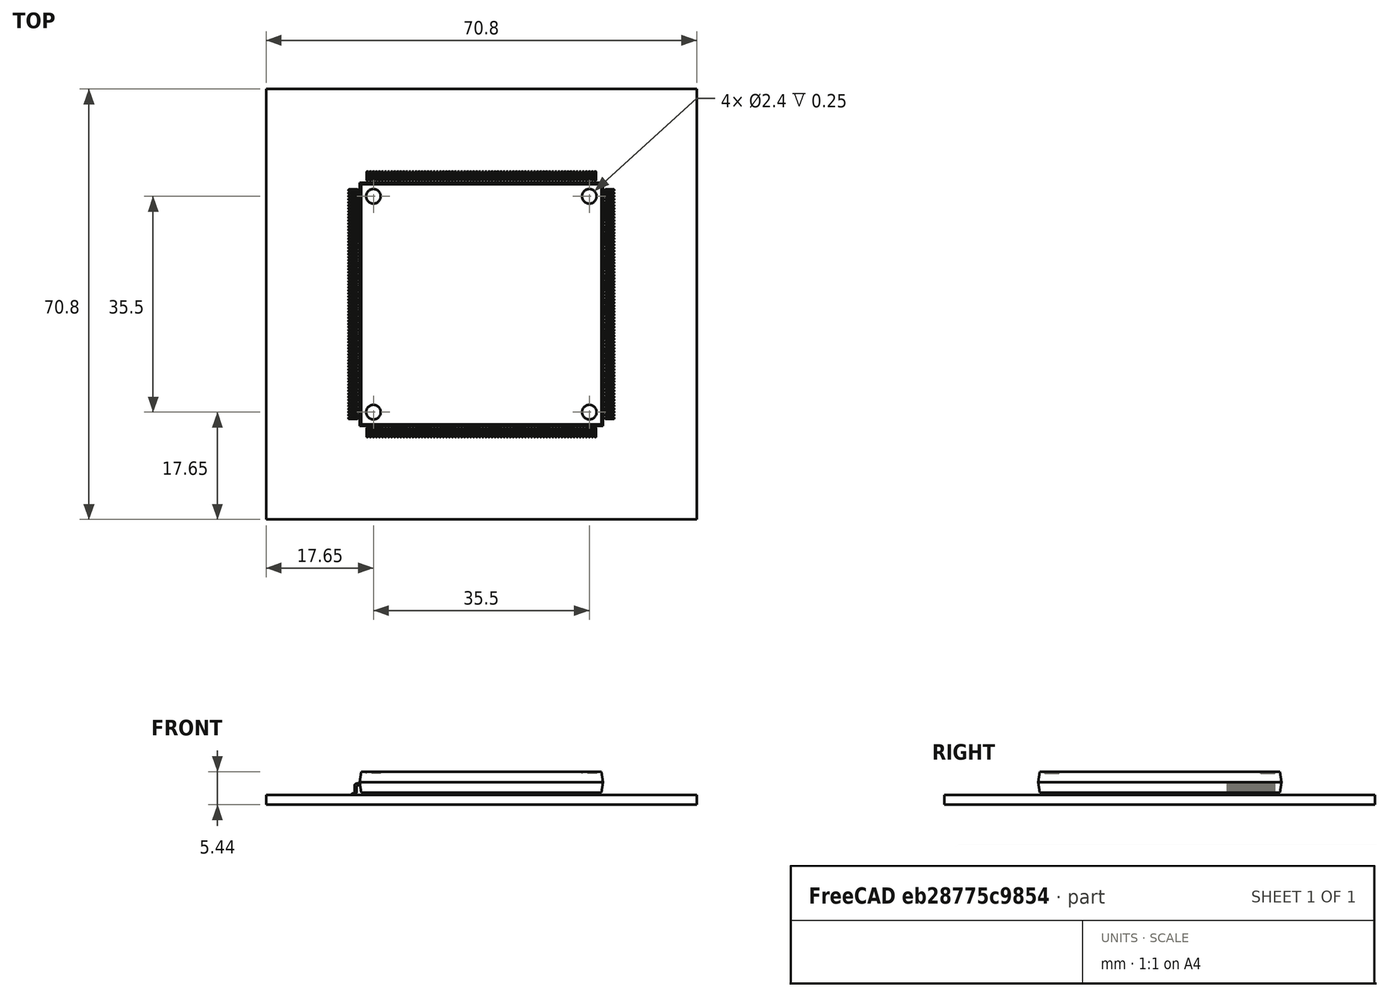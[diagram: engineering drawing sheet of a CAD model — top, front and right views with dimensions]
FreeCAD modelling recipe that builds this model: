
FCSTD DOCUMENT  (FreeCAD 0.19R24291 (Git))
Label: AT40K40
License: All rights reserved
LicenseURL: http://en.wikipedia.org/wiki/All_rights_reserved
objects: PartDesign::SubtractiveBox×1824, PartDesign::AdditiveBox×1217, PartDesign::Fillet×912, PartDesign::SubtractiveCylinder×612, PartDesign::Body×305, App::Part×28, PartDesign::Chamfer×8, Part::FeaturePython×5, Sketcher::SketchObject×1, App::DocumentObjectGroup×1
note: 9457 computed .brp shape members not serialized (recipe doc carries the construction recipe); baked Part::Feature solids carry a one-line shape summary decoded from their .brp

FEATURE [Sketcher::SketchObject] Sketch001  label="body-sketch"
  FullyConstrained = false
  MapMode = 5
  Support = -> [XY_Plane]
  sketch-geometry (20):
    g0: LineSegment StartX=20.05 StartY=20 StartZ=0 EndX=20.05 EndY=-20 EndZ=0
    g1: ArcOfCircle CenterX=20 CenterY=-20 CenterZ=0 NormalX=0 NormalY=0 NormalZ=1 AngleXU=-3.14159 Radius=0.05 StartAngle=0 EndAngle=3.14159
    g2: LineSegment StartX=19.95 StartY=-20 StartZ=0 EndX=19.95 EndY=20 EndZ=0
    g3: ArcOfCircle CenterX=20 CenterY=20 CenterZ=0 NormalX=0 NormalY=0 NormalZ=1 AngleXU=-3.14159 Radius=0.05 StartAngle=3.14159 EndAngle=6.28319
    g4: LineSegment StartX=-20.0354 StartY=19.0354 StartZ=0 EndX=-19.0354 EndY=20.0354 EndZ=0
    g5: ArcOfCircle CenterX=-19 CenterY=20 CenterZ=0 NormalX=0 NormalY=0 NormalZ=1 AngleXU=-0.785398 Radius=0.05 StartAngle=0 EndAngle=3.14159
    g6: LineSegment StartX=-18.9646 StartY=19.9646 StartZ=0 EndX=-19.9646 EndY=18.9646 EndZ=0
    g7: ArcOfCircle CenterX=-20 CenterY=19 CenterZ=0 NormalX=0 NormalY=0 NormalZ=1 AngleXU=-0.785398 Radius=0.05 StartAngle=3.14159 EndAngle=6.28319
    g8: LineSegment StartX=20 StartY=-20.05 StartZ=0 EndX=-20 EndY=-20.05 EndZ=0
    g9: ArcOfCircle CenterX=-20 CenterY=-20 CenterZ=0 NormalX=0 NormalY=0 NormalZ=1 AngleXU=1.5708 Radius=0.05 StartAngle=0 EndAngle=3.14159
    g10: LineSegment StartX=-20 StartY=-19.95 StartZ=0 EndX=20 EndY=-19.95 EndZ=0
    g11: ArcOfCircle CenterX=20 CenterY=-20 CenterZ=0 NormalX=0 NormalY=0 NormalZ=1 AngleXU=1.5708 Radius=0.05 StartAngle=3.14159 EndAngle=6.28319
    g12: LineSegment StartX=-19 StartY=20.05 StartZ=0 EndX=20 EndY=20.05 EndZ=0
    g13: ArcOfCircle CenterX=20 CenterY=20 CenterZ=0 NormalX=0 NormalY=0 NormalZ=1 AngleXU=-1.5708 Radius=0.05 StartAngle=0 EndAngle=3.14159
    g14: LineSegment StartX=20 StartY=19.95 StartZ=0 EndX=-19 EndY=19.95 EndZ=0
    g15: ArcOfCircle CenterX=-19 CenterY=20 CenterZ=0 NormalX=0 NormalY=0 NormalZ=1 AngleXU=-1.5708 Radius=0.05 StartAngle=3.14159 EndAngle=6.28319
    g16: LineSegment StartX=-20.05 StartY=-20 StartZ=0 EndX=-20.05 EndY=19 EndZ=0
    g17: ArcOfCircle CenterX=-20 CenterY=19 CenterZ=0 NormalX=0 NormalY=0 NormalZ=1 AngleXU=1e-16 Radius=0.05 StartAngle=0 EndAngle=3.14159
    g18: LineSegment StartX=-19.95 StartY=19 StartZ=0 EndX=-19.95 EndY=-20 EndZ=0
    g19: ArcOfCircle CenterX=-20 CenterY=-20 CenterZ=0 NormalX=0 NormalY=0 NormalZ=1 AngleXU=0 Radius=0.05 StartAngle=3.14159 EndAngle=6.28319
FEATURE [PartDesign::AdditiveBox] Box
  AttacherType = Attacher::AttachEngine3D
  AttachmentOffset = pos=(-20,-20,0.375) rot=(0,0,1;0rad)
  Height = 3.475
  Length = 40
  MapMode = 5
  Placement = pos=(-20,-20,0.375) rot=(0,0,1;0rad)
  Support = -> [XY_Plane]
  Width = 40
FEATURE [PartDesign::SubtractiveCylinder] Cylinder
  Angle = 360
  AttacherType = Attacher::AttachEngine3D
  AttachmentOffset = pos=(17.75,-17.75,3.6) rot=(0,0,1;0rad)
  BaseFeature = -> Box
  Height = 0.25
  MapMode = 5
  Placement = pos=(17.75,-17.75,3.6) rot=(0,0,1;0rad)
  Radius = 1.2
  Support = -> [XY_Plane]
FEATURE [PartDesign::SubtractiveCylinder] Cylinder001
  Angle = 360
  AttacherType = Attacher::AttachEngine3D
  AttachmentOffset = pos=(-17.75,17.75,3.6) rot=(0,0,1;0rad)
  BaseFeature = -> Cylinder
  Height = 0.25
  MapMode = 5
  Placement = pos=(-17.75,17.75,3.6) rot=(0,0,1;0rad)
  Radius = 1.2
  Support = -> [XY_Plane]
FEATURE [PartDesign::SubtractiveCylinder] Cylinder002
  Angle = 360
  AttacherType = Attacher::AttachEngine3D
  AttachmentOffset = pos=(-17.75,-17.75,3.6) rot=(0,0,1;0rad)
  BaseFeature = -> Cylinder001
  Height = 0.25
  MapMode = 5
  Placement = pos=(-17.75,-17.75,3.6) rot=(0,0,1;0rad)
  Radius = 1.2
  Support = -> [XY_Plane]
FEATURE [PartDesign::SubtractiveCylinder] Cylinder003
  Angle = 360
  AttacherType = Attacher::AttachEngine3D
  AttachmentOffset = pos=(17.75,17.75,3.6) rot=(0,0,1;0rad)
  BaseFeature = -> Cylinder002
  Height = 0.25
  MapMode = 5
  Placement = pos=(17.75,17.75,3.6) rot=(0,0,1;0rad)
  Radius = 1.2
  Support = -> [XY_Plane]
FEATURE [PartDesign::AdditiveBox] Box001
  AttacherType = Attacher::AttachEngine3D
  AttachmentOffset = pos=(-21.3,18.635,0) rot=(0,0,1;0rad)
  Height = 1.9
  Length = 1.3
  MapMode = 5
  Placement = pos=(-21.3,18.635,0) rot=(0,0,1;0rad)
  Support = -> [XY_Plane001]
  Width = 0.23
FEATURE [PartDesign::SubtractiveBox] Box002
  AttacherType = Attacher::AttachEngine3D
  AttachmentOffset = pos=(-21.35,18.635,0.35) rot=(0,0,1;0rad)
  BaseFeature = -> Box001
  Height = 1.55
  Length = 0.5
  MapMode = 5
  Placement = pos=(-21.35,18.635,0.35) rot=(0,0,1;0rad)
  Support = -> [XY_Plane001]
  Width = 0.23
FEATURE [PartDesign::SubtractiveBox] Box003
  AttacherType = Attacher::AttachEngine3D
  AttachmentOffset = pos=(-20.5,18.63,0) rot=(0,0,1;0rad)
  BaseFeature = -> Box002
  Height = 1.635
  Length = 0.5
  MapMode = 5
  Placement = pos=(-20.5,18.63,0) rot=(0,0,1;0rad)
  Support = -> [XY_Plane001]
  Width = 0.25
FEATURE [PartDesign::SubtractiveBox] Box004
  AttacherType = Attacher::AttachEngine3D
  AttachmentOffset = pos=(-21.19,18.635,-0.12) rot=(0,-1,0;0.15708rad)
  BaseFeature = -> Box003
  Height = 0.12
  Length = 0.725
  MapMode = 5
  Placement = pos=(-21.19,18.635,-0.12) rot=(0,-1,0;0.15708rad)
  Support = -> [XY_Plane001]
  Width = 0.25
FEATURE [PartDesign::SubtractiveBox] Box005
  AttacherType = Attacher::AttachEngine3D
  AttachmentOffset = pos=(-21.5005,18.625,0.235) rot=(0,-1,0;0.174533rad)
  BaseFeature = -> Box004
  Height = 0.3
  Length = 0.6605
  MapMode = 5
  Placement = pos=(-21.5005,18.625,0.235) rot=(0,-1,0;0.174533rad)
  Support = -> [XY_Plane001]
  Width = 0.25
FEATURE [PartDesign::Fillet] Fillet
  Base = -> Box005 [Edge2]
  BaseFeature = -> Box005
  Placement = pos=(-21.5005,18.625,0.235) rot=(0,-1,0;0.174533rad)
  Radius = 0.05
  SupportTransform = false
FEATURE [PartDesign::Fillet] Fillet001
  Base = -> Fillet [Edge33]
  BaseFeature = -> Fillet
  Placement = pos=(-21.5005,18.625,0.235) rot=(0,-1,0;0.174533rad)
  Radius = 0.5
  SupportTransform = false
FEATURE [PartDesign::AdditiveBox] Box006
  AttacherType = Attacher::AttachEngine3D
  AttachmentOffset = pos=(-21.1,18.635,0.305) rot=(0,1,0;0.785398rad)
  BaseFeature = -> Fillet001
  Height = 0.375
  Length = 0.2
  MapMode = 5
  Placement = pos=(-21.1,18.635,0.305) rot=(0,1,0;0.785398rad)
  Support = -> [XY_Plane001]
  Width = 0.23
FEATURE [PartDesign::SubtractiveCylinder] Cylinder004
  Angle = 360
  AttacherType = Attacher::AttachEngine3D
  AttachmentOffset = pos=(-21.055,18.935,0.52) rot=(1,0,0;1.5708rad)
  BaseFeature = -> Box006
  Height = 0.375
  MapMode = 5
  Placement = pos=(-21.055,18.935,0.52) rot=(1,0,0;1.5708rad)
  Radius = 0.205
  Support = -> [XY_Plane001]
FEATURE [PartDesign::SubtractiveBox] Box007
  AttacherType = Attacher::AttachEngine3D
  AttachmentOffset = pos=(-20.95,18.635,0.53) rot=(0,0,1;0rad)
  BaseFeature = -> Cylinder004
  Height = 0.5
  Length = 0.1
  MapMode = 5
  Placement = pos=(-20.95,18.635,0.53) rot=(0,0,1;0rad)
  Support = -> [XY_Plane001]
  Width = 0.23
FEATURE [PartDesign::SubtractiveBox] Box008
  AttacherType = Attacher::AttachEngine3D
  AttachmentOffset = pos=(-21.15,18.635,0.297) rot=(0,-1,0;0.174533rad)
  BaseFeature = -> Box007
  Height = 0.115
  Length = 0.115
  MapMode = 5
  Placement = pos=(-21.15,18.635,0.297) rot=(0,-1,0;0.174533rad)
  Support = -> [XY_Plane001]
  Width = 0.23
FEATURE [PartDesign::Fillet] Fillet002
  Base = -> Box008 [Edge28]
  BaseFeature = -> Box008
  Placement = pos=(-21.15,18.635,0.297) rot=(0,-1,0;0.174533rad)
  Radius = 0.375
  SupportTransform = false
FEATURE [PartDesign::AdditiveBox] Box009
  AttacherType = Attacher::AttachEngine3D
  AttachmentOffset = pos=(-20.7,18.635,1.55) rot=(0,1,0;0.785398rad)
  BaseFeature = -> Fillet002
  Height = 0.375
  Length = 0.23
  MapMode = 5
  Placement = pos=(-20.7,18.635,1.55) rot=(0,1,0;0.785398rad)
  Support = -> [XY_Plane001]
  Width = 0.23
FEATURE [PartDesign::SubtractiveCylinder] Cylinder005
  Angle = 360
  AttacherType = Attacher::AttachEngine3D
  AttachmentOffset = pos=(-20.271,18.635,1.4056) rot=(-1,0,0;1.5708rad)
  BaseFeature = -> Box009
  Height = 0.23
  MapMode = 5
  Placement = pos=(-20.271,18.635,1.4056) rot=(-1,0,0;1.5708rad)
  Radius = 0.23
  Support = -> [XY_Plane001]
FEATURE [PartDesign::Chamfer] Chamfer
  Angle = 45
  Base = -> Cylinder003 [Edge2]
  BaseFeature = -> Cylinder003
  ChamferType = 1
  FlipDirection = false
  Placement = pos=(17.75,17.75,3.6) rot=(0,0,1;0rad)
  Size = 1.7125
  Size2 = 0.25
  SupportTransform = false
FEATURE [PartDesign::Chamfer] Chamfer001
  Angle = 45
  Base = -> Chamfer [Edge3]
  BaseFeature = -> Chamfer
  ChamferType = 1
  FlipDirection = false
  Placement = pos=(17.75,17.75,3.6) rot=(0,0,1;0rad)
  Size = 1.7125
  Size2 = 0.25
  SupportTransform = false
FEATURE [PartDesign::Chamfer] Chamfer002
  Angle = 45
  Base = -> Chamfer001 [Edge15]
  BaseFeature = -> Chamfer001
  ChamferType = 1
  FlipDirection = false
  Placement = pos=(17.75,17.75,3.6) rot=(0,0,1;0rad)
  Size = 1.7125
  Size2 = 0.25
  SupportTransform = false
FEATURE [PartDesign::Chamfer] Chamfer003
  Angle = 45
  Base = -> Chamfer002 [Edge30]
  BaseFeature = -> Chamfer002
  ChamferType = 1
  FlipDirection = false
  Placement = pos=(17.75,17.75,3.6) rot=(0,0,1;0rad)
  Size = 1.7125
  Size2 = 0.25
  SupportTransform = false
FEATURE [PartDesign::Chamfer] Chamfer004
  Angle = 45
  Base = -> Chamfer003 [Edge5]
  BaseFeature = -> Chamfer003
  ChamferType = 1
  FlipDirection = false
  Placement = pos=(17.75,17.75,3.6) rot=(0,0,1;0rad)
  Size = 1.7125
  Size2 = 0.25
  SupportTransform = false
FEATURE [PartDesign::Chamfer] Chamfer005
  Angle = 45
  Base = -> Chamfer004 [Edge3]
  BaseFeature = -> Chamfer004
  ChamferType = 1
  FlipDirection = false
  Placement = pos=(17.75,17.75,3.6) rot=(0,0,1;0rad)
  Size = 1.7125
  Size2 = 0.25
  SupportTransform = false
FEATURE [PartDesign::Chamfer] Chamfer006
  Angle = 45
  Base = -> Chamfer005 [Edge8]
  BaseFeature = -> Chamfer005
  ChamferType = 1
  FlipDirection = false
  Placement = pos=(17.75,17.75,3.6) rot=(0,0,1;0rad)
  Size = 1.7125
  Size2 = 0.25
  SupportTransform = false
FEATURE [PartDesign::Chamfer] Chamfer007
  Angle = 45
  Base = -> Chamfer006 [Edge6]
  BaseFeature = -> Chamfer006
  ChamferType = 1
  FlipDirection = false
  Placement = pos=(17.75,17.75,3.6) rot=(0,0,1;0rad)
  Size = 1.7125
  Size2 = 0.25
  SupportTransform = false
FEATURE [PartDesign::Body] Body
  Group = -> [Sketch001,Box,Cylinder,Cylinder001,Cylinder002,Cylinder003,Chamfer,Chamfer001,Chamfer002,Chamfer003,Chamfer004,Chamfer005,Chamfer006,Chamfer007]
  Origin = -> Origin
  Tip = -> Chamfer007
FEATURE [PartDesign::AdditiveBox] Box010
  AttacherType = Attacher::AttachEngine3D
  AttachmentOffset = pos=(-20.1,18.635,1.635) rot=(0,0,1;0rad)
  BaseFeature = -> Cylinder005
  Height = 0.265
  Length = 0.23
  MapMode = 5
  Placement = pos=(-20.1,18.635,1.635) rot=(0,0,1;0rad)
  Support = -> [XY_Plane001]
  Width = 0.23
FEATURE [PartDesign::Body] Body001  label="pin1"
  Group = -> [Box001,Box002,Box003,Box004,Box005,Fillet,Fillet001,Box006,Cylinder004,Box007,Box008,Fillet002,Box009,Cylinder005,Box010]
  Origin = -> Origin001
  Tip = -> Box010
FEATURE [PartDesign::AdditiveBox] Box019
  AttacherType = Attacher::AttachEngine3D
  AttachmentOffset = pos=(-21.3,18.635,0) rot=(0,0,1;0rad)
  Height = 1.9
  Length = 1.3
  MapMode = 5
  Placement = pos=(-21.3,18.635,0) rot=(0,0,1;0rad)
  Support = -> [XY_Plane002]
  Width = 0.23
FEATURE [PartDesign::SubtractiveBox] Box020
  AttacherType = Attacher::AttachEngine3D
  AttachmentOffset = pos=(-21.35,18.635,0.35) rot=(0,0,1;0rad)
  BaseFeature = -> Box019
  Height = 1.55
  Length = 0.5
  MapMode = 5
  Placement = pos=(-21.35,18.635,0.35) rot=(0,0,1;0rad)
  Support = -> [XY_Plane002]
  Width = 0.23
FEATURE [PartDesign::SubtractiveBox] Box014
  AttacherType = Attacher::AttachEngine3D
  AttachmentOffset = pos=(-20.5,18.63,0) rot=(0,0,1;0rad)
  BaseFeature = -> Box020
  Height = 1.635
  Length = 0.5
  MapMode = 5
  Placement = pos=(-20.5,18.63,0) rot=(0,0,1;0rad)
  Support = -> [XY_Plane002]
  Width = 0.25
FEATURE [PartDesign::SubtractiveBox] Box015
  AttacherType = Attacher::AttachEngine3D
  AttachmentOffset = pos=(-21.19,18.635,-0.12) rot=(0,-1,0;0.15708rad)
  BaseFeature = -> Box014
  Height = 0.12
  Length = 0.725
  MapMode = 5
  Placement = pos=(-21.19,18.635,-0.12) rot=(0,-1,0;0.15708rad)
  Support = -> [XY_Plane002]
  Width = 0.25
FEATURE [PartDesign::SubtractiveBox] Box018
  AttacherType = Attacher::AttachEngine3D
  AttachmentOffset = pos=(-21.5005,18.625,0.235) rot=(0,-1,0;0.174533rad)
  BaseFeature = -> Box015
  Height = 0.3
  Length = 0.6605
  MapMode = 5
  Placement = pos=(-21.5005,18.625,0.235) rot=(0,-1,0;0.174533rad)
  Support = -> [XY_Plane002]
  Width = 0.25
FEATURE [PartDesign::Fillet] Fillet004
  Base = -> Box018 [Edge2]
  BaseFeature = -> Box018
  Placement = pos=(-21.5005,18.625,0.235) rot=(0,-1,0;0.174533rad)
  Radius = 0.05
  SupportTransform = false
FEATURE [PartDesign::Fillet] Fillet003
  Base = -> Fillet004 [Edge33]
  BaseFeature = -> Fillet004
  Placement = pos=(-21.5005,18.625,0.235) rot=(0,-1,0;0.174533rad)
  Radius = 0.5
  SupportTransform = false
FEATURE [PartDesign::AdditiveBox] Box011
  AttacherType = Attacher::AttachEngine3D
  AttachmentOffset = pos=(-21.1,18.635,0.305) rot=(0,1,0;0.785398rad)
  BaseFeature = -> Fillet003
  Height = 0.375
  Length = 0.2
  MapMode = 5
  Placement = pos=(-21.1,18.635,0.305) rot=(0,1,0;0.785398rad)
  Support = -> [XY_Plane002]
  Width = 0.23
FEATURE [PartDesign::SubtractiveCylinder] Cylinder006
  Angle = 360
  AttacherType = Attacher::AttachEngine3D
  AttachmentOffset = pos=(-21.055,18.935,0.52) rot=(1,0,0;1.5708rad)
  BaseFeature = -> Box011
  Height = 0.375
  MapMode = 5
  Placement = pos=(-21.055,18.935,0.52) rot=(1,0,0;1.5708rad)
  Radius = 0.205
  Support = -> [XY_Plane002]
FEATURE [PartDesign::SubtractiveBox] Box013
  AttacherType = Attacher::AttachEngine3D
  AttachmentOffset = pos=(-20.95,18.635,0.53) rot=(0,0,1;0rad)
  BaseFeature = -> Cylinder006
  Height = 0.5
  Length = 0.1
  MapMode = 5
  Placement = pos=(-20.95,18.635,0.53) rot=(0,0,1;0rad)
  Support = -> [XY_Plane002]
  Width = 0.23
FEATURE [PartDesign::SubtractiveBox] Box012
  AttacherType = Attacher::AttachEngine3D
  AttachmentOffset = pos=(-21.15,18.635,0.297) rot=(0,-1,0;0.174533rad)
  BaseFeature = -> Box013
  Height = 0.115
  Length = 0.115
  MapMode = 5
  Placement = pos=(-21.15,18.635,0.297) rot=(0,-1,0;0.174533rad)
  Support = -> [XY_Plane002]
  Width = 0.23
FEATURE [PartDesign::Fillet] Fillet005
  Base = -> Box012 [Edge28]
  BaseFeature = -> Box012
  Placement = pos=(-21.15,18.635,0.297) rot=(0,-1,0;0.174533rad)
  Radius = 0.375
  SupportTransform = false
FEATURE [PartDesign::AdditiveBox] Box016
  AttacherType = Attacher::AttachEngine3D
  AttachmentOffset = pos=(-20.7,18.635,1.55) rot=(0,1,0;0.785398rad)
  BaseFeature = -> Fillet005
  Height = 0.375
  Length = 0.23
  MapMode = 5
  Placement = pos=(-20.7,18.635,1.55) rot=(0,1,0;0.785398rad)
  Support = -> [XY_Plane002]
  Width = 0.23
FEATURE [PartDesign::SubtractiveCylinder] Cylinder007
  Angle = 360
  AttacherType = Attacher::AttachEngine3D
  AttachmentOffset = pos=(-20.271,18.635,1.4056) rot=(-1,0,0;1.5708rad)
  BaseFeature = -> Box016
  Height = 0.23
  MapMode = 5
  Placement = pos=(-20.271,18.635,1.4056) rot=(-1,0,0;1.5708rad)
  Radius = 0.23
  Support = -> [XY_Plane002]
FEATURE [PartDesign::AdditiveBox] Box017
  AttacherType = Attacher::AttachEngine3D
  AttachmentOffset = pos=(-20.1,18.635,1.635) rot=(0,0,1;0rad)
  BaseFeature = -> Cylinder007
  Height = 0.265
  Length = 0.23
  MapMode = 5
  Placement = pos=(-20.1,18.635,1.635) rot=(0,0,1;0rad)
  Support = -> [XY_Plane002]
  Width = 0.23
FEATURE [PartDesign::Body] Body002  label="pin002"
  Group = -> [Box019,Box020,Box014,Box015,Box018,Fillet004,Fillet003,Box011,Cylinder006,Box013,Box012,Fillet005,Box016,Cylinder007,Box017]
  Origin = -> Origin002
  Placement = pos=(0,-0.5,0) rot=(0,0,1;0rad)
  Tip = -> Box017
FEATURE [PartDesign::AdditiveBox] Box029
  AttacherType = Attacher::AttachEngine3D
  AttachmentOffset = pos=(-21.3,18.635,0) rot=(0,0,1;0rad)
  Height = 1.9
  Length = 1.3
  MapMode = 5
  Placement = pos=(-21.3,18.635,0) rot=(0,0,1;0rad)
  Support = -> [XY_Plane003]
  Width = 0.23
FEATURE [PartDesign::SubtractiveBox] Box030
  AttacherType = Attacher::AttachEngine3D
  AttachmentOffset = pos=(-21.35,18.635,0.35) rot=(0,0,1;0rad)
  BaseFeature = -> Box029
  Height = 1.55
  Length = 0.5
  MapMode = 5
  Placement = pos=(-21.35,18.635,0.35) rot=(0,0,1;0rad)
  Support = -> [XY_Plane003]
  Width = 0.23
FEATURE [PartDesign::SubtractiveBox] Box021
  AttacherType = Attacher::AttachEngine3D
  AttachmentOffset = pos=(-20.5,18.63,0) rot=(0,0,1;0rad)
  BaseFeature = -> Box030
  Height = 1.635
  Length = 0.5
  MapMode = 5
  Placement = pos=(-20.5,18.63,0) rot=(0,0,1;0rad)
  Support = -> [XY_Plane003]
  Width = 0.25
FEATURE [PartDesign::SubtractiveBox] Box026
  AttacherType = Attacher::AttachEngine3D
  AttachmentOffset = pos=(-21.19,18.635,-0.12) rot=(0,-1,0;0.15708rad)
  BaseFeature = -> Box021
  Height = 0.12
  Length = 0.725
  MapMode = 5
  Placement = pos=(-21.19,18.635,-0.12) rot=(0,-1,0;0.15708rad)
  Support = -> [XY_Plane003]
  Width = 0.25
FEATURE [PartDesign::SubtractiveBox] Box027
  AttacherType = Attacher::AttachEngine3D
  AttachmentOffset = pos=(-21.5005,18.625,0.235) rot=(0,-1,0;0.174533rad)
  BaseFeature = -> Box026
  Height = 0.3
  Length = 0.6605
  MapMode = 5
  Placement = pos=(-21.5005,18.625,0.235) rot=(0,-1,0;0.174533rad)
  Support = -> [XY_Plane003]
  Width = 0.25
FEATURE [PartDesign::Fillet] Fillet006
  Base = -> Box027 [Edge2]
  BaseFeature = -> Box027
  Placement = pos=(-21.5005,18.625,0.235) rot=(0,-1,0;0.174533rad)
  Radius = 0.05
  SupportTransform = false
FEATURE [PartDesign::Fillet] Fillet007
  Base = -> Fillet006 [Edge33]
  BaseFeature = -> Fillet006
  Placement = pos=(-21.5005,18.625,0.235) rot=(0,-1,0;0.174533rad)
  Radius = 0.5
  SupportTransform = false
FEATURE [PartDesign::AdditiveBox] Box023
  AttacherType = Attacher::AttachEngine3D
  AttachmentOffset = pos=(-21.1,18.635,0.305) rot=(0,1,0;0.785398rad)
  BaseFeature = -> Fillet007
  Height = 0.375
  Length = 0.2
  MapMode = 5
  Placement = pos=(-21.1,18.635,0.305) rot=(0,1,0;0.785398rad)
  Support = -> [XY_Plane003]
  Width = 0.23
FEATURE [PartDesign::SubtractiveCylinder] Cylinder008
  Angle = 360
  AttacherType = Attacher::AttachEngine3D
  AttachmentOffset = pos=(-21.055,18.935,0.52) rot=(1,0,0;1.5708rad)
  BaseFeature = -> Box023
  Height = 0.375
  MapMode = 5
  Placement = pos=(-21.055,18.935,0.52) rot=(1,0,0;1.5708rad)
  Radius = 0.205
  Support = -> [XY_Plane003]
FEATURE [PartDesign::SubtractiveBox] Box025
  AttacherType = Attacher::AttachEngine3D
  AttachmentOffset = pos=(-20.95,18.635,0.53) rot=(0,0,1;0rad)
  BaseFeature = -> Cylinder008
  Height = 0.5
  Length = 0.1
  MapMode = 5
  Placement = pos=(-20.95,18.635,0.53) rot=(0,0,1;0rad)
  Support = -> [XY_Plane003]
  Width = 0.23
FEATURE [PartDesign::SubtractiveBox] Box024
  AttacherType = Attacher::AttachEngine3D
  AttachmentOffset = pos=(-21.15,18.635,0.297) rot=(0,-1,0;0.174533rad)
  BaseFeature = -> Box025
  Height = 0.115
  Length = 0.115
  MapMode = 5
  Placement = pos=(-21.15,18.635,0.297) rot=(0,-1,0;0.174533rad)
  Support = -> [XY_Plane003]
  Width = 0.23
FEATURE [PartDesign::Fillet] Fillet008
  Base = -> Box024 [Edge28]
  BaseFeature = -> Box024
  Placement = pos=(-21.15,18.635,0.297) rot=(0,-1,0;0.174533rad)
  Radius = 0.375
  SupportTransform = false
FEATURE [PartDesign::AdditiveBox] Box022
  AttacherType = Attacher::AttachEngine3D
  AttachmentOffset = pos=(-20.7,18.635,1.55) rot=(0,1,0;0.785398rad)
  BaseFeature = -> Fillet008
  Height = 0.375
  Length = 0.23
  MapMode = 5
  Placement = pos=(-20.7,18.635,1.55) rot=(0,1,0;0.785398rad)
  Support = -> [XY_Plane003]
  Width = 0.23
FEATURE [PartDesign::SubtractiveCylinder] Cylinder009
  Angle = 360
  AttacherType = Attacher::AttachEngine3D
  AttachmentOffset = pos=(-20.271,18.635,1.4056) rot=(-1,0,0;1.5708rad)
  BaseFeature = -> Box022
  Height = 0.23
  MapMode = 5
  Placement = pos=(-20.271,18.635,1.4056) rot=(-1,0,0;1.5708rad)
  Radius = 0.23
  Support = -> [XY_Plane003]
FEATURE [PartDesign::AdditiveBox] Box028
  AttacherType = Attacher::AttachEngine3D
  AttachmentOffset = pos=(-20.1,18.635,1.635) rot=(0,0,1;0rad)
  BaseFeature = -> Cylinder009
  Height = 0.265
  Length = 0.23
  MapMode = 5
  Placement = pos=(-20.1,18.635,1.635) rot=(0,0,1;0rad)
  Support = -> [XY_Plane003]
  Width = 0.23
FEATURE [PartDesign::Body] Body003  label="pin003"
  Group = -> [Box029,Box030,Box021,Box026,Box027,Fillet006,Fillet007,Box023,Cylinder008,Box025,Box024,Fillet008,Box022,Cylinder009,Box028]
  Origin = -> Origin003
  Placement = pos=(0,-1,0) rot=(0,0,1;0rad)
  Tip = -> Box028
FEATURE [PartDesign::AdditiveBox] Box048
  AttacherType = Attacher::AttachEngine3D
  AttachmentOffset = pos=(-21.3,18.635,0) rot=(0,0,1;0rad)
  Height = 1.9
  Length = 1.3
  MapMode = 5
  Placement = pos=(-21.3,18.635,0) rot=(0,0,1;0rad)
  Support = -> [XY_Plane006]
  Width = 0.23
FEATURE [PartDesign::SubtractiveBox] Box049
  AttacherType = Attacher::AttachEngine3D
  AttachmentOffset = pos=(-21.35,18.635,0.35) rot=(0,0,1;0rad)
  BaseFeature = -> Box048
  Height = 1.55
  Length = 0.5
  MapMode = 5
  Placement = pos=(-21.35,18.635,0.35) rot=(0,0,1;0rad)
  Support = -> [XY_Plane006]
  Width = 0.23
FEATURE [PartDesign::SubtractiveBox] Box038
  AttacherType = Attacher::AttachEngine3D
  AttachmentOffset = pos=(-20.5,18.63,0) rot=(0,0,1;0rad)
  BaseFeature = -> Box049
  Height = 1.635
  Length = 0.5
  MapMode = 5
  Placement = pos=(-20.5,18.63,0) rot=(0,0,1;0rad)
  Support = -> [XY_Plane006]
  Width = 0.25
FEATURE [PartDesign::SubtractiveBox] Box045
  AttacherType = Attacher::AttachEngine3D
  AttachmentOffset = pos=(-21.19,18.635,-0.12) rot=(0,-1,0;0.15708rad)
  BaseFeature = -> Box038
  Height = 0.12
  Length = 0.725
  MapMode = 5
  Placement = pos=(-21.19,18.635,-0.12) rot=(0,-1,0;0.15708rad)
  Support = -> [XY_Plane006]
  Width = 0.25
FEATURE [PartDesign::SubtractiveBox] Box046
  AttacherType = Attacher::AttachEngine3D
  AttachmentOffset = pos=(-21.5005,18.625,0.235) rot=(0,-1,0;0.174533rad)
  BaseFeature = -> Box045
  Height = 0.3
  Length = 0.6605
  MapMode = 5
  Placement = pos=(-21.5005,18.625,0.235) rot=(0,-1,0;0.174533rad)
  Support = -> [XY_Plane006]
  Width = 0.25
FEATURE [PartDesign::Fillet] Fillet010
  Base = -> Box046 [Edge2]
  BaseFeature = -> Box046
  Placement = pos=(-21.5005,18.625,0.235) rot=(0,-1,0;0.174533rad)
  Radius = 0.05
  SupportTransform = false
FEATURE [PartDesign::Fillet] Fillet011
  Base = -> Fillet010 [Edge33]
  BaseFeature = -> Fillet010
  Placement = pos=(-21.5005,18.625,0.235) rot=(0,-1,0;0.174533rad)
  Radius = 0.5
  SupportTransform = false
FEATURE [PartDesign::AdditiveBox] Box040
  AttacherType = Attacher::AttachEngine3D
  AttachmentOffset = pos=(-21.1,18.635,0.305) rot=(0,1,0;0.785398rad)
  BaseFeature = -> Fillet011
  Height = 0.375
  Length = 0.2
  MapMode = 5
  Placement = pos=(-21.1,18.635,0.305) rot=(0,1,0;0.785398rad)
  Support = -> [XY_Plane006]
  Width = 0.23
FEATURE [PartDesign::SubtractiveCylinder] Cylinder012
  Angle = 360
  AttacherType = Attacher::AttachEngine3D
  AttachmentOffset = pos=(-21.055,18.935,0.52) rot=(1,0,0;1.5708rad)
  BaseFeature = -> Box040
  Height = 0.375
  MapMode = 5
  Placement = pos=(-21.055,18.935,0.52) rot=(1,0,0;1.5708rad)
  Radius = 0.205
  Support = -> [XY_Plane006]
FEATURE [PartDesign::SubtractiveBox] Box044
  AttacherType = Attacher::AttachEngine3D
  AttachmentOffset = pos=(-20.95,18.635,0.53) rot=(0,0,1;0rad)
  BaseFeature = -> Cylinder012
  Height = 0.5
  Length = 0.1
  MapMode = 5
  Placement = pos=(-20.95,18.635,0.53) rot=(0,0,1;0rad)
  Support = -> [XY_Plane006]
  Width = 0.23
FEATURE [PartDesign::SubtractiveBox] Box041
  AttacherType = Attacher::AttachEngine3D
  AttachmentOffset = pos=(-21.15,18.635,0.297) rot=(0,-1,0;0.174533rad)
  BaseFeature = -> Box044
  Height = 0.115
  Length = 0.115
  MapMode = 5
  Placement = pos=(-21.15,18.635,0.297) rot=(0,-1,0;0.174533rad)
  Support = -> [XY_Plane006]
  Width = 0.23
FEATURE [PartDesign::Fillet] Fillet012
  Base = -> Box041 [Edge28]
  BaseFeature = -> Box041
  Placement = pos=(-21.15,18.635,0.297) rot=(0,-1,0;0.174533rad)
  Radius = 0.375
  SupportTransform = false
FEATURE [PartDesign::AdditiveBox] Box039
  AttacherType = Attacher::AttachEngine3D
  AttachmentOffset = pos=(-20.7,18.635,1.55) rot=(0,1,0;0.785398rad)
  BaseFeature = -> Fillet012
  Height = 0.375
  Length = 0.23
  MapMode = 5
  Placement = pos=(-20.7,18.635,1.55) rot=(0,1,0;0.785398rad)
  Support = -> [XY_Plane006]
  Width = 0.23
FEATURE [PartDesign::SubtractiveCylinder] Cylinder013
  Angle = 360
  AttacherType = Attacher::AttachEngine3D
  AttachmentOffset = pos=(-20.271,18.635,1.4056) rot=(-1,0,0;1.5708rad)
  BaseFeature = -> Box039
  Height = 0.23
  MapMode = 5
  Placement = pos=(-20.271,18.635,1.4056) rot=(-1,0,0;1.5708rad)
  Radius = 0.23
  Support = -> [XY_Plane006]
FEATURE [PartDesign::AdditiveBox] Box047
  AttacherType = Attacher::AttachEngine3D
  AttachmentOffset = pos=(-20.1,18.635,1.635) rot=(0,0,1;0rad)
  BaseFeature = -> Cylinder013
  Height = 0.265
  Length = 0.23
  MapMode = 5
  Placement = pos=(-20.1,18.635,1.635) rot=(0,0,1;0rad)
  Support = -> [XY_Plane006]
  Width = 0.23
FEATURE [PartDesign::Body] Body005  label="pin005"
  Group = -> [Box048,Box049,Box038,Box045,Box046,Fillet010,Fillet011,Box040,Cylinder012,Box044,Box041,Fillet012,Box039,Cylinder013,Box047]
  Origin = -> Origin005
  Placement = pos=(0,-2,0) rot=(0,0,1;0rad)
  Tip = -> Box047
FEATURE [PartDesign::AdditiveBox] Box055
  AttacherType = Attacher::AttachEngine3D
  AttachmentOffset = pos=(-21.3,18.635,0) rot=(0,0,1;0rad)
  Height = 1.9
  Length = 1.3
  MapMode = 5
  Placement = pos=(-21.3,18.635,0) rot=(0,0,1;0rad)
  Support = -> [XY_Plane004]
  Width = 0.23
FEATURE [PartDesign::SubtractiveBox] Box058
  AttacherType = Attacher::AttachEngine3D
  AttachmentOffset = pos=(-21.35,18.635,0.35) rot=(0,0,1;0rad)
  BaseFeature = -> Box055
  Height = 1.55
  Length = 0.5
  MapMode = 5
  Placement = pos=(-21.35,18.635,0.35) rot=(0,0,1;0rad)
  Support = -> [XY_Plane004]
  Width = 0.23
FEATURE [PartDesign::SubtractiveBox] Box035
  AttacherType = Attacher::AttachEngine3D
  AttachmentOffset = pos=(-20.5,18.63,0) rot=(0,0,1;0rad)
  BaseFeature = -> Box058
  Height = 1.635
  Length = 0.5
  MapMode = 5
  Placement = pos=(-20.5,18.63,0) rot=(0,0,1;0rad)
  Support = -> [XY_Plane004]
  Width = 0.25
FEATURE [PartDesign::SubtractiveBox] Box054
  AttacherType = Attacher::AttachEngine3D
  AttachmentOffset = pos=(-21.19,18.635,-0.12) rot=(0,-1,0;0.15708rad)
  BaseFeature = -> Box035
  Height = 0.12
  Length = 0.725
  MapMode = 5
  Placement = pos=(-21.19,18.635,-0.12) rot=(0,-1,0;0.15708rad)
  Support = -> [XY_Plane004]
  Width = 0.25
FEATURE [PartDesign::SubtractiveBox] Box052
  AttacherType = Attacher::AttachEngine3D
  AttachmentOffset = pos=(-21.5005,18.625,0.235) rot=(0,-1,0;0.174533rad)
  BaseFeature = -> Box054
  Height = 0.3
  Length = 0.6605
  MapMode = 5
  Placement = pos=(-21.5005,18.625,0.235) rot=(0,-1,0;0.174533rad)
  Support = -> [XY_Plane004]
  Width = 0.25
FEATURE [PartDesign::Fillet] Fillet013
  Base = -> Box052 [Edge2]
  BaseFeature = -> Box052
  Placement = pos=(-21.5005,18.625,0.235) rot=(0,-1,0;0.174533rad)
  Radius = 0.05
  SupportTransform = false
FEATURE [PartDesign::Fillet] Fillet014
  Base = -> Fillet013 [Edge33]
  BaseFeature = -> Fillet013
  Placement = pos=(-21.5005,18.625,0.235) rot=(0,-1,0;0.174533rad)
  Radius = 0.5
  SupportTransform = false
FEATURE [PartDesign::AdditiveBox] Box042
  AttacherType = Attacher::AttachEngine3D
  AttachmentOffset = pos=(-21.1,18.635,0.305) rot=(0,1,0;0.785398rad)
  BaseFeature = -> Fillet014
  Height = 0.375
  Length = 0.2
  MapMode = 5
  Placement = pos=(-21.1,18.635,0.305) rot=(0,1,0;0.785398rad)
  Support = -> [XY_Plane004]
  Width = 0.23
FEATURE [PartDesign::SubtractiveCylinder] Cylinder014
  Angle = 360
  AttacherType = Attacher::AttachEngine3D
  AttachmentOffset = pos=(-21.055,18.935,0.52) rot=(1,0,0;1.5708rad)
  BaseFeature = -> Box042
  Height = 0.375
  MapMode = 5
  Placement = pos=(-21.055,18.935,0.52) rot=(1,0,0;1.5708rad)
  Radius = 0.205
  Support = -> [XY_Plane004]
FEATURE [PartDesign::SubtractiveBox] Box057
  AttacherType = Attacher::AttachEngine3D
  AttachmentOffset = pos=(-20.95,18.635,0.53) rot=(0,0,1;0rad)
  BaseFeature = -> Cylinder014
  Height = 0.5
  Length = 0.1
  MapMode = 5
  Placement = pos=(-20.95,18.635,0.53) rot=(0,0,1;0rad)
  Support = -> [XY_Plane004]
  Width = 0.23
FEATURE [PartDesign::SubtractiveBox] Box051
  AttacherType = Attacher::AttachEngine3D
  AttachmentOffset = pos=(-21.15,18.635,0.297) rot=(0,-1,0;0.174533rad)
  BaseFeature = -> Box057
  Height = 0.115
  Length = 0.115
  MapMode = 5
  Placement = pos=(-21.15,18.635,0.297) rot=(0,-1,0;0.174533rad)
  Support = -> [XY_Plane004]
  Width = 0.23
FEATURE [PartDesign::Fillet] Fillet015
  Base = -> Box051 [Edge28]
  BaseFeature = -> Box051
  Placement = pos=(-21.15,18.635,0.297) rot=(0,-1,0;0.174533rad)
  Radius = 0.375
  SupportTransform = false
FEATURE [PartDesign::AdditiveBox] Box050
  AttacherType = Attacher::AttachEngine3D
  AttachmentOffset = pos=(-20.7,18.635,1.55) rot=(0,1,0;0.785398rad)
  BaseFeature = -> Fillet015
  Height = 0.375
  Length = 0.23
  MapMode = 5
  Placement = pos=(-20.7,18.635,1.55) rot=(0,1,0;0.785398rad)
  Support = -> [XY_Plane004]
  Width = 0.23
FEATURE [PartDesign::SubtractiveCylinder] Cylinder015
  Angle = 360
  AttacherType = Attacher::AttachEngine3D
  AttachmentOffset = pos=(-20.271,18.635,1.4056) rot=(-1,0,0;1.5708rad)
  BaseFeature = -> Box050
  Height = 0.23
  MapMode = 5
  Placement = pos=(-20.271,18.635,1.4056) rot=(-1,0,0;1.5708rad)
  Radius = 0.23
  Support = -> [XY_Plane004]
FEATURE [PartDesign::AdditiveBox] Box053
  AttacherType = Attacher::AttachEngine3D
  AttachmentOffset = pos=(-20.1,18.635,1.635) rot=(0,0,1;0rad)
  BaseFeature = -> Cylinder015
  Height = 0.265
  Length = 0.23
  MapMode = 5
  Placement = pos=(-20.1,18.635,1.635) rot=(0,0,1;0rad)
  Support = -> [XY_Plane004]
  Width = 0.23
FEATURE [PartDesign::Body] Body006  label="pin006"
  Group = -> [Box055,Box058,Box035,Box054,Box052,Fillet013,Fillet014,Box042,Cylinder014,Box057,Box051,Fillet015,Box050,Cylinder015,Box053]
  Origin = -> Origin006
  Placement = pos=(0,-2.5,0) rot=(0,0,1;0rad)
  Tip = -> Box053
FEATURE [PartDesign::AdditiveBox] Box059
  AttacherType = Attacher::AttachEngine3D
  AttachmentOffset = pos=(-21.3,18.635,0) rot=(0,0,1;0rad)
  Height = 1.9
  Length = 1.3
  MapMode = 5
  Placement = pos=(-21.3,18.635,0) rot=(0,0,1;0rad)
  Support = -> [XY_Plane005]
  Width = 0.23
FEATURE [PartDesign::SubtractiveBox] Box060
  AttacherType = Attacher::AttachEngine3D
  AttachmentOffset = pos=(-21.35,18.635,0.35) rot=(0,0,1;0rad)
  BaseFeature = -> Box059
  Height = 1.55
  Length = 0.5
  MapMode = 5
  Placement = pos=(-21.35,18.635,0.35) rot=(0,0,1;0rad)
  Support = -> [XY_Plane005]
  Width = 0.23
FEATURE [PartDesign::SubtractiveBox] Box034
  AttacherType = Attacher::AttachEngine3D
  AttachmentOffset = pos=(-20.5,18.63,0) rot=(0,0,1;0rad)
  BaseFeature = -> Box060
  Height = 1.635
  Length = 0.5
  MapMode = 5
  Placement = pos=(-20.5,18.63,0) rot=(0,0,1;0rad)
  Support = -> [XY_Plane005]
  Width = 0.25
FEATURE [PartDesign::SubtractiveBox] Box036
  AttacherType = Attacher::AttachEngine3D
  AttachmentOffset = pos=(-21.19,18.635,-0.12) rot=(0,-1,0;0.15708rad)
  BaseFeature = -> Box034
  Height = 0.12
  Length = 0.725
  MapMode = 5
  Placement = pos=(-21.19,18.635,-0.12) rot=(0,-1,0;0.15708rad)
  Support = -> [XY_Plane005]
  Width = 0.25
FEATURE [PartDesign::SubtractiveBox] Box056
  AttacherType = Attacher::AttachEngine3D
  AttachmentOffset = pos=(-21.5005,18.625,0.235) rot=(0,-1,0;0.174533rad)
  BaseFeature = -> Box036
  Height = 0.3
  Length = 0.6605
  MapMode = 5
  Placement = pos=(-21.5005,18.625,0.235) rot=(0,-1,0;0.174533rad)
  Support = -> [XY_Plane005]
  Width = 0.25
FEATURE [PartDesign::Fillet] Fillet016
  Base = -> Box056 [Edge2]
  BaseFeature = -> Box056
  Placement = pos=(-21.5005,18.625,0.235) rot=(0,-1,0;0.174533rad)
  Radius = 0.05
  SupportTransform = false
FEATURE [PartDesign::Fillet] Fillet009
  Base = -> Fillet016 [Edge33]
  BaseFeature = -> Fillet016
  Placement = pos=(-21.5005,18.625,0.235) rot=(0,-1,0;0.174533rad)
  Radius = 0.5
  SupportTransform = false
FEATURE [PartDesign::AdditiveBox] Box031
  AttacherType = Attacher::AttachEngine3D
  AttachmentOffset = pos=(-21.1,18.635,0.305) rot=(0,1,0;0.785398rad)
  BaseFeature = -> Fillet009
  Height = 0.375
  Length = 0.2
  MapMode = 5
  Placement = pos=(-21.1,18.635,0.305) rot=(0,1,0;0.785398rad)
  Support = -> [XY_Plane005]
  Width = 0.23
FEATURE [PartDesign::SubtractiveCylinder] Cylinder010
  Angle = 360
  AttacherType = Attacher::AttachEngine3D
  AttachmentOffset = pos=(-21.055,18.935,0.52) rot=(1,0,0;1.5708rad)
  BaseFeature = -> Box031
  Height = 0.375
  MapMode = 5
  Placement = pos=(-21.055,18.935,0.52) rot=(1,0,0;1.5708rad)
  Radius = 0.205
  Support = -> [XY_Plane005]
FEATURE [PartDesign::SubtractiveBox] Box033
  AttacherType = Attacher::AttachEngine3D
  AttachmentOffset = pos=(-20.95,18.635,0.53) rot=(0,0,1;0rad)
  BaseFeature = -> Cylinder010
  Height = 0.5
  Length = 0.1
  MapMode = 5
  Placement = pos=(-20.95,18.635,0.53) rot=(0,0,1;0rad)
  Support = -> [XY_Plane005]
  Width = 0.23
FEATURE [PartDesign::SubtractiveBox] Box032
  AttacherType = Attacher::AttachEngine3D
  AttachmentOffset = pos=(-21.15,18.635,0.297) rot=(0,-1,0;0.174533rad)
  BaseFeature = -> Box033
  Height = 0.115
  Length = 0.115
  MapMode = 5
  Placement = pos=(-21.15,18.635,0.297) rot=(0,-1,0;0.174533rad)
  Support = -> [XY_Plane005]
  Width = 0.23
FEATURE [PartDesign::Fillet] Fillet017
  Base = -> Box032 [Edge28]
  BaseFeature = -> Box032
  Placement = pos=(-21.15,18.635,0.297) rot=(0,-1,0;0.174533rad)
  Radius = 0.375
  SupportTransform = false
FEATURE [PartDesign::AdditiveBox] Box037
  AttacherType = Attacher::AttachEngine3D
  AttachmentOffset = pos=(-20.7,18.635,1.55) rot=(0,1,0;0.785398rad)
  BaseFeature = -> Fillet017
  Height = 0.375
  Length = 0.23
  MapMode = 5
  Placement = pos=(-20.7,18.635,1.55) rot=(0,1,0;0.785398rad)
  Support = -> [XY_Plane005]
  Width = 0.23
FEATURE [PartDesign::SubtractiveCylinder] Cylinder011
  Angle = 360
  AttacherType = Attacher::AttachEngine3D
  AttachmentOffset = pos=(-20.271,18.635,1.4056) rot=(-1,0,0;1.5708rad)
  BaseFeature = -> Box037
  Height = 0.23
  MapMode = 5
  Placement = pos=(-20.271,18.635,1.4056) rot=(-1,0,0;1.5708rad)
  Radius = 0.23
  Support = -> [XY_Plane005]
FEATURE [PartDesign::AdditiveBox] Box043
  AttacherType = Attacher::AttachEngine3D
  AttachmentOffset = pos=(-20.1,18.635,1.635) rot=(0,0,1;0rad)
  BaseFeature = -> Cylinder011
  Height = 0.265
  Length = 0.23
  MapMode = 5
  Placement = pos=(-20.1,18.635,1.635) rot=(0,0,1;0rad)
  Support = -> [XY_Plane005]
  Width = 0.23
FEATURE [PartDesign::Body] Body004  label="pin004"
  Group = -> [Box059,Box060,Box034,Box036,Box056,Fillet016,Fillet009,Box031,Cylinder010,Box033,Box032,Fillet017,Box037,Cylinder011,Box043]
  Origin = -> Origin004
  Placement = pos=(0,-1.5,0) rot=(0,0,1;0rad)
  Tip = -> Box043
FEATURE [PartDesign::AdditiveBox] Box075
  AttacherType = Attacher::AttachEngine3D
  AttachmentOffset = pos=(-21.3,18.635,0) rot=(0,0,1;0rad)
  Height = 1.9
  Length = 1.3
  MapMode = 5
  Placement = pos=(-21.3,18.635,0) rot=(0,0,1;0rad)
  Support = -> [XY_Plane010]
  Width = 0.23
FEATURE [PartDesign::SubtractiveBox] Box078
  AttacherType = Attacher::AttachEngine3D
  AttachmentOffset = pos=(-21.35,18.635,0.35) rot=(0,0,1;0rad)
  BaseFeature = -> Box075
  Height = 1.55
  Length = 0.5
  MapMode = 5
  Placement = pos=(-21.35,18.635,0.35) rot=(0,0,1;0rad)
  Support = -> [XY_Plane010]
  Width = 0.23
FEATURE [PartDesign::SubtractiveBox] Box071
  AttacherType = Attacher::AttachEngine3D
  AttachmentOffset = pos=(-20.5,18.63,0) rot=(0,0,1;0rad)
  BaseFeature = -> Box078
  Height = 1.635
  Length = 0.5
  MapMode = 5
  Placement = pos=(-20.5,18.63,0) rot=(0,0,1;0rad)
  Support = -> [XY_Plane010]
  Width = 0.25
FEATURE [PartDesign::SubtractiveBox] Box080
  AttacherType = Attacher::AttachEngine3D
  AttachmentOffset = pos=(-21.19,18.635,-0.12) rot=(0,-1,0;0.15708rad)
  BaseFeature = -> Box071
  Height = 0.12
  Length = 0.725
  MapMode = 5
  Placement = pos=(-21.19,18.635,-0.12) rot=(0,-1,0;0.15708rad)
  Support = -> [XY_Plane010]
  Width = 0.25
FEATURE [PartDesign::SubtractiveBox] Box081
  AttacherType = Attacher::AttachEngine3D
  AttachmentOffset = pos=(-21.5005,18.625,0.235) rot=(0,-1,0;0.174533rad)
  BaseFeature = -> Box080
  Height = 0.3
  Length = 0.6605
  MapMode = 5
  Placement = pos=(-21.5005,18.625,0.235) rot=(0,-1,0;0.174533rad)
  Support = -> [XY_Plane010]
  Width = 0.25
FEATURE [PartDesign::AdditiveBox] Box087
  AttacherType = Attacher::AttachEngine3D
  AttachmentOffset = pos=(-21.3,18.635,0) rot=(0,0,1;0rad)
  Height = 1.9
  Length = 1.3
  MapMode = 5
  Placement = pos=(-21.3,18.635,0) rot=(0,0,1;0rad)
  Support = -> [XY_Plane007]
  Width = 0.23
FEATURE [PartDesign::SubtractiveBox] Box090
  AttacherType = Attacher::AttachEngine3D
  AttachmentOffset = pos=(-21.35,18.635,0.35) rot=(0,0,1;0rad)
  BaseFeature = -> Box087
  Height = 1.55
  Length = 0.5
  MapMode = 5
  Placement = pos=(-21.35,18.635,0.35) rot=(0,0,1;0rad)
  Support = -> [XY_Plane007]
  Width = 0.23
FEATURE [PartDesign::SubtractiveBox] Box069
  AttacherType = Attacher::AttachEngine3D
  AttachmentOffset = pos=(-20.5,18.63,0) rot=(0,0,1;0rad)
  BaseFeature = -> Box090
  Height = 1.635
  Length = 0.5
  MapMode = 5
  Placement = pos=(-20.5,18.63,0) rot=(0,0,1;0rad)
  Support = -> [XY_Plane007]
  Width = 0.25
FEATURE [PartDesign::SubtractiveBox] Box077
  AttacherType = Attacher::AttachEngine3D
  AttachmentOffset = pos=(-21.19,18.635,-0.12) rot=(0,-1,0;0.15708rad)
  BaseFeature = -> Box069
  Height = 0.12
  Length = 0.725
  MapMode = 5
  Placement = pos=(-21.19,18.635,-0.12) rot=(0,-1,0;0.15708rad)
  Support = -> [XY_Plane007]
  Width = 0.25
FEATURE [PartDesign::SubtractiveBox] Box086
  AttacherType = Attacher::AttachEngine3D
  AttachmentOffset = pos=(-21.5005,18.625,0.235) rot=(0,-1,0;0.174533rad)
  BaseFeature = -> Box077
  Height = 0.3
  Length = 0.6605
  MapMode = 5
  Placement = pos=(-21.5005,18.625,0.235) rot=(0,-1,0;0.174533rad)
  Support = -> [XY_Plane007]
  Width = 0.25
FEATURE [PartDesign::AdditiveBox] Box091
  AttacherType = Attacher::AttachEngine3D
  AttachmentOffset = pos=(-21.3,18.635,0) rot=(0,0,1;0rad)
  Height = 1.9
  Length = 1.3
  MapMode = 5
  Placement = pos=(-21.3,18.635,0) rot=(0,0,1;0rad)
  Support = -> [XY_Plane011]
  Width = 0.23
FEATURE [PartDesign::SubtractiveBox] Box089
  AttacherType = Attacher::AttachEngine3D
  AttachmentOffset = pos=(-21.35,18.635,0.35) rot=(0,0,1;0rad)
  BaseFeature = -> Box091
  Height = 1.55
  Length = 0.5
  MapMode = 5
  Placement = pos=(-21.35,18.635,0.35) rot=(0,0,1;0rad)
  Support = -> [XY_Plane011]
  Width = 0.23
FEATURE [PartDesign::SubtractiveBox] Box068
  AttacherType = Attacher::AttachEngine3D
  AttachmentOffset = pos=(-20.5,18.63,0) rot=(0,0,1;0rad)
  BaseFeature = -> Box089
  Height = 1.635
  Length = 0.5
  MapMode = 5
  Placement = pos=(-20.5,18.63,0) rot=(0,0,1;0rad)
  Support = -> [XY_Plane011]
  Width = 0.25
FEATURE [PartDesign::SubtractiveBox] Box070
  AttacherType = Attacher::AttachEngine3D
  AttachmentOffset = pos=(-21.19,18.635,-0.12) rot=(0,-1,0;0.15708rad)
  BaseFeature = -> Box068
  Height = 0.12
  Length = 0.725
  MapMode = 5
  Placement = pos=(-21.19,18.635,-0.12) rot=(0,-1,0;0.15708rad)
  Support = -> [XY_Plane011]
  Width = 0.25
FEATURE [PartDesign::SubtractiveBox] Box088
  AttacherType = Attacher::AttachEngine3D
  AttachmentOffset = pos=(-21.5005,18.625,0.235) rot=(0,-1,0;0.174533rad)
  BaseFeature = -> Box070
  Height = 0.3
  Length = 0.6605
  MapMode = 5
  Placement = pos=(-21.5005,18.625,0.235) rot=(0,-1,0;0.174533rad)
  Support = -> [XY_Plane011]
  Width = 0.25
FEATURE [PartDesign::Fillet] Fillet025
  Base = -> Box081 [Edge2]
  BaseFeature = -> Box081
  Placement = pos=(-21.5005,18.625,0.235) rot=(0,-1,0;0.174533rad)
  Radius = 0.05
  SupportTransform = false
FEATURE [PartDesign::Fillet] Fillet027
  Base = -> Fillet025 [Edge33]
  BaseFeature = -> Fillet025
  Placement = pos=(-21.5005,18.625,0.235) rot=(0,-1,0;0.174533rad)
  Radius = 0.5
  SupportTransform = false
FEATURE [PartDesign::AdditiveBox] Box062
  AttacherType = Attacher::AttachEngine3D
  AttachmentOffset = pos=(-21.1,18.635,0.305) rot=(0,1,0;0.785398rad)
  BaseFeature = -> Fillet027
  Height = 0.375
  Length = 0.2
  MapMode = 5
  Placement = pos=(-21.1,18.635,0.305) rot=(0,1,0;0.785398rad)
  Support = -> [XY_Plane010]
  Width = 0.23
FEATURE [PartDesign::SubtractiveCylinder] Cylinder018
  Angle = 360
  AttacherType = Attacher::AttachEngine3D
  AttachmentOffset = pos=(-21.055,18.935,0.52) rot=(1,0,0;1.5708rad)
  BaseFeature = -> Box062
  Height = 0.375
  MapMode = 5
  Placement = pos=(-21.055,18.935,0.52) rot=(1,0,0;1.5708rad)
  Radius = 0.205
  Support = -> [XY_Plane010]
FEATURE [PartDesign::SubtractiveBox] Box083
  AttacherType = Attacher::AttachEngine3D
  AttachmentOffset = pos=(-20.95,18.635,0.53) rot=(0,0,1;0rad)
  BaseFeature = -> Cylinder018
  Height = 0.5
  Length = 0.1
  MapMode = 5
  Placement = pos=(-20.95,18.635,0.53) rot=(0,0,1;0rad)
  Support = -> [XY_Plane010]
  Width = 0.23
FEATURE [PartDesign::SubtractiveBox] Box073
  AttacherType = Attacher::AttachEngine3D
  AttachmentOffset = pos=(-21.15,18.635,0.297) rot=(0,-1,0;0.174533rad)
  BaseFeature = -> Box083
  Height = 0.115
  Length = 0.115
  MapMode = 5
  Placement = pos=(-21.15,18.635,0.297) rot=(0,-1,0;0.174533rad)
  Support = -> [XY_Plane010]
  Width = 0.23
FEATURE [PartDesign::Fillet] Fillet026
  Base = -> Box073 [Edge28]
  BaseFeature = -> Box073
  Placement = pos=(-21.15,18.635,0.297) rot=(0,-1,0;0.174533rad)
  Radius = 0.375
  SupportTransform = false
FEATURE [PartDesign::AdditiveBox] Box072
  AttacherType = Attacher::AttachEngine3D
  AttachmentOffset = pos=(-20.7,18.635,1.55) rot=(0,1,0;0.785398rad)
  BaseFeature = -> Fillet026
  Height = 0.375
  Length = 0.23
  MapMode = 5
  Placement = pos=(-20.7,18.635,1.55) rot=(0,1,0;0.785398rad)
  Support = -> [XY_Plane010]
  Width = 0.23
FEATURE [PartDesign::SubtractiveCylinder] Cylinder020
  Angle = 360
  AttacherType = Attacher::AttachEngine3D
  AttachmentOffset = pos=(-20.271,18.635,1.4056) rot=(-1,0,0;1.5708rad)
  BaseFeature = -> Box072
  Height = 0.23
  MapMode = 5
  Placement = pos=(-20.271,18.635,1.4056) rot=(-1,0,0;1.5708rad)
  Radius = 0.23
  Support = -> [XY_Plane010]
FEATURE [PartDesign::AdditiveBox] Box082
  AttacherType = Attacher::AttachEngine3D
  AttachmentOffset = pos=(-20.1,18.635,1.635) rot=(0,0,1;0rad)
  BaseFeature = -> Cylinder020
  Height = 0.265
  Length = 0.23
  MapMode = 5
  Placement = pos=(-20.1,18.635,1.635) rot=(0,0,1;0rad)
  Support = -> [XY_Plane010]
  Width = 0.23
FEATURE [PartDesign::Body] Body011  label="pin011"
  Group = -> [Box075,Box078,Box071,Box080,Box081,Fillet025,Fillet027,Box062,Cylinder018,Box083,Box073,Fillet026,Box072,Cylinder020,Box082]
  Origin = -> Origin011
  Placement = pos=(0,-5,0) rot=(0,0,1;0rad)
  Tip = -> Box082
FEATURE [PartDesign::Fillet] Fillet028
  Base = -> Box086 [Edge2]
  BaseFeature = -> Box086
  Placement = pos=(-21.5005,18.625,0.235) rot=(0,-1,0;0.174533rad)
  Radius = 0.05
  SupportTransform = false
FEATURE [PartDesign::Fillet] Fillet029
  Base = -> Fillet028 [Edge33]
  BaseFeature = -> Fillet028
  Placement = pos=(-21.5005,18.625,0.235) rot=(0,-1,0;0.174533rad)
  Radius = 0.5
  SupportTransform = false
FEATURE [PartDesign::AdditiveBox] Box074
  AttacherType = Attacher::AttachEngine3D
  AttachmentOffset = pos=(-21.1,18.635,0.305) rot=(0,1,0;0.785398rad)
  BaseFeature = -> Fillet029
  Height = 0.375
  Length = 0.2
  MapMode = 5
  Placement = pos=(-21.1,18.635,0.305) rot=(0,1,0;0.785398rad)
  Support = -> [XY_Plane007]
  Width = 0.23
FEATURE [PartDesign::SubtractiveCylinder] Cylinder019
  Angle = 360
  AttacherType = Attacher::AttachEngine3D
  AttachmentOffset = pos=(-21.055,18.935,0.52) rot=(1,0,0;1.5708rad)
  BaseFeature = -> Box074
  Height = 0.375
  MapMode = 5
  Placement = pos=(-21.055,18.935,0.52) rot=(1,0,0;1.5708rad)
  Radius = 0.205
  Support = -> [XY_Plane007]
FEATURE [PartDesign::SubtractiveBox] Box079
  AttacherType = Attacher::AttachEngine3D
  AttachmentOffset = pos=(-20.95,18.635,0.53) rot=(0,0,1;0rad)
  BaseFeature = -> Cylinder019
  Height = 0.5
  Length = 0.1
  MapMode = 5
  Placement = pos=(-20.95,18.635,0.53) rot=(0,0,1;0rad)
  Support = -> [XY_Plane007]
  Width = 0.23
FEATURE [PartDesign::SubtractiveBox] Box085
  AttacherType = Attacher::AttachEngine3D
  AttachmentOffset = pos=(-21.15,18.635,0.297) rot=(0,-1,0;0.174533rad)
  BaseFeature = -> Box079
  Height = 0.115
  Length = 0.115
  MapMode = 5
  Placement = pos=(-21.15,18.635,0.297) rot=(0,-1,0;0.174533rad)
  Support = -> [XY_Plane007]
  Width = 0.23
FEATURE [PartDesign::Fillet] Fillet019
  Base = -> Box085 [Edge28]
  BaseFeature = -> Box085
  Placement = pos=(-21.15,18.635,0.297) rot=(0,-1,0;0.174533rad)
  Radius = 0.375
  SupportTransform = false
FEATURE [PartDesign::AdditiveBox] Box084
  AttacherType = Attacher::AttachEngine3D
  AttachmentOffset = pos=(-20.7,18.635,1.55) rot=(0,1,0;0.785398rad)
  BaseFeature = -> Fillet019
  Height = 0.375
  Length = 0.23
  MapMode = 5
  Placement = pos=(-20.7,18.635,1.55) rot=(0,1,0;0.785398rad)
  Support = -> [XY_Plane007]
  Width = 0.23
FEATURE [PartDesign::SubtractiveCylinder] Cylinder021
  Angle = 360
  AttacherType = Attacher::AttachEngine3D
  AttachmentOffset = pos=(-20.271,18.635,1.4056) rot=(-1,0,0;1.5708rad)
  BaseFeature = -> Box084
  Height = 0.23
  MapMode = 5
  Placement = pos=(-20.271,18.635,1.4056) rot=(-1,0,0;1.5708rad)
  Radius = 0.23
  Support = -> [XY_Plane007]
FEATURE [PartDesign::AdditiveBox] Box076
  AttacherType = Attacher::AttachEngine3D
  AttachmentOffset = pos=(-20.1,18.635,1.635) rot=(0,0,1;0rad)
  BaseFeature = -> Cylinder021
  Height = 0.265
  Length = 0.23
  MapMode = 5
  Placement = pos=(-20.1,18.635,1.635) rot=(0,0,1;0rad)
  Support = -> [XY_Plane007]
  Width = 0.23
FEATURE [PartDesign::Body] Body012  label="pin012"
  Group = -> [Box087,Box090,Box069,Box077,Box086,Fillet028,Fillet029,Box074,Cylinder019,Box079,Box085,Fillet019,Box084,Cylinder021,Box076]
  Origin = -> Origin012
  Placement = pos=(0,-5.5,0) rot=(0,0,1;0rad)
  Tip = -> Box076
FEATURE [PartDesign::AdditiveBox] Box108
  AttacherType = Attacher::AttachEngine3D
  AttachmentOffset = pos=(-21.3,18.635,0) rot=(0,0,1;0rad)
  Height = 1.9
  Length = 1.3
  MapMode = 5
  Placement = pos=(-21.3,18.635,0) rot=(0,0,1;0rad)
  Support = -> [XY_Plane012]
  Width = 0.23
FEATURE [PartDesign::SubtractiveBox] Box109
  AttacherType = Attacher::AttachEngine3D
  AttachmentOffset = pos=(-21.35,18.635,0.35) rot=(0,0,1;0rad)
  BaseFeature = -> Box108
  Height = 1.55
  Length = 0.5
  MapMode = 5
  Placement = pos=(-21.35,18.635,0.35) rot=(0,0,1;0rad)
  Support = -> [XY_Plane012]
  Width = 0.23
FEATURE [PartDesign::SubtractiveBox] Box098
  AttacherType = Attacher::AttachEngine3D
  AttachmentOffset = pos=(-20.5,18.63,0) rot=(0,0,1;0rad)
  BaseFeature = -> Box109
  Height = 1.635
  Length = 0.5
  MapMode = 5
  Placement = pos=(-20.5,18.63,0) rot=(0,0,1;0rad)
  Support = -> [XY_Plane012]
  Width = 0.25
FEATURE [PartDesign::SubtractiveBox] Box105
  AttacherType = Attacher::AttachEngine3D
  AttachmentOffset = pos=(-21.19,18.635,-0.12) rot=(0,-1,0;0.15708rad)
  BaseFeature = -> Box098
  Height = 0.12
  Length = 0.725
  MapMode = 5
  Placement = pos=(-21.19,18.635,-0.12) rot=(0,-1,0;0.15708rad)
  Support = -> [XY_Plane012]
  Width = 0.25
FEATURE [PartDesign::SubtractiveBox] Box106
  AttacherType = Attacher::AttachEngine3D
  AttachmentOffset = pos=(-21.5005,18.625,0.235) rot=(0,-1,0;0.174533rad)
  BaseFeature = -> Box105
  Height = 0.3
  Length = 0.6605
  MapMode = 5
  Placement = pos=(-21.5005,18.625,0.235) rot=(0,-1,0;0.174533rad)
  Support = -> [XY_Plane012]
  Width = 0.25
FEATURE [PartDesign::Fillet] Fillet020
  Base = -> Box106 [Edge2]
  BaseFeature = -> Box106
  Placement = pos=(-21.5005,18.625,0.235) rot=(0,-1,0;0.174533rad)
  Radius = 0.05
  SupportTransform = false
FEATURE [PartDesign::Fillet] Fillet021
  Base = -> Fillet020 [Edge33]
  BaseFeature = -> Fillet020
  Placement = pos=(-21.5005,18.625,0.235) rot=(0,-1,0;0.174533rad)
  Radius = 0.5
  SupportTransform = false
FEATURE [PartDesign::AdditiveBox] Box100
  AttacherType = Attacher::AttachEngine3D
  AttachmentOffset = pos=(-21.1,18.635,0.305) rot=(0,1,0;0.785398rad)
  BaseFeature = -> Fillet021
  Height = 0.375
  Length = 0.2
  MapMode = 5
  Placement = pos=(-21.1,18.635,0.305) rot=(0,1,0;0.785398rad)
  Support = -> [XY_Plane012]
  Width = 0.23
FEATURE [PartDesign::SubtractiveCylinder] Cylinder024
  Angle = 360
  AttacherType = Attacher::AttachEngine3D
  AttachmentOffset = pos=(-21.055,18.935,0.52) rot=(1,0,0;1.5708rad)
  BaseFeature = -> Box100
  Height = 0.375
  MapMode = 5
  Placement = pos=(-21.055,18.935,0.52) rot=(1,0,0;1.5708rad)
  Radius = 0.205
  Support = -> [XY_Plane012]
FEATURE [PartDesign::SubtractiveBox] Box104
  AttacherType = Attacher::AttachEngine3D
  AttachmentOffset = pos=(-20.95,18.635,0.53) rot=(0,0,1;0rad)
  BaseFeature = -> Cylinder024
  Height = 0.5
  Length = 0.1
  MapMode = 5
  Placement = pos=(-20.95,18.635,0.53) rot=(0,0,1;0rad)
  Support = -> [XY_Plane012]
  Width = 0.23
FEATURE [PartDesign::SubtractiveBox] Box101
  AttacherType = Attacher::AttachEngine3D
  AttachmentOffset = pos=(-21.15,18.635,0.297) rot=(0,-1,0;0.174533rad)
  BaseFeature = -> Box104
  Height = 0.115
  Length = 0.115
  MapMode = 5
  Placement = pos=(-21.15,18.635,0.297) rot=(0,-1,0;0.174533rad)
  Support = -> [XY_Plane012]
  Width = 0.23
FEATURE [PartDesign::Fillet] Fillet022
  Base = -> Box101 [Edge28]
  BaseFeature = -> Box101
  Placement = pos=(-21.15,18.635,0.297) rot=(0,-1,0;0.174533rad)
  Radius = 0.375
  SupportTransform = false
FEATURE [PartDesign::AdditiveBox] Box099
  AttacherType = Attacher::AttachEngine3D
  AttachmentOffset = pos=(-20.7,18.635,1.55) rot=(0,1,0;0.785398rad)
  BaseFeature = -> Fillet022
  Height = 0.375
  Length = 0.23
  MapMode = 5
  Placement = pos=(-20.7,18.635,1.55) rot=(0,1,0;0.785398rad)
  Support = -> [XY_Plane012]
  Width = 0.23
FEATURE [PartDesign::SubtractiveCylinder] Cylinder025
  Angle = 360
  AttacherType = Attacher::AttachEngine3D
  AttachmentOffset = pos=(-20.271,18.635,1.4056) rot=(-1,0,0;1.5708rad)
  BaseFeature = -> Box099
  Height = 0.23
  MapMode = 5
  Placement = pos=(-20.271,18.635,1.4056) rot=(-1,0,0;1.5708rad)
  Radius = 0.23
  Support = -> [XY_Plane012]
FEATURE [PartDesign::AdditiveBox] Box107
  AttacherType = Attacher::AttachEngine3D
  AttachmentOffset = pos=(-20.1,18.635,1.635) rot=(0,0,1;0rad)
  BaseFeature = -> Cylinder025
  Height = 0.265
  Length = 0.23
  MapMode = 5
  Placement = pos=(-20.1,18.635,1.635) rot=(0,0,1;0rad)
  Support = -> [XY_Plane012]
  Width = 0.23
FEATURE [PartDesign::Body] Body008  label="pin008"
  Group = -> [Box108,Box109,Box098,Box105,Box106,Fillet020,Fillet021,Box100,Cylinder024,Box104,Box101,Fillet022,Box099,Cylinder025,Box107]
  Origin = -> Origin008
  Placement = pos=(0,-3.5,0) rot=(0,0,1;0rad)
  Tip = -> Box107
FEATURE [PartDesign::AdditiveBox] Box115
  AttacherType = Attacher::AttachEngine3D
  AttachmentOffset = pos=(-21.3,18.635,0) rot=(0,0,1;0rad)
  Height = 1.9
  Length = 1.3
  MapMode = 5
  Placement = pos=(-21.3,18.635,0) rot=(0,0,1;0rad)
  Support = -> [XY_Plane008]
  Width = 0.23
FEATURE [PartDesign::SubtractiveBox] Box118
  AttacherType = Attacher::AttachEngine3D
  AttachmentOffset = pos=(-21.35,18.635,0.35) rot=(0,0,1;0rad)
  BaseFeature = -> Box115
  Height = 1.55
  Length = 0.5
  MapMode = 5
  Placement = pos=(-21.35,18.635,0.35) rot=(0,0,1;0rad)
  Support = -> [XY_Plane008]
  Width = 0.23
FEATURE [PartDesign::SubtractiveBox] Box095
  AttacherType = Attacher::AttachEngine3D
  AttachmentOffset = pos=(-20.5,18.63,0) rot=(0,0,1;0rad)
  BaseFeature = -> Box118
  Height = 1.635
  Length = 0.5
  MapMode = 5
  Placement = pos=(-20.5,18.63,0) rot=(0,0,1;0rad)
  Support = -> [XY_Plane008]
  Width = 0.25
FEATURE [PartDesign::SubtractiveBox] Box114
  AttacherType = Attacher::AttachEngine3D
  AttachmentOffset = pos=(-21.19,18.635,-0.12) rot=(0,-1,0;0.15708rad)
  BaseFeature = -> Box095
  Height = 0.12
  Length = 0.725
  MapMode = 5
  Placement = pos=(-21.19,18.635,-0.12) rot=(0,-1,0;0.15708rad)
  Support = -> [XY_Plane008]
  Width = 0.25
FEATURE [PartDesign::SubtractiveBox] Box112
  AttacherType = Attacher::AttachEngine3D
  AttachmentOffset = pos=(-21.5005,18.625,0.235) rot=(0,-1,0;0.174533rad)
  BaseFeature = -> Box114
  Height = 0.3
  Length = 0.6605
  MapMode = 5
  Placement = pos=(-21.5005,18.625,0.235) rot=(0,-1,0;0.174533rad)
  Support = -> [XY_Plane008]
  Width = 0.25
FEATURE [PartDesign::Fillet] Fillet023
  Base = -> Box112 [Edge2]
  BaseFeature = -> Box112
  Placement = pos=(-21.5005,18.625,0.235) rot=(0,-1,0;0.174533rad)
  Radius = 0.05
  SupportTransform = false
FEATURE [PartDesign::Fillet] Fillet030
  Base = -> Fillet023 [Edge33]
  BaseFeature = -> Fillet023
  Placement = pos=(-21.5005,18.625,0.235) rot=(0,-1,0;0.174533rad)
  Radius = 0.5
  SupportTransform = false
FEATURE [PartDesign::AdditiveBox] Box102
  AttacherType = Attacher::AttachEngine3D
  AttachmentOffset = pos=(-21.1,18.635,0.305) rot=(0,1,0;0.785398rad)
  BaseFeature = -> Fillet030
  Height = 0.375
  Length = 0.2
  MapMode = 5
  Placement = pos=(-21.1,18.635,0.305) rot=(0,1,0;0.785398rad)
  Support = -> [XY_Plane008]
  Width = 0.23
FEATURE [PartDesign::SubtractiveCylinder] Cylinder026
  Angle = 360
  AttacherType = Attacher::AttachEngine3D
  AttachmentOffset = pos=(-21.055,18.935,0.52) rot=(1,0,0;1.5708rad)
  BaseFeature = -> Box102
  Height = 0.375
  MapMode = 5
  Placement = pos=(-21.055,18.935,0.52) rot=(1,0,0;1.5708rad)
  Radius = 0.205
  Support = -> [XY_Plane008]
FEATURE [PartDesign::SubtractiveBox] Box117
  AttacherType = Attacher::AttachEngine3D
  AttachmentOffset = pos=(-20.95,18.635,0.53) rot=(0,0,1;0rad)
  BaseFeature = -> Cylinder026
  Height = 0.5
  Length = 0.1
  MapMode = 5
  Placement = pos=(-20.95,18.635,0.53) rot=(0,0,1;0rad)
  Support = -> [XY_Plane008]
  Width = 0.23
FEATURE [PartDesign::SubtractiveBox] Box111
  AttacherType = Attacher::AttachEngine3D
  AttachmentOffset = pos=(-21.15,18.635,0.297) rot=(0,-1,0;0.174533rad)
  BaseFeature = -> Box117
  Height = 0.115
  Length = 0.115
  MapMode = 5
  Placement = pos=(-21.15,18.635,0.297) rot=(0,-1,0;0.174533rad)
  Support = -> [XY_Plane008]
  Width = 0.23
FEATURE [PartDesign::Fillet] Fillet031
  Base = -> Box111 [Edge28]
  BaseFeature = -> Box111
  Placement = pos=(-21.15,18.635,0.297) rot=(0,-1,0;0.174533rad)
  Radius = 0.375
  SupportTransform = false
FEATURE [PartDesign::AdditiveBox] Box110
  AttacherType = Attacher::AttachEngine3D
  AttachmentOffset = pos=(-20.7,18.635,1.55) rot=(0,1,0;0.785398rad)
  BaseFeature = -> Fillet031
  Height = 0.375
  Length = 0.23
  MapMode = 5
  Placement = pos=(-20.7,18.635,1.55) rot=(0,1,0;0.785398rad)
  Support = -> [XY_Plane008]
  Width = 0.23
FEATURE [PartDesign::SubtractiveCylinder] Cylinder027
  Angle = 360
  AttacherType = Attacher::AttachEngine3D
  AttachmentOffset = pos=(-20.271,18.635,1.4056) rot=(-1,0,0;1.5708rad)
  BaseFeature = -> Box110
  Height = 0.23
  MapMode = 5
  Placement = pos=(-20.271,18.635,1.4056) rot=(-1,0,0;1.5708rad)
  Radius = 0.23
  Support = -> [XY_Plane008]
FEATURE [PartDesign::AdditiveBox] Box113
  AttacherType = Attacher::AttachEngine3D
  AttachmentOffset = pos=(-20.1,18.635,1.635) rot=(0,0,1;0rad)
  BaseFeature = -> Cylinder027
  Height = 0.265
  Length = 0.23
  MapMode = 5
  Placement = pos=(-20.1,18.635,1.635) rot=(0,0,1;0rad)
  Support = -> [XY_Plane008]
  Width = 0.23
FEATURE [PartDesign::Body] Body009  label="pin009"
  Group = -> [Box115,Box118,Box095,Box114,Box112,Fillet023,Fillet030,Box102,Cylinder026,Box117,Box111,Fillet031,Box110,Cylinder027,Box113]
  Origin = -> Origin009
  Placement = pos=(0,-4,0) rot=(0,0,1;0rad)
  Tip = -> Box113
FEATURE [PartDesign::AdditiveBox] Box119
  AttacherType = Attacher::AttachEngine3D
  AttachmentOffset = pos=(-21.3,18.635,0) rot=(0,0,1;0rad)
  Height = 1.9
  Length = 1.3
  MapMode = 5
  Placement = pos=(-21.3,18.635,0) rot=(0,0,1;0rad)
  Support = -> [XY_Plane009]
  Width = 0.23
FEATURE [PartDesign::Fillet] Fillet034
  Base = -> Box088 [Edge2]
  BaseFeature = -> Box088
  Placement = pos=(-21.5005,18.625,0.235) rot=(0,-1,0;0.174533rad)
  Radius = 0.05
  SupportTransform = false
FEATURE [PartDesign::Fillet] Fillet024
  Base = -> Fillet034 [Edge33]
  BaseFeature = -> Fillet034
  Placement = pos=(-21.5005,18.625,0.235) rot=(0,-1,0;0.174533rad)
  Radius = 0.5
  SupportTransform = false
FEATURE [PartDesign::AdditiveBox] Box065
  AttacherType = Attacher::AttachEngine3D
  AttachmentOffset = pos=(-21.1,18.635,0.305) rot=(0,1,0;0.785398rad)
  BaseFeature = -> Fillet024
  Height = 0.375
  Length = 0.2
  MapMode = 5
  Placement = pos=(-21.1,18.635,0.305) rot=(0,1,0;0.785398rad)
  Support = -> [XY_Plane011]
  Width = 0.23
FEATURE [PartDesign::SubtractiveCylinder] Cylinder017
  Angle = 360
  AttacherType = Attacher::AttachEngine3D
  AttachmentOffset = pos=(-21.055,18.935,0.52) rot=(1,0,0;1.5708rad)
  BaseFeature = -> Box065
  Height = 0.375
  MapMode = 5
  Placement = pos=(-21.055,18.935,0.52) rot=(1,0,0;1.5708rad)
  Radius = 0.205
  Support = -> [XY_Plane011]
FEATURE [PartDesign::SubtractiveBox] Box067
  AttacherType = Attacher::AttachEngine3D
  AttachmentOffset = pos=(-20.95,18.635,0.53) rot=(0,0,1;0rad)
  BaseFeature = -> Cylinder017
  Height = 0.5
  Length = 0.1
  MapMode = 5
  Placement = pos=(-20.95,18.635,0.53) rot=(0,0,1;0rad)
  Support = -> [XY_Plane011]
  Width = 0.23
FEATURE [PartDesign::SubtractiveBox] Box066
  AttacherType = Attacher::AttachEngine3D
  AttachmentOffset = pos=(-21.15,18.635,0.297) rot=(0,-1,0;0.174533rad)
  BaseFeature = -> Box067
  Height = 0.115
  Length = 0.115
  MapMode = 5
  Placement = pos=(-21.15,18.635,0.297) rot=(0,-1,0;0.174533rad)
  Support = -> [XY_Plane011]
  Width = 0.23
FEATURE [PartDesign::Fillet] Fillet033
  Base = -> Box066 [Edge28]
  BaseFeature = -> Box066
  Placement = pos=(-21.15,18.635,0.297) rot=(0,-1,0;0.174533rad)
  Radius = 0.375
  SupportTransform = false
FEATURE [PartDesign::AdditiveBox] Box064
  AttacherType = Attacher::AttachEngine3D
  AttachmentOffset = pos=(-20.7,18.635,1.55) rot=(0,1,0;0.785398rad)
  BaseFeature = -> Fillet033
  Height = 0.375
  Length = 0.23
  MapMode = 5
  Placement = pos=(-20.7,18.635,1.55) rot=(0,1,0;0.785398rad)
  Support = -> [XY_Plane011]
  Width = 0.23
FEATURE [PartDesign::SubtractiveCylinder] Cylinder016
  Angle = 360
  AttacherType = Attacher::AttachEngine3D
  AttachmentOffset = pos=(-20.271,18.635,1.4056) rot=(-1,0,0;1.5708rad)
  BaseFeature = -> Box064
  Height = 0.23
  MapMode = 5
  Placement = pos=(-20.271,18.635,1.4056) rot=(-1,0,0;1.5708rad)
  Radius = 0.23
  Support = -> [XY_Plane011]
FEATURE [PartDesign::AdditiveBox] Box063
  AttacherType = Attacher::AttachEngine3D
  AttachmentOffset = pos=(-20.1,18.635,1.635) rot=(0,0,1;0rad)
  BaseFeature = -> Cylinder016
  Height = 0.265
  Length = 0.23
  MapMode = 5
  Placement = pos=(-20.1,18.635,1.635) rot=(0,0,1;0rad)
  Support = -> [XY_Plane011]
  Width = 0.23
FEATURE [PartDesign::Body] Body010  label="pin010"
  Group = -> [Box091,Box089,Box068,Box070,Box088,Fillet034,Fillet024,Box065,Cylinder017,Box067,Box066,Fillet033,Box064,Cylinder016,Box063]
  Origin = -> Origin010
  Placement = pos=(0,-4.5,0) rot=(0,0,1;0rad)
  Tip = -> Box063
FEATURE [PartDesign::SubtractiveBox] Box120
  AttacherType = Attacher::AttachEngine3D
  AttachmentOffset = pos=(-21.35,18.635,0.35) rot=(0,0,1;0rad)
  BaseFeature = -> Box119
  Height = 1.55
  Length = 0.5
  MapMode = 5
  Placement = pos=(-21.35,18.635,0.35) rot=(0,0,1;0rad)
  Support = -> [XY_Plane009]
  Width = 0.23
FEATURE [PartDesign::SubtractiveBox] Box094
  AttacherType = Attacher::AttachEngine3D
  AttachmentOffset = pos=(-20.5,18.63,0) rot=(0,0,1;0rad)
  BaseFeature = -> Box120
  Height = 1.635
  Length = 0.5
  MapMode = 5
  Placement = pos=(-20.5,18.63,0) rot=(0,0,1;0rad)
  Support = -> [XY_Plane009]
  Width = 0.25
FEATURE [PartDesign::SubtractiveBox] Box096
  AttacherType = Attacher::AttachEngine3D
  AttachmentOffset = pos=(-21.19,18.635,-0.12) rot=(0,-1,0;0.15708rad)
  BaseFeature = -> Box094
  Height = 0.12
  Length = 0.725
  MapMode = 5
  Placement = pos=(-21.19,18.635,-0.12) rot=(0,-1,0;0.15708rad)
  Support = -> [XY_Plane009]
  Width = 0.25
FEATURE [PartDesign::SubtractiveBox] Box116
  AttacherType = Attacher::AttachEngine3D
  AttachmentOffset = pos=(-21.5005,18.625,0.235) rot=(0,-1,0;0.174533rad)
  BaseFeature = -> Box096
  Height = 0.3
  Length = 0.6605
  MapMode = 5
  Placement = pos=(-21.5005,18.625,0.235) rot=(0,-1,0;0.174533rad)
  Support = -> [XY_Plane009]
  Width = 0.25
FEATURE [PartDesign::Fillet] Fillet032
  Base = -> Box116 [Edge2]
  BaseFeature = -> Box116
  Placement = pos=(-21.5005,18.625,0.235) rot=(0,-1,0;0.174533rad)
  Radius = 0.05
  SupportTransform = false
FEATURE [PartDesign::Fillet] Fillet018
  Base = -> Fillet032 [Edge33]
  BaseFeature = -> Fillet032
  Placement = pos=(-21.5005,18.625,0.235) rot=(0,-1,0;0.174533rad)
  Radius = 0.5
  SupportTransform = false
FEATURE [PartDesign::AdditiveBox] Box061
  AttacherType = Attacher::AttachEngine3D
  AttachmentOffset = pos=(-21.1,18.635,0.305) rot=(0,1,0;0.785398rad)
  BaseFeature = -> Fillet018
  Height = 0.375
  Length = 0.2
  MapMode = 5
  Placement = pos=(-21.1,18.635,0.305) rot=(0,1,0;0.785398rad)
  Support = -> [XY_Plane009]
  Width = 0.23
FEATURE [PartDesign::SubtractiveCylinder] Cylinder022
  Angle = 360
  AttacherType = Attacher::AttachEngine3D
  AttachmentOffset = pos=(-21.055,18.935,0.52) rot=(1,0,0;1.5708rad)
  BaseFeature = -> Box061
  Height = 0.375
  MapMode = 5
  Placement = pos=(-21.055,18.935,0.52) rot=(1,0,0;1.5708rad)
  Radius = 0.205
  Support = -> [XY_Plane009]
FEATURE [PartDesign::SubtractiveBox] Box093
  AttacherType = Attacher::AttachEngine3D
  AttachmentOffset = pos=(-20.95,18.635,0.53) rot=(0,0,1;0rad)
  BaseFeature = -> Cylinder022
  Height = 0.5
  Length = 0.1
  MapMode = 5
  Placement = pos=(-20.95,18.635,0.53) rot=(0,0,1;0rad)
  Support = -> [XY_Plane009]
  Width = 0.23
FEATURE [PartDesign::SubtractiveBox] Box092
  AttacherType = Attacher::AttachEngine3D
  AttachmentOffset = pos=(-21.15,18.635,0.297) rot=(0,-1,0;0.174533rad)
  BaseFeature = -> Box093
  Height = 0.115
  Length = 0.115
  MapMode = 5
  Placement = pos=(-21.15,18.635,0.297) rot=(0,-1,0;0.174533rad)
  Support = -> [XY_Plane009]
  Width = 0.23
FEATURE [PartDesign::Fillet] Fillet035
  Base = -> Box092 [Edge28]
  BaseFeature = -> Box092
  Placement = pos=(-21.15,18.635,0.297) rot=(0,-1,0;0.174533rad)
  Radius = 0.375
  SupportTransform = false
FEATURE [PartDesign::AdditiveBox] Box097
  AttacherType = Attacher::AttachEngine3D
  AttachmentOffset = pos=(-20.7,18.635,1.55) rot=(0,1,0;0.785398rad)
  BaseFeature = -> Fillet035
  Height = 0.375
  Length = 0.23
  MapMode = 5
  Placement = pos=(-20.7,18.635,1.55) rot=(0,1,0;0.785398rad)
  Support = -> [XY_Plane009]
  Width = 0.23
FEATURE [PartDesign::SubtractiveCylinder] Cylinder023
  Angle = 360
  AttacherType = Attacher::AttachEngine3D
  AttachmentOffset = pos=(-20.271,18.635,1.4056) rot=(-1,0,0;1.5708rad)
  BaseFeature = -> Box097
  Height = 0.23
  MapMode = 5
  Placement = pos=(-20.271,18.635,1.4056) rot=(-1,0,0;1.5708rad)
  Radius = 0.23
  Support = -> [XY_Plane009]
FEATURE [PartDesign::AdditiveBox] Box103
  AttacherType = Attacher::AttachEngine3D
  AttachmentOffset = pos=(-20.1,18.635,1.635) rot=(0,0,1;0rad)
  BaseFeature = -> Cylinder023
  Height = 0.265
  Length = 0.23
  MapMode = 5
  Placement = pos=(-20.1,18.635,1.635) rot=(0,0,1;0rad)
  Support = -> [XY_Plane009]
  Width = 0.23
FEATURE [PartDesign::Body] Body007  label="pin007"
  Group = -> [Box119,Box120,Box094,Box096,Box116,Fillet032,Fillet018,Box061,Cylinder022,Box093,Box092,Fillet035,Box097,Cylinder023,Box103]
  Origin = -> Origin007
  Placement = pos=(0,-3,0) rot=(0,0,1;0rad)
  Tip = -> Box103
FEATURE [App::Part] Part  label="Pin-set1"
  Group = -> [Body001,Body002,Body003,Body004,Body005,Body006,Body007,Body008,Body009,Body010,Body011,Body012]
  Origin = -> Origin013
FEATURE [PartDesign::AdditiveBox] Box129
  AttacherType = Attacher::AttachEngine3D
  AttachmentOffset = pos=(-21.3,18.635,0) rot=(0,0,1;0rad)
  Height = 1.9
  Length = 1.3
  MapMode = 5
  Placement = pos=(-21.3,18.635,0) rot=(0,0,1;0rad)
  Support = -> [XY_Plane025]
  Width = 0.23
FEATURE [PartDesign::SubtractiveBox] Box122
  AttacherType = Attacher::AttachEngine3D
  AttachmentOffset = pos=(-21.35,18.635,0.35) rot=(0,0,1;0rad)
  BaseFeature = -> Box129
  Height = 1.55
  Length = 0.5
  MapMode = 5
  Placement = pos=(-21.35,18.635,0.35) rot=(0,0,1;0rad)
  Support = -> [XY_Plane025]
  Width = 0.23
FEATURE [PartDesign::AdditiveBox] Box132
  AttacherType = Attacher::AttachEngine3D
  AttachmentOffset = pos=(-21.3,18.635,0) rot=(0,0,1;0rad)
  Height = 1.9
  Length = 1.3
  MapMode = 5
  Placement = pos=(-21.3,18.635,0) rot=(0,0,1;0rad)
  Support = -> [XY_Plane021]
  Width = 0.23
FEATURE [PartDesign::SubtractiveBox] Box127
  AttacherType = Attacher::AttachEngine3D
  AttachmentOffset = pos=(-21.35,18.635,0.35) rot=(0,0,1;0rad)
  BaseFeature = -> Box132
  Height = 1.55
  Length = 0.5
  MapMode = 5
  Placement = pos=(-21.35,18.635,0.35) rot=(0,0,1;0rad)
  Support = -> [XY_Plane021]
  Width = 0.23
FEATURE [PartDesign::AdditiveBox] Box135
  AttacherType = Attacher::AttachEngine3D
  AttachmentOffset = pos=(-21.3,18.635,0) rot=(0,0,1;0rad)
  Height = 1.9
  Length = 1.3
  MapMode = 5
  Placement = pos=(-21.3,18.635,0) rot=(0,0,1;0rad)
  Support = -> [XY_Plane020]
  Width = 0.23
FEATURE [PartDesign::SubtractiveBox] Box136
  AttacherType = Attacher::AttachEngine3D
  AttachmentOffset = pos=(-21.35,18.635,0.35) rot=(0,0,1;0rad)
  BaseFeature = -> Box135
  Height = 1.55
  Length = 0.5
  MapMode = 5
  Placement = pos=(-21.35,18.635,0.35) rot=(0,0,1;0rad)
  Support = -> [XY_Plane020]
  Width = 0.23
FEATURE [PartDesign::AdditiveBox] Box151
  AttacherType = Attacher::AttachEngine3D
  AttachmentOffset = pos=(-21.3,18.635,0) rot=(0,0,1;0rad)
  Height = 1.9
  Length = 1.3
  MapMode = 5
  Placement = pos=(-21.3,18.635,0) rot=(0,0,1;0rad)
  Support = -> [XY_Plane017]
  Width = 0.23
FEATURE [PartDesign::SubtractiveBox] Box154
  AttacherType = Attacher::AttachEngine3D
  AttachmentOffset = pos=(-21.35,18.635,0.35) rot=(0,0,1;0rad)
  BaseFeature = -> Box151
  Height = 1.55
  Length = 0.5
  MapMode = 5
  Placement = pos=(-21.35,18.635,0.35) rot=(0,0,1;0rad)
  Support = -> [XY_Plane017]
  Width = 0.23
FEATURE [PartDesign::SubtractiveBox] Box147
  AttacherType = Attacher::AttachEngine3D
  AttachmentOffset = pos=(-20.5,18.63,0) rot=(0,0,1;0rad)
  BaseFeature = -> Box154
  Height = 1.635
  Length = 0.5
  MapMode = 5
  Placement = pos=(-20.5,18.63,0) rot=(0,0,1;0rad)
  Support = -> [XY_Plane017]
  Width = 0.25
FEATURE [PartDesign::SubtractiveBox] Box156
  AttacherType = Attacher::AttachEngine3D
  AttachmentOffset = pos=(-21.19,18.635,-0.12) rot=(0,-1,0;0.15708rad)
  BaseFeature = -> Box147
  Height = 0.12
  Length = 0.725
  MapMode = 5
  Placement = pos=(-21.19,18.635,-0.12) rot=(0,-1,0;0.15708rad)
  Support = -> [XY_Plane017]
  Width = 0.25
FEATURE [PartDesign::SubtractiveBox] Box157
  AttacherType = Attacher::AttachEngine3D
  AttachmentOffset = pos=(-21.5005,18.625,0.235) rot=(0,-1,0;0.174533rad)
  BaseFeature = -> Box156
  Height = 0.3
  Length = 0.6605
  MapMode = 5
  Placement = pos=(-21.5005,18.625,0.235) rot=(0,-1,0;0.174533rad)
  Support = -> [XY_Plane017]
  Width = 0.25
FEATURE [PartDesign::AdditiveBox] Box163
  AttacherType = Attacher::AttachEngine3D
  AttachmentOffset = pos=(-21.3,18.635,0) rot=(0,0,1;0rad)
  Height = 1.9
  Length = 1.3
  MapMode = 5
  Placement = pos=(-21.3,18.635,0) rot=(0,0,1;0rad)
  Support = -> [XY_Plane014]
  Width = 0.23
FEATURE [PartDesign::SubtractiveBox] Box169
  AttacherType = Attacher::AttachEngine3D
  AttachmentOffset = pos=(-21.35,18.635,0.35) rot=(0,0,1;0rad)
  BaseFeature = -> Box163
  Height = 1.55
  Length = 0.5
  MapMode = 5
  Placement = pos=(-21.35,18.635,0.35) rot=(0,0,1;0rad)
  Support = -> [XY_Plane014]
  Width = 0.23
FEATURE [PartDesign::SubtractiveBox] Box145
  AttacherType = Attacher::AttachEngine3D
  AttachmentOffset = pos=(-20.5,18.63,0) rot=(0,0,1;0rad)
  BaseFeature = -> Box169
  Height = 1.635
  Length = 0.5
  MapMode = 5
  Placement = pos=(-20.5,18.63,0) rot=(0,0,1;0rad)
  Support = -> [XY_Plane014]
  Width = 0.25
FEATURE [PartDesign::SubtractiveBox] Box153
  AttacherType = Attacher::AttachEngine3D
  AttachmentOffset = pos=(-21.19,18.635,-0.12) rot=(0,-1,0;0.15708rad)
  BaseFeature = -> Box145
  Height = 0.12
  Length = 0.725
  MapMode = 5
  Placement = pos=(-21.19,18.635,-0.12) rot=(0,-1,0;0.15708rad)
  Support = -> [XY_Plane014]
  Width = 0.25
FEATURE [PartDesign::SubtractiveBox] Box162
  AttacherType = Attacher::AttachEngine3D
  AttachmentOffset = pos=(-21.5005,18.625,0.235) rot=(0,-1,0;0.174533rad)
  BaseFeature = -> Box153
  Height = 0.3
  Length = 0.6605
  MapMode = 5
  Placement = pos=(-21.5005,18.625,0.235) rot=(0,-1,0;0.174533rad)
  Support = -> [XY_Plane014]
  Width = 0.25
FEATURE [PartDesign::AdditiveBox] Box174
  AttacherType = Attacher::AttachEngine3D
  AttachmentOffset = pos=(-21.3,18.635,0) rot=(0,0,1;0rad)
  Height = 1.9
  Length = 1.3
  MapMode = 5
  Placement = pos=(-21.3,18.635,0) rot=(0,0,1;0rad)
  Support = -> [XY_Plane018]
  Width = 0.23
FEATURE [PartDesign::SubtractiveBox] Box165
  AttacherType = Attacher::AttachEngine3D
  AttachmentOffset = pos=(-21.35,18.635,0.35) rot=(0,0,1;0rad)
  BaseFeature = -> Box174
  Height = 1.55
  Length = 0.5
  MapMode = 5
  Placement = pos=(-21.35,18.635,0.35) rot=(0,0,1;0rad)
  Support = -> [XY_Plane018]
  Width = 0.23
FEATURE [PartDesign::SubtractiveBox] Box144
  AttacherType = Attacher::AttachEngine3D
  AttachmentOffset = pos=(-20.5,18.63,0) rot=(0,0,1;0rad)
  BaseFeature = -> Box165
  Height = 1.635
  Length = 0.5
  MapMode = 5
  Placement = pos=(-20.5,18.63,0) rot=(0,0,1;0rad)
  Support = -> [XY_Plane018]
  Width = 0.25
FEATURE [PartDesign::SubtractiveBox] Box146
  AttacherType = Attacher::AttachEngine3D
  AttachmentOffset = pos=(-21.19,18.635,-0.12) rot=(0,-1,0;0.15708rad)
  BaseFeature = -> Box144
  Height = 0.12
  Length = 0.725
  MapMode = 5
  Placement = pos=(-21.19,18.635,-0.12) rot=(0,-1,0;0.15708rad)
  Support = -> [XY_Plane018]
  Width = 0.25
FEATURE [PartDesign::SubtractiveBox] Box164
  AttacherType = Attacher::AttachEngine3D
  AttachmentOffset = pos=(-21.5005,18.625,0.235) rot=(0,-1,0;0.174533rad)
  BaseFeature = -> Box146
  Height = 0.3
  Length = 0.6605
  MapMode = 5
  Placement = pos=(-21.5005,18.625,0.235) rot=(0,-1,0;0.174533rad)
  Support = -> [XY_Plane018]
  Width = 0.25
FEATURE [PartDesign::AdditiveBox] Box180
  AttacherType = Attacher::AttachEngine3D
  AttachmentOffset = pos=(-21.3,18.635,0) rot=(0,0,1;0rad)
  Height = 1.9
  Length = 1.3
  MapMode = 5
  Placement = pos=(-21.3,18.635,0) rot=(0,0,1;0rad)
  Support = -> [XY_Plane022]
  Width = 0.23
FEATURE [PartDesign::SubtractiveBox] Box183
  AttacherType = Attacher::AttachEngine3D
  AttachmentOffset = pos=(-21.35,18.635,0.35) rot=(0,0,1;0rad)
  BaseFeature = -> Box180
  Height = 1.55
  Length = 0.5
  MapMode = 5
  Placement = pos=(-21.35,18.635,0.35) rot=(0,0,1;0rad)
  Support = -> [XY_Plane022]
  Width = 0.23
FEATURE [PartDesign::SubtractiveBox] Box168
  AttacherType = Attacher::AttachEngine3D
  AttachmentOffset = pos=(-20.5,18.63,0) rot=(0,0,1;0rad)
  BaseFeature = -> Box183
  Height = 1.635
  Length = 0.5
  MapMode = 5
  Placement = pos=(-20.5,18.63,0) rot=(0,0,1;0rad)
  Support = -> [XY_Plane022]
  Width = 0.25
FEATURE [PartDesign::SubtractiveBox] Box193
  AttacherType = Attacher::AttachEngine3D
  AttachmentOffset = pos=(-21.19,18.635,-0.12) rot=(0,-1,0;0.15708rad)
  BaseFeature = -> Box168
  Height = 0.12
  Length = 0.725
  MapMode = 5
  Placement = pos=(-21.19,18.635,-0.12) rot=(0,-1,0;0.15708rad)
  Support = -> [XY_Plane022]
  Width = 0.25
FEATURE [PartDesign::SubtractiveBox] Box188
  AttacherType = Attacher::AttachEngine3D
  AttachmentOffset = pos=(-21.5005,18.625,0.235) rot=(0,-1,0;0.174533rad)
  BaseFeature = -> Box193
  Height = 0.3
  Length = 0.6605
  MapMode = 5
  Placement = pos=(-21.5005,18.625,0.235) rot=(0,-1,0;0.174533rad)
  Support = -> [XY_Plane022]
  Width = 0.25
FEATURE [PartDesign::SubtractiveBox] Box196
  AttacherType = Attacher::AttachEngine3D
  AttachmentOffset = pos=(-20.5,18.63,0) rot=(0,0,1;0rad)
  BaseFeature = -> Box127
  Height = 1.635
  Length = 0.5
  MapMode = 5
  Placement = pos=(-20.5,18.63,0) rot=(0,0,1;0rad)
  Support = -> [XY_Plane021]
  Width = 0.25
FEATURE [PartDesign::SubtractiveBox] Box124
  AttacherType = Attacher::AttachEngine3D
  AttachmentOffset = pos=(-21.19,18.635,-0.12) rot=(0,-1,0;0.15708rad)
  BaseFeature = -> Box196
  Height = 0.12
  Length = 0.725
  MapMode = 5
  Placement = pos=(-21.19,18.635,-0.12) rot=(0,-1,0;0.15708rad)
  Support = -> [XY_Plane021]
  Width = 0.25
FEATURE [PartDesign::SubtractiveBox] Box123
  AttacherType = Attacher::AttachEngine3D
  AttachmentOffset = pos=(-21.5005,18.625,0.235) rot=(0,-1,0;0.174533rad)
  BaseFeature = -> Box124
  Height = 0.3
  Length = 0.6605
  MapMode = 5
  Placement = pos=(-21.5005,18.625,0.235) rot=(0,-1,0;0.174533rad)
  Support = -> [XY_Plane021]
  Width = 0.25
FEATURE [PartDesign::AdditiveBox] Box199
  AttacherType = Attacher::AttachEngine3D
  AttachmentOffset = pos=(-21.3,18.635,0) rot=(0,0,1;0rad)
  Height = 1.9
  Length = 1.3
  MapMode = 5
  Placement = pos=(-21.3,18.635,0) rot=(0,0,1;0rad)
  Support = -> [XY_Plane023]
  Width = 0.23
FEATURE [PartDesign::SubtractiveBox] Box197
  AttacherType = Attacher::AttachEngine3D
  AttachmentOffset = pos=(-21.35,18.635,0.35) rot=(0,0,1;0rad)
  BaseFeature = -> Box199
  Height = 1.55
  Length = 0.5
  MapMode = 5
  Placement = pos=(-21.35,18.635,0.35) rot=(0,0,1;0rad)
  Support = -> [XY_Plane023]
  Width = 0.23
FEATURE [PartDesign::SubtractiveBox] Box175
  AttacherType = Attacher::AttachEngine3D
  AttachmentOffset = pos=(-20.5,18.63,0) rot=(0,0,1;0rad)
  BaseFeature = -> Box197
  Height = 1.635
  Length = 0.5
  MapMode = 5
  Placement = pos=(-20.5,18.63,0) rot=(0,0,1;0rad)
  Support = -> [XY_Plane023]
  Width = 0.25
FEATURE [PartDesign::SubtractiveBox] Box178
  AttacherType = Attacher::AttachEngine3D
  AttachmentOffset = pos=(-21.19,18.635,-0.12) rot=(0,-1,0;0.15708rad)
  BaseFeature = -> Box175
  Height = 0.12
  Length = 0.725
  MapMode = 5
  Placement = pos=(-21.19,18.635,-0.12) rot=(0,-1,0;0.15708rad)
  Support = -> [XY_Plane023]
  Width = 0.25
FEATURE [PartDesign::SubtractiveBox] Box202
  AttacherType = Attacher::AttachEngine3D
  AttachmentOffset = pos=(-20.5,18.63,0) rot=(0,0,1;0rad)
  BaseFeature = -> Box136
  Height = 1.635
  Length = 0.5
  MapMode = 5
  Placement = pos=(-20.5,18.63,0) rot=(0,0,1;0rad)
  Support = -> [XY_Plane020]
  Width = 0.25
FEATURE [PartDesign::AdditiveBox] Box203
  AttacherType = Attacher::AttachEngine3D
  AttachmentOffset = pos=(-21.3,18.635,0) rot=(0,0,1;0rad)
  Height = 1.9
  Length = 1.3
  MapMode = 5
  Placement = pos=(-21.3,18.635,0) rot=(0,0,1;0rad)
  Support = -> [XY_Plane019]
  Width = 0.23
FEATURE [PartDesign::SubtractiveBox] Box198
  AttacherType = Attacher::AttachEngine3D
  AttachmentOffset = pos=(-21.35,18.635,0.35) rot=(0,0,1;0rad)
  BaseFeature = -> Box203
  Height = 1.55
  Length = 0.5
  MapMode = 5
  Placement = pos=(-21.35,18.635,0.35) rot=(0,0,1;0rad)
  Support = -> [XY_Plane019]
  Width = 0.23
FEATURE [PartDesign::SubtractiveBox] Box167
  AttacherType = Attacher::AttachEngine3D
  AttachmentOffset = pos=(-20.5,18.63,0) rot=(0,0,1;0rad)
  BaseFeature = -> Box198
  Height = 1.635
  Length = 0.5
  MapMode = 5
  Placement = pos=(-20.5,18.63,0) rot=(0,0,1;0rad)
  Support = -> [XY_Plane019]
  Width = 0.25
FEATURE [PartDesign::SubtractiveBox] Box182
  AttacherType = Attacher::AttachEngine3D
  AttachmentOffset = pos=(-21.19,18.635,-0.12) rot=(0,-1,0;0.15708rad)
  BaseFeature = -> Box167
  Height = 0.12
  Length = 0.725
  MapMode = 5
  Placement = pos=(-21.19,18.635,-0.12) rot=(0,-1,0;0.15708rad)
  Support = -> [XY_Plane019]
  Width = 0.25
FEATURE [PartDesign::SubtractiveBox] Box186
  AttacherType = Attacher::AttachEngine3D
  AttachmentOffset = pos=(-21.5005,18.625,0.235) rot=(0,-1,0;0.174533rad)
  BaseFeature = -> Box182
  Height = 0.3
  Length = 0.6605
  MapMode = 5
  Placement = pos=(-21.5005,18.625,0.235) rot=(0,-1,0;0.174533rad)
  Support = -> [XY_Plane019]
  Width = 0.25
FEATURE [PartDesign::SubtractiveBox] Box204
  AttacherType = Attacher::AttachEngine3D
  AttachmentOffset = pos=(-21.5005,18.625,0.235) rot=(0,-1,0;0.174533rad)
  BaseFeature = -> Box178
  Height = 0.3
  Length = 0.6605
  MapMode = 5
  Placement = pos=(-21.5005,18.625,0.235) rot=(0,-1,0;0.174533rad)
  Support = -> [XY_Plane023]
  Width = 0.25
FEATURE [PartDesign::SubtractiveBox] Box209
  AttacherType = Attacher::AttachEngine3D
  AttachmentOffset = pos=(-20.5,18.63,0) rot=(0,0,1;0rad)
  BaseFeature = -> Box122
  Height = 1.635
  Length = 0.5
  MapMode = 5
  Placement = pos=(-20.5,18.63,0) rot=(0,0,1;0rad)
  Support = -> [XY_Plane025]
  Width = 0.25
FEATURE [PartDesign::SubtractiveBox] Box125
  AttacherType = Attacher::AttachEngine3D
  AttachmentOffset = pos=(-21.19,18.635,-0.12) rot=(0,-1,0;0.15708rad)
  BaseFeature = -> Box209
  Height = 0.12
  Length = 0.725
  MapMode = 5
  Placement = pos=(-21.19,18.635,-0.12) rot=(0,-1,0;0.15708rad)
  Support = -> [XY_Plane025]
  Width = 0.25
FEATURE [PartDesign::SubtractiveBox] Box128
  AttacherType = Attacher::AttachEngine3D
  AttachmentOffset = pos=(-21.5005,18.625,0.235) rot=(0,-1,0;0.174533rad)
  BaseFeature = -> Box125
  Height = 0.3
  Length = 0.6605
  MapMode = 5
  Placement = pos=(-21.5005,18.625,0.235) rot=(0,-1,0;0.174533rad)
  Support = -> [XY_Plane025]
  Width = 0.25
FEATURE [PartDesign::SubtractiveBox] Box210
  AttacherType = Attacher::AttachEngine3D
  AttachmentOffset = pos=(-21.19,18.635,-0.12) rot=(0,-1,0;0.15708rad)
  BaseFeature = -> Box202
  Height = 0.12
  Length = 0.725
  MapMode = 5
  Placement = pos=(-21.19,18.635,-0.12) rot=(0,-1,0;0.15708rad)
  Support = -> [XY_Plane020]
  Width = 0.25
FEATURE [PartDesign::SubtractiveBox] Box133
  AttacherType = Attacher::AttachEngine3D
  AttachmentOffset = pos=(-21.5005,18.625,0.235) rot=(0,-1,0;0.174533rad)
  BaseFeature = -> Box210
  Height = 0.3
  Length = 0.6605
  MapMode = 5
  Placement = pos=(-21.5005,18.625,0.235) rot=(0,-1,0;0.174533rad)
  Support = -> [XY_Plane020]
  Width = 0.25
FEATURE [PartDesign::Fillet] Fillet043
  Base = -> Box157 [Edge2]
  BaseFeature = -> Box157
  Placement = pos=(-21.5005,18.625,0.235) rot=(0,-1,0;0.174533rad)
  Radius = 0.05
  SupportTransform = false
FEATURE [PartDesign::Fillet] Fillet045
  Base = -> Fillet043 [Edge33]
  BaseFeature = -> Fillet043
  Placement = pos=(-21.5005,18.625,0.235) rot=(0,-1,0;0.174533rad)
  Radius = 0.5
  SupportTransform = false
FEATURE [PartDesign::AdditiveBox] Box138
  AttacherType = Attacher::AttachEngine3D
  AttachmentOffset = pos=(-21.1,18.635,0.305) rot=(0,1,0;0.785398rad)
  BaseFeature = -> Fillet045
  Height = 0.375
  Length = 0.2
  MapMode = 5
  Placement = pos=(-21.1,18.635,0.305) rot=(0,1,0;0.785398rad)
  Support = -> [XY_Plane017]
  Width = 0.23
FEATURE [PartDesign::SubtractiveCylinder] Cylinder032
  Angle = 360
  AttacherType = Attacher::AttachEngine3D
  AttachmentOffset = pos=(-21.055,18.935,0.52) rot=(1,0,0;1.5708rad)
  BaseFeature = -> Box138
  Height = 0.375
  MapMode = 5
  Placement = pos=(-21.055,18.935,0.52) rot=(1,0,0;1.5708rad)
  Radius = 0.205
  Support = -> [XY_Plane017]
FEATURE [PartDesign::SubtractiveBox] Box159
  AttacherType = Attacher::AttachEngine3D
  AttachmentOffset = pos=(-20.95,18.635,0.53) rot=(0,0,1;0rad)
  BaseFeature = -> Cylinder032
  Height = 0.5
  Length = 0.1
  MapMode = 5
  Placement = pos=(-20.95,18.635,0.53) rot=(0,0,1;0rad)
  Support = -> [XY_Plane017]
  Width = 0.23
FEATURE [PartDesign::SubtractiveBox] Box149
  AttacherType = Attacher::AttachEngine3D
  AttachmentOffset = pos=(-21.15,18.635,0.297) rot=(0,-1,0;0.174533rad)
  BaseFeature = -> Box159
  Height = 0.115
  Length = 0.115
  MapMode = 5
  Placement = pos=(-21.15,18.635,0.297) rot=(0,-1,0;0.174533rad)
  Support = -> [XY_Plane017]
  Width = 0.23
FEATURE [PartDesign::Fillet] Fillet044
  Base = -> Box149 [Edge28]
  BaseFeature = -> Box149
  Placement = pos=(-21.15,18.635,0.297) rot=(0,-1,0;0.174533rad)
  Radius = 0.375
  SupportTransform = false
FEATURE [PartDesign::AdditiveBox] Box148
  AttacherType = Attacher::AttachEngine3D
  AttachmentOffset = pos=(-20.7,18.635,1.55) rot=(0,1,0;0.785398rad)
  BaseFeature = -> Fillet044
  Height = 0.375
  Length = 0.23
  MapMode = 5
  Placement = pos=(-20.7,18.635,1.55) rot=(0,1,0;0.785398rad)
  Support = -> [XY_Plane017]
  Width = 0.23
FEATURE [PartDesign::SubtractiveCylinder] Cylinder034
  Angle = 360
  AttacherType = Attacher::AttachEngine3D
  AttachmentOffset = pos=(-20.271,18.635,1.4056) rot=(-1,0,0;1.5708rad)
  BaseFeature = -> Box148
  Height = 0.23
  MapMode = 5
  Placement = pos=(-20.271,18.635,1.4056) rot=(-1,0,0;1.5708rad)
  Radius = 0.23
  Support = -> [XY_Plane017]
FEATURE [PartDesign::AdditiveBox] Box158
  AttacherType = Attacher::AttachEngine3D
  AttachmentOffset = pos=(-20.1,18.635,1.635) rot=(0,0,1;0rad)
  BaseFeature = -> Cylinder034
  Height = 0.265
  Length = 0.23
  MapMode = 5
  Placement = pos=(-20.1,18.635,1.635) rot=(0,0,1;0rad)
  Support = -> [XY_Plane017]
  Width = 0.23
FEATURE [PartDesign::Body] Body017  label="pin017"
  Group = -> [Box151,Box154,Box147,Box156,Box157,Fillet043,Fillet045,Box138,Cylinder032,Box159,Box149,Fillet044,Box148,Cylinder034,Box158]
  Origin = -> Origin021
  Placement = pos=(0,-2,0) rot=(0,0,1;0rad)
  Tip = -> Box158
FEATURE [PartDesign::Fillet] Fillet046
  Base = -> Box162 [Edge2]
  BaseFeature = -> Box162
  Placement = pos=(-21.5005,18.625,0.235) rot=(0,-1,0;0.174533rad)
  Radius = 0.05
  SupportTransform = false
FEATURE [PartDesign::Fillet] Fillet047
  Base = -> Fillet046 [Edge33]
  BaseFeature = -> Fillet046
  Placement = pos=(-21.5005,18.625,0.235) rot=(0,-1,0;0.174533rad)
  Radius = 0.5
  SupportTransform = false
FEATURE [PartDesign::AdditiveBox] Box150
  AttacherType = Attacher::AttachEngine3D
  AttachmentOffset = pos=(-21.1,18.635,0.305) rot=(0,1,0;0.785398rad)
  BaseFeature = -> Fillet047
  Height = 0.375
  Length = 0.2
  MapMode = 5
  Placement = pos=(-21.1,18.635,0.305) rot=(0,1,0;0.785398rad)
  Support = -> [XY_Plane014]
  Width = 0.23
FEATURE [PartDesign::SubtractiveCylinder] Cylinder033
  Angle = 360
  AttacherType = Attacher::AttachEngine3D
  AttachmentOffset = pos=(-21.055,18.935,0.52) rot=(1,0,0;1.5708rad)
  BaseFeature = -> Box150
  Height = 0.375
  MapMode = 5
  Placement = pos=(-21.055,18.935,0.52) rot=(1,0,0;1.5708rad)
  Radius = 0.205
  Support = -> [XY_Plane014]
FEATURE [PartDesign::SubtractiveBox] Box155
  AttacherType = Attacher::AttachEngine3D
  AttachmentOffset = pos=(-20.95,18.635,0.53) rot=(0,0,1;0rad)
  BaseFeature = -> Cylinder033
  Height = 0.5
  Length = 0.1
  MapMode = 5
  Placement = pos=(-20.95,18.635,0.53) rot=(0,0,1;0rad)
  Support = -> [XY_Plane014]
  Width = 0.23
FEATURE [PartDesign::SubtractiveBox] Box161
  AttacherType = Attacher::AttachEngine3D
  AttachmentOffset = pos=(-21.15,18.635,0.297) rot=(0,-1,0;0.174533rad)
  BaseFeature = -> Box155
  Height = 0.115
  Length = 0.115
  MapMode = 5
  Placement = pos=(-21.15,18.635,0.297) rot=(0,-1,0;0.174533rad)
  Support = -> [XY_Plane014]
  Width = 0.23
FEATURE [PartDesign::Fillet] Fillet037
  Base = -> Box161 [Edge28]
  BaseFeature = -> Box161
  Placement = pos=(-21.15,18.635,0.297) rot=(0,-1,0;0.174533rad)
  Radius = 0.375
  SupportTransform = false
FEATURE [PartDesign::AdditiveBox] Box160
  AttacherType = Attacher::AttachEngine3D
  AttachmentOffset = pos=(-20.7,18.635,1.55) rot=(0,1,0;0.785398rad)
  BaseFeature = -> Fillet037
  Height = 0.375
  Length = 0.23
  MapMode = 5
  Placement = pos=(-20.7,18.635,1.55) rot=(0,1,0;0.785398rad)
  Support = -> [XY_Plane014]
  Width = 0.23
FEATURE [PartDesign::SubtractiveCylinder] Cylinder035
  Angle = 360
  AttacherType = Attacher::AttachEngine3D
  AttachmentOffset = pos=(-20.271,18.635,1.4056) rot=(-1,0,0;1.5708rad)
  BaseFeature = -> Box160
  Height = 0.23
  MapMode = 5
  Placement = pos=(-20.271,18.635,1.4056) rot=(-1,0,0;1.5708rad)
  Radius = 0.23
  Support = -> [XY_Plane014]
FEATURE [PartDesign::AdditiveBox] Box152
  AttacherType = Attacher::AttachEngine3D
  AttachmentOffset = pos=(-20.1,18.635,1.635) rot=(0,0,1;0rad)
  BaseFeature = -> Cylinder035
  Height = 0.265
  Length = 0.23
  MapMode = 5
  Placement = pos=(-20.1,18.635,1.635) rot=(0,0,1;0rad)
  Support = -> [XY_Plane014]
  Width = 0.23
FEATURE [PartDesign::Body] Body018  label="pin018"
  Group = -> [Box163,Box169,Box145,Box153,Box162,Fillet046,Fillet047,Box150,Cylinder033,Box155,Box161,Fillet037,Box160,Cylinder035,Box152]
  Origin = -> Origin023
  Placement = pos=(0,-2.5,0) rot=(0,0,1;0rad)
  Tip = -> Box152
FEATURE [PartDesign::AdditiveBox] Box228
  AttacherType = Attacher::AttachEngine3D
  AttachmentOffset = pos=(-21.3,18.635,0) rot=(0,0,1;0rad)
  Height = 1.9
  Length = 1.3
  MapMode = 5
  Placement = pos=(-21.3,18.635,0) rot=(0,0,1;0rad)
  Support = -> [XY_Plane024]
  Width = 0.23
FEATURE [PartDesign::SubtractiveBox] Box229
  AttacherType = Attacher::AttachEngine3D
  AttachmentOffset = pos=(-21.35,18.635,0.35) rot=(0,0,1;0rad)
  BaseFeature = -> Box228
  Height = 1.55
  Length = 0.5
  MapMode = 5
  Placement = pos=(-21.35,18.635,0.35) rot=(0,0,1;0rad)
  Support = -> [XY_Plane024]
  Width = 0.23
FEATURE [PartDesign::SubtractiveBox] Box218
  AttacherType = Attacher::AttachEngine3D
  AttachmentOffset = pos=(-20.5,18.63,0) rot=(0,0,1;0rad)
  BaseFeature = -> Box229
  Height = 1.635
  Length = 0.5
  MapMode = 5
  Placement = pos=(-20.5,18.63,0) rot=(0,0,1;0rad)
  Support = -> [XY_Plane024]
  Width = 0.25
FEATURE [PartDesign::SubtractiveBox] Box225
  AttacherType = Attacher::AttachEngine3D
  AttachmentOffset = pos=(-21.19,18.635,-0.12) rot=(0,-1,0;0.15708rad)
  BaseFeature = -> Box218
  Height = 0.12
  Length = 0.725
  MapMode = 5
  Placement = pos=(-21.19,18.635,-0.12) rot=(0,-1,0;0.15708rad)
  Support = -> [XY_Plane024]
  Width = 0.25
FEATURE [PartDesign::SubtractiveBox] Box226
  AttacherType = Attacher::AttachEngine3D
  AttachmentOffset = pos=(-21.5005,18.625,0.235) rot=(0,-1,0;0.174533rad)
  BaseFeature = -> Box225
  Height = 0.3
  Length = 0.6605
  MapMode = 5
  Placement = pos=(-21.5005,18.625,0.235) rot=(0,-1,0;0.174533rad)
  Support = -> [XY_Plane024]
  Width = 0.25
FEATURE [PartDesign::Fillet] Fillet038
  Base = -> Box226 [Edge2]
  BaseFeature = -> Box226
  Placement = pos=(-21.5005,18.625,0.235) rot=(0,-1,0;0.174533rad)
  Radius = 0.05
  SupportTransform = false
FEATURE [PartDesign::Fillet] Fillet039
  Base = -> Fillet038 [Edge33]
  BaseFeature = -> Fillet038
  Placement = pos=(-21.5005,18.625,0.235) rot=(0,-1,0;0.174533rad)
  Radius = 0.5
  SupportTransform = false
FEATURE [PartDesign::AdditiveBox] Box220
  AttacherType = Attacher::AttachEngine3D
  AttachmentOffset = pos=(-21.1,18.635,0.305) rot=(0,1,0;0.785398rad)
  BaseFeature = -> Fillet039
  Height = 0.375
  Length = 0.2
  MapMode = 5
  Placement = pos=(-21.1,18.635,0.305) rot=(0,1,0;0.785398rad)
  Support = -> [XY_Plane024]
  Width = 0.23
FEATURE [PartDesign::SubtractiveCylinder] Cylinder048
  Angle = 360
  AttacherType = Attacher::AttachEngine3D
  AttachmentOffset = pos=(-21.055,18.935,0.52) rot=(1,0,0;1.5708rad)
  BaseFeature = -> Box220
  Height = 0.375
  MapMode = 5
  Placement = pos=(-21.055,18.935,0.52) rot=(1,0,0;1.5708rad)
  Radius = 0.205
  Support = -> [XY_Plane024]
FEATURE [PartDesign::SubtractiveBox] Box224
  AttacherType = Attacher::AttachEngine3D
  AttachmentOffset = pos=(-20.95,18.635,0.53) rot=(0,0,1;0rad)
  BaseFeature = -> Cylinder048
  Height = 0.5
  Length = 0.1
  MapMode = 5
  Placement = pos=(-20.95,18.635,0.53) rot=(0,0,1;0rad)
  Support = -> [XY_Plane024]
  Width = 0.23
FEATURE [PartDesign::SubtractiveBox] Box221
  AttacherType = Attacher::AttachEngine3D
  AttachmentOffset = pos=(-21.15,18.635,0.297) rot=(0,-1,0;0.174533rad)
  BaseFeature = -> Box224
  Height = 0.115
  Length = 0.115
  MapMode = 5
  Placement = pos=(-21.15,18.635,0.297) rot=(0,-1,0;0.174533rad)
  Support = -> [XY_Plane024]
  Width = 0.23
FEATURE [PartDesign::Fillet] Fillet040
  Base = -> Box221 [Edge28]
  BaseFeature = -> Box221
  Placement = pos=(-21.15,18.635,0.297) rot=(0,-1,0;0.174533rad)
  Radius = 0.375
  SupportTransform = false
FEATURE [PartDesign::AdditiveBox] Box219
  AttacherType = Attacher::AttachEngine3D
  AttachmentOffset = pos=(-20.7,18.635,1.55) rot=(0,1,0;0.785398rad)
  BaseFeature = -> Fillet040
  Height = 0.375
  Length = 0.23
  MapMode = 5
  Placement = pos=(-20.7,18.635,1.55) rot=(0,1,0;0.785398rad)
  Support = -> [XY_Plane024]
  Width = 0.23
FEATURE [PartDesign::SubtractiveCylinder] Cylinder049
  Angle = 360
  AttacherType = Attacher::AttachEngine3D
  AttachmentOffset = pos=(-20.271,18.635,1.4056) rot=(-1,0,0;1.5708rad)
  BaseFeature = -> Box219
  Height = 0.23
  MapMode = 5
  Placement = pos=(-20.271,18.635,1.4056) rot=(-1,0,0;1.5708rad)
  Radius = 0.23
  Support = -> [XY_Plane024]
FEATURE [PartDesign::AdditiveBox] Box227
  AttacherType = Attacher::AttachEngine3D
  AttachmentOffset = pos=(-20.1,18.635,1.635) rot=(0,0,1;0rad)
  BaseFeature = -> Cylinder049
  Height = 0.265
  Length = 0.23
  MapMode = 5
  Placement = pos=(-20.1,18.635,1.635) rot=(0,0,1;0rad)
  Support = -> [XY_Plane024]
  Width = 0.23
FEATURE [PartDesign::Body] Body014  label="pin014"
  Group = -> [Box228,Box229,Box218,Box225,Box226,Fillet038,Fillet039,Box220,Cylinder048,Box224,Box221,Fillet040,Box219,Cylinder049,Box227]
  Origin = -> Origin016
  Placement = pos=(0,-0.5,0) rot=(0,0,1;0rad)
  Tip = -> Box227
FEATURE [PartDesign::AdditiveBox] Box235
  AttacherType = Attacher::AttachEngine3D
  AttachmentOffset = pos=(-21.3,18.635,0) rot=(0,0,1;0rad)
  Height = 1.9
  Length = 1.3
  MapMode = 5
  Placement = pos=(-21.3,18.635,0) rot=(0,0,1;0rad)
  Support = -> [XY_Plane015]
  Width = 0.23
FEATURE [PartDesign::SubtractiveBox] Box238
  AttacherType = Attacher::AttachEngine3D
  AttachmentOffset = pos=(-21.35,18.635,0.35) rot=(0,0,1;0rad)
  BaseFeature = -> Box235
  Height = 1.55
  Length = 0.5
  MapMode = 5
  Placement = pos=(-21.35,18.635,0.35) rot=(0,0,1;0rad)
  Support = -> [XY_Plane015]
  Width = 0.23
FEATURE [PartDesign::SubtractiveBox] Box215
  AttacherType = Attacher::AttachEngine3D
  AttachmentOffset = pos=(-20.5,18.63,0) rot=(0,0,1;0rad)
  BaseFeature = -> Box238
  Height = 1.635
  Length = 0.5
  MapMode = 5
  Placement = pos=(-20.5,18.63,0) rot=(0,0,1;0rad)
  Support = -> [XY_Plane015]
  Width = 0.25
FEATURE [PartDesign::SubtractiveBox] Box234
  AttacherType = Attacher::AttachEngine3D
  AttachmentOffset = pos=(-21.19,18.635,-0.12) rot=(0,-1,0;0.15708rad)
  BaseFeature = -> Box215
  Height = 0.12
  Length = 0.725
  MapMode = 5
  Placement = pos=(-21.19,18.635,-0.12) rot=(0,-1,0;0.15708rad)
  Support = -> [XY_Plane015]
  Width = 0.25
FEATURE [PartDesign::SubtractiveBox] Box232
  AttacherType = Attacher::AttachEngine3D
  AttachmentOffset = pos=(-21.5005,18.625,0.235) rot=(0,-1,0;0.174533rad)
  BaseFeature = -> Box234
  Height = 0.3
  Length = 0.6605
  MapMode = 5
  Placement = pos=(-21.5005,18.625,0.235) rot=(0,-1,0;0.174533rad)
  Support = -> [XY_Plane015]
  Width = 0.25
FEATURE [PartDesign::Fillet] Fillet041
  Base = -> Box232 [Edge2]
  BaseFeature = -> Box232
  Placement = pos=(-21.5005,18.625,0.235) rot=(0,-1,0;0.174533rad)
  Radius = 0.05
  SupportTransform = false
FEATURE [PartDesign::Fillet] Fillet048
  Base = -> Fillet041 [Edge33]
  BaseFeature = -> Fillet041
  Placement = pos=(-21.5005,18.625,0.235) rot=(0,-1,0;0.174533rad)
  Radius = 0.5
  SupportTransform = false
FEATURE [PartDesign::AdditiveBox] Box222
  AttacherType = Attacher::AttachEngine3D
  AttachmentOffset = pos=(-21.1,18.635,0.305) rot=(0,1,0;0.785398rad)
  BaseFeature = -> Fillet048
  Height = 0.375
  Length = 0.2
  MapMode = 5
  Placement = pos=(-21.1,18.635,0.305) rot=(0,1,0;0.785398rad)
  Support = -> [XY_Plane015]
  Width = 0.23
FEATURE [PartDesign::SubtractiveCylinder] Cylinder050
  Angle = 360
  AttacherType = Attacher::AttachEngine3D
  AttachmentOffset = pos=(-21.055,18.935,0.52) rot=(1,0,0;1.5708rad)
  BaseFeature = -> Box222
  Height = 0.375
  MapMode = 5
  Placement = pos=(-21.055,18.935,0.52) rot=(1,0,0;1.5708rad)
  Radius = 0.205
  Support = -> [XY_Plane015]
FEATURE [PartDesign::SubtractiveBox] Box237
  AttacherType = Attacher::AttachEngine3D
  AttachmentOffset = pos=(-20.95,18.635,0.53) rot=(0,0,1;0rad)
  BaseFeature = -> Cylinder050
  Height = 0.5
  Length = 0.1
  MapMode = 5
  Placement = pos=(-20.95,18.635,0.53) rot=(0,0,1;0rad)
  Support = -> [XY_Plane015]
  Width = 0.23
FEATURE [PartDesign::SubtractiveBox] Box231
  AttacherType = Attacher::AttachEngine3D
  AttachmentOffset = pos=(-21.15,18.635,0.297) rot=(0,-1,0;0.174533rad)
  BaseFeature = -> Box237
  Height = 0.115
  Length = 0.115
  MapMode = 5
  Placement = pos=(-21.15,18.635,0.297) rot=(0,-1,0;0.174533rad)
  Support = -> [XY_Plane015]
  Width = 0.23
FEATURE [PartDesign::Fillet] Fillet049
  Base = -> Box231 [Edge28]
  BaseFeature = -> Box231
  Placement = pos=(-21.15,18.635,0.297) rot=(0,-1,0;0.174533rad)
  Radius = 0.375
  SupportTransform = false
FEATURE [PartDesign::AdditiveBox] Box230
  AttacherType = Attacher::AttachEngine3D
  AttachmentOffset = pos=(-20.7,18.635,1.55) rot=(0,1,0;0.785398rad)
  BaseFeature = -> Fillet049
  Height = 0.375
  Length = 0.23
  MapMode = 5
  Placement = pos=(-20.7,18.635,1.55) rot=(0,1,0;0.785398rad)
  Support = -> [XY_Plane015]
  Width = 0.23
FEATURE [PartDesign::SubtractiveCylinder] Cylinder051
  Angle = 360
  AttacherType = Attacher::AttachEngine3D
  AttachmentOffset = pos=(-20.271,18.635,1.4056) rot=(-1,0,0;1.5708rad)
  BaseFeature = -> Box230
  Height = 0.23
  MapMode = 5
  Placement = pos=(-20.271,18.635,1.4056) rot=(-1,0,0;1.5708rad)
  Radius = 0.23
  Support = -> [XY_Plane015]
FEATURE [PartDesign::AdditiveBox] Box233
  AttacherType = Attacher::AttachEngine3D
  AttachmentOffset = pos=(-20.1,18.635,1.635) rot=(0,0,1;0rad)
  BaseFeature = -> Cylinder051
  Height = 0.265
  Length = 0.23
  MapMode = 5
  Placement = pos=(-20.1,18.635,1.635) rot=(0,0,1;0rad)
  Support = -> [XY_Plane015]
  Width = 0.23
FEATURE [PartDesign::Body] Body015  label="pin015"
  Group = -> [Box235,Box238,Box215,Box234,Box232,Fillet041,Fillet048,Box222,Cylinder050,Box237,Box231,Fillet049,Box230,Cylinder051,Box233]
  Origin = -> Origin017
  Placement = pos=(0,-1,0) rot=(0,0,1;0rad)
  Tip = -> Box233
FEATURE [PartDesign::AdditiveBox] Box239
  AttacherType = Attacher::AttachEngine3D
  AttachmentOffset = pos=(-21.3,18.635,0) rot=(0,0,1;0rad)
  Height = 1.9
  Length = 1.3
  MapMode = 5
  Placement = pos=(-21.3,18.635,0) rot=(0,0,1;0rad)
  Support = -> [XY_Plane016]
  Width = 0.23
FEATURE [PartDesign::Fillet] Fillet052
  Base = -> Box123 [Edge2]
  BaseFeature = -> Box123
  Placement = pos=(-21.5005,18.625,0.235) rot=(0,-1,0;0.174533rad)
  Radius = 0.05
  SupportTransform = false
FEATURE [PartDesign::Fillet] Fillet055
  Base = -> Box186 [Edge2]
  BaseFeature = -> Box186
  Placement = pos=(-21.5005,18.625,0.235) rot=(0,-1,0;0.174533rad)
  Radius = 0.05
  SupportTransform = false
FEATURE [PartDesign::Fillet] Fillet057
  Base = -> Box164 [Edge2]
  BaseFeature = -> Box164
  Placement = pos=(-21.5005,18.625,0.235) rot=(0,-1,0;0.174533rad)
  Radius = 0.05
  SupportTransform = false
FEATURE [PartDesign::Fillet] Fillet042
  Base = -> Fillet057 [Edge33]
  BaseFeature = -> Fillet057
  Placement = pos=(-21.5005,18.625,0.235) rot=(0,-1,0;0.174533rad)
  Radius = 0.5
  SupportTransform = false
FEATURE [PartDesign::AdditiveBox] Box141
  AttacherType = Attacher::AttachEngine3D
  AttachmentOffset = pos=(-21.1,18.635,0.305) rot=(0,1,0;0.785398rad)
  BaseFeature = -> Fillet042
  Height = 0.375
  Length = 0.2
  MapMode = 5
  Placement = pos=(-21.1,18.635,0.305) rot=(0,1,0;0.785398rad)
  Support = -> [XY_Plane018]
  Width = 0.23
FEATURE [PartDesign::SubtractiveCylinder] Cylinder031
  Angle = 360
  AttacherType = Attacher::AttachEngine3D
  AttachmentOffset = pos=(-21.055,18.935,0.52) rot=(1,0,0;1.5708rad)
  BaseFeature = -> Box141
  Height = 0.375
  MapMode = 5
  Placement = pos=(-21.055,18.935,0.52) rot=(1,0,0;1.5708rad)
  Radius = 0.205
  Support = -> [XY_Plane018]
FEATURE [PartDesign::SubtractiveBox] Box143
  AttacherType = Attacher::AttachEngine3D
  AttachmentOffset = pos=(-20.95,18.635,0.53) rot=(0,0,1;0rad)
  BaseFeature = -> Cylinder031
  Height = 0.5
  Length = 0.1
  MapMode = 5
  Placement = pos=(-20.95,18.635,0.53) rot=(0,0,1;0rad)
  Support = -> [XY_Plane018]
  Width = 0.23
FEATURE [PartDesign::SubtractiveBox] Box142
  AttacherType = Attacher::AttachEngine3D
  AttachmentOffset = pos=(-21.15,18.635,0.297) rot=(0,-1,0;0.174533rad)
  BaseFeature = -> Box143
  Height = 0.115
  Length = 0.115
  MapMode = 5
  Placement = pos=(-21.15,18.635,0.297) rot=(0,-1,0;0.174533rad)
  Support = -> [XY_Plane018]
  Width = 0.23
FEATURE [PartDesign::Fillet] Fillet056
  Base = -> Box142 [Edge28]
  BaseFeature = -> Box142
  Placement = pos=(-21.15,18.635,0.297) rot=(0,-1,0;0.174533rad)
  Radius = 0.375
  SupportTransform = false
FEATURE [PartDesign::AdditiveBox] Box140
  AttacherType = Attacher::AttachEngine3D
  AttachmentOffset = pos=(-20.7,18.635,1.55) rot=(0,1,0;0.785398rad)
  BaseFeature = -> Fillet056
  Height = 0.375
  Length = 0.23
  MapMode = 5
  Placement = pos=(-20.7,18.635,1.55) rot=(0,1,0;0.785398rad)
  Support = -> [XY_Plane018]
  Width = 0.23
FEATURE [PartDesign::SubtractiveCylinder] Cylinder030
  Angle = 360
  AttacherType = Attacher::AttachEngine3D
  AttachmentOffset = pos=(-20.271,18.635,1.4056) rot=(-1,0,0;1.5708rad)
  BaseFeature = -> Box140
  Height = 0.23
  MapMode = 5
  Placement = pos=(-20.271,18.635,1.4056) rot=(-1,0,0;1.5708rad)
  Radius = 0.23
  Support = -> [XY_Plane018]
FEATURE [PartDesign::AdditiveBox] Box139
  AttacherType = Attacher::AttachEngine3D
  AttachmentOffset = pos=(-20.1,18.635,1.635) rot=(0,0,1;0rad)
  BaseFeature = -> Cylinder030
  Height = 0.265
  Length = 0.23
  MapMode = 5
  Placement = pos=(-20.1,18.635,1.635) rot=(0,0,1;0rad)
  Support = -> [XY_Plane018]
  Width = 0.23
FEATURE [PartDesign::Body] Body016  label="pin016"
  Group = -> [Box174,Box165,Box144,Box146,Box164,Fillet057,Fillet042,Box141,Cylinder031,Box143,Box142,Fillet056,Box140,Cylinder030,Box139]
  Origin = -> Origin020
  Placement = pos=(0,-1.5,0) rot=(0,0,1;0rad)
  Tip = -> Box139
FEATURE [PartDesign::Fillet] Fillet058
  Base = -> Box128 [Edge2]
  BaseFeature = -> Box128
  Placement = pos=(-21.5005,18.625,0.235) rot=(0,-1,0;0.174533rad)
  Radius = 0.05
  SupportTransform = false
FEATURE [PartDesign::Fillet] Fillet059
  Base = -> Fillet058 [Edge33]
  BaseFeature = -> Fillet058
  Placement = pos=(-21.5005,18.625,0.235) rot=(0,-1,0;0.174533rad)
  Radius = 0.5
  SupportTransform = false
FEATURE [PartDesign::AdditiveBox] Box206
  AttacherType = Attacher::AttachEngine3D
  AttachmentOffset = pos=(-21.1,18.635,0.305) rot=(0,1,0;0.785398rad)
  BaseFeature = -> Fillet059
  Height = 0.375
  Length = 0.2
  MapMode = 5
  Placement = pos=(-21.1,18.635,0.305) rot=(0,1,0;0.785398rad)
  Support = -> [XY_Plane025]
  Width = 0.23
FEATURE [PartDesign::SubtractiveCylinder] Cylinder046
  Angle = 360
  AttacherType = Attacher::AttachEngine3D
  AttachmentOffset = pos=(-21.055,18.935,0.52) rot=(1,0,0;1.5708rad)
  BaseFeature = -> Box206
  Height = 0.375
  MapMode = 5
  Placement = pos=(-21.055,18.935,0.52) rot=(1,0,0;1.5708rad)
  Radius = 0.205
  Support = -> [XY_Plane025]
FEATURE [PartDesign::SubtractiveBox] Box213
  AttacherType = Attacher::AttachEngine3D
  AttachmentOffset = pos=(-20.95,18.635,0.53) rot=(0,0,1;0rad)
  BaseFeature = -> Cylinder046
  Height = 0.5
  Length = 0.1
  MapMode = 5
  Placement = pos=(-20.95,18.635,0.53) rot=(0,0,1;0rad)
  Support = -> [XY_Plane025]
  Width = 0.23
FEATURE [PartDesign::SubtractiveBox] Box211
  AttacherType = Attacher::AttachEngine3D
  AttachmentOffset = pos=(-21.15,18.635,0.297) rot=(0,-1,0;0.174533rad)
  BaseFeature = -> Box213
  Height = 0.115
  Length = 0.115
  MapMode = 5
  Placement = pos=(-21.15,18.635,0.297) rot=(0,-1,0;0.174533rad)
  Support = -> [XY_Plane025]
  Width = 0.23
FEATURE [PartDesign::Fillet] Fillet060
  Base = -> Box211 [Edge28]
  BaseFeature = -> Box211
  Placement = pos=(-21.15,18.635,0.297) rot=(0,-1,0;0.174533rad)
  Radius = 0.375
  SupportTransform = false
FEATURE [PartDesign::AdditiveBox] Box207
  AttacherType = Attacher::AttachEngine3D
  AttachmentOffset = pos=(-20.7,18.635,1.55) rot=(0,1,0;0.785398rad)
  BaseFeature = -> Fillet060
  Height = 0.375
  Length = 0.23
  MapMode = 5
  Placement = pos=(-20.7,18.635,1.55) rot=(0,1,0;0.785398rad)
  Support = -> [XY_Plane025]
  Width = 0.23
FEATURE [PartDesign::SubtractiveCylinder] Cylinder047
  Angle = 360
  AttacherType = Attacher::AttachEngine3D
  AttachmentOffset = pos=(-20.271,18.635,1.4056) rot=(-1,0,0;1.5708rad)
  BaseFeature = -> Box207
  Height = 0.23
  MapMode = 5
  Placement = pos=(-20.271,18.635,1.4056) rot=(-1,0,0;1.5708rad)
  Radius = 0.23
  Support = -> [XY_Plane025]
FEATURE [PartDesign::AdditiveBox] Box126
  AttacherType = Attacher::AttachEngine3D
  AttachmentOffset = pos=(-20.1,18.635,1.635) rot=(0,0,1;0rad)
  BaseFeature = -> Cylinder047
  Height = 0.265
  Length = 0.23
  MapMode = 5
  Placement = pos=(-20.1,18.635,1.635) rot=(0,0,1;0rad)
  Support = -> [XY_Plane025]
  Width = 0.23
FEATURE [PartDesign::Body] Body020  label="pin020"
  Group = -> [Box129,Box122,Box209,Box125,Box128,Fillet058,Fillet059,Box206,Cylinder046,Box213,Box211,Fillet060,Box207,Cylinder047,Box126]
  Origin = -> Origin024
  Placement = pos=(0,-3.5,0) rot=(0,0,1;0rad)
  Tip = -> Box126
FEATURE [PartDesign::Fillet] Fillet061
  Base = -> Box188 [Edge2]
  BaseFeature = -> Box188
  Placement = pos=(-21.5005,18.625,0.235) rot=(0,-1,0;0.174533rad)
  Radius = 0.05
  SupportTransform = false
FEATURE [PartDesign::Fillet] Fillet063
  Base = -> Fillet061 [Edge33]
  BaseFeature = -> Fillet061
  Placement = pos=(-21.5005,18.625,0.235) rot=(0,-1,0;0.174533rad)
  Radius = 0.5
  SupportTransform = false
FEATURE [PartDesign::AdditiveBox] Box172
  AttacherType = Attacher::AttachEngine3D
  AttachmentOffset = pos=(-21.1,18.635,0.305) rot=(0,1,0;0.785398rad)
  BaseFeature = -> Fillet063
  Height = 0.375
  Length = 0.2
  MapMode = 5
  Placement = pos=(-21.1,18.635,0.305) rot=(0,1,0;0.785398rad)
  Support = -> [XY_Plane022]
  Width = 0.23
FEATURE [PartDesign::SubtractiveCylinder] Cylinder038
  Angle = 360
  AttacherType = Attacher::AttachEngine3D
  AttachmentOffset = pos=(-21.055,18.935,0.52) rot=(1,0,0;1.5708rad)
  BaseFeature = -> Box172
  Height = 0.375
  MapMode = 5
  Placement = pos=(-21.055,18.935,0.52) rot=(1,0,0;1.5708rad)
  Radius = 0.205
  Support = -> [XY_Plane022]
FEATURE [PartDesign::SubtractiveBox] Box189
  AttacherType = Attacher::AttachEngine3D
  AttachmentOffset = pos=(-20.95,18.635,0.53) rot=(0,0,1;0rad)
  BaseFeature = -> Cylinder038
  Height = 0.5
  Length = 0.1
  MapMode = 5
  Placement = pos=(-20.95,18.635,0.53) rot=(0,0,1;0rad)
  Support = -> [XY_Plane022]
  Width = 0.23
FEATURE [PartDesign::SubtractiveBox] Box184
  AttacherType = Attacher::AttachEngine3D
  AttachmentOffset = pos=(-21.15,18.635,0.297) rot=(0,-1,0;0.174533rad)
  BaseFeature = -> Box189
  Height = 0.115
  Length = 0.115
  MapMode = 5
  Placement = pos=(-21.15,18.635,0.297) rot=(0,-1,0;0.174533rad)
  Support = -> [XY_Plane022]
  Width = 0.23
FEATURE [PartDesign::Fillet] Fillet062
  Base = -> Box184 [Edge28]
  BaseFeature = -> Box184
  Placement = pos=(-21.15,18.635,0.297) rot=(0,-1,0;0.174533rad)
  Radius = 0.375
  SupportTransform = false
FEATURE [PartDesign::AdditiveBox] Box179
  AttacherType = Attacher::AttachEngine3D
  AttachmentOffset = pos=(-20.7,18.635,1.55) rot=(0,1,0;0.785398rad)
  BaseFeature = -> Fillet062
  Height = 0.375
  Length = 0.23
  MapMode = 5
  Placement = pos=(-20.7,18.635,1.55) rot=(0,1,0;0.785398rad)
  Support = -> [XY_Plane022]
  Width = 0.23
FEATURE [PartDesign::SubtractiveCylinder] Cylinder039
  Angle = 360
  AttacherType = Attacher::AttachEngine3D
  AttachmentOffset = pos=(-20.271,18.635,1.4056) rot=(-1,0,0;1.5708rad)
  BaseFeature = -> Box179
  Height = 0.23
  MapMode = 5
  Placement = pos=(-20.271,18.635,1.4056) rot=(-1,0,0;1.5708rad)
  Radius = 0.23
  Support = -> [XY_Plane022]
FEATURE [PartDesign::AdditiveBox] Box187
  AttacherType = Attacher::AttachEngine3D
  AttachmentOffset = pos=(-20.1,18.635,1.635) rot=(0,0,1;0rad)
  BaseFeature = -> Cylinder039
  Height = 0.265
  Length = 0.23
  MapMode = 5
  Placement = pos=(-20.1,18.635,1.635) rot=(0,0,1;0rad)
  Support = -> [XY_Plane022]
  Width = 0.23
FEATURE [PartDesign::Body] Body023  label="pin023"
  Group = -> [Box180,Box183,Box168,Box193,Box188,Fillet061,Fillet063,Box172,Cylinder038,Box189,Box184,Fillet062,Box179,Cylinder039,Box187]
  Origin = -> Origin022
  Placement = pos=(0,-5,0) rot=(0,0,1;0rad)
  Tip = -> Box187
FEATURE [PartDesign::Fillet] Fillet064
  Base = -> Fillet052 [Edge33]
  BaseFeature = -> Fillet052
  Placement = pos=(-21.5005,18.625,0.235) rot=(0,-1,0;0.174533rad)
  Radius = 0.5
  SupportTransform = false
FEATURE [PartDesign::AdditiveBox] Box205
  AttacherType = Attacher::AttachEngine3D
  AttachmentOffset = pos=(-21.1,18.635,0.305) rot=(0,1,0;0.785398rad)
  BaseFeature = -> Fillet064
  Height = 0.375
  Length = 0.2
  MapMode = 5
  Placement = pos=(-21.1,18.635,0.305) rot=(0,1,0;0.785398rad)
  Support = -> [XY_Plane021]
  Width = 0.23
FEATURE [PartDesign::SubtractiveCylinder] Cylinder028
  Angle = 360
  AttacherType = Attacher::AttachEngine3D
  AttachmentOffset = pos=(-21.055,18.935,0.52) rot=(1,0,0;1.5708rad)
  BaseFeature = -> Box205
  Height = 0.375
  MapMode = 5
  Placement = pos=(-21.055,18.935,0.52) rot=(1,0,0;1.5708rad)
  Radius = 0.205
  Support = -> [XY_Plane021]
FEATURE [PartDesign::SubtractiveBox] Box134
  AttacherType = Attacher::AttachEngine3D
  AttachmentOffset = pos=(-20.95,18.635,0.53) rot=(0,0,1;0rad)
  BaseFeature = -> Cylinder028
  Height = 0.5
  Length = 0.1
  MapMode = 5
  Placement = pos=(-20.95,18.635,0.53) rot=(0,0,1;0rad)
  Support = -> [XY_Plane021]
  Width = 0.23
FEATURE [PartDesign::SubtractiveBox] Box131
  AttacherType = Attacher::AttachEngine3D
  AttachmentOffset = pos=(-21.15,18.635,0.297) rot=(0,-1,0;0.174533rad)
  BaseFeature = -> Box134
  Height = 0.115
  Length = 0.115
  MapMode = 5
  Placement = pos=(-21.15,18.635,0.297) rot=(0,-1,0;0.174533rad)
  Support = -> [XY_Plane021]
  Width = 0.23
FEATURE [PartDesign::Fillet] Fillet065
  Base = -> Box131 [Edge28]
  BaseFeature = -> Box131
  Placement = pos=(-21.15,18.635,0.297) rot=(0,-1,0;0.174533rad)
  Radius = 0.375
  SupportTransform = false
FEATURE [PartDesign::AdditiveBox] Box130
  AttacherType = Attacher::AttachEngine3D
  AttachmentOffset = pos=(-20.7,18.635,1.55) rot=(0,1,0;0.785398rad)
  BaseFeature = -> Fillet065
  Height = 0.375
  Length = 0.23
  MapMode = 5
  Placement = pos=(-20.7,18.635,1.55) rot=(0,1,0;0.785398rad)
  Support = -> [XY_Plane021]
  Width = 0.23
FEATURE [PartDesign::SubtractiveCylinder] Cylinder029
  Angle = 360
  AttacherType = Attacher::AttachEngine3D
  AttachmentOffset = pos=(-20.271,18.635,1.4056) rot=(-1,0,0;1.5708rad)
  BaseFeature = -> Box130
  Height = 0.23
  MapMode = 5
  Placement = pos=(-20.271,18.635,1.4056) rot=(-1,0,0;1.5708rad)
  Radius = 0.23
  Support = -> [XY_Plane021]
FEATURE [PartDesign::AdditiveBox] Box121
  AttacherType = Attacher::AttachEngine3D
  AttachmentOffset = pos=(-20.1,18.635,1.635) rot=(0,0,1;0rad)
  BaseFeature = -> Cylinder029
  Height = 0.265
  Length = 0.23
  MapMode = 5
  Placement = pos=(-20.1,18.635,1.635) rot=(0,0,1;0rad)
  Support = -> [XY_Plane021]
  Width = 0.23
FEATURE [PartDesign::Body] Body021  label="pin021"
  Group = -> [Box132,Box127,Box196,Box124,Box123,Fillet052,Fillet064,Box205,Cylinder028,Box134,Box131,Fillet065,Box130,Cylinder029,Box121]
  Origin = -> Origin018
  Placement = pos=(0,-4,0) rot=(0,0,1;0rad)
  Tip = -> Box121
FEATURE [PartDesign::Fillet] Fillet066
  Base = -> Box133 [Edge2]
  BaseFeature = -> Box133
  Placement = pos=(-21.5005,18.625,0.235) rot=(0,-1,0;0.174533rad)
  Radius = 0.05
  SupportTransform = false
FEATURE [PartDesign::Fillet] Fillet054
  Base = -> Fillet066 [Edge33]
  BaseFeature = -> Fillet066
  Placement = pos=(-21.5005,18.625,0.235) rot=(0,-1,0;0.174533rad)
  Radius = 0.5
  SupportTransform = false
FEATURE [PartDesign::AdditiveBox] Box177
  AttacherType = Attacher::AttachEngine3D
  AttachmentOffset = pos=(-21.1,18.635,0.305) rot=(0,1,0;0.785398rad)
  BaseFeature = -> Fillet054
  Height = 0.375
  Length = 0.2
  MapMode = 5
  Placement = pos=(-21.1,18.635,0.305) rot=(0,1,0;0.785398rad)
  Support = -> [XY_Plane020]
  Width = 0.23
FEATURE [PartDesign::SubtractiveCylinder] Cylinder043
  Angle = 360
  AttacherType = Attacher::AttachEngine3D
  AttachmentOffset = pos=(-21.055,18.935,0.52) rot=(1,0,0;1.5708rad)
  BaseFeature = -> Box177
  Height = 0.375
  MapMode = 5
  Placement = pos=(-21.055,18.935,0.52) rot=(1,0,0;1.5708rad)
  Radius = 0.205
  Support = -> [XY_Plane020]
FEATURE [PartDesign::SubtractiveBox] Box200
  AttacherType = Attacher::AttachEngine3D
  AttachmentOffset = pos=(-20.95,18.635,0.53) rot=(0,0,1;0rad)
  BaseFeature = -> Cylinder043
  Height = 0.5
  Length = 0.1
  MapMode = 5
  Placement = pos=(-20.95,18.635,0.53) rot=(0,0,1;0rad)
  Support = -> [XY_Plane020]
  Width = 0.23
FEATURE [PartDesign::SubtractiveBox] Box201
  AttacherType = Attacher::AttachEngine3D
  AttachmentOffset = pos=(-21.15,18.635,0.297) rot=(0,-1,0;0.174533rad)
  BaseFeature = -> Box200
  Height = 0.115
  Length = 0.115
  MapMode = 5
  Placement = pos=(-21.15,18.635,0.297) rot=(0,-1,0;0.174533rad)
  Support = -> [XY_Plane020]
  Width = 0.23
FEATURE [PartDesign::Fillet] Fillet068
  Base = -> Box201 [Edge28]
  BaseFeature = -> Box201
  Placement = pos=(-21.15,18.635,0.297) rot=(0,-1,0;0.174533rad)
  Radius = 0.375
  SupportTransform = false
FEATURE [PartDesign::AdditiveBox] Box208
  AttacherType = Attacher::AttachEngine3D
  AttachmentOffset = pos=(-20.7,18.635,1.55) rot=(0,1,0;0.785398rad)
  BaseFeature = -> Fillet068
  Height = 0.375
  Length = 0.23
  MapMode = 5
  Placement = pos=(-20.7,18.635,1.55) rot=(0,1,0;0.785398rad)
  Support = -> [XY_Plane020]
  Width = 0.23
FEATURE [PartDesign::SubtractiveCylinder] Cylinder044
  Angle = 360
  AttacherType = Attacher::AttachEngine3D
  AttachmentOffset = pos=(-20.271,18.635,1.4056) rot=(-1,0,0;1.5708rad)
  BaseFeature = -> Box208
  Height = 0.23
  MapMode = 5
  Placement = pos=(-20.271,18.635,1.4056) rot=(-1,0,0;1.5708rad)
  Radius = 0.23
  Support = -> [XY_Plane020]
FEATURE [PartDesign::AdditiveBox] Box212
  AttacherType = Attacher::AttachEngine3D
  AttachmentOffset = pos=(-20.1,18.635,1.635) rot=(0,0,1;0rad)
  BaseFeature = -> Cylinder044
  Height = 0.265
  Length = 0.23
  MapMode = 5
  Placement = pos=(-20.1,18.635,1.635) rot=(0,0,1;0rad)
  Support = -> [XY_Plane020]
  Width = 0.23
FEATURE [PartDesign::Body] Body019  label="pin019"
  Group = -> [Box135,Box136,Box202,Box210,Box133,Fillet066,Fillet054,Box177,Cylinder043,Box200,Box201,Fillet068,Box208,Cylinder044,Box212]
  Origin = -> Origin019
  Placement = pos=(0,-3,0) rot=(0,0,1;0rad)
  Tip = -> Box212
FEATURE [PartDesign::Fillet] Fillet069
  Base = -> Fillet055 [Edge33]
  BaseFeature = -> Fillet055
  Placement = pos=(-21.5005,18.625,0.235) rot=(0,-1,0;0.174533rad)
  Radius = 0.5
  SupportTransform = false
FEATURE [PartDesign::AdditiveBox] Box185
  AttacherType = Attacher::AttachEngine3D
  AttachmentOffset = pos=(-21.1,18.635,0.305) rot=(0,1,0;0.785398rad)
  BaseFeature = -> Fillet069
  Height = 0.375
  Length = 0.2
  MapMode = 5
  Placement = pos=(-21.1,18.635,0.305) rot=(0,1,0;0.785398rad)
  Support = -> [XY_Plane019]
  Width = 0.23
FEATURE [PartDesign::SubtractiveCylinder] Cylinder042
  Angle = 360
  AttacherType = Attacher::AttachEngine3D
  AttachmentOffset = pos=(-21.055,18.935,0.52) rot=(1,0,0;1.5708rad)
  BaseFeature = -> Box185
  Height = 0.375
  MapMode = 5
  Placement = pos=(-21.055,18.935,0.52) rot=(1,0,0;1.5708rad)
  Radius = 0.205
  Support = -> [XY_Plane019]
FEATURE [PartDesign::SubtractiveBox] Box192
  AttacherType = Attacher::AttachEngine3D
  AttachmentOffset = pos=(-20.95,18.635,0.53) rot=(0,0,1;0rad)
  BaseFeature = -> Cylinder042
  Height = 0.5
  Length = 0.1
  MapMode = 5
  Placement = pos=(-20.95,18.635,0.53) rot=(0,0,1;0rad)
  Support = -> [XY_Plane019]
  Width = 0.23
FEATURE [PartDesign::SubtractiveBox] Box195
  AttacherType = Attacher::AttachEngine3D
  AttachmentOffset = pos=(-21.15,18.635,0.297) rot=(0,-1,0;0.174533rad)
  BaseFeature = -> Box192
  Height = 0.115
  Length = 0.115
  MapMode = 5
  Placement = pos=(-21.15,18.635,0.297) rot=(0,-1,0;0.174533rad)
  Support = -> [XY_Plane019]
  Width = 0.23
FEATURE [PartDesign::Fillet] Fillet051
  Base = -> Box195 [Edge28]
  BaseFeature = -> Box195
  Placement = pos=(-21.15,18.635,0.297) rot=(0,-1,0;0.174533rad)
  Radius = 0.375
  SupportTransform = false
FEATURE [PartDesign::AdditiveBox] Box194
  AttacherType = Attacher::AttachEngine3D
  AttachmentOffset = pos=(-20.7,18.635,1.55) rot=(0,1,0;0.785398rad)
  BaseFeature = -> Fillet051
  Height = 0.375
  Length = 0.23
  MapMode = 5
  Placement = pos=(-20.7,18.635,1.55) rot=(0,1,0;0.785398rad)
  Support = -> [XY_Plane019]
  Width = 0.23
FEATURE [PartDesign::SubtractiveCylinder] Cylinder041
  Angle = 360
  AttacherType = Attacher::AttachEngine3D
  AttachmentOffset = pos=(-20.271,18.635,1.4056) rot=(-1,0,0;1.5708rad)
  BaseFeature = -> Box194
  Height = 0.23
  MapMode = 5
  Placement = pos=(-20.271,18.635,1.4056) rot=(-1,0,0;1.5708rad)
  Radius = 0.23
  Support = -> [XY_Plane019]
FEATURE [PartDesign::AdditiveBox] Box181
  AttacherType = Attacher::AttachEngine3D
  AttachmentOffset = pos=(-20.1,18.635,1.635) rot=(0,0,1;0rad)
  BaseFeature = -> Cylinder041
  Height = 0.265
  Length = 0.23
  MapMode = 5
  Placement = pos=(-20.1,18.635,1.635) rot=(0,0,1;0rad)
  Support = -> [XY_Plane019]
  Width = 0.23
FEATURE [PartDesign::Body] Body024  label="pin024"
  Group = -> [Box203,Box198,Box167,Box182,Box186,Fillet055,Fillet069,Box185,Cylinder042,Box192,Box195,Fillet051,Box194,Cylinder041,Box181]
  Origin = -> Origin025
  Placement = pos=(0,-5.5,0) rot=(0,0,1;0rad)
  Tip = -> Box181
FEATURE [PartDesign::Fillet] Fillet070
  Base = -> Box204 [Edge2]
  BaseFeature = -> Box204
  Placement = pos=(-21.5005,18.625,0.235) rot=(0,-1,0;0.174533rad)
  Radius = 0.05
  SupportTransform = false
FEATURE [PartDesign::Fillet] Fillet053
  Base = -> Fillet070 [Edge33]
  BaseFeature = -> Fillet070
  Placement = pos=(-21.5005,18.625,0.235) rot=(0,-1,0;0.174533rad)
  Radius = 0.5
  SupportTransform = false
FEATURE [PartDesign::AdditiveBox] Box171
  AttacherType = Attacher::AttachEngine3D
  AttachmentOffset = pos=(-21.1,18.635,0.305) rot=(0,1,0;0.785398rad)
  BaseFeature = -> Fillet053
  Height = 0.375
  Length = 0.2
  MapMode = 5
  Placement = pos=(-21.1,18.635,0.305) rot=(0,1,0;0.785398rad)
  Support = -> [XY_Plane023]
  Width = 0.23
FEATURE [PartDesign::SubtractiveCylinder] Cylinder036
  Angle = 360
  AttacherType = Attacher::AttachEngine3D
  AttachmentOffset = pos=(-21.055,18.935,0.52) rot=(1,0,0;1.5708rad)
  BaseFeature = -> Box171
  Height = 0.375
  MapMode = 5
  Placement = pos=(-21.055,18.935,0.52) rot=(1,0,0;1.5708rad)
  Radius = 0.205
  Support = -> [XY_Plane023]
FEATURE [PartDesign::SubtractiveBox] Box173
  AttacherType = Attacher::AttachEngine3D
  AttachmentOffset = pos=(-20.95,18.635,0.53) rot=(0,0,1;0rad)
  BaseFeature = -> Cylinder036
  Height = 0.5
  Length = 0.1
  MapMode = 5
  Placement = pos=(-20.95,18.635,0.53) rot=(0,0,1;0rad)
  Support = -> [XY_Plane023]
  Width = 0.23
FEATURE [PartDesign::SubtractiveBox] Box170
  AttacherType = Attacher::AttachEngine3D
  AttachmentOffset = pos=(-21.15,18.635,0.297) rot=(0,-1,0;0.174533rad)
  BaseFeature = -> Box173
  Height = 0.115
  Length = 0.115
  MapMode = 5
  Placement = pos=(-21.15,18.635,0.297) rot=(0,-1,0;0.174533rad)
  Support = -> [XY_Plane023]
  Width = 0.23
FEATURE [PartDesign::Fillet] Fillet067
  Base = -> Box170 [Edge28]
  BaseFeature = -> Box170
  Placement = pos=(-21.15,18.635,0.297) rot=(0,-1,0;0.174533rad)
  Radius = 0.375
  SupportTransform = false
FEATURE [PartDesign::AdditiveBox] Box176
  AttacherType = Attacher::AttachEngine3D
  AttachmentOffset = pos=(-20.7,18.635,1.55) rot=(0,1,0;0.785398rad)
  BaseFeature = -> Fillet067
  Height = 0.375
  Length = 0.23
  MapMode = 5
  Placement = pos=(-20.7,18.635,1.55) rot=(0,1,0;0.785398rad)
  Support = -> [XY_Plane023]
  Width = 0.23
FEATURE [PartDesign::SubtractiveCylinder] Cylinder037
  Angle = 360
  AttacherType = Attacher::AttachEngine3D
  AttachmentOffset = pos=(-20.271,18.635,1.4056) rot=(-1,0,0;1.5708rad)
  BaseFeature = -> Box176
  Height = 0.23
  MapMode = 5
  Placement = pos=(-20.271,18.635,1.4056) rot=(-1,0,0;1.5708rad)
  Radius = 0.23
  Support = -> [XY_Plane023]
FEATURE [PartDesign::AdditiveBox] Box166
  AttacherType = Attacher::AttachEngine3D
  AttachmentOffset = pos=(-20.1,18.635,1.635) rot=(0,0,1;0rad)
  BaseFeature = -> Cylinder037
  Height = 0.265
  Length = 0.23
  MapMode = 5
  Placement = pos=(-20.1,18.635,1.635) rot=(0,0,1;0rad)
  Support = -> [XY_Plane023]
  Width = 0.23
FEATURE [PartDesign::Body] Body022  label="pin022"
  Group = -> [Box199,Box197,Box175,Box178,Box204,Fillet070,Fillet053,Box171,Cylinder036,Box173,Box170,Fillet067,Box176,Cylinder037,Box166]
  Origin = -> Origin014
  Placement = pos=(0,-4.5,0) rot=(0,0,1;0rad)
  Tip = -> Box166
FEATURE [PartDesign::SubtractiveBox] Box240
  AttacherType = Attacher::AttachEngine3D
  AttachmentOffset = pos=(-21.35,18.635,0.35) rot=(0,0,1;0rad)
  BaseFeature = -> Box239
  Height = 1.55
  Length = 0.5
  MapMode = 5
  Placement = pos=(-21.35,18.635,0.35) rot=(0,0,1;0rad)
  Support = -> [XY_Plane016]
  Width = 0.23
FEATURE [PartDesign::SubtractiveBox] Box214
  AttacherType = Attacher::AttachEngine3D
  AttachmentOffset = pos=(-20.5,18.63,0) rot=(0,0,1;0rad)
  BaseFeature = -> Box240
  Height = 1.635
  Length = 0.5
  MapMode = 5
  Placement = pos=(-20.5,18.63,0) rot=(0,0,1;0rad)
  Support = -> [XY_Plane016]
  Width = 0.25
FEATURE [PartDesign::SubtractiveBox] Box216
  AttacherType = Attacher::AttachEngine3D
  AttachmentOffset = pos=(-21.19,18.635,-0.12) rot=(0,-1,0;0.15708rad)
  BaseFeature = -> Box214
  Height = 0.12
  Length = 0.725
  MapMode = 5
  Placement = pos=(-21.19,18.635,-0.12) rot=(0,-1,0;0.15708rad)
  Support = -> [XY_Plane016]
  Width = 0.25
FEATURE [PartDesign::SubtractiveBox] Box236
  AttacherType = Attacher::AttachEngine3D
  AttachmentOffset = pos=(-21.5005,18.625,0.235) rot=(0,-1,0;0.174533rad)
  BaseFeature = -> Box216
  Height = 0.3
  Length = 0.6605
  MapMode = 5
  Placement = pos=(-21.5005,18.625,0.235) rot=(0,-1,0;0.174533rad)
  Support = -> [XY_Plane016]
  Width = 0.25
FEATURE [PartDesign::Fillet] Fillet050
  Base = -> Box236 [Edge2]
  BaseFeature = -> Box236
  Placement = pos=(-21.5005,18.625,0.235) rot=(0,-1,0;0.174533rad)
  Radius = 0.05
  SupportTransform = false
FEATURE [PartDesign::Fillet] Fillet036
  Base = -> Fillet050 [Edge33]
  BaseFeature = -> Fillet050
  Placement = pos=(-21.5005,18.625,0.235) rot=(0,-1,0;0.174533rad)
  Radius = 0.5
  SupportTransform = false
FEATURE [PartDesign::AdditiveBox] Box137
  AttacherType = Attacher::AttachEngine3D
  AttachmentOffset = pos=(-21.1,18.635,0.305) rot=(0,1,0;0.785398rad)
  BaseFeature = -> Fillet036
  Height = 0.375
  Length = 0.2
  MapMode = 5
  Placement = pos=(-21.1,18.635,0.305) rot=(0,1,0;0.785398rad)
  Support = -> [XY_Plane016]
  Width = 0.23
FEATURE [PartDesign::SubtractiveCylinder] Cylinder040
  Angle = 360
  AttacherType = Attacher::AttachEngine3D
  AttachmentOffset = pos=(-21.055,18.935,0.52) rot=(1,0,0;1.5708rad)
  BaseFeature = -> Box137
  Height = 0.375
  MapMode = 5
  Placement = pos=(-21.055,18.935,0.52) rot=(1,0,0;1.5708rad)
  Radius = 0.205
  Support = -> [XY_Plane016]
FEATURE [PartDesign::SubtractiveBox] Box191
  AttacherType = Attacher::AttachEngine3D
  AttachmentOffset = pos=(-20.95,18.635,0.53) rot=(0,0,1;0rad)
  BaseFeature = -> Cylinder040
  Height = 0.5
  Length = 0.1
  MapMode = 5
  Placement = pos=(-20.95,18.635,0.53) rot=(0,0,1;0rad)
  Support = -> [XY_Plane016]
  Width = 0.23
FEATURE [PartDesign::SubtractiveBox] Box190
  AttacherType = Attacher::AttachEngine3D
  AttachmentOffset = pos=(-21.15,18.635,0.297) rot=(0,-1,0;0.174533rad)
  BaseFeature = -> Box191
  Height = 0.115
  Length = 0.115
  MapMode = 5
  Placement = pos=(-21.15,18.635,0.297) rot=(0,-1,0;0.174533rad)
  Support = -> [XY_Plane016]
  Width = 0.23
FEATURE [PartDesign::Fillet] Fillet071
  Base = -> Box190 [Edge28]
  BaseFeature = -> Box190
  Placement = pos=(-21.15,18.635,0.297) rot=(0,-1,0;0.174533rad)
  Radius = 0.375
  SupportTransform = false
FEATURE [PartDesign::AdditiveBox] Box217
  AttacherType = Attacher::AttachEngine3D
  AttachmentOffset = pos=(-20.7,18.635,1.55) rot=(0,1,0;0.785398rad)
  BaseFeature = -> Fillet071
  Height = 0.375
  Length = 0.23
  MapMode = 5
  Placement = pos=(-20.7,18.635,1.55) rot=(0,1,0;0.785398rad)
  Support = -> [XY_Plane016]
  Width = 0.23
FEATURE [PartDesign::SubtractiveCylinder] Cylinder045
  Angle = 360
  AttacherType = Attacher::AttachEngine3D
  AttachmentOffset = pos=(-20.271,18.635,1.4056) rot=(-1,0,0;1.5708rad)
  BaseFeature = -> Box217
  Height = 0.23
  MapMode = 5
  Placement = pos=(-20.271,18.635,1.4056) rot=(-1,0,0;1.5708rad)
  Radius = 0.23
  Support = -> [XY_Plane016]
FEATURE [PartDesign::AdditiveBox] Box223
  AttacherType = Attacher::AttachEngine3D
  AttachmentOffset = pos=(-20.1,18.635,1.635) rot=(0,0,1;0rad)
  BaseFeature = -> Cylinder045
  Height = 0.265
  Length = 0.23
  MapMode = 5
  Placement = pos=(-20.1,18.635,1.635) rot=(0,0,1;0rad)
  Support = -> [XY_Plane016]
  Width = 0.23
FEATURE [PartDesign::Body] Body013  label="pin013"
  Group = -> [Box239,Box240,Box214,Box216,Box236,Fillet050,Fillet036,Box137,Cylinder040,Box191,Box190,Fillet071,Box217,Cylinder045,Box223]
  Origin = -> Origin015
  Tip = -> Box223
FEATURE [App::Part] Part001  label="Pin-set002"
  Group = -> [Body013,Body014,Body015,Body016,Body017,Body018,Body019,Body020,Body021,Body022,Body023,Body024]
  Origin = -> Origin026
  Placement = pos=(0,-6,0) rot=(0,0,1;0rad)
FEATURE [PartDesign::AdditiveBox] Box243
  AttacherType = Attacher::AttachEngine3D
  AttachmentOffset = pos=(-21.3,18.635,0) rot=(0,0,1;0rad)
  Height = 1.9
  Length = 1.3
  MapMode = 5
  Placement = pos=(-21.3,18.635,0) rot=(0,0,1;0rad)
  Support = -> [XY_Plane033]
  Width = 0.23
FEATURE [PartDesign::AdditiveBox] Box244
  AttacherType = Attacher::AttachEngine3D
  AttachmentOffset = pos=(-21.3,18.635,0) rot=(0,0,1;0rad)
  Height = 1.9
  Length = 1.3
  MapMode = 5
  Placement = pos=(-21.3,18.635,0) rot=(0,0,1;0rad)
  Support = -> [XY_Plane036]
  Width = 0.23
FEATURE [PartDesign::SubtractiveBox] Box248
  AttacherType = Attacher::AttachEngine3D
  AttachmentOffset = pos=(-21.35,18.635,0.35) rot=(0,0,1;0rad)
  BaseFeature = -> Box243
  Height = 1.55
  Length = 0.5
  MapMode = 5
  Placement = pos=(-21.35,18.635,0.35) rot=(0,0,1;0rad)
  Support = -> [XY_Plane033]
  Width = 0.23
FEATURE [PartDesign::AdditiveBox] Box249
  AttacherType = Attacher::AttachEngine3D
  AttachmentOffset = pos=(-21.3,18.635,0) rot=(0,0,1;0rad)
  Height = 1.9
  Length = 1.3
  MapMode = 5
  Placement = pos=(-21.3,18.635,0) rot=(0,0,1;0rad)
  Support = -> [XY_Plane038]
  Width = 0.23
FEATURE [PartDesign::SubtractiveBox] Box252
  AttacherType = Attacher::AttachEngine3D
  AttachmentOffset = pos=(-21.35,18.635,0.35) rot=(0,0,1;0rad)
  BaseFeature = -> Box249
  Height = 1.55
  Length = 0.5
  MapMode = 5
  Placement = pos=(-21.35,18.635,0.35) rot=(0,0,1;0rad)
  Support = -> [XY_Plane038]
  Width = 0.23
FEATURE [PartDesign::SubtractiveBox] Box256
  AttacherType = Attacher::AttachEngine3D
  AttachmentOffset = pos=(-21.35,18.635,0.35) rot=(0,0,1;0rad)
  BaseFeature = -> Box244
  Height = 1.55
  Length = 0.5
  MapMode = 5
  Placement = pos=(-21.35,18.635,0.35) rot=(0,0,1;0rad)
  Support = -> [XY_Plane036]
  Width = 0.23
FEATURE [PartDesign::AdditiveBox] Box265
  AttacherType = Attacher::AttachEngine3D
  AttachmentOffset = pos=(-21.3,18.635,0) rot=(0,0,1;0rad)
  Height = 1.9
  Length = 1.3
  MapMode = 5
  Placement = pos=(-21.3,18.635,0) rot=(0,0,1;0rad)
  Support = -> [XY_Plane031]
  Width = 0.23
FEATURE [PartDesign::SubtractiveBox] Box261
  AttacherType = Attacher::AttachEngine3D
  AttachmentOffset = pos=(-21.35,18.635,0.35) rot=(0,0,1;0rad)
  BaseFeature = -> Box265
  Height = 1.55
  Length = 0.5
  MapMode = 5
  Placement = pos=(-21.35,18.635,0.35) rot=(0,0,1;0rad)
  Support = -> [XY_Plane031]
  Width = 0.23
FEATURE [PartDesign::AdditiveBox] Box279
  AttacherType = Attacher::AttachEngine3D
  AttachmentOffset = pos=(-21.3,18.635,0) rot=(0,0,1;0rad)
  Height = 1.9
  Length = 1.3
  MapMode = 5
  Placement = pos=(-21.3,18.635,0) rot=(0,0,1;0rad)
  Support = -> [XY_Plane029]
  Width = 0.23
FEATURE [PartDesign::SubtractiveBox] Box270
  AttacherType = Attacher::AttachEngine3D
  AttachmentOffset = pos=(-21.35,18.635,0.35) rot=(0,0,1;0rad)
  BaseFeature = -> Box279
  Height = 1.55
  Length = 0.5
  MapMode = 5
  Placement = pos=(-21.35,18.635,0.35) rot=(0,0,1;0rad)
  Support = -> [XY_Plane029]
  Width = 0.23
FEATURE [PartDesign::AdditiveBox] Box285
  AttacherType = Attacher::AttachEngine3D
  AttachmentOffset = pos=(-21.3,18.635,0) rot=(0,0,1;0rad)
  Height = 1.9
  Length = 1.3
  MapMode = 5
  Placement = pos=(-21.3,18.635,0) rot=(0,0,1;0rad)
  Support = -> [XY_Plane028]
  Width = 0.23
FEATURE [PartDesign::SubtractiveBox] Box276
  AttacherType = Attacher::AttachEngine3D
  AttachmentOffset = pos=(-21.35,18.635,0.35) rot=(0,0,1;0rad)
  BaseFeature = -> Box285
  Height = 1.55
  Length = 0.5
  MapMode = 5
  Placement = pos=(-21.35,18.635,0.35) rot=(0,0,1;0rad)
  Support = -> [XY_Plane028]
  Width = 0.23
FEATURE [PartDesign::AdditiveBox] Box293
  AttacherType = Attacher::AttachEngine3D
  AttachmentOffset = pos=(-21.3,18.635,0) rot=(0,0,1;0rad)
  Height = 1.9
  Length = 1.3
  MapMode = 5
  Placement = pos=(-21.3,18.635,0) rot=(0,0,1;0rad)
  Support = -> [XY_Plane035]
  Width = 0.23
FEATURE [PartDesign::SubtractiveBox] Box290
  AttacherType = Attacher::AttachEngine3D
  AttachmentOffset = pos=(-21.35,18.635,0.35) rot=(0,0,1;0rad)
  BaseFeature = -> Box293
  Height = 1.55
  Length = 0.5
  MapMode = 5
  Placement = pos=(-21.35,18.635,0.35) rot=(0,0,1;0rad)
  Support = -> [XY_Plane035]
  Width = 0.23
FEATURE [PartDesign::SubtractiveBox] Box280
  AttacherType = Attacher::AttachEngine3D
  AttachmentOffset = pos=(-20.5,18.63,0) rot=(0,0,1;0rad)
  BaseFeature = -> Box290
  Height = 1.635
  Length = 0.5
  MapMode = 5
  Placement = pos=(-20.5,18.63,0) rot=(0,0,1;0rad)
  Support = -> [XY_Plane035]
  Width = 0.25
FEATURE [PartDesign::SubtractiveBox] Box294
  AttacherType = Attacher::AttachEngine3D
  AttachmentOffset = pos=(-21.19,18.635,-0.12) rot=(0,-1,0;0.15708rad)
  BaseFeature = -> Box280
  Height = 0.12
  Length = 0.725
  MapMode = 5
  Placement = pos=(-21.19,18.635,-0.12) rot=(0,-1,0;0.15708rad)
  Support = -> [XY_Plane035]
  Width = 0.25
FEATURE [PartDesign::SubtractiveBox] Box298
  AttacherType = Attacher::AttachEngine3D
  AttachmentOffset = pos=(-20.5,18.63,0) rot=(0,0,1;0rad)
  BaseFeature = -> Box248
  Height = 1.635
  Length = 0.5
  MapMode = 5
  Placement = pos=(-20.5,18.63,0) rot=(0,0,1;0rad)
  Support = -> [XY_Plane033]
  Width = 0.25
FEATURE [PartDesign::SubtractiveBox] Box246
  AttacherType = Attacher::AttachEngine3D
  AttachmentOffset = pos=(-21.19,18.635,-0.12) rot=(0,-1,0;0.15708rad)
  BaseFeature = -> Box298
  Height = 0.12
  Length = 0.725
  MapMode = 5
  Placement = pos=(-21.19,18.635,-0.12) rot=(0,-1,0;0.15708rad)
  Support = -> [XY_Plane033]
  Width = 0.25
FEATURE [PartDesign::SubtractiveBox] Box245
  AttacherType = Attacher::AttachEngine3D
  AttachmentOffset = pos=(-21.5005,18.625,0.235) rot=(0,-1,0;0.174533rad)
  BaseFeature = -> Box246
  Height = 0.3
  Length = 0.6605
  MapMode = 5
  Placement = pos=(-21.5005,18.625,0.235) rot=(0,-1,0;0.174533rad)
  Support = -> [XY_Plane033]
  Width = 0.25
FEATURE [PartDesign::SubtractiveBox] Box301
  AttacherType = Attacher::AttachEngine3D
  AttachmentOffset = pos=(-21.5005,18.625,0.235) rot=(0,-1,0;0.174533rad)
  BaseFeature = -> Box294
  Height = 0.3
  Length = 0.6605
  MapMode = 5
  Placement = pos=(-21.5005,18.625,0.235) rot=(0,-1,0;0.174533rad)
  Support = -> [XY_Plane035]
  Width = 0.25
FEATURE [PartDesign::AdditiveBox] Box308
  AttacherType = Attacher::AttachEngine3D
  AttachmentOffset = pos=(-21.3,18.635,0) rot=(0,0,1;0rad)
  Height = 1.9
  Length = 1.3
  MapMode = 5
  Placement = pos=(-21.3,18.635,0) rot=(0,0,1;0rad)
  Support = -> [XY_Plane037]
  Width = 0.23
FEATURE [PartDesign::SubtractiveBox] Box296
  AttacherType = Attacher::AttachEngine3D
  AttachmentOffset = pos=(-21.35,18.635,0.35) rot=(0,0,1;0rad)
  BaseFeature = -> Box308
  Height = 1.55
  Length = 0.5
  MapMode = 5
  Placement = pos=(-21.35,18.635,0.35) rot=(0,0,1;0rad)
  Support = -> [XY_Plane037]
  Width = 0.23
FEATURE [PartDesign::SubtractiveBox] Box284
  AttacherType = Attacher::AttachEngine3D
  AttachmentOffset = pos=(-20.5,18.63,0) rot=(0,0,1;0rad)
  BaseFeature = -> Box296
  Height = 1.635
  Length = 0.5
  MapMode = 5
  Placement = pos=(-20.5,18.63,0) rot=(0,0,1;0rad)
  Support = -> [XY_Plane037]
  Width = 0.25
FEATURE [PartDesign::SubtractiveBox] Box275
  AttacherType = Attacher::AttachEngine3D
  AttachmentOffset = pos=(-21.19,18.635,-0.12) rot=(0,-1,0;0.15708rad)
  BaseFeature = -> Box284
  Height = 0.12
  Length = 0.725
  MapMode = 5
  Placement = pos=(-21.19,18.635,-0.12) rot=(0,-1,0;0.15708rad)
  Support = -> [XY_Plane037]
  Width = 0.25
FEATURE [PartDesign::SubtractiveBox] Box310
  AttacherType = Attacher::AttachEngine3D
  AttachmentOffset = pos=(-20.5,18.63,0) rot=(0,0,1;0rad)
  BaseFeature = -> Box256
  Height = 1.635
  Length = 0.5
  MapMode = 5
  Placement = pos=(-20.5,18.63,0) rot=(0,0,1;0rad)
  Support = -> [XY_Plane036]
  Width = 0.25
FEATURE [PartDesign::AdditiveBox] Box312
  AttacherType = Attacher::AttachEngine3D
  AttachmentOffset = pos=(-21.3,18.635,0) rot=(0,0,1;0rad)
  Height = 1.9
  Length = 1.3
  MapMode = 5
  Placement = pos=(-21.3,18.635,0) rot=(0,0,1;0rad)
  Support = -> [XY_Plane027]
  Width = 0.23
FEATURE [PartDesign::SubtractiveBox] Box307
  AttacherType = Attacher::AttachEngine3D
  AttachmentOffset = pos=(-21.35,18.635,0.35) rot=(0,0,1;0rad)
  BaseFeature = -> Box312
  Height = 1.55
  Length = 0.5
  MapMode = 5
  Placement = pos=(-21.35,18.635,0.35) rot=(0,0,1;0rad)
  Support = -> [XY_Plane027]
  Width = 0.23
FEATURE [PartDesign::SubtractiveBox] Box278
  AttacherType = Attacher::AttachEngine3D
  AttachmentOffset = pos=(-20.5,18.63,0) rot=(0,0,1;0rad)
  BaseFeature = -> Box307
  Height = 1.635
  Length = 0.5
  MapMode = 5
  Placement = pos=(-20.5,18.63,0) rot=(0,0,1;0rad)
  Support = -> [XY_Plane027]
  Width = 0.25
FEATURE [PartDesign::SubtractiveBox] Box288
  AttacherType = Attacher::AttachEngine3D
  AttachmentOffset = pos=(-21.19,18.635,-0.12) rot=(0,-1,0;0.15708rad)
  BaseFeature = -> Box278
  Height = 0.12
  Length = 0.725
  MapMode = 5
  Placement = pos=(-21.19,18.635,-0.12) rot=(0,-1,0;0.15708rad)
  Support = -> [XY_Plane027]
  Width = 0.25
FEATURE [PartDesign::SubtractiveBox] Box289
  AttacherType = Attacher::AttachEngine3D
  AttachmentOffset = pos=(-21.5005,18.625,0.235) rot=(0,-1,0;0.174533rad)
  BaseFeature = -> Box288
  Height = 0.3
  Length = 0.6605
  MapMode = 5
  Placement = pos=(-21.5005,18.625,0.235) rot=(0,-1,0;0.174533rad)
  Support = -> [XY_Plane027]
  Width = 0.25
FEATURE [PartDesign::SubtractiveBox] Box315
  AttacherType = Attacher::AttachEngine3D
  AttachmentOffset = pos=(-20.5,18.63,0) rot=(0,0,1;0rad)
  BaseFeature = -> Box252
  Height = 1.635
  Length = 0.5
  MapMode = 5
  Placement = pos=(-20.5,18.63,0) rot=(0,0,1;0rad)
  Support = -> [XY_Plane038]
  Width = 0.25
FEATURE [PartDesign::SubtractiveBox] Box253
  AttacherType = Attacher::AttachEngine3D
  AttachmentOffset = pos=(-21.19,18.635,-0.12) rot=(0,-1,0;0.15708rad)
  BaseFeature = -> Box315
  Height = 0.12
  Length = 0.725
  MapMode = 5
  Placement = pos=(-21.19,18.635,-0.12) rot=(0,-1,0;0.15708rad)
  Support = -> [XY_Plane038]
  Width = 0.25
FEATURE [PartDesign::SubtractiveBox] Box242
  AttacherType = Attacher::AttachEngine3D
  AttachmentOffset = pos=(-21.5005,18.625,0.235) rot=(0,-1,0;0.174533rad)
  BaseFeature = -> Box253
  Height = 0.3
  Length = 0.6605
  MapMode = 5
  Placement = pos=(-21.5005,18.625,0.235) rot=(0,-1,0;0.174533rad)
  Support = -> [XY_Plane038]
  Width = 0.25
FEATURE [PartDesign::SubtractiveBox] Box316
  AttacherType = Attacher::AttachEngine3D
  AttachmentOffset = pos=(-21.19,18.635,-0.12) rot=(0,-1,0;0.15708rad)
  BaseFeature = -> Box310
  Height = 0.12
  Length = 0.725
  MapMode = 5
  Placement = pos=(-21.19,18.635,-0.12) rot=(0,-1,0;0.15708rad)
  Support = -> [XY_Plane036]
  Width = 0.25
FEATURE [PartDesign::SubtractiveBox] Box254
  AttacherType = Attacher::AttachEngine3D
  AttachmentOffset = pos=(-21.5005,18.625,0.235) rot=(0,-1,0;0.174533rad)
  BaseFeature = -> Box316
  Height = 0.3
  Length = 0.6605
  MapMode = 5
  Placement = pos=(-21.5005,18.625,0.235) rot=(0,-1,0;0.174533rad)
  Support = -> [XY_Plane036]
  Width = 0.25
FEATURE [PartDesign::SubtractiveBox] Box317
  AttacherType = Attacher::AttachEngine3D
  AttachmentOffset = pos=(-21.5005,18.625,0.235) rot=(0,-1,0;0.174533rad)
  BaseFeature = -> Box275
  Height = 0.3
  Length = 0.6605
  MapMode = 5
  Placement = pos=(-21.5005,18.625,0.235) rot=(0,-1,0;0.174533rad)
  Support = -> [XY_Plane037]
  Width = 0.25
FEATURE [PartDesign::AdditiveBox] Box337
  AttacherType = Attacher::AttachEngine3D
  AttachmentOffset = pos=(-21.3,18.635,0) rot=(0,0,1;0rad)
  Height = 1.9
  Length = 1.3
  MapMode = 5
  Placement = pos=(-21.3,18.635,0) rot=(0,0,1;0rad)
  Support = -> [XY_Plane034]
  Width = 0.23
FEATURE [PartDesign::SubtractiveBox] Box327
  AttacherType = Attacher::AttachEngine3D
  AttachmentOffset = pos=(-21.35,18.635,0.35) rot=(0,0,1;0rad)
  BaseFeature = -> Box337
  Height = 1.55
  Length = 0.5
  MapMode = 5
  Placement = pos=(-21.35,18.635,0.35) rot=(0,0,1;0rad)
  Support = -> [XY_Plane034]
  Width = 0.23
FEATURE [PartDesign::SubtractiveBox] Box329
  AttacherType = Attacher::AttachEngine3D
  AttachmentOffset = pos=(-20.5,18.63,0) rot=(0,0,1;0rad)
  BaseFeature = -> Box327
  Height = 1.635
  Length = 0.5
  MapMode = 5
  Placement = pos=(-20.5,18.63,0) rot=(0,0,1;0rad)
  Support = -> [XY_Plane034]
  Width = 0.25
FEATURE [PartDesign::SubtractiveBox] Box333
  AttacherType = Attacher::AttachEngine3D
  AttachmentOffset = pos=(-21.19,18.635,-0.12) rot=(0,-1,0;0.15708rad)
  BaseFeature = -> Box329
  Height = 0.12
  Length = 0.725
  MapMode = 5
  Placement = pos=(-21.19,18.635,-0.12) rot=(0,-1,0;0.15708rad)
  Support = -> [XY_Plane034]
  Width = 0.25
FEATURE [PartDesign::SubtractiveBox] Box334
  AttacherType = Attacher::AttachEngine3D
  AttachmentOffset = pos=(-21.5005,18.625,0.235) rot=(0,-1,0;0.174533rad)
  BaseFeature = -> Box333
  Height = 0.3
  Length = 0.6605
  MapMode = 5
  Placement = pos=(-21.5005,18.625,0.235) rot=(0,-1,0;0.174533rad)
  Support = -> [XY_Plane034]
  Width = 0.25
FEATURE [PartDesign::AdditiveBox] Box343
  AttacherType = Attacher::AttachEngine3D
  AttachmentOffset = pos=(-21.3,18.635,0) rot=(0,0,1;0rad)
  Height = 1.9
  Length = 1.3
  MapMode = 5
  Placement = pos=(-21.3,18.635,0) rot=(0,0,1;0rad)
  Support = -> [XY_Plane030]
  Width = 0.23
FEATURE [PartDesign::SubtractiveBox] Box341
  AttacherType = Attacher::AttachEngine3D
  AttachmentOffset = pos=(-21.35,18.635,0.35) rot=(0,0,1;0rad)
  BaseFeature = -> Box343
  Height = 1.55
  Length = 0.5
  MapMode = 5
  Placement = pos=(-21.35,18.635,0.35) rot=(0,0,1;0rad)
  Support = -> [XY_Plane030]
  Width = 0.23
FEATURE [PartDesign::SubtractiveBox] Box326
  AttacherType = Attacher::AttachEngine3D
  AttachmentOffset = pos=(-20.5,18.63,0) rot=(0,0,1;0rad)
  BaseFeature = -> Box341
  Height = 1.635
  Length = 0.5
  MapMode = 5
  Placement = pos=(-20.5,18.63,0) rot=(0,0,1;0rad)
  Support = -> [XY_Plane030]
  Width = 0.25
FEATURE [PartDesign::AdditiveBox] Box345
  AttacherType = Attacher::AttachEngine3D
  AttachmentOffset = pos=(-21.3,18.635,0) rot=(0,0,1;0rad)
  Height = 1.9
  Length = 1.3
  MapMode = 5
  Placement = pos=(-21.3,18.635,0) rot=(0,0,1;0rad)
  Support = -> [XY_Plane032]
  Width = 0.23
FEATURE [PartDesign::SubtractiveBox] Box347
  AttacherType = Attacher::AttachEngine3D
  AttachmentOffset = pos=(-21.19,18.635,-0.12) rot=(0,-1,0;0.15708rad)
  BaseFeature = -> Box326
  Height = 0.12
  Length = 0.725
  MapMode = 5
  Placement = pos=(-21.19,18.635,-0.12) rot=(0,-1,0;0.15708rad)
  Support = -> [XY_Plane030]
  Width = 0.25
FEATURE [PartDesign::SubtractiveBox] Box346
  AttacherType = Attacher::AttachEngine3D
  AttachmentOffset = pos=(-21.5005,18.625,0.235) rot=(0,-1,0;0.174533rad)
  BaseFeature = -> Box347
  Height = 0.3
  Length = 0.6605
  MapMode = 5
  Placement = pos=(-21.5005,18.625,0.235) rot=(0,-1,0;0.174533rad)
  Support = -> [XY_Plane030]
  Width = 0.25
FEATURE [PartDesign::SubtractiveBox] Box348
  AttacherType = Attacher::AttachEngine3D
  AttachmentOffset = pos=(-21.35,18.635,0.35) rot=(0,0,1;0rad)
  BaseFeature = -> Box345
  Height = 1.55
  Length = 0.5
  MapMode = 5
  Placement = pos=(-21.35,18.635,0.35) rot=(0,0,1;0rad)
  Support = -> [XY_Plane032]
  Width = 0.23
FEATURE [PartDesign::SubtractiveBox] Box328
  AttacherType = Attacher::AttachEngine3D
  AttachmentOffset = pos=(-20.5,18.63,0) rot=(0,0,1;0rad)
  BaseFeature = -> Box348
  Height = 1.635
  Length = 0.5
  MapMode = 5
  Placement = pos=(-20.5,18.63,0) rot=(0,0,1;0rad)
  Support = -> [XY_Plane032]
  Width = 0.25
FEATURE [PartDesign::SubtractiveBox] Box323
  AttacherType = Attacher::AttachEngine3D
  AttachmentOffset = pos=(-21.19,18.635,-0.12) rot=(0,-1,0;0.15708rad)
  BaseFeature = -> Box328
  Height = 0.12
  Length = 0.725
  MapMode = 5
  Placement = pos=(-21.19,18.635,-0.12) rot=(0,-1,0;0.15708rad)
  Support = -> [XY_Plane032]
  Width = 0.25
FEATURE [PartDesign::SubtractiveBox] Box344
  AttacherType = Attacher::AttachEngine3D
  AttachmentOffset = pos=(-21.5005,18.625,0.235) rot=(0,-1,0;0.174533rad)
  BaseFeature = -> Box323
  Height = 0.3
  Length = 0.6605
  MapMode = 5
  Placement = pos=(-21.5005,18.625,0.235) rot=(0,-1,0;0.174533rad)
  Support = -> [XY_Plane032]
  Width = 0.25
FEATURE [PartDesign::Fillet] Fillet077
  Base = -> Box334 [Edge2]
  BaseFeature = -> Box334
  Placement = pos=(-21.5005,18.625,0.235) rot=(0,-1,0;0.174533rad)
  Radius = 0.05
  SupportTransform = false
FEATURE [PartDesign::Fillet] Fillet078
  Base = -> Fillet077 [Edge33]
  BaseFeature = -> Fillet077
  Placement = pos=(-21.5005,18.625,0.235) rot=(0,-1,0;0.174533rad)
  Radius = 0.5
  SupportTransform = false
FEATURE [PartDesign::AdditiveBox] Box320
  AttacherType = Attacher::AttachEngine3D
  AttachmentOffset = pos=(-21.1,18.635,0.305) rot=(0,1,0;0.785398rad)
  BaseFeature = -> Fillet078
  Height = 0.375
  Length = 0.2
  MapMode = 5
  Placement = pos=(-21.1,18.635,0.305) rot=(0,1,0;0.785398rad)
  Support = -> [XY_Plane034]
  Width = 0.23
FEATURE [PartDesign::SubtractiveCylinder] Cylinder068
  Angle = 360
  AttacherType = Attacher::AttachEngine3D
  AttachmentOffset = pos=(-21.055,18.935,0.52) rot=(1,0,0;1.5708rad)
  BaseFeature = -> Box320
  Height = 0.375
  MapMode = 5
  Placement = pos=(-21.055,18.935,0.52) rot=(1,0,0;1.5708rad)
  Radius = 0.205
  Support = -> [XY_Plane034]
FEATURE [PartDesign::SubtractiveBox] Box335
  AttacherType = Attacher::AttachEngine3D
  AttachmentOffset = pos=(-20.95,18.635,0.53) rot=(0,0,1;0rad)
  BaseFeature = -> Cylinder068
  Height = 0.5
  Length = 0.1
  MapMode = 5
  Placement = pos=(-20.95,18.635,0.53) rot=(0,0,1;0rad)
  Support = -> [XY_Plane034]
  Width = 0.23
FEATURE [PartDesign::SubtractiveBox] Box331
  AttacherType = Attacher::AttachEngine3D
  AttachmentOffset = pos=(-21.15,18.635,0.297) rot=(0,-1,0;0.174533rad)
  BaseFeature = -> Box335
  Height = 0.115
  Length = 0.115
  MapMode = 5
  Placement = pos=(-21.15,18.635,0.297) rot=(0,-1,0;0.174533rad)
  Support = -> [XY_Plane034]
  Width = 0.23
FEATURE [PartDesign::Fillet] Fillet079
  Base = -> Box346 [Edge2]
  BaseFeature = -> Box346
  Placement = pos=(-21.5005,18.625,0.235) rot=(0,-1,0;0.174533rad)
  Radius = 0.05
  SupportTransform = false
FEATURE [PartDesign::Fillet] Fillet085
  Base = -> Box331 [Edge28]
  BaseFeature = -> Box331
  Placement = pos=(-21.15,18.635,0.297) rot=(0,-1,0;0.174533rad)
  Radius = 0.375
  SupportTransform = false
FEATURE [PartDesign::AdditiveBox] Box330
  AttacherType = Attacher::AttachEngine3D
  AttachmentOffset = pos=(-20.7,18.635,1.55) rot=(0,1,0;0.785398rad)
  BaseFeature = -> Fillet085
  Height = 0.375
  Length = 0.23
  MapMode = 5
  Placement = pos=(-20.7,18.635,1.55) rot=(0,1,0;0.785398rad)
  Support = -> [XY_Plane034]
  Width = 0.23
FEATURE [PartDesign::SubtractiveCylinder] Cylinder071
  Angle = 360
  AttacherType = Attacher::AttachEngine3D
  AttachmentOffset = pos=(-20.271,18.635,1.4056) rot=(-1,0,0;1.5708rad)
  BaseFeature = -> Box330
  Height = 0.23
  MapMode = 5
  Placement = pos=(-20.271,18.635,1.4056) rot=(-1,0,0;1.5708rad)
  Radius = 0.23
  Support = -> [XY_Plane034]
FEATURE [PartDesign::AdditiveBox] Box336
  AttacherType = Attacher::AttachEngine3D
  AttachmentOffset = pos=(-20.1,18.635,1.635) rot=(0,0,1;0rad)
  BaseFeature = -> Cylinder071
  Height = 0.265
  Length = 0.23
  MapMode = 5
  Placement = pos=(-20.1,18.635,1.635) rot=(0,0,1;0rad)
  Support = -> [XY_Plane034]
  Width = 0.23
FEATURE [PartDesign::Body] Body026  label="pin026"
  Group = -> [Box337,Box327,Box329,Box333,Box334,Fillet077,Fillet078,Box320,Cylinder068,Box335,Box331,Fillet085,Box330,Cylinder071,Box336]
  Origin = -> Origin029
  Placement = pos=(0,-0.5,0) rot=(0,0,1;0rad)
  Tip = -> Box336
FEATURE [PartDesign::Fillet] Fillet086
  Base = -> Fillet079 [Edge33]
  BaseFeature = -> Fillet079
  Placement = pos=(-21.5005,18.625,0.235) rot=(0,-1,0;0.174533rad)
  Radius = 0.5
  SupportTransform = false
FEATURE [PartDesign::AdditiveBox] Box325
  AttacherType = Attacher::AttachEngine3D
  AttachmentOffset = pos=(-21.1,18.635,0.305) rot=(0,1,0;0.785398rad)
  BaseFeature = -> Fillet086
  Height = 0.375
  Length = 0.2
  MapMode = 5
  Placement = pos=(-21.1,18.635,0.305) rot=(0,1,0;0.785398rad)
  Support = -> [XY_Plane030]
  Width = 0.23
FEATURE [PartDesign::SubtractiveCylinder] Cylinder072
  Angle = 360
  AttacherType = Attacher::AttachEngine3D
  AttachmentOffset = pos=(-21.055,18.935,0.52) rot=(1,0,0;1.5708rad)
  BaseFeature = -> Box325
  Height = 0.375
  MapMode = 5
  Placement = pos=(-21.055,18.935,0.52) rot=(1,0,0;1.5708rad)
  Radius = 0.205
  Support = -> [XY_Plane030]
FEATURE [PartDesign::SubtractiveBox] Box340
  AttacherType = Attacher::AttachEngine3D
  AttachmentOffset = pos=(-20.95,18.635,0.53) rot=(0,0,1;0rad)
  BaseFeature = -> Cylinder072
  Height = 0.5
  Length = 0.1
  MapMode = 5
  Placement = pos=(-20.95,18.635,0.53) rot=(0,0,1;0rad)
  Support = -> [XY_Plane030]
  Width = 0.23
FEATURE [PartDesign::SubtractiveBox] Box338
  AttacherType = Attacher::AttachEngine3D
  AttachmentOffset = pos=(-21.15,18.635,0.297) rot=(0,-1,0;0.174533rad)
  BaseFeature = -> Box340
  Height = 0.115
  Length = 0.115
  MapMode = 5
  Placement = pos=(-21.15,18.635,0.297) rot=(0,-1,0;0.174533rad)
  Support = -> [XY_Plane030]
  Width = 0.23
FEATURE [PartDesign::Fillet] Fillet074
  Base = -> Box338 [Edge28]
  BaseFeature = -> Box338
  Placement = pos=(-21.15,18.635,0.297) rot=(0,-1,0;0.174533rad)
  Radius = 0.375
  SupportTransform = false
FEATURE [PartDesign::AdditiveBox] Box339
  AttacherType = Attacher::AttachEngine3D
  AttachmentOffset = pos=(-20.7,18.635,1.55) rot=(0,1,0;0.785398rad)
  BaseFeature = -> Fillet074
  Height = 0.375
  Length = 0.23
  MapMode = 5
  Placement = pos=(-20.7,18.635,1.55) rot=(0,1,0;0.785398rad)
  Support = -> [XY_Plane030]
  Width = 0.23
FEATURE [PartDesign::SubtractiveCylinder] Cylinder073
  Angle = 360
  AttacherType = Attacher::AttachEngine3D
  AttachmentOffset = pos=(-20.271,18.635,1.4056) rot=(-1,0,0;1.5708rad)
  BaseFeature = -> Box339
  Height = 0.23
  MapMode = 5
  Placement = pos=(-20.271,18.635,1.4056) rot=(-1,0,0;1.5708rad)
  Radius = 0.23
  Support = -> [XY_Plane030]
FEATURE [PartDesign::AdditiveBox] Box342
  AttacherType = Attacher::AttachEngine3D
  AttachmentOffset = pos=(-20.1,18.635,1.635) rot=(0,0,1;0rad)
  BaseFeature = -> Cylinder073
  Height = 0.265
  Length = 0.23
  MapMode = 5
  Placement = pos=(-20.1,18.635,1.635) rot=(0,0,1;0rad)
  Support = -> [XY_Plane030]
  Width = 0.23
FEATURE [PartDesign::Body] Body030  label="pin030"
  Group = -> [Box343,Box341,Box326,Box347,Box346,Fillet079,Fillet086,Box325,Cylinder072,Box340,Box338,Fillet074,Box339,Cylinder073,Box342]
  Origin = -> Origin032
  Placement = pos=(0,-1,0) rot=(0,0,1;0rad)
  Tip = -> Box342
FEATURE [PartDesign::Fillet] Fillet087
  Base = -> Box344 [Edge2]
  BaseFeature = -> Box344
  Placement = pos=(-21.5005,18.625,0.235) rot=(0,-1,0;0.174533rad)
  Radius = 0.05
  SupportTransform = false
FEATURE [PartDesign::Fillet] Fillet072
  Base = -> Fillet087 [Edge33]
  BaseFeature = -> Fillet087
  Placement = pos=(-21.5005,18.625,0.235) rot=(0,-1,0;0.174533rad)
  Radius = 0.5
  SupportTransform = false
FEATURE [PartDesign::AdditiveBox] Box257
  AttacherType = Attacher::AttachEngine3D
  AttachmentOffset = pos=(-21.1,18.635,0.305) rot=(0,1,0;0.785398rad)
  BaseFeature = -> Fillet072
  Height = 0.375
  Length = 0.2
  MapMode = 5
  Placement = pos=(-21.1,18.635,0.305) rot=(0,1,0;0.785398rad)
  Support = -> [XY_Plane032]
  Width = 0.23
FEATURE [PartDesign::SubtractiveCylinder] Cylinder063
  Angle = 360
  AttacherType = Attacher::AttachEngine3D
  AttachmentOffset = pos=(-21.055,18.935,0.52) rot=(1,0,0;1.5708rad)
  BaseFeature = -> Box257
  Height = 0.375
  MapMode = 5
  Placement = pos=(-21.055,18.935,0.52) rot=(1,0,0;1.5708rad)
  Radius = 0.205
  Support = -> [XY_Plane032]
FEATURE [PartDesign::SubtractiveBox] Box303
  AttacherType = Attacher::AttachEngine3D
  AttachmentOffset = pos=(-20.95,18.635,0.53) rot=(0,0,1;0rad)
  BaseFeature = -> Cylinder063
  Height = 0.5
  Length = 0.1
  MapMode = 5
  Placement = pos=(-20.95,18.635,0.53) rot=(0,0,1;0rad)
  Support = -> [XY_Plane032]
  Width = 0.23
FEATURE [PartDesign::SubtractiveBox] Box291
  AttacherType = Attacher::AttachEngine3D
  AttachmentOffset = pos=(-21.15,18.635,0.297) rot=(0,-1,0;0.174533rad)
  BaseFeature = -> Box303
  Height = 0.115
  Length = 0.115
  MapMode = 5
  Placement = pos=(-21.15,18.635,0.297) rot=(0,-1,0;0.174533rad)
  Support = -> [XY_Plane032]
  Width = 0.23
FEATURE [PartDesign::Fillet] Fillet091
  Base = -> Box301 [Edge2]
  BaseFeature = -> Box301
  Placement = pos=(-21.5005,18.625,0.235) rot=(0,-1,0;0.174533rad)
  Radius = 0.05
  SupportTransform = false
FEATURE [PartDesign::Fillet] Fillet093
  Base = -> Fillet091 [Edge33]
  BaseFeature = -> Fillet091
  Placement = pos=(-21.5005,18.625,0.235) rot=(0,-1,0;0.174533rad)
  Radius = 0.5
  SupportTransform = false
FEATURE [PartDesign::AdditiveBox] Box283
  AttacherType = Attacher::AttachEngine3D
  AttachmentOffset = pos=(-21.1,18.635,0.305) rot=(0,1,0;0.785398rad)
  BaseFeature = -> Fillet093
  Height = 0.375
  Length = 0.2
  MapMode = 5
  Placement = pos=(-21.1,18.635,0.305) rot=(0,1,0;0.785398rad)
  Support = -> [XY_Plane035]
  Width = 0.23
FEATURE [PartDesign::SubtractiveCylinder] Cylinder060
  Angle = 360
  AttacherType = Attacher::AttachEngine3D
  AttachmentOffset = pos=(-21.055,18.935,0.52) rot=(1,0,0;1.5708rad)
  BaseFeature = -> Box283
  Height = 0.375
  MapMode = 5
  Placement = pos=(-21.055,18.935,0.52) rot=(1,0,0;1.5708rad)
  Radius = 0.205
  Support = -> [XY_Plane035]
FEATURE [PartDesign::SubtractiveBox] Box302
  AttacherType = Attacher::AttachEngine3D
  AttachmentOffset = pos=(-20.95,18.635,0.53) rot=(0,0,1;0rad)
  BaseFeature = -> Cylinder060
  Height = 0.5
  Length = 0.1
  MapMode = 5
  Placement = pos=(-20.95,18.635,0.53) rot=(0,0,1;0rad)
  Support = -> [XY_Plane035]
  Width = 0.23
FEATURE [PartDesign::SubtractiveBox] Box287
  AttacherType = Attacher::AttachEngine3D
  AttachmentOffset = pos=(-21.15,18.635,0.297) rot=(0,-1,0;0.174533rad)
  BaseFeature = -> Box302
  Height = 0.115
  Length = 0.115
  MapMode = 5
  Placement = pos=(-21.15,18.635,0.297) rot=(0,-1,0;0.174533rad)
  Support = -> [XY_Plane035]
  Width = 0.23
FEATURE [PartDesign::Fillet] Fillet092
  Base = -> Box287 [Edge28]
  BaseFeature = -> Box287
  Placement = pos=(-21.15,18.635,0.297) rot=(0,-1,0;0.174533rad)
  Radius = 0.375
  SupportTransform = false
FEATURE [PartDesign::AdditiveBox] Box292
  AttacherType = Attacher::AttachEngine3D
  AttachmentOffset = pos=(-20.7,18.635,1.55) rot=(0,1,0;0.785398rad)
  BaseFeature = -> Fillet092
  Height = 0.375
  Length = 0.23
  MapMode = 5
  Placement = pos=(-20.7,18.635,1.55) rot=(0,1,0;0.785398rad)
  Support = -> [XY_Plane035]
  Width = 0.23
FEATURE [PartDesign::SubtractiveCylinder] Cylinder062
  Angle = 360
  AttacherType = Attacher::AttachEngine3D
  AttachmentOffset = pos=(-20.271,18.635,1.4056) rot=(-1,0,0;1.5708rad)
  BaseFeature = -> Box292
  Height = 0.23
  MapMode = 5
  Placement = pos=(-20.271,18.635,1.4056) rot=(-1,0,0;1.5708rad)
  Radius = 0.23
  Support = -> [XY_Plane035]
FEATURE [PartDesign::AdditiveBox] Box300
  AttacherType = Attacher::AttachEngine3D
  AttachmentOffset = pos=(-20.1,18.635,1.635) rot=(0,0,1;0rad)
  BaseFeature = -> Cylinder062
  Height = 0.265
  Length = 0.23
  MapMode = 5
  Placement = pos=(-20.1,18.635,1.635) rot=(0,0,1;0rad)
  Support = -> [XY_Plane035]
  Width = 0.23
FEATURE [PartDesign::Body] Body033  label="pin033"
  Group = -> [Box293,Box290,Box280,Box294,Box301,Fillet091,Fillet093,Box283,Cylinder060,Box302,Box287,Fillet092,Box292,Cylinder062,Box300]
  Origin = -> Origin031
  Placement = pos=(0,-5,0) rot=(0,0,1;0rad)
  Tip = -> Box300
FEATURE [PartDesign::Fillet] Fillet094
  Base = -> Box242 [Edge2]
  BaseFeature = -> Box242
  Placement = pos=(-21.5005,18.625,0.235) rot=(0,-1,0;0.174533rad)
  Radius = 0.05
  SupportTransform = false
FEATURE [PartDesign::Fillet] Fillet097
  Base = -> Box245 [Edge2]
  BaseFeature = -> Box245
  Placement = pos=(-21.5005,18.625,0.235) rot=(0,-1,0;0.174533rad)
  Radius = 0.05
  SupportTransform = false
FEATURE [PartDesign::Fillet] Fillet098
  Base = -> Box289 [Edge2]
  BaseFeature = -> Box289
  Placement = pos=(-21.5005,18.625,0.235) rot=(0,-1,0;0.174533rad)
  Radius = 0.05
  SupportTransform = false
FEATURE [PartDesign::Fillet] Fillet099
  Base = -> Fillet094 [Edge33]
  BaseFeature = -> Fillet094
  Placement = pos=(-21.5005,18.625,0.235) rot=(0,-1,0;0.174533rad)
  Radius = 0.5
  SupportTransform = false
FEATURE [PartDesign::AdditiveBox] Box322
  AttacherType = Attacher::AttachEngine3D
  AttachmentOffset = pos=(-21.1,18.635,0.305) rot=(0,1,0;0.785398rad)
  BaseFeature = -> Fillet099
  Height = 0.375
  Length = 0.2
  MapMode = 5
  Placement = pos=(-21.1,18.635,0.305) rot=(0,1,0;0.785398rad)
  Support = -> [XY_Plane038]
  Width = 0.23
FEATURE [PartDesign::SubtractiveCylinder] Cylinder070
  Angle = 360
  AttacherType = Attacher::AttachEngine3D
  AttachmentOffset = pos=(-21.055,18.935,0.52) rot=(1,0,0;1.5708rad)
  BaseFeature = -> Box322
  Height = 0.375
  MapMode = 5
  Placement = pos=(-21.055,18.935,0.52) rot=(1,0,0;1.5708rad)
  Radius = 0.205
  Support = -> [XY_Plane038]
FEATURE [PartDesign::SubtractiveBox] Box319
  AttacherType = Attacher::AttachEngine3D
  AttachmentOffset = pos=(-20.95,18.635,0.53) rot=(0,0,1;0rad)
  BaseFeature = -> Cylinder070
  Height = 0.5
  Length = 0.1
  MapMode = 5
  Placement = pos=(-20.95,18.635,0.53) rot=(0,0,1;0rad)
  Support = -> [XY_Plane038]
  Width = 0.23
FEATURE [PartDesign::SubtractiveBox] Box311
  AttacherType = Attacher::AttachEngine3D
  AttachmentOffset = pos=(-21.15,18.635,0.297) rot=(0,-1,0;0.174533rad)
  BaseFeature = -> Box319
  Height = 0.115
  Length = 0.115
  MapMode = 5
  Placement = pos=(-21.15,18.635,0.297) rot=(0,-1,0;0.174533rad)
  Support = -> [XY_Plane038]
  Width = 0.23
FEATURE [PartDesign::Fillet] Fillet089
  Base = -> Box311 [Edge28]
  BaseFeature = -> Box311
  Placement = pos=(-21.15,18.635,0.297) rot=(0,-1,0;0.174533rad)
  Radius = 0.375
  SupportTransform = false
FEATURE [PartDesign::AdditiveBox] Box314
  AttacherType = Attacher::AttachEngine3D
  AttachmentOffset = pos=(-20.7,18.635,1.55) rot=(0,1,0;0.785398rad)
  BaseFeature = -> Fillet089
  Height = 0.375
  Length = 0.23
  MapMode = 5
  Placement = pos=(-20.7,18.635,1.55) rot=(0,1,0;0.785398rad)
  Support = -> [XY_Plane038]
  Width = 0.23
FEATURE [PartDesign::SubtractiveCylinder] Cylinder069
  Angle = 360
  AttacherType = Attacher::AttachEngine3D
  AttachmentOffset = pos=(-20.271,18.635,1.4056) rot=(-1,0,0;1.5708rad)
  BaseFeature = -> Box314
  Height = 0.23
  MapMode = 5
  Placement = pos=(-20.271,18.635,1.4056) rot=(-1,0,0;1.5708rad)
  Radius = 0.23
  Support = -> [XY_Plane038]
FEATURE [PartDesign::AdditiveBox] Box247
  AttacherType = Attacher::AttachEngine3D
  AttachmentOffset = pos=(-20.1,18.635,1.635) rot=(0,0,1;0rad)
  BaseFeature = -> Cylinder069
  Height = 0.265
  Length = 0.23
  MapMode = 5
  Placement = pos=(-20.1,18.635,1.635) rot=(0,0,1;0rad)
  Support = -> [XY_Plane038]
  Width = 0.23
FEATURE [PartDesign::Body] Body035  label="pin035"
  Group = -> [Box249,Box252,Box315,Box253,Box242,Fillet094,Fillet099,Box322,Cylinder070,Box319,Box311,Fillet089,Box314,Cylinder069,Box247]
  Origin = -> Origin038
  Placement = pos=(0,-3.5,0) rot=(0,0,1;0rad)
  Tip = -> Box247
FEATURE [PartDesign::Fillet] Fillet101
  Base = -> Fillet097 [Edge33]
  BaseFeature = -> Fillet097
  Placement = pos=(-21.5005,18.625,0.235) rot=(0,-1,0;0.174533rad)
  Radius = 0.5
  SupportTransform = false
FEATURE [PartDesign::AdditiveBox] Box321
  AttacherType = Attacher::AttachEngine3D
  AttachmentOffset = pos=(-21.1,18.635,0.305) rot=(0,1,0;0.785398rad)
  BaseFeature = -> Fillet101
  Height = 0.375
  Length = 0.2
  MapMode = 5
  Placement = pos=(-21.1,18.635,0.305) rot=(0,1,0;0.785398rad)
  Support = -> [XY_Plane033]
  Width = 0.23
FEATURE [PartDesign::SubtractiveCylinder] Cylinder052
  Angle = 360
  AttacherType = Attacher::AttachEngine3D
  AttachmentOffset = pos=(-21.055,18.935,0.52) rot=(1,0,0;1.5708rad)
  BaseFeature = -> Box321
  Height = 0.375
  MapMode = 5
  Placement = pos=(-21.055,18.935,0.52) rot=(1,0,0;1.5708rad)
  Radius = 0.205
  Support = -> [XY_Plane033]
FEATURE [PartDesign::SubtractiveBox] Box255
  AttacherType = Attacher::AttachEngine3D
  AttachmentOffset = pos=(-20.95,18.635,0.53) rot=(0,0,1;0rad)
  BaseFeature = -> Cylinder052
  Height = 0.5
  Length = 0.1
  MapMode = 5
  Placement = pos=(-20.95,18.635,0.53) rot=(0,0,1;0rad)
  Support = -> [XY_Plane033]
  Width = 0.23
FEATURE [PartDesign::SubtractiveBox] Box251
  AttacherType = Attacher::AttachEngine3D
  AttachmentOffset = pos=(-21.15,18.635,0.297) rot=(0,-1,0;0.174533rad)
  BaseFeature = -> Box255
  Height = 0.115
  Length = 0.115
  MapMode = 5
  Placement = pos=(-21.15,18.635,0.297) rot=(0,-1,0;0.174533rad)
  Support = -> [XY_Plane033]
  Width = 0.23
FEATURE [PartDesign::Fillet] Fillet102
  Base = -> Box317 [Edge2]
  BaseFeature = -> Box317
  Placement = pos=(-21.5005,18.625,0.235) rot=(0,-1,0;0.174533rad)
  Radius = 0.05
  SupportTransform = false
FEATURE [PartDesign::Fillet] Fillet095
  Base = -> Fillet102 [Edge33]
  BaseFeature = -> Fillet102
  Placement = pos=(-21.5005,18.625,0.235) rot=(0,-1,0;0.174533rad)
  Radius = 0.5
  SupportTransform = false
FEATURE [PartDesign::AdditiveBox] Box274
  AttacherType = Attacher::AttachEngine3D
  AttachmentOffset = pos=(-21.1,18.635,0.305) rot=(0,1,0;0.785398rad)
  BaseFeature = -> Fillet095
  Height = 0.375
  Length = 0.2
  MapMode = 5
  Placement = pos=(-21.1,18.635,0.305) rot=(0,1,0;0.785398rad)
  Support = -> [XY_Plane037]
  Width = 0.23
FEATURE [PartDesign::SubtractiveCylinder] Cylinder058
  Angle = 360
  AttacherType = Attacher::AttachEngine3D
  AttachmentOffset = pos=(-21.055,18.935,0.52) rot=(1,0,0;1.5708rad)
  BaseFeature = -> Box274
  Height = 0.375
  MapMode = 5
  Placement = pos=(-21.055,18.935,0.52) rot=(1,0,0;1.5708rad)
  Radius = 0.205
  Support = -> [XY_Plane037]
FEATURE [PartDesign::SubtractiveBox] Box271
  AttacherType = Attacher::AttachEngine3D
  AttachmentOffset = pos=(-20.95,18.635,0.53) rot=(0,0,1;0rad)
  BaseFeature = -> Cylinder058
  Height = 0.5
  Length = 0.1
  MapMode = 5
  Placement = pos=(-20.95,18.635,0.53) rot=(0,0,1;0rad)
  Support = -> [XY_Plane037]
  Width = 0.23
FEATURE [PartDesign::SubtractiveBox] Box282
  AttacherType = Attacher::AttachEngine3D
  AttachmentOffset = pos=(-21.15,18.635,0.297) rot=(0,-1,0;0.174533rad)
  BaseFeature = -> Box271
  Height = 0.115
  Length = 0.115
  MapMode = 5
  Placement = pos=(-21.15,18.635,0.297) rot=(0,-1,0;0.174533rad)
  Support = -> [XY_Plane037]
  Width = 0.23
FEATURE [PartDesign::Fillet] Fillet103
  Base = -> Box254 [Edge2]
  BaseFeature = -> Box254
  Placement = pos=(-21.5005,18.625,0.235) rot=(0,-1,0;0.174533rad)
  Radius = 0.05
  SupportTransform = false
FEATURE [PartDesign::Fillet] Fillet096
  Base = -> Fillet103 [Edge33]
  BaseFeature = -> Fillet103
  Placement = pos=(-21.5005,18.625,0.235) rot=(0,-1,0;0.174533rad)
  Radius = 0.5
  SupportTransform = false
FEATURE [PartDesign::AdditiveBox] Box286
  AttacherType = Attacher::AttachEngine3D
  AttachmentOffset = pos=(-21.1,18.635,0.305) rot=(0,1,0;0.785398rad)
  BaseFeature = -> Fillet096
  Height = 0.375
  Length = 0.2
  MapMode = 5
  Placement = pos=(-21.1,18.635,0.305) rot=(0,1,0;0.785398rad)
  Support = -> [XY_Plane036]
  Width = 0.23
FEATURE [PartDesign::SubtractiveCylinder] Cylinder065
  Angle = 360
  AttacherType = Attacher::AttachEngine3D
  AttachmentOffset = pos=(-21.055,18.935,0.52) rot=(1,0,0;1.5708rad)
  BaseFeature = -> Box286
  Height = 0.375
  MapMode = 5
  Placement = pos=(-21.055,18.935,0.52) rot=(1,0,0;1.5708rad)
  Radius = 0.205
  Support = -> [XY_Plane036]
FEATURE [PartDesign::SubtractiveBox] Box297
  AttacherType = Attacher::AttachEngine3D
  AttachmentOffset = pos=(-20.95,18.635,0.53) rot=(0,0,1;0rad)
  BaseFeature = -> Cylinder065
  Height = 0.5
  Length = 0.1
  MapMode = 5
  Placement = pos=(-20.95,18.635,0.53) rot=(0,0,1;0rad)
  Support = -> [XY_Plane036]
  Width = 0.23
FEATURE [PartDesign::SubtractiveBox] Box309
  AttacherType = Attacher::AttachEngine3D
  AttachmentOffset = pos=(-21.15,18.635,0.297) rot=(0,-1,0;0.174533rad)
  BaseFeature = -> Box297
  Height = 0.115
  Length = 0.115
  MapMode = 5
  Placement = pos=(-21.15,18.635,0.297) rot=(0,-1,0;0.174533rad)
  Support = -> [XY_Plane036]
  Width = 0.23
FEATURE [PartDesign::Fillet] Fillet100
  Base = -> Box309 [Edge28]
  BaseFeature = -> Box309
  Placement = pos=(-21.15,18.635,0.297) rot=(0,-1,0;0.174533rad)
  Radius = 0.375
  SupportTransform = false
FEATURE [PartDesign::AdditiveBox] Box313
  AttacherType = Attacher::AttachEngine3D
  AttachmentOffset = pos=(-20.7,18.635,1.55) rot=(0,1,0;0.785398rad)
  BaseFeature = -> Fillet100
  Height = 0.375
  Length = 0.23
  MapMode = 5
  Placement = pos=(-20.7,18.635,1.55) rot=(0,1,0;0.785398rad)
  Support = -> [XY_Plane036]
  Width = 0.23
FEATURE [PartDesign::SubtractiveCylinder] Cylinder066
  Angle = 360
  AttacherType = Attacher::AttachEngine3D
  AttachmentOffset = pos=(-20.271,18.635,1.4056) rot=(-1,0,0;1.5708rad)
  BaseFeature = -> Box313
  Height = 0.23
  MapMode = 5
  Placement = pos=(-20.271,18.635,1.4056) rot=(-1,0,0;1.5708rad)
  Radius = 0.23
  Support = -> [XY_Plane036]
FEATURE [PartDesign::AdditiveBox] Box324
  AttacherType = Attacher::AttachEngine3D
  AttachmentOffset = pos=(-20.1,18.635,1.635) rot=(0,0,1;0rad)
  BaseFeature = -> Cylinder066
  Height = 0.265
  Length = 0.23
  MapMode = 5
  Placement = pos=(-20.1,18.635,1.635) rot=(0,0,1;0rad)
  Support = -> [XY_Plane036]
  Width = 0.23
FEATURE [PartDesign::Body] Body034  label="pin034"
  Group = -> [Box244,Box256,Box310,Box316,Box254,Fillet103,Fillet096,Box286,Cylinder065,Box297,Box309,Fillet100,Box313,Cylinder066,Box324]
  Origin = -> Origin039
  Placement = pos=(0,-3,0) rot=(0,0,1;0rad)
  Tip = -> Box324
FEATURE [PartDesign::Fillet] Fillet104
  Base = -> Fillet098 [Edge33]
  BaseFeature = -> Fillet098
  Placement = pos=(-21.5005,18.625,0.235) rot=(0,-1,0;0.174533rad)
  Radius = 0.5
  SupportTransform = false
FEATURE [PartDesign::AdditiveBox] Box299
  AttacherType = Attacher::AttachEngine3D
  AttachmentOffset = pos=(-21.1,18.635,0.305) rot=(0,1,0;0.785398rad)
  BaseFeature = -> Fillet104
  Height = 0.375
  Length = 0.2
  MapMode = 5
  Placement = pos=(-21.1,18.635,0.305) rot=(0,1,0;0.785398rad)
  Support = -> [XY_Plane027]
  Width = 0.23
FEATURE [PartDesign::SubtractiveCylinder] Cylinder064
  Angle = 360
  AttacherType = Attacher::AttachEngine3D
  AttachmentOffset = pos=(-21.055,18.935,0.52) rot=(1,0,0;1.5708rad)
  BaseFeature = -> Box299
  Height = 0.375
  MapMode = 5
  Placement = pos=(-21.055,18.935,0.52) rot=(1,0,0;1.5708rad)
  Radius = 0.205
  Support = -> [XY_Plane027]
FEATURE [PartDesign::SubtractiveBox] Box304
  AttacherType = Attacher::AttachEngine3D
  AttachmentOffset = pos=(-20.95,18.635,0.53) rot=(0,0,1;0rad)
  BaseFeature = -> Cylinder064
  Height = 0.5
  Length = 0.1
  MapMode = 5
  Placement = pos=(-20.95,18.635,0.53) rot=(0,0,1;0rad)
  Support = -> [XY_Plane027]
  Width = 0.23
FEATURE [PartDesign::SubtractiveBox] Box306
  AttacherType = Attacher::AttachEngine3D
  AttachmentOffset = pos=(-21.15,18.635,0.297) rot=(0,-1,0;0.174533rad)
  BaseFeature = -> Box304
  Height = 0.115
  Length = 0.115
  MapMode = 5
  Placement = pos=(-21.15,18.635,0.297) rot=(0,-1,0;0.174533rad)
  Support = -> [XY_Plane027]
  Width = 0.23
FEATURE [PartDesign::Fillet] Fillet075
  Base = -> Box306 [Edge28]
  BaseFeature = -> Box306
  Placement = pos=(-21.15,18.635,0.297) rot=(0,-1,0;0.174533rad)
  Radius = 0.375
  SupportTransform = false
FEATURE [PartDesign::AdditiveBox] Box305
  AttacherType = Attacher::AttachEngine3D
  AttachmentOffset = pos=(-20.7,18.635,1.55) rot=(0,1,0;0.785398rad)
  BaseFeature = -> Fillet075
  Height = 0.375
  Length = 0.23
  MapMode = 5
  Placement = pos=(-20.7,18.635,1.55) rot=(0,1,0;0.785398rad)
  Support = -> [XY_Plane027]
  Width = 0.23
FEATURE [PartDesign::SubtractiveCylinder] Cylinder061
  Angle = 360
  AttacherType = Attacher::AttachEngine3D
  AttachmentOffset = pos=(-20.271,18.635,1.4056) rot=(-1,0,0;1.5708rad)
  BaseFeature = -> Box305
  Height = 0.23
  MapMode = 5
  Placement = pos=(-20.271,18.635,1.4056) rot=(-1,0,0;1.5708rad)
  Radius = 0.23
  Support = -> [XY_Plane027]
FEATURE [PartDesign::AdditiveBox] Box295
  AttacherType = Attacher::AttachEngine3D
  AttachmentOffset = pos=(-20.1,18.635,1.635) rot=(0,0,1;0rad)
  BaseFeature = -> Cylinder061
  Height = 0.265
  Length = 0.23
  MapMode = 5
  Placement = pos=(-20.1,18.635,1.635) rot=(0,0,1;0rad)
  Support = -> [XY_Plane027]
  Width = 0.23
FEATURE [PartDesign::Body] Body036  label="pin036"
  Group = -> [Box312,Box307,Box278,Box288,Box289,Fillet098,Fillet104,Box299,Cylinder064,Box304,Box306,Fillet075,Box305,Cylinder061,Box295]
  Origin = -> Origin035
  Placement = pos=(0,-5.5,0) rot=(0,0,1;0rad)
  Tip = -> Box295
FEATURE [PartDesign::Fillet] Fillet105
  Base = -> Box251 [Edge28]
  BaseFeature = -> Box251
  Placement = pos=(-21.15,18.635,0.297) rot=(0,-1,0;0.174533rad)
  Radius = 0.375
  SupportTransform = false
FEATURE [PartDesign::AdditiveBox] Box250
  AttacherType = Attacher::AttachEngine3D
  AttachmentOffset = pos=(-20.7,18.635,1.55) rot=(0,1,0;0.785398rad)
  BaseFeature = -> Fillet105
  Height = 0.375
  Length = 0.23
  MapMode = 5
  Placement = pos=(-20.7,18.635,1.55) rot=(0,1,0;0.785398rad)
  Support = -> [XY_Plane033]
  Width = 0.23
FEATURE [PartDesign::SubtractiveCylinder] Cylinder053
  Angle = 360
  AttacherType = Attacher::AttachEngine3D
  AttachmentOffset = pos=(-20.271,18.635,1.4056) rot=(-1,0,0;1.5708rad)
  BaseFeature = -> Box250
  Height = 0.23
  MapMode = 5
  Placement = pos=(-20.271,18.635,1.4056) rot=(-1,0,0;1.5708rad)
  Radius = 0.23
  Support = -> [XY_Plane033]
FEATURE [PartDesign::AdditiveBox] Box241
  AttacherType = Attacher::AttachEngine3D
  AttachmentOffset = pos=(-20.1,18.635,1.635) rot=(0,0,1;0rad)
  BaseFeature = -> Cylinder053
  Height = 0.265
  Length = 0.23
  MapMode = 5
  Placement = pos=(-20.1,18.635,1.635) rot=(0,0,1;0rad)
  Support = -> [XY_Plane033]
  Width = 0.23
FEATURE [PartDesign::Body] Body031  label="pin031"
  Group = -> [Box243,Box248,Box298,Box246,Box245,Fillet097,Fillet101,Box321,Cylinder052,Box255,Box251,Fillet105,Box250,Cylinder053,Box241]
  Origin = -> Origin034
  Placement = pos=(0,-4,0) rot=(0,0,1;0rad)
  Tip = -> Box241
FEATURE [PartDesign::Fillet] Fillet106
  Base = -> Box282 [Edge28]
  BaseFeature = -> Box282
  Placement = pos=(-21.15,18.635,0.297) rot=(0,-1,0;0.174533rad)
  Radius = 0.375
  SupportTransform = false
FEATURE [PartDesign::AdditiveBox] Box277
  AttacherType = Attacher::AttachEngine3D
  AttachmentOffset = pos=(-20.7,18.635,1.55) rot=(0,1,0;0.785398rad)
  BaseFeature = -> Fillet106
  Height = 0.375
  Length = 0.23
  MapMode = 5
  Placement = pos=(-20.7,18.635,1.55) rot=(0,1,0;0.785398rad)
  Support = -> [XY_Plane037]
  Width = 0.23
FEATURE [PartDesign::SubtractiveCylinder] Cylinder059
  Angle = 360
  AttacherType = Attacher::AttachEngine3D
  AttachmentOffset = pos=(-20.271,18.635,1.4056) rot=(-1,0,0;1.5708rad)
  BaseFeature = -> Box277
  Height = 0.23
  MapMode = 5
  Placement = pos=(-20.271,18.635,1.4056) rot=(-1,0,0;1.5708rad)
  Radius = 0.23
  Support = -> [XY_Plane037]
FEATURE [PartDesign::AdditiveBox] Box281
  AttacherType = Attacher::AttachEngine3D
  AttachmentOffset = pos=(-20.1,18.635,1.635) rot=(0,0,1;0rad)
  BaseFeature = -> Cylinder059
  Height = 0.265
  Length = 0.23
  MapMode = 5
  Placement = pos=(-20.1,18.635,1.635) rot=(0,0,1;0rad)
  Support = -> [XY_Plane037]
  Width = 0.23
FEATURE [PartDesign::Body] Body032  label="pin032"
  Group = -> [Box308,Box296,Box284,Box275,Box317,Fillet102,Fillet095,Box274,Cylinder058,Box271,Box282,Fillet106,Box277,Cylinder059,Box281]
  Origin = -> Origin028
  Placement = pos=(0,-4.5,0) rot=(0,0,1;0rad)
  Tip = -> Box281
FEATURE [PartDesign::Fillet] Fillet107
  Base = -> Box291 [Edge28]
  BaseFeature = -> Box291
  Placement = pos=(-21.15,18.635,0.297) rot=(0,-1,0;0.174533rad)
  Radius = 0.375
  SupportTransform = false
FEATURE [PartDesign::AdditiveBox] Box318
  AttacherType = Attacher::AttachEngine3D
  AttachmentOffset = pos=(-20.7,18.635,1.55) rot=(0,1,0;0.785398rad)
  BaseFeature = -> Fillet107
  Height = 0.375
  Length = 0.23
  MapMode = 5
  Placement = pos=(-20.7,18.635,1.55) rot=(0,1,0;0.785398rad)
  Support = -> [XY_Plane032]
  Width = 0.23
FEATURE [PartDesign::SubtractiveCylinder] Cylinder067
  Angle = 360
  AttacherType = Attacher::AttachEngine3D
  AttachmentOffset = pos=(-20.271,18.635,1.4056) rot=(-1,0,0;1.5708rad)
  BaseFeature = -> Box318
  Height = 0.23
  MapMode = 5
  Placement = pos=(-20.271,18.635,1.4056) rot=(-1,0,0;1.5708rad)
  Radius = 0.23
  Support = -> [XY_Plane032]
FEATURE [PartDesign::AdditiveBox] Box332
  AttacherType = Attacher::AttachEngine3D
  AttachmentOffset = pos=(-20.1,18.635,1.635) rot=(0,0,1;0rad)
  BaseFeature = -> Cylinder067
  Height = 0.265
  Length = 0.23
  MapMode = 5
  Placement = pos=(-20.1,18.635,1.635) rot=(0,0,1;0rad)
  Support = -> [XY_Plane032]
  Width = 0.23
FEATURE [PartDesign::Body] Body028  label="pin028"
  Group = -> [Box345,Box348,Box328,Box323,Box344,Fillet087,Fillet072,Box257,Cylinder063,Box303,Box291,Fillet107,Box318,Cylinder067,Box332]
  Origin = -> Origin027
  Tip = -> Box332
FEATURE [PartDesign::SubtractiveBox] Box351
  AttacherType = Attacher::AttachEngine3D
  AttachmentOffset = pos=(-20.5,18.63,0) rot=(0,0,1;0rad)
  BaseFeature = -> Box261
  Height = 1.635
  Length = 0.5
  MapMode = 5
  Placement = pos=(-20.5,18.63,0) rot=(0,0,1;0rad)
  Support = -> [XY_Plane031]
  Width = 0.25
FEATURE [PartDesign::SubtractiveBox] Box263
  AttacherType = Attacher::AttachEngine3D
  AttachmentOffset = pos=(-21.19,18.635,-0.12) rot=(0,-1,0;0.15708rad)
  BaseFeature = -> Box351
  Height = 0.12
  Length = 0.725
  MapMode = 5
  Placement = pos=(-21.19,18.635,-0.12) rot=(0,-1,0;0.15708rad)
  Support = -> [XY_Plane031]
  Width = 0.25
FEATURE [PartDesign::SubtractiveBox] Box264
  AttacherType = Attacher::AttachEngine3D
  AttachmentOffset = pos=(-21.5005,18.625,0.235) rot=(0,-1,0;0.174533rad)
  BaseFeature = -> Box263
  Height = 0.3
  Length = 0.6605
  MapMode = 5
  Placement = pos=(-21.5005,18.625,0.235) rot=(0,-1,0;0.174533rad)
  Support = -> [XY_Plane031]
  Width = 0.25
FEATURE [PartDesign::Fillet] Fillet081
  Base = -> Box264 [Edge2]
  BaseFeature = -> Box264
  Placement = pos=(-21.5005,18.625,0.235) rot=(0,-1,0;0.174533rad)
  Radius = 0.05
  SupportTransform = false
FEATURE [PartDesign::Fillet] Fillet082
  Base = -> Fillet081 [Edge33]
  BaseFeature = -> Fillet081
  Placement = pos=(-21.5005,18.625,0.235) rot=(0,-1,0;0.174533rad)
  Radius = 0.5
  SupportTransform = false
FEATURE [PartDesign::SubtractiveBox] Box354
  AttacherType = Attacher::AttachEngine3D
  AttachmentOffset = pos=(-20.5,18.63,0) rot=(0,0,1;0rad)
  BaseFeature = -> Box270
  Height = 1.635
  Length = 0.5
  MapMode = 5
  Placement = pos=(-20.5,18.63,0) rot=(0,0,1;0rad)
  Support = -> [XY_Plane029]
  Width = 0.25
FEATURE [PartDesign::SubtractiveBox] Box259
  AttacherType = Attacher::AttachEngine3D
  AttachmentOffset = pos=(-21.19,18.635,-0.12) rot=(0,-1,0;0.15708rad)
  BaseFeature = -> Box354
  Height = 0.12
  Length = 0.725
  MapMode = 5
  Placement = pos=(-21.19,18.635,-0.12) rot=(0,-1,0;0.15708rad)
  Support = -> [XY_Plane029]
  Width = 0.25
FEATURE [PartDesign::SubtractiveBox] Box272
  AttacherType = Attacher::AttachEngine3D
  AttachmentOffset = pos=(-21.5005,18.625,0.235) rot=(0,-1,0;0.174533rad)
  BaseFeature = -> Box259
  Height = 0.3
  Length = 0.6605
  MapMode = 5
  Placement = pos=(-21.5005,18.625,0.235) rot=(0,-1,0;0.174533rad)
  Support = -> [XY_Plane029]
  Width = 0.25
FEATURE [PartDesign::Fillet] Fillet083
  Base = -> Box272 [Edge2]
  BaseFeature = -> Box272
  Placement = pos=(-21.5005,18.625,0.235) rot=(0,-1,0;0.174533rad)
  Radius = 0.05
  SupportTransform = false
FEATURE [PartDesign::Fillet] Fillet084
  Base = -> Fillet083 [Edge33]
  BaseFeature = -> Fillet083
  Placement = pos=(-21.5005,18.625,0.235) rot=(0,-1,0;0.174533rad)
  Radius = 0.5
  SupportTransform = false
FEATURE [PartDesign::AdditiveBox] Box349
  AttacherType = Attacher::AttachEngine3D
  AttachmentOffset = pos=(-21.1,18.635,0.305) rot=(0,1,0;0.785398rad)
  BaseFeature = -> Fillet084
  Height = 0.375
  Length = 0.2
  MapMode = 5
  Placement = pos=(-21.1,18.635,0.305) rot=(0,1,0;0.785398rad)
  Support = -> [XY_Plane029]
  Width = 0.23
FEATURE [PartDesign::SubtractiveCylinder] Cylinder056
  Angle = 360
  AttacherType = Attacher::AttachEngine3D
  AttachmentOffset = pos=(-21.055,18.935,0.52) rot=(1,0,0;1.5708rad)
  BaseFeature = -> Box349
  Height = 0.375
  MapMode = 5
  Placement = pos=(-21.055,18.935,0.52) rot=(1,0,0;1.5708rad)
  Radius = 0.205
  Support = -> [XY_Plane029]
FEATURE [PartDesign::SubtractiveBox] Box262
  AttacherType = Attacher::AttachEngine3D
  AttachmentOffset = pos=(-20.95,18.635,0.53) rot=(0,0,1;0rad)
  BaseFeature = -> Cylinder056
  Height = 0.5
  Length = 0.1
  MapMode = 5
  Placement = pos=(-20.95,18.635,0.53) rot=(0,0,1;0rad)
  Support = -> [XY_Plane029]
  Width = 0.23
FEATURE [PartDesign::SubtractiveBox] Box269
  AttacherType = Attacher::AttachEngine3D
  AttachmentOffset = pos=(-21.15,18.635,0.297) rot=(0,-1,0;0.174533rad)
  BaseFeature = -> Box262
  Height = 0.115
  Length = 0.115
  MapMode = 5
  Placement = pos=(-21.15,18.635,0.297) rot=(0,-1,0;0.174533rad)
  Support = -> [XY_Plane029]
  Width = 0.23
FEATURE [PartDesign::Fillet] Fillet073
  Base = -> Box269 [Edge28]
  BaseFeature = -> Box269
  Placement = pos=(-21.15,18.635,0.297) rot=(0,-1,0;0.174533rad)
  Radius = 0.375
  SupportTransform = false
FEATURE [PartDesign::AdditiveBox] Box268
  AttacherType = Attacher::AttachEngine3D
  AttachmentOffset = pos=(-20.7,18.635,1.55) rot=(0,1,0;0.785398rad)
  BaseFeature = -> Fillet073
  Height = 0.375
  Length = 0.23
  MapMode = 5
  Placement = pos=(-20.7,18.635,1.55) rot=(0,1,0;0.785398rad)
  Support = -> [XY_Plane029]
  Width = 0.23
FEATURE [PartDesign::SubtractiveCylinder] Cylinder055
  Angle = 360
  AttacherType = Attacher::AttachEngine3D
  AttachmentOffset = pos=(-20.271,18.635,1.4056) rot=(-1,0,0;1.5708rad)
  BaseFeature = -> Box268
  Height = 0.23
  MapMode = 5
  Placement = pos=(-20.271,18.635,1.4056) rot=(-1,0,0;1.5708rad)
  Radius = 0.23
  Support = -> [XY_Plane029]
FEATURE [PartDesign::AdditiveBox] Box260
  AttacherType = Attacher::AttachEngine3D
  AttachmentOffset = pos=(-20.1,18.635,1.635) rot=(0,0,1;0rad)
  BaseFeature = -> Cylinder055
  Height = 0.265
  Length = 0.23
  MapMode = 5
  Placement = pos=(-20.1,18.635,1.635) rot=(0,0,1;0rad)
  Support = -> [XY_Plane029]
  Width = 0.23
FEATURE [PartDesign::Body] Body029  label="pin029"
  Group = -> [Box279,Box270,Box354,Box259,Box272,Fillet083,Fillet084,Box349,Cylinder056,Box262,Box269,Fillet073,Box268,Cylinder055,Box260]
  Origin = -> Origin036
  Placement = pos=(0,-2.5,0) rot=(0,0,1;0rad)
  Tip = -> Box260
FEATURE [PartDesign::AdditiveBox] Box356
  AttacherType = Attacher::AttachEngine3D
  AttachmentOffset = pos=(-21.1,18.635,0.305) rot=(0,1,0;0.785398rad)
  BaseFeature = -> Fillet082
  Height = 0.375
  Length = 0.2
  MapMode = 5
  Placement = pos=(-21.1,18.635,0.305) rot=(0,1,0;0.785398rad)
  Support = -> [XY_Plane031]
  Width = 0.23
FEATURE [PartDesign::SubtractiveCylinder] Cylinder075
  Angle = 360
  AttacherType = Attacher::AttachEngine3D
  AttachmentOffset = pos=(-21.055,18.935,0.52) rot=(1,0,0;1.5708rad)
  BaseFeature = -> Box356
  Height = 0.375
  MapMode = 5
  Placement = pos=(-21.055,18.935,0.52) rot=(1,0,0;1.5708rad)
  Radius = 0.205
  Support = -> [XY_Plane031]
FEATURE [PartDesign::SubtractiveBox] Box267
  AttacherType = Attacher::AttachEngine3D
  AttachmentOffset = pos=(-20.95,18.635,0.53) rot=(0,0,1;0rad)
  BaseFeature = -> Cylinder075
  Height = 0.5
  Length = 0.1
  MapMode = 5
  Placement = pos=(-20.95,18.635,0.53) rot=(0,0,1;0rad)
  Support = -> [XY_Plane031]
  Width = 0.23
FEATURE [PartDesign::SubtractiveBox] Box258
  AttacherType = Attacher::AttachEngine3D
  AttachmentOffset = pos=(-21.15,18.635,0.297) rot=(0,-1,0;0.174533rad)
  BaseFeature = -> Box267
  Height = 0.115
  Length = 0.115
  MapMode = 5
  Placement = pos=(-21.15,18.635,0.297) rot=(0,-1,0;0.174533rad)
  Support = -> [XY_Plane031]
  Width = 0.23
FEATURE [PartDesign::Fillet] Fillet076
  Base = -> Box258 [Edge28]
  BaseFeature = -> Box258
  Placement = pos=(-21.15,18.635,0.297) rot=(0,-1,0;0.174533rad)
  Radius = 0.375
  SupportTransform = false
FEATURE [PartDesign::AdditiveBox] Box350
  AttacherType = Attacher::AttachEngine3D
  AttachmentOffset = pos=(-20.7,18.635,1.55) rot=(0,1,0;0.785398rad)
  BaseFeature = -> Fillet076
  Height = 0.375
  Length = 0.23
  MapMode = 5
  Placement = pos=(-20.7,18.635,1.55) rot=(0,1,0;0.785398rad)
  Support = -> [XY_Plane031]
  Width = 0.23
FEATURE [PartDesign::SubtractiveCylinder] Cylinder057
  Angle = 360
  AttacherType = Attacher::AttachEngine3D
  AttachmentOffset = pos=(-20.271,18.635,1.4056) rot=(-1,0,0;1.5708rad)
  BaseFeature = -> Box350
  Height = 0.23
  MapMode = 5
  Placement = pos=(-20.271,18.635,1.4056) rot=(-1,0,0;1.5708rad)
  Radius = 0.23
  Support = -> [XY_Plane031]
FEATURE [PartDesign::AdditiveBox] Box266
  AttacherType = Attacher::AttachEngine3D
  AttachmentOffset = pos=(-20.1,18.635,1.635) rot=(0,0,1;0rad)
  BaseFeature = -> Cylinder057
  Height = 0.265
  Length = 0.23
  MapMode = 5
  Placement = pos=(-20.1,18.635,1.635) rot=(0,0,1;0rad)
  Support = -> [XY_Plane031]
  Width = 0.23
FEATURE [PartDesign::Body] Body025  label="pin025"
  Group = -> [Box265,Box261,Box351,Box263,Box264,Fillet081,Fillet082,Box356,Cylinder075,Box267,Box258,Fillet076,Box350,Cylinder057,Box266]
  Origin = -> Origin030
  Placement = pos=(0,-2,0) rot=(0,0,1;0rad)
  Tip = -> Box266
FEATURE [PartDesign::SubtractiveBox] Box360
  AttacherType = Attacher::AttachEngine3D
  AttachmentOffset = pos=(-20.5,18.63,0) rot=(0,0,1;0rad)
  BaseFeature = -> Box276
  Height = 1.635
  Length = 0.5
  MapMode = 5
  Placement = pos=(-20.5,18.63,0) rot=(0,0,1;0rad)
  Support = -> [XY_Plane028]
  Width = 0.25
FEATURE [PartDesign::SubtractiveBox] Box355
  AttacherType = Attacher::AttachEngine3D
  AttachmentOffset = pos=(-21.19,18.635,-0.12) rot=(0,-1,0;0.15708rad)
  BaseFeature = -> Box360
  Height = 0.12
  Length = 0.725
  MapMode = 5
  Placement = pos=(-21.19,18.635,-0.12) rot=(0,-1,0;0.15708rad)
  Support = -> [XY_Plane028]
  Width = 0.25
FEATURE [PartDesign::SubtractiveBox] Box273
  AttacherType = Attacher::AttachEngine3D
  AttachmentOffset = pos=(-21.5005,18.625,0.235) rot=(0,-1,0;0.174533rad)
  BaseFeature = -> Box355
  Height = 0.3
  Length = 0.6605
  MapMode = 5
  Placement = pos=(-21.5005,18.625,0.235) rot=(0,-1,0;0.174533rad)
  Support = -> [XY_Plane028]
  Width = 0.25
FEATURE [PartDesign::Fillet] Fillet090
  Base = -> Box273 [Edge2]
  BaseFeature = -> Box273
  Placement = pos=(-21.5005,18.625,0.235) rot=(0,-1,0;0.174533rad)
  Radius = 0.05
  SupportTransform = false
FEATURE [PartDesign::Fillet] Fillet080
  Base = -> Fillet090 [Edge33]
  BaseFeature = -> Fillet090
  Placement = pos=(-21.5005,18.625,0.235) rot=(0,-1,0;0.174533rad)
  Radius = 0.5
  SupportTransform = false
FEATURE [PartDesign::AdditiveBox] Box358
  AttacherType = Attacher::AttachEngine3D
  AttachmentOffset = pos=(-21.1,18.635,0.305) rot=(0,1,0;0.785398rad)
  BaseFeature = -> Fillet080
  Height = 0.375
  Length = 0.2
  MapMode = 5
  Placement = pos=(-21.1,18.635,0.305) rot=(0,1,0;0.785398rad)
  Support = -> [XY_Plane028]
  Width = 0.23
FEATURE [PartDesign::SubtractiveCylinder] Cylinder074
  Angle = 360
  AttacherType = Attacher::AttachEngine3D
  AttachmentOffset = pos=(-21.055,18.935,0.52) rot=(1,0,0;1.5708rad)
  BaseFeature = -> Box358
  Height = 0.375
  MapMode = 5
  Placement = pos=(-21.055,18.935,0.52) rot=(1,0,0;1.5708rad)
  Radius = 0.205
  Support = -> [XY_Plane028]
FEATURE [PartDesign::SubtractiveBox] Box353
  AttacherType = Attacher::AttachEngine3D
  AttachmentOffset = pos=(-20.95,18.635,0.53) rot=(0,0,1;0rad)
  BaseFeature = -> Cylinder074
  Height = 0.5
  Length = 0.1
  MapMode = 5
  Placement = pos=(-20.95,18.635,0.53) rot=(0,0,1;0rad)
  Support = -> [XY_Plane028]
  Width = 0.23
FEATURE [PartDesign::SubtractiveBox] Box352
  AttacherType = Attacher::AttachEngine3D
  AttachmentOffset = pos=(-21.15,18.635,0.297) rot=(0,-1,0;0.174533rad)
  BaseFeature = -> Box353
  Height = 0.115
  Length = 0.115
  MapMode = 5
  Placement = pos=(-21.15,18.635,0.297) rot=(0,-1,0;0.174533rad)
  Support = -> [XY_Plane028]
  Width = 0.23
FEATURE [PartDesign::Fillet] Fillet088
  Base = -> Box352 [Edge28]
  BaseFeature = -> Box352
  Placement = pos=(-21.15,18.635,0.297) rot=(0,-1,0;0.174533rad)
  Radius = 0.375
  SupportTransform = false
FEATURE [PartDesign::AdditiveBox] Box357
  AttacherType = Attacher::AttachEngine3D
  AttachmentOffset = pos=(-20.7,18.635,1.55) rot=(0,1,0;0.785398rad)
  BaseFeature = -> Fillet088
  Height = 0.375
  Length = 0.23
  MapMode = 5
  Placement = pos=(-20.7,18.635,1.55) rot=(0,1,0;0.785398rad)
  Support = -> [XY_Plane028]
  Width = 0.23
FEATURE [PartDesign::SubtractiveCylinder] Cylinder054
  Angle = 360
  AttacherType = Attacher::AttachEngine3D
  AttachmentOffset = pos=(-20.271,18.635,1.4056) rot=(-1,0,0;1.5708rad)
  BaseFeature = -> Box357
  Height = 0.23
  MapMode = 5
  Placement = pos=(-20.271,18.635,1.4056) rot=(-1,0,0;1.5708rad)
  Radius = 0.23
  Support = -> [XY_Plane028]
FEATURE [PartDesign::AdditiveBox] Box359
  AttacherType = Attacher::AttachEngine3D
  AttachmentOffset = pos=(-20.1,18.635,1.635) rot=(0,0,1;0rad)
  BaseFeature = -> Cylinder054
  Height = 0.265
  Length = 0.23
  MapMode = 5
  Placement = pos=(-20.1,18.635,1.635) rot=(0,0,1;0rad)
  Support = -> [XY_Plane028]
  Width = 0.23
FEATURE [PartDesign::Body] Body027  label="pin027"
  Group = -> [Box285,Box276,Box360,Box355,Box273,Fillet090,Fillet080,Box358,Cylinder074,Box353,Box352,Fillet088,Box357,Cylinder054,Box359]
  Origin = -> Origin033
  Placement = pos=(0,-1.5,0) rot=(0,0,1;0rad)
  Tip = -> Box359
FEATURE [App::Part] Part002  label="Pin-set003"
  Group = -> [Body028,Body026,Body030,Body027,Body025,Body029,Body034,Body035,Body031,Body032,Body033,Body036]
  Origin = -> Origin037
  Placement = pos=(0,-12,0) rot=(0,0,1;0rad)
FEATURE [PartDesign::AdditiveBox] Box362
  AttacherType = Attacher::AttachEngine3D
  AttachmentOffset = pos=(-21.3,18.635,0) rot=(0,0,1;0rad)
  Height = 1.9
  Length = 1.3
  MapMode = 5
  Placement = pos=(-21.3,18.635,0) rot=(0,0,1;0rad)
  Support = -> [XY_Plane049]
  Width = 0.23
FEATURE [PartDesign::AdditiveBox] Box364
  AttacherType = Attacher::AttachEngine3D
  AttachmentOffset = pos=(-21.3,18.635,0) rot=(0,0,1;0rad)
  Height = 1.9
  Length = 1.3
  MapMode = 5
  Placement = pos=(-21.3,18.635,0) rot=(0,0,1;0rad)
  Support = -> [XY_Plane047]
  Width = 0.23
FEATURE [PartDesign::SubtractiveBox] Box366
  AttacherType = Attacher::AttachEngine3D
  AttachmentOffset = pos=(-21.35,18.635,0.35) rot=(0,0,1;0rad)
  BaseFeature = -> Box364
  Height = 1.55
  Length = 0.5
  MapMode = 5
  Placement = pos=(-21.35,18.635,0.35) rot=(0,0,1;0rad)
  Support = -> [XY_Plane047]
  Width = 0.23
FEATURE [PartDesign::AdditiveBox] Box369
  AttacherType = Attacher::AttachEngine3D
  AttachmentOffset = pos=(-21.3,18.635,0) rot=(0,0,1;0rad)
  Height = 1.9
  Length = 1.3
  MapMode = 5
  Placement = pos=(-21.3,18.635,0) rot=(0,0,1;0rad)
  Support = -> [XY_Plane052]
  Width = 0.23
FEATURE [PartDesign::SubtractiveBox] Box372
  AttacherType = Attacher::AttachEngine3D
  AttachmentOffset = pos=(-21.35,18.635,0.35) rot=(0,0,1;0rad)
  BaseFeature = -> Box362
  Height = 1.55
  Length = 0.5
  MapMode = 5
  Placement = pos=(-21.35,18.635,0.35) rot=(0,0,1;0rad)
  Support = -> [XY_Plane049]
  Width = 0.23
FEATURE [PartDesign::SubtractiveBox] Box377
  AttacherType = Attacher::AttachEngine3D
  AttachmentOffset = pos=(-21.35,18.635,0.35) rot=(0,0,1;0rad)
  BaseFeature = -> Box369
  Height = 1.55
  Length = 0.5
  MapMode = 5
  Placement = pos=(-21.35,18.635,0.35) rot=(0,0,1;0rad)
  Support = -> [XY_Plane052]
  Width = 0.23
FEATURE [PartDesign::AdditiveBox] Box380
  AttacherType = Attacher::AttachEngine3D
  AttachmentOffset = pos=(-21.3,18.635,0) rot=(0,0,1;0rad)
  Height = 1.9
  Length = 1.3
  MapMode = 5
  Placement = pos=(-21.3,18.635,0) rot=(0,0,1;0rad)
  Support = -> [XY_Plane045]
  Width = 0.23
FEATURE [PartDesign::SubtractiveBox] Box391
  AttacherType = Attacher::AttachEngine3D
  AttachmentOffset = pos=(-21.35,18.635,0.35) rot=(0,0,1;0rad)
  BaseFeature = -> Box380
  Height = 1.55
  Length = 0.5
  MapMode = 5
  Placement = pos=(-21.35,18.635,0.35) rot=(0,0,1;0rad)
  Support = -> [XY_Plane045]
  Width = 0.23
FEATURE [PartDesign::AdditiveBox] Box402
  AttacherType = Attacher::AttachEngine3D
  AttachmentOffset = pos=(-21.3,18.635,0) rot=(0,0,1;0rad)
  Height = 1.9
  Length = 1.3
  MapMode = 5
  Placement = pos=(-21.3,18.635,0) rot=(0,0,1;0rad)
  Support = -> [XY_Plane042]
  Width = 0.23
FEATURE [PartDesign::SubtractiveBox] Box396
  AttacherType = Attacher::AttachEngine3D
  AttachmentOffset = pos=(-21.35,18.635,0.35) rot=(0,0,1;0rad)
  BaseFeature = -> Box402
  Height = 1.55
  Length = 0.5
  MapMode = 5
  Placement = pos=(-21.35,18.635,0.35) rot=(0,0,1;0rad)
  Support = -> [XY_Plane042]
  Width = 0.23
FEATURE [PartDesign::AdditiveBox] Box404
  AttacherType = Attacher::AttachEngine3D
  AttachmentOffset = pos=(-21.3,18.635,0) rot=(0,0,1;0rad)
  Height = 1.9
  Length = 1.3
  MapMode = 5
  Placement = pos=(-21.3,18.635,0) rot=(0,0,1;0rad)
  Support = -> [XY_Plane041]
  Width = 0.23
FEATURE [PartDesign::SubtractiveBox] Box382
  AttacherType = Attacher::AttachEngine3D
  AttachmentOffset = pos=(-21.35,18.635,0.35) rot=(0,0,1;0rad)
  BaseFeature = -> Box404
  Height = 1.55
  Length = 0.5
  MapMode = 5
  Placement = pos=(-21.35,18.635,0.35) rot=(0,0,1;0rad)
  Support = -> [XY_Plane041]
  Width = 0.23
FEATURE [PartDesign::AdditiveBox] Box410
  AttacherType = Attacher::AttachEngine3D
  AttachmentOffset = pos=(-21.3,18.635,0) rot=(0,0,1;0rad)
  Height = 1.9
  Length = 1.3
  MapMode = 5
  Placement = pos=(-21.3,18.635,0) rot=(0,0,1;0rad)
  Support = -> [XY_Plane048]
  Width = 0.23
FEATURE [PartDesign::SubtractiveBox] Box415
  AttacherType = Attacher::AttachEngine3D
  AttachmentOffset = pos=(-20.5,18.63,0) rot=(0,0,1;0rad)
  BaseFeature = -> Box366
  Height = 1.635
  Length = 0.5
  MapMode = 5
  Placement = pos=(-20.5,18.63,0) rot=(0,0,1;0rad)
  Support = -> [XY_Plane047]
  Width = 0.25
FEATURE [PartDesign::SubtractiveBox] Box375
  AttacherType = Attacher::AttachEngine3D
  AttachmentOffset = pos=(-21.19,18.635,-0.12) rot=(0,-1,0;0.15708rad)
  BaseFeature = -> Box415
  Height = 0.12
  Length = 0.725
  MapMode = 5
  Placement = pos=(-21.19,18.635,-0.12) rot=(0,-1,0;0.15708rad)
  Support = -> [XY_Plane047]
  Width = 0.25
FEATURE [PartDesign::SubtractiveBox] Box376
  AttacherType = Attacher::AttachEngine3D
  AttachmentOffset = pos=(-21.5005,18.625,0.235) rot=(0,-1,0;0.174533rad)
  BaseFeature = -> Box375
  Height = 0.3
  Length = 0.6605
  MapMode = 5
  Placement = pos=(-21.5005,18.625,0.235) rot=(0,-1,0;0.174533rad)
  Support = -> [XY_Plane047]
  Width = 0.25
FEATURE [PartDesign::Fillet] Fillet135
  Base = -> Box376 [Edge2]
  BaseFeature = -> Box376
  Placement = pos=(-21.5005,18.625,0.235) rot=(0,-1,0;0.174533rad)
  Radius = 0.05
  SupportTransform = false
FEATURE [PartDesign::Fillet] Fillet140
  Base = -> Fillet135 [Edge33]
  BaseFeature = -> Fillet135
  Placement = pos=(-21.5005,18.625,0.235) rot=(0,-1,0;0.174533rad)
  Radius = 0.5
  SupportTransform = false
FEATURE [PartDesign::SubtractiveBox] Box416
  AttacherType = Attacher::AttachEngine3D
  AttachmentOffset = pos=(-21.35,18.635,0.35) rot=(0,0,1;0rad)
  BaseFeature = -> Box410
  Height = 1.55
  Length = 0.5
  MapMode = 5
  Placement = pos=(-21.35,18.635,0.35) rot=(0,0,1;0rad)
  Support = -> [XY_Plane048]
  Width = 0.23
FEATURE [PartDesign::SubtractiveBox] Box405
  AttacherType = Attacher::AttachEngine3D
  AttachmentOffset = pos=(-20.5,18.63,0) rot=(0,0,1;0rad)
  BaseFeature = -> Box416
  Height = 1.635
  Length = 0.5
  MapMode = 5
  Placement = pos=(-20.5,18.63,0) rot=(0,0,1;0rad)
  Support = -> [XY_Plane048]
  Width = 0.25
FEATURE [PartDesign::SubtractiveBox] Box413
  AttacherType = Attacher::AttachEngine3D
  AttachmentOffset = pos=(-21.19,18.635,-0.12) rot=(0,-1,0;0.15708rad)
  BaseFeature = -> Box405
  Height = 0.12
  Length = 0.725
  MapMode = 5
  Placement = pos=(-21.19,18.635,-0.12) rot=(0,-1,0;0.15708rad)
  Support = -> [XY_Plane048]
  Width = 0.25
FEATURE [PartDesign::AdditiveBox] Box423
  AttacherType = Attacher::AttachEngine3D
  AttachmentOffset = pos=(-21.3,18.635,0) rot=(0,0,1;0rad)
  Height = 1.9
  Length = 1.3
  MapMode = 5
  Placement = pos=(-21.3,18.635,0) rot=(0,0,1;0rad)
  Support = -> [XY_Plane050]
  Width = 0.23
FEATURE [PartDesign::SubtractiveBox] Box418
  AttacherType = Attacher::AttachEngine3D
  AttachmentOffset = pos=(-21.35,18.635,0.35) rot=(0,0,1;0rad)
  BaseFeature = -> Box423
  Height = 1.55
  Length = 0.5
  MapMode = 5
  Placement = pos=(-21.35,18.635,0.35) rot=(0,0,1;0rad)
  Support = -> [XY_Plane050]
  Width = 0.23
FEATURE [PartDesign::SubtractiveBox] Box403
  AttacherType = Attacher::AttachEngine3D
  AttachmentOffset = pos=(-20.5,18.63,0) rot=(0,0,1;0rad)
  BaseFeature = -> Box418
  Height = 1.635
  Length = 0.5
  MapMode = 5
  Placement = pos=(-20.5,18.63,0) rot=(0,0,1;0rad)
  Support = -> [XY_Plane050]
  Width = 0.25
FEATURE [PartDesign::SubtractiveBox] Box397
  AttacherType = Attacher::AttachEngine3D
  AttachmentOffset = pos=(-21.19,18.635,-0.12) rot=(0,-1,0;0.15708rad)
  BaseFeature = -> Box403
  Height = 0.12
  Length = 0.725
  MapMode = 5
  Placement = pos=(-21.19,18.635,-0.12) rot=(0,-1,0;0.15708rad)
  Support = -> [XY_Plane050]
  Width = 0.25
FEATURE [PartDesign::SubtractiveBox] Box427
  AttacherType = Attacher::AttachEngine3D
  AttachmentOffset = pos=(-20.5,18.63,0) rot=(0,0,1;0rad)
  BaseFeature = -> Box372
  Height = 1.635
  Length = 0.5
  MapMode = 5
  Placement = pos=(-20.5,18.63,0) rot=(0,0,1;0rad)
  Support = -> [XY_Plane049]
  Width = 0.25
FEATURE [PartDesign::SubtractiveBox] Box428
  AttacherType = Attacher::AttachEngine3D
  AttachmentOffset = pos=(-21.5005,18.625,0.235) rot=(0,-1,0;0.174533rad)
  BaseFeature = -> Box413
  Height = 0.3
  Length = 0.6605
  MapMode = 5
  Placement = pos=(-21.5005,18.625,0.235) rot=(0,-1,0;0.174533rad)
  Support = -> [XY_Plane048]
  Width = 0.25
FEATURE [PartDesign::Fillet] Fillet129
  Base = -> Box428 [Edge2]
  BaseFeature = -> Box428
  Placement = pos=(-21.5005,18.625,0.235) rot=(0,-1,0;0.174533rad)
  Radius = 0.05
  SupportTransform = false
FEATURE [PartDesign::Fillet] Fillet121
  Base = -> Fillet129 [Edge33]
  BaseFeature = -> Fillet129
  Placement = pos=(-21.5005,18.625,0.235) rot=(0,-1,0;0.174533rad)
  Radius = 0.5
  SupportTransform = false
FEATURE [PartDesign::AdditiveBox] Box399
  AttacherType = Attacher::AttachEngine3D
  AttachmentOffset = pos=(-21.1,18.635,0.305) rot=(0,1,0;0.785398rad)
  BaseFeature = -> Fillet121
  Height = 0.375
  Length = 0.2
  MapMode = 5
  Placement = pos=(-21.1,18.635,0.305) rot=(0,1,0;0.785398rad)
  Support = -> [XY_Plane048]
  Width = 0.23
FEATURE [PartDesign::SubtractiveCylinder] Cylinder084
  Angle = 360
  AttacherType = Attacher::AttachEngine3D
  AttachmentOffset = pos=(-21.055,18.935,0.52) rot=(1,0,0;1.5708rad)
  BaseFeature = -> Box399
  Height = 0.375
  MapMode = 5
  Placement = pos=(-21.055,18.935,0.52) rot=(1,0,0;1.5708rad)
  Radius = 0.205
  Support = -> [XY_Plane048]
FEATURE [PartDesign::SubtractiveBox] Box426
  AttacherType = Attacher::AttachEngine3D
  AttachmentOffset = pos=(-20.95,18.635,0.53) rot=(0,0,1;0rad)
  BaseFeature = -> Cylinder084
  Height = 0.5
  Length = 0.1
  MapMode = 5
  Placement = pos=(-20.95,18.635,0.53) rot=(0,0,1;0rad)
  Support = -> [XY_Plane048]
  Width = 0.23
FEATURE [PartDesign::SubtractiveBox] Box406
  AttacherType = Attacher::AttachEngine3D
  AttachmentOffset = pos=(-21.15,18.635,0.297) rot=(0,-1,0;0.174533rad)
  BaseFeature = -> Box426
  Height = 0.115
  Length = 0.115
  MapMode = 5
  Placement = pos=(-21.15,18.635,0.297) rot=(0,-1,0;0.174533rad)
  Support = -> [XY_Plane048]
  Width = 0.23
FEATURE [PartDesign::Fillet] Fillet127
  Base = -> Box406 [Edge28]
  BaseFeature = -> Box406
  Placement = pos=(-21.15,18.635,0.297) rot=(0,-1,0;0.174533rad)
  Radius = 0.375
  SupportTransform = false
FEATURE [PartDesign::AdditiveBox] Box412
  AttacherType = Attacher::AttachEngine3D
  AttachmentOffset = pos=(-20.7,18.635,1.55) rot=(0,1,0;0.785398rad)
  BaseFeature = -> Fillet127
  Height = 0.375
  Length = 0.23
  MapMode = 5
  Placement = pos=(-20.7,18.635,1.55) rot=(0,1,0;0.785398rad)
  Support = -> [XY_Plane048]
  Width = 0.23
FEATURE [PartDesign::SubtractiveCylinder] Cylinder085
  Angle = 360
  AttacherType = Attacher::AttachEngine3D
  AttachmentOffset = pos=(-20.271,18.635,1.4056) rot=(-1,0,0;1.5708rad)
  BaseFeature = -> Box412
  Height = 0.23
  MapMode = 5
  Placement = pos=(-20.271,18.635,1.4056) rot=(-1,0,0;1.5708rad)
  Radius = 0.23
  Support = -> [XY_Plane048]
FEATURE [PartDesign::AdditiveBox] Box421
  AttacherType = Attacher::AttachEngine3D
  AttachmentOffset = pos=(-20.1,18.635,1.635) rot=(0,0,1;0rad)
  BaseFeature = -> Cylinder085
  Height = 0.265
  Length = 0.23
  MapMode = 5
  Placement = pos=(-20.1,18.635,1.635) rot=(0,0,1;0rad)
  Support = -> [XY_Plane048]
  Width = 0.23
FEATURE [PartDesign::Body] Body046  label="pin046"
  Group = -> [Box410,Box416,Box405,Box413,Box428,Fillet129,Fillet121,Box399,Cylinder084,Box426,Box406,Fillet127,Box412,Cylinder085,Box421]
  Origin = -> Origin046
  Placement = pos=(0,-5,0) rot=(0,0,1;0rad)
  Tip = -> Box421
FEATURE [PartDesign::AdditiveBox] Box431
  AttacherType = Attacher::AttachEngine3D
  AttachmentOffset = pos=(-21.3,18.635,0) rot=(0,0,1;0rad)
  Height = 1.9
  Length = 1.3
  MapMode = 5
  Placement = pos=(-21.3,18.635,0) rot=(0,0,1;0rad)
  Support = -> [XY_Plane040]
  Width = 0.23
FEATURE [PartDesign::SubtractiveBox] Box429
  AttacherType = Attacher::AttachEngine3D
  AttachmentOffset = pos=(-21.35,18.635,0.35) rot=(0,0,1;0rad)
  BaseFeature = -> Box431
  Height = 1.55
  Length = 0.5
  MapMode = 5
  Placement = pos=(-21.35,18.635,0.35) rot=(0,0,1;0rad)
  Support = -> [XY_Plane040]
  Width = 0.23
FEATURE [PartDesign::SubtractiveBox] Box387
  AttacherType = Attacher::AttachEngine3D
  AttachmentOffset = pos=(-20.5,18.63,0) rot=(0,0,1;0rad)
  BaseFeature = -> Box429
  Height = 1.635
  Length = 0.5
  MapMode = 5
  Placement = pos=(-20.5,18.63,0) rot=(0,0,1;0rad)
  Support = -> [XY_Plane040]
  Width = 0.25
FEATURE [PartDesign::SubtractiveBox] Box408
  AttacherType = Attacher::AttachEngine3D
  AttachmentOffset = pos=(-21.19,18.635,-0.12) rot=(0,-1,0;0.15708rad)
  BaseFeature = -> Box387
  Height = 0.12
  Length = 0.725
  MapMode = 5
  Placement = pos=(-21.19,18.635,-0.12) rot=(0,-1,0;0.15708rad)
  Support = -> [XY_Plane040]
  Width = 0.25
FEATURE [PartDesign::SubtractiveBox] Box400
  AttacherType = Attacher::AttachEngine3D
  AttachmentOffset = pos=(-21.5005,18.625,0.235) rot=(0,-1,0;0.174533rad)
  BaseFeature = -> Box408
  Height = 0.3
  Length = 0.6605
  MapMode = 5
  Placement = pos=(-21.5005,18.625,0.235) rot=(0,-1,0;0.174533rad)
  Support = -> [XY_Plane040]
  Width = 0.25
FEATURE [PartDesign::Fillet] Fillet123
  Base = -> Box400 [Edge2]
  BaseFeature = -> Box400
  Placement = pos=(-21.5005,18.625,0.235) rot=(0,-1,0;0.174533rad)
  Radius = 0.05
  SupportTransform = false
FEATURE [PartDesign::Fillet] Fillet141
  Base = -> Fillet123 [Edge33]
  BaseFeature = -> Fillet123
  Placement = pos=(-21.5005,18.625,0.235) rot=(0,-1,0;0.174533rad)
  Radius = 0.5
  SupportTransform = false
FEATURE [PartDesign::AdditiveBox] Box422
  AttacherType = Attacher::AttachEngine3D
  AttachmentOffset = pos=(-21.1,18.635,0.305) rot=(0,1,0;0.785398rad)
  BaseFeature = -> Fillet141
  Height = 0.375
  Length = 0.2
  MapMode = 5
  Placement = pos=(-21.1,18.635,0.305) rot=(0,1,0;0.785398rad)
  Support = -> [XY_Plane040]
  Width = 0.23
FEATURE [PartDesign::SubtractiveCylinder] Cylinder091
  Angle = 360
  AttacherType = Attacher::AttachEngine3D
  AttachmentOffset = pos=(-21.055,18.935,0.52) rot=(1,0,0;1.5708rad)
  BaseFeature = -> Box422
  Height = 0.375
  MapMode = 5
  Placement = pos=(-21.055,18.935,0.52) rot=(1,0,0;1.5708rad)
  Radius = 0.205
  Support = -> [XY_Plane040]
FEATURE [PartDesign::SubtractiveBox] Box419
  AttacherType = Attacher::AttachEngine3D
  AttachmentOffset = pos=(-20.95,18.635,0.53) rot=(0,0,1;0rad)
  BaseFeature = -> Cylinder091
  Height = 0.5
  Length = 0.1
  MapMode = 5
  Placement = pos=(-20.95,18.635,0.53) rot=(0,0,1;0rad)
  Support = -> [XY_Plane040]
  Width = 0.23
FEATURE [PartDesign::SubtractiveBox] Box420
  AttacherType = Attacher::AttachEngine3D
  AttachmentOffset = pos=(-21.15,18.635,0.297) rot=(0,-1,0;0.174533rad)
  BaseFeature = -> Box419
  Height = 0.115
  Length = 0.115
  MapMode = 5
  Placement = pos=(-21.15,18.635,0.297) rot=(0,-1,0;0.174533rad)
  Support = -> [XY_Plane040]
  Width = 0.23
FEATURE [PartDesign::Fillet] Fillet112
  Base = -> Box420 [Edge28]
  BaseFeature = -> Box420
  Placement = pos=(-21.15,18.635,0.297) rot=(0,-1,0;0.174533rad)
  Radius = 0.375
  SupportTransform = false
FEATURE [PartDesign::AdditiveBox] Box425
  AttacherType = Attacher::AttachEngine3D
  AttachmentOffset = pos=(-20.7,18.635,1.55) rot=(0,1,0;0.785398rad)
  BaseFeature = -> Fillet112
  Height = 0.375
  Length = 0.23
  MapMode = 5
  Placement = pos=(-20.7,18.635,1.55) rot=(0,1,0;0.785398rad)
  Support = -> [XY_Plane040]
  Width = 0.23
FEATURE [PartDesign::SubtractiveCylinder] Cylinder086
  Angle = 360
  AttacherType = Attacher::AttachEngine3D
  AttachmentOffset = pos=(-20.271,18.635,1.4056) rot=(-1,0,0;1.5708rad)
  BaseFeature = -> Box425
  Height = 0.23
  MapMode = 5
  Placement = pos=(-20.271,18.635,1.4056) rot=(-1,0,0;1.5708rad)
  Radius = 0.23
  Support = -> [XY_Plane040]
FEATURE [PartDesign::AdditiveBox] Box417
  AttacherType = Attacher::AttachEngine3D
  AttachmentOffset = pos=(-20.1,18.635,1.635) rot=(0,0,1;0rad)
  BaseFeature = -> Cylinder086
  Height = 0.265
  Length = 0.23
  MapMode = 5
  Placement = pos=(-20.1,18.635,1.635) rot=(0,0,1;0rad)
  Support = -> [XY_Plane040]
  Width = 0.23
FEATURE [PartDesign::Body] Body048  label="pin048"
  Group = -> [Box431,Box429,Box387,Box408,Box400,Fillet123,Fillet141,Box422,Cylinder091,Box419,Box420,Fillet112,Box425,Cylinder086,Box417]
  Origin = -> Origin050
  Placement = pos=(0,-5.5,0) rot=(0,0,1;0rad)
  Tip = -> Box417
FEATURE [PartDesign::SubtractiveBox] Box434
  AttacherType = Attacher::AttachEngine3D
  AttachmentOffset = pos=(-21.19,18.635,-0.12) rot=(0,-1,0;0.15708rad)
  BaseFeature = -> Box427
  Height = 0.12
  Length = 0.725
  MapMode = 5
  Placement = pos=(-21.19,18.635,-0.12) rot=(0,-1,0;0.15708rad)
  Support = -> [XY_Plane049]
  Width = 0.25
FEATURE [PartDesign::SubtractiveBox] Box371
  AttacherType = Attacher::AttachEngine3D
  AttachmentOffset = pos=(-21.5005,18.625,0.235) rot=(0,-1,0;0.174533rad)
  BaseFeature = -> Box434
  Height = 0.3
  Length = 0.6605
  MapMode = 5
  Placement = pos=(-21.5005,18.625,0.235) rot=(0,-1,0;0.174533rad)
  Support = -> [XY_Plane049]
  Width = 0.25
FEATURE [PartDesign::Fillet] Fillet142
  Base = -> Box371 [Edge2]
  BaseFeature = -> Box371
  Placement = pos=(-21.5005,18.625,0.235) rot=(0,-1,0;0.174533rad)
  Radius = 0.05
  SupportTransform = false
FEATURE [PartDesign::Fillet] Fillet134
  Base = -> Fillet142 [Edge33]
  BaseFeature = -> Fillet142
  Placement = pos=(-21.5005,18.625,0.235) rot=(0,-1,0;0.174533rad)
  Radius = 0.5
  SupportTransform = false
FEATURE [PartDesign::AdditiveBox] Box407
  AttacherType = Attacher::AttachEngine3D
  AttachmentOffset = pos=(-21.1,18.635,0.305) rot=(0,1,0;0.785398rad)
  BaseFeature = -> Fillet134
  Height = 0.375
  Length = 0.2
  MapMode = 5
  Placement = pos=(-21.1,18.635,0.305) rot=(0,1,0;0.785398rad)
  Support = -> [XY_Plane049]
  Width = 0.23
FEATURE [PartDesign::SubtractiveCylinder] Cylinder089
  Angle = 360
  AttacherType = Attacher::AttachEngine3D
  AttachmentOffset = pos=(-21.055,18.935,0.52) rot=(1,0,0;1.5708rad)
  BaseFeature = -> Box407
  Height = 0.375
  MapMode = 5
  Placement = pos=(-21.055,18.935,0.52) rot=(1,0,0;1.5708rad)
  Radius = 0.205
  Support = -> [XY_Plane049]
FEATURE [PartDesign::SubtractiveBox] Box414
  AttacherType = Attacher::AttachEngine3D
  AttachmentOffset = pos=(-20.95,18.635,0.53) rot=(0,0,1;0rad)
  BaseFeature = -> Cylinder089
  Height = 0.5
  Length = 0.1
  MapMode = 5
  Placement = pos=(-20.95,18.635,0.53) rot=(0,0,1;0rad)
  Support = -> [XY_Plane049]
  Width = 0.23
FEATURE [PartDesign::SubtractiveBox] Box432
  AttacherType = Attacher::AttachEngine3D
  AttachmentOffset = pos=(-21.15,18.635,0.297) rot=(0,-1,0;0.174533rad)
  BaseFeature = -> Box414
  Height = 0.115
  Length = 0.115
  MapMode = 5
  Placement = pos=(-21.15,18.635,0.297) rot=(0,-1,0;0.174533rad)
  Support = -> [XY_Plane049]
  Width = 0.23
FEATURE [PartDesign::Fillet] Fillet136
  Base = -> Box432 [Edge28]
  BaseFeature = -> Box432
  Placement = pos=(-21.15,18.635,0.297) rot=(0,-1,0;0.174533rad)
  Radius = 0.375
  SupportTransform = false
FEATURE [PartDesign::AdditiveBox] Box433
  AttacherType = Attacher::AttachEngine3D
  AttachmentOffset = pos=(-20.7,18.635,1.55) rot=(0,1,0;0.785398rad)
  BaseFeature = -> Fillet136
  Height = 0.375
  Length = 0.23
  MapMode = 5
  Placement = pos=(-20.7,18.635,1.55) rot=(0,1,0;0.785398rad)
  Support = -> [XY_Plane049]
  Width = 0.23
FEATURE [PartDesign::SubtractiveCylinder] Cylinder090
  Angle = 360
  AttacherType = Attacher::AttachEngine3D
  AttachmentOffset = pos=(-20.271,18.635,1.4056) rot=(-1,0,0;1.5708rad)
  BaseFeature = -> Box433
  Height = 0.23
  MapMode = 5
  Placement = pos=(-20.271,18.635,1.4056) rot=(-1,0,0;1.5708rad)
  Radius = 0.23
  Support = -> [XY_Plane049]
FEATURE [PartDesign::AdditiveBox] Box435
  AttacherType = Attacher::AttachEngine3D
  AttachmentOffset = pos=(-20.1,18.635,1.635) rot=(0,0,1;0rad)
  BaseFeature = -> Cylinder090
  Height = 0.265
  Length = 0.23
  MapMode = 5
  Placement = pos=(-20.1,18.635,1.635) rot=(0,0,1;0rad)
  Support = -> [XY_Plane049]
  Width = 0.23
FEATURE [PartDesign::Body] Body047  label="pin047"
  Group = -> [Box362,Box372,Box427,Box434,Box371,Fillet142,Fillet134,Box407,Cylinder089,Box414,Box432,Fillet136,Box433,Cylinder090,Box435]
  Origin = -> Origin041
  Placement = pos=(0,-3,0) rot=(0,0,1;0rad)
  Tip = -> Box435
FEATURE [PartDesign::SubtractiveBox] Box439
  AttacherType = Attacher::AttachEngine3D
  AttachmentOffset = pos=(-21.5005,18.625,0.235) rot=(0,-1,0;0.174533rad)
  BaseFeature = -> Box397
  Height = 0.3
  Length = 0.6605
  MapMode = 5
  Placement = pos=(-21.5005,18.625,0.235) rot=(0,-1,0;0.174533rad)
  Support = -> [XY_Plane050]
  Width = 0.25
FEATURE [PartDesign::Fillet] Fillet143
  Base = -> Box439 [Edge2]
  BaseFeature = -> Box439
  Placement = pos=(-21.5005,18.625,0.235) rot=(0,-1,0;0.174533rad)
  Radius = 0.05
  SupportTransform = false
FEATURE [PartDesign::Fillet] Fillet122
  Base = -> Fillet143 [Edge33]
  BaseFeature = -> Fillet143
  Placement = pos=(-21.5005,18.625,0.235) rot=(0,-1,0;0.174533rad)
  Radius = 0.5
  SupportTransform = false
FEATURE [PartDesign::AdditiveBox] Box384
  AttacherType = Attacher::AttachEngine3D
  AttachmentOffset = pos=(-21.1,18.635,0.305) rot=(0,1,0;0.785398rad)
  BaseFeature = -> Fillet122
  Height = 0.375
  Length = 0.2
  MapMode = 5
  Placement = pos=(-21.1,18.635,0.305) rot=(0,1,0;0.785398rad)
  Support = -> [XY_Plane050]
  Width = 0.23
FEATURE [PartDesign::SubtractiveCylinder] Cylinder082
  Angle = 360
  AttacherType = Attacher::AttachEngine3D
  AttachmentOffset = pos=(-21.055,18.935,0.52) rot=(1,0,0;1.5708rad)
  BaseFeature = -> Box384
  Height = 0.375
  MapMode = 5
  Placement = pos=(-21.055,18.935,0.52) rot=(1,0,0;1.5708rad)
  Radius = 0.205
  Support = -> [XY_Plane050]
FEATURE [PartDesign::SubtractiveBox] Box383
  AttacherType = Attacher::AttachEngine3D
  AttachmentOffset = pos=(-20.95,18.635,0.53) rot=(0,0,1;0rad)
  BaseFeature = -> Cylinder082
  Height = 0.5
  Length = 0.1
  MapMode = 5
  Placement = pos=(-20.95,18.635,0.53) rot=(0,0,1;0rad)
  Support = -> [XY_Plane050]
  Width = 0.23
FEATURE [PartDesign::SubtractiveBox] Box411
  AttacherType = Attacher::AttachEngine3D
  AttachmentOffset = pos=(-21.15,18.635,0.297) rot=(0,-1,0;0.174533rad)
  BaseFeature = -> Box383
  Height = 0.115
  Length = 0.115
  MapMode = 5
  Placement = pos=(-21.15,18.635,0.297) rot=(0,-1,0;0.174533rad)
  Support = -> [XY_Plane050]
  Width = 0.23
FEATURE [PartDesign::Fillet] Fillet139
  Base = -> Box411 [Edge28]
  BaseFeature = -> Box411
  Placement = pos=(-21.15,18.635,0.297) rot=(0,-1,0;0.174533rad)
  Radius = 0.375
  SupportTransform = false
FEATURE [PartDesign::AdditiveBox] Box398
  AttacherType = Attacher::AttachEngine3D
  AttachmentOffset = pos=(-20.7,18.635,1.55) rot=(0,1,0;0.785398rad)
  BaseFeature = -> Fillet139
  Height = 0.375
  Length = 0.23
  MapMode = 5
  Placement = pos=(-20.7,18.635,1.55) rot=(0,1,0;0.785398rad)
  Support = -> [XY_Plane050]
  Width = 0.23
FEATURE [PartDesign::SubtractiveCylinder] Cylinder083
  Angle = 360
  AttacherType = Attacher::AttachEngine3D
  AttachmentOffset = pos=(-20.271,18.635,1.4056) rot=(-1,0,0;1.5708rad)
  BaseFeature = -> Box398
  Height = 0.23
  MapMode = 5
  Placement = pos=(-20.271,18.635,1.4056) rot=(-1,0,0;1.5708rad)
  Radius = 0.23
  Support = -> [XY_Plane050]
FEATURE [PartDesign::AdditiveBox] Box401
  AttacherType = Attacher::AttachEngine3D
  AttachmentOffset = pos=(-20.1,18.635,1.635) rot=(0,0,1;0rad)
  BaseFeature = -> Cylinder083
  Height = 0.265
  Length = 0.23
  MapMode = 5
  Placement = pos=(-20.1,18.635,1.635) rot=(0,0,1;0rad)
  Support = -> [XY_Plane050]
  Width = 0.23
FEATURE [PartDesign::Body] Body043  label="pin043"
  Group = -> [Box423,Box418,Box403,Box397,Box439,Fillet143,Fillet122,Box384,Cylinder082,Box383,Box411,Fillet139,Box398,Cylinder083,Box401]
  Origin = -> Origin042
  Placement = pos=(0,-4.5,0) rot=(0,0,1;0rad)
  Tip = -> Box401
FEATURE [PartDesign::SubtractiveBox] Box442
  AttacherType = Attacher::AttachEngine3D
  AttachmentOffset = pos=(-20.5,18.63,0) rot=(0,0,1;0rad)
  BaseFeature = -> Box377
  Height = 1.635
  Length = 0.5
  MapMode = 5
  Placement = pos=(-20.5,18.63,0) rot=(0,0,1;0rad)
  Support = -> [XY_Plane052]
  Width = 0.25
FEATURE [PartDesign::SubtractiveBox] Box378
  AttacherType = Attacher::AttachEngine3D
  AttachmentOffset = pos=(-21.19,18.635,-0.12) rot=(0,-1,0;0.15708rad)
  BaseFeature = -> Box442
  Height = 0.12
  Length = 0.725
  MapMode = 5
  Placement = pos=(-21.19,18.635,-0.12) rot=(0,-1,0;0.15708rad)
  Support = -> [XY_Plane052]
  Width = 0.25
FEATURE [PartDesign::SubtractiveBox] Box363
  AttacherType = Attacher::AttachEngine3D
  AttachmentOffset = pos=(-21.5005,18.625,0.235) rot=(0,-1,0;0.174533rad)
  BaseFeature = -> Box378
  Height = 0.3
  Length = 0.6605
  MapMode = 5
  Placement = pos=(-21.5005,18.625,0.235) rot=(0,-1,0;0.174533rad)
  Support = -> [XY_Plane052]
  Width = 0.25
FEATURE [PartDesign::Fillet] Fillet132
  Base = -> Box363 [Edge2]
  BaseFeature = -> Box363
  Placement = pos=(-21.5005,18.625,0.235) rot=(0,-1,0;0.174533rad)
  Radius = 0.05
  SupportTransform = false
FEATURE [PartDesign::Fillet] Fillet124
  Base = -> Fillet132 [Edge33]
  BaseFeature = -> Fillet132
  Placement = pos=(-21.5005,18.625,0.235) rot=(0,-1,0;0.174533rad)
  Radius = 0.5
  SupportTransform = false
FEATURE [PartDesign::AdditiveBox] Box443
  AttacherType = Attacher::AttachEngine3D
  AttachmentOffset = pos=(-21.1,18.635,0.305) rot=(0,1,0;0.785398rad)
  BaseFeature = -> Fillet140
  Height = 0.375
  Length = 0.2
  MapMode = 5
  Placement = pos=(-21.1,18.635,0.305) rot=(0,1,0;0.785398rad)
  Support = -> [XY_Plane047]
  Width = 0.23
FEATURE [PartDesign::SubtractiveCylinder] Cylinder076
  Angle = 360
  AttacherType = Attacher::AttachEngine3D
  AttachmentOffset = pos=(-21.055,18.935,0.52) rot=(1,0,0;1.5708rad)
  BaseFeature = -> Box443
  Height = 0.375
  MapMode = 5
  Placement = pos=(-21.055,18.935,0.52) rot=(1,0,0;1.5708rad)
  Radius = 0.205
  Support = -> [XY_Plane047]
FEATURE [PartDesign::SubtractiveBox] Box374
  AttacherType = Attacher::AttachEngine3D
  AttachmentOffset = pos=(-20.95,18.635,0.53) rot=(0,0,1;0rad)
  BaseFeature = -> Cylinder076
  Height = 0.5
  Length = 0.1
  MapMode = 5
  Placement = pos=(-20.95,18.635,0.53) rot=(0,0,1;0rad)
  Support = -> [XY_Plane047]
  Width = 0.23
FEATURE [PartDesign::SubtractiveBox] Box367
  AttacherType = Attacher::AttachEngine3D
  AttachmentOffset = pos=(-21.15,18.635,0.297) rot=(0,-1,0;0.174533rad)
  BaseFeature = -> Box374
  Height = 0.115
  Length = 0.115
  MapMode = 5
  Placement = pos=(-21.15,18.635,0.297) rot=(0,-1,0;0.174533rad)
  Support = -> [XY_Plane047]
  Width = 0.23
FEATURE [PartDesign::Fillet] Fillet138
  Base = -> Box367 [Edge28]
  BaseFeature = -> Box367
  Placement = pos=(-21.15,18.635,0.297) rot=(0,-1,0;0.174533rad)
  Radius = 0.375
  SupportTransform = false
FEATURE [PartDesign::AdditiveBox] Box370
  AttacherType = Attacher::AttachEngine3D
  AttachmentOffset = pos=(-20.7,18.635,1.55) rot=(0,1,0;0.785398rad)
  BaseFeature = -> Fillet138
  Height = 0.375
  Length = 0.23
  MapMode = 5
  Placement = pos=(-20.7,18.635,1.55) rot=(0,1,0;0.785398rad)
  Support = -> [XY_Plane047]
  Width = 0.23
FEATURE [PartDesign::SubtractiveCylinder] Cylinder077
  Angle = 360
  AttacherType = Attacher::AttachEngine3D
  AttachmentOffset = pos=(-20.271,18.635,1.4056) rot=(-1,0,0;1.5708rad)
  BaseFeature = -> Box370
  Height = 0.23
  MapMode = 5
  Placement = pos=(-20.271,18.635,1.4056) rot=(-1,0,0;1.5708rad)
  Radius = 0.23
  Support = -> [XY_Plane047]
FEATURE [PartDesign::AdditiveBox] Box361
  AttacherType = Attacher::AttachEngine3D
  AttachmentOffset = pos=(-20.1,18.635,1.635) rot=(0,0,1;0rad)
  BaseFeature = -> Cylinder077
  Height = 0.265
  Length = 0.23
  MapMode = 5
  Placement = pos=(-20.1,18.635,1.635) rot=(0,0,1;0rad)
  Support = -> [XY_Plane047]
  Width = 0.23
FEATURE [PartDesign::Body] Body044  label="pin044"
  Group = -> [Box364,Box366,Box415,Box375,Box376,Fillet135,Fillet140,Box443,Cylinder076,Box374,Box367,Fillet138,Box370,Cylinder077,Box361]
  Origin = -> Origin048
  Placement = pos=(0,-4,0) rot=(0,0,1;0rad)
  Tip = -> Box361
FEATURE [PartDesign::AdditiveBox] Box446
  AttacherType = Attacher::AttachEngine3D
  AttachmentOffset = pos=(-21.1,18.635,0.305) rot=(0,1,0;0.785398rad)
  BaseFeature = -> Fillet124
  Height = 0.375
  Length = 0.2
  MapMode = 5
  Placement = pos=(-21.1,18.635,0.305) rot=(0,1,0;0.785398rad)
  Support = -> [XY_Plane052]
  Width = 0.23
FEATURE [PartDesign::SubtractiveCylinder] Cylinder092
  Angle = 360
  AttacherType = Attacher::AttachEngine3D
  AttachmentOffset = pos=(-21.055,18.935,0.52) rot=(1,0,0;1.5708rad)
  BaseFeature = -> Box446
  Height = 0.375
  MapMode = 5
  Placement = pos=(-21.055,18.935,0.52) rot=(1,0,0;1.5708rad)
  Radius = 0.205
  Support = -> [XY_Plane052]
FEATURE [PartDesign::SubtractiveBox] Box445
  AttacherType = Attacher::AttachEngine3D
  AttachmentOffset = pos=(-20.95,18.635,0.53) rot=(0,0,1;0rad)
  BaseFeature = -> Cylinder092
  Height = 0.5
  Length = 0.1
  MapMode = 5
  Placement = pos=(-20.95,18.635,0.53) rot=(0,0,1;0rad)
  Support = -> [XY_Plane052]
  Width = 0.23
FEATURE [PartDesign::SubtractiveBox] Box430
  AttacherType = Attacher::AttachEngine3D
  AttachmentOffset = pos=(-21.15,18.635,0.297) rot=(0,-1,0;0.174533rad)
  BaseFeature = -> Box445
  Height = 0.115
  Length = 0.115
  MapMode = 5
  Placement = pos=(-21.15,18.635,0.297) rot=(0,-1,0;0.174533rad)
  Support = -> [XY_Plane052]
  Width = 0.23
FEATURE [PartDesign::Fillet] Fillet128
  Base = -> Box430 [Edge28]
  BaseFeature = -> Box430
  Placement = pos=(-21.15,18.635,0.297) rot=(0,-1,0;0.174533rad)
  Radius = 0.375
  SupportTransform = false
FEATURE [PartDesign::AdditiveBox] Box440
  AttacherType = Attacher::AttachEngine3D
  AttachmentOffset = pos=(-20.7,18.635,1.55) rot=(0,1,0;0.785398rad)
  BaseFeature = -> Fillet128
  Height = 0.375
  Length = 0.23
  MapMode = 5
  Placement = pos=(-20.7,18.635,1.55) rot=(0,1,0;0.785398rad)
  Support = -> [XY_Plane052]
  Width = 0.23
FEATURE [PartDesign::SubtractiveCylinder] Cylinder093
  Angle = 360
  AttacherType = Attacher::AttachEngine3D
  AttachmentOffset = pos=(-20.271,18.635,1.4056) rot=(-1,0,0;1.5708rad)
  BaseFeature = -> Box440
  Height = 0.23
  MapMode = 5
  Placement = pos=(-20.271,18.635,1.4056) rot=(-1,0,0;1.5708rad)
  Radius = 0.23
  Support = -> [XY_Plane052]
FEATURE [PartDesign::AdditiveBox] Box365
  AttacherType = Attacher::AttachEngine3D
  AttachmentOffset = pos=(-20.1,18.635,1.635) rot=(0,0,1;0rad)
  BaseFeature = -> Cylinder093
  Height = 0.265
  Length = 0.23
  MapMode = 5
  Placement = pos=(-20.1,18.635,1.635) rot=(0,0,1;0rad)
  Support = -> [XY_Plane052]
  Width = 0.23
FEATURE [PartDesign::Body] Body042  label="pin042"
  Group = -> [Box369,Box377,Box442,Box378,Box363,Fillet132,Fillet124,Box446,Cylinder092,Box445,Box430,Fillet128,Box440,Cylinder093,Box365]
  Origin = -> Origin052
  Placement = pos=(0,-3.5,0) rot=(0,0,1;0rad)
  Tip = -> Box365
FEATURE [PartDesign::AdditiveBox] Box455
  AttacherType = Attacher::AttachEngine3D
  AttachmentOffset = pos=(-21.3,18.635,0) rot=(0,0,1;0rad)
  Height = 1.9
  Length = 1.3
  MapMode = 5
  Placement = pos=(-21.3,18.635,0) rot=(0,0,1;0rad)
  Support = -> [XY_Plane046]
  Width = 0.23
FEATURE [PartDesign::SubtractiveBox] Box448
  AttacherType = Attacher::AttachEngine3D
  AttachmentOffset = pos=(-21.35,18.635,0.35) rot=(0,0,1;0rad)
  BaseFeature = -> Box455
  Height = 1.55
  Length = 0.5
  MapMode = 5
  Placement = pos=(-21.35,18.635,0.35) rot=(0,0,1;0rad)
  Support = -> [XY_Plane046]
  Width = 0.23
FEATURE [PartDesign::SubtractiveBox] Box438
  AttacherType = Attacher::AttachEngine3D
  AttachmentOffset = pos=(-20.5,18.63,0) rot=(0,0,1;0rad)
  BaseFeature = -> Box448
  Height = 1.635
  Length = 0.5
  MapMode = 5
  Placement = pos=(-20.5,18.63,0) rot=(0,0,1;0rad)
  Support = -> [XY_Plane046]
  Width = 0.25
FEATURE [PartDesign::SubtractiveBox] Box452
  AttacherType = Attacher::AttachEngine3D
  AttachmentOffset = pos=(-21.19,18.635,-0.12) rot=(0,-1,0;0.15708rad)
  BaseFeature = -> Box438
  Height = 0.12
  Length = 0.725
  MapMode = 5
  Placement = pos=(-21.19,18.635,-0.12) rot=(0,-1,0;0.15708rad)
  Support = -> [XY_Plane046]
  Width = 0.25
FEATURE [PartDesign::SubtractiveBox] Box453
  AttacherType = Attacher::AttachEngine3D
  AttachmentOffset = pos=(-21.5005,18.625,0.235) rot=(0,-1,0;0.174533rad)
  BaseFeature = -> Box452
  Height = 0.3
  Length = 0.6605
  MapMode = 5
  Placement = pos=(-21.5005,18.625,0.235) rot=(0,-1,0;0.174533rad)
  Support = -> [XY_Plane046]
  Width = 0.25
FEATURE [PartDesign::Fillet] Fillet114
  Base = -> Box453 [Edge2]
  BaseFeature = -> Box453
  Placement = pos=(-21.5005,18.625,0.235) rot=(0,-1,0;0.174533rad)
  Radius = 0.05
  SupportTransform = false
FEATURE [PartDesign::Fillet] Fillet115
  Base = -> Fillet114 [Edge33]
  BaseFeature = -> Fillet114
  Placement = pos=(-21.5005,18.625,0.235) rot=(0,-1,0;0.174533rad)
  Radius = 0.5
  SupportTransform = false
FEATURE [PartDesign::AdditiveBox] Box437
  AttacherType = Attacher::AttachEngine3D
  AttachmentOffset = pos=(-21.1,18.635,0.305) rot=(0,1,0;0.785398rad)
  BaseFeature = -> Fillet115
  Height = 0.375
  Length = 0.2
  MapMode = 5
  Placement = pos=(-21.1,18.635,0.305) rot=(0,1,0;0.785398rad)
  Support = -> [XY_Plane046]
  Width = 0.23
FEATURE [PartDesign::SubtractiveCylinder] Cylinder094
  Angle = 360
  AttacherType = Attacher::AttachEngine3D
  AttachmentOffset = pos=(-21.055,18.935,0.52) rot=(1,0,0;1.5708rad)
  BaseFeature = -> Box437
  Height = 0.375
  MapMode = 5
  Placement = pos=(-21.055,18.935,0.52) rot=(1,0,0;1.5708rad)
  Radius = 0.205
  Support = -> [XY_Plane046]
FEATURE [PartDesign::SubtractiveBox] Box459
  AttacherType = Attacher::AttachEngine3D
  AttachmentOffset = pos=(-20.95,18.635,0.53) rot=(0,0,1;0rad)
  BaseFeature = -> Cylinder094
  Height = 0.5
  Length = 0.1
  MapMode = 5
  Placement = pos=(-20.95,18.635,0.53) rot=(0,0,1;0rad)
  Support = -> [XY_Plane046]
  Width = 0.23
FEATURE [PartDesign::SubtractiveBox] Box451
  AttacherType = Attacher::AttachEngine3D
  AttachmentOffset = pos=(-21.15,18.635,0.297) rot=(0,-1,0;0.174533rad)
  BaseFeature = -> Box459
  Height = 0.115
  Length = 0.115
  MapMode = 5
  Placement = pos=(-21.15,18.635,0.297) rot=(0,-1,0;0.174533rad)
  Support = -> [XY_Plane046]
  Width = 0.23
FEATURE [PartDesign::Fillet] Fillet130
  Base = -> Box451 [Edge28]
  BaseFeature = -> Box451
  Placement = pos=(-21.15,18.635,0.297) rot=(0,-1,0;0.174533rad)
  Radius = 0.375
  SupportTransform = false
FEATURE [PartDesign::AdditiveBox] Box450
  AttacherType = Attacher::AttachEngine3D
  AttachmentOffset = pos=(-20.7,18.635,1.55) rot=(0,1,0;0.785398rad)
  BaseFeature = -> Fillet130
  Height = 0.375
  Length = 0.23
  MapMode = 5
  Placement = pos=(-20.7,18.635,1.55) rot=(0,1,0;0.785398rad)
  Support = -> [XY_Plane046]
  Width = 0.23
FEATURE [PartDesign::SubtractiveCylinder] Cylinder095
  Angle = 360
  AttacherType = Attacher::AttachEngine3D
  AttachmentOffset = pos=(-20.271,18.635,1.4056) rot=(-1,0,0;1.5708rad)
  BaseFeature = -> Box450
  Height = 0.23
  MapMode = 5
  Placement = pos=(-20.271,18.635,1.4056) rot=(-1,0,0;1.5708rad)
  Radius = 0.23
  Support = -> [XY_Plane046]
FEATURE [PartDesign::AdditiveBox] Box456
  AttacherType = Attacher::AttachEngine3D
  AttachmentOffset = pos=(-20.1,18.635,1.635) rot=(0,0,1;0rad)
  BaseFeature = -> Cylinder095
  Height = 0.265
  Length = 0.23
  MapMode = 5
  Placement = pos=(-20.1,18.635,1.635) rot=(0,0,1;0rad)
  Support = -> [XY_Plane046]
  Width = 0.23
FEATURE [PartDesign::Body] Body037  label="pin037"
  Group = -> [Box455,Box448,Box438,Box452,Box453,Fillet114,Fillet115,Box437,Cylinder094,Box459,Box451,Fillet130,Box450,Cylinder095,Box456]
  Origin = -> Origin044
  Placement = pos=(0,-0.5,0) rot=(0,0,1;0rad)
  Tip = -> Box456
FEATURE [PartDesign::SubtractiveBox] Box468
  AttacherType = Attacher::AttachEngine3D
  AttachmentOffset = pos=(-20.5,18.63,0) rot=(0,0,1;0rad)
  BaseFeature = -> Box391
  Height = 1.635
  Length = 0.5
  MapMode = 5
  Placement = pos=(-20.5,18.63,0) rot=(0,0,1;0rad)
  Support = -> [XY_Plane045]
  Width = 0.25
FEATURE [PartDesign::SubtractiveBox] Box389
  AttacherType = Attacher::AttachEngine3D
  AttachmentOffset = pos=(-21.19,18.635,-0.12) rot=(0,-1,0;0.15708rad)
  BaseFeature = -> Box468
  Height = 0.12
  Length = 0.725
  MapMode = 5
  Placement = pos=(-21.19,18.635,-0.12) rot=(0,-1,0;0.15708rad)
  Support = -> [XY_Plane045]
  Width = 0.25
FEATURE [PartDesign::SubtractiveBox] Box386
  AttacherType = Attacher::AttachEngine3D
  AttachmentOffset = pos=(-21.5005,18.625,0.235) rot=(0,-1,0;0.174533rad)
  BaseFeature = -> Box389
  Height = 0.3
  Length = 0.6605
  MapMode = 5
  Placement = pos=(-21.5005,18.625,0.235) rot=(0,-1,0;0.174533rad)
  Support = -> [XY_Plane045]
  Width = 0.25
FEATURE [PartDesign::Fillet] Fillet116
  Base = -> Box386 [Edge2]
  BaseFeature = -> Box386
  Placement = pos=(-21.5005,18.625,0.235) rot=(0,-1,0;0.174533rad)
  Radius = 0.05
  SupportTransform = false
FEATURE [PartDesign::Fillet] Fillet119
  Base = -> Fillet116 [Edge33]
  BaseFeature = -> Fillet116
  Placement = pos=(-21.5005,18.625,0.235) rot=(0,-1,0;0.174533rad)
  Radius = 0.5
  SupportTransform = false
FEATURE [PartDesign::SubtractiveBox] Box470
  AttacherType = Attacher::AttachEngine3D
  AttachmentOffset = pos=(-20.5,18.63,0) rot=(0,0,1;0rad)
  BaseFeature = -> Box382
  Height = 1.635
  Length = 0.5
  MapMode = 5
  Placement = pos=(-20.5,18.63,0) rot=(0,0,1;0rad)
  Support = -> [XY_Plane041]
  Width = 0.25
FEATURE [PartDesign::SubtractiveBox] Box368
  AttacherType = Attacher::AttachEngine3D
  AttachmentOffset = pos=(-21.19,18.635,-0.12) rot=(0,-1,0;0.15708rad)
  BaseFeature = -> Box470
  Height = 0.12
  Length = 0.725
  MapMode = 5
  Placement = pos=(-21.19,18.635,-0.12) rot=(0,-1,0;0.15708rad)
  Support = -> [XY_Plane041]
  Width = 0.25
FEATURE [PartDesign::SubtractiveBox] Box388
  AttacherType = Attacher::AttachEngine3D
  AttachmentOffset = pos=(-21.5005,18.625,0.235) rot=(0,-1,0;0.174533rad)
  BaseFeature = -> Box368
  Height = 0.3
  Length = 0.6605
  MapMode = 5
  Placement = pos=(-21.5005,18.625,0.235) rot=(0,-1,0;0.174533rad)
  Support = -> [XY_Plane041]
  Width = 0.25
FEATURE [PartDesign::Fillet] Fillet120
  Base = -> Box388 [Edge2]
  BaseFeature = -> Box388
  Placement = pos=(-21.5005,18.625,0.235) rot=(0,-1,0;0.174533rad)
  Radius = 0.05
  SupportTransform = false
FEATURE [PartDesign::Fillet] Fillet110
  Base = -> Fillet120 [Edge33]
  BaseFeature = -> Fillet120
  Placement = pos=(-21.5005,18.625,0.235) rot=(0,-1,0;0.174533rad)
  Radius = 0.5
  SupportTransform = false
FEATURE [PartDesign::AdditiveBox] Box471
  AttacherType = Attacher::AttachEngine3D
  AttachmentOffset = pos=(-21.3,18.635,0) rot=(0,0,1;0rad)
  Height = 1.9
  Length = 1.3
  MapMode = 5
  Placement = pos=(-21.3,18.635,0) rot=(0,0,1;0rad)
  Support = -> [XY_Plane043]
  Width = 0.23
FEATURE [PartDesign::SubtractiveBox] Box466
  AttacherType = Attacher::AttachEngine3D
  AttachmentOffset = pos=(-21.35,18.635,0.35) rot=(0,0,1;0rad)
  BaseFeature = -> Box471
  Height = 1.55
  Length = 0.5
  MapMode = 5
  Placement = pos=(-21.35,18.635,0.35) rot=(0,0,1;0rad)
  Support = -> [XY_Plane043]
  Width = 0.23
FEATURE [PartDesign::SubtractiveBox] Box447
  AttacherType = Attacher::AttachEngine3D
  AttachmentOffset = pos=(-20.5,18.63,0) rot=(0,0,1;0rad)
  BaseFeature = -> Box466
  Height = 1.635
  Length = 0.5
  MapMode = 5
  Placement = pos=(-20.5,18.63,0) rot=(0,0,1;0rad)
  Support = -> [XY_Plane043]
  Width = 0.25
FEATURE [PartDesign::SubtractiveBox] Box463
  AttacherType = Attacher::AttachEngine3D
  AttachmentOffset = pos=(-21.19,18.635,-0.12) rot=(0,-1,0;0.15708rad)
  BaseFeature = -> Box447
  Height = 0.12
  Length = 0.725
  MapMode = 5
  Placement = pos=(-21.19,18.635,-0.12) rot=(0,-1,0;0.15708rad)
  Support = -> [XY_Plane043]
  Width = 0.25
FEATURE [PartDesign::SubtractiveBox] Box462
  AttacherType = Attacher::AttachEngine3D
  AttachmentOffset = pos=(-21.5005,18.625,0.235) rot=(0,-1,0;0.174533rad)
  BaseFeature = -> Box463
  Height = 0.3
  Length = 0.6605
  MapMode = 5
  Placement = pos=(-21.5005,18.625,0.235) rot=(0,-1,0;0.174533rad)
  Support = -> [XY_Plane043]
  Width = 0.25
FEATURE [PartDesign::Fillet] Fillet117
  Base = -> Box462 [Edge2]
  BaseFeature = -> Box462
  Placement = pos=(-21.5005,18.625,0.235) rot=(0,-1,0;0.174533rad)
  Radius = 0.05
  SupportTransform = false
FEATURE [PartDesign::Fillet] Fillet131
  Base = -> Fillet117 [Edge33]
  BaseFeature = -> Fillet117
  Placement = pos=(-21.5005,18.625,0.235) rot=(0,-1,0;0.174533rad)
  Radius = 0.5
  SupportTransform = false
FEATURE [PartDesign::AdditiveBox] Box436
  AttacherType = Attacher::AttachEngine3D
  AttachmentOffset = pos=(-21.1,18.635,0.305) rot=(0,1,0;0.785398rad)
  BaseFeature = -> Fillet131
  Height = 0.375
  Length = 0.2
  MapMode = 5
  Placement = pos=(-21.1,18.635,0.305) rot=(0,1,0;0.785398rad)
  Support = -> [XY_Plane043]
  Width = 0.23
FEATURE [PartDesign::SubtractiveCylinder] Cylinder098
  Angle = 360
  AttacherType = Attacher::AttachEngine3D
  AttachmentOffset = pos=(-21.055,18.935,0.52) rot=(1,0,0;1.5708rad)
  BaseFeature = -> Box436
  Height = 0.375
  MapMode = 5
  Placement = pos=(-21.055,18.935,0.52) rot=(1,0,0;1.5708rad)
  Radius = 0.205
  Support = -> [XY_Plane043]
FEATURE [PartDesign::SubtractiveBox] Box460
  AttacherType = Attacher::AttachEngine3D
  AttachmentOffset = pos=(-20.95,18.635,0.53) rot=(0,0,1;0rad)
  BaseFeature = -> Cylinder098
  Height = 0.5
  Length = 0.1
  MapMode = 5
  Placement = pos=(-20.95,18.635,0.53) rot=(0,0,1;0rad)
  Support = -> [XY_Plane043]
  Width = 0.23
FEATURE [PartDesign::SubtractiveBox] Box458
  AttacherType = Attacher::AttachEngine3D
  AttachmentOffset = pos=(-21.15,18.635,0.297) rot=(0,-1,0;0.174533rad)
  BaseFeature = -> Box460
  Height = 0.115
  Length = 0.115
  MapMode = 5
  Placement = pos=(-21.15,18.635,0.297) rot=(0,-1,0;0.174533rad)
  Support = -> [XY_Plane043]
  Width = 0.23
FEATURE [PartDesign::Fillet] Fillet111
  Base = -> Box458 [Edge28]
  BaseFeature = -> Box458
  Placement = pos=(-21.15,18.635,0.297) rot=(0,-1,0;0.174533rad)
  Radius = 0.375
  SupportTransform = false
FEATURE [PartDesign::AdditiveBox] Box457
  AttacherType = Attacher::AttachEngine3D
  AttachmentOffset = pos=(-20.7,18.635,1.55) rot=(0,1,0;0.785398rad)
  BaseFeature = -> Fillet111
  Height = 0.375
  Length = 0.23
  MapMode = 5
  Placement = pos=(-20.7,18.635,1.55) rot=(0,1,0;0.785398rad)
  Support = -> [XY_Plane043]
  Width = 0.23
FEATURE [PartDesign::SubtractiveCylinder] Cylinder097
  Angle = 360
  AttacherType = Attacher::AttachEngine3D
  AttachmentOffset = pos=(-20.271,18.635,1.4056) rot=(-1,0,0;1.5708rad)
  BaseFeature = -> Box457
  Height = 0.23
  MapMode = 5
  Placement = pos=(-20.271,18.635,1.4056) rot=(-1,0,0;1.5708rad)
  Radius = 0.23
  Support = -> [XY_Plane043]
FEATURE [PartDesign::AdditiveBox] Box465
  AttacherType = Attacher::AttachEngine3D
  AttachmentOffset = pos=(-20.1,18.635,1.635) rot=(0,0,1;0rad)
  BaseFeature = -> Cylinder097
  Height = 0.265
  Length = 0.23
  MapMode = 5
  Placement = pos=(-20.1,18.635,1.635) rot=(0,0,1;0rad)
  Support = -> [XY_Plane043]
  Width = 0.23
FEATURE [PartDesign::Body] Body045  label="pin045"
  Group = -> [Box471,Box466,Box447,Box463,Box462,Fillet117,Fillet131,Box436,Cylinder098,Box460,Box458,Fillet111,Box457,Cylinder097,Box465]
  Origin = -> Origin049
  Placement = pos=(0,-1,0) rot=(0,0,1;0rad)
  Tip = -> Box465
FEATURE [PartDesign::AdditiveBox] Box472
  AttacherType = Attacher::AttachEngine3D
  AttachmentOffset = pos=(-21.3,18.635,0) rot=(0,0,1;0rad)
  Height = 1.9
  Length = 1.3
  MapMode = 5
  Placement = pos=(-21.3,18.635,0) rot=(0,0,1;0rad)
  Support = -> [XY_Plane044]
  Width = 0.23
FEATURE [PartDesign::SubtractiveBox] Box473
  AttacherType = Attacher::AttachEngine3D
  AttachmentOffset = pos=(-21.35,18.635,0.35) rot=(0,0,1;0rad)
  BaseFeature = -> Box472
  Height = 1.55
  Length = 0.5
  MapMode = 5
  Placement = pos=(-21.35,18.635,0.35) rot=(0,0,1;0rad)
  Support = -> [XY_Plane044]
  Width = 0.23
FEATURE [PartDesign::SubtractiveBox] Box449
  AttacherType = Attacher::AttachEngine3D
  AttachmentOffset = pos=(-20.5,18.63,0) rot=(0,0,1;0rad)
  BaseFeature = -> Box473
  Height = 1.635
  Length = 0.5
  MapMode = 5
  Placement = pos=(-20.5,18.63,0) rot=(0,0,1;0rad)
  Support = -> [XY_Plane044]
  Width = 0.25
FEATURE [PartDesign::SubtractiveBox] Box441
  AttacherType = Attacher::AttachEngine3D
  AttachmentOffset = pos=(-21.19,18.635,-0.12) rot=(0,-1,0;0.15708rad)
  BaseFeature = -> Box449
  Height = 0.12
  Length = 0.725
  MapMode = 5
  Placement = pos=(-21.19,18.635,-0.12) rot=(0,-1,0;0.15708rad)
  Support = -> [XY_Plane044]
  Width = 0.25
FEATURE [PartDesign::SubtractiveBox] Box461
  AttacherType = Attacher::AttachEngine3D
  AttachmentOffset = pos=(-21.5005,18.625,0.235) rot=(0,-1,0;0.174533rad)
  BaseFeature = -> Box441
  Height = 0.3
  Length = 0.6605
  MapMode = 5
  Placement = pos=(-21.5005,18.625,0.235) rot=(0,-1,0;0.174533rad)
  Support = -> [XY_Plane044]
  Width = 0.25
FEATURE [PartDesign::Fillet] Fillet133
  Base = -> Box461 [Edge2]
  BaseFeature = -> Box461
  Placement = pos=(-21.5005,18.625,0.235) rot=(0,-1,0;0.174533rad)
  Radius = 0.05
  SupportTransform = false
FEATURE [PartDesign::Fillet] Fillet108
  Base = -> Fillet133 [Edge33]
  BaseFeature = -> Fillet133
  Placement = pos=(-21.5005,18.625,0.235) rot=(0,-1,0;0.174533rad)
  Radius = 0.5
  SupportTransform = false
FEATURE [PartDesign::AdditiveBox] Box373
  AttacherType = Attacher::AttachEngine3D
  AttachmentOffset = pos=(-21.1,18.635,0.305) rot=(0,1,0;0.785398rad)
  BaseFeature = -> Fillet108
  Height = 0.375
  Length = 0.2
  MapMode = 5
  Placement = pos=(-21.1,18.635,0.305) rot=(0,1,0;0.785398rad)
  Support = -> [XY_Plane044]
  Width = 0.23
FEATURE [PartDesign::SubtractiveCylinder] Cylinder088
  Angle = 360
  AttacherType = Attacher::AttachEngine3D
  AttachmentOffset = pos=(-21.055,18.935,0.52) rot=(1,0,0;1.5708rad)
  BaseFeature = -> Box373
  Height = 0.375
  MapMode = 5
  Placement = pos=(-21.055,18.935,0.52) rot=(1,0,0;1.5708rad)
  Radius = 0.205
  Support = -> [XY_Plane044]
FEATURE [PartDesign::SubtractiveBox] Box424
  AttacherType = Attacher::AttachEngine3D
  AttachmentOffset = pos=(-20.95,18.635,0.53) rot=(0,0,1;0rad)
  BaseFeature = -> Cylinder088
  Height = 0.5
  Length = 0.1
  MapMode = 5
  Placement = pos=(-20.95,18.635,0.53) rot=(0,0,1;0rad)
  Support = -> [XY_Plane044]
  Width = 0.23
FEATURE [PartDesign::SubtractiveBox] Box409
  AttacherType = Attacher::AttachEngine3D
  AttachmentOffset = pos=(-21.15,18.635,0.297) rot=(0,-1,0;0.174533rad)
  BaseFeature = -> Box424
  Height = 0.115
  Length = 0.115
  MapMode = 5
  Placement = pos=(-21.15,18.635,0.297) rot=(0,-1,0;0.174533rad)
  Support = -> [XY_Plane044]
  Width = 0.23
FEATURE [PartDesign::Fillet] Fillet137
  Base = -> Box409 [Edge28]
  BaseFeature = -> Box409
  Placement = pos=(-21.15,18.635,0.297) rot=(0,-1,0;0.174533rad)
  Radius = 0.375
  SupportTransform = false
FEATURE [PartDesign::AdditiveBox] Box444
  AttacherType = Attacher::AttachEngine3D
  AttachmentOffset = pos=(-20.7,18.635,1.55) rot=(0,1,0;0.785398rad)
  BaseFeature = -> Fillet137
  Height = 0.375
  Length = 0.23
  MapMode = 5
  Placement = pos=(-20.7,18.635,1.55) rot=(0,1,0;0.785398rad)
  Support = -> [XY_Plane044]
  Width = 0.23
FEATURE [PartDesign::SubtractiveCylinder] Cylinder087
  Angle = 360
  AttacherType = Attacher::AttachEngine3D
  AttachmentOffset = pos=(-20.271,18.635,1.4056) rot=(-1,0,0;1.5708rad)
  BaseFeature = -> Box444
  Height = 0.23
  MapMode = 5
  Placement = pos=(-20.271,18.635,1.4056) rot=(-1,0,0;1.5708rad)
  Radius = 0.23
  Support = -> [XY_Plane044]
FEATURE [PartDesign::AdditiveBox] Box454
  AttacherType = Attacher::AttachEngine3D
  AttachmentOffset = pos=(-20.1,18.635,1.635) rot=(0,0,1;0rad)
  BaseFeature = -> Cylinder087
  Height = 0.265
  Length = 0.23
  MapMode = 5
  Placement = pos=(-20.1,18.635,1.635) rot=(0,0,1;0rad)
  Support = -> [XY_Plane044]
  Width = 0.23
FEATURE [PartDesign::Body] Body039  label="pin039"
  Group = -> [Box472,Box473,Box449,Box441,Box461,Fillet133,Fillet108,Box373,Cylinder088,Box424,Box409,Fillet137,Box444,Cylinder087,Box454]
  Origin = -> Origin043
  Tip = -> Box454
FEATURE [PartDesign::AdditiveBox] Box474
  AttacherType = Attacher::AttachEngine3D
  AttachmentOffset = pos=(-21.1,18.635,0.305) rot=(0,1,0;0.785398rad)
  BaseFeature = -> Fillet110
  Height = 0.375
  Length = 0.2
  MapMode = 5
  Placement = pos=(-21.1,18.635,0.305) rot=(0,1,0;0.785398rad)
  Support = -> [XY_Plane041]
  Width = 0.23
FEATURE [PartDesign::SubtractiveCylinder] Cylinder080
  Angle = 360
  AttacherType = Attacher::AttachEngine3D
  AttachmentOffset = pos=(-21.055,18.935,0.52) rot=(1,0,0;1.5708rad)
  BaseFeature = -> Box474
  Height = 0.375
  MapMode = 5
  Placement = pos=(-21.055,18.935,0.52) rot=(1,0,0;1.5708rad)
  Radius = 0.205
  Support = -> [XY_Plane041]
FEATURE [PartDesign::SubtractiveBox] Box390
  AttacherType = Attacher::AttachEngine3D
  AttachmentOffset = pos=(-20.95,18.635,0.53) rot=(0,0,1;0rad)
  BaseFeature = -> Cylinder080
  Height = 0.5
  Length = 0.1
  MapMode = 5
  Placement = pos=(-20.95,18.635,0.53) rot=(0,0,1;0rad)
  Support = -> [XY_Plane041]
  Width = 0.23
FEATURE [PartDesign::SubtractiveBox] Box394
  AttacherType = Attacher::AttachEngine3D
  AttachmentOffset = pos=(-21.15,18.635,0.297) rot=(0,-1,0;0.174533rad)
  BaseFeature = -> Box390
  Height = 0.115
  Length = 0.115
  MapMode = 5
  Placement = pos=(-21.15,18.635,0.297) rot=(0,-1,0;0.174533rad)
  Support = -> [XY_Plane041]
  Width = 0.23
FEATURE [PartDesign::Fillet] Fillet109
  Base = -> Box394 [Edge28]
  BaseFeature = -> Box394
  Placement = pos=(-21.15,18.635,0.297) rot=(0,-1,0;0.174533rad)
  Radius = 0.375
  SupportTransform = false
FEATURE [PartDesign::AdditiveBox] Box381
  AttacherType = Attacher::AttachEngine3D
  AttachmentOffset = pos=(-20.7,18.635,1.55) rot=(0,1,0;0.785398rad)
  BaseFeature = -> Fillet109
  Height = 0.375
  Length = 0.23
  MapMode = 5
  Placement = pos=(-20.7,18.635,1.55) rot=(0,1,0;0.785398rad)
  Support = -> [XY_Plane041]
  Width = 0.23
FEATURE [PartDesign::SubtractiveCylinder] Cylinder079
  Angle = 360
  AttacherType = Attacher::AttachEngine3D
  AttachmentOffset = pos=(-20.271,18.635,1.4056) rot=(-1,0,0;1.5708rad)
  BaseFeature = -> Box381
  Height = 0.23
  MapMode = 5
  Placement = pos=(-20.271,18.635,1.4056) rot=(-1,0,0;1.5708rad)
  Radius = 0.23
  Support = -> [XY_Plane041]
FEATURE [PartDesign::AdditiveBox] Box385
  AttacherType = Attacher::AttachEngine3D
  AttachmentOffset = pos=(-20.1,18.635,1.635) rot=(0,0,1;0rad)
  BaseFeature = -> Cylinder079
  Height = 0.265
  Length = 0.23
  MapMode = 5
  Placement = pos=(-20.1,18.635,1.635) rot=(0,0,1;0rad)
  Support = -> [XY_Plane041]
  Width = 0.23
FEATURE [PartDesign::Body] Body040  label="pin040"
  Group = -> [Box404,Box382,Box470,Box368,Box388,Fillet120,Fillet110,Box474,Cylinder080,Box390,Box394,Fillet109,Box381,Cylinder079,Box385]
  Origin = -> Origin051
  Placement = pos=(0,-2.5,0) rot=(0,0,1;0rad)
  Tip = -> Box385
FEATURE [PartDesign::SubtractiveBox] Box476
  AttacherType = Attacher::AttachEngine3D
  AttachmentOffset = pos=(-20.5,18.63,0) rot=(0,0,1;0rad)
  BaseFeature = -> Box396
  Height = 1.635
  Length = 0.5
  MapMode = 5
  Placement = pos=(-20.5,18.63,0) rot=(0,0,1;0rad)
  Support = -> [XY_Plane042]
  Width = 0.25
FEATURE [PartDesign::SubtractiveBox] Box464
  AttacherType = Attacher::AttachEngine3D
  AttachmentOffset = pos=(-21.19,18.635,-0.12) rot=(0,-1,0;0.15708rad)
  BaseFeature = -> Box476
  Height = 0.12
  Length = 0.725
  MapMode = 5
  Placement = pos=(-21.19,18.635,-0.12) rot=(0,-1,0;0.15708rad)
  Support = -> [XY_Plane042]
  Width = 0.25
FEATURE [PartDesign::SubtractiveBox] Box395
  AttacherType = Attacher::AttachEngine3D
  AttachmentOffset = pos=(-21.5005,18.625,0.235) rot=(0,-1,0;0.174533rad)
  BaseFeature = -> Box464
  Height = 0.3
  Length = 0.6605
  MapMode = 5
  Placement = pos=(-21.5005,18.625,0.235) rot=(0,-1,0;0.174533rad)
  Support = -> [XY_Plane042]
  Width = 0.25
FEATURE [PartDesign::Fillet] Fillet125
  Base = -> Box395 [Edge2]
  BaseFeature = -> Box395
  Placement = pos=(-21.5005,18.625,0.235) rot=(0,-1,0;0.174533rad)
  Radius = 0.05
  SupportTransform = false
FEATURE [PartDesign::Fillet] Fillet118
  Base = -> Fillet125 [Edge33]
  BaseFeature = -> Fillet125
  Placement = pos=(-21.5005,18.625,0.235) rot=(0,-1,0;0.174533rad)
  Radius = 0.5
  SupportTransform = false
FEATURE [PartDesign::AdditiveBox] Box477
  AttacherType = Attacher::AttachEngine3D
  AttachmentOffset = pos=(-21.1,18.635,0.305) rot=(0,1,0;0.785398rad)
  BaseFeature = -> Fillet119
  Height = 0.375
  Length = 0.2
  MapMode = 5
  Placement = pos=(-21.1,18.635,0.305) rot=(0,1,0;0.785398rad)
  Support = -> [XY_Plane045]
  Width = 0.23
FEATURE [PartDesign::SubtractiveCylinder] Cylinder099
  Angle = 360
  AttacherType = Attacher::AttachEngine3D
  AttachmentOffset = pos=(-21.055,18.935,0.52) rot=(1,0,0;1.5708rad)
  BaseFeature = -> Box477
  Height = 0.375
  MapMode = 5
  Placement = pos=(-21.055,18.935,0.52) rot=(1,0,0;1.5708rad)
  Radius = 0.205
  Support = -> [XY_Plane045]
FEATURE [PartDesign::SubtractiveBox] Box393
  AttacherType = Attacher::AttachEngine3D
  AttachmentOffset = pos=(-20.95,18.635,0.53) rot=(0,0,1;0rad)
  BaseFeature = -> Cylinder099
  Height = 0.5
  Length = 0.1
  MapMode = 5
  Placement = pos=(-20.95,18.635,0.53) rot=(0,0,1;0rad)
  Support = -> [XY_Plane045]
  Width = 0.23
FEATURE [PartDesign::SubtractiveBox] Box379
  AttacherType = Attacher::AttachEngine3D
  AttachmentOffset = pos=(-21.15,18.635,0.297) rot=(0,-1,0;0.174533rad)
  BaseFeature = -> Box393
  Height = 0.115
  Length = 0.115
  MapMode = 5
  Placement = pos=(-21.15,18.635,0.297) rot=(0,-1,0;0.174533rad)
  Support = -> [XY_Plane045]
  Width = 0.23
FEATURE [PartDesign::Fillet] Fillet113
  Base = -> Box379 [Edge28]
  BaseFeature = -> Box379
  Placement = pos=(-21.15,18.635,0.297) rot=(0,-1,0;0.174533rad)
  Radius = 0.375
  SupportTransform = false
FEATURE [PartDesign::AdditiveBox] Box467
  AttacherType = Attacher::AttachEngine3D
  AttachmentOffset = pos=(-20.7,18.635,1.55) rot=(0,1,0;0.785398rad)
  BaseFeature = -> Fillet113
  Height = 0.375
  Length = 0.23
  MapMode = 5
  Placement = pos=(-20.7,18.635,1.55) rot=(0,1,0;0.785398rad)
  Support = -> [XY_Plane045]
  Width = 0.23
FEATURE [PartDesign::SubtractiveCylinder] Cylinder081
  Angle = 360
  AttacherType = Attacher::AttachEngine3D
  AttachmentOffset = pos=(-20.271,18.635,1.4056) rot=(-1,0,0;1.5708rad)
  BaseFeature = -> Box467
  Height = 0.23
  MapMode = 5
  Placement = pos=(-20.271,18.635,1.4056) rot=(-1,0,0;1.5708rad)
  Radius = 0.23
  Support = -> [XY_Plane045]
FEATURE [PartDesign::AdditiveBox] Box392
  AttacherType = Attacher::AttachEngine3D
  AttachmentOffset = pos=(-20.1,18.635,1.635) rot=(0,0,1;0rad)
  BaseFeature = -> Cylinder081
  Height = 0.265
  Length = 0.23
  MapMode = 5
  Placement = pos=(-20.1,18.635,1.635) rot=(0,0,1;0rad)
  Support = -> [XY_Plane045]
  Width = 0.23
FEATURE [PartDesign::Body] Body038  label="pin038"
  Group = -> [Box380,Box391,Box468,Box389,Box386,Fillet116,Fillet119,Box477,Cylinder099,Box393,Box379,Fillet113,Box467,Cylinder081,Box392]
  Origin = -> Origin045
  Placement = pos=(0,-2,0) rot=(0,0,1;0rad)
  Tip = -> Box392
FEATURE [PartDesign::AdditiveBox] Box479
  AttacherType = Attacher::AttachEngine3D
  AttachmentOffset = pos=(-21.1,18.635,0.305) rot=(0,1,0;0.785398rad)
  BaseFeature = -> Fillet118
  Height = 0.375
  Length = 0.2
  MapMode = 5
  Placement = pos=(-21.1,18.635,0.305) rot=(0,1,0;0.785398rad)
  Support = -> [XY_Plane042]
  Width = 0.23
FEATURE [PartDesign::SubtractiveCylinder] Cylinder096
  Angle = 360
  AttacherType = Attacher::AttachEngine3D
  AttachmentOffset = pos=(-21.055,18.935,0.52) rot=(1,0,0;1.5708rad)
  BaseFeature = -> Box479
  Height = 0.375
  MapMode = 5
  Placement = pos=(-21.055,18.935,0.52) rot=(1,0,0;1.5708rad)
  Radius = 0.205
  Support = -> [XY_Plane042]
FEATURE [PartDesign::SubtractiveBox] Box469
  AttacherType = Attacher::AttachEngine3D
  AttachmentOffset = pos=(-20.95,18.635,0.53) rot=(0,0,1;0rad)
  BaseFeature = -> Cylinder096
  Height = 0.5
  Length = 0.1
  MapMode = 5
  Placement = pos=(-20.95,18.635,0.53) rot=(0,0,1;0rad)
  Support = -> [XY_Plane042]
  Width = 0.23
FEATURE [PartDesign::SubtractiveBox] Box475
  AttacherType = Attacher::AttachEngine3D
  AttachmentOffset = pos=(-21.15,18.635,0.297) rot=(0,-1,0;0.174533rad)
  BaseFeature = -> Box469
  Height = 0.115
  Length = 0.115
  MapMode = 5
  Placement = pos=(-21.15,18.635,0.297) rot=(0,-1,0;0.174533rad)
  Support = -> [XY_Plane042]
  Width = 0.23
FEATURE [PartDesign::Fillet] Fillet126
  Base = -> Box475 [Edge28]
  BaseFeature = -> Box475
  Placement = pos=(-21.15,18.635,0.297) rot=(0,-1,0;0.174533rad)
  Radius = 0.375
  SupportTransform = false
FEATURE [PartDesign::AdditiveBox] Box478
  AttacherType = Attacher::AttachEngine3D
  AttachmentOffset = pos=(-20.7,18.635,1.55) rot=(0,1,0;0.785398rad)
  BaseFeature = -> Fillet126
  Height = 0.375
  Length = 0.23
  MapMode = 5
  Placement = pos=(-20.7,18.635,1.55) rot=(0,1,0;0.785398rad)
  Support = -> [XY_Plane042]
  Width = 0.23
FEATURE [PartDesign::SubtractiveCylinder] Cylinder078
  Angle = 360
  AttacherType = Attacher::AttachEngine3D
  AttachmentOffset = pos=(-20.271,18.635,1.4056) rot=(-1,0,0;1.5708rad)
  BaseFeature = -> Box478
  Height = 0.23
  MapMode = 5
  Placement = pos=(-20.271,18.635,1.4056) rot=(-1,0,0;1.5708rad)
  Radius = 0.23
  Support = -> [XY_Plane042]
FEATURE [PartDesign::AdditiveBox] Box480
  AttacherType = Attacher::AttachEngine3D
  AttachmentOffset = pos=(-20.1,18.635,1.635) rot=(0,0,1;0rad)
  BaseFeature = -> Cylinder078
  Height = 0.265
  Length = 0.23
  MapMode = 5
  Placement = pos=(-20.1,18.635,1.635) rot=(0,0,1;0rad)
  Support = -> [XY_Plane042]
  Width = 0.23
FEATURE [PartDesign::Body] Body041  label="pin041"
  Group = -> [Box402,Box396,Box476,Box464,Box395,Fillet125,Fillet118,Box479,Cylinder096,Box469,Box475,Fillet126,Box478,Cylinder078,Box480]
  Origin = -> Origin047
  Placement = pos=(0,-1.5,0) rot=(0,0,1;0rad)
  Tip = -> Box480
FEATURE [App::Part] Part003  label="Pin-set004"
  Group = -> [Body039,Body037,Body045,Body041,Body038,Body040,Body047,Body042,Body044,Body043,Body046,Body048]
  Origin = -> Origin040
  Placement = pos=(0,-18,0) rot=(0,0,1;0rad)
FEATURE [PartDesign::AdditiveBox] Box500
  AttacherType = Attacher::AttachEngine3D
  AttachmentOffset = pos=(-21.3,18.635,0) rot=(0,0,1;0rad)
  Height = 1.9
  Length = 1.3
  MapMode = 5
  Placement = pos=(-21.3,18.635,0) rot=(0,0,1;0rad)
  Support = -> [XY_Plane053]
  Width = 0.23
FEATURE [PartDesign::SubtractiveBox] Box485
  AttacherType = Attacher::AttachEngine3D
  AttachmentOffset = pos=(-21.35,18.635,0.35) rot=(0,0,1;0rad)
  BaseFeature = -> Box500
  Height = 1.55
  Length = 0.5
  MapMode = 5
  Placement = pos=(-21.35,18.635,0.35) rot=(0,0,1;0rad)
  Support = -> [XY_Plane053]
  Width = 0.23
FEATURE [PartDesign::AdditiveBox] Box504
  AttacherType = Attacher::AttachEngine3D
  AttachmentOffset = pos=(-21.3,18.635,0) rot=(0,0,1;0rad)
  Height = 1.9
  Length = 1.3
  MapMode = 5
  Placement = pos=(-21.3,18.635,0) rot=(0,0,1;0rad)
  Support = -> [XY_Plane055]
  Width = 0.23
FEATURE [PartDesign::SubtractiveBox] Box487
  AttacherType = Attacher::AttachEngine3D
  AttachmentOffset = pos=(-21.35,18.635,0.35) rot=(0,0,1;0rad)
  BaseFeature = -> Box504
  Height = 1.55
  Length = 0.5
  MapMode = 5
  Placement = pos=(-21.35,18.635,0.35) rot=(0,0,1;0rad)
  Support = -> [XY_Plane055]
  Width = 0.23
FEATURE [PartDesign::AdditiveBox] Box511
  AttacherType = Attacher::AttachEngine3D
  AttachmentOffset = pos=(-21.3,18.635,0) rot=(0,0,1;0rad)
  Height = 1.9
  Length = 1.3
  MapMode = 5
  Placement = pos=(-21.3,18.635,0) rot=(0,0,1;0rad)
  Support = -> [XY_Plane062]
  Width = 0.23
FEATURE [PartDesign::SubtractiveBox] Box519
  AttacherType = Attacher::AttachEngine3D
  AttachmentOffset = pos=(-21.35,18.635,0.35) rot=(0,0,1;0rad)
  BaseFeature = -> Box511
  Height = 1.55
  Length = 0.5
  MapMode = 5
  Placement = pos=(-21.35,18.635,0.35) rot=(0,0,1;0rad)
  Support = -> [XY_Plane062]
  Width = 0.23
FEATURE [PartDesign::SubtractiveBox] Box509
  AttacherType = Attacher::AttachEngine3D
  AttachmentOffset = pos=(-20.5,18.63,0) rot=(0,0,1;0rad)
  BaseFeature = -> Box519
  Height = 1.635
  Length = 0.5
  MapMode = 5
  Placement = pos=(-20.5,18.63,0) rot=(0,0,1;0rad)
  Support = -> [XY_Plane062]
  Width = 0.25
FEATURE [PartDesign::SubtractiveBox] Box513
  AttacherType = Attacher::AttachEngine3D
  AttachmentOffset = pos=(-21.19,18.635,-0.12) rot=(0,-1,0;0.15708rad)
  BaseFeature = -> Box509
  Height = 0.12
  Length = 0.725
  MapMode = 5
  Placement = pos=(-21.19,18.635,-0.12) rot=(0,-1,0;0.15708rad)
  Support = -> [XY_Plane062]
  Width = 0.25
FEATURE [PartDesign::SubtractiveBox] Box518
  AttacherType = Attacher::AttachEngine3D
  AttachmentOffset = pos=(-21.5005,18.625,0.235) rot=(0,-1,0;0.174533rad)
  BaseFeature = -> Box513
  Height = 0.3
  Length = 0.6605
  MapMode = 5
  Placement = pos=(-21.5005,18.625,0.235) rot=(0,-1,0;0.174533rad)
  Support = -> [XY_Plane062]
  Width = 0.25
FEATURE [PartDesign::AdditiveBox] Box525
  AttacherType = Attacher::AttachEngine3D
  AttachmentOffset = pos=(-21.3,18.635,0) rot=(0,0,1;0rad)
  Height = 1.9
  Length = 1.3
  MapMode = 5
  Placement = pos=(-21.3,18.635,0) rot=(0,0,1;0rad)
  Support = -> [XY_Plane059]
  Width = 0.23
FEATURE [PartDesign::SubtractiveBox] Box517
  AttacherType = Attacher::AttachEngine3D
  AttachmentOffset = pos=(-21.35,18.635,0.35) rot=(0,0,1;0rad)
  BaseFeature = -> Box525
  Height = 1.55
  Length = 0.5
  MapMode = 5
  Placement = pos=(-21.35,18.635,0.35) rot=(0,0,1;0rad)
  Support = -> [XY_Plane059]
  Width = 0.23
FEATURE [PartDesign::SubtractiveBox] Box505
  AttacherType = Attacher::AttachEngine3D
  AttachmentOffset = pos=(-20.5,18.63,0) rot=(0,0,1;0rad)
  BaseFeature = -> Box517
  Height = 1.635
  Length = 0.5
  MapMode = 5
  Placement = pos=(-20.5,18.63,0) rot=(0,0,1;0rad)
  Support = -> [XY_Plane059]
  Width = 0.25
FEATURE [PartDesign::SubtractiveBox] Box507
  AttacherType = Attacher::AttachEngine3D
  AttachmentOffset = pos=(-21.19,18.635,-0.12) rot=(0,-1,0;0.15708rad)
  BaseFeature = -> Box505
  Height = 0.12
  Length = 0.725
  MapMode = 5
  Placement = pos=(-21.19,18.635,-0.12) rot=(0,-1,0;0.15708rad)
  Support = -> [XY_Plane059]
  Width = 0.25
FEATURE [PartDesign::AdditiveBox] Box529
  AttacherType = Attacher::AttachEngine3D
  AttachmentOffset = pos=(-21.3,18.635,0) rot=(0,0,1;0rad)
  Height = 1.9
  Length = 1.3
  MapMode = 5
  Placement = pos=(-21.3,18.635,0) rot=(0,0,1;0rad)
  Support = -> [XY_Plane054]
  Width = 0.23
FEATURE [PartDesign::SubtractiveBox] Box530
  AttacherType = Attacher::AttachEngine3D
  AttachmentOffset = pos=(-21.35,18.635,0.35) rot=(0,0,1;0rad)
  BaseFeature = -> Box529
  Height = 1.55
  Length = 0.5
  MapMode = 5
  Placement = pos=(-21.35,18.635,0.35) rot=(0,0,1;0rad)
  Support = -> [XY_Plane054]
  Width = 0.23
FEATURE [PartDesign::SubtractiveBox] Box488
  AttacherType = Attacher::AttachEngine3D
  AttachmentOffset = pos=(-20.5,18.63,0) rot=(0,0,1;0rad)
  BaseFeature = -> Box530
  Height = 1.635
  Length = 0.5
  MapMode = 5
  Placement = pos=(-20.5,18.63,0) rot=(0,0,1;0rad)
  Support = -> [XY_Plane054]
  Width = 0.25
FEATURE [PartDesign::SubtractiveBox] Box499
  AttacherType = Attacher::AttachEngine3D
  AttachmentOffset = pos=(-21.19,18.635,-0.12) rot=(0,-1,0;0.15708rad)
  BaseFeature = -> Box488
  Height = 0.12
  Length = 0.725
  MapMode = 5
  Placement = pos=(-21.19,18.635,-0.12) rot=(0,-1,0;0.15708rad)
  Support = -> [XY_Plane054]
  Width = 0.25
FEATURE [PartDesign::SubtractiveBox] Box498
  AttacherType = Attacher::AttachEngine3D
  AttachmentOffset = pos=(-21.5005,18.625,0.235) rot=(0,-1,0;0.174533rad)
  BaseFeature = -> Box499
  Height = 0.3
  Length = 0.6605
  MapMode = 5
  Placement = pos=(-21.5005,18.625,0.235) rot=(0,-1,0;0.174533rad)
  Support = -> [XY_Plane054]
  Width = 0.25
FEATURE [PartDesign::AdditiveBox] Box535
  AttacherType = Attacher::AttachEngine3D
  AttachmentOffset = pos=(-21.3,18.635,0) rot=(0,0,1;0rad)
  Height = 1.9
  Length = 1.3
  MapMode = 5
  Placement = pos=(-21.3,18.635,0) rot=(0,0,1;0rad)
  Support = -> [XY_Plane061]
  Width = 0.23
FEATURE [PartDesign::SubtractiveBox] Box536
  AttacherType = Attacher::AttachEngine3D
  AttachmentOffset = pos=(-21.35,18.635,0.35) rot=(0,0,1;0rad)
  BaseFeature = -> Box535
  Height = 1.55
  Length = 0.5
  MapMode = 5
  Placement = pos=(-21.35,18.635,0.35) rot=(0,0,1;0rad)
  Support = -> [XY_Plane061]
  Width = 0.23
FEATURE [PartDesign::SubtractiveBox] Box521
  AttacherType = Attacher::AttachEngine3D
  AttachmentOffset = pos=(-20.5,18.63,0) rot=(0,0,1;0rad)
  BaseFeature = -> Box536
  Height = 1.635
  Length = 0.5
  MapMode = 5
  Placement = pos=(-20.5,18.63,0) rot=(0,0,1;0rad)
  Support = -> [XY_Plane061]
  Width = 0.25
FEATURE [PartDesign::AdditiveBox] Box537
  AttacherType = Attacher::AttachEngine3D
  AttachmentOffset = pos=(-21.3,18.635,0) rot=(0,0,1;0rad)
  Height = 1.9
  Length = 1.3
  MapMode = 5
  Placement = pos=(-21.3,18.635,0) rot=(0,0,1;0rad)
  Support = -> [XY_Plane064]
  Width = 0.23
FEATURE [PartDesign::AdditiveBox] Box541
  AttacherType = Attacher::AttachEngine3D
  AttachmentOffset = pos=(-21.3,18.635,0) rot=(0,0,1;0rad)
  Height = 1.9
  Length = 1.3
  MapMode = 5
  Placement = pos=(-21.3,18.635,0) rot=(0,0,1;0rad)
  Support = -> [XY_Plane063]
  Width = 0.23
FEATURE [PartDesign::SubtractiveBox] Box545
  AttacherType = Attacher::AttachEngine3D
  AttachmentOffset = pos=(-21.19,18.635,-0.12) rot=(0,-1,0;0.15708rad)
  BaseFeature = -> Box521
  Height = 0.12
  Length = 0.725
  MapMode = 5
  Placement = pos=(-21.19,18.635,-0.12) rot=(0,-1,0;0.15708rad)
  Support = -> [XY_Plane061]
  Width = 0.25
FEATURE [PartDesign::SubtractiveBox] Box547
  AttacherType = Attacher::AttachEngine3D
  AttachmentOffset = pos=(-21.5005,18.625,0.235) rot=(0,-1,0;0.174533rad)
  BaseFeature = -> Box545
  Height = 0.3
  Length = 0.6605
  MapMode = 5
  Placement = pos=(-21.5005,18.625,0.235) rot=(0,-1,0;0.174533rad)
  Support = -> [XY_Plane061]
  Width = 0.25
FEATURE [PartDesign::SubtractiveBox] Box550
  AttacherType = Attacher::AttachEngine3D
  AttachmentOffset = pos=(-21.35,18.635,0.35) rot=(0,0,1;0rad)
  BaseFeature = -> Box537
  Height = 1.55
  Length = 0.5
  MapMode = 5
  Placement = pos=(-21.35,18.635,0.35) rot=(0,0,1;0rad)
  Support = -> [XY_Plane064]
  Width = 0.23
FEATURE [PartDesign::AdditiveBox] Box551
  AttacherType = Attacher::AttachEngine3D
  AttachmentOffset = pos=(-21.3,18.635,0) rot=(0,0,1;0rad)
  Height = 1.9
  Length = 1.3
  MapMode = 5
  Placement = pos=(-21.3,18.635,0) rot=(0,0,1;0rad)
  Support = -> [XY_Plane056]
  Width = 0.23
FEATURE [PartDesign::SubtractiveBox] Box496
  AttacherType = Attacher::AttachEngine3D
  AttachmentOffset = pos=(-21.35,18.635,0.35) rot=(0,0,1;0rad)
  BaseFeature = -> Box551
  Height = 1.55
  Length = 0.5
  MapMode = 5
  Placement = pos=(-21.35,18.635,0.35) rot=(0,0,1;0rad)
  Support = -> [XY_Plane056]
  Width = 0.23
FEATURE [PartDesign::SubtractiveBox] Box553
  AttacherType = Attacher::AttachEngine3D
  AttachmentOffset = pos=(-21.35,18.635,0.35) rot=(0,0,1;0rad)
  BaseFeature = -> Box541
  Height = 1.55
  Length = 0.5
  MapMode = 5
  Placement = pos=(-21.35,18.635,0.35) rot=(0,0,1;0rad)
  Support = -> [XY_Plane063]
  Width = 0.23
FEATURE [PartDesign::SubtractiveBox] Box527
  AttacherType = Attacher::AttachEngine3D
  AttachmentOffset = pos=(-20.5,18.63,0) rot=(0,0,1;0rad)
  BaseFeature = -> Box553
  Height = 1.635
  Length = 0.5
  MapMode = 5
  Placement = pos=(-20.5,18.63,0) rot=(0,0,1;0rad)
  Support = -> [XY_Plane063]
  Width = 0.25
FEATURE [PartDesign::Fillet] Fillet157
  Base = -> Box498 [Edge2]
  BaseFeature = -> Box498
  Placement = pos=(-21.5005,18.625,0.235) rot=(0,-1,0;0.174533rad)
  Radius = 0.05
  SupportTransform = false
FEATURE [PartDesign::Fillet] Fillet165
  Base = -> Box518 [Edge2]
  BaseFeature = -> Box518
  Placement = pos=(-21.5005,18.625,0.235) rot=(0,-1,0;0.174533rad)
  Radius = 0.05
  SupportTransform = false
FEATURE [PartDesign::Fillet] Fillet147
  Base = -> Fillet165 [Edge33]
  BaseFeature = -> Fillet165
  Placement = pos=(-21.5005,18.625,0.235) rot=(0,-1,0;0.174533rad)
  Radius = 0.5
  SupportTransform = false
FEATURE [PartDesign::AdditiveBox] Box497
  AttacherType = Attacher::AttachEngine3D
  AttachmentOffset = pos=(-21.1,18.635,0.305) rot=(0,1,0;0.785398rad)
  BaseFeature = -> Fillet147
  Height = 0.375
  Length = 0.2
  MapMode = 5
  Placement = pos=(-21.1,18.635,0.305) rot=(0,1,0;0.785398rad)
  Support = -> [XY_Plane062]
  Width = 0.23
FEATURE [PartDesign::SubtractiveCylinder] Cylinder104
  Angle = 360
  AttacherType = Attacher::AttachEngine3D
  AttachmentOffset = pos=(-21.055,18.935,0.52) rot=(1,0,0;1.5708rad)
  BaseFeature = -> Box497
  Height = 0.375
  MapMode = 5
  Placement = pos=(-21.055,18.935,0.52) rot=(1,0,0;1.5708rad)
  Radius = 0.205
  Support = -> [XY_Plane062]
FEATURE [PartDesign::SubtractiveBox] Box528
  AttacherType = Attacher::AttachEngine3D
  AttachmentOffset = pos=(-20.95,18.635,0.53) rot=(0,0,1;0rad)
  BaseFeature = -> Cylinder104
  Height = 0.5
  Length = 0.1
  MapMode = 5
  Placement = pos=(-20.95,18.635,0.53) rot=(0,0,1;0rad)
  Support = -> [XY_Plane062]
  Width = 0.23
FEATURE [PartDesign::SubtractiveBox] Box503
  AttacherType = Attacher::AttachEngine3D
  AttachmentOffset = pos=(-21.15,18.635,0.297) rot=(0,-1,0;0.174533rad)
  BaseFeature = -> Box528
  Height = 0.115
  Length = 0.115
  MapMode = 5
  Placement = pos=(-21.15,18.635,0.297) rot=(0,-1,0;0.174533rad)
  Support = -> [XY_Plane062]
  Width = 0.23
FEATURE [PartDesign::Fillet] Fillet153
  Base = -> Box503 [Edge28]
  BaseFeature = -> Box503
  Placement = pos=(-21.15,18.635,0.297) rot=(0,-1,0;0.174533rad)
  Radius = 0.375
  SupportTransform = false
FEATURE [PartDesign::AdditiveBox] Box512
  AttacherType = Attacher::AttachEngine3D
  AttachmentOffset = pos=(-20.7,18.635,1.55) rot=(0,1,0;0.785398rad)
  BaseFeature = -> Fillet153
  Height = 0.375
  Length = 0.23
  MapMode = 5
  Placement = pos=(-20.7,18.635,1.55) rot=(0,1,0;0.785398rad)
  Support = -> [XY_Plane062]
  Width = 0.23
FEATURE [PartDesign::SubtractiveCylinder] Cylinder102
  Angle = 360
  AttacherType = Attacher::AttachEngine3D
  AttachmentOffset = pos=(-20.271,18.635,1.4056) rot=(-1,0,0;1.5708rad)
  BaseFeature = -> Box512
  Height = 0.23
  MapMode = 5
  Placement = pos=(-20.271,18.635,1.4056) rot=(-1,0,0;1.5708rad)
  Radius = 0.23
  Support = -> [XY_Plane062]
FEATURE [PartDesign::AdditiveBox] Box522
  AttacherType = Attacher::AttachEngine3D
  AttachmentOffset = pos=(-20.1,18.635,1.635) rot=(0,0,1;0rad)
  BaseFeature = -> Cylinder102
  Height = 0.265
  Length = 0.23
  MapMode = 5
  Placement = pos=(-20.1,18.635,1.635) rot=(0,0,1;0rad)
  Support = -> [XY_Plane062]
  Width = 0.23
FEATURE [PartDesign::Fillet] Fillet167
  Base = -> Box547 [Edge2]
  BaseFeature = -> Box547
  Placement = pos=(-21.5005,18.625,0.235) rot=(0,-1,0;0.174533rad)
  Radius = 0.05
  SupportTransform = false
FEATURE [PartDesign::Fillet] Fillet170
  Base = -> Fillet167 [Edge33]
  BaseFeature = -> Fillet167
  Placement = pos=(-21.5005,18.625,0.235) rot=(0,-1,0;0.174533rad)
  Radius = 0.5
  SupportTransform = false
FEATURE [PartDesign::Body] Body060  label="pin060"
  Group = -> [Box511,Box519,Box509,Box513,Box518,Fillet165,Fillet147,Box497,Cylinder104,Box528,Box503,Fillet153,Box512,Cylinder102,Box522]
  Origin = -> Origin054
  Placement = pos=(0,-5,0) rot=(0,0,1;0rad)
  Tip = -> Box522
FEATURE [PartDesign::Fillet] Fillet176
  Base = -> Fillet157 [Edge33]
  BaseFeature = -> Fillet157
  Placement = pos=(-21.5005,18.625,0.235) rot=(0,-1,0;0.174533rad)
  Radius = 0.5
  SupportTransform = false
FEATURE [PartDesign::AdditiveBox] Box524
  AttacherType = Attacher::AttachEngine3D
  AttachmentOffset = pos=(-21.1,18.635,0.305) rot=(0,1,0;0.785398rad)
  BaseFeature = -> Fillet176
  Height = 0.375
  Length = 0.2
  MapMode = 5
  Placement = pos=(-21.1,18.635,0.305) rot=(0,1,0;0.785398rad)
  Support = -> [XY_Plane054]
  Width = 0.23
FEATURE [PartDesign::SubtractiveCylinder] Cylinder110
  Angle = 360
  AttacherType = Attacher::AttachEngine3D
  AttachmentOffset = pos=(-21.055,18.935,0.52) rot=(1,0,0;1.5708rad)
  BaseFeature = -> Box524
  Height = 0.375
  MapMode = 5
  Placement = pos=(-21.055,18.935,0.52) rot=(1,0,0;1.5708rad)
  Radius = 0.205
  Support = -> [XY_Plane054]
FEATURE [PartDesign::SubtractiveBox] Box520
  AttacherType = Attacher::AttachEngine3D
  AttachmentOffset = pos=(-20.95,18.635,0.53) rot=(0,0,1;0rad)
  BaseFeature = -> Cylinder110
  Height = 0.5
  Length = 0.1
  MapMode = 5
  Placement = pos=(-20.95,18.635,0.53) rot=(0,0,1;0rad)
  Support = -> [XY_Plane054]
  Width = 0.23
FEATURE [PartDesign::SubtractiveBox] Box516
  AttacherType = Attacher::AttachEngine3D
  AttachmentOffset = pos=(-21.15,18.635,0.297) rot=(0,-1,0;0.174533rad)
  BaseFeature = -> Box520
  Height = 0.115
  Length = 0.115
  MapMode = 5
  Placement = pos=(-21.15,18.635,0.297) rot=(0,-1,0;0.174533rad)
  Support = -> [XY_Plane054]
  Width = 0.23
FEATURE [PartDesign::Fillet] Fillet158
  Base = -> Box516 [Edge28]
  BaseFeature = -> Box516
  Placement = pos=(-21.15,18.635,0.297) rot=(0,-1,0;0.174533rad)
  Radius = 0.375
  SupportTransform = false
FEATURE [PartDesign::AdditiveBox] Box526
  AttacherType = Attacher::AttachEngine3D
  AttachmentOffset = pos=(-20.7,18.635,1.55) rot=(0,1,0;0.785398rad)
  BaseFeature = -> Fillet158
  Height = 0.375
  Length = 0.23
  MapMode = 5
  Placement = pos=(-20.7,18.635,1.55) rot=(0,1,0;0.785398rad)
  Support = -> [XY_Plane054]
  Width = 0.23
FEATURE [PartDesign::SubtractiveCylinder] Cylinder107
  Angle = 360
  AttacherType = Attacher::AttachEngine3D
  AttachmentOffset = pos=(-20.271,18.635,1.4056) rot=(-1,0,0;1.5708rad)
  BaseFeature = -> Box526
  Height = 0.23
  MapMode = 5
  Placement = pos=(-20.271,18.635,1.4056) rot=(-1,0,0;1.5708rad)
  Radius = 0.23
  Support = -> [XY_Plane054]
FEATURE [PartDesign::AdditiveBox] Box523
  AttacherType = Attacher::AttachEngine3D
  AttachmentOffset = pos=(-20.1,18.635,1.635) rot=(0,0,1;0rad)
  BaseFeature = -> Cylinder107
  Height = 0.265
  Length = 0.23
  MapMode = 5
  Placement = pos=(-20.1,18.635,1.635) rot=(0,0,1;0rad)
  Support = -> [XY_Plane054]
  Width = 0.23
FEATURE [PartDesign::Body] Body059  label="pin059"
  Group = -> [Box529,Box530,Box488,Box499,Box498,Fillet157,Fillet176,Box524,Cylinder110,Box520,Box516,Fillet158,Box526,Cylinder107,Box523]
  Origin = -> Origin057
  Placement = pos=(0,-5.5,0) rot=(0,0,1;0rad)
  Tip = -> Box523
FEATURE [PartDesign::AdditiveBox] Box557
  AttacherType = Attacher::AttachEngine3D
  AttachmentOffset = pos=(-21.1,18.635,0.305) rot=(0,1,0;0.785398rad)
  BaseFeature = -> Fillet170
  Height = 0.375
  Length = 0.2
  MapMode = 5
  Placement = pos=(-21.1,18.635,0.305) rot=(0,1,0;0.785398rad)
  Support = -> [XY_Plane061]
  Width = 0.23
FEATURE [PartDesign::SubtractiveCylinder] Cylinder112
  Angle = 360
  AttacherType = Attacher::AttachEngine3D
  AttachmentOffset = pos=(-21.055,18.935,0.52) rot=(1,0,0;1.5708rad)
  BaseFeature = -> Box557
  Height = 0.375
  MapMode = 5
  Placement = pos=(-21.055,18.935,0.52) rot=(1,0,0;1.5708rad)
  Radius = 0.205
  Support = -> [XY_Plane061]
FEATURE [PartDesign::SubtractiveBox] Box546
  AttacherType = Attacher::AttachEngine3D
  AttachmentOffset = pos=(-20.95,18.635,0.53) rot=(0,0,1;0rad)
  BaseFeature = -> Cylinder112
  Height = 0.5
  Length = 0.1
  MapMode = 5
  Placement = pos=(-20.95,18.635,0.53) rot=(0,0,1;0rad)
  Support = -> [XY_Plane061]
  Width = 0.23
FEATURE [PartDesign::SubtractiveBox] Box539
  AttacherType = Attacher::AttachEngine3D
  AttachmentOffset = pos=(-21.15,18.635,0.297) rot=(0,-1,0;0.174533rad)
  BaseFeature = -> Box546
  Height = 0.115
  Length = 0.115
  MapMode = 5
  Placement = pos=(-21.15,18.635,0.297) rot=(0,-1,0;0.174533rad)
  Support = -> [XY_Plane061]
  Width = 0.23
FEATURE [PartDesign::Fillet] Fillet172
  Base = -> Box539 [Edge28]
  BaseFeature = -> Box539
  Placement = pos=(-21.15,18.635,0.297) rot=(0,-1,0;0.174533rad)
  Radius = 0.375
  SupportTransform = false
FEATURE [PartDesign::AdditiveBox] Box544
  AttacherType = Attacher::AttachEngine3D
  AttachmentOffset = pos=(-20.7,18.635,1.55) rot=(0,1,0;0.785398rad)
  BaseFeature = -> Fillet172
  Height = 0.375
  Length = 0.23
  MapMode = 5
  Placement = pos=(-20.7,18.635,1.55) rot=(0,1,0;0.785398rad)
  Support = -> [XY_Plane061]
  Width = 0.23
FEATURE [PartDesign::SubtractiveCylinder] Cylinder111
  Angle = 360
  AttacherType = Attacher::AttachEngine3D
  AttachmentOffset = pos=(-20.271,18.635,1.4056) rot=(-1,0,0;1.5708rad)
  BaseFeature = -> Box544
  Height = 0.23
  MapMode = 5
  Placement = pos=(-20.271,18.635,1.4056) rot=(-1,0,0;1.5708rad)
  Radius = 0.23
  Support = -> [XY_Plane061]
FEATURE [PartDesign::AdditiveBox] Box534
  AttacherType = Attacher::AttachEngine3D
  AttachmentOffset = pos=(-20.1,18.635,1.635) rot=(0,0,1;0rad)
  BaseFeature = -> Cylinder111
  Height = 0.265
  Length = 0.23
  MapMode = 5
  Placement = pos=(-20.1,18.635,1.635) rot=(0,0,1;0rad)
  Support = -> [XY_Plane061]
  Width = 0.23
FEATURE [PartDesign::Body] Body056  label="pin056"
  Group = -> [Box535,Box536,Box521,Box545,Box547,Fillet167,Fillet170,Box557,Cylinder112,Box546,Box539,Fillet172,Box544,Cylinder111,Box534]
  Origin = -> Origin065
  Placement = pos=(0,-4,0) rot=(0,0,1;0rad)
  Tip = -> Box534
FEATURE [PartDesign::SubtractiveBox] Box560
  AttacherType = Attacher::AttachEngine3D
  AttachmentOffset = pos=(-21.5005,18.625,0.235) rot=(0,-1,0;0.174533rad)
  BaseFeature = -> Box507
  Height = 0.3
  Length = 0.6605
  MapMode = 5
  Placement = pos=(-21.5005,18.625,0.235) rot=(0,-1,0;0.174533rad)
  Support = -> [XY_Plane059]
  Width = 0.25
FEATURE [PartDesign::Fillet] Fillet179
  Base = -> Box560 [Edge2]
  BaseFeature = -> Box560
  Placement = pos=(-21.5005,18.625,0.235) rot=(0,-1,0;0.174533rad)
  Radius = 0.05
  SupportTransform = false
FEATURE [PartDesign::Fillet] Fillet161
  Base = -> Fillet179 [Edge33]
  BaseFeature = -> Fillet179
  Placement = pos=(-21.5005,18.625,0.235) rot=(0,-1,0;0.174533rad)
  Radius = 0.5
  SupportTransform = false
FEATURE [PartDesign::AdditiveBox] Box484
  AttacherType = Attacher::AttachEngine3D
  AttachmentOffset = pos=(-21.1,18.635,0.305) rot=(0,1,0;0.785398rad)
  BaseFeature = -> Fillet161
  Height = 0.375
  Length = 0.2
  MapMode = 5
  Placement = pos=(-21.1,18.635,0.305) rot=(0,1,0;0.785398rad)
  Support = -> [XY_Plane059]
  Width = 0.23
FEATURE [PartDesign::SubtractiveCylinder] Cylinder101
  Angle = 360
  AttacherType = Attacher::AttachEngine3D
  AttachmentOffset = pos=(-21.055,18.935,0.52) rot=(1,0,0;1.5708rad)
  BaseFeature = -> Box484
  Height = 0.375
  MapMode = 5
  Placement = pos=(-21.055,18.935,0.52) rot=(1,0,0;1.5708rad)
  Radius = 0.205
  Support = -> [XY_Plane059]
FEATURE [PartDesign::SubtractiveBox] Box483
  AttacherType = Attacher::AttachEngine3D
  AttachmentOffset = pos=(-20.95,18.635,0.53) rot=(0,0,1;0rad)
  BaseFeature = -> Cylinder101
  Height = 0.5
  Length = 0.1
  MapMode = 5
  Placement = pos=(-20.95,18.635,0.53) rot=(0,0,1;0rad)
  Support = -> [XY_Plane059]
  Width = 0.23
FEATURE [PartDesign::SubtractiveBox] Box501
  AttacherType = Attacher::AttachEngine3D
  AttachmentOffset = pos=(-21.15,18.635,0.297) rot=(0,-1,0;0.174533rad)
  BaseFeature = -> Box483
  Height = 0.115
  Length = 0.115
  MapMode = 5
  Placement = pos=(-21.15,18.635,0.297) rot=(0,-1,0;0.174533rad)
  Support = -> [XY_Plane059]
  Width = 0.23
FEATURE [PartDesign::Fillet] Fillet174
  Base = -> Box501 [Edge28]
  BaseFeature = -> Box501
  Placement = pos=(-21.15,18.635,0.297) rot=(0,-1,0;0.174533rad)
  Radius = 0.375
  SupportTransform = false
FEATURE [PartDesign::AdditiveBox] Box508
  AttacherType = Attacher::AttachEngine3D
  AttachmentOffset = pos=(-20.7,18.635,1.55) rot=(0,1,0;0.785398rad)
  BaseFeature = -> Fillet174
  Height = 0.375
  Length = 0.23
  MapMode = 5
  Placement = pos=(-20.7,18.635,1.55) rot=(0,1,0;0.785398rad)
  Support = -> [XY_Plane059]
  Width = 0.23
FEATURE [PartDesign::SubtractiveCylinder] Cylinder103
  Angle = 360
  AttacherType = Attacher::AttachEngine3D
  AttachmentOffset = pos=(-20.271,18.635,1.4056) rot=(-1,0,0;1.5708rad)
  BaseFeature = -> Box508
  Height = 0.23
  MapMode = 5
  Placement = pos=(-20.271,18.635,1.4056) rot=(-1,0,0;1.5708rad)
  Radius = 0.23
  Support = -> [XY_Plane059]
FEATURE [PartDesign::AdditiveBox] Box502
  AttacherType = Attacher::AttachEngine3D
  AttachmentOffset = pos=(-20.1,18.635,1.635) rot=(0,0,1;0rad)
  BaseFeature = -> Cylinder103
  Height = 0.265
  Length = 0.23
  MapMode = 5
  Placement = pos=(-20.1,18.635,1.635) rot=(0,0,1;0rad)
  Support = -> [XY_Plane059]
  Width = 0.23
FEATURE [PartDesign::Body] Body055  label="pin055"
  Group = -> [Box525,Box517,Box505,Box507,Box560,Fillet179,Fillet161,Box484,Cylinder101,Box483,Box501,Fillet174,Box508,Cylinder103,Box502]
  Origin = -> Origin056
  Placement = pos=(0,-4.5,0) rot=(0,0,1;0rad)
  Tip = -> Box502
FEATURE [PartDesign::SubtractiveBox] Box565
  AttacherType = Attacher::AttachEngine3D
  AttachmentOffset = pos=(-21.19,18.635,-0.12) rot=(0,-1,0;0.15708rad)
  BaseFeature = -> Box527
  Height = 0.12
  Length = 0.725
  MapMode = 5
  Placement = pos=(-21.19,18.635,-0.12) rot=(0,-1,0;0.15708rad)
  Support = -> [XY_Plane063]
  Width = 0.25
FEATURE [PartDesign::SubtractiveBox] Box538
  AttacherType = Attacher::AttachEngine3D
  AttachmentOffset = pos=(-21.5005,18.625,0.235) rot=(0,-1,0;0.174533rad)
  BaseFeature = -> Box565
  Height = 0.3
  Length = 0.6605
  MapMode = 5
  Placement = pos=(-21.5005,18.625,0.235) rot=(0,-1,0;0.174533rad)
  Support = -> [XY_Plane063]
  Width = 0.25
FEATURE [PartDesign::Fillet] Fillet178
  Base = -> Box538 [Edge2]
  BaseFeature = -> Box538
  Placement = pos=(-21.5005,18.625,0.235) rot=(0,-1,0;0.174533rad)
  Radius = 0.05
  SupportTransform = false
FEATURE [PartDesign::Fillet] Fillet177
  Base = -> Fillet178 [Edge33]
  BaseFeature = -> Fillet178
  Placement = pos=(-21.5005,18.625,0.235) rot=(0,-1,0;0.174533rad)
  Radius = 0.5
  SupportTransform = false
FEATURE [PartDesign::AdditiveBox] Box506
  AttacherType = Attacher::AttachEngine3D
  AttachmentOffset = pos=(-21.1,18.635,0.305) rot=(0,1,0;0.785398rad)
  BaseFeature = -> Fillet177
  Height = 0.375
  Length = 0.2
  MapMode = 5
  Placement = pos=(-21.1,18.635,0.305) rot=(0,1,0;0.785398rad)
  Support = -> [XY_Plane063]
  Width = 0.23
FEATURE [PartDesign::SubtractiveCylinder] Cylinder106
  Angle = 360
  AttacherType = Attacher::AttachEngine3D
  AttachmentOffset = pos=(-21.055,18.935,0.52) rot=(1,0,0;1.5708rad)
  BaseFeature = -> Box506
  Height = 0.375
  MapMode = 5
  Placement = pos=(-21.055,18.935,0.52) rot=(1,0,0;1.5708rad)
  Radius = 0.205
  Support = -> [XY_Plane063]
FEATURE [PartDesign::SubtractiveBox] Box514
  AttacherType = Attacher::AttachEngine3D
  AttachmentOffset = pos=(-20.95,18.635,0.53) rot=(0,0,1;0rad)
  BaseFeature = -> Cylinder106
  Height = 0.5
  Length = 0.1
  MapMode = 5
  Placement = pos=(-20.95,18.635,0.53) rot=(0,0,1;0rad)
  Support = -> [XY_Plane063]
  Width = 0.23
FEATURE [PartDesign::SubtractiveBox] Box531
  AttacherType = Attacher::AttachEngine3D
  AttachmentOffset = pos=(-21.15,18.635,0.297) rot=(0,-1,0;0.174533rad)
  BaseFeature = -> Box514
  Height = 0.115
  Length = 0.115
  MapMode = 5
  Placement = pos=(-21.15,18.635,0.297) rot=(0,-1,0;0.174533rad)
  Support = -> [XY_Plane063]
  Width = 0.23
FEATURE [PartDesign::Fillet] Fillet169
  Base = -> Box531 [Edge28]
  BaseFeature = -> Box531
  Placement = pos=(-21.15,18.635,0.297) rot=(0,-1,0;0.174533rad)
  Radius = 0.375
  SupportTransform = false
FEATURE [PartDesign::AdditiveBox] Box533
  AttacherType = Attacher::AttachEngine3D
  AttachmentOffset = pos=(-20.7,18.635,1.55) rot=(0,1,0;0.785398rad)
  BaseFeature = -> Fillet169
  Height = 0.375
  Length = 0.23
  MapMode = 5
  Placement = pos=(-20.7,18.635,1.55) rot=(0,1,0;0.785398rad)
  Support = -> [XY_Plane063]
  Width = 0.23
FEATURE [PartDesign::SubtractiveCylinder] Cylinder109
  Angle = 360
  AttacherType = Attacher::AttachEngine3D
  AttachmentOffset = pos=(-20.271,18.635,1.4056) rot=(-1,0,0;1.5708rad)
  BaseFeature = -> Box533
  Height = 0.23
  MapMode = 5
  Placement = pos=(-20.271,18.635,1.4056) rot=(-1,0,0;1.5708rad)
  Radius = 0.23
  Support = -> [XY_Plane063]
FEATURE [PartDesign::AdditiveBox] Box556
  AttacherType = Attacher::AttachEngine3D
  AttachmentOffset = pos=(-20.1,18.635,1.635) rot=(0,0,1;0rad)
  BaseFeature = -> Cylinder109
  Height = 0.265
  Length = 0.23
  MapMode = 5
  Placement = pos=(-20.1,18.635,1.635) rot=(0,0,1;0rad)
  Support = -> [XY_Plane063]
  Width = 0.23
FEATURE [PartDesign::Body] Body057  label="pin057"
  Group = -> [Box541,Box553,Box527,Box565,Box538,Fillet178,Fillet177,Box506,Cylinder106,Box514,Box531,Fillet169,Box533,Cylinder109,Box556]
  Origin = -> Origin060
  Placement = pos=(0,-3,0) rot=(0,0,1;0rad)
  Tip = -> Box556
FEATURE [PartDesign::SubtractiveBox] Box566
  AttacherType = Attacher::AttachEngine3D
  AttachmentOffset = pos=(-20.5,18.63,0) rot=(0,0,1;0rad)
  BaseFeature = -> Box550
  Height = 1.635
  Length = 0.5
  MapMode = 5
  Placement = pos=(-20.5,18.63,0) rot=(0,0,1;0rad)
  Support = -> [XY_Plane064]
  Width = 0.25
FEATURE [PartDesign::SubtractiveBox] Box548
  AttacherType = Attacher::AttachEngine3D
  AttachmentOffset = pos=(-21.19,18.635,-0.12) rot=(0,-1,0;0.15708rad)
  BaseFeature = -> Box566
  Height = 0.12
  Length = 0.725
  MapMode = 5
  Placement = pos=(-21.19,18.635,-0.12) rot=(0,-1,0;0.15708rad)
  Support = -> [XY_Plane064]
  Width = 0.25
FEATURE [PartDesign::SubtractiveBox] Box540
  AttacherType = Attacher::AttachEngine3D
  AttachmentOffset = pos=(-21.5005,18.625,0.235) rot=(0,-1,0;0.174533rad)
  BaseFeature = -> Box548
  Height = 0.3
  Length = 0.6605
  MapMode = 5
  Placement = pos=(-21.5005,18.625,0.235) rot=(0,-1,0;0.174533rad)
  Support = -> [XY_Plane064]
  Width = 0.25
FEATURE [PartDesign::Fillet] Fillet175
  Base = -> Box540 [Edge2]
  BaseFeature = -> Box540
  Placement = pos=(-21.5005,18.625,0.235) rot=(0,-1,0;0.174533rad)
  Radius = 0.05
  SupportTransform = false
FEATURE [PartDesign::Fillet] Fillet162
  Base = -> Fillet175 [Edge33]
  BaseFeature = -> Fillet175
  Placement = pos=(-21.5005,18.625,0.235) rot=(0,-1,0;0.174533rad)
  Radius = 0.5
  SupportTransform = false
FEATURE [PartDesign::AdditiveBox] Box564
  AttacherType = Attacher::AttachEngine3D
  AttachmentOffset = pos=(-21.1,18.635,0.305) rot=(0,1,0;0.785398rad)
  BaseFeature = -> Fillet162
  Height = 0.375
  Length = 0.2
  MapMode = 5
  Placement = pos=(-21.1,18.635,0.305) rot=(0,1,0;0.785398rad)
  Support = -> [XY_Plane064]
  Width = 0.23
FEATURE [PartDesign::SubtractiveCylinder] Cylinder117
  Angle = 360
  AttacherType = Attacher::AttachEngine3D
  AttachmentOffset = pos=(-21.055,18.935,0.52) rot=(1,0,0;1.5708rad)
  BaseFeature = -> Box564
  Height = 0.375
  MapMode = 5
  Placement = pos=(-21.055,18.935,0.52) rot=(1,0,0;1.5708rad)
  Radius = 0.205
  Support = -> [XY_Plane064]
FEATURE [PartDesign::SubtractiveBox] Box555
  AttacherType = Attacher::AttachEngine3D
  AttachmentOffset = pos=(-20.95,18.635,0.53) rot=(0,0,1;0rad)
  BaseFeature = -> Cylinder117
  Height = 0.5
  Length = 0.1
  MapMode = 5
  Placement = pos=(-20.95,18.635,0.53) rot=(0,0,1;0rad)
  Support = -> [XY_Plane064]
  Width = 0.23
FEATURE [PartDesign::SubtractiveBox] Box532
  AttacherType = Attacher::AttachEngine3D
  AttachmentOffset = pos=(-21.15,18.635,0.297) rot=(0,-1,0;0.174533rad)
  BaseFeature = -> Box555
  Height = 0.115
  Length = 0.115
  MapMode = 5
  Placement = pos=(-21.15,18.635,0.297) rot=(0,-1,0;0.174533rad)
  Support = -> [XY_Plane064]
  Width = 0.23
FEATURE [PartDesign::Fillet] Fillet164
  Base = -> Box532 [Edge28]
  BaseFeature = -> Box532
  Placement = pos=(-21.15,18.635,0.297) rot=(0,-1,0;0.174533rad)
  Radius = 0.375
  SupportTransform = false
FEATURE [PartDesign::AdditiveBox] Box563
  AttacherType = Attacher::AttachEngine3D
  AttachmentOffset = pos=(-20.7,18.635,1.55) rot=(0,1,0;0.785398rad)
  BaseFeature = -> Fillet164
  Height = 0.375
  Length = 0.23
  MapMode = 5
  Placement = pos=(-20.7,18.635,1.55) rot=(0,1,0;0.785398rad)
  Support = -> [XY_Plane064]
  Width = 0.23
FEATURE [PartDesign::SubtractiveCylinder] Cylinder116
  Angle = 360
  AttacherType = Attacher::AttachEngine3D
  AttachmentOffset = pos=(-20.271,18.635,1.4056) rot=(-1,0,0;1.5708rad)
  BaseFeature = -> Box563
  Height = 0.23
  MapMode = 5
  Placement = pos=(-20.271,18.635,1.4056) rot=(-1,0,0;1.5708rad)
  Radius = 0.23
  Support = -> [XY_Plane064]
FEATURE [PartDesign::AdditiveBox] Box542
  AttacherType = Attacher::AttachEngine3D
  AttachmentOffset = pos=(-20.1,18.635,1.635) rot=(0,0,1;0rad)
  BaseFeature = -> Cylinder116
  Height = 0.265
  Length = 0.23
  MapMode = 5
  Placement = pos=(-20.1,18.635,1.635) rot=(0,0,1;0rad)
  Support = -> [XY_Plane064]
  Width = 0.23
FEATURE [PartDesign::Body] Body054  label="pin054"
  Group = -> [Box537,Box550,Box566,Box548,Box540,Fillet175,Fillet162,Box564,Cylinder117,Box555,Box532,Fillet164,Box563,Cylinder116,Box542]
  Origin = -> Origin064
  Placement = pos=(0,-3.5,0) rot=(0,0,1;0rad)
  Tip = -> Box542
FEATURE [PartDesign::AdditiveBox] Box583
  AttacherType = Attacher::AttachEngine3D
  AttachmentOffset = pos=(-21.3,18.635,0) rot=(0,0,1;0rad)
  Height = 1.9
  Length = 1.3
  MapMode = 5
  Placement = pos=(-21.3,18.635,0) rot=(0,0,1;0rad)
  Support = -> [XY_Plane060]
  Width = 0.23
FEATURE [PartDesign::SubtractiveBox] Box571
  AttacherType = Attacher::AttachEngine3D
  AttachmentOffset = pos=(-21.35,18.635,0.35) rot=(0,0,1;0rad)
  BaseFeature = -> Box583
  Height = 1.55
  Length = 0.5
  MapMode = 5
  Placement = pos=(-21.35,18.635,0.35) rot=(0,0,1;0rad)
  Support = -> [XY_Plane060]
  Width = 0.23
FEATURE [PartDesign::SubtractiveBox] Box554
  AttacherType = Attacher::AttachEngine3D
  AttachmentOffset = pos=(-20.5,18.63,0) rot=(0,0,1;0rad)
  BaseFeature = -> Box571
  Height = 1.635
  Length = 0.5
  MapMode = 5
  Placement = pos=(-20.5,18.63,0) rot=(0,0,1;0rad)
  Support = -> [XY_Plane060]
  Width = 0.25
FEATURE [PartDesign::SubtractiveBox] Box576
  AttacherType = Attacher::AttachEngine3D
  AttachmentOffset = pos=(-21.19,18.635,-0.12) rot=(0,-1,0;0.15708rad)
  BaseFeature = -> Box554
  Height = 0.12
  Length = 0.725
  MapMode = 5
  Placement = pos=(-21.19,18.635,-0.12) rot=(0,-1,0;0.15708rad)
  Support = -> [XY_Plane060]
  Width = 0.25
FEATURE [PartDesign::SubtractiveBox] Box569
  AttacherType = Attacher::AttachEngine3D
  AttachmentOffset = pos=(-21.5005,18.625,0.235) rot=(0,-1,0;0.174533rad)
  BaseFeature = -> Box576
  Height = 0.3
  Length = 0.6605
  MapMode = 5
  Placement = pos=(-21.5005,18.625,0.235) rot=(0,-1,0;0.174533rad)
  Support = -> [XY_Plane060]
  Width = 0.25
FEATURE [PartDesign::Fillet] Fillet152
  Base = -> Box569 [Edge2]
  BaseFeature = -> Box569
  Placement = pos=(-21.5005,18.625,0.235) rot=(0,-1,0;0.174533rad)
  Radius = 0.05
  SupportTransform = false
FEATURE [PartDesign::Fillet] Fillet154
  Base = -> Fillet152 [Edge33]
  BaseFeature = -> Fillet152
  Placement = pos=(-21.5005,18.625,0.235) rot=(0,-1,0;0.174533rad)
  Radius = 0.5
  SupportTransform = false
FEATURE [PartDesign::AdditiveBox] Box561
  AttacherType = Attacher::AttachEngine3D
  AttachmentOffset = pos=(-21.1,18.635,0.305) rot=(0,1,0;0.785398rad)
  BaseFeature = -> Fillet154
  Height = 0.375
  Length = 0.2
  MapMode = 5
  Placement = pos=(-21.1,18.635,0.305) rot=(0,1,0;0.785398rad)
  Support = -> [XY_Plane060]
  Width = 0.23
FEATURE [PartDesign::SubtractiveCylinder] Cylinder118
  Angle = 360
  AttacherType = Attacher::AttachEngine3D
  AttachmentOffset = pos=(-21.055,18.935,0.52) rot=(1,0,0;1.5708rad)
  BaseFeature = -> Box561
  Height = 0.375
  MapMode = 5
  Placement = pos=(-21.055,18.935,0.52) rot=(1,0,0;1.5708rad)
  Radius = 0.205
  Support = -> [XY_Plane060]
FEATURE [PartDesign::SubtractiveBox] Box575
  AttacherType = Attacher::AttachEngine3D
  AttachmentOffset = pos=(-20.95,18.635,0.53) rot=(0,0,1;0rad)
  BaseFeature = -> Cylinder118
  Height = 0.5
  Length = 0.1
  MapMode = 5
  Placement = pos=(-20.95,18.635,0.53) rot=(0,0,1;0rad)
  Support = -> [XY_Plane060]
  Width = 0.23
FEATURE [PartDesign::SubtractiveBox] Box562
  AttacherType = Attacher::AttachEngine3D
  AttachmentOffset = pos=(-21.15,18.635,0.297) rot=(0,-1,0;0.174533rad)
  BaseFeature = -> Box575
  Height = 0.115
  Length = 0.115
  MapMode = 5
  Placement = pos=(-21.15,18.635,0.297) rot=(0,-1,0;0.174533rad)
  Support = -> [XY_Plane060]
  Width = 0.23
FEATURE [PartDesign::Fillet] Fillet168
  Base = -> Box562 [Edge28]
  BaseFeature = -> Box562
  Placement = pos=(-21.15,18.635,0.297) rot=(0,-1,0;0.174533rad)
  Radius = 0.375
  SupportTransform = false
FEATURE [PartDesign::AdditiveBox] Box570
  AttacherType = Attacher::AttachEngine3D
  AttachmentOffset = pos=(-20.7,18.635,1.55) rot=(0,1,0;0.785398rad)
  BaseFeature = -> Fillet168
  Height = 0.375
  Length = 0.23
  MapMode = 5
  Placement = pos=(-20.7,18.635,1.55) rot=(0,1,0;0.785398rad)
  Support = -> [XY_Plane060]
  Width = 0.23
FEATURE [PartDesign::SubtractiveCylinder] Cylinder120
  Angle = 360
  AttacherType = Attacher::AttachEngine3D
  AttachmentOffset = pos=(-20.271,18.635,1.4056) rot=(-1,0,0;1.5708rad)
  BaseFeature = -> Box570
  Height = 0.23
  MapMode = 5
  Placement = pos=(-20.271,18.635,1.4056) rot=(-1,0,0;1.5708rad)
  Radius = 0.23
  Support = -> [XY_Plane060]
FEATURE [PartDesign::AdditiveBox] Box579
  AttacherType = Attacher::AttachEngine3D
  AttachmentOffset = pos=(-20.1,18.635,1.635) rot=(0,0,1;0rad)
  BaseFeature = -> Cylinder120
  Height = 0.265
  Length = 0.23
  MapMode = 5
  Placement = pos=(-20.1,18.635,1.635) rot=(0,0,1;0rad)
  Support = -> [XY_Plane060]
  Width = 0.23
FEATURE [PartDesign::Body] Body049  label="pin049"
  Group = -> [Box583,Box571,Box554,Box576,Box569,Fillet152,Fillet154,Box561,Cylinder118,Box575,Box562,Fillet168,Box570,Cylinder120,Box579]
  Origin = -> Origin053
  Placement = pos=(0,-0.5,0) rot=(0,0,1;0rad)
  Tip = -> Box579
FEATURE [PartDesign::SubtractiveBox] Box587
  AttacherType = Attacher::AttachEngine3D
  AttachmentOffset = pos=(-20.5,18.63,0) rot=(0,0,1;0rad)
  BaseFeature = -> Box485
  Height = 1.635
  Length = 0.5
  MapMode = 5
  Placement = pos=(-20.5,18.63,0) rot=(0,0,1;0rad)
  Support = -> [XY_Plane053]
  Width = 0.25
FEATURE [PartDesign::SubtractiveBox] Box574
  AttacherType = Attacher::AttachEngine3D
  AttachmentOffset = pos=(-21.19,18.635,-0.12) rot=(0,-1,0;0.15708rad)
  BaseFeature = -> Box587
  Height = 0.12
  Length = 0.725
  MapMode = 5
  Placement = pos=(-21.19,18.635,-0.12) rot=(0,-1,0;0.15708rad)
  Support = -> [XY_Plane053]
  Width = 0.25
FEATURE [PartDesign::SubtractiveBox] Box490
  AttacherType = Attacher::AttachEngine3D
  AttachmentOffset = pos=(-21.5005,18.625,0.235) rot=(0,-1,0;0.174533rad)
  BaseFeature = -> Box574
  Height = 0.3
  Length = 0.6605
  MapMode = 5
  Placement = pos=(-21.5005,18.625,0.235) rot=(0,-1,0;0.174533rad)
  Support = -> [XY_Plane053]
  Width = 0.25
FEATURE [PartDesign::Fillet] Fillet151
  Base = -> Box490 [Edge2]
  BaseFeature = -> Box490
  Placement = pos=(-21.5005,18.625,0.235) rot=(0,-1,0;0.174533rad)
  Radius = 0.05
  SupportTransform = false
FEATURE [PartDesign::Fillet] Fillet160
  Base = -> Fillet151 [Edge33]
  BaseFeature = -> Fillet151
  Placement = pos=(-21.5005,18.625,0.235) rot=(0,-1,0;0.174533rad)
  Radius = 0.5
  SupportTransform = false
FEATURE [PartDesign::AdditiveBox] Box592
  AttacherType = Attacher::AttachEngine3D
  AttachmentOffset = pos=(-21.3,18.635,0) rot=(0,0,1;0rad)
  Height = 1.9
  Length = 1.3
  MapMode = 5
  Placement = pos=(-21.3,18.635,0) rot=(0,0,1;0rad)
  Support = -> [XY_Plane058]
  Width = 0.23
FEATURE [PartDesign::SubtractiveBox] Box593
  AttacherType = Attacher::AttachEngine3D
  AttachmentOffset = pos=(-20.5,18.63,0) rot=(0,0,1;0rad)
  BaseFeature = -> Box496
  Height = 1.635
  Length = 0.5
  MapMode = 5
  Placement = pos=(-20.5,18.63,0) rot=(0,0,1;0rad)
  Support = -> [XY_Plane056]
  Width = 0.25
FEATURE [PartDesign::SubtractiveBox] Box481
  AttacherType = Attacher::AttachEngine3D
  AttachmentOffset = pos=(-21.19,18.635,-0.12) rot=(0,-1,0;0.15708rad)
  BaseFeature = -> Box593
  Height = 0.12
  Length = 0.725
  MapMode = 5
  Placement = pos=(-21.19,18.635,-0.12) rot=(0,-1,0;0.15708rad)
  Support = -> [XY_Plane056]
  Width = 0.25
FEATURE [PartDesign::SubtractiveBox] Box491
  AttacherType = Attacher::AttachEngine3D
  AttachmentOffset = pos=(-21.5005,18.625,0.235) rot=(0,-1,0;0.174533rad)
  BaseFeature = -> Box481
  Height = 0.3
  Length = 0.6605
  MapMode = 5
  Placement = pos=(-21.5005,18.625,0.235) rot=(0,-1,0;0.174533rad)
  Support = -> [XY_Plane056]
  Width = 0.25
FEATURE [PartDesign::Fillet] Fillet156
  Base = -> Box491 [Edge2]
  BaseFeature = -> Box491
  Placement = pos=(-21.5005,18.625,0.235) rot=(0,-1,0;0.174533rad)
  Radius = 0.05
  SupportTransform = false
FEATURE [PartDesign::Fillet] Fillet150
  Base = -> Fillet156 [Edge33]
  BaseFeature = -> Fillet156
  Placement = pos=(-21.5005,18.625,0.235) rot=(0,-1,0;0.174533rad)
  Radius = 0.5
  SupportTransform = false
FEATURE [PartDesign::AdditiveBox] Box594
  AttacherType = Attacher::AttachEngine3D
  AttachmentOffset = pos=(-21.3,18.635,0) rot=(0,0,1;0rad)
  Height = 1.9
  Length = 1.3
  MapMode = 5
  Placement = pos=(-21.3,18.635,0) rot=(0,0,1;0rad)
  Support = -> [XY_Plane057]
  Width = 0.23
FEATURE [PartDesign::SubtractiveBox] Box588
  AttacherType = Attacher::AttachEngine3D
  AttachmentOffset = pos=(-21.35,18.635,0.35) rot=(0,0,1;0rad)
  BaseFeature = -> Box594
  Height = 1.55
  Length = 0.5
  MapMode = 5
  Placement = pos=(-21.35,18.635,0.35) rot=(0,0,1;0rad)
  Support = -> [XY_Plane057]
  Width = 0.23
FEATURE [PartDesign::SubtractiveBox] Box568
  AttacherType = Attacher::AttachEngine3D
  AttachmentOffset = pos=(-20.5,18.63,0) rot=(0,0,1;0rad)
  BaseFeature = -> Box588
  Height = 1.635
  Length = 0.5
  MapMode = 5
  Placement = pos=(-20.5,18.63,0) rot=(0,0,1;0rad)
  Support = -> [XY_Plane057]
  Width = 0.25
FEATURE [PartDesign::SubtractiveBox] Box567
  AttacherType = Attacher::AttachEngine3D
  AttachmentOffset = pos=(-21.19,18.635,-0.12) rot=(0,-1,0;0.15708rad)
  BaseFeature = -> Box568
  Height = 0.12
  Length = 0.725
  MapMode = 5
  Placement = pos=(-21.19,18.635,-0.12) rot=(0,-1,0;0.15708rad)
  Support = -> [XY_Plane057]
  Width = 0.25
FEATURE [PartDesign::SubtractiveBox] Box582
  AttacherType = Attacher::AttachEngine3D
  AttachmentOffset = pos=(-21.5005,18.625,0.235) rot=(0,-1,0;0.174533rad)
  BaseFeature = -> Box567
  Height = 0.3
  Length = 0.6605
  MapMode = 5
  Placement = pos=(-21.5005,18.625,0.235) rot=(0,-1,0;0.174533rad)
  Support = -> [XY_Plane057]
  Width = 0.25
FEATURE [PartDesign::Fillet] Fillet166
  Base = -> Box582 [Edge2]
  BaseFeature = -> Box582
  Placement = pos=(-21.5005,18.625,0.235) rot=(0,-1,0;0.174533rad)
  Radius = 0.05
  SupportTransform = false
FEATURE [PartDesign::Fillet] Fillet145
  Base = -> Fillet166 [Edge33]
  BaseFeature = -> Fillet166
  Placement = pos=(-21.5005,18.625,0.235) rot=(0,-1,0;0.174533rad)
  Radius = 0.5
  SupportTransform = false
FEATURE [PartDesign::AdditiveBox] Box552
  AttacherType = Attacher::AttachEngine3D
  AttachmentOffset = pos=(-21.1,18.635,0.305) rot=(0,1,0;0.785398rad)
  BaseFeature = -> Fillet145
  Height = 0.375
  Length = 0.2
  MapMode = 5
  Placement = pos=(-21.1,18.635,0.305) rot=(0,1,0;0.785398rad)
  Support = -> [XY_Plane057]
  Width = 0.23
FEATURE [PartDesign::SubtractiveCylinder] Cylinder108
  Angle = 360
  AttacherType = Attacher::AttachEngine3D
  AttachmentOffset = pos=(-21.055,18.935,0.52) rot=(1,0,0;1.5708rad)
  BaseFeature = -> Box552
  Height = 0.375
  MapMode = 5
  Placement = pos=(-21.055,18.935,0.52) rot=(1,0,0;1.5708rad)
  Radius = 0.205
  Support = -> [XY_Plane057]
FEATURE [PartDesign::SubtractiveBox] Box515
  AttacherType = Attacher::AttachEngine3D
  AttachmentOffset = pos=(-20.95,18.635,0.53) rot=(0,0,1;0rad)
  BaseFeature = -> Cylinder108
  Height = 0.5
  Length = 0.1
  MapMode = 5
  Placement = pos=(-20.95,18.635,0.53) rot=(0,0,1;0rad)
  Support = -> [XY_Plane057]
  Width = 0.23
FEATURE [PartDesign::SubtractiveBox] Box510
  AttacherType = Attacher::AttachEngine3D
  AttachmentOffset = pos=(-21.15,18.635,0.297) rot=(0,-1,0;0.174533rad)
  BaseFeature = -> Box515
  Height = 0.115
  Length = 0.115
  MapMode = 5
  Placement = pos=(-21.15,18.635,0.297) rot=(0,-1,0;0.174533rad)
  Support = -> [XY_Plane057]
  Width = 0.23
FEATURE [PartDesign::Fillet] Fillet171
  Base = -> Box510 [Edge28]
  BaseFeature = -> Box510
  Placement = pos=(-21.15,18.635,0.297) rot=(0,-1,0;0.174533rad)
  Radius = 0.375
  SupportTransform = false
FEATURE [PartDesign::AdditiveBox] Box558
  AttacherType = Attacher::AttachEngine3D
  AttachmentOffset = pos=(-20.7,18.635,1.55) rot=(0,1,0;0.785398rad)
  BaseFeature = -> Fillet171
  Height = 0.375
  Length = 0.23
  MapMode = 5
  Placement = pos=(-20.7,18.635,1.55) rot=(0,1,0;0.785398rad)
  Support = -> [XY_Plane057]
  Width = 0.23
FEATURE [PartDesign::SubtractiveCylinder] Cylinder105
  Angle = 360
  AttacherType = Attacher::AttachEngine3D
  AttachmentOffset = pos=(-20.271,18.635,1.4056) rot=(-1,0,0;1.5708rad)
  BaseFeature = -> Box558
  Height = 0.23
  MapMode = 5
  Placement = pos=(-20.271,18.635,1.4056) rot=(-1,0,0;1.5708rad)
  Radius = 0.23
  Support = -> [XY_Plane057]
FEATURE [PartDesign::AdditiveBox] Box577
  AttacherType = Attacher::AttachEngine3D
  AttachmentOffset = pos=(-20.1,18.635,1.635) rot=(0,0,1;0rad)
  BaseFeature = -> Cylinder105
  Height = 0.265
  Length = 0.23
  MapMode = 5
  Placement = pos=(-20.1,18.635,1.635) rot=(0,0,1;0rad)
  Support = -> [XY_Plane057]
  Width = 0.23
FEATURE [PartDesign::Body] Body051  label="pin051"
  Group = -> [Box594,Box588,Box568,Box567,Box582,Fillet166,Fillet145,Box552,Cylinder108,Box515,Box510,Fillet171,Box558,Cylinder105,Box577]
  Origin = -> Origin059
  Tip = -> Box577
FEATURE [PartDesign::SubtractiveBox] Box597
  AttacherType = Attacher::AttachEngine3D
  AttachmentOffset = pos=(-21.35,18.635,0.35) rot=(0,0,1;0rad)
  BaseFeature = -> Box592
  Height = 1.55
  Length = 0.5
  MapMode = 5
  Placement = pos=(-21.35,18.635,0.35) rot=(0,0,1;0rad)
  Support = -> [XY_Plane058]
  Width = 0.23
FEATURE [PartDesign::SubtractiveBox] Box572
  AttacherType = Attacher::AttachEngine3D
  AttachmentOffset = pos=(-20.5,18.63,0) rot=(0,0,1;0rad)
  BaseFeature = -> Box597
  Height = 1.635
  Length = 0.5
  MapMode = 5
  Placement = pos=(-20.5,18.63,0) rot=(0,0,1;0rad)
  Support = -> [XY_Plane058]
  Width = 0.25
FEATURE [PartDesign::SubtractiveBox] Box584
  AttacherType = Attacher::AttachEngine3D
  AttachmentOffset = pos=(-21.19,18.635,-0.12) rot=(0,-1,0;0.15708rad)
  BaseFeature = -> Box572
  Height = 0.12
  Length = 0.725
  MapMode = 5
  Placement = pos=(-21.19,18.635,-0.12) rot=(0,-1,0;0.15708rad)
  Support = -> [XY_Plane058]
  Width = 0.25
FEATURE [PartDesign::SubtractiveBox] Box581
  AttacherType = Attacher::AttachEngine3D
  AttachmentOffset = pos=(-21.5005,18.625,0.235) rot=(0,-1,0;0.174533rad)
  BaseFeature = -> Box584
  Height = 0.3
  Length = 0.6605
  MapMode = 5
  Placement = pos=(-21.5005,18.625,0.235) rot=(0,-1,0;0.174533rad)
  Support = -> [XY_Plane058]
  Width = 0.25
FEATURE [PartDesign::Fillet] Fillet159
  Base = -> Box581 [Edge2]
  BaseFeature = -> Box581
  Placement = pos=(-21.5005,18.625,0.235) rot=(0,-1,0;0.174533rad)
  Radius = 0.05
  SupportTransform = false
FEATURE [PartDesign::Fillet] Fillet173
  Base = -> Fillet159 [Edge33]
  BaseFeature = -> Fillet159
  Placement = pos=(-21.5005,18.625,0.235) rot=(0,-1,0;0.174533rad)
  Radius = 0.5
  SupportTransform = false
FEATURE [PartDesign::AdditiveBox] Box559
  AttacherType = Attacher::AttachEngine3D
  AttachmentOffset = pos=(-21.1,18.635,0.305) rot=(0,1,0;0.785398rad)
  BaseFeature = -> Fillet173
  Height = 0.375
  Length = 0.2
  MapMode = 5
  Placement = pos=(-21.1,18.635,0.305) rot=(0,1,0;0.785398rad)
  Support = -> [XY_Plane058]
  Width = 0.23
FEATURE [PartDesign::SubtractiveCylinder] Cylinder122
  Angle = 360
  AttacherType = Attacher::AttachEngine3D
  AttachmentOffset = pos=(-21.055,18.935,0.52) rot=(1,0,0;1.5708rad)
  BaseFeature = -> Box559
  Height = 0.375
  MapMode = 5
  Placement = pos=(-21.055,18.935,0.52) rot=(1,0,0;1.5708rad)
  Radius = 0.205
  Support = -> [XY_Plane058]
FEATURE [PartDesign::SubtractiveBox] Box573
  AttacherType = Attacher::AttachEngine3D
  AttachmentOffset = pos=(-20.95,18.635,0.53) rot=(0,0,1;0rad)
  BaseFeature = -> Cylinder122
  Height = 0.5
  Length = 0.1
  MapMode = 5
  Placement = pos=(-20.95,18.635,0.53) rot=(0,0,1;0rad)
  Support = -> [XY_Plane058]
  Width = 0.23
FEATURE [PartDesign::SubtractiveBox] Box580
  AttacherType = Attacher::AttachEngine3D
  AttachmentOffset = pos=(-21.15,18.635,0.297) rot=(0,-1,0;0.174533rad)
  BaseFeature = -> Box573
  Height = 0.115
  Length = 0.115
  MapMode = 5
  Placement = pos=(-21.15,18.635,0.297) rot=(0,-1,0;0.174533rad)
  Support = -> [XY_Plane058]
  Width = 0.23
FEATURE [PartDesign::Fillet] Fillet148
  Base = -> Box580 [Edge28]
  BaseFeature = -> Box580
  Placement = pos=(-21.15,18.635,0.297) rot=(0,-1,0;0.174533rad)
  Radius = 0.375
  SupportTransform = false
FEATURE [PartDesign::AdditiveBox] Box578
  AttacherType = Attacher::AttachEngine3D
  AttachmentOffset = pos=(-20.7,18.635,1.55) rot=(0,1,0;0.785398rad)
  BaseFeature = -> Fillet148
  Height = 0.375
  Length = 0.23
  MapMode = 5
  Placement = pos=(-20.7,18.635,1.55) rot=(0,1,0;0.785398rad)
  Support = -> [XY_Plane058]
  Width = 0.23
FEATURE [PartDesign::SubtractiveCylinder] Cylinder119
  Angle = 360
  AttacherType = Attacher::AttachEngine3D
  AttachmentOffset = pos=(-20.271,18.635,1.4056) rot=(-1,0,0;1.5708rad)
  BaseFeature = -> Box578
  Height = 0.23
  MapMode = 5
  Placement = pos=(-20.271,18.635,1.4056) rot=(-1,0,0;1.5708rad)
  Radius = 0.23
  Support = -> [XY_Plane058]
FEATURE [PartDesign::AdditiveBox] Box585
  AttacherType = Attacher::AttachEngine3D
  AttachmentOffset = pos=(-20.1,18.635,1.635) rot=(0,0,1;0rad)
  BaseFeature = -> Cylinder119
  Height = 0.265
  Length = 0.23
  MapMode = 5
  Placement = pos=(-20.1,18.635,1.635) rot=(0,0,1;0rad)
  Support = -> [XY_Plane058]
  Width = 0.23
FEATURE [PartDesign::Body] Body058  label="pin058"
  Group = -> [Box592,Box597,Box572,Box584,Box581,Fillet159,Fillet173,Box559,Cylinder122,Box573,Box580,Fillet148,Box578,Cylinder119,Box585]
  Origin = -> Origin055
  Placement = pos=(0,-1,0) rot=(0,0,1;0rad)
  Tip = -> Box585
FEATURE [PartDesign::SubtractiveBox] Box598
  AttacherType = Attacher::AttachEngine3D
  AttachmentOffset = pos=(-20.5,18.63,0) rot=(0,0,1;0rad)
  BaseFeature = -> Box487
  Height = 1.635
  Length = 0.5
  MapMode = 5
  Placement = pos=(-20.5,18.63,0) rot=(0,0,1;0rad)
  Support = -> [XY_Plane055]
  Width = 0.25
FEATURE [PartDesign::SubtractiveBox] Box543
  AttacherType = Attacher::AttachEngine3D
  AttachmentOffset = pos=(-21.19,18.635,-0.12) rot=(0,-1,0;0.15708rad)
  BaseFeature = -> Box598
  Height = 0.12
  Length = 0.725
  MapMode = 5
  Placement = pos=(-21.19,18.635,-0.12) rot=(0,-1,0;0.15708rad)
  Support = -> [XY_Plane055]
  Width = 0.25
FEATURE [PartDesign::SubtractiveBox] Box493
  AttacherType = Attacher::AttachEngine3D
  AttachmentOffset = pos=(-21.5005,18.625,0.235) rot=(0,-1,0;0.174533rad)
  BaseFeature = -> Box543
  Height = 0.3
  Length = 0.6605
  MapMode = 5
  Placement = pos=(-21.5005,18.625,0.235) rot=(0,-1,0;0.174533rad)
  Support = -> [XY_Plane055]
  Width = 0.25
FEATURE [PartDesign::Fillet] Fillet155
  Base = -> Box493 [Edge2]
  BaseFeature = -> Box493
  Placement = pos=(-21.5005,18.625,0.235) rot=(0,-1,0;0.174533rad)
  Radius = 0.05
  SupportTransform = false
FEATURE [PartDesign::Fillet] Fillet146
  Base = -> Fillet155 [Edge33]
  BaseFeature = -> Fillet155
  Placement = pos=(-21.5005,18.625,0.235) rot=(0,-1,0;0.174533rad)
  Radius = 0.5
  SupportTransform = false
FEATURE [PartDesign::AdditiveBox] Box591
  AttacherType = Attacher::AttachEngine3D
  AttachmentOffset = pos=(-21.1,18.635,0.305) rot=(0,1,0;0.785398rad)
  BaseFeature = -> Fillet146
  Height = 0.375
  Length = 0.2
  MapMode = 5
  Placement = pos=(-21.1,18.635,0.305) rot=(0,1,0;0.785398rad)
  Support = -> [XY_Plane055]
  Width = 0.23
FEATURE [PartDesign::SubtractiveCylinder] Cylinder114
  Angle = 360
  AttacherType = Attacher::AttachEngine3D
  AttachmentOffset = pos=(-21.055,18.935,0.52) rot=(1,0,0;1.5708rad)
  BaseFeature = -> Box591
  Height = 0.375
  MapMode = 5
  Placement = pos=(-21.055,18.935,0.52) rot=(1,0,0;1.5708rad)
  Radius = 0.205
  Support = -> [XY_Plane055]
FEATURE [PartDesign::SubtractiveBox] Box482
  AttacherType = Attacher::AttachEngine3D
  AttachmentOffset = pos=(-20.95,18.635,0.53) rot=(0,0,1;0rad)
  BaseFeature = -> Cylinder114
  Height = 0.5
  Length = 0.1
  MapMode = 5
  Placement = pos=(-20.95,18.635,0.53) rot=(0,0,1;0rad)
  Support = -> [XY_Plane055]
  Width = 0.23
FEATURE [PartDesign::SubtractiveBox] Box489
  AttacherType = Attacher::AttachEngine3D
  AttachmentOffset = pos=(-21.15,18.635,0.297) rot=(0,-1,0;0.174533rad)
  BaseFeature = -> Box482
  Height = 0.115
  Length = 0.115
  MapMode = 5
  Placement = pos=(-21.15,18.635,0.297) rot=(0,-1,0;0.174533rad)
  Support = -> [XY_Plane055]
  Width = 0.23
FEATURE [PartDesign::Fillet] Fillet144
  Base = -> Box489 [Edge28]
  BaseFeature = -> Box489
  Placement = pos=(-21.15,18.635,0.297) rot=(0,-1,0;0.174533rad)
  Radius = 0.375
  SupportTransform = false
FEATURE [PartDesign::AdditiveBox] Box492
  AttacherType = Attacher::AttachEngine3D
  AttachmentOffset = pos=(-20.7,18.635,1.55) rot=(0,1,0;0.785398rad)
  BaseFeature = -> Fillet144
  Height = 0.375
  Length = 0.23
  MapMode = 5
  Placement = pos=(-20.7,18.635,1.55) rot=(0,1,0;0.785398rad)
  Support = -> [XY_Plane055]
  Width = 0.23
FEATURE [PartDesign::SubtractiveCylinder] Cylinder113
  Angle = 360
  AttacherType = Attacher::AttachEngine3D
  AttachmentOffset = pos=(-20.271,18.635,1.4056) rot=(-1,0,0;1.5708rad)
  BaseFeature = -> Box492
  Height = 0.23
  MapMode = 5
  Placement = pos=(-20.271,18.635,1.4056) rot=(-1,0,0;1.5708rad)
  Radius = 0.23
  Support = -> [XY_Plane055]
FEATURE [PartDesign::AdditiveBox] Box486
  AttacherType = Attacher::AttachEngine3D
  AttachmentOffset = pos=(-20.1,18.635,1.635) rot=(0,0,1;0rad)
  BaseFeature = -> Cylinder113
  Height = 0.265
  Length = 0.23
  MapMode = 5
  Placement = pos=(-20.1,18.635,1.635) rot=(0,0,1;0rad)
  Support = -> [XY_Plane055]
  Width = 0.23
FEATURE [PartDesign::Body] Body052  label="pin052"
  Group = -> [Box504,Box487,Box598,Box543,Box493,Fillet155,Fillet146,Box591,Cylinder114,Box482,Box489,Fillet144,Box492,Cylinder113,Box486]
  Origin = -> Origin058
  Placement = pos=(0,-2.5,0) rot=(0,0,1;0rad)
  Tip = -> Box486
FEATURE [PartDesign::AdditiveBox] Box599
  AttacherType = Attacher::AttachEngine3D
  AttachmentOffset = pos=(-21.1,18.635,0.305) rot=(0,1,0;0.785398rad)
  BaseFeature = -> Fillet150
  Height = 0.375
  Length = 0.2
  MapMode = 5
  Placement = pos=(-21.1,18.635,0.305) rot=(0,1,0;0.785398rad)
  Support = -> [XY_Plane056]
  Width = 0.23
FEATURE [PartDesign::SubtractiveCylinder] Cylinder123
  Angle = 360
  AttacherType = Attacher::AttachEngine3D
  AttachmentOffset = pos=(-21.055,18.935,0.52) rot=(1,0,0;1.5708rad)
  BaseFeature = -> Box599
  Height = 0.375
  MapMode = 5
  Placement = pos=(-21.055,18.935,0.52) rot=(1,0,0;1.5708rad)
  Radius = 0.205
  Support = -> [XY_Plane056]
FEATURE [PartDesign::SubtractiveBox] Box495
  AttacherType = Attacher::AttachEngine3D
  AttachmentOffset = pos=(-20.95,18.635,0.53) rot=(0,0,1;0rad)
  BaseFeature = -> Cylinder123
  Height = 0.5
  Length = 0.1
  MapMode = 5
  Placement = pos=(-20.95,18.635,0.53) rot=(0,0,1;0rad)
  Support = -> [XY_Plane056]
  Width = 0.23
FEATURE [PartDesign::SubtractiveBox] Box549
  AttacherType = Attacher::AttachEngine3D
  AttachmentOffset = pos=(-21.15,18.635,0.297) rot=(0,-1,0;0.174533rad)
  BaseFeature = -> Box495
  Height = 0.115
  Length = 0.115
  MapMode = 5
  Placement = pos=(-21.15,18.635,0.297) rot=(0,-1,0;0.174533rad)
  Support = -> [XY_Plane056]
  Width = 0.23
FEATURE [PartDesign::Fillet] Fillet149
  Base = -> Box549 [Edge28]
  BaseFeature = -> Box549
  Placement = pos=(-21.15,18.635,0.297) rot=(0,-1,0;0.174533rad)
  Radius = 0.375
  SupportTransform = false
FEATURE [PartDesign::AdditiveBox] Box586
  AttacherType = Attacher::AttachEngine3D
  AttachmentOffset = pos=(-20.7,18.635,1.55) rot=(0,1,0;0.785398rad)
  BaseFeature = -> Fillet149
  Height = 0.375
  Length = 0.23
  MapMode = 5
  Placement = pos=(-20.7,18.635,1.55) rot=(0,1,0;0.785398rad)
  Support = -> [XY_Plane056]
  Width = 0.23
FEATURE [PartDesign::SubtractiveCylinder] Cylinder100
  Angle = 360
  AttacherType = Attacher::AttachEngine3D
  AttachmentOffset = pos=(-20.271,18.635,1.4056) rot=(-1,0,0;1.5708rad)
  BaseFeature = -> Box586
  Height = 0.23
  MapMode = 5
  Placement = pos=(-20.271,18.635,1.4056) rot=(-1,0,0;1.5708rad)
  Radius = 0.23
  Support = -> [XY_Plane056]
FEATURE [PartDesign::AdditiveBox] Box494
  AttacherType = Attacher::AttachEngine3D
  AttachmentOffset = pos=(-20.1,18.635,1.635) rot=(0,0,1;0rad)
  BaseFeature = -> Cylinder100
  Height = 0.265
  Length = 0.23
  MapMode = 5
  Placement = pos=(-20.1,18.635,1.635) rot=(0,0,1;0rad)
  Support = -> [XY_Plane056]
  Width = 0.23
FEATURE [PartDesign::Body] Body050  label="pin050"
  Group = -> [Box551,Box496,Box593,Box481,Box491,Fillet156,Fillet150,Box599,Cylinder123,Box495,Box549,Fillet149,Box586,Cylinder100,Box494]
  Origin = -> Origin061
  Placement = pos=(0,-2,0) rot=(0,0,1;0rad)
  Tip = -> Box494
FEATURE [PartDesign::AdditiveBox] Box600
  AttacherType = Attacher::AttachEngine3D
  AttachmentOffset = pos=(-21.1,18.635,0.305) rot=(0,1,0;0.785398rad)
  BaseFeature = -> Fillet160
  Height = 0.375
  Length = 0.2
  MapMode = 5
  Placement = pos=(-21.1,18.635,0.305) rot=(0,1,0;0.785398rad)
  Support = -> [XY_Plane053]
  Width = 0.23
FEATURE [PartDesign::SubtractiveCylinder] Cylinder121
  Angle = 360
  AttacherType = Attacher::AttachEngine3D
  AttachmentOffset = pos=(-21.055,18.935,0.52) rot=(1,0,0;1.5708rad)
  BaseFeature = -> Box600
  Height = 0.375
  MapMode = 5
  Placement = pos=(-21.055,18.935,0.52) rot=(1,0,0;1.5708rad)
  Radius = 0.205
  Support = -> [XY_Plane053]
FEATURE [PartDesign::SubtractiveBox] Box595
  AttacherType = Attacher::AttachEngine3D
  AttachmentOffset = pos=(-20.95,18.635,0.53) rot=(0,0,1;0rad)
  BaseFeature = -> Cylinder121
  Height = 0.5
  Length = 0.1
  MapMode = 5
  Placement = pos=(-20.95,18.635,0.53) rot=(0,0,1;0rad)
  Support = -> [XY_Plane053]
  Width = 0.23
FEATURE [PartDesign::SubtractiveBox] Box596
  AttacherType = Attacher::AttachEngine3D
  AttachmentOffset = pos=(-21.15,18.635,0.297) rot=(0,-1,0;0.174533rad)
  BaseFeature = -> Box595
  Height = 0.115
  Length = 0.115
  MapMode = 5
  Placement = pos=(-21.15,18.635,0.297) rot=(0,-1,0;0.174533rad)
  Support = -> [XY_Plane053]
  Width = 0.23
FEATURE [PartDesign::Fillet] Fillet163
  Base = -> Box596 [Edge28]
  BaseFeature = -> Box596
  Placement = pos=(-21.15,18.635,0.297) rot=(0,-1,0;0.174533rad)
  Radius = 0.375
  SupportTransform = false
FEATURE [PartDesign::AdditiveBox] Box589
  AttacherType = Attacher::AttachEngine3D
  AttachmentOffset = pos=(-20.7,18.635,1.55) rot=(0,1,0;0.785398rad)
  BaseFeature = -> Fillet163
  Height = 0.375
  Length = 0.23
  MapMode = 5
  Placement = pos=(-20.7,18.635,1.55) rot=(0,1,0;0.785398rad)
  Support = -> [XY_Plane053]
  Width = 0.23
FEATURE [PartDesign::SubtractiveCylinder] Cylinder115
  Angle = 360
  AttacherType = Attacher::AttachEngine3D
  AttachmentOffset = pos=(-20.271,18.635,1.4056) rot=(-1,0,0;1.5708rad)
  BaseFeature = -> Box589
  Height = 0.23
  MapMode = 5
  Placement = pos=(-20.271,18.635,1.4056) rot=(-1,0,0;1.5708rad)
  Radius = 0.23
  Support = -> [XY_Plane053]
FEATURE [PartDesign::AdditiveBox] Box590
  AttacherType = Attacher::AttachEngine3D
  AttachmentOffset = pos=(-20.1,18.635,1.635) rot=(0,0,1;0rad)
  BaseFeature = -> Cylinder115
  Height = 0.265
  Length = 0.23
  MapMode = 5
  Placement = pos=(-20.1,18.635,1.635) rot=(0,0,1;0rad)
  Support = -> [XY_Plane053]
  Width = 0.23
FEATURE [PartDesign::Body] Body053  label="pin053"
  Group = -> [Box500,Box485,Box587,Box574,Box490,Fillet151,Fillet160,Box600,Cylinder121,Box595,Box596,Fillet163,Box589,Cylinder115,Box590]
  Origin = -> Origin062
  Placement = pos=(0,-1.5,0) rot=(0,0,1;0rad)
  Tip = -> Box590
FEATURE [App::Part] Part004  label="Pin-set005"
  Group = -> [Body051,Body049,Body058,Body053,Body050,Body052,Body057,Body054,Body056,Body055,Body060,Body059]
  Origin = -> Origin063
  Placement = pos=(0,-24,0) rot=(0,0,1;0rad)
FEATURE [PartDesign::AdditiveBox] Box622
  AttacherType = Attacher::AttachEngine3D
  AttachmentOffset = pos=(-21.3,18.635,0) rot=(0,0,1;0rad)
  Height = 1.9
  Length = 1.3
  MapMode = 5
  Placement = pos=(-21.3,18.635,0) rot=(0,0,1;0rad)
  Support = -> [XY_Plane066]
  Width = 0.23
FEATURE [PartDesign::SubtractiveBox] Box607
  AttacherType = Attacher::AttachEngine3D
  AttachmentOffset = pos=(-21.35,18.635,0.35) rot=(0,0,1;0rad)
  BaseFeature = -> Box622
  Height = 1.55
  Length = 0.5
  MapMode = 5
  Placement = pos=(-21.35,18.635,0.35) rot=(0,0,1;0rad)
  Support = -> [XY_Plane066]
  Width = 0.23
FEATURE [PartDesign::AdditiveBox] Box624
  AttacherType = Attacher::AttachEngine3D
  AttachmentOffset = pos=(-21.3,18.635,0) rot=(0,0,1;0rad)
  Height = 1.9
  Length = 1.3
  MapMode = 5
  Placement = pos=(-21.3,18.635,0) rot=(0,0,1;0rad)
  Support = -> [XY_Plane069]
  Width = 0.23
FEATURE [PartDesign::SubtractiveBox] Box606
  AttacherType = Attacher::AttachEngine3D
  AttachmentOffset = pos=(-21.35,18.635,0.35) rot=(0,0,1;0rad)
  BaseFeature = -> Box624
  Height = 1.55
  Length = 0.5
  MapMode = 5
  Placement = pos=(-21.35,18.635,0.35) rot=(0,0,1;0rad)
  Support = -> [XY_Plane069]
  Width = 0.23
FEATURE [PartDesign::AdditiveBox] Box635
  AttacherType = Attacher::AttachEngine3D
  AttachmentOffset = pos=(-21.3,18.635,0) rot=(0,0,1;0rad)
  Height = 1.9
  Length = 1.3
  MapMode = 5
  Placement = pos=(-21.3,18.635,0) rot=(0,0,1;0rad)
  Support = -> [XY_Plane073]
  Width = 0.23
FEATURE [PartDesign::AdditiveBox] Box637
  AttacherType = Attacher::AttachEngine3D
  AttachmentOffset = pos=(-21.3,18.635,0) rot=(0,0,1;0rad)
  Height = 1.9
  Length = 1.3
  MapMode = 5
  Placement = pos=(-21.3,18.635,0) rot=(0,0,1;0rad)
  Support = -> [XY_Plane074]
  Width = 0.23
FEATURE [PartDesign::SubtractiveBox] Box643
  AttacherType = Attacher::AttachEngine3D
  AttachmentOffset = pos=(-21.35,18.635,0.35) rot=(0,0,1;0rad)
  BaseFeature = -> Box635
  Height = 1.55
  Length = 0.5
  MapMode = 5
  Placement = pos=(-21.35,18.635,0.35) rot=(0,0,1;0rad)
  Support = -> [XY_Plane073]
  Width = 0.23
FEATURE [PartDesign::SubtractiveBox] Box627
  AttacherType = Attacher::AttachEngine3D
  AttachmentOffset = pos=(-20.5,18.63,0) rot=(0,0,1;0rad)
  BaseFeature = -> Box643
  Height = 1.635
  Length = 0.5
  MapMode = 5
  Placement = pos=(-20.5,18.63,0) rot=(0,0,1;0rad)
  Support = -> [XY_Plane073]
  Width = 0.25
FEATURE [PartDesign::SubtractiveBox] Box632
  AttacherType = Attacher::AttachEngine3D
  AttachmentOffset = pos=(-21.19,18.635,-0.12) rot=(0,-1,0;0.15708rad)
  BaseFeature = -> Box627
  Height = 0.12
  Length = 0.725
  MapMode = 5
  Placement = pos=(-21.19,18.635,-0.12) rot=(0,-1,0;0.15708rad)
  Support = -> [XY_Plane073]
  Width = 0.25
FEATURE [PartDesign::SubtractiveBox] Box638
  AttacherType = Attacher::AttachEngine3D
  AttachmentOffset = pos=(-21.5005,18.625,0.235) rot=(0,-1,0;0.174533rad)
  BaseFeature = -> Box632
  Height = 0.3
  Length = 0.6605
  MapMode = 5
  Placement = pos=(-21.5005,18.625,0.235) rot=(0,-1,0;0.174533rad)
  Support = -> [XY_Plane073]
  Width = 0.25
FEATURE [PartDesign::SubtractiveBox] Box645
  AttacherType = Attacher::AttachEngine3D
  AttachmentOffset = pos=(-21.35,18.635,0.35) rot=(0,0,1;0rad)
  BaseFeature = -> Box637
  Height = 1.55
  Length = 0.5
  MapMode = 5
  Placement = pos=(-21.35,18.635,0.35) rot=(0,0,1;0rad)
  Support = -> [XY_Plane074]
  Width = 0.23
FEATURE [PartDesign::SubtractiveBox] Box629
  AttacherType = Attacher::AttachEngine3D
  AttachmentOffset = pos=(-20.5,18.63,0) rot=(0,0,1;0rad)
  BaseFeature = -> Box645
  Height = 1.635
  Length = 0.5
  MapMode = 5
  Placement = pos=(-20.5,18.63,0) rot=(0,0,1;0rad)
  Support = -> [XY_Plane074]
  Width = 0.25
FEATURE [PartDesign::SubtractiveBox] Box634
  AttacherType = Attacher::AttachEngine3D
  AttachmentOffset = pos=(-21.19,18.635,-0.12) rot=(0,-1,0;0.15708rad)
  BaseFeature = -> Box629
  Height = 0.12
  Length = 0.725
  MapMode = 5
  Placement = pos=(-21.19,18.635,-0.12) rot=(0,-1,0;0.15708rad)
  Support = -> [XY_Plane074]
  Width = 0.25
FEATURE [PartDesign::AdditiveBox] Box649
  AttacherType = Attacher::AttachEngine3D
  AttachmentOffset = pos=(-21.3,18.635,0) rot=(0,0,1;0rad)
  Height = 1.9
  Length = 1.3
  MapMode = 5
  Placement = pos=(-21.3,18.635,0) rot=(0,0,1;0rad)
  Support = -> [XY_Plane072]
  Width = 0.23
FEATURE [PartDesign::AdditiveBox] Box652
  AttacherType = Attacher::AttachEngine3D
  AttachmentOffset = pos=(-21.3,18.635,0) rot=(0,0,1;0rad)
  Height = 1.9
  Length = 1.3
  MapMode = 5
  Placement = pos=(-21.3,18.635,0) rot=(0,0,1;0rad)
  Support = -> [XY_Plane076]
  Width = 0.23
FEATURE [PartDesign::AdditiveBox] Box654
  AttacherType = Attacher::AttachEngine3D
  AttachmentOffset = pos=(-21.3,18.635,0) rot=(0,0,1;0rad)
  Height = 1.9
  Length = 1.3
  MapMode = 5
  Placement = pos=(-21.3,18.635,0) rot=(0,0,1;0rad)
  Support = -> [XY_Plane068]
  Width = 0.23
FEATURE [PartDesign::SubtractiveBox] Box660
  AttacherType = Attacher::AttachEngine3D
  AttachmentOffset = pos=(-21.35,18.635,0.35) rot=(0,0,1;0rad)
  BaseFeature = -> Box654
  Height = 1.55
  Length = 0.5
  MapMode = 5
  Placement = pos=(-21.35,18.635,0.35) rot=(0,0,1;0rad)
  Support = -> [XY_Plane068]
  Width = 0.23
FEATURE [PartDesign::SubtractiveBox] Box608
  AttacherType = Attacher::AttachEngine3D
  AttachmentOffset = pos=(-20.5,18.63,0) rot=(0,0,1;0rad)
  BaseFeature = -> Box660
  Height = 1.635
  Length = 0.5
  MapMode = 5
  Placement = pos=(-20.5,18.63,0) rot=(0,0,1;0rad)
  Support = -> [XY_Plane068]
  Width = 0.25
FEATURE [PartDesign::SubtractiveBox] Box620
  AttacherType = Attacher::AttachEngine3D
  AttachmentOffset = pos=(-21.19,18.635,-0.12) rot=(0,-1,0;0.15708rad)
  BaseFeature = -> Box608
  Height = 0.12
  Length = 0.725
  MapMode = 5
  Placement = pos=(-21.19,18.635,-0.12) rot=(0,-1,0;0.15708rad)
  Support = -> [XY_Plane068]
  Width = 0.25
FEATURE [PartDesign::SubtractiveBox] Box616
  AttacherType = Attacher::AttachEngine3D
  AttachmentOffset = pos=(-21.5005,18.625,0.235) rot=(0,-1,0;0.174533rad)
  BaseFeature = -> Box620
  Height = 0.3
  Length = 0.6605
  MapMode = 5
  Placement = pos=(-21.5005,18.625,0.235) rot=(0,-1,0;0.174533rad)
  Support = -> [XY_Plane068]
  Width = 0.25
FEATURE [PartDesign::SubtractiveBox] Box663
  AttacherType = Attacher::AttachEngine3D
  AttachmentOffset = pos=(-21.35,18.635,0.35) rot=(0,0,1;0rad)
  BaseFeature = -> Box649
  Height = 1.55
  Length = 0.5
  MapMode = 5
  Placement = pos=(-21.35,18.635,0.35) rot=(0,0,1;0rad)
  Support = -> [XY_Plane072]
  Width = 0.23
FEATURE [PartDesign::SubtractiveBox] Box646
  AttacherType = Attacher::AttachEngine3D
  AttachmentOffset = pos=(-20.5,18.63,0) rot=(0,0,1;0rad)
  BaseFeature = -> Box663
  Height = 1.635
  Length = 0.5
  MapMode = 5
  Placement = pos=(-20.5,18.63,0) rot=(0,0,1;0rad)
  Support = -> [XY_Plane072]
  Width = 0.25
FEATURE [PartDesign::AdditiveBox] Box664
  AttacherType = Attacher::AttachEngine3D
  AttachmentOffset = pos=(-21.3,18.635,0) rot=(0,0,1;0rad)
  Height = 1.9
  Length = 1.3
  MapMode = 5
  Placement = pos=(-21.3,18.635,0) rot=(0,0,1;0rad)
  Support = -> [XY_Plane077]
  Width = 0.23
FEATURE [PartDesign::SubtractiveBox] Box668
  AttacherType = Attacher::AttachEngine3D
  AttachmentOffset = pos=(-21.19,18.635,-0.12) rot=(0,-1,0;0.15708rad)
  BaseFeature = -> Box646
  Height = 0.12
  Length = 0.725
  MapMode = 5
  Placement = pos=(-21.19,18.635,-0.12) rot=(0,-1,0;0.15708rad)
  Support = -> [XY_Plane072]
  Width = 0.25
FEATURE [PartDesign::SubtractiveBox] Box658
  AttacherType = Attacher::AttachEngine3D
  AttachmentOffset = pos=(-21.5005,18.625,0.235) rot=(0,-1,0;0.174533rad)
  BaseFeature = -> Box668
  Height = 0.3
  Length = 0.6605
  MapMode = 5
  Placement = pos=(-21.5005,18.625,0.235) rot=(0,-1,0;0.174533rad)
  Support = -> [XY_Plane072]
  Width = 0.25
FEATURE [PartDesign::AdditiveBox] Box670
  AttacherType = Attacher::AttachEngine3D
  AttachmentOffset = pos=(-21.3,18.635,0) rot=(0,0,1;0rad)
  Height = 1.9
  Length = 1.3
  MapMode = 5
  Placement = pos=(-21.3,18.635,0) rot=(0,0,1;0rad)
  Support = -> [XY_Plane070]
  Width = 0.23
FEATURE [PartDesign::SubtractiveBox] Box618
  AttacherType = Attacher::AttachEngine3D
  AttachmentOffset = pos=(-21.35,18.635,0.35) rot=(0,0,1;0rad)
  BaseFeature = -> Box670
  Height = 1.55
  Length = 0.5
  MapMode = 5
  Placement = pos=(-21.35,18.635,0.35) rot=(0,0,1;0rad)
  Support = -> [XY_Plane070]
  Width = 0.23
FEATURE [PartDesign::SubtractiveBox] Box673
  AttacherType = Attacher::AttachEngine3D
  AttachmentOffset = pos=(-21.35,18.635,0.35) rot=(0,0,1;0rad)
  BaseFeature = -> Box664
  Height = 1.55
  Length = 0.5
  MapMode = 5
  Placement = pos=(-21.35,18.635,0.35) rot=(0,0,1;0rad)
  Support = -> [XY_Plane077]
  Width = 0.23
FEATURE [PartDesign::SubtractiveBox] Box675
  AttacherType = Attacher::AttachEngine3D
  AttachmentOffset = pos=(-21.35,18.635,0.35) rot=(0,0,1;0rad)
  BaseFeature = -> Box652
  Height = 1.55
  Length = 0.5
  MapMode = 5
  Placement = pos=(-21.35,18.635,0.35) rot=(0,0,1;0rad)
  Support = -> [XY_Plane076]
  Width = 0.23
FEATURE [PartDesign::SubtractiveBox] Box639
  AttacherType = Attacher::AttachEngine3D
  AttachmentOffset = pos=(-20.5,18.63,0) rot=(0,0,1;0rad)
  BaseFeature = -> Box675
  Height = 1.635
  Length = 0.5
  MapMode = 5
  Placement = pos=(-20.5,18.63,0) rot=(0,0,1;0rad)
  Support = -> [XY_Plane076]
  Width = 0.25
FEATURE [PartDesign::SubtractiveBox] Box683
  AttacherType = Attacher::AttachEngine3D
  AttachmentOffset = pos=(-21.5005,18.625,0.235) rot=(0,-1,0;0.174533rad)
  BaseFeature = -> Box634
  Height = 0.3
  Length = 0.6605
  MapMode = 5
  Placement = pos=(-21.5005,18.625,0.235) rot=(0,-1,0;0.174533rad)
  Support = -> [XY_Plane074]
  Width = 0.25
FEATURE [PartDesign::SubtractiveBox] Box686
  AttacherType = Attacher::AttachEngine3D
  AttachmentOffset = pos=(-20.5,18.63,0) rot=(0,0,1;0rad)
  BaseFeature = -> Box673
  Height = 1.635
  Length = 0.5
  MapMode = 5
  Placement = pos=(-20.5,18.63,0) rot=(0,0,1;0rad)
  Support = -> [XY_Plane077]
  Width = 0.25
FEATURE [PartDesign::SubtractiveBox] Box657
  AttacherType = Attacher::AttachEngine3D
  AttachmentOffset = pos=(-21.19,18.635,-0.12) rot=(0,-1,0;0.15708rad)
  BaseFeature = -> Box686
  Height = 0.12
  Length = 0.725
  MapMode = 5
  Placement = pos=(-21.19,18.635,-0.12) rot=(0,-1,0;0.15708rad)
  Support = -> [XY_Plane077]
  Width = 0.25
FEATURE [PartDesign::SubtractiveBox] Box656
  AttacherType = Attacher::AttachEngine3D
  AttachmentOffset = pos=(-21.5005,18.625,0.235) rot=(0,-1,0;0.174533rad)
  BaseFeature = -> Box657
  Height = 0.3
  Length = 0.6605
  MapMode = 5
  Placement = pos=(-21.5005,18.625,0.235) rot=(0,-1,0;0.174533rad)
  Support = -> [XY_Plane077]
  Width = 0.25
FEATURE [PartDesign::SubtractiveBox] Box691
  AttacherType = Attacher::AttachEngine3D
  AttachmentOffset = pos=(-21.19,18.635,-0.12) rot=(0,-1,0;0.15708rad)
  BaseFeature = -> Box639
  Height = 0.12
  Length = 0.725
  MapMode = 5
  Placement = pos=(-21.19,18.635,-0.12) rot=(0,-1,0;0.15708rad)
  Support = -> [XY_Plane076]
  Width = 0.25
FEATURE [PartDesign::SubtractiveBox] Box651
  AttacherType = Attacher::AttachEngine3D
  AttachmentOffset = pos=(-21.5005,18.625,0.235) rot=(0,-1,0;0.174533rad)
  BaseFeature = -> Box691
  Height = 0.3
  Length = 0.6605
  MapMode = 5
  Placement = pos=(-21.5005,18.625,0.235) rot=(0,-1,0;0.174533rad)
  Support = -> [XY_Plane076]
  Width = 0.25
FEATURE [PartDesign::AdditiveBox] Box703
  AttacherType = Attacher::AttachEngine3D
  AttachmentOffset = pos=(-21.3,18.635,0) rot=(0,0,1;0rad)
  Height = 1.9
  Length = 1.3
  MapMode = 5
  Placement = pos=(-21.3,18.635,0) rot=(0,0,1;0rad)
  Support = -> [XY_Plane067]
  Width = 0.23
FEATURE [PartDesign::SubtractiveBox] Box705
  AttacherType = Attacher::AttachEngine3D
  AttachmentOffset = pos=(-20.5,18.63,0) rot=(0,0,1;0rad)
  BaseFeature = -> Box607
  Height = 1.635
  Length = 0.5
  MapMode = 5
  Placement = pos=(-20.5,18.63,0) rot=(0,0,1;0rad)
  Support = -> [XY_Plane066]
  Width = 0.25
FEATURE [PartDesign::SubtractiveBox] Box701
  AttacherType = Attacher::AttachEngine3D
  AttachmentOffset = pos=(-21.19,18.635,-0.12) rot=(0,-1,0;0.15708rad)
  BaseFeature = -> Box705
  Height = 0.12
  Length = 0.725
  MapMode = 5
  Placement = pos=(-21.19,18.635,-0.12) rot=(0,-1,0;0.15708rad)
  Support = -> [XY_Plane066]
  Width = 0.25
FEATURE [PartDesign::SubtractiveBox] Box617
  AttacherType = Attacher::AttachEngine3D
  AttachmentOffset = pos=(-21.5005,18.625,0.235) rot=(0,-1,0;0.174533rad)
  BaseFeature = -> Box701
  Height = 0.3
  Length = 0.6605
  MapMode = 5
  Placement = pos=(-21.5005,18.625,0.235) rot=(0,-1,0;0.174533rad)
  Support = -> [XY_Plane066]
  Width = 0.25
FEATURE [PartDesign::Fillet] Fillet187
  Base = -> Box617 [Edge2]
  BaseFeature = -> Box617
  Placement = pos=(-21.5005,18.625,0.235) rot=(0,-1,0;0.174533rad)
  Radius = 0.05
  SupportTransform = false
FEATURE [PartDesign::SubtractiveBox] Box710
  AttacherType = Attacher::AttachEngine3D
  AttachmentOffset = pos=(-21.35,18.635,0.35) rot=(0,0,1;0rad)
  BaseFeature = -> Box703
  Height = 1.55
  Length = 0.5
  MapMode = 5
  Placement = pos=(-21.35,18.635,0.35) rot=(0,0,1;0rad)
  Support = -> [XY_Plane067]
  Width = 0.23
FEATURE [PartDesign::SubtractiveBox] Box688
  AttacherType = Attacher::AttachEngine3D
  AttachmentOffset = pos=(-20.5,18.63,0) rot=(0,0,1;0rad)
  BaseFeature = -> Box710
  Height = 1.635
  Length = 0.5
  MapMode = 5
  Placement = pos=(-20.5,18.63,0) rot=(0,0,1;0rad)
  Support = -> [XY_Plane067]
  Width = 0.25
FEATURE [PartDesign::SubtractiveBox] Box687
  AttacherType = Attacher::AttachEngine3D
  AttachmentOffset = pos=(-21.19,18.635,-0.12) rot=(0,-1,0;0.15708rad)
  BaseFeature = -> Box688
  Height = 0.12
  Length = 0.725
  MapMode = 5
  Placement = pos=(-21.19,18.635,-0.12) rot=(0,-1,0;0.15708rad)
  Support = -> [XY_Plane067]
  Width = 0.25
FEATURE [PartDesign::SubtractiveBox] Box706
  AttacherType = Attacher::AttachEngine3D
  AttachmentOffset = pos=(-21.5005,18.625,0.235) rot=(0,-1,0;0.174533rad)
  BaseFeature = -> Box687
  Height = 0.3
  Length = 0.6605
  MapMode = 5
  Placement = pos=(-21.5005,18.625,0.235) rot=(0,-1,0;0.174533rad)
  Support = -> [XY_Plane067]
  Width = 0.25
FEATURE [PartDesign::AdditiveBox] Box712
  AttacherType = Attacher::AttachEngine3D
  AttachmentOffset = pos=(-21.3,18.635,0) rot=(0,0,1;0rad)
  Height = 1.9
  Length = 1.3
  MapMode = 5
  Placement = pos=(-21.3,18.635,0) rot=(0,0,1;0rad)
  Support = -> [XY_Plane075]
  Width = 0.23
FEATURE [PartDesign::SubtractiveBox] Box680
  AttacherType = Attacher::AttachEngine3D
  AttachmentOffset = pos=(-21.35,18.635,0.35) rot=(0,0,1;0rad)
  BaseFeature = -> Box712
  Height = 1.55
  Length = 0.5
  MapMode = 5
  Placement = pos=(-21.35,18.635,0.35) rot=(0,0,1;0rad)
  Support = -> [XY_Plane075]
  Width = 0.23
FEATURE [PartDesign::SubtractiveBox] Box676
  AttacherType = Attacher::AttachEngine3D
  AttachmentOffset = pos=(-20.5,18.63,0) rot=(0,0,1;0rad)
  BaseFeature = -> Box680
  Height = 1.635
  Length = 0.5
  MapMode = 5
  Placement = pos=(-20.5,18.63,0) rot=(0,0,1;0rad)
  Support = -> [XY_Plane075]
  Width = 0.25
FEATURE [PartDesign::SubtractiveBox] Box699
  AttacherType = Attacher::AttachEngine3D
  AttachmentOffset = pos=(-21.19,18.635,-0.12) rot=(0,-1,0;0.15708rad)
  BaseFeature = -> Box676
  Height = 0.12
  Length = 0.725
  MapMode = 5
  Placement = pos=(-21.19,18.635,-0.12) rot=(0,-1,0;0.15708rad)
  Support = -> [XY_Plane075]
  Width = 0.25
FEATURE [PartDesign::SubtractiveBox] Box689
  AttacherType = Attacher::AttachEngine3D
  AttachmentOffset = pos=(-21.5005,18.625,0.235) rot=(0,-1,0;0.174533rad)
  BaseFeature = -> Box699
  Height = 0.3
  Length = 0.6605
  MapMode = 5
  Placement = pos=(-21.5005,18.625,0.235) rot=(0,-1,0;0.174533rad)
  Support = -> [XY_Plane075]
  Width = 0.25
FEATURE [PartDesign::Fillet] Fillet188
  Base = -> Box689 [Edge2]
  BaseFeature = -> Box689
  Placement = pos=(-21.5005,18.625,0.235) rot=(0,-1,0;0.174533rad)
  Radius = 0.05
  SupportTransform = false
FEATURE [PartDesign::AdditiveBox] Box713
  AttacherType = Attacher::AttachEngine3D
  AttachmentOffset = pos=(-21.3,18.635,0) rot=(0,0,1;0rad)
  Height = 1.9
  Length = 1.3
  MapMode = 5
  Placement = pos=(-21.3,18.635,0) rot=(0,0,1;0rad)
  Support = -> [XY_Plane071]
  Width = 0.23
FEATURE [PartDesign::SubtractiveBox] Box714
  AttacherType = Attacher::AttachEngine3D
  AttachmentOffset = pos=(-20.5,18.63,0) rot=(0,0,1;0rad)
  BaseFeature = -> Box618
  Height = 1.635
  Length = 0.5
  MapMode = 5
  Placement = pos=(-20.5,18.63,0) rot=(0,0,1;0rad)
  Support = -> [XY_Plane070]
  Width = 0.25
FEATURE [PartDesign::SubtractiveBox] Box602
  AttacherType = Attacher::AttachEngine3D
  AttachmentOffset = pos=(-21.19,18.635,-0.12) rot=(0,-1,0;0.15708rad)
  BaseFeature = -> Box714
  Height = 0.12
  Length = 0.725
  MapMode = 5
  Placement = pos=(-21.19,18.635,-0.12) rot=(0,-1,0;0.15708rad)
  Support = -> [XY_Plane070]
  Width = 0.25
FEATURE [PartDesign::SubtractiveBox] Box611
  AttacherType = Attacher::AttachEngine3D
  AttachmentOffset = pos=(-21.5005,18.625,0.235) rot=(0,-1,0;0.174533rad)
  BaseFeature = -> Box602
  Height = 0.3
  Length = 0.6605
  MapMode = 5
  Placement = pos=(-21.5005,18.625,0.235) rot=(0,-1,0;0.174533rad)
  Support = -> [XY_Plane070]
  Width = 0.25
FEATURE [PartDesign::SubtractiveBox] Box718
  AttacherType = Attacher::AttachEngine3D
  AttachmentOffset = pos=(-21.35,18.635,0.35) rot=(0,0,1;0rad)
  BaseFeature = -> Box713
  Height = 1.55
  Length = 0.5
  MapMode = 5
  Placement = pos=(-21.35,18.635,0.35) rot=(0,0,1;0rad)
  Support = -> [XY_Plane071]
  Width = 0.23
FEATURE [PartDesign::SubtractiveBox] Box700
  AttacherType = Attacher::AttachEngine3D
  AttachmentOffset = pos=(-20.5,18.63,0) rot=(0,0,1;0rad)
  BaseFeature = -> Box718
  Height = 1.635
  Length = 0.5
  MapMode = 5
  Placement = pos=(-20.5,18.63,0) rot=(0,0,1;0rad)
  Support = -> [XY_Plane071]
  Width = 0.25
FEATURE [PartDesign::SubtractiveBox] Box702
  AttacherType = Attacher::AttachEngine3D
  AttachmentOffset = pos=(-21.19,18.635,-0.12) rot=(0,-1,0;0.15708rad)
  BaseFeature = -> Box700
  Height = 0.12
  Length = 0.725
  MapMode = 5
  Placement = pos=(-21.19,18.635,-0.12) rot=(0,-1,0;0.15708rad)
  Support = -> [XY_Plane071]
  Width = 0.25
FEATURE [PartDesign::SubtractiveBox] Box698
  AttacherType = Attacher::AttachEngine3D
  AttachmentOffset = pos=(-21.5005,18.625,0.235) rot=(0,-1,0;0.174533rad)
  BaseFeature = -> Box702
  Height = 0.3
  Length = 0.6605
  MapMode = 5
  Placement = pos=(-21.5005,18.625,0.235) rot=(0,-1,0;0.174533rad)
  Support = -> [XY_Plane071]
  Width = 0.25
FEATURE [PartDesign::SubtractiveBox] Box719
  AttacherType = Attacher::AttachEngine3D
  AttachmentOffset = pos=(-20.5,18.63,0) rot=(0,0,1;0rad)
  BaseFeature = -> Box606
  Height = 1.635
  Length = 0.5
  MapMode = 5
  Placement = pos=(-20.5,18.63,0) rot=(0,0,1;0rad)
  Support = -> [XY_Plane069]
  Width = 0.25
FEATURE [PartDesign::SubtractiveBox] Box666
  AttacherType = Attacher::AttachEngine3D
  AttachmentOffset = pos=(-21.19,18.635,-0.12) rot=(0,-1,0;0.15708rad)
  BaseFeature = -> Box719
  Height = 0.12
  Length = 0.725
  MapMode = 5
  Placement = pos=(-21.19,18.635,-0.12) rot=(0,-1,0;0.15708rad)
  Support = -> [XY_Plane069]
  Width = 0.25
FEATURE [PartDesign::SubtractiveBox] Box619
  AttacherType = Attacher::AttachEngine3D
  AttachmentOffset = pos=(-21.5005,18.625,0.235) rot=(0,-1,0;0.174533rad)
  BaseFeature = -> Box666
  Height = 0.3
  Length = 0.6605
  MapMode = 5
  Placement = pos=(-21.5005,18.625,0.235) rot=(0,-1,0;0.174533rad)
  Support = -> [XY_Plane069]
  Width = 0.25
FEATURE [PartDesign::Fillet] Fillet190
  Base = -> Box619 [Edge2]
  BaseFeature = -> Box619
  Placement = pos=(-21.5005,18.625,0.235) rot=(0,-1,0;0.174533rad)
  Radius = 0.05
  SupportTransform = false
FEATURE [PartDesign::Fillet] Fillet181
  Base = -> Fillet190 [Edge33]
  BaseFeature = -> Fillet190
  Placement = pos=(-21.5005,18.625,0.235) rot=(0,-1,0;0.174533rad)
  Radius = 0.5
  SupportTransform = false
FEATURE [PartDesign::AdditiveBox] Box708
  AttacherType = Attacher::AttachEngine3D
  AttachmentOffset = pos=(-21.1,18.635,0.305) rot=(0,1,0;0.785398rad)
  BaseFeature = -> Fillet181
  Height = 0.375
  Length = 0.2
  MapMode = 5
  Placement = pos=(-21.1,18.635,0.305) rot=(0,1,0;0.785398rad)
  Support = -> [XY_Plane069]
  Width = 0.23
FEATURE [PartDesign::SubtractiveCylinder] Cylinder138
  Angle = 360
  AttacherType = Attacher::AttachEngine3D
  AttachmentOffset = pos=(-21.055,18.935,0.52) rot=(1,0,0;1.5708rad)
  BaseFeature = -> Box708
  Height = 0.375
  MapMode = 5
  Placement = pos=(-21.055,18.935,0.52) rot=(1,0,0;1.5708rad)
  Radius = 0.205
  Support = -> [XY_Plane069]
FEATURE [PartDesign::SubtractiveBox] Box601
  AttacherType = Attacher::AttachEngine3D
  AttachmentOffset = pos=(-20.95,18.635,0.53) rot=(0,0,1;0rad)
  BaseFeature = -> Cylinder138
  Height = 0.5
  Length = 0.1
  MapMode = 5
  Placement = pos=(-20.95,18.635,0.53) rot=(0,0,1;0rad)
  Support = -> [XY_Plane069]
  Width = 0.23
FEATURE [PartDesign::SubtractiveBox] Box609
  AttacherType = Attacher::AttachEngine3D
  AttachmentOffset = pos=(-21.15,18.635,0.297) rot=(0,-1,0;0.174533rad)
  BaseFeature = -> Box601
  Height = 0.115
  Length = 0.115
  MapMode = 5
  Placement = pos=(-21.15,18.635,0.297) rot=(0,-1,0;0.174533rad)
  Support = -> [XY_Plane069]
  Width = 0.23
FEATURE [PartDesign::Fillet] Fillet184
  Base = -> Box609 [Edge28]
  BaseFeature = -> Box609
  Placement = pos=(-21.15,18.635,0.297) rot=(0,-1,0;0.174533rad)
  Radius = 0.375
  SupportTransform = false
FEATURE [PartDesign::AdditiveBox] Box614
  AttacherType = Attacher::AttachEngine3D
  AttachmentOffset = pos=(-20.7,18.635,1.55) rot=(0,1,0;0.785398rad)
  BaseFeature = -> Fillet184
  Height = 0.375
  Length = 0.23
  MapMode = 5
  Placement = pos=(-20.7,18.635,1.55) rot=(0,1,0;0.785398rad)
  Support = -> [XY_Plane069]
  Width = 0.23
FEATURE [PartDesign::SubtractiveCylinder] Cylinder140
  Angle = 360
  AttacherType = Attacher::AttachEngine3D
  AttachmentOffset = pos=(-20.271,18.635,1.4056) rot=(-1,0,0;1.5708rad)
  BaseFeature = -> Box614
  Height = 0.23
  MapMode = 5
  Placement = pos=(-20.271,18.635,1.4056) rot=(-1,0,0;1.5708rad)
  Radius = 0.23
  Support = -> [XY_Plane069]
FEATURE [PartDesign::AdditiveBox] Box605
  AttacherType = Attacher::AttachEngine3D
  AttachmentOffset = pos=(-20.1,18.635,1.635) rot=(0,0,1;0rad)
  BaseFeature = -> Cylinder140
  Height = 0.265
  Length = 0.23
  MapMode = 5
  Placement = pos=(-20.1,18.635,1.635) rot=(0,0,1;0rad)
  Support = -> [XY_Plane069]
  Width = 0.23
FEATURE [PartDesign::Fillet] Fillet191
  Base = -> Fillet188 [Edge33]
  BaseFeature = -> Fillet188
  Placement = pos=(-21.5005,18.625,0.235) rot=(0,-1,0;0.174533rad)
  Radius = 0.5
  SupportTransform = false
FEATURE [PartDesign::AdditiveBox] Box684
  AttacherType = Attacher::AttachEngine3D
  AttachmentOffset = pos=(-21.1,18.635,0.305) rot=(0,1,0;0.785398rad)
  BaseFeature = -> Fillet191
  Height = 0.375
  Length = 0.2
  MapMode = 5
  Placement = pos=(-21.1,18.635,0.305) rot=(0,1,0;0.785398rad)
  Support = -> [XY_Plane075]
  Width = 0.23
FEATURE [PartDesign::SubtractiveCylinder] Cylinder142
  Angle = 360
  AttacherType = Attacher::AttachEngine3D
  AttachmentOffset = pos=(-21.055,18.935,0.52) rot=(1,0,0;1.5708rad)
  BaseFeature = -> Box684
  Height = 0.375
  MapMode = 5
  Placement = pos=(-21.055,18.935,0.52) rot=(1,0,0;1.5708rad)
  Radius = 0.205
  Support = -> [XY_Plane075]
FEATURE [PartDesign::SubtractiveBox] Box692
  AttacherType = Attacher::AttachEngine3D
  AttachmentOffset = pos=(-20.95,18.635,0.53) rot=(0,0,1;0rad)
  BaseFeature = -> Cylinder142
  Height = 0.5
  Length = 0.1
  MapMode = 5
  Placement = pos=(-20.95,18.635,0.53) rot=(0,0,1;0rad)
  Support = -> [XY_Plane075]
  Width = 0.23
FEATURE [PartDesign::SubtractiveBox] Box685
  AttacherType = Attacher::AttachEngine3D
  AttachmentOffset = pos=(-21.15,18.635,0.297) rot=(0,-1,0;0.174533rad)
  BaseFeature = -> Box692
  Height = 0.115
  Length = 0.115
  MapMode = 5
  Placement = pos=(-21.15,18.635,0.297) rot=(0,-1,0;0.174533rad)
  Support = -> [XY_Plane075]
  Width = 0.23
FEATURE [PartDesign::Fillet] Fillet192
  Base = -> Box611 [Edge2]
  BaseFeature = -> Box611
  Placement = pos=(-21.5005,18.625,0.235) rot=(0,-1,0;0.174533rad)
  Radius = 0.05
  SupportTransform = false
FEATURE [PartDesign::Fillet] Fillet186
  Base = -> Fillet192 [Edge33]
  BaseFeature = -> Fillet192
  Placement = pos=(-21.5005,18.625,0.235) rot=(0,-1,0;0.174533rad)
  Radius = 0.5
  SupportTransform = false
FEATURE [PartDesign::AdditiveBox] Box717
  AttacherType = Attacher::AttachEngine3D
  AttachmentOffset = pos=(-21.1,18.635,0.305) rot=(0,1,0;0.785398rad)
  BaseFeature = -> Fillet186
  Height = 0.375
  Length = 0.2
  MapMode = 5
  Placement = pos=(-21.1,18.635,0.305) rot=(0,1,0;0.785398rad)
  Support = -> [XY_Plane070]
  Width = 0.23
FEATURE [PartDesign::SubtractiveCylinder] Cylinder147
  Angle = 360
  AttacherType = Attacher::AttachEngine3D
  AttachmentOffset = pos=(-21.055,18.935,0.52) rot=(1,0,0;1.5708rad)
  BaseFeature = -> Box717
  Height = 0.375
  MapMode = 5
  Placement = pos=(-21.055,18.935,0.52) rot=(1,0,0;1.5708rad)
  Radius = 0.205
  Support = -> [XY_Plane070]
FEATURE [PartDesign::SubtractiveBox] Box621
  AttacherType = Attacher::AttachEngine3D
  AttachmentOffset = pos=(-20.95,18.635,0.53) rot=(0,0,1;0rad)
  BaseFeature = -> Cylinder147
  Height = 0.5
  Length = 0.1
  MapMode = 5
  Placement = pos=(-20.95,18.635,0.53) rot=(0,0,1;0rad)
  Support = -> [XY_Plane070]
  Width = 0.23
FEATURE [PartDesign::SubtractiveBox] Box669
  AttacherType = Attacher::AttachEngine3D
  AttachmentOffset = pos=(-21.15,18.635,0.297) rot=(0,-1,0;0.174533rad)
  BaseFeature = -> Box621
  Height = 0.115
  Length = 0.115
  MapMode = 5
  Placement = pos=(-21.15,18.635,0.297) rot=(0,-1,0;0.174533rad)
  Support = -> [XY_Plane070]
  Width = 0.23
FEATURE [PartDesign::Fillet] Fillet185
  Base = -> Box669 [Edge28]
  BaseFeature = -> Box669
  Placement = pos=(-21.15,18.635,0.297) rot=(0,-1,0;0.174533rad)
  Radius = 0.375
  SupportTransform = false
FEATURE [PartDesign::AdditiveBox] Box707
  AttacherType = Attacher::AttachEngine3D
  AttachmentOffset = pos=(-20.7,18.635,1.55) rot=(0,1,0;0.785398rad)
  BaseFeature = -> Fillet185
  Height = 0.375
  Length = 0.23
  MapMode = 5
  Placement = pos=(-20.7,18.635,1.55) rot=(0,1,0;0.785398rad)
  Support = -> [XY_Plane070]
  Width = 0.23
FEATURE [PartDesign::SubtractiveCylinder] Cylinder125
  Angle = 360
  AttacherType = Attacher::AttachEngine3D
  AttachmentOffset = pos=(-20.271,18.635,1.4056) rot=(-1,0,0;1.5708rad)
  BaseFeature = -> Box707
  Height = 0.23
  MapMode = 5
  Placement = pos=(-20.271,18.635,1.4056) rot=(-1,0,0;1.5708rad)
  Radius = 0.23
  Support = -> [XY_Plane070]
FEATURE [PartDesign::AdditiveBox] Box615
  AttacherType = Attacher::AttachEngine3D
  AttachmentOffset = pos=(-20.1,18.635,1.635) rot=(0,0,1;0rad)
  BaseFeature = -> Cylinder125
  Height = 0.265
  Length = 0.23
  MapMode = 5
  Placement = pos=(-20.1,18.635,1.635) rot=(0,0,1;0rad)
  Support = -> [XY_Plane070]
  Width = 0.23
FEATURE [PartDesign::Body] Body062  label="pin062"
  Group = -> [Box670,Box618,Box714,Box602,Box611,Fillet192,Fillet186,Box717,Cylinder147,Box621,Box669,Fillet185,Box707,Cylinder125,Box615]
  Origin = -> Origin072
  Placement = pos=(0,-2,0) rot=(0,0,1;0rad)
  Tip = -> Box615
FEATURE [PartDesign::Fillet] Fillet194
  Base = -> Box706 [Edge2]
  BaseFeature = -> Box706
  Placement = pos=(-21.5005,18.625,0.235) rot=(0,-1,0;0.174533rad)
  Radius = 0.05
  SupportTransform = false
FEATURE [PartDesign::Fillet] Fillet180
  Base = -> Fillet194 [Edge33]
  BaseFeature = -> Fillet194
  Placement = pos=(-21.5005,18.625,0.235) rot=(0,-1,0;0.174533rad)
  Radius = 0.5
  SupportTransform = false
FEATURE [PartDesign::AdditiveBox] Box672
  AttacherType = Attacher::AttachEngine3D
  AttachmentOffset = pos=(-21.1,18.635,0.305) rot=(0,1,0;0.785398rad)
  BaseFeature = -> Fillet180
  Height = 0.375
  Length = 0.2
  MapMode = 5
  Placement = pos=(-21.1,18.635,0.305) rot=(0,1,0;0.785398rad)
  Support = -> [XY_Plane067]
  Width = 0.23
FEATURE [PartDesign::SubtractiveCylinder] Cylinder134
  Angle = 360
  AttacherType = Attacher::AttachEngine3D
  AttachmentOffset = pos=(-21.055,18.935,0.52) rot=(1,0,0;1.5708rad)
  BaseFeature = -> Box672
  Height = 0.375
  MapMode = 5
  Placement = pos=(-21.055,18.935,0.52) rot=(1,0,0;1.5708rad)
  Radius = 0.205
  Support = -> [XY_Plane067]
FEATURE [PartDesign::SubtractiveBox] Box633
  AttacherType = Attacher::AttachEngine3D
  AttachmentOffset = pos=(-20.95,18.635,0.53) rot=(0,0,1;0rad)
  BaseFeature = -> Cylinder134
  Height = 0.5
  Length = 0.1
  MapMode = 5
  Placement = pos=(-20.95,18.635,0.53) rot=(0,0,1;0rad)
  Support = -> [XY_Plane067]
  Width = 0.23
FEATURE [PartDesign::SubtractiveBox] Box625
  AttacherType = Attacher::AttachEngine3D
  AttachmentOffset = pos=(-21.15,18.635,0.297) rot=(0,-1,0;0.174533rad)
  BaseFeature = -> Box633
  Height = 0.115
  Length = 0.115
  MapMode = 5
  Placement = pos=(-21.15,18.635,0.297) rot=(0,-1,0;0.174533rad)
  Support = -> [XY_Plane067]
  Width = 0.23
FEATURE [PartDesign::Fillet] Fillet195
  Base = -> Box638 [Edge2]
  BaseFeature = -> Box638
  Placement = pos=(-21.5005,18.625,0.235) rot=(0,-1,0;0.174533rad)
  Radius = 0.05
  SupportTransform = false
FEATURE [PartDesign::Fillet] Fillet182
  Base = -> Fillet195 [Edge33]
  BaseFeature = -> Fillet195
  Placement = pos=(-21.5005,18.625,0.235) rot=(0,-1,0;0.174533rad)
  Radius = 0.5
  SupportTransform = false
FEATURE [PartDesign::AdditiveBox] Box612
  AttacherType = Attacher::AttachEngine3D
  AttachmentOffset = pos=(-21.1,18.635,0.305) rot=(0,1,0;0.785398rad)
  BaseFeature = -> Fillet182
  Height = 0.375
  Length = 0.2
  MapMode = 5
  Placement = pos=(-21.1,18.635,0.305) rot=(0,1,0;0.785398rad)
  Support = -> [XY_Plane073]
  Width = 0.23
FEATURE [PartDesign::SubtractiveCylinder] Cylinder130
  Angle = 360
  AttacherType = Attacher::AttachEngine3D
  AttachmentOffset = pos=(-21.055,18.935,0.52) rot=(1,0,0;1.5708rad)
  BaseFeature = -> Box612
  Height = 0.375
  MapMode = 5
  Placement = pos=(-21.055,18.935,0.52) rot=(1,0,0;1.5708rad)
  Radius = 0.205
  Support = -> [XY_Plane073]
FEATURE [PartDesign::SubtractiveBox] Box640
  AttacherType = Attacher::AttachEngine3D
  AttachmentOffset = pos=(-20.95,18.635,0.53) rot=(0,0,1;0rad)
  BaseFeature = -> Cylinder130
  Height = 0.5
  Length = 0.1
  MapMode = 5
  Placement = pos=(-20.95,18.635,0.53) rot=(0,0,1;0rad)
  Support = -> [XY_Plane073]
  Width = 0.23
FEATURE [PartDesign::SubtractiveBox] Box613
  AttacherType = Attacher::AttachEngine3D
  AttachmentOffset = pos=(-21.15,18.635,0.297) rot=(0,-1,0;0.174533rad)
  BaseFeature = -> Box640
  Height = 0.115
  Length = 0.115
  MapMode = 5
  Placement = pos=(-21.15,18.635,0.297) rot=(0,-1,0;0.174533rad)
  Support = -> [XY_Plane073]
  Width = 0.23
FEATURE [PartDesign::Fillet] Fillet189
  Base = -> Box613 [Edge28]
  BaseFeature = -> Box613
  Placement = pos=(-21.15,18.635,0.297) rot=(0,-1,0;0.174533rad)
  Radius = 0.375
  SupportTransform = false
FEATURE [PartDesign::AdditiveBox] Box631
  AttacherType = Attacher::AttachEngine3D
  AttachmentOffset = pos=(-20.7,18.635,1.55) rot=(0,1,0;0.785398rad)
  BaseFeature = -> Fillet189
  Height = 0.375
  Length = 0.23
  MapMode = 5
  Placement = pos=(-20.7,18.635,1.55) rot=(0,1,0;0.785398rad)
  Support = -> [XY_Plane073]
  Width = 0.23
FEATURE [PartDesign::SubtractiveCylinder] Cylinder126
  Angle = 360
  AttacherType = Attacher::AttachEngine3D
  AttachmentOffset = pos=(-20.271,18.635,1.4056) rot=(-1,0,0;1.5708rad)
  BaseFeature = -> Box631
  Height = 0.23
  MapMode = 5
  Placement = pos=(-20.271,18.635,1.4056) rot=(-1,0,0;1.5708rad)
  Radius = 0.23
  Support = -> [XY_Plane073]
FEATURE [PartDesign::AdditiveBox] Box647
  AttacherType = Attacher::AttachEngine3D
  AttachmentOffset = pos=(-20.1,18.635,1.635) rot=(0,0,1;0rad)
  BaseFeature = -> Cylinder126
  Height = 0.265
  Length = 0.23
  MapMode = 5
  Placement = pos=(-20.1,18.635,1.635) rot=(0,0,1;0rad)
  Support = -> [XY_Plane073]
  Width = 0.23
FEATURE [PartDesign::Fillet] Fillet197
  Base = -> Box698 [Edge2]
  BaseFeature = -> Box698
  Placement = pos=(-21.5005,18.625,0.235) rot=(0,-1,0;0.174533rad)
  Radius = 0.05
  SupportTransform = false
FEATURE [PartDesign::Body] Body065  label="pin065"
  Group = -> [Box624,Box606,Box719,Box666,Box619,Fillet190,Fillet181,Box708,Cylinder138,Box601,Box609,Fillet184,Box614,Cylinder140,Box605]
  Origin = -> Origin070
  Placement = pos=(0,-2.5,0) rot=(0,0,1;0rad)
  Tip = -> Box605
FEATURE [PartDesign::Fillet] Fillet199
  Base = -> Fillet187 [Edge33]
  BaseFeature = -> Fillet187
  Placement = pos=(-21.5005,18.625,0.235) rot=(0,-1,0;0.174533rad)
  Radius = 0.5
  SupportTransform = false
FEATURE [PartDesign::AdditiveBox] Box720
  AttacherType = Attacher::AttachEngine3D
  AttachmentOffset = pos=(-21.1,18.635,0.305) rot=(0,1,0;0.785398rad)
  BaseFeature = -> Fillet199
  Height = 0.375
  Length = 0.2
  MapMode = 5
  Placement = pos=(-21.1,18.635,0.305) rot=(0,1,0;0.785398rad)
  Support = -> [XY_Plane066]
  Width = 0.23
FEATURE [PartDesign::SubtractiveCylinder] Cylinder145
  Angle = 360
  AttacherType = Attacher::AttachEngine3D
  AttachmentOffset = pos=(-21.055,18.935,0.52) rot=(1,0,0;1.5708rad)
  BaseFeature = -> Box720
  Height = 0.375
  MapMode = 5
  Placement = pos=(-21.055,18.935,0.52) rot=(1,0,0;1.5708rad)
  Radius = 0.205
  Support = -> [XY_Plane066]
FEATURE [PartDesign::SubtractiveBox] Box716
  AttacherType = Attacher::AttachEngine3D
  AttachmentOffset = pos=(-20.95,18.635,0.53) rot=(0,0,1;0rad)
  BaseFeature = -> Cylinder145
  Height = 0.5
  Length = 0.1
  MapMode = 5
  Placement = pos=(-20.95,18.635,0.53) rot=(0,0,1;0rad)
  Support = -> [XY_Plane066]
  Width = 0.23
FEATURE [PartDesign::SubtractiveBox] Box704
  AttacherType = Attacher::AttachEngine3D
  AttachmentOffset = pos=(-21.15,18.635,0.297) rot=(0,-1,0;0.174533rad)
  BaseFeature = -> Box716
  Height = 0.115
  Length = 0.115
  MapMode = 5
  Placement = pos=(-21.15,18.635,0.297) rot=(0,-1,0;0.174533rad)
  Support = -> [XY_Plane066]
  Width = 0.23
FEATURE [PartDesign::Fillet] Fillet200
  Base = -> Box616 [Edge2]
  BaseFeature = -> Box616
  Placement = pos=(-21.5005,18.625,0.235) rot=(0,-1,0;0.174533rad)
  Radius = 0.05
  SupportTransform = false
FEATURE [PartDesign::Fillet] Fillet202
  Base = -> Box704 [Edge28]
  BaseFeature = -> Box704
  Placement = pos=(-21.15,18.635,0.297) rot=(0,-1,0;0.174533rad)
  Radius = 0.375
  SupportTransform = false
FEATURE [PartDesign::AdditiveBox] Box715
  AttacherType = Attacher::AttachEngine3D
  AttachmentOffset = pos=(-20.7,18.635,1.55) rot=(0,1,0;0.785398rad)
  BaseFeature = -> Fillet202
  Height = 0.375
  Length = 0.23
  MapMode = 5
  Placement = pos=(-20.7,18.635,1.55) rot=(0,1,0;0.785398rad)
  Support = -> [XY_Plane066]
  Width = 0.23
FEATURE [PartDesign::SubtractiveCylinder] Cylinder137
  Angle = 360
  AttacherType = Attacher::AttachEngine3D
  AttachmentOffset = pos=(-20.271,18.635,1.4056) rot=(-1,0,0;1.5708rad)
  BaseFeature = -> Box715
  Height = 0.23
  MapMode = 5
  Placement = pos=(-20.271,18.635,1.4056) rot=(-1,0,0;1.5708rad)
  Radius = 0.23
  Support = -> [XY_Plane066]
FEATURE [PartDesign::AdditiveBox] Box711
  AttacherType = Attacher::AttachEngine3D
  AttachmentOffset = pos=(-20.1,18.635,1.635) rot=(0,0,1;0rad)
  BaseFeature = -> Cylinder137
  Height = 0.265
  Length = 0.23
  MapMode = 5
  Placement = pos=(-20.1,18.635,1.635) rot=(0,0,1;0rad)
  Support = -> [XY_Plane066]
  Width = 0.23
FEATURE [PartDesign::Body] Body066  label="pin066"
  Group = -> [Box622,Box607,Box705,Box701,Box617,Fillet187,Fillet199,Box720,Cylinder145,Box716,Box704,Fillet202,Box715,Cylinder137,Box711]
  Origin = -> Origin076
  Placement = pos=(0,-1.5,0) rot=(0,0,1;0rad)
  Tip = -> Box711
FEATURE [PartDesign::Fillet] Fillet203
  Base = -> Box651 [Edge2]
  BaseFeature = -> Box651
  Placement = pos=(-21.5005,18.625,0.235) rot=(0,-1,0;0.174533rad)
  Radius = 0.05
  SupportTransform = false
FEATURE [PartDesign::Fillet] Fillet204
  Base = -> Box685 [Edge28]
  BaseFeature = -> Box685
  Placement = pos=(-21.15,18.635,0.297) rot=(0,-1,0;0.174533rad)
  Radius = 0.375
  SupportTransform = false
FEATURE [PartDesign::AdditiveBox] Box690
  AttacherType = Attacher::AttachEngine3D
  AttachmentOffset = pos=(-20.7,18.635,1.55) rot=(0,1,0;0.785398rad)
  BaseFeature = -> Fillet204
  Height = 0.375
  Length = 0.23
  MapMode = 5
  Placement = pos=(-20.7,18.635,1.55) rot=(0,1,0;0.785398rad)
  Support = -> [XY_Plane075]
  Width = 0.23
FEATURE [PartDesign::SubtractiveCylinder] Cylinder143
  Angle = 360
  AttacherType = Attacher::AttachEngine3D
  AttachmentOffset = pos=(-20.271,18.635,1.4056) rot=(-1,0,0;1.5708rad)
  BaseFeature = -> Box690
  Height = 0.23
  MapMode = 5
  Placement = pos=(-20.271,18.635,1.4056) rot=(-1,0,0;1.5708rad)
  Radius = 0.23
  Support = -> [XY_Plane075]
FEATURE [PartDesign::AdditiveBox] Box695
  AttacherType = Attacher::AttachEngine3D
  AttachmentOffset = pos=(-20.1,18.635,1.635) rot=(0,0,1;0rad)
  BaseFeature = -> Cylinder143
  Height = 0.265
  Length = 0.23
  MapMode = 5
  Placement = pos=(-20.1,18.635,1.635) rot=(0,0,1;0rad)
  Support = -> [XY_Plane075]
  Width = 0.23
FEATURE [PartDesign::Body] Body061  label="pin061"
  Group = -> [Box712,Box680,Box676,Box699,Box689,Fillet188,Fillet191,Box684,Cylinder142,Box692,Box685,Fillet204,Box690,Cylinder143,Box695]
  Origin = -> Origin066
  Placement = pos=(0,-0.5,0) rot=(0,0,1;0rad)
  Tip = -> Box695
FEATURE [PartDesign::Body] Body071  label="pin071"
  Group = -> [Box635,Box643,Box627,Box632,Box638,Fillet195,Fillet182,Box612,Cylinder130,Box640,Box613,Fillet189,Box631,Cylinder126,Box647]
  Origin = -> Origin067
  Placement = pos=(0,-5,0) rot=(0,0,1;0rad)
  Tip = -> Box647
FEATURE [PartDesign::Fillet] Fillet209
  Base = -> Box658 [Edge2]
  BaseFeature = -> Box658
  Placement = pos=(-21.5005,18.625,0.235) rot=(0,-1,0;0.174533rad)
  Radius = 0.05
  SupportTransform = false
FEATURE [PartDesign::Fillet] Fillet207
  Base = -> Fillet209 [Edge33]
  BaseFeature = -> Fillet209
  Placement = pos=(-21.5005,18.625,0.235) rot=(0,-1,0;0.174533rad)
  Radius = 0.5
  SupportTransform = false
FEATURE [PartDesign::AdditiveBox] Box677
  AttacherType = Attacher::AttachEngine3D
  AttachmentOffset = pos=(-21.1,18.635,0.305) rot=(0,1,0;0.785398rad)
  BaseFeature = -> Fillet207
  Height = 0.375
  Length = 0.2
  MapMode = 5
  Placement = pos=(-21.1,18.635,0.305) rot=(0,1,0;0.785398rad)
  Support = -> [XY_Plane072]
  Width = 0.23
FEATURE [PartDesign::SubtractiveCylinder] Cylinder136
  Angle = 360
  AttacherType = Attacher::AttachEngine3D
  AttachmentOffset = pos=(-21.055,18.935,0.52) rot=(1,0,0;1.5708rad)
  BaseFeature = -> Box677
  Height = 0.375
  MapMode = 5
  Placement = pos=(-21.055,18.935,0.52) rot=(1,0,0;1.5708rad)
  Radius = 0.205
  Support = -> [XY_Plane072]
FEATURE [PartDesign::SubtractiveBox] Box667
  AttacherType = Attacher::AttachEngine3D
  AttachmentOffset = pos=(-20.95,18.635,0.53) rot=(0,0,1;0rad)
  BaseFeature = -> Cylinder136
  Height = 0.5
  Length = 0.1
  MapMode = 5
  Placement = pos=(-20.95,18.635,0.53) rot=(0,0,1;0rad)
  Support = -> [XY_Plane072]
  Width = 0.23
FEATURE [PartDesign::SubtractiveBox] Box659
  AttacherType = Attacher::AttachEngine3D
  AttachmentOffset = pos=(-21.15,18.635,0.297) rot=(0,-1,0;0.174533rad)
  BaseFeature = -> Box667
  Height = 0.115
  Length = 0.115
  MapMode = 5
  Placement = pos=(-21.15,18.635,0.297) rot=(0,-1,0;0.174533rad)
  Support = -> [XY_Plane072]
  Width = 0.23
FEATURE [PartDesign::Fillet] Fillet205
  Base = -> Box659 [Edge28]
  BaseFeature = -> Box659
  Placement = pos=(-21.15,18.635,0.297) rot=(0,-1,0;0.174533rad)
  Radius = 0.375
  SupportTransform = false
FEATURE [PartDesign::AdditiveBox] Box665
  AttacherType = Attacher::AttachEngine3D
  AttachmentOffset = pos=(-20.7,18.635,1.55) rot=(0,1,0;0.785398rad)
  BaseFeature = -> Fillet205
  Height = 0.375
  Length = 0.23
  MapMode = 5
  Placement = pos=(-20.7,18.635,1.55) rot=(0,1,0;0.785398rad)
  Support = -> [XY_Plane072]
  Width = 0.23
FEATURE [PartDesign::SubtractiveCylinder] Cylinder135
  Angle = 360
  AttacherType = Attacher::AttachEngine3D
  AttachmentOffset = pos=(-20.271,18.635,1.4056) rot=(-1,0,0;1.5708rad)
  BaseFeature = -> Box665
  Height = 0.23
  MapMode = 5
  Placement = pos=(-20.271,18.635,1.4056) rot=(-1,0,0;1.5708rad)
  Radius = 0.23
  Support = -> [XY_Plane072]
FEATURE [PartDesign::AdditiveBox] Box650
  AttacherType = Attacher::AttachEngine3D
  AttachmentOffset = pos=(-20.1,18.635,1.635) rot=(0,0,1;0rad)
  BaseFeature = -> Cylinder135
  Height = 0.265
  Length = 0.23
  MapMode = 5
  Placement = pos=(-20.1,18.635,1.635) rot=(0,0,1;0rad)
  Support = -> [XY_Plane072]
  Width = 0.23
FEATURE [PartDesign::Body] Body069  label="pin069"
  Group = -> [Box649,Box663,Box646,Box668,Box658,Fillet209,Fillet207,Box677,Cylinder136,Box667,Box659,Fillet205,Box665,Cylinder135,Box650]
  Origin = -> Origin078
  Placement = pos=(0,-4,0) rot=(0,0,1;0rad)
  Tip = -> Box650
FEATURE [PartDesign::Fillet] Fillet210
  Base = -> Fillet200 [Edge33]
  BaseFeature = -> Fillet200
  Placement = pos=(-21.5005,18.625,0.235) rot=(0,-1,0;0.174533rad)
  Radius = 0.5
  SupportTransform = false
FEATURE [PartDesign::AdditiveBox] Box644
  AttacherType = Attacher::AttachEngine3D
  AttachmentOffset = pos=(-21.1,18.635,0.305) rot=(0,1,0;0.785398rad)
  BaseFeature = -> Fillet210
  Height = 0.375
  Length = 0.2
  MapMode = 5
  Placement = pos=(-21.1,18.635,0.305) rot=(0,1,0;0.785398rad)
  Support = -> [XY_Plane068]
  Width = 0.23
FEATURE [PartDesign::SubtractiveCylinder] Cylinder132
  Angle = 360
  AttacherType = Attacher::AttachEngine3D
  AttachmentOffset = pos=(-21.055,18.935,0.52) rot=(1,0,0;1.5708rad)
  BaseFeature = -> Box644
  Height = 0.375
  MapMode = 5
  Placement = pos=(-21.055,18.935,0.52) rot=(1,0,0;1.5708rad)
  Radius = 0.205
  Support = -> [XY_Plane068]
FEATURE [PartDesign::SubtractiveBox] Box641
  AttacherType = Attacher::AttachEngine3D
  AttachmentOffset = pos=(-20.95,18.635,0.53) rot=(0,0,1;0rad)
  BaseFeature = -> Cylinder132
  Height = 0.5
  Length = 0.1
  MapMode = 5
  Placement = pos=(-20.95,18.635,0.53) rot=(0,0,1;0rad)
  Support = -> [XY_Plane068]
  Width = 0.23
FEATURE [PartDesign::SubtractiveBox] Box636
  AttacherType = Attacher::AttachEngine3D
  AttachmentOffset = pos=(-21.15,18.635,0.297) rot=(0,-1,0;0.174533rad)
  BaseFeature = -> Box641
  Height = 0.115
  Length = 0.115
  MapMode = 5
  Placement = pos=(-21.15,18.635,0.297) rot=(0,-1,0;0.174533rad)
  Support = -> [XY_Plane068]
  Width = 0.23
FEATURE [PartDesign::Fillet] Fillet198
  Base = -> Box636 [Edge28]
  BaseFeature = -> Box636
  Placement = pos=(-21.15,18.635,0.297) rot=(0,-1,0;0.174533rad)
  Radius = 0.375
  SupportTransform = false
FEATURE [PartDesign::AdditiveBox] Box648
  AttacherType = Attacher::AttachEngine3D
  AttachmentOffset = pos=(-20.7,18.635,1.55) rot=(0,1,0;0.785398rad)
  BaseFeature = -> Fillet198
  Height = 0.375
  Length = 0.23
  MapMode = 5
  Placement = pos=(-20.7,18.635,1.55) rot=(0,1,0;0.785398rad)
  Support = -> [XY_Plane068]
  Width = 0.23
FEATURE [PartDesign::SubtractiveCylinder] Cylinder133
  Angle = 360
  AttacherType = Attacher::AttachEngine3D
  AttachmentOffset = pos=(-20.271,18.635,1.4056) rot=(-1,0,0;1.5708rad)
  BaseFeature = -> Box648
  Height = 0.23
  MapMode = 5
  Placement = pos=(-20.271,18.635,1.4056) rot=(-1,0,0;1.5708rad)
  Radius = 0.23
  Support = -> [XY_Plane068]
FEATURE [PartDesign::AdditiveBox] Box642
  AttacherType = Attacher::AttachEngine3D
  AttachmentOffset = pos=(-20.1,18.635,1.635) rot=(0,0,1;0rad)
  BaseFeature = -> Cylinder133
  Height = 0.265
  Length = 0.23
  MapMode = 5
  Placement = pos=(-20.1,18.635,1.635) rot=(0,0,1;0rad)
  Support = -> [XY_Plane068]
  Width = 0.23
FEATURE [PartDesign::Body] Body072  label="pin072"
  Group = -> [Box654,Box660,Box608,Box620,Box616,Fillet200,Fillet210,Box644,Cylinder132,Box641,Box636,Fillet198,Box648,Cylinder133,Box642]
  Origin = -> Origin069
  Placement = pos=(0,-5.5,0) rot=(0,0,1;0rad)
  Tip = -> Box642
FEATURE [PartDesign::Fillet] Fillet211
  Base = -> Box625 [Edge28]
  BaseFeature = -> Box625
  Placement = pos=(-21.15,18.635,0.297) rot=(0,-1,0;0.174533rad)
  Radius = 0.375
  SupportTransform = false
FEATURE [PartDesign::AdditiveBox] Box682
  AttacherType = Attacher::AttachEngine3D
  AttachmentOffset = pos=(-20.7,18.635,1.55) rot=(0,1,0;0.785398rad)
  BaseFeature = -> Fillet211
  Height = 0.375
  Length = 0.23
  MapMode = 5
  Placement = pos=(-20.7,18.635,1.55) rot=(0,1,0;0.785398rad)
  Support = -> [XY_Plane067]
  Width = 0.23
FEATURE [PartDesign::SubtractiveCylinder] Cylinder128
  Angle = 360
  AttacherType = Attacher::AttachEngine3D
  AttachmentOffset = pos=(-20.271,18.635,1.4056) rot=(-1,0,0;1.5708rad)
  BaseFeature = -> Box682
  Height = 0.23
  MapMode = 5
  Placement = pos=(-20.271,18.635,1.4056) rot=(-1,0,0;1.5708rad)
  Radius = 0.23
  Support = -> [XY_Plane067]
FEATURE [PartDesign::AdditiveBox] Box694
  AttacherType = Attacher::AttachEngine3D
  AttachmentOffset = pos=(-20.1,18.635,1.635) rot=(0,0,1;0rad)
  BaseFeature = -> Cylinder128
  Height = 0.265
  Length = 0.23
  MapMode = 5
  Placement = pos=(-20.1,18.635,1.635) rot=(0,0,1;0rad)
  Support = -> [XY_Plane067]
  Width = 0.23
FEATURE [PartDesign::Body] Body064  label="pin064"
  Group = -> [Box703,Box710,Box688,Box687,Box706,Fillet194,Fillet180,Box672,Cylinder134,Box633,Box625,Fillet211,Box682,Cylinder128,Box694]
  Origin = -> Origin073
  Tip = -> Box694
FEATURE [PartDesign::Fillet] Fillet212
  Base = -> Fillet203 [Edge33]
  BaseFeature = -> Fillet203
  Placement = pos=(-21.5005,18.625,0.235) rot=(0,-1,0;0.174533rad)
  Radius = 0.5
  SupportTransform = false
FEATURE [PartDesign::AdditiveBox] Box628
  AttacherType = Attacher::AttachEngine3D
  AttachmentOffset = pos=(-21.1,18.635,0.305) rot=(0,1,0;0.785398rad)
  BaseFeature = -> Fillet212
  Height = 0.375
  Length = 0.2
  MapMode = 5
  Placement = pos=(-21.1,18.635,0.305) rot=(0,1,0;0.785398rad)
  Support = -> [XY_Plane076]
  Width = 0.23
FEATURE [PartDesign::SubtractiveCylinder] Cylinder127
  Angle = 360
  AttacherType = Attacher::AttachEngine3D
  AttachmentOffset = pos=(-21.055,18.935,0.52) rot=(1,0,0;1.5708rad)
  BaseFeature = -> Box628
  Height = 0.375
  MapMode = 5
  Placement = pos=(-21.055,18.935,0.52) rot=(1,0,0;1.5708rad)
  Radius = 0.205
  Support = -> [XY_Plane076]
FEATURE [PartDesign::SubtractiveBox] Box626
  AttacherType = Attacher::AttachEngine3D
  AttachmentOffset = pos=(-20.95,18.635,0.53) rot=(0,0,1;0rad)
  BaseFeature = -> Cylinder127
  Height = 0.5
  Length = 0.1
  MapMode = 5
  Placement = pos=(-20.95,18.635,0.53) rot=(0,0,1;0rad)
  Support = -> [XY_Plane076]
  Width = 0.23
FEATURE [PartDesign::SubtractiveBox] Box662
  AttacherType = Attacher::AttachEngine3D
  AttachmentOffset = pos=(-21.15,18.635,0.297) rot=(0,-1,0;0.174533rad)
  BaseFeature = -> Box626
  Height = 0.115
  Length = 0.115
  MapMode = 5
  Placement = pos=(-21.15,18.635,0.297) rot=(0,-1,0;0.174533rad)
  Support = -> [XY_Plane076]
  Width = 0.23
FEATURE [PartDesign::Fillet] Fillet208
  Base = -> Box662 [Edge28]
  BaseFeature = -> Box662
  Placement = pos=(-21.15,18.635,0.297) rot=(0,-1,0;0.174533rad)
  Radius = 0.375
  SupportTransform = false
FEATURE [PartDesign::AdditiveBox] Box655
  AttacherType = Attacher::AttachEngine3D
  AttachmentOffset = pos=(-20.7,18.635,1.55) rot=(0,1,0;0.785398rad)
  BaseFeature = -> Fillet208
  Height = 0.375
  Length = 0.23
  MapMode = 5
  Placement = pos=(-20.7,18.635,1.55) rot=(0,1,0;0.785398rad)
  Support = -> [XY_Plane076]
  Width = 0.23
FEATURE [PartDesign::SubtractiveCylinder] Cylinder131
  Angle = 360
  AttacherType = Attacher::AttachEngine3D
  AttachmentOffset = pos=(-20.271,18.635,1.4056) rot=(-1,0,0;1.5708rad)
  BaseFeature = -> Box655
  Height = 0.23
  MapMode = 5
  Placement = pos=(-20.271,18.635,1.4056) rot=(-1,0,0;1.5708rad)
  Radius = 0.23
  Support = -> [XY_Plane076]
FEATURE [PartDesign::AdditiveBox] Box681
  AttacherType = Attacher::AttachEngine3D
  AttachmentOffset = pos=(-20.1,18.635,1.635) rot=(0,0,1;0rad)
  BaseFeature = -> Cylinder131
  Height = 0.265
  Length = 0.23
  MapMode = 5
  Placement = pos=(-20.1,18.635,1.635) rot=(0,0,1;0rad)
  Support = -> [XY_Plane076]
  Width = 0.23
FEATURE [PartDesign::Body] Body063  label="pin063"
  Group = -> [Box652,Box675,Box639,Box691,Box651,Fillet203,Fillet212,Box628,Cylinder127,Box626,Box662,Fillet208,Box655,Cylinder131,Box681]
  Origin = -> Origin071
  Placement = pos=(0,-3,0) rot=(0,0,1;0rad)
  Tip = -> Box681
FEATURE [PartDesign::Fillet] Fillet213
  Base = -> Fillet197 [Edge33]
  BaseFeature = -> Fillet197
  Placement = pos=(-21.5005,18.625,0.235) rot=(0,-1,0;0.174533rad)
  Radius = 0.5
  SupportTransform = false
FEATURE [PartDesign::AdditiveBox] Box671
  AttacherType = Attacher::AttachEngine3D
  AttachmentOffset = pos=(-21.1,18.635,0.305) rot=(0,1,0;0.785398rad)
  BaseFeature = -> Fillet213
  Height = 0.375
  Length = 0.2
  MapMode = 5
  Placement = pos=(-21.1,18.635,0.305) rot=(0,1,0;0.785398rad)
  Support = -> [XY_Plane071]
  Width = 0.23
FEATURE [PartDesign::SubtractiveCylinder] Cylinder146
  Angle = 360
  AttacherType = Attacher::AttachEngine3D
  AttachmentOffset = pos=(-21.055,18.935,0.52) rot=(1,0,0;1.5708rad)
  BaseFeature = -> Box671
  Height = 0.375
  MapMode = 5
  Placement = pos=(-21.055,18.935,0.52) rot=(1,0,0;1.5708rad)
  Radius = 0.205
  Support = -> [XY_Plane071]
FEATURE [PartDesign::SubtractiveBox] Box696
  AttacherType = Attacher::AttachEngine3D
  AttachmentOffset = pos=(-20.95,18.635,0.53) rot=(0,0,1;0rad)
  BaseFeature = -> Cylinder146
  Height = 0.5
  Length = 0.1
  MapMode = 5
  Placement = pos=(-20.95,18.635,0.53) rot=(0,0,1;0rad)
  Support = -> [XY_Plane071]
  Width = 0.23
FEATURE [PartDesign::SubtractiveBox] Box697
  AttacherType = Attacher::AttachEngine3D
  AttachmentOffset = pos=(-21.15,18.635,0.297) rot=(0,-1,0;0.174533rad)
  BaseFeature = -> Box696
  Height = 0.115
  Length = 0.115
  MapMode = 5
  Placement = pos=(-21.15,18.635,0.297) rot=(0,-1,0;0.174533rad)
  Support = -> [XY_Plane071]
  Width = 0.23
FEATURE [PartDesign::Fillet] Fillet183
  Base = -> Box697 [Edge28]
  BaseFeature = -> Box697
  Placement = pos=(-21.15,18.635,0.297) rot=(0,-1,0;0.174533rad)
  Radius = 0.375
  SupportTransform = false
FEATURE [PartDesign::AdditiveBox] Box693
  AttacherType = Attacher::AttachEngine3D
  AttachmentOffset = pos=(-20.7,18.635,1.55) rot=(0,1,0;0.785398rad)
  BaseFeature = -> Fillet183
  Height = 0.375
  Length = 0.23
  MapMode = 5
  Placement = pos=(-20.7,18.635,1.55) rot=(0,1,0;0.785398rad)
  Support = -> [XY_Plane071]
  Width = 0.23
FEATURE [PartDesign::SubtractiveCylinder] Cylinder144
  Angle = 360
  AttacherType = Attacher::AttachEngine3D
  AttachmentOffset = pos=(-20.271,18.635,1.4056) rot=(-1,0,0;1.5708rad)
  BaseFeature = -> Box693
  Height = 0.23
  MapMode = 5
  Placement = pos=(-20.271,18.635,1.4056) rot=(-1,0,0;1.5708rad)
  Radius = 0.23
  Support = -> [XY_Plane071]
FEATURE [PartDesign::AdditiveBox] Box709
  AttacherType = Attacher::AttachEngine3D
  AttachmentOffset = pos=(-20.1,18.635,1.635) rot=(0,0,1;0rad)
  BaseFeature = -> Cylinder144
  Height = 0.265
  Length = 0.23
  MapMode = 5
  Placement = pos=(-20.1,18.635,1.635) rot=(0,0,1;0rad)
  Support = -> [XY_Plane071]
  Width = 0.23
FEATURE [PartDesign::Body] Body070  label="pin070"
  Group = -> [Box713,Box718,Box700,Box702,Box698,Fillet197,Fillet213,Box671,Cylinder146,Box696,Box697,Fillet183,Box693,Cylinder144,Box709]
  Origin = -> Origin068
  Placement = pos=(0,-1,0) rot=(0,0,1;0rad)
  Tip = -> Box709
FEATURE [PartDesign::Fillet] Fillet214
  Base = -> Box656 [Edge2]
  BaseFeature = -> Box656
  Placement = pos=(-21.5005,18.625,0.235) rot=(0,-1,0;0.174533rad)
  Radius = 0.05
  SupportTransform = false
FEATURE [PartDesign::Fillet] Fillet201
  Base = -> Fillet214 [Edge33]
  BaseFeature = -> Fillet214
  Placement = pos=(-21.5005,18.625,0.235) rot=(0,-1,0;0.174533rad)
  Radius = 0.5
  SupportTransform = false
FEATURE [PartDesign::AdditiveBox] Box674
  AttacherType = Attacher::AttachEngine3D
  AttachmentOffset = pos=(-21.1,18.635,0.305) rot=(0,1,0;0.785398rad)
  BaseFeature = -> Fillet201
  Height = 0.375
  Length = 0.2
  MapMode = 5
  Placement = pos=(-21.1,18.635,0.305) rot=(0,1,0;0.785398rad)
  Support = -> [XY_Plane077]
  Width = 0.23
FEATURE [PartDesign::SubtractiveCylinder] Cylinder141
  Angle = 360
  AttacherType = Attacher::AttachEngine3D
  AttachmentOffset = pos=(-21.055,18.935,0.52) rot=(1,0,0;1.5708rad)
  BaseFeature = -> Box674
  Height = 0.375
  MapMode = 5
  Placement = pos=(-21.055,18.935,0.52) rot=(1,0,0;1.5708rad)
  Radius = 0.205
  Support = -> [XY_Plane077]
FEATURE [PartDesign::SubtractiveBox] Box678
  AttacherType = Attacher::AttachEngine3D
  AttachmentOffset = pos=(-20.95,18.635,0.53) rot=(0,0,1;0rad)
  BaseFeature = -> Cylinder141
  Height = 0.5
  Length = 0.1
  MapMode = 5
  Placement = pos=(-20.95,18.635,0.53) rot=(0,0,1;0rad)
  Support = -> [XY_Plane077]
  Width = 0.23
FEATURE [PartDesign::SubtractiveBox] Box661
  AttacherType = Attacher::AttachEngine3D
  AttachmentOffset = pos=(-21.15,18.635,0.297) rot=(0,-1,0;0.174533rad)
  BaseFeature = -> Box678
  Height = 0.115
  Length = 0.115
  MapMode = 5
  Placement = pos=(-21.15,18.635,0.297) rot=(0,-1,0;0.174533rad)
  Support = -> [XY_Plane077]
  Width = 0.23
FEATURE [PartDesign::Fillet] Fillet193
  Base = -> Box661 [Edge28]
  BaseFeature = -> Box661
  Placement = pos=(-21.15,18.635,0.297) rot=(0,-1,0;0.174533rad)
  Radius = 0.375
  SupportTransform = false
FEATURE [PartDesign::AdditiveBox] Box679
  AttacherType = Attacher::AttachEngine3D
  AttachmentOffset = pos=(-20.7,18.635,1.55) rot=(0,1,0;0.785398rad)
  BaseFeature = -> Fillet193
  Height = 0.375
  Length = 0.23
  MapMode = 5
  Placement = pos=(-20.7,18.635,1.55) rot=(0,1,0;0.785398rad)
  Support = -> [XY_Plane077]
  Width = 0.23
FEATURE [PartDesign::SubtractiveCylinder] Cylinder139
  Angle = 360
  AttacherType = Attacher::AttachEngine3D
  AttachmentOffset = pos=(-20.271,18.635,1.4056) rot=(-1,0,0;1.5708rad)
  BaseFeature = -> Box679
  Height = 0.23
  MapMode = 5
  Placement = pos=(-20.271,18.635,1.4056) rot=(-1,0,0;1.5708rad)
  Radius = 0.23
  Support = -> [XY_Plane077]
FEATURE [PartDesign::AdditiveBox] Box653
  AttacherType = Attacher::AttachEngine3D
  AttachmentOffset = pos=(-20.1,18.635,1.635) rot=(0,0,1;0rad)
  BaseFeature = -> Cylinder139
  Height = 0.265
  Length = 0.23
  MapMode = 5
  Placement = pos=(-20.1,18.635,1.635) rot=(0,0,1;0rad)
  Support = -> [XY_Plane077]
  Width = 0.23
FEATURE [PartDesign::Body] Body068  label="pin068"
  Group = -> [Box664,Box673,Box686,Box657,Box656,Fillet214,Fillet201,Box674,Cylinder141,Box678,Box661,Fillet193,Box679,Cylinder139,Box653]
  Origin = -> Origin077
  Placement = pos=(0,-3.5,0) rot=(0,0,1;0rad)
  Tip = -> Box653
FEATURE [PartDesign::Fillet] Fillet215
  Base = -> Box683 [Edge2]
  BaseFeature = -> Box683
  Placement = pos=(-21.5005,18.625,0.235) rot=(0,-1,0;0.174533rad)
  Radius = 0.05
  SupportTransform = false
FEATURE [PartDesign::Fillet] Fillet196
  Base = -> Fillet215 [Edge33]
  BaseFeature = -> Fillet215
  Placement = pos=(-21.5005,18.625,0.235) rot=(0,-1,0;0.174533rad)
  Radius = 0.5
  SupportTransform = false
FEATURE [PartDesign::AdditiveBox] Box604
  AttacherType = Attacher::AttachEngine3D
  AttachmentOffset = pos=(-21.1,18.635,0.305) rot=(0,1,0;0.785398rad)
  BaseFeature = -> Fillet196
  Height = 0.375
  Length = 0.2
  MapMode = 5
  Placement = pos=(-21.1,18.635,0.305) rot=(0,1,0;0.785398rad)
  Support = -> [XY_Plane074]
  Width = 0.23
FEATURE [PartDesign::SubtractiveCylinder] Cylinder124
  Angle = 360
  AttacherType = Attacher::AttachEngine3D
  AttachmentOffset = pos=(-21.055,18.935,0.52) rot=(1,0,0;1.5708rad)
  BaseFeature = -> Box604
  Height = 0.375
  MapMode = 5
  Placement = pos=(-21.055,18.935,0.52) rot=(1,0,0;1.5708rad)
  Radius = 0.205
  Support = -> [XY_Plane074]
FEATURE [PartDesign::SubtractiveBox] Box603
  AttacherType = Attacher::AttachEngine3D
  AttachmentOffset = pos=(-20.95,18.635,0.53) rot=(0,0,1;0rad)
  BaseFeature = -> Cylinder124
  Height = 0.5
  Length = 0.1
  MapMode = 5
  Placement = pos=(-20.95,18.635,0.53) rot=(0,0,1;0rad)
  Support = -> [XY_Plane074]
  Width = 0.23
FEATURE [PartDesign::SubtractiveBox] Box610
  AttacherType = Attacher::AttachEngine3D
  AttachmentOffset = pos=(-21.15,18.635,0.297) rot=(0,-1,0;0.174533rad)
  BaseFeature = -> Box603
  Height = 0.115
  Length = 0.115
  MapMode = 5
  Placement = pos=(-21.15,18.635,0.297) rot=(0,-1,0;0.174533rad)
  Support = -> [XY_Plane074]
  Width = 0.23
FEATURE [PartDesign::Fillet] Fillet206
  Base = -> Box610 [Edge28]
  BaseFeature = -> Box610
  Placement = pos=(-21.15,18.635,0.297) rot=(0,-1,0;0.174533rad)
  Radius = 0.375
  SupportTransform = false
FEATURE [PartDesign::AdditiveBox] Box630
  AttacherType = Attacher::AttachEngine3D
  AttachmentOffset = pos=(-20.7,18.635,1.55) rot=(0,1,0;0.785398rad)
  BaseFeature = -> Fillet206
  Height = 0.375
  Length = 0.23
  MapMode = 5
  Placement = pos=(-20.7,18.635,1.55) rot=(0,1,0;0.785398rad)
  Support = -> [XY_Plane074]
  Width = 0.23
FEATURE [PartDesign::SubtractiveCylinder] Cylinder129
  Angle = 360
  AttacherType = Attacher::AttachEngine3D
  AttachmentOffset = pos=(-20.271,18.635,1.4056) rot=(-1,0,0;1.5708rad)
  BaseFeature = -> Box630
  Height = 0.23
  MapMode = 5
  Placement = pos=(-20.271,18.635,1.4056) rot=(-1,0,0;1.5708rad)
  Radius = 0.23
  Support = -> [XY_Plane074]
FEATURE [PartDesign::AdditiveBox] Box623
  AttacherType = Attacher::AttachEngine3D
  AttachmentOffset = pos=(-20.1,18.635,1.635) rot=(0,0,1;0rad)
  BaseFeature = -> Cylinder129
  Height = 0.265
  Length = 0.23
  MapMode = 5
  Placement = pos=(-20.1,18.635,1.635) rot=(0,0,1;0rad)
  Support = -> [XY_Plane074]
  Width = 0.23
FEATURE [PartDesign::Body] Body067  label="pin067"
  Group = -> [Box637,Box645,Box629,Box634,Box683,Fillet215,Fillet196,Box604,Cylinder124,Box603,Box610,Fillet206,Box630,Cylinder129,Box623]
  Origin = -> Origin074
  Placement = pos=(0,-4.5,0) rot=(0,0,1;0rad)
  Tip = -> Box623
FEATURE [PartDesign::AdditiveBox] Box738
  AttacherType = Attacher::AttachEngine3D
  AttachmentOffset = pos=(-21.3,18.635,0) rot=(0,0,1;0rad)
  Height = 1.9
  Length = 1.3
  MapMode = 5
  Placement = pos=(-21.3,18.635,0) rot=(0,0,1;0rad)
  Support = -> [XY_Plane080]
  Width = 0.23
FEATURE [PartDesign::AdditiveBox] Box740
  AttacherType = Attacher::AttachEngine3D
  AttachmentOffset = pos=(-21.3,18.635,0) rot=(0,0,1;0rad)
  Height = 1.9
  Length = 1.3
  MapMode = 5
  Placement = pos=(-21.3,18.635,0) rot=(0,0,1;0rad)
  Support = -> [XY_Plane081]
  Width = 0.23
FEATURE [PartDesign::AdditiveBox] Box743
  AttacherType = Attacher::AttachEngine3D
  AttachmentOffset = pos=(-21.3,18.635,0) rot=(0,0,1;0rad)
  Height = 1.9
  Length = 1.3
  MapMode = 5
  Placement = pos=(-21.3,18.635,0) rot=(0,0,1;0rad)
  Support = -> [XY_Plane079]
  Width = 0.23
FEATURE [PartDesign::SubtractiveBox] Box744
  AttacherType = Attacher::AttachEngine3D
  AttachmentOffset = pos=(-21.35,18.635,0.35) rot=(0,0,1;0rad)
  BaseFeature = -> Box740
  Height = 1.55
  Length = 0.5
  MapMode = 5
  Placement = pos=(-21.35,18.635,0.35) rot=(0,0,1;0rad)
  Support = -> [XY_Plane081]
  Width = 0.23
FEATURE [PartDesign::SubtractiveBox] Box734
  AttacherType = Attacher::AttachEngine3D
  AttachmentOffset = pos=(-20.5,18.63,0) rot=(0,0,1;0rad)
  BaseFeature = -> Box744
  Height = 1.635
  Length = 0.5
  MapMode = 5
  Placement = pos=(-20.5,18.63,0) rot=(0,0,1;0rad)
  Support = -> [XY_Plane081]
  Width = 0.25
FEATURE [PartDesign::SubtractiveBox] Box735
  AttacherType = Attacher::AttachEngine3D
  AttachmentOffset = pos=(-21.19,18.635,-0.12) rot=(0,-1,0;0.15708rad)
  BaseFeature = -> Box734
  Height = 0.12
  Length = 0.725
  MapMode = 5
  Placement = pos=(-21.19,18.635,-0.12) rot=(0,-1,0;0.15708rad)
  Support = -> [XY_Plane081]
  Width = 0.25
FEATURE [PartDesign::SubtractiveBox] Box747
  AttacherType = Attacher::AttachEngine3D
  AttachmentOffset = pos=(-21.35,18.635,0.35) rot=(0,0,1;0rad)
  BaseFeature = -> Box738
  Height = 1.55
  Length = 0.5
  MapMode = 5
  Placement = pos=(-21.35,18.635,0.35) rot=(0,0,1;0rad)
  Support = -> [XY_Plane080]
  Width = 0.23
FEATURE [PartDesign::SubtractiveBox] Box737
  AttacherType = Attacher::AttachEngine3D
  AttachmentOffset = pos=(-20.5,18.63,0) rot=(0,0,1;0rad)
  BaseFeature = -> Box747
  Height = 1.635
  Length = 0.5
  MapMode = 5
  Placement = pos=(-20.5,18.63,0) rot=(0,0,1;0rad)
  Support = -> [XY_Plane080]
  Width = 0.25
FEATURE [PartDesign::SubtractiveBox] Box733
  AttacherType = Attacher::AttachEngine3D
  AttachmentOffset = pos=(-21.19,18.635,-0.12) rot=(0,-1,0;0.15708rad)
  BaseFeature = -> Box737
  Height = 0.12
  Length = 0.725
  MapMode = 5
  Placement = pos=(-21.19,18.635,-0.12) rot=(0,-1,0;0.15708rad)
  Support = -> [XY_Plane080]
  Width = 0.25
FEATURE [PartDesign::SubtractiveBox] Box731
  AttacherType = Attacher::AttachEngine3D
  AttachmentOffset = pos=(-21.5005,18.625,0.235) rot=(0,-1,0;0.174533rad)
  BaseFeature = -> Box733
  Height = 0.3
  Length = 0.6605
  MapMode = 5
  Placement = pos=(-21.5005,18.625,0.235) rot=(0,-1,0;0.174533rad)
  Support = -> [XY_Plane080]
  Width = 0.25
FEATURE [PartDesign::AdditiveBox] Box751
  AttacherType = Attacher::AttachEngine3D
  AttachmentOffset = pos=(-21.3,18.635,0) rot=(0,0,1;0rad)
  Height = 1.9
  Length = 1.3
  MapMode = 5
  Placement = pos=(-21.3,18.635,0) rot=(0,0,1;0rad)
  Support = -> [XY_Plane082]
  Width = 0.23
FEATURE [PartDesign::SubtractiveBox] Box752
  AttacherType = Attacher::AttachEngine3D
  AttachmentOffset = pos=(-21.35,18.635,0.35) rot=(0,0,1;0rad)
  BaseFeature = -> Box743
  Height = 1.55
  Length = 0.5
  MapMode = 5
  Placement = pos=(-21.35,18.635,0.35) rot=(0,0,1;0rad)
  Support = -> [XY_Plane079]
  Width = 0.23
FEATURE [PartDesign::SubtractiveBox] Box721
  AttacherType = Attacher::AttachEngine3D
  AttachmentOffset = pos=(-20.5,18.63,0) rot=(0,0,1;0rad)
  BaseFeature = -> Box752
  Height = 1.635
  Length = 0.5
  MapMode = 5
  Placement = pos=(-20.5,18.63,0) rot=(0,0,1;0rad)
  Support = -> [XY_Plane079]
  Width = 0.25
FEATURE [PartDesign::SubtractiveBox] Box727
  AttacherType = Attacher::AttachEngine3D
  AttachmentOffset = pos=(-21.19,18.635,-0.12) rot=(0,-1,0;0.15708rad)
  BaseFeature = -> Box721
  Height = 0.12
  Length = 0.725
  MapMode = 5
  Placement = pos=(-21.19,18.635,-0.12) rot=(0,-1,0;0.15708rad)
  Support = -> [XY_Plane079]
  Width = 0.25
FEATURE [PartDesign::SubtractiveBox] Box725
  AttacherType = Attacher::AttachEngine3D
  AttachmentOffset = pos=(-21.5005,18.625,0.235) rot=(0,-1,0;0.174533rad)
  BaseFeature = -> Box727
  Height = 0.3
  Length = 0.6605
  MapMode = 5
  Placement = pos=(-21.5005,18.625,0.235) rot=(0,-1,0;0.174533rad)
  Support = -> [XY_Plane079]
  Width = 0.25
FEATURE [PartDesign::SubtractiveBox] Box756
  AttacherType = Attacher::AttachEngine3D
  AttachmentOffset = pos=(-21.35,18.635,0.35) rot=(0,0,1;0rad)
  BaseFeature = -> Box751
  Height = 1.55
  Length = 0.5
  MapMode = 5
  Placement = pos=(-21.35,18.635,0.35) rot=(0,0,1;0rad)
  Support = -> [XY_Plane082]
  Width = 0.23
FEATURE [PartDesign::SubtractiveBox] Box745
  AttacherType = Attacher::AttachEngine3D
  AttachmentOffset = pos=(-20.5,18.63,0) rot=(0,0,1;0rad)
  BaseFeature = -> Box756
  Height = 1.635
  Length = 0.5
  MapMode = 5
  Placement = pos=(-20.5,18.63,0) rot=(0,0,1;0rad)
  Support = -> [XY_Plane082]
  Width = 0.25
FEATURE [PartDesign::SubtractiveBox] Box757
  AttacherType = Attacher::AttachEngine3D
  AttachmentOffset = pos=(-21.19,18.635,-0.12) rot=(0,-1,0;0.15708rad)
  BaseFeature = -> Box745
  Height = 0.12
  Length = 0.725
  MapMode = 5
  Placement = pos=(-21.19,18.635,-0.12) rot=(0,-1,0;0.15708rad)
  Support = -> [XY_Plane082]
  Width = 0.25
FEATURE [PartDesign::SubtractiveBox] Box754
  AttacherType = Attacher::AttachEngine3D
  AttachmentOffset = pos=(-21.5005,18.625,0.235) rot=(0,-1,0;0.174533rad)
  BaseFeature = -> Box757
  Height = 0.3
  Length = 0.6605
  MapMode = 5
  Placement = pos=(-21.5005,18.625,0.235) rot=(0,-1,0;0.174533rad)
  Support = -> [XY_Plane082]
  Width = 0.25
FEATURE [PartDesign::SubtractiveBox] Box760
  AttacherType = Attacher::AttachEngine3D
  AttachmentOffset = pos=(-21.5005,18.625,0.235) rot=(0,-1,0;0.174533rad)
  BaseFeature = -> Box735
  Height = 0.3
  Length = 0.6605
  MapMode = 5
  Placement = pos=(-21.5005,18.625,0.235) rot=(0,-1,0;0.174533rad)
  Support = -> [XY_Plane081]
  Width = 0.25
FEATURE [PartDesign::Fillet] Fillet217
  Base = -> Box731 [Edge2]
  BaseFeature = -> Box731
  Placement = pos=(-21.5005,18.625,0.235) rot=(0,-1,0;0.174533rad)
  Radius = 0.05
  SupportTransform = false
FEATURE [PartDesign::Fillet] Fillet219
  Base = -> Fillet217 [Edge33]
  BaseFeature = -> Fillet217
  Placement = pos=(-21.5005,18.625,0.235) rot=(0,-1,0;0.174533rad)
  Radius = 0.5
  SupportTransform = false
FEATURE [PartDesign::AdditiveBox] Box728
  AttacherType = Attacher::AttachEngine3D
  AttachmentOffset = pos=(-21.1,18.635,0.305) rot=(0,1,0;0.785398rad)
  BaseFeature = -> Fillet219
  Height = 0.375
  Length = 0.2
  MapMode = 5
  Placement = pos=(-21.1,18.635,0.305) rot=(0,1,0;0.785398rad)
  Support = -> [XY_Plane080]
  Width = 0.23
FEATURE [PartDesign::SubtractiveCylinder] Cylinder152
  Angle = 360
  AttacherType = Attacher::AttachEngine3D
  AttachmentOffset = pos=(-21.055,18.935,0.52) rot=(1,0,0;1.5708rad)
  BaseFeature = -> Box728
  Height = 0.375
  MapMode = 5
  Placement = pos=(-21.055,18.935,0.52) rot=(1,0,0;1.5708rad)
  Radius = 0.205
  Support = -> [XY_Plane080]
FEATURE [PartDesign::SubtractiveBox] Box732
  AttacherType = Attacher::AttachEngine3D
  AttachmentOffset = pos=(-20.95,18.635,0.53) rot=(0,0,1;0rad)
  BaseFeature = -> Cylinder152
  Height = 0.5
  Length = 0.1
  MapMode = 5
  Placement = pos=(-20.95,18.635,0.53) rot=(0,0,1;0rad)
  Support = -> [XY_Plane080]
  Width = 0.23
FEATURE [PartDesign::SubtractiveBox] Box726
  AttacherType = Attacher::AttachEngine3D
  AttachmentOffset = pos=(-21.15,18.635,0.297) rot=(0,-1,0;0.174533rad)
  BaseFeature = -> Box732
  Height = 0.115
  Length = 0.115
  MapMode = 5
  Placement = pos=(-21.15,18.635,0.297) rot=(0,-1,0;0.174533rad)
  Support = -> [XY_Plane080]
  Width = 0.23
FEATURE [PartDesign::Fillet] Fillet218
  Base = -> Box726 [Edge28]
  BaseFeature = -> Box726
  Placement = pos=(-21.15,18.635,0.297) rot=(0,-1,0;0.174533rad)
  Radius = 0.375
  SupportTransform = false
FEATURE [PartDesign::AdditiveBox] Box736
  AttacherType = Attacher::AttachEngine3D
  AttachmentOffset = pos=(-20.7,18.635,1.55) rot=(0,1,0;0.785398rad)
  BaseFeature = -> Fillet218
  Height = 0.375
  Length = 0.23
  MapMode = 5
  Placement = pos=(-20.7,18.635,1.55) rot=(0,1,0;0.785398rad)
  Support = -> [XY_Plane080]
  Width = 0.23
FEATURE [PartDesign::SubtractiveCylinder] Cylinder149
  Angle = 360
  AttacherType = Attacher::AttachEngine3D
  AttachmentOffset = pos=(-20.271,18.635,1.4056) rot=(-1,0,0;1.5708rad)
  BaseFeature = -> Box736
  Height = 0.23
  MapMode = 5
  Placement = pos=(-20.271,18.635,1.4056) rot=(-1,0,0;1.5708rad)
  Radius = 0.23
  Support = -> [XY_Plane080]
FEATURE [PartDesign::AdditiveBox] Box748
  AttacherType = Attacher::AttachEngine3D
  AttachmentOffset = pos=(-20.1,18.635,1.635) rot=(0,0,1;0rad)
  BaseFeature = -> Cylinder149
  Height = 0.265
  Length = 0.23
  MapMode = 5
  Placement = pos=(-20.1,18.635,1.635) rot=(0,0,1;0rad)
  Support = -> [XY_Plane080]
  Width = 0.23
FEATURE [PartDesign::Fillet] Fillet220
  Base = -> Box725 [Edge2]
  BaseFeature = -> Box725
  Placement = pos=(-21.5005,18.625,0.235) rot=(0,-1,0;0.174533rad)
  Radius = 0.05
  SupportTransform = false
FEATURE [PartDesign::Body] Body073  label="pin073"
  Group = -> [Box738,Box747,Box737,Box733,Box731,Fillet217,Fillet219,Box728,Cylinder152,Box732,Box726,Fillet218,Box736,Cylinder149,Box748]
  Origin = -> Origin079
  Placement = pos=(0,-6,0) rot=(0,0,1;0rad)
  Tip = -> Box748
FEATURE [PartDesign::Fillet] Fillet225
  Base = -> Box754 [Edge2]
  BaseFeature = -> Box754
  Placement = pos=(-21.5005,18.625,0.235) rot=(0,-1,0;0.174533rad)
  Radius = 0.05
  SupportTransform = false
FEATURE [PartDesign::Fillet] Fillet224
  Base = -> Fillet225 [Edge33]
  BaseFeature = -> Fillet225
  Placement = pos=(-21.5005,18.625,0.235) rot=(0,-1,0;0.174533rad)
  Radius = 0.5
  SupportTransform = false
FEATURE [PartDesign::AdditiveBox] Box759
  AttacherType = Attacher::AttachEngine3D
  AttachmentOffset = pos=(-21.1,18.635,0.305) rot=(0,1,0;0.785398rad)
  BaseFeature = -> Fillet224
  Height = 0.375
  Length = 0.2
  MapMode = 5
  Placement = pos=(-21.1,18.635,0.305) rot=(0,1,0;0.785398rad)
  Support = -> [XY_Plane082]
  Width = 0.23
FEATURE [PartDesign::SubtractiveCylinder] Cylinder155
  Angle = 360
  AttacherType = Attacher::AttachEngine3D
  AttachmentOffset = pos=(-21.055,18.935,0.52) rot=(1,0,0;1.5708rad)
  BaseFeature = -> Box759
  Height = 0.375
  MapMode = 5
  Placement = pos=(-21.055,18.935,0.52) rot=(1,0,0;1.5708rad)
  Radius = 0.205
  Support = -> [XY_Plane082]
FEATURE [PartDesign::SubtractiveBox] Box758
  AttacherType = Attacher::AttachEngine3D
  AttachmentOffset = pos=(-20.95,18.635,0.53) rot=(0,0,1;0rad)
  BaseFeature = -> Cylinder155
  Height = 0.5
  Length = 0.1
  MapMode = 5
  Placement = pos=(-20.95,18.635,0.53) rot=(0,0,1;0rad)
  Support = -> [XY_Plane082]
  Width = 0.23
FEATURE [PartDesign::SubtractiveBox] Box753
  AttacherType = Attacher::AttachEngine3D
  AttachmentOffset = pos=(-21.15,18.635,0.297) rot=(0,-1,0;0.174533rad)
  BaseFeature = -> Box758
  Height = 0.115
  Length = 0.115
  MapMode = 5
  Placement = pos=(-21.15,18.635,0.297) rot=(0,-1,0;0.174533rad)
  Support = -> [XY_Plane082]
  Width = 0.23
FEATURE [PartDesign::Fillet] Fillet221
  Base = -> Box753 [Edge28]
  BaseFeature = -> Box753
  Placement = pos=(-21.15,18.635,0.297) rot=(0,-1,0;0.174533rad)
  Radius = 0.375
  SupportTransform = false
FEATURE [PartDesign::AdditiveBox] Box755
  AttacherType = Attacher::AttachEngine3D
  AttachmentOffset = pos=(-20.7,18.635,1.55) rot=(0,1,0;0.785398rad)
  BaseFeature = -> Fillet221
  Height = 0.375
  Length = 0.23
  MapMode = 5
  Placement = pos=(-20.7,18.635,1.55) rot=(0,1,0;0.785398rad)
  Support = -> [XY_Plane082]
  Width = 0.23
FEATURE [PartDesign::SubtractiveCylinder] Cylinder154
  Angle = 360
  AttacherType = Attacher::AttachEngine3D
  AttachmentOffset = pos=(-20.271,18.635,1.4056) rot=(-1,0,0;1.5708rad)
  BaseFeature = -> Box755
  Height = 0.23
  MapMode = 5
  Placement = pos=(-20.271,18.635,1.4056) rot=(-1,0,0;1.5708rad)
  Radius = 0.23
  Support = -> [XY_Plane082]
FEATURE [PartDesign::AdditiveBox] Box742
  AttacherType = Attacher::AttachEngine3D
  AttachmentOffset = pos=(-20.1,18.635,1.635) rot=(0,0,1;0rad)
  BaseFeature = -> Cylinder154
  Height = 0.265
  Length = 0.23
  MapMode = 5
  Placement = pos=(-20.1,18.635,1.635) rot=(0,0,1;0rad)
  Support = -> [XY_Plane082]
  Width = 0.23
FEATURE [PartDesign::Body] Body075  label="pin075"
  Group = -> [Box751,Box756,Box745,Box757,Box754,Fillet225,Fillet224,Box759,Cylinder155,Box758,Box753,Fillet221,Box755,Cylinder154,Box742]
  Origin = -> Origin082
  Placement = pos=(0,-7,0) rot=(0,0,1;0rad)
  Tip = -> Box742
FEATURE [PartDesign::Fillet] Fillet226
  Base = -> Fillet220 [Edge33]
  BaseFeature = -> Fillet220
  Placement = pos=(-21.5005,18.625,0.235) rot=(0,-1,0;0.174533rad)
  Radius = 0.5
  SupportTransform = false
FEATURE [PartDesign::AdditiveBox] Box746
  AttacherType = Attacher::AttachEngine3D
  AttachmentOffset = pos=(-21.1,18.635,0.305) rot=(0,1,0;0.785398rad)
  BaseFeature = -> Fillet226
  Height = 0.375
  Length = 0.2
  MapMode = 5
  Placement = pos=(-21.1,18.635,0.305) rot=(0,1,0;0.785398rad)
  Support = -> [XY_Plane079]
  Width = 0.23
FEATURE [PartDesign::SubtractiveCylinder] Cylinder151
  Angle = 360
  AttacherType = Attacher::AttachEngine3D
  AttachmentOffset = pos=(-21.055,18.935,0.52) rot=(1,0,0;1.5708rad)
  BaseFeature = -> Box746
  Height = 0.375
  MapMode = 5
  Placement = pos=(-21.055,18.935,0.52) rot=(1,0,0;1.5708rad)
  Radius = 0.205
  Support = -> [XY_Plane079]
FEATURE [PartDesign::SubtractiveBox] Box741
  AttacherType = Attacher::AttachEngine3D
  AttachmentOffset = pos=(-20.95,18.635,0.53) rot=(0,0,1;0rad)
  BaseFeature = -> Cylinder151
  Height = 0.5
  Length = 0.1
  MapMode = 5
  Placement = pos=(-20.95,18.635,0.53) rot=(0,0,1;0rad)
  Support = -> [XY_Plane079]
  Width = 0.23
FEATURE [PartDesign::SubtractiveBox] Box739
  AttacherType = Attacher::AttachEngine3D
  AttachmentOffset = pos=(-21.15,18.635,0.297) rot=(0,-1,0;0.174533rad)
  BaseFeature = -> Box741
  Height = 0.115
  Length = 0.115
  MapMode = 5
  Placement = pos=(-21.15,18.635,0.297) rot=(0,-1,0;0.174533rad)
  Support = -> [XY_Plane079]
  Width = 0.23
FEATURE [PartDesign::Fillet] Fillet223
  Base = -> Box739 [Edge28]
  BaseFeature = -> Box739
  Placement = pos=(-21.15,18.635,0.297) rot=(0,-1,0;0.174533rad)
  Radius = 0.375
  SupportTransform = false
FEATURE [PartDesign::AdditiveBox] Box749
  AttacherType = Attacher::AttachEngine3D
  AttachmentOffset = pos=(-20.7,18.635,1.55) rot=(0,1,0;0.785398rad)
  BaseFeature = -> Fillet223
  Height = 0.375
  Length = 0.23
  MapMode = 5
  Placement = pos=(-20.7,18.635,1.55) rot=(0,1,0;0.785398rad)
  Support = -> [XY_Plane079]
  Width = 0.23
FEATURE [PartDesign::SubtractiveCylinder] Cylinder153
  Angle = 360
  AttacherType = Attacher::AttachEngine3D
  AttachmentOffset = pos=(-20.271,18.635,1.4056) rot=(-1,0,0;1.5708rad)
  BaseFeature = -> Box749
  Height = 0.23
  MapMode = 5
  Placement = pos=(-20.271,18.635,1.4056) rot=(-1,0,0;1.5708rad)
  Radius = 0.23
  Support = -> [XY_Plane079]
FEATURE [PartDesign::AdditiveBox] Box750
  AttacherType = Attacher::AttachEngine3D
  AttachmentOffset = pos=(-20.1,18.635,1.635) rot=(0,0,1;0rad)
  BaseFeature = -> Cylinder153
  Height = 0.265
  Length = 0.23
  MapMode = 5
  Placement = pos=(-20.1,18.635,1.635) rot=(0,0,1;0rad)
  Support = -> [XY_Plane079]
  Width = 0.23
FEATURE [PartDesign::Body] Body076  label="pin076"
  Group = -> [Box743,Box752,Box721,Box727,Box725,Fillet220,Fillet226,Box746,Cylinder151,Box741,Box739,Fillet223,Box749,Cylinder153,Box750]
  Origin = -> Origin080
  Placement = pos=(0,-7.5,0) rot=(0,0,1;0rad)
  Tip = -> Box750
FEATURE [PartDesign::Fillet] Fillet227
  Base = -> Box760 [Edge2]
  BaseFeature = -> Box760
  Placement = pos=(-21.5005,18.625,0.235) rot=(0,-1,0;0.174533rad)
  Radius = 0.05
  SupportTransform = false
FEATURE [PartDesign::Fillet] Fillet216
  Base = -> Fillet227 [Edge33]
  BaseFeature = -> Fillet227
  Placement = pos=(-21.5005,18.625,0.235) rot=(0,-1,0;0.174533rad)
  Radius = 0.5
  SupportTransform = false
FEATURE [PartDesign::AdditiveBox] Box723
  AttacherType = Attacher::AttachEngine3D
  AttachmentOffset = pos=(-21.1,18.635,0.305) rot=(0,1,0;0.785398rad)
  BaseFeature = -> Fillet216
  Height = 0.375
  Length = 0.2
  MapMode = 5
  Placement = pos=(-21.1,18.635,0.305) rot=(0,1,0;0.785398rad)
  Support = -> [XY_Plane081]
  Width = 0.23
FEATURE [PartDesign::SubtractiveCylinder] Cylinder148
  Angle = 360
  AttacherType = Attacher::AttachEngine3D
  AttachmentOffset = pos=(-21.055,18.935,0.52) rot=(1,0,0;1.5708rad)
  BaseFeature = -> Box723
  Height = 0.375
  MapMode = 5
  Placement = pos=(-21.055,18.935,0.52) rot=(1,0,0;1.5708rad)
  Radius = 0.205
  Support = -> [XY_Plane081]
FEATURE [PartDesign::SubtractiveBox] Box724
  AttacherType = Attacher::AttachEngine3D
  AttachmentOffset = pos=(-20.95,18.635,0.53) rot=(0,0,1;0rad)
  BaseFeature = -> Cylinder148
  Height = 0.5
  Length = 0.1
  MapMode = 5
  Placement = pos=(-20.95,18.635,0.53) rot=(0,0,1;0rad)
  Support = -> [XY_Plane081]
  Width = 0.23
FEATURE [PartDesign::SubtractiveBox] Box722
  AttacherType = Attacher::AttachEngine3D
  AttachmentOffset = pos=(-21.15,18.635,0.297) rot=(0,-1,0;0.174533rad)
  BaseFeature = -> Box724
  Height = 0.115
  Length = 0.115
  MapMode = 5
  Placement = pos=(-21.15,18.635,0.297) rot=(0,-1,0;0.174533rad)
  Support = -> [XY_Plane081]
  Width = 0.23
FEATURE [PartDesign::Fillet] Fillet222
  Base = -> Box722 [Edge28]
  BaseFeature = -> Box722
  Placement = pos=(-21.15,18.635,0.297) rot=(0,-1,0;0.174533rad)
  Radius = 0.375
  SupportTransform = false
FEATURE [PartDesign::AdditiveBox] Box730
  AttacherType = Attacher::AttachEngine3D
  AttachmentOffset = pos=(-20.7,18.635,1.55) rot=(0,1,0;0.785398rad)
  BaseFeature = -> Fillet222
  Height = 0.375
  Length = 0.23
  MapMode = 5
  Placement = pos=(-20.7,18.635,1.55) rot=(0,1,0;0.785398rad)
  Support = -> [XY_Plane081]
  Width = 0.23
FEATURE [PartDesign::SubtractiveCylinder] Cylinder150
  Angle = 360
  AttacherType = Attacher::AttachEngine3D
  AttachmentOffset = pos=(-20.271,18.635,1.4056) rot=(-1,0,0;1.5708rad)
  BaseFeature = -> Box730
  Height = 0.23
  MapMode = 5
  Placement = pos=(-20.271,18.635,1.4056) rot=(-1,0,0;1.5708rad)
  Radius = 0.23
  Support = -> [XY_Plane081]
FEATURE [PartDesign::AdditiveBox] Box729
  AttacherType = Attacher::AttachEngine3D
  AttachmentOffset = pos=(-20.1,18.635,1.635) rot=(0,0,1;0rad)
  BaseFeature = -> Cylinder150
  Height = 0.265
  Length = 0.23
  MapMode = 5
  Placement = pos=(-20.1,18.635,1.635) rot=(0,0,1;0rad)
  Support = -> [XY_Plane081]
  Width = 0.23
FEATURE [PartDesign::Body] Body074  label="pin074"
  Group = -> [Box740,Box744,Box734,Box735,Box760,Fillet227,Fillet216,Box723,Cylinder148,Box724,Box722,Fillet222,Box730,Cylinder150,Box729]
  Origin = -> Origin081
  Placement = pos=(0,-6.5,0) rot=(0,0,1;0rad)
  Tip = -> Box729
FEATURE [App::Part] Part005  label="Pin-set006"
  Group = -> [Body064,Body061,Body070,Body066,Body062,Body065,Body063,Body068,Body069,Body067,Body071,Body072,Body073,Body074,Body075,Body076]
  Origin = -> Origin075
  Placement = pos=(0,-30,0) rot=(0,0,1;0rad)
FEATURE [App::Part] Part006  label="Pin-collection1"
  Group = -> [Part,Part001,Part002,Part003,Part004,Part005]
  Origin = -> Origin083
FEATURE [PartDesign::AdditiveBox] Box769
  AttacherType = Attacher::AttachEngine3D
  AttachmentOffset = pos=(-21.3,18.635,0) rot=(0,0,1;0rad)
  Height = 1.9
  Length = 1.3
  MapMode = 5
  Placement = pos=(-21.3,18.635,0) rot=(0,0,1;0rad)
  Support = -> [XY_Plane096]
  Width = 0.23
FEATURE [PartDesign::SubtractiveBox] Box762
  AttacherType = Attacher::AttachEngine3D
  AttachmentOffset = pos=(-21.35,18.635,0.35) rot=(0,0,1;0rad)
  BaseFeature = -> Box769
  Height = 1.55
  Length = 0.5
  MapMode = 5
  Placement = pos=(-21.35,18.635,0.35) rot=(0,0,1;0rad)
  Support = -> [XY_Plane096]
  Width = 0.23
FEATURE [PartDesign::AdditiveBox] Box772
  AttacherType = Attacher::AttachEngine3D
  AttachmentOffset = pos=(-21.3,18.635,0) rot=(0,0,1;0rad)
  Height = 1.9
  Length = 1.3
  MapMode = 5
  Placement = pos=(-21.3,18.635,0) rot=(0,0,1;0rad)
  Support = -> [XY_Plane092]
  Width = 0.23
FEATURE [PartDesign::SubtractiveBox] Box767
  AttacherType = Attacher::AttachEngine3D
  AttachmentOffset = pos=(-21.35,18.635,0.35) rot=(0,0,1;0rad)
  BaseFeature = -> Box772
  Height = 1.55
  Length = 0.5
  MapMode = 5
  Placement = pos=(-21.35,18.635,0.35) rot=(0,0,1;0rad)
  Support = -> [XY_Plane092]
  Width = 0.23
FEATURE [PartDesign::AdditiveBox] Box776
  AttacherType = Attacher::AttachEngine3D
  AttachmentOffset = pos=(-21.3,18.635,0) rot=(0,0,1;0rad)
  Height = 1.9
  Length = 1.3
  MapMode = 5
  Placement = pos=(-21.3,18.635,0) rot=(0,0,1;0rad)
  Support = -> [XY_Plane091]
  Width = 0.23
FEATURE [PartDesign::SubtractiveBox] Box777
  AttacherType = Attacher::AttachEngine3D
  AttachmentOffset = pos=(-21.35,18.635,0.35) rot=(0,0,1;0rad)
  BaseFeature = -> Box776
  Height = 1.55
  Length = 0.5
  MapMode = 5
  Placement = pos=(-21.35,18.635,0.35) rot=(0,0,1;0rad)
  Support = -> [XY_Plane091]
  Width = 0.23
FEATURE [PartDesign::AdditiveBox] Box779
  AttacherType = Attacher::AttachEngine3D
  AttachmentOffset = pos=(-21.3,18.635,0) rot=(0,0,1;0rad)
  Height = 1.9
  Length = 1.3
  MapMode = 5
  Placement = pos=(-21.3,18.635,0) rot=(0,0,1;0rad)
  Support = -> [XY_Plane104]
  Width = 0.23
FEATURE [PartDesign::AdditiveBox] Box780
  AttacherType = Attacher::AttachEngine3D
  AttachmentOffset = pos=(-21.3,18.635,0) rot=(0,0,1;0rad)
  Height = 1.9
  Length = 1.3
  MapMode = 5
  Placement = pos=(-21.3,18.635,0) rot=(0,0,1;0rad)
  Support = -> [XY_Plane107]
  Width = 0.23
FEATURE [PartDesign::SubtractiveBox] Box784
  AttacherType = Attacher::AttachEngine3D
  AttachmentOffset = pos=(-21.35,18.635,0.35) rot=(0,0,1;0rad)
  BaseFeature = -> Box779
  Height = 1.55
  Length = 0.5
  MapMode = 5
  Placement = pos=(-21.35,18.635,0.35) rot=(0,0,1;0rad)
  Support = -> [XY_Plane104]
  Width = 0.23
FEATURE [PartDesign::AdditiveBox] Box785
  AttacherType = Attacher::AttachEngine3D
  AttachmentOffset = pos=(-21.3,18.635,0) rot=(0,0,1;0rad)
  Height = 1.9
  Length = 1.3
  MapMode = 5
  Placement = pos=(-21.3,18.635,0) rot=(0,0,1;0rad)
  Support = -> [XY_Plane109]
  Width = 0.23
FEATURE [PartDesign::SubtractiveBox] Box788
  AttacherType = Attacher::AttachEngine3D
  AttachmentOffset = pos=(-21.35,18.635,0.35) rot=(0,0,1;0rad)
  BaseFeature = -> Box785
  Height = 1.55
  Length = 0.5
  MapMode = 5
  Placement = pos=(-21.35,18.635,0.35) rot=(0,0,1;0rad)
  Support = -> [XY_Plane109]
  Width = 0.23
FEATURE [PartDesign::SubtractiveBox] Box792
  AttacherType = Attacher::AttachEngine3D
  AttachmentOffset = pos=(-21.35,18.635,0.35) rot=(0,0,1;0rad)
  BaseFeature = -> Box780
  Height = 1.55
  Length = 0.5
  MapMode = 5
  Placement = pos=(-21.35,18.635,0.35) rot=(0,0,1;0rad)
  Support = -> [XY_Plane107]
  Width = 0.23
FEATURE [PartDesign::AdditiveBox] Box808
  AttacherType = Attacher::AttachEngine3D
  AttachmentOffset = pos=(-21.3,18.635,0) rot=(0,0,1;0rad)
  Height = 1.9
  Length = 1.3
  MapMode = 5
  Placement = pos=(-21.3,18.635,0) rot=(0,0,1;0rad)
  Support = -> [XY_Plane087]
  Width = 0.23
FEATURE [PartDesign::SubtractiveBox] Box811
  AttacherType = Attacher::AttachEngine3D
  AttachmentOffset = pos=(-21.35,18.635,0.35) rot=(0,0,1;0rad)
  BaseFeature = -> Box808
  Height = 1.55
  Length = 0.5
  MapMode = 5
  Placement = pos=(-21.35,18.635,0.35) rot=(0,0,1;0rad)
  Support = -> [XY_Plane087]
  Width = 0.23
FEATURE [PartDesign::SubtractiveBox] Box804
  AttacherType = Attacher::AttachEngine3D
  AttachmentOffset = pos=(-20.5,18.63,0) rot=(0,0,1;0rad)
  BaseFeature = -> Box811
  Height = 1.635
  Length = 0.5
  MapMode = 5
  Placement = pos=(-20.5,18.63,0) rot=(0,0,1;0rad)
  Support = -> [XY_Plane087]
  Width = 0.25
FEATURE [PartDesign::SubtractiveBox] Box813
  AttacherType = Attacher::AttachEngine3D
  AttachmentOffset = pos=(-21.19,18.635,-0.12) rot=(0,-1,0;0.15708rad)
  BaseFeature = -> Box804
  Height = 0.12
  Length = 0.725
  MapMode = 5
  Placement = pos=(-21.19,18.635,-0.12) rot=(0,-1,0;0.15708rad)
  Support = -> [XY_Plane087]
  Width = 0.25
FEATURE [PartDesign::SubtractiveBox] Box814
  AttacherType = Attacher::AttachEngine3D
  AttachmentOffset = pos=(-21.5005,18.625,0.235) rot=(0,-1,0;0.174533rad)
  BaseFeature = -> Box813
  Height = 0.3
  Length = 0.6605
  MapMode = 5
  Placement = pos=(-21.5005,18.625,0.235) rot=(0,-1,0;0.174533rad)
  Support = -> [XY_Plane087]
  Width = 0.25
FEATURE [PartDesign::AdditiveBox] Box820
  AttacherType = Attacher::AttachEngine3D
  AttachmentOffset = pos=(-21.3,18.635,0) rot=(0,0,1;0rad)
  Height = 1.9
  Length = 1.3
  MapMode = 5
  Placement = pos=(-21.3,18.635,0) rot=(0,0,1;0rad)
  Support = -> [XY_Plane084]
  Width = 0.23
FEATURE [PartDesign::SubtractiveBox] Box826
  AttacherType = Attacher::AttachEngine3D
  AttachmentOffset = pos=(-21.35,18.635,0.35) rot=(0,0,1;0rad)
  BaseFeature = -> Box820
  Height = 1.55
  Length = 0.5
  MapMode = 5
  Placement = pos=(-21.35,18.635,0.35) rot=(0,0,1;0rad)
  Support = -> [XY_Plane084]
  Width = 0.23
FEATURE [PartDesign::SubtractiveBox] Box802
  AttacherType = Attacher::AttachEngine3D
  AttachmentOffset = pos=(-20.5,18.63,0) rot=(0,0,1;0rad)
  BaseFeature = -> Box826
  Height = 1.635
  Length = 0.5
  MapMode = 5
  Placement = pos=(-20.5,18.63,0) rot=(0,0,1;0rad)
  Support = -> [XY_Plane084]
  Width = 0.25
FEATURE [PartDesign::SubtractiveBox] Box810
  AttacherType = Attacher::AttachEngine3D
  AttachmentOffset = pos=(-21.19,18.635,-0.12) rot=(0,-1,0;0.15708rad)
  BaseFeature = -> Box802
  Height = 0.12
  Length = 0.725
  MapMode = 5
  Placement = pos=(-21.19,18.635,-0.12) rot=(0,-1,0;0.15708rad)
  Support = -> [XY_Plane084]
  Width = 0.25
FEATURE [PartDesign::SubtractiveBox] Box819
  AttacherType = Attacher::AttachEngine3D
  AttachmentOffset = pos=(-21.5005,18.625,0.235) rot=(0,-1,0;0.174533rad)
  BaseFeature = -> Box810
  Height = 0.3
  Length = 0.6605
  MapMode = 5
  Placement = pos=(-21.5005,18.625,0.235) rot=(0,-1,0;0.174533rad)
  Support = -> [XY_Plane084]
  Width = 0.25
FEATURE [PartDesign::AdditiveBox] Box831
  AttacherType = Attacher::AttachEngine3D
  AttachmentOffset = pos=(-21.3,18.635,0) rot=(0,0,1;0rad)
  Height = 1.9
  Length = 1.3
  MapMode = 5
  Placement = pos=(-21.3,18.635,0) rot=(0,0,1;0rad)
  Support = -> [XY_Plane088]
  Width = 0.23
FEATURE [PartDesign::SubtractiveBox] Box822
  AttacherType = Attacher::AttachEngine3D
  AttachmentOffset = pos=(-21.35,18.635,0.35) rot=(0,0,1;0rad)
  BaseFeature = -> Box831
  Height = 1.55
  Length = 0.5
  MapMode = 5
  Placement = pos=(-21.35,18.635,0.35) rot=(0,0,1;0rad)
  Support = -> [XY_Plane088]
  Width = 0.23
FEATURE [PartDesign::SubtractiveBox] Box801
  AttacherType = Attacher::AttachEngine3D
  AttachmentOffset = pos=(-20.5,18.63,0) rot=(0,0,1;0rad)
  BaseFeature = -> Box822
  Height = 1.635
  Length = 0.5
  MapMode = 5
  Placement = pos=(-20.5,18.63,0) rot=(0,0,1;0rad)
  Support = -> [XY_Plane088]
  Width = 0.25
FEATURE [PartDesign::SubtractiveBox] Box803
  AttacherType = Attacher::AttachEngine3D
  AttachmentOffset = pos=(-21.19,18.635,-0.12) rot=(0,-1,0;0.15708rad)
  BaseFeature = -> Box801
  Height = 0.12
  Length = 0.725
  MapMode = 5
  Placement = pos=(-21.19,18.635,-0.12) rot=(0,-1,0;0.15708rad)
  Support = -> [XY_Plane088]
  Width = 0.25
FEATURE [PartDesign::SubtractiveBox] Box821
  AttacherType = Attacher::AttachEngine3D
  AttachmentOffset = pos=(-21.5005,18.625,0.235) rot=(0,-1,0;0.174533rad)
  BaseFeature = -> Box803
  Height = 0.3
  Length = 0.6605
  MapMode = 5
  Placement = pos=(-21.5005,18.625,0.235) rot=(0,-1,0;0.174533rad)
  Support = -> [XY_Plane088]
  Width = 0.25
FEATURE [PartDesign::AdditiveBox] Box837
  AttacherType = Attacher::AttachEngine3D
  AttachmentOffset = pos=(-21.3,18.635,0) rot=(0,0,1;0rad)
  Height = 1.9
  Length = 1.3
  MapMode = 5
  Placement = pos=(-21.3,18.635,0) rot=(0,0,1;0rad)
  Support = -> [XY_Plane093]
  Width = 0.23
FEATURE [PartDesign::SubtractiveBox] Box840
  AttacherType = Attacher::AttachEngine3D
  AttachmentOffset = pos=(-21.35,18.635,0.35) rot=(0,0,1;0rad)
  BaseFeature = -> Box837
  Height = 1.55
  Length = 0.5
  MapMode = 5
  Placement = pos=(-21.35,18.635,0.35) rot=(0,0,1;0rad)
  Support = -> [XY_Plane093]
  Width = 0.23
FEATURE [PartDesign::SubtractiveBox] Box825
  AttacherType = Attacher::AttachEngine3D
  AttachmentOffset = pos=(-20.5,18.63,0) rot=(0,0,1;0rad)
  BaseFeature = -> Box840
  Height = 1.635
  Length = 0.5
  MapMode = 5
  Placement = pos=(-20.5,18.63,0) rot=(0,0,1;0rad)
  Support = -> [XY_Plane093]
  Width = 0.25
FEATURE [PartDesign::SubtractiveBox] Box850
  AttacherType = Attacher::AttachEngine3D
  AttachmentOffset = pos=(-21.19,18.635,-0.12) rot=(0,-1,0;0.15708rad)
  BaseFeature = -> Box825
  Height = 0.12
  Length = 0.725
  MapMode = 5
  Placement = pos=(-21.19,18.635,-0.12) rot=(0,-1,0;0.15708rad)
  Support = -> [XY_Plane093]
  Width = 0.25
FEATURE [PartDesign::SubtractiveBox] Box845
  AttacherType = Attacher::AttachEngine3D
  AttachmentOffset = pos=(-21.5005,18.625,0.235) rot=(0,-1,0;0.174533rad)
  BaseFeature = -> Box850
  Height = 0.3
  Length = 0.6605
  MapMode = 5
  Placement = pos=(-21.5005,18.625,0.235) rot=(0,-1,0;0.174533rad)
  Support = -> [XY_Plane093]
  Width = 0.25
FEATURE [PartDesign::SubtractiveBox] Box853
  AttacherType = Attacher::AttachEngine3D
  AttachmentOffset = pos=(-20.5,18.63,0) rot=(0,0,1;0rad)
  BaseFeature = -> Box767
  Height = 1.635
  Length = 0.5
  MapMode = 5
  Placement = pos=(-20.5,18.63,0) rot=(0,0,1;0rad)
  Support = -> [XY_Plane092]
  Width = 0.25
FEATURE [PartDesign::SubtractiveBox] Box764
  AttacherType = Attacher::AttachEngine3D
  AttachmentOffset = pos=(-21.19,18.635,-0.12) rot=(0,-1,0;0.15708rad)
  BaseFeature = -> Box853
  Height = 0.12
  Length = 0.725
  MapMode = 5
  Placement = pos=(-21.19,18.635,-0.12) rot=(0,-1,0;0.15708rad)
  Support = -> [XY_Plane092]
  Width = 0.25
FEATURE [PartDesign::SubtractiveBox] Box763
  AttacherType = Attacher::AttachEngine3D
  AttachmentOffset = pos=(-21.5005,18.625,0.235) rot=(0,-1,0;0.174533rad)
  BaseFeature = -> Box764
  Height = 0.3
  Length = 0.6605
  MapMode = 5
  Placement = pos=(-21.5005,18.625,0.235) rot=(0,-1,0;0.174533rad)
  Support = -> [XY_Plane092]
  Width = 0.25
FEATURE [PartDesign::AdditiveBox] Box856
  AttacherType = Attacher::AttachEngine3D
  AttachmentOffset = pos=(-21.3,18.635,0) rot=(0,0,1;0rad)
  Height = 1.9
  Length = 1.3
  MapMode = 5
  Placement = pos=(-21.3,18.635,0) rot=(0,0,1;0rad)
  Support = -> [XY_Plane094]
  Width = 0.23
FEATURE [PartDesign::SubtractiveBox] Box854
  AttacherType = Attacher::AttachEngine3D
  AttachmentOffset = pos=(-21.35,18.635,0.35) rot=(0,0,1;0rad)
  BaseFeature = -> Box856
  Height = 1.55
  Length = 0.5
  MapMode = 5
  Placement = pos=(-21.35,18.635,0.35) rot=(0,0,1;0rad)
  Support = -> [XY_Plane094]
  Width = 0.23
FEATURE [PartDesign::SubtractiveBox] Box832
  AttacherType = Attacher::AttachEngine3D
  AttachmentOffset = pos=(-20.5,18.63,0) rot=(0,0,1;0rad)
  BaseFeature = -> Box854
  Height = 1.635
  Length = 0.5
  MapMode = 5
  Placement = pos=(-20.5,18.63,0) rot=(0,0,1;0rad)
  Support = -> [XY_Plane094]
  Width = 0.25
FEATURE [PartDesign::SubtractiveBox] Box835
  AttacherType = Attacher::AttachEngine3D
  AttachmentOffset = pos=(-21.19,18.635,-0.12) rot=(0,-1,0;0.15708rad)
  BaseFeature = -> Box832
  Height = 0.12
  Length = 0.725
  MapMode = 5
  Placement = pos=(-21.19,18.635,-0.12) rot=(0,-1,0;0.15708rad)
  Support = -> [XY_Plane094]
  Width = 0.25
FEATURE [PartDesign::SubtractiveBox] Box859
  AttacherType = Attacher::AttachEngine3D
  AttachmentOffset = pos=(-20.5,18.63,0) rot=(0,0,1;0rad)
  BaseFeature = -> Box777
  Height = 1.635
  Length = 0.5
  MapMode = 5
  Placement = pos=(-20.5,18.63,0) rot=(0,0,1;0rad)
  Support = -> [XY_Plane091]
  Width = 0.25
FEATURE [PartDesign::AdditiveBox] Box860
  AttacherType = Attacher::AttachEngine3D
  AttachmentOffset = pos=(-21.3,18.635,0) rot=(0,0,1;0rad)
  Height = 1.9
  Length = 1.3
  MapMode = 5
  Placement = pos=(-21.3,18.635,0) rot=(0,0,1;0rad)
  Support = -> [XY_Plane089]
  Width = 0.23
FEATURE [PartDesign::SubtractiveBox] Box855
  AttacherType = Attacher::AttachEngine3D
  AttachmentOffset = pos=(-21.35,18.635,0.35) rot=(0,0,1;0rad)
  BaseFeature = -> Box860
  Height = 1.55
  Length = 0.5
  MapMode = 5
  Placement = pos=(-21.35,18.635,0.35) rot=(0,0,1;0rad)
  Support = -> [XY_Plane089]
  Width = 0.23
FEATURE [PartDesign::SubtractiveBox] Box824
  AttacherType = Attacher::AttachEngine3D
  AttachmentOffset = pos=(-20.5,18.63,0) rot=(0,0,1;0rad)
  BaseFeature = -> Box855
  Height = 1.635
  Length = 0.5
  MapMode = 5
  Placement = pos=(-20.5,18.63,0) rot=(0,0,1;0rad)
  Support = -> [XY_Plane089]
  Width = 0.25
FEATURE [PartDesign::SubtractiveBox] Box839
  AttacherType = Attacher::AttachEngine3D
  AttachmentOffset = pos=(-21.19,18.635,-0.12) rot=(0,-1,0;0.15708rad)
  BaseFeature = -> Box824
  Height = 0.12
  Length = 0.725
  MapMode = 5
  Placement = pos=(-21.19,18.635,-0.12) rot=(0,-1,0;0.15708rad)
  Support = -> [XY_Plane089]
  Width = 0.25
FEATURE [PartDesign::SubtractiveBox] Box843
  AttacherType = Attacher::AttachEngine3D
  AttachmentOffset = pos=(-21.5005,18.625,0.235) rot=(0,-1,0;0.174533rad)
  BaseFeature = -> Box839
  Height = 0.3
  Length = 0.6605
  MapMode = 5
  Placement = pos=(-21.5005,18.625,0.235) rot=(0,-1,0;0.174533rad)
  Support = -> [XY_Plane089]
  Width = 0.25
FEATURE [PartDesign::SubtractiveBox] Box861
  AttacherType = Attacher::AttachEngine3D
  AttachmentOffset = pos=(-21.5005,18.625,0.235) rot=(0,-1,0;0.174533rad)
  BaseFeature = -> Box835
  Height = 0.3
  Length = 0.6605
  MapMode = 5
  Placement = pos=(-21.5005,18.625,0.235) rot=(0,-1,0;0.174533rad)
  Support = -> [XY_Plane094]
  Width = 0.25
FEATURE [PartDesign::SubtractiveBox] Box866
  AttacherType = Attacher::AttachEngine3D
  AttachmentOffset = pos=(-20.5,18.63,0) rot=(0,0,1;0rad)
  BaseFeature = -> Box762
  Height = 1.635
  Length = 0.5
  MapMode = 5
  Placement = pos=(-20.5,18.63,0) rot=(0,0,1;0rad)
  Support = -> [XY_Plane096]
  Width = 0.25
FEATURE [PartDesign::SubtractiveBox] Box765
  AttacherType = Attacher::AttachEngine3D
  AttachmentOffset = pos=(-21.19,18.635,-0.12) rot=(0,-1,0;0.15708rad)
  BaseFeature = -> Box866
  Height = 0.12
  Length = 0.725
  MapMode = 5
  Placement = pos=(-21.19,18.635,-0.12) rot=(0,-1,0;0.15708rad)
  Support = -> [XY_Plane096]
  Width = 0.25
FEATURE [PartDesign::SubtractiveBox] Box768
  AttacherType = Attacher::AttachEngine3D
  AttachmentOffset = pos=(-21.5005,18.625,0.235) rot=(0,-1,0;0.174533rad)
  BaseFeature = -> Box765
  Height = 0.3
  Length = 0.6605
  MapMode = 5
  Placement = pos=(-21.5005,18.625,0.235) rot=(0,-1,0;0.174533rad)
  Support = -> [XY_Plane096]
  Width = 0.25
FEATURE [PartDesign::SubtractiveBox] Box867
  AttacherType = Attacher::AttachEngine3D
  AttachmentOffset = pos=(-21.19,18.635,-0.12) rot=(0,-1,0;0.15708rad)
  BaseFeature = -> Box859
  Height = 0.12
  Length = 0.725
  MapMode = 5
  Placement = pos=(-21.19,18.635,-0.12) rot=(0,-1,0;0.15708rad)
  Support = -> [XY_Plane091]
  Width = 0.25
FEATURE [PartDesign::SubtractiveBox] Box773
  AttacherType = Attacher::AttachEngine3D
  AttachmentOffset = pos=(-21.5005,18.625,0.235) rot=(0,-1,0;0.174533rad)
  BaseFeature = -> Box867
  Height = 0.3
  Length = 0.6605
  MapMode = 5
  Placement = pos=(-21.5005,18.625,0.235) rot=(0,-1,0;0.174533rad)
  Support = -> [XY_Plane091]
  Width = 0.25
FEATURE [PartDesign::Fillet] Fillet237
  Base = -> Box814 [Edge2]
  BaseFeature = -> Box814
  Placement = pos=(-21.5005,18.625,0.235) rot=(0,-1,0;0.174533rad)
  Radius = 0.05
  SupportTransform = false
FEATURE [PartDesign::Fillet] Fillet239
  Base = -> Fillet237 [Edge33]
  BaseFeature = -> Fillet237
  Placement = pos=(-21.5005,18.625,0.235) rot=(0,-1,0;0.174533rad)
  Radius = 0.5
  SupportTransform = false
FEATURE [PartDesign::AdditiveBox] Box795
  AttacherType = Attacher::AttachEngine3D
  AttachmentOffset = pos=(-21.1,18.635,0.305) rot=(0,1,0;0.785398rad)
  BaseFeature = -> Fillet239
  Height = 0.375
  Length = 0.2
  MapMode = 5
  Placement = pos=(-21.1,18.635,0.305) rot=(0,1,0;0.785398rad)
  Support = -> [XY_Plane087]
  Width = 0.23
FEATURE [PartDesign::SubtractiveCylinder] Cylinder163
  Angle = 360
  AttacherType = Attacher::AttachEngine3D
  AttachmentOffset = pos=(-21.055,18.935,0.52) rot=(1,0,0;1.5708rad)
  BaseFeature = -> Box795
  Height = 0.375
  MapMode = 5
  Placement = pos=(-21.055,18.935,0.52) rot=(1,0,0;1.5708rad)
  Radius = 0.205
  Support = -> [XY_Plane087]
FEATURE [PartDesign::SubtractiveBox] Box816
  AttacherType = Attacher::AttachEngine3D
  AttachmentOffset = pos=(-20.95,18.635,0.53) rot=(0,0,1;0rad)
  BaseFeature = -> Cylinder163
  Height = 0.5
  Length = 0.1
  MapMode = 5
  Placement = pos=(-20.95,18.635,0.53) rot=(0,0,1;0rad)
  Support = -> [XY_Plane087]
  Width = 0.23
FEATURE [PartDesign::SubtractiveBox] Box806
  AttacherType = Attacher::AttachEngine3D
  AttachmentOffset = pos=(-21.15,18.635,0.297) rot=(0,-1,0;0.174533rad)
  BaseFeature = -> Box816
  Height = 0.115
  Length = 0.115
  MapMode = 5
  Placement = pos=(-21.15,18.635,0.297) rot=(0,-1,0;0.174533rad)
  Support = -> [XY_Plane087]
  Width = 0.23
FEATURE [PartDesign::Fillet] Fillet238
  Base = -> Box806 [Edge28]
  BaseFeature = -> Box806
  Placement = pos=(-21.15,18.635,0.297) rot=(0,-1,0;0.174533rad)
  Radius = 0.375
  SupportTransform = false
FEATURE [PartDesign::AdditiveBox] Box805
  AttacherType = Attacher::AttachEngine3D
  AttachmentOffset = pos=(-20.7,18.635,1.55) rot=(0,1,0;0.785398rad)
  BaseFeature = -> Fillet238
  Height = 0.375
  Length = 0.23
  MapMode = 5
  Placement = pos=(-20.7,18.635,1.55) rot=(0,1,0;0.785398rad)
  Support = -> [XY_Plane087]
  Width = 0.23
FEATURE [PartDesign::SubtractiveCylinder] Cylinder165
  Angle = 360
  AttacherType = Attacher::AttachEngine3D
  AttachmentOffset = pos=(-20.271,18.635,1.4056) rot=(-1,0,0;1.5708rad)
  BaseFeature = -> Box805
  Height = 0.23
  MapMode = 5
  Placement = pos=(-20.271,18.635,1.4056) rot=(-1,0,0;1.5708rad)
  Radius = 0.23
  Support = -> [XY_Plane087]
FEATURE [PartDesign::AdditiveBox] Box815
  AttacherType = Attacher::AttachEngine3D
  AttachmentOffset = pos=(-20.1,18.635,1.635) rot=(0,0,1;0rad)
  BaseFeature = -> Cylinder165
  Height = 0.265
  Length = 0.23
  MapMode = 5
  Placement = pos=(-20.1,18.635,1.635) rot=(0,0,1;0rad)
  Support = -> [XY_Plane087]
  Width = 0.23
FEATURE [PartDesign::Body] Body081  label="pin081"
  Group = -> [Box808,Box811,Box804,Box813,Box814,Fillet237,Fillet239,Box795,Cylinder163,Box816,Box806,Fillet238,Box805,Cylinder165,Box815]
  Origin = -> Origin091
  Placement = pos=(0,-2,0) rot=(0,0,1;0rad)
  Tip = -> Box815
FEATURE [PartDesign::Fillet] Fillet240
  Base = -> Box819 [Edge2]
  BaseFeature = -> Box819
  Placement = pos=(-21.5005,18.625,0.235) rot=(0,-1,0;0.174533rad)
  Radius = 0.05
  SupportTransform = false
FEATURE [PartDesign::Fillet] Fillet241
  Base = -> Fillet240 [Edge33]
  BaseFeature = -> Fillet240
  Placement = pos=(-21.5005,18.625,0.235) rot=(0,-1,0;0.174533rad)
  Radius = 0.5
  SupportTransform = false
FEATURE [PartDesign::AdditiveBox] Box807
  AttacherType = Attacher::AttachEngine3D
  AttachmentOffset = pos=(-21.1,18.635,0.305) rot=(0,1,0;0.785398rad)
  BaseFeature = -> Fillet241
  Height = 0.375
  Length = 0.2
  MapMode = 5
  Placement = pos=(-21.1,18.635,0.305) rot=(0,1,0;0.785398rad)
  Support = -> [XY_Plane084]
  Width = 0.23
FEATURE [PartDesign::SubtractiveCylinder] Cylinder164
  Angle = 360
  AttacherType = Attacher::AttachEngine3D
  AttachmentOffset = pos=(-21.055,18.935,0.52) rot=(1,0,0;1.5708rad)
  BaseFeature = -> Box807
  Height = 0.375
  MapMode = 5
  Placement = pos=(-21.055,18.935,0.52) rot=(1,0,0;1.5708rad)
  Radius = 0.205
  Support = -> [XY_Plane084]
FEATURE [PartDesign::SubtractiveBox] Box812
  AttacherType = Attacher::AttachEngine3D
  AttachmentOffset = pos=(-20.95,18.635,0.53) rot=(0,0,1;0rad)
  BaseFeature = -> Cylinder164
  Height = 0.5
  Length = 0.1
  MapMode = 5
  Placement = pos=(-20.95,18.635,0.53) rot=(0,0,1;0rad)
  Support = -> [XY_Plane084]
  Width = 0.23
FEATURE [PartDesign::SubtractiveBox] Box818
  AttacherType = Attacher::AttachEngine3D
  AttachmentOffset = pos=(-21.15,18.635,0.297) rot=(0,-1,0;0.174533rad)
  BaseFeature = -> Box812
  Height = 0.115
  Length = 0.115
  MapMode = 5
  Placement = pos=(-21.15,18.635,0.297) rot=(0,-1,0;0.174533rad)
  Support = -> [XY_Plane084]
  Width = 0.23
FEATURE [PartDesign::Fillet] Fillet229
  Base = -> Box818 [Edge28]
  BaseFeature = -> Box818
  Placement = pos=(-21.15,18.635,0.297) rot=(0,-1,0;0.174533rad)
  Radius = 0.375
  SupportTransform = false
FEATURE [PartDesign::AdditiveBox] Box817
  AttacherType = Attacher::AttachEngine3D
  AttachmentOffset = pos=(-20.7,18.635,1.55) rot=(0,1,0;0.785398rad)
  BaseFeature = -> Fillet229
  Height = 0.375
  Length = 0.23
  MapMode = 5
  Placement = pos=(-20.7,18.635,1.55) rot=(0,1,0;0.785398rad)
  Support = -> [XY_Plane084]
  Width = 0.23
FEATURE [PartDesign::SubtractiveCylinder] Cylinder166
  Angle = 360
  AttacherType = Attacher::AttachEngine3D
  AttachmentOffset = pos=(-20.271,18.635,1.4056) rot=(-1,0,0;1.5708rad)
  BaseFeature = -> Box817
  Height = 0.23
  MapMode = 5
  Placement = pos=(-20.271,18.635,1.4056) rot=(-1,0,0;1.5708rad)
  Radius = 0.23
  Support = -> [XY_Plane084]
FEATURE [PartDesign::AdditiveBox] Box809
  AttacherType = Attacher::AttachEngine3D
  AttachmentOffset = pos=(-20.1,18.635,1.635) rot=(0,0,1;0rad)
  BaseFeature = -> Cylinder166
  Height = 0.265
  Length = 0.23
  MapMode = 5
  Placement = pos=(-20.1,18.635,1.635) rot=(0,0,1;0rad)
  Support = -> [XY_Plane084]
  Width = 0.23
FEATURE [PartDesign::Body] Body082  label="pin082"
  Group = -> [Box820,Box826,Box802,Box810,Box819,Fillet240,Fillet241,Box807,Cylinder164,Box812,Box818,Fillet229,Box817,Cylinder166,Box809]
  Origin = -> Origin096
  Placement = pos=(0,-2.5,0) rot=(0,0,1;0rad)
  Tip = -> Box809
FEATURE [PartDesign::AdditiveBox] Box886
  AttacherType = Attacher::AttachEngine3D
  AttachmentOffset = pos=(-21.3,18.635,0) rot=(0,0,1;0rad)
  Height = 1.9
  Length = 1.3
  MapMode = 5
  Placement = pos=(-21.3,18.635,0) rot=(0,0,1;0rad)
  Support = -> [XY_Plane095]
  Width = 0.23
FEATURE [PartDesign::SubtractiveBox] Box887
  AttacherType = Attacher::AttachEngine3D
  AttachmentOffset = pos=(-21.35,18.635,0.35) rot=(0,0,1;0rad)
  BaseFeature = -> Box886
  Height = 1.55
  Length = 0.5
  MapMode = 5
  Placement = pos=(-21.35,18.635,0.35) rot=(0,0,1;0rad)
  Support = -> [XY_Plane095]
  Width = 0.23
FEATURE [PartDesign::SubtractiveBox] Box876
  AttacherType = Attacher::AttachEngine3D
  AttachmentOffset = pos=(-20.5,18.63,0) rot=(0,0,1;0rad)
  BaseFeature = -> Box887
  Height = 1.635
  Length = 0.5
  MapMode = 5
  Placement = pos=(-20.5,18.63,0) rot=(0,0,1;0rad)
  Support = -> [XY_Plane095]
  Width = 0.25
FEATURE [PartDesign::SubtractiveBox] Box883
  AttacherType = Attacher::AttachEngine3D
  AttachmentOffset = pos=(-21.19,18.635,-0.12) rot=(0,-1,0;0.15708rad)
  BaseFeature = -> Box876
  Height = 0.12
  Length = 0.725
  MapMode = 5
  Placement = pos=(-21.19,18.635,-0.12) rot=(0,-1,0;0.15708rad)
  Support = -> [XY_Plane095]
  Width = 0.25
FEATURE [PartDesign::SubtractiveBox] Box884
  AttacherType = Attacher::AttachEngine3D
  AttachmentOffset = pos=(-21.5005,18.625,0.235) rot=(0,-1,0;0.174533rad)
  BaseFeature = -> Box883
  Height = 0.3
  Length = 0.6605
  MapMode = 5
  Placement = pos=(-21.5005,18.625,0.235) rot=(0,-1,0;0.174533rad)
  Support = -> [XY_Plane095]
  Width = 0.25
FEATURE [PartDesign::Fillet] Fillet232
  Base = -> Box884 [Edge2]
  BaseFeature = -> Box884
  Placement = pos=(-21.5005,18.625,0.235) rot=(0,-1,0;0.174533rad)
  Radius = 0.05
  SupportTransform = false
FEATURE [PartDesign::Fillet] Fillet233
  Base = -> Fillet232 [Edge33]
  BaseFeature = -> Fillet232
  Placement = pos=(-21.5005,18.625,0.235) rot=(0,-1,0;0.174533rad)
  Radius = 0.5
  SupportTransform = false
FEATURE [PartDesign::AdditiveBox] Box878
  AttacherType = Attacher::AttachEngine3D
  AttachmentOffset = pos=(-21.1,18.635,0.305) rot=(0,1,0;0.785398rad)
  BaseFeature = -> Fillet233
  Height = 0.375
  Length = 0.2
  MapMode = 5
  Placement = pos=(-21.1,18.635,0.305) rot=(0,1,0;0.785398rad)
  Support = -> [XY_Plane095]
  Width = 0.23
FEATURE [PartDesign::SubtractiveCylinder] Cylinder179
  Angle = 360
  AttacherType = Attacher::AttachEngine3D
  AttachmentOffset = pos=(-21.055,18.935,0.52) rot=(1,0,0;1.5708rad)
  BaseFeature = -> Box878
  Height = 0.375
  MapMode = 5
  Placement = pos=(-21.055,18.935,0.52) rot=(1,0,0;1.5708rad)
  Radius = 0.205
  Support = -> [XY_Plane095]
FEATURE [PartDesign::SubtractiveBox] Box882
  AttacherType = Attacher::AttachEngine3D
  AttachmentOffset = pos=(-20.95,18.635,0.53) rot=(0,0,1;0rad)
  BaseFeature = -> Cylinder179
  Height = 0.5
  Length = 0.1
  MapMode = 5
  Placement = pos=(-20.95,18.635,0.53) rot=(0,0,1;0rad)
  Support = -> [XY_Plane095]
  Width = 0.23
FEATURE [PartDesign::SubtractiveBox] Box879
  AttacherType = Attacher::AttachEngine3D
  AttachmentOffset = pos=(-21.15,18.635,0.297) rot=(0,-1,0;0.174533rad)
  BaseFeature = -> Box882
  Height = 0.115
  Length = 0.115
  MapMode = 5
  Placement = pos=(-21.15,18.635,0.297) rot=(0,-1,0;0.174533rad)
  Support = -> [XY_Plane095]
  Width = 0.23
FEATURE [PartDesign::Fillet] Fillet234
  Base = -> Box879 [Edge28]
  BaseFeature = -> Box879
  Placement = pos=(-21.15,18.635,0.297) rot=(0,-1,0;0.174533rad)
  Radius = 0.375
  SupportTransform = false
FEATURE [PartDesign::AdditiveBox] Box877
  AttacherType = Attacher::AttachEngine3D
  AttachmentOffset = pos=(-20.7,18.635,1.55) rot=(0,1,0;0.785398rad)
  BaseFeature = -> Fillet234
  Height = 0.375
  Length = 0.23
  MapMode = 5
  Placement = pos=(-20.7,18.635,1.55) rot=(0,1,0;0.785398rad)
  Support = -> [XY_Plane095]
  Width = 0.23
FEATURE [PartDesign::SubtractiveCylinder] Cylinder180
  Angle = 360
  AttacherType = Attacher::AttachEngine3D
  AttachmentOffset = pos=(-20.271,18.635,1.4056) rot=(-1,0,0;1.5708rad)
  BaseFeature = -> Box877
  Height = 0.23
  MapMode = 5
  Placement = pos=(-20.271,18.635,1.4056) rot=(-1,0,0;1.5708rad)
  Radius = 0.23
  Support = -> [XY_Plane095]
FEATURE [PartDesign::AdditiveBox] Box885
  AttacherType = Attacher::AttachEngine3D
  AttachmentOffset = pos=(-20.1,18.635,1.635) rot=(0,0,1;0rad)
  BaseFeature = -> Cylinder180
  Height = 0.265
  Length = 0.23
  MapMode = 5
  Placement = pos=(-20.1,18.635,1.635) rot=(0,0,1;0rad)
  Support = -> [XY_Plane095]
  Width = 0.23
FEATURE [PartDesign::Body] Body078  label="pin078"
  Group = -> [Box886,Box887,Box876,Box883,Box884,Fillet232,Fillet233,Box878,Cylinder179,Box882,Box879,Fillet234,Box877,Cylinder180,Box885]
  Origin = -> Origin086
  Placement = pos=(0,-0.5,0) rot=(0,0,1;0rad)
  Tip = -> Box885
FEATURE [PartDesign::AdditiveBox] Box893
  AttacherType = Attacher::AttachEngine3D
  AttachmentOffset = pos=(-21.3,18.635,0) rot=(0,0,1;0rad)
  Height = 1.9
  Length = 1.3
  MapMode = 5
  Placement = pos=(-21.3,18.635,0) rot=(0,0,1;0rad)
  Support = -> [XY_Plane085]
  Width = 0.23
FEATURE [PartDesign::SubtractiveBox] Box896
  AttacherType = Attacher::AttachEngine3D
  AttachmentOffset = pos=(-21.35,18.635,0.35) rot=(0,0,1;0rad)
  BaseFeature = -> Box893
  Height = 1.55
  Length = 0.5
  MapMode = 5
  Placement = pos=(-21.35,18.635,0.35) rot=(0,0,1;0rad)
  Support = -> [XY_Plane085]
  Width = 0.23
FEATURE [PartDesign::SubtractiveBox] Box872
  AttacherType = Attacher::AttachEngine3D
  AttachmentOffset = pos=(-20.5,18.63,0) rot=(0,0,1;0rad)
  BaseFeature = -> Box896
  Height = 1.635
  Length = 0.5
  MapMode = 5
  Placement = pos=(-20.5,18.63,0) rot=(0,0,1;0rad)
  Support = -> [XY_Plane085]
  Width = 0.25
FEATURE [PartDesign::SubtractiveBox] Box892
  AttacherType = Attacher::AttachEngine3D
  AttachmentOffset = pos=(-21.19,18.635,-0.12) rot=(0,-1,0;0.15708rad)
  BaseFeature = -> Box872
  Height = 0.12
  Length = 0.725
  MapMode = 5
  Placement = pos=(-21.19,18.635,-0.12) rot=(0,-1,0;0.15708rad)
  Support = -> [XY_Plane085]
  Width = 0.25
FEATURE [PartDesign::SubtractiveBox] Box890
  AttacherType = Attacher::AttachEngine3D
  AttachmentOffset = pos=(-21.5005,18.625,0.235) rot=(0,-1,0;0.174533rad)
  BaseFeature = -> Box892
  Height = 0.3
  Length = 0.6605
  MapMode = 5
  Placement = pos=(-21.5005,18.625,0.235) rot=(0,-1,0;0.174533rad)
  Support = -> [XY_Plane085]
  Width = 0.25
FEATURE [PartDesign::Fillet] Fillet235
  Base = -> Box890 [Edge2]
  BaseFeature = -> Box890
  Placement = pos=(-21.5005,18.625,0.235) rot=(0,-1,0;0.174533rad)
  Radius = 0.05
  SupportTransform = false
FEATURE [PartDesign::Fillet] Fillet242
  Base = -> Fillet235 [Edge33]
  BaseFeature = -> Fillet235
  Placement = pos=(-21.5005,18.625,0.235) rot=(0,-1,0;0.174533rad)
  Radius = 0.5
  SupportTransform = false
FEATURE [PartDesign::AdditiveBox] Box880
  AttacherType = Attacher::AttachEngine3D
  AttachmentOffset = pos=(-21.1,18.635,0.305) rot=(0,1,0;0.785398rad)
  BaseFeature = -> Fillet242
  Height = 0.375
  Length = 0.2
  MapMode = 5
  Placement = pos=(-21.1,18.635,0.305) rot=(0,1,0;0.785398rad)
  Support = -> [XY_Plane085]
  Width = 0.23
FEATURE [PartDesign::SubtractiveCylinder] Cylinder181
  Angle = 360
  AttacherType = Attacher::AttachEngine3D
  AttachmentOffset = pos=(-21.055,18.935,0.52) rot=(1,0,0;1.5708rad)
  BaseFeature = -> Box880
  Height = 0.375
  MapMode = 5
  Placement = pos=(-21.055,18.935,0.52) rot=(1,0,0;1.5708rad)
  Radius = 0.205
  Support = -> [XY_Plane085]
FEATURE [PartDesign::SubtractiveBox] Box895
  AttacherType = Attacher::AttachEngine3D
  AttachmentOffset = pos=(-20.95,18.635,0.53) rot=(0,0,1;0rad)
  BaseFeature = -> Cylinder181
  Height = 0.5
  Length = 0.1
  MapMode = 5
  Placement = pos=(-20.95,18.635,0.53) rot=(0,0,1;0rad)
  Support = -> [XY_Plane085]
  Width = 0.23
FEATURE [PartDesign::SubtractiveBox] Box889
  AttacherType = Attacher::AttachEngine3D
  AttachmentOffset = pos=(-21.15,18.635,0.297) rot=(0,-1,0;0.174533rad)
  BaseFeature = -> Box895
  Height = 0.115
  Length = 0.115
  MapMode = 5
  Placement = pos=(-21.15,18.635,0.297) rot=(0,-1,0;0.174533rad)
  Support = -> [XY_Plane085]
  Width = 0.23
FEATURE [PartDesign::Fillet] Fillet243
  Base = -> Box889 [Edge28]
  BaseFeature = -> Box889
  Placement = pos=(-21.15,18.635,0.297) rot=(0,-1,0;0.174533rad)
  Radius = 0.375
  SupportTransform = false
FEATURE [PartDesign::AdditiveBox] Box888
  AttacherType = Attacher::AttachEngine3D
  AttachmentOffset = pos=(-20.7,18.635,1.55) rot=(0,1,0;0.785398rad)
  BaseFeature = -> Fillet243
  Height = 0.375
  Length = 0.23
  MapMode = 5
  Placement = pos=(-20.7,18.635,1.55) rot=(0,1,0;0.785398rad)
  Support = -> [XY_Plane085]
  Width = 0.23
FEATURE [PartDesign::SubtractiveCylinder] Cylinder182
  Angle = 360
  AttacherType = Attacher::AttachEngine3D
  AttachmentOffset = pos=(-20.271,18.635,1.4056) rot=(-1,0,0;1.5708rad)
  BaseFeature = -> Box888
  Height = 0.23
  MapMode = 5
  Placement = pos=(-20.271,18.635,1.4056) rot=(-1,0,0;1.5708rad)
  Radius = 0.23
  Support = -> [XY_Plane085]
FEATURE [PartDesign::AdditiveBox] Box891
  AttacherType = Attacher::AttachEngine3D
  AttachmentOffset = pos=(-20.1,18.635,1.635) rot=(0,0,1;0rad)
  BaseFeature = -> Cylinder182
  Height = 0.265
  Length = 0.23
  MapMode = 5
  Placement = pos=(-20.1,18.635,1.635) rot=(0,0,1;0rad)
  Support = -> [XY_Plane085]
  Width = 0.23
FEATURE [PartDesign::Body] Body079  label="pin079"
  Group = -> [Box893,Box896,Box872,Box892,Box890,Fillet235,Fillet242,Box880,Cylinder181,Box895,Box889,Fillet243,Box888,Cylinder182,Box891]
  Origin = -> Origin087
  Placement = pos=(0,-1,0) rot=(0,0,1;0rad)
  Tip = -> Box891
FEATURE [PartDesign::AdditiveBox] Box897
  AttacherType = Attacher::AttachEngine3D
  AttachmentOffset = pos=(-21.3,18.635,0) rot=(0,0,1;0rad)
  Height = 1.9
  Length = 1.3
  MapMode = 5
  Placement = pos=(-21.3,18.635,0) rot=(0,0,1;0rad)
  Support = -> [XY_Plane086]
  Width = 0.23
FEATURE [PartDesign::Fillet] Fillet246
  Base = -> Box763 [Edge2]
  BaseFeature = -> Box763
  Placement = pos=(-21.5005,18.625,0.235) rot=(0,-1,0;0.174533rad)
  Radius = 0.05
  SupportTransform = false
FEATURE [PartDesign::Fillet] Fillet249
  Base = -> Box843 [Edge2]
  BaseFeature = -> Box843
  Placement = pos=(-21.5005,18.625,0.235) rot=(0,-1,0;0.174533rad)
  Radius = 0.05
  SupportTransform = false
FEATURE [PartDesign::Fillet] Fillet251
  Base = -> Box821 [Edge2]
  BaseFeature = -> Box821
  Placement = pos=(-21.5005,18.625,0.235) rot=(0,-1,0;0.174533rad)
  Radius = 0.05
  SupportTransform = false
FEATURE [PartDesign::Fillet] Fillet236
  Base = -> Fillet251 [Edge33]
  BaseFeature = -> Fillet251
  Placement = pos=(-21.5005,18.625,0.235) rot=(0,-1,0;0.174533rad)
  Radius = 0.5
  SupportTransform = false
FEATURE [PartDesign::AdditiveBox] Box798
  AttacherType = Attacher::AttachEngine3D
  AttachmentOffset = pos=(-21.1,18.635,0.305) rot=(0,1,0;0.785398rad)
  BaseFeature = -> Fillet236
  Height = 0.375
  Length = 0.2
  MapMode = 5
  Placement = pos=(-21.1,18.635,0.305) rot=(0,1,0;0.785398rad)
  Support = -> [XY_Plane088]
  Width = 0.23
FEATURE [PartDesign::SubtractiveCylinder] Cylinder162
  Angle = 360
  AttacherType = Attacher::AttachEngine3D
  AttachmentOffset = pos=(-21.055,18.935,0.52) rot=(1,0,0;1.5708rad)
  BaseFeature = -> Box798
  Height = 0.375
  MapMode = 5
  Placement = pos=(-21.055,18.935,0.52) rot=(1,0,0;1.5708rad)
  Radius = 0.205
  Support = -> [XY_Plane088]
FEATURE [PartDesign::SubtractiveBox] Box800
  AttacherType = Attacher::AttachEngine3D
  AttachmentOffset = pos=(-20.95,18.635,0.53) rot=(0,0,1;0rad)
  BaseFeature = -> Cylinder162
  Height = 0.5
  Length = 0.1
  MapMode = 5
  Placement = pos=(-20.95,18.635,0.53) rot=(0,0,1;0rad)
  Support = -> [XY_Plane088]
  Width = 0.23
FEATURE [PartDesign::SubtractiveBox] Box799
  AttacherType = Attacher::AttachEngine3D
  AttachmentOffset = pos=(-21.15,18.635,0.297) rot=(0,-1,0;0.174533rad)
  BaseFeature = -> Box800
  Height = 0.115
  Length = 0.115
  MapMode = 5
  Placement = pos=(-21.15,18.635,0.297) rot=(0,-1,0;0.174533rad)
  Support = -> [XY_Plane088]
  Width = 0.23
FEATURE [PartDesign::Fillet] Fillet250
  Base = -> Box799 [Edge28]
  BaseFeature = -> Box799
  Placement = pos=(-21.15,18.635,0.297) rot=(0,-1,0;0.174533rad)
  Radius = 0.375
  SupportTransform = false
FEATURE [PartDesign::AdditiveBox] Box797
  AttacherType = Attacher::AttachEngine3D
  AttachmentOffset = pos=(-20.7,18.635,1.55) rot=(0,1,0;0.785398rad)
  BaseFeature = -> Fillet250
  Height = 0.375
  Length = 0.23
  MapMode = 5
  Placement = pos=(-20.7,18.635,1.55) rot=(0,1,0;0.785398rad)
  Support = -> [XY_Plane088]
  Width = 0.23
FEATURE [PartDesign::SubtractiveCylinder] Cylinder161
  Angle = 360
  AttacherType = Attacher::AttachEngine3D
  AttachmentOffset = pos=(-20.271,18.635,1.4056) rot=(-1,0,0;1.5708rad)
  BaseFeature = -> Box797
  Height = 0.23
  MapMode = 5
  Placement = pos=(-20.271,18.635,1.4056) rot=(-1,0,0;1.5708rad)
  Radius = 0.23
  Support = -> [XY_Plane088]
FEATURE [PartDesign::AdditiveBox] Box796
  AttacherType = Attacher::AttachEngine3D
  AttachmentOffset = pos=(-20.1,18.635,1.635) rot=(0,0,1;0rad)
  BaseFeature = -> Cylinder161
  Height = 0.265
  Length = 0.23
  MapMode = 5
  Placement = pos=(-20.1,18.635,1.635) rot=(0,0,1;0rad)
  Support = -> [XY_Plane088]
  Width = 0.23
FEATURE [PartDesign::Body] Body080  label="pin080"
  Group = -> [Box831,Box822,Box801,Box803,Box821,Fillet251,Fillet236,Box798,Cylinder162,Box800,Box799,Fillet250,Box797,Cylinder161,Box796]
  Origin = -> Origin090
  Placement = pos=(0,-1.5,0) rot=(0,0,1;0rad)
  Tip = -> Box796
FEATURE [PartDesign::Fillet] Fillet252
  Base = -> Box768 [Edge2]
  BaseFeature = -> Box768
  Placement = pos=(-21.5005,18.625,0.235) rot=(0,-1,0;0.174533rad)
  Radius = 0.05
  SupportTransform = false
FEATURE [PartDesign::Fillet] Fillet253
  Base = -> Fillet252 [Edge33]
  BaseFeature = -> Fillet252
  Placement = pos=(-21.5005,18.625,0.235) rot=(0,-1,0;0.174533rad)
  Radius = 0.5
  SupportTransform = false
FEATURE [PartDesign::AdditiveBox] Box863
  AttacherType = Attacher::AttachEngine3D
  AttachmentOffset = pos=(-21.1,18.635,0.305) rot=(0,1,0;0.785398rad)
  BaseFeature = -> Fillet253
  Height = 0.375
  Length = 0.2
  MapMode = 5
  Placement = pos=(-21.1,18.635,0.305) rot=(0,1,0;0.785398rad)
  Support = -> [XY_Plane096]
  Width = 0.23
FEATURE [PartDesign::SubtractiveCylinder] Cylinder177
  Angle = 360
  AttacherType = Attacher::AttachEngine3D
  AttachmentOffset = pos=(-21.055,18.935,0.52) rot=(1,0,0;1.5708rad)
  BaseFeature = -> Box863
  Height = 0.375
  MapMode = 5
  Placement = pos=(-21.055,18.935,0.52) rot=(1,0,0;1.5708rad)
  Radius = 0.205
  Support = -> [XY_Plane096]
FEATURE [PartDesign::SubtractiveBox] Box870
  AttacherType = Attacher::AttachEngine3D
  AttachmentOffset = pos=(-20.95,18.635,0.53) rot=(0,0,1;0rad)
  BaseFeature = -> Cylinder177
  Height = 0.5
  Length = 0.1
  MapMode = 5
  Placement = pos=(-20.95,18.635,0.53) rot=(0,0,1;0rad)
  Support = -> [XY_Plane096]
  Width = 0.23
FEATURE [PartDesign::SubtractiveBox] Box868
  AttacherType = Attacher::AttachEngine3D
  AttachmentOffset = pos=(-21.15,18.635,0.297) rot=(0,-1,0;0.174533rad)
  BaseFeature = -> Box870
  Height = 0.115
  Length = 0.115
  MapMode = 5
  Placement = pos=(-21.15,18.635,0.297) rot=(0,-1,0;0.174533rad)
  Support = -> [XY_Plane096]
  Width = 0.23
FEATURE [PartDesign::Fillet] Fillet254
  Base = -> Box868 [Edge28]
  BaseFeature = -> Box868
  Placement = pos=(-21.15,18.635,0.297) rot=(0,-1,0;0.174533rad)
  Radius = 0.375
  SupportTransform = false
FEATURE [PartDesign::AdditiveBox] Box864
  AttacherType = Attacher::AttachEngine3D
  AttachmentOffset = pos=(-20.7,18.635,1.55) rot=(0,1,0;0.785398rad)
  BaseFeature = -> Fillet254
  Height = 0.375
  Length = 0.23
  MapMode = 5
  Placement = pos=(-20.7,18.635,1.55) rot=(0,1,0;0.785398rad)
  Support = -> [XY_Plane096]
  Width = 0.23
FEATURE [PartDesign::SubtractiveCylinder] Cylinder178
  Angle = 360
  AttacherType = Attacher::AttachEngine3D
  AttachmentOffset = pos=(-20.271,18.635,1.4056) rot=(-1,0,0;1.5708rad)
  BaseFeature = -> Box864
  Height = 0.23
  MapMode = 5
  Placement = pos=(-20.271,18.635,1.4056) rot=(-1,0,0;1.5708rad)
  Radius = 0.23
  Support = -> [XY_Plane096]
FEATURE [PartDesign::AdditiveBox] Box766
  AttacherType = Attacher::AttachEngine3D
  AttachmentOffset = pos=(-20.1,18.635,1.635) rot=(0,0,1;0rad)
  BaseFeature = -> Cylinder178
  Height = 0.265
  Length = 0.23
  MapMode = 5
  Placement = pos=(-20.1,18.635,1.635) rot=(0,0,1;0rad)
  Support = -> [XY_Plane096]
  Width = 0.23
FEATURE [PartDesign::Body] Body084  label="pin084"
  Group = -> [Box769,Box762,Box866,Box765,Box768,Fillet252,Fillet253,Box863,Cylinder177,Box870,Box868,Fillet254,Box864,Cylinder178,Box766]
  Origin = -> Origin097
  Placement = pos=(0,-3.5,0) rot=(0,0,1;0rad)
  Tip = -> Box766
FEATURE [PartDesign::Fillet] Fillet255
  Base = -> Box845 [Edge2]
  BaseFeature = -> Box845
  Placement = pos=(-21.5005,18.625,0.235) rot=(0,-1,0;0.174533rad)
  Radius = 0.05
  SupportTransform = false
FEATURE [PartDesign::Fillet] Fillet257
  Base = -> Fillet255 [Edge33]
  BaseFeature = -> Fillet255
  Placement = pos=(-21.5005,18.625,0.235) rot=(0,-1,0;0.174533rad)
  Radius = 0.5
  SupportTransform = false
FEATURE [PartDesign::AdditiveBox] Box829
  AttacherType = Attacher::AttachEngine3D
  AttachmentOffset = pos=(-21.1,18.635,0.305) rot=(0,1,0;0.785398rad)
  BaseFeature = -> Fillet257
  Height = 0.375
  Length = 0.2
  MapMode = 5
  Placement = pos=(-21.1,18.635,0.305) rot=(0,1,0;0.785398rad)
  Support = -> [XY_Plane093]
  Width = 0.23
FEATURE [PartDesign::SubtractiveCylinder] Cylinder169
  Angle = 360
  AttacherType = Attacher::AttachEngine3D
  AttachmentOffset = pos=(-21.055,18.935,0.52) rot=(1,0,0;1.5708rad)
  BaseFeature = -> Box829
  Height = 0.375
  MapMode = 5
  Placement = pos=(-21.055,18.935,0.52) rot=(1,0,0;1.5708rad)
  Radius = 0.205
  Support = -> [XY_Plane093]
FEATURE [PartDesign::SubtractiveBox] Box846
  AttacherType = Attacher::AttachEngine3D
  AttachmentOffset = pos=(-20.95,18.635,0.53) rot=(0,0,1;0rad)
  BaseFeature = -> Cylinder169
  Height = 0.5
  Length = 0.1
  MapMode = 5
  Placement = pos=(-20.95,18.635,0.53) rot=(0,0,1;0rad)
  Support = -> [XY_Plane093]
  Width = 0.23
FEATURE [PartDesign::SubtractiveBox] Box841
  AttacherType = Attacher::AttachEngine3D
  AttachmentOffset = pos=(-21.15,18.635,0.297) rot=(0,-1,0;0.174533rad)
  BaseFeature = -> Box846
  Height = 0.115
  Length = 0.115
  MapMode = 5
  Placement = pos=(-21.15,18.635,0.297) rot=(0,-1,0;0.174533rad)
  Support = -> [XY_Plane093]
  Width = 0.23
FEATURE [PartDesign::Fillet] Fillet256
  Base = -> Box841 [Edge28]
  BaseFeature = -> Box841
  Placement = pos=(-21.15,18.635,0.297) rot=(0,-1,0;0.174533rad)
  Radius = 0.375
  SupportTransform = false
FEATURE [PartDesign::AdditiveBox] Box836
  AttacherType = Attacher::AttachEngine3D
  AttachmentOffset = pos=(-20.7,18.635,1.55) rot=(0,1,0;0.785398rad)
  BaseFeature = -> Fillet256
  Height = 0.375
  Length = 0.23
  MapMode = 5
  Placement = pos=(-20.7,18.635,1.55) rot=(0,1,0;0.785398rad)
  Support = -> [XY_Plane093]
  Width = 0.23
FEATURE [PartDesign::SubtractiveCylinder] Cylinder170
  Angle = 360
  AttacherType = Attacher::AttachEngine3D
  AttachmentOffset = pos=(-20.271,18.635,1.4056) rot=(-1,0,0;1.5708rad)
  BaseFeature = -> Box836
  Height = 0.23
  MapMode = 5
  Placement = pos=(-20.271,18.635,1.4056) rot=(-1,0,0;1.5708rad)
  Radius = 0.23
  Support = -> [XY_Plane093]
FEATURE [PartDesign::AdditiveBox] Box844
  AttacherType = Attacher::AttachEngine3D
  AttachmentOffset = pos=(-20.1,18.635,1.635) rot=(0,0,1;0rad)
  BaseFeature = -> Cylinder170
  Height = 0.265
  Length = 0.23
  MapMode = 5
  Placement = pos=(-20.1,18.635,1.635) rot=(0,0,1;0rad)
  Support = -> [XY_Plane093]
  Width = 0.23
FEATURE [PartDesign::Body] Body087  label="pin087"
  Group = -> [Box837,Box840,Box825,Box850,Box845,Fillet255,Fillet257,Box829,Cylinder169,Box846,Box841,Fillet256,Box836,Cylinder170,Box844]
  Origin = -> Origin092
  Placement = pos=(0,-5,0) rot=(0,0,1;0rad)
  Tip = -> Box844
FEATURE [PartDesign::Fillet] Fillet258
  Base = -> Fillet246 [Edge33]
  BaseFeature = -> Fillet246
  Placement = pos=(-21.5005,18.625,0.235) rot=(0,-1,0;0.174533rad)
  Radius = 0.5
  SupportTransform = false
FEATURE [PartDesign::AdditiveBox] Box862
  AttacherType = Attacher::AttachEngine3D
  AttachmentOffset = pos=(-21.1,18.635,0.305) rot=(0,1,0;0.785398rad)
  BaseFeature = -> Fillet258
  Height = 0.375
  Length = 0.2
  MapMode = 5
  Placement = pos=(-21.1,18.635,0.305) rot=(0,1,0;0.785398rad)
  Support = -> [XY_Plane092]
  Width = 0.23
FEATURE [PartDesign::SubtractiveCylinder] Cylinder156
  Angle = 360
  AttacherType = Attacher::AttachEngine3D
  AttachmentOffset = pos=(-21.055,18.935,0.52) rot=(1,0,0;1.5708rad)
  BaseFeature = -> Box862
  Height = 0.375
  MapMode = 5
  Placement = pos=(-21.055,18.935,0.52) rot=(1,0,0;1.5708rad)
  Radius = 0.205
  Support = -> [XY_Plane092]
FEATURE [PartDesign::SubtractiveBox] Box774
  AttacherType = Attacher::AttachEngine3D
  AttachmentOffset = pos=(-20.95,18.635,0.53) rot=(0,0,1;0rad)
  BaseFeature = -> Cylinder156
  Height = 0.5
  Length = 0.1
  MapMode = 5
  Placement = pos=(-20.95,18.635,0.53) rot=(0,0,1;0rad)
  Support = -> [XY_Plane092]
  Width = 0.23
FEATURE [PartDesign::SubtractiveBox] Box771
  AttacherType = Attacher::AttachEngine3D
  AttachmentOffset = pos=(-21.15,18.635,0.297) rot=(0,-1,0;0.174533rad)
  BaseFeature = -> Box774
  Height = 0.115
  Length = 0.115
  MapMode = 5
  Placement = pos=(-21.15,18.635,0.297) rot=(0,-1,0;0.174533rad)
  Support = -> [XY_Plane092]
  Width = 0.23
FEATURE [PartDesign::Fillet] Fillet259
  Base = -> Box771 [Edge28]
  BaseFeature = -> Box771
  Placement = pos=(-21.15,18.635,0.297) rot=(0,-1,0;0.174533rad)
  Radius = 0.375
  SupportTransform = false
FEATURE [PartDesign::AdditiveBox] Box770
  AttacherType = Attacher::AttachEngine3D
  AttachmentOffset = pos=(-20.7,18.635,1.55) rot=(0,1,0;0.785398rad)
  BaseFeature = -> Fillet259
  Height = 0.375
  Length = 0.23
  MapMode = 5
  Placement = pos=(-20.7,18.635,1.55) rot=(0,1,0;0.785398rad)
  Support = -> [XY_Plane092]
  Width = 0.23
FEATURE [PartDesign::SubtractiveCylinder] Cylinder157
  Angle = 360
  AttacherType = Attacher::AttachEngine3D
  AttachmentOffset = pos=(-20.271,18.635,1.4056) rot=(-1,0,0;1.5708rad)
  BaseFeature = -> Box770
  Height = 0.23
  MapMode = 5
  Placement = pos=(-20.271,18.635,1.4056) rot=(-1,0,0;1.5708rad)
  Radius = 0.23
  Support = -> [XY_Plane092]
FEATURE [PartDesign::AdditiveBox] Box761
  AttacherType = Attacher::AttachEngine3D
  AttachmentOffset = pos=(-20.1,18.635,1.635) rot=(0,0,1;0rad)
  BaseFeature = -> Cylinder157
  Height = 0.265
  Length = 0.23
  MapMode = 5
  Placement = pos=(-20.1,18.635,1.635) rot=(0,0,1;0rad)
  Support = -> [XY_Plane092]
  Width = 0.23
FEATURE [PartDesign::Body] Body085  label="pin085"
  Group = -> [Box772,Box767,Box853,Box764,Box763,Fillet246,Fillet258,Box862,Cylinder156,Box774,Box771,Fillet259,Box770,Cylinder157,Box761]
  Origin = -> Origin088
  Placement = pos=(0,-4,0) rot=(0,0,1;0rad)
  Tip = -> Box761
FEATURE [PartDesign::Fillet] Fillet260
  Base = -> Box773 [Edge2]
  BaseFeature = -> Box773
  Placement = pos=(-21.5005,18.625,0.235) rot=(0,-1,0;0.174533rad)
  Radius = 0.05
  SupportTransform = false
FEATURE [PartDesign::Fillet] Fillet248
  Base = -> Fillet260 [Edge33]
  BaseFeature = -> Fillet260
  Placement = pos=(-21.5005,18.625,0.235) rot=(0,-1,0;0.174533rad)
  Radius = 0.5
  SupportTransform = false
FEATURE [PartDesign::AdditiveBox] Box834
  AttacherType = Attacher::AttachEngine3D
  AttachmentOffset = pos=(-21.1,18.635,0.305) rot=(0,1,0;0.785398rad)
  BaseFeature = -> Fillet248
  Height = 0.375
  Length = 0.2
  MapMode = 5
  Placement = pos=(-21.1,18.635,0.305) rot=(0,1,0;0.785398rad)
  Support = -> [XY_Plane091]
  Width = 0.23
FEATURE [PartDesign::SubtractiveCylinder] Cylinder174
  Angle = 360
  AttacherType = Attacher::AttachEngine3D
  AttachmentOffset = pos=(-21.055,18.935,0.52) rot=(1,0,0;1.5708rad)
  BaseFeature = -> Box834
  Height = 0.375
  MapMode = 5
  Placement = pos=(-21.055,18.935,0.52) rot=(1,0,0;1.5708rad)
  Radius = 0.205
  Support = -> [XY_Plane091]
FEATURE [PartDesign::SubtractiveBox] Box857
  AttacherType = Attacher::AttachEngine3D
  AttachmentOffset = pos=(-20.95,18.635,0.53) rot=(0,0,1;0rad)
  BaseFeature = -> Cylinder174
  Height = 0.5
  Length = 0.1
  MapMode = 5
  Placement = pos=(-20.95,18.635,0.53) rot=(0,0,1;0rad)
  Support = -> [XY_Plane091]
  Width = 0.23
FEATURE [PartDesign::SubtractiveBox] Box858
  AttacherType = Attacher::AttachEngine3D
  AttachmentOffset = pos=(-21.15,18.635,0.297) rot=(0,-1,0;0.174533rad)
  BaseFeature = -> Box857
  Height = 0.115
  Length = 0.115
  MapMode = 5
  Placement = pos=(-21.15,18.635,0.297) rot=(0,-1,0;0.174533rad)
  Support = -> [XY_Plane091]
  Width = 0.23
FEATURE [PartDesign::Fillet] Fillet262
  Base = -> Box858 [Edge28]
  BaseFeature = -> Box858
  Placement = pos=(-21.15,18.635,0.297) rot=(0,-1,0;0.174533rad)
  Radius = 0.375
  SupportTransform = false
FEATURE [PartDesign::AdditiveBox] Box865
  AttacherType = Attacher::AttachEngine3D
  AttachmentOffset = pos=(-20.7,18.635,1.55) rot=(0,1,0;0.785398rad)
  BaseFeature = -> Fillet262
  Height = 0.375
  Length = 0.23
  MapMode = 5
  Placement = pos=(-20.7,18.635,1.55) rot=(0,1,0;0.785398rad)
  Support = -> [XY_Plane091]
  Width = 0.23
FEATURE [PartDesign::SubtractiveCylinder] Cylinder175
  Angle = 360
  AttacherType = Attacher::AttachEngine3D
  AttachmentOffset = pos=(-20.271,18.635,1.4056) rot=(-1,0,0;1.5708rad)
  BaseFeature = -> Box865
  Height = 0.23
  MapMode = 5
  Placement = pos=(-20.271,18.635,1.4056) rot=(-1,0,0;1.5708rad)
  Radius = 0.23
  Support = -> [XY_Plane091]
FEATURE [PartDesign::AdditiveBox] Box869
  AttacherType = Attacher::AttachEngine3D
  AttachmentOffset = pos=(-20.1,18.635,1.635) rot=(0,0,1;0rad)
  BaseFeature = -> Cylinder175
  Height = 0.265
  Length = 0.23
  MapMode = 5
  Placement = pos=(-20.1,18.635,1.635) rot=(0,0,1;0rad)
  Support = -> [XY_Plane091]
  Width = 0.23
FEATURE [PartDesign::Body] Body083  label="pin083"
  Group = -> [Box776,Box777,Box859,Box867,Box773,Fillet260,Fillet248,Box834,Cylinder174,Box857,Box858,Fillet262,Box865,Cylinder175,Box869]
  Origin = -> Origin089
  Placement = pos=(0,-3,0) rot=(0,0,1;0rad)
  Tip = -> Box869
FEATURE [PartDesign::Fillet] Fillet263
  Base = -> Fillet249 [Edge33]
  BaseFeature = -> Fillet249
  Placement = pos=(-21.5005,18.625,0.235) rot=(0,-1,0;0.174533rad)
  Radius = 0.5
  SupportTransform = false
FEATURE [PartDesign::AdditiveBox] Box842
  AttacherType = Attacher::AttachEngine3D
  AttachmentOffset = pos=(-21.1,18.635,0.305) rot=(0,1,0;0.785398rad)
  BaseFeature = -> Fillet263
  Height = 0.375
  Length = 0.2
  MapMode = 5
  Placement = pos=(-21.1,18.635,0.305) rot=(0,1,0;0.785398rad)
  Support = -> [XY_Plane089]
  Width = 0.23
FEATURE [PartDesign::SubtractiveCylinder] Cylinder173
  Angle = 360
  AttacherType = Attacher::AttachEngine3D
  AttachmentOffset = pos=(-21.055,18.935,0.52) rot=(1,0,0;1.5708rad)
  BaseFeature = -> Box842
  Height = 0.375
  MapMode = 5
  Placement = pos=(-21.055,18.935,0.52) rot=(1,0,0;1.5708rad)
  Radius = 0.205
  Support = -> [XY_Plane089]
FEATURE [PartDesign::SubtractiveBox] Box849
  AttacherType = Attacher::AttachEngine3D
  AttachmentOffset = pos=(-20.95,18.635,0.53) rot=(0,0,1;0rad)
  BaseFeature = -> Cylinder173
  Height = 0.5
  Length = 0.1
  MapMode = 5
  Placement = pos=(-20.95,18.635,0.53) rot=(0,0,1;0rad)
  Support = -> [XY_Plane089]
  Width = 0.23
FEATURE [PartDesign::SubtractiveBox] Box852
  AttacherType = Attacher::AttachEngine3D
  AttachmentOffset = pos=(-21.15,18.635,0.297) rot=(0,-1,0;0.174533rad)
  BaseFeature = -> Box849
  Height = 0.115
  Length = 0.115
  MapMode = 5
  Placement = pos=(-21.15,18.635,0.297) rot=(0,-1,0;0.174533rad)
  Support = -> [XY_Plane089]
  Width = 0.23
FEATURE [PartDesign::Fillet] Fillet245
  Base = -> Box852 [Edge28]
  BaseFeature = -> Box852
  Placement = pos=(-21.15,18.635,0.297) rot=(0,-1,0;0.174533rad)
  Radius = 0.375
  SupportTransform = false
FEATURE [PartDesign::AdditiveBox] Box851
  AttacherType = Attacher::AttachEngine3D
  AttachmentOffset = pos=(-20.7,18.635,1.55) rot=(0,1,0;0.785398rad)
  BaseFeature = -> Fillet245
  Height = 0.375
  Length = 0.23
  MapMode = 5
  Placement = pos=(-20.7,18.635,1.55) rot=(0,1,0;0.785398rad)
  Support = -> [XY_Plane089]
  Width = 0.23
FEATURE [PartDesign::SubtractiveCylinder] Cylinder172
  Angle = 360
  AttacherType = Attacher::AttachEngine3D
  AttachmentOffset = pos=(-20.271,18.635,1.4056) rot=(-1,0,0;1.5708rad)
  BaseFeature = -> Box851
  Height = 0.23
  MapMode = 5
  Placement = pos=(-20.271,18.635,1.4056) rot=(-1,0,0;1.5708rad)
  Radius = 0.23
  Support = -> [XY_Plane089]
FEATURE [PartDesign::AdditiveBox] Box838
  AttacherType = Attacher::AttachEngine3D
  AttachmentOffset = pos=(-20.1,18.635,1.635) rot=(0,0,1;0rad)
  BaseFeature = -> Cylinder172
  Height = 0.265
  Length = 0.23
  MapMode = 5
  Placement = pos=(-20.1,18.635,1.635) rot=(0,0,1;0rad)
  Support = -> [XY_Plane089]
  Width = 0.23
FEATURE [PartDesign::Body] Body088  label="pin088"
  Group = -> [Box860,Box855,Box824,Box839,Box843,Fillet249,Fillet263,Box842,Cylinder173,Box849,Box852,Fillet245,Box851,Cylinder172,Box838]
  Origin = -> Origin098
  Placement = pos=(0,-5.5,0) rot=(0,0,1;0rad)
  Tip = -> Box838
FEATURE [PartDesign::Fillet] Fillet264
  Base = -> Box861 [Edge2]
  BaseFeature = -> Box861
  Placement = pos=(-21.5005,18.625,0.235) rot=(0,-1,0;0.174533rad)
  Radius = 0.05
  SupportTransform = false
FEATURE [PartDesign::Fillet] Fillet247
  Base = -> Fillet264 [Edge33]
  BaseFeature = -> Fillet264
  Placement = pos=(-21.5005,18.625,0.235) rot=(0,-1,0;0.174533rad)
  Radius = 0.5
  SupportTransform = false
FEATURE [PartDesign::AdditiveBox] Box828
  AttacherType = Attacher::AttachEngine3D
  AttachmentOffset = pos=(-21.1,18.635,0.305) rot=(0,1,0;0.785398rad)
  BaseFeature = -> Fillet247
  Height = 0.375
  Length = 0.2
  MapMode = 5
  Placement = pos=(-21.1,18.635,0.305) rot=(0,1,0;0.785398rad)
  Support = -> [XY_Plane094]
  Width = 0.23
FEATURE [PartDesign::SubtractiveCylinder] Cylinder167
  Angle = 360
  AttacherType = Attacher::AttachEngine3D
  AttachmentOffset = pos=(-21.055,18.935,0.52) rot=(1,0,0;1.5708rad)
  BaseFeature = -> Box828
  Height = 0.375
  MapMode = 5
  Placement = pos=(-21.055,18.935,0.52) rot=(1,0,0;1.5708rad)
  Radius = 0.205
  Support = -> [XY_Plane094]
FEATURE [PartDesign::SubtractiveBox] Box830
  AttacherType = Attacher::AttachEngine3D
  AttachmentOffset = pos=(-20.95,18.635,0.53) rot=(0,0,1;0rad)
  BaseFeature = -> Cylinder167
  Height = 0.5
  Length = 0.1
  MapMode = 5
  Placement = pos=(-20.95,18.635,0.53) rot=(0,0,1;0rad)
  Support = -> [XY_Plane094]
  Width = 0.23
FEATURE [PartDesign::SubtractiveBox] Box827
  AttacherType = Attacher::AttachEngine3D
  AttachmentOffset = pos=(-21.15,18.635,0.297) rot=(0,-1,0;0.174533rad)
  BaseFeature = -> Box830
  Height = 0.115
  Length = 0.115
  MapMode = 5
  Placement = pos=(-21.15,18.635,0.297) rot=(0,-1,0;0.174533rad)
  Support = -> [XY_Plane094]
  Width = 0.23
FEATURE [PartDesign::Fillet] Fillet261
  Base = -> Box827 [Edge28]
  BaseFeature = -> Box827
  Placement = pos=(-21.15,18.635,0.297) rot=(0,-1,0;0.174533rad)
  Radius = 0.375
  SupportTransform = false
FEATURE [PartDesign::AdditiveBox] Box833
  AttacherType = Attacher::AttachEngine3D
  AttachmentOffset = pos=(-20.7,18.635,1.55) rot=(0,1,0;0.785398rad)
  BaseFeature = -> Fillet261
  Height = 0.375
  Length = 0.23
  MapMode = 5
  Placement = pos=(-20.7,18.635,1.55) rot=(0,1,0;0.785398rad)
  Support = -> [XY_Plane094]
  Width = 0.23
FEATURE [PartDesign::SubtractiveCylinder] Cylinder168
  Angle = 360
  AttacherType = Attacher::AttachEngine3D
  AttachmentOffset = pos=(-20.271,18.635,1.4056) rot=(-1,0,0;1.5708rad)
  BaseFeature = -> Box833
  Height = 0.23
  MapMode = 5
  Placement = pos=(-20.271,18.635,1.4056) rot=(-1,0,0;1.5708rad)
  Radius = 0.23
  Support = -> [XY_Plane094]
FEATURE [PartDesign::AdditiveBox] Box823
  AttacherType = Attacher::AttachEngine3D
  AttachmentOffset = pos=(-20.1,18.635,1.635) rot=(0,0,1;0rad)
  BaseFeature = -> Cylinder168
  Height = 0.265
  Length = 0.23
  MapMode = 5
  Placement = pos=(-20.1,18.635,1.635) rot=(0,0,1;0rad)
  Support = -> [XY_Plane094]
  Width = 0.23
FEATURE [PartDesign::Body] Body086  label="pin086"
  Group = -> [Box856,Box854,Box832,Box835,Box861,Fillet264,Fillet247,Box828,Cylinder167,Box830,Box827,Fillet261,Box833,Cylinder168,Box823]
  Origin = -> Origin084
  Placement = pos=(0,-4.5,0) rot=(0,0,1;0rad)
  Tip = -> Box823
FEATURE [PartDesign::AdditiveBox] Box904
  AttacherType = Attacher::AttachEngine3D
  AttachmentOffset = pos=(-21.3,18.635,0) rot=(0,0,1;0rad)
  Height = 1.9
  Length = 1.3
  MapMode = 5
  Placement = pos=(-21.3,18.635,0) rot=(0,0,1;0rad)
  Support = -> [XY_Plane102]
  Width = 0.23
FEATURE [PartDesign::SubtractiveBox] Box900
  AttacherType = Attacher::AttachEngine3D
  AttachmentOffset = pos=(-21.35,18.635,0.35) rot=(0,0,1;0rad)
  BaseFeature = -> Box904
  Height = 1.55
  Length = 0.5
  MapMode = 5
  Placement = pos=(-21.35,18.635,0.35) rot=(0,0,1;0rad)
  Support = -> [XY_Plane102]
  Width = 0.23
FEATURE [PartDesign::AdditiveBox] Box918
  AttacherType = Attacher::AttachEngine3D
  AttachmentOffset = pos=(-21.3,18.635,0) rot=(0,0,1;0rad)
  Height = 1.9
  Length = 1.3
  MapMode = 5
  Placement = pos=(-21.3,18.635,0) rot=(0,0,1;0rad)
  Support = -> [XY_Plane100]
  Width = 0.23
FEATURE [PartDesign::SubtractiveBox] Box909
  AttacherType = Attacher::AttachEngine3D
  AttachmentOffset = pos=(-21.35,18.635,0.35) rot=(0,0,1;0rad)
  BaseFeature = -> Box918
  Height = 1.55
  Length = 0.5
  MapMode = 5
  Placement = pos=(-21.35,18.635,0.35) rot=(0,0,1;0rad)
  Support = -> [XY_Plane100]
  Width = 0.23
FEATURE [PartDesign::AdditiveBox] Box924
  AttacherType = Attacher::AttachEngine3D
  AttachmentOffset = pos=(-21.3,18.635,0) rot=(0,0,1;0rad)
  Height = 1.9
  Length = 1.3
  MapMode = 5
  Placement = pos=(-21.3,18.635,0) rot=(0,0,1;0rad)
  Support = -> [XY_Plane097]
  Width = 0.23
FEATURE [PartDesign::SubtractiveBox] Box915
  AttacherType = Attacher::AttachEngine3D
  AttachmentOffset = pos=(-21.35,18.635,0.35) rot=(0,0,1;0rad)
  BaseFeature = -> Box924
  Height = 1.55
  Length = 0.5
  MapMode = 5
  Placement = pos=(-21.35,18.635,0.35) rot=(0,0,1;0rad)
  Support = -> [XY_Plane097]
  Width = 0.23
FEATURE [PartDesign::AdditiveBox] Box932
  AttacherType = Attacher::AttachEngine3D
  AttachmentOffset = pos=(-21.3,18.635,0) rot=(0,0,1;0rad)
  Height = 1.9
  Length = 1.3
  MapMode = 5
  Placement = pos=(-21.3,18.635,0) rot=(0,0,1;0rad)
  Support = -> [XY_Plane106]
  Width = 0.23
FEATURE [PartDesign::SubtractiveBox] Box929
  AttacherType = Attacher::AttachEngine3D
  AttachmentOffset = pos=(-21.35,18.635,0.35) rot=(0,0,1;0rad)
  BaseFeature = -> Box932
  Height = 1.55
  Length = 0.5
  MapMode = 5
  Placement = pos=(-21.35,18.635,0.35) rot=(0,0,1;0rad)
  Support = -> [XY_Plane106]
  Width = 0.23
FEATURE [PartDesign::SubtractiveBox] Box919
  AttacherType = Attacher::AttachEngine3D
  AttachmentOffset = pos=(-20.5,18.63,0) rot=(0,0,1;0rad)
  BaseFeature = -> Box929
  Height = 1.635
  Length = 0.5
  MapMode = 5
  Placement = pos=(-20.5,18.63,0) rot=(0,0,1;0rad)
  Support = -> [XY_Plane106]
  Width = 0.25
FEATURE [PartDesign::SubtractiveBox] Box933
  AttacherType = Attacher::AttachEngine3D
  AttachmentOffset = pos=(-21.19,18.635,-0.12) rot=(0,-1,0;0.15708rad)
  BaseFeature = -> Box919
  Height = 0.12
  Length = 0.725
  MapMode = 5
  Placement = pos=(-21.19,18.635,-0.12) rot=(0,-1,0;0.15708rad)
  Support = -> [XY_Plane106]
  Width = 0.25
FEATURE [PartDesign::SubtractiveBox] Box937
  AttacherType = Attacher::AttachEngine3D
  AttachmentOffset = pos=(-20.5,18.63,0) rot=(0,0,1;0rad)
  BaseFeature = -> Box784
  Height = 1.635
  Length = 0.5
  MapMode = 5
  Placement = pos=(-20.5,18.63,0) rot=(0,0,1;0rad)
  Support = -> [XY_Plane104]
  Width = 0.25
FEATURE [PartDesign::SubtractiveBox] Box782
  AttacherType = Attacher::AttachEngine3D
  AttachmentOffset = pos=(-21.19,18.635,-0.12) rot=(0,-1,0;0.15708rad)
  BaseFeature = -> Box937
  Height = 0.12
  Length = 0.725
  MapMode = 5
  Placement = pos=(-21.19,18.635,-0.12) rot=(0,-1,0;0.15708rad)
  Support = -> [XY_Plane104]
  Width = 0.25
FEATURE [PartDesign::SubtractiveBox] Box781
  AttacherType = Attacher::AttachEngine3D
  AttachmentOffset = pos=(-21.5005,18.625,0.235) rot=(0,-1,0;0.174533rad)
  BaseFeature = -> Box782
  Height = 0.3
  Length = 0.6605
  MapMode = 5
  Placement = pos=(-21.5005,18.625,0.235) rot=(0,-1,0;0.174533rad)
  Support = -> [XY_Plane104]
  Width = 0.25
FEATURE [PartDesign::SubtractiveBox] Box940
  AttacherType = Attacher::AttachEngine3D
  AttachmentOffset = pos=(-21.5005,18.625,0.235) rot=(0,-1,0;0.174533rad)
  BaseFeature = -> Box933
  Height = 0.3
  Length = 0.6605
  MapMode = 5
  Placement = pos=(-21.5005,18.625,0.235) rot=(0,-1,0;0.174533rad)
  Support = -> [XY_Plane106]
  Width = 0.25
FEATURE [PartDesign::AdditiveBox] Box947
  AttacherType = Attacher::AttachEngine3D
  AttachmentOffset = pos=(-21.3,18.635,0) rot=(0,0,1;0rad)
  Height = 1.9
  Length = 1.3
  MapMode = 5
  Placement = pos=(-21.3,18.635,0) rot=(0,0,1;0rad)
  Support = -> [XY_Plane108]
  Width = 0.23
FEATURE [PartDesign::SubtractiveBox] Box935
  AttacherType = Attacher::AttachEngine3D
  AttachmentOffset = pos=(-21.35,18.635,0.35) rot=(0,0,1;0rad)
  BaseFeature = -> Box947
  Height = 1.55
  Length = 0.5
  MapMode = 5
  Placement = pos=(-21.35,18.635,0.35) rot=(0,0,1;0rad)
  Support = -> [XY_Plane108]
  Width = 0.23
FEATURE [PartDesign::SubtractiveBox] Box923
  AttacherType = Attacher::AttachEngine3D
  AttachmentOffset = pos=(-20.5,18.63,0) rot=(0,0,1;0rad)
  BaseFeature = -> Box935
  Height = 1.635
  Length = 0.5
  MapMode = 5
  Placement = pos=(-20.5,18.63,0) rot=(0,0,1;0rad)
  Support = -> [XY_Plane108]
  Width = 0.25
FEATURE [PartDesign::SubtractiveBox] Box914
  AttacherType = Attacher::AttachEngine3D
  AttachmentOffset = pos=(-21.19,18.635,-0.12) rot=(0,-1,0;0.15708rad)
  BaseFeature = -> Box923
  Height = 0.12
  Length = 0.725
  MapMode = 5
  Placement = pos=(-21.19,18.635,-0.12) rot=(0,-1,0;0.15708rad)
  Support = -> [XY_Plane108]
  Width = 0.25
FEATURE [PartDesign::SubtractiveBox] Box949
  AttacherType = Attacher::AttachEngine3D
  AttachmentOffset = pos=(-20.5,18.63,0) rot=(0,0,1;0rad)
  BaseFeature = -> Box792
  Height = 1.635
  Length = 0.5
  MapMode = 5
  Placement = pos=(-20.5,18.63,0) rot=(0,0,1;0rad)
  Support = -> [XY_Plane107]
  Width = 0.25
FEATURE [PartDesign::AdditiveBox] Box951
  AttacherType = Attacher::AttachEngine3D
  AttachmentOffset = pos=(-21.3,18.635,0) rot=(0,0,1;0rad)
  Height = 1.9
  Length = 1.3
  MapMode = 5
  Placement = pos=(-21.3,18.635,0) rot=(0,0,1;0rad)
  Support = -> [XY_Plane090]
  Width = 0.23
FEATURE [PartDesign::SubtractiveBox] Box946
  AttacherType = Attacher::AttachEngine3D
  AttachmentOffset = pos=(-21.35,18.635,0.35) rot=(0,0,1;0rad)
  BaseFeature = -> Box951
  Height = 1.55
  Length = 0.5
  MapMode = 5
  Placement = pos=(-21.35,18.635,0.35) rot=(0,0,1;0rad)
  Support = -> [XY_Plane090]
  Width = 0.23
FEATURE [PartDesign::SubtractiveBox] Box917
  AttacherType = Attacher::AttachEngine3D
  AttachmentOffset = pos=(-20.5,18.63,0) rot=(0,0,1;0rad)
  BaseFeature = -> Box946
  Height = 1.635
  Length = 0.5
  MapMode = 5
  Placement = pos=(-20.5,18.63,0) rot=(0,0,1;0rad)
  Support = -> [XY_Plane090]
  Width = 0.25
FEATURE [PartDesign::SubtractiveBox] Box927
  AttacherType = Attacher::AttachEngine3D
  AttachmentOffset = pos=(-21.19,18.635,-0.12) rot=(0,-1,0;0.15708rad)
  BaseFeature = -> Box917
  Height = 0.12
  Length = 0.725
  MapMode = 5
  Placement = pos=(-21.19,18.635,-0.12) rot=(0,-1,0;0.15708rad)
  Support = -> [XY_Plane090]
  Width = 0.25
FEATURE [PartDesign::SubtractiveBox] Box928
  AttacherType = Attacher::AttachEngine3D
  AttachmentOffset = pos=(-21.5005,18.625,0.235) rot=(0,-1,0;0.174533rad)
  BaseFeature = -> Box927
  Height = 0.3
  Length = 0.6605
  MapMode = 5
  Placement = pos=(-21.5005,18.625,0.235) rot=(0,-1,0;0.174533rad)
  Support = -> [XY_Plane090]
  Width = 0.25
FEATURE [PartDesign::SubtractiveBox] Box954
  AttacherType = Attacher::AttachEngine3D
  AttachmentOffset = pos=(-20.5,18.63,0) rot=(0,0,1;0rad)
  BaseFeature = -> Box788
  Height = 1.635
  Length = 0.5
  MapMode = 5
  Placement = pos=(-20.5,18.63,0) rot=(0,0,1;0rad)
  Support = -> [XY_Plane109]
  Width = 0.25
FEATURE [PartDesign::SubtractiveBox] Box789
  AttacherType = Attacher::AttachEngine3D
  AttachmentOffset = pos=(-21.19,18.635,-0.12) rot=(0,-1,0;0.15708rad)
  BaseFeature = -> Box954
  Height = 0.12
  Length = 0.725
  MapMode = 5
  Placement = pos=(-21.19,18.635,-0.12) rot=(0,-1,0;0.15708rad)
  Support = -> [XY_Plane109]
  Width = 0.25
FEATURE [PartDesign::SubtractiveBox] Box778
  AttacherType = Attacher::AttachEngine3D
  AttachmentOffset = pos=(-21.5005,18.625,0.235) rot=(0,-1,0;0.174533rad)
  BaseFeature = -> Box789
  Height = 0.3
  Length = 0.6605
  MapMode = 5
  Placement = pos=(-21.5005,18.625,0.235) rot=(0,-1,0;0.174533rad)
  Support = -> [XY_Plane109]
  Width = 0.25
FEATURE [PartDesign::SubtractiveBox] Box955
  AttacherType = Attacher::AttachEngine3D
  AttachmentOffset = pos=(-21.19,18.635,-0.12) rot=(0,-1,0;0.15708rad)
  BaseFeature = -> Box949
  Height = 0.12
  Length = 0.725
  MapMode = 5
  Placement = pos=(-21.19,18.635,-0.12) rot=(0,-1,0;0.15708rad)
  Support = -> [XY_Plane107]
  Width = 0.25
FEATURE [PartDesign::SubtractiveBox] Box790
  AttacherType = Attacher::AttachEngine3D
  AttachmentOffset = pos=(-21.5005,18.625,0.235) rot=(0,-1,0;0.174533rad)
  BaseFeature = -> Box955
  Height = 0.3
  Length = 0.6605
  MapMode = 5
  Placement = pos=(-21.5005,18.625,0.235) rot=(0,-1,0;0.174533rad)
  Support = -> [XY_Plane107]
  Width = 0.25
FEATURE [PartDesign::SubtractiveBox] Box956
  AttacherType = Attacher::AttachEngine3D
  AttachmentOffset = pos=(-21.5005,18.625,0.235) rot=(0,-1,0;0.174533rad)
  BaseFeature = -> Box914
  Height = 0.3
  Length = 0.6605
  MapMode = 5
  Placement = pos=(-21.5005,18.625,0.235) rot=(0,-1,0;0.174533rad)
  Support = -> [XY_Plane108]
  Width = 0.25
FEATURE [PartDesign::AdditiveBox] Box976
  AttacherType = Attacher::AttachEngine3D
  AttachmentOffset = pos=(-21.3,18.635,0) rot=(0,0,1;0rad)
  Height = 1.9
  Length = 1.3
  MapMode = 5
  Placement = pos=(-21.3,18.635,0) rot=(0,0,1;0rad)
  Support = -> [XY_Plane105]
  Width = 0.23
FEATURE [PartDesign::SubtractiveBox] Box966
  AttacherType = Attacher::AttachEngine3D
  AttachmentOffset = pos=(-21.35,18.635,0.35) rot=(0,0,1;0rad)
  BaseFeature = -> Box976
  Height = 1.55
  Length = 0.5
  MapMode = 5
  Placement = pos=(-21.35,18.635,0.35) rot=(0,0,1;0rad)
  Support = -> [XY_Plane105]
  Width = 0.23
FEATURE [PartDesign::SubtractiveBox] Box968
  AttacherType = Attacher::AttachEngine3D
  AttachmentOffset = pos=(-20.5,18.63,0) rot=(0,0,1;0rad)
  BaseFeature = -> Box966
  Height = 1.635
  Length = 0.5
  MapMode = 5
  Placement = pos=(-20.5,18.63,0) rot=(0,0,1;0rad)
  Support = -> [XY_Plane105]
  Width = 0.25
FEATURE [PartDesign::SubtractiveBox] Box972
  AttacherType = Attacher::AttachEngine3D
  AttachmentOffset = pos=(-21.19,18.635,-0.12) rot=(0,-1,0;0.15708rad)
  BaseFeature = -> Box968
  Height = 0.12
  Length = 0.725
  MapMode = 5
  Placement = pos=(-21.19,18.635,-0.12) rot=(0,-1,0;0.15708rad)
  Support = -> [XY_Plane105]
  Width = 0.25
FEATURE [PartDesign::SubtractiveBox] Box973
  AttacherType = Attacher::AttachEngine3D
  AttachmentOffset = pos=(-21.5005,18.625,0.235) rot=(0,-1,0;0.174533rad)
  BaseFeature = -> Box972
  Height = 0.3
  Length = 0.6605
  MapMode = 5
  Placement = pos=(-21.5005,18.625,0.235) rot=(0,-1,0;0.174533rad)
  Support = -> [XY_Plane105]
  Width = 0.25
FEATURE [PartDesign::AdditiveBox] Box982
  AttacherType = Attacher::AttachEngine3D
  AttachmentOffset = pos=(-21.3,18.635,0) rot=(0,0,1;0rad)
  Height = 1.9
  Length = 1.3
  MapMode = 5
  Placement = pos=(-21.3,18.635,0) rot=(0,0,1;0rad)
  Support = -> [XY_Plane122]
  Width = 0.23
FEATURE [PartDesign::AdditiveBox] Box984
  AttacherType = Attacher::AttachEngine3D
  AttachmentOffset = pos=(-21.3,18.635,0) rot=(0,0,1;0rad)
  Height = 1.9
  Length = 1.3
  MapMode = 5
  Placement = pos=(-21.3,18.635,0) rot=(0,0,1;0rad)
  Support = -> [XY_Plane101]
  Width = 0.23
FEATURE [PartDesign::SubtractiveBox] Box981
  AttacherType = Attacher::AttachEngine3D
  AttachmentOffset = pos=(-21.35,18.635,0.35) rot=(0,0,1;0rad)
  BaseFeature = -> Box984
  Height = 1.55
  Length = 0.5
  MapMode = 5
  Placement = pos=(-21.35,18.635,0.35) rot=(0,0,1;0rad)
  Support = -> [XY_Plane101]
  Width = 0.23
FEATURE [PartDesign::SubtractiveBox] Box965
  AttacherType = Attacher::AttachEngine3D
  AttachmentOffset = pos=(-20.5,18.63,0) rot=(0,0,1;0rad)
  BaseFeature = -> Box981
  Height = 1.635
  Length = 0.5
  MapMode = 5
  Placement = pos=(-20.5,18.63,0) rot=(0,0,1;0rad)
  Support = -> [XY_Plane101]
  Width = 0.25
FEATURE [PartDesign::AdditiveBox] Box986
  AttacherType = Attacher::AttachEngine3D
  AttachmentOffset = pos=(-21.3,18.635,0) rot=(0,0,1;0rad)
  Height = 1.9
  Length = 1.3
  MapMode = 5
  Placement = pos=(-21.3,18.635,0) rot=(0,0,1;0rad)
  Support = -> [XY_Plane103]
  Width = 0.23
FEATURE [PartDesign::SubtractiveBox] Box988
  AttacherType = Attacher::AttachEngine3D
  AttachmentOffset = pos=(-21.19,18.635,-0.12) rot=(0,-1,0;0.15708rad)
  BaseFeature = -> Box965
  Height = 0.12
  Length = 0.725
  MapMode = 5
  Placement = pos=(-21.19,18.635,-0.12) rot=(0,-1,0;0.15708rad)
  Support = -> [XY_Plane101]
  Width = 0.25
FEATURE [PartDesign::SubtractiveBox] Box987
  AttacherType = Attacher::AttachEngine3D
  AttachmentOffset = pos=(-21.5005,18.625,0.235) rot=(0,-1,0;0.174533rad)
  BaseFeature = -> Box988
  Height = 0.3
  Length = 0.6605
  MapMode = 5
  Placement = pos=(-21.5005,18.625,0.235) rot=(0,-1,0;0.174533rad)
  Support = -> [XY_Plane101]
  Width = 0.25
FEATURE [PartDesign::SubtractiveBox] Box989
  AttacherType = Attacher::AttachEngine3D
  AttachmentOffset = pos=(-21.35,18.635,0.35) rot=(0,0,1;0rad)
  BaseFeature = -> Box986
  Height = 1.55
  Length = 0.5
  MapMode = 5
  Placement = pos=(-21.35,18.635,0.35) rot=(0,0,1;0rad)
  Support = -> [XY_Plane103]
  Width = 0.23
FEATURE [PartDesign::SubtractiveBox] Box967
  AttacherType = Attacher::AttachEngine3D
  AttachmentOffset = pos=(-20.5,18.63,0) rot=(0,0,1;0rad)
  BaseFeature = -> Box989
  Height = 1.635
  Length = 0.5
  MapMode = 5
  Placement = pos=(-20.5,18.63,0) rot=(0,0,1;0rad)
  Support = -> [XY_Plane103]
  Width = 0.25
FEATURE [PartDesign::SubtractiveBox] Box962
  AttacherType = Attacher::AttachEngine3D
  AttachmentOffset = pos=(-21.19,18.635,-0.12) rot=(0,-1,0;0.15708rad)
  BaseFeature = -> Box967
  Height = 0.12
  Length = 0.725
  MapMode = 5
  Placement = pos=(-21.19,18.635,-0.12) rot=(0,-1,0;0.15708rad)
  Support = -> [XY_Plane103]
  Width = 0.25
FEATURE [PartDesign::SubtractiveBox] Box985
  AttacherType = Attacher::AttachEngine3D
  AttachmentOffset = pos=(-21.5005,18.625,0.235) rot=(0,-1,0;0.174533rad)
  BaseFeature = -> Box962
  Height = 0.3
  Length = 0.6605
  MapMode = 5
  Placement = pos=(-21.5005,18.625,0.235) rot=(0,-1,0;0.174533rad)
  Support = -> [XY_Plane103]
  Width = 0.25
FEATURE [PartDesign::AdditiveBox] Box991
  AttacherType = Attacher::AttachEngine3D
  AttachmentOffset = pos=(-21.3,18.635,0) rot=(0,0,1;0rad)
  Height = 1.9
  Length = 1.3
  MapMode = 5
  Placement = pos=(-21.3,18.635,0) rot=(0,0,1;0rad)
  Support = -> [XY_Plane120]
  Width = 0.23
FEATURE [PartDesign::Fillet] Fillet268
  Base = -> Box973 [Edge2]
  BaseFeature = -> Box973
  Placement = pos=(-21.5005,18.625,0.235) rot=(0,-1,0;0.174533rad)
  Radius = 0.05
  SupportTransform = false
FEATURE [PartDesign::Fillet] Fillet269
  Base = -> Fillet268 [Edge33]
  BaseFeature = -> Fillet268
  Placement = pos=(-21.5005,18.625,0.235) rot=(0,-1,0;0.174533rad)
  Radius = 0.5
  SupportTransform = false
FEATURE [PartDesign::AdditiveBox] Box959
  AttacherType = Attacher::AttachEngine3D
  AttachmentOffset = pos=(-21.1,18.635,0.305) rot=(0,1,0;0.785398rad)
  BaseFeature = -> Fillet269
  Height = 0.375
  Length = 0.2
  MapMode = 5
  Placement = pos=(-21.1,18.635,0.305) rot=(0,1,0;0.785398rad)
  Support = -> [XY_Plane105]
  Width = 0.23
FEATURE [PartDesign::SubtractiveCylinder] Cylinder196
  Angle = 360
  AttacherType = Attacher::AttachEngine3D
  AttachmentOffset = pos=(-21.055,18.935,0.52) rot=(1,0,0;1.5708rad)
  BaseFeature = -> Box959
  Height = 0.375
  MapMode = 5
  Placement = pos=(-21.055,18.935,0.52) rot=(1,0,0;1.5708rad)
  Radius = 0.205
  Support = -> [XY_Plane105]
FEATURE [PartDesign::SubtractiveBox] Box974
  AttacherType = Attacher::AttachEngine3D
  AttachmentOffset = pos=(-20.95,18.635,0.53) rot=(0,0,1;0rad)
  BaseFeature = -> Cylinder196
  Height = 0.5
  Length = 0.1
  MapMode = 5
  Placement = pos=(-20.95,18.635,0.53) rot=(0,0,1;0rad)
  Support = -> [XY_Plane105]
  Width = 0.23
FEATURE [PartDesign::SubtractiveBox] Box970
  AttacherType = Attacher::AttachEngine3D
  AttachmentOffset = pos=(-21.15,18.635,0.297) rot=(0,-1,0;0.174533rad)
  BaseFeature = -> Box974
  Height = 0.115
  Length = 0.115
  MapMode = 5
  Placement = pos=(-21.15,18.635,0.297) rot=(0,-1,0;0.174533rad)
  Support = -> [XY_Plane105]
  Width = 0.23
FEATURE [PartDesign::Fillet] Fillet270
  Base = -> Box987 [Edge2]
  BaseFeature = -> Box987
  Placement = pos=(-21.5005,18.625,0.235) rot=(0,-1,0;0.174533rad)
  Radius = 0.05
  SupportTransform = false
FEATURE [PartDesign::Fillet] Fillet276
  Base = -> Box970 [Edge28]
  BaseFeature = -> Box970
  Placement = pos=(-21.15,18.635,0.297) rot=(0,-1,0;0.174533rad)
  Radius = 0.375
  SupportTransform = false
FEATURE [PartDesign::AdditiveBox] Box969
  AttacherType = Attacher::AttachEngine3D
  AttachmentOffset = pos=(-20.7,18.635,1.55) rot=(0,1,0;0.785398rad)
  BaseFeature = -> Fillet276
  Height = 0.375
  Length = 0.23
  MapMode = 5
  Placement = pos=(-20.7,18.635,1.55) rot=(0,1,0;0.785398rad)
  Support = -> [XY_Plane105]
  Width = 0.23
FEATURE [PartDesign::SubtractiveCylinder] Cylinder199
  Angle = 360
  AttacherType = Attacher::AttachEngine3D
  AttachmentOffset = pos=(-20.271,18.635,1.4056) rot=(-1,0,0;1.5708rad)
  BaseFeature = -> Box969
  Height = 0.23
  MapMode = 5
  Placement = pos=(-20.271,18.635,1.4056) rot=(-1,0,0;1.5708rad)
  Radius = 0.23
  Support = -> [XY_Plane105]
FEATURE [PartDesign::AdditiveBox] Box975
  AttacherType = Attacher::AttachEngine3D
  AttachmentOffset = pos=(-20.1,18.635,1.635) rot=(0,0,1;0rad)
  BaseFeature = -> Cylinder199
  Height = 0.265
  Length = 0.23
  MapMode = 5
  Placement = pos=(-20.1,18.635,1.635) rot=(0,0,1;0rad)
  Support = -> [XY_Plane105]
  Width = 0.23
FEATURE [PartDesign::Body] Body090  label="pin090"
  Group = -> [Box976,Box966,Box968,Box972,Box973,Fillet268,Fillet269,Box959,Cylinder196,Box974,Box970,Fillet276,Box969,Cylinder199,Box975]
  Origin = -> Origin095
  Placement = pos=(0,-0.5,0) rot=(0,0,1;0rad)
  Tip = -> Box975
FEATURE [PartDesign::Fillet] Fillet277
  Base = -> Fillet270 [Edge33]
  BaseFeature = -> Fillet270
  Placement = pos=(-21.5005,18.625,0.235) rot=(0,-1,0;0.174533rad)
  Radius = 0.5
  SupportTransform = false
FEATURE [PartDesign::AdditiveBox] Box964
  AttacherType = Attacher::AttachEngine3D
  AttachmentOffset = pos=(-21.1,18.635,0.305) rot=(0,1,0;0.785398rad)
  BaseFeature = -> Fillet277
  Height = 0.375
  Length = 0.2
  MapMode = 5
  Placement = pos=(-21.1,18.635,0.305) rot=(0,1,0;0.785398rad)
  Support = -> [XY_Plane101]
  Width = 0.23
FEATURE [PartDesign::SubtractiveCylinder] Cylinder200
  Angle = 360
  AttacherType = Attacher::AttachEngine3D
  AttachmentOffset = pos=(-21.055,18.935,0.52) rot=(1,0,0;1.5708rad)
  BaseFeature = -> Box964
  Height = 0.375
  MapMode = 5
  Placement = pos=(-21.055,18.935,0.52) rot=(1,0,0;1.5708rad)
  Radius = 0.205
  Support = -> [XY_Plane101]
FEATURE [PartDesign::SubtractiveBox] Box980
  AttacherType = Attacher::AttachEngine3D
  AttachmentOffset = pos=(-20.95,18.635,0.53) rot=(0,0,1;0rad)
  BaseFeature = -> Cylinder200
  Height = 0.5
  Length = 0.1
  MapMode = 5
  Placement = pos=(-20.95,18.635,0.53) rot=(0,0,1;0rad)
  Support = -> [XY_Plane101]
  Width = 0.23
FEATURE [PartDesign::SubtractiveBox] Box977
  AttacherType = Attacher::AttachEngine3D
  AttachmentOffset = pos=(-21.15,18.635,0.297) rot=(0,-1,0;0.174533rad)
  BaseFeature = -> Box980
  Height = 0.115
  Length = 0.115
  MapMode = 5
  Placement = pos=(-21.15,18.635,0.297) rot=(0,-1,0;0.174533rad)
  Support = -> [XY_Plane101]
  Width = 0.23
FEATURE [PartDesign::Fillet] Fillet265
  Base = -> Box977 [Edge28]
  BaseFeature = -> Box977
  Placement = pos=(-21.15,18.635,0.297) rot=(0,-1,0;0.174533rad)
  Radius = 0.375
  SupportTransform = false
FEATURE [PartDesign::AdditiveBox] Box979
  AttacherType = Attacher::AttachEngine3D
  AttachmentOffset = pos=(-20.7,18.635,1.55) rot=(0,1,0;0.785398rad)
  BaseFeature = -> Fillet265
  Height = 0.375
  Length = 0.23
  MapMode = 5
  Placement = pos=(-20.7,18.635,1.55) rot=(0,1,0;0.785398rad)
  Support = -> [XY_Plane101]
  Width = 0.23
FEATURE [PartDesign::SubtractiveCylinder] Cylinder201
  Angle = 360
  AttacherType = Attacher::AttachEngine3D
  AttachmentOffset = pos=(-20.271,18.635,1.4056) rot=(-1,0,0;1.5708rad)
  BaseFeature = -> Box979
  Height = 0.23
  MapMode = 5
  Placement = pos=(-20.271,18.635,1.4056) rot=(-1,0,0;1.5708rad)
  Radius = 0.23
  Support = -> [XY_Plane101]
FEATURE [PartDesign::AdditiveBox] Box983
  AttacherType = Attacher::AttachEngine3D
  AttachmentOffset = pos=(-20.1,18.635,1.635) rot=(0,0,1;0rad)
  BaseFeature = -> Cylinder201
  Height = 0.265
  Length = 0.23
  MapMode = 5
  Placement = pos=(-20.1,18.635,1.635) rot=(0,0,1;0rad)
  Support = -> [XY_Plane101]
  Width = 0.23
FEATURE [PartDesign::Body] Body094  label="pin094"
  Group = -> [Box984,Box981,Box965,Box988,Box987,Fillet270,Fillet277,Box964,Cylinder200,Box980,Box977,Fillet265,Box979,Cylinder201,Box983]
  Origin = -> Origin104
  Placement = pos=(0,-1,0) rot=(0,0,1;0rad)
  Tip = -> Box983
FEATURE [PartDesign::Fillet] Fillet278
  Base = -> Box985 [Edge2]
  BaseFeature = -> Box985
  Placement = pos=(-21.5005,18.625,0.235) rot=(0,-1,0;0.174533rad)
  Radius = 0.05
  SupportTransform = false
FEATURE [PartDesign::Fillet] Fillet230
  Base = -> Fillet278 [Edge33]
  BaseFeature = -> Fillet278
  Placement = pos=(-21.5005,18.625,0.235) rot=(0,-1,0;0.174533rad)
  Radius = 0.5
  SupportTransform = false
FEATURE [PartDesign::AdditiveBox] Box793
  AttacherType = Attacher::AttachEngine3D
  AttachmentOffset = pos=(-21.1,18.635,0.305) rot=(0,1,0;0.785398rad)
  BaseFeature = -> Fillet230
  Height = 0.375
  Length = 0.2
  MapMode = 5
  Placement = pos=(-21.1,18.635,0.305) rot=(0,1,0;0.785398rad)
  Support = -> [XY_Plane103]
  Width = 0.23
FEATURE [PartDesign::SubtractiveCylinder] Cylinder191
  Angle = 360
  AttacherType = Attacher::AttachEngine3D
  AttachmentOffset = pos=(-21.055,18.935,0.52) rot=(1,0,0;1.5708rad)
  BaseFeature = -> Box793
  Height = 0.375
  MapMode = 5
  Placement = pos=(-21.055,18.935,0.52) rot=(1,0,0;1.5708rad)
  Radius = 0.205
  Support = -> [XY_Plane103]
FEATURE [PartDesign::SubtractiveBox] Box942
  AttacherType = Attacher::AttachEngine3D
  AttachmentOffset = pos=(-20.95,18.635,0.53) rot=(0,0,1;0rad)
  BaseFeature = -> Cylinder191
  Height = 0.5
  Length = 0.1
  MapMode = 5
  Placement = pos=(-20.95,18.635,0.53) rot=(0,0,1;0rad)
  Support = -> [XY_Plane103]
  Width = 0.23
FEATURE [PartDesign::SubtractiveBox] Box930
  AttacherType = Attacher::AttachEngine3D
  AttachmentOffset = pos=(-21.15,18.635,0.297) rot=(0,-1,0;0.174533rad)
  BaseFeature = -> Box942
  Height = 0.115
  Length = 0.115
  MapMode = 5
  Placement = pos=(-21.15,18.635,0.297) rot=(0,-1,0;0.174533rad)
  Support = -> [XY_Plane103]
  Width = 0.23
FEATURE [PartDesign::Fillet] Fillet282
  Base = -> Box940 [Edge2]
  BaseFeature = -> Box940
  Placement = pos=(-21.5005,18.625,0.235) rot=(0,-1,0;0.174533rad)
  Radius = 0.05
  SupportTransform = false
FEATURE [PartDesign::Fillet] Fillet284
  Base = -> Fillet282 [Edge33]
  BaseFeature = -> Fillet282
  Placement = pos=(-21.5005,18.625,0.235) rot=(0,-1,0;0.174533rad)
  Radius = 0.5
  SupportTransform = false
FEATURE [PartDesign::AdditiveBox] Box922
  AttacherType = Attacher::AttachEngine3D
  AttachmentOffset = pos=(-21.1,18.635,0.305) rot=(0,1,0;0.785398rad)
  BaseFeature = -> Fillet284
  Height = 0.375
  Length = 0.2
  MapMode = 5
  Placement = pos=(-21.1,18.635,0.305) rot=(0,1,0;0.785398rad)
  Support = -> [XY_Plane106]
  Width = 0.23
FEATURE [PartDesign::SubtractiveCylinder] Cylinder188
  Angle = 360
  AttacherType = Attacher::AttachEngine3D
  AttachmentOffset = pos=(-21.055,18.935,0.52) rot=(1,0,0;1.5708rad)
  BaseFeature = -> Box922
  Height = 0.375
  MapMode = 5
  Placement = pos=(-21.055,18.935,0.52) rot=(1,0,0;1.5708rad)
  Radius = 0.205
  Support = -> [XY_Plane106]
FEATURE [PartDesign::SubtractiveBox] Box941
  AttacherType = Attacher::AttachEngine3D
  AttachmentOffset = pos=(-20.95,18.635,0.53) rot=(0,0,1;0rad)
  BaseFeature = -> Cylinder188
  Height = 0.5
  Length = 0.1
  MapMode = 5
  Placement = pos=(-20.95,18.635,0.53) rot=(0,0,1;0rad)
  Support = -> [XY_Plane106]
  Width = 0.23
FEATURE [PartDesign::SubtractiveBox] Box926
  AttacherType = Attacher::AttachEngine3D
  AttachmentOffset = pos=(-21.15,18.635,0.297) rot=(0,-1,0;0.174533rad)
  BaseFeature = -> Box941
  Height = 0.115
  Length = 0.115
  MapMode = 5
  Placement = pos=(-21.15,18.635,0.297) rot=(0,-1,0;0.174533rad)
  Support = -> [XY_Plane106]
  Width = 0.23
FEATURE [PartDesign::Fillet] Fillet283
  Base = -> Box926 [Edge28]
  BaseFeature = -> Box926
  Placement = pos=(-21.15,18.635,0.297) rot=(0,-1,0;0.174533rad)
  Radius = 0.375
  SupportTransform = false
FEATURE [PartDesign::AdditiveBox] Box931
  AttacherType = Attacher::AttachEngine3D
  AttachmentOffset = pos=(-20.7,18.635,1.55) rot=(0,1,0;0.785398rad)
  BaseFeature = -> Fillet283
  Height = 0.375
  Length = 0.23
  MapMode = 5
  Placement = pos=(-20.7,18.635,1.55) rot=(0,1,0;0.785398rad)
  Support = -> [XY_Plane106]
  Width = 0.23
FEATURE [PartDesign::SubtractiveCylinder] Cylinder190
  Angle = 360
  AttacherType = Attacher::AttachEngine3D
  AttachmentOffset = pos=(-20.271,18.635,1.4056) rot=(-1,0,0;1.5708rad)
  BaseFeature = -> Box931
  Height = 0.23
  MapMode = 5
  Placement = pos=(-20.271,18.635,1.4056) rot=(-1,0,0;1.5708rad)
  Radius = 0.23
  Support = -> [XY_Plane106]
FEATURE [PartDesign::AdditiveBox] Box939
  AttacherType = Attacher::AttachEngine3D
  AttachmentOffset = pos=(-20.1,18.635,1.635) rot=(0,0,1;0rad)
  BaseFeature = -> Cylinder190
  Height = 0.265
  Length = 0.23
  MapMode = 5
  Placement = pos=(-20.1,18.635,1.635) rot=(0,0,1;0rad)
  Support = -> [XY_Plane106]
  Width = 0.23
FEATURE [PartDesign::Body] Body097  label="pin097"
  Group = -> [Box932,Box929,Box919,Box933,Box940,Fillet282,Fillet284,Box922,Cylinder188,Box941,Box926,Fillet283,Box931,Cylinder190,Box939]
  Origin = -> Origin103
  Placement = pos=(0,-5,0) rot=(0,0,1;0rad)
  Tip = -> Box939
FEATURE [PartDesign::Fillet] Fillet285
  Base = -> Box778 [Edge2]
  BaseFeature = -> Box778
  Placement = pos=(-21.5005,18.625,0.235) rot=(0,-1,0;0.174533rad)
  Radius = 0.05
  SupportTransform = false
FEATURE [PartDesign::Fillet] Fillet288
  Base = -> Box781 [Edge2]
  BaseFeature = -> Box781
  Placement = pos=(-21.5005,18.625,0.235) rot=(0,-1,0;0.174533rad)
  Radius = 0.05
  SupportTransform = false
FEATURE [PartDesign::Fillet] Fillet289
  Base = -> Box928 [Edge2]
  BaseFeature = -> Box928
  Placement = pos=(-21.5005,18.625,0.235) rot=(0,-1,0;0.174533rad)
  Radius = 0.05
  SupportTransform = false
FEATURE [PartDesign::Fillet] Fillet290
  Base = -> Fillet285 [Edge33]
  BaseFeature = -> Fillet285
  Placement = pos=(-21.5005,18.625,0.235) rot=(0,-1,0;0.174533rad)
  Radius = 0.5
  SupportTransform = false
FEATURE [PartDesign::AdditiveBox] Box961
  AttacherType = Attacher::AttachEngine3D
  AttachmentOffset = pos=(-21.1,18.635,0.305) rot=(0,1,0;0.785398rad)
  BaseFeature = -> Fillet290
  Height = 0.375
  Length = 0.2
  MapMode = 5
  Placement = pos=(-21.1,18.635,0.305) rot=(0,1,0;0.785398rad)
  Support = -> [XY_Plane109]
  Width = 0.23
FEATURE [PartDesign::SubtractiveCylinder] Cylinder198
  Angle = 360
  AttacherType = Attacher::AttachEngine3D
  AttachmentOffset = pos=(-21.055,18.935,0.52) rot=(1,0,0;1.5708rad)
  BaseFeature = -> Box961
  Height = 0.375
  MapMode = 5
  Placement = pos=(-21.055,18.935,0.52) rot=(1,0,0;1.5708rad)
  Radius = 0.205
  Support = -> [XY_Plane109]
FEATURE [PartDesign::SubtractiveBox] Box958
  AttacherType = Attacher::AttachEngine3D
  AttachmentOffset = pos=(-20.95,18.635,0.53) rot=(0,0,1;0rad)
  BaseFeature = -> Cylinder198
  Height = 0.5
  Length = 0.1
  MapMode = 5
  Placement = pos=(-20.95,18.635,0.53) rot=(0,0,1;0rad)
  Support = -> [XY_Plane109]
  Width = 0.23
FEATURE [PartDesign::SubtractiveBox] Box950
  AttacherType = Attacher::AttachEngine3D
  AttachmentOffset = pos=(-21.15,18.635,0.297) rot=(0,-1,0;0.174533rad)
  BaseFeature = -> Box958
  Height = 0.115
  Length = 0.115
  MapMode = 5
  Placement = pos=(-21.15,18.635,0.297) rot=(0,-1,0;0.174533rad)
  Support = -> [XY_Plane109]
  Width = 0.23
FEATURE [PartDesign::Fillet] Fillet280
  Base = -> Box950 [Edge28]
  BaseFeature = -> Box950
  Placement = pos=(-21.15,18.635,0.297) rot=(0,-1,0;0.174533rad)
  Radius = 0.375
  SupportTransform = false
FEATURE [PartDesign::AdditiveBox] Box953
  AttacherType = Attacher::AttachEngine3D
  AttachmentOffset = pos=(-20.7,18.635,1.55) rot=(0,1,0;0.785398rad)
  BaseFeature = -> Fillet280
  Height = 0.375
  Length = 0.23
  MapMode = 5
  Placement = pos=(-20.7,18.635,1.55) rot=(0,1,0;0.785398rad)
  Support = -> [XY_Plane109]
  Width = 0.23
FEATURE [PartDesign::SubtractiveCylinder] Cylinder197
  Angle = 360
  AttacherType = Attacher::AttachEngine3D
  AttachmentOffset = pos=(-20.271,18.635,1.4056) rot=(-1,0,0;1.5708rad)
  BaseFeature = -> Box953
  Height = 0.23
  MapMode = 5
  Placement = pos=(-20.271,18.635,1.4056) rot=(-1,0,0;1.5708rad)
  Radius = 0.23
  Support = -> [XY_Plane109]
FEATURE [PartDesign::AdditiveBox] Box783
  AttacherType = Attacher::AttachEngine3D
  AttachmentOffset = pos=(-20.1,18.635,1.635) rot=(0,0,1;0rad)
  BaseFeature = -> Cylinder197
  Height = 0.265
  Length = 0.23
  MapMode = 5
  Placement = pos=(-20.1,18.635,1.635) rot=(0,0,1;0rad)
  Support = -> [XY_Plane109]
  Width = 0.23
FEATURE [PartDesign::Body] Body099  label="pin099"
  Group = -> [Box785,Box788,Box954,Box789,Box778,Fillet285,Fillet290,Box961,Cylinder198,Box958,Box950,Fillet280,Box953,Cylinder197,Box783]
  Origin = -> Origin119
  Placement = pos=(0,-3.5,0) rot=(0,0,1;0rad)
  Tip = -> Box783
FEATURE [PartDesign::Fillet] Fillet292
  Base = -> Fillet288 [Edge33]
  BaseFeature = -> Fillet288
  Placement = pos=(-21.5005,18.625,0.235) rot=(0,-1,0;0.174533rad)
  Radius = 0.5
  SupportTransform = false
FEATURE [PartDesign::AdditiveBox] Box960
  AttacherType = Attacher::AttachEngine3D
  AttachmentOffset = pos=(-21.1,18.635,0.305) rot=(0,1,0;0.785398rad)
  BaseFeature = -> Fillet292
  Height = 0.375
  Length = 0.2
  MapMode = 5
  Placement = pos=(-21.1,18.635,0.305) rot=(0,1,0;0.785398rad)
  Support = -> [XY_Plane104]
  Width = 0.23
FEATURE [PartDesign::SubtractiveCylinder] Cylinder158
  Angle = 360
  AttacherType = Attacher::AttachEngine3D
  AttachmentOffset = pos=(-21.055,18.935,0.52) rot=(1,0,0;1.5708rad)
  BaseFeature = -> Box960
  Height = 0.375
  MapMode = 5
  Placement = pos=(-21.055,18.935,0.52) rot=(1,0,0;1.5708rad)
  Radius = 0.205
  Support = -> [XY_Plane104]
FEATURE [PartDesign::SubtractiveBox] Box791
  AttacherType = Attacher::AttachEngine3D
  AttachmentOffset = pos=(-20.95,18.635,0.53) rot=(0,0,1;0rad)
  BaseFeature = -> Cylinder158
  Height = 0.5
  Length = 0.1
  MapMode = 5
  Placement = pos=(-20.95,18.635,0.53) rot=(0,0,1;0rad)
  Support = -> [XY_Plane104]
  Width = 0.23
FEATURE [PartDesign::SubtractiveBox] Box787
  AttacherType = Attacher::AttachEngine3D
  AttachmentOffset = pos=(-21.15,18.635,0.297) rot=(0,-1,0;0.174533rad)
  BaseFeature = -> Box791
  Height = 0.115
  Length = 0.115
  MapMode = 5
  Placement = pos=(-21.15,18.635,0.297) rot=(0,-1,0;0.174533rad)
  Support = -> [XY_Plane104]
  Width = 0.23
FEATURE [PartDesign::Fillet] Fillet293
  Base = -> Box956 [Edge2]
  BaseFeature = -> Box956
  Placement = pos=(-21.5005,18.625,0.235) rot=(0,-1,0;0.174533rad)
  Radius = 0.05
  SupportTransform = false
FEATURE [PartDesign::Fillet] Fillet286
  Base = -> Fillet293 [Edge33]
  BaseFeature = -> Fillet293
  Placement = pos=(-21.5005,18.625,0.235) rot=(0,-1,0;0.174533rad)
  Radius = 0.5
  SupportTransform = false
FEATURE [PartDesign::AdditiveBox] Box913
  AttacherType = Attacher::AttachEngine3D
  AttachmentOffset = pos=(-21.1,18.635,0.305) rot=(0,1,0;0.785398rad)
  BaseFeature = -> Fillet286
  Height = 0.375
  Length = 0.2
  MapMode = 5
  Placement = pos=(-21.1,18.635,0.305) rot=(0,1,0;0.785398rad)
  Support = -> [XY_Plane108]
  Width = 0.23
FEATURE [PartDesign::SubtractiveCylinder] Cylinder186
  Angle = 360
  AttacherType = Attacher::AttachEngine3D
  AttachmentOffset = pos=(-21.055,18.935,0.52) rot=(1,0,0;1.5708rad)
  BaseFeature = -> Box913
  Height = 0.375
  MapMode = 5
  Placement = pos=(-21.055,18.935,0.52) rot=(1,0,0;1.5708rad)
  Radius = 0.205
  Support = -> [XY_Plane108]
FEATURE [PartDesign::SubtractiveBox] Box910
  AttacherType = Attacher::AttachEngine3D
  AttachmentOffset = pos=(-20.95,18.635,0.53) rot=(0,0,1;0rad)
  BaseFeature = -> Cylinder186
  Height = 0.5
  Length = 0.1
  MapMode = 5
  Placement = pos=(-20.95,18.635,0.53) rot=(0,0,1;0rad)
  Support = -> [XY_Plane108]
  Width = 0.23
FEATURE [PartDesign::SubtractiveBox] Box921
  AttacherType = Attacher::AttachEngine3D
  AttachmentOffset = pos=(-21.15,18.635,0.297) rot=(0,-1,0;0.174533rad)
  BaseFeature = -> Box910
  Height = 0.115
  Length = 0.115
  MapMode = 5
  Placement = pos=(-21.15,18.635,0.297) rot=(0,-1,0;0.174533rad)
  Support = -> [XY_Plane108]
  Width = 0.23
FEATURE [PartDesign::Fillet] Fillet294
  Base = -> Box790 [Edge2]
  BaseFeature = -> Box790
  Placement = pos=(-21.5005,18.625,0.235) rot=(0,-1,0;0.174533rad)
  Radius = 0.05
  SupportTransform = false
FEATURE [PartDesign::Fillet] Fillet287
  Base = -> Fillet294 [Edge33]
  BaseFeature = -> Fillet294
  Placement = pos=(-21.5005,18.625,0.235) rot=(0,-1,0;0.174533rad)
  Radius = 0.5
  SupportTransform = false
FEATURE [PartDesign::AdditiveBox] Box925
  AttacherType = Attacher::AttachEngine3D
  AttachmentOffset = pos=(-21.1,18.635,0.305) rot=(0,1,0;0.785398rad)
  BaseFeature = -> Fillet287
  Height = 0.375
  Length = 0.2
  MapMode = 5
  Placement = pos=(-21.1,18.635,0.305) rot=(0,1,0;0.785398rad)
  Support = -> [XY_Plane107]
  Width = 0.23
FEATURE [PartDesign::SubtractiveCylinder] Cylinder193
  Angle = 360
  AttacherType = Attacher::AttachEngine3D
  AttachmentOffset = pos=(-21.055,18.935,0.52) rot=(1,0,0;1.5708rad)
  BaseFeature = -> Box925
  Height = 0.375
  MapMode = 5
  Placement = pos=(-21.055,18.935,0.52) rot=(1,0,0;1.5708rad)
  Radius = 0.205
  Support = -> [XY_Plane107]
FEATURE [PartDesign::SubtractiveBox] Box936
  AttacherType = Attacher::AttachEngine3D
  AttachmentOffset = pos=(-20.95,18.635,0.53) rot=(0,0,1;0rad)
  BaseFeature = -> Cylinder193
  Height = 0.5
  Length = 0.1
  MapMode = 5
  Placement = pos=(-20.95,18.635,0.53) rot=(0,0,1;0rad)
  Support = -> [XY_Plane107]
  Width = 0.23
FEATURE [PartDesign::SubtractiveBox] Box948
  AttacherType = Attacher::AttachEngine3D
  AttachmentOffset = pos=(-21.15,18.635,0.297) rot=(0,-1,0;0.174533rad)
  BaseFeature = -> Box936
  Height = 0.115
  Length = 0.115
  MapMode = 5
  Placement = pos=(-21.15,18.635,0.297) rot=(0,-1,0;0.174533rad)
  Support = -> [XY_Plane107]
  Width = 0.23
FEATURE [PartDesign::Fillet] Fillet291
  Base = -> Box948 [Edge28]
  BaseFeature = -> Box948
  Placement = pos=(-21.15,18.635,0.297) rot=(0,-1,0;0.174533rad)
  Radius = 0.375
  SupportTransform = false
FEATURE [PartDesign::AdditiveBox] Box952
  AttacherType = Attacher::AttachEngine3D
  AttachmentOffset = pos=(-20.7,18.635,1.55) rot=(0,1,0;0.785398rad)
  BaseFeature = -> Fillet291
  Height = 0.375
  Length = 0.23
  MapMode = 5
  Placement = pos=(-20.7,18.635,1.55) rot=(0,1,0;0.785398rad)
  Support = -> [XY_Plane107]
  Width = 0.23
FEATURE [PartDesign::SubtractiveCylinder] Cylinder194
  Angle = 360
  AttacherType = Attacher::AttachEngine3D
  AttachmentOffset = pos=(-20.271,18.635,1.4056) rot=(-1,0,0;1.5708rad)
  BaseFeature = -> Box952
  Height = 0.23
  MapMode = 5
  Placement = pos=(-20.271,18.635,1.4056) rot=(-1,0,0;1.5708rad)
  Radius = 0.23
  Support = -> [XY_Plane107]
FEATURE [PartDesign::AdditiveBox] Box963
  AttacherType = Attacher::AttachEngine3D
  AttachmentOffset = pos=(-20.1,18.635,1.635) rot=(0,0,1;0rad)
  BaseFeature = -> Cylinder194
  Height = 0.265
  Length = 0.23
  MapMode = 5
  Placement = pos=(-20.1,18.635,1.635) rot=(0,0,1;0rad)
  Support = -> [XY_Plane107]
  Width = 0.23
FEATURE [PartDesign::Body] Body098  label="pin098"
  Group = -> [Box780,Box792,Box949,Box955,Box790,Fillet294,Fillet287,Box925,Cylinder193,Box936,Box948,Fillet291,Box952,Cylinder194,Box963]
  Origin = -> Origin121
  Placement = pos=(0,-3,0) rot=(0,0,1;0rad)
  Tip = -> Box963
FEATURE [PartDesign::Fillet] Fillet295
  Base = -> Fillet289 [Edge33]
  BaseFeature = -> Fillet289
  Placement = pos=(-21.5005,18.625,0.235) rot=(0,-1,0;0.174533rad)
  Radius = 0.5
  SupportTransform = false
FEATURE [PartDesign::AdditiveBox] Box938
  AttacherType = Attacher::AttachEngine3D
  AttachmentOffset = pos=(-21.1,18.635,0.305) rot=(0,1,0;0.785398rad)
  BaseFeature = -> Fillet295
  Height = 0.375
  Length = 0.2
  MapMode = 5
  Placement = pos=(-21.1,18.635,0.305) rot=(0,1,0;0.785398rad)
  Support = -> [XY_Plane090]
  Width = 0.23
FEATURE [PartDesign::SubtractiveCylinder] Cylinder192
  Angle = 360
  AttacherType = Attacher::AttachEngine3D
  AttachmentOffset = pos=(-21.055,18.935,0.52) rot=(1,0,0;1.5708rad)
  BaseFeature = -> Box938
  Height = 0.375
  MapMode = 5
  Placement = pos=(-21.055,18.935,0.52) rot=(1,0,0;1.5708rad)
  Radius = 0.205
  Support = -> [XY_Plane090]
FEATURE [PartDesign::SubtractiveBox] Box943
  AttacherType = Attacher::AttachEngine3D
  AttachmentOffset = pos=(-20.95,18.635,0.53) rot=(0,0,1;0rad)
  BaseFeature = -> Cylinder192
  Height = 0.5
  Length = 0.1
  MapMode = 5
  Placement = pos=(-20.95,18.635,0.53) rot=(0,0,1;0rad)
  Support = -> [XY_Plane090]
  Width = 0.23
FEATURE [PartDesign::SubtractiveBox] Box945
  AttacherType = Attacher::AttachEngine3D
  AttachmentOffset = pos=(-21.15,18.635,0.297) rot=(0,-1,0;0.174533rad)
  BaseFeature = -> Box943
  Height = 0.115
  Length = 0.115
  MapMode = 5
  Placement = pos=(-21.15,18.635,0.297) rot=(0,-1,0;0.174533rad)
  Support = -> [XY_Plane090]
  Width = 0.23
FEATURE [PartDesign::Fillet] Fillet266
  Base = -> Box945 [Edge28]
  BaseFeature = -> Box945
  Placement = pos=(-21.15,18.635,0.297) rot=(0,-1,0;0.174533rad)
  Radius = 0.375
  SupportTransform = false
FEATURE [PartDesign::AdditiveBox] Box944
  AttacherType = Attacher::AttachEngine3D
  AttachmentOffset = pos=(-20.7,18.635,1.55) rot=(0,1,0;0.785398rad)
  BaseFeature = -> Fillet266
  Height = 0.375
  Length = 0.23
  MapMode = 5
  Placement = pos=(-20.7,18.635,1.55) rot=(0,1,0;0.785398rad)
  Support = -> [XY_Plane090]
  Width = 0.23
FEATURE [PartDesign::SubtractiveCylinder] Cylinder189
  Angle = 360
  AttacherType = Attacher::AttachEngine3D
  AttachmentOffset = pos=(-20.271,18.635,1.4056) rot=(-1,0,0;1.5708rad)
  BaseFeature = -> Box944
  Height = 0.23
  MapMode = 5
  Placement = pos=(-20.271,18.635,1.4056) rot=(-1,0,0;1.5708rad)
  Radius = 0.23
  Support = -> [XY_Plane090]
FEATURE [PartDesign::AdditiveBox] Box934
  AttacherType = Attacher::AttachEngine3D
  AttachmentOffset = pos=(-20.1,18.635,1.635) rot=(0,0,1;0rad)
  BaseFeature = -> Cylinder189
  Height = 0.265
  Length = 0.23
  MapMode = 5
  Placement = pos=(-20.1,18.635,1.635) rot=(0,0,1;0rad)
  Support = -> [XY_Plane090]
  Width = 0.23
FEATURE [PartDesign::Body] Body100  label="pin100"
  Group = -> [Box951,Box946,Box917,Box927,Box928,Fillet289,Fillet295,Box938,Cylinder192,Box943,Box945,Fillet266,Box944,Cylinder189,Box934]
  Origin = -> Origin107
  Placement = pos=(0,-5.5,0) rot=(0,0,1;0rad)
  Tip = -> Box934
FEATURE [PartDesign::Fillet] Fillet296
  Base = -> Box787 [Edge28]
  BaseFeature = -> Box787
  Placement = pos=(-21.15,18.635,0.297) rot=(0,-1,0;0.174533rad)
  Radius = 0.375
  SupportTransform = false
FEATURE [PartDesign::AdditiveBox] Box786
  AttacherType = Attacher::AttachEngine3D
  AttachmentOffset = pos=(-20.7,18.635,1.55) rot=(0,1,0;0.785398rad)
  BaseFeature = -> Fillet296
  Height = 0.375
  Length = 0.23
  MapMode = 5
  Placement = pos=(-20.7,18.635,1.55) rot=(0,1,0;0.785398rad)
  Support = -> [XY_Plane104]
  Width = 0.23
FEATURE [PartDesign::SubtractiveCylinder] Cylinder159
  Angle = 360
  AttacherType = Attacher::AttachEngine3D
  AttachmentOffset = pos=(-20.271,18.635,1.4056) rot=(-1,0,0;1.5708rad)
  BaseFeature = -> Box786
  Height = 0.23
  MapMode = 5
  Placement = pos=(-20.271,18.635,1.4056) rot=(-1,0,0;1.5708rad)
  Radius = 0.23
  Support = -> [XY_Plane104]
FEATURE [PartDesign::AdditiveBox] Box775
  AttacherType = Attacher::AttachEngine3D
  AttachmentOffset = pos=(-20.1,18.635,1.635) rot=(0,0,1;0rad)
  BaseFeature = -> Cylinder159
  Height = 0.265
  Length = 0.23
  MapMode = 5
  Placement = pos=(-20.1,18.635,1.635) rot=(0,0,1;0rad)
  Support = -> [XY_Plane104]
  Width = 0.23
FEATURE [PartDesign::Body] Body095  label="pin095"
  Group = -> [Box779,Box784,Box937,Box782,Box781,Fillet288,Fillet292,Box960,Cylinder158,Box791,Box787,Fillet296,Box786,Cylinder159,Box775]
  Origin = -> Origin106
  Placement = pos=(0,-4,0) rot=(0,0,1;0rad)
  Tip = -> Box775
FEATURE [PartDesign::Fillet] Fillet297
  Base = -> Box921 [Edge28]
  BaseFeature = -> Box921
  Placement = pos=(-21.15,18.635,0.297) rot=(0,-1,0;0.174533rad)
  Radius = 0.375
  SupportTransform = false
FEATURE [PartDesign::AdditiveBox] Box916
  AttacherType = Attacher::AttachEngine3D
  AttachmentOffset = pos=(-20.7,18.635,1.55) rot=(0,1,0;0.785398rad)
  BaseFeature = -> Fillet297
  Height = 0.375
  Length = 0.23
  MapMode = 5
  Placement = pos=(-20.7,18.635,1.55) rot=(0,1,0;0.785398rad)
  Support = -> [XY_Plane108]
  Width = 0.23
FEATURE [PartDesign::SubtractiveCylinder] Cylinder187
  Angle = 360
  AttacherType = Attacher::AttachEngine3D
  AttachmentOffset = pos=(-20.271,18.635,1.4056) rot=(-1,0,0;1.5708rad)
  BaseFeature = -> Box916
  Height = 0.23
  MapMode = 5
  Placement = pos=(-20.271,18.635,1.4056) rot=(-1,0,0;1.5708rad)
  Radius = 0.23
  Support = -> [XY_Plane108]
FEATURE [PartDesign::AdditiveBox] Box920
  AttacherType = Attacher::AttachEngine3D
  AttachmentOffset = pos=(-20.1,18.635,1.635) rot=(0,0,1;0rad)
  BaseFeature = -> Cylinder187
  Height = 0.265
  Length = 0.23
  MapMode = 5
  Placement = pos=(-20.1,18.635,1.635) rot=(0,0,1;0rad)
  Support = -> [XY_Plane108]
  Width = 0.23
FEATURE [PartDesign::Body] Body096  label="pin096"
  Group = -> [Box947,Box935,Box923,Box914,Box956,Fillet293,Fillet286,Box913,Cylinder186,Box910,Box921,Fillet297,Box916,Cylinder187,Box920]
  Origin = -> Origin094
  Placement = pos=(0,-4.5,0) rot=(0,0,1;0rad)
  Tip = -> Box920
FEATURE [PartDesign::Fillet] Fillet298
  Base = -> Box930 [Edge28]
  BaseFeature = -> Box930
  Placement = pos=(-21.15,18.635,0.297) rot=(0,-1,0;0.174533rad)
  Radius = 0.375
  SupportTransform = false
FEATURE [PartDesign::AdditiveBox] Box957
  AttacherType = Attacher::AttachEngine3D
  AttachmentOffset = pos=(-20.7,18.635,1.55) rot=(0,1,0;0.785398rad)
  BaseFeature = -> Fillet298
  Height = 0.375
  Length = 0.23
  MapMode = 5
  Placement = pos=(-20.7,18.635,1.55) rot=(0,1,0;0.785398rad)
  Support = -> [XY_Plane103]
  Width = 0.23
FEATURE [PartDesign::SubtractiveCylinder] Cylinder195
  Angle = 360
  AttacherType = Attacher::AttachEngine3D
  AttachmentOffset = pos=(-20.271,18.635,1.4056) rot=(-1,0,0;1.5708rad)
  BaseFeature = -> Box957
  Height = 0.23
  MapMode = 5
  Placement = pos=(-20.271,18.635,1.4056) rot=(-1,0,0;1.5708rad)
  Radius = 0.23
  Support = -> [XY_Plane103]
FEATURE [PartDesign::AdditiveBox] Box971
  AttacherType = Attacher::AttachEngine3D
  AttachmentOffset = pos=(-20.1,18.635,1.635) rot=(0,0,1;0rad)
  BaseFeature = -> Cylinder195
  Height = 0.265
  Length = 0.23
  MapMode = 5
  Placement = pos=(-20.1,18.635,1.635) rot=(0,0,1;0rad)
  Support = -> [XY_Plane103]
  Width = 0.23
FEATURE [PartDesign::Body] Body092  label="pin092"
  Group = -> [Box986,Box989,Box967,Box962,Box985,Fillet278,Fillet230,Box793,Cylinder191,Box942,Box930,Fillet298,Box957,Cylinder195,Box971]
  Origin = -> Origin093
  Tip = -> Box971
FEATURE [PartDesign::SubtractiveBox] Box993
  AttacherType = Attacher::AttachEngine3D
  AttachmentOffset = pos=(-21.35,18.635,0.35) rot=(0,0,1;0rad)
  BaseFeature = -> Box991
  Height = 1.55
  Length = 0.5
  MapMode = 5
  Placement = pos=(-21.35,18.635,0.35) rot=(0,0,1;0rad)
  Support = -> [XY_Plane120]
  Width = 0.23
FEATURE [PartDesign::AdditiveBox] Box996
  AttacherType = Attacher::AttachEngine3D
  AttachmentOffset = pos=(-21.3,18.635,0) rot=(0,0,1;0rad)
  Height = 1.9
  Length = 1.3
  MapMode = 5
  Placement = pos=(-21.3,18.635,0) rot=(0,0,1;0rad)
  Support = -> [XY_Plane125]
  Width = 0.23
FEATURE [PartDesign::SubtractiveBox] Box999
  AttacherType = Attacher::AttachEngine3D
  AttachmentOffset = pos=(-21.35,18.635,0.35) rot=(0,0,1;0rad)
  BaseFeature = -> Box982
  Height = 1.55
  Length = 0.5
  MapMode = 5
  Placement = pos=(-21.35,18.635,0.35) rot=(0,0,1;0rad)
  Support = -> [XY_Plane122]
  Width = 0.23
FEATURE [PartDesign::SubtractiveBox] Box1004
  AttacherType = Attacher::AttachEngine3D
  AttachmentOffset = pos=(-21.35,18.635,0.35) rot=(0,0,1;0rad)
  BaseFeature = -> Box996
  Height = 1.55
  Length = 0.5
  MapMode = 5
  Placement = pos=(-21.35,18.635,0.35) rot=(0,0,1;0rad)
  Support = -> [XY_Plane125]
  Width = 0.23
FEATURE [PartDesign::AdditiveBox] Box1007
  AttacherType = Attacher::AttachEngine3D
  AttachmentOffset = pos=(-21.3,18.635,0) rot=(0,0,1;0rad)
  Height = 1.9
  Length = 1.3
  MapMode = 5
  Placement = pos=(-21.3,18.635,0) rot=(0,0,1;0rad)
  Support = -> [XY_Plane118]
  Width = 0.23
FEATURE [PartDesign::SubtractiveBox] Box1018
  AttacherType = Attacher::AttachEngine3D
  AttachmentOffset = pos=(-21.35,18.635,0.35) rot=(0,0,1;0rad)
  BaseFeature = -> Box1007
  Height = 1.55
  Length = 0.5
  MapMode = 5
  Placement = pos=(-21.35,18.635,0.35) rot=(0,0,1;0rad)
  Support = -> [XY_Plane118]
  Width = 0.23
FEATURE [PartDesign::AdditiveBox] Box1029
  AttacherType = Attacher::AttachEngine3D
  AttachmentOffset = pos=(-21.3,18.635,0) rot=(0,0,1;0rad)
  Height = 1.9
  Length = 1.3
  MapMode = 5
  Placement = pos=(-21.3,18.635,0) rot=(0,0,1;0rad)
  Support = -> [XY_Plane115]
  Width = 0.23
FEATURE [PartDesign::SubtractiveBox] Box1023
  AttacherType = Attacher::AttachEngine3D
  AttachmentOffset = pos=(-21.35,18.635,0.35) rot=(0,0,1;0rad)
  BaseFeature = -> Box1029
  Height = 1.55
  Length = 0.5
  MapMode = 5
  Placement = pos=(-21.35,18.635,0.35) rot=(0,0,1;0rad)
  Support = -> [XY_Plane115]
  Width = 0.23
FEATURE [PartDesign::AdditiveBox] Box1031
  AttacherType = Attacher::AttachEngine3D
  AttachmentOffset = pos=(-21.3,18.635,0) rot=(0,0,1;0rad)
  Height = 1.9
  Length = 1.3
  MapMode = 5
  Placement = pos=(-21.3,18.635,0) rot=(0,0,1;0rad)
  Support = -> [XY_Plane114]
  Width = 0.23
FEATURE [PartDesign::SubtractiveBox] Box1009
  AttacherType = Attacher::AttachEngine3D
  AttachmentOffset = pos=(-21.35,18.635,0.35) rot=(0,0,1;0rad)
  BaseFeature = -> Box1031
  Height = 1.55
  Length = 0.5
  MapMode = 5
  Placement = pos=(-21.35,18.635,0.35) rot=(0,0,1;0rad)
  Support = -> [XY_Plane114]
  Width = 0.23
FEATURE [PartDesign::AdditiveBox] Box1037
  AttacherType = Attacher::AttachEngine3D
  AttachmentOffset = pos=(-21.3,18.635,0) rot=(0,0,1;0rad)
  Height = 1.9
  Length = 1.3
  MapMode = 5
  Placement = pos=(-21.3,18.635,0) rot=(0,0,1;0rad)
  Support = -> [XY_Plane121]
  Width = 0.23
FEATURE [PartDesign::SubtractiveBox] Box1042
  AttacherType = Attacher::AttachEngine3D
  AttachmentOffset = pos=(-20.5,18.63,0) rot=(0,0,1;0rad)
  BaseFeature = -> Box993
  Height = 1.635
  Length = 0.5
  MapMode = 5
  Placement = pos=(-20.5,18.63,0) rot=(0,0,1;0rad)
  Support = -> [XY_Plane120]
  Width = 0.25
FEATURE [PartDesign::SubtractiveBox] Box1002
  AttacherType = Attacher::AttachEngine3D
  AttachmentOffset = pos=(-21.19,18.635,-0.12) rot=(0,-1,0;0.15708rad)
  BaseFeature = -> Box1042
  Height = 0.12
  Length = 0.725
  MapMode = 5
  Placement = pos=(-21.19,18.635,-0.12) rot=(0,-1,0;0.15708rad)
  Support = -> [XY_Plane120]
  Width = 0.25
FEATURE [PartDesign::SubtractiveBox] Box1003
  AttacherType = Attacher::AttachEngine3D
  AttachmentOffset = pos=(-21.5005,18.625,0.235) rot=(0,-1,0;0.174533rad)
  BaseFeature = -> Box1002
  Height = 0.3
  Length = 0.6605
  MapMode = 5
  Placement = pos=(-21.5005,18.625,0.235) rot=(0,-1,0;0.174533rad)
  Support = -> [XY_Plane120]
  Width = 0.25
FEATURE [PartDesign::Fillet] Fillet326
  Base = -> Box1003 [Edge2]
  BaseFeature = -> Box1003
  Placement = pos=(-21.5005,18.625,0.235) rot=(0,-1,0;0.174533rad)
  Radius = 0.05
  SupportTransform = false
FEATURE [PartDesign::Fillet] Fillet331
  Base = -> Fillet326 [Edge33]
  BaseFeature = -> Fillet326
  Placement = pos=(-21.5005,18.625,0.235) rot=(0,-1,0;0.174533rad)
  Radius = 0.5
  SupportTransform = false
FEATURE [PartDesign::SubtractiveBox] Box1043
  AttacherType = Attacher::AttachEngine3D
  AttachmentOffset = pos=(-21.35,18.635,0.35) rot=(0,0,1;0rad)
  BaseFeature = -> Box1037
  Height = 1.55
  Length = 0.5
  MapMode = 5
  Placement = pos=(-21.35,18.635,0.35) rot=(0,0,1;0rad)
  Support = -> [XY_Plane121]
  Width = 0.23
FEATURE [PartDesign::SubtractiveBox] Box1032
  AttacherType = Attacher::AttachEngine3D
  AttachmentOffset = pos=(-20.5,18.63,0) rot=(0,0,1;0rad)
  BaseFeature = -> Box1043
  Height = 1.635
  Length = 0.5
  MapMode = 5
  Placement = pos=(-20.5,18.63,0) rot=(0,0,1;0rad)
  Support = -> [XY_Plane121]
  Width = 0.25
FEATURE [PartDesign::SubtractiveBox] Box1040
  AttacherType = Attacher::AttachEngine3D
  AttachmentOffset = pos=(-21.19,18.635,-0.12) rot=(0,-1,0;0.15708rad)
  BaseFeature = -> Box1032
  Height = 0.12
  Length = 0.725
  MapMode = 5
  Placement = pos=(-21.19,18.635,-0.12) rot=(0,-1,0;0.15708rad)
  Support = -> [XY_Plane121]
  Width = 0.25
FEATURE [PartDesign::AdditiveBox] Box1050
  AttacherType = Attacher::AttachEngine3D
  AttachmentOffset = pos=(-21.3,18.635,0) rot=(0,0,1;0rad)
  Height = 1.9
  Length = 1.3
  MapMode = 5
  Placement = pos=(-21.3,18.635,0) rot=(0,0,1;0rad)
  Support = -> [XY_Plane123]
  Width = 0.23
FEATURE [PartDesign::SubtractiveBox] Box1045
  AttacherType = Attacher::AttachEngine3D
  AttachmentOffset = pos=(-21.35,18.635,0.35) rot=(0,0,1;0rad)
  BaseFeature = -> Box1050
  Height = 1.55
  Length = 0.5
  MapMode = 5
  Placement = pos=(-21.35,18.635,0.35) rot=(0,0,1;0rad)
  Support = -> [XY_Plane123]
  Width = 0.23
FEATURE [PartDesign::SubtractiveBox] Box1030
  AttacherType = Attacher::AttachEngine3D
  AttachmentOffset = pos=(-20.5,18.63,0) rot=(0,0,1;0rad)
  BaseFeature = -> Box1045
  Height = 1.635
  Length = 0.5
  MapMode = 5
  Placement = pos=(-20.5,18.63,0) rot=(0,0,1;0rad)
  Support = -> [XY_Plane123]
  Width = 0.25
FEATURE [PartDesign::SubtractiveBox] Box1024
  AttacherType = Attacher::AttachEngine3D
  AttachmentOffset = pos=(-21.19,18.635,-0.12) rot=(0,-1,0;0.15708rad)
  BaseFeature = -> Box1030
  Height = 0.12
  Length = 0.725
  MapMode = 5
  Placement = pos=(-21.19,18.635,-0.12) rot=(0,-1,0;0.15708rad)
  Support = -> [XY_Plane123]
  Width = 0.25
FEATURE [PartDesign::SubtractiveBox] Box1054
  AttacherType = Attacher::AttachEngine3D
  AttachmentOffset = pos=(-20.5,18.63,0) rot=(0,0,1;0rad)
  BaseFeature = -> Box999
  Height = 1.635
  Length = 0.5
  MapMode = 5
  Placement = pos=(-20.5,18.63,0) rot=(0,0,1;0rad)
  Support = -> [XY_Plane122]
  Width = 0.25
FEATURE [PartDesign::SubtractiveBox] Box1055
  AttacherType = Attacher::AttachEngine3D
  AttachmentOffset = pos=(-21.5005,18.625,0.235) rot=(0,-1,0;0.174533rad)
  BaseFeature = -> Box1040
  Height = 0.3
  Length = 0.6605
  MapMode = 5
  Placement = pos=(-21.5005,18.625,0.235) rot=(0,-1,0;0.174533rad)
  Support = -> [XY_Plane121]
  Width = 0.25
FEATURE [PartDesign::Fillet] Fillet320
  Base = -> Box1055 [Edge2]
  BaseFeature = -> Box1055
  Placement = pos=(-21.5005,18.625,0.235) rot=(0,-1,0;0.174533rad)
  Radius = 0.05
  SupportTransform = false
FEATURE [PartDesign::Fillet] Fillet312
  Base = -> Fillet320 [Edge33]
  BaseFeature = -> Fillet320
  Placement = pos=(-21.5005,18.625,0.235) rot=(0,-1,0;0.174533rad)
  Radius = 0.5
  SupportTransform = false
FEATURE [PartDesign::AdditiveBox] Box1026
  AttacherType = Attacher::AttachEngine3D
  AttachmentOffset = pos=(-21.1,18.635,0.305) rot=(0,1,0;0.785398rad)
  BaseFeature = -> Fillet312
  Height = 0.375
  Length = 0.2
  MapMode = 5
  Placement = pos=(-21.1,18.635,0.305) rot=(0,1,0;0.785398rad)
  Support = -> [XY_Plane121]
  Width = 0.23
FEATURE [PartDesign::SubtractiveCylinder] Cylinder210
  Angle = 360
  AttacherType = Attacher::AttachEngine3D
  AttachmentOffset = pos=(-21.055,18.935,0.52) rot=(1,0,0;1.5708rad)
  BaseFeature = -> Box1026
  Height = 0.375
  MapMode = 5
  Placement = pos=(-21.055,18.935,0.52) rot=(1,0,0;1.5708rad)
  Radius = 0.205
  Support = -> [XY_Plane121]
FEATURE [PartDesign::SubtractiveBox] Box1053
  AttacherType = Attacher::AttachEngine3D
  AttachmentOffset = pos=(-20.95,18.635,0.53) rot=(0,0,1;0rad)
  BaseFeature = -> Cylinder210
  Height = 0.5
  Length = 0.1
  MapMode = 5
  Placement = pos=(-20.95,18.635,0.53) rot=(0,0,1;0rad)
  Support = -> [XY_Plane121]
  Width = 0.23
FEATURE [PartDesign::SubtractiveBox] Box1033
  AttacherType = Attacher::AttachEngine3D
  AttachmentOffset = pos=(-21.15,18.635,0.297) rot=(0,-1,0;0.174533rad)
  BaseFeature = -> Box1053
  Height = 0.115
  Length = 0.115
  MapMode = 5
  Placement = pos=(-21.15,18.635,0.297) rot=(0,-1,0;0.174533rad)
  Support = -> [XY_Plane121]
  Width = 0.23
FEATURE [PartDesign::Fillet] Fillet318
  Base = -> Box1033 [Edge28]
  BaseFeature = -> Box1033
  Placement = pos=(-21.15,18.635,0.297) rot=(0,-1,0;0.174533rad)
  Radius = 0.375
  SupportTransform = false
FEATURE [PartDesign::AdditiveBox] Box1039
  AttacherType = Attacher::AttachEngine3D
  AttachmentOffset = pos=(-20.7,18.635,1.55) rot=(0,1,0;0.785398rad)
  BaseFeature = -> Fillet318
  Height = 0.375
  Length = 0.23
  MapMode = 5
  Placement = pos=(-20.7,18.635,1.55) rot=(0,1,0;0.785398rad)
  Support = -> [XY_Plane121]
  Width = 0.23
FEATURE [PartDesign::SubtractiveCylinder] Cylinder211
  Angle = 360
  AttacherType = Attacher::AttachEngine3D
  AttachmentOffset = pos=(-20.271,18.635,1.4056) rot=(-1,0,0;1.5708rad)
  BaseFeature = -> Box1039
  Height = 0.23
  MapMode = 5
  Placement = pos=(-20.271,18.635,1.4056) rot=(-1,0,0;1.5708rad)
  Radius = 0.23
  Support = -> [XY_Plane121]
FEATURE [PartDesign::AdditiveBox] Box1048
  AttacherType = Attacher::AttachEngine3D
  AttachmentOffset = pos=(-20.1,18.635,1.635) rot=(0,0,1;0rad)
  BaseFeature = -> Cylinder211
  Height = 0.265
  Length = 0.23
  MapMode = 5
  Placement = pos=(-20.1,18.635,1.635) rot=(0,0,1;0rad)
  Support = -> [XY_Plane121]
  Width = 0.23
FEATURE [PartDesign::Body] Body110  label="pin110"
  Group = -> [Box1037,Box1043,Box1032,Box1040,Box1055,Fillet320,Fillet312,Box1026,Cylinder210,Box1053,Box1033,Fillet318,Box1039,Cylinder211,Box1048]
  Origin = -> Origin114
  Placement = pos=(0,-5,0) rot=(0,0,1;0rad)
  Tip = -> Box1048
FEATURE [PartDesign::AdditiveBox] Box1058
  AttacherType = Attacher::AttachEngine3D
  AttachmentOffset = pos=(-21.3,18.635,0) rot=(0,0,1;0rad)
  Height = 1.9
  Length = 1.3
  MapMode = 5
  Placement = pos=(-21.3,18.635,0) rot=(0,0,1;0rad)
  Support = -> [XY_Plane113]
  Width = 0.23
FEATURE [PartDesign::SubtractiveBox] Box1056
  AttacherType = Attacher::AttachEngine3D
  AttachmentOffset = pos=(-21.35,18.635,0.35) rot=(0,0,1;0rad)
  BaseFeature = -> Box1058
  Height = 1.55
  Length = 0.5
  MapMode = 5
  Placement = pos=(-21.35,18.635,0.35) rot=(0,0,1;0rad)
  Support = -> [XY_Plane113]
  Width = 0.23
FEATURE [PartDesign::SubtractiveBox] Box1014
  AttacherType = Attacher::AttachEngine3D
  AttachmentOffset = pos=(-20.5,18.63,0) rot=(0,0,1;0rad)
  BaseFeature = -> Box1056
  Height = 1.635
  Length = 0.5
  MapMode = 5
  Placement = pos=(-20.5,18.63,0) rot=(0,0,1;0rad)
  Support = -> [XY_Plane113]
  Width = 0.25
FEATURE [PartDesign::SubtractiveBox] Box1035
  AttacherType = Attacher::AttachEngine3D
  AttachmentOffset = pos=(-21.19,18.635,-0.12) rot=(0,-1,0;0.15708rad)
  BaseFeature = -> Box1014
  Height = 0.12
  Length = 0.725
  MapMode = 5
  Placement = pos=(-21.19,18.635,-0.12) rot=(0,-1,0;0.15708rad)
  Support = -> [XY_Plane113]
  Width = 0.25
FEATURE [PartDesign::SubtractiveBox] Box1027
  AttacherType = Attacher::AttachEngine3D
  AttachmentOffset = pos=(-21.5005,18.625,0.235) rot=(0,-1,0;0.174533rad)
  BaseFeature = -> Box1035
  Height = 0.3
  Length = 0.6605
  MapMode = 5
  Placement = pos=(-21.5005,18.625,0.235) rot=(0,-1,0;0.174533rad)
  Support = -> [XY_Plane113]
  Width = 0.25
FEATURE [PartDesign::Fillet] Fillet314
  Base = -> Box1027 [Edge2]
  BaseFeature = -> Box1027
  Placement = pos=(-21.5005,18.625,0.235) rot=(0,-1,0;0.174533rad)
  Radius = 0.05
  SupportTransform = false
FEATURE [PartDesign::Fillet] Fillet332
  Base = -> Fillet314 [Edge33]
  BaseFeature = -> Fillet314
  Placement = pos=(-21.5005,18.625,0.235) rot=(0,-1,0;0.174533rad)
  Radius = 0.5
  SupportTransform = false
FEATURE [PartDesign::AdditiveBox] Box1049
  AttacherType = Attacher::AttachEngine3D
  AttachmentOffset = pos=(-21.1,18.635,0.305) rot=(0,1,0;0.785398rad)
  BaseFeature = -> Fillet332
  Height = 0.375
  Length = 0.2
  MapMode = 5
  Placement = pos=(-21.1,18.635,0.305) rot=(0,1,0;0.785398rad)
  Support = -> [XY_Plane113]
  Width = 0.23
FEATURE [PartDesign::SubtractiveCylinder] Cylinder217
  Angle = 360
  AttacherType = Attacher::AttachEngine3D
  AttachmentOffset = pos=(-21.055,18.935,0.52) rot=(1,0,0;1.5708rad)
  BaseFeature = -> Box1049
  Height = 0.375
  MapMode = 5
  Placement = pos=(-21.055,18.935,0.52) rot=(1,0,0;1.5708rad)
  Radius = 0.205
  Support = -> [XY_Plane113]
FEATURE [PartDesign::SubtractiveBox] Box1046
  AttacherType = Attacher::AttachEngine3D
  AttachmentOffset = pos=(-20.95,18.635,0.53) rot=(0,0,1;0rad)
  BaseFeature = -> Cylinder217
  Height = 0.5
  Length = 0.1
  MapMode = 5
  Placement = pos=(-20.95,18.635,0.53) rot=(0,0,1;0rad)
  Support = -> [XY_Plane113]
  Width = 0.23
FEATURE [PartDesign::SubtractiveBox] Box1047
  AttacherType = Attacher::AttachEngine3D
  AttachmentOffset = pos=(-21.15,18.635,0.297) rot=(0,-1,0;0.174533rad)
  BaseFeature = -> Box1046
  Height = 0.115
  Length = 0.115
  MapMode = 5
  Placement = pos=(-21.15,18.635,0.297) rot=(0,-1,0;0.174533rad)
  Support = -> [XY_Plane113]
  Width = 0.23
FEATURE [PartDesign::Fillet] Fillet303
  Base = -> Box1047 [Edge28]
  BaseFeature = -> Box1047
  Placement = pos=(-21.15,18.635,0.297) rot=(0,-1,0;0.174533rad)
  Radius = 0.375
  SupportTransform = false
FEATURE [PartDesign::AdditiveBox] Box1052
  AttacherType = Attacher::AttachEngine3D
  AttachmentOffset = pos=(-20.7,18.635,1.55) rot=(0,1,0;0.785398rad)
  BaseFeature = -> Fillet303
  Height = 0.375
  Length = 0.23
  MapMode = 5
  Placement = pos=(-20.7,18.635,1.55) rot=(0,1,0;0.785398rad)
  Support = -> [XY_Plane113]
  Width = 0.23
FEATURE [PartDesign::SubtractiveCylinder] Cylinder212
  Angle = 360
  AttacherType = Attacher::AttachEngine3D
  AttachmentOffset = pos=(-20.271,18.635,1.4056) rot=(-1,0,0;1.5708rad)
  BaseFeature = -> Box1052
  Height = 0.23
  MapMode = 5
  Placement = pos=(-20.271,18.635,1.4056) rot=(-1,0,0;1.5708rad)
  Radius = 0.23
  Support = -> [XY_Plane113]
FEATURE [PartDesign::AdditiveBox] Box1044
  AttacherType = Attacher::AttachEngine3D
  AttachmentOffset = pos=(-20.1,18.635,1.635) rot=(0,0,1;0rad)
  BaseFeature = -> Cylinder212
  Height = 0.265
  Length = 0.23
  MapMode = 5
  Placement = pos=(-20.1,18.635,1.635) rot=(0,0,1;0rad)
  Support = -> [XY_Plane113]
  Width = 0.23
FEATURE [PartDesign::Body] Body112  label="pin112"
  Group = -> [Box1058,Box1056,Box1014,Box1035,Box1027,Fillet314,Fillet332,Box1049,Cylinder217,Box1046,Box1047,Fillet303,Box1052,Cylinder212,Box1044]
  Origin = -> Origin118
  Placement = pos=(0,-5.5,0) rot=(0,0,1;0rad)
  Tip = -> Box1044
FEATURE [PartDesign::SubtractiveBox] Box1061
  AttacherType = Attacher::AttachEngine3D
  AttachmentOffset = pos=(-21.19,18.635,-0.12) rot=(0,-1,0;0.15708rad)
  BaseFeature = -> Box1054
  Height = 0.12
  Length = 0.725
  MapMode = 5
  Placement = pos=(-21.19,18.635,-0.12) rot=(0,-1,0;0.15708rad)
  Support = -> [XY_Plane122]
  Width = 0.25
FEATURE [PartDesign::SubtractiveBox] Box998
  AttacherType = Attacher::AttachEngine3D
  AttachmentOffset = pos=(-21.5005,18.625,0.235) rot=(0,-1,0;0.174533rad)
  BaseFeature = -> Box1061
  Height = 0.3
  Length = 0.6605
  MapMode = 5
  Placement = pos=(-21.5005,18.625,0.235) rot=(0,-1,0;0.174533rad)
  Support = -> [XY_Plane122]
  Width = 0.25
FEATURE [PartDesign::Fillet] Fillet333
  Base = -> Box998 [Edge2]
  BaseFeature = -> Box998
  Placement = pos=(-21.5005,18.625,0.235) rot=(0,-1,0;0.174533rad)
  Radius = 0.05
  SupportTransform = false
FEATURE [PartDesign::Fillet] Fillet325
  Base = -> Fillet333 [Edge33]
  BaseFeature = -> Fillet333
  Placement = pos=(-21.5005,18.625,0.235) rot=(0,-1,0;0.174533rad)
  Radius = 0.5
  SupportTransform = false
FEATURE [PartDesign::AdditiveBox] Box1034
  AttacherType = Attacher::AttachEngine3D
  AttachmentOffset = pos=(-21.1,18.635,0.305) rot=(0,1,0;0.785398rad)
  BaseFeature = -> Fillet325
  Height = 0.375
  Length = 0.2
  MapMode = 5
  Placement = pos=(-21.1,18.635,0.305) rot=(0,1,0;0.785398rad)
  Support = -> [XY_Plane122]
  Width = 0.23
FEATURE [PartDesign::SubtractiveCylinder] Cylinder215
  Angle = 360
  AttacherType = Attacher::AttachEngine3D
  AttachmentOffset = pos=(-21.055,18.935,0.52) rot=(1,0,0;1.5708rad)
  BaseFeature = -> Box1034
  Height = 0.375
  MapMode = 5
  Placement = pos=(-21.055,18.935,0.52) rot=(1,0,0;1.5708rad)
  Radius = 0.205
  Support = -> [XY_Plane122]
FEATURE [PartDesign::SubtractiveBox] Box1041
  AttacherType = Attacher::AttachEngine3D
  AttachmentOffset = pos=(-20.95,18.635,0.53) rot=(0,0,1;0rad)
  BaseFeature = -> Cylinder215
  Height = 0.5
  Length = 0.1
  MapMode = 5
  Placement = pos=(-20.95,18.635,0.53) rot=(0,0,1;0rad)
  Support = -> [XY_Plane122]
  Width = 0.23
FEATURE [PartDesign::SubtractiveBox] Box1059
  AttacherType = Attacher::AttachEngine3D
  AttachmentOffset = pos=(-21.15,18.635,0.297) rot=(0,-1,0;0.174533rad)
  BaseFeature = -> Box1041
  Height = 0.115
  Length = 0.115
  MapMode = 5
  Placement = pos=(-21.15,18.635,0.297) rot=(0,-1,0;0.174533rad)
  Support = -> [XY_Plane122]
  Width = 0.23
FEATURE [PartDesign::Fillet] Fillet327
  Base = -> Box1059 [Edge28]
  BaseFeature = -> Box1059
  Placement = pos=(-21.15,18.635,0.297) rot=(0,-1,0;0.174533rad)
  Radius = 0.375
  SupportTransform = false
FEATURE [PartDesign::AdditiveBox] Box1060
  AttacherType = Attacher::AttachEngine3D
  AttachmentOffset = pos=(-20.7,18.635,1.55) rot=(0,1,0;0.785398rad)
  BaseFeature = -> Fillet327
  Height = 0.375
  Length = 0.23
  MapMode = 5
  Placement = pos=(-20.7,18.635,1.55) rot=(0,1,0;0.785398rad)
  Support = -> [XY_Plane122]
  Width = 0.23
FEATURE [PartDesign::SubtractiveCylinder] Cylinder216
  Angle = 360
  AttacherType = Attacher::AttachEngine3D
  AttachmentOffset = pos=(-20.271,18.635,1.4056) rot=(-1,0,0;1.5708rad)
  BaseFeature = -> Box1060
  Height = 0.23
  MapMode = 5
  Placement = pos=(-20.271,18.635,1.4056) rot=(-1,0,0;1.5708rad)
  Radius = 0.23
  Support = -> [XY_Plane122]
FEATURE [PartDesign::AdditiveBox] Box1062
  AttacherType = Attacher::AttachEngine3D
  AttachmentOffset = pos=(-20.1,18.635,1.635) rot=(0,0,1;0rad)
  BaseFeature = -> Cylinder216
  Height = 0.265
  Length = 0.23
  MapMode = 5
  Placement = pos=(-20.1,18.635,1.635) rot=(0,0,1;0rad)
  Support = -> [XY_Plane122]
  Width = 0.23
FEATURE [PartDesign::Body] Body111  label="pin111"
  Group = -> [Box982,Box999,Box1054,Box1061,Box998,Fillet333,Fillet325,Box1034,Cylinder215,Box1041,Box1059,Fillet327,Box1060,Cylinder216,Box1062]
  Origin = -> Origin101
  Placement = pos=(0,-3,0) rot=(0,0,1;0rad)
  Tip = -> Box1062
FEATURE [PartDesign::SubtractiveBox] Box1066
  AttacherType = Attacher::AttachEngine3D
  AttachmentOffset = pos=(-21.5005,18.625,0.235) rot=(0,-1,0;0.174533rad)
  BaseFeature = -> Box1024
  Height = 0.3
  Length = 0.6605
  MapMode = 5
  Placement = pos=(-21.5005,18.625,0.235) rot=(0,-1,0;0.174533rad)
  Support = -> [XY_Plane123]
  Width = 0.25
FEATURE [PartDesign::Fillet] Fillet334
  Base = -> Box1066 [Edge2]
  BaseFeature = -> Box1066
  Placement = pos=(-21.5005,18.625,0.235) rot=(0,-1,0;0.174533rad)
  Radius = 0.05
  SupportTransform = false
FEATURE [PartDesign::Fillet] Fillet313
  Base = -> Fillet334 [Edge33]
  BaseFeature = -> Fillet334
  Placement = pos=(-21.5005,18.625,0.235) rot=(0,-1,0;0.174533rad)
  Radius = 0.5
  SupportTransform = false
FEATURE [PartDesign::AdditiveBox] Box1011
  AttacherType = Attacher::AttachEngine3D
  AttachmentOffset = pos=(-21.1,18.635,0.305) rot=(0,1,0;0.785398rad)
  BaseFeature = -> Fillet313
  Height = 0.375
  Length = 0.2
  MapMode = 5
  Placement = pos=(-21.1,18.635,0.305) rot=(0,1,0;0.785398rad)
  Support = -> [XY_Plane123]
  Width = 0.23
FEATURE [PartDesign::SubtractiveCylinder] Cylinder208
  Angle = 360
  AttacherType = Attacher::AttachEngine3D
  AttachmentOffset = pos=(-21.055,18.935,0.52) rot=(1,0,0;1.5708rad)
  BaseFeature = -> Box1011
  Height = 0.375
  MapMode = 5
  Placement = pos=(-21.055,18.935,0.52) rot=(1,0,0;1.5708rad)
  Radius = 0.205
  Support = -> [XY_Plane123]
FEATURE [PartDesign::SubtractiveBox] Box1010
  AttacherType = Attacher::AttachEngine3D
  AttachmentOffset = pos=(-20.95,18.635,0.53) rot=(0,0,1;0rad)
  BaseFeature = -> Cylinder208
  Height = 0.5
  Length = 0.1
  MapMode = 5
  Placement = pos=(-20.95,18.635,0.53) rot=(0,0,1;0rad)
  Support = -> [XY_Plane123]
  Width = 0.23
FEATURE [PartDesign::SubtractiveBox] Box1038
  AttacherType = Attacher::AttachEngine3D
  AttachmentOffset = pos=(-21.15,18.635,0.297) rot=(0,-1,0;0.174533rad)
  BaseFeature = -> Box1010
  Height = 0.115
  Length = 0.115
  MapMode = 5
  Placement = pos=(-21.15,18.635,0.297) rot=(0,-1,0;0.174533rad)
  Support = -> [XY_Plane123]
  Width = 0.23
FEATURE [PartDesign::Fillet] Fillet330
  Base = -> Box1038 [Edge28]
  BaseFeature = -> Box1038
  Placement = pos=(-21.15,18.635,0.297) rot=(0,-1,0;0.174533rad)
  Radius = 0.375
  SupportTransform = false
FEATURE [PartDesign::AdditiveBox] Box1025
  AttacherType = Attacher::AttachEngine3D
  AttachmentOffset = pos=(-20.7,18.635,1.55) rot=(0,1,0;0.785398rad)
  BaseFeature = -> Fillet330
  Height = 0.375
  Length = 0.23
  MapMode = 5
  Placement = pos=(-20.7,18.635,1.55) rot=(0,1,0;0.785398rad)
  Support = -> [XY_Plane123]
  Width = 0.23
FEATURE [PartDesign::SubtractiveCylinder] Cylinder209
  Angle = 360
  AttacherType = Attacher::AttachEngine3D
  AttachmentOffset = pos=(-20.271,18.635,1.4056) rot=(-1,0,0;1.5708rad)
  BaseFeature = -> Box1025
  Height = 0.23
  MapMode = 5
  Placement = pos=(-20.271,18.635,1.4056) rot=(-1,0,0;1.5708rad)
  Radius = 0.23
  Support = -> [XY_Plane123]
FEATURE [PartDesign::AdditiveBox] Box1028
  AttacherType = Attacher::AttachEngine3D
  AttachmentOffset = pos=(-20.1,18.635,1.635) rot=(0,0,1;0rad)
  BaseFeature = -> Cylinder209
  Height = 0.265
  Length = 0.23
  MapMode = 5
  Placement = pos=(-20.1,18.635,1.635) rot=(0,0,1;0rad)
  Support = -> [XY_Plane123]
  Width = 0.23
FEATURE [PartDesign::Body] Body107  label="pin107"
  Group = -> [Box1050,Box1045,Box1030,Box1024,Box1066,Fillet334,Fillet313,Box1011,Cylinder208,Box1010,Box1038,Fillet330,Box1025,Cylinder209,Box1028]
  Origin = -> Origin108
  Placement = pos=(0,-4.5,0) rot=(0,0,1;0rad)
  Tip = -> Box1028
FEATURE [PartDesign::SubtractiveBox] Box1069
  AttacherType = Attacher::AttachEngine3D
  AttachmentOffset = pos=(-20.5,18.63,0) rot=(0,0,1;0rad)
  BaseFeature = -> Box1004
  Height = 1.635
  Length = 0.5
  MapMode = 5
  Placement = pos=(-20.5,18.63,0) rot=(0,0,1;0rad)
  Support = -> [XY_Plane125]
  Width = 0.25
FEATURE [PartDesign::SubtractiveBox] Box1005
  AttacherType = Attacher::AttachEngine3D
  AttachmentOffset = pos=(-21.19,18.635,-0.12) rot=(0,-1,0;0.15708rad)
  BaseFeature = -> Box1069
  Height = 0.12
  Length = 0.725
  MapMode = 5
  Placement = pos=(-21.19,18.635,-0.12) rot=(0,-1,0;0.15708rad)
  Support = -> [XY_Plane125]
  Width = 0.25
FEATURE [PartDesign::SubtractiveBox] Box990
  AttacherType = Attacher::AttachEngine3D
  AttachmentOffset = pos=(-21.5005,18.625,0.235) rot=(0,-1,0;0.174533rad)
  BaseFeature = -> Box1005
  Height = 0.3
  Length = 0.6605
  MapMode = 5
  Placement = pos=(-21.5005,18.625,0.235) rot=(0,-1,0;0.174533rad)
  Support = -> [XY_Plane125]
  Width = 0.25
FEATURE [PartDesign::Fillet] Fillet323
  Base = -> Box990 [Edge2]
  BaseFeature = -> Box990
  Placement = pos=(-21.5005,18.625,0.235) rot=(0,-1,0;0.174533rad)
  Radius = 0.05
  SupportTransform = false
FEATURE [PartDesign::Fillet] Fillet315
  Base = -> Fillet323 [Edge33]
  BaseFeature = -> Fillet323
  Placement = pos=(-21.5005,18.625,0.235) rot=(0,-1,0;0.174533rad)
  Radius = 0.5
  SupportTransform = false
FEATURE [PartDesign::AdditiveBox] Box1070
  AttacherType = Attacher::AttachEngine3D
  AttachmentOffset = pos=(-21.1,18.635,0.305) rot=(0,1,0;0.785398rad)
  BaseFeature = -> Fillet331
  Height = 0.375
  Length = 0.2
  MapMode = 5
  Placement = pos=(-21.1,18.635,0.305) rot=(0,1,0;0.785398rad)
  Support = -> [XY_Plane120]
  Width = 0.23
FEATURE [PartDesign::SubtractiveCylinder] Cylinder202
  Angle = 360
  AttacherType = Attacher::AttachEngine3D
  AttachmentOffset = pos=(-21.055,18.935,0.52) rot=(1,0,0;1.5708rad)
  BaseFeature = -> Box1070
  Height = 0.375
  MapMode = 5
  Placement = pos=(-21.055,18.935,0.52) rot=(1,0,0;1.5708rad)
  Radius = 0.205
  Support = -> [XY_Plane120]
FEATURE [PartDesign::SubtractiveBox] Box1001
  AttacherType = Attacher::AttachEngine3D
  AttachmentOffset = pos=(-20.95,18.635,0.53) rot=(0,0,1;0rad)
  BaseFeature = -> Cylinder202
  Height = 0.5
  Length = 0.1
  MapMode = 5
  Placement = pos=(-20.95,18.635,0.53) rot=(0,0,1;0rad)
  Support = -> [XY_Plane120]
  Width = 0.23
FEATURE [PartDesign::SubtractiveBox] Box994
  AttacherType = Attacher::AttachEngine3D
  AttachmentOffset = pos=(-21.15,18.635,0.297) rot=(0,-1,0;0.174533rad)
  BaseFeature = -> Box1001
  Height = 0.115
  Length = 0.115
  MapMode = 5
  Placement = pos=(-21.15,18.635,0.297) rot=(0,-1,0;0.174533rad)
  Support = -> [XY_Plane120]
  Width = 0.23
FEATURE [PartDesign::Fillet] Fillet329
  Base = -> Box994 [Edge28]
  BaseFeature = -> Box994
  Placement = pos=(-21.15,18.635,0.297) rot=(0,-1,0;0.174533rad)
  Radius = 0.375
  SupportTransform = false
FEATURE [PartDesign::AdditiveBox] Box997
  AttacherType = Attacher::AttachEngine3D
  AttachmentOffset = pos=(-20.7,18.635,1.55) rot=(0,1,0;0.785398rad)
  BaseFeature = -> Fillet329
  Height = 0.375
  Length = 0.23
  MapMode = 5
  Placement = pos=(-20.7,18.635,1.55) rot=(0,1,0;0.785398rad)
  Support = -> [XY_Plane120]
  Width = 0.23
FEATURE [PartDesign::SubtractiveCylinder] Cylinder203
  Angle = 360
  AttacherType = Attacher::AttachEngine3D
  AttachmentOffset = pos=(-20.271,18.635,1.4056) rot=(-1,0,0;1.5708rad)
  BaseFeature = -> Box997
  Height = 0.23
  MapMode = 5
  Placement = pos=(-20.271,18.635,1.4056) rot=(-1,0,0;1.5708rad)
  Radius = 0.23
  Support = -> [XY_Plane120]
FEATURE [PartDesign::AdditiveBox] Box978
  AttacherType = Attacher::AttachEngine3D
  AttachmentOffset = pos=(-20.1,18.635,1.635) rot=(0,0,1;0rad)
  BaseFeature = -> Cylinder203
  Height = 0.265
  Length = 0.23
  MapMode = 5
  Placement = pos=(-20.1,18.635,1.635) rot=(0,0,1;0rad)
  Support = -> [XY_Plane120]
  Width = 0.23
FEATURE [PartDesign::Body] Body108  label="pin108"
  Group = -> [Box991,Box993,Box1042,Box1002,Box1003,Fillet326,Fillet331,Box1070,Cylinder202,Box1001,Box994,Fillet329,Box997,Cylinder203,Box978]
  Origin = -> Origin116
  Placement = pos=(0,-4,0) rot=(0,0,1;0rad)
  Tip = -> Box978
FEATURE [PartDesign::AdditiveBox] Box1073
  AttacherType = Attacher::AttachEngine3D
  AttachmentOffset = pos=(-21.1,18.635,0.305) rot=(0,1,0;0.785398rad)
  BaseFeature = -> Fillet315
  Height = 0.375
  Length = 0.2
  MapMode = 5
  Placement = pos=(-21.1,18.635,0.305) rot=(0,1,0;0.785398rad)
  Support = -> [XY_Plane125]
  Width = 0.23
FEATURE [PartDesign::SubtractiveCylinder] Cylinder218
  Angle = 360
  AttacherType = Attacher::AttachEngine3D
  AttachmentOffset = pos=(-21.055,18.935,0.52) rot=(1,0,0;1.5708rad)
  BaseFeature = -> Box1073
  Height = 0.375
  MapMode = 5
  Placement = pos=(-21.055,18.935,0.52) rot=(1,0,0;1.5708rad)
  Radius = 0.205
  Support = -> [XY_Plane125]
FEATURE [PartDesign::SubtractiveBox] Box1072
  AttacherType = Attacher::AttachEngine3D
  AttachmentOffset = pos=(-20.95,18.635,0.53) rot=(0,0,1;0rad)
  BaseFeature = -> Cylinder218
  Height = 0.5
  Length = 0.1
  MapMode = 5
  Placement = pos=(-20.95,18.635,0.53) rot=(0,0,1;0rad)
  Support = -> [XY_Plane125]
  Width = 0.23
FEATURE [PartDesign::SubtractiveBox] Box1057
  AttacherType = Attacher::AttachEngine3D
  AttachmentOffset = pos=(-21.15,18.635,0.297) rot=(0,-1,0;0.174533rad)
  BaseFeature = -> Box1072
  Height = 0.115
  Length = 0.115
  MapMode = 5
  Placement = pos=(-21.15,18.635,0.297) rot=(0,-1,0;0.174533rad)
  Support = -> [XY_Plane125]
  Width = 0.23
FEATURE [PartDesign::Fillet] Fillet319
  Base = -> Box1057 [Edge28]
  BaseFeature = -> Box1057
  Placement = pos=(-21.15,18.635,0.297) rot=(0,-1,0;0.174533rad)
  Radius = 0.375
  SupportTransform = false
FEATURE [PartDesign::AdditiveBox] Box1067
  AttacherType = Attacher::AttachEngine3D
  AttachmentOffset = pos=(-20.7,18.635,1.55) rot=(0,1,0;0.785398rad)
  BaseFeature = -> Fillet319
  Height = 0.375
  Length = 0.23
  MapMode = 5
  Placement = pos=(-20.7,18.635,1.55) rot=(0,1,0;0.785398rad)
  Support = -> [XY_Plane125]
  Width = 0.23
FEATURE [PartDesign::SubtractiveCylinder] Cylinder219
  Angle = 360
  AttacherType = Attacher::AttachEngine3D
  AttachmentOffset = pos=(-20.271,18.635,1.4056) rot=(-1,0,0;1.5708rad)
  BaseFeature = -> Box1067
  Height = 0.23
  MapMode = 5
  Placement = pos=(-20.271,18.635,1.4056) rot=(-1,0,0;1.5708rad)
  Radius = 0.23
  Support = -> [XY_Plane125]
FEATURE [PartDesign::AdditiveBox] Box992
  AttacherType = Attacher::AttachEngine3D
  AttachmentOffset = pos=(-20.1,18.635,1.635) rot=(0,0,1;0rad)
  BaseFeature = -> Cylinder219
  Height = 0.265
  Length = 0.23
  MapMode = 5
  Placement = pos=(-20.1,18.635,1.635) rot=(0,0,1;0rad)
  Support = -> [XY_Plane125]
  Width = 0.23
FEATURE [PartDesign::Body] Body106  label="pin106"
  Group = -> [Box996,Box1004,Box1069,Box1005,Box990,Fillet323,Fillet315,Box1073,Cylinder218,Box1072,Box1057,Fillet319,Box1067,Cylinder219,Box992]
  Origin = -> Origin122
  Placement = pos=(0,-3.5,0) rot=(0,0,1;0rad)
  Tip = -> Box992
FEATURE [PartDesign::AdditiveBox] Box1082
  AttacherType = Attacher::AttachEngine3D
  AttachmentOffset = pos=(-21.3,18.635,0) rot=(0,0,1;0rad)
  Height = 1.9
  Length = 1.3
  MapMode = 5
  Placement = pos=(-21.3,18.635,0) rot=(0,0,1;0rad)
  Support = -> [XY_Plane119]
  Width = 0.23
FEATURE [PartDesign::SubtractiveBox] Box1075
  AttacherType = Attacher::AttachEngine3D
  AttachmentOffset = pos=(-21.35,18.635,0.35) rot=(0,0,1;0rad)
  BaseFeature = -> Box1082
  Height = 1.55
  Length = 0.5
  MapMode = 5
  Placement = pos=(-21.35,18.635,0.35) rot=(0,0,1;0rad)
  Support = -> [XY_Plane119]
  Width = 0.23
FEATURE [PartDesign::SubtractiveBox] Box1065
  AttacherType = Attacher::AttachEngine3D
  AttachmentOffset = pos=(-20.5,18.63,0) rot=(0,0,1;0rad)
  BaseFeature = -> Box1075
  Height = 1.635
  Length = 0.5
  MapMode = 5
  Placement = pos=(-20.5,18.63,0) rot=(0,0,1;0rad)
  Support = -> [XY_Plane119]
  Width = 0.25
FEATURE [PartDesign::SubtractiveBox] Box1079
  AttacherType = Attacher::AttachEngine3D
  AttachmentOffset = pos=(-21.19,18.635,-0.12) rot=(0,-1,0;0.15708rad)
  BaseFeature = -> Box1065
  Height = 0.12
  Length = 0.725
  MapMode = 5
  Placement = pos=(-21.19,18.635,-0.12) rot=(0,-1,0;0.15708rad)
  Support = -> [XY_Plane119]
  Width = 0.25
FEATURE [PartDesign::SubtractiveBox] Box1080
  AttacherType = Attacher::AttachEngine3D
  AttachmentOffset = pos=(-21.5005,18.625,0.235) rot=(0,-1,0;0.174533rad)
  BaseFeature = -> Box1079
  Height = 0.3
  Length = 0.6605
  MapMode = 5
  Placement = pos=(-21.5005,18.625,0.235) rot=(0,-1,0;0.174533rad)
  Support = -> [XY_Plane119]
  Width = 0.25
FEATURE [PartDesign::Fillet] Fillet305
  Base = -> Box1080 [Edge2]
  BaseFeature = -> Box1080
  Placement = pos=(-21.5005,18.625,0.235) rot=(0,-1,0;0.174533rad)
  Radius = 0.05
  SupportTransform = false
FEATURE [PartDesign::Fillet] Fillet306
  Base = -> Fillet305 [Edge33]
  BaseFeature = -> Fillet305
  Placement = pos=(-21.5005,18.625,0.235) rot=(0,-1,0;0.174533rad)
  Radius = 0.5
  SupportTransform = false
FEATURE [PartDesign::AdditiveBox] Box1064
  AttacherType = Attacher::AttachEngine3D
  AttachmentOffset = pos=(-21.1,18.635,0.305) rot=(0,1,0;0.785398rad)
  BaseFeature = -> Fillet306
  Height = 0.375
  Length = 0.2
  MapMode = 5
  Placement = pos=(-21.1,18.635,0.305) rot=(0,1,0;0.785398rad)
  Support = -> [XY_Plane119]
  Width = 0.23
FEATURE [PartDesign::SubtractiveCylinder] Cylinder220
  Angle = 360
  AttacherType = Attacher::AttachEngine3D
  AttachmentOffset = pos=(-21.055,18.935,0.52) rot=(1,0,0;1.5708rad)
  BaseFeature = -> Box1064
  Height = 0.375
  MapMode = 5
  Placement = pos=(-21.055,18.935,0.52) rot=(1,0,0;1.5708rad)
  Radius = 0.205
  Support = -> [XY_Plane119]
FEATURE [PartDesign::SubtractiveBox] Box1086
  AttacherType = Attacher::AttachEngine3D
  AttachmentOffset = pos=(-20.95,18.635,0.53) rot=(0,0,1;0rad)
  BaseFeature = -> Cylinder220
  Height = 0.5
  Length = 0.1
  MapMode = 5
  Placement = pos=(-20.95,18.635,0.53) rot=(0,0,1;0rad)
  Support = -> [XY_Plane119]
  Width = 0.23
FEATURE [PartDesign::SubtractiveBox] Box1078
  AttacherType = Attacher::AttachEngine3D
  AttachmentOffset = pos=(-21.15,18.635,0.297) rot=(0,-1,0;0.174533rad)
  BaseFeature = -> Box1086
  Height = 0.115
  Length = 0.115
  MapMode = 5
  Placement = pos=(-21.15,18.635,0.297) rot=(0,-1,0;0.174533rad)
  Support = -> [XY_Plane119]
  Width = 0.23
FEATURE [PartDesign::Fillet] Fillet321
  Base = -> Box1078 [Edge28]
  BaseFeature = -> Box1078
  Placement = pos=(-21.15,18.635,0.297) rot=(0,-1,0;0.174533rad)
  Radius = 0.375
  SupportTransform = false
FEATURE [PartDesign::AdditiveBox] Box1077
  AttacherType = Attacher::AttachEngine3D
  AttachmentOffset = pos=(-20.7,18.635,1.55) rot=(0,1,0;0.785398rad)
  BaseFeature = -> Fillet321
  Height = 0.375
  Length = 0.23
  MapMode = 5
  Placement = pos=(-20.7,18.635,1.55) rot=(0,1,0;0.785398rad)
  Support = -> [XY_Plane119]
  Width = 0.23
FEATURE [PartDesign::SubtractiveCylinder] Cylinder221
  Angle = 360
  AttacherType = Attacher::AttachEngine3D
  AttachmentOffset = pos=(-20.271,18.635,1.4056) rot=(-1,0,0;1.5708rad)
  BaseFeature = -> Box1077
  Height = 0.23
  MapMode = 5
  Placement = pos=(-20.271,18.635,1.4056) rot=(-1,0,0;1.5708rad)
  Radius = 0.23
  Support = -> [XY_Plane119]
FEATURE [PartDesign::AdditiveBox] Box1083
  AttacherType = Attacher::AttachEngine3D
  AttachmentOffset = pos=(-20.1,18.635,1.635) rot=(0,0,1;0rad)
  BaseFeature = -> Cylinder221
  Height = 0.265
  Length = 0.23
  MapMode = 5
  Placement = pos=(-20.1,18.635,1.635) rot=(0,0,1;0rad)
  Support = -> [XY_Plane119]
  Width = 0.23
FEATURE [PartDesign::Body] Body101  label="pin101"
  Group = -> [Box1082,Box1075,Box1065,Box1079,Box1080,Fillet305,Fillet306,Box1064,Cylinder220,Box1086,Box1078,Fillet321,Box1077,Cylinder221,Box1083]
  Origin = -> Origin111
  Placement = pos=(0,-0.5,0) rot=(0,0,1;0rad)
  Tip = -> Box1083
FEATURE [PartDesign::AdditiveBox] Box1106
  AttacherType = Attacher::AttachEngine3D
  AttachmentOffset = pos=(-21.3,18.635,0) rot=(0,0,1;0rad)
  Height = 1.9
  Length = 1.3
  MapMode = 5
  Placement = pos=(-21.3,18.635,0) rot=(0,0,1;0rad)
  Support = -> [XY_Plane098]
  Width = 0.23
FEATURE [PartDesign::SubtractiveBox] Box1091
  AttacherType = Attacher::AttachEngine3D
  AttachmentOffset = pos=(-21.35,18.635,0.35) rot=(0,0,1;0rad)
  BaseFeature = -> Box1106
  Height = 1.55
  Length = 0.5
  MapMode = 5
  Placement = pos=(-21.35,18.635,0.35) rot=(0,0,1;0rad)
  Support = -> [XY_Plane098]
  Width = 0.23
FEATURE [PartDesign::AdditiveBox] Box1110
  AttacherType = Attacher::AttachEngine3D
  AttachmentOffset = pos=(-21.3,18.635,0) rot=(0,0,1;0rad)
  Height = 1.9
  Length = 1.3
  MapMode = 5
  Placement = pos=(-21.3,18.635,0) rot=(0,0,1;0rad)
  Support = -> [XY_Plane112]
  Width = 0.23
FEATURE [PartDesign::SubtractiveBox] Box1093
  AttacherType = Attacher::AttachEngine3D
  AttachmentOffset = pos=(-21.35,18.635,0.35) rot=(0,0,1;0rad)
  BaseFeature = -> Box1110
  Height = 1.55
  Length = 0.5
  MapMode = 5
  Placement = pos=(-21.35,18.635,0.35) rot=(0,0,1;0rad)
  Support = -> [XY_Plane112]
  Width = 0.23
FEATURE [PartDesign::AdditiveBox] Box1117
  AttacherType = Attacher::AttachEngine3D
  AttachmentOffset = pos=(-21.3,18.635,0) rot=(0,0,1;0rad)
  Height = 1.9
  Length = 1.3
  MapMode = 5
  Placement = pos=(-21.3,18.635,0) rot=(0,0,1;0rad)
  Support = -> [XY_Plane133]
  Width = 0.23
FEATURE [PartDesign::SubtractiveBox] Box1125
  AttacherType = Attacher::AttachEngine3D
  AttachmentOffset = pos=(-21.35,18.635,0.35) rot=(0,0,1;0rad)
  BaseFeature = -> Box1117
  Height = 1.55
  Length = 0.5
  MapMode = 5
  Placement = pos=(-21.35,18.635,0.35) rot=(0,0,1;0rad)
  Support = -> [XY_Plane133]
  Width = 0.23
FEATURE [PartDesign::SubtractiveBox] Box1115
  AttacherType = Attacher::AttachEngine3D
  AttachmentOffset = pos=(-20.5,18.63,0) rot=(0,0,1;0rad)
  BaseFeature = -> Box1125
  Height = 1.635
  Length = 0.5
  MapMode = 5
  Placement = pos=(-20.5,18.63,0) rot=(0,0,1;0rad)
  Support = -> [XY_Plane133]
  Width = 0.25
FEATURE [PartDesign::SubtractiveBox] Box1119
  AttacherType = Attacher::AttachEngine3D
  AttachmentOffset = pos=(-21.19,18.635,-0.12) rot=(0,-1,0;0.15708rad)
  BaseFeature = -> Box1115
  Height = 0.12
  Length = 0.725
  MapMode = 5
  Placement = pos=(-21.19,18.635,-0.12) rot=(0,-1,0;0.15708rad)
  Support = -> [XY_Plane133]
  Width = 0.25
FEATURE [PartDesign::SubtractiveBox] Box1124
  AttacherType = Attacher::AttachEngine3D
  AttachmentOffset = pos=(-21.5005,18.625,0.235) rot=(0,-1,0;0.174533rad)
  BaseFeature = -> Box1119
  Height = 0.3
  Length = 0.6605
  MapMode = 5
  Placement = pos=(-21.5005,18.625,0.235) rot=(0,-1,0;0.174533rad)
  Support = -> [XY_Plane133]
  Width = 0.25
FEATURE [PartDesign::AdditiveBox] Box1131
  AttacherType = Attacher::AttachEngine3D
  AttachmentOffset = pos=(-21.3,18.635,0) rot=(0,0,1;0rad)
  Height = 1.9
  Length = 1.3
  MapMode = 5
  Placement = pos=(-21.3,18.635,0) rot=(0,0,1;0rad)
  Support = -> [XY_Plane130]
  Width = 0.23
FEATURE [PartDesign::SubtractiveBox] Box1123
  AttacherType = Attacher::AttachEngine3D
  AttachmentOffset = pos=(-21.35,18.635,0.35) rot=(0,0,1;0rad)
  BaseFeature = -> Box1131
  Height = 1.55
  Length = 0.5
  MapMode = 5
  Placement = pos=(-21.35,18.635,0.35) rot=(0,0,1;0rad)
  Support = -> [XY_Plane130]
  Width = 0.23
FEATURE [PartDesign::SubtractiveBox] Box1111
  AttacherType = Attacher::AttachEngine3D
  AttachmentOffset = pos=(-20.5,18.63,0) rot=(0,0,1;0rad)
  BaseFeature = -> Box1123
  Height = 1.635
  Length = 0.5
  MapMode = 5
  Placement = pos=(-20.5,18.63,0) rot=(0,0,1;0rad)
  Support = -> [XY_Plane130]
  Width = 0.25
FEATURE [PartDesign::SubtractiveBox] Box1113
  AttacherType = Attacher::AttachEngine3D
  AttachmentOffset = pos=(-21.19,18.635,-0.12) rot=(0,-1,0;0.15708rad)
  BaseFeature = -> Box1111
  Height = 0.12
  Length = 0.725
  MapMode = 5
  Placement = pos=(-21.19,18.635,-0.12) rot=(0,-1,0;0.15708rad)
  Support = -> [XY_Plane130]
  Width = 0.25
FEATURE [PartDesign::AdditiveBox] Box1135
  AttacherType = Attacher::AttachEngine3D
  AttachmentOffset = pos=(-21.3,18.635,0) rot=(0,0,1;0rad)
  Height = 1.9
  Length = 1.3
  MapMode = 5
  Placement = pos=(-21.3,18.635,0) rot=(0,0,1;0rad)
  Support = -> [XY_Plane111]
  Width = 0.23
FEATURE [PartDesign::SubtractiveBox] Box1136
  AttacherType = Attacher::AttachEngine3D
  AttachmentOffset = pos=(-21.35,18.635,0.35) rot=(0,0,1;0rad)
  BaseFeature = -> Box1135
  Height = 1.55
  Length = 0.5
  MapMode = 5
  Placement = pos=(-21.35,18.635,0.35) rot=(0,0,1;0rad)
  Support = -> [XY_Plane111]
  Width = 0.23
FEATURE [PartDesign::SubtractiveBox] Box1094
  AttacherType = Attacher::AttachEngine3D
  AttachmentOffset = pos=(-20.5,18.63,0) rot=(0,0,1;0rad)
  BaseFeature = -> Box1136
  Height = 1.635
  Length = 0.5
  MapMode = 5
  Placement = pos=(-20.5,18.63,0) rot=(0,0,1;0rad)
  Support = -> [XY_Plane111]
  Width = 0.25
FEATURE [PartDesign::SubtractiveBox] Box1105
  AttacherType = Attacher::AttachEngine3D
  AttachmentOffset = pos=(-21.19,18.635,-0.12) rot=(0,-1,0;0.15708rad)
  BaseFeature = -> Box1094
  Height = 0.12
  Length = 0.725
  MapMode = 5
  Placement = pos=(-21.19,18.635,-0.12) rot=(0,-1,0;0.15708rad)
  Support = -> [XY_Plane111]
  Width = 0.25
FEATURE [PartDesign::SubtractiveBox] Box1104
  AttacherType = Attacher::AttachEngine3D
  AttachmentOffset = pos=(-21.5005,18.625,0.235) rot=(0,-1,0;0.174533rad)
  BaseFeature = -> Box1105
  Height = 0.3
  Length = 0.6605
  MapMode = 5
  Placement = pos=(-21.5005,18.625,0.235) rot=(0,-1,0;0.174533rad)
  Support = -> [XY_Plane111]
  Width = 0.25
FEATURE [PartDesign::SubtractiveBox] Box1148
  AttacherType = Attacher::AttachEngine3D
  AttachmentOffset = pos=(-20.5,18.63,0) rot=(0,0,1;0rad)
  BaseFeature = -> Box1018
  Height = 1.635
  Length = 0.5
  MapMode = 5
  Placement = pos=(-20.5,18.63,0) rot=(0,0,1;0rad)
  Support = -> [XY_Plane118]
  Width = 0.25
FEATURE [PartDesign::SubtractiveBox] Box1016
  AttacherType = Attacher::AttachEngine3D
  AttachmentOffset = pos=(-21.19,18.635,-0.12) rot=(0,-1,0;0.15708rad)
  BaseFeature = -> Box1148
  Height = 0.12
  Length = 0.725
  MapMode = 5
  Placement = pos=(-21.19,18.635,-0.12) rot=(0,-1,0;0.15708rad)
  Support = -> [XY_Plane118]
  Width = 0.25
FEATURE [PartDesign::SubtractiveBox] Box1013
  AttacherType = Attacher::AttachEngine3D
  AttachmentOffset = pos=(-21.5005,18.625,0.235) rot=(0,-1,0;0.174533rad)
  BaseFeature = -> Box1016
  Height = 0.3
  Length = 0.6605
  MapMode = 5
  Placement = pos=(-21.5005,18.625,0.235) rot=(0,-1,0;0.174533rad)
  Support = -> [XY_Plane118]
  Width = 0.25
FEATURE [PartDesign::Fillet] Fillet307
  Base = -> Box1013 [Edge2]
  BaseFeature = -> Box1013
  Placement = pos=(-21.5005,18.625,0.235) rot=(0,-1,0;0.174533rad)
  Radius = 0.05
  SupportTransform = false
FEATURE [PartDesign::Fillet] Fillet310
  Base = -> Fillet307 [Edge33]
  BaseFeature = -> Fillet307
  Placement = pos=(-21.5005,18.625,0.235) rot=(0,-1,0;0.174533rad)
  Radius = 0.5
  SupportTransform = false
FEATURE [PartDesign::SubtractiveBox] Box1150
  AttacherType = Attacher::AttachEngine3D
  AttachmentOffset = pos=(-20.5,18.63,0) rot=(0,0,1;0rad)
  BaseFeature = -> Box1009
  Height = 1.635
  Length = 0.5
  MapMode = 5
  Placement = pos=(-20.5,18.63,0) rot=(0,0,1;0rad)
  Support = -> [XY_Plane114]
  Width = 0.25
FEATURE [PartDesign::SubtractiveBox] Box995
  AttacherType = Attacher::AttachEngine3D
  AttachmentOffset = pos=(-21.19,18.635,-0.12) rot=(0,-1,0;0.15708rad)
  BaseFeature = -> Box1150
  Height = 0.12
  Length = 0.725
  MapMode = 5
  Placement = pos=(-21.19,18.635,-0.12) rot=(0,-1,0;0.15708rad)
  Support = -> [XY_Plane114]
  Width = 0.25
FEATURE [PartDesign::SubtractiveBox] Box1015
  AttacherType = Attacher::AttachEngine3D
  AttachmentOffset = pos=(-21.5005,18.625,0.235) rot=(0,-1,0;0.174533rad)
  BaseFeature = -> Box995
  Height = 0.3
  Length = 0.6605
  MapMode = 5
  Placement = pos=(-21.5005,18.625,0.235) rot=(0,-1,0;0.174533rad)
  Support = -> [XY_Plane114]
  Width = 0.25
FEATURE [PartDesign::Fillet] Fillet311
  Base = -> Box1015 [Edge2]
  BaseFeature = -> Box1015
  Placement = pos=(-21.5005,18.625,0.235) rot=(0,-1,0;0.174533rad)
  Radius = 0.05
  SupportTransform = false
FEATURE [PartDesign::Fillet] Fillet301
  Base = -> Fillet311 [Edge33]
  BaseFeature = -> Fillet311
  Placement = pos=(-21.5005,18.625,0.235) rot=(0,-1,0;0.174533rad)
  Radius = 0.5
  SupportTransform = false
FEATURE [PartDesign::AdditiveBox] Box1151
  AttacherType = Attacher::AttachEngine3D
  AttachmentOffset = pos=(-21.3,18.635,0) rot=(0,0,1;0rad)
  Height = 1.9
  Length = 1.3
  MapMode = 5
  Placement = pos=(-21.3,18.635,0) rot=(0,0,1;0rad)
  Support = -> [XY_Plane116]
  Width = 0.23
FEATURE [PartDesign::SubtractiveBox] Box1146
  AttacherType = Attacher::AttachEngine3D
  AttachmentOffset = pos=(-21.35,18.635,0.35) rot=(0,0,1;0rad)
  BaseFeature = -> Box1151
  Height = 1.55
  Length = 0.5
  MapMode = 5
  Placement = pos=(-21.35,18.635,0.35) rot=(0,0,1;0rad)
  Support = -> [XY_Plane116]
  Width = 0.23
FEATURE [PartDesign::SubtractiveBox] Box1074
  AttacherType = Attacher::AttachEngine3D
  AttachmentOffset = pos=(-20.5,18.63,0) rot=(0,0,1;0rad)
  BaseFeature = -> Box1146
  Height = 1.635
  Length = 0.5
  MapMode = 5
  Placement = pos=(-20.5,18.63,0) rot=(0,0,1;0rad)
  Support = -> [XY_Plane116]
  Width = 0.25
FEATURE [PartDesign::SubtractiveBox] Box1143
  AttacherType = Attacher::AttachEngine3D
  AttachmentOffset = pos=(-21.19,18.635,-0.12) rot=(0,-1,0;0.15708rad)
  BaseFeature = -> Box1074
  Height = 0.12
  Length = 0.725
  MapMode = 5
  Placement = pos=(-21.19,18.635,-0.12) rot=(0,-1,0;0.15708rad)
  Support = -> [XY_Plane116]
  Width = 0.25
FEATURE [PartDesign::SubtractiveBox] Box1142
  AttacherType = Attacher::AttachEngine3D
  AttachmentOffset = pos=(-21.5005,18.625,0.235) rot=(0,-1,0;0.174533rad)
  BaseFeature = -> Box1143
  Height = 0.3
  Length = 0.6605
  MapMode = 5
  Placement = pos=(-21.5005,18.625,0.235) rot=(0,-1,0;0.174533rad)
  Support = -> [XY_Plane116]
  Width = 0.25
FEATURE [PartDesign::Fillet] Fillet308
  Base = -> Box1142 [Edge2]
  BaseFeature = -> Box1142
  Placement = pos=(-21.5005,18.625,0.235) rot=(0,-1,0;0.174533rad)
  Radius = 0.05
  SupportTransform = false
FEATURE [PartDesign::Fillet] Fillet322
  Base = -> Fillet308 [Edge33]
  BaseFeature = -> Fillet308
  Placement = pos=(-21.5005,18.625,0.235) rot=(0,-1,0;0.174533rad)
  Radius = 0.5
  SupportTransform = false
FEATURE [PartDesign::AdditiveBox] Box1063
  AttacherType = Attacher::AttachEngine3D
  AttachmentOffset = pos=(-21.1,18.635,0.305) rot=(0,1,0;0.785398rad)
  BaseFeature = -> Fillet322
  Height = 0.375
  Length = 0.2
  MapMode = 5
  Placement = pos=(-21.1,18.635,0.305) rot=(0,1,0;0.785398rad)
  Support = -> [XY_Plane116]
  Width = 0.23
FEATURE [PartDesign::SubtractiveCylinder] Cylinder235
  Angle = 360
  AttacherType = Attacher::AttachEngine3D
  AttachmentOffset = pos=(-21.055,18.935,0.52) rot=(1,0,0;1.5708rad)
  BaseFeature = -> Box1063
  Height = 0.375
  MapMode = 5
  Placement = pos=(-21.055,18.935,0.52) rot=(1,0,0;1.5708rad)
  Radius = 0.205
  Support = -> [XY_Plane116]
FEATURE [PartDesign::SubtractiveBox] Box1140
  AttacherType = Attacher::AttachEngine3D
  AttachmentOffset = pos=(-20.95,18.635,0.53) rot=(0,0,1;0rad)
  BaseFeature = -> Cylinder235
  Height = 0.5
  Length = 0.1
  MapMode = 5
  Placement = pos=(-20.95,18.635,0.53) rot=(0,0,1;0rad)
  Support = -> [XY_Plane116]
  Width = 0.23
FEATURE [PartDesign::SubtractiveBox] Box1085
  AttacherType = Attacher::AttachEngine3D
  AttachmentOffset = pos=(-21.15,18.635,0.297) rot=(0,-1,0;0.174533rad)
  BaseFeature = -> Box1140
  Height = 0.115
  Length = 0.115
  MapMode = 5
  Placement = pos=(-21.15,18.635,0.297) rot=(0,-1,0;0.174533rad)
  Support = -> [XY_Plane116]
  Width = 0.23
FEATURE [PartDesign::Fillet] Fillet302
  Base = -> Box1085 [Edge28]
  BaseFeature = -> Box1085
  Placement = pos=(-21.15,18.635,0.297) rot=(0,-1,0;0.174533rad)
  Radius = 0.375
  SupportTransform = false
FEATURE [PartDesign::AdditiveBox] Box1084
  AttacherType = Attacher::AttachEngine3D
  AttachmentOffset = pos=(-20.7,18.635,1.55) rot=(0,1,0;0.785398rad)
  BaseFeature = -> Fillet302
  Height = 0.375
  Length = 0.23
  MapMode = 5
  Placement = pos=(-20.7,18.635,1.55) rot=(0,1,0;0.785398rad)
  Support = -> [XY_Plane116]
  Width = 0.23
FEATURE [PartDesign::SubtractiveCylinder] Cylinder234
  Angle = 360
  AttacherType = Attacher::AttachEngine3D
  AttachmentOffset = pos=(-20.271,18.635,1.4056) rot=(-1,0,0;1.5708rad)
  BaseFeature = -> Box1084
  Height = 0.23
  MapMode = 5
  Placement = pos=(-20.271,18.635,1.4056) rot=(-1,0,0;1.5708rad)
  Radius = 0.23
  Support = -> [XY_Plane116]
FEATURE [PartDesign::AdditiveBox] Box1145
  AttacherType = Attacher::AttachEngine3D
  AttachmentOffset = pos=(-20.1,18.635,1.635) rot=(0,0,1;0rad)
  BaseFeature = -> Cylinder234
  Height = 0.265
  Length = 0.23
  MapMode = 5
  Placement = pos=(-20.1,18.635,1.635) rot=(0,0,1;0rad)
  Support = -> [XY_Plane116]
  Width = 0.23
FEATURE [PartDesign::Body] Body109  label="pin109"
  Group = -> [Box1151,Box1146,Box1074,Box1143,Box1142,Fillet308,Fillet322,Box1063,Cylinder235,Box1140,Box1085,Fillet302,Box1084,Cylinder234,Box1145]
  Origin = -> Origin117
  Placement = pos=(0,-1,0) rot=(0,0,1;0rad)
  Tip = -> Box1145
FEATURE [PartDesign::AdditiveBox] Box1152
  AttacherType = Attacher::AttachEngine3D
  AttachmentOffset = pos=(-21.3,18.635,0) rot=(0,0,1;0rad)
  Height = 1.9
  Length = 1.3
  MapMode = 5
  Placement = pos=(-21.3,18.635,0) rot=(0,0,1;0rad)
  Support = -> [XY_Plane117]
  Width = 0.23
FEATURE [PartDesign::SubtractiveBox] Box1153
  AttacherType = Attacher::AttachEngine3D
  AttachmentOffset = pos=(-21.35,18.635,0.35) rot=(0,0,1;0rad)
  BaseFeature = -> Box1152
  Height = 1.55
  Length = 0.5
  MapMode = 5
  Placement = pos=(-21.35,18.635,0.35) rot=(0,0,1;0rad)
  Support = -> [XY_Plane117]
  Width = 0.23
FEATURE [PartDesign::SubtractiveBox] Box1076
  AttacherType = Attacher::AttachEngine3D
  AttachmentOffset = pos=(-20.5,18.63,0) rot=(0,0,1;0rad)
  BaseFeature = -> Box1153
  Height = 1.635
  Length = 0.5
  MapMode = 5
  Placement = pos=(-20.5,18.63,0) rot=(0,0,1;0rad)
  Support = -> [XY_Plane117]
  Width = 0.25
FEATURE [PartDesign::SubtractiveBox] Box1068
  AttacherType = Attacher::AttachEngine3D
  AttachmentOffset = pos=(-21.19,18.635,-0.12) rot=(0,-1,0;0.15708rad)
  BaseFeature = -> Box1076
  Height = 0.12
  Length = 0.725
  MapMode = 5
  Placement = pos=(-21.19,18.635,-0.12) rot=(0,-1,0;0.15708rad)
  Support = -> [XY_Plane117]
  Width = 0.25
FEATURE [PartDesign::SubtractiveBox] Box1141
  AttacherType = Attacher::AttachEngine3D
  AttachmentOffset = pos=(-21.5005,18.625,0.235) rot=(0,-1,0;0.174533rad)
  BaseFeature = -> Box1068
  Height = 0.3
  Length = 0.6605
  MapMode = 5
  Placement = pos=(-21.5005,18.625,0.235) rot=(0,-1,0;0.174533rad)
  Support = -> [XY_Plane117]
  Width = 0.25
FEATURE [PartDesign::Fillet] Fillet324
  Base = -> Box1141 [Edge2]
  BaseFeature = -> Box1141
  Placement = pos=(-21.5005,18.625,0.235) rot=(0,-1,0;0.174533rad)
  Radius = 0.05
  SupportTransform = false
FEATURE [PartDesign::Fillet] Fillet299
  Base = -> Fillet324 [Edge33]
  BaseFeature = -> Fillet324
  Placement = pos=(-21.5005,18.625,0.235) rot=(0,-1,0;0.174533rad)
  Radius = 0.5
  SupportTransform = false
FEATURE [PartDesign::AdditiveBox] Box1000
  AttacherType = Attacher::AttachEngine3D
  AttachmentOffset = pos=(-21.1,18.635,0.305) rot=(0,1,0;0.785398rad)
  BaseFeature = -> Fillet299
  Height = 0.375
  Length = 0.2
  MapMode = 5
  Placement = pos=(-21.1,18.635,0.305) rot=(0,1,0;0.785398rad)
  Support = -> [XY_Plane117]
  Width = 0.23
FEATURE [PartDesign::SubtractiveCylinder] Cylinder214
  Angle = 360
  AttacherType = Attacher::AttachEngine3D
  AttachmentOffset = pos=(-21.055,18.935,0.52) rot=(1,0,0;1.5708rad)
  BaseFeature = -> Box1000
  Height = 0.375
  MapMode = 5
  Placement = pos=(-21.055,18.935,0.52) rot=(1,0,0;1.5708rad)
  Radius = 0.205
  Support = -> [XY_Plane117]
FEATURE [PartDesign::SubtractiveBox] Box1051
  AttacherType = Attacher::AttachEngine3D
  AttachmentOffset = pos=(-20.95,18.635,0.53) rot=(0,0,1;0rad)
  BaseFeature = -> Cylinder214
  Height = 0.5
  Length = 0.1
  MapMode = 5
  Placement = pos=(-20.95,18.635,0.53) rot=(0,0,1;0rad)
  Support = -> [XY_Plane117]
  Width = 0.23
FEATURE [PartDesign::SubtractiveBox] Box1036
  AttacherType = Attacher::AttachEngine3D
  AttachmentOffset = pos=(-21.15,18.635,0.297) rot=(0,-1,0;0.174533rad)
  BaseFeature = -> Box1051
  Height = 0.115
  Length = 0.115
  MapMode = 5
  Placement = pos=(-21.15,18.635,0.297) rot=(0,-1,0;0.174533rad)
  Support = -> [XY_Plane117]
  Width = 0.23
FEATURE [PartDesign::Fillet] Fillet328
  Base = -> Box1036 [Edge28]
  BaseFeature = -> Box1036
  Placement = pos=(-21.15,18.635,0.297) rot=(0,-1,0;0.174533rad)
  Radius = 0.375
  SupportTransform = false
FEATURE [PartDesign::AdditiveBox] Box1071
  AttacherType = Attacher::AttachEngine3D
  AttachmentOffset = pos=(-20.7,18.635,1.55) rot=(0,1,0;0.785398rad)
  BaseFeature = -> Fillet328
  Height = 0.375
  Length = 0.23
  MapMode = 5
  Placement = pos=(-20.7,18.635,1.55) rot=(0,1,0;0.785398rad)
  Support = -> [XY_Plane117]
  Width = 0.23
FEATURE [PartDesign::SubtractiveCylinder] Cylinder213
  Angle = 360
  AttacherType = Attacher::AttachEngine3D
  AttachmentOffset = pos=(-20.271,18.635,1.4056) rot=(-1,0,0;1.5708rad)
  BaseFeature = -> Box1071
  Height = 0.23
  MapMode = 5
  Placement = pos=(-20.271,18.635,1.4056) rot=(-1,0,0;1.5708rad)
  Radius = 0.23
  Support = -> [XY_Plane117]
FEATURE [PartDesign::AdditiveBox] Box1081
  AttacherType = Attacher::AttachEngine3D
  AttachmentOffset = pos=(-20.1,18.635,1.635) rot=(0,0,1;0rad)
  BaseFeature = -> Cylinder213
  Height = 0.265
  Length = 0.23
  MapMode = 5
  Placement = pos=(-20.1,18.635,1.635) rot=(0,0,1;0rad)
  Support = -> [XY_Plane117]
  Width = 0.23
FEATURE [PartDesign::Body] Body103  label="pin103"
  Group = -> [Box1152,Box1153,Box1076,Box1068,Box1141,Fillet324,Fillet299,Box1000,Cylinder214,Box1051,Box1036,Fillet328,Box1071,Cylinder213,Box1081]
  Origin = -> Origin110
  Tip = -> Box1081
FEATURE [PartDesign::AdditiveBox] Box1154
  AttacherType = Attacher::AttachEngine3D
  AttachmentOffset = pos=(-21.1,18.635,0.305) rot=(0,1,0;0.785398rad)
  BaseFeature = -> Fillet301
  Height = 0.375
  Length = 0.2
  MapMode = 5
  Placement = pos=(-21.1,18.635,0.305) rot=(0,1,0;0.785398rad)
  Support = -> [XY_Plane114]
  Width = 0.23
FEATURE [PartDesign::SubtractiveCylinder] Cylinder206
  Angle = 360
  AttacherType = Attacher::AttachEngine3D
  AttachmentOffset = pos=(-21.055,18.935,0.52) rot=(1,0,0;1.5708rad)
  BaseFeature = -> Box1154
  Height = 0.375
  MapMode = 5
  Placement = pos=(-21.055,18.935,0.52) rot=(1,0,0;1.5708rad)
  Radius = 0.205
  Support = -> [XY_Plane114]
FEATURE [PartDesign::SubtractiveBox] Box1017
  AttacherType = Attacher::AttachEngine3D
  AttachmentOffset = pos=(-20.95,18.635,0.53) rot=(0,0,1;0rad)
  BaseFeature = -> Cylinder206
  Height = 0.5
  Length = 0.1
  MapMode = 5
  Placement = pos=(-20.95,18.635,0.53) rot=(0,0,1;0rad)
  Support = -> [XY_Plane114]
  Width = 0.23
FEATURE [PartDesign::SubtractiveBox] Box1021
  AttacherType = Attacher::AttachEngine3D
  AttachmentOffset = pos=(-21.15,18.635,0.297) rot=(0,-1,0;0.174533rad)
  BaseFeature = -> Box1017
  Height = 0.115
  Length = 0.115
  MapMode = 5
  Placement = pos=(-21.15,18.635,0.297) rot=(0,-1,0;0.174533rad)
  Support = -> [XY_Plane114]
  Width = 0.23
FEATURE [PartDesign::Fillet] Fillet300
  Base = -> Box1021 [Edge28]
  BaseFeature = -> Box1021
  Placement = pos=(-21.15,18.635,0.297) rot=(0,-1,0;0.174533rad)
  Radius = 0.375
  SupportTransform = false
FEATURE [PartDesign::AdditiveBox] Box1008
  AttacherType = Attacher::AttachEngine3D
  AttachmentOffset = pos=(-20.7,18.635,1.55) rot=(0,1,0;0.785398rad)
  BaseFeature = -> Fillet300
  Height = 0.375
  Length = 0.23
  MapMode = 5
  Placement = pos=(-20.7,18.635,1.55) rot=(0,1,0;0.785398rad)
  Support = -> [XY_Plane114]
  Width = 0.23
FEATURE [PartDesign::SubtractiveCylinder] Cylinder205
  Angle = 360
  AttacherType = Attacher::AttachEngine3D
  AttachmentOffset = pos=(-20.271,18.635,1.4056) rot=(-1,0,0;1.5708rad)
  BaseFeature = -> Box1008
  Height = 0.23
  MapMode = 5
  Placement = pos=(-20.271,18.635,1.4056) rot=(-1,0,0;1.5708rad)
  Radius = 0.23
  Support = -> [XY_Plane114]
FEATURE [PartDesign::AdditiveBox] Box1012
  AttacherType = Attacher::AttachEngine3D
  AttachmentOffset = pos=(-20.1,18.635,1.635) rot=(0,0,1;0rad)
  BaseFeature = -> Cylinder205
  Height = 0.265
  Length = 0.23
  MapMode = 5
  Placement = pos=(-20.1,18.635,1.635) rot=(0,0,1;0rad)
  Support = -> [XY_Plane114]
  Width = 0.23
FEATURE [PartDesign::Body] Body104  label="pin104"
  Group = -> [Box1031,Box1009,Box1150,Box995,Box1015,Fillet311,Fillet301,Box1154,Cylinder206,Box1017,Box1021,Fillet300,Box1008,Cylinder205,Box1012]
  Origin = -> Origin120
  Placement = pos=(0,-2.5,0) rot=(0,0,1;0rad)
  Tip = -> Box1012
FEATURE [PartDesign::AdditiveBox] Box1157
  AttacherType = Attacher::AttachEngine3D
  AttachmentOffset = pos=(-21.3,18.635,0) rot=(0,0,1;0rad)
  Height = 1.9
  Length = 1.3
  MapMode = 5
  Placement = pos=(-21.3,18.635,0) rot=(0,0,1;0rad)
  Support = -> [XY_Plane132]
  Width = 0.23
FEATURE [PartDesign::SubtractiveBox] Box1158
  AttacherType = Attacher::AttachEngine3D
  AttachmentOffset = pos=(-20.5,18.63,0) rot=(0,0,1;0rad)
  BaseFeature = -> Box1023
  Height = 1.635
  Length = 0.5
  MapMode = 5
  Placement = pos=(-20.5,18.63,0) rot=(0,0,1;0rad)
  Support = -> [XY_Plane115]
  Width = 0.25
FEATURE [PartDesign::SubtractiveBox] Box1144
  AttacherType = Attacher::AttachEngine3D
  AttachmentOffset = pos=(-21.19,18.635,-0.12) rot=(0,-1,0;0.15708rad)
  BaseFeature = -> Box1158
  Height = 0.12
  Length = 0.725
  MapMode = 5
  Placement = pos=(-21.19,18.635,-0.12) rot=(0,-1,0;0.15708rad)
  Support = -> [XY_Plane115]
  Width = 0.25
FEATURE [PartDesign::SubtractiveBox] Box1022
  AttacherType = Attacher::AttachEngine3D
  AttachmentOffset = pos=(-21.5005,18.625,0.235) rot=(0,-1,0;0.174533rad)
  BaseFeature = -> Box1144
  Height = 0.3
  Length = 0.6605
  MapMode = 5
  Placement = pos=(-21.5005,18.625,0.235) rot=(0,-1,0;0.174533rad)
  Support = -> [XY_Plane115]
  Width = 0.25
FEATURE [PartDesign::Fillet] Fillet316
  Base = -> Box1022 [Edge2]
  BaseFeature = -> Box1022
  Placement = pos=(-21.5005,18.625,0.235) rot=(0,-1,0;0.174533rad)
  Radius = 0.05
  SupportTransform = false
FEATURE [PartDesign::Fillet] Fillet309
  Base = -> Fillet316 [Edge33]
  BaseFeature = -> Fillet316
  Placement = pos=(-21.5005,18.625,0.235) rot=(0,-1,0;0.174533rad)
  Radius = 0.5
  SupportTransform = false
FEATURE [PartDesign::SubtractiveBox] Box1159
  AttacherType = Attacher::AttachEngine3D
  AttachmentOffset = pos=(-21.35,18.635,0.35) rot=(0,0,1;0rad)
  BaseFeature = -> Box1157
  Height = 1.55
  Length = 0.5
  MapMode = 5
  Placement = pos=(-21.35,18.635,0.35) rot=(0,0,1;0rad)
  Support = -> [XY_Plane132]
  Width = 0.23
FEATURE [PartDesign::SubtractiveBox] Box1127
  AttacherType = Attacher::AttachEngine3D
  AttachmentOffset = pos=(-20.5,18.63,0) rot=(0,0,1;0rad)
  BaseFeature = -> Box1159
  Height = 1.635
  Length = 0.5
  MapMode = 5
  Placement = pos=(-20.5,18.63,0) rot=(0,0,1;0rad)
  Support = -> [XY_Plane132]
  Width = 0.25
FEATURE [PartDesign::AdditiveBox] Box1160
  AttacherType = Attacher::AttachEngine3D
  AttachmentOffset = pos=(-21.3,18.635,0) rot=(0,0,1;0rad)
  Height = 1.9
  Length = 1.3
  MapMode = 5
  Placement = pos=(-21.3,18.635,0) rot=(0,0,1;0rad)
  Support = -> [XY_Plane135]
  Width = 0.23
FEATURE [PartDesign::AdditiveBox] Box1163
  AttacherType = Attacher::AttachEngine3D
  AttachmentOffset = pos=(-21.1,18.635,0.305) rot=(0,1,0;0.785398rad)
  BaseFeature = -> Fillet310
  Height = 0.375
  Length = 0.2
  MapMode = 5
  Placement = pos=(-21.1,18.635,0.305) rot=(0,1,0;0.785398rad)
  Support = -> [XY_Plane118]
  Width = 0.23
FEATURE [PartDesign::SubtractiveCylinder] Cylinder236
  Angle = 360
  AttacherType = Attacher::AttachEngine3D
  AttachmentOffset = pos=(-21.055,18.935,0.52) rot=(1,0,0;1.5708rad)
  BaseFeature = -> Box1163
  Height = 0.375
  MapMode = 5
  Placement = pos=(-21.055,18.935,0.52) rot=(1,0,0;1.5708rad)
  Radius = 0.205
  Support = -> [XY_Plane118]
FEATURE [PartDesign::SubtractiveBox] Box1020
  AttacherType = Attacher::AttachEngine3D
  AttachmentOffset = pos=(-20.95,18.635,0.53) rot=(0,0,1;0rad)
  BaseFeature = -> Cylinder236
  Height = 0.5
  Length = 0.1
  MapMode = 5
  Placement = pos=(-20.95,18.635,0.53) rot=(0,0,1;0rad)
  Support = -> [XY_Plane118]
  Width = 0.23
FEATURE [PartDesign::SubtractiveBox] Box1006
  AttacherType = Attacher::AttachEngine3D
  AttachmentOffset = pos=(-21.15,18.635,0.297) rot=(0,-1,0;0.174533rad)
  BaseFeature = -> Box1020
  Height = 0.115
  Length = 0.115
  MapMode = 5
  Placement = pos=(-21.15,18.635,0.297) rot=(0,-1,0;0.174533rad)
  Support = -> [XY_Plane118]
  Width = 0.23
FEATURE [PartDesign::Fillet] Fillet304
  Base = -> Box1006 [Edge28]
  BaseFeature = -> Box1006
  Placement = pos=(-21.15,18.635,0.297) rot=(0,-1,0;0.174533rad)
  Radius = 0.375
  SupportTransform = false
FEATURE [PartDesign::AdditiveBox] Box1147
  AttacherType = Attacher::AttachEngine3D
  AttachmentOffset = pos=(-20.7,18.635,1.55) rot=(0,1,0;0.785398rad)
  BaseFeature = -> Fillet304
  Height = 0.375
  Length = 0.23
  MapMode = 5
  Placement = pos=(-20.7,18.635,1.55) rot=(0,1,0;0.785398rad)
  Support = -> [XY_Plane118]
  Width = 0.23
FEATURE [PartDesign::SubtractiveCylinder] Cylinder207
  Angle = 360
  AttacherType = Attacher::AttachEngine3D
  AttachmentOffset = pos=(-20.271,18.635,1.4056) rot=(-1,0,0;1.5708rad)
  BaseFeature = -> Box1147
  Height = 0.23
  MapMode = 5
  Placement = pos=(-20.271,18.635,1.4056) rot=(-1,0,0;1.5708rad)
  Radius = 0.23
  Support = -> [XY_Plane118]
FEATURE [PartDesign::AdditiveBox] Box1019
  AttacherType = Attacher::AttachEngine3D
  AttachmentOffset = pos=(-20.1,18.635,1.635) rot=(0,0,1;0rad)
  BaseFeature = -> Cylinder207
  Height = 0.265
  Length = 0.23
  MapMode = 5
  Placement = pos=(-20.1,18.635,1.635) rot=(0,0,1;0rad)
  Support = -> [XY_Plane118]
  Width = 0.23
FEATURE [PartDesign::Body] Body102  label="pin102"
  Group = -> [Box1007,Box1018,Box1148,Box1016,Box1013,Fillet307,Fillet310,Box1163,Cylinder236,Box1020,Box1006,Fillet304,Box1147,Cylinder207,Box1019]
  Origin = -> Origin112
  Placement = pos=(0,-2,0) rot=(0,0,1;0rad)
  Tip = -> Box1019
FEATURE [PartDesign::AdditiveBox] Box1165
  AttacherType = Attacher::AttachEngine3D
  AttachmentOffset = pos=(-21.1,18.635,0.305) rot=(0,1,0;0.785398rad)
  BaseFeature = -> Fillet309
  Height = 0.375
  Length = 0.2
  MapMode = 5
  Placement = pos=(-21.1,18.635,0.305) rot=(0,1,0;0.785398rad)
  Support = -> [XY_Plane115]
  Width = 0.23
FEATURE [PartDesign::SubtractiveCylinder] Cylinder233
  Angle = 360
  AttacherType = Attacher::AttachEngine3D
  AttachmentOffset = pos=(-21.055,18.935,0.52) rot=(1,0,0;1.5708rad)
  BaseFeature = -> Box1165
  Height = 0.375
  MapMode = 5
  Placement = pos=(-21.055,18.935,0.52) rot=(1,0,0;1.5708rad)
  Radius = 0.205
  Support = -> [XY_Plane115]
FEATURE [PartDesign::SubtractiveBox] Box1149
  AttacherType = Attacher::AttachEngine3D
  AttachmentOffset = pos=(-20.95,18.635,0.53) rot=(0,0,1;0rad)
  BaseFeature = -> Cylinder233
  Height = 0.5
  Length = 0.1
  MapMode = 5
  Placement = pos=(-20.95,18.635,0.53) rot=(0,0,1;0rad)
  Support = -> [XY_Plane115]
  Width = 0.23
FEATURE [PartDesign::SubtractiveBox] Box1155
  AttacherType = Attacher::AttachEngine3D
  AttachmentOffset = pos=(-21.15,18.635,0.297) rot=(0,-1,0;0.174533rad)
  BaseFeature = -> Box1149
  Height = 0.115
  Length = 0.115
  MapMode = 5
  Placement = pos=(-21.15,18.635,0.297) rot=(0,-1,0;0.174533rad)
  Support = -> [XY_Plane115]
  Width = 0.23
FEATURE [PartDesign::Fillet] Fillet317
  Base = -> Box1155 [Edge28]
  BaseFeature = -> Box1155
  Placement = pos=(-21.15,18.635,0.297) rot=(0,-1,0;0.174533rad)
  Radius = 0.375
  SupportTransform = false
FEATURE [PartDesign::AdditiveBox] Box1164
  AttacherType = Attacher::AttachEngine3D
  AttachmentOffset = pos=(-20.7,18.635,1.55) rot=(0,1,0;0.785398rad)
  BaseFeature = -> Fillet317
  Height = 0.375
  Length = 0.23
  MapMode = 5
  Placement = pos=(-20.7,18.635,1.55) rot=(0,1,0;0.785398rad)
  Support = -> [XY_Plane115]
  Width = 0.23
FEATURE [PartDesign::SubtractiveCylinder] Cylinder204
  Angle = 360
  AttacherType = Attacher::AttachEngine3D
  AttachmentOffset = pos=(-20.271,18.635,1.4056) rot=(-1,0,0;1.5708rad)
  BaseFeature = -> Box1164
  Height = 0.23
  MapMode = 5
  Placement = pos=(-20.271,18.635,1.4056) rot=(-1,0,0;1.5708rad)
  Radius = 0.23
  Support = -> [XY_Plane115]
FEATURE [PartDesign::AdditiveBox] Box1167
  AttacherType = Attacher::AttachEngine3D
  AttachmentOffset = pos=(-20.1,18.635,1.635) rot=(0,0,1;0rad)
  BaseFeature = -> Cylinder204
  Height = 0.265
  Length = 0.23
  MapMode = 5
  Placement = pos=(-20.1,18.635,1.635) rot=(0,0,1;0rad)
  Support = -> [XY_Plane115]
  Width = 0.23
FEATURE [PartDesign::Body] Body105  label="pin105"
  Group = -> [Box1029,Box1023,Box1158,Box1144,Box1022,Fillet316,Fillet309,Box1165,Cylinder233,Box1149,Box1155,Fillet317,Box1164,Cylinder204,Box1167]
  Origin = -> Origin115
  Placement = pos=(0,-1.5,0) rot=(0,0,1;0rad)
  Tip = -> Box1167
FEATURE [App::Part] Part007  label="Pin-set007"
  Group = -> [Body103,Body101,Body109,Body105,Body102,Body104,Body111,Body106,Body108,Body107,Body110,Body112]
  Origin = -> Origin100
  Placement = pos=(0,-12,0) rot=(0,0,1;0rad)
FEATURE [PartDesign::AdditiveBox] Box1168
  AttacherType = Attacher::AttachEngine3D
  AttachmentOffset = pos=(-21.3,18.635,0) rot=(0,0,1;0rad)
  Height = 1.9
  Length = 1.3
  MapMode = 5
  Placement = pos=(-21.3,18.635,0) rot=(0,0,1;0rad)
  Support = -> [XY_Plane134]
  Width = 0.23
FEATURE [PartDesign::SubtractiveBox] Box1172
  AttacherType = Attacher::AttachEngine3D
  AttachmentOffset = pos=(-21.19,18.635,-0.12) rot=(0,-1,0;0.15708rad)
  BaseFeature = -> Box1127
  Height = 0.12
  Length = 0.725
  MapMode = 5
  Placement = pos=(-21.19,18.635,-0.12) rot=(0,-1,0;0.15708rad)
  Support = -> [XY_Plane132]
  Width = 0.25
FEATURE [PartDesign::SubtractiveBox] Box1174
  AttacherType = Attacher::AttachEngine3D
  AttachmentOffset = pos=(-21.5005,18.625,0.235) rot=(0,-1,0;0.174533rad)
  BaseFeature = -> Box1172
  Height = 0.3
  Length = 0.6605
  MapMode = 5
  Placement = pos=(-21.5005,18.625,0.235) rot=(0,-1,0;0.174533rad)
  Support = -> [XY_Plane132]
  Width = 0.25
FEATURE [PartDesign::SubtractiveBox] Box1177
  AttacherType = Attacher::AttachEngine3D
  AttachmentOffset = pos=(-21.35,18.635,0.35) rot=(0,0,1;0rad)
  BaseFeature = -> Box1160
  Height = 1.55
  Length = 0.5
  MapMode = 5
  Placement = pos=(-21.35,18.635,0.35) rot=(0,0,1;0rad)
  Support = -> [XY_Plane135]
  Width = 0.23
FEATURE [PartDesign::AdditiveBox] Box1178
  AttacherType = Attacher::AttachEngine3D
  AttachmentOffset = pos=(-21.3,18.635,0) rot=(0,0,1;0rad)
  Height = 1.9
  Length = 1.3
  MapMode = 5
  Placement = pos=(-21.3,18.635,0) rot=(0,0,1;0rad)
  Support = -> [XY_Plane127]
  Width = 0.23
FEATURE [PartDesign::SubtractiveBox] Box1102
  AttacherType = Attacher::AttachEngine3D
  AttachmentOffset = pos=(-21.35,18.635,0.35) rot=(0,0,1;0rad)
  BaseFeature = -> Box1178
  Height = 1.55
  Length = 0.5
  MapMode = 5
  Placement = pos=(-21.35,18.635,0.35) rot=(0,0,1;0rad)
  Support = -> [XY_Plane127]
  Width = 0.23
FEATURE [PartDesign::SubtractiveBox] Box1180
  AttacherType = Attacher::AttachEngine3D
  AttachmentOffset = pos=(-21.35,18.635,0.35) rot=(0,0,1;0rad)
  BaseFeature = -> Box1168
  Height = 1.55
  Length = 0.5
  MapMode = 5
  Placement = pos=(-21.35,18.635,0.35) rot=(0,0,1;0rad)
  Support = -> [XY_Plane134]
  Width = 0.23
FEATURE [PartDesign::SubtractiveBox] Box1133
  AttacherType = Attacher::AttachEngine3D
  AttachmentOffset = pos=(-20.5,18.63,0) rot=(0,0,1;0rad)
  BaseFeature = -> Box1180
  Height = 1.635
  Length = 0.5
  MapMode = 5
  Placement = pos=(-20.5,18.63,0) rot=(0,0,1;0rad)
  Support = -> [XY_Plane134]
  Width = 0.25
FEATURE [PartDesign::Fillet] Fillet348
  Base = -> Box1104 [Edge2]
  BaseFeature = -> Box1104
  Placement = pos=(-21.5005,18.625,0.235) rot=(0,-1,0;0.174533rad)
  Radius = 0.05
  SupportTransform = false
FEATURE [PartDesign::Fillet] Fillet356
  Base = -> Box1124 [Edge2]
  BaseFeature = -> Box1124
  Placement = pos=(-21.5005,18.625,0.235) rot=(0,-1,0;0.174533rad)
  Radius = 0.05
  SupportTransform = false
FEATURE [PartDesign::Fillet] Fillet338
  Base = -> Fillet356 [Edge33]
  BaseFeature = -> Fillet356
  Placement = pos=(-21.5005,18.625,0.235) rot=(0,-1,0;0.174533rad)
  Radius = 0.5
  SupportTransform = false
FEATURE [PartDesign::AdditiveBox] Box1103
  AttacherType = Attacher::AttachEngine3D
  AttachmentOffset = pos=(-21.1,18.635,0.305) rot=(0,1,0;0.785398rad)
  BaseFeature = -> Fillet338
  Height = 0.375
  Length = 0.2
  MapMode = 5
  Placement = pos=(-21.1,18.635,0.305) rot=(0,1,0;0.785398rad)
  Support = -> [XY_Plane133]
  Width = 0.23
FEATURE [PartDesign::SubtractiveCylinder] Cylinder226
  Angle = 360
  AttacherType = Attacher::AttachEngine3D
  AttachmentOffset = pos=(-21.055,18.935,0.52) rot=(1,0,0;1.5708rad)
  BaseFeature = -> Box1103
  Height = 0.375
  MapMode = 5
  Placement = pos=(-21.055,18.935,0.52) rot=(1,0,0;1.5708rad)
  Radius = 0.205
  Support = -> [XY_Plane133]
FEATURE [PartDesign::SubtractiveBox] Box1134
  AttacherType = Attacher::AttachEngine3D
  AttachmentOffset = pos=(-20.95,18.635,0.53) rot=(0,0,1;0rad)
  BaseFeature = -> Cylinder226
  Height = 0.5
  Length = 0.1
  MapMode = 5
  Placement = pos=(-20.95,18.635,0.53) rot=(0,0,1;0rad)
  Support = -> [XY_Plane133]
  Width = 0.23
FEATURE [PartDesign::SubtractiveBox] Box1109
  AttacherType = Attacher::AttachEngine3D
  AttachmentOffset = pos=(-21.15,18.635,0.297) rot=(0,-1,0;0.174533rad)
  BaseFeature = -> Box1134
  Height = 0.115
  Length = 0.115
  MapMode = 5
  Placement = pos=(-21.15,18.635,0.297) rot=(0,-1,0;0.174533rad)
  Support = -> [XY_Plane133]
  Width = 0.23
FEATURE [PartDesign::Fillet] Fillet344
  Base = -> Box1109 [Edge28]
  BaseFeature = -> Box1109
  Placement = pos=(-21.15,18.635,0.297) rot=(0,-1,0;0.174533rad)
  Radius = 0.375
  SupportTransform = false
FEATURE [PartDesign::AdditiveBox] Box1118
  AttacherType = Attacher::AttachEngine3D
  AttachmentOffset = pos=(-20.7,18.635,1.55) rot=(0,1,0;0.785398rad)
  BaseFeature = -> Fillet344
  Height = 0.375
  Length = 0.23
  MapMode = 5
  Placement = pos=(-20.7,18.635,1.55) rot=(0,1,0;0.785398rad)
  Support = -> [XY_Plane133]
  Width = 0.23
FEATURE [PartDesign::SubtractiveCylinder] Cylinder224
  Angle = 360
  AttacherType = Attacher::AttachEngine3D
  AttachmentOffset = pos=(-20.271,18.635,1.4056) rot=(-1,0,0;1.5708rad)
  BaseFeature = -> Box1118
  Height = 0.23
  MapMode = 5
  Placement = pos=(-20.271,18.635,1.4056) rot=(-1,0,0;1.5708rad)
  Radius = 0.23
  Support = -> [XY_Plane133]
FEATURE [PartDesign::AdditiveBox] Box1128
  AttacherType = Attacher::AttachEngine3D
  AttachmentOffset = pos=(-20.1,18.635,1.635) rot=(0,0,1;0rad)
  BaseFeature = -> Cylinder224
  Height = 0.265
  Length = 0.23
  MapMode = 5
  Placement = pos=(-20.1,18.635,1.635) rot=(0,0,1;0rad)
  Support = -> [XY_Plane133]
  Width = 0.23
FEATURE [PartDesign::Fillet] Fillet358
  Base = -> Box1174 [Edge2]
  BaseFeature = -> Box1174
  Placement = pos=(-21.5005,18.625,0.235) rot=(0,-1,0;0.174533rad)
  Radius = 0.05
  SupportTransform = false
FEATURE [PartDesign::Fillet] Fillet361
  Base = -> Fillet358 [Edge33]
  BaseFeature = -> Fillet358
  Placement = pos=(-21.5005,18.625,0.235) rot=(0,-1,0;0.174533rad)
  Radius = 0.5
  SupportTransform = false
FEATURE [PartDesign::Body] Body124  label="pin124"
  Group = -> [Box1117,Box1125,Box1115,Box1119,Box1124,Fillet356,Fillet338,Box1103,Cylinder226,Box1134,Box1109,Fillet344,Box1118,Cylinder224,Box1128]
  Origin = -> Origin124
  Placement = pos=(0,-5,0) rot=(0,0,1;0rad)
  Tip = -> Box1128
FEATURE [PartDesign::Fillet] Fillet367
  Base = -> Fillet348 [Edge33]
  BaseFeature = -> Fillet348
  Placement = pos=(-21.5005,18.625,0.235) rot=(0,-1,0;0.174533rad)
  Radius = 0.5
  SupportTransform = false
FEATURE [PartDesign::AdditiveBox] Box1130
  AttacherType = Attacher::AttachEngine3D
  AttachmentOffset = pos=(-21.1,18.635,0.305) rot=(0,1,0;0.785398rad)
  BaseFeature = -> Fillet367
  Height = 0.375
  Length = 0.2
  MapMode = 5
  Placement = pos=(-21.1,18.635,0.305) rot=(0,1,0;0.785398rad)
  Support = -> [XY_Plane111]
  Width = 0.23
FEATURE [PartDesign::SubtractiveCylinder] Cylinder232
  Angle = 360
  AttacherType = Attacher::AttachEngine3D
  AttachmentOffset = pos=(-21.055,18.935,0.52) rot=(1,0,0;1.5708rad)
  BaseFeature = -> Box1130
  Height = 0.375
  MapMode = 5
  Placement = pos=(-21.055,18.935,0.52) rot=(1,0,0;1.5708rad)
  Radius = 0.205
  Support = -> [XY_Plane111]
FEATURE [PartDesign::SubtractiveBox] Box1126
  AttacherType = Attacher::AttachEngine3D
  AttachmentOffset = pos=(-20.95,18.635,0.53) rot=(0,0,1;0rad)
  BaseFeature = -> Cylinder232
  Height = 0.5
  Length = 0.1
  MapMode = 5
  Placement = pos=(-20.95,18.635,0.53) rot=(0,0,1;0rad)
  Support = -> [XY_Plane111]
  Width = 0.23
FEATURE [PartDesign::SubtractiveBox] Box1122
  AttacherType = Attacher::AttachEngine3D
  AttachmentOffset = pos=(-21.15,18.635,0.297) rot=(0,-1,0;0.174533rad)
  BaseFeature = -> Box1126
  Height = 0.115
  Length = 0.115
  MapMode = 5
  Placement = pos=(-21.15,18.635,0.297) rot=(0,-1,0;0.174533rad)
  Support = -> [XY_Plane111]
  Width = 0.23
FEATURE [PartDesign::Fillet] Fillet349
  Base = -> Box1122 [Edge28]
  BaseFeature = -> Box1122
  Placement = pos=(-21.15,18.635,0.297) rot=(0,-1,0;0.174533rad)
  Radius = 0.375
  SupportTransform = false
FEATURE [PartDesign::AdditiveBox] Box1132
  AttacherType = Attacher::AttachEngine3D
  AttachmentOffset = pos=(-20.7,18.635,1.55) rot=(0,1,0;0.785398rad)
  BaseFeature = -> Fillet349
  Height = 0.375
  Length = 0.23
  MapMode = 5
  Placement = pos=(-20.7,18.635,1.55) rot=(0,1,0;0.785398rad)
  Support = -> [XY_Plane111]
  Width = 0.23
FEATURE [PartDesign::SubtractiveCylinder] Cylinder229
  Angle = 360
  AttacherType = Attacher::AttachEngine3D
  AttachmentOffset = pos=(-20.271,18.635,1.4056) rot=(-1,0,0;1.5708rad)
  BaseFeature = -> Box1132
  Height = 0.23
  MapMode = 5
  Placement = pos=(-20.271,18.635,1.4056) rot=(-1,0,0;1.5708rad)
  Radius = 0.23
  Support = -> [XY_Plane111]
FEATURE [PartDesign::AdditiveBox] Box1129
  AttacherType = Attacher::AttachEngine3D
  AttachmentOffset = pos=(-20.1,18.635,1.635) rot=(0,0,1;0rad)
  BaseFeature = -> Cylinder229
  Height = 0.265
  Length = 0.23
  MapMode = 5
  Placement = pos=(-20.1,18.635,1.635) rot=(0,0,1;0rad)
  Support = -> [XY_Plane111]
  Width = 0.23
FEATURE [PartDesign::Body] Body123  label="pin123"
  Group = -> [Box1135,Box1136,Box1094,Box1105,Box1104,Fillet348,Fillet367,Box1130,Cylinder232,Box1126,Box1122,Fillet349,Box1132,Cylinder229,Box1129]
  Origin = -> Origin128
  Placement = pos=(0,-5.5,0) rot=(0,0,1;0rad)
  Tip = -> Box1129
FEATURE [PartDesign::SubtractiveBox] Box1183
  AttacherType = Attacher::AttachEngine3D
  AttachmentOffset = pos=(-20.5,18.63,0) rot=(0,0,1;0rad)
  BaseFeature = -> Box900
  Height = 1.635
  Length = 0.5
  MapMode = 5
  Placement = pos=(-20.5,18.63,0) rot=(0,0,1;0rad)
  Support = -> [XY_Plane102]
  Width = 0.25
FEATURE [PartDesign::SubtractiveBox] Box902
  AttacherType = Attacher::AttachEngine3D
  AttachmentOffset = pos=(-21.19,18.635,-0.12) rot=(0,-1,0;0.15708rad)
  BaseFeature = -> Box1183
  Height = 0.12
  Length = 0.725
  MapMode = 5
  Placement = pos=(-21.19,18.635,-0.12) rot=(0,-1,0;0.15708rad)
  Support = -> [XY_Plane102]
  Width = 0.25
FEATURE [PartDesign::SubtractiveBox] Box903
  AttacherType = Attacher::AttachEngine3D
  AttachmentOffset = pos=(-21.5005,18.625,0.235) rot=(0,-1,0;0.174533rad)
  BaseFeature = -> Box902
  Height = 0.3
  Length = 0.6605
  MapMode = 5
  Placement = pos=(-21.5005,18.625,0.235) rot=(0,-1,0;0.174533rad)
  Support = -> [XY_Plane102]
  Width = 0.25
FEATURE [PartDesign::Fillet] Fillet272
  Base = -> Box903 [Edge2]
  BaseFeature = -> Box903
  Placement = pos=(-21.5005,18.625,0.235) rot=(0,-1,0;0.174533rad)
  Radius = 0.05
  SupportTransform = false
FEATURE [PartDesign::Fillet] Fillet273
  Base = -> Fillet272 [Edge33]
  BaseFeature = -> Fillet272
  Placement = pos=(-21.5005,18.625,0.235) rot=(0,-1,0;0.174533rad)
  Radius = 0.5
  SupportTransform = false
FEATURE [PartDesign::SubtractiveBox] Box1186
  AttacherType = Attacher::AttachEngine3D
  AttachmentOffset = pos=(-20.5,18.63,0) rot=(0,0,1;0rad)
  BaseFeature = -> Box909
  Height = 1.635
  Length = 0.5
  MapMode = 5
  Placement = pos=(-20.5,18.63,0) rot=(0,0,1;0rad)
  Support = -> [XY_Plane100]
  Width = 0.25
FEATURE [PartDesign::SubtractiveBox] Box898
  AttacherType = Attacher::AttachEngine3D
  AttachmentOffset = pos=(-21.19,18.635,-0.12) rot=(0,-1,0;0.15708rad)
  BaseFeature = -> Box1186
  Height = 0.12
  Length = 0.725
  MapMode = 5
  Placement = pos=(-21.19,18.635,-0.12) rot=(0,-1,0;0.15708rad)
  Support = -> [XY_Plane100]
  Width = 0.25
FEATURE [PartDesign::SubtractiveBox] Box911
  AttacherType = Attacher::AttachEngine3D
  AttachmentOffset = pos=(-21.5005,18.625,0.235) rot=(0,-1,0;0.174533rad)
  BaseFeature = -> Box898
  Height = 0.3
  Length = 0.6605
  MapMode = 5
  Placement = pos=(-21.5005,18.625,0.235) rot=(0,-1,0;0.174533rad)
  Support = -> [XY_Plane100]
  Width = 0.25
FEATURE [PartDesign::Fillet] Fillet274
  Base = -> Box911 [Edge2]
  BaseFeature = -> Box911
  Placement = pos=(-21.5005,18.625,0.235) rot=(0,-1,0;0.174533rad)
  Radius = 0.05
  SupportTransform = false
FEATURE [PartDesign::Fillet] Fillet275
  Base = -> Fillet274 [Edge33]
  BaseFeature = -> Fillet274
  Placement = pos=(-21.5005,18.625,0.235) rot=(0,-1,0;0.174533rad)
  Radius = 0.5
  SupportTransform = false
FEATURE [PartDesign::AdditiveBox] Box1181
  AttacherType = Attacher::AttachEngine3D
  AttachmentOffset = pos=(-21.1,18.635,0.305) rot=(0,1,0;0.785398rad)
  BaseFeature = -> Fillet275
  Height = 0.375
  Length = 0.2
  MapMode = 5
  Placement = pos=(-21.1,18.635,0.305) rot=(0,1,0;0.785398rad)
  Support = -> [XY_Plane100]
  Width = 0.23
FEATURE [PartDesign::SubtractiveCylinder] Cylinder184
  Angle = 360
  AttacherType = Attacher::AttachEngine3D
  AttachmentOffset = pos=(-21.055,18.935,0.52) rot=(1,0,0;1.5708rad)
  BaseFeature = -> Box1181
  Height = 0.375
  MapMode = 5
  Placement = pos=(-21.055,18.935,0.52) rot=(1,0,0;1.5708rad)
  Radius = 0.205
  Support = -> [XY_Plane100]
FEATURE [PartDesign::SubtractiveBox] Box901
  AttacherType = Attacher::AttachEngine3D
  AttachmentOffset = pos=(-20.95,18.635,0.53) rot=(0,0,1;0rad)
  BaseFeature = -> Cylinder184
  Height = 0.5
  Length = 0.1
  MapMode = 5
  Placement = pos=(-20.95,18.635,0.53) rot=(0,0,1;0rad)
  Support = -> [XY_Plane100]
  Width = 0.23
FEATURE [PartDesign::SubtractiveBox] Box908
  AttacherType = Attacher::AttachEngine3D
  AttachmentOffset = pos=(-21.15,18.635,0.297) rot=(0,-1,0;0.174533rad)
  BaseFeature = -> Box901
  Height = 0.115
  Length = 0.115
  MapMode = 5
  Placement = pos=(-21.15,18.635,0.297) rot=(0,-1,0;0.174533rad)
  Support = -> [XY_Plane100]
  Width = 0.23
FEATURE [PartDesign::Fillet] Fillet231
  Base = -> Box908 [Edge28]
  BaseFeature = -> Box908
  Placement = pos=(-21.15,18.635,0.297) rot=(0,-1,0;0.174533rad)
  Radius = 0.375
  SupportTransform = false
FEATURE [PartDesign::AdditiveBox] Box907
  AttacherType = Attacher::AttachEngine3D
  AttachmentOffset = pos=(-20.7,18.635,1.55) rot=(0,1,0;0.785398rad)
  BaseFeature = -> Fillet231
  Height = 0.375
  Length = 0.23
  MapMode = 5
  Placement = pos=(-20.7,18.635,1.55) rot=(0,1,0;0.785398rad)
  Support = -> [XY_Plane100]
  Width = 0.23
FEATURE [PartDesign::SubtractiveCylinder] Cylinder183
  Angle = 360
  AttacherType = Attacher::AttachEngine3D
  AttachmentOffset = pos=(-20.271,18.635,1.4056) rot=(-1,0,0;1.5708rad)
  BaseFeature = -> Box907
  Height = 0.23
  MapMode = 5
  Placement = pos=(-20.271,18.635,1.4056) rot=(-1,0,0;1.5708rad)
  Radius = 0.23
  Support = -> [XY_Plane100]
FEATURE [PartDesign::AdditiveBox] Box899
  AttacherType = Attacher::AttachEngine3D
  AttachmentOffset = pos=(-20.1,18.635,1.635) rot=(0,0,1;0rad)
  BaseFeature = -> Cylinder183
  Height = 0.265
  Length = 0.23
  MapMode = 5
  Placement = pos=(-20.1,18.635,1.635) rot=(0,0,1;0rad)
  Support = -> [XY_Plane100]
  Width = 0.23
FEATURE [PartDesign::Body] Body093  label="pin093"
  Group = -> [Box918,Box909,Box1186,Box898,Box911,Fillet274,Fillet275,Box1181,Cylinder184,Box901,Box908,Fillet231,Box907,Cylinder183,Box899]
  Origin = -> Origin109
  Placement = pos=(0,-2.5,0) rot=(0,0,1;0rad)
  Tip = -> Box899
FEATURE [PartDesign::AdditiveBox] Box1188
  AttacherType = Attacher::AttachEngine3D
  AttachmentOffset = pos=(-21.1,18.635,0.305) rot=(0,1,0;0.785398rad)
  BaseFeature = -> Fillet273
  Height = 0.375
  Length = 0.2
  MapMode = 5
  Placement = pos=(-21.1,18.635,0.305) rot=(0,1,0;0.785398rad)
  Support = -> [XY_Plane102]
  Width = 0.23
FEATURE [PartDesign::SubtractiveCylinder] Cylinder243
  Angle = 360
  AttacherType = Attacher::AttachEngine3D
  AttachmentOffset = pos=(-21.055,18.935,0.52) rot=(1,0,0;1.5708rad)
  BaseFeature = -> Box1188
  Height = 0.375
  MapMode = 5
  Placement = pos=(-21.055,18.935,0.52) rot=(1,0,0;1.5708rad)
  Radius = 0.205
  Support = -> [XY_Plane102]
FEATURE [PartDesign::SubtractiveBox] Box906
  AttacherType = Attacher::AttachEngine3D
  AttachmentOffset = pos=(-20.95,18.635,0.53) rot=(0,0,1;0rad)
  BaseFeature = -> Cylinder243
  Height = 0.5
  Length = 0.1
  MapMode = 5
  Placement = pos=(-20.95,18.635,0.53) rot=(0,0,1;0rad)
  Support = -> [XY_Plane102]
  Width = 0.23
FEATURE [PartDesign::SubtractiveBox] Box874
  AttacherType = Attacher::AttachEngine3D
  AttachmentOffset = pos=(-21.15,18.635,0.297) rot=(0,-1,0;0.174533rad)
  BaseFeature = -> Box906
  Height = 0.115
  Length = 0.115
  MapMode = 5
  Placement = pos=(-21.15,18.635,0.297) rot=(0,-1,0;0.174533rad)
  Support = -> [XY_Plane102]
  Width = 0.23
FEATURE [PartDesign::Fillet] Fillet267
  Base = -> Box874 [Edge28]
  BaseFeature = -> Box874
  Placement = pos=(-21.15,18.635,0.297) rot=(0,-1,0;0.174533rad)
  Radius = 0.375
  SupportTransform = false
FEATURE [PartDesign::AdditiveBox] Box1182
  AttacherType = Attacher::AttachEngine3D
  AttachmentOffset = pos=(-20.7,18.635,1.55) rot=(0,1,0;0.785398rad)
  BaseFeature = -> Fillet267
  Height = 0.375
  Length = 0.23
  MapMode = 5
  Placement = pos=(-20.7,18.635,1.55) rot=(0,1,0;0.785398rad)
  Support = -> [XY_Plane102]
  Width = 0.23
FEATURE [PartDesign::SubtractiveCylinder] Cylinder185
  Angle = 360
  AttacherType = Attacher::AttachEngine3D
  AttachmentOffset = pos=(-20.271,18.635,1.4056) rot=(-1,0,0;1.5708rad)
  BaseFeature = -> Box1182
  Height = 0.23
  MapMode = 5
  Placement = pos=(-20.271,18.635,1.4056) rot=(-1,0,0;1.5708rad)
  Radius = 0.23
  Support = -> [XY_Plane102]
FEATURE [PartDesign::AdditiveBox] Box905
  AttacherType = Attacher::AttachEngine3D
  AttachmentOffset = pos=(-20.1,18.635,1.635) rot=(0,0,1;0rad)
  BaseFeature = -> Cylinder185
  Height = 0.265
  Length = 0.23
  MapMode = 5
  Placement = pos=(-20.1,18.635,1.635) rot=(0,0,1;0rad)
  Support = -> [XY_Plane102]
  Width = 0.23
FEATURE [PartDesign::Body] Body089  label="pin089"
  Group = -> [Box904,Box900,Box1183,Box902,Box903,Fillet272,Fillet273,Box1188,Cylinder243,Box906,Box874,Fillet267,Box1182,Cylinder185,Box905]
  Origin = -> Origin102
  Placement = pos=(0,-2,0) rot=(0,0,1;0rad)
  Tip = -> Box905
FEATURE [PartDesign::SubtractiveBox] Box1192
  AttacherType = Attacher::AttachEngine3D
  AttachmentOffset = pos=(-20.5,18.63,0) rot=(0,0,1;0rad)
  BaseFeature = -> Box915
  Height = 1.635
  Length = 0.5
  MapMode = 5
  Placement = pos=(-20.5,18.63,0) rot=(0,0,1;0rad)
  Support = -> [XY_Plane097]
  Width = 0.25
FEATURE [PartDesign::SubtractiveBox] Box1187
  AttacherType = Attacher::AttachEngine3D
  AttachmentOffset = pos=(-21.19,18.635,-0.12) rot=(0,-1,0;0.15708rad)
  BaseFeature = -> Box1192
  Height = 0.12
  Length = 0.725
  MapMode = 5
  Placement = pos=(-21.19,18.635,-0.12) rot=(0,-1,0;0.15708rad)
  Support = -> [XY_Plane097]
  Width = 0.25
FEATURE [PartDesign::SubtractiveBox] Box912
  AttacherType = Attacher::AttachEngine3D
  AttachmentOffset = pos=(-21.5005,18.625,0.235) rot=(0,-1,0;0.174533rad)
  BaseFeature = -> Box1187
  Height = 0.3
  Length = 0.6605
  MapMode = 5
  Placement = pos=(-21.5005,18.625,0.235) rot=(0,-1,0;0.174533rad)
  Support = -> [XY_Plane097]
  Width = 0.25
FEATURE [PartDesign::Fillet] Fillet281
  Base = -> Box912 [Edge2]
  BaseFeature = -> Box912
  Placement = pos=(-21.5005,18.625,0.235) rot=(0,-1,0;0.174533rad)
  Radius = 0.05
  SupportTransform = false
FEATURE [PartDesign::Fillet] Fillet271
  Base = -> Fillet281 [Edge33]
  BaseFeature = -> Fillet281
  Placement = pos=(-21.5005,18.625,0.235) rot=(0,-1,0;0.174533rad)
  Radius = 0.5
  SupportTransform = false
FEATURE [PartDesign::AdditiveBox] Box1190
  AttacherType = Attacher::AttachEngine3D
  AttachmentOffset = pos=(-21.1,18.635,0.305) rot=(0,1,0;0.785398rad)
  BaseFeature = -> Fillet271
  Height = 0.375
  Length = 0.2
  MapMode = 5
  Placement = pos=(-21.1,18.635,0.305) rot=(0,1,0;0.785398rad)
  Support = -> [XY_Plane097]
  Width = 0.23
FEATURE [PartDesign::SubtractiveCylinder] Cylinder242
  Angle = 360
  AttacherType = Attacher::AttachEngine3D
  AttachmentOffset = pos=(-21.055,18.935,0.52) rot=(1,0,0;1.5708rad)
  BaseFeature = -> Box1190
  Height = 0.375
  MapMode = 5
  Placement = pos=(-21.055,18.935,0.52) rot=(1,0,0;1.5708rad)
  Radius = 0.205
  Support = -> [XY_Plane097]
FEATURE [PartDesign::SubtractiveBox] Box1185
  AttacherType = Attacher::AttachEngine3D
  AttachmentOffset = pos=(-20.95,18.635,0.53) rot=(0,0,1;0rad)
  BaseFeature = -> Cylinder242
  Height = 0.5
  Length = 0.1
  MapMode = 5
  Placement = pos=(-20.95,18.635,0.53) rot=(0,0,1;0rad)
  Support = -> [XY_Plane097]
  Width = 0.23
FEATURE [PartDesign::SubtractiveBox] Box1184
  AttacherType = Attacher::AttachEngine3D
  AttachmentOffset = pos=(-21.15,18.635,0.297) rot=(0,-1,0;0.174533rad)
  BaseFeature = -> Box1185
  Height = 0.115
  Length = 0.115
  MapMode = 5
  Placement = pos=(-21.15,18.635,0.297) rot=(0,-1,0;0.174533rad)
  Support = -> [XY_Plane097]
  Width = 0.23
FEATURE [PartDesign::Fillet] Fillet279
  Base = -> Box1184 [Edge28]
  BaseFeature = -> Box1184
  Placement = pos=(-21.15,18.635,0.297) rot=(0,-1,0;0.174533rad)
  Radius = 0.375
  SupportTransform = false
FEATURE [PartDesign::AdditiveBox] Box1189
  AttacherType = Attacher::AttachEngine3D
  AttachmentOffset = pos=(-20.7,18.635,1.55) rot=(0,1,0;0.785398rad)
  BaseFeature = -> Fillet279
  Height = 0.375
  Length = 0.23
  MapMode = 5
  Placement = pos=(-20.7,18.635,1.55) rot=(0,1,0;0.785398rad)
  Support = -> [XY_Plane097]
  Width = 0.23
FEATURE [PartDesign::SubtractiveCylinder] Cylinder160
  Angle = 360
  AttacherType = Attacher::AttachEngine3D
  AttachmentOffset = pos=(-20.271,18.635,1.4056) rot=(-1,0,0;1.5708rad)
  BaseFeature = -> Box1189
  Height = 0.23
  MapMode = 5
  Placement = pos=(-20.271,18.635,1.4056) rot=(-1,0,0;1.5708rad)
  Radius = 0.23
  Support = -> [XY_Plane097]
FEATURE [PartDesign::AdditiveBox] Box1191
  AttacherType = Attacher::AttachEngine3D
  AttachmentOffset = pos=(-20.1,18.635,1.635) rot=(0,0,1;0rad)
  BaseFeature = -> Cylinder160
  Height = 0.265
  Length = 0.23
  MapMode = 5
  Placement = pos=(-20.1,18.635,1.635) rot=(0,0,1;0rad)
  Support = -> [XY_Plane097]
  Width = 0.23
FEATURE [PartDesign::Body] Body091  label="pin091"
  Group = -> [Box924,Box915,Box1192,Box1187,Box912,Fillet281,Fillet271,Box1190,Cylinder242,Box1185,Box1184,Fillet279,Box1189,Cylinder160,Box1191]
  Origin = -> Origin105
  Placement = pos=(0,-1.5,0) rot=(0,0,1;0rad)
  Tip = -> Box1191
FEATURE [App::Part] Part008  label="Pin-set008"
  Group = -> [Body092,Body090,Body094,Body091,Body089,Body093,Body098,Body099,Body095,Body096,Body097,Body100]
  Origin = -> Origin113
  Placement = pos=(0,-6,0) rot=(0,0,1;0rad)
FEATURE [PartDesign::SubtractiveBox] Box1193
  AttacherType = Attacher::AttachEngine3D
  AttachmentOffset = pos=(-21.35,18.635,0.35) rot=(0,0,1;0rad)
  BaseFeature = -> Box897
  Height = 1.55
  Length = 0.5
  MapMode = 5
  Placement = pos=(-21.35,18.635,0.35) rot=(0,0,1;0rad)
  Support = -> [XY_Plane086]
  Width = 0.23
FEATURE [PartDesign::SubtractiveBox] Box871
  AttacherType = Attacher::AttachEngine3D
  AttachmentOffset = pos=(-20.5,18.63,0) rot=(0,0,1;0rad)
  BaseFeature = -> Box1193
  Height = 1.635
  Length = 0.5
  MapMode = 5
  Placement = pos=(-20.5,18.63,0) rot=(0,0,1;0rad)
  Support = -> [XY_Plane086]
  Width = 0.25
FEATURE [PartDesign::SubtractiveBox] Box873
  AttacherType = Attacher::AttachEngine3D
  AttachmentOffset = pos=(-21.19,18.635,-0.12) rot=(0,-1,0;0.15708rad)
  BaseFeature = -> Box871
  Height = 0.12
  Length = 0.725
  MapMode = 5
  Placement = pos=(-21.19,18.635,-0.12) rot=(0,-1,0;0.15708rad)
  Support = -> [XY_Plane086]
  Width = 0.25
FEATURE [PartDesign::SubtractiveBox] Box894
  AttacherType = Attacher::AttachEngine3D
  AttachmentOffset = pos=(-21.5005,18.625,0.235) rot=(0,-1,0;0.174533rad)
  BaseFeature = -> Box873
  Height = 0.3
  Length = 0.6605
  MapMode = 5
  Placement = pos=(-21.5005,18.625,0.235) rot=(0,-1,0;0.174533rad)
  Support = -> [XY_Plane086]
  Width = 0.25
FEATURE [PartDesign::Fillet] Fillet244
  Base = -> Box894 [Edge2]
  BaseFeature = -> Box894
  Placement = pos=(-21.5005,18.625,0.235) rot=(0,-1,0;0.174533rad)
  Radius = 0.05
  SupportTransform = false
FEATURE [PartDesign::Fillet] Fillet228
  Base = -> Fillet244 [Edge33]
  BaseFeature = -> Fillet244
  Placement = pos=(-21.5005,18.625,0.235) rot=(0,-1,0;0.174533rad)
  Radius = 0.5
  SupportTransform = false
FEATURE [PartDesign::AdditiveBox] Box794
  AttacherType = Attacher::AttachEngine3D
  AttachmentOffset = pos=(-21.1,18.635,0.305) rot=(0,1,0;0.785398rad)
  BaseFeature = -> Fillet228
  Height = 0.375
  Length = 0.2
  MapMode = 5
  Placement = pos=(-21.1,18.635,0.305) rot=(0,1,0;0.785398rad)
  Support = -> [XY_Plane086]
  Width = 0.23
FEATURE [PartDesign::SubtractiveCylinder] Cylinder171
  Angle = 360
  AttacherType = Attacher::AttachEngine3D
  AttachmentOffset = pos=(-21.055,18.935,0.52) rot=(1,0,0;1.5708rad)
  BaseFeature = -> Box794
  Height = 0.375
  MapMode = 5
  Placement = pos=(-21.055,18.935,0.52) rot=(1,0,0;1.5708rad)
  Radius = 0.205
  Support = -> [XY_Plane086]
FEATURE [PartDesign::SubtractiveBox] Box848
  AttacherType = Attacher::AttachEngine3D
  AttachmentOffset = pos=(-20.95,18.635,0.53) rot=(0,0,1;0rad)
  BaseFeature = -> Cylinder171
  Height = 0.5
  Length = 0.1
  MapMode = 5
  Placement = pos=(-20.95,18.635,0.53) rot=(0,0,1;0rad)
  Support = -> [XY_Plane086]
  Width = 0.23
FEATURE [PartDesign::SubtractiveBox] Box847
  AttacherType = Attacher::AttachEngine3D
  AttachmentOffset = pos=(-21.15,18.635,0.297) rot=(0,-1,0;0.174533rad)
  BaseFeature = -> Box848
  Height = 0.115
  Length = 0.115
  MapMode = 5
  Placement = pos=(-21.15,18.635,0.297) rot=(0,-1,0;0.174533rad)
  Support = -> [XY_Plane086]
  Width = 0.23
FEATURE [PartDesign::Fillet] Fillet371
  Base = -> Box847 [Edge28]
  BaseFeature = -> Box847
  Placement = pos=(-21.15,18.635,0.297) rot=(0,-1,0;0.174533rad)
  Radius = 0.375
  SupportTransform = false
FEATURE [PartDesign::AdditiveBox] Box875
  AttacherType = Attacher::AttachEngine3D
  AttachmentOffset = pos=(-20.7,18.635,1.55) rot=(0,1,0;0.785398rad)
  BaseFeature = -> Fillet371
  Height = 0.375
  Length = 0.23
  MapMode = 5
  Placement = pos=(-20.7,18.635,1.55) rot=(0,1,0;0.785398rad)
  Support = -> [XY_Plane086]
  Width = 0.23
FEATURE [PartDesign::SubtractiveCylinder] Cylinder176
  Angle = 360
  AttacherType = Attacher::AttachEngine3D
  AttachmentOffset = pos=(-20.271,18.635,1.4056) rot=(-1,0,0;1.5708rad)
  BaseFeature = -> Box875
  Height = 0.23
  MapMode = 5
  Placement = pos=(-20.271,18.635,1.4056) rot=(-1,0,0;1.5708rad)
  Radius = 0.23
  Support = -> [XY_Plane086]
FEATURE [PartDesign::AdditiveBox] Box881
  AttacherType = Attacher::AttachEngine3D
  AttachmentOffset = pos=(-20.1,18.635,1.635) rot=(0,0,1;0rad)
  BaseFeature = -> Cylinder176
  Height = 0.265
  Length = 0.23
  MapMode = 5
  Placement = pos=(-20.1,18.635,1.635) rot=(0,0,1;0rad)
  Support = -> [XY_Plane086]
  Width = 0.23
FEATURE [PartDesign::Body] Body077  label="pin077"
  Group = -> [Box897,Box1193,Box871,Box873,Box894,Fillet244,Fillet228,Box794,Cylinder171,Box848,Box847,Fillet371,Box875,Cylinder176,Box881]
  Origin = -> Origin085
  Tip = -> Box881
FEATURE [App::Part] Part010  label="Pin-set009"
  Group = -> [Body077,Body078,Body079,Body080,Body081,Body082,Body083,Body084,Body085,Body086,Body087,Body088]
  Origin = -> Origin099
FEATURE [PartDesign::AdditiveBox] Box1197
  AttacherType = Attacher::AttachEngine3D
  AttachmentOffset = pos=(-21.1,18.635,0.305) rot=(0,1,0;0.785398rad)
  BaseFeature = -> Fillet361
  Height = 0.375
  Length = 0.2
  MapMode = 5
  Placement = pos=(-21.1,18.635,0.305) rot=(0,1,0;0.785398rad)
  Support = -> [XY_Plane132]
  Width = 0.23
FEATURE [PartDesign::SubtractiveCylinder] Cylinder238
  Angle = 360
  AttacherType = Attacher::AttachEngine3D
  AttachmentOffset = pos=(-21.055,18.935,0.52) rot=(1,0,0;1.5708rad)
  BaseFeature = -> Box1197
  Height = 0.375
  MapMode = 5
  Placement = pos=(-21.055,18.935,0.52) rot=(1,0,0;1.5708rad)
  Radius = 0.205
  Support = -> [XY_Plane132]
FEATURE [PartDesign::SubtractiveBox] Box1173
  AttacherType = Attacher::AttachEngine3D
  AttachmentOffset = pos=(-20.95,18.635,0.53) rot=(0,0,1;0rad)
  BaseFeature = -> Cylinder238
  Height = 0.5
  Length = 0.1
  MapMode = 5
  Placement = pos=(-20.95,18.635,0.53) rot=(0,0,1;0rad)
  Support = -> [XY_Plane132]
  Width = 0.23
FEATURE [PartDesign::SubtractiveBox] Box1162
  AttacherType = Attacher::AttachEngine3D
  AttachmentOffset = pos=(-21.15,18.635,0.297) rot=(0,-1,0;0.174533rad)
  BaseFeature = -> Box1173
  Height = 0.115
  Length = 0.115
  MapMode = 5
  Placement = pos=(-21.15,18.635,0.297) rot=(0,-1,0;0.174533rad)
  Support = -> [XY_Plane132]
  Width = 0.23
FEATURE [PartDesign::Fillet] Fillet363
  Base = -> Box1162 [Edge28]
  BaseFeature = -> Box1162
  Placement = pos=(-21.15,18.635,0.297) rot=(0,-1,0;0.174533rad)
  Radius = 0.375
  SupportTransform = false
FEATURE [PartDesign::AdditiveBox] Box1171
  AttacherType = Attacher::AttachEngine3D
  AttachmentOffset = pos=(-20.7,18.635,1.55) rot=(0,1,0;0.785398rad)
  BaseFeature = -> Fillet363
  Height = 0.375
  Length = 0.23
  MapMode = 5
  Placement = pos=(-20.7,18.635,1.55) rot=(0,1,0;0.785398rad)
  Support = -> [XY_Plane132]
  Width = 0.23
FEATURE [PartDesign::SubtractiveCylinder] Cylinder237
  Angle = 360
  AttacherType = Attacher::AttachEngine3D
  AttachmentOffset = pos=(-20.271,18.635,1.4056) rot=(-1,0,0;1.5708rad)
  BaseFeature = -> Box1171
  Height = 0.23
  MapMode = 5
  Placement = pos=(-20.271,18.635,1.4056) rot=(-1,0,0;1.5708rad)
  Radius = 0.23
  Support = -> [XY_Plane132]
FEATURE [PartDesign::AdditiveBox] Box1156
  AttacherType = Attacher::AttachEngine3D
  AttachmentOffset = pos=(-20.1,18.635,1.635) rot=(0,0,1;0rad)
  BaseFeature = -> Cylinder237
  Height = 0.265
  Length = 0.23
  MapMode = 5
  Placement = pos=(-20.1,18.635,1.635) rot=(0,0,1;0rad)
  Support = -> [XY_Plane132]
  Width = 0.23
FEATURE [PartDesign::Body] Body120  label="pin120"
  Group = -> [Box1157,Box1159,Box1127,Box1172,Box1174,Fillet358,Fillet361,Box1197,Cylinder238,Box1173,Box1162,Fillet363,Box1171,Cylinder237,Box1156]
  Origin = -> Origin144
  Placement = pos=(0,-4,0) rot=(0,0,1;0rad)
  Tip = -> Box1156
FEATURE [PartDesign::SubtractiveBox] Box1200
  AttacherType = Attacher::AttachEngine3D
  AttachmentOffset = pos=(-21.5005,18.625,0.235) rot=(0,-1,0;0.174533rad)
  BaseFeature = -> Box1113
  Height = 0.3
  Length = 0.6605
  MapMode = 5
  Placement = pos=(-21.5005,18.625,0.235) rot=(0,-1,0;0.174533rad)
  Support = -> [XY_Plane130]
  Width = 0.25
FEATURE [PartDesign::Fillet] Fillet370
  Base = -> Box1200 [Edge2]
  BaseFeature = -> Box1200
  Placement = pos=(-21.5005,18.625,0.235) rot=(0,-1,0;0.174533rad)
  Radius = 0.05
  SupportTransform = false
FEATURE [PartDesign::Fillet] Fillet352
  Base = -> Fillet370 [Edge33]
  BaseFeature = -> Fillet370
  Placement = pos=(-21.5005,18.625,0.235) rot=(0,-1,0;0.174533rad)
  Radius = 0.5
  SupportTransform = false
FEATURE [PartDesign::AdditiveBox] Box1090
  AttacherType = Attacher::AttachEngine3D
  AttachmentOffset = pos=(-21.1,18.635,0.305) rot=(0,1,0;0.785398rad)
  BaseFeature = -> Fillet352
  Height = 0.375
  Length = 0.2
  MapMode = 5
  Placement = pos=(-21.1,18.635,0.305) rot=(0,1,0;0.785398rad)
  Support = -> [XY_Plane130]
  Width = 0.23
FEATURE [PartDesign::SubtractiveCylinder] Cylinder223
  Angle = 360
  AttacherType = Attacher::AttachEngine3D
  AttachmentOffset = pos=(-21.055,18.935,0.52) rot=(1,0,0;1.5708rad)
  BaseFeature = -> Box1090
  Height = 0.375
  MapMode = 5
  Placement = pos=(-21.055,18.935,0.52) rot=(1,0,0;1.5708rad)
  Radius = 0.205
  Support = -> [XY_Plane130]
FEATURE [PartDesign::SubtractiveBox] Box1089
  AttacherType = Attacher::AttachEngine3D
  AttachmentOffset = pos=(-20.95,18.635,0.53) rot=(0,0,1;0rad)
  BaseFeature = -> Cylinder223
  Height = 0.5
  Length = 0.1
  MapMode = 5
  Placement = pos=(-20.95,18.635,0.53) rot=(0,0,1;0rad)
  Support = -> [XY_Plane130]
  Width = 0.23
FEATURE [PartDesign::SubtractiveBox] Box1107
  AttacherType = Attacher::AttachEngine3D
  AttachmentOffset = pos=(-21.15,18.635,0.297) rot=(0,-1,0;0.174533rad)
  BaseFeature = -> Box1089
  Height = 0.115
  Length = 0.115
  MapMode = 5
  Placement = pos=(-21.15,18.635,0.297) rot=(0,-1,0;0.174533rad)
  Support = -> [XY_Plane130]
  Width = 0.23
FEATURE [PartDesign::Fillet] Fillet365
  Base = -> Box1107 [Edge28]
  BaseFeature = -> Box1107
  Placement = pos=(-21.15,18.635,0.297) rot=(0,-1,0;0.174533rad)
  Radius = 0.375
  SupportTransform = false
FEATURE [PartDesign::AdditiveBox] Box1114
  AttacherType = Attacher::AttachEngine3D
  AttachmentOffset = pos=(-20.7,18.635,1.55) rot=(0,1,0;0.785398rad)
  BaseFeature = -> Fillet365
  Height = 0.375
  Length = 0.23
  MapMode = 5
  Placement = pos=(-20.7,18.635,1.55) rot=(0,1,0;0.785398rad)
  Support = -> [XY_Plane130]
  Width = 0.23
FEATURE [PartDesign::SubtractiveCylinder] Cylinder225
  Angle = 360
  AttacherType = Attacher::AttachEngine3D
  AttachmentOffset = pos=(-20.271,18.635,1.4056) rot=(-1,0,0;1.5708rad)
  BaseFeature = -> Box1114
  Height = 0.23
  MapMode = 5
  Placement = pos=(-20.271,18.635,1.4056) rot=(-1,0,0;1.5708rad)
  Radius = 0.23
  Support = -> [XY_Plane130]
FEATURE [PartDesign::AdditiveBox] Box1108
  AttacherType = Attacher::AttachEngine3D
  AttachmentOffset = pos=(-20.1,18.635,1.635) rot=(0,0,1;0rad)
  BaseFeature = -> Cylinder225
  Height = 0.265
  Length = 0.23
  MapMode = 5
  Placement = pos=(-20.1,18.635,1.635) rot=(0,0,1;0rad)
  Support = -> [XY_Plane130]
  Width = 0.23
FEATURE [PartDesign::Body] Body119  label="pin119"
  Group = -> [Box1131,Box1123,Box1111,Box1113,Box1200,Fillet370,Fillet352,Box1090,Cylinder223,Box1089,Box1107,Fillet365,Box1114,Cylinder225,Box1108]
  Origin = -> Origin127
  Placement = pos=(0,-4.5,0) rot=(0,0,1;0rad)
  Tip = -> Box1108
FEATURE [PartDesign::SubtractiveBox] Box1205
  AttacherType = Attacher::AttachEngine3D
  AttachmentOffset = pos=(-21.19,18.635,-0.12) rot=(0,-1,0;0.15708rad)
  BaseFeature = -> Box1133
  Height = 0.12
  Length = 0.725
  MapMode = 5
  Placement = pos=(-21.19,18.635,-0.12) rot=(0,-1,0;0.15708rad)
  Support = -> [XY_Plane134]
  Width = 0.25
FEATURE [PartDesign::SubtractiveBox] Box1161
  AttacherType = Attacher::AttachEngine3D
  AttachmentOffset = pos=(-21.5005,18.625,0.235) rot=(0,-1,0;0.174533rad)
  BaseFeature = -> Box1205
  Height = 0.3
  Length = 0.6605
  MapMode = 5
  Placement = pos=(-21.5005,18.625,0.235) rot=(0,-1,0;0.174533rad)
  Support = -> [XY_Plane134]
  Width = 0.25
FEATURE [PartDesign::Fillet] Fillet369
  Base = -> Box1161 [Edge2]
  BaseFeature = -> Box1161
  Placement = pos=(-21.5005,18.625,0.235) rot=(0,-1,0;0.174533rad)
  Radius = 0.05
  SupportTransform = false
FEATURE [PartDesign::Fillet] Fillet368
  Base = -> Fillet369 [Edge33]
  BaseFeature = -> Fillet369
  Placement = pos=(-21.5005,18.625,0.235) rot=(0,-1,0;0.174533rad)
  Radius = 0.5
  SupportTransform = false
FEATURE [PartDesign::AdditiveBox] Box1112
  AttacherType = Attacher::AttachEngine3D
  AttachmentOffset = pos=(-21.1,18.635,0.305) rot=(0,1,0;0.785398rad)
  BaseFeature = -> Fillet368
  Height = 0.375
  Length = 0.2
  MapMode = 5
  Placement = pos=(-21.1,18.635,0.305) rot=(0,1,0;0.785398rad)
  Support = -> [XY_Plane134]
  Width = 0.23
FEATURE [PartDesign::SubtractiveCylinder] Cylinder228
  Angle = 360
  AttacherType = Attacher::AttachEngine3D
  AttachmentOffset = pos=(-21.055,18.935,0.52) rot=(1,0,0;1.5708rad)
  BaseFeature = -> Box1112
  Height = 0.375
  MapMode = 5
  Placement = pos=(-21.055,18.935,0.52) rot=(1,0,0;1.5708rad)
  Radius = 0.205
  Support = -> [XY_Plane134]
FEATURE [PartDesign::SubtractiveBox] Box1120
  AttacherType = Attacher::AttachEngine3D
  AttachmentOffset = pos=(-20.95,18.635,0.53) rot=(0,0,1;0rad)
  BaseFeature = -> Cylinder228
  Height = 0.5
  Length = 0.1
  MapMode = 5
  Placement = pos=(-20.95,18.635,0.53) rot=(0,0,1;0rad)
  Support = -> [XY_Plane134]
  Width = 0.23
FEATURE [PartDesign::SubtractiveBox] Box1137
  AttacherType = Attacher::AttachEngine3D
  AttachmentOffset = pos=(-21.15,18.635,0.297) rot=(0,-1,0;0.174533rad)
  BaseFeature = -> Box1120
  Height = 0.115
  Length = 0.115
  MapMode = 5
  Placement = pos=(-21.15,18.635,0.297) rot=(0,-1,0;0.174533rad)
  Support = -> [XY_Plane134]
  Width = 0.23
FEATURE [PartDesign::Fillet] Fillet360
  Base = -> Box1137 [Edge28]
  BaseFeature = -> Box1137
  Placement = pos=(-21.15,18.635,0.297) rot=(0,-1,0;0.174533rad)
  Radius = 0.375
  SupportTransform = false
FEATURE [PartDesign::AdditiveBox] Box1139
  AttacherType = Attacher::AttachEngine3D
  AttachmentOffset = pos=(-20.7,18.635,1.55) rot=(0,1,0;0.785398rad)
  BaseFeature = -> Fillet360
  Height = 0.375
  Length = 0.23
  MapMode = 5
  Placement = pos=(-20.7,18.635,1.55) rot=(0,1,0;0.785398rad)
  Support = -> [XY_Plane134]
  Width = 0.23
FEATURE [PartDesign::SubtractiveCylinder] Cylinder231
  Angle = 360
  AttacherType = Attacher::AttachEngine3D
  AttachmentOffset = pos=(-20.271,18.635,1.4056) rot=(-1,0,0;1.5708rad)
  BaseFeature = -> Box1139
  Height = 0.23
  MapMode = 5
  Placement = pos=(-20.271,18.635,1.4056) rot=(-1,0,0;1.5708rad)
  Radius = 0.23
  Support = -> [XY_Plane134]
FEATURE [PartDesign::AdditiveBox] Box1196
  AttacherType = Attacher::AttachEngine3D
  AttachmentOffset = pos=(-20.1,18.635,1.635) rot=(0,0,1;0rad)
  BaseFeature = -> Cylinder231
  Height = 0.265
  Length = 0.23
  MapMode = 5
  Placement = pos=(-20.1,18.635,1.635) rot=(0,0,1;0rad)
  Support = -> [XY_Plane134]
  Width = 0.23
FEATURE [PartDesign::Body] Body121  label="pin121"
  Group = -> [Box1168,Box1180,Box1133,Box1205,Box1161,Fillet369,Fillet368,Box1112,Cylinder228,Box1120,Box1137,Fillet360,Box1139,Cylinder231,Box1196]
  Origin = -> Origin138
  Placement = pos=(0,-3,0) rot=(0,0,1;0rad)
  Tip = -> Box1196
FEATURE [PartDesign::SubtractiveBox] Box1206
  AttacherType = Attacher::AttachEngine3D
  AttachmentOffset = pos=(-20.5,18.63,0) rot=(0,0,1;0rad)
  BaseFeature = -> Box1177
  Height = 1.635
  Length = 0.5
  MapMode = 5
  Placement = pos=(-20.5,18.63,0) rot=(0,0,1;0rad)
  Support = -> [XY_Plane135]
  Width = 0.25
FEATURE [PartDesign::SubtractiveBox] Box1175
  AttacherType = Attacher::AttachEngine3D
  AttachmentOffset = pos=(-21.19,18.635,-0.12) rot=(0,-1,0;0.15708rad)
  BaseFeature = -> Box1206
  Height = 0.12
  Length = 0.725
  MapMode = 5
  Placement = pos=(-21.19,18.635,-0.12) rot=(0,-1,0;0.15708rad)
  Support = -> [XY_Plane135]
  Width = 0.25
FEATURE [PartDesign::SubtractiveBox] Box1166
  AttacherType = Attacher::AttachEngine3D
  AttachmentOffset = pos=(-21.5005,18.625,0.235) rot=(0,-1,0;0.174533rad)
  BaseFeature = -> Box1175
  Height = 0.3
  Length = 0.6605
  MapMode = 5
  Placement = pos=(-21.5005,18.625,0.235) rot=(0,-1,0;0.174533rad)
  Support = -> [XY_Plane135]
  Width = 0.25
FEATURE [PartDesign::Fillet] Fillet366
  Base = -> Box1166 [Edge2]
  BaseFeature = -> Box1166
  Placement = pos=(-21.5005,18.625,0.235) rot=(0,-1,0;0.174533rad)
  Radius = 0.05
  SupportTransform = false
FEATURE [PartDesign::Fillet] Fillet353
  Base = -> Fillet366 [Edge33]
  BaseFeature = -> Fillet366
  Placement = pos=(-21.5005,18.625,0.235) rot=(0,-1,0;0.174533rad)
  Radius = 0.5
  SupportTransform = false
FEATURE [PartDesign::AdditiveBox] Box1204
  AttacherType = Attacher::AttachEngine3D
  AttachmentOffset = pos=(-21.1,18.635,0.305) rot=(0,1,0;0.785398rad)
  BaseFeature = -> Fillet353
  Height = 0.375
  Length = 0.2
  MapMode = 5
  Placement = pos=(-21.1,18.635,0.305) rot=(0,1,0;0.785398rad)
  Support = -> [XY_Plane135]
  Width = 0.23
FEATURE [PartDesign::SubtractiveCylinder] Cylinder245
  Angle = 360
  AttacherType = Attacher::AttachEngine3D
  AttachmentOffset = pos=(-21.055,18.935,0.52) rot=(1,0,0;1.5708rad)
  BaseFeature = -> Box1204
  Height = 0.375
  MapMode = 5
  Placement = pos=(-21.055,18.935,0.52) rot=(1,0,0;1.5708rad)
  Radius = 0.205
  Support = -> [XY_Plane135]
FEATURE [PartDesign::SubtractiveBox] Box1195
  AttacherType = Attacher::AttachEngine3D
  AttachmentOffset = pos=(-20.95,18.635,0.53) rot=(0,0,1;0rad)
  BaseFeature = -> Cylinder245
  Height = 0.5
  Length = 0.1
  MapMode = 5
  Placement = pos=(-20.95,18.635,0.53) rot=(0,0,1;0rad)
  Support = -> [XY_Plane135]
  Width = 0.23
FEATURE [PartDesign::SubtractiveBox] Box1138
  AttacherType = Attacher::AttachEngine3D
  AttachmentOffset = pos=(-21.15,18.635,0.297) rot=(0,-1,0;0.174533rad)
  BaseFeature = -> Box1195
  Height = 0.115
  Length = 0.115
  MapMode = 5
  Placement = pos=(-21.15,18.635,0.297) rot=(0,-1,0;0.174533rad)
  Support = -> [XY_Plane135]
  Width = 0.23
FEATURE [PartDesign::Fillet] Fillet355
  Base = -> Box1138 [Edge28]
  BaseFeature = -> Box1138
  Placement = pos=(-21.15,18.635,0.297) rot=(0,-1,0;0.174533rad)
  Radius = 0.375
  SupportTransform = false
FEATURE [PartDesign::AdditiveBox] Box1203
  AttacherType = Attacher::AttachEngine3D
  AttachmentOffset = pos=(-20.7,18.635,1.55) rot=(0,1,0;0.785398rad)
  BaseFeature = -> Fillet355
  Height = 0.375
  Length = 0.23
  MapMode = 5
  Placement = pos=(-20.7,18.635,1.55) rot=(0,1,0;0.785398rad)
  Support = -> [XY_Plane135]
  Width = 0.23
FEATURE [PartDesign::SubtractiveCylinder] Cylinder244
  Angle = 360
  AttacherType = Attacher::AttachEngine3D
  AttachmentOffset = pos=(-20.271,18.635,1.4056) rot=(-1,0,0;1.5708rad)
  BaseFeature = -> Box1203
  Height = 0.23
  MapMode = 5
  Placement = pos=(-20.271,18.635,1.4056) rot=(-1,0,0;1.5708rad)
  Radius = 0.23
  Support = -> [XY_Plane135]
FEATURE [PartDesign::AdditiveBox] Box1169
  AttacherType = Attacher::AttachEngine3D
  AttachmentOffset = pos=(-20.1,18.635,1.635) rot=(0,0,1;0rad)
  BaseFeature = -> Cylinder244
  Height = 0.265
  Length = 0.23
  MapMode = 5
  Placement = pos=(-20.1,18.635,1.635) rot=(0,0,1;0rad)
  Support = -> [XY_Plane135]
  Width = 0.23
FEATURE [PartDesign::Body] Body118  label="pin118"
  Group = -> [Box1160,Box1177,Box1206,Box1175,Box1166,Fillet366,Fillet353,Box1204,Cylinder245,Box1195,Box1138,Fillet355,Box1203,Cylinder244,Box1169]
  Origin = -> Origin143
  Placement = pos=(0,-3.5,0) rot=(0,0,1;0rad)
  Tip = -> Box1169
FEATURE [PartDesign::AdditiveBox] Box1223
  AttacherType = Attacher::AttachEngine3D
  AttachmentOffset = pos=(-21.3,18.635,0) rot=(0,0,1;0rad)
  Height = 1.9
  Length = 1.3
  MapMode = 5
  Placement = pos=(-21.3,18.635,0) rot=(0,0,1;0rad)
  Support = -> [XY_Plane131]
  Width = 0.23
FEATURE [PartDesign::SubtractiveBox] Box1211
  AttacherType = Attacher::AttachEngine3D
  AttachmentOffset = pos=(-21.35,18.635,0.35) rot=(0,0,1;0rad)
  BaseFeature = -> Box1223
  Height = 1.55
  Length = 0.5
  MapMode = 5
  Placement = pos=(-21.35,18.635,0.35) rot=(0,0,1;0rad)
  Support = -> [XY_Plane131]
  Width = 0.23
FEATURE [PartDesign::SubtractiveBox] Box1194
  AttacherType = Attacher::AttachEngine3D
  AttachmentOffset = pos=(-20.5,18.63,0) rot=(0,0,1;0rad)
  BaseFeature = -> Box1211
  Height = 1.635
  Length = 0.5
  MapMode = 5
  Placement = pos=(-20.5,18.63,0) rot=(0,0,1;0rad)
  Support = -> [XY_Plane131]
  Width = 0.25
FEATURE [PartDesign::SubtractiveBox] Box1216
  AttacherType = Attacher::AttachEngine3D
  AttachmentOffset = pos=(-21.19,18.635,-0.12) rot=(0,-1,0;0.15708rad)
  BaseFeature = -> Box1194
  Height = 0.12
  Length = 0.725
  MapMode = 5
  Placement = pos=(-21.19,18.635,-0.12) rot=(0,-1,0;0.15708rad)
  Support = -> [XY_Plane131]
  Width = 0.25
FEATURE [PartDesign::SubtractiveBox] Box1209
  AttacherType = Attacher::AttachEngine3D
  AttachmentOffset = pos=(-21.5005,18.625,0.235) rot=(0,-1,0;0.174533rad)
  BaseFeature = -> Box1216
  Height = 0.3
  Length = 0.6605
  MapMode = 5
  Placement = pos=(-21.5005,18.625,0.235) rot=(0,-1,0;0.174533rad)
  Support = -> [XY_Plane131]
  Width = 0.25
FEATURE [PartDesign::Fillet] Fillet343
  Base = -> Box1209 [Edge2]
  BaseFeature = -> Box1209
  Placement = pos=(-21.5005,18.625,0.235) rot=(0,-1,0;0.174533rad)
  Radius = 0.05
  SupportTransform = false
FEATURE [PartDesign::Fillet] Fillet345
  Base = -> Fillet343 [Edge33]
  BaseFeature = -> Fillet343
  Placement = pos=(-21.5005,18.625,0.235) rot=(0,-1,0;0.174533rad)
  Radius = 0.5
  SupportTransform = false
FEATURE [PartDesign::AdditiveBox] Box1201
  AttacherType = Attacher::AttachEngine3D
  AttachmentOffset = pos=(-21.1,18.635,0.305) rot=(0,1,0;0.785398rad)
  BaseFeature = -> Fillet345
  Height = 0.375
  Length = 0.2
  MapMode = 5
  Placement = pos=(-21.1,18.635,0.305) rot=(0,1,0;0.785398rad)
  Support = -> [XY_Plane131]
  Width = 0.23
FEATURE [PartDesign::SubtractiveCylinder] Cylinder246
  Angle = 360
  AttacherType = Attacher::AttachEngine3D
  AttachmentOffset = pos=(-21.055,18.935,0.52) rot=(1,0,0;1.5708rad)
  BaseFeature = -> Box1201
  Height = 0.375
  MapMode = 5
  Placement = pos=(-21.055,18.935,0.52) rot=(1,0,0;1.5708rad)
  Radius = 0.205
  Support = -> [XY_Plane131]
FEATURE [PartDesign::SubtractiveBox] Box1215
  AttacherType = Attacher::AttachEngine3D
  AttachmentOffset = pos=(-20.95,18.635,0.53) rot=(0,0,1;0rad)
  BaseFeature = -> Cylinder246
  Height = 0.5
  Length = 0.1
  MapMode = 5
  Placement = pos=(-20.95,18.635,0.53) rot=(0,0,1;0rad)
  Support = -> [XY_Plane131]
  Width = 0.23
FEATURE [PartDesign::SubtractiveBox] Box1202
  AttacherType = Attacher::AttachEngine3D
  AttachmentOffset = pos=(-21.15,18.635,0.297) rot=(0,-1,0;0.174533rad)
  BaseFeature = -> Box1215
  Height = 0.115
  Length = 0.115
  MapMode = 5
  Placement = pos=(-21.15,18.635,0.297) rot=(0,-1,0;0.174533rad)
  Support = -> [XY_Plane131]
  Width = 0.23
FEATURE [PartDesign::Fillet] Fillet359
  Base = -> Box1202 [Edge28]
  BaseFeature = -> Box1202
  Placement = pos=(-21.15,18.635,0.297) rot=(0,-1,0;0.174533rad)
  Radius = 0.375
  SupportTransform = false
FEATURE [PartDesign::AdditiveBox] Box1210
  AttacherType = Attacher::AttachEngine3D
  AttachmentOffset = pos=(-20.7,18.635,1.55) rot=(0,1,0;0.785398rad)
  BaseFeature = -> Fillet359
  Height = 0.375
  Length = 0.23
  MapMode = 5
  Placement = pos=(-20.7,18.635,1.55) rot=(0,1,0;0.785398rad)
  Support = -> [XY_Plane131]
  Width = 0.23
FEATURE [PartDesign::SubtractiveCylinder] Cylinder248
  Angle = 360
  AttacherType = Attacher::AttachEngine3D
  AttachmentOffset = pos=(-20.271,18.635,1.4056) rot=(-1,0,0;1.5708rad)
  BaseFeature = -> Box1210
  Height = 0.23
  MapMode = 5
  Placement = pos=(-20.271,18.635,1.4056) rot=(-1,0,0;1.5708rad)
  Radius = 0.23
  Support = -> [XY_Plane131]
FEATURE [PartDesign::AdditiveBox] Box1219
  AttacherType = Attacher::AttachEngine3D
  AttachmentOffset = pos=(-20.1,18.635,1.635) rot=(0,0,1;0rad)
  BaseFeature = -> Cylinder248
  Height = 0.265
  Length = 0.23
  MapMode = 5
  Placement = pos=(-20.1,18.635,1.635) rot=(0,0,1;0rad)
  Support = -> [XY_Plane131]
  Width = 0.23
FEATURE [PartDesign::Body] Body113  label="pin113"
  Group = -> [Box1223,Box1211,Box1194,Box1216,Box1209,Fillet343,Fillet345,Box1201,Cylinder246,Box1215,Box1202,Fillet359,Box1210,Cylinder248,Box1219]
  Origin = -> Origin123
  Placement = pos=(0,-0.5,0) rot=(0,0,1;0rad)
  Tip = -> Box1219
FEATURE [PartDesign::SubtractiveBox] Box1227
  AttacherType = Attacher::AttachEngine3D
  AttachmentOffset = pos=(-20.5,18.63,0) rot=(0,0,1;0rad)
  BaseFeature = -> Box1091
  Height = 1.635
  Length = 0.5
  MapMode = 5
  Placement = pos=(-20.5,18.63,0) rot=(0,0,1;0rad)
  Support = -> [XY_Plane098]
  Width = 0.25
FEATURE [PartDesign::SubtractiveBox] Box1214
  AttacherType = Attacher::AttachEngine3D
  AttachmentOffset = pos=(-21.19,18.635,-0.12) rot=(0,-1,0;0.15708rad)
  BaseFeature = -> Box1227
  Height = 0.12
  Length = 0.725
  MapMode = 5
  Placement = pos=(-21.19,18.635,-0.12) rot=(0,-1,0;0.15708rad)
  Support = -> [XY_Plane098]
  Width = 0.25
FEATURE [PartDesign::SubtractiveBox] Box1096
  AttacherType = Attacher::AttachEngine3D
  AttachmentOffset = pos=(-21.5005,18.625,0.235) rot=(0,-1,0;0.174533rad)
  BaseFeature = -> Box1214
  Height = 0.3
  Length = 0.6605
  MapMode = 5
  Placement = pos=(-21.5005,18.625,0.235) rot=(0,-1,0;0.174533rad)
  Support = -> [XY_Plane098]
  Width = 0.25
FEATURE [PartDesign::Fillet] Fillet342
  Base = -> Box1096 [Edge2]
  BaseFeature = -> Box1096
  Placement = pos=(-21.5005,18.625,0.235) rot=(0,-1,0;0.174533rad)
  Radius = 0.05
  SupportTransform = false
FEATURE [PartDesign::Fillet] Fillet351
  Base = -> Fillet342 [Edge33]
  BaseFeature = -> Fillet342
  Placement = pos=(-21.5005,18.625,0.235) rot=(0,-1,0;0.174533rad)
  Radius = 0.5
  SupportTransform = false
FEATURE [PartDesign::AdditiveBox] Box1233
  AttacherType = Attacher::AttachEngine3D
  AttachmentOffset = pos=(-21.3,18.635,0) rot=(0,0,1;0rad)
  Height = 1.9
  Length = 1.3
  MapMode = 5
  Placement = pos=(-21.3,18.635,0) rot=(0,0,1;0rad)
  Support = -> [XY_Plane129]
  Width = 0.23
FEATURE [PartDesign::SubtractiveBox] Box1234
  AttacherType = Attacher::AttachEngine3D
  AttachmentOffset = pos=(-20.5,18.63,0) rot=(0,0,1;0rad)
  BaseFeature = -> Box1102
  Height = 1.635
  Length = 0.5
  MapMode = 5
  Placement = pos=(-20.5,18.63,0) rot=(0,0,1;0rad)
  Support = -> [XY_Plane127]
  Width = 0.25
FEATURE [PartDesign::SubtractiveBox] Box1087
  AttacherType = Attacher::AttachEngine3D
  AttachmentOffset = pos=(-21.19,18.635,-0.12) rot=(0,-1,0;0.15708rad)
  BaseFeature = -> Box1234
  Height = 0.12
  Length = 0.725
  MapMode = 5
  Placement = pos=(-21.19,18.635,-0.12) rot=(0,-1,0;0.15708rad)
  Support = -> [XY_Plane127]
  Width = 0.25
FEATURE [PartDesign::SubtractiveBox] Box1097
  AttacherType = Attacher::AttachEngine3D
  AttachmentOffset = pos=(-21.5005,18.625,0.235) rot=(0,-1,0;0.174533rad)
  BaseFeature = -> Box1087
  Height = 0.3
  Length = 0.6605
  MapMode = 5
  Placement = pos=(-21.5005,18.625,0.235) rot=(0,-1,0;0.174533rad)
  Support = -> [XY_Plane127]
  Width = 0.25
FEATURE [PartDesign::Fillet] Fillet347
  Base = -> Box1097 [Edge2]
  BaseFeature = -> Box1097
  Placement = pos=(-21.5005,18.625,0.235) rot=(0,-1,0;0.174533rad)
  Radius = 0.05
  SupportTransform = false
FEATURE [PartDesign::Fillet] Fillet341
  Base = -> Fillet347 [Edge33]
  BaseFeature = -> Fillet347
  Placement = pos=(-21.5005,18.625,0.235) rot=(0,-1,0;0.174533rad)
  Radius = 0.5
  SupportTransform = false
FEATURE [PartDesign::AdditiveBox] Box1235
  AttacherType = Attacher::AttachEngine3D
  AttachmentOffset = pos=(-21.3,18.635,0) rot=(0,0,1;0rad)
  Height = 1.9
  Length = 1.3
  MapMode = 5
  Placement = pos=(-21.3,18.635,0) rot=(0,0,1;0rad)
  Support = -> [XY_Plane128]
  Width = 0.23
FEATURE [PartDesign::SubtractiveBox] Box1228
  AttacherType = Attacher::AttachEngine3D
  AttachmentOffset = pos=(-21.35,18.635,0.35) rot=(0,0,1;0rad)
  BaseFeature = -> Box1235
  Height = 1.55
  Length = 0.5
  MapMode = 5
  Placement = pos=(-21.35,18.635,0.35) rot=(0,0,1;0rad)
  Support = -> [XY_Plane128]
  Width = 0.23
FEATURE [PartDesign::SubtractiveBox] Box1208
  AttacherType = Attacher::AttachEngine3D
  AttachmentOffset = pos=(-20.5,18.63,0) rot=(0,0,1;0rad)
  BaseFeature = -> Box1228
  Height = 1.635
  Length = 0.5
  MapMode = 5
  Placement = pos=(-20.5,18.63,0) rot=(0,0,1;0rad)
  Support = -> [XY_Plane128]
  Width = 0.25
FEATURE [PartDesign::SubtractiveBox] Box1207
  AttacherType = Attacher::AttachEngine3D
  AttachmentOffset = pos=(-21.19,18.635,-0.12) rot=(0,-1,0;0.15708rad)
  BaseFeature = -> Box1208
  Height = 0.12
  Length = 0.725
  MapMode = 5
  Placement = pos=(-21.19,18.635,-0.12) rot=(0,-1,0;0.15708rad)
  Support = -> [XY_Plane128]
  Width = 0.25
FEATURE [PartDesign::SubtractiveBox] Box1222
  AttacherType = Attacher::AttachEngine3D
  AttachmentOffset = pos=(-21.5005,18.625,0.235) rot=(0,-1,0;0.174533rad)
  BaseFeature = -> Box1207
  Height = 0.3
  Length = 0.6605
  MapMode = 5
  Placement = pos=(-21.5005,18.625,0.235) rot=(0,-1,0;0.174533rad)
  Support = -> [XY_Plane128]
  Width = 0.25
FEATURE [PartDesign::Fillet] Fillet357
  Base = -> Box1222 [Edge2]
  BaseFeature = -> Box1222
  Placement = pos=(-21.5005,18.625,0.235) rot=(0,-1,0;0.174533rad)
  Radius = 0.05
  SupportTransform = false
FEATURE [PartDesign::Fillet] Fillet336
  Base = -> Fillet357 [Edge33]
  BaseFeature = -> Fillet357
  Placement = pos=(-21.5005,18.625,0.235) rot=(0,-1,0;0.174533rad)
  Radius = 0.5
  SupportTransform = false
FEATURE [PartDesign::AdditiveBox] Box1179
  AttacherType = Attacher::AttachEngine3D
  AttachmentOffset = pos=(-21.1,18.635,0.305) rot=(0,1,0;0.785398rad)
  BaseFeature = -> Fillet336
  Height = 0.375
  Length = 0.2
  MapMode = 5
  Placement = pos=(-21.1,18.635,0.305) rot=(0,1,0;0.785398rad)
  Support = -> [XY_Plane128]
  Width = 0.23
FEATURE [PartDesign::SubtractiveCylinder] Cylinder230
  Angle = 360
  AttacherType = Attacher::AttachEngine3D
  AttachmentOffset = pos=(-21.055,18.935,0.52) rot=(1,0,0;1.5708rad)
  BaseFeature = -> Box1179
  Height = 0.375
  MapMode = 5
  Placement = pos=(-21.055,18.935,0.52) rot=(1,0,0;1.5708rad)
  Radius = 0.205
  Support = -> [XY_Plane128]
FEATURE [PartDesign::SubtractiveBox] Box1121
  AttacherType = Attacher::AttachEngine3D
  AttachmentOffset = pos=(-20.95,18.635,0.53) rot=(0,0,1;0rad)
  BaseFeature = -> Cylinder230
  Height = 0.5
  Length = 0.1
  MapMode = 5
  Placement = pos=(-20.95,18.635,0.53) rot=(0,0,1;0rad)
  Support = -> [XY_Plane128]
  Width = 0.23
FEATURE [PartDesign::SubtractiveBox] Box1116
  AttacherType = Attacher::AttachEngine3D
  AttachmentOffset = pos=(-21.15,18.635,0.297) rot=(0,-1,0;0.174533rad)
  BaseFeature = -> Box1121
  Height = 0.115
  Length = 0.115
  MapMode = 5
  Placement = pos=(-21.15,18.635,0.297) rot=(0,-1,0;0.174533rad)
  Support = -> [XY_Plane128]
  Width = 0.23
FEATURE [PartDesign::Fillet] Fillet362
  Base = -> Box1116 [Edge28]
  BaseFeature = -> Box1116
  Placement = pos=(-21.15,18.635,0.297) rot=(0,-1,0;0.174533rad)
  Radius = 0.375
  SupportTransform = false
FEATURE [PartDesign::AdditiveBox] Box1198
  AttacherType = Attacher::AttachEngine3D
  AttachmentOffset = pos=(-20.7,18.635,1.55) rot=(0,1,0;0.785398rad)
  BaseFeature = -> Fillet362
  Height = 0.375
  Length = 0.23
  MapMode = 5
  Placement = pos=(-20.7,18.635,1.55) rot=(0,1,0;0.785398rad)
  Support = -> [XY_Plane128]
  Width = 0.23
FEATURE [PartDesign::SubtractiveCylinder] Cylinder227
  Angle = 360
  AttacherType = Attacher::AttachEngine3D
  AttachmentOffset = pos=(-20.271,18.635,1.4056) rot=(-1,0,0;1.5708rad)
  BaseFeature = -> Box1198
  Height = 0.23
  MapMode = 5
  Placement = pos=(-20.271,18.635,1.4056) rot=(-1,0,0;1.5708rad)
  Radius = 0.23
  Support = -> [XY_Plane128]
FEATURE [PartDesign::AdditiveBox] Box1217
  AttacherType = Attacher::AttachEngine3D
  AttachmentOffset = pos=(-20.1,18.635,1.635) rot=(0,0,1;0rad)
  BaseFeature = -> Cylinder227
  Height = 0.265
  Length = 0.23
  MapMode = 5
  Placement = pos=(-20.1,18.635,1.635) rot=(0,0,1;0rad)
  Support = -> [XY_Plane128]
  Width = 0.23
FEATURE [PartDesign::Body] Body115  label="pin115"
  Group = -> [Box1235,Box1228,Box1208,Box1207,Box1222,Fillet357,Fillet336,Box1179,Cylinder230,Box1121,Box1116,Fillet362,Box1198,Cylinder227,Box1217]
  Origin = -> Origin131
  Tip = -> Box1217
FEATURE [PartDesign::SubtractiveBox] Box1238
  AttacherType = Attacher::AttachEngine3D
  AttachmentOffset = pos=(-21.35,18.635,0.35) rot=(0,0,1;0rad)
  BaseFeature = -> Box1233
  Height = 1.55
  Length = 0.5
  MapMode = 5
  Placement = pos=(-21.35,18.635,0.35) rot=(0,0,1;0rad)
  Support = -> [XY_Plane129]
  Width = 0.23
FEATURE [PartDesign::SubtractiveBox] Box1212
  AttacherType = Attacher::AttachEngine3D
  AttachmentOffset = pos=(-20.5,18.63,0) rot=(0,0,1;0rad)
  BaseFeature = -> Box1238
  Height = 1.635
  Length = 0.5
  MapMode = 5
  Placement = pos=(-20.5,18.63,0) rot=(0,0,1;0rad)
  Support = -> [XY_Plane129]
  Width = 0.25
FEATURE [PartDesign::SubtractiveBox] Box1224
  AttacherType = Attacher::AttachEngine3D
  AttachmentOffset = pos=(-21.19,18.635,-0.12) rot=(0,-1,0;0.15708rad)
  BaseFeature = -> Box1212
  Height = 0.12
  Length = 0.725
  MapMode = 5
  Placement = pos=(-21.19,18.635,-0.12) rot=(0,-1,0;0.15708rad)
  Support = -> [XY_Plane129]
  Width = 0.25
FEATURE [PartDesign::SubtractiveBox] Box1221
  AttacherType = Attacher::AttachEngine3D
  AttachmentOffset = pos=(-21.5005,18.625,0.235) rot=(0,-1,0;0.174533rad)
  BaseFeature = -> Box1224
  Height = 0.3
  Length = 0.6605
  MapMode = 5
  Placement = pos=(-21.5005,18.625,0.235) rot=(0,-1,0;0.174533rad)
  Support = -> [XY_Plane129]
  Width = 0.25
FEATURE [PartDesign::Fillet] Fillet350
  Base = -> Box1221 [Edge2]
  BaseFeature = -> Box1221
  Placement = pos=(-21.5005,18.625,0.235) rot=(0,-1,0;0.174533rad)
  Radius = 0.05
  SupportTransform = false
FEATURE [PartDesign::Fillet] Fillet364
  Base = -> Fillet350 [Edge33]
  BaseFeature = -> Fillet350
  Placement = pos=(-21.5005,18.625,0.235) rot=(0,-1,0;0.174533rad)
  Radius = 0.5
  SupportTransform = false
FEATURE [PartDesign::AdditiveBox] Box1199
  AttacherType = Attacher::AttachEngine3D
  AttachmentOffset = pos=(-21.1,18.635,0.305) rot=(0,1,0;0.785398rad)
  BaseFeature = -> Fillet364
  Height = 0.375
  Length = 0.2
  MapMode = 5
  Placement = pos=(-21.1,18.635,0.305) rot=(0,1,0;0.785398rad)
  Support = -> [XY_Plane129]
  Width = 0.23
FEATURE [PartDesign::SubtractiveCylinder] Cylinder250
  Angle = 360
  AttacherType = Attacher::AttachEngine3D
  AttachmentOffset = pos=(-21.055,18.935,0.52) rot=(1,0,0;1.5708rad)
  BaseFeature = -> Box1199
  Height = 0.375
  MapMode = 5
  Placement = pos=(-21.055,18.935,0.52) rot=(1,0,0;1.5708rad)
  Radius = 0.205
  Support = -> [XY_Plane129]
FEATURE [PartDesign::SubtractiveBox] Box1213
  AttacherType = Attacher::AttachEngine3D
  AttachmentOffset = pos=(-20.95,18.635,0.53) rot=(0,0,1;0rad)
  BaseFeature = -> Cylinder250
  Height = 0.5
  Length = 0.1
  MapMode = 5
  Placement = pos=(-20.95,18.635,0.53) rot=(0,0,1;0rad)
  Support = -> [XY_Plane129]
  Width = 0.23
FEATURE [PartDesign::SubtractiveBox] Box1220
  AttacherType = Attacher::AttachEngine3D
  AttachmentOffset = pos=(-21.15,18.635,0.297) rot=(0,-1,0;0.174533rad)
  BaseFeature = -> Box1213
  Height = 0.115
  Length = 0.115
  MapMode = 5
  Placement = pos=(-21.15,18.635,0.297) rot=(0,-1,0;0.174533rad)
  Support = -> [XY_Plane129]
  Width = 0.23
FEATURE [PartDesign::Fillet] Fillet339
  Base = -> Box1220 [Edge28]
  BaseFeature = -> Box1220
  Placement = pos=(-21.15,18.635,0.297) rot=(0,-1,0;0.174533rad)
  Radius = 0.375
  SupportTransform = false
FEATURE [PartDesign::AdditiveBox] Box1218
  AttacherType = Attacher::AttachEngine3D
  AttachmentOffset = pos=(-20.7,18.635,1.55) rot=(0,1,0;0.785398rad)
  BaseFeature = -> Fillet339
  Height = 0.375
  Length = 0.23
  MapMode = 5
  Placement = pos=(-20.7,18.635,1.55) rot=(0,1,0;0.785398rad)
  Support = -> [XY_Plane129]
  Width = 0.23
FEATURE [PartDesign::SubtractiveCylinder] Cylinder247
  Angle = 360
  AttacherType = Attacher::AttachEngine3D
  AttachmentOffset = pos=(-20.271,18.635,1.4056) rot=(-1,0,0;1.5708rad)
  BaseFeature = -> Box1218
  Height = 0.23
  MapMode = 5
  Placement = pos=(-20.271,18.635,1.4056) rot=(-1,0,0;1.5708rad)
  Radius = 0.23
  Support = -> [XY_Plane129]
FEATURE [PartDesign::AdditiveBox] Box1225
  AttacherType = Attacher::AttachEngine3D
  AttachmentOffset = pos=(-20.1,18.635,1.635) rot=(0,0,1;0rad)
  BaseFeature = -> Cylinder247
  Height = 0.265
  Length = 0.23
  MapMode = 5
  Placement = pos=(-20.1,18.635,1.635) rot=(0,0,1;0rad)
  Support = -> [XY_Plane129]
  Width = 0.23
FEATURE [PartDesign::Body] Body122  label="pin122"
  Group = -> [Box1233,Box1238,Box1212,Box1224,Box1221,Fillet350,Fillet364,Box1199,Cylinder250,Box1213,Box1220,Fillet339,Box1218,Cylinder247,Box1225]
  Origin = -> Origin126
  Placement = pos=(0,-1,0) rot=(0,0,1;0rad)
  Tip = -> Box1225
FEATURE [PartDesign::SubtractiveBox] Box1239
  AttacherType = Attacher::AttachEngine3D
  AttachmentOffset = pos=(-20.5,18.63,0) rot=(0,0,1;0rad)
  BaseFeature = -> Box1093
  Height = 1.635
  Length = 0.5
  MapMode = 5
  Placement = pos=(-20.5,18.63,0) rot=(0,0,1;0rad)
  Support = -> [XY_Plane112]
  Width = 0.25
FEATURE [PartDesign::SubtractiveBox] Box1170
  AttacherType = Attacher::AttachEngine3D
  AttachmentOffset = pos=(-21.19,18.635,-0.12) rot=(0,-1,0;0.15708rad)
  BaseFeature = -> Box1239
  Height = 0.12
  Length = 0.725
  MapMode = 5
  Placement = pos=(-21.19,18.635,-0.12) rot=(0,-1,0;0.15708rad)
  Support = -> [XY_Plane112]
  Width = 0.25
FEATURE [PartDesign::SubtractiveBox] Box1099
  AttacherType = Attacher::AttachEngine3D
  AttachmentOffset = pos=(-21.5005,18.625,0.235) rot=(0,-1,0;0.174533rad)
  BaseFeature = -> Box1170
  Height = 0.3
  Length = 0.6605
  MapMode = 5
  Placement = pos=(-21.5005,18.625,0.235) rot=(0,-1,0;0.174533rad)
  Support = -> [XY_Plane112]
  Width = 0.25
FEATURE [PartDesign::Fillet] Fillet346
  Base = -> Box1099 [Edge2]
  BaseFeature = -> Box1099
  Placement = pos=(-21.5005,18.625,0.235) rot=(0,-1,0;0.174533rad)
  Radius = 0.05
  SupportTransform = false
FEATURE [PartDesign::Fillet] Fillet337
  Base = -> Fillet346 [Edge33]
  BaseFeature = -> Fillet346
  Placement = pos=(-21.5005,18.625,0.235) rot=(0,-1,0;0.174533rad)
  Radius = 0.5
  SupportTransform = false
FEATURE [PartDesign::AdditiveBox] Box1232
  AttacherType = Attacher::AttachEngine3D
  AttachmentOffset = pos=(-21.1,18.635,0.305) rot=(0,1,0;0.785398rad)
  BaseFeature = -> Fillet337
  Height = 0.375
  Length = 0.2
  MapMode = 5
  Placement = pos=(-21.1,18.635,0.305) rot=(0,1,0;0.785398rad)
  Support = -> [XY_Plane112]
  Width = 0.23
FEATURE [PartDesign::SubtractiveCylinder] Cylinder240
  Angle = 360
  AttacherType = Attacher::AttachEngine3D
  AttachmentOffset = pos=(-21.055,18.935,0.52) rot=(1,0,0;1.5708rad)
  BaseFeature = -> Box1232
  Height = 0.375
  MapMode = 5
  Placement = pos=(-21.055,18.935,0.52) rot=(1,0,0;1.5708rad)
  Radius = 0.205
  Support = -> [XY_Plane112]
FEATURE [PartDesign::SubtractiveBox] Box1088
  AttacherType = Attacher::AttachEngine3D
  AttachmentOffset = pos=(-20.95,18.635,0.53) rot=(0,0,1;0rad)
  BaseFeature = -> Cylinder240
  Height = 0.5
  Length = 0.1
  MapMode = 5
  Placement = pos=(-20.95,18.635,0.53) rot=(0,0,1;0rad)
  Support = -> [XY_Plane112]
  Width = 0.23
FEATURE [PartDesign::SubtractiveBox] Box1095
  AttacherType = Attacher::AttachEngine3D
  AttachmentOffset = pos=(-21.15,18.635,0.297) rot=(0,-1,0;0.174533rad)
  BaseFeature = -> Box1088
  Height = 0.115
  Length = 0.115
  MapMode = 5
  Placement = pos=(-21.15,18.635,0.297) rot=(0,-1,0;0.174533rad)
  Support = -> [XY_Plane112]
  Width = 0.23
FEATURE [PartDesign::Fillet] Fillet335
  Base = -> Box1095 [Edge28]
  BaseFeature = -> Box1095
  Placement = pos=(-21.15,18.635,0.297) rot=(0,-1,0;0.174533rad)
  Radius = 0.375
  SupportTransform = false
FEATURE [PartDesign::AdditiveBox] Box1098
  AttacherType = Attacher::AttachEngine3D
  AttachmentOffset = pos=(-20.7,18.635,1.55) rot=(0,1,0;0.785398rad)
  BaseFeature = -> Fillet335
  Height = 0.375
  Length = 0.23
  MapMode = 5
  Placement = pos=(-20.7,18.635,1.55) rot=(0,1,0;0.785398rad)
  Support = -> [XY_Plane112]
  Width = 0.23
FEATURE [PartDesign::SubtractiveCylinder] Cylinder239
  Angle = 360
  AttacherType = Attacher::AttachEngine3D
  AttachmentOffset = pos=(-20.271,18.635,1.4056) rot=(-1,0,0;1.5708rad)
  BaseFeature = -> Box1098
  Height = 0.23
  MapMode = 5
  Placement = pos=(-20.271,18.635,1.4056) rot=(-1,0,0;1.5708rad)
  Radius = 0.23
  Support = -> [XY_Plane112]
FEATURE [PartDesign::AdditiveBox] Box1092
  AttacherType = Attacher::AttachEngine3D
  AttachmentOffset = pos=(-20.1,18.635,1.635) rot=(0,0,1;0rad)
  BaseFeature = -> Cylinder239
  Height = 0.265
  Length = 0.23
  MapMode = 5
  Placement = pos=(-20.1,18.635,1.635) rot=(0,0,1;0rad)
  Support = -> [XY_Plane112]
  Width = 0.23
FEATURE [PartDesign::Body] Body116  label="pin116"
  Group = -> [Box1110,Box1093,Box1239,Box1170,Box1099,Fillet346,Fillet337,Box1232,Cylinder240,Box1088,Box1095,Fillet335,Box1098,Cylinder239,Box1092]
  Origin = -> Origin130
  Placement = pos=(0,-2.5,0) rot=(0,0,1;0rad)
  Tip = -> Box1092
FEATURE [PartDesign::AdditiveBox] Box1240
  AttacherType = Attacher::AttachEngine3D
  AttachmentOffset = pos=(-21.1,18.635,0.305) rot=(0,1,0;0.785398rad)
  BaseFeature = -> Fillet341
  Height = 0.375
  Length = 0.2
  MapMode = 5
  Placement = pos=(-21.1,18.635,0.305) rot=(0,1,0;0.785398rad)
  Support = -> [XY_Plane127]
  Width = 0.23
FEATURE [PartDesign::SubtractiveCylinder] Cylinder251
  Angle = 360
  AttacherType = Attacher::AttachEngine3D
  AttachmentOffset = pos=(-21.055,18.935,0.52) rot=(1,0,0;1.5708rad)
  BaseFeature = -> Box1240
  Height = 0.375
  MapMode = 5
  Placement = pos=(-21.055,18.935,0.52) rot=(1,0,0;1.5708rad)
  Radius = 0.205
  Support = -> [XY_Plane127]
FEATURE [PartDesign::SubtractiveBox] Box1101
  AttacherType = Attacher::AttachEngine3D
  AttachmentOffset = pos=(-20.95,18.635,0.53) rot=(0,0,1;0rad)
  BaseFeature = -> Cylinder251
  Height = 0.5
  Length = 0.1
  MapMode = 5
  Placement = pos=(-20.95,18.635,0.53) rot=(0,0,1;0rad)
  Support = -> [XY_Plane127]
  Width = 0.23
FEATURE [PartDesign::SubtractiveBox] Box1176
  AttacherType = Attacher::AttachEngine3D
  AttachmentOffset = pos=(-21.15,18.635,0.297) rot=(0,-1,0;0.174533rad)
  BaseFeature = -> Box1101
  Height = 0.115
  Length = 0.115
  MapMode = 5
  Placement = pos=(-21.15,18.635,0.297) rot=(0,-1,0;0.174533rad)
  Support = -> [XY_Plane127]
  Width = 0.23
FEATURE [PartDesign::Fillet] Fillet340
  Base = -> Box1176 [Edge28]
  BaseFeature = -> Box1176
  Placement = pos=(-21.15,18.635,0.297) rot=(0,-1,0;0.174533rad)
  Radius = 0.375
  SupportTransform = false
FEATURE [PartDesign::AdditiveBox] Box1226
  AttacherType = Attacher::AttachEngine3D
  AttachmentOffset = pos=(-20.7,18.635,1.55) rot=(0,1,0;0.785398rad)
  BaseFeature = -> Fillet340
  Height = 0.375
  Length = 0.23
  MapMode = 5
  Placement = pos=(-20.7,18.635,1.55) rot=(0,1,0;0.785398rad)
  Support = -> [XY_Plane127]
  Width = 0.23
FEATURE [PartDesign::SubtractiveCylinder] Cylinder222
  Angle = 360
  AttacherType = Attacher::AttachEngine3D
  AttachmentOffset = pos=(-20.271,18.635,1.4056) rot=(-1,0,0;1.5708rad)
  BaseFeature = -> Box1226
  Height = 0.23
  MapMode = 5
  Placement = pos=(-20.271,18.635,1.4056) rot=(-1,0,0;1.5708rad)
  Radius = 0.23
  Support = -> [XY_Plane127]
FEATURE [PartDesign::AdditiveBox] Box1100
  AttacherType = Attacher::AttachEngine3D
  AttachmentOffset = pos=(-20.1,18.635,1.635) rot=(0,0,1;0rad)
  BaseFeature = -> Cylinder222
  Height = 0.265
  Length = 0.23
  MapMode = 5
  Placement = pos=(-20.1,18.635,1.635) rot=(0,0,1;0rad)
  Support = -> [XY_Plane127]
  Width = 0.23
FEATURE [PartDesign::Body] Body114  label="pin114"
  Group = -> [Box1178,Box1102,Box1234,Box1087,Box1097,Fillet347,Fillet341,Box1240,Cylinder251,Box1101,Box1176,Fillet340,Box1226,Cylinder222,Box1100]
  Origin = -> Origin139
  Placement = pos=(0,-2,0) rot=(0,0,1;0rad)
  Tip = -> Box1100
FEATURE [PartDesign::AdditiveBox] Box1241
  AttacherType = Attacher::AttachEngine3D
  AttachmentOffset = pos=(-21.1,18.635,0.305) rot=(0,1,0;0.785398rad)
  BaseFeature = -> Fillet351
  Height = 0.375
  Length = 0.2
  MapMode = 5
  Placement = pos=(-21.1,18.635,0.305) rot=(0,1,0;0.785398rad)
  Support = -> [XY_Plane098]
  Width = 0.23
FEATURE [PartDesign::SubtractiveCylinder] Cylinder249
  Angle = 360
  AttacherType = Attacher::AttachEngine3D
  AttachmentOffset = pos=(-21.055,18.935,0.52) rot=(1,0,0;1.5708rad)
  BaseFeature = -> Box1241
  Height = 0.375
  MapMode = 5
  Placement = pos=(-21.055,18.935,0.52) rot=(1,0,0;1.5708rad)
  Radius = 0.205
  Support = -> [XY_Plane098]
FEATURE [PartDesign::SubtractiveBox] Box1236
  AttacherType = Attacher::AttachEngine3D
  AttachmentOffset = pos=(-20.95,18.635,0.53) rot=(0,0,1;0rad)
  BaseFeature = -> Cylinder249
  Height = 0.5
  Length = 0.1
  MapMode = 5
  Placement = pos=(-20.95,18.635,0.53) rot=(0,0,1;0rad)
  Support = -> [XY_Plane098]
  Width = 0.23
FEATURE [PartDesign::SubtractiveBox] Box1237
  AttacherType = Attacher::AttachEngine3D
  AttachmentOffset = pos=(-21.15,18.635,0.297) rot=(0,-1,0;0.174533rad)
  BaseFeature = -> Box1236
  Height = 0.115
  Length = 0.115
  MapMode = 5
  Placement = pos=(-21.15,18.635,0.297) rot=(0,-1,0;0.174533rad)
  Support = -> [XY_Plane098]
  Width = 0.23
FEATURE [PartDesign::Fillet] Fillet354
  Base = -> Box1237 [Edge28]
  BaseFeature = -> Box1237
  Placement = pos=(-21.15,18.635,0.297) rot=(0,-1,0;0.174533rad)
  Radius = 0.375
  SupportTransform = false
FEATURE [PartDesign::AdditiveBox] Box1229
  AttacherType = Attacher::AttachEngine3D
  AttachmentOffset = pos=(-20.7,18.635,1.55) rot=(0,1,0;0.785398rad)
  BaseFeature = -> Fillet354
  Height = 0.375
  Length = 0.23
  MapMode = 5
  Placement = pos=(-20.7,18.635,1.55) rot=(0,1,0;0.785398rad)
  Support = -> [XY_Plane098]
  Width = 0.23
FEATURE [PartDesign::SubtractiveCylinder] Cylinder241
  Angle = 360
  AttacherType = Attacher::AttachEngine3D
  AttachmentOffset = pos=(-20.271,18.635,1.4056) rot=(-1,0,0;1.5708rad)
  BaseFeature = -> Box1229
  Height = 0.23
  MapMode = 5
  Placement = pos=(-20.271,18.635,1.4056) rot=(-1,0,0;1.5708rad)
  Radius = 0.23
  Support = -> [XY_Plane098]
FEATURE [PartDesign::AdditiveBox] Box1230
  AttacherType = Attacher::AttachEngine3D
  AttachmentOffset = pos=(-20.1,18.635,1.635) rot=(0,0,1;0rad)
  BaseFeature = -> Cylinder241
  Height = 0.265
  Length = 0.23
  MapMode = 5
  Placement = pos=(-20.1,18.635,1.635) rot=(0,0,1;0rad)
  Support = -> [XY_Plane098]
  Width = 0.23
FEATURE [PartDesign::Body] Body117  label="pin117"
  Group = -> [Box1106,Box1091,Box1227,Box1214,Box1096,Fillet342,Fillet351,Box1241,Cylinder249,Box1236,Box1237,Fillet354,Box1229,Cylinder241,Box1230]
  Origin = -> Origin141
  Placement = pos=(0,-1.5,0) rot=(0,0,1;0rad)
  Tip = -> Box1230
FEATURE [App::Part] Part013  label="Pin-set012"
  Group = -> [Body115,Body113,Body122,Body117,Body114,Body116,Body121,Body118,Body120,Body119,Body124,Body123]
  Origin = -> Origin142
  Placement = pos=(0,-18,0) rot=(0,0,1;0rad)
FEATURE [PartDesign::AdditiveBox] Box1262
  AttacherType = Attacher::AttachEngine3D
  AttachmentOffset = pos=(-21.3,18.635,0) rot=(0,0,1;0rad)
  Height = 1.9
  Length = 1.3
  MapMode = 5
  Placement = pos=(-21.3,18.635,0) rot=(0,0,1;0rad)
  Support = -> [XY_Plane136]
  Width = 0.23
FEATURE [PartDesign::SubtractiveBox] Box1247
  AttacherType = Attacher::AttachEngine3D
  AttachmentOffset = pos=(-21.35,18.635,0.35) rot=(0,0,1;0rad)
  BaseFeature = -> Box1262
  Height = 1.55
  Length = 0.5
  MapMode = 5
  Placement = pos=(-21.35,18.635,0.35) rot=(0,0,1;0rad)
  Support = -> [XY_Plane136]
  Width = 0.23
FEATURE [PartDesign::AdditiveBox] Box1264
  AttacherType = Attacher::AttachEngine3D
  AttachmentOffset = pos=(-21.3,18.635,0) rot=(0,0,1;0rad)
  Height = 1.9
  Length = 1.3
  MapMode = 5
  Placement = pos=(-21.3,18.635,0) rot=(0,0,1;0rad)
  Support = -> [XY_Plane140]
  Width = 0.23
FEATURE [PartDesign::SubtractiveBox] Box1246
  AttacherType = Attacher::AttachEngine3D
  AttachmentOffset = pos=(-21.35,18.635,0.35) rot=(0,0,1;0rad)
  BaseFeature = -> Box1264
  Height = 1.55
  Length = 0.5
  MapMode = 5
  Placement = pos=(-21.35,18.635,0.35) rot=(0,0,1;0rad)
  Support = -> [XY_Plane140]
  Width = 0.23
FEATURE [PartDesign::AdditiveBox] Box1275
  AttacherType = Attacher::AttachEngine3D
  AttachmentOffset = pos=(-21.3,18.635,0) rot=(0,0,1;0rad)
  Height = 1.9
  Length = 1.3
  MapMode = 5
  Placement = pos=(-21.3,18.635,0) rot=(0,0,1;0rad)
  Support = -> [XY_Plane144]
  Width = 0.23
FEATURE [PartDesign::AdditiveBox] Box1277
  AttacherType = Attacher::AttachEngine3D
  AttachmentOffset = pos=(-21.3,18.635,0) rot=(0,0,1;0rad)
  Height = 1.9
  Length = 1.3
  MapMode = 5
  Placement = pos=(-21.3,18.635,0) rot=(0,0,1;0rad)
  Support = -> [XY_Plane145]
  Width = 0.23
FEATURE [PartDesign::SubtractiveBox] Box1283
  AttacherType = Attacher::AttachEngine3D
  AttachmentOffset = pos=(-21.35,18.635,0.35) rot=(0,0,1;0rad)
  BaseFeature = -> Box1275
  Height = 1.55
  Length = 0.5
  MapMode = 5
  Placement = pos=(-21.35,18.635,0.35) rot=(0,0,1;0rad)
  Support = -> [XY_Plane144]
  Width = 0.23
FEATURE [PartDesign::SubtractiveBox] Box1267
  AttacherType = Attacher::AttachEngine3D
  AttachmentOffset = pos=(-20.5,18.63,0) rot=(0,0,1;0rad)
  BaseFeature = -> Box1283
  Height = 1.635
  Length = 0.5
  MapMode = 5
  Placement = pos=(-20.5,18.63,0) rot=(0,0,1;0rad)
  Support = -> [XY_Plane144]
  Width = 0.25
FEATURE [PartDesign::SubtractiveBox] Box1272
  AttacherType = Attacher::AttachEngine3D
  AttachmentOffset = pos=(-21.19,18.635,-0.12) rot=(0,-1,0;0.15708rad)
  BaseFeature = -> Box1267
  Height = 0.12
  Length = 0.725
  MapMode = 5
  Placement = pos=(-21.19,18.635,-0.12) rot=(0,-1,0;0.15708rad)
  Support = -> [XY_Plane144]
  Width = 0.25
FEATURE [PartDesign::SubtractiveBox] Box1278
  AttacherType = Attacher::AttachEngine3D
  AttachmentOffset = pos=(-21.5005,18.625,0.235) rot=(0,-1,0;0.174533rad)
  BaseFeature = -> Box1272
  Height = 0.3
  Length = 0.6605
  MapMode = 5
  Placement = pos=(-21.5005,18.625,0.235) rot=(0,-1,0;0.174533rad)
  Support = -> [XY_Plane144]
  Width = 0.25
FEATURE [PartDesign::SubtractiveBox] Box1285
  AttacherType = Attacher::AttachEngine3D
  AttachmentOffset = pos=(-21.35,18.635,0.35) rot=(0,0,1;0rad)
  BaseFeature = -> Box1277
  Height = 1.55
  Length = 0.5
  MapMode = 5
  Placement = pos=(-21.35,18.635,0.35) rot=(0,0,1;0rad)
  Support = -> [XY_Plane145]
  Width = 0.23
FEATURE [PartDesign::SubtractiveBox] Box1269
  AttacherType = Attacher::AttachEngine3D
  AttachmentOffset = pos=(-20.5,18.63,0) rot=(0,0,1;0rad)
  BaseFeature = -> Box1285
  Height = 1.635
  Length = 0.5
  MapMode = 5
  Placement = pos=(-20.5,18.63,0) rot=(0,0,1;0rad)
  Support = -> [XY_Plane145]
  Width = 0.25
FEATURE [PartDesign::SubtractiveBox] Box1274
  AttacherType = Attacher::AttachEngine3D
  AttachmentOffset = pos=(-21.19,18.635,-0.12) rot=(0,-1,0;0.15708rad)
  BaseFeature = -> Box1269
  Height = 0.12
  Length = 0.725
  MapMode = 5
  Placement = pos=(-21.19,18.635,-0.12) rot=(0,-1,0;0.15708rad)
  Support = -> [XY_Plane145]
  Width = 0.25
FEATURE [PartDesign::AdditiveBox] Box1289
  AttacherType = Attacher::AttachEngine3D
  AttachmentOffset = pos=(-21.3,18.635,0) rot=(0,0,1;0rad)
  Height = 1.9
  Length = 1.3
  MapMode = 5
  Placement = pos=(-21.3,18.635,0) rot=(0,0,1;0rad)
  Support = -> [XY_Plane143]
  Width = 0.23
FEATURE [PartDesign::AdditiveBox] Box1292
  AttacherType = Attacher::AttachEngine3D
  AttachmentOffset = pos=(-21.3,18.635,0) rot=(0,0,1;0rad)
  Height = 1.9
  Length = 1.3
  MapMode = 5
  Placement = pos=(-21.3,18.635,0) rot=(0,0,1;0rad)
  Support = -> [XY_Plane147]
  Width = 0.23
FEATURE [PartDesign::AdditiveBox] Box1294
  AttacherType = Attacher::AttachEngine3D
  AttachmentOffset = pos=(-21.3,18.635,0) rot=(0,0,1;0rad)
  Height = 1.9
  Length = 1.3
  MapMode = 5
  Placement = pos=(-21.3,18.635,0) rot=(0,0,1;0rad)
  Support = -> [XY_Plane139]
  Width = 0.23
FEATURE [PartDesign::SubtractiveBox] Box1300
  AttacherType = Attacher::AttachEngine3D
  AttachmentOffset = pos=(-21.35,18.635,0.35) rot=(0,0,1;0rad)
  BaseFeature = -> Box1294
  Height = 1.55
  Length = 0.5
  MapMode = 5
  Placement = pos=(-21.35,18.635,0.35) rot=(0,0,1;0rad)
  Support = -> [XY_Plane139]
  Width = 0.23
FEATURE [PartDesign::SubtractiveBox] Box1248
  AttacherType = Attacher::AttachEngine3D
  AttachmentOffset = pos=(-20.5,18.63,0) rot=(0,0,1;0rad)
  BaseFeature = -> Box1300
  Height = 1.635
  Length = 0.5
  MapMode = 5
  Placement = pos=(-20.5,18.63,0) rot=(0,0,1;0rad)
  Support = -> [XY_Plane139]
  Width = 0.25
FEATURE [PartDesign::SubtractiveBox] Box1260
  AttacherType = Attacher::AttachEngine3D
  AttachmentOffset = pos=(-21.19,18.635,-0.12) rot=(0,-1,0;0.15708rad)
  BaseFeature = -> Box1248
  Height = 0.12
  Length = 0.725
  MapMode = 5
  Placement = pos=(-21.19,18.635,-0.12) rot=(0,-1,0;0.15708rad)
  Support = -> [XY_Plane139]
  Width = 0.25
FEATURE [PartDesign::SubtractiveBox] Box1256
  AttacherType = Attacher::AttachEngine3D
  AttachmentOffset = pos=(-21.5005,18.625,0.235) rot=(0,-1,0;0.174533rad)
  BaseFeature = -> Box1260
  Height = 0.3
  Length = 0.6605
  MapMode = 5
  Placement = pos=(-21.5005,18.625,0.235) rot=(0,-1,0;0.174533rad)
  Support = -> [XY_Plane139]
  Width = 0.25
FEATURE [PartDesign::SubtractiveBox] Box1303
  AttacherType = Attacher::AttachEngine3D
  AttachmentOffset = pos=(-21.35,18.635,0.35) rot=(0,0,1;0rad)
  BaseFeature = -> Box1289
  Height = 1.55
  Length = 0.5
  MapMode = 5
  Placement = pos=(-21.35,18.635,0.35) rot=(0,0,1;0rad)
  Support = -> [XY_Plane143]
  Width = 0.23
FEATURE [PartDesign::SubtractiveBox] Box1286
  AttacherType = Attacher::AttachEngine3D
  AttachmentOffset = pos=(-20.5,18.63,0) rot=(0,0,1;0rad)
  BaseFeature = -> Box1303
  Height = 1.635
  Length = 0.5
  MapMode = 5
  Placement = pos=(-20.5,18.63,0) rot=(0,0,1;0rad)
  Support = -> [XY_Plane143]
  Width = 0.25
FEATURE [PartDesign::AdditiveBox] Box1304
  AttacherType = Attacher::AttachEngine3D
  AttachmentOffset = pos=(-21.3,18.635,0) rot=(0,0,1;0rad)
  Height = 1.9
  Length = 1.3
  MapMode = 5
  Placement = pos=(-21.3,18.635,0) rot=(0,0,1;0rad)
  Support = -> [XY_Plane148]
  Width = 0.23
FEATURE [PartDesign::SubtractiveBox] Box1308
  AttacherType = Attacher::AttachEngine3D
  AttachmentOffset = pos=(-21.19,18.635,-0.12) rot=(0,-1,0;0.15708rad)
  BaseFeature = -> Box1286
  Height = 0.12
  Length = 0.725
  MapMode = 5
  Placement = pos=(-21.19,18.635,-0.12) rot=(0,-1,0;0.15708rad)
  Support = -> [XY_Plane143]
  Width = 0.25
FEATURE [PartDesign::SubtractiveBox] Box1298
  AttacherType = Attacher::AttachEngine3D
  AttachmentOffset = pos=(-21.5005,18.625,0.235) rot=(0,-1,0;0.174533rad)
  BaseFeature = -> Box1308
  Height = 0.3
  Length = 0.6605
  MapMode = 5
  Placement = pos=(-21.5005,18.625,0.235) rot=(0,-1,0;0.174533rad)
  Support = -> [XY_Plane143]
  Width = 0.25
FEATURE [PartDesign::AdditiveBox] Box1310
  AttacherType = Attacher::AttachEngine3D
  AttachmentOffset = pos=(-21.3,18.635,0) rot=(0,0,1;0rad)
  Height = 1.9
  Length = 1.3
  MapMode = 5
  Placement = pos=(-21.3,18.635,0) rot=(0,0,1;0rad)
  Support = -> [XY_Plane141]
  Width = 0.23
FEATURE [PartDesign::SubtractiveBox] Box1258
  AttacherType = Attacher::AttachEngine3D
  AttachmentOffset = pos=(-21.35,18.635,0.35) rot=(0,0,1;0rad)
  BaseFeature = -> Box1310
  Height = 1.55
  Length = 0.5
  MapMode = 5
  Placement = pos=(-21.35,18.635,0.35) rot=(0,0,1;0rad)
  Support = -> [XY_Plane141]
  Width = 0.23
FEATURE [PartDesign::SubtractiveBox] Box1313
  AttacherType = Attacher::AttachEngine3D
  AttachmentOffset = pos=(-21.35,18.635,0.35) rot=(0,0,1;0rad)
  BaseFeature = -> Box1304
  Height = 1.55
  Length = 0.5
  MapMode = 5
  Placement = pos=(-21.35,18.635,0.35) rot=(0,0,1;0rad)
  Support = -> [XY_Plane148]
  Width = 0.23
FEATURE [PartDesign::SubtractiveBox] Box1315
  AttacherType = Attacher::AttachEngine3D
  AttachmentOffset = pos=(-21.35,18.635,0.35) rot=(0,0,1;0rad)
  BaseFeature = -> Box1292
  Height = 1.55
  Length = 0.5
  MapMode = 5
  Placement = pos=(-21.35,18.635,0.35) rot=(0,0,1;0rad)
  Support = -> [XY_Plane147]
  Width = 0.23
FEATURE [PartDesign::SubtractiveBox] Box1279
  AttacherType = Attacher::AttachEngine3D
  AttachmentOffset = pos=(-20.5,18.63,0) rot=(0,0,1;0rad)
  BaseFeature = -> Box1315
  Height = 1.635
  Length = 0.5
  MapMode = 5
  Placement = pos=(-20.5,18.63,0) rot=(0,0,1;0rad)
  Support = -> [XY_Plane147]
  Width = 0.25
FEATURE [PartDesign::SubtractiveBox] Box1323
  AttacherType = Attacher::AttachEngine3D
  AttachmentOffset = pos=(-21.5005,18.625,0.235) rot=(0,-1,0;0.174533rad)
  BaseFeature = -> Box1274
  Height = 0.3
  Length = 0.6605
  MapMode = 5
  Placement = pos=(-21.5005,18.625,0.235) rot=(0,-1,0;0.174533rad)
  Support = -> [XY_Plane145]
  Width = 0.25
FEATURE [PartDesign::SubtractiveBox] Box1326
  AttacherType = Attacher::AttachEngine3D
  AttachmentOffset = pos=(-20.5,18.63,0) rot=(0,0,1;0rad)
  BaseFeature = -> Box1313
  Height = 1.635
  Length = 0.5
  MapMode = 5
  Placement = pos=(-20.5,18.63,0) rot=(0,0,1;0rad)
  Support = -> [XY_Plane148]
  Width = 0.25
FEATURE [PartDesign::SubtractiveBox] Box1297
  AttacherType = Attacher::AttachEngine3D
  AttachmentOffset = pos=(-21.19,18.635,-0.12) rot=(0,-1,0;0.15708rad)
  BaseFeature = -> Box1326
  Height = 0.12
  Length = 0.725
  MapMode = 5
  Placement = pos=(-21.19,18.635,-0.12) rot=(0,-1,0;0.15708rad)
  Support = -> [XY_Plane148]
  Width = 0.25
FEATURE [PartDesign::SubtractiveBox] Box1296
  AttacherType = Attacher::AttachEngine3D
  AttachmentOffset = pos=(-21.5005,18.625,0.235) rot=(0,-1,0;0.174533rad)
  BaseFeature = -> Box1297
  Height = 0.3
  Length = 0.6605
  MapMode = 5
  Placement = pos=(-21.5005,18.625,0.235) rot=(0,-1,0;0.174533rad)
  Support = -> [XY_Plane148]
  Width = 0.25
FEATURE [PartDesign::SubtractiveBox] Box1331
  AttacherType = Attacher::AttachEngine3D
  AttachmentOffset = pos=(-21.19,18.635,-0.12) rot=(0,-1,0;0.15708rad)
  BaseFeature = -> Box1279
  Height = 0.12
  Length = 0.725
  MapMode = 5
  Placement = pos=(-21.19,18.635,-0.12) rot=(0,-1,0;0.15708rad)
  Support = -> [XY_Plane147]
  Width = 0.25
FEATURE [PartDesign::SubtractiveBox] Box1291
  AttacherType = Attacher::AttachEngine3D
  AttachmentOffset = pos=(-21.5005,18.625,0.235) rot=(0,-1,0;0.174533rad)
  BaseFeature = -> Box1331
  Height = 0.3
  Length = 0.6605
  MapMode = 5
  Placement = pos=(-21.5005,18.625,0.235) rot=(0,-1,0;0.174533rad)
  Support = -> [XY_Plane147]
  Width = 0.25
FEATURE [PartDesign::AdditiveBox] Box1343
  AttacherType = Attacher::AttachEngine3D
  AttachmentOffset = pos=(-21.3,18.635,0) rot=(0,0,1;0rad)
  Height = 1.9
  Length = 1.3
  MapMode = 5
  Placement = pos=(-21.3,18.635,0) rot=(0,0,1;0rad)
  Support = -> [XY_Plane137]
  Width = 0.23
FEATURE [PartDesign::SubtractiveBox] Box1345
  AttacherType = Attacher::AttachEngine3D
  AttachmentOffset = pos=(-20.5,18.63,0) rot=(0,0,1;0rad)
  BaseFeature = -> Box1247
  Height = 1.635
  Length = 0.5
  MapMode = 5
  Placement = pos=(-20.5,18.63,0) rot=(0,0,1;0rad)
  Support = -> [XY_Plane136]
  Width = 0.25
FEATURE [PartDesign::SubtractiveBox] Box1341
  AttacherType = Attacher::AttachEngine3D
  AttachmentOffset = pos=(-21.19,18.635,-0.12) rot=(0,-1,0;0.15708rad)
  BaseFeature = -> Box1345
  Height = 0.12
  Length = 0.725
  MapMode = 5
  Placement = pos=(-21.19,18.635,-0.12) rot=(0,-1,0;0.15708rad)
  Support = -> [XY_Plane136]
  Width = 0.25
FEATURE [PartDesign::SubtractiveBox] Box1257
  AttacherType = Attacher::AttachEngine3D
  AttachmentOffset = pos=(-21.5005,18.625,0.235) rot=(0,-1,0;0.174533rad)
  BaseFeature = -> Box1341
  Height = 0.3
  Length = 0.6605
  MapMode = 5
  Placement = pos=(-21.5005,18.625,0.235) rot=(0,-1,0;0.174533rad)
  Support = -> [XY_Plane136]
  Width = 0.25
FEATURE [PartDesign::Fillet] Fillet379
  Base = -> Box1257 [Edge2]
  BaseFeature = -> Box1257
  Placement = pos=(-21.5005,18.625,0.235) rot=(0,-1,0;0.174533rad)
  Radius = 0.05
  SupportTransform = false
FEATURE [PartDesign::SubtractiveBox] Box1350
  AttacherType = Attacher::AttachEngine3D
  AttachmentOffset = pos=(-21.35,18.635,0.35) rot=(0,0,1;0rad)
  BaseFeature = -> Box1343
  Height = 1.55
  Length = 0.5
  MapMode = 5
  Placement = pos=(-21.35,18.635,0.35) rot=(0,0,1;0rad)
  Support = -> [XY_Plane137]
  Width = 0.23
FEATURE [PartDesign::SubtractiveBox] Box1328
  AttacherType = Attacher::AttachEngine3D
  AttachmentOffset = pos=(-20.5,18.63,0) rot=(0,0,1;0rad)
  BaseFeature = -> Box1350
  Height = 1.635
  Length = 0.5
  MapMode = 5
  Placement = pos=(-20.5,18.63,0) rot=(0,0,1;0rad)
  Support = -> [XY_Plane137]
  Width = 0.25
FEATURE [PartDesign::SubtractiveBox] Box1327
  AttacherType = Attacher::AttachEngine3D
  AttachmentOffset = pos=(-21.19,18.635,-0.12) rot=(0,-1,0;0.15708rad)
  BaseFeature = -> Box1328
  Height = 0.12
  Length = 0.725
  MapMode = 5
  Placement = pos=(-21.19,18.635,-0.12) rot=(0,-1,0;0.15708rad)
  Support = -> [XY_Plane137]
  Width = 0.25
FEATURE [PartDesign::SubtractiveBox] Box1346
  AttacherType = Attacher::AttachEngine3D
  AttachmentOffset = pos=(-21.5005,18.625,0.235) rot=(0,-1,0;0.174533rad)
  BaseFeature = -> Box1327
  Height = 0.3
  Length = 0.6605
  MapMode = 5
  Placement = pos=(-21.5005,18.625,0.235) rot=(0,-1,0;0.174533rad)
  Support = -> [XY_Plane137]
  Width = 0.25
FEATURE [PartDesign::AdditiveBox] Box1352
  AttacherType = Attacher::AttachEngine3D
  AttachmentOffset = pos=(-21.3,18.635,0) rot=(0,0,1;0rad)
  Height = 1.9
  Length = 1.3
  MapMode = 5
  Placement = pos=(-21.3,18.635,0) rot=(0,0,1;0rad)
  Support = -> [XY_Plane146]
  Width = 0.23
FEATURE [PartDesign::SubtractiveBox] Box1320
  AttacherType = Attacher::AttachEngine3D
  AttachmentOffset = pos=(-21.35,18.635,0.35) rot=(0,0,1;0rad)
  BaseFeature = -> Box1352
  Height = 1.55
  Length = 0.5
  MapMode = 5
  Placement = pos=(-21.35,18.635,0.35) rot=(0,0,1;0rad)
  Support = -> [XY_Plane146]
  Width = 0.23
FEATURE [PartDesign::SubtractiveBox] Box1316
  AttacherType = Attacher::AttachEngine3D
  AttachmentOffset = pos=(-20.5,18.63,0) rot=(0,0,1;0rad)
  BaseFeature = -> Box1320
  Height = 1.635
  Length = 0.5
  MapMode = 5
  Placement = pos=(-20.5,18.63,0) rot=(0,0,1;0rad)
  Support = -> [XY_Plane146]
  Width = 0.25
FEATURE [PartDesign::SubtractiveBox] Box1339
  AttacherType = Attacher::AttachEngine3D
  AttachmentOffset = pos=(-21.19,18.635,-0.12) rot=(0,-1,0;0.15708rad)
  BaseFeature = -> Box1316
  Height = 0.12
  Length = 0.725
  MapMode = 5
  Placement = pos=(-21.19,18.635,-0.12) rot=(0,-1,0;0.15708rad)
  Support = -> [XY_Plane146]
  Width = 0.25
FEATURE [PartDesign::SubtractiveBox] Box1329
  AttacherType = Attacher::AttachEngine3D
  AttachmentOffset = pos=(-21.5005,18.625,0.235) rot=(0,-1,0;0.174533rad)
  BaseFeature = -> Box1339
  Height = 0.3
  Length = 0.6605
  MapMode = 5
  Placement = pos=(-21.5005,18.625,0.235) rot=(0,-1,0;0.174533rad)
  Support = -> [XY_Plane146]
  Width = 0.25
FEATURE [PartDesign::Fillet] Fillet380
  Base = -> Box1329 [Edge2]
  BaseFeature = -> Box1329
  Placement = pos=(-21.5005,18.625,0.235) rot=(0,-1,0;0.174533rad)
  Radius = 0.05
  SupportTransform = false
FEATURE [PartDesign::AdditiveBox] Box1353
  AttacherType = Attacher::AttachEngine3D
  AttachmentOffset = pos=(-21.3,18.635,0) rot=(0,0,1;0rad)
  Height = 1.9
  Length = 1.3
  MapMode = 5
  Placement = pos=(-21.3,18.635,0) rot=(0,0,1;0rad)
  Support = -> [XY_Plane142]
  Width = 0.23
FEATURE [PartDesign::SubtractiveBox] Box1354
  AttacherType = Attacher::AttachEngine3D
  AttachmentOffset = pos=(-20.5,18.63,0) rot=(0,0,1;0rad)
  BaseFeature = -> Box1258
  Height = 1.635
  Length = 0.5
  MapMode = 5
  Placement = pos=(-20.5,18.63,0) rot=(0,0,1;0rad)
  Support = -> [XY_Plane141]
  Width = 0.25
FEATURE [PartDesign::SubtractiveBox] Box1242
  AttacherType = Attacher::AttachEngine3D
  AttachmentOffset = pos=(-21.19,18.635,-0.12) rot=(0,-1,0;0.15708rad)
  BaseFeature = -> Box1354
  Height = 0.12
  Length = 0.725
  MapMode = 5
  Placement = pos=(-21.19,18.635,-0.12) rot=(0,-1,0;0.15708rad)
  Support = -> [XY_Plane141]
  Width = 0.25
FEATURE [PartDesign::SubtractiveBox] Box1251
  AttacherType = Attacher::AttachEngine3D
  AttachmentOffset = pos=(-21.5005,18.625,0.235) rot=(0,-1,0;0.174533rad)
  BaseFeature = -> Box1242
  Height = 0.3
  Length = 0.6605
  MapMode = 5
  Placement = pos=(-21.5005,18.625,0.235) rot=(0,-1,0;0.174533rad)
  Support = -> [XY_Plane141]
  Width = 0.25
FEATURE [PartDesign::SubtractiveBox] Box1360
  AttacherType = Attacher::AttachEngine3D
  AttachmentOffset = pos=(-21.35,18.635,0.35) rot=(0,0,1;0rad)
  BaseFeature = -> Box1353
  Height = 1.55
  Length = 0.5
  MapMode = 5
  Placement = pos=(-21.35,18.635,0.35) rot=(0,0,1;0rad)
  Support = -> [XY_Plane142]
  Width = 0.23
FEATURE [PartDesign::SubtractiveBox] Box1340
  AttacherType = Attacher::AttachEngine3D
  AttachmentOffset = pos=(-20.5,18.63,0) rot=(0,0,1;0rad)
  BaseFeature = -> Box1360
  Height = 1.635
  Length = 0.5
  MapMode = 5
  Placement = pos=(-20.5,18.63,0) rot=(0,0,1;0rad)
  Support = -> [XY_Plane142]
  Width = 0.25
FEATURE [PartDesign::SubtractiveBox] Box1342
  AttacherType = Attacher::AttachEngine3D
  AttachmentOffset = pos=(-21.19,18.635,-0.12) rot=(0,-1,0;0.15708rad)
  BaseFeature = -> Box1340
  Height = 0.12
  Length = 0.725
  MapMode = 5
  Placement = pos=(-21.19,18.635,-0.12) rot=(0,-1,0;0.15708rad)
  Support = -> [XY_Plane142]
  Width = 0.25
FEATURE [PartDesign::SubtractiveBox] Box1338
  AttacherType = Attacher::AttachEngine3D
  AttachmentOffset = pos=(-21.5005,18.625,0.235) rot=(0,-1,0;0.174533rad)
  BaseFeature = -> Box1342
  Height = 0.3
  Length = 0.6605
  MapMode = 5
  Placement = pos=(-21.5005,18.625,0.235) rot=(0,-1,0;0.174533rad)
  Support = -> [XY_Plane142]
  Width = 0.25
FEATURE [PartDesign::SubtractiveBox] Box1361
  AttacherType = Attacher::AttachEngine3D
  AttachmentOffset = pos=(-20.5,18.63,0) rot=(0,0,1;0rad)
  BaseFeature = -> Box1246
  Height = 1.635
  Length = 0.5
  MapMode = 5
  Placement = pos=(-20.5,18.63,0) rot=(0,0,1;0rad)
  Support = -> [XY_Plane140]
  Width = 0.25
FEATURE [PartDesign::SubtractiveBox] Box1306
  AttacherType = Attacher::AttachEngine3D
  AttachmentOffset = pos=(-21.19,18.635,-0.12) rot=(0,-1,0;0.15708rad)
  BaseFeature = -> Box1361
  Height = 0.12
  Length = 0.725
  MapMode = 5
  Placement = pos=(-21.19,18.635,-0.12) rot=(0,-1,0;0.15708rad)
  Support = -> [XY_Plane140]
  Width = 0.25
FEATURE [PartDesign::SubtractiveBox] Box1259
  AttacherType = Attacher::AttachEngine3D
  AttachmentOffset = pos=(-21.5005,18.625,0.235) rot=(0,-1,0;0.174533rad)
  BaseFeature = -> Box1306
  Height = 0.3
  Length = 0.6605
  MapMode = 5
  Placement = pos=(-21.5005,18.625,0.235) rot=(0,-1,0;0.174533rad)
  Support = -> [XY_Plane140]
  Width = 0.25
FEATURE [PartDesign::AdditiveBox] Box1381
  AttacherType = Attacher::AttachEngine3D
  AttachmentOffset = pos=(-21.3,18.635,0) rot=(0,0,1;0rad)
  Height = 1.9
  Length = 1.3
  MapMode = 5
  Placement = pos=(-21.3,18.635,0) rot=(0,0,1;0rad)
  Support = -> [XY_Plane150]
  Width = 0.23
FEATURE [PartDesign::SubtractiveBox] Box1365
  AttacherType = Attacher::AttachEngine3D
  AttachmentOffset = pos=(-21.35,18.635,0.35) rot=(0,0,1;0rad)
  BaseFeature = -> Box1381
  Height = 1.55
  Length = 0.5
  MapMode = 5
  Placement = pos=(-21.35,18.635,0.35) rot=(0,0,1;0rad)
  Support = -> [XY_Plane150]
  Width = 0.23
FEATURE [PartDesign::AdditiveBox] Box1384
  AttacherType = Attacher::AttachEngine3D
  AttachmentOffset = pos=(-21.3,18.635,0) rot=(0,0,1;0rad)
  Height = 1.9
  Length = 1.3
  MapMode = 5
  Placement = pos=(-21.3,18.635,0) rot=(0,0,1;0rad)
  Support = -> [XY_Plane151]
  Width = 0.23
FEATURE [PartDesign::SubtractiveBox] Box1364
  AttacherType = Attacher::AttachEngine3D
  AttachmentOffset = pos=(-21.35,18.635,0.35) rot=(0,0,1;0rad)
  BaseFeature = -> Box1384
  Height = 1.55
  Length = 0.5
  MapMode = 5
  Placement = pos=(-21.35,18.635,0.35) rot=(0,0,1;0rad)
  Support = -> [XY_Plane151]
  Width = 0.23
FEATURE [PartDesign::Fillet] Fillet382
  Base = -> Box1259 [Edge2]
  BaseFeature = -> Box1259
  Placement = pos=(-21.5005,18.625,0.235) rot=(0,-1,0;0.174533rad)
  Radius = 0.05
  SupportTransform = false
FEATURE [PartDesign::Fillet] Fillet373
  Base = -> Fillet382 [Edge33]
  BaseFeature = -> Fillet382
  Placement = pos=(-21.5005,18.625,0.235) rot=(0,-1,0;0.174533rad)
  Radius = 0.5
  SupportTransform = false
FEATURE [PartDesign::AdditiveBox] Box1348
  AttacherType = Attacher::AttachEngine3D
  AttachmentOffset = pos=(-21.1,18.635,0.305) rot=(0,1,0;0.785398rad)
  BaseFeature = -> Fillet373
  Height = 0.375
  Length = 0.2
  MapMode = 5
  Placement = pos=(-21.1,18.635,0.305) rot=(0,1,0;0.785398rad)
  Support = -> [XY_Plane140]
  Width = 0.23
FEATURE [PartDesign::SubtractiveCylinder] Cylinder266
  Angle = 360
  AttacherType = Attacher::AttachEngine3D
  AttachmentOffset = pos=(-21.055,18.935,0.52) rot=(1,0,0;1.5708rad)
  BaseFeature = -> Box1348
  Height = 0.375
  MapMode = 5
  Placement = pos=(-21.055,18.935,0.52) rot=(1,0,0;1.5708rad)
  Radius = 0.205
  Support = -> [XY_Plane140]
FEATURE [PartDesign::SubtractiveBox] Box1231
  AttacherType = Attacher::AttachEngine3D
  AttachmentOffset = pos=(-20.95,18.635,0.53) rot=(0,0,1;0rad)
  BaseFeature = -> Cylinder266
  Height = 0.5
  Length = 0.1
  MapMode = 5
  Placement = pos=(-20.95,18.635,0.53) rot=(0,0,1;0rad)
  Support = -> [XY_Plane140]
  Width = 0.23
FEATURE [PartDesign::SubtractiveBox] Box1249
  AttacherType = Attacher::AttachEngine3D
  AttachmentOffset = pos=(-21.15,18.635,0.297) rot=(0,-1,0;0.174533rad)
  BaseFeature = -> Box1231
  Height = 0.115
  Length = 0.115
  MapMode = 5
  Placement = pos=(-21.15,18.635,0.297) rot=(0,-1,0;0.174533rad)
  Support = -> [XY_Plane140]
  Width = 0.23
FEATURE [PartDesign::Fillet] Fillet376
  Base = -> Box1249 [Edge28]
  BaseFeature = -> Box1249
  Placement = pos=(-21.15,18.635,0.297) rot=(0,-1,0;0.174533rad)
  Radius = 0.375
  SupportTransform = false
FEATURE [PartDesign::AdditiveBox] Box1254
  AttacherType = Attacher::AttachEngine3D
  AttachmentOffset = pos=(-20.7,18.635,1.55) rot=(0,1,0;0.785398rad)
  BaseFeature = -> Fillet376
  Height = 0.375
  Length = 0.23
  MapMode = 5
  Placement = pos=(-20.7,18.635,1.55) rot=(0,1,0;0.785398rad)
  Support = -> [XY_Plane140]
  Width = 0.23
FEATURE [PartDesign::SubtractiveCylinder] Cylinder268
  Angle = 360
  AttacherType = Attacher::AttachEngine3D
  AttachmentOffset = pos=(-20.271,18.635,1.4056) rot=(-1,0,0;1.5708rad)
  BaseFeature = -> Box1254
  Height = 0.23
  MapMode = 5
  Placement = pos=(-20.271,18.635,1.4056) rot=(-1,0,0;1.5708rad)
  Radius = 0.23
  Support = -> [XY_Plane140]
FEATURE [PartDesign::AdditiveBox] Box1245
  AttacherType = Attacher::AttachEngine3D
  AttachmentOffset = pos=(-20.1,18.635,1.635) rot=(0,0,1;0rad)
  BaseFeature = -> Cylinder268
  Height = 0.265
  Length = 0.23
  MapMode = 5
  Placement = pos=(-20.1,18.635,1.635) rot=(0,0,1;0rad)
  Support = -> [XY_Plane140]
  Width = 0.23
FEATURE [PartDesign::Fillet] Fillet383
  Base = -> Fillet380 [Edge33]
  BaseFeature = -> Fillet380
  Placement = pos=(-21.5005,18.625,0.235) rot=(0,-1,0;0.174533rad)
  Radius = 0.5
  SupportTransform = false
FEATURE [PartDesign::AdditiveBox] Box1324
  AttacherType = Attacher::AttachEngine3D
  AttachmentOffset = pos=(-21.1,18.635,0.305) rot=(0,1,0;0.785398rad)
  BaseFeature = -> Fillet383
  Height = 0.375
  Length = 0.2
  MapMode = 5
  Placement = pos=(-21.1,18.635,0.305) rot=(0,1,0;0.785398rad)
  Support = -> [XY_Plane146]
  Width = 0.23
FEATURE [PartDesign::SubtractiveCylinder] Cylinder270
  Angle = 360
  AttacherType = Attacher::AttachEngine3D
  AttachmentOffset = pos=(-21.055,18.935,0.52) rot=(1,0,0;1.5708rad)
  BaseFeature = -> Box1324
  Height = 0.375
  MapMode = 5
  Placement = pos=(-21.055,18.935,0.52) rot=(1,0,0;1.5708rad)
  Radius = 0.205
  Support = -> [XY_Plane146]
FEATURE [PartDesign::SubtractiveBox] Box1332
  AttacherType = Attacher::AttachEngine3D
  AttachmentOffset = pos=(-20.95,18.635,0.53) rot=(0,0,1;0rad)
  BaseFeature = -> Cylinder270
  Height = 0.5
  Length = 0.1
  MapMode = 5
  Placement = pos=(-20.95,18.635,0.53) rot=(0,0,1;0rad)
  Support = -> [XY_Plane146]
  Width = 0.23
FEATURE [PartDesign::SubtractiveBox] Box1325
  AttacherType = Attacher::AttachEngine3D
  AttachmentOffset = pos=(-21.15,18.635,0.297) rot=(0,-1,0;0.174533rad)
  BaseFeature = -> Box1332
  Height = 0.115
  Length = 0.115
  MapMode = 5
  Placement = pos=(-21.15,18.635,0.297) rot=(0,-1,0;0.174533rad)
  Support = -> [XY_Plane146]
  Width = 0.23
FEATURE [PartDesign::Fillet] Fillet384
  Base = -> Box1251 [Edge2]
  BaseFeature = -> Box1251
  Placement = pos=(-21.5005,18.625,0.235) rot=(0,-1,0;0.174533rad)
  Radius = 0.05
  SupportTransform = false
FEATURE [PartDesign::Fillet] Fillet378
  Base = -> Fillet384 [Edge33]
  BaseFeature = -> Fillet384
  Placement = pos=(-21.5005,18.625,0.235) rot=(0,-1,0;0.174533rad)
  Radius = 0.5
  SupportTransform = false
FEATURE [PartDesign::AdditiveBox] Box1357
  AttacherType = Attacher::AttachEngine3D
  AttachmentOffset = pos=(-21.1,18.635,0.305) rot=(0,1,0;0.785398rad)
  BaseFeature = -> Fillet378
  Height = 0.375
  Length = 0.2
  MapMode = 5
  Placement = pos=(-21.1,18.635,0.305) rot=(0,1,0;0.785398rad)
  Support = -> [XY_Plane141]
  Width = 0.23
FEATURE [PartDesign::SubtractiveCylinder] Cylinder275
  Angle = 360
  AttacherType = Attacher::AttachEngine3D
  AttachmentOffset = pos=(-21.055,18.935,0.52) rot=(1,0,0;1.5708rad)
  BaseFeature = -> Box1357
  Height = 0.375
  MapMode = 5
  Placement = pos=(-21.055,18.935,0.52) rot=(1,0,0;1.5708rad)
  Radius = 0.205
  Support = -> [XY_Plane141]
FEATURE [PartDesign::SubtractiveBox] Box1261
  AttacherType = Attacher::AttachEngine3D
  AttachmentOffset = pos=(-20.95,18.635,0.53) rot=(0,0,1;0rad)
  BaseFeature = -> Cylinder275
  Height = 0.5
  Length = 0.1
  MapMode = 5
  Placement = pos=(-20.95,18.635,0.53) rot=(0,0,1;0rad)
  Support = -> [XY_Plane141]
  Width = 0.23
FEATURE [PartDesign::SubtractiveBox] Box1309
  AttacherType = Attacher::AttachEngine3D
  AttachmentOffset = pos=(-21.15,18.635,0.297) rot=(0,-1,0;0.174533rad)
  BaseFeature = -> Box1261
  Height = 0.115
  Length = 0.115
  MapMode = 5
  Placement = pos=(-21.15,18.635,0.297) rot=(0,-1,0;0.174533rad)
  Support = -> [XY_Plane141]
  Width = 0.23
FEATURE [PartDesign::Fillet] Fillet377
  Base = -> Box1309 [Edge28]
  BaseFeature = -> Box1309
  Placement = pos=(-21.15,18.635,0.297) rot=(0,-1,0;0.174533rad)
  Radius = 0.375
  SupportTransform = false
FEATURE [PartDesign::AdditiveBox] Box1347
  AttacherType = Attacher::AttachEngine3D
  AttachmentOffset = pos=(-20.7,18.635,1.55) rot=(0,1,0;0.785398rad)
  BaseFeature = -> Fillet377
  Height = 0.375
  Length = 0.23
  MapMode = 5
  Placement = pos=(-20.7,18.635,1.55) rot=(0,1,0;0.785398rad)
  Support = -> [XY_Plane141]
  Width = 0.23
FEATURE [PartDesign::SubtractiveCylinder] Cylinder253
  Angle = 360
  AttacherType = Attacher::AttachEngine3D
  AttachmentOffset = pos=(-20.271,18.635,1.4056) rot=(-1,0,0;1.5708rad)
  BaseFeature = -> Box1347
  Height = 0.23
  MapMode = 5
  Placement = pos=(-20.271,18.635,1.4056) rot=(-1,0,0;1.5708rad)
  Radius = 0.23
  Support = -> [XY_Plane141]
FEATURE [PartDesign::AdditiveBox] Box1255
  AttacherType = Attacher::AttachEngine3D
  AttachmentOffset = pos=(-20.1,18.635,1.635) rot=(0,0,1;0rad)
  BaseFeature = -> Cylinder253
  Height = 0.265
  Length = 0.23
  MapMode = 5
  Placement = pos=(-20.1,18.635,1.635) rot=(0,0,1;0rad)
  Support = -> [XY_Plane141]
  Width = 0.23
FEATURE [PartDesign::Body] Body126  label="pin126"
  Group = -> [Box1310,Box1258,Box1354,Box1242,Box1251,Fillet384,Fillet378,Box1357,Cylinder275,Box1261,Box1309,Fillet377,Box1347,Cylinder253,Box1255]
  Origin = -> Origin136
  Placement = pos=(0,-2,0) rot=(0,0,1;0rad)
  Tip = -> Box1255
FEATURE [PartDesign::Fillet] Fillet386
  Base = -> Box1346 [Edge2]
  BaseFeature = -> Box1346
  Placement = pos=(-21.5005,18.625,0.235) rot=(0,-1,0;0.174533rad)
  Radius = 0.05
  SupportTransform = false
FEATURE [PartDesign::Fillet] Fillet372
  Base = -> Fillet386 [Edge33]
  BaseFeature = -> Fillet386
  Placement = pos=(-21.5005,18.625,0.235) rot=(0,-1,0;0.174533rad)
  Radius = 0.5
  SupportTransform = false
FEATURE [PartDesign::AdditiveBox] Box1312
  AttacherType = Attacher::AttachEngine3D
  AttachmentOffset = pos=(-21.1,18.635,0.305) rot=(0,1,0;0.785398rad)
  BaseFeature = -> Fillet372
  Height = 0.375
  Length = 0.2
  MapMode = 5
  Placement = pos=(-21.1,18.635,0.305) rot=(0,1,0;0.785398rad)
  Support = -> [XY_Plane137]
  Width = 0.23
FEATURE [PartDesign::SubtractiveCylinder] Cylinder262
  Angle = 360
  AttacherType = Attacher::AttachEngine3D
  AttachmentOffset = pos=(-21.055,18.935,0.52) rot=(1,0,0;1.5708rad)
  BaseFeature = -> Box1312
  Height = 0.375
  MapMode = 5
  Placement = pos=(-21.055,18.935,0.52) rot=(1,0,0;1.5708rad)
  Radius = 0.205
  Support = -> [XY_Plane137]
FEATURE [PartDesign::SubtractiveBox] Box1273
  AttacherType = Attacher::AttachEngine3D
  AttachmentOffset = pos=(-20.95,18.635,0.53) rot=(0,0,1;0rad)
  BaseFeature = -> Cylinder262
  Height = 0.5
  Length = 0.1
  MapMode = 5
  Placement = pos=(-20.95,18.635,0.53) rot=(0,0,1;0rad)
  Support = -> [XY_Plane137]
  Width = 0.23
FEATURE [PartDesign::SubtractiveBox] Box1265
  AttacherType = Attacher::AttachEngine3D
  AttachmentOffset = pos=(-21.15,18.635,0.297) rot=(0,-1,0;0.174533rad)
  BaseFeature = -> Box1273
  Height = 0.115
  Length = 0.115
  MapMode = 5
  Placement = pos=(-21.15,18.635,0.297) rot=(0,-1,0;0.174533rad)
  Support = -> [XY_Plane137]
  Width = 0.23
FEATURE [PartDesign::Fillet] Fillet387
  Base = -> Box1278 [Edge2]
  BaseFeature = -> Box1278
  Placement = pos=(-21.5005,18.625,0.235) rot=(0,-1,0;0.174533rad)
  Radius = 0.05
  SupportTransform = false
FEATURE [PartDesign::Fillet] Fillet374
  Base = -> Fillet387 [Edge33]
  BaseFeature = -> Fillet387
  Placement = pos=(-21.5005,18.625,0.235) rot=(0,-1,0;0.174533rad)
  Radius = 0.5
  SupportTransform = false
FEATURE [PartDesign::AdditiveBox] Box1252
  AttacherType = Attacher::AttachEngine3D
  AttachmentOffset = pos=(-21.1,18.635,0.305) rot=(0,1,0;0.785398rad)
  BaseFeature = -> Fillet374
  Height = 0.375
  Length = 0.2
  MapMode = 5
  Placement = pos=(-21.1,18.635,0.305) rot=(0,1,0;0.785398rad)
  Support = -> [XY_Plane144]
  Width = 0.23
FEATURE [PartDesign::SubtractiveCylinder] Cylinder258
  Angle = 360
  AttacherType = Attacher::AttachEngine3D
  AttachmentOffset = pos=(-21.055,18.935,0.52) rot=(1,0,0;1.5708rad)
  BaseFeature = -> Box1252
  Height = 0.375
  MapMode = 5
  Placement = pos=(-21.055,18.935,0.52) rot=(1,0,0;1.5708rad)
  Radius = 0.205
  Support = -> [XY_Plane144]
FEATURE [PartDesign::SubtractiveBox] Box1280
  AttacherType = Attacher::AttachEngine3D
  AttachmentOffset = pos=(-20.95,18.635,0.53) rot=(0,0,1;0rad)
  BaseFeature = -> Cylinder258
  Height = 0.5
  Length = 0.1
  MapMode = 5
  Placement = pos=(-20.95,18.635,0.53) rot=(0,0,1;0rad)
  Support = -> [XY_Plane144]
  Width = 0.23
FEATURE [PartDesign::SubtractiveBox] Box1253
  AttacherType = Attacher::AttachEngine3D
  AttachmentOffset = pos=(-21.15,18.635,0.297) rot=(0,-1,0;0.174533rad)
  BaseFeature = -> Box1280
  Height = 0.115
  Length = 0.115
  MapMode = 5
  Placement = pos=(-21.15,18.635,0.297) rot=(0,-1,0;0.174533rad)
  Support = -> [XY_Plane144]
  Width = 0.23
FEATURE [PartDesign::Fillet] Fillet381
  Base = -> Box1253 [Edge28]
  BaseFeature = -> Box1253
  Placement = pos=(-21.15,18.635,0.297) rot=(0,-1,0;0.174533rad)
  Radius = 0.375
  SupportTransform = false
FEATURE [PartDesign::AdditiveBox] Box1271
  AttacherType = Attacher::AttachEngine3D
  AttachmentOffset = pos=(-20.7,18.635,1.55) rot=(0,1,0;0.785398rad)
  BaseFeature = -> Fillet381
  Height = 0.375
  Length = 0.23
  MapMode = 5
  Placement = pos=(-20.7,18.635,1.55) rot=(0,1,0;0.785398rad)
  Support = -> [XY_Plane144]
  Width = 0.23
FEATURE [PartDesign::SubtractiveCylinder] Cylinder254
  Angle = 360
  AttacherType = Attacher::AttachEngine3D
  AttachmentOffset = pos=(-20.271,18.635,1.4056) rot=(-1,0,0;1.5708rad)
  BaseFeature = -> Box1271
  Height = 0.23
  MapMode = 5
  Placement = pos=(-20.271,18.635,1.4056) rot=(-1,0,0;1.5708rad)
  Radius = 0.23
  Support = -> [XY_Plane144]
FEATURE [PartDesign::AdditiveBox] Box1287
  AttacherType = Attacher::AttachEngine3D
  AttachmentOffset = pos=(-20.1,18.635,1.635) rot=(0,0,1;0rad)
  BaseFeature = -> Cylinder254
  Height = 0.265
  Length = 0.23
  MapMode = 5
  Placement = pos=(-20.1,18.635,1.635) rot=(0,0,1;0rad)
  Support = -> [XY_Plane144]
  Width = 0.23
FEATURE [PartDesign::Fillet] Fillet389
  Base = -> Box1338 [Edge2]
  BaseFeature = -> Box1338
  Placement = pos=(-21.5005,18.625,0.235) rot=(0,-1,0;0.174533rad)
  Radius = 0.05
  SupportTransform = false
FEATURE [PartDesign::Body] Body129  label="pin129"
  Group = -> [Box1264,Box1246,Box1361,Box1306,Box1259,Fillet382,Fillet373,Box1348,Cylinder266,Box1231,Box1249,Fillet376,Box1254,Cylinder268,Box1245]
  Origin = -> Origin134
  Placement = pos=(0,-2.5,0) rot=(0,0,1;0rad)
  Tip = -> Box1245
FEATURE [PartDesign::Fillet] Fillet391
  Base = -> Fillet379 [Edge33]
  BaseFeature = -> Fillet379
  Placement = pos=(-21.5005,18.625,0.235) rot=(0,-1,0;0.174533rad)
  Radius = 0.5
  SupportTransform = false
FEATURE [PartDesign::AdditiveBox] Box1362
  AttacherType = Attacher::AttachEngine3D
  AttachmentOffset = pos=(-21.1,18.635,0.305) rot=(0,1,0;0.785398rad)
  BaseFeature = -> Fillet391
  Height = 0.375
  Length = 0.2
  MapMode = 5
  Placement = pos=(-21.1,18.635,0.305) rot=(0,1,0;0.785398rad)
  Support = -> [XY_Plane136]
  Width = 0.23
FEATURE [PartDesign::SubtractiveCylinder] Cylinder273
  Angle = 360
  AttacherType = Attacher::AttachEngine3D
  AttachmentOffset = pos=(-21.055,18.935,0.52) rot=(1,0,0;1.5708rad)
  BaseFeature = -> Box1362
  Height = 0.375
  MapMode = 5
  Placement = pos=(-21.055,18.935,0.52) rot=(1,0,0;1.5708rad)
  Radius = 0.205
  Support = -> [XY_Plane136]
FEATURE [PartDesign::SubtractiveBox] Box1356
  AttacherType = Attacher::AttachEngine3D
  AttachmentOffset = pos=(-20.95,18.635,0.53) rot=(0,0,1;0rad)
  BaseFeature = -> Cylinder273
  Height = 0.5
  Length = 0.1
  MapMode = 5
  Placement = pos=(-20.95,18.635,0.53) rot=(0,0,1;0rad)
  Support = -> [XY_Plane136]
  Width = 0.23
FEATURE [PartDesign::SubtractiveBox] Box1344
  AttacherType = Attacher::AttachEngine3D
  AttachmentOffset = pos=(-21.15,18.635,0.297) rot=(0,-1,0;0.174533rad)
  BaseFeature = -> Box1356
  Height = 0.115
  Length = 0.115
  MapMode = 5
  Placement = pos=(-21.15,18.635,0.297) rot=(0,-1,0;0.174533rad)
  Support = -> [XY_Plane136]
  Width = 0.23
FEATURE [PartDesign::Fillet] Fillet392
  Base = -> Box1256 [Edge2]
  BaseFeature = -> Box1256
  Placement = pos=(-21.5005,18.625,0.235) rot=(0,-1,0;0.174533rad)
  Radius = 0.05
  SupportTransform = false
FEATURE [PartDesign::Fillet] Fillet394
  Base = -> Box1344 [Edge28]
  BaseFeature = -> Box1344
  Placement = pos=(-21.15,18.635,0.297) rot=(0,-1,0;0.174533rad)
  Radius = 0.375
  SupportTransform = false
FEATURE [PartDesign::AdditiveBox] Box1355
  AttacherType = Attacher::AttachEngine3D
  AttachmentOffset = pos=(-20.7,18.635,1.55) rot=(0,1,0;0.785398rad)
  BaseFeature = -> Fillet394
  Height = 0.375
  Length = 0.23
  MapMode = 5
  Placement = pos=(-20.7,18.635,1.55) rot=(0,1,0;0.785398rad)
  Support = -> [XY_Plane136]
  Width = 0.23
FEATURE [PartDesign::SubtractiveCylinder] Cylinder265
  Angle = 360
  AttacherType = Attacher::AttachEngine3D
  AttachmentOffset = pos=(-20.271,18.635,1.4056) rot=(-1,0,0;1.5708rad)
  BaseFeature = -> Box1355
  Height = 0.23
  MapMode = 5
  Placement = pos=(-20.271,18.635,1.4056) rot=(-1,0,0;1.5708rad)
  Radius = 0.23
  Support = -> [XY_Plane136]
FEATURE [PartDesign::AdditiveBox] Box1351
  AttacherType = Attacher::AttachEngine3D
  AttachmentOffset = pos=(-20.1,18.635,1.635) rot=(0,0,1;0rad)
  BaseFeature = -> Cylinder265
  Height = 0.265
  Length = 0.23
  MapMode = 5
  Placement = pos=(-20.1,18.635,1.635) rot=(0,0,1;0rad)
  Support = -> [XY_Plane136]
  Width = 0.23
FEATURE [PartDesign::Body] Body130  label="pin130"
  Group = -> [Box1262,Box1247,Box1345,Box1341,Box1257,Fillet379,Fillet391,Box1362,Cylinder273,Box1356,Box1344,Fillet394,Box1355,Cylinder265,Box1351]
  Origin = -> Origin151
  Placement = pos=(0,-1.5,0) rot=(0,0,1;0rad)
  Tip = -> Box1351
FEATURE [PartDesign::Fillet] Fillet395
  Base = -> Box1291 [Edge2]
  BaseFeature = -> Box1291
  Placement = pos=(-21.5005,18.625,0.235) rot=(0,-1,0;0.174533rad)
  Radius = 0.05
  SupportTransform = false
FEATURE [PartDesign::Fillet] Fillet396
  Base = -> Box1325 [Edge28]
  BaseFeature = -> Box1325
  Placement = pos=(-21.15,18.635,0.297) rot=(0,-1,0;0.174533rad)
  Radius = 0.375
  SupportTransform = false
FEATURE [PartDesign::AdditiveBox] Box1330
  AttacherType = Attacher::AttachEngine3D
  AttachmentOffset = pos=(-20.7,18.635,1.55) rot=(0,1,0;0.785398rad)
  BaseFeature = -> Fillet396
  Height = 0.375
  Length = 0.23
  MapMode = 5
  Placement = pos=(-20.7,18.635,1.55) rot=(0,1,0;0.785398rad)
  Support = -> [XY_Plane146]
  Width = 0.23
FEATURE [PartDesign::SubtractiveCylinder] Cylinder271
  Angle = 360
  AttacherType = Attacher::AttachEngine3D
  AttachmentOffset = pos=(-20.271,18.635,1.4056) rot=(-1,0,0;1.5708rad)
  BaseFeature = -> Box1330
  Height = 0.23
  MapMode = 5
  Placement = pos=(-20.271,18.635,1.4056) rot=(-1,0,0;1.5708rad)
  Radius = 0.23
  Support = -> [XY_Plane146]
FEATURE [PartDesign::AdditiveBox] Box1335
  AttacherType = Attacher::AttachEngine3D
  AttachmentOffset = pos=(-20.1,18.635,1.635) rot=(0,0,1;0rad)
  BaseFeature = -> Cylinder271
  Height = 0.265
  Length = 0.23
  MapMode = 5
  Placement = pos=(-20.1,18.635,1.635) rot=(0,0,1;0rad)
  Support = -> [XY_Plane146]
  Width = 0.23
FEATURE [PartDesign::Body] Body125  label="pin125"
  Group = -> [Box1352,Box1320,Box1316,Box1339,Box1329,Fillet380,Fillet383,Box1324,Cylinder270,Box1332,Box1325,Fillet396,Box1330,Cylinder271,Box1335]
  Origin = -> Origin125
  Placement = pos=(0,-0.5,0) rot=(0,0,1;0rad)
  Tip = -> Box1335
FEATURE [PartDesign::Body] Body135  label="pin135"
  Group = -> [Box1275,Box1283,Box1267,Box1272,Box1278,Fillet387,Fillet374,Box1252,Cylinder258,Box1280,Box1253,Fillet381,Box1271,Cylinder254,Box1287]
  Origin = -> Origin129
  Placement = pos=(0,-5,0) rot=(0,0,1;0rad)
  Tip = -> Box1287
FEATURE [PartDesign::Fillet] Fillet401
  Base = -> Box1298 [Edge2]
  BaseFeature = -> Box1298
  Placement = pos=(-21.5005,18.625,0.235) rot=(0,-1,0;0.174533rad)
  Radius = 0.05
  SupportTransform = false
FEATURE [PartDesign::Fillet] Fillet399
  Base = -> Fillet401 [Edge33]
  BaseFeature = -> Fillet401
  Placement = pos=(-21.5005,18.625,0.235) rot=(0,-1,0;0.174533rad)
  Radius = 0.5
  SupportTransform = false
FEATURE [PartDesign::AdditiveBox] Box1317
  AttacherType = Attacher::AttachEngine3D
  AttachmentOffset = pos=(-21.1,18.635,0.305) rot=(0,1,0;0.785398rad)
  BaseFeature = -> Fillet399
  Height = 0.375
  Length = 0.2
  MapMode = 5
  Placement = pos=(-21.1,18.635,0.305) rot=(0,1,0;0.785398rad)
  Support = -> [XY_Plane143]
  Width = 0.23
FEATURE [PartDesign::SubtractiveCylinder] Cylinder264
  Angle = 360
  AttacherType = Attacher::AttachEngine3D
  AttachmentOffset = pos=(-21.055,18.935,0.52) rot=(1,0,0;1.5708rad)
  BaseFeature = -> Box1317
  Height = 0.375
  MapMode = 5
  Placement = pos=(-21.055,18.935,0.52) rot=(1,0,0;1.5708rad)
  Radius = 0.205
  Support = -> [XY_Plane143]
FEATURE [PartDesign::SubtractiveBox] Box1307
  AttacherType = Attacher::AttachEngine3D
  AttachmentOffset = pos=(-20.95,18.635,0.53) rot=(0,0,1;0rad)
  BaseFeature = -> Cylinder264
  Height = 0.5
  Length = 0.1
  MapMode = 5
  Placement = pos=(-20.95,18.635,0.53) rot=(0,0,1;0rad)
  Support = -> [XY_Plane143]
  Width = 0.23
FEATURE [PartDesign::SubtractiveBox] Box1299
  AttacherType = Attacher::AttachEngine3D
  AttachmentOffset = pos=(-21.15,18.635,0.297) rot=(0,-1,0;0.174533rad)
  BaseFeature = -> Box1307
  Height = 0.115
  Length = 0.115
  MapMode = 5
  Placement = pos=(-21.15,18.635,0.297) rot=(0,-1,0;0.174533rad)
  Support = -> [XY_Plane143]
  Width = 0.23
FEATURE [PartDesign::Fillet] Fillet397
  Base = -> Box1299 [Edge28]
  BaseFeature = -> Box1299
  Placement = pos=(-21.15,18.635,0.297) rot=(0,-1,0;0.174533rad)
  Radius = 0.375
  SupportTransform = false
FEATURE [PartDesign::AdditiveBox] Box1305
  AttacherType = Attacher::AttachEngine3D
  AttachmentOffset = pos=(-20.7,18.635,1.55) rot=(0,1,0;0.785398rad)
  BaseFeature = -> Fillet397
  Height = 0.375
  Length = 0.23
  MapMode = 5
  Placement = pos=(-20.7,18.635,1.55) rot=(0,1,0;0.785398rad)
  Support = -> [XY_Plane143]
  Width = 0.23
FEATURE [PartDesign::SubtractiveCylinder] Cylinder263
  Angle = 360
  AttacherType = Attacher::AttachEngine3D
  AttachmentOffset = pos=(-20.271,18.635,1.4056) rot=(-1,0,0;1.5708rad)
  BaseFeature = -> Box1305
  Height = 0.23
  MapMode = 5
  Placement = pos=(-20.271,18.635,1.4056) rot=(-1,0,0;1.5708rad)
  Radius = 0.23
  Support = -> [XY_Plane143]
FEATURE [PartDesign::AdditiveBox] Box1290
  AttacherType = Attacher::AttachEngine3D
  AttachmentOffset = pos=(-20.1,18.635,1.635) rot=(0,0,1;0rad)
  BaseFeature = -> Cylinder263
  Height = 0.265
  Length = 0.23
  MapMode = 5
  Placement = pos=(-20.1,18.635,1.635) rot=(0,0,1;0rad)
  Support = -> [XY_Plane143]
  Width = 0.23
FEATURE [PartDesign::Body] Body133  label="pin133"
  Group = -> [Box1289,Box1303,Box1286,Box1308,Box1298,Fillet401,Fillet399,Box1317,Cylinder264,Box1307,Box1299,Fillet397,Box1305,Cylinder263,Box1290]
  Origin = -> Origin163
  Placement = pos=(0,-4,0) rot=(0,0,1;0rad)
  Tip = -> Box1290
FEATURE [PartDesign::Fillet] Fillet402
  Base = -> Fillet392 [Edge33]
  BaseFeature = -> Fillet392
  Placement = pos=(-21.5005,18.625,0.235) rot=(0,-1,0;0.174533rad)
  Radius = 0.5
  SupportTransform = false
FEATURE [PartDesign::AdditiveBox] Box1284
  AttacherType = Attacher::AttachEngine3D
  AttachmentOffset = pos=(-21.1,18.635,0.305) rot=(0,1,0;0.785398rad)
  BaseFeature = -> Fillet402
  Height = 0.375
  Length = 0.2
  MapMode = 5
  Placement = pos=(-21.1,18.635,0.305) rot=(0,1,0;0.785398rad)
  Support = -> [XY_Plane139]
  Width = 0.23
FEATURE [PartDesign::SubtractiveCylinder] Cylinder260
  Angle = 360
  AttacherType = Attacher::AttachEngine3D
  AttachmentOffset = pos=(-21.055,18.935,0.52) rot=(1,0,0;1.5708rad)
  BaseFeature = -> Box1284
  Height = 0.375
  MapMode = 5
  Placement = pos=(-21.055,18.935,0.52) rot=(1,0,0;1.5708rad)
  Radius = 0.205
  Support = -> [XY_Plane139]
FEATURE [PartDesign::SubtractiveBox] Box1281
  AttacherType = Attacher::AttachEngine3D
  AttachmentOffset = pos=(-20.95,18.635,0.53) rot=(0,0,1;0rad)
  BaseFeature = -> Cylinder260
  Height = 0.5
  Length = 0.1
  MapMode = 5
  Placement = pos=(-20.95,18.635,0.53) rot=(0,0,1;0rad)
  Support = -> [XY_Plane139]
  Width = 0.23
FEATURE [PartDesign::SubtractiveBox] Box1276
  AttacherType = Attacher::AttachEngine3D
  AttachmentOffset = pos=(-21.15,18.635,0.297) rot=(0,-1,0;0.174533rad)
  BaseFeature = -> Box1281
  Height = 0.115
  Length = 0.115
  MapMode = 5
  Placement = pos=(-21.15,18.635,0.297) rot=(0,-1,0;0.174533rad)
  Support = -> [XY_Plane139]
  Width = 0.23
FEATURE [PartDesign::Fillet] Fillet390
  Base = -> Box1276 [Edge28]
  BaseFeature = -> Box1276
  Placement = pos=(-21.15,18.635,0.297) rot=(0,-1,0;0.174533rad)
  Radius = 0.375
  SupportTransform = false
FEATURE [PartDesign::AdditiveBox] Box1288
  AttacherType = Attacher::AttachEngine3D
  AttachmentOffset = pos=(-20.7,18.635,1.55) rot=(0,1,0;0.785398rad)
  BaseFeature = -> Fillet390
  Height = 0.375
  Length = 0.23
  MapMode = 5
  Placement = pos=(-20.7,18.635,1.55) rot=(0,1,0;0.785398rad)
  Support = -> [XY_Plane139]
  Width = 0.23
FEATURE [PartDesign::SubtractiveCylinder] Cylinder261
  Angle = 360
  AttacherType = Attacher::AttachEngine3D
  AttachmentOffset = pos=(-20.271,18.635,1.4056) rot=(-1,0,0;1.5708rad)
  BaseFeature = -> Box1288
  Height = 0.23
  MapMode = 5
  Placement = pos=(-20.271,18.635,1.4056) rot=(-1,0,0;1.5708rad)
  Radius = 0.23
  Support = -> [XY_Plane139]
FEATURE [PartDesign::AdditiveBox] Box1282
  AttacherType = Attacher::AttachEngine3D
  AttachmentOffset = pos=(-20.1,18.635,1.635) rot=(0,0,1;0rad)
  BaseFeature = -> Cylinder261
  Height = 0.265
  Length = 0.23
  MapMode = 5
  Placement = pos=(-20.1,18.635,1.635) rot=(0,0,1;0rad)
  Support = -> [XY_Plane139]
  Width = 0.23
FEATURE [PartDesign::Body] Body136  label="pin136"
  Group = -> [Box1294,Box1300,Box1248,Box1260,Box1256,Fillet392,Fillet402,Box1284,Cylinder260,Box1281,Box1276,Fillet390,Box1288,Cylinder261,Box1282]
  Origin = -> Origin133
  Placement = pos=(0,-5.5,0) rot=(0,0,1;0rad)
  Tip = -> Box1282
FEATURE [PartDesign::Fillet] Fillet403
  Base = -> Box1265 [Edge28]
  BaseFeature = -> Box1265
  Placement = pos=(-21.15,18.635,0.297) rot=(0,-1,0;0.174533rad)
  Radius = 0.375
  SupportTransform = false
FEATURE [PartDesign::AdditiveBox] Box1322
  AttacherType = Attacher::AttachEngine3D
  AttachmentOffset = pos=(-20.7,18.635,1.55) rot=(0,1,0;0.785398rad)
  BaseFeature = -> Fillet403
  Height = 0.375
  Length = 0.23
  MapMode = 5
  Placement = pos=(-20.7,18.635,1.55) rot=(0,1,0;0.785398rad)
  Support = -> [XY_Plane137]
  Width = 0.23
FEATURE [PartDesign::SubtractiveCylinder] Cylinder256
  Angle = 360
  AttacherType = Attacher::AttachEngine3D
  AttachmentOffset = pos=(-20.271,18.635,1.4056) rot=(-1,0,0;1.5708rad)
  BaseFeature = -> Box1322
  Height = 0.23
  MapMode = 5
  Placement = pos=(-20.271,18.635,1.4056) rot=(-1,0,0;1.5708rad)
  Radius = 0.23
  Support = -> [XY_Plane137]
FEATURE [PartDesign::AdditiveBox] Box1334
  AttacherType = Attacher::AttachEngine3D
  AttachmentOffset = pos=(-20.1,18.635,1.635) rot=(0,0,1;0rad)
  BaseFeature = -> Cylinder256
  Height = 0.265
  Length = 0.23
  MapMode = 5
  Placement = pos=(-20.1,18.635,1.635) rot=(0,0,1;0rad)
  Support = -> [XY_Plane137]
  Width = 0.23
FEATURE [PartDesign::Body] Body128  label="pin128"
  Group = -> [Box1343,Box1350,Box1328,Box1327,Box1346,Fillet386,Fillet372,Box1312,Cylinder262,Box1273,Box1265,Fillet403,Box1322,Cylinder256,Box1334]
  Origin = -> Origin137
  Tip = -> Box1334
FEATURE [PartDesign::Fillet] Fillet404
  Base = -> Fillet395 [Edge33]
  BaseFeature = -> Fillet395
  Placement = pos=(-21.5005,18.625,0.235) rot=(0,-1,0;0.174533rad)
  Radius = 0.5
  SupportTransform = false
FEATURE [PartDesign::AdditiveBox] Box1268
  AttacherType = Attacher::AttachEngine3D
  AttachmentOffset = pos=(-21.1,18.635,0.305) rot=(0,1,0;0.785398rad)
  BaseFeature = -> Fillet404
  Height = 0.375
  Length = 0.2
  MapMode = 5
  Placement = pos=(-21.1,18.635,0.305) rot=(0,1,0;0.785398rad)
  Support = -> [XY_Plane147]
  Width = 0.23
FEATURE [PartDesign::SubtractiveCylinder] Cylinder255
  Angle = 360
  AttacherType = Attacher::AttachEngine3D
  AttachmentOffset = pos=(-21.055,18.935,0.52) rot=(1,0,0;1.5708rad)
  BaseFeature = -> Box1268
  Height = 0.375
  MapMode = 5
  Placement = pos=(-21.055,18.935,0.52) rot=(1,0,0;1.5708rad)
  Radius = 0.205
  Support = -> [XY_Plane147]
FEATURE [PartDesign::SubtractiveBox] Box1266
  AttacherType = Attacher::AttachEngine3D
  AttachmentOffset = pos=(-20.95,18.635,0.53) rot=(0,0,1;0rad)
  BaseFeature = -> Cylinder255
  Height = 0.5
  Length = 0.1
  MapMode = 5
  Placement = pos=(-20.95,18.635,0.53) rot=(0,0,1;0rad)
  Support = -> [XY_Plane147]
  Width = 0.23
FEATURE [PartDesign::SubtractiveBox] Box1302
  AttacherType = Attacher::AttachEngine3D
  AttachmentOffset = pos=(-21.15,18.635,0.297) rot=(0,-1,0;0.174533rad)
  BaseFeature = -> Box1266
  Height = 0.115
  Length = 0.115
  MapMode = 5
  Placement = pos=(-21.15,18.635,0.297) rot=(0,-1,0;0.174533rad)
  Support = -> [XY_Plane147]
  Width = 0.23
FEATURE [PartDesign::Fillet] Fillet400
  Base = -> Box1302 [Edge28]
  BaseFeature = -> Box1302
  Placement = pos=(-21.15,18.635,0.297) rot=(0,-1,0;0.174533rad)
  Radius = 0.375
  SupportTransform = false
FEATURE [PartDesign::AdditiveBox] Box1295
  AttacherType = Attacher::AttachEngine3D
  AttachmentOffset = pos=(-20.7,18.635,1.55) rot=(0,1,0;0.785398rad)
  BaseFeature = -> Fillet400
  Height = 0.375
  Length = 0.23
  MapMode = 5
  Placement = pos=(-20.7,18.635,1.55) rot=(0,1,0;0.785398rad)
  Support = -> [XY_Plane147]
  Width = 0.23
FEATURE [PartDesign::SubtractiveCylinder] Cylinder259
  Angle = 360
  AttacherType = Attacher::AttachEngine3D
  AttachmentOffset = pos=(-20.271,18.635,1.4056) rot=(-1,0,0;1.5708rad)
  BaseFeature = -> Box1295
  Height = 0.23
  MapMode = 5
  Placement = pos=(-20.271,18.635,1.4056) rot=(-1,0,0;1.5708rad)
  Radius = 0.23
  Support = -> [XY_Plane147]
FEATURE [PartDesign::AdditiveBox] Box1321
  AttacherType = Attacher::AttachEngine3D
  AttachmentOffset = pos=(-20.1,18.635,1.635) rot=(0,0,1;0rad)
  BaseFeature = -> Cylinder259
  Height = 0.265
  Length = 0.23
  MapMode = 5
  Placement = pos=(-20.1,18.635,1.635) rot=(0,0,1;0rad)
  Support = -> [XY_Plane147]
  Width = 0.23
FEATURE [PartDesign::Body] Body127  label="pin127"
  Group = -> [Box1292,Box1315,Box1279,Box1331,Box1291,Fillet395,Fillet404,Box1268,Cylinder255,Box1266,Box1302,Fillet400,Box1295,Cylinder259,Box1321]
  Origin = -> Origin135
  Placement = pos=(0,-3,0) rot=(0,0,1;0rad)
  Tip = -> Box1321
FEATURE [PartDesign::Fillet] Fillet405
  Base = -> Fillet389 [Edge33]
  BaseFeature = -> Fillet389
  Placement = pos=(-21.5005,18.625,0.235) rot=(0,-1,0;0.174533rad)
  Radius = 0.5
  SupportTransform = false
FEATURE [PartDesign::AdditiveBox] Box1311
  AttacherType = Attacher::AttachEngine3D
  AttachmentOffset = pos=(-21.1,18.635,0.305) rot=(0,1,0;0.785398rad)
  BaseFeature = -> Fillet405
  Height = 0.375
  Length = 0.2
  MapMode = 5
  Placement = pos=(-21.1,18.635,0.305) rot=(0,1,0;0.785398rad)
  Support = -> [XY_Plane142]
  Width = 0.23
FEATURE [PartDesign::SubtractiveCylinder] Cylinder274
  Angle = 360
  AttacherType = Attacher::AttachEngine3D
  AttachmentOffset = pos=(-21.055,18.935,0.52) rot=(1,0,0;1.5708rad)
  BaseFeature = -> Box1311
  Height = 0.375
  MapMode = 5
  Placement = pos=(-21.055,18.935,0.52) rot=(1,0,0;1.5708rad)
  Radius = 0.205
  Support = -> [XY_Plane142]
FEATURE [PartDesign::SubtractiveBox] Box1336
  AttacherType = Attacher::AttachEngine3D
  AttachmentOffset = pos=(-20.95,18.635,0.53) rot=(0,0,1;0rad)
  BaseFeature = -> Cylinder274
  Height = 0.5
  Length = 0.1
  MapMode = 5
  Placement = pos=(-20.95,18.635,0.53) rot=(0,0,1;0rad)
  Support = -> [XY_Plane142]
  Width = 0.23
FEATURE [PartDesign::SubtractiveBox] Box1337
  AttacherType = Attacher::AttachEngine3D
  AttachmentOffset = pos=(-21.15,18.635,0.297) rot=(0,-1,0;0.174533rad)
  BaseFeature = -> Box1336
  Height = 0.115
  Length = 0.115
  MapMode = 5
  Placement = pos=(-21.15,18.635,0.297) rot=(0,-1,0;0.174533rad)
  Support = -> [XY_Plane142]
  Width = 0.23
FEATURE [PartDesign::Fillet] Fillet375
  Base = -> Box1337 [Edge28]
  BaseFeature = -> Box1337
  Placement = pos=(-21.15,18.635,0.297) rot=(0,-1,0;0.174533rad)
  Radius = 0.375
  SupportTransform = false
FEATURE [PartDesign::AdditiveBox] Box1333
  AttacherType = Attacher::AttachEngine3D
  AttachmentOffset = pos=(-20.7,18.635,1.55) rot=(0,1,0;0.785398rad)
  BaseFeature = -> Fillet375
  Height = 0.375
  Length = 0.23
  MapMode = 5
  Placement = pos=(-20.7,18.635,1.55) rot=(0,1,0;0.785398rad)
  Support = -> [XY_Plane142]
  Width = 0.23
FEATURE [PartDesign::SubtractiveCylinder] Cylinder272
  Angle = 360
  AttacherType = Attacher::AttachEngine3D
  AttachmentOffset = pos=(-20.271,18.635,1.4056) rot=(-1,0,0;1.5708rad)
  BaseFeature = -> Box1333
  Height = 0.23
  MapMode = 5
  Placement = pos=(-20.271,18.635,1.4056) rot=(-1,0,0;1.5708rad)
  Radius = 0.23
  Support = -> [XY_Plane142]
FEATURE [PartDesign::AdditiveBox] Box1349
  AttacherType = Attacher::AttachEngine3D
  AttachmentOffset = pos=(-20.1,18.635,1.635) rot=(0,0,1;0rad)
  BaseFeature = -> Cylinder272
  Height = 0.265
  Length = 0.23
  MapMode = 5
  Placement = pos=(-20.1,18.635,1.635) rot=(0,0,1;0rad)
  Support = -> [XY_Plane142]
  Width = 0.23
FEATURE [PartDesign::Body] Body134  label="pin134"
  Group = -> [Box1353,Box1360,Box1340,Box1342,Box1338,Fillet389,Fillet405,Box1311,Cylinder274,Box1336,Box1337,Fillet375,Box1333,Cylinder272,Box1349]
  Origin = -> Origin132
  Placement = pos=(0,-1,0) rot=(0,0,1;0rad)
  Tip = -> Box1349
FEATURE [PartDesign::Fillet] Fillet406
  Base = -> Box1296 [Edge2]
  BaseFeature = -> Box1296
  Placement = pos=(-21.5005,18.625,0.235) rot=(0,-1,0;0.174533rad)
  Radius = 0.05
  SupportTransform = false
FEATURE [PartDesign::Fillet] Fillet393
  Base = -> Fillet406 [Edge33]
  BaseFeature = -> Fillet406
  Placement = pos=(-21.5005,18.625,0.235) rot=(0,-1,0;0.174533rad)
  Radius = 0.5
  SupportTransform = false
FEATURE [PartDesign::AdditiveBox] Box1314
  AttacherType = Attacher::AttachEngine3D
  AttachmentOffset = pos=(-21.1,18.635,0.305) rot=(0,1,0;0.785398rad)
  BaseFeature = -> Fillet393
  Height = 0.375
  Length = 0.2
  MapMode = 5
  Placement = pos=(-21.1,18.635,0.305) rot=(0,1,0;0.785398rad)
  Support = -> [XY_Plane148]
  Width = 0.23
FEATURE [PartDesign::SubtractiveCylinder] Cylinder269
  Angle = 360
  AttacherType = Attacher::AttachEngine3D
  AttachmentOffset = pos=(-21.055,18.935,0.52) rot=(1,0,0;1.5708rad)
  BaseFeature = -> Box1314
  Height = 0.375
  MapMode = 5
  Placement = pos=(-21.055,18.935,0.52) rot=(1,0,0;1.5708rad)
  Radius = 0.205
  Support = -> [XY_Plane148]
FEATURE [PartDesign::SubtractiveBox] Box1318
  AttacherType = Attacher::AttachEngine3D
  AttachmentOffset = pos=(-20.95,18.635,0.53) rot=(0,0,1;0rad)
  BaseFeature = -> Cylinder269
  Height = 0.5
  Length = 0.1
  MapMode = 5
  Placement = pos=(-20.95,18.635,0.53) rot=(0,0,1;0rad)
  Support = -> [XY_Plane148]
  Width = 0.23
FEATURE [PartDesign::SubtractiveBox] Box1301
  AttacherType = Attacher::AttachEngine3D
  AttachmentOffset = pos=(-21.15,18.635,0.297) rot=(0,-1,0;0.174533rad)
  BaseFeature = -> Box1318
  Height = 0.115
  Length = 0.115
  MapMode = 5
  Placement = pos=(-21.15,18.635,0.297) rot=(0,-1,0;0.174533rad)
  Support = -> [XY_Plane148]
  Width = 0.23
FEATURE [PartDesign::Fillet] Fillet385
  Base = -> Box1301 [Edge28]
  BaseFeature = -> Box1301
  Placement = pos=(-21.15,18.635,0.297) rot=(0,-1,0;0.174533rad)
  Radius = 0.375
  SupportTransform = false
FEATURE [PartDesign::AdditiveBox] Box1319
  AttacherType = Attacher::AttachEngine3D
  AttachmentOffset = pos=(-20.7,18.635,1.55) rot=(0,1,0;0.785398rad)
  BaseFeature = -> Fillet385
  Height = 0.375
  Length = 0.23
  MapMode = 5
  Placement = pos=(-20.7,18.635,1.55) rot=(0,1,0;0.785398rad)
  Support = -> [XY_Plane148]
  Width = 0.23
FEATURE [PartDesign::SubtractiveCylinder] Cylinder267
  Angle = 360
  AttacherType = Attacher::AttachEngine3D
  AttachmentOffset = pos=(-20.271,18.635,1.4056) rot=(-1,0,0;1.5708rad)
  BaseFeature = -> Box1319
  Height = 0.23
  MapMode = 5
  Placement = pos=(-20.271,18.635,1.4056) rot=(-1,0,0;1.5708rad)
  Radius = 0.23
  Support = -> [XY_Plane148]
FEATURE [PartDesign::AdditiveBox] Box1293
  AttacherType = Attacher::AttachEngine3D
  AttachmentOffset = pos=(-20.1,18.635,1.635) rot=(0,0,1;0rad)
  BaseFeature = -> Cylinder267
  Height = 0.265
  Length = 0.23
  MapMode = 5
  Placement = pos=(-20.1,18.635,1.635) rot=(0,0,1;0rad)
  Support = -> [XY_Plane148]
  Width = 0.23
FEATURE [PartDesign::Body] Body132  label="pin132"
  Group = -> [Box1304,Box1313,Box1326,Box1297,Box1296,Fillet406,Fillet393,Box1314,Cylinder269,Box1318,Box1301,Fillet385,Box1319,Cylinder267,Box1293]
  Origin = -> Origin152
  Placement = pos=(0,-3.5,0) rot=(0,0,1;0rad)
  Tip = -> Box1293
FEATURE [PartDesign::Fillet] Fillet407
  Base = -> Box1323 [Edge2]
  BaseFeature = -> Box1323
  Placement = pos=(-21.5005,18.625,0.235) rot=(0,-1,0;0.174533rad)
  Radius = 0.05
  SupportTransform = false
FEATURE [PartDesign::Fillet] Fillet388
  Base = -> Fillet407 [Edge33]
  BaseFeature = -> Fillet407
  Placement = pos=(-21.5005,18.625,0.235) rot=(0,-1,0;0.174533rad)
  Radius = 0.5
  SupportTransform = false
FEATURE [PartDesign::AdditiveBox] Box1244
  AttacherType = Attacher::AttachEngine3D
  AttachmentOffset = pos=(-21.1,18.635,0.305) rot=(0,1,0;0.785398rad)
  BaseFeature = -> Fillet388
  Height = 0.375
  Length = 0.2
  MapMode = 5
  Placement = pos=(-21.1,18.635,0.305) rot=(0,1,0;0.785398rad)
  Support = -> [XY_Plane145]
  Width = 0.23
FEATURE [PartDesign::SubtractiveCylinder] Cylinder252
  Angle = 360
  AttacherType = Attacher::AttachEngine3D
  AttachmentOffset = pos=(-21.055,18.935,0.52) rot=(1,0,0;1.5708rad)
  BaseFeature = -> Box1244
  Height = 0.375
  MapMode = 5
  Placement = pos=(-21.055,18.935,0.52) rot=(1,0,0;1.5708rad)
  Radius = 0.205
  Support = -> [XY_Plane145]
FEATURE [PartDesign::SubtractiveBox] Box1243
  AttacherType = Attacher::AttachEngine3D
  AttachmentOffset = pos=(-20.95,18.635,0.53) rot=(0,0,1;0rad)
  BaseFeature = -> Cylinder252
  Height = 0.5
  Length = 0.1
  MapMode = 5
  Placement = pos=(-20.95,18.635,0.53) rot=(0,0,1;0rad)
  Support = -> [XY_Plane145]
  Width = 0.23
FEATURE [PartDesign::SubtractiveBox] Box1250
  AttacherType = Attacher::AttachEngine3D
  AttachmentOffset = pos=(-21.15,18.635,0.297) rot=(0,-1,0;0.174533rad)
  BaseFeature = -> Box1243
  Height = 0.115
  Length = 0.115
  MapMode = 5
  Placement = pos=(-21.15,18.635,0.297) rot=(0,-1,0;0.174533rad)
  Support = -> [XY_Plane145]
  Width = 0.23
FEATURE [PartDesign::Fillet] Fillet398
  Base = -> Box1250 [Edge28]
  BaseFeature = -> Box1250
  Placement = pos=(-21.15,18.635,0.297) rot=(0,-1,0;0.174533rad)
  Radius = 0.375
  SupportTransform = false
FEATURE [PartDesign::AdditiveBox] Box1270
  AttacherType = Attacher::AttachEngine3D
  AttachmentOffset = pos=(-20.7,18.635,1.55) rot=(0,1,0;0.785398rad)
  BaseFeature = -> Fillet398
  Height = 0.375
  Length = 0.23
  MapMode = 5
  Placement = pos=(-20.7,18.635,1.55) rot=(0,1,0;0.785398rad)
  Support = -> [XY_Plane145]
  Width = 0.23
FEATURE [PartDesign::SubtractiveCylinder] Cylinder257
  Angle = 360
  AttacherType = Attacher::AttachEngine3D
  AttachmentOffset = pos=(-20.271,18.635,1.4056) rot=(-1,0,0;1.5708rad)
  BaseFeature = -> Box1270
  Height = 0.23
  MapMode = 5
  Placement = pos=(-20.271,18.635,1.4056) rot=(-1,0,0;1.5708rad)
  Radius = 0.23
  Support = -> [XY_Plane145]
FEATURE [PartDesign::AdditiveBox] Box1263
  AttacherType = Attacher::AttachEngine3D
  AttachmentOffset = pos=(-20.1,18.635,1.635) rot=(0,0,1;0rad)
  BaseFeature = -> Cylinder257
  Height = 0.265
  Length = 0.23
  MapMode = 5
  Placement = pos=(-20.1,18.635,1.635) rot=(0,0,1;0rad)
  Support = -> [XY_Plane145]
  Width = 0.23
FEATURE [PartDesign::Body] Body131  label="pin131"
  Group = -> [Box1277,Box1285,Box1269,Box1274,Box1323,Fillet407,Fillet388,Box1244,Cylinder252,Box1243,Box1250,Fillet398,Box1270,Cylinder257,Box1263]
  Origin = -> Origin140
  Placement = pos=(0,-4.5,0) rot=(0,0,1;0rad)
  Tip = -> Box1263
FEATURE [App::Part] Part011  label="Pin-set010"
  Group = -> [Body128,Body125,Body134,Body130,Body126,Body129,Body127,Body132,Body133,Body131,Body135,Body136]
  Origin = -> Origin145
  Placement = pos=(0,-24,0) rot=(0,0,1;0rad)
FEATURE [PartDesign::AdditiveBox] Box1397
  AttacherType = Attacher::AttachEngine3D
  AttachmentOffset = pos=(-21.3,18.635,0) rot=(0,0,1;0rad)
  Height = 1.9
  Length = 1.3
  MapMode = 5
  Placement = pos=(-21.3,18.635,0) rot=(0,0,1;0rad)
  Support = -> [XY_Plane157]
  Width = 0.23
FEATURE [PartDesign::AdditiveBox] Box1399
  AttacherType = Attacher::AttachEngine3D
  AttachmentOffset = pos=(-21.3,18.635,0) rot=(0,0,1;0rad)
  Height = 1.9
  Length = 1.3
  MapMode = 5
  Placement = pos=(-21.3,18.635,0) rot=(0,0,1;0rad)
  Support = -> [XY_Plane158]
  Width = 0.23
FEATURE [PartDesign::AdditiveBox] Box1404
  AttacherType = Attacher::AttachEngine3D
  AttachmentOffset = pos=(-21.3,18.635,0) rot=(0,0,1;0rad)
  Height = 1.9
  Length = 1.3
  MapMode = 5
  Placement = pos=(-21.3,18.635,0) rot=(0,0,1;0rad)
  Support = -> [XY_Plane153]
  Width = 0.23
FEATURE [PartDesign::SubtractiveBox] Box1406
  AttacherType = Attacher::AttachEngine3D
  AttachmentOffset = pos=(-21.35,18.635,0.35) rot=(0,0,1;0rad)
  BaseFeature = -> Box1399
  Height = 1.55
  Length = 0.5
  MapMode = 5
  Placement = pos=(-21.35,18.635,0.35) rot=(0,0,1;0rad)
  Support = -> [XY_Plane158]
  Width = 0.23
FEATURE [PartDesign::SubtractiveBox] Box1393
  AttacherType = Attacher::AttachEngine3D
  AttachmentOffset = pos=(-20.5,18.63,0) rot=(0,0,1;0rad)
  BaseFeature = -> Box1406
  Height = 1.635
  Length = 0.5
  MapMode = 5
  Placement = pos=(-20.5,18.63,0) rot=(0,0,1;0rad)
  Support = -> [XY_Plane158]
  Width = 0.25
FEATURE [PartDesign::SubtractiveBox] Box1394
  AttacherType = Attacher::AttachEngine3D
  AttachmentOffset = pos=(-21.19,18.635,-0.12) rot=(0,-1,0;0.15708rad)
  BaseFeature = -> Box1393
  Height = 0.12
  Length = 0.725
  MapMode = 5
  Placement = pos=(-21.19,18.635,-0.12) rot=(0,-1,0;0.15708rad)
  Support = -> [XY_Plane158]
  Width = 0.25
FEATURE [PartDesign::SubtractiveBox] Box1409
  AttacherType = Attacher::AttachEngine3D
  AttachmentOffset = pos=(-21.35,18.635,0.35) rot=(0,0,1;0rad)
  BaseFeature = -> Box1397
  Height = 1.55
  Length = 0.5
  MapMode = 5
  Placement = pos=(-21.35,18.635,0.35) rot=(0,0,1;0rad)
  Support = -> [XY_Plane157]
  Width = 0.23
FEATURE [PartDesign::SubtractiveBox] Box1396
  AttacherType = Attacher::AttachEngine3D
  AttachmentOffset = pos=(-20.5,18.63,0) rot=(0,0,1;0rad)
  BaseFeature = -> Box1409
  Height = 1.635
  Length = 0.5
  MapMode = 5
  Placement = pos=(-20.5,18.63,0) rot=(0,0,1;0rad)
  Support = -> [XY_Plane157]
  Width = 0.25
FEATURE [PartDesign::SubtractiveBox] Box1391
  AttacherType = Attacher::AttachEngine3D
  AttachmentOffset = pos=(-21.19,18.635,-0.12) rot=(0,-1,0;0.15708rad)
  BaseFeature = -> Box1396
  Height = 0.12
  Length = 0.725
  MapMode = 5
  Placement = pos=(-21.19,18.635,-0.12) rot=(0,-1,0;0.15708rad)
  Support = -> [XY_Plane157]
  Width = 0.25
FEATURE [PartDesign::SubtractiveBox] Box1389
  AttacherType = Attacher::AttachEngine3D
  AttachmentOffset = pos=(-21.5005,18.625,0.235) rot=(0,-1,0;0.174533rad)
  BaseFeature = -> Box1391
  Height = 0.3
  Length = 0.6605
  MapMode = 5
  Placement = pos=(-21.5005,18.625,0.235) rot=(0,-1,0;0.174533rad)
  Support = -> [XY_Plane157]
  Width = 0.25
FEATURE [PartDesign::AdditiveBox] Box1413
  AttacherType = Attacher::AttachEngine3D
  AttachmentOffset = pos=(-21.3,18.635,0) rot=(0,0,1;0rad)
  Height = 1.9
  Length = 1.3
  MapMode = 5
  Placement = pos=(-21.3,18.635,0) rot=(0,0,1;0rad)
  Support = -> [XY_Plane159]
  Width = 0.23
FEATURE [PartDesign::AdditiveBox] Box1414
  AttacherType = Attacher::AttachEngine3D
  AttachmentOffset = pos=(-21.3,18.635,0) rot=(0,0,1;0rad)
  Height = 1.9
  Length = 1.3
  MapMode = 5
  Placement = pos=(-21.3,18.635,0) rot=(0,0,1;0rad)
  Support = -> [XY_Plane160]
  Width = 0.23
FEATURE [PartDesign::AdditiveBox] Box1417
  AttacherType = Attacher::AttachEngine3D
  AttachmentOffset = pos=(-21.3,18.635,0) rot=(0,0,1;0rad)
  Height = 1.9
  Length = 1.3
  MapMode = 5
  Placement = pos=(-21.3,18.635,0) rot=(0,0,1;0rad)
  Support = -> [XY_Plane162]
  Width = 0.23
FEATURE [PartDesign::SubtractiveBox] Box1418
  AttacherType = Attacher::AttachEngine3D
  AttachmentOffset = pos=(-21.35,18.635,0.35) rot=(0,0,1;0rad)
  BaseFeature = -> Box1404
  Height = 1.55
  Length = 0.5
  MapMode = 5
  Placement = pos=(-21.35,18.635,0.35) rot=(0,0,1;0rad)
  Support = -> [XY_Plane153]
  Width = 0.23
FEATURE [PartDesign::SubtractiveBox] Box1358
  AttacherType = Attacher::AttachEngine3D
  AttachmentOffset = pos=(-20.5,18.63,0) rot=(0,0,1;0rad)
  BaseFeature = -> Box1418
  Height = 1.635
  Length = 0.5
  MapMode = 5
  Placement = pos=(-20.5,18.63,0) rot=(0,0,1;0rad)
  Support = -> [XY_Plane153]
  Width = 0.25
FEATURE [PartDesign::SubtractiveBox] Box1377
  AttacherType = Attacher::AttachEngine3D
  AttachmentOffset = pos=(-21.19,18.635,-0.12) rot=(0,-1,0;0.15708rad)
  BaseFeature = -> Box1358
  Height = 0.12
  Length = 0.725
  MapMode = 5
  Placement = pos=(-21.19,18.635,-0.12) rot=(0,-1,0;0.15708rad)
  Support = -> [XY_Plane153]
  Width = 0.25
FEATURE [PartDesign::SubtractiveBox] Box1373
  AttacherType = Attacher::AttachEngine3D
  AttachmentOffset = pos=(-21.5005,18.625,0.235) rot=(0,-1,0;0.174533rad)
  BaseFeature = -> Box1377
  Height = 0.3
  Length = 0.6605
  MapMode = 5
  Placement = pos=(-21.5005,18.625,0.235) rot=(0,-1,0;0.174533rad)
  Support = -> [XY_Plane153]
  Width = 0.25
FEATURE [PartDesign::AdditiveBox] Box1420
  AttacherType = Attacher::AttachEngine3D
  AttachmentOffset = pos=(-21.3,18.635,0) rot=(0,0,1;0rad)
  Height = 1.9
  Length = 1.3
  MapMode = 5
  Placement = pos=(-21.3,18.635,0) rot=(0,0,1;0rad)
  Support = -> [XY_Plane154]
  Width = 0.23
FEATURE [PartDesign::SubtractiveBox] Box1372
  AttacherType = Attacher::AttachEngine3D
  AttachmentOffset = pos=(-21.35,18.635,0.35) rot=(0,0,1;0rad)
  BaseFeature = -> Box1420
  Height = 1.55
  Length = 0.5
  MapMode = 5
  Placement = pos=(-21.35,18.635,0.35) rot=(0,0,1;0rad)
  Support = -> [XY_Plane154]
  Width = 0.23
FEATURE [PartDesign::SubtractiveBox] Box1427
  AttacherType = Attacher::AttachEngine3D
  AttachmentOffset = pos=(-21.35,18.635,0.35) rot=(0,0,1;0rad)
  BaseFeature = -> Box1413
  Height = 1.55
  Length = 0.5
  MapMode = 5
  Placement = pos=(-21.35,18.635,0.35) rot=(0,0,1;0rad)
  Support = -> [XY_Plane159]
  Width = 0.23
FEATURE [PartDesign::SubtractiveBox] Box1407
  AttacherType = Attacher::AttachEngine3D
  AttachmentOffset = pos=(-20.5,18.63,0) rot=(0,0,1;0rad)
  BaseFeature = -> Box1427
  Height = 1.635
  Length = 0.5
  MapMode = 5
  Placement = pos=(-20.5,18.63,0) rot=(0,0,1;0rad)
  Support = -> [XY_Plane159]
  Width = 0.25
FEATURE [PartDesign::SubtractiveBox] Box1428
  AttacherType = Attacher::AttachEngine3D
  AttachmentOffset = pos=(-21.19,18.635,-0.12) rot=(0,-1,0;0.15708rad)
  BaseFeature = -> Box1407
  Height = 0.12
  Length = 0.725
  MapMode = 5
  Placement = pos=(-21.19,18.635,-0.12) rot=(0,-1,0;0.15708rad)
  Support = -> [XY_Plane159]
  Width = 0.25
FEATURE [PartDesign::SubtractiveBox] Box1422
  AttacherType = Attacher::AttachEngine3D
  AttachmentOffset = pos=(-21.5005,18.625,0.235) rot=(0,-1,0;0.174533rad)
  BaseFeature = -> Box1428
  Height = 0.3
  Length = 0.6605
  MapMode = 5
  Placement = pos=(-21.5005,18.625,0.235) rot=(0,-1,0;0.174533rad)
  Support = -> [XY_Plane159]
  Width = 0.25
FEATURE [PartDesign::SubtractiveBox] Box1434
  AttacherType = Attacher::AttachEngine3D
  AttachmentOffset = pos=(-21.35,18.635,0.35) rot=(0,0,1;0rad)
  BaseFeature = -> Box1414
  Height = 1.55
  Length = 0.5
  MapMode = 5
  Placement = pos=(-21.35,18.635,0.35) rot=(0,0,1;0rad)
  Support = -> [XY_Plane160]
  Width = 0.23
FEATURE [PartDesign::SubtractiveBox] Box1400
  AttacherType = Attacher::AttachEngine3D
  AttachmentOffset = pos=(-20.5,18.63,0) rot=(0,0,1;0rad)
  BaseFeature = -> Box1434
  Height = 1.635
  Length = 0.5
  MapMode = 5
  Placement = pos=(-20.5,18.63,0) rot=(0,0,1;0rad)
  Support = -> [XY_Plane160]
  Width = 0.25
FEATURE [PartDesign::SubtractiveBox] Box1436
  AttacherType = Attacher::AttachEngine3D
  AttachmentOffset = pos=(-21.35,18.635,0.35) rot=(0,0,1;0rad)
  BaseFeature = -> Box1417
  Height = 1.55
  Length = 0.5
  MapMode = 5
  Placement = pos=(-21.35,18.635,0.35) rot=(0,0,1;0rad)
  Support = -> [XY_Plane162]
  Width = 0.23
FEATURE [PartDesign::SubtractiveBox] Box1442
  AttacherType = Attacher::AttachEngine3D
  AttachmentOffset = pos=(-21.5005,18.625,0.235) rot=(0,-1,0;0.174533rad)
  BaseFeature = -> Box1394
  Height = 0.3
  Length = 0.6605
  MapMode = 5
  Placement = pos=(-21.5005,18.625,0.235) rot=(0,-1,0;0.174533rad)
  Support = -> [XY_Plane158]
  Width = 0.25
FEATURE [PartDesign::SubtractiveBox] Box1448
  AttacherType = Attacher::AttachEngine3D
  AttachmentOffset = pos=(-20.5,18.63,0) rot=(0,0,1;0rad)
  BaseFeature = -> Box1436
  Height = 1.635
  Length = 0.5
  MapMode = 5
  Placement = pos=(-20.5,18.63,0) rot=(0,0,1;0rad)
  Support = -> [XY_Plane162]
  Width = 0.25
FEATURE [PartDesign::SubtractiveBox] Box1421
  AttacherType = Attacher::AttachEngine3D
  AttachmentOffset = pos=(-21.19,18.635,-0.12) rot=(0,-1,0;0.15708rad)
  BaseFeature = -> Box1448
  Height = 0.12
  Length = 0.725
  MapMode = 5
  Placement = pos=(-21.19,18.635,-0.12) rot=(0,-1,0;0.15708rad)
  Support = -> [XY_Plane162]
  Width = 0.25
FEATURE [PartDesign::SubtractiveBox] Box1405
  AttacherType = Attacher::AttachEngine3D
  AttachmentOffset = pos=(-21.5005,18.625,0.235) rot=(0,-1,0;0.174533rad)
  BaseFeature = -> Box1421
  Height = 0.3
  Length = 0.6605
  MapMode = 5
  Placement = pos=(-21.5005,18.625,0.235) rot=(0,-1,0;0.174533rad)
  Support = -> [XY_Plane162]
  Width = 0.25
FEATURE [PartDesign::AdditiveBox] Box1453
  AttacherType = Attacher::AttachEngine3D
  AttachmentOffset = pos=(-21.3,18.635,0) rot=(0,0,1;0rad)
  Height = 1.9
  Length = 1.3
  MapMode = 5
  Placement = pos=(-21.3,18.635,0) rot=(0,0,1;0rad)
  Support = -> [XY_Plane155]
  Width = 0.23
FEATURE [PartDesign::SubtractiveBox] Box1460
  AttacherType = Attacher::AttachEngine3D
  AttachmentOffset = pos=(-21.19,18.635,-0.12) rot=(0,-1,0;0.15708rad)
  BaseFeature = -> Box1400
  Height = 0.12
  Length = 0.725
  MapMode = 5
  Placement = pos=(-21.19,18.635,-0.12) rot=(0,-1,0;0.15708rad)
  Support = -> [XY_Plane160]
  Width = 0.25
FEATURE [PartDesign::SubtractiveBox] Box1402
  AttacherType = Attacher::AttachEngine3D
  AttachmentOffset = pos=(-21.5005,18.625,0.235) rot=(0,-1,0;0.174533rad)
  BaseFeature = -> Box1460
  Height = 0.3
  Length = 0.6605
  MapMode = 5
  Placement = pos=(-21.5005,18.625,0.235) rot=(0,-1,0;0.174533rad)
  Support = -> [XY_Plane160]
  Width = 0.25
FEATURE [PartDesign::SubtractiveBox] Box1469
  AttacherType = Attacher::AttachEngine3D
  AttachmentOffset = pos=(-20.5,18.63,0) rot=(0,0,1;0rad)
  BaseFeature = -> Box1364
  Height = 1.635
  Length = 0.5
  MapMode = 5
  Placement = pos=(-20.5,18.63,0) rot=(0,0,1;0rad)
  Support = -> [XY_Plane151]
  Width = 0.25
FEATURE [PartDesign::SubtractiveBox] Box1425
  AttacherType = Attacher::AttachEngine3D
  AttachmentOffset = pos=(-21.19,18.635,-0.12) rot=(0,-1,0;0.15708rad)
  BaseFeature = -> Box1469
  Height = 0.12
  Length = 0.725
  MapMode = 5
  Placement = pos=(-21.19,18.635,-0.12) rot=(0,-1,0;0.15708rad)
  Support = -> [XY_Plane151]
  Width = 0.25
FEATURE [PartDesign::SubtractiveBox] Box1379
  AttacherType = Attacher::AttachEngine3D
  AttachmentOffset = pos=(-21.5005,18.625,0.235) rot=(0,-1,0;0.174533rad)
  BaseFeature = -> Box1425
  Height = 0.3
  Length = 0.6605
  MapMode = 5
  Placement = pos=(-21.5005,18.625,0.235) rot=(0,-1,0;0.174533rad)
  Support = -> [XY_Plane151]
  Width = 0.25
FEATURE [PartDesign::SubtractiveBox] Box1471
  AttacherType = Attacher::AttachEngine3D
  AttachmentOffset = pos=(-21.35,18.635,0.35) rot=(0,0,1;0rad)
  BaseFeature = -> Box1453
  Height = 1.55
  Length = 0.5
  MapMode = 5
  Placement = pos=(-21.35,18.635,0.35) rot=(0,0,1;0rad)
  Support = -> [XY_Plane155]
  Width = 0.23
FEATURE [PartDesign::SubtractiveBox] Box1439
  AttacherType = Attacher::AttachEngine3D
  AttachmentOffset = pos=(-20.5,18.63,0) rot=(0,0,1;0rad)
  BaseFeature = -> Box1471
  Height = 1.635
  Length = 0.5
  MapMode = 5
  Placement = pos=(-20.5,18.63,0) rot=(0,0,1;0rad)
  Support = -> [XY_Plane155]
  Width = 0.25
FEATURE [PartDesign::SubtractiveBox] Box1449
  AttacherType = Attacher::AttachEngine3D
  AttachmentOffset = pos=(-21.19,18.635,-0.12) rot=(0,-1,0;0.15708rad)
  BaseFeature = -> Box1439
  Height = 0.12
  Length = 0.725
  MapMode = 5
  Placement = pos=(-21.19,18.635,-0.12) rot=(0,-1,0;0.15708rad)
  Support = -> [XY_Plane155]
  Width = 0.25
FEATURE [PartDesign::SubtractiveBox] Box1464
  AttacherType = Attacher::AttachEngine3D
  AttachmentOffset = pos=(-21.5005,18.625,0.235) rot=(0,-1,0;0.174533rad)
  BaseFeature = -> Box1449
  Height = 0.3
  Length = 0.6605
  MapMode = 5
  Placement = pos=(-21.5005,18.625,0.235) rot=(0,-1,0;0.174533rad)
  Support = -> [XY_Plane155]
  Width = 0.25
FEATURE [PartDesign::AdditiveBox] Box1472
  AttacherType = Attacher::AttachEngine3D
  AttachmentOffset = pos=(-21.3,18.635,0) rot=(0,0,1;0rad)
  Height = 1.9
  Length = 1.3
  MapMode = 5
  Placement = pos=(-21.3,18.635,0) rot=(0,0,1;0rad)
  Support = -> [XY_Plane156]
  Width = 0.23
FEATURE [PartDesign::SubtractiveBox] Box1446
  AttacherType = Attacher::AttachEngine3D
  AttachmentOffset = pos=(-21.35,18.635,0.35) rot=(0,0,1;0rad)
  BaseFeature = -> Box1472
  Height = 1.55
  Length = 0.5
  MapMode = 5
  Placement = pos=(-21.35,18.635,0.35) rot=(0,0,1;0rad)
  Support = -> [XY_Plane156]
  Width = 0.23
FEATURE [PartDesign::SubtractiveBox] Box1435
  AttacherType = Attacher::AttachEngine3D
  AttachmentOffset = pos=(-20.5,18.63,0) rot=(0,0,1;0rad)
  BaseFeature = -> Box1446
  Height = 1.635
  Length = 0.5
  MapMode = 5
  Placement = pos=(-20.5,18.63,0) rot=(0,0,1;0rad)
  Support = -> [XY_Plane156]
  Width = 0.25
FEATURE [PartDesign::SubtractiveBox] Box1462
  AttacherType = Attacher::AttachEngine3D
  AttachmentOffset = pos=(-21.19,18.635,-0.12) rot=(0,-1,0;0.15708rad)
  BaseFeature = -> Box1435
  Height = 0.12
  Length = 0.725
  MapMode = 5
  Placement = pos=(-21.19,18.635,-0.12) rot=(0,-1,0;0.15708rad)
  Support = -> [XY_Plane156]
  Width = 0.25
FEATURE [PartDesign::SubtractiveBox] Box1450
  AttacherType = Attacher::AttachEngine3D
  AttachmentOffset = pos=(-21.5005,18.625,0.235) rot=(0,-1,0;0.174533rad)
  BaseFeature = -> Box1462
  Height = 0.3
  Length = 0.6605
  MapMode = 5
  Placement = pos=(-21.5005,18.625,0.235) rot=(0,-1,0;0.174533rad)
  Support = -> [XY_Plane156]
  Width = 0.25
FEATURE [PartDesign::SubtractiveBox] Box1473
  AttacherType = Attacher::AttachEngine3D
  AttachmentOffset = pos=(-20.5,18.63,0) rot=(0,0,1;0rad)
  BaseFeature = -> Box1365
  Height = 1.635
  Length = 0.5
  MapMode = 5
  Placement = pos=(-20.5,18.63,0) rot=(0,0,1;0rad)
  Support = -> [XY_Plane150]
  Width = 0.25
FEATURE [PartDesign::SubtractiveBox] Box1452
  AttacherType = Attacher::AttachEngine3D
  AttachmentOffset = pos=(-21.19,18.635,-0.12) rot=(0,-1,0;0.15708rad)
  BaseFeature = -> Box1473
  Height = 0.12
  Length = 0.725
  MapMode = 5
  Placement = pos=(-21.19,18.635,-0.12) rot=(0,-1,0;0.15708rad)
  Support = -> [XY_Plane150]
  Width = 0.25
FEATURE [PartDesign::SubtractiveBox] Box1376
  AttacherType = Attacher::AttachEngine3D
  AttachmentOffset = pos=(-21.5005,18.625,0.235) rot=(0,-1,0;0.174533rad)
  BaseFeature = -> Box1452
  Height = 0.3
  Length = 0.6605
  MapMode = 5
  Placement = pos=(-21.5005,18.625,0.235) rot=(0,-1,0;0.174533rad)
  Support = -> [XY_Plane150]
  Width = 0.25
FEATURE [PartDesign::AdditiveBox] Box1474
  AttacherType = Attacher::AttachEngine3D
  AttachmentOffset = pos=(-21.3,18.635,0) rot=(0,0,1;0rad)
  Height = 1.9
  Length = 1.3
  MapMode = 5
  Placement = pos=(-21.3,18.635,0) rot=(0,0,1;0rad)
  Support = -> [XY_Plane152]
  Width = 0.23
FEATURE [PartDesign::SubtractiveBox] Box1468
  AttacherType = Attacher::AttachEngine3D
  AttachmentOffset = pos=(-21.35,18.635,0.35) rot=(0,0,1;0rad)
  BaseFeature = -> Box1474
  Height = 1.55
  Length = 0.5
  MapMode = 5
  Placement = pos=(-21.35,18.635,0.35) rot=(0,0,1;0rad)
  Support = -> [XY_Plane152]
  Width = 0.23
FEATURE [PartDesign::SubtractiveBox] Box1458
  AttacherType = Attacher::AttachEngine3D
  AttachmentOffset = pos=(-20.5,18.63,0) rot=(0,0,1;0rad)
  BaseFeature = -> Box1468
  Height = 1.635
  Length = 0.5
  MapMode = 5
  Placement = pos=(-20.5,18.63,0) rot=(0,0,1;0rad)
  Support = -> [XY_Plane152]
  Width = 0.25
FEATURE [PartDesign::SubtractiveBox] Box1463
  AttacherType = Attacher::AttachEngine3D
  AttachmentOffset = pos=(-21.19,18.635,-0.12) rot=(0,-1,0;0.15708rad)
  BaseFeature = -> Box1458
  Height = 0.12
  Length = 0.725
  MapMode = 5
  Placement = pos=(-21.19,18.635,-0.12) rot=(0,-1,0;0.15708rad)
  Support = -> [XY_Plane152]
  Width = 0.25
FEATURE [PartDesign::SubtractiveBox] Box1459
  AttacherType = Attacher::AttachEngine3D
  AttachmentOffset = pos=(-21.5005,18.625,0.235) rot=(0,-1,0;0.174533rad)
  BaseFeature = -> Box1463
  Height = 0.3
  Length = 0.6605
  MapMode = 5
  Placement = pos=(-21.5005,18.625,0.235) rot=(0,-1,0;0.174533rad)
  Support = -> [XY_Plane152]
  Width = 0.25
FEATURE [PartDesign::SubtractiveBox] Box1475
  AttacherType = Attacher::AttachEngine3D
  AttachmentOffset = pos=(-20.5,18.63,0) rot=(0,0,1;0rad)
  BaseFeature = -> Box1372
  Height = 1.635
  Length = 0.5
  MapMode = 5
  Placement = pos=(-20.5,18.63,0) rot=(0,0,1;0rad)
  Support = -> [XY_Plane154]
  Width = 0.25
FEATURE [PartDesign::SubtractiveBox] Box1370
  AttacherType = Attacher::AttachEngine3D
  AttachmentOffset = pos=(-21.19,18.635,-0.12) rot=(0,-1,0;0.15708rad)
  BaseFeature = -> Box1475
  Height = 0.12
  Length = 0.725
  MapMode = 5
  Placement = pos=(-21.19,18.635,-0.12) rot=(0,-1,0;0.15708rad)
  Support = -> [XY_Plane154]
  Width = 0.25
FEATURE [PartDesign::SubtractiveBox] Box1371
  AttacherType = Attacher::AttachEngine3D
  AttachmentOffset = pos=(-21.5005,18.625,0.235) rot=(0,-1,0;0.174533rad)
  BaseFeature = -> Box1370
  Height = 0.3
  Length = 0.6605
  MapMode = 5
  Placement = pos=(-21.5005,18.625,0.235) rot=(0,-1,0;0.174533rad)
  Support = -> [XY_Plane154]
  Width = 0.25
FEATURE [PartDesign::Fillet] Fillet409
  Base = -> Box1464 [Edge2]
  BaseFeature = -> Box1464
  Placement = pos=(-21.5005,18.625,0.235) rot=(0,-1,0;0.174533rad)
  Radius = 0.05
  SupportTransform = false
FEATURE [PartDesign::Fillet] Fillet408
  Base = -> Fillet409 [Edge33]
  BaseFeature = -> Fillet409
  Placement = pos=(-21.5005,18.625,0.235) rot=(0,-1,0;0.174533rad)
  Radius = 0.5
  SupportTransform = false
FEATURE [PartDesign::AdditiveBox] Box1431
  AttacherType = Attacher::AttachEngine3D
  AttachmentOffset = pos=(-21.1,18.635,0.305) rot=(0,1,0;0.785398rad)
  BaseFeature = -> Fillet408
  Height = 0.375
  Length = 0.2
  MapMode = 5
  Placement = pos=(-21.1,18.635,0.305) rot=(0,1,0;0.785398rad)
  Support = -> [XY_Plane155]
  Width = 0.23
FEATURE [PartDesign::SubtractiveCylinder] Cylinder285
  Angle = 360
  AttacherType = Attacher::AttachEngine3D
  AttachmentOffset = pos=(-21.055,18.935,0.52) rot=(1,0,0;1.5708rad)
  BaseFeature = -> Box1431
  Height = 0.375
  MapMode = 5
  Placement = pos=(-21.055,18.935,0.52) rot=(1,0,0;1.5708rad)
  Radius = 0.205
  Support = -> [XY_Plane155]
FEATURE [PartDesign::SubtractiveBox] Box1388
  AttacherType = Attacher::AttachEngine3D
  AttachmentOffset = pos=(-20.95,18.635,0.53) rot=(0,0,1;0rad)
  BaseFeature = -> Cylinder285
  Height = 0.5
  Length = 0.1
  MapMode = 5
  Placement = pos=(-20.95,18.635,0.53) rot=(0,0,1;0rad)
  Support = -> [XY_Plane155]
  Width = 0.23
FEATURE [PartDesign::SubtractiveBox] Box1385
  AttacherType = Attacher::AttachEngine3D
  AttachmentOffset = pos=(-21.15,18.635,0.297) rot=(0,-1,0;0.174533rad)
  BaseFeature = -> Box1388
  Height = 0.115
  Length = 0.115
  MapMode = 5
  Placement = pos=(-21.15,18.635,0.297) rot=(0,-1,0;0.174533rad)
  Support = -> [XY_Plane155]
  Width = 0.23
FEATURE [PartDesign::Fillet] Fillet413
  Base = -> Box1389 [Edge2]
  BaseFeature = -> Box1389
  Placement = pos=(-21.5005,18.625,0.235) rot=(0,-1,0;0.174533rad)
  Radius = 0.05
  SupportTransform = false
FEATURE [PartDesign::Fillet] Fillet416
  Base = -> Fillet413 [Edge33]
  BaseFeature = -> Fillet413
  Placement = pos=(-21.5005,18.625,0.235) rot=(0,-1,0;0.174533rad)
  Radius = 0.5
  SupportTransform = false
FEATURE [PartDesign::AdditiveBox] Box1380
  AttacherType = Attacher::AttachEngine3D
  AttachmentOffset = pos=(-21.1,18.635,0.305) rot=(0,1,0;0.785398rad)
  BaseFeature = -> Fillet416
  Height = 0.375
  Length = 0.2
  MapMode = 5
  Placement = pos=(-21.1,18.635,0.305) rot=(0,1,0;0.785398rad)
  Support = -> [XY_Plane157]
  Width = 0.23
FEATURE [PartDesign::SubtractiveCylinder] Cylinder283
  Angle = 360
  AttacherType = Attacher::AttachEngine3D
  AttachmentOffset = pos=(-21.055,18.935,0.52) rot=(1,0,0;1.5708rad)
  BaseFeature = -> Box1380
  Height = 0.375
  MapMode = 5
  Placement = pos=(-21.055,18.935,0.52) rot=(1,0,0;1.5708rad)
  Radius = 0.205
  Support = -> [XY_Plane157]
FEATURE [PartDesign::SubtractiveBox] Box1390
  AttacherType = Attacher::AttachEngine3D
  AttachmentOffset = pos=(-20.95,18.635,0.53) rot=(0,0,1;0rad)
  BaseFeature = -> Cylinder283
  Height = 0.5
  Length = 0.1
  MapMode = 5
  Placement = pos=(-20.95,18.635,0.53) rot=(0,0,1;0rad)
  Support = -> [XY_Plane157]
  Width = 0.23
FEATURE [PartDesign::SubtractiveBox] Box1375
  AttacherType = Attacher::AttachEngine3D
  AttachmentOffset = pos=(-21.15,18.635,0.297) rot=(0,-1,0;0.174533rad)
  BaseFeature = -> Box1390
  Height = 0.115
  Length = 0.115
  MapMode = 5
  Placement = pos=(-21.15,18.635,0.297) rot=(0,-1,0;0.174533rad)
  Support = -> [XY_Plane157]
  Width = 0.23
FEATURE [PartDesign::Fillet] Fillet415
  Base = -> Box1375 [Edge28]
  BaseFeature = -> Box1375
  Placement = pos=(-21.15,18.635,0.297) rot=(0,-1,0;0.174533rad)
  Radius = 0.375
  SupportTransform = false
FEATURE [PartDesign::AdditiveBox] Box1395
  AttacherType = Attacher::AttachEngine3D
  AttachmentOffset = pos=(-20.7,18.635,1.55) rot=(0,1,0;0.785398rad)
  BaseFeature = -> Fillet415
  Height = 0.375
  Length = 0.23
  MapMode = 5
  Placement = pos=(-20.7,18.635,1.55) rot=(0,1,0;0.785398rad)
  Support = -> [XY_Plane157]
  Width = 0.23
FEATURE [PartDesign::SubtractiveCylinder] Cylinder277
  Angle = 360
  AttacherType = Attacher::AttachEngine3D
  AttachmentOffset = pos=(-20.271,18.635,1.4056) rot=(-1,0,0;1.5708rad)
  BaseFeature = -> Box1395
  Height = 0.23
  MapMode = 5
  Placement = pos=(-20.271,18.635,1.4056) rot=(-1,0,0;1.5708rad)
  Radius = 0.23
  Support = -> [XY_Plane157]
FEATURE [PartDesign::AdditiveBox] Box1410
  AttacherType = Attacher::AttachEngine3D
  AttachmentOffset = pos=(-20.1,18.635,1.635) rot=(0,0,1;0rad)
  BaseFeature = -> Cylinder277
  Height = 0.265
  Length = 0.23
  MapMode = 5
  Placement = pos=(-20.1,18.635,1.635) rot=(0,0,1;0rad)
  Support = -> [XY_Plane157]
  Width = 0.23
FEATURE [PartDesign::Fillet] Fillet419
  Base = -> Box1450 [Edge2]
  BaseFeature = -> Box1450
  Placement = pos=(-21.5005,18.625,0.235) rot=(0,-1,0;0.174533rad)
  Radius = 0.05
  SupportTransform = false
FEATURE [PartDesign::Fillet] Fillet410
  Base = -> Fillet419 [Edge33]
  BaseFeature = -> Fillet419
  Placement = pos=(-21.5005,18.625,0.235) rot=(0,-1,0;0.174533rad)
  Radius = 0.5
  SupportTransform = false
FEATURE [PartDesign::AdditiveBox] Box1438
  AttacherType = Attacher::AttachEngine3D
  AttachmentOffset = pos=(-21.1,18.635,0.305) rot=(0,1,0;0.785398rad)
  BaseFeature = -> Fillet410
  Height = 0.375
  Length = 0.2
  MapMode = 5
  Placement = pos=(-21.1,18.635,0.305) rot=(0,1,0;0.785398rad)
  Support = -> [XY_Plane156]
  Width = 0.23
FEATURE [PartDesign::SubtractiveCylinder] Cylinder294
  Angle = 360
  AttacherType = Attacher::AttachEngine3D
  AttachmentOffset = pos=(-21.055,18.935,0.52) rot=(1,0,0;1.5708rad)
  BaseFeature = -> Box1438
  Height = 0.375
  MapMode = 5
  Placement = pos=(-21.055,18.935,0.52) rot=(1,0,0;1.5708rad)
  Radius = 0.205
  Support = -> [XY_Plane156]
FEATURE [PartDesign::SubtractiveBox] Box1455
  AttacherType = Attacher::AttachEngine3D
  AttachmentOffset = pos=(-20.95,18.635,0.53) rot=(0,0,1;0rad)
  BaseFeature = -> Cylinder294
  Height = 0.5
  Length = 0.1
  MapMode = 5
  Placement = pos=(-20.95,18.635,0.53) rot=(0,0,1;0rad)
  Support = -> [XY_Plane156]
  Width = 0.23
FEATURE [PartDesign::SubtractiveBox] Box1443
  AttacherType = Attacher::AttachEngine3D
  AttachmentOffset = pos=(-21.15,18.635,0.297) rot=(0,-1,0;0.174533rad)
  BaseFeature = -> Box1455
  Height = 0.115
  Length = 0.115
  MapMode = 5
  Placement = pos=(-21.15,18.635,0.297) rot=(0,-1,0;0.174533rad)
  Support = -> [XY_Plane156]
  Width = 0.23
FEATURE [PartDesign::Fillet] Fillet421
  Base = -> Box1376 [Edge2]
  BaseFeature = -> Box1376
  Placement = pos=(-21.5005,18.625,0.235) rot=(0,-1,0;0.174533rad)
  Radius = 0.05
  SupportTransform = false
FEATURE [PartDesign::Fillet] Fillet422
  Base = -> Box1373 [Edge2]
  BaseFeature = -> Box1373
  Placement = pos=(-21.5005,18.625,0.235) rot=(0,-1,0;0.174533rad)
  Radius = 0.05
  SupportTransform = false
FEATURE [PartDesign::Fillet] Fillet423
  Base = -> Box1379 [Edge2]
  BaseFeature = -> Box1379
  Placement = pos=(-21.5005,18.625,0.235) rot=(0,-1,0;0.174533rad)
  Radius = 0.05
  SupportTransform = false
FEATURE [PartDesign::Fillet] Fillet412
  Base = -> Fillet423 [Edge33]
  BaseFeature = -> Fillet423
  Placement = pos=(-21.5005,18.625,0.235) rot=(0,-1,0;0.174533rad)
  Radius = 0.5
  SupportTransform = false
FEATURE [PartDesign::AdditiveBox] Box1477
  AttacherType = Attacher::AttachEngine3D
  AttachmentOffset = pos=(-21.1,18.635,0.305) rot=(0,1,0;0.785398rad)
  BaseFeature = -> Fillet412
  Height = 0.375
  Length = 0.2
  MapMode = 5
  Placement = pos=(-21.1,18.635,0.305) rot=(0,1,0;0.785398rad)
  Support = -> [XY_Plane151]
  Width = 0.23
FEATURE [PartDesign::SubtractiveCylinder] Cylinder290
  Angle = 360
  AttacherType = Attacher::AttachEngine3D
  AttachmentOffset = pos=(-21.055,18.935,0.52) rot=(1,0,0;1.5708rad)
  BaseFeature = -> Box1477
  Height = 0.375
  MapMode = 5
  Placement = pos=(-21.055,18.935,0.52) rot=(1,0,0;1.5708rad)
  Radius = 0.205
  Support = -> [XY_Plane151]
FEATURE [PartDesign::SubtractiveBox] Box1367
  AttacherType = Attacher::AttachEngine3D
  AttachmentOffset = pos=(-20.95,18.635,0.53) rot=(0,0,1;0rad)
  BaseFeature = -> Cylinder290
  Height = 0.5
  Length = 0.1
  MapMode = 5
  Placement = pos=(-20.95,18.635,0.53) rot=(0,0,1;0rad)
  Support = -> [XY_Plane151]
  Width = 0.23
FEATURE [PartDesign::SubtractiveBox] Box1369
  AttacherType = Attacher::AttachEngine3D
  AttachmentOffset = pos=(-21.15,18.635,0.297) rot=(0,-1,0;0.174533rad)
  BaseFeature = -> Box1367
  Height = 0.115
  Length = 0.115
  MapMode = 5
  Placement = pos=(-21.15,18.635,0.297) rot=(0,-1,0;0.174533rad)
  Support = -> [XY_Plane151]
  Width = 0.23
FEATURE [PartDesign::Fillet] Fillet420
  Base = -> Box1369 [Edge28]
  BaseFeature = -> Box1369
  Placement = pos=(-21.15,18.635,0.297) rot=(0,-1,0;0.174533rad)
  Radius = 0.375
  SupportTransform = false
FEATURE [PartDesign::AdditiveBox] Box1374
  AttacherType = Attacher::AttachEngine3D
  AttachmentOffset = pos=(-20.7,18.635,1.55) rot=(0,1,0;0.785398rad)
  BaseFeature = -> Fillet420
  Height = 0.375
  Length = 0.23
  MapMode = 5
  Placement = pos=(-20.7,18.635,1.55) rot=(0,1,0;0.785398rad)
  Support = -> [XY_Plane151]
  Width = 0.23
FEATURE [PartDesign::SubtractiveCylinder] Cylinder293
  Angle = 360
  AttacherType = Attacher::AttachEngine3D
  AttachmentOffset = pos=(-20.271,18.635,1.4056) rot=(-1,0,0;1.5708rad)
  BaseFeature = -> Box1374
  Height = 0.23
  MapMode = 5
  Placement = pos=(-20.271,18.635,1.4056) rot=(-1,0,0;1.5708rad)
  Radius = 0.23
  Support = -> [XY_Plane151]
FEATURE [PartDesign::AdditiveBox] Box1366
  AttacherType = Attacher::AttachEngine3D
  AttachmentOffset = pos=(-20.1,18.635,1.635) rot=(0,0,1;0rad)
  BaseFeature = -> Cylinder293
  Height = 0.265
  Length = 0.23
  MapMode = 5
  Placement = pos=(-20.1,18.635,1.635) rot=(0,0,1;0rad)
  Support = -> [XY_Plane151]
  Width = 0.23
FEATURE [PartDesign::Fillet] Fillet424
  Base = -> Box1371 [Edge2]
  BaseFeature = -> Box1371
  Placement = pos=(-21.5005,18.625,0.235) rot=(0,-1,0;0.174533rad)
  Radius = 0.05
  SupportTransform = false
FEATURE [PartDesign::Fillet] Fillet417
  Base = -> Fillet424 [Edge33]
  BaseFeature = -> Fillet424
  Placement = pos=(-21.5005,18.625,0.235) rot=(0,-1,0;0.174533rad)
  Radius = 0.5
  SupportTransform = false
FEATURE [PartDesign::AdditiveBox] Box1480
  AttacherType = Attacher::AttachEngine3D
  AttachmentOffset = pos=(-21.1,18.635,0.305) rot=(0,1,0;0.785398rad)
  BaseFeature = -> Fillet417
  Height = 0.375
  Length = 0.2
  MapMode = 5
  Placement = pos=(-21.1,18.635,0.305) rot=(0,1,0;0.785398rad)
  Support = -> [XY_Plane154]
  Width = 0.23
FEATURE [PartDesign::Fillet] Fillet427
  Base = -> Box1402 [Edge2]
  BaseFeature = -> Box1402
  Placement = pos=(-21.5005,18.625,0.235) rot=(0,-1,0;0.174533rad)
  Radius = 0.05
  SupportTransform = false
FEATURE [PartDesign::Body] Body142  label="pin142"
  Group = -> [Box1397,Box1409,Box1396,Box1391,Box1389,Fillet413,Fillet416,Box1380,Cylinder283,Box1390,Box1375,Fillet415,Box1395,Cylinder277,Box1410]
  Origin = -> Origin146
  Placement = pos=(0,-5,0) rot=(0,0,1;0rad)
  Tip = -> Box1410
FEATURE [PartDesign::Fillet] Fillet430
  Base = -> Box1385 [Edge28]
  BaseFeature = -> Box1385
  Placement = pos=(-21.15,18.635,0.297) rot=(0,-1,0;0.174533rad)
  Radius = 0.375
  SupportTransform = false
FEATURE [PartDesign::AdditiveBox] Box1441
  AttacherType = Attacher::AttachEngine3D
  AttachmentOffset = pos=(-20.7,18.635,1.55) rot=(0,1,0;0.785398rad)
  BaseFeature = -> Fillet430
  Height = 0.375
  Length = 0.23
  MapMode = 5
  Placement = pos=(-20.7,18.635,1.55) rot=(0,1,0;0.785398rad)
  Support = -> [XY_Plane155]
  Width = 0.23
FEATURE [PartDesign::SubtractiveCylinder] Cylinder279
  Angle = 360
  AttacherType = Attacher::AttachEngine3D
  AttachmentOffset = pos=(-20.271,18.635,1.4056) rot=(-1,0,0;1.5708rad)
  BaseFeature = -> Box1441
  Height = 0.23
  MapMode = 5
  Placement = pos=(-20.271,18.635,1.4056) rot=(-1,0,0;1.5708rad)
  Radius = 0.23
  Support = -> [XY_Plane155]
FEATURE [PartDesign::AdditiveBox] Box1457
  AttacherType = Attacher::AttachEngine3D
  AttachmentOffset = pos=(-20.1,18.635,1.635) rot=(0,0,1;0rad)
  BaseFeature = -> Cylinder279
  Height = 0.265
  Length = 0.23
  MapMode = 5
  Placement = pos=(-20.1,18.635,1.635) rot=(0,0,1;0rad)
  Support = -> [XY_Plane155]
  Width = 0.23
FEATURE [PartDesign::Body] Body140  label="pin140"
  Group = -> [Box1453,Box1471,Box1439,Box1449,Box1464,Fillet409,Fillet408,Box1431,Cylinder285,Box1388,Box1385,Fillet430,Box1441,Cylinder279,Box1457]
  Origin = -> Origin165
  Tip = -> Box1457
FEATURE [PartDesign::Fillet] Fillet433
  Base = -> Box1443 [Edge28]
  BaseFeature = -> Box1443
  Placement = pos=(-21.15,18.635,0.297) rot=(0,-1,0;0.174533rad)
  Radius = 0.375
  SupportTransform = false
FEATURE [PartDesign::AdditiveBox] Box1440
  AttacherType = Attacher::AttachEngine3D
  AttachmentOffset = pos=(-20.7,18.635,1.55) rot=(0,1,0;0.785398rad)
  BaseFeature = -> Fillet433
  Height = 0.375
  Length = 0.23
  MapMode = 5
  Placement = pos=(-20.7,18.635,1.55) rot=(0,1,0;0.785398rad)
  Support = -> [XY_Plane156]
  Width = 0.23
FEATURE [PartDesign::SubtractiveCylinder] Cylinder295
  Angle = 360
  AttacherType = Attacher::AttachEngine3D
  AttachmentOffset = pos=(-20.271,18.635,1.4056) rot=(-1,0,0;1.5708rad)
  BaseFeature = -> Box1440
  Height = 0.23
  MapMode = 5
  Placement = pos=(-20.271,18.635,1.4056) rot=(-1,0,0;1.5708rad)
  Radius = 0.23
  Support = -> [XY_Plane156]
FEATURE [PartDesign::AdditiveBox] Box1456
  AttacherType = Attacher::AttachEngine3D
  AttachmentOffset = pos=(-20.1,18.635,1.635) rot=(0,0,1;0rad)
  BaseFeature = -> Cylinder295
  Height = 0.265
  Length = 0.23
  MapMode = 5
  Placement = pos=(-20.1,18.635,1.635) rot=(0,0,1;0rad)
  Support = -> [XY_Plane156]
  Width = 0.23
FEATURE [PartDesign::Body] Body137  label="pin137"
  Group = -> [Box1472,Box1446,Box1435,Box1462,Box1450,Fillet419,Fillet410,Box1438,Cylinder294,Box1455,Box1443,Fillet433,Box1440,Cylinder295,Box1456]
  Origin = -> Origin153
  Placement = pos=(0,-0.5,0) rot=(0,0,1;0rad)
  Tip = -> Box1456
FEATURE [PartDesign::Fillet] Fillet434
  Base = -> Fillet421 [Edge33]
  BaseFeature = -> Fillet421
  Placement = pos=(-21.5005,18.625,0.235) rot=(0,-1,0;0.174533rad)
  Radius = 0.5
  SupportTransform = false
FEATURE [PartDesign::AdditiveBox] Box1470
  AttacherType = Attacher::AttachEngine3D
  AttachmentOffset = pos=(-21.1,18.635,0.305) rot=(0,1,0;0.785398rad)
  BaseFeature = -> Fillet434
  Height = 0.375
  Length = 0.2
  MapMode = 5
  Placement = pos=(-21.1,18.635,0.305) rot=(0,1,0;0.785398rad)
  Support = -> [XY_Plane150]
  Width = 0.23
FEATURE [PartDesign::SubtractiveCylinder] Cylinder296
  Angle = 360
  AttacherType = Attacher::AttachEngine3D
  AttachmentOffset = pos=(-21.055,18.935,0.52) rot=(1,0,0;1.5708rad)
  BaseFeature = -> Box1470
  Height = 0.375
  MapMode = 5
  Placement = pos=(-21.055,18.935,0.52) rot=(1,0,0;1.5708rad)
  Radius = 0.205
  Support = -> [XY_Plane150]
FEATURE [PartDesign::SubtractiveBox] Box1467
  AttacherType = Attacher::AttachEngine3D
  AttachmentOffset = pos=(-20.95,18.635,0.53) rot=(0,0,1;0rad)
  BaseFeature = -> Cylinder296
  Height = 0.5
  Length = 0.1
  MapMode = 5
  Placement = pos=(-20.95,18.635,0.53) rot=(0,0,1;0rad)
  Support = -> [XY_Plane150]
  Width = 0.23
FEATURE [PartDesign::SubtractiveBox] Box1466
  AttacherType = Attacher::AttachEngine3D
  AttachmentOffset = pos=(-21.15,18.635,0.297) rot=(0,-1,0;0.174533rad)
  BaseFeature = -> Box1467
  Height = 0.115
  Length = 0.115
  MapMode = 5
  Placement = pos=(-21.15,18.635,0.297) rot=(0,-1,0;0.174533rad)
  Support = -> [XY_Plane150]
  Width = 0.23
FEATURE [PartDesign::Fillet] Fillet426
  Base = -> Box1466 [Edge28]
  BaseFeature = -> Box1466
  Placement = pos=(-21.15,18.635,0.297) rot=(0,-1,0;0.174533rad)
  Radius = 0.375
  SupportTransform = false
FEATURE [PartDesign::AdditiveBox] Box1476
  AttacherType = Attacher::AttachEngine3D
  AttachmentOffset = pos=(-20.7,18.635,1.55) rot=(0,1,0;0.785398rad)
  BaseFeature = -> Fillet426
  Height = 0.375
  Length = 0.23
  MapMode = 5
  Placement = pos=(-20.7,18.635,1.55) rot=(0,1,0;0.785398rad)
  Support = -> [XY_Plane150]
  Width = 0.23
FEATURE [PartDesign::SubtractiveCylinder] Cylinder289
  Angle = 360
  AttacherType = Attacher::AttachEngine3D
  AttachmentOffset = pos=(-20.271,18.635,1.4056) rot=(-1,0,0;1.5708rad)
  BaseFeature = -> Box1476
  Height = 0.23
  MapMode = 5
  Placement = pos=(-20.271,18.635,1.4056) rot=(-1,0,0;1.5708rad)
  Radius = 0.23
  Support = -> [XY_Plane150]
FEATURE [PartDesign::AdditiveBox] Box1479
  AttacherType = Attacher::AttachEngine3D
  AttachmentOffset = pos=(-20.1,18.635,1.635) rot=(0,0,1;0rad)
  BaseFeature = -> Cylinder289
  Height = 0.265
  Length = 0.23
  MapMode = 5
  Placement = pos=(-20.1,18.635,1.635) rot=(0,0,1;0rad)
  Support = -> [XY_Plane150]
  Width = 0.23
FEATURE [PartDesign::Fillet] Fillet435
  Base = -> Box1459 [Edge2]
  BaseFeature = -> Box1459
  Placement = pos=(-21.5005,18.625,0.235) rot=(0,-1,0;0.174533rad)
  Radius = 0.05
  SupportTransform = false
FEATURE [PartDesign::Fillet] Fillet431
  Base = -> Fillet435 [Edge33]
  BaseFeature = -> Fillet435
  Placement = pos=(-21.5005,18.625,0.235) rot=(0,-1,0;0.174533rad)
  Radius = 0.5
  SupportTransform = false
FEATURE [PartDesign::AdditiveBox] Box1432
  AttacherType = Attacher::AttachEngine3D
  AttachmentOffset = pos=(-21.1,18.635,0.305) rot=(0,1,0;0.785398rad)
  BaseFeature = -> Fillet431
  Height = 0.375
  Length = 0.2
  MapMode = 5
  Placement = pos=(-21.1,18.635,0.305) rot=(0,1,0;0.785398rad)
  Support = -> [XY_Plane152]
  Width = 0.23
FEATURE [PartDesign::SubtractiveCylinder] Cylinder298
  Angle = 360
  AttacherType = Attacher::AttachEngine3D
  AttachmentOffset = pos=(-21.055,18.935,0.52) rot=(1,0,0;1.5708rad)
  BaseFeature = -> Box1432
  Height = 0.375
  MapMode = 5
  Placement = pos=(-21.055,18.935,0.52) rot=(1,0,0;1.5708rad)
  Radius = 0.205
  Support = -> [XY_Plane152]
FEATURE [PartDesign::SubtractiveBox] Box1461
  AttacherType = Attacher::AttachEngine3D
  AttachmentOffset = pos=(-20.95,18.635,0.53) rot=(0,0,1;0rad)
  BaseFeature = -> Cylinder298
  Height = 0.5
  Length = 0.1
  MapMode = 5
  Placement = pos=(-20.95,18.635,0.53) rot=(0,0,1;0rad)
  Support = -> [XY_Plane152]
  Width = 0.23
FEATURE [PartDesign::SubtractiveBox] Box1451
  AttacherType = Attacher::AttachEngine3D
  AttachmentOffset = pos=(-21.15,18.635,0.297) rot=(0,-1,0;0.174533rad)
  BaseFeature = -> Box1461
  Height = 0.115
  Length = 0.115
  MapMode = 5
  Placement = pos=(-21.15,18.635,0.297) rot=(0,-1,0;0.174533rad)
  Support = -> [XY_Plane152]
  Width = 0.23
FEATURE [PartDesign::Fillet] Fillet414
  Base = -> Box1451 [Edge28]
  BaseFeature = -> Box1451
  Placement = pos=(-21.15,18.635,0.297) rot=(0,-1,0;0.174533rad)
  Radius = 0.375
  SupportTransform = false
FEATURE [PartDesign::AdditiveBox] Box1454
  AttacherType = Attacher::AttachEngine3D
  AttachmentOffset = pos=(-20.7,18.635,1.55) rot=(0,1,0;0.785398rad)
  BaseFeature = -> Fillet414
  Height = 0.375
  Length = 0.23
  MapMode = 5
  Placement = pos=(-20.7,18.635,1.55) rot=(0,1,0;0.785398rad)
  Support = -> [XY_Plane152]
  Width = 0.23
FEATURE [PartDesign::SubtractiveCylinder] Cylinder297
  Angle = 360
  AttacherType = Attacher::AttachEngine3D
  AttachmentOffset = pos=(-20.271,18.635,1.4056) rot=(-1,0,0;1.5708rad)
  BaseFeature = -> Box1454
  Height = 0.23
  MapMode = 5
  Placement = pos=(-20.271,18.635,1.4056) rot=(-1,0,0;1.5708rad)
  Radius = 0.23
  Support = -> [XY_Plane152]
FEATURE [PartDesign::AdditiveBox] Box1478
  AttacherType = Attacher::AttachEngine3D
  AttachmentOffset = pos=(-20.1,18.635,1.635) rot=(0,0,1;0rad)
  BaseFeature = -> Cylinder297
  Height = 0.265
  Length = 0.23
  MapMode = 5
  Placement = pos=(-20.1,18.635,1.635) rot=(0,0,1;0rad)
  Support = -> [XY_Plane152]
  Width = 0.23
FEATURE [PartDesign::Body] Body143  label="pin143"
  Group = -> [Box1474,Box1468,Box1458,Box1463,Box1459,Fillet435,Fillet431,Box1432,Cylinder298,Box1461,Box1451,Fillet414,Box1454,Cylinder297,Box1478]
  Origin = -> Origin155
  Placement = pos=(0,-1,0) rot=(0,0,1;0rad)
  Tip = -> Box1478
FEATURE [PartDesign::Body] Body145  label="pin145"
  Group = -> [Box1384,Box1364,Box1469,Box1425,Box1379,Fillet423,Fillet412,Box1477,Cylinder290,Box1367,Box1369,Fillet420,Box1374,Cylinder293,Box1366]
  Origin = -> Origin148
  Placement = pos=(0,-2.5,0) rot=(0,0,1;0rad)
  Tip = -> Box1366
FEATURE [PartDesign::Body] Body146  label="pin146"
  Group = -> [Box1381,Box1365,Box1473,Box1452,Box1376,Fillet421,Fillet434,Box1470,Cylinder296,Box1467,Box1466,Fillet426,Box1476,Cylinder289,Box1479]
  Origin = -> Origin160
  Placement = pos=(0,-1.5,0) rot=(0,0,1;0rad)
  Tip = -> Box1479
FEATURE [PartDesign::Fillet] Fillet439
  Base = -> Box1422 [Edge2]
  BaseFeature = -> Box1422
  Placement = pos=(-21.5005,18.625,0.235) rot=(0,-1,0;0.174533rad)
  Radius = 0.05
  SupportTransform = false
FEATURE [PartDesign::Fillet] Fillet438
  Base = -> Fillet439 [Edge33]
  BaseFeature = -> Fillet439
  Placement = pos=(-21.5005,18.625,0.235) rot=(0,-1,0;0.174533rad)
  Radius = 0.5
  SupportTransform = false
FEATURE [PartDesign::AdditiveBox] Box1437
  AttacherType = Attacher::AttachEngine3D
  AttachmentOffset = pos=(-21.1,18.635,0.305) rot=(0,1,0;0.785398rad)
  BaseFeature = -> Fillet438
  Height = 0.375
  Length = 0.2
  MapMode = 5
  Placement = pos=(-21.1,18.635,0.305) rot=(0,1,0;0.785398rad)
  Support = -> [XY_Plane159]
  Width = 0.23
FEATURE [PartDesign::SubtractiveCylinder] Cylinder288
  Angle = 360
  AttacherType = Attacher::AttachEngine3D
  AttachmentOffset = pos=(-21.055,18.935,0.52) rot=(1,0,0;1.5708rad)
  BaseFeature = -> Box1437
  Height = 0.375
  MapMode = 5
  Placement = pos=(-21.055,18.935,0.52) rot=(1,0,0;1.5708rad)
  Radius = 0.205
  Support = -> [XY_Plane159]
FEATURE [PartDesign::SubtractiveBox] Box1430
  AttacherType = Attacher::AttachEngine3D
  AttachmentOffset = pos=(-20.95,18.635,0.53) rot=(0,0,1;0rad)
  BaseFeature = -> Cylinder288
  Height = 0.5
  Length = 0.1
  MapMode = 5
  Placement = pos=(-20.95,18.635,0.53) rot=(0,0,1;0rad)
  Support = -> [XY_Plane159]
  Width = 0.23
FEATURE [PartDesign::SubtractiveBox] Box1419
  AttacherType = Attacher::AttachEngine3D
  AttachmentOffset = pos=(-21.15,18.635,0.297) rot=(0,-1,0;0.174533rad)
  BaseFeature = -> Box1430
  Height = 0.115
  Length = 0.115
  MapMode = 5
  Placement = pos=(-21.15,18.635,0.297) rot=(0,-1,0;0.174533rad)
  Support = -> [XY_Plane159]
  Width = 0.23
FEATURE [PartDesign::Fillet] Fillet429
  Base = -> Box1419 [Edge28]
  BaseFeature = -> Box1419
  Placement = pos=(-21.15,18.635,0.297) rot=(0,-1,0;0.174533rad)
  Radius = 0.375
  SupportTransform = false
FEATURE [PartDesign::AdditiveBox] Box1426
  AttacherType = Attacher::AttachEngine3D
  AttachmentOffset = pos=(-20.7,18.635,1.55) rot=(0,1,0;0.785398rad)
  BaseFeature = -> Fillet429
  Height = 0.375
  Length = 0.23
  MapMode = 5
  Placement = pos=(-20.7,18.635,1.55) rot=(0,1,0;0.785398rad)
  Support = -> [XY_Plane159]
  Width = 0.23
FEATURE [PartDesign::SubtractiveCylinder] Cylinder287
  Angle = 360
  AttacherType = Attacher::AttachEngine3D
  AttachmentOffset = pos=(-20.271,18.635,1.4056) rot=(-1,0,0;1.5708rad)
  BaseFeature = -> Box1426
  Height = 0.23
  MapMode = 5
  Placement = pos=(-20.271,18.635,1.4056) rot=(-1,0,0;1.5708rad)
  Radius = 0.23
  Support = -> [XY_Plane159]
FEATURE [PartDesign::AdditiveBox] Box1403
  AttacherType = Attacher::AttachEngine3D
  AttachmentOffset = pos=(-20.1,18.635,1.635) rot=(0,0,1;0rad)
  BaseFeature = -> Cylinder287
  Height = 0.265
  Length = 0.23
  MapMode = 5
  Placement = pos=(-20.1,18.635,1.635) rot=(0,0,1;0rad)
  Support = -> [XY_Plane159]
  Width = 0.23
FEATURE [PartDesign::Body] Body147  label="pin147"
  Group = -> [Box1413,Box1427,Box1407,Box1428,Box1422,Fillet439,Fillet438,Box1437,Cylinder288,Box1430,Box1419,Fillet429,Box1426,Cylinder287,Box1403]
  Origin = -> Origin166
  Placement = pos=(0,-4,0) rot=(0,0,1;0rad)
  Tip = -> Box1403
FEATURE [PartDesign::Fillet] Fillet440
  Base = -> Fillet422 [Edge33]
  BaseFeature = -> Fillet422
  Placement = pos=(-21.5005,18.625,0.235) rot=(0,-1,0;0.174533rad)
  Radius = 0.5
  SupportTransform = false
FEATURE [PartDesign::AdditiveBox] Box1408
  AttacherType = Attacher::AttachEngine3D
  AttachmentOffset = pos=(-21.1,18.635,0.305) rot=(0,1,0;0.785398rad)
  BaseFeature = -> Fillet440
  Height = 0.375
  Length = 0.2
  MapMode = 5
  Placement = pos=(-21.1,18.635,0.305) rot=(0,1,0;0.785398rad)
  Support = -> [XY_Plane153]
  Width = 0.23
FEATURE [PartDesign::SubtractiveCylinder] Cylinder281
  Angle = 360
  AttacherType = Attacher::AttachEngine3D
  AttachmentOffset = pos=(-21.055,18.935,0.52) rot=(1,0,0;1.5708rad)
  BaseFeature = -> Box1408
  Height = 0.375
  MapMode = 5
  Placement = pos=(-21.055,18.935,0.52) rot=(1,0,0;1.5708rad)
  Radius = 0.205
  Support = -> [XY_Plane153]
FEATURE [PartDesign::SubtractiveBox] Box1401
  AttacherType = Attacher::AttachEngine3D
  AttachmentOffset = pos=(-20.95,18.635,0.53) rot=(0,0,1;0rad)
  BaseFeature = -> Cylinder281
  Height = 0.5
  Length = 0.1
  MapMode = 5
  Placement = pos=(-20.95,18.635,0.53) rot=(0,0,1;0rad)
  Support = -> [XY_Plane153]
  Width = 0.23
FEATURE [PartDesign::SubtractiveBox] Box1398
  AttacherType = Attacher::AttachEngine3D
  AttachmentOffset = pos=(-21.15,18.635,0.297) rot=(0,-1,0;0.174533rad)
  BaseFeature = -> Box1401
  Height = 0.115
  Length = 0.115
  MapMode = 5
  Placement = pos=(-21.15,18.635,0.297) rot=(0,-1,0;0.174533rad)
  Support = -> [XY_Plane153]
  Width = 0.23
FEATURE [PartDesign::Fillet] Fillet436
  Base = -> Box1398 [Edge28]
  BaseFeature = -> Box1398
  Placement = pos=(-21.15,18.635,0.297) rot=(0,-1,0;0.174533rad)
  Radius = 0.375
  SupportTransform = false
FEATURE [PartDesign::AdditiveBox] Box1411
  AttacherType = Attacher::AttachEngine3D
  AttachmentOffset = pos=(-20.7,18.635,1.55) rot=(0,1,0;0.785398rad)
  BaseFeature = -> Fillet436
  Height = 0.375
  Length = 0.23
  MapMode = 5
  Placement = pos=(-20.7,18.635,1.55) rot=(0,1,0;0.785398rad)
  Support = -> [XY_Plane153]
  Width = 0.23
FEATURE [PartDesign::SubtractiveCylinder] Cylinder286
  Angle = 360
  AttacherType = Attacher::AttachEngine3D
  AttachmentOffset = pos=(-20.271,18.635,1.4056) rot=(-1,0,0;1.5708rad)
  BaseFeature = -> Box1411
  Height = 0.23
  MapMode = 5
  Placement = pos=(-20.271,18.635,1.4056) rot=(-1,0,0;1.5708rad)
  Radius = 0.23
  Support = -> [XY_Plane153]
FEATURE [PartDesign::AdditiveBox] Box1412
  AttacherType = Attacher::AttachEngine3D
  AttachmentOffset = pos=(-20.1,18.635,1.635) rot=(0,0,1;0rad)
  BaseFeature = -> Cylinder286
  Height = 0.265
  Length = 0.23
  MapMode = 5
  Placement = pos=(-20.1,18.635,1.635) rot=(0,0,1;0rad)
  Support = -> [XY_Plane153]
  Width = 0.23
FEATURE [PartDesign::Body] Body148  label="pin148"
  Group = -> [Box1404,Box1418,Box1358,Box1377,Box1373,Fillet422,Fillet440,Box1408,Cylinder281,Box1401,Box1398,Fillet436,Box1411,Cylinder286,Box1412]
  Origin = -> Origin157
  Placement = pos=(0,-5.5,0) rot=(0,0,1;0rad)
  Tip = -> Box1412
FEATURE [PartDesign::Fillet] Fillet441
  Base = -> Fillet427 [Edge33]
  BaseFeature = -> Fillet427
  Placement = pos=(-21.5005,18.625,0.235) rot=(0,-1,0;0.174533rad)
  Radius = 0.5
  SupportTransform = false
FEATURE [PartDesign::AdditiveBox] Box1392
  AttacherType = Attacher::AttachEngine3D
  AttachmentOffset = pos=(-21.1,18.635,0.305) rot=(0,1,0;0.785398rad)
  BaseFeature = -> Fillet441
  Height = 0.375
  Length = 0.2
  MapMode = 5
  Placement = pos=(-21.1,18.635,0.305) rot=(0,1,0;0.785398rad)
  Support = -> [XY_Plane160]
  Width = 0.23
FEATURE [PartDesign::SubtractiveCylinder] Cylinder282
  Angle = 360
  AttacherType = Attacher::AttachEngine3D
  AttachmentOffset = pos=(-21.055,18.935,0.52) rot=(1,0,0;1.5708rad)
  BaseFeature = -> Box1392
  Height = 0.375
  MapMode = 5
  Placement = pos=(-21.055,18.935,0.52) rot=(1,0,0;1.5708rad)
  Radius = 0.205
  Support = -> [XY_Plane160]
FEATURE [PartDesign::SubtractiveBox] Box1386
  AttacherType = Attacher::AttachEngine3D
  AttachmentOffset = pos=(-20.95,18.635,0.53) rot=(0,0,1;0rad)
  BaseFeature = -> Cylinder282
  Height = 0.5
  Length = 0.1
  MapMode = 5
  Placement = pos=(-20.95,18.635,0.53) rot=(0,0,1;0rad)
  Support = -> [XY_Plane160]
  Width = 0.23
FEATURE [PartDesign::SubtractiveBox] Box1424
  AttacherType = Attacher::AttachEngine3D
  AttachmentOffset = pos=(-21.15,18.635,0.297) rot=(0,-1,0;0.174533rad)
  BaseFeature = -> Box1386
  Height = 0.115
  Length = 0.115
  MapMode = 5
  Placement = pos=(-21.15,18.635,0.297) rot=(0,-1,0;0.174533rad)
  Support = -> [XY_Plane160]
  Width = 0.23
FEATURE [PartDesign::Fillet] Fillet428
  Base = -> Box1424 [Edge28]
  BaseFeature = -> Box1424
  Placement = pos=(-21.15,18.635,0.297) rot=(0,-1,0;0.174533rad)
  Radius = 0.375
  SupportTransform = false
FEATURE [PartDesign::AdditiveBox] Box1416
  AttacherType = Attacher::AttachEngine3D
  AttachmentOffset = pos=(-20.7,18.635,1.55) rot=(0,1,0;0.785398rad)
  BaseFeature = -> Fillet428
  Height = 0.375
  Length = 0.23
  MapMode = 5
  Placement = pos=(-20.7,18.635,1.55) rot=(0,1,0;0.785398rad)
  Support = -> [XY_Plane160]
  Width = 0.23
FEATURE [PartDesign::SubtractiveCylinder] Cylinder284
  Angle = 360
  AttacherType = Attacher::AttachEngine3D
  AttachmentOffset = pos=(-20.271,18.635,1.4056) rot=(-1,0,0;1.5708rad)
  BaseFeature = -> Box1416
  Height = 0.23
  MapMode = 5
  Placement = pos=(-20.271,18.635,1.4056) rot=(-1,0,0;1.5708rad)
  Radius = 0.23
  Support = -> [XY_Plane160]
FEATURE [PartDesign::AdditiveBox] Box1445
  AttacherType = Attacher::AttachEngine3D
  AttachmentOffset = pos=(-20.1,18.635,1.635) rot=(0,0,1;0rad)
  BaseFeature = -> Cylinder284
  Height = 0.265
  Length = 0.23
  MapMode = 5
  Placement = pos=(-20.1,18.635,1.635) rot=(0,0,1;0rad)
  Support = -> [XY_Plane160]
  Width = 0.23
FEATURE [PartDesign::Body] Body139  label="pin139"
  Group = -> [Box1414,Box1434,Box1400,Box1460,Box1402,Fillet427,Fillet441,Box1392,Cylinder282,Box1386,Box1424,Fillet428,Box1416,Cylinder284,Box1445]
  Origin = -> Origin147
  Placement = pos=(0,-3,0) rot=(0,0,1;0rad)
  Tip = -> Box1445
FEATURE [PartDesign::Fillet] Fillet442
  Base = -> Box1405 [Edge2]
  BaseFeature = -> Box1405
  Placement = pos=(-21.5005,18.625,0.235) rot=(0,-1,0;0.174533rad)
  Radius = 0.05
  SupportTransform = false
FEATURE [PartDesign::Fillet] Fillet437
  Base = -> Fillet442 [Edge33]
  BaseFeature = -> Fillet442
  Placement = pos=(-21.5005,18.625,0.235) rot=(0,-1,0;0.174533rad)
  Radius = 0.5
  SupportTransform = false
FEATURE [PartDesign::AdditiveBox] Box1433
  AttacherType = Attacher::AttachEngine3D
  AttachmentOffset = pos=(-21.1,18.635,0.305) rot=(0,1,0;0.785398rad)
  BaseFeature = -> Fillet437
  Height = 0.375
  Length = 0.2
  MapMode = 5
  Placement = pos=(-21.1,18.635,0.305) rot=(0,1,0;0.785398rad)
  Support = -> [XY_Plane162]
  Width = 0.23
FEATURE [PartDesign::SubtractiveCylinder] Cylinder292
  Angle = 360
  AttacherType = Attacher::AttachEngine3D
  AttachmentOffset = pos=(-21.055,18.935,0.52) rot=(1,0,0;1.5708rad)
  BaseFeature = -> Box1433
  Height = 0.375
  MapMode = 5
  Placement = pos=(-21.055,18.935,0.52) rot=(1,0,0;1.5708rad)
  Radius = 0.205
  Support = -> [XY_Plane162]
FEATURE [PartDesign::SubtractiveBox] Box1447
  AttacherType = Attacher::AttachEngine3D
  AttachmentOffset = pos=(-20.95,18.635,0.53) rot=(0,0,1;0rad)
  BaseFeature = -> Cylinder292
  Height = 0.5
  Length = 0.1
  MapMode = 5
  Placement = pos=(-20.95,18.635,0.53) rot=(0,0,1;0rad)
  Support = -> [XY_Plane162]
  Width = 0.23
FEATURE [PartDesign::SubtractiveBox] Box1423
  AttacherType = Attacher::AttachEngine3D
  AttachmentOffset = pos=(-21.15,18.635,0.297) rot=(0,-1,0;0.174533rad)
  BaseFeature = -> Box1447
  Height = 0.115
  Length = 0.115
  MapMode = 5
  Placement = pos=(-21.15,18.635,0.297) rot=(0,-1,0;0.174533rad)
  Support = -> [XY_Plane162]
  Width = 0.23
FEATURE [PartDesign::Fillet] Fillet425
  Base = -> Box1423 [Edge28]
  BaseFeature = -> Box1423
  Placement = pos=(-21.15,18.635,0.297) rot=(0,-1,0;0.174533rad)
  Radius = 0.375
  SupportTransform = false
FEATURE [PartDesign::AdditiveBox] Box1444
  AttacherType = Attacher::AttachEngine3D
  AttachmentOffset = pos=(-20.7,18.635,1.55) rot=(0,1,0;0.785398rad)
  BaseFeature = -> Fillet425
  Height = 0.375
  Length = 0.23
  MapMode = 5
  Placement = pos=(-20.7,18.635,1.55) rot=(0,1,0;0.785398rad)
  Support = -> [XY_Plane162]
  Width = 0.23
FEATURE [PartDesign::SubtractiveCylinder] Cylinder291
  Angle = 360
  AttacherType = Attacher::AttachEngine3D
  AttachmentOffset = pos=(-20.271,18.635,1.4056) rot=(-1,0,0;1.5708rad)
  BaseFeature = -> Box1444
  Height = 0.23
  MapMode = 5
  Placement = pos=(-20.271,18.635,1.4056) rot=(-1,0,0;1.5708rad)
  Radius = 0.23
  Support = -> [XY_Plane162]
FEATURE [PartDesign::AdditiveBox] Box1415
  AttacherType = Attacher::AttachEngine3D
  AttachmentOffset = pos=(-20.1,18.635,1.635) rot=(0,0,1;0rad)
  BaseFeature = -> Cylinder291
  Height = 0.265
  Length = 0.23
  MapMode = 5
  Placement = pos=(-20.1,18.635,1.635) rot=(0,0,1;0rad)
  Support = -> [XY_Plane162]
  Width = 0.23
FEATURE [PartDesign::Body] Body141  label="pin141"
  Group = -> [Box1417,Box1436,Box1448,Box1421,Box1405,Fillet442,Fillet437,Box1433,Cylinder292,Box1447,Box1423,Fillet425,Box1444,Cylinder291,Box1415]
  Origin = -> Origin158
  Placement = pos=(0,-3.5,0) rot=(0,0,1;0rad)
  Tip = -> Box1415
FEATURE [PartDesign::Fillet] Fillet443
  Base = -> Box1442 [Edge2]
  BaseFeature = -> Box1442
  Placement = pos=(-21.5005,18.625,0.235) rot=(0,-1,0;0.174533rad)
  Radius = 0.05
  SupportTransform = false
FEATURE [PartDesign::Fillet] Fillet411
  Base = -> Fillet443 [Edge33]
  BaseFeature = -> Fillet443
  Placement = pos=(-21.5005,18.625,0.235) rot=(0,-1,0;0.174533rad)
  Radius = 0.5
  SupportTransform = false
FEATURE [PartDesign::AdditiveBox] Box1363
  AttacherType = Attacher::AttachEngine3D
  AttachmentOffset = pos=(-21.1,18.635,0.305) rot=(0,1,0;0.785398rad)
  BaseFeature = -> Fillet411
  Height = 0.375
  Length = 0.2
  MapMode = 5
  Placement = pos=(-21.1,18.635,0.305) rot=(0,1,0;0.785398rad)
  Support = -> [XY_Plane158]
  Width = 0.23
FEATURE [PartDesign::SubtractiveCylinder] Cylinder276
  Angle = 360
  AttacherType = Attacher::AttachEngine3D
  AttachmentOffset = pos=(-21.055,18.935,0.52) rot=(1,0,0;1.5708rad)
  BaseFeature = -> Box1363
  Height = 0.375
  MapMode = 5
  Placement = pos=(-21.055,18.935,0.52) rot=(1,0,0;1.5708rad)
  Radius = 0.205
  Support = -> [XY_Plane158]
FEATURE [PartDesign::SubtractiveBox] Box1368
  AttacherType = Attacher::AttachEngine3D
  AttachmentOffset = pos=(-20.95,18.635,0.53) rot=(0,0,1;0rad)
  BaseFeature = -> Cylinder276
  Height = 0.5
  Length = 0.1
  MapMode = 5
  Placement = pos=(-20.95,18.635,0.53) rot=(0,0,1;0rad)
  Support = -> [XY_Plane158]
  Width = 0.23
FEATURE [PartDesign::SubtractiveBox] Box1359
  AttacherType = Attacher::AttachEngine3D
  AttachmentOffset = pos=(-21.15,18.635,0.297) rot=(0,-1,0;0.174533rad)
  BaseFeature = -> Box1368
  Height = 0.115
  Length = 0.115
  MapMode = 5
  Placement = pos=(-21.15,18.635,0.297) rot=(0,-1,0;0.174533rad)
  Support = -> [XY_Plane158]
  Width = 0.23
FEATURE [PartDesign::Fillet] Fillet432
  Base = -> Box1359 [Edge28]
  BaseFeature = -> Box1359
  Placement = pos=(-21.15,18.635,0.297) rot=(0,-1,0;0.174533rad)
  Radius = 0.375
  SupportTransform = false
FEATURE [PartDesign::AdditiveBox] Box1387
  AttacherType = Attacher::AttachEngine3D
  AttachmentOffset = pos=(-20.7,18.635,1.55) rot=(0,1,0;0.785398rad)
  BaseFeature = -> Fillet432
  Height = 0.375
  Length = 0.23
  MapMode = 5
  Placement = pos=(-20.7,18.635,1.55) rot=(0,1,0;0.785398rad)
  Support = -> [XY_Plane158]
  Width = 0.23
FEATURE [PartDesign::SubtractiveCylinder] Cylinder280
  Angle = 360
  AttacherType = Attacher::AttachEngine3D
  AttachmentOffset = pos=(-20.271,18.635,1.4056) rot=(-1,0,0;1.5708rad)
  BaseFeature = -> Box1387
  Height = 0.23
  MapMode = 5
  Placement = pos=(-20.271,18.635,1.4056) rot=(-1,0,0;1.5708rad)
  Radius = 0.23
  Support = -> [XY_Plane158]
FEATURE [PartDesign::AdditiveBox] Box1383
  AttacherType = Attacher::AttachEngine3D
  AttachmentOffset = pos=(-20.1,18.635,1.635) rot=(0,0,1;0rad)
  BaseFeature = -> Cylinder280
  Height = 0.265
  Length = 0.23
  MapMode = 5
  Placement = pos=(-20.1,18.635,1.635) rot=(0,0,1;0rad)
  Support = -> [XY_Plane158]
  Width = 0.23
FEATURE [PartDesign::Body] Body144  label="pin144"
  Group = -> [Box1399,Box1406,Box1393,Box1394,Box1442,Fillet443,Fillet411,Box1363,Cylinder276,Box1368,Box1359,Fillet432,Box1387,Cylinder280,Box1383]
  Origin = -> Origin164
  Placement = pos=(0,-4.5,0) rot=(0,0,1;0rad)
  Tip = -> Box1383
FEATURE [PartDesign::SubtractiveCylinder] Cylinder299
  Angle = 360
  AttacherType = Attacher::AttachEngine3D
  AttachmentOffset = pos=(-21.055,18.935,0.52) rot=(1,0,0;1.5708rad)
  BaseFeature = -> Box1480
  Height = 0.375
  MapMode = 5
  Placement = pos=(-21.055,18.935,0.52) rot=(1,0,0;1.5708rad)
  Radius = 0.205
  Support = -> [XY_Plane154]
FEATURE [PartDesign::SubtractiveBox] Box1378
  AttacherType = Attacher::AttachEngine3D
  AttachmentOffset = pos=(-20.95,18.635,0.53) rot=(0,0,1;0rad)
  BaseFeature = -> Cylinder299
  Height = 0.5
  Length = 0.1
  MapMode = 5
  Placement = pos=(-20.95,18.635,0.53) rot=(0,0,1;0rad)
  Support = -> [XY_Plane154]
  Width = 0.23
FEATURE [PartDesign::SubtractiveBox] Box1429
  AttacherType = Attacher::AttachEngine3D
  AttachmentOffset = pos=(-21.15,18.635,0.297) rot=(0,-1,0;0.174533rad)
  BaseFeature = -> Box1378
  Height = 0.115
  Length = 0.115
  MapMode = 5
  Placement = pos=(-21.15,18.635,0.297) rot=(0,-1,0;0.174533rad)
  Support = -> [XY_Plane154]
  Width = 0.23
FEATURE [PartDesign::Fillet] Fillet418
  Base = -> Box1429 [Edge28]
  BaseFeature = -> Box1429
  Placement = pos=(-21.15,18.635,0.297) rot=(0,-1,0;0.174533rad)
  Radius = 0.375
  SupportTransform = false
FEATURE [PartDesign::AdditiveBox] Box1465
  AttacherType = Attacher::AttachEngine3D
  AttachmentOffset = pos=(-20.7,18.635,1.55) rot=(0,1,0;0.785398rad)
  BaseFeature = -> Fillet418
  Height = 0.375
  Length = 0.23
  MapMode = 5
  Placement = pos=(-20.7,18.635,1.55) rot=(0,1,0;0.785398rad)
  Support = -> [XY_Plane154]
  Width = 0.23
FEATURE [PartDesign::SubtractiveCylinder] Cylinder278
  Angle = 360
  AttacherType = Attacher::AttachEngine3D
  AttachmentOffset = pos=(-20.271,18.635,1.4056) rot=(-1,0,0;1.5708rad)
  BaseFeature = -> Box1465
  Height = 0.23
  MapMode = 5
  Placement = pos=(-20.271,18.635,1.4056) rot=(-1,0,0;1.5708rad)
  Radius = 0.23
  Support = -> [XY_Plane154]
FEATURE [PartDesign::AdditiveBox] Box1382
  AttacherType = Attacher::AttachEngine3D
  AttachmentOffset = pos=(-20.1,18.635,1.635) rot=(0,0,1;0rad)
  BaseFeature = -> Cylinder278
  Height = 0.265
  Length = 0.23
  MapMode = 5
  Placement = pos=(-20.1,18.635,1.635) rot=(0,0,1;0rad)
  Support = -> [XY_Plane154]
  Width = 0.23
FEATURE [PartDesign::Body] Body138  label="pin138"
  Group = -> [Box1420,Box1372,Box1475,Box1370,Box1371,Fillet424,Fillet417,Box1480,Cylinder299,Box1378,Box1429,Fillet418,Box1465,Cylinder278,Box1382]
  Origin = -> Origin156
  Placement = pos=(0,-2,0) rot=(0,0,1;0rad)
  Tip = -> Box1382
FEATURE [PartDesign::AdditiveBox] Box1494
  AttacherType = Attacher::AttachEngine3D
  AttachmentOffset = pos=(-21.3,18.635,0) rot=(0,0,1;0rad)
  Height = 1.9
  Length = 1.3
  MapMode = 5
  Placement = pos=(-21.3,18.635,0) rot=(0,0,1;0rad)
  Support = -> [XY_Plane163]
  Width = 0.23
FEATURE [PartDesign::AdditiveBox] Box1500
  AttacherType = Attacher::AttachEngine3D
  AttachmentOffset = pos=(-21.3,18.635,0) rot=(0,0,1;0rad)
  Height = 1.9
  Length = 1.3
  MapMode = 5
  Placement = pos=(-21.3,18.635,0) rot=(0,0,1;0rad)
  Support = -> [XY_Plane164]
  Width = 0.23
FEATURE [PartDesign::AdditiveBox] Box1501
  AttacherType = Attacher::AttachEngine3D
  AttachmentOffset = pos=(-21.3,18.635,0) rot=(0,0,1;0rad)
  Height = 1.9
  Length = 1.3
  MapMode = 5
  Placement = pos=(-21.3,18.635,0) rot=(0,0,1;0rad)
  Support = -> [XY_Plane165]
  Width = 0.23
FEATURE [PartDesign::SubtractiveBox] Box1503
  AttacherType = Attacher::AttachEngine3D
  AttachmentOffset = pos=(-21.35,18.635,0.35) rot=(0,0,1;0rad)
  BaseFeature = -> Box1500
  Height = 1.55
  Length = 0.5
  MapMode = 5
  Placement = pos=(-21.35,18.635,0.35) rot=(0,0,1;0rad)
  Support = -> [XY_Plane164]
  Width = 0.23
FEATURE [PartDesign::SubtractiveBox] Box1493
  AttacherType = Attacher::AttachEngine3D
  AttachmentOffset = pos=(-20.5,18.63,0) rot=(0,0,1;0rad)
  BaseFeature = -> Box1503
  Height = 1.635
  Length = 0.5
  MapMode = 5
  Placement = pos=(-20.5,18.63,0) rot=(0,0,1;0rad)
  Support = -> [XY_Plane164]
  Width = 0.25
FEATURE [PartDesign::SubtractiveBox] Box1497
  AttacherType = Attacher::AttachEngine3D
  AttachmentOffset = pos=(-21.19,18.635,-0.12) rot=(0,-1,0;0.15708rad)
  BaseFeature = -> Box1493
  Height = 0.12
  Length = 0.725
  MapMode = 5
  Placement = pos=(-21.19,18.635,-0.12) rot=(0,-1,0;0.15708rad)
  Support = -> [XY_Plane164]
  Width = 0.25
FEATURE [PartDesign::SubtractiveBox] Box1492
  AttacherType = Attacher::AttachEngine3D
  AttachmentOffset = pos=(-21.5005,18.625,0.235) rot=(0,-1,0;0.174533rad)
  BaseFeature = -> Box1497
  Height = 0.3
  Length = 0.6605
  MapMode = 5
  Placement = pos=(-21.5005,18.625,0.235) rot=(0,-1,0;0.174533rad)
  Support = -> [XY_Plane164]
  Width = 0.25
FEATURE [PartDesign::SubtractiveBox] Box1507
  AttacherType = Attacher::AttachEngine3D
  AttachmentOffset = pos=(-21.35,18.635,0.35) rot=(0,0,1;0rad)
  BaseFeature = -> Box1501
  Height = 1.55
  Length = 0.5
  MapMode = 5
  Placement = pos=(-21.35,18.635,0.35) rot=(0,0,1;0rad)
  Support = -> [XY_Plane165]
  Width = 0.23
FEATURE [PartDesign::SubtractiveBox] Box1498
  AttacherType = Attacher::AttachEngine3D
  AttachmentOffset = pos=(-20.5,18.63,0) rot=(0,0,1;0rad)
  BaseFeature = -> Box1507
  Height = 1.635
  Length = 0.5
  MapMode = 5
  Placement = pos=(-20.5,18.63,0) rot=(0,0,1;0rad)
  Support = -> [XY_Plane165]
  Width = 0.25
FEATURE [PartDesign::SubtractiveBox] Box1499
  AttacherType = Attacher::AttachEngine3D
  AttachmentOffset = pos=(-21.19,18.635,-0.12) rot=(0,-1,0;0.15708rad)
  BaseFeature = -> Box1498
  Height = 0.12
  Length = 0.725
  MapMode = 5
  Placement = pos=(-21.19,18.635,-0.12) rot=(0,-1,0;0.15708rad)
  Support = -> [XY_Plane165]
  Width = 0.25
FEATURE [PartDesign::AdditiveBox] Box1515
  AttacherType = Attacher::AttachEngine3D
  AttachmentOffset = pos=(-21.3,18.635,0) rot=(0,0,1;0rad)
  Height = 1.9
  Length = 1.3
  MapMode = 5
  Placement = pos=(-21.3,18.635,0) rot=(0,0,1;0rad)
  Support = -> [XY_Plane166]
  Width = 0.23
FEATURE [PartDesign::SubtractiveBox] Box1516
  AttacherType = Attacher::AttachEngine3D
  AttachmentOffset = pos=(-21.35,18.635,0.35) rot=(0,0,1;0rad)
  BaseFeature = -> Box1494
  Height = 1.55
  Length = 0.5
  MapMode = 5
  Placement = pos=(-21.35,18.635,0.35) rot=(0,0,1;0rad)
  Support = -> [XY_Plane163]
  Width = 0.23
FEATURE [PartDesign::SubtractiveBox] Box1483
  AttacherType = Attacher::AttachEngine3D
  AttachmentOffset = pos=(-20.5,18.63,0) rot=(0,0,1;0rad)
  BaseFeature = -> Box1516
  Height = 1.635
  Length = 0.5
  MapMode = 5
  Placement = pos=(-20.5,18.63,0) rot=(0,0,1;0rad)
  Support = -> [XY_Plane163]
  Width = 0.25
FEATURE [PartDesign::SubtractiveBox] Box1488
  AttacherType = Attacher::AttachEngine3D
  AttachmentOffset = pos=(-21.19,18.635,-0.12) rot=(0,-1,0;0.15708rad)
  BaseFeature = -> Box1483
  Height = 0.12
  Length = 0.725
  MapMode = 5
  Placement = pos=(-21.19,18.635,-0.12) rot=(0,-1,0;0.15708rad)
  Support = -> [XY_Plane163]
  Width = 0.25
FEATURE [PartDesign::SubtractiveBox] Box1486
  AttacherType = Attacher::AttachEngine3D
  AttachmentOffset = pos=(-21.5005,18.625,0.235) rot=(0,-1,0;0.174533rad)
  BaseFeature = -> Box1488
  Height = 0.3
  Length = 0.6605
  MapMode = 5
  Placement = pos=(-21.5005,18.625,0.235) rot=(0,-1,0;0.174533rad)
  Support = -> [XY_Plane163]
  Width = 0.25
FEATURE [PartDesign::SubtractiveBox] Box1517
  AttacherType = Attacher::AttachEngine3D
  AttachmentOffset = pos=(-21.5005,18.625,0.235) rot=(0,-1,0;0.174533rad)
  BaseFeature = -> Box1499
  Height = 0.3
  Length = 0.6605
  MapMode = 5
  Placement = pos=(-21.5005,18.625,0.235) rot=(0,-1,0;0.174533rad)
  Support = -> [XY_Plane165]
  Width = 0.25
FEATURE [PartDesign::SubtractiveBox] Box1518
  AttacherType = Attacher::AttachEngine3D
  AttachmentOffset = pos=(-21.35,18.635,0.35) rot=(0,0,1;0rad)
  BaseFeature = -> Box1515
  Height = 1.55
  Length = 0.5
  MapMode = 5
  Placement = pos=(-21.35,18.635,0.35) rot=(0,0,1;0rad)
  Support = -> [XY_Plane166]
  Width = 0.23
FEATURE [PartDesign::SubtractiveBox] Box1514
  AttacherType = Attacher::AttachEngine3D
  AttachmentOffset = pos=(-20.5,18.63,0) rot=(0,0,1;0rad)
  BaseFeature = -> Box1518
  Height = 1.635
  Length = 0.5
  MapMode = 5
  Placement = pos=(-20.5,18.63,0) rot=(0,0,1;0rad)
  Support = -> [XY_Plane166]
  Width = 0.25
FEATURE [PartDesign::SubtractiveBox] Box1519
  AttacherType = Attacher::AttachEngine3D
  AttachmentOffset = pos=(-21.19,18.635,-0.12) rot=(0,-1,0;0.15708rad)
  BaseFeature = -> Box1514
  Height = 0.12
  Length = 0.725
  MapMode = 5
  Placement = pos=(-21.19,18.635,-0.12) rot=(0,-1,0;0.15708rad)
  Support = -> [XY_Plane166]
  Width = 0.25
FEATURE [PartDesign::SubtractiveBox] Box1505
  AttacherType = Attacher::AttachEngine3D
  AttachmentOffset = pos=(-21.5005,18.625,0.235) rot=(0,-1,0;0.174533rad)
  BaseFeature = -> Box1519
  Height = 0.3
  Length = 0.6605
  MapMode = 5
  Placement = pos=(-21.5005,18.625,0.235) rot=(0,-1,0;0.174533rad)
  Support = -> [XY_Plane166]
  Width = 0.25
FEATURE [PartDesign::Fillet] Fillet447
  Base = -> Box1486 [Edge2]
  BaseFeature = -> Box1486
  Placement = pos=(-21.5005,18.625,0.235) rot=(0,-1,0;0.174533rad)
  Radius = 0.05
  SupportTransform = false
FEATURE [PartDesign::Fillet] Fillet451
  Base = -> Box1492 [Edge2]
  BaseFeature = -> Box1492
  Placement = pos=(-21.5005,18.625,0.235) rot=(0,-1,0;0.174533rad)
  Radius = 0.05
  SupportTransform = false
FEATURE [PartDesign::Fillet] Fillet446
  Base = -> Fillet451 [Edge33]
  BaseFeature = -> Fillet451
  Placement = pos=(-21.5005,18.625,0.235) rot=(0,-1,0;0.174533rad)
  Radius = 0.5
  SupportTransform = false
FEATURE [PartDesign::AdditiveBox] Box1482
  AttacherType = Attacher::AttachEngine3D
  AttachmentOffset = pos=(-21.1,18.635,0.305) rot=(0,1,0;0.785398rad)
  BaseFeature = -> Fillet446
  Height = 0.375
  Length = 0.2
  MapMode = 5
  Placement = pos=(-21.1,18.635,0.305) rot=(0,1,0;0.785398rad)
  Support = -> [XY_Plane164]
  Width = 0.23
FEATURE [PartDesign::SubtractiveCylinder] Cylinder302
  Angle = 360
  AttacherType = Attacher::AttachEngine3D
  AttachmentOffset = pos=(-21.055,18.935,0.52) rot=(1,0,0;1.5708rad)
  BaseFeature = -> Box1482
  Height = 0.375
  MapMode = 5
  Placement = pos=(-21.055,18.935,0.52) rot=(1,0,0;1.5708rad)
  Radius = 0.205
  Support = -> [XY_Plane164]
FEATURE [PartDesign::SubtractiveBox] Box1496
  AttacherType = Attacher::AttachEngine3D
  AttachmentOffset = pos=(-20.95,18.635,0.53) rot=(0,0,1;0rad)
  BaseFeature = -> Cylinder302
  Height = 0.5
  Length = 0.1
  MapMode = 5
  Placement = pos=(-20.95,18.635,0.53) rot=(0,0,1;0rad)
  Support = -> [XY_Plane164]
  Width = 0.23
FEATURE [PartDesign::SubtractiveBox] Box1487
  AttacherType = Attacher::AttachEngine3D
  AttachmentOffset = pos=(-21.15,18.635,0.297) rot=(0,-1,0;0.174533rad)
  BaseFeature = -> Box1496
  Height = 0.115
  Length = 0.115
  MapMode = 5
  Placement = pos=(-21.15,18.635,0.297) rot=(0,-1,0;0.174533rad)
  Support = -> [XY_Plane164]
  Width = 0.23
FEATURE [PartDesign::Fillet] Fillet450
  Base = -> Box1487 [Edge28]
  BaseFeature = -> Box1487
  Placement = pos=(-21.15,18.635,0.297) rot=(0,-1,0;0.174533rad)
  Radius = 0.375
  SupportTransform = false
FEATURE [PartDesign::AdditiveBox] Box1490
  AttacherType = Attacher::AttachEngine3D
  AttachmentOffset = pos=(-20.7,18.635,1.55) rot=(0,1,0;0.785398rad)
  BaseFeature = -> Fillet450
  Height = 0.375
  Length = 0.23
  MapMode = 5
  Placement = pos=(-20.7,18.635,1.55) rot=(0,1,0;0.785398rad)
  Support = -> [XY_Plane164]
  Width = 0.23
FEATURE [PartDesign::SubtractiveCylinder] Cylinder301
  Angle = 360
  AttacherType = Attacher::AttachEngine3D
  AttachmentOffset = pos=(-20.271,18.635,1.4056) rot=(-1,0,0;1.5708rad)
  BaseFeature = -> Box1490
  Height = 0.23
  MapMode = 5
  Placement = pos=(-20.271,18.635,1.4056) rot=(-1,0,0;1.5708rad)
  Radius = 0.23
  Support = -> [XY_Plane164]
FEATURE [PartDesign::AdditiveBox] Box1508
  AttacherType = Attacher::AttachEngine3D
  AttachmentOffset = pos=(-20.1,18.635,1.635) rot=(0,0,1;0rad)
  BaseFeature = -> Cylinder301
  Height = 0.265
  Length = 0.23
  MapMode = 5
  Placement = pos=(-20.1,18.635,1.635) rot=(0,0,1;0rad)
  Support = -> [XY_Plane164]
  Width = 0.23
FEATURE [PartDesign::Body] Body149  label="pin149"
  Group = -> [Box1500,Box1503,Box1493,Box1497,Box1492,Fillet451,Fillet446,Box1482,Cylinder302,Box1496,Box1487,Fillet450,Box1490,Cylinder301,Box1508]
  Origin = -> Origin149
  Placement = pos=(0,-6,0) rot=(0,0,1;0rad)
  Tip = -> Box1508
FEATURE [PartDesign::Fillet] Fillet453
  Base = -> Box1505 [Edge2]
  BaseFeature = -> Box1505
  Placement = pos=(-21.5005,18.625,0.235) rot=(0,-1,0;0.174533rad)
  Radius = 0.05
  SupportTransform = false
FEATURE [PartDesign::Fillet] Fillet444
  Base = -> Fillet453 [Edge33]
  BaseFeature = -> Fillet453
  Placement = pos=(-21.5005,18.625,0.235) rot=(0,-1,0;0.174533rad)
  Radius = 0.5
  SupportTransform = false
FEATURE [PartDesign::AdditiveBox] Box1513
  AttacherType = Attacher::AttachEngine3D
  AttachmentOffset = pos=(-21.1,18.635,0.305) rot=(0,1,0;0.785398rad)
  BaseFeature = -> Fillet444
  Height = 0.375
  Length = 0.2
  MapMode = 5
  Placement = pos=(-21.1,18.635,0.305) rot=(0,1,0;0.785398rad)
  Support = -> [XY_Plane166]
  Width = 0.23
FEATURE [PartDesign::SubtractiveCylinder] Cylinder307
  Angle = 360
  AttacherType = Attacher::AttachEngine3D
  AttachmentOffset = pos=(-21.055,18.935,0.52) rot=(1,0,0;1.5708rad)
  BaseFeature = -> Box1513
  Height = 0.375
  MapMode = 5
  Placement = pos=(-21.055,18.935,0.52) rot=(1,0,0;1.5708rad)
  Radius = 0.205
  Support = -> [XY_Plane166]
FEATURE [PartDesign::SubtractiveBox] Box1520
  AttacherType = Attacher::AttachEngine3D
  AttachmentOffset = pos=(-20.95,18.635,0.53) rot=(0,0,1;0rad)
  BaseFeature = -> Cylinder307
  Height = 0.5
  Length = 0.1
  MapMode = 5
  Placement = pos=(-20.95,18.635,0.53) rot=(0,0,1;0rad)
  Support = -> [XY_Plane166]
  Width = 0.23
FEATURE [PartDesign::SubtractiveBox] Box1512
  AttacherType = Attacher::AttachEngine3D
  AttachmentOffset = pos=(-21.15,18.635,0.297) rot=(0,-1,0;0.174533rad)
  BaseFeature = -> Box1520
  Height = 0.115
  Length = 0.115
  MapMode = 5
  Placement = pos=(-21.15,18.635,0.297) rot=(0,-1,0;0.174533rad)
  Support = -> [XY_Plane166]
  Width = 0.23
FEATURE [PartDesign::Fillet] Fillet448
  Base = -> Box1512 [Edge28]
  BaseFeature = -> Box1512
  Placement = pos=(-21.15,18.635,0.297) rot=(0,-1,0;0.174533rad)
  Radius = 0.375
  SupportTransform = false
FEATURE [PartDesign::AdditiveBox] Box1506
  AttacherType = Attacher::AttachEngine3D
  AttachmentOffset = pos=(-20.7,18.635,1.55) rot=(0,1,0;0.785398rad)
  BaseFeature = -> Fillet448
  Height = 0.375
  Length = 0.23
  MapMode = 5
  Placement = pos=(-20.7,18.635,1.55) rot=(0,1,0;0.785398rad)
  Support = -> [XY_Plane166]
  Width = 0.23
FEATURE [PartDesign::SubtractiveCylinder] Cylinder306
  Angle = 360
  AttacherType = Attacher::AttachEngine3D
  AttachmentOffset = pos=(-20.271,18.635,1.4056) rot=(-1,0,0;1.5708rad)
  BaseFeature = -> Box1506
  Height = 0.23
  MapMode = 5
  Placement = pos=(-20.271,18.635,1.4056) rot=(-1,0,0;1.5708rad)
  Radius = 0.23
  Support = -> [XY_Plane166]
FEATURE [PartDesign::AdditiveBox] Box1502
  AttacherType = Attacher::AttachEngine3D
  AttachmentOffset = pos=(-20.1,18.635,1.635) rot=(0,0,1;0rad)
  BaseFeature = -> Cylinder306
  Height = 0.265
  Length = 0.23
  MapMode = 5
  Placement = pos=(-20.1,18.635,1.635) rot=(0,0,1;0rad)
  Support = -> [XY_Plane166]
  Width = 0.23
FEATURE [PartDesign::Body] Body151  label="pin151"
  Group = -> [Box1515,Box1518,Box1514,Box1519,Box1505,Fillet453,Fillet444,Box1513,Cylinder307,Box1520,Box1512,Fillet448,Box1506,Cylinder306,Box1502]
  Origin = -> Origin150
  Placement = pos=(0,-7,0) rot=(0,0,1;0rad)
  Tip = -> Box1502
FEATURE [PartDesign::Fillet] Fillet454
  Base = -> Box1517 [Edge2]
  BaseFeature = -> Box1517
  Placement = pos=(-21.5005,18.625,0.235) rot=(0,-1,0;0.174533rad)
  Radius = 0.05
  SupportTransform = false
FEATURE [PartDesign::Fillet] Fillet445
  Base = -> Fillet454 [Edge33]
  BaseFeature = -> Fillet454
  Placement = pos=(-21.5005,18.625,0.235) rot=(0,-1,0;0.174533rad)
  Radius = 0.5
  SupportTransform = false
FEATURE [PartDesign::AdditiveBox] Box1481
  AttacherType = Attacher::AttachEngine3D
  AttachmentOffset = pos=(-21.1,18.635,0.305) rot=(0,1,0;0.785398rad)
  BaseFeature = -> Fillet445
  Height = 0.375
  Length = 0.2
  MapMode = 5
  Placement = pos=(-21.1,18.635,0.305) rot=(0,1,0;0.785398rad)
  Support = -> [XY_Plane165]
  Width = 0.23
FEATURE [PartDesign::SubtractiveCylinder] Cylinder300
  Angle = 360
  AttacherType = Attacher::AttachEngine3D
  AttachmentOffset = pos=(-21.055,18.935,0.52) rot=(1,0,0;1.5708rad)
  BaseFeature = -> Box1481
  Height = 0.375
  MapMode = 5
  Placement = pos=(-21.055,18.935,0.52) rot=(1,0,0;1.5708rad)
  Radius = 0.205
  Support = -> [XY_Plane165]
FEATURE [PartDesign::SubtractiveBox] Box1484
  AttacherType = Attacher::AttachEngine3D
  AttachmentOffset = pos=(-20.95,18.635,0.53) rot=(0,0,1;0rad)
  BaseFeature = -> Cylinder300
  Height = 0.5
  Length = 0.1
  MapMode = 5
  Placement = pos=(-20.95,18.635,0.53) rot=(0,0,1;0rad)
  Support = -> [XY_Plane165]
  Width = 0.23
FEATURE [PartDesign::SubtractiveBox] Box1485
  AttacherType = Attacher::AttachEngine3D
  AttachmentOffset = pos=(-21.15,18.635,0.297) rot=(0,-1,0;0.174533rad)
  BaseFeature = -> Box1484
  Height = 0.115
  Length = 0.115
  MapMode = 5
  Placement = pos=(-21.15,18.635,0.297) rot=(0,-1,0;0.174533rad)
  Support = -> [XY_Plane165]
  Width = 0.23
FEATURE [PartDesign::Fillet] Fillet449
  Base = -> Box1485 [Edge28]
  BaseFeature = -> Box1485
  Placement = pos=(-21.15,18.635,0.297) rot=(0,-1,0;0.174533rad)
  Radius = 0.375
  SupportTransform = false
FEATURE [PartDesign::AdditiveBox] Box1495
  AttacherType = Attacher::AttachEngine3D
  AttachmentOffset = pos=(-20.7,18.635,1.55) rot=(0,1,0;0.785398rad)
  BaseFeature = -> Fillet449
  Height = 0.375
  Length = 0.23
  MapMode = 5
  Placement = pos=(-20.7,18.635,1.55) rot=(0,1,0;0.785398rad)
  Support = -> [XY_Plane165]
  Width = 0.23
FEATURE [PartDesign::SubtractiveCylinder] Cylinder304
  Angle = 360
  AttacherType = Attacher::AttachEngine3D
  AttachmentOffset = pos=(-20.271,18.635,1.4056) rot=(-1,0,0;1.5708rad)
  BaseFeature = -> Box1495
  Height = 0.23
  MapMode = 5
  Placement = pos=(-20.271,18.635,1.4056) rot=(-1,0,0;1.5708rad)
  Radius = 0.23
  Support = -> [XY_Plane165]
FEATURE [PartDesign::AdditiveBox] Box1489
  AttacherType = Attacher::AttachEngine3D
  AttachmentOffset = pos=(-20.1,18.635,1.635) rot=(0,0,1;0rad)
  BaseFeature = -> Cylinder304
  Height = 0.265
  Length = 0.23
  MapMode = 5
  Placement = pos=(-20.1,18.635,1.635) rot=(0,0,1;0rad)
  Support = -> [XY_Plane165]
  Width = 0.23
FEATURE [PartDesign::Body] Body150  label="pin150"
  Group = -> [Box1501,Box1507,Box1498,Box1499,Box1517,Fillet454,Fillet445,Box1481,Cylinder300,Box1484,Box1485,Fillet449,Box1495,Cylinder304,Box1489]
  Origin = -> Origin161
  Placement = pos=(0,-6.5,0) rot=(0,0,1;0rad)
  Tip = -> Box1489
FEATURE [PartDesign::Fillet] Fillet455
  Base = -> Fillet447 [Edge33]
  BaseFeature = -> Fillet447
  Placement = pos=(-21.5005,18.625,0.235) rot=(0,-1,0;0.174533rad)
  Radius = 0.5
  SupportTransform = false
FEATURE [PartDesign::AdditiveBox] Box1510
  AttacherType = Attacher::AttachEngine3D
  AttachmentOffset = pos=(-21.1,18.635,0.305) rot=(0,1,0;0.785398rad)
  BaseFeature = -> Fillet455
  Height = 0.375
  Length = 0.2
  MapMode = 5
  Placement = pos=(-21.1,18.635,0.305) rot=(0,1,0;0.785398rad)
  Support = -> [XY_Plane163]
  Width = 0.23
FEATURE [PartDesign::SubtractiveCylinder] Cylinder305
  Angle = 360
  AttacherType = Attacher::AttachEngine3D
  AttachmentOffset = pos=(-21.055,18.935,0.52) rot=(1,0,0;1.5708rad)
  BaseFeature = -> Box1510
  Height = 0.375
  MapMode = 5
  Placement = pos=(-21.055,18.935,0.52) rot=(1,0,0;1.5708rad)
  Radius = 0.205
  Support = -> [XY_Plane163]
FEATURE [PartDesign::SubtractiveBox] Box1504
  AttacherType = Attacher::AttachEngine3D
  AttachmentOffset = pos=(-20.95,18.635,0.53) rot=(0,0,1;0rad)
  BaseFeature = -> Cylinder305
  Height = 0.5
  Length = 0.1
  MapMode = 5
  Placement = pos=(-20.95,18.635,0.53) rot=(0,0,1;0rad)
  Support = -> [XY_Plane163]
  Width = 0.23
FEATURE [PartDesign::SubtractiveBox] Box1491
  AttacherType = Attacher::AttachEngine3D
  AttachmentOffset = pos=(-21.15,18.635,0.297) rot=(0,-1,0;0.174533rad)
  BaseFeature = -> Box1504
  Height = 0.115
  Length = 0.115
  MapMode = 5
  Placement = pos=(-21.15,18.635,0.297) rot=(0,-1,0;0.174533rad)
  Support = -> [XY_Plane163]
  Width = 0.23
FEATURE [PartDesign::Fillet] Fillet452
  Base = -> Box1491 [Edge28]
  BaseFeature = -> Box1491
  Placement = pos=(-21.15,18.635,0.297) rot=(0,-1,0;0.174533rad)
  Radius = 0.375
  SupportTransform = false
FEATURE [PartDesign::AdditiveBox] Box1511
  AttacherType = Attacher::AttachEngine3D
  AttachmentOffset = pos=(-20.7,18.635,1.55) rot=(0,1,0;0.785398rad)
  BaseFeature = -> Fillet452
  Height = 0.375
  Length = 0.23
  MapMode = 5
  Placement = pos=(-20.7,18.635,1.55) rot=(0,1,0;0.785398rad)
  Support = -> [XY_Plane163]
  Width = 0.23
FEATURE [PartDesign::SubtractiveCylinder] Cylinder303
  Angle = 360
  AttacherType = Attacher::AttachEngine3D
  AttachmentOffset = pos=(-20.271,18.635,1.4056) rot=(-1,0,0;1.5708rad)
  BaseFeature = -> Box1511
  Height = 0.23
  MapMode = 5
  Placement = pos=(-20.271,18.635,1.4056) rot=(-1,0,0;1.5708rad)
  Radius = 0.23
  Support = -> [XY_Plane163]
FEATURE [PartDesign::AdditiveBox] Box1509
  AttacherType = Attacher::AttachEngine3D
  AttachmentOffset = pos=(-20.1,18.635,1.635) rot=(0,0,1;0rad)
  BaseFeature = -> Cylinder303
  Height = 0.265
  Length = 0.23
  MapMode = 5
  Placement = pos=(-20.1,18.635,1.635) rot=(0,0,1;0rad)
  Support = -> [XY_Plane163]
  Width = 0.23
FEATURE [PartDesign::Body] Body152  label="pin152"
  Group = -> [Box1494,Box1516,Box1483,Box1488,Box1486,Fillet447,Fillet455,Box1510,Cylinder305,Box1504,Box1491,Fillet452,Box1511,Cylinder303,Box1509]
  Origin = -> Origin159
  Placement = pos=(0,-7.5,0) rot=(0,0,1;0rad)
  Tip = -> Box1509
FEATURE [App::Part] Part012  label="Pin-set011"
  Group = -> [Body140,Body137,Body143,Body146,Body138,Body145,Body139,Body141,Body147,Body144,Body142,Body148,Body149,Body150,Body151,Body152]
  Origin = -> Origin154
  Placement = pos=(0,-30,0) rot=(0,0,1;0rad)
FEATURE [App::Part] Part009  label="Pin-collection002"
  Group = -> [Part010,Part008,Part007,Part013,Part011,Part012]
  Origin = -> Origin162
  Placement = pos=(0,0,0) rot=(0,0,1;1.5708rad)
FEATURE [PartDesign::AdditiveBox] Box1529
  AttacherType = Attacher::AttachEngine3D
  AttachmentOffset = pos=(-21.3,18.635,0) rot=(0,0,1;0rad)
  Height = 1.9
  Length = 1.3
  MapMode = 5
  Placement = pos=(-21.3,18.635,0) rot=(0,0,1;0rad)
  Support = -> [XY_Plane179]
  Width = 0.23
FEATURE [PartDesign::SubtractiveBox] Box1522
  AttacherType = Attacher::AttachEngine3D
  AttachmentOffset = pos=(-21.35,18.635,0.35) rot=(0,0,1;0rad)
  BaseFeature = -> Box1529
  Height = 1.55
  Length = 0.5
  MapMode = 5
  Placement = pos=(-21.35,18.635,0.35) rot=(0,0,1;0rad)
  Support = -> [XY_Plane179]
  Width = 0.23
FEATURE [PartDesign::AdditiveBox] Box1532
  AttacherType = Attacher::AttachEngine3D
  AttachmentOffset = pos=(-21.3,18.635,0) rot=(0,0,1;0rad)
  Height = 1.9
  Length = 1.3
  MapMode = 5
  Placement = pos=(-21.3,18.635,0) rot=(0,0,1;0rad)
  Support = -> [XY_Plane175]
  Width = 0.23
FEATURE [PartDesign::SubtractiveBox] Box1527
  AttacherType = Attacher::AttachEngine3D
  AttachmentOffset = pos=(-21.35,18.635,0.35) rot=(0,0,1;0rad)
  BaseFeature = -> Box1532
  Height = 1.55
  Length = 0.5
  MapMode = 5
  Placement = pos=(-21.35,18.635,0.35) rot=(0,0,1;0rad)
  Support = -> [XY_Plane175]
  Width = 0.23
FEATURE [PartDesign::AdditiveBox] Box1536
  AttacherType = Attacher::AttachEngine3D
  AttachmentOffset = pos=(-21.3,18.635,0) rot=(0,0,1;0rad)
  Height = 1.9
  Length = 1.3
  MapMode = 5
  Placement = pos=(-21.3,18.635,0) rot=(0,0,1;0rad)
  Support = -> [XY_Plane174]
  Width = 0.23
FEATURE [PartDesign::SubtractiveBox] Box1537
  AttacherType = Attacher::AttachEngine3D
  AttachmentOffset = pos=(-21.35,18.635,0.35) rot=(0,0,1;0rad)
  BaseFeature = -> Box1536
  Height = 1.55
  Length = 0.5
  MapMode = 5
  Placement = pos=(-21.35,18.635,0.35) rot=(0,0,1;0rad)
  Support = -> [XY_Plane174]
  Width = 0.23
FEATURE [PartDesign::AdditiveBox] Box1539
  AttacherType = Attacher::AttachEngine3D
  AttachmentOffset = pos=(-21.3,18.635,0) rot=(0,0,1;0rad)
  Height = 1.9
  Length = 1.3
  MapMode = 5
  Placement = pos=(-21.3,18.635,0) rot=(0,0,1;0rad)
  Support = -> [XY_Plane187]
  Width = 0.23
FEATURE [PartDesign::AdditiveBox] Box1540
  AttacherType = Attacher::AttachEngine3D
  AttachmentOffset = pos=(-21.3,18.635,0) rot=(0,0,1;0rad)
  Height = 1.9
  Length = 1.3
  MapMode = 5
  Placement = pos=(-21.3,18.635,0) rot=(0,0,1;0rad)
  Support = -> [XY_Plane190]
  Width = 0.23
FEATURE [PartDesign::SubtractiveBox] Box1544
  AttacherType = Attacher::AttachEngine3D
  AttachmentOffset = pos=(-21.35,18.635,0.35) rot=(0,0,1;0rad)
  BaseFeature = -> Box1539
  Height = 1.55
  Length = 0.5
  MapMode = 5
  Placement = pos=(-21.35,18.635,0.35) rot=(0,0,1;0rad)
  Support = -> [XY_Plane187]
  Width = 0.23
FEATURE [PartDesign::AdditiveBox] Box1545
  AttacherType = Attacher::AttachEngine3D
  AttachmentOffset = pos=(-21.3,18.635,0) rot=(0,0,1;0rad)
  Height = 1.9
  Length = 1.3
  MapMode = 5
  Placement = pos=(-21.3,18.635,0) rot=(0,0,1;0rad)
  Support = -> [XY_Plane192]
  Width = 0.23
FEATURE [PartDesign::SubtractiveBox] Box1548
  AttacherType = Attacher::AttachEngine3D
  AttachmentOffset = pos=(-21.35,18.635,0.35) rot=(0,0,1;0rad)
  BaseFeature = -> Box1545
  Height = 1.55
  Length = 0.5
  MapMode = 5
  Placement = pos=(-21.35,18.635,0.35) rot=(0,0,1;0rad)
  Support = -> [XY_Plane192]
  Width = 0.23
FEATURE [PartDesign::SubtractiveBox] Box1552
  AttacherType = Attacher::AttachEngine3D
  AttachmentOffset = pos=(-21.35,18.635,0.35) rot=(0,0,1;0rad)
  BaseFeature = -> Box1540
  Height = 1.55
  Length = 0.5
  MapMode = 5
  Placement = pos=(-21.35,18.635,0.35) rot=(0,0,1;0rad)
  Support = -> [XY_Plane190]
  Width = 0.23
FEATURE [PartDesign::AdditiveBox] Box1568
  AttacherType = Attacher::AttachEngine3D
  AttachmentOffset = pos=(-21.3,18.635,0) rot=(0,0,1;0rad)
  Height = 1.9
  Length = 1.3
  MapMode = 5
  Placement = pos=(-21.3,18.635,0) rot=(0,0,1;0rad)
  Support = -> [XY_Plane170]
  Width = 0.23
FEATURE [PartDesign::SubtractiveBox] Box1571
  AttacherType = Attacher::AttachEngine3D
  AttachmentOffset = pos=(-21.35,18.635,0.35) rot=(0,0,1;0rad)
  BaseFeature = -> Box1568
  Height = 1.55
  Length = 0.5
  MapMode = 5
  Placement = pos=(-21.35,18.635,0.35) rot=(0,0,1;0rad)
  Support = -> [XY_Plane170]
  Width = 0.23
FEATURE [PartDesign::SubtractiveBox] Box1564
  AttacherType = Attacher::AttachEngine3D
  AttachmentOffset = pos=(-20.5,18.63,0) rot=(0,0,1;0rad)
  BaseFeature = -> Box1571
  Height = 1.635
  Length = 0.5
  MapMode = 5
  Placement = pos=(-20.5,18.63,0) rot=(0,0,1;0rad)
  Support = -> [XY_Plane170]
  Width = 0.25
FEATURE [PartDesign::SubtractiveBox] Box1573
  AttacherType = Attacher::AttachEngine3D
  AttachmentOffset = pos=(-21.19,18.635,-0.12) rot=(0,-1,0;0.15708rad)
  BaseFeature = -> Box1564
  Height = 0.12
  Length = 0.725
  MapMode = 5
  Placement = pos=(-21.19,18.635,-0.12) rot=(0,-1,0;0.15708rad)
  Support = -> [XY_Plane170]
  Width = 0.25
FEATURE [PartDesign::SubtractiveBox] Box1574
  AttacherType = Attacher::AttachEngine3D
  AttachmentOffset = pos=(-21.5005,18.625,0.235) rot=(0,-1,0;0.174533rad)
  BaseFeature = -> Box1573
  Height = 0.3
  Length = 0.6605
  MapMode = 5
  Placement = pos=(-21.5005,18.625,0.235) rot=(0,-1,0;0.174533rad)
  Support = -> [XY_Plane170]
  Width = 0.25
FEATURE [PartDesign::AdditiveBox] Box1580
  AttacherType = Attacher::AttachEngine3D
  AttachmentOffset = pos=(-21.3,18.635,0) rot=(0,0,1;0rad)
  Height = 1.9
  Length = 1.3
  MapMode = 5
  Placement = pos=(-21.3,18.635,0) rot=(0,0,1;0rad)
  Support = -> [XY_Plane167]
  Width = 0.23
FEATURE [PartDesign::SubtractiveBox] Box1586
  AttacherType = Attacher::AttachEngine3D
  AttachmentOffset = pos=(-21.35,18.635,0.35) rot=(0,0,1;0rad)
  BaseFeature = -> Box1580
  Height = 1.55
  Length = 0.5
  MapMode = 5
  Placement = pos=(-21.35,18.635,0.35) rot=(0,0,1;0rad)
  Support = -> [XY_Plane167]
  Width = 0.23
FEATURE [PartDesign::SubtractiveBox] Box1562
  AttacherType = Attacher::AttachEngine3D
  AttachmentOffset = pos=(-20.5,18.63,0) rot=(0,0,1;0rad)
  BaseFeature = -> Box1586
  Height = 1.635
  Length = 0.5
  MapMode = 5
  Placement = pos=(-20.5,18.63,0) rot=(0,0,1;0rad)
  Support = -> [XY_Plane167]
  Width = 0.25
FEATURE [PartDesign::SubtractiveBox] Box1570
  AttacherType = Attacher::AttachEngine3D
  AttachmentOffset = pos=(-21.19,18.635,-0.12) rot=(0,-1,0;0.15708rad)
  BaseFeature = -> Box1562
  Height = 0.12
  Length = 0.725
  MapMode = 5
  Placement = pos=(-21.19,18.635,-0.12) rot=(0,-1,0;0.15708rad)
  Support = -> [XY_Plane167]
  Width = 0.25
FEATURE [PartDesign::SubtractiveBox] Box1579
  AttacherType = Attacher::AttachEngine3D
  AttachmentOffset = pos=(-21.5005,18.625,0.235) rot=(0,-1,0;0.174533rad)
  BaseFeature = -> Box1570
  Height = 0.3
  Length = 0.6605
  MapMode = 5
  Placement = pos=(-21.5005,18.625,0.235) rot=(0,-1,0;0.174533rad)
  Support = -> [XY_Plane167]
  Width = 0.25
FEATURE [PartDesign::AdditiveBox] Box1591
  AttacherType = Attacher::AttachEngine3D
  AttachmentOffset = pos=(-21.3,18.635,0) rot=(0,0,1;0rad)
  Height = 1.9
  Length = 1.3
  MapMode = 5
  Placement = pos=(-21.3,18.635,0) rot=(0,0,1;0rad)
  Support = -> [XY_Plane171]
  Width = 0.23
FEATURE [PartDesign::SubtractiveBox] Box1582
  AttacherType = Attacher::AttachEngine3D
  AttachmentOffset = pos=(-21.35,18.635,0.35) rot=(0,0,1;0rad)
  BaseFeature = -> Box1591
  Height = 1.55
  Length = 0.5
  MapMode = 5
  Placement = pos=(-21.35,18.635,0.35) rot=(0,0,1;0rad)
  Support = -> [XY_Plane171]
  Width = 0.23
FEATURE [PartDesign::SubtractiveBox] Box1561
  AttacherType = Attacher::AttachEngine3D
  AttachmentOffset = pos=(-20.5,18.63,0) rot=(0,0,1;0rad)
  BaseFeature = -> Box1582
  Height = 1.635
  Length = 0.5
  MapMode = 5
  Placement = pos=(-20.5,18.63,0) rot=(0,0,1;0rad)
  Support = -> [XY_Plane171]
  Width = 0.25
FEATURE [PartDesign::SubtractiveBox] Box1563
  AttacherType = Attacher::AttachEngine3D
  AttachmentOffset = pos=(-21.19,18.635,-0.12) rot=(0,-1,0;0.15708rad)
  BaseFeature = -> Box1561
  Height = 0.12
  Length = 0.725
  MapMode = 5
  Placement = pos=(-21.19,18.635,-0.12) rot=(0,-1,0;0.15708rad)
  Support = -> [XY_Plane171]
  Width = 0.25
FEATURE [PartDesign::SubtractiveBox] Box1581
  AttacherType = Attacher::AttachEngine3D
  AttachmentOffset = pos=(-21.5005,18.625,0.235) rot=(0,-1,0;0.174533rad)
  BaseFeature = -> Box1563
  Height = 0.3
  Length = 0.6605
  MapMode = 5
  Placement = pos=(-21.5005,18.625,0.235) rot=(0,-1,0;0.174533rad)
  Support = -> [XY_Plane171]
  Width = 0.25
FEATURE [PartDesign::AdditiveBox] Box1597
  AttacherType = Attacher::AttachEngine3D
  AttachmentOffset = pos=(-21.3,18.635,0) rot=(0,0,1;0rad)
  Height = 1.9
  Length = 1.3
  MapMode = 5
  Placement = pos=(-21.3,18.635,0) rot=(0,0,1;0rad)
  Support = -> [XY_Plane176]
  Width = 0.23
FEATURE [PartDesign::SubtractiveBox] Box1600
  AttacherType = Attacher::AttachEngine3D
  AttachmentOffset = pos=(-21.35,18.635,0.35) rot=(0,0,1;0rad)
  BaseFeature = -> Box1597
  Height = 1.55
  Length = 0.5
  MapMode = 5
  Placement = pos=(-21.35,18.635,0.35) rot=(0,0,1;0rad)
  Support = -> [XY_Plane176]
  Width = 0.23
FEATURE [PartDesign::SubtractiveBox] Box1585
  AttacherType = Attacher::AttachEngine3D
  AttachmentOffset = pos=(-20.5,18.63,0) rot=(0,0,1;0rad)
  BaseFeature = -> Box1600
  Height = 1.635
  Length = 0.5
  MapMode = 5
  Placement = pos=(-20.5,18.63,0) rot=(0,0,1;0rad)
  Support = -> [XY_Plane176]
  Width = 0.25
FEATURE [PartDesign::SubtractiveBox] Box1610
  AttacherType = Attacher::AttachEngine3D
  AttachmentOffset = pos=(-21.19,18.635,-0.12) rot=(0,-1,0;0.15708rad)
  BaseFeature = -> Box1585
  Height = 0.12
  Length = 0.725
  MapMode = 5
  Placement = pos=(-21.19,18.635,-0.12) rot=(0,-1,0;0.15708rad)
  Support = -> [XY_Plane176]
  Width = 0.25
FEATURE [PartDesign::SubtractiveBox] Box1605
  AttacherType = Attacher::AttachEngine3D
  AttachmentOffset = pos=(-21.5005,18.625,0.235) rot=(0,-1,0;0.174533rad)
  BaseFeature = -> Box1610
  Height = 0.3
  Length = 0.6605
  MapMode = 5
  Placement = pos=(-21.5005,18.625,0.235) rot=(0,-1,0;0.174533rad)
  Support = -> [XY_Plane176]
  Width = 0.25
FEATURE [PartDesign::SubtractiveBox] Box1613
  AttacherType = Attacher::AttachEngine3D
  AttachmentOffset = pos=(-20.5,18.63,0) rot=(0,0,1;0rad)
  BaseFeature = -> Box1527
  Height = 1.635
  Length = 0.5
  MapMode = 5
  Placement = pos=(-20.5,18.63,0) rot=(0,0,1;0rad)
  Support = -> [XY_Plane175]
  Width = 0.25
FEATURE [PartDesign::SubtractiveBox] Box1524
  AttacherType = Attacher::AttachEngine3D
  AttachmentOffset = pos=(-21.19,18.635,-0.12) rot=(0,-1,0;0.15708rad)
  BaseFeature = -> Box1613
  Height = 0.12
  Length = 0.725
  MapMode = 5
  Placement = pos=(-21.19,18.635,-0.12) rot=(0,-1,0;0.15708rad)
  Support = -> [XY_Plane175]
  Width = 0.25
FEATURE [PartDesign::SubtractiveBox] Box1523
  AttacherType = Attacher::AttachEngine3D
  AttachmentOffset = pos=(-21.5005,18.625,0.235) rot=(0,-1,0;0.174533rad)
  BaseFeature = -> Box1524
  Height = 0.3
  Length = 0.6605
  MapMode = 5
  Placement = pos=(-21.5005,18.625,0.235) rot=(0,-1,0;0.174533rad)
  Support = -> [XY_Plane175]
  Width = 0.25
FEATURE [PartDesign::AdditiveBox] Box1616
  AttacherType = Attacher::AttachEngine3D
  AttachmentOffset = pos=(-21.3,18.635,0) rot=(0,0,1;0rad)
  Height = 1.9
  Length = 1.3
  MapMode = 5
  Placement = pos=(-21.3,18.635,0) rot=(0,0,1;0rad)
  Support = -> [XY_Plane177]
  Width = 0.23
FEATURE [PartDesign::SubtractiveBox] Box1614
  AttacherType = Attacher::AttachEngine3D
  AttachmentOffset = pos=(-21.35,18.635,0.35) rot=(0,0,1;0rad)
  BaseFeature = -> Box1616
  Height = 1.55
  Length = 0.5
  MapMode = 5
  Placement = pos=(-21.35,18.635,0.35) rot=(0,0,1;0rad)
  Support = -> [XY_Plane177]
  Width = 0.23
FEATURE [PartDesign::SubtractiveBox] Box1592
  AttacherType = Attacher::AttachEngine3D
  AttachmentOffset = pos=(-20.5,18.63,0) rot=(0,0,1;0rad)
  BaseFeature = -> Box1614
  Height = 1.635
  Length = 0.5
  MapMode = 5
  Placement = pos=(-20.5,18.63,0) rot=(0,0,1;0rad)
  Support = -> [XY_Plane177]
  Width = 0.25
FEATURE [PartDesign::SubtractiveBox] Box1595
  AttacherType = Attacher::AttachEngine3D
  AttachmentOffset = pos=(-21.19,18.635,-0.12) rot=(0,-1,0;0.15708rad)
  BaseFeature = -> Box1592
  Height = 0.12
  Length = 0.725
  MapMode = 5
  Placement = pos=(-21.19,18.635,-0.12) rot=(0,-1,0;0.15708rad)
  Support = -> [XY_Plane177]
  Width = 0.25
FEATURE [PartDesign::SubtractiveBox] Box1619
  AttacherType = Attacher::AttachEngine3D
  AttachmentOffset = pos=(-20.5,18.63,0) rot=(0,0,1;0rad)
  BaseFeature = -> Box1537
  Height = 1.635
  Length = 0.5
  MapMode = 5
  Placement = pos=(-20.5,18.63,0) rot=(0,0,1;0rad)
  Support = -> [XY_Plane174]
  Width = 0.25
FEATURE [PartDesign::AdditiveBox] Box1620
  AttacherType = Attacher::AttachEngine3D
  AttachmentOffset = pos=(-21.3,18.635,0) rot=(0,0,1;0rad)
  Height = 1.9
  Length = 1.3
  MapMode = 5
  Placement = pos=(-21.3,18.635,0) rot=(0,0,1;0rad)
  Support = -> [XY_Plane172]
  Width = 0.23
FEATURE [PartDesign::SubtractiveBox] Box1615
  AttacherType = Attacher::AttachEngine3D
  AttachmentOffset = pos=(-21.35,18.635,0.35) rot=(0,0,1;0rad)
  BaseFeature = -> Box1620
  Height = 1.55
  Length = 0.5
  MapMode = 5
  Placement = pos=(-21.35,18.635,0.35) rot=(0,0,1;0rad)
  Support = -> [XY_Plane172]
  Width = 0.23
FEATURE [PartDesign::SubtractiveBox] Box1584
  AttacherType = Attacher::AttachEngine3D
  AttachmentOffset = pos=(-20.5,18.63,0) rot=(0,0,1;0rad)
  BaseFeature = -> Box1615
  Height = 1.635
  Length = 0.5
  MapMode = 5
  Placement = pos=(-20.5,18.63,0) rot=(0,0,1;0rad)
  Support = -> [XY_Plane172]
  Width = 0.25
FEATURE [PartDesign::SubtractiveBox] Box1599
  AttacherType = Attacher::AttachEngine3D
  AttachmentOffset = pos=(-21.19,18.635,-0.12) rot=(0,-1,0;0.15708rad)
  BaseFeature = -> Box1584
  Height = 0.12
  Length = 0.725
  MapMode = 5
  Placement = pos=(-21.19,18.635,-0.12) rot=(0,-1,0;0.15708rad)
  Support = -> [XY_Plane172]
  Width = 0.25
FEATURE [PartDesign::SubtractiveBox] Box1603
  AttacherType = Attacher::AttachEngine3D
  AttachmentOffset = pos=(-21.5005,18.625,0.235) rot=(0,-1,0;0.174533rad)
  BaseFeature = -> Box1599
  Height = 0.3
  Length = 0.6605
  MapMode = 5
  Placement = pos=(-21.5005,18.625,0.235) rot=(0,-1,0;0.174533rad)
  Support = -> [XY_Plane172]
  Width = 0.25
FEATURE [PartDesign::SubtractiveBox] Box1621
  AttacherType = Attacher::AttachEngine3D
  AttachmentOffset = pos=(-21.5005,18.625,0.235) rot=(0,-1,0;0.174533rad)
  BaseFeature = -> Box1595
  Height = 0.3
  Length = 0.6605
  MapMode = 5
  Placement = pos=(-21.5005,18.625,0.235) rot=(0,-1,0;0.174533rad)
  Support = -> [XY_Plane177]
  Width = 0.25
FEATURE [PartDesign::SubtractiveBox] Box1626
  AttacherType = Attacher::AttachEngine3D
  AttachmentOffset = pos=(-20.5,18.63,0) rot=(0,0,1;0rad)
  BaseFeature = -> Box1522
  Height = 1.635
  Length = 0.5
  MapMode = 5
  Placement = pos=(-20.5,18.63,0) rot=(0,0,1;0rad)
  Support = -> [XY_Plane179]
  Width = 0.25
FEATURE [PartDesign::SubtractiveBox] Box1525
  AttacherType = Attacher::AttachEngine3D
  AttachmentOffset = pos=(-21.19,18.635,-0.12) rot=(0,-1,0;0.15708rad)
  BaseFeature = -> Box1626
  Height = 0.12
  Length = 0.725
  MapMode = 5
  Placement = pos=(-21.19,18.635,-0.12) rot=(0,-1,0;0.15708rad)
  Support = -> [XY_Plane179]
  Width = 0.25
FEATURE [PartDesign::SubtractiveBox] Box1528
  AttacherType = Attacher::AttachEngine3D
  AttachmentOffset = pos=(-21.5005,18.625,0.235) rot=(0,-1,0;0.174533rad)
  BaseFeature = -> Box1525
  Height = 0.3
  Length = 0.6605
  MapMode = 5
  Placement = pos=(-21.5005,18.625,0.235) rot=(0,-1,0;0.174533rad)
  Support = -> [XY_Plane179]
  Width = 0.25
FEATURE [PartDesign::SubtractiveBox] Box1627
  AttacherType = Attacher::AttachEngine3D
  AttachmentOffset = pos=(-21.19,18.635,-0.12) rot=(0,-1,0;0.15708rad)
  BaseFeature = -> Box1619
  Height = 0.12
  Length = 0.725
  MapMode = 5
  Placement = pos=(-21.19,18.635,-0.12) rot=(0,-1,0;0.15708rad)
  Support = -> [XY_Plane174]
  Width = 0.25
FEATURE [PartDesign::SubtractiveBox] Box1533
  AttacherType = Attacher::AttachEngine3D
  AttachmentOffset = pos=(-21.5005,18.625,0.235) rot=(0,-1,0;0.174533rad)
  BaseFeature = -> Box1627
  Height = 0.3
  Length = 0.6605
  MapMode = 5
  Placement = pos=(-21.5005,18.625,0.235) rot=(0,-1,0;0.174533rad)
  Support = -> [XY_Plane174]
  Width = 0.25
FEATURE [PartDesign::Fillet] Fillet465
  Base = -> Box1574 [Edge2]
  BaseFeature = -> Box1574
  Placement = pos=(-21.5005,18.625,0.235) rot=(0,-1,0;0.174533rad)
  Radius = 0.05
  SupportTransform = false
FEATURE [PartDesign::Fillet] Fillet467
  Base = -> Fillet465 [Edge33]
  BaseFeature = -> Fillet465
  Placement = pos=(-21.5005,18.625,0.235) rot=(0,-1,0;0.174533rad)
  Radius = 0.5
  SupportTransform = false
FEATURE [PartDesign::AdditiveBox] Box1555
  AttacherType = Attacher::AttachEngine3D
  AttachmentOffset = pos=(-21.1,18.635,0.305) rot=(0,1,0;0.785398rad)
  BaseFeature = -> Fillet467
  Height = 0.375
  Length = 0.2
  MapMode = 5
  Placement = pos=(-21.1,18.635,0.305) rot=(0,1,0;0.785398rad)
  Support = -> [XY_Plane170]
  Width = 0.23
FEATURE [PartDesign::SubtractiveCylinder] Cylinder315
  Angle = 360
  AttacherType = Attacher::AttachEngine3D
  AttachmentOffset = pos=(-21.055,18.935,0.52) rot=(1,0,0;1.5708rad)
  BaseFeature = -> Box1555
  Height = 0.375
  MapMode = 5
  Placement = pos=(-21.055,18.935,0.52) rot=(1,0,0;1.5708rad)
  Radius = 0.205
  Support = -> [XY_Plane170]
FEATURE [PartDesign::SubtractiveBox] Box1576
  AttacherType = Attacher::AttachEngine3D
  AttachmentOffset = pos=(-20.95,18.635,0.53) rot=(0,0,1;0rad)
  BaseFeature = -> Cylinder315
  Height = 0.5
  Length = 0.1
  MapMode = 5
  Placement = pos=(-20.95,18.635,0.53) rot=(0,0,1;0rad)
  Support = -> [XY_Plane170]
  Width = 0.23
FEATURE [PartDesign::SubtractiveBox] Box1566
  AttacherType = Attacher::AttachEngine3D
  AttachmentOffset = pos=(-21.15,18.635,0.297) rot=(0,-1,0;0.174533rad)
  BaseFeature = -> Box1576
  Height = 0.115
  Length = 0.115
  MapMode = 5
  Placement = pos=(-21.15,18.635,0.297) rot=(0,-1,0;0.174533rad)
  Support = -> [XY_Plane170]
  Width = 0.23
FEATURE [PartDesign::Fillet] Fillet466
  Base = -> Box1566 [Edge28]
  BaseFeature = -> Box1566
  Placement = pos=(-21.15,18.635,0.297) rot=(0,-1,0;0.174533rad)
  Radius = 0.375
  SupportTransform = false
FEATURE [PartDesign::AdditiveBox] Box1565
  AttacherType = Attacher::AttachEngine3D
  AttachmentOffset = pos=(-20.7,18.635,1.55) rot=(0,1,0;0.785398rad)
  BaseFeature = -> Fillet466
  Height = 0.375
  Length = 0.23
  MapMode = 5
  Placement = pos=(-20.7,18.635,1.55) rot=(0,1,0;0.785398rad)
  Support = -> [XY_Plane170]
  Width = 0.23
FEATURE [PartDesign::SubtractiveCylinder] Cylinder317
  Angle = 360
  AttacherType = Attacher::AttachEngine3D
  AttachmentOffset = pos=(-20.271,18.635,1.4056) rot=(-1,0,0;1.5708rad)
  BaseFeature = -> Box1565
  Height = 0.23
  MapMode = 5
  Placement = pos=(-20.271,18.635,1.4056) rot=(-1,0,0;1.5708rad)
  Radius = 0.23
  Support = -> [XY_Plane170]
FEATURE [PartDesign::AdditiveBox] Box1575
  AttacherType = Attacher::AttachEngine3D
  AttachmentOffset = pos=(-20.1,18.635,1.635) rot=(0,0,1;0rad)
  BaseFeature = -> Cylinder317
  Height = 0.265
  Length = 0.23
  MapMode = 5
  Placement = pos=(-20.1,18.635,1.635) rot=(0,0,1;0rad)
  Support = -> [XY_Plane170]
  Width = 0.23
FEATURE [PartDesign::Body] Body157  label="pin157"
  Group = -> [Box1568,Box1571,Box1564,Box1573,Box1574,Fillet465,Fillet467,Box1555,Cylinder315,Box1576,Box1566,Fillet466,Box1565,Cylinder317,Box1575]
  Origin = -> Origin174
  Placement = pos=(0,-2,0) rot=(0,0,1;0rad)
  Tip = -> Box1575
FEATURE [PartDesign::Fillet] Fillet468
  Base = -> Box1579 [Edge2]
  BaseFeature = -> Box1579
  Placement = pos=(-21.5005,18.625,0.235) rot=(0,-1,0;0.174533rad)
  Radius = 0.05
  SupportTransform = false
FEATURE [PartDesign::Fillet] Fillet469
  Base = -> Fillet468 [Edge33]
  BaseFeature = -> Fillet468
  Placement = pos=(-21.5005,18.625,0.235) rot=(0,-1,0;0.174533rad)
  Radius = 0.5
  SupportTransform = false
FEATURE [PartDesign::AdditiveBox] Box1567
  AttacherType = Attacher::AttachEngine3D
  AttachmentOffset = pos=(-21.1,18.635,0.305) rot=(0,1,0;0.785398rad)
  BaseFeature = -> Fillet469
  Height = 0.375
  Length = 0.2
  MapMode = 5
  Placement = pos=(-21.1,18.635,0.305) rot=(0,1,0;0.785398rad)
  Support = -> [XY_Plane167]
  Width = 0.23
FEATURE [PartDesign::SubtractiveCylinder] Cylinder316
  Angle = 360
  AttacherType = Attacher::AttachEngine3D
  AttachmentOffset = pos=(-21.055,18.935,0.52) rot=(1,0,0;1.5708rad)
  BaseFeature = -> Box1567
  Height = 0.375
  MapMode = 5
  Placement = pos=(-21.055,18.935,0.52) rot=(1,0,0;1.5708rad)
  Radius = 0.205
  Support = -> [XY_Plane167]
FEATURE [PartDesign::SubtractiveBox] Box1572
  AttacherType = Attacher::AttachEngine3D
  AttachmentOffset = pos=(-20.95,18.635,0.53) rot=(0,0,1;0rad)
  BaseFeature = -> Cylinder316
  Height = 0.5
  Length = 0.1
  MapMode = 5
  Placement = pos=(-20.95,18.635,0.53) rot=(0,0,1;0rad)
  Support = -> [XY_Plane167]
  Width = 0.23
FEATURE [PartDesign::SubtractiveBox] Box1578
  AttacherType = Attacher::AttachEngine3D
  AttachmentOffset = pos=(-21.15,18.635,0.297) rot=(0,-1,0;0.174533rad)
  BaseFeature = -> Box1572
  Height = 0.115
  Length = 0.115
  MapMode = 5
  Placement = pos=(-21.15,18.635,0.297) rot=(0,-1,0;0.174533rad)
  Support = -> [XY_Plane167]
  Width = 0.23
FEATURE [PartDesign::Fillet] Fillet457
  Base = -> Box1578 [Edge28]
  BaseFeature = -> Box1578
  Placement = pos=(-21.15,18.635,0.297) rot=(0,-1,0;0.174533rad)
  Radius = 0.375
  SupportTransform = false
FEATURE [PartDesign::AdditiveBox] Box1577
  AttacherType = Attacher::AttachEngine3D
  AttachmentOffset = pos=(-20.7,18.635,1.55) rot=(0,1,0;0.785398rad)
  BaseFeature = -> Fillet457
  Height = 0.375
  Length = 0.23
  MapMode = 5
  Placement = pos=(-20.7,18.635,1.55) rot=(0,1,0;0.785398rad)
  Support = -> [XY_Plane167]
  Width = 0.23
FEATURE [PartDesign::SubtractiveCylinder] Cylinder318
  Angle = 360
  AttacherType = Attacher::AttachEngine3D
  AttachmentOffset = pos=(-20.271,18.635,1.4056) rot=(-1,0,0;1.5708rad)
  BaseFeature = -> Box1577
  Height = 0.23
  MapMode = 5
  Placement = pos=(-20.271,18.635,1.4056) rot=(-1,0,0;1.5708rad)
  Radius = 0.23
  Support = -> [XY_Plane167]
FEATURE [PartDesign::AdditiveBox] Box1569
  AttacherType = Attacher::AttachEngine3D
  AttachmentOffset = pos=(-20.1,18.635,1.635) rot=(0,0,1;0rad)
  BaseFeature = -> Cylinder318
  Height = 0.265
  Length = 0.23
  MapMode = 5
  Placement = pos=(-20.1,18.635,1.635) rot=(0,0,1;0rad)
  Support = -> [XY_Plane167]
  Width = 0.23
FEATURE [PartDesign::Body] Body158  label="pin158"
  Group = -> [Box1580,Box1586,Box1562,Box1570,Box1579,Fillet468,Fillet469,Box1567,Cylinder316,Box1572,Box1578,Fillet457,Box1577,Cylinder318,Box1569]
  Origin = -> Origin179
  Placement = pos=(0,-2.5,0) rot=(0,0,1;0rad)
  Tip = -> Box1569
FEATURE [PartDesign::AdditiveBox] Box1646
  AttacherType = Attacher::AttachEngine3D
  AttachmentOffset = pos=(-21.3,18.635,0) rot=(0,0,1;0rad)
  Height = 1.9
  Length = 1.3
  MapMode = 5
  Placement = pos=(-21.3,18.635,0) rot=(0,0,1;0rad)
  Support = -> [XY_Plane178]
  Width = 0.23
FEATURE [PartDesign::SubtractiveBox] Box1647
  AttacherType = Attacher::AttachEngine3D
  AttachmentOffset = pos=(-21.35,18.635,0.35) rot=(0,0,1;0rad)
  BaseFeature = -> Box1646
  Height = 1.55
  Length = 0.5
  MapMode = 5
  Placement = pos=(-21.35,18.635,0.35) rot=(0,0,1;0rad)
  Support = -> [XY_Plane178]
  Width = 0.23
FEATURE [PartDesign::SubtractiveBox] Box1636
  AttacherType = Attacher::AttachEngine3D
  AttachmentOffset = pos=(-20.5,18.63,0) rot=(0,0,1;0rad)
  BaseFeature = -> Box1647
  Height = 1.635
  Length = 0.5
  MapMode = 5
  Placement = pos=(-20.5,18.63,0) rot=(0,0,1;0rad)
  Support = -> [XY_Plane178]
  Width = 0.25
FEATURE [PartDesign::SubtractiveBox] Box1643
  AttacherType = Attacher::AttachEngine3D
  AttachmentOffset = pos=(-21.19,18.635,-0.12) rot=(0,-1,0;0.15708rad)
  BaseFeature = -> Box1636
  Height = 0.12
  Length = 0.725
  MapMode = 5
  Placement = pos=(-21.19,18.635,-0.12) rot=(0,-1,0;0.15708rad)
  Support = -> [XY_Plane178]
  Width = 0.25
FEATURE [PartDesign::SubtractiveBox] Box1644
  AttacherType = Attacher::AttachEngine3D
  AttachmentOffset = pos=(-21.5005,18.625,0.235) rot=(0,-1,0;0.174533rad)
  BaseFeature = -> Box1643
  Height = 0.3
  Length = 0.6605
  MapMode = 5
  Placement = pos=(-21.5005,18.625,0.235) rot=(0,-1,0;0.174533rad)
  Support = -> [XY_Plane178]
  Width = 0.25
FEATURE [PartDesign::Fillet] Fillet460
  Base = -> Box1644 [Edge2]
  BaseFeature = -> Box1644
  Placement = pos=(-21.5005,18.625,0.235) rot=(0,-1,0;0.174533rad)
  Radius = 0.05
  SupportTransform = false
FEATURE [PartDesign::Fillet] Fillet461
  Base = -> Fillet460 [Edge33]
  BaseFeature = -> Fillet460
  Placement = pos=(-21.5005,18.625,0.235) rot=(0,-1,0;0.174533rad)
  Radius = 0.5
  SupportTransform = false
FEATURE [PartDesign::AdditiveBox] Box1638
  AttacherType = Attacher::AttachEngine3D
  AttachmentOffset = pos=(-21.1,18.635,0.305) rot=(0,1,0;0.785398rad)
  BaseFeature = -> Fillet461
  Height = 0.375
  Length = 0.2
  MapMode = 5
  Placement = pos=(-21.1,18.635,0.305) rot=(0,1,0;0.785398rad)
  Support = -> [XY_Plane178]
  Width = 0.23
FEATURE [PartDesign::SubtractiveCylinder] Cylinder331
  Angle = 360
  AttacherType = Attacher::AttachEngine3D
  AttachmentOffset = pos=(-21.055,18.935,0.52) rot=(1,0,0;1.5708rad)
  BaseFeature = -> Box1638
  Height = 0.375
  MapMode = 5
  Placement = pos=(-21.055,18.935,0.52) rot=(1,0,0;1.5708rad)
  Radius = 0.205
  Support = -> [XY_Plane178]
FEATURE [PartDesign::SubtractiveBox] Box1642
  AttacherType = Attacher::AttachEngine3D
  AttachmentOffset = pos=(-20.95,18.635,0.53) rot=(0,0,1;0rad)
  BaseFeature = -> Cylinder331
  Height = 0.5
  Length = 0.1
  MapMode = 5
  Placement = pos=(-20.95,18.635,0.53) rot=(0,0,1;0rad)
  Support = -> [XY_Plane178]
  Width = 0.23
FEATURE [PartDesign::SubtractiveBox] Box1639
  AttacherType = Attacher::AttachEngine3D
  AttachmentOffset = pos=(-21.15,18.635,0.297) rot=(0,-1,0;0.174533rad)
  BaseFeature = -> Box1642
  Height = 0.115
  Length = 0.115
  MapMode = 5
  Placement = pos=(-21.15,18.635,0.297) rot=(0,-1,0;0.174533rad)
  Support = -> [XY_Plane178]
  Width = 0.23
FEATURE [PartDesign::Fillet] Fillet462
  Base = -> Box1639 [Edge28]
  BaseFeature = -> Box1639
  Placement = pos=(-21.15,18.635,0.297) rot=(0,-1,0;0.174533rad)
  Radius = 0.375
  SupportTransform = false
FEATURE [PartDesign::AdditiveBox] Box1637
  AttacherType = Attacher::AttachEngine3D
  AttachmentOffset = pos=(-20.7,18.635,1.55) rot=(0,1,0;0.785398rad)
  BaseFeature = -> Fillet462
  Height = 0.375
  Length = 0.23
  MapMode = 5
  Placement = pos=(-20.7,18.635,1.55) rot=(0,1,0;0.785398rad)
  Support = -> [XY_Plane178]
  Width = 0.23
FEATURE [PartDesign::SubtractiveCylinder] Cylinder332
  Angle = 360
  AttacherType = Attacher::AttachEngine3D
  AttachmentOffset = pos=(-20.271,18.635,1.4056) rot=(-1,0,0;1.5708rad)
  BaseFeature = -> Box1637
  Height = 0.23
  MapMode = 5
  Placement = pos=(-20.271,18.635,1.4056) rot=(-1,0,0;1.5708rad)
  Radius = 0.23
  Support = -> [XY_Plane178]
FEATURE [PartDesign::AdditiveBox] Box1645
  AttacherType = Attacher::AttachEngine3D
  AttachmentOffset = pos=(-20.1,18.635,1.635) rot=(0,0,1;0rad)
  BaseFeature = -> Cylinder332
  Height = 0.265
  Length = 0.23
  MapMode = 5
  Placement = pos=(-20.1,18.635,1.635) rot=(0,0,1;0rad)
  Support = -> [XY_Plane178]
  Width = 0.23
FEATURE [PartDesign::Body] Body154  label="pin154"
  Group = -> [Box1646,Box1647,Box1636,Box1643,Box1644,Fillet460,Fillet461,Box1638,Cylinder331,Box1642,Box1639,Fillet462,Box1637,Cylinder332,Box1645]
  Origin = -> Origin169
  Placement = pos=(0,-0.5,0) rot=(0,0,1;0rad)
  Tip = -> Box1645
FEATURE [PartDesign::AdditiveBox] Box1653
  AttacherType = Attacher::AttachEngine3D
  AttachmentOffset = pos=(-21.3,18.635,0) rot=(0,0,1;0rad)
  Height = 1.9
  Length = 1.3
  MapMode = 5
  Placement = pos=(-21.3,18.635,0) rot=(0,0,1;0rad)
  Support = -> [XY_Plane168]
  Width = 0.23
FEATURE [PartDesign::SubtractiveBox] Box1656
  AttacherType = Attacher::AttachEngine3D
  AttachmentOffset = pos=(-21.35,18.635,0.35) rot=(0,0,1;0rad)
  BaseFeature = -> Box1653
  Height = 1.55
  Length = 0.5
  MapMode = 5
  Placement = pos=(-21.35,18.635,0.35) rot=(0,0,1;0rad)
  Support = -> [XY_Plane168]
  Width = 0.23
FEATURE [PartDesign::SubtractiveBox] Box1632
  AttacherType = Attacher::AttachEngine3D
  AttachmentOffset = pos=(-20.5,18.63,0) rot=(0,0,1;0rad)
  BaseFeature = -> Box1656
  Height = 1.635
  Length = 0.5
  MapMode = 5
  Placement = pos=(-20.5,18.63,0) rot=(0,0,1;0rad)
  Support = -> [XY_Plane168]
  Width = 0.25
FEATURE [PartDesign::SubtractiveBox] Box1652
  AttacherType = Attacher::AttachEngine3D
  AttachmentOffset = pos=(-21.19,18.635,-0.12) rot=(0,-1,0;0.15708rad)
  BaseFeature = -> Box1632
  Height = 0.12
  Length = 0.725
  MapMode = 5
  Placement = pos=(-21.19,18.635,-0.12) rot=(0,-1,0;0.15708rad)
  Support = -> [XY_Plane168]
  Width = 0.25
FEATURE [PartDesign::SubtractiveBox] Box1650
  AttacherType = Attacher::AttachEngine3D
  AttachmentOffset = pos=(-21.5005,18.625,0.235) rot=(0,-1,0;0.174533rad)
  BaseFeature = -> Box1652
  Height = 0.3
  Length = 0.6605
  MapMode = 5
  Placement = pos=(-21.5005,18.625,0.235) rot=(0,-1,0;0.174533rad)
  Support = -> [XY_Plane168]
  Width = 0.25
FEATURE [PartDesign::Fillet] Fillet463
  Base = -> Box1650 [Edge2]
  BaseFeature = -> Box1650
  Placement = pos=(-21.5005,18.625,0.235) rot=(0,-1,0;0.174533rad)
  Radius = 0.05
  SupportTransform = false
FEATURE [PartDesign::Fillet] Fillet470
  Base = -> Fillet463 [Edge33]
  BaseFeature = -> Fillet463
  Placement = pos=(-21.5005,18.625,0.235) rot=(0,-1,0;0.174533rad)
  Radius = 0.5
  SupportTransform = false
FEATURE [PartDesign::AdditiveBox] Box1640
  AttacherType = Attacher::AttachEngine3D
  AttachmentOffset = pos=(-21.1,18.635,0.305) rot=(0,1,0;0.785398rad)
  BaseFeature = -> Fillet470
  Height = 0.375
  Length = 0.2
  MapMode = 5
  Placement = pos=(-21.1,18.635,0.305) rot=(0,1,0;0.785398rad)
  Support = -> [XY_Plane168]
  Width = 0.23
FEATURE [PartDesign::SubtractiveCylinder] Cylinder333
  Angle = 360
  AttacherType = Attacher::AttachEngine3D
  AttachmentOffset = pos=(-21.055,18.935,0.52) rot=(1,0,0;1.5708rad)
  BaseFeature = -> Box1640
  Height = 0.375
  MapMode = 5
  Placement = pos=(-21.055,18.935,0.52) rot=(1,0,0;1.5708rad)
  Radius = 0.205
  Support = -> [XY_Plane168]
FEATURE [PartDesign::SubtractiveBox] Box1655
  AttacherType = Attacher::AttachEngine3D
  AttachmentOffset = pos=(-20.95,18.635,0.53) rot=(0,0,1;0rad)
  BaseFeature = -> Cylinder333
  Height = 0.5
  Length = 0.1
  MapMode = 5
  Placement = pos=(-20.95,18.635,0.53) rot=(0,0,1;0rad)
  Support = -> [XY_Plane168]
  Width = 0.23
FEATURE [PartDesign::SubtractiveBox] Box1649
  AttacherType = Attacher::AttachEngine3D
  AttachmentOffset = pos=(-21.15,18.635,0.297) rot=(0,-1,0;0.174533rad)
  BaseFeature = -> Box1655
  Height = 0.115
  Length = 0.115
  MapMode = 5
  Placement = pos=(-21.15,18.635,0.297) rot=(0,-1,0;0.174533rad)
  Support = -> [XY_Plane168]
  Width = 0.23
FEATURE [PartDesign::Fillet] Fillet471
  Base = -> Box1649 [Edge28]
  BaseFeature = -> Box1649
  Placement = pos=(-21.15,18.635,0.297) rot=(0,-1,0;0.174533rad)
  Radius = 0.375
  SupportTransform = false
FEATURE [PartDesign::AdditiveBox] Box1648
  AttacherType = Attacher::AttachEngine3D
  AttachmentOffset = pos=(-20.7,18.635,1.55) rot=(0,1,0;0.785398rad)
  BaseFeature = -> Fillet471
  Height = 0.375
  Length = 0.23
  MapMode = 5
  Placement = pos=(-20.7,18.635,1.55) rot=(0,1,0;0.785398rad)
  Support = -> [XY_Plane168]
  Width = 0.23
FEATURE [PartDesign::SubtractiveCylinder] Cylinder334
  Angle = 360
  AttacherType = Attacher::AttachEngine3D
  AttachmentOffset = pos=(-20.271,18.635,1.4056) rot=(-1,0,0;1.5708rad)
  BaseFeature = -> Box1648
  Height = 0.23
  MapMode = 5
  Placement = pos=(-20.271,18.635,1.4056) rot=(-1,0,0;1.5708rad)
  Radius = 0.23
  Support = -> [XY_Plane168]
FEATURE [PartDesign::AdditiveBox] Box1651
  AttacherType = Attacher::AttachEngine3D
  AttachmentOffset = pos=(-20.1,18.635,1.635) rot=(0,0,1;0rad)
  BaseFeature = -> Cylinder334
  Height = 0.265
  Length = 0.23
  MapMode = 5
  Placement = pos=(-20.1,18.635,1.635) rot=(0,0,1;0rad)
  Support = -> [XY_Plane168]
  Width = 0.23
FEATURE [PartDesign::Body] Body155  label="pin155"
  Group = -> [Box1653,Box1656,Box1632,Box1652,Box1650,Fillet463,Fillet470,Box1640,Cylinder333,Box1655,Box1649,Fillet471,Box1648,Cylinder334,Box1651]
  Origin = -> Origin170
  Placement = pos=(0,-1,0) rot=(0,0,1;0rad)
  Tip = -> Box1651
FEATURE [PartDesign::AdditiveBox] Box1657
  AttacherType = Attacher::AttachEngine3D
  AttachmentOffset = pos=(-21.3,18.635,0) rot=(0,0,1;0rad)
  Height = 1.9
  Length = 1.3
  MapMode = 5
  Placement = pos=(-21.3,18.635,0) rot=(0,0,1;0rad)
  Support = -> [XY_Plane169]
  Width = 0.23
FEATURE [PartDesign::Fillet] Fillet474
  Base = -> Box1523 [Edge2]
  BaseFeature = -> Box1523
  Placement = pos=(-21.5005,18.625,0.235) rot=(0,-1,0;0.174533rad)
  Radius = 0.05
  SupportTransform = false
FEATURE [PartDesign::Fillet] Fillet477
  Base = -> Box1603 [Edge2]
  BaseFeature = -> Box1603
  Placement = pos=(-21.5005,18.625,0.235) rot=(0,-1,0;0.174533rad)
  Radius = 0.05
  SupportTransform = false
FEATURE [PartDesign::Fillet] Fillet479
  Base = -> Box1581 [Edge2]
  BaseFeature = -> Box1581
  Placement = pos=(-21.5005,18.625,0.235) rot=(0,-1,0;0.174533rad)
  Radius = 0.05
  SupportTransform = false
FEATURE [PartDesign::Fillet] Fillet464
  Base = -> Fillet479 [Edge33]
  BaseFeature = -> Fillet479
  Placement = pos=(-21.5005,18.625,0.235) rot=(0,-1,0;0.174533rad)
  Radius = 0.5
  SupportTransform = false
FEATURE [PartDesign::AdditiveBox] Box1558
  AttacherType = Attacher::AttachEngine3D
  AttachmentOffset = pos=(-21.1,18.635,0.305) rot=(0,1,0;0.785398rad)
  BaseFeature = -> Fillet464
  Height = 0.375
  Length = 0.2
  MapMode = 5
  Placement = pos=(-21.1,18.635,0.305) rot=(0,1,0;0.785398rad)
  Support = -> [XY_Plane171]
  Width = 0.23
FEATURE [PartDesign::SubtractiveCylinder] Cylinder314
  Angle = 360
  AttacherType = Attacher::AttachEngine3D
  AttachmentOffset = pos=(-21.055,18.935,0.52) rot=(1,0,0;1.5708rad)
  BaseFeature = -> Box1558
  Height = 0.375
  MapMode = 5
  Placement = pos=(-21.055,18.935,0.52) rot=(1,0,0;1.5708rad)
  Radius = 0.205
  Support = -> [XY_Plane171]
FEATURE [PartDesign::SubtractiveBox] Box1560
  AttacherType = Attacher::AttachEngine3D
  AttachmentOffset = pos=(-20.95,18.635,0.53) rot=(0,0,1;0rad)
  BaseFeature = -> Cylinder314
  Height = 0.5
  Length = 0.1
  MapMode = 5
  Placement = pos=(-20.95,18.635,0.53) rot=(0,0,1;0rad)
  Support = -> [XY_Plane171]
  Width = 0.23
FEATURE [PartDesign::SubtractiveBox] Box1559
  AttacherType = Attacher::AttachEngine3D
  AttachmentOffset = pos=(-21.15,18.635,0.297) rot=(0,-1,0;0.174533rad)
  BaseFeature = -> Box1560
  Height = 0.115
  Length = 0.115
  MapMode = 5
  Placement = pos=(-21.15,18.635,0.297) rot=(0,-1,0;0.174533rad)
  Support = -> [XY_Plane171]
  Width = 0.23
FEATURE [PartDesign::Fillet] Fillet478
  Base = -> Box1559 [Edge28]
  BaseFeature = -> Box1559
  Placement = pos=(-21.15,18.635,0.297) rot=(0,-1,0;0.174533rad)
  Radius = 0.375
  SupportTransform = false
FEATURE [PartDesign::AdditiveBox] Box1557
  AttacherType = Attacher::AttachEngine3D
  AttachmentOffset = pos=(-20.7,18.635,1.55) rot=(0,1,0;0.785398rad)
  BaseFeature = -> Fillet478
  Height = 0.375
  Length = 0.23
  MapMode = 5
  Placement = pos=(-20.7,18.635,1.55) rot=(0,1,0;0.785398rad)
  Support = -> [XY_Plane171]
  Width = 0.23
FEATURE [PartDesign::SubtractiveCylinder] Cylinder313
  Angle = 360
  AttacherType = Attacher::AttachEngine3D
  AttachmentOffset = pos=(-20.271,18.635,1.4056) rot=(-1,0,0;1.5708rad)
  BaseFeature = -> Box1557
  Height = 0.23
  MapMode = 5
  Placement = pos=(-20.271,18.635,1.4056) rot=(-1,0,0;1.5708rad)
  Radius = 0.23
  Support = -> [XY_Plane171]
FEATURE [PartDesign::AdditiveBox] Box1556
  AttacherType = Attacher::AttachEngine3D
  AttachmentOffset = pos=(-20.1,18.635,1.635) rot=(0,0,1;0rad)
  BaseFeature = -> Cylinder313
  Height = 0.265
  Length = 0.23
  MapMode = 5
  Placement = pos=(-20.1,18.635,1.635) rot=(0,0,1;0rad)
  Support = -> [XY_Plane171]
  Width = 0.23
FEATURE [PartDesign::Body] Body156  label="pin156"
  Group = -> [Box1591,Box1582,Box1561,Box1563,Box1581,Fillet479,Fillet464,Box1558,Cylinder314,Box1560,Box1559,Fillet478,Box1557,Cylinder313,Box1556]
  Origin = -> Origin173
  Placement = pos=(0,-1.5,0) rot=(0,0,1;0rad)
  Tip = -> Box1556
FEATURE [PartDesign::Fillet] Fillet480
  Base = -> Box1528 [Edge2]
  BaseFeature = -> Box1528
  Placement = pos=(-21.5005,18.625,0.235) rot=(0,-1,0;0.174533rad)
  Radius = 0.05
  SupportTransform = false
FEATURE [PartDesign::Fillet] Fillet481
  Base = -> Fillet480 [Edge33]
  BaseFeature = -> Fillet480
  Placement = pos=(-21.5005,18.625,0.235) rot=(0,-1,0;0.174533rad)
  Radius = 0.5
  SupportTransform = false
FEATURE [PartDesign::AdditiveBox] Box1623
  AttacherType = Attacher::AttachEngine3D
  AttachmentOffset = pos=(-21.1,18.635,0.305) rot=(0,1,0;0.785398rad)
  BaseFeature = -> Fillet481
  Height = 0.375
  Length = 0.2
  MapMode = 5
  Placement = pos=(-21.1,18.635,0.305) rot=(0,1,0;0.785398rad)
  Support = -> [XY_Plane179]
  Width = 0.23
FEATURE [PartDesign::SubtractiveCylinder] Cylinder329
  Angle = 360
  AttacherType = Attacher::AttachEngine3D
  AttachmentOffset = pos=(-21.055,18.935,0.52) rot=(1,0,0;1.5708rad)
  BaseFeature = -> Box1623
  Height = 0.375
  MapMode = 5
  Placement = pos=(-21.055,18.935,0.52) rot=(1,0,0;1.5708rad)
  Radius = 0.205
  Support = -> [XY_Plane179]
FEATURE [PartDesign::SubtractiveBox] Box1630
  AttacherType = Attacher::AttachEngine3D
  AttachmentOffset = pos=(-20.95,18.635,0.53) rot=(0,0,1;0rad)
  BaseFeature = -> Cylinder329
  Height = 0.5
  Length = 0.1
  MapMode = 5
  Placement = pos=(-20.95,18.635,0.53) rot=(0,0,1;0rad)
  Support = -> [XY_Plane179]
  Width = 0.23
FEATURE [PartDesign::SubtractiveBox] Box1628
  AttacherType = Attacher::AttachEngine3D
  AttachmentOffset = pos=(-21.15,18.635,0.297) rot=(0,-1,0;0.174533rad)
  BaseFeature = -> Box1630
  Height = 0.115
  Length = 0.115
  MapMode = 5
  Placement = pos=(-21.15,18.635,0.297) rot=(0,-1,0;0.174533rad)
  Support = -> [XY_Plane179]
  Width = 0.23
FEATURE [PartDesign::Fillet] Fillet482
  Base = -> Box1628 [Edge28]
  BaseFeature = -> Box1628
  Placement = pos=(-21.15,18.635,0.297) rot=(0,-1,0;0.174533rad)
  Radius = 0.375
  SupportTransform = false
FEATURE [PartDesign::AdditiveBox] Box1624
  AttacherType = Attacher::AttachEngine3D
  AttachmentOffset = pos=(-20.7,18.635,1.55) rot=(0,1,0;0.785398rad)
  BaseFeature = -> Fillet482
  Height = 0.375
  Length = 0.23
  MapMode = 5
  Placement = pos=(-20.7,18.635,1.55) rot=(0,1,0;0.785398rad)
  Support = -> [XY_Plane179]
  Width = 0.23
FEATURE [PartDesign::SubtractiveCylinder] Cylinder330
  Angle = 360
  AttacherType = Attacher::AttachEngine3D
  AttachmentOffset = pos=(-20.271,18.635,1.4056) rot=(-1,0,0;1.5708rad)
  BaseFeature = -> Box1624
  Height = 0.23
  MapMode = 5
  Placement = pos=(-20.271,18.635,1.4056) rot=(-1,0,0;1.5708rad)
  Radius = 0.23
  Support = -> [XY_Plane179]
FEATURE [PartDesign::AdditiveBox] Box1526
  AttacherType = Attacher::AttachEngine3D
  AttachmentOffset = pos=(-20.1,18.635,1.635) rot=(0,0,1;0rad)
  BaseFeature = -> Cylinder330
  Height = 0.265
  Length = 0.23
  MapMode = 5
  Placement = pos=(-20.1,18.635,1.635) rot=(0,0,1;0rad)
  Support = -> [XY_Plane179]
  Width = 0.23
FEATURE [PartDesign::Body] Body160  label="pin160"
  Group = -> [Box1529,Box1522,Box1626,Box1525,Box1528,Fillet480,Fillet481,Box1623,Cylinder329,Box1630,Box1628,Fillet482,Box1624,Cylinder330,Box1526]
  Origin = -> Origin180
  Placement = pos=(0,-3.5,0) rot=(0,0,1;0rad)
  Tip = -> Box1526
FEATURE [PartDesign::Fillet] Fillet483
  Base = -> Box1605 [Edge2]
  BaseFeature = -> Box1605
  Placement = pos=(-21.5005,18.625,0.235) rot=(0,-1,0;0.174533rad)
  Radius = 0.05
  SupportTransform = false
FEATURE [PartDesign::Fillet] Fillet485
  Base = -> Fillet483 [Edge33]
  BaseFeature = -> Fillet483
  Placement = pos=(-21.5005,18.625,0.235) rot=(0,-1,0;0.174533rad)
  Radius = 0.5
  SupportTransform = false
FEATURE [PartDesign::AdditiveBox] Box1589
  AttacherType = Attacher::AttachEngine3D
  AttachmentOffset = pos=(-21.1,18.635,0.305) rot=(0,1,0;0.785398rad)
  BaseFeature = -> Fillet485
  Height = 0.375
  Length = 0.2
  MapMode = 5
  Placement = pos=(-21.1,18.635,0.305) rot=(0,1,0;0.785398rad)
  Support = -> [XY_Plane176]
  Width = 0.23
FEATURE [PartDesign::SubtractiveCylinder] Cylinder321
  Angle = 360
  AttacherType = Attacher::AttachEngine3D
  AttachmentOffset = pos=(-21.055,18.935,0.52) rot=(1,0,0;1.5708rad)
  BaseFeature = -> Box1589
  Height = 0.375
  MapMode = 5
  Placement = pos=(-21.055,18.935,0.52) rot=(1,0,0;1.5708rad)
  Radius = 0.205
  Support = -> [XY_Plane176]
FEATURE [PartDesign::SubtractiveBox] Box1606
  AttacherType = Attacher::AttachEngine3D
  AttachmentOffset = pos=(-20.95,18.635,0.53) rot=(0,0,1;0rad)
  BaseFeature = -> Cylinder321
  Height = 0.5
  Length = 0.1
  MapMode = 5
  Placement = pos=(-20.95,18.635,0.53) rot=(0,0,1;0rad)
  Support = -> [XY_Plane176]
  Width = 0.23
FEATURE [PartDesign::SubtractiveBox] Box1601
  AttacherType = Attacher::AttachEngine3D
  AttachmentOffset = pos=(-21.15,18.635,0.297) rot=(0,-1,0;0.174533rad)
  BaseFeature = -> Box1606
  Height = 0.115
  Length = 0.115
  MapMode = 5
  Placement = pos=(-21.15,18.635,0.297) rot=(0,-1,0;0.174533rad)
  Support = -> [XY_Plane176]
  Width = 0.23
FEATURE [PartDesign::Fillet] Fillet484
  Base = -> Box1601 [Edge28]
  BaseFeature = -> Box1601
  Placement = pos=(-21.15,18.635,0.297) rot=(0,-1,0;0.174533rad)
  Radius = 0.375
  SupportTransform = false
FEATURE [PartDesign::AdditiveBox] Box1596
  AttacherType = Attacher::AttachEngine3D
  AttachmentOffset = pos=(-20.7,18.635,1.55) rot=(0,1,0;0.785398rad)
  BaseFeature = -> Fillet484
  Height = 0.375
  Length = 0.23
  MapMode = 5
  Placement = pos=(-20.7,18.635,1.55) rot=(0,1,0;0.785398rad)
  Support = -> [XY_Plane176]
  Width = 0.23
FEATURE [PartDesign::SubtractiveCylinder] Cylinder322
  Angle = 360
  AttacherType = Attacher::AttachEngine3D
  AttachmentOffset = pos=(-20.271,18.635,1.4056) rot=(-1,0,0;1.5708rad)
  BaseFeature = -> Box1596
  Height = 0.23
  MapMode = 5
  Placement = pos=(-20.271,18.635,1.4056) rot=(-1,0,0;1.5708rad)
  Radius = 0.23
  Support = -> [XY_Plane176]
FEATURE [PartDesign::AdditiveBox] Box1604
  AttacherType = Attacher::AttachEngine3D
  AttachmentOffset = pos=(-20.1,18.635,1.635) rot=(0,0,1;0rad)
  BaseFeature = -> Cylinder322
  Height = 0.265
  Length = 0.23
  MapMode = 5
  Placement = pos=(-20.1,18.635,1.635) rot=(0,0,1;0rad)
  Support = -> [XY_Plane176]
  Width = 0.23
FEATURE [PartDesign::Body] Body163  label="pin163"
  Group = -> [Box1597,Box1600,Box1585,Box1610,Box1605,Fillet483,Fillet485,Box1589,Cylinder321,Box1606,Box1601,Fillet484,Box1596,Cylinder322,Box1604]
  Origin = -> Origin175
  Placement = pos=(0,-5,0) rot=(0,0,1;0rad)
  Tip = -> Box1604
FEATURE [PartDesign::Fillet] Fillet486
  Base = -> Fillet474 [Edge33]
  BaseFeature = -> Fillet474
  Placement = pos=(-21.5005,18.625,0.235) rot=(0,-1,0;0.174533rad)
  Radius = 0.5
  SupportTransform = false
FEATURE [PartDesign::AdditiveBox] Box1622
  AttacherType = Attacher::AttachEngine3D
  AttachmentOffset = pos=(-21.1,18.635,0.305) rot=(0,1,0;0.785398rad)
  BaseFeature = -> Fillet486
  Height = 0.375
  Length = 0.2
  MapMode = 5
  Placement = pos=(-21.1,18.635,0.305) rot=(0,1,0;0.785398rad)
  Support = -> [XY_Plane175]
  Width = 0.23
FEATURE [PartDesign::SubtractiveCylinder] Cylinder308
  Angle = 360
  AttacherType = Attacher::AttachEngine3D
  AttachmentOffset = pos=(-21.055,18.935,0.52) rot=(1,0,0;1.5708rad)
  BaseFeature = -> Box1622
  Height = 0.375
  MapMode = 5
  Placement = pos=(-21.055,18.935,0.52) rot=(1,0,0;1.5708rad)
  Radius = 0.205
  Support = -> [XY_Plane175]
FEATURE [PartDesign::SubtractiveBox] Box1534
  AttacherType = Attacher::AttachEngine3D
  AttachmentOffset = pos=(-20.95,18.635,0.53) rot=(0,0,1;0rad)
  BaseFeature = -> Cylinder308
  Height = 0.5
  Length = 0.1
  MapMode = 5
  Placement = pos=(-20.95,18.635,0.53) rot=(0,0,1;0rad)
  Support = -> [XY_Plane175]
  Width = 0.23
FEATURE [PartDesign::SubtractiveBox] Box1531
  AttacherType = Attacher::AttachEngine3D
  AttachmentOffset = pos=(-21.15,18.635,0.297) rot=(0,-1,0;0.174533rad)
  BaseFeature = -> Box1534
  Height = 0.115
  Length = 0.115
  MapMode = 5
  Placement = pos=(-21.15,18.635,0.297) rot=(0,-1,0;0.174533rad)
  Support = -> [XY_Plane175]
  Width = 0.23
FEATURE [PartDesign::Fillet] Fillet487
  Base = -> Box1531 [Edge28]
  BaseFeature = -> Box1531
  Placement = pos=(-21.15,18.635,0.297) rot=(0,-1,0;0.174533rad)
  Radius = 0.375
  SupportTransform = false
FEATURE [PartDesign::AdditiveBox] Box1530
  AttacherType = Attacher::AttachEngine3D
  AttachmentOffset = pos=(-20.7,18.635,1.55) rot=(0,1,0;0.785398rad)
  BaseFeature = -> Fillet487
  Height = 0.375
  Length = 0.23
  MapMode = 5
  Placement = pos=(-20.7,18.635,1.55) rot=(0,1,0;0.785398rad)
  Support = -> [XY_Plane175]
  Width = 0.23
FEATURE [PartDesign::SubtractiveCylinder] Cylinder309
  Angle = 360
  AttacherType = Attacher::AttachEngine3D
  AttachmentOffset = pos=(-20.271,18.635,1.4056) rot=(-1,0,0;1.5708rad)
  BaseFeature = -> Box1530
  Height = 0.23
  MapMode = 5
  Placement = pos=(-20.271,18.635,1.4056) rot=(-1,0,0;1.5708rad)
  Radius = 0.23
  Support = -> [XY_Plane175]
FEATURE [PartDesign::AdditiveBox] Box1521
  AttacherType = Attacher::AttachEngine3D
  AttachmentOffset = pos=(-20.1,18.635,1.635) rot=(0,0,1;0rad)
  BaseFeature = -> Cylinder309
  Height = 0.265
  Length = 0.23
  MapMode = 5
  Placement = pos=(-20.1,18.635,1.635) rot=(0,0,1;0rad)
  Support = -> [XY_Plane175]
  Width = 0.23
FEATURE [PartDesign::Body] Body161  label="pin161"
  Group = -> [Box1532,Box1527,Box1613,Box1524,Box1523,Fillet474,Fillet486,Box1622,Cylinder308,Box1534,Box1531,Fillet487,Box1530,Cylinder309,Box1521]
  Origin = -> Origin171
  Placement = pos=(0,-4,0) rot=(0,0,1;0rad)
  Tip = -> Box1521
FEATURE [PartDesign::Fillet] Fillet488
  Base = -> Box1533 [Edge2]
  BaseFeature = -> Box1533
  Placement = pos=(-21.5005,18.625,0.235) rot=(0,-1,0;0.174533rad)
  Radius = 0.05
  SupportTransform = false
FEATURE [PartDesign::Fillet] Fillet476
  Base = -> Fillet488 [Edge33]
  BaseFeature = -> Fillet488
  Placement = pos=(-21.5005,18.625,0.235) rot=(0,-1,0;0.174533rad)
  Radius = 0.5
  SupportTransform = false
FEATURE [PartDesign::AdditiveBox] Box1594
  AttacherType = Attacher::AttachEngine3D
  AttachmentOffset = pos=(-21.1,18.635,0.305) rot=(0,1,0;0.785398rad)
  BaseFeature = -> Fillet476
  Height = 0.375
  Length = 0.2
  MapMode = 5
  Placement = pos=(-21.1,18.635,0.305) rot=(0,1,0;0.785398rad)
  Support = -> [XY_Plane174]
  Width = 0.23
FEATURE [PartDesign::SubtractiveCylinder] Cylinder326
  Angle = 360
  AttacherType = Attacher::AttachEngine3D
  AttachmentOffset = pos=(-21.055,18.935,0.52) rot=(1,0,0;1.5708rad)
  BaseFeature = -> Box1594
  Height = 0.375
  MapMode = 5
  Placement = pos=(-21.055,18.935,0.52) rot=(1,0,0;1.5708rad)
  Radius = 0.205
  Support = -> [XY_Plane174]
FEATURE [PartDesign::SubtractiveBox] Box1617
  AttacherType = Attacher::AttachEngine3D
  AttachmentOffset = pos=(-20.95,18.635,0.53) rot=(0,0,1;0rad)
  BaseFeature = -> Cylinder326
  Height = 0.5
  Length = 0.1
  MapMode = 5
  Placement = pos=(-20.95,18.635,0.53) rot=(0,0,1;0rad)
  Support = -> [XY_Plane174]
  Width = 0.23
FEATURE [PartDesign::SubtractiveBox] Box1618
  AttacherType = Attacher::AttachEngine3D
  AttachmentOffset = pos=(-21.15,18.635,0.297) rot=(0,-1,0;0.174533rad)
  BaseFeature = -> Box1617
  Height = 0.115
  Length = 0.115
  MapMode = 5
  Placement = pos=(-21.15,18.635,0.297) rot=(0,-1,0;0.174533rad)
  Support = -> [XY_Plane174]
  Width = 0.23
FEATURE [PartDesign::Fillet] Fillet490
  Base = -> Box1618 [Edge28]
  BaseFeature = -> Box1618
  Placement = pos=(-21.15,18.635,0.297) rot=(0,-1,0;0.174533rad)
  Radius = 0.375
  SupportTransform = false
FEATURE [PartDesign::AdditiveBox] Box1625
  AttacherType = Attacher::AttachEngine3D
  AttachmentOffset = pos=(-20.7,18.635,1.55) rot=(0,1,0;0.785398rad)
  BaseFeature = -> Fillet490
  Height = 0.375
  Length = 0.23
  MapMode = 5
  Placement = pos=(-20.7,18.635,1.55) rot=(0,1,0;0.785398rad)
  Support = -> [XY_Plane174]
  Width = 0.23
FEATURE [PartDesign::SubtractiveCylinder] Cylinder327
  Angle = 360
  AttacherType = Attacher::AttachEngine3D
  AttachmentOffset = pos=(-20.271,18.635,1.4056) rot=(-1,0,0;1.5708rad)
  BaseFeature = -> Box1625
  Height = 0.23
  MapMode = 5
  Placement = pos=(-20.271,18.635,1.4056) rot=(-1,0,0;1.5708rad)
  Radius = 0.23
  Support = -> [XY_Plane174]
FEATURE [PartDesign::AdditiveBox] Box1629
  AttacherType = Attacher::AttachEngine3D
  AttachmentOffset = pos=(-20.1,18.635,1.635) rot=(0,0,1;0rad)
  BaseFeature = -> Cylinder327
  Height = 0.265
  Length = 0.23
  MapMode = 5
  Placement = pos=(-20.1,18.635,1.635) rot=(0,0,1;0rad)
  Support = -> [XY_Plane174]
  Width = 0.23
FEATURE [PartDesign::Body] Body159  label="pin159"
  Group = -> [Box1536,Box1537,Box1619,Box1627,Box1533,Fillet488,Fillet476,Box1594,Cylinder326,Box1617,Box1618,Fillet490,Box1625,Cylinder327,Box1629]
  Origin = -> Origin172
  Placement = pos=(0,-3,0) rot=(0,0,1;0rad)
  Tip = -> Box1629
FEATURE [PartDesign::Fillet] Fillet491
  Base = -> Fillet477 [Edge33]
  BaseFeature = -> Fillet477
  Placement = pos=(-21.5005,18.625,0.235) rot=(0,-1,0;0.174533rad)
  Radius = 0.5
  SupportTransform = false
FEATURE [PartDesign::AdditiveBox] Box1602
  AttacherType = Attacher::AttachEngine3D
  AttachmentOffset = pos=(-21.1,18.635,0.305) rot=(0,1,0;0.785398rad)
  BaseFeature = -> Fillet491
  Height = 0.375
  Length = 0.2
  MapMode = 5
  Placement = pos=(-21.1,18.635,0.305) rot=(0,1,0;0.785398rad)
  Support = -> [XY_Plane172]
  Width = 0.23
FEATURE [PartDesign::SubtractiveCylinder] Cylinder325
  Angle = 360
  AttacherType = Attacher::AttachEngine3D
  AttachmentOffset = pos=(-21.055,18.935,0.52) rot=(1,0,0;1.5708rad)
  BaseFeature = -> Box1602
  Height = 0.375
  MapMode = 5
  Placement = pos=(-21.055,18.935,0.52) rot=(1,0,0;1.5708rad)
  Radius = 0.205
  Support = -> [XY_Plane172]
FEATURE [PartDesign::SubtractiveBox] Box1609
  AttacherType = Attacher::AttachEngine3D
  AttachmentOffset = pos=(-20.95,18.635,0.53) rot=(0,0,1;0rad)
  BaseFeature = -> Cylinder325
  Height = 0.5
  Length = 0.1
  MapMode = 5
  Placement = pos=(-20.95,18.635,0.53) rot=(0,0,1;0rad)
  Support = -> [XY_Plane172]
  Width = 0.23
FEATURE [PartDesign::SubtractiveBox] Box1612
  AttacherType = Attacher::AttachEngine3D
  AttachmentOffset = pos=(-21.15,18.635,0.297) rot=(0,-1,0;0.174533rad)
  BaseFeature = -> Box1609
  Height = 0.115
  Length = 0.115
  MapMode = 5
  Placement = pos=(-21.15,18.635,0.297) rot=(0,-1,0;0.174533rad)
  Support = -> [XY_Plane172]
  Width = 0.23
FEATURE [PartDesign::Fillet] Fillet473
  Base = -> Box1612 [Edge28]
  BaseFeature = -> Box1612
  Placement = pos=(-21.15,18.635,0.297) rot=(0,-1,0;0.174533rad)
  Radius = 0.375
  SupportTransform = false
FEATURE [PartDesign::AdditiveBox] Box1611
  AttacherType = Attacher::AttachEngine3D
  AttachmentOffset = pos=(-20.7,18.635,1.55) rot=(0,1,0;0.785398rad)
  BaseFeature = -> Fillet473
  Height = 0.375
  Length = 0.23
  MapMode = 5
  Placement = pos=(-20.7,18.635,1.55) rot=(0,1,0;0.785398rad)
  Support = -> [XY_Plane172]
  Width = 0.23
FEATURE [PartDesign::SubtractiveCylinder] Cylinder324
  Angle = 360
  AttacherType = Attacher::AttachEngine3D
  AttachmentOffset = pos=(-20.271,18.635,1.4056) rot=(-1,0,0;1.5708rad)
  BaseFeature = -> Box1611
  Height = 0.23
  MapMode = 5
  Placement = pos=(-20.271,18.635,1.4056) rot=(-1,0,0;1.5708rad)
  Radius = 0.23
  Support = -> [XY_Plane172]
FEATURE [PartDesign::AdditiveBox] Box1598
  AttacherType = Attacher::AttachEngine3D
  AttachmentOffset = pos=(-20.1,18.635,1.635) rot=(0,0,1;0rad)
  BaseFeature = -> Cylinder324
  Height = 0.265
  Length = 0.23
  MapMode = 5
  Placement = pos=(-20.1,18.635,1.635) rot=(0,0,1;0rad)
  Support = -> [XY_Plane172]
  Width = 0.23
FEATURE [PartDesign::Body] Body164  label="pin164"
  Group = -> [Box1620,Box1615,Box1584,Box1599,Box1603,Fillet477,Fillet491,Box1602,Cylinder325,Box1609,Box1612,Fillet473,Box1611,Cylinder324,Box1598]
  Origin = -> Origin181
  Placement = pos=(0,-5.5,0) rot=(0,0,1;0rad)
  Tip = -> Box1598
FEATURE [PartDesign::Fillet] Fillet492
  Base = -> Box1621 [Edge2]
  BaseFeature = -> Box1621
  Placement = pos=(-21.5005,18.625,0.235) rot=(0,-1,0;0.174533rad)
  Radius = 0.05
  SupportTransform = false
FEATURE [PartDesign::Fillet] Fillet475
  Base = -> Fillet492 [Edge33]
  BaseFeature = -> Fillet492
  Placement = pos=(-21.5005,18.625,0.235) rot=(0,-1,0;0.174533rad)
  Radius = 0.5
  SupportTransform = false
FEATURE [PartDesign::AdditiveBox] Box1588
  AttacherType = Attacher::AttachEngine3D
  AttachmentOffset = pos=(-21.1,18.635,0.305) rot=(0,1,0;0.785398rad)
  BaseFeature = -> Fillet475
  Height = 0.375
  Length = 0.2
  MapMode = 5
  Placement = pos=(-21.1,18.635,0.305) rot=(0,1,0;0.785398rad)
  Support = -> [XY_Plane177]
  Width = 0.23
FEATURE [PartDesign::SubtractiveCylinder] Cylinder319
  Angle = 360
  AttacherType = Attacher::AttachEngine3D
  AttachmentOffset = pos=(-21.055,18.935,0.52) rot=(1,0,0;1.5708rad)
  BaseFeature = -> Box1588
  Height = 0.375
  MapMode = 5
  Placement = pos=(-21.055,18.935,0.52) rot=(1,0,0;1.5708rad)
  Radius = 0.205
  Support = -> [XY_Plane177]
FEATURE [PartDesign::SubtractiveBox] Box1590
  AttacherType = Attacher::AttachEngine3D
  AttachmentOffset = pos=(-20.95,18.635,0.53) rot=(0,0,1;0rad)
  BaseFeature = -> Cylinder319
  Height = 0.5
  Length = 0.1
  MapMode = 5
  Placement = pos=(-20.95,18.635,0.53) rot=(0,0,1;0rad)
  Support = -> [XY_Plane177]
  Width = 0.23
FEATURE [PartDesign::SubtractiveBox] Box1587
  AttacherType = Attacher::AttachEngine3D
  AttachmentOffset = pos=(-21.15,18.635,0.297) rot=(0,-1,0;0.174533rad)
  BaseFeature = -> Box1590
  Height = 0.115
  Length = 0.115
  MapMode = 5
  Placement = pos=(-21.15,18.635,0.297) rot=(0,-1,0;0.174533rad)
  Support = -> [XY_Plane177]
  Width = 0.23
FEATURE [PartDesign::Fillet] Fillet489
  Base = -> Box1587 [Edge28]
  BaseFeature = -> Box1587
  Placement = pos=(-21.15,18.635,0.297) rot=(0,-1,0;0.174533rad)
  Radius = 0.375
  SupportTransform = false
FEATURE [PartDesign::AdditiveBox] Box1593
  AttacherType = Attacher::AttachEngine3D
  AttachmentOffset = pos=(-20.7,18.635,1.55) rot=(0,1,0;0.785398rad)
  BaseFeature = -> Fillet489
  Height = 0.375
  Length = 0.23
  MapMode = 5
  Placement = pos=(-20.7,18.635,1.55) rot=(0,1,0;0.785398rad)
  Support = -> [XY_Plane177]
  Width = 0.23
FEATURE [PartDesign::SubtractiveCylinder] Cylinder320
  Angle = 360
  AttacherType = Attacher::AttachEngine3D
  AttachmentOffset = pos=(-20.271,18.635,1.4056) rot=(-1,0,0;1.5708rad)
  BaseFeature = -> Box1593
  Height = 0.23
  MapMode = 5
  Placement = pos=(-20.271,18.635,1.4056) rot=(-1,0,0;1.5708rad)
  Radius = 0.23
  Support = -> [XY_Plane177]
FEATURE [PartDesign::AdditiveBox] Box1583
  AttacherType = Attacher::AttachEngine3D
  AttachmentOffset = pos=(-20.1,18.635,1.635) rot=(0,0,1;0rad)
  BaseFeature = -> Cylinder320
  Height = 0.265
  Length = 0.23
  MapMode = 5
  Placement = pos=(-20.1,18.635,1.635) rot=(0,0,1;0rad)
  Support = -> [XY_Plane177]
  Width = 0.23
FEATURE [PartDesign::Body] Body162  label="pin162"
  Group = -> [Box1616,Box1614,Box1592,Box1595,Box1621,Fillet492,Fillet475,Box1588,Cylinder319,Box1590,Box1587,Fillet489,Box1593,Cylinder320,Box1583]
  Origin = -> Origin167
  Placement = pos=(0,-4.5,0) rot=(0,0,1;0rad)
  Tip = -> Box1583
FEATURE [PartDesign::AdditiveBox] Box1664
  AttacherType = Attacher::AttachEngine3D
  AttachmentOffset = pos=(-21.3,18.635,0) rot=(0,0,1;0rad)
  Height = 1.9
  Length = 1.3
  MapMode = 5
  Placement = pos=(-21.3,18.635,0) rot=(0,0,1;0rad)
  Support = -> [XY_Plane185]
  Width = 0.23
FEATURE [PartDesign::SubtractiveBox] Box1660
  AttacherType = Attacher::AttachEngine3D
  AttachmentOffset = pos=(-21.35,18.635,0.35) rot=(0,0,1;0rad)
  BaseFeature = -> Box1664
  Height = 1.55
  Length = 0.5
  MapMode = 5
  Placement = pos=(-21.35,18.635,0.35) rot=(0,0,1;0rad)
  Support = -> [XY_Plane185]
  Width = 0.23
FEATURE [PartDesign::AdditiveBox] Box1678
  AttacherType = Attacher::AttachEngine3D
  AttachmentOffset = pos=(-21.3,18.635,0) rot=(0,0,1;0rad)
  Height = 1.9
  Length = 1.3
  MapMode = 5
  Placement = pos=(-21.3,18.635,0) rot=(0,0,1;0rad)
  Support = -> [XY_Plane183]
  Width = 0.23
FEATURE [PartDesign::SubtractiveBox] Box1669
  AttacherType = Attacher::AttachEngine3D
  AttachmentOffset = pos=(-21.35,18.635,0.35) rot=(0,0,1;0rad)
  BaseFeature = -> Box1678
  Height = 1.55
  Length = 0.5
  MapMode = 5
  Placement = pos=(-21.35,18.635,0.35) rot=(0,0,1;0rad)
  Support = -> [XY_Plane183]
  Width = 0.23
FEATURE [PartDesign::AdditiveBox] Box1684
  AttacherType = Attacher::AttachEngine3D
  AttachmentOffset = pos=(-21.3,18.635,0) rot=(0,0,1;0rad)
  Height = 1.9
  Length = 1.3
  MapMode = 5
  Placement = pos=(-21.3,18.635,0) rot=(0,0,1;0rad)
  Support = -> [XY_Plane180]
  Width = 0.23
FEATURE [PartDesign::SubtractiveBox] Box1675
  AttacherType = Attacher::AttachEngine3D
  AttachmentOffset = pos=(-21.35,18.635,0.35) rot=(0,0,1;0rad)
  BaseFeature = -> Box1684
  Height = 1.55
  Length = 0.5
  MapMode = 5
  Placement = pos=(-21.35,18.635,0.35) rot=(0,0,1;0rad)
  Support = -> [XY_Plane180]
  Width = 0.23
FEATURE [PartDesign::AdditiveBox] Box1692
  AttacherType = Attacher::AttachEngine3D
  AttachmentOffset = pos=(-21.3,18.635,0) rot=(0,0,1;0rad)
  Height = 1.9
  Length = 1.3
  MapMode = 5
  Placement = pos=(-21.3,18.635,0) rot=(0,0,1;0rad)
  Support = -> [XY_Plane189]
  Width = 0.23
FEATURE [PartDesign::SubtractiveBox] Box1689
  AttacherType = Attacher::AttachEngine3D
  AttachmentOffset = pos=(-21.35,18.635,0.35) rot=(0,0,1;0rad)
  BaseFeature = -> Box1692
  Height = 1.55
  Length = 0.5
  MapMode = 5
  Placement = pos=(-21.35,18.635,0.35) rot=(0,0,1;0rad)
  Support = -> [XY_Plane189]
  Width = 0.23
FEATURE [PartDesign::SubtractiveBox] Box1679
  AttacherType = Attacher::AttachEngine3D
  AttachmentOffset = pos=(-20.5,18.63,0) rot=(0,0,1;0rad)
  BaseFeature = -> Box1689
  Height = 1.635
  Length = 0.5
  MapMode = 5
  Placement = pos=(-20.5,18.63,0) rot=(0,0,1;0rad)
  Support = -> [XY_Plane189]
  Width = 0.25
FEATURE [PartDesign::SubtractiveBox] Box1693
  AttacherType = Attacher::AttachEngine3D
  AttachmentOffset = pos=(-21.19,18.635,-0.12) rot=(0,-1,0;0.15708rad)
  BaseFeature = -> Box1679
  Height = 0.12
  Length = 0.725
  MapMode = 5
  Placement = pos=(-21.19,18.635,-0.12) rot=(0,-1,0;0.15708rad)
  Support = -> [XY_Plane189]
  Width = 0.25
FEATURE [PartDesign::SubtractiveBox] Box1697
  AttacherType = Attacher::AttachEngine3D
  AttachmentOffset = pos=(-20.5,18.63,0) rot=(0,0,1;0rad)
  BaseFeature = -> Box1544
  Height = 1.635
  Length = 0.5
  MapMode = 5
  Placement = pos=(-20.5,18.63,0) rot=(0,0,1;0rad)
  Support = -> [XY_Plane187]
  Width = 0.25
FEATURE [PartDesign::SubtractiveBox] Box1542
  AttacherType = Attacher::AttachEngine3D
  AttachmentOffset = pos=(-21.19,18.635,-0.12) rot=(0,-1,0;0.15708rad)
  BaseFeature = -> Box1697
  Height = 0.12
  Length = 0.725
  MapMode = 5
  Placement = pos=(-21.19,18.635,-0.12) rot=(0,-1,0;0.15708rad)
  Support = -> [XY_Plane187]
  Width = 0.25
FEATURE [PartDesign::SubtractiveBox] Box1541
  AttacherType = Attacher::AttachEngine3D
  AttachmentOffset = pos=(-21.5005,18.625,0.235) rot=(0,-1,0;0.174533rad)
  BaseFeature = -> Box1542
  Height = 0.3
  Length = 0.6605
  MapMode = 5
  Placement = pos=(-21.5005,18.625,0.235) rot=(0,-1,0;0.174533rad)
  Support = -> [XY_Plane187]
  Width = 0.25
FEATURE [PartDesign::SubtractiveBox] Box1700
  AttacherType = Attacher::AttachEngine3D
  AttachmentOffset = pos=(-21.5005,18.625,0.235) rot=(0,-1,0;0.174533rad)
  BaseFeature = -> Box1693
  Height = 0.3
  Length = 0.6605
  MapMode = 5
  Placement = pos=(-21.5005,18.625,0.235) rot=(0,-1,0;0.174533rad)
  Support = -> [XY_Plane189]
  Width = 0.25
FEATURE [PartDesign::AdditiveBox] Box1707
  AttacherType = Attacher::AttachEngine3D
  AttachmentOffset = pos=(-21.3,18.635,0) rot=(0,0,1;0rad)
  Height = 1.9
  Length = 1.3
  MapMode = 5
  Placement = pos=(-21.3,18.635,0) rot=(0,0,1;0rad)
  Support = -> [XY_Plane191]
  Width = 0.23
FEATURE [PartDesign::SubtractiveBox] Box1695
  AttacherType = Attacher::AttachEngine3D
  AttachmentOffset = pos=(-21.35,18.635,0.35) rot=(0,0,1;0rad)
  BaseFeature = -> Box1707
  Height = 1.55
  Length = 0.5
  MapMode = 5
  Placement = pos=(-21.35,18.635,0.35) rot=(0,0,1;0rad)
  Support = -> [XY_Plane191]
  Width = 0.23
FEATURE [PartDesign::SubtractiveBox] Box1683
  AttacherType = Attacher::AttachEngine3D
  AttachmentOffset = pos=(-20.5,18.63,0) rot=(0,0,1;0rad)
  BaseFeature = -> Box1695
  Height = 1.635
  Length = 0.5
  MapMode = 5
  Placement = pos=(-20.5,18.63,0) rot=(0,0,1;0rad)
  Support = -> [XY_Plane191]
  Width = 0.25
FEATURE [PartDesign::SubtractiveBox] Box1674
  AttacherType = Attacher::AttachEngine3D
  AttachmentOffset = pos=(-21.19,18.635,-0.12) rot=(0,-1,0;0.15708rad)
  BaseFeature = -> Box1683
  Height = 0.12
  Length = 0.725
  MapMode = 5
  Placement = pos=(-21.19,18.635,-0.12) rot=(0,-1,0;0.15708rad)
  Support = -> [XY_Plane191]
  Width = 0.25
FEATURE [PartDesign::SubtractiveBox] Box1709
  AttacherType = Attacher::AttachEngine3D
  AttachmentOffset = pos=(-20.5,18.63,0) rot=(0,0,1;0rad)
  BaseFeature = -> Box1552
  Height = 1.635
  Length = 0.5
  MapMode = 5
  Placement = pos=(-20.5,18.63,0) rot=(0,0,1;0rad)
  Support = -> [XY_Plane190]
  Width = 0.25
FEATURE [PartDesign::AdditiveBox] Box1711
  AttacherType = Attacher::AttachEngine3D
  AttachmentOffset = pos=(-21.3,18.635,0) rot=(0,0,1;0rad)
  Height = 1.9
  Length = 1.3
  MapMode = 5
  Placement = pos=(-21.3,18.635,0) rot=(0,0,1;0rad)
  Support = -> [XY_Plane173]
  Width = 0.23
FEATURE [PartDesign::SubtractiveBox] Box1706
  AttacherType = Attacher::AttachEngine3D
  AttachmentOffset = pos=(-21.35,18.635,0.35) rot=(0,0,1;0rad)
  BaseFeature = -> Box1711
  Height = 1.55
  Length = 0.5
  MapMode = 5
  Placement = pos=(-21.35,18.635,0.35) rot=(0,0,1;0rad)
  Support = -> [XY_Plane173]
  Width = 0.23
FEATURE [PartDesign::SubtractiveBox] Box1677
  AttacherType = Attacher::AttachEngine3D
  AttachmentOffset = pos=(-20.5,18.63,0) rot=(0,0,1;0rad)
  BaseFeature = -> Box1706
  Height = 1.635
  Length = 0.5
  MapMode = 5
  Placement = pos=(-20.5,18.63,0) rot=(0,0,1;0rad)
  Support = -> [XY_Plane173]
  Width = 0.25
FEATURE [PartDesign::SubtractiveBox] Box1687
  AttacherType = Attacher::AttachEngine3D
  AttachmentOffset = pos=(-21.19,18.635,-0.12) rot=(0,-1,0;0.15708rad)
  BaseFeature = -> Box1677
  Height = 0.12
  Length = 0.725
  MapMode = 5
  Placement = pos=(-21.19,18.635,-0.12) rot=(0,-1,0;0.15708rad)
  Support = -> [XY_Plane173]
  Width = 0.25
FEATURE [PartDesign::SubtractiveBox] Box1688
  AttacherType = Attacher::AttachEngine3D
  AttachmentOffset = pos=(-21.5005,18.625,0.235) rot=(0,-1,0;0.174533rad)
  BaseFeature = -> Box1687
  Height = 0.3
  Length = 0.6605
  MapMode = 5
  Placement = pos=(-21.5005,18.625,0.235) rot=(0,-1,0;0.174533rad)
  Support = -> [XY_Plane173]
  Width = 0.25
FEATURE [PartDesign::SubtractiveBox] Box1714
  AttacherType = Attacher::AttachEngine3D
  AttachmentOffset = pos=(-20.5,18.63,0) rot=(0,0,1;0rad)
  BaseFeature = -> Box1548
  Height = 1.635
  Length = 0.5
  MapMode = 5
  Placement = pos=(-20.5,18.63,0) rot=(0,0,1;0rad)
  Support = -> [XY_Plane192]
  Width = 0.25
FEATURE [PartDesign::SubtractiveBox] Box1549
  AttacherType = Attacher::AttachEngine3D
  AttachmentOffset = pos=(-21.19,18.635,-0.12) rot=(0,-1,0;0.15708rad)
  BaseFeature = -> Box1714
  Height = 0.12
  Length = 0.725
  MapMode = 5
  Placement = pos=(-21.19,18.635,-0.12) rot=(0,-1,0;0.15708rad)
  Support = -> [XY_Plane192]
  Width = 0.25
FEATURE [PartDesign::SubtractiveBox] Box1538
  AttacherType = Attacher::AttachEngine3D
  AttachmentOffset = pos=(-21.5005,18.625,0.235) rot=(0,-1,0;0.174533rad)
  BaseFeature = -> Box1549
  Height = 0.3
  Length = 0.6605
  MapMode = 5
  Placement = pos=(-21.5005,18.625,0.235) rot=(0,-1,0;0.174533rad)
  Support = -> [XY_Plane192]
  Width = 0.25
FEATURE [PartDesign::SubtractiveBox] Box1715
  AttacherType = Attacher::AttachEngine3D
  AttachmentOffset = pos=(-21.19,18.635,-0.12) rot=(0,-1,0;0.15708rad)
  BaseFeature = -> Box1709
  Height = 0.12
  Length = 0.725
  MapMode = 5
  Placement = pos=(-21.19,18.635,-0.12) rot=(0,-1,0;0.15708rad)
  Support = -> [XY_Plane190]
  Width = 0.25
FEATURE [PartDesign::SubtractiveBox] Box1550
  AttacherType = Attacher::AttachEngine3D
  AttachmentOffset = pos=(-21.5005,18.625,0.235) rot=(0,-1,0;0.174533rad)
  BaseFeature = -> Box1715
  Height = 0.3
  Length = 0.6605
  MapMode = 5
  Placement = pos=(-21.5005,18.625,0.235) rot=(0,-1,0;0.174533rad)
  Support = -> [XY_Plane190]
  Width = 0.25
FEATURE [PartDesign::SubtractiveBox] Box1716
  AttacherType = Attacher::AttachEngine3D
  AttachmentOffset = pos=(-21.5005,18.625,0.235) rot=(0,-1,0;0.174533rad)
  BaseFeature = -> Box1674
  Height = 0.3
  Length = 0.6605
  MapMode = 5
  Placement = pos=(-21.5005,18.625,0.235) rot=(0,-1,0;0.174533rad)
  Support = -> [XY_Plane191]
  Width = 0.25
FEATURE [PartDesign::AdditiveBox] Box1736
  AttacherType = Attacher::AttachEngine3D
  AttachmentOffset = pos=(-21.3,18.635,0) rot=(0,0,1;0rad)
  Height = 1.9
  Length = 1.3
  MapMode = 5
  Placement = pos=(-21.3,18.635,0) rot=(0,0,1;0rad)
  Support = -> [XY_Plane188]
  Width = 0.23
FEATURE [PartDesign::SubtractiveBox] Box1726
  AttacherType = Attacher::AttachEngine3D
  AttachmentOffset = pos=(-21.35,18.635,0.35) rot=(0,0,1;0rad)
  BaseFeature = -> Box1736
  Height = 1.55
  Length = 0.5
  MapMode = 5
  Placement = pos=(-21.35,18.635,0.35) rot=(0,0,1;0rad)
  Support = -> [XY_Plane188]
  Width = 0.23
FEATURE [PartDesign::SubtractiveBox] Box1728
  AttacherType = Attacher::AttachEngine3D
  AttachmentOffset = pos=(-20.5,18.63,0) rot=(0,0,1;0rad)
  BaseFeature = -> Box1726
  Height = 1.635
  Length = 0.5
  MapMode = 5
  Placement = pos=(-20.5,18.63,0) rot=(0,0,1;0rad)
  Support = -> [XY_Plane188]
  Width = 0.25
FEATURE [PartDesign::SubtractiveBox] Box1732
  AttacherType = Attacher::AttachEngine3D
  AttachmentOffset = pos=(-21.19,18.635,-0.12) rot=(0,-1,0;0.15708rad)
  BaseFeature = -> Box1728
  Height = 0.12
  Length = 0.725
  MapMode = 5
  Placement = pos=(-21.19,18.635,-0.12) rot=(0,-1,0;0.15708rad)
  Support = -> [XY_Plane188]
  Width = 0.25
FEATURE [PartDesign::SubtractiveBox] Box1733
  AttacherType = Attacher::AttachEngine3D
  AttachmentOffset = pos=(-21.5005,18.625,0.235) rot=(0,-1,0;0.174533rad)
  BaseFeature = -> Box1732
  Height = 0.3
  Length = 0.6605
  MapMode = 5
  Placement = pos=(-21.5005,18.625,0.235) rot=(0,-1,0;0.174533rad)
  Support = -> [XY_Plane188]
  Width = 0.25
FEATURE [PartDesign::AdditiveBox] Box1742
  AttacherType = Attacher::AttachEngine3D
  AttachmentOffset = pos=(-21.3,18.635,0) rot=(0,0,1;0rad)
  Height = 1.9
  Length = 1.3
  MapMode = 5
  Placement = pos=(-21.3,18.635,0) rot=(0,0,1;0rad)
  Support = -> [XY_Plane205]
  Width = 0.23
FEATURE [PartDesign::AdditiveBox] Box1744
  AttacherType = Attacher::AttachEngine3D
  AttachmentOffset = pos=(-21.3,18.635,0) rot=(0,0,1;0rad)
  Height = 1.9
  Length = 1.3
  MapMode = 5
  Placement = pos=(-21.3,18.635,0) rot=(0,0,1;0rad)
  Support = -> [XY_Plane184]
  Width = 0.23
FEATURE [PartDesign::SubtractiveBox] Box1741
  AttacherType = Attacher::AttachEngine3D
  AttachmentOffset = pos=(-21.35,18.635,0.35) rot=(0,0,1;0rad)
  BaseFeature = -> Box1744
  Height = 1.55
  Length = 0.5
  MapMode = 5
  Placement = pos=(-21.35,18.635,0.35) rot=(0,0,1;0rad)
  Support = -> [XY_Plane184]
  Width = 0.23
FEATURE [PartDesign::SubtractiveBox] Box1725
  AttacherType = Attacher::AttachEngine3D
  AttachmentOffset = pos=(-20.5,18.63,0) rot=(0,0,1;0rad)
  BaseFeature = -> Box1741
  Height = 1.635
  Length = 0.5
  MapMode = 5
  Placement = pos=(-20.5,18.63,0) rot=(0,0,1;0rad)
  Support = -> [XY_Plane184]
  Width = 0.25
FEATURE [PartDesign::AdditiveBox] Box1746
  AttacherType = Attacher::AttachEngine3D
  AttachmentOffset = pos=(-21.3,18.635,0) rot=(0,0,1;0rad)
  Height = 1.9
  Length = 1.3
  MapMode = 5
  Placement = pos=(-21.3,18.635,0) rot=(0,0,1;0rad)
  Support = -> [XY_Plane186]
  Width = 0.23
FEATURE [PartDesign::SubtractiveBox] Box1748
  AttacherType = Attacher::AttachEngine3D
  AttachmentOffset = pos=(-21.19,18.635,-0.12) rot=(0,-1,0;0.15708rad)
  BaseFeature = -> Box1725
  Height = 0.12
  Length = 0.725
  MapMode = 5
  Placement = pos=(-21.19,18.635,-0.12) rot=(0,-1,0;0.15708rad)
  Support = -> [XY_Plane184]
  Width = 0.25
FEATURE [PartDesign::SubtractiveBox] Box1747
  AttacherType = Attacher::AttachEngine3D
  AttachmentOffset = pos=(-21.5005,18.625,0.235) rot=(0,-1,0;0.174533rad)
  BaseFeature = -> Box1748
  Height = 0.3
  Length = 0.6605
  MapMode = 5
  Placement = pos=(-21.5005,18.625,0.235) rot=(0,-1,0;0.174533rad)
  Support = -> [XY_Plane184]
  Width = 0.25
FEATURE [PartDesign::SubtractiveBox] Box1749
  AttacherType = Attacher::AttachEngine3D
  AttachmentOffset = pos=(-21.35,18.635,0.35) rot=(0,0,1;0rad)
  BaseFeature = -> Box1746
  Height = 1.55
  Length = 0.5
  MapMode = 5
  Placement = pos=(-21.35,18.635,0.35) rot=(0,0,1;0rad)
  Support = -> [XY_Plane186]
  Width = 0.23
FEATURE [PartDesign::SubtractiveBox] Box1727
  AttacherType = Attacher::AttachEngine3D
  AttachmentOffset = pos=(-20.5,18.63,0) rot=(0,0,1;0rad)
  BaseFeature = -> Box1749
  Height = 1.635
  Length = 0.5
  MapMode = 5
  Placement = pos=(-20.5,18.63,0) rot=(0,0,1;0rad)
  Support = -> [XY_Plane186]
  Width = 0.25
FEATURE [PartDesign::SubtractiveBox] Box1722
  AttacherType = Attacher::AttachEngine3D
  AttachmentOffset = pos=(-21.19,18.635,-0.12) rot=(0,-1,0;0.15708rad)
  BaseFeature = -> Box1727
  Height = 0.12
  Length = 0.725
  MapMode = 5
  Placement = pos=(-21.19,18.635,-0.12) rot=(0,-1,0;0.15708rad)
  Support = -> [XY_Plane186]
  Width = 0.25
FEATURE [PartDesign::SubtractiveBox] Box1745
  AttacherType = Attacher::AttachEngine3D
  AttachmentOffset = pos=(-21.5005,18.625,0.235) rot=(0,-1,0;0.174533rad)
  BaseFeature = -> Box1722
  Height = 0.3
  Length = 0.6605
  MapMode = 5
  Placement = pos=(-21.5005,18.625,0.235) rot=(0,-1,0;0.174533rad)
  Support = -> [XY_Plane186]
  Width = 0.25
FEATURE [PartDesign::AdditiveBox] Box1751
  AttacherType = Attacher::AttachEngine3D
  AttachmentOffset = pos=(-21.3,18.635,0) rot=(0,0,1;0rad)
  Height = 1.9
  Length = 1.3
  MapMode = 5
  Placement = pos=(-21.3,18.635,0) rot=(0,0,1;0rad)
  Support = -> [XY_Plane203]
  Width = 0.23
FEATURE [PartDesign::Fillet] Fillet496
  Base = -> Box1733 [Edge2]
  BaseFeature = -> Box1733
  Placement = pos=(-21.5005,18.625,0.235) rot=(0,-1,0;0.174533rad)
  Radius = 0.05
  SupportTransform = false
FEATURE [PartDesign::Fillet] Fillet497
  Base = -> Fillet496 [Edge33]
  BaseFeature = -> Fillet496
  Placement = pos=(-21.5005,18.625,0.235) rot=(0,-1,0;0.174533rad)
  Radius = 0.5
  SupportTransform = false
FEATURE [PartDesign::AdditiveBox] Box1719
  AttacherType = Attacher::AttachEngine3D
  AttachmentOffset = pos=(-21.1,18.635,0.305) rot=(0,1,0;0.785398rad)
  BaseFeature = -> Fillet497
  Height = 0.375
  Length = 0.2
  MapMode = 5
  Placement = pos=(-21.1,18.635,0.305) rot=(0,1,0;0.785398rad)
  Support = -> [XY_Plane188]
  Width = 0.23
FEATURE [PartDesign::SubtractiveCylinder] Cylinder348
  Angle = 360
  AttacherType = Attacher::AttachEngine3D
  AttachmentOffset = pos=(-21.055,18.935,0.52) rot=(1,0,0;1.5708rad)
  BaseFeature = -> Box1719
  Height = 0.375
  MapMode = 5
  Placement = pos=(-21.055,18.935,0.52) rot=(1,0,0;1.5708rad)
  Radius = 0.205
  Support = -> [XY_Plane188]
FEATURE [PartDesign::SubtractiveBox] Box1734
  AttacherType = Attacher::AttachEngine3D
  AttachmentOffset = pos=(-20.95,18.635,0.53) rot=(0,0,1;0rad)
  BaseFeature = -> Cylinder348
  Height = 0.5
  Length = 0.1
  MapMode = 5
  Placement = pos=(-20.95,18.635,0.53) rot=(0,0,1;0rad)
  Support = -> [XY_Plane188]
  Width = 0.23
FEATURE [PartDesign::SubtractiveBox] Box1730
  AttacherType = Attacher::AttachEngine3D
  AttachmentOffset = pos=(-21.15,18.635,0.297) rot=(0,-1,0;0.174533rad)
  BaseFeature = -> Box1734
  Height = 0.115
  Length = 0.115
  MapMode = 5
  Placement = pos=(-21.15,18.635,0.297) rot=(0,-1,0;0.174533rad)
  Support = -> [XY_Plane188]
  Width = 0.23
FEATURE [PartDesign::Fillet] Fillet498
  Base = -> Box1747 [Edge2]
  BaseFeature = -> Box1747
  Placement = pos=(-21.5005,18.625,0.235) rot=(0,-1,0;0.174533rad)
  Radius = 0.05
  SupportTransform = false
FEATURE [PartDesign::Fillet] Fillet504
  Base = -> Box1730 [Edge28]
  BaseFeature = -> Box1730
  Placement = pos=(-21.15,18.635,0.297) rot=(0,-1,0;0.174533rad)
  Radius = 0.375
  SupportTransform = false
FEATURE [PartDesign::AdditiveBox] Box1729
  AttacherType = Attacher::AttachEngine3D
  AttachmentOffset = pos=(-20.7,18.635,1.55) rot=(0,1,0;0.785398rad)
  BaseFeature = -> Fillet504
  Height = 0.375
  Length = 0.23
  MapMode = 5
  Placement = pos=(-20.7,18.635,1.55) rot=(0,1,0;0.785398rad)
  Support = -> [XY_Plane188]
  Width = 0.23
FEATURE [PartDesign::SubtractiveCylinder] Cylinder351
  Angle = 360
  AttacherType = Attacher::AttachEngine3D
  AttachmentOffset = pos=(-20.271,18.635,1.4056) rot=(-1,0,0;1.5708rad)
  BaseFeature = -> Box1729
  Height = 0.23
  MapMode = 5
  Placement = pos=(-20.271,18.635,1.4056) rot=(-1,0,0;1.5708rad)
  Radius = 0.23
  Support = -> [XY_Plane188]
FEATURE [PartDesign::AdditiveBox] Box1735
  AttacherType = Attacher::AttachEngine3D
  AttachmentOffset = pos=(-20.1,18.635,1.635) rot=(0,0,1;0rad)
  BaseFeature = -> Cylinder351
  Height = 0.265
  Length = 0.23
  MapMode = 5
  Placement = pos=(-20.1,18.635,1.635) rot=(0,0,1;0rad)
  Support = -> [XY_Plane188]
  Width = 0.23
FEATURE [PartDesign::Body] Body166  label="pin166"
  Group = -> [Box1736,Box1726,Box1728,Box1732,Box1733,Fillet496,Fillet497,Box1719,Cylinder348,Box1734,Box1730,Fillet504,Box1729,Cylinder351,Box1735]
  Origin = -> Origin178
  Placement = pos=(0,-0.5,0) rot=(0,0,1;0rad)
  Tip = -> Box1735
FEATURE [PartDesign::Fillet] Fillet505
  Base = -> Fillet498 [Edge33]
  BaseFeature = -> Fillet498
  Placement = pos=(-21.5005,18.625,0.235) rot=(0,-1,0;0.174533rad)
  Radius = 0.5
  SupportTransform = false
FEATURE [PartDesign::AdditiveBox] Box1724
  AttacherType = Attacher::AttachEngine3D
  AttachmentOffset = pos=(-21.1,18.635,0.305) rot=(0,1,0;0.785398rad)
  BaseFeature = -> Fillet505
  Height = 0.375
  Length = 0.2
  MapMode = 5
  Placement = pos=(-21.1,18.635,0.305) rot=(0,1,0;0.785398rad)
  Support = -> [XY_Plane184]
  Width = 0.23
FEATURE [PartDesign::SubtractiveCylinder] Cylinder352
  Angle = 360
  AttacherType = Attacher::AttachEngine3D
  AttachmentOffset = pos=(-21.055,18.935,0.52) rot=(1,0,0;1.5708rad)
  BaseFeature = -> Box1724
  Height = 0.375
  MapMode = 5
  Placement = pos=(-21.055,18.935,0.52) rot=(1,0,0;1.5708rad)
  Radius = 0.205
  Support = -> [XY_Plane184]
FEATURE [PartDesign::SubtractiveBox] Box1740
  AttacherType = Attacher::AttachEngine3D
  AttachmentOffset = pos=(-20.95,18.635,0.53) rot=(0,0,1;0rad)
  BaseFeature = -> Cylinder352
  Height = 0.5
  Length = 0.1
  MapMode = 5
  Placement = pos=(-20.95,18.635,0.53) rot=(0,0,1;0rad)
  Support = -> [XY_Plane184]
  Width = 0.23
FEATURE [PartDesign::SubtractiveBox] Box1737
  AttacherType = Attacher::AttachEngine3D
  AttachmentOffset = pos=(-21.15,18.635,0.297) rot=(0,-1,0;0.174533rad)
  BaseFeature = -> Box1740
  Height = 0.115
  Length = 0.115
  MapMode = 5
  Placement = pos=(-21.15,18.635,0.297) rot=(0,-1,0;0.174533rad)
  Support = -> [XY_Plane184]
  Width = 0.23
FEATURE [PartDesign::Fillet] Fillet493
  Base = -> Box1737 [Edge28]
  BaseFeature = -> Box1737
  Placement = pos=(-21.15,18.635,0.297) rot=(0,-1,0;0.174533rad)
  Radius = 0.375
  SupportTransform = false
FEATURE [PartDesign::AdditiveBox] Box1739
  AttacherType = Attacher::AttachEngine3D
  AttachmentOffset = pos=(-20.7,18.635,1.55) rot=(0,1,0;0.785398rad)
  BaseFeature = -> Fillet493
  Height = 0.375
  Length = 0.23
  MapMode = 5
  Placement = pos=(-20.7,18.635,1.55) rot=(0,1,0;0.785398rad)
  Support = -> [XY_Plane184]
  Width = 0.23
FEATURE [PartDesign::SubtractiveCylinder] Cylinder353
  Angle = 360
  AttacherType = Attacher::AttachEngine3D
  AttachmentOffset = pos=(-20.271,18.635,1.4056) rot=(-1,0,0;1.5708rad)
  BaseFeature = -> Box1739
  Height = 0.23
  MapMode = 5
  Placement = pos=(-20.271,18.635,1.4056) rot=(-1,0,0;1.5708rad)
  Radius = 0.23
  Support = -> [XY_Plane184]
FEATURE [PartDesign::AdditiveBox] Box1743
  AttacherType = Attacher::AttachEngine3D
  AttachmentOffset = pos=(-20.1,18.635,1.635) rot=(0,0,1;0rad)
  BaseFeature = -> Cylinder353
  Height = 0.265
  Length = 0.23
  MapMode = 5
  Placement = pos=(-20.1,18.635,1.635) rot=(0,0,1;0rad)
  Support = -> [XY_Plane184]
  Width = 0.23
FEATURE [PartDesign::Body] Body170  label="pin170"
  Group = -> [Box1744,Box1741,Box1725,Box1748,Box1747,Fillet498,Fillet505,Box1724,Cylinder352,Box1740,Box1737,Fillet493,Box1739,Cylinder353,Box1743]
  Origin = -> Origin187
  Placement = pos=(0,-1,0) rot=(0,0,1;0rad)
  Tip = -> Box1743
FEATURE [PartDesign::Fillet] Fillet506
  Base = -> Box1745 [Edge2]
  BaseFeature = -> Box1745
  Placement = pos=(-21.5005,18.625,0.235) rot=(0,-1,0;0.174533rad)
  Radius = 0.05
  SupportTransform = false
FEATURE [PartDesign::Fillet] Fillet458
  Base = -> Fillet506 [Edge33]
  BaseFeature = -> Fillet506
  Placement = pos=(-21.5005,18.625,0.235) rot=(0,-1,0;0.174533rad)
  Radius = 0.5
  SupportTransform = false
FEATURE [PartDesign::AdditiveBox] Box1553
  AttacherType = Attacher::AttachEngine3D
  AttachmentOffset = pos=(-21.1,18.635,0.305) rot=(0,1,0;0.785398rad)
  BaseFeature = -> Fillet458
  Height = 0.375
  Length = 0.2
  MapMode = 5
  Placement = pos=(-21.1,18.635,0.305) rot=(0,1,0;0.785398rad)
  Support = -> [XY_Plane186]
  Width = 0.23
FEATURE [PartDesign::SubtractiveCylinder] Cylinder343
  Angle = 360
  AttacherType = Attacher::AttachEngine3D
  AttachmentOffset = pos=(-21.055,18.935,0.52) rot=(1,0,0;1.5708rad)
  BaseFeature = -> Box1553
  Height = 0.375
  MapMode = 5
  Placement = pos=(-21.055,18.935,0.52) rot=(1,0,0;1.5708rad)
  Radius = 0.205
  Support = -> [XY_Plane186]
FEATURE [PartDesign::SubtractiveBox] Box1702
  AttacherType = Attacher::AttachEngine3D
  AttachmentOffset = pos=(-20.95,18.635,0.53) rot=(0,0,1;0rad)
  BaseFeature = -> Cylinder343
  Height = 0.5
  Length = 0.1
  MapMode = 5
  Placement = pos=(-20.95,18.635,0.53) rot=(0,0,1;0rad)
  Support = -> [XY_Plane186]
  Width = 0.23
FEATURE [PartDesign::SubtractiveBox] Box1690
  AttacherType = Attacher::AttachEngine3D
  AttachmentOffset = pos=(-21.15,18.635,0.297) rot=(0,-1,0;0.174533rad)
  BaseFeature = -> Box1702
  Height = 0.115
  Length = 0.115
  MapMode = 5
  Placement = pos=(-21.15,18.635,0.297) rot=(0,-1,0;0.174533rad)
  Support = -> [XY_Plane186]
  Width = 0.23
FEATURE [PartDesign::Fillet] Fillet510
  Base = -> Box1700 [Edge2]
  BaseFeature = -> Box1700
  Placement = pos=(-21.5005,18.625,0.235) rot=(0,-1,0;0.174533rad)
  Radius = 0.05
  SupportTransform = false
FEATURE [PartDesign::Fillet] Fillet512
  Base = -> Fillet510 [Edge33]
  BaseFeature = -> Fillet510
  Placement = pos=(-21.5005,18.625,0.235) rot=(0,-1,0;0.174533rad)
  Radius = 0.5
  SupportTransform = false
FEATURE [PartDesign::AdditiveBox] Box1682
  AttacherType = Attacher::AttachEngine3D
  AttachmentOffset = pos=(-21.1,18.635,0.305) rot=(0,1,0;0.785398rad)
  BaseFeature = -> Fillet512
  Height = 0.375
  Length = 0.2
  MapMode = 5
  Placement = pos=(-21.1,18.635,0.305) rot=(0,1,0;0.785398rad)
  Support = -> [XY_Plane189]
  Width = 0.23
FEATURE [PartDesign::SubtractiveCylinder] Cylinder340
  Angle = 360
  AttacherType = Attacher::AttachEngine3D
  AttachmentOffset = pos=(-21.055,18.935,0.52) rot=(1,0,0;1.5708rad)
  BaseFeature = -> Box1682
  Height = 0.375
  MapMode = 5
  Placement = pos=(-21.055,18.935,0.52) rot=(1,0,0;1.5708rad)
  Radius = 0.205
  Support = -> [XY_Plane189]
FEATURE [PartDesign::SubtractiveBox] Box1701
  AttacherType = Attacher::AttachEngine3D
  AttachmentOffset = pos=(-20.95,18.635,0.53) rot=(0,0,1;0rad)
  BaseFeature = -> Cylinder340
  Height = 0.5
  Length = 0.1
  MapMode = 5
  Placement = pos=(-20.95,18.635,0.53) rot=(0,0,1;0rad)
  Support = -> [XY_Plane189]
  Width = 0.23
FEATURE [PartDesign::SubtractiveBox] Box1686
  AttacherType = Attacher::AttachEngine3D
  AttachmentOffset = pos=(-21.15,18.635,0.297) rot=(0,-1,0;0.174533rad)
  BaseFeature = -> Box1701
  Height = 0.115
  Length = 0.115
  MapMode = 5
  Placement = pos=(-21.15,18.635,0.297) rot=(0,-1,0;0.174533rad)
  Support = -> [XY_Plane189]
  Width = 0.23
FEATURE [PartDesign::Fillet] Fillet511
  Base = -> Box1686 [Edge28]
  BaseFeature = -> Box1686
  Placement = pos=(-21.15,18.635,0.297) rot=(0,-1,0;0.174533rad)
  Radius = 0.375
  SupportTransform = false
FEATURE [PartDesign::AdditiveBox] Box1691
  AttacherType = Attacher::AttachEngine3D
  AttachmentOffset = pos=(-20.7,18.635,1.55) rot=(0,1,0;0.785398rad)
  BaseFeature = -> Fillet511
  Height = 0.375
  Length = 0.23
  MapMode = 5
  Placement = pos=(-20.7,18.635,1.55) rot=(0,1,0;0.785398rad)
  Support = -> [XY_Plane189]
  Width = 0.23
FEATURE [PartDesign::SubtractiveCylinder] Cylinder342
  Angle = 360
  AttacherType = Attacher::AttachEngine3D
  AttachmentOffset = pos=(-20.271,18.635,1.4056) rot=(-1,0,0;1.5708rad)
  BaseFeature = -> Box1691
  Height = 0.23
  MapMode = 5
  Placement = pos=(-20.271,18.635,1.4056) rot=(-1,0,0;1.5708rad)
  Radius = 0.23
  Support = -> [XY_Plane189]
FEATURE [PartDesign::AdditiveBox] Box1699
  AttacherType = Attacher::AttachEngine3D
  AttachmentOffset = pos=(-20.1,18.635,1.635) rot=(0,0,1;0rad)
  BaseFeature = -> Cylinder342
  Height = 0.265
  Length = 0.23
  MapMode = 5
  Placement = pos=(-20.1,18.635,1.635) rot=(0,0,1;0rad)
  Support = -> [XY_Plane189]
  Width = 0.23
FEATURE [PartDesign::Body] Body173  label="pin173"
  Group = -> [Box1692,Box1689,Box1679,Box1693,Box1700,Fillet510,Fillet512,Box1682,Cylinder340,Box1701,Box1686,Fillet511,Box1691,Cylinder342,Box1699]
  Origin = -> Origin186
  Placement = pos=(0,-5,0) rot=(0,0,1;0rad)
  Tip = -> Box1699
FEATURE [PartDesign::Fillet] Fillet513
  Base = -> Box1538 [Edge2]
  BaseFeature = -> Box1538
  Placement = pos=(-21.5005,18.625,0.235) rot=(0,-1,0;0.174533rad)
  Radius = 0.05
  SupportTransform = false
FEATURE [PartDesign::Fillet] Fillet516
  Base = -> Box1541 [Edge2]
  BaseFeature = -> Box1541
  Placement = pos=(-21.5005,18.625,0.235) rot=(0,-1,0;0.174533rad)
  Radius = 0.05
  SupportTransform = false
FEATURE [PartDesign::Fillet] Fillet517
  Base = -> Box1688 [Edge2]
  BaseFeature = -> Box1688
  Placement = pos=(-21.5005,18.625,0.235) rot=(0,-1,0;0.174533rad)
  Radius = 0.05
  SupportTransform = false
FEATURE [PartDesign::Fillet] Fillet518
  Base = -> Fillet513 [Edge33]
  BaseFeature = -> Fillet513
  Placement = pos=(-21.5005,18.625,0.235) rot=(0,-1,0;0.174533rad)
  Radius = 0.5
  SupportTransform = false
FEATURE [PartDesign::AdditiveBox] Box1721
  AttacherType = Attacher::AttachEngine3D
  AttachmentOffset = pos=(-21.1,18.635,0.305) rot=(0,1,0;0.785398rad)
  BaseFeature = -> Fillet518
  Height = 0.375
  Length = 0.2
  MapMode = 5
  Placement = pos=(-21.1,18.635,0.305) rot=(0,1,0;0.785398rad)
  Support = -> [XY_Plane192]
  Width = 0.23
FEATURE [PartDesign::SubtractiveCylinder] Cylinder350
  Angle = 360
  AttacherType = Attacher::AttachEngine3D
  AttachmentOffset = pos=(-21.055,18.935,0.52) rot=(1,0,0;1.5708rad)
  BaseFeature = -> Box1721
  Height = 0.375
  MapMode = 5
  Placement = pos=(-21.055,18.935,0.52) rot=(1,0,0;1.5708rad)
  Radius = 0.205
  Support = -> [XY_Plane192]
FEATURE [PartDesign::SubtractiveBox] Box1718
  AttacherType = Attacher::AttachEngine3D
  AttachmentOffset = pos=(-20.95,18.635,0.53) rot=(0,0,1;0rad)
  BaseFeature = -> Cylinder350
  Height = 0.5
  Length = 0.1
  MapMode = 5
  Placement = pos=(-20.95,18.635,0.53) rot=(0,0,1;0rad)
  Support = -> [XY_Plane192]
  Width = 0.23
FEATURE [PartDesign::SubtractiveBox] Box1710
  AttacherType = Attacher::AttachEngine3D
  AttachmentOffset = pos=(-21.15,18.635,0.297) rot=(0,-1,0;0.174533rad)
  BaseFeature = -> Box1718
  Height = 0.115
  Length = 0.115
  MapMode = 5
  Placement = pos=(-21.15,18.635,0.297) rot=(0,-1,0;0.174533rad)
  Support = -> [XY_Plane192]
  Width = 0.23
FEATURE [PartDesign::Fillet] Fillet508
  Base = -> Box1710 [Edge28]
  BaseFeature = -> Box1710
  Placement = pos=(-21.15,18.635,0.297) rot=(0,-1,0;0.174533rad)
  Radius = 0.375
  SupportTransform = false
FEATURE [PartDesign::AdditiveBox] Box1713
  AttacherType = Attacher::AttachEngine3D
  AttachmentOffset = pos=(-20.7,18.635,1.55) rot=(0,1,0;0.785398rad)
  BaseFeature = -> Fillet508
  Height = 0.375
  Length = 0.23
  MapMode = 5
  Placement = pos=(-20.7,18.635,1.55) rot=(0,1,0;0.785398rad)
  Support = -> [XY_Plane192]
  Width = 0.23
FEATURE [PartDesign::SubtractiveCylinder] Cylinder349
  Angle = 360
  AttacherType = Attacher::AttachEngine3D
  AttachmentOffset = pos=(-20.271,18.635,1.4056) rot=(-1,0,0;1.5708rad)
  BaseFeature = -> Box1713
  Height = 0.23
  MapMode = 5
  Placement = pos=(-20.271,18.635,1.4056) rot=(-1,0,0;1.5708rad)
  Radius = 0.23
  Support = -> [XY_Plane192]
FEATURE [PartDesign::AdditiveBox] Box1543
  AttacherType = Attacher::AttachEngine3D
  AttachmentOffset = pos=(-20.1,18.635,1.635) rot=(0,0,1;0rad)
  BaseFeature = -> Cylinder349
  Height = 0.265
  Length = 0.23
  MapMode = 5
  Placement = pos=(-20.1,18.635,1.635) rot=(0,0,1;0rad)
  Support = -> [XY_Plane192]
  Width = 0.23
FEATURE [PartDesign::Body] Body175  label="pin175"
  Group = -> [Box1545,Box1548,Box1714,Box1549,Box1538,Fillet513,Fillet518,Box1721,Cylinder350,Box1718,Box1710,Fillet508,Box1713,Cylinder349,Box1543]
  Origin = -> Origin202
  Placement = pos=(0,-3.5,0) rot=(0,0,1;0rad)
  Tip = -> Box1543
FEATURE [PartDesign::Fillet] Fillet520
  Base = -> Fillet516 [Edge33]
  BaseFeature = -> Fillet516
  Placement = pos=(-21.5005,18.625,0.235) rot=(0,-1,0;0.174533rad)
  Radius = 0.5
  SupportTransform = false
FEATURE [PartDesign::AdditiveBox] Box1720
  AttacherType = Attacher::AttachEngine3D
  AttachmentOffset = pos=(-21.1,18.635,0.305) rot=(0,1,0;0.785398rad)
  BaseFeature = -> Fillet520
  Height = 0.375
  Length = 0.2
  MapMode = 5
  Placement = pos=(-21.1,18.635,0.305) rot=(0,1,0;0.785398rad)
  Support = -> [XY_Plane187]
  Width = 0.23
FEATURE [PartDesign::SubtractiveCylinder] Cylinder310
  Angle = 360
  AttacherType = Attacher::AttachEngine3D
  AttachmentOffset = pos=(-21.055,18.935,0.52) rot=(1,0,0;1.5708rad)
  BaseFeature = -> Box1720
  Height = 0.375
  MapMode = 5
  Placement = pos=(-21.055,18.935,0.52) rot=(1,0,0;1.5708rad)
  Radius = 0.205
  Support = -> [XY_Plane187]
FEATURE [PartDesign::SubtractiveBox] Box1551
  AttacherType = Attacher::AttachEngine3D
  AttachmentOffset = pos=(-20.95,18.635,0.53) rot=(0,0,1;0rad)
  BaseFeature = -> Cylinder310
  Height = 0.5
  Length = 0.1
  MapMode = 5
  Placement = pos=(-20.95,18.635,0.53) rot=(0,0,1;0rad)
  Support = -> [XY_Plane187]
  Width = 0.23
FEATURE [PartDesign::SubtractiveBox] Box1547
  AttacherType = Attacher::AttachEngine3D
  AttachmentOffset = pos=(-21.15,18.635,0.297) rot=(0,-1,0;0.174533rad)
  BaseFeature = -> Box1551
  Height = 0.115
  Length = 0.115
  MapMode = 5
  Placement = pos=(-21.15,18.635,0.297) rot=(0,-1,0;0.174533rad)
  Support = -> [XY_Plane187]
  Width = 0.23
FEATURE [PartDesign::Fillet] Fillet521
  Base = -> Box1716 [Edge2]
  BaseFeature = -> Box1716
  Placement = pos=(-21.5005,18.625,0.235) rot=(0,-1,0;0.174533rad)
  Radius = 0.05
  SupportTransform = false
FEATURE [PartDesign::Fillet] Fillet514
  Base = -> Fillet521 [Edge33]
  BaseFeature = -> Fillet521
  Placement = pos=(-21.5005,18.625,0.235) rot=(0,-1,0;0.174533rad)
  Radius = 0.5
  SupportTransform = false
FEATURE [PartDesign::AdditiveBox] Box1673
  AttacherType = Attacher::AttachEngine3D
  AttachmentOffset = pos=(-21.1,18.635,0.305) rot=(0,1,0;0.785398rad)
  BaseFeature = -> Fillet514
  Height = 0.375
  Length = 0.2
  MapMode = 5
  Placement = pos=(-21.1,18.635,0.305) rot=(0,1,0;0.785398rad)
  Support = -> [XY_Plane191]
  Width = 0.23
FEATURE [PartDesign::SubtractiveCylinder] Cylinder338
  Angle = 360
  AttacherType = Attacher::AttachEngine3D
  AttachmentOffset = pos=(-21.055,18.935,0.52) rot=(1,0,0;1.5708rad)
  BaseFeature = -> Box1673
  Height = 0.375
  MapMode = 5
  Placement = pos=(-21.055,18.935,0.52) rot=(1,0,0;1.5708rad)
  Radius = 0.205
  Support = -> [XY_Plane191]
FEATURE [PartDesign::SubtractiveBox] Box1670
  AttacherType = Attacher::AttachEngine3D
  AttachmentOffset = pos=(-20.95,18.635,0.53) rot=(0,0,1;0rad)
  BaseFeature = -> Cylinder338
  Height = 0.5
  Length = 0.1
  MapMode = 5
  Placement = pos=(-20.95,18.635,0.53) rot=(0,0,1;0rad)
  Support = -> [XY_Plane191]
  Width = 0.23
FEATURE [PartDesign::SubtractiveBox] Box1681
  AttacherType = Attacher::AttachEngine3D
  AttachmentOffset = pos=(-21.15,18.635,0.297) rot=(0,-1,0;0.174533rad)
  BaseFeature = -> Box1670
  Height = 0.115
  Length = 0.115
  MapMode = 5
  Placement = pos=(-21.15,18.635,0.297) rot=(0,-1,0;0.174533rad)
  Support = -> [XY_Plane191]
  Width = 0.23
FEATURE [PartDesign::Fillet] Fillet522
  Base = -> Box1550 [Edge2]
  BaseFeature = -> Box1550
  Placement = pos=(-21.5005,18.625,0.235) rot=(0,-1,0;0.174533rad)
  Radius = 0.05
  SupportTransform = false
FEATURE [PartDesign::Fillet] Fillet515
  Base = -> Fillet522 [Edge33]
  BaseFeature = -> Fillet522
  Placement = pos=(-21.5005,18.625,0.235) rot=(0,-1,0;0.174533rad)
  Radius = 0.5
  SupportTransform = false
FEATURE [PartDesign::AdditiveBox] Box1685
  AttacherType = Attacher::AttachEngine3D
  AttachmentOffset = pos=(-21.1,18.635,0.305) rot=(0,1,0;0.785398rad)
  BaseFeature = -> Fillet515
  Height = 0.375
  Length = 0.2
  MapMode = 5
  Placement = pos=(-21.1,18.635,0.305) rot=(0,1,0;0.785398rad)
  Support = -> [XY_Plane190]
  Width = 0.23
FEATURE [PartDesign::SubtractiveCylinder] Cylinder345
  Angle = 360
  AttacherType = Attacher::AttachEngine3D
  AttachmentOffset = pos=(-21.055,18.935,0.52) rot=(1,0,0;1.5708rad)
  BaseFeature = -> Box1685
  Height = 0.375
  MapMode = 5
  Placement = pos=(-21.055,18.935,0.52) rot=(1,0,0;1.5708rad)
  Radius = 0.205
  Support = -> [XY_Plane190]
FEATURE [PartDesign::SubtractiveBox] Box1696
  AttacherType = Attacher::AttachEngine3D
  AttachmentOffset = pos=(-20.95,18.635,0.53) rot=(0,0,1;0rad)
  BaseFeature = -> Cylinder345
  Height = 0.5
  Length = 0.1
  MapMode = 5
  Placement = pos=(-20.95,18.635,0.53) rot=(0,0,1;0rad)
  Support = -> [XY_Plane190]
  Width = 0.23
FEATURE [PartDesign::SubtractiveBox] Box1708
  AttacherType = Attacher::AttachEngine3D
  AttachmentOffset = pos=(-21.15,18.635,0.297) rot=(0,-1,0;0.174533rad)
  BaseFeature = -> Box1696
  Height = 0.115
  Length = 0.115
  MapMode = 5
  Placement = pos=(-21.15,18.635,0.297) rot=(0,-1,0;0.174533rad)
  Support = -> [XY_Plane190]
  Width = 0.23
FEATURE [PartDesign::Fillet] Fillet519
  Base = -> Box1708 [Edge28]
  BaseFeature = -> Box1708
  Placement = pos=(-21.15,18.635,0.297) rot=(0,-1,0;0.174533rad)
  Radius = 0.375
  SupportTransform = false
FEATURE [PartDesign::AdditiveBox] Box1712
  AttacherType = Attacher::AttachEngine3D
  AttachmentOffset = pos=(-20.7,18.635,1.55) rot=(0,1,0;0.785398rad)
  BaseFeature = -> Fillet519
  Height = 0.375
  Length = 0.23
  MapMode = 5
  Placement = pos=(-20.7,18.635,1.55) rot=(0,1,0;0.785398rad)
  Support = -> [XY_Plane190]
  Width = 0.23
FEATURE [PartDesign::SubtractiveCylinder] Cylinder346
  Angle = 360
  AttacherType = Attacher::AttachEngine3D
  AttachmentOffset = pos=(-20.271,18.635,1.4056) rot=(-1,0,0;1.5708rad)
  BaseFeature = -> Box1712
  Height = 0.23
  MapMode = 5
  Placement = pos=(-20.271,18.635,1.4056) rot=(-1,0,0;1.5708rad)
  Radius = 0.23
  Support = -> [XY_Plane190]
FEATURE [PartDesign::AdditiveBox] Box1723
  AttacherType = Attacher::AttachEngine3D
  AttachmentOffset = pos=(-20.1,18.635,1.635) rot=(0,0,1;0rad)
  BaseFeature = -> Cylinder346
  Height = 0.265
  Length = 0.23
  MapMode = 5
  Placement = pos=(-20.1,18.635,1.635) rot=(0,0,1;0rad)
  Support = -> [XY_Plane190]
  Width = 0.23
FEATURE [PartDesign::Body] Body174  label="pin174"
  Group = -> [Box1540,Box1552,Box1709,Box1715,Box1550,Fillet522,Fillet515,Box1685,Cylinder345,Box1696,Box1708,Fillet519,Box1712,Cylinder346,Box1723]
  Origin = -> Origin204
  Placement = pos=(0,-3,0) rot=(0,0,1;0rad)
  Tip = -> Box1723
FEATURE [PartDesign::Fillet] Fillet523
  Base = -> Fillet517 [Edge33]
  BaseFeature = -> Fillet517
  Placement = pos=(-21.5005,18.625,0.235) rot=(0,-1,0;0.174533rad)
  Radius = 0.5
  SupportTransform = false
FEATURE [PartDesign::AdditiveBox] Box1698
  AttacherType = Attacher::AttachEngine3D
  AttachmentOffset = pos=(-21.1,18.635,0.305) rot=(0,1,0;0.785398rad)
  BaseFeature = -> Fillet523
  Height = 0.375
  Length = 0.2
  MapMode = 5
  Placement = pos=(-21.1,18.635,0.305) rot=(0,1,0;0.785398rad)
  Support = -> [XY_Plane173]
  Width = 0.23
FEATURE [PartDesign::SubtractiveCylinder] Cylinder344
  Angle = 360
  AttacherType = Attacher::AttachEngine3D
  AttachmentOffset = pos=(-21.055,18.935,0.52) rot=(1,0,0;1.5708rad)
  BaseFeature = -> Box1698
  Height = 0.375
  MapMode = 5
  Placement = pos=(-21.055,18.935,0.52) rot=(1,0,0;1.5708rad)
  Radius = 0.205
  Support = -> [XY_Plane173]
FEATURE [PartDesign::SubtractiveBox] Box1703
  AttacherType = Attacher::AttachEngine3D
  AttachmentOffset = pos=(-20.95,18.635,0.53) rot=(0,0,1;0rad)
  BaseFeature = -> Cylinder344
  Height = 0.5
  Length = 0.1
  MapMode = 5
  Placement = pos=(-20.95,18.635,0.53) rot=(0,0,1;0rad)
  Support = -> [XY_Plane173]
  Width = 0.23
FEATURE [PartDesign::SubtractiveBox] Box1705
  AttacherType = Attacher::AttachEngine3D
  AttachmentOffset = pos=(-21.15,18.635,0.297) rot=(0,-1,0;0.174533rad)
  BaseFeature = -> Box1703
  Height = 0.115
  Length = 0.115
  MapMode = 5
  Placement = pos=(-21.15,18.635,0.297) rot=(0,-1,0;0.174533rad)
  Support = -> [XY_Plane173]
  Width = 0.23
FEATURE [PartDesign::Fillet] Fillet494
  Base = -> Box1705 [Edge28]
  BaseFeature = -> Box1705
  Placement = pos=(-21.15,18.635,0.297) rot=(0,-1,0;0.174533rad)
  Radius = 0.375
  SupportTransform = false
FEATURE [PartDesign::AdditiveBox] Box1704
  AttacherType = Attacher::AttachEngine3D
  AttachmentOffset = pos=(-20.7,18.635,1.55) rot=(0,1,0;0.785398rad)
  BaseFeature = -> Fillet494
  Height = 0.375
  Length = 0.23
  MapMode = 5
  Placement = pos=(-20.7,18.635,1.55) rot=(0,1,0;0.785398rad)
  Support = -> [XY_Plane173]
  Width = 0.23
FEATURE [PartDesign::SubtractiveCylinder] Cylinder341
  Angle = 360
  AttacherType = Attacher::AttachEngine3D
  AttachmentOffset = pos=(-20.271,18.635,1.4056) rot=(-1,0,0;1.5708rad)
  BaseFeature = -> Box1704
  Height = 0.23
  MapMode = 5
  Placement = pos=(-20.271,18.635,1.4056) rot=(-1,0,0;1.5708rad)
  Radius = 0.23
  Support = -> [XY_Plane173]
FEATURE [PartDesign::AdditiveBox] Box1694
  AttacherType = Attacher::AttachEngine3D
  AttachmentOffset = pos=(-20.1,18.635,1.635) rot=(0,0,1;0rad)
  BaseFeature = -> Cylinder341
  Height = 0.265
  Length = 0.23
  MapMode = 5
  Placement = pos=(-20.1,18.635,1.635) rot=(0,0,1;0rad)
  Support = -> [XY_Plane173]
  Width = 0.23
FEATURE [PartDesign::Body] Body176  label="pin176"
  Group = -> [Box1711,Box1706,Box1677,Box1687,Box1688,Fillet517,Fillet523,Box1698,Cylinder344,Box1703,Box1705,Fillet494,Box1704,Cylinder341,Box1694]
  Origin = -> Origin190
  Placement = pos=(0,-5.5,0) rot=(0,0,1;0rad)
  Tip = -> Box1694
FEATURE [PartDesign::Fillet] Fillet524
  Base = -> Box1547 [Edge28]
  BaseFeature = -> Box1547
  Placement = pos=(-21.15,18.635,0.297) rot=(0,-1,0;0.174533rad)
  Radius = 0.375
  SupportTransform = false
FEATURE [PartDesign::AdditiveBox] Box1546
  AttacherType = Attacher::AttachEngine3D
  AttachmentOffset = pos=(-20.7,18.635,1.55) rot=(0,1,0;0.785398rad)
  BaseFeature = -> Fillet524
  Height = 0.375
  Length = 0.23
  MapMode = 5
  Placement = pos=(-20.7,18.635,1.55) rot=(0,1,0;0.785398rad)
  Support = -> [XY_Plane187]
  Width = 0.23
FEATURE [PartDesign::SubtractiveCylinder] Cylinder311
  Angle = 360
  AttacherType = Attacher::AttachEngine3D
  AttachmentOffset = pos=(-20.271,18.635,1.4056) rot=(-1,0,0;1.5708rad)
  BaseFeature = -> Box1546
  Height = 0.23
  MapMode = 5
  Placement = pos=(-20.271,18.635,1.4056) rot=(-1,0,0;1.5708rad)
  Radius = 0.23
  Support = -> [XY_Plane187]
FEATURE [PartDesign::AdditiveBox] Box1535
  AttacherType = Attacher::AttachEngine3D
  AttachmentOffset = pos=(-20.1,18.635,1.635) rot=(0,0,1;0rad)
  BaseFeature = -> Cylinder311
  Height = 0.265
  Length = 0.23
  MapMode = 5
  Placement = pos=(-20.1,18.635,1.635) rot=(0,0,1;0rad)
  Support = -> [XY_Plane187]
  Width = 0.23
FEATURE [PartDesign::Body] Body171  label="pin171"
  Group = -> [Box1539,Box1544,Box1697,Box1542,Box1541,Fillet516,Fillet520,Box1720,Cylinder310,Box1551,Box1547,Fillet524,Box1546,Cylinder311,Box1535]
  Origin = -> Origin189
  Placement = pos=(0,-4,0) rot=(0,0,1;0rad)
  Tip = -> Box1535
FEATURE [PartDesign::Fillet] Fillet525
  Base = -> Box1681 [Edge28]
  BaseFeature = -> Box1681
  Placement = pos=(-21.15,18.635,0.297) rot=(0,-1,0;0.174533rad)
  Radius = 0.375
  SupportTransform = false
FEATURE [PartDesign::AdditiveBox] Box1676
  AttacherType = Attacher::AttachEngine3D
  AttachmentOffset = pos=(-20.7,18.635,1.55) rot=(0,1,0;0.785398rad)
  BaseFeature = -> Fillet525
  Height = 0.375
  Length = 0.23
  MapMode = 5
  Placement = pos=(-20.7,18.635,1.55) rot=(0,1,0;0.785398rad)
  Support = -> [XY_Plane191]
  Width = 0.23
FEATURE [PartDesign::SubtractiveCylinder] Cylinder339
  Angle = 360
  AttacherType = Attacher::AttachEngine3D
  AttachmentOffset = pos=(-20.271,18.635,1.4056) rot=(-1,0,0;1.5708rad)
  BaseFeature = -> Box1676
  Height = 0.23
  MapMode = 5
  Placement = pos=(-20.271,18.635,1.4056) rot=(-1,0,0;1.5708rad)
  Radius = 0.23
  Support = -> [XY_Plane191]
FEATURE [PartDesign::AdditiveBox] Box1680
  AttacherType = Attacher::AttachEngine3D
  AttachmentOffset = pos=(-20.1,18.635,1.635) rot=(0,0,1;0rad)
  BaseFeature = -> Cylinder339
  Height = 0.265
  Length = 0.23
  MapMode = 5
  Placement = pos=(-20.1,18.635,1.635) rot=(0,0,1;0rad)
  Support = -> [XY_Plane191]
  Width = 0.23
FEATURE [PartDesign::Body] Body172  label="pin172"
  Group = -> [Box1707,Box1695,Box1683,Box1674,Box1716,Fillet521,Fillet514,Box1673,Cylinder338,Box1670,Box1681,Fillet525,Box1676,Cylinder339,Box1680]
  Origin = -> Origin177
  Placement = pos=(0,-4.5,0) rot=(0,0,1;0rad)
  Tip = -> Box1680
FEATURE [PartDesign::Fillet] Fillet526
  Base = -> Box1690 [Edge28]
  BaseFeature = -> Box1690
  Placement = pos=(-21.15,18.635,0.297) rot=(0,-1,0;0.174533rad)
  Radius = 0.375
  SupportTransform = false
FEATURE [PartDesign::AdditiveBox] Box1717
  AttacherType = Attacher::AttachEngine3D
  AttachmentOffset = pos=(-20.7,18.635,1.55) rot=(0,1,0;0.785398rad)
  BaseFeature = -> Fillet526
  Height = 0.375
  Length = 0.23
  MapMode = 5
  Placement = pos=(-20.7,18.635,1.55) rot=(0,1,0;0.785398rad)
  Support = -> [XY_Plane186]
  Width = 0.23
FEATURE [PartDesign::SubtractiveCylinder] Cylinder347
  Angle = 360
  AttacherType = Attacher::AttachEngine3D
  AttachmentOffset = pos=(-20.271,18.635,1.4056) rot=(-1,0,0;1.5708rad)
  BaseFeature = -> Box1717
  Height = 0.23
  MapMode = 5
  Placement = pos=(-20.271,18.635,1.4056) rot=(-1,0,0;1.5708rad)
  Radius = 0.23
  Support = -> [XY_Plane186]
FEATURE [PartDesign::AdditiveBox] Box1731
  AttacherType = Attacher::AttachEngine3D
  AttachmentOffset = pos=(-20.1,18.635,1.635) rot=(0,0,1;0rad)
  BaseFeature = -> Cylinder347
  Height = 0.265
  Length = 0.23
  MapMode = 5
  Placement = pos=(-20.1,18.635,1.635) rot=(0,0,1;0rad)
  Support = -> [XY_Plane186]
  Width = 0.23
FEATURE [PartDesign::Body] Body168  label="pin168"
  Group = -> [Box1746,Box1749,Box1727,Box1722,Box1745,Fillet506,Fillet458,Box1553,Cylinder343,Box1702,Box1690,Fillet526,Box1717,Cylinder347,Box1731]
  Origin = -> Origin176
  Tip = -> Box1731
FEATURE [PartDesign::SubtractiveBox] Box1753
  AttacherType = Attacher::AttachEngine3D
  AttachmentOffset = pos=(-21.35,18.635,0.35) rot=(0,0,1;0rad)
  BaseFeature = -> Box1751
  Height = 1.55
  Length = 0.5
  MapMode = 5
  Placement = pos=(-21.35,18.635,0.35) rot=(0,0,1;0rad)
  Support = -> [XY_Plane203]
  Width = 0.23
FEATURE [PartDesign::AdditiveBox] Box1756
  AttacherType = Attacher::AttachEngine3D
  AttachmentOffset = pos=(-21.3,18.635,0) rot=(0,0,1;0rad)
  Height = 1.9
  Length = 1.3
  MapMode = 5
  Placement = pos=(-21.3,18.635,0) rot=(0,0,1;0rad)
  Support = -> [XY_Plane208]
  Width = 0.23
FEATURE [PartDesign::SubtractiveBox] Box1759
  AttacherType = Attacher::AttachEngine3D
  AttachmentOffset = pos=(-21.35,18.635,0.35) rot=(0,0,1;0rad)
  BaseFeature = -> Box1742
  Height = 1.55
  Length = 0.5
  MapMode = 5
  Placement = pos=(-21.35,18.635,0.35) rot=(0,0,1;0rad)
  Support = -> [XY_Plane205]
  Width = 0.23
FEATURE [PartDesign::SubtractiveBox] Box1764
  AttacherType = Attacher::AttachEngine3D
  AttachmentOffset = pos=(-21.35,18.635,0.35) rot=(0,0,1;0rad)
  BaseFeature = -> Box1756
  Height = 1.55
  Length = 0.5
  MapMode = 5
  Placement = pos=(-21.35,18.635,0.35) rot=(0,0,1;0rad)
  Support = -> [XY_Plane208]
  Width = 0.23
FEATURE [PartDesign::AdditiveBox] Box1767
  AttacherType = Attacher::AttachEngine3D
  AttachmentOffset = pos=(-21.3,18.635,0) rot=(0,0,1;0rad)
  Height = 1.9
  Length = 1.3
  MapMode = 5
  Placement = pos=(-21.3,18.635,0) rot=(0,0,1;0rad)
  Support = -> [XY_Plane201]
  Width = 0.23
FEATURE [PartDesign::SubtractiveBox] Box1778
  AttacherType = Attacher::AttachEngine3D
  AttachmentOffset = pos=(-21.35,18.635,0.35) rot=(0,0,1;0rad)
  BaseFeature = -> Box1767
  Height = 1.55
  Length = 0.5
  MapMode = 5
  Placement = pos=(-21.35,18.635,0.35) rot=(0,0,1;0rad)
  Support = -> [XY_Plane201]
  Width = 0.23
FEATURE [PartDesign::AdditiveBox] Box1789
  AttacherType = Attacher::AttachEngine3D
  AttachmentOffset = pos=(-21.3,18.635,0) rot=(0,0,1;0rad)
  Height = 1.9
  Length = 1.3
  MapMode = 5
  Placement = pos=(-21.3,18.635,0) rot=(0,0,1;0rad)
  Support = -> [XY_Plane198]
  Width = 0.23
FEATURE [PartDesign::SubtractiveBox] Box1783
  AttacherType = Attacher::AttachEngine3D
  AttachmentOffset = pos=(-21.35,18.635,0.35) rot=(0,0,1;0rad)
  BaseFeature = -> Box1789
  Height = 1.55
  Length = 0.5
  MapMode = 5
  Placement = pos=(-21.35,18.635,0.35) rot=(0,0,1;0rad)
  Support = -> [XY_Plane198]
  Width = 0.23
FEATURE [PartDesign::AdditiveBox] Box1791
  AttacherType = Attacher::AttachEngine3D
  AttachmentOffset = pos=(-21.3,18.635,0) rot=(0,0,1;0rad)
  Height = 1.9
  Length = 1.3
  MapMode = 5
  Placement = pos=(-21.3,18.635,0) rot=(0,0,1;0rad)
  Support = -> [XY_Plane197]
  Width = 0.23
FEATURE [PartDesign::SubtractiveBox] Box1769
  AttacherType = Attacher::AttachEngine3D
  AttachmentOffset = pos=(-21.35,18.635,0.35) rot=(0,0,1;0rad)
  BaseFeature = -> Box1791
  Height = 1.55
  Length = 0.5
  MapMode = 5
  Placement = pos=(-21.35,18.635,0.35) rot=(0,0,1;0rad)
  Support = -> [XY_Plane197]
  Width = 0.23
FEATURE [PartDesign::AdditiveBox] Box1797
  AttacherType = Attacher::AttachEngine3D
  AttachmentOffset = pos=(-21.3,18.635,0) rot=(0,0,1;0rad)
  Height = 1.9
  Length = 1.3
  MapMode = 5
  Placement = pos=(-21.3,18.635,0) rot=(0,0,1;0rad)
  Support = -> [XY_Plane204]
  Width = 0.23
FEATURE [PartDesign::SubtractiveBox] Box1802
  AttacherType = Attacher::AttachEngine3D
  AttachmentOffset = pos=(-20.5,18.63,0) rot=(0,0,1;0rad)
  BaseFeature = -> Box1753
  Height = 1.635
  Length = 0.5
  MapMode = 5
  Placement = pos=(-20.5,18.63,0) rot=(0,0,1;0rad)
  Support = -> [XY_Plane203]
  Width = 0.25
FEATURE [PartDesign::SubtractiveBox] Box1762
  AttacherType = Attacher::AttachEngine3D
  AttachmentOffset = pos=(-21.19,18.635,-0.12) rot=(0,-1,0;0.15708rad)
  BaseFeature = -> Box1802
  Height = 0.12
  Length = 0.725
  MapMode = 5
  Placement = pos=(-21.19,18.635,-0.12) rot=(0,-1,0;0.15708rad)
  Support = -> [XY_Plane203]
  Width = 0.25
FEATURE [PartDesign::SubtractiveBox] Box1763
  AttacherType = Attacher::AttachEngine3D
  AttachmentOffset = pos=(-21.5005,18.625,0.235) rot=(0,-1,0;0.174533rad)
  BaseFeature = -> Box1762
  Height = 0.3
  Length = 0.6605
  MapMode = 5
  Placement = pos=(-21.5005,18.625,0.235) rot=(0,-1,0;0.174533rad)
  Support = -> [XY_Plane203]
  Width = 0.25
FEATURE [PartDesign::Fillet] Fillet554
  Base = -> Box1763 [Edge2]
  BaseFeature = -> Box1763
  Placement = pos=(-21.5005,18.625,0.235) rot=(0,-1,0;0.174533rad)
  Radius = 0.05
  SupportTransform = false
FEATURE [PartDesign::Fillet] Fillet559
  Base = -> Fillet554 [Edge33]
  BaseFeature = -> Fillet554
  Placement = pos=(-21.5005,18.625,0.235) rot=(0,-1,0;0.174533rad)
  Radius = 0.5
  SupportTransform = false
FEATURE [PartDesign::SubtractiveBox] Box1803
  AttacherType = Attacher::AttachEngine3D
  AttachmentOffset = pos=(-21.35,18.635,0.35) rot=(0,0,1;0rad)
  BaseFeature = -> Box1797
  Height = 1.55
  Length = 0.5
  MapMode = 5
  Placement = pos=(-21.35,18.635,0.35) rot=(0,0,1;0rad)
  Support = -> [XY_Plane204]
  Width = 0.23
FEATURE [PartDesign::SubtractiveBox] Box1792
  AttacherType = Attacher::AttachEngine3D
  AttachmentOffset = pos=(-20.5,18.63,0) rot=(0,0,1;0rad)
  BaseFeature = -> Box1803
  Height = 1.635
  Length = 0.5
  MapMode = 5
  Placement = pos=(-20.5,18.63,0) rot=(0,0,1;0rad)
  Support = -> [XY_Plane204]
  Width = 0.25
FEATURE [PartDesign::SubtractiveBox] Box1800
  AttacherType = Attacher::AttachEngine3D
  AttachmentOffset = pos=(-21.19,18.635,-0.12) rot=(0,-1,0;0.15708rad)
  BaseFeature = -> Box1792
  Height = 0.12
  Length = 0.725
  MapMode = 5
  Placement = pos=(-21.19,18.635,-0.12) rot=(0,-1,0;0.15708rad)
  Support = -> [XY_Plane204]
  Width = 0.25
FEATURE [PartDesign::AdditiveBox] Box1810
  AttacherType = Attacher::AttachEngine3D
  AttachmentOffset = pos=(-21.3,18.635,0) rot=(0,0,1;0rad)
  Height = 1.9
  Length = 1.3
  MapMode = 5
  Placement = pos=(-21.3,18.635,0) rot=(0,0,1;0rad)
  Support = -> [XY_Plane206]
  Width = 0.23
FEATURE [PartDesign::SubtractiveBox] Box1805
  AttacherType = Attacher::AttachEngine3D
  AttachmentOffset = pos=(-21.35,18.635,0.35) rot=(0,0,1;0rad)
  BaseFeature = -> Box1810
  Height = 1.55
  Length = 0.5
  MapMode = 5
  Placement = pos=(-21.35,18.635,0.35) rot=(0,0,1;0rad)
  Support = -> [XY_Plane206]
  Width = 0.23
FEATURE [PartDesign::SubtractiveBox] Box1790
  AttacherType = Attacher::AttachEngine3D
  AttachmentOffset = pos=(-20.5,18.63,0) rot=(0,0,1;0rad)
  BaseFeature = -> Box1805
  Height = 1.635
  Length = 0.5
  MapMode = 5
  Placement = pos=(-20.5,18.63,0) rot=(0,0,1;0rad)
  Support = -> [XY_Plane206]
  Width = 0.25
FEATURE [PartDesign::SubtractiveBox] Box1784
  AttacherType = Attacher::AttachEngine3D
  AttachmentOffset = pos=(-21.19,18.635,-0.12) rot=(0,-1,0;0.15708rad)
  BaseFeature = -> Box1790
  Height = 0.12
  Length = 0.725
  MapMode = 5
  Placement = pos=(-21.19,18.635,-0.12) rot=(0,-1,0;0.15708rad)
  Support = -> [XY_Plane206]
  Width = 0.25
FEATURE [PartDesign::SubtractiveBox] Box1814
  AttacherType = Attacher::AttachEngine3D
  AttachmentOffset = pos=(-20.5,18.63,0) rot=(0,0,1;0rad)
  BaseFeature = -> Box1759
  Height = 1.635
  Length = 0.5
  MapMode = 5
  Placement = pos=(-20.5,18.63,0) rot=(0,0,1;0rad)
  Support = -> [XY_Plane205]
  Width = 0.25
FEATURE [PartDesign::SubtractiveBox] Box1815
  AttacherType = Attacher::AttachEngine3D
  AttachmentOffset = pos=(-21.5005,18.625,0.235) rot=(0,-1,0;0.174533rad)
  BaseFeature = -> Box1800
  Height = 0.3
  Length = 0.6605
  MapMode = 5
  Placement = pos=(-21.5005,18.625,0.235) rot=(0,-1,0;0.174533rad)
  Support = -> [XY_Plane204]
  Width = 0.25
FEATURE [PartDesign::Fillet] Fillet548
  Base = -> Box1815 [Edge2]
  BaseFeature = -> Box1815
  Placement = pos=(-21.5005,18.625,0.235) rot=(0,-1,0;0.174533rad)
  Radius = 0.05
  SupportTransform = false
FEATURE [PartDesign::Fillet] Fillet540
  Base = -> Fillet548 [Edge33]
  BaseFeature = -> Fillet548
  Placement = pos=(-21.5005,18.625,0.235) rot=(0,-1,0;0.174533rad)
  Radius = 0.5
  SupportTransform = false
FEATURE [PartDesign::AdditiveBox] Box1786
  AttacherType = Attacher::AttachEngine3D
  AttachmentOffset = pos=(-21.1,18.635,0.305) rot=(0,1,0;0.785398rad)
  BaseFeature = -> Fillet540
  Height = 0.375
  Length = 0.2
  MapMode = 5
  Placement = pos=(-21.1,18.635,0.305) rot=(0,1,0;0.785398rad)
  Support = -> [XY_Plane204]
  Width = 0.23
FEATURE [PartDesign::SubtractiveCylinder] Cylinder362
  Angle = 360
  AttacherType = Attacher::AttachEngine3D
  AttachmentOffset = pos=(-21.055,18.935,0.52) rot=(1,0,0;1.5708rad)
  BaseFeature = -> Box1786
  Height = 0.375
  MapMode = 5
  Placement = pos=(-21.055,18.935,0.52) rot=(1,0,0;1.5708rad)
  Radius = 0.205
  Support = -> [XY_Plane204]
FEATURE [PartDesign::SubtractiveBox] Box1813
  AttacherType = Attacher::AttachEngine3D
  AttachmentOffset = pos=(-20.95,18.635,0.53) rot=(0,0,1;0rad)
  BaseFeature = -> Cylinder362
  Height = 0.5
  Length = 0.1
  MapMode = 5
  Placement = pos=(-20.95,18.635,0.53) rot=(0,0,1;0rad)
  Support = -> [XY_Plane204]
  Width = 0.23
FEATURE [PartDesign::SubtractiveBox] Box1793
  AttacherType = Attacher::AttachEngine3D
  AttachmentOffset = pos=(-21.15,18.635,0.297) rot=(0,-1,0;0.174533rad)
  BaseFeature = -> Box1813
  Height = 0.115
  Length = 0.115
  MapMode = 5
  Placement = pos=(-21.15,18.635,0.297) rot=(0,-1,0;0.174533rad)
  Support = -> [XY_Plane204]
  Width = 0.23
FEATURE [PartDesign::Fillet] Fillet546
  Base = -> Box1793 [Edge28]
  BaseFeature = -> Box1793
  Placement = pos=(-21.15,18.635,0.297) rot=(0,-1,0;0.174533rad)
  Radius = 0.375
  SupportTransform = false
FEATURE [PartDesign::AdditiveBox] Box1799
  AttacherType = Attacher::AttachEngine3D
  AttachmentOffset = pos=(-20.7,18.635,1.55) rot=(0,1,0;0.785398rad)
  BaseFeature = -> Fillet546
  Height = 0.375
  Length = 0.23
  MapMode = 5
  Placement = pos=(-20.7,18.635,1.55) rot=(0,1,0;0.785398rad)
  Support = -> [XY_Plane204]
  Width = 0.23
FEATURE [PartDesign::SubtractiveCylinder] Cylinder363
  Angle = 360
  AttacherType = Attacher::AttachEngine3D
  AttachmentOffset = pos=(-20.271,18.635,1.4056) rot=(-1,0,0;1.5708rad)
  BaseFeature = -> Box1799
  Height = 0.23
  MapMode = 5
  Placement = pos=(-20.271,18.635,1.4056) rot=(-1,0,0;1.5708rad)
  Radius = 0.23
  Support = -> [XY_Plane204]
FEATURE [PartDesign::AdditiveBox] Box1808
  AttacherType = Attacher::AttachEngine3D
  AttachmentOffset = pos=(-20.1,18.635,1.635) rot=(0,0,1;0rad)
  BaseFeature = -> Cylinder363
  Height = 0.265
  Length = 0.23
  MapMode = 5
  Placement = pos=(-20.1,18.635,1.635) rot=(0,0,1;0rad)
  Support = -> [XY_Plane204]
  Width = 0.23
FEATURE [PartDesign::Body] Body186  label="pin186"
  Group = -> [Box1797,Box1803,Box1792,Box1800,Box1815,Fillet548,Fillet540,Box1786,Cylinder362,Box1813,Box1793,Fillet546,Box1799,Cylinder363,Box1808]
  Origin = -> Origin197
  Placement = pos=(0,-5,0) rot=(0,0,1;0rad)
  Tip = -> Box1808
FEATURE [PartDesign::AdditiveBox] Box1818
  AttacherType = Attacher::AttachEngine3D
  AttachmentOffset = pos=(-21.3,18.635,0) rot=(0,0,1;0rad)
  Height = 1.9
  Length = 1.3
  MapMode = 5
  Placement = pos=(-21.3,18.635,0) rot=(0,0,1;0rad)
  Support = -> [XY_Plane196]
  Width = 0.23
FEATURE [PartDesign::SubtractiveBox] Box1816
  AttacherType = Attacher::AttachEngine3D
  AttachmentOffset = pos=(-21.35,18.635,0.35) rot=(0,0,1;0rad)
  BaseFeature = -> Box1818
  Height = 1.55
  Length = 0.5
  MapMode = 5
  Placement = pos=(-21.35,18.635,0.35) rot=(0,0,1;0rad)
  Support = -> [XY_Plane196]
  Width = 0.23
FEATURE [PartDesign::SubtractiveBox] Box1774
  AttacherType = Attacher::AttachEngine3D
  AttachmentOffset = pos=(-20.5,18.63,0) rot=(0,0,1;0rad)
  BaseFeature = -> Box1816
  Height = 1.635
  Length = 0.5
  MapMode = 5
  Placement = pos=(-20.5,18.63,0) rot=(0,0,1;0rad)
  Support = -> [XY_Plane196]
  Width = 0.25
FEATURE [PartDesign::SubtractiveBox] Box1795
  AttacherType = Attacher::AttachEngine3D
  AttachmentOffset = pos=(-21.19,18.635,-0.12) rot=(0,-1,0;0.15708rad)
  BaseFeature = -> Box1774
  Height = 0.12
  Length = 0.725
  MapMode = 5
  Placement = pos=(-21.19,18.635,-0.12) rot=(0,-1,0;0.15708rad)
  Support = -> [XY_Plane196]
  Width = 0.25
FEATURE [PartDesign::SubtractiveBox] Box1787
  AttacherType = Attacher::AttachEngine3D
  AttachmentOffset = pos=(-21.5005,18.625,0.235) rot=(0,-1,0;0.174533rad)
  BaseFeature = -> Box1795
  Height = 0.3
  Length = 0.6605
  MapMode = 5
  Placement = pos=(-21.5005,18.625,0.235) rot=(0,-1,0;0.174533rad)
  Support = -> [XY_Plane196]
  Width = 0.25
FEATURE [PartDesign::Fillet] Fillet542
  Base = -> Box1787 [Edge2]
  BaseFeature = -> Box1787
  Placement = pos=(-21.5005,18.625,0.235) rot=(0,-1,0;0.174533rad)
  Radius = 0.05
  SupportTransform = false
FEATURE [PartDesign::Fillet] Fillet560
  Base = -> Fillet542 [Edge33]
  BaseFeature = -> Fillet542
  Placement = pos=(-21.5005,18.625,0.235) rot=(0,-1,0;0.174533rad)
  Radius = 0.5
  SupportTransform = false
FEATURE [PartDesign::AdditiveBox] Box1809
  AttacherType = Attacher::AttachEngine3D
  AttachmentOffset = pos=(-21.1,18.635,0.305) rot=(0,1,0;0.785398rad)
  BaseFeature = -> Fillet560
  Height = 0.375
  Length = 0.2
  MapMode = 5
  Placement = pos=(-21.1,18.635,0.305) rot=(0,1,0;0.785398rad)
  Support = -> [XY_Plane196]
  Width = 0.23
FEATURE [PartDesign::SubtractiveCylinder] Cylinder369
  Angle = 360
  AttacherType = Attacher::AttachEngine3D
  AttachmentOffset = pos=(-21.055,18.935,0.52) rot=(1,0,0;1.5708rad)
  BaseFeature = -> Box1809
  Height = 0.375
  MapMode = 5
  Placement = pos=(-21.055,18.935,0.52) rot=(1,0,0;1.5708rad)
  Radius = 0.205
  Support = -> [XY_Plane196]
FEATURE [PartDesign::SubtractiveBox] Box1806
  AttacherType = Attacher::AttachEngine3D
  AttachmentOffset = pos=(-20.95,18.635,0.53) rot=(0,0,1;0rad)
  BaseFeature = -> Cylinder369
  Height = 0.5
  Length = 0.1
  MapMode = 5
  Placement = pos=(-20.95,18.635,0.53) rot=(0,0,1;0rad)
  Support = -> [XY_Plane196]
  Width = 0.23
FEATURE [PartDesign::SubtractiveBox] Box1807
  AttacherType = Attacher::AttachEngine3D
  AttachmentOffset = pos=(-21.15,18.635,0.297) rot=(0,-1,0;0.174533rad)
  BaseFeature = -> Box1806
  Height = 0.115
  Length = 0.115
  MapMode = 5
  Placement = pos=(-21.15,18.635,0.297) rot=(0,-1,0;0.174533rad)
  Support = -> [XY_Plane196]
  Width = 0.23
FEATURE [PartDesign::Fillet] Fillet531
  Base = -> Box1807 [Edge28]
  BaseFeature = -> Box1807
  Placement = pos=(-21.15,18.635,0.297) rot=(0,-1,0;0.174533rad)
  Radius = 0.375
  SupportTransform = false
FEATURE [PartDesign::AdditiveBox] Box1812
  AttacherType = Attacher::AttachEngine3D
  AttachmentOffset = pos=(-20.7,18.635,1.55) rot=(0,1,0;0.785398rad)
  BaseFeature = -> Fillet531
  Height = 0.375
  Length = 0.23
  MapMode = 5
  Placement = pos=(-20.7,18.635,1.55) rot=(0,1,0;0.785398rad)
  Support = -> [XY_Plane196]
  Width = 0.23
FEATURE [PartDesign::SubtractiveCylinder] Cylinder364
  Angle = 360
  AttacherType = Attacher::AttachEngine3D
  AttachmentOffset = pos=(-20.271,18.635,1.4056) rot=(-1,0,0;1.5708rad)
  BaseFeature = -> Box1812
  Height = 0.23
  MapMode = 5
  Placement = pos=(-20.271,18.635,1.4056) rot=(-1,0,0;1.5708rad)
  Radius = 0.23
  Support = -> [XY_Plane196]
FEATURE [PartDesign::AdditiveBox] Box1804
  AttacherType = Attacher::AttachEngine3D
  AttachmentOffset = pos=(-20.1,18.635,1.635) rot=(0,0,1;0rad)
  BaseFeature = -> Cylinder364
  Height = 0.265
  Length = 0.23
  MapMode = 5
  Placement = pos=(-20.1,18.635,1.635) rot=(0,0,1;0rad)
  Support = -> [XY_Plane196]
  Width = 0.23
FEATURE [PartDesign::Body] Body188  label="pin188"
  Group = -> [Box1818,Box1816,Box1774,Box1795,Box1787,Fillet542,Fillet560,Box1809,Cylinder369,Box1806,Box1807,Fillet531,Box1812,Cylinder364,Box1804]
  Origin = -> Origin201
  Placement = pos=(0,-5.5,0) rot=(0,0,1;0rad)
  Tip = -> Box1804
FEATURE [PartDesign::SubtractiveBox] Box1821
  AttacherType = Attacher::AttachEngine3D
  AttachmentOffset = pos=(-21.19,18.635,-0.12) rot=(0,-1,0;0.15708rad)
  BaseFeature = -> Box1814
  Height = 0.12
  Length = 0.725
  MapMode = 5
  Placement = pos=(-21.19,18.635,-0.12) rot=(0,-1,0;0.15708rad)
  Support = -> [XY_Plane205]
  Width = 0.25
FEATURE [PartDesign::SubtractiveBox] Box1758
  AttacherType = Attacher::AttachEngine3D
  AttachmentOffset = pos=(-21.5005,18.625,0.235) rot=(0,-1,0;0.174533rad)
  BaseFeature = -> Box1821
  Height = 0.3
  Length = 0.6605
  MapMode = 5
  Placement = pos=(-21.5005,18.625,0.235) rot=(0,-1,0;0.174533rad)
  Support = -> [XY_Plane205]
  Width = 0.25
FEATURE [PartDesign::Fillet] Fillet561
  Base = -> Box1758 [Edge2]
  BaseFeature = -> Box1758
  Placement = pos=(-21.5005,18.625,0.235) rot=(0,-1,0;0.174533rad)
  Radius = 0.05
  SupportTransform = false
FEATURE [PartDesign::Fillet] Fillet553
  Base = -> Fillet561 [Edge33]
  BaseFeature = -> Fillet561
  Placement = pos=(-21.5005,18.625,0.235) rot=(0,-1,0;0.174533rad)
  Radius = 0.5
  SupportTransform = false
FEATURE [PartDesign::AdditiveBox] Box1794
  AttacherType = Attacher::AttachEngine3D
  AttachmentOffset = pos=(-21.1,18.635,0.305) rot=(0,1,0;0.785398rad)
  BaseFeature = -> Fillet553
  Height = 0.375
  Length = 0.2
  MapMode = 5
  Placement = pos=(-21.1,18.635,0.305) rot=(0,1,0;0.785398rad)
  Support = -> [XY_Plane205]
  Width = 0.23
FEATURE [PartDesign::SubtractiveCylinder] Cylinder367
  Angle = 360
  AttacherType = Attacher::AttachEngine3D
  AttachmentOffset = pos=(-21.055,18.935,0.52) rot=(1,0,0;1.5708rad)
  BaseFeature = -> Box1794
  Height = 0.375
  MapMode = 5
  Placement = pos=(-21.055,18.935,0.52) rot=(1,0,0;1.5708rad)
  Radius = 0.205
  Support = -> [XY_Plane205]
FEATURE [PartDesign::SubtractiveBox] Box1801
  AttacherType = Attacher::AttachEngine3D
  AttachmentOffset = pos=(-20.95,18.635,0.53) rot=(0,0,1;0rad)
  BaseFeature = -> Cylinder367
  Height = 0.5
  Length = 0.1
  MapMode = 5
  Placement = pos=(-20.95,18.635,0.53) rot=(0,0,1;0rad)
  Support = -> [XY_Plane205]
  Width = 0.23
FEATURE [PartDesign::SubtractiveBox] Box1819
  AttacherType = Attacher::AttachEngine3D
  AttachmentOffset = pos=(-21.15,18.635,0.297) rot=(0,-1,0;0.174533rad)
  BaseFeature = -> Box1801
  Height = 0.115
  Length = 0.115
  MapMode = 5
  Placement = pos=(-21.15,18.635,0.297) rot=(0,-1,0;0.174533rad)
  Support = -> [XY_Plane205]
  Width = 0.23
FEATURE [PartDesign::Fillet] Fillet555
  Base = -> Box1819 [Edge28]
  BaseFeature = -> Box1819
  Placement = pos=(-21.15,18.635,0.297) rot=(0,-1,0;0.174533rad)
  Radius = 0.375
  SupportTransform = false
FEATURE [PartDesign::AdditiveBox] Box1820
  AttacherType = Attacher::AttachEngine3D
  AttachmentOffset = pos=(-20.7,18.635,1.55) rot=(0,1,0;0.785398rad)
  BaseFeature = -> Fillet555
  Height = 0.375
  Length = 0.23
  MapMode = 5
  Placement = pos=(-20.7,18.635,1.55) rot=(0,1,0;0.785398rad)
  Support = -> [XY_Plane205]
  Width = 0.23
FEATURE [PartDesign::SubtractiveCylinder] Cylinder368
  Angle = 360
  AttacherType = Attacher::AttachEngine3D
  AttachmentOffset = pos=(-20.271,18.635,1.4056) rot=(-1,0,0;1.5708rad)
  BaseFeature = -> Box1820
  Height = 0.23
  MapMode = 5
  Placement = pos=(-20.271,18.635,1.4056) rot=(-1,0,0;1.5708rad)
  Radius = 0.23
  Support = -> [XY_Plane205]
FEATURE [PartDesign::AdditiveBox] Box1822
  AttacherType = Attacher::AttachEngine3D
  AttachmentOffset = pos=(-20.1,18.635,1.635) rot=(0,0,1;0rad)
  BaseFeature = -> Cylinder368
  Height = 0.265
  Length = 0.23
  MapMode = 5
  Placement = pos=(-20.1,18.635,1.635) rot=(0,0,1;0rad)
  Support = -> [XY_Plane205]
  Width = 0.23
FEATURE [PartDesign::Body] Body187  label="pin187"
  Group = -> [Box1742,Box1759,Box1814,Box1821,Box1758,Fillet561,Fillet553,Box1794,Cylinder367,Box1801,Box1819,Fillet555,Box1820,Cylinder368,Box1822]
  Origin = -> Origin184
  Placement = pos=(0,-3,0) rot=(0,0,1;0rad)
  Tip = -> Box1822
FEATURE [PartDesign::SubtractiveBox] Box1826
  AttacherType = Attacher::AttachEngine3D
  AttachmentOffset = pos=(-21.5005,18.625,0.235) rot=(0,-1,0;0.174533rad)
  BaseFeature = -> Box1784
  Height = 0.3
  Length = 0.6605
  MapMode = 5
  Placement = pos=(-21.5005,18.625,0.235) rot=(0,-1,0;0.174533rad)
  Support = -> [XY_Plane206]
  Width = 0.25
FEATURE [PartDesign::Fillet] Fillet562
  Base = -> Box1826 [Edge2]
  BaseFeature = -> Box1826
  Placement = pos=(-21.5005,18.625,0.235) rot=(0,-1,0;0.174533rad)
  Radius = 0.05
  SupportTransform = false
FEATURE [PartDesign::Fillet] Fillet541
  Base = -> Fillet562 [Edge33]
  BaseFeature = -> Fillet562
  Placement = pos=(-21.5005,18.625,0.235) rot=(0,-1,0;0.174533rad)
  Radius = 0.5
  SupportTransform = false
FEATURE [PartDesign::AdditiveBox] Box1771
  AttacherType = Attacher::AttachEngine3D
  AttachmentOffset = pos=(-21.1,18.635,0.305) rot=(0,1,0;0.785398rad)
  BaseFeature = -> Fillet541
  Height = 0.375
  Length = 0.2
  MapMode = 5
  Placement = pos=(-21.1,18.635,0.305) rot=(0,1,0;0.785398rad)
  Support = -> [XY_Plane206]
  Width = 0.23
FEATURE [PartDesign::SubtractiveCylinder] Cylinder360
  Angle = 360
  AttacherType = Attacher::AttachEngine3D
  AttachmentOffset = pos=(-21.055,18.935,0.52) rot=(1,0,0;1.5708rad)
  BaseFeature = -> Box1771
  Height = 0.375
  MapMode = 5
  Placement = pos=(-21.055,18.935,0.52) rot=(1,0,0;1.5708rad)
  Radius = 0.205
  Support = -> [XY_Plane206]
FEATURE [PartDesign::SubtractiveBox] Box1770
  AttacherType = Attacher::AttachEngine3D
  AttachmentOffset = pos=(-20.95,18.635,0.53) rot=(0,0,1;0rad)
  BaseFeature = -> Cylinder360
  Height = 0.5
  Length = 0.1
  MapMode = 5
  Placement = pos=(-20.95,18.635,0.53) rot=(0,0,1;0rad)
  Support = -> [XY_Plane206]
  Width = 0.23
FEATURE [PartDesign::SubtractiveBox] Box1798
  AttacherType = Attacher::AttachEngine3D
  AttachmentOffset = pos=(-21.15,18.635,0.297) rot=(0,-1,0;0.174533rad)
  BaseFeature = -> Box1770
  Height = 0.115
  Length = 0.115
  MapMode = 5
  Placement = pos=(-21.15,18.635,0.297) rot=(0,-1,0;0.174533rad)
  Support = -> [XY_Plane206]
  Width = 0.23
FEATURE [PartDesign::Fillet] Fillet558
  Base = -> Box1798 [Edge28]
  BaseFeature = -> Box1798
  Placement = pos=(-21.15,18.635,0.297) rot=(0,-1,0;0.174533rad)
  Radius = 0.375
  SupportTransform = false
FEATURE [PartDesign::AdditiveBox] Box1785
  AttacherType = Attacher::AttachEngine3D
  AttachmentOffset = pos=(-20.7,18.635,1.55) rot=(0,1,0;0.785398rad)
  BaseFeature = -> Fillet558
  Height = 0.375
  Length = 0.23
  MapMode = 5
  Placement = pos=(-20.7,18.635,1.55) rot=(0,1,0;0.785398rad)
  Support = -> [XY_Plane206]
  Width = 0.23
FEATURE [PartDesign::SubtractiveCylinder] Cylinder361
  Angle = 360
  AttacherType = Attacher::AttachEngine3D
  AttachmentOffset = pos=(-20.271,18.635,1.4056) rot=(-1,0,0;1.5708rad)
  BaseFeature = -> Box1785
  Height = 0.23
  MapMode = 5
  Placement = pos=(-20.271,18.635,1.4056) rot=(-1,0,0;1.5708rad)
  Radius = 0.23
  Support = -> [XY_Plane206]
FEATURE [PartDesign::AdditiveBox] Box1788
  AttacherType = Attacher::AttachEngine3D
  AttachmentOffset = pos=(-20.1,18.635,1.635) rot=(0,0,1;0rad)
  BaseFeature = -> Cylinder361
  Height = 0.265
  Length = 0.23
  MapMode = 5
  Placement = pos=(-20.1,18.635,1.635) rot=(0,0,1;0rad)
  Support = -> [XY_Plane206]
  Width = 0.23
FEATURE [PartDesign::Body] Body183  label="pin183"
  Group = -> [Box1810,Box1805,Box1790,Box1784,Box1826,Fillet562,Fillet541,Box1771,Cylinder360,Box1770,Box1798,Fillet558,Box1785,Cylinder361,Box1788]
  Origin = -> Origin191
  Placement = pos=(0,-4.5,0) rot=(0,0,1;0rad)
  Tip = -> Box1788
FEATURE [PartDesign::SubtractiveBox] Box1829
  AttacherType = Attacher::AttachEngine3D
  AttachmentOffset = pos=(-20.5,18.63,0) rot=(0,0,1;0rad)
  BaseFeature = -> Box1764
  Height = 1.635
  Length = 0.5
  MapMode = 5
  Placement = pos=(-20.5,18.63,0) rot=(0,0,1;0rad)
  Support = -> [XY_Plane208]
  Width = 0.25
FEATURE [PartDesign::SubtractiveBox] Box1765
  AttacherType = Attacher::AttachEngine3D
  AttachmentOffset = pos=(-21.19,18.635,-0.12) rot=(0,-1,0;0.15708rad)
  BaseFeature = -> Box1829
  Height = 0.12
  Length = 0.725
  MapMode = 5
  Placement = pos=(-21.19,18.635,-0.12) rot=(0,-1,0;0.15708rad)
  Support = -> [XY_Plane208]
  Width = 0.25
FEATURE [PartDesign::SubtractiveBox] Box1750
  AttacherType = Attacher::AttachEngine3D
  AttachmentOffset = pos=(-21.5005,18.625,0.235) rot=(0,-1,0;0.174533rad)
  BaseFeature = -> Box1765
  Height = 0.3
  Length = 0.6605
  MapMode = 5
  Placement = pos=(-21.5005,18.625,0.235) rot=(0,-1,0;0.174533rad)
  Support = -> [XY_Plane208]
  Width = 0.25
FEATURE [PartDesign::Fillet] Fillet551
  Base = -> Box1750 [Edge2]
  BaseFeature = -> Box1750
  Placement = pos=(-21.5005,18.625,0.235) rot=(0,-1,0;0.174533rad)
  Radius = 0.05
  SupportTransform = false
FEATURE [PartDesign::Fillet] Fillet543
  Base = -> Fillet551 [Edge33]
  BaseFeature = -> Fillet551
  Placement = pos=(-21.5005,18.625,0.235) rot=(0,-1,0;0.174533rad)
  Radius = 0.5
  SupportTransform = false
FEATURE [PartDesign::AdditiveBox] Box1830
  AttacherType = Attacher::AttachEngine3D
  AttachmentOffset = pos=(-21.1,18.635,0.305) rot=(0,1,0;0.785398rad)
  BaseFeature = -> Fillet559
  Height = 0.375
  Length = 0.2
  MapMode = 5
  Placement = pos=(-21.1,18.635,0.305) rot=(0,1,0;0.785398rad)
  Support = -> [XY_Plane203]
  Width = 0.23
FEATURE [PartDesign::SubtractiveCylinder] Cylinder354
  Angle = 360
  AttacherType = Attacher::AttachEngine3D
  AttachmentOffset = pos=(-21.055,18.935,0.52) rot=(1,0,0;1.5708rad)
  BaseFeature = -> Box1830
  Height = 0.375
  MapMode = 5
  Placement = pos=(-21.055,18.935,0.52) rot=(1,0,0;1.5708rad)
  Radius = 0.205
  Support = -> [XY_Plane203]
FEATURE [PartDesign::SubtractiveBox] Box1761
  AttacherType = Attacher::AttachEngine3D
  AttachmentOffset = pos=(-20.95,18.635,0.53) rot=(0,0,1;0rad)
  BaseFeature = -> Cylinder354
  Height = 0.5
  Length = 0.1
  MapMode = 5
  Placement = pos=(-20.95,18.635,0.53) rot=(0,0,1;0rad)
  Support = -> [XY_Plane203]
  Width = 0.23
FEATURE [PartDesign::SubtractiveBox] Box1754
  AttacherType = Attacher::AttachEngine3D
  AttachmentOffset = pos=(-21.15,18.635,0.297) rot=(0,-1,0;0.174533rad)
  BaseFeature = -> Box1761
  Height = 0.115
  Length = 0.115
  MapMode = 5
  Placement = pos=(-21.15,18.635,0.297) rot=(0,-1,0;0.174533rad)
  Support = -> [XY_Plane203]
  Width = 0.23
FEATURE [PartDesign::Fillet] Fillet557
  Base = -> Box1754 [Edge28]
  BaseFeature = -> Box1754
  Placement = pos=(-21.15,18.635,0.297) rot=(0,-1,0;0.174533rad)
  Radius = 0.375
  SupportTransform = false
FEATURE [PartDesign::AdditiveBox] Box1757
  AttacherType = Attacher::AttachEngine3D
  AttachmentOffset = pos=(-20.7,18.635,1.55) rot=(0,1,0;0.785398rad)
  BaseFeature = -> Fillet557
  Height = 0.375
  Length = 0.23
  MapMode = 5
  Placement = pos=(-20.7,18.635,1.55) rot=(0,1,0;0.785398rad)
  Support = -> [XY_Plane203]
  Width = 0.23
FEATURE [PartDesign::SubtractiveCylinder] Cylinder355
  Angle = 360
  AttacherType = Attacher::AttachEngine3D
  AttachmentOffset = pos=(-20.271,18.635,1.4056) rot=(-1,0,0;1.5708rad)
  BaseFeature = -> Box1757
  Height = 0.23
  MapMode = 5
  Placement = pos=(-20.271,18.635,1.4056) rot=(-1,0,0;1.5708rad)
  Radius = 0.23
  Support = -> [XY_Plane203]
FEATURE [PartDesign::AdditiveBox] Box1738
  AttacherType = Attacher::AttachEngine3D
  AttachmentOffset = pos=(-20.1,18.635,1.635) rot=(0,0,1;0rad)
  BaseFeature = -> Cylinder355
  Height = 0.265
  Length = 0.23
  MapMode = 5
  Placement = pos=(-20.1,18.635,1.635) rot=(0,0,1;0rad)
  Support = -> [XY_Plane203]
  Width = 0.23
FEATURE [PartDesign::Body] Body184  label="pin184"
  Group = -> [Box1751,Box1753,Box1802,Box1762,Box1763,Fillet554,Fillet559,Box1830,Cylinder354,Box1761,Box1754,Fillet557,Box1757,Cylinder355,Box1738]
  Origin = -> Origin199
  Placement = pos=(0,-4,0) rot=(0,0,1;0rad)
  Tip = -> Box1738
FEATURE [PartDesign::AdditiveBox] Box1833
  AttacherType = Attacher::AttachEngine3D
  AttachmentOffset = pos=(-21.1,18.635,0.305) rot=(0,1,0;0.785398rad)
  BaseFeature = -> Fillet543
  Height = 0.375
  Length = 0.2
  MapMode = 5
  Placement = pos=(-21.1,18.635,0.305) rot=(0,1,0;0.785398rad)
  Support = -> [XY_Plane208]
  Width = 0.23
FEATURE [PartDesign::SubtractiveCylinder] Cylinder370
  Angle = 360
  AttacherType = Attacher::AttachEngine3D
  AttachmentOffset = pos=(-21.055,18.935,0.52) rot=(1,0,0;1.5708rad)
  BaseFeature = -> Box1833
  Height = 0.375
  MapMode = 5
  Placement = pos=(-21.055,18.935,0.52) rot=(1,0,0;1.5708rad)
  Radius = 0.205
  Support = -> [XY_Plane208]
FEATURE [PartDesign::SubtractiveBox] Box1832
  AttacherType = Attacher::AttachEngine3D
  AttachmentOffset = pos=(-20.95,18.635,0.53) rot=(0,0,1;0rad)
  BaseFeature = -> Cylinder370
  Height = 0.5
  Length = 0.1
  MapMode = 5
  Placement = pos=(-20.95,18.635,0.53) rot=(0,0,1;0rad)
  Support = -> [XY_Plane208]
  Width = 0.23
FEATURE [PartDesign::SubtractiveBox] Box1817
  AttacherType = Attacher::AttachEngine3D
  AttachmentOffset = pos=(-21.15,18.635,0.297) rot=(0,-1,0;0.174533rad)
  BaseFeature = -> Box1832
  Height = 0.115
  Length = 0.115
  MapMode = 5
  Placement = pos=(-21.15,18.635,0.297) rot=(0,-1,0;0.174533rad)
  Support = -> [XY_Plane208]
  Width = 0.23
FEATURE [PartDesign::Fillet] Fillet547
  Base = -> Box1817 [Edge28]
  BaseFeature = -> Box1817
  Placement = pos=(-21.15,18.635,0.297) rot=(0,-1,0;0.174533rad)
  Radius = 0.375
  SupportTransform = false
FEATURE [PartDesign::AdditiveBox] Box1827
  AttacherType = Attacher::AttachEngine3D
  AttachmentOffset = pos=(-20.7,18.635,1.55) rot=(0,1,0;0.785398rad)
  BaseFeature = -> Fillet547
  Height = 0.375
  Length = 0.23
  MapMode = 5
  Placement = pos=(-20.7,18.635,1.55) rot=(0,1,0;0.785398rad)
  Support = -> [XY_Plane208]
  Width = 0.23
FEATURE [PartDesign::SubtractiveCylinder] Cylinder371
  Angle = 360
  AttacherType = Attacher::AttachEngine3D
  AttachmentOffset = pos=(-20.271,18.635,1.4056) rot=(-1,0,0;1.5708rad)
  BaseFeature = -> Box1827
  Height = 0.23
  MapMode = 5
  Placement = pos=(-20.271,18.635,1.4056) rot=(-1,0,0;1.5708rad)
  Radius = 0.23
  Support = -> [XY_Plane208]
FEATURE [PartDesign::AdditiveBox] Box1752
  AttacherType = Attacher::AttachEngine3D
  AttachmentOffset = pos=(-20.1,18.635,1.635) rot=(0,0,1;0rad)
  BaseFeature = -> Cylinder371
  Height = 0.265
  Length = 0.23
  MapMode = 5
  Placement = pos=(-20.1,18.635,1.635) rot=(0,0,1;0rad)
  Support = -> [XY_Plane208]
  Width = 0.23
FEATURE [PartDesign::Body] Body182  label="pin182"
  Group = -> [Box1756,Box1764,Box1829,Box1765,Box1750,Fillet551,Fillet543,Box1833,Cylinder370,Box1832,Box1817,Fillet547,Box1827,Cylinder371,Box1752]
  Origin = -> Origin205
  Placement = pos=(0,-3.5,0) rot=(0,0,1;0rad)
  Tip = -> Box1752
FEATURE [PartDesign::AdditiveBox] Box1842
  AttacherType = Attacher::AttachEngine3D
  AttachmentOffset = pos=(-21.3,18.635,0) rot=(0,0,1;0rad)
  Height = 1.9
  Length = 1.3
  MapMode = 5
  Placement = pos=(-21.3,18.635,0) rot=(0,0,1;0rad)
  Support = -> [XY_Plane202]
  Width = 0.23
FEATURE [PartDesign::SubtractiveBox] Box1835
  AttacherType = Attacher::AttachEngine3D
  AttachmentOffset = pos=(-21.35,18.635,0.35) rot=(0,0,1;0rad)
  BaseFeature = -> Box1842
  Height = 1.55
  Length = 0.5
  MapMode = 5
  Placement = pos=(-21.35,18.635,0.35) rot=(0,0,1;0rad)
  Support = -> [XY_Plane202]
  Width = 0.23
FEATURE [PartDesign::SubtractiveBox] Box1825
  AttacherType = Attacher::AttachEngine3D
  AttachmentOffset = pos=(-20.5,18.63,0) rot=(0,0,1;0rad)
  BaseFeature = -> Box1835
  Height = 1.635
  Length = 0.5
  MapMode = 5
  Placement = pos=(-20.5,18.63,0) rot=(0,0,1;0rad)
  Support = -> [XY_Plane202]
  Width = 0.25
FEATURE [PartDesign::SubtractiveBox] Box1839
  AttacherType = Attacher::AttachEngine3D
  AttachmentOffset = pos=(-21.19,18.635,-0.12) rot=(0,-1,0;0.15708rad)
  BaseFeature = -> Box1825
  Height = 0.12
  Length = 0.725
  MapMode = 5
  Placement = pos=(-21.19,18.635,-0.12) rot=(0,-1,0;0.15708rad)
  Support = -> [XY_Plane202]
  Width = 0.25
FEATURE [PartDesign::SubtractiveBox] Box1840
  AttacherType = Attacher::AttachEngine3D
  AttachmentOffset = pos=(-21.5005,18.625,0.235) rot=(0,-1,0;0.174533rad)
  BaseFeature = -> Box1839
  Height = 0.3
  Length = 0.6605
  MapMode = 5
  Placement = pos=(-21.5005,18.625,0.235) rot=(0,-1,0;0.174533rad)
  Support = -> [XY_Plane202]
  Width = 0.25
FEATURE [PartDesign::Fillet] Fillet533
  Base = -> Box1840 [Edge2]
  BaseFeature = -> Box1840
  Placement = pos=(-21.5005,18.625,0.235) rot=(0,-1,0;0.174533rad)
  Radius = 0.05
  SupportTransform = false
FEATURE [PartDesign::Fillet] Fillet534
  Base = -> Fillet533 [Edge33]
  BaseFeature = -> Fillet533
  Placement = pos=(-21.5005,18.625,0.235) rot=(0,-1,0;0.174533rad)
  Radius = 0.5
  SupportTransform = false
FEATURE [PartDesign::AdditiveBox] Box1824
  AttacherType = Attacher::AttachEngine3D
  AttachmentOffset = pos=(-21.1,18.635,0.305) rot=(0,1,0;0.785398rad)
  BaseFeature = -> Fillet534
  Height = 0.375
  Length = 0.2
  MapMode = 5
  Placement = pos=(-21.1,18.635,0.305) rot=(0,1,0;0.785398rad)
  Support = -> [XY_Plane202]
  Width = 0.23
FEATURE [PartDesign::SubtractiveCylinder] Cylinder372
  Angle = 360
  AttacherType = Attacher::AttachEngine3D
  AttachmentOffset = pos=(-21.055,18.935,0.52) rot=(1,0,0;1.5708rad)
  BaseFeature = -> Box1824
  Height = 0.375
  MapMode = 5
  Placement = pos=(-21.055,18.935,0.52) rot=(1,0,0;1.5708rad)
  Radius = 0.205
  Support = -> [XY_Plane202]
FEATURE [PartDesign::SubtractiveBox] Box1846
  AttacherType = Attacher::AttachEngine3D
  AttachmentOffset = pos=(-20.95,18.635,0.53) rot=(0,0,1;0rad)
  BaseFeature = -> Cylinder372
  Height = 0.5
  Length = 0.1
  MapMode = 5
  Placement = pos=(-20.95,18.635,0.53) rot=(0,0,1;0rad)
  Support = -> [XY_Plane202]
  Width = 0.23
FEATURE [PartDesign::SubtractiveBox] Box1838
  AttacherType = Attacher::AttachEngine3D
  AttachmentOffset = pos=(-21.15,18.635,0.297) rot=(0,-1,0;0.174533rad)
  BaseFeature = -> Box1846
  Height = 0.115
  Length = 0.115
  MapMode = 5
  Placement = pos=(-21.15,18.635,0.297) rot=(0,-1,0;0.174533rad)
  Support = -> [XY_Plane202]
  Width = 0.23
FEATURE [PartDesign::Fillet] Fillet549
  Base = -> Box1838 [Edge28]
  BaseFeature = -> Box1838
  Placement = pos=(-21.15,18.635,0.297) rot=(0,-1,0;0.174533rad)
  Radius = 0.375
  SupportTransform = false
FEATURE [PartDesign::AdditiveBox] Box1837
  AttacherType = Attacher::AttachEngine3D
  AttachmentOffset = pos=(-20.7,18.635,1.55) rot=(0,1,0;0.785398rad)
  BaseFeature = -> Fillet549
  Height = 0.375
  Length = 0.23
  MapMode = 5
  Placement = pos=(-20.7,18.635,1.55) rot=(0,1,0;0.785398rad)
  Support = -> [XY_Plane202]
  Width = 0.23
FEATURE [PartDesign::SubtractiveCylinder] Cylinder373
  Angle = 360
  AttacherType = Attacher::AttachEngine3D
  AttachmentOffset = pos=(-20.271,18.635,1.4056) rot=(-1,0,0;1.5708rad)
  BaseFeature = -> Box1837
  Height = 0.23
  MapMode = 5
  Placement = pos=(-20.271,18.635,1.4056) rot=(-1,0,0;1.5708rad)
  Radius = 0.23
  Support = -> [XY_Plane202]
FEATURE [PartDesign::AdditiveBox] Box1843
  AttacherType = Attacher::AttachEngine3D
  AttachmentOffset = pos=(-20.1,18.635,1.635) rot=(0,0,1;0rad)
  BaseFeature = -> Cylinder373
  Height = 0.265
  Length = 0.23
  MapMode = 5
  Placement = pos=(-20.1,18.635,1.635) rot=(0,0,1;0rad)
  Support = -> [XY_Plane202]
  Width = 0.23
FEATURE [PartDesign::Body] Body177  label="pin177"
  Group = -> [Box1842,Box1835,Box1825,Box1839,Box1840,Fillet533,Fillet534,Box1824,Cylinder372,Box1846,Box1838,Fillet549,Box1837,Cylinder373,Box1843]
  Origin = -> Origin194
  Placement = pos=(0,-0.5,0) rot=(0,0,1;0rad)
  Tip = -> Box1843
FEATURE [PartDesign::AdditiveBox] Box1866
  AttacherType = Attacher::AttachEngine3D
  AttachmentOffset = pos=(-21.3,18.635,0) rot=(0,0,1;0rad)
  Height = 1.9
  Length = 1.3
  MapMode = 5
  Placement = pos=(-21.3,18.635,0) rot=(0,0,1;0rad)
  Support = -> [XY_Plane181]
  Width = 0.23
FEATURE [PartDesign::SubtractiveBox] Box1851
  AttacherType = Attacher::AttachEngine3D
  AttachmentOffset = pos=(-21.35,18.635,0.35) rot=(0,0,1;0rad)
  BaseFeature = -> Box1866
  Height = 1.55
  Length = 0.5
  MapMode = 5
  Placement = pos=(-21.35,18.635,0.35) rot=(0,0,1;0rad)
  Support = -> [XY_Plane181]
  Width = 0.23
FEATURE [PartDesign::AdditiveBox] Box1870
  AttacherType = Attacher::AttachEngine3D
  AttachmentOffset = pos=(-21.3,18.635,0) rot=(0,0,1;0rad)
  Height = 1.9
  Length = 1.3
  MapMode = 5
  Placement = pos=(-21.3,18.635,0) rot=(0,0,1;0rad)
  Support = -> [XY_Plane195]
  Width = 0.23
FEATURE [PartDesign::SubtractiveBox] Box1853
  AttacherType = Attacher::AttachEngine3D
  AttachmentOffset = pos=(-21.35,18.635,0.35) rot=(0,0,1;0rad)
  BaseFeature = -> Box1870
  Height = 1.55
  Length = 0.5
  MapMode = 5
  Placement = pos=(-21.35,18.635,0.35) rot=(0,0,1;0rad)
  Support = -> [XY_Plane195]
  Width = 0.23
FEATURE [PartDesign::AdditiveBox] Box1877
  AttacherType = Attacher::AttachEngine3D
  AttachmentOffset = pos=(-21.3,18.635,0) rot=(0,0,1;0rad)
  Height = 1.9
  Length = 1.3
  MapMode = 5
  Placement = pos=(-21.3,18.635,0) rot=(0,0,1;0rad)
  Support = -> [XY_Plane216]
  Width = 0.23
FEATURE [PartDesign::SubtractiveBox] Box1885
  AttacherType = Attacher::AttachEngine3D
  AttachmentOffset = pos=(-21.35,18.635,0.35) rot=(0,0,1;0rad)
  BaseFeature = -> Box1877
  Height = 1.55
  Length = 0.5
  MapMode = 5
  Placement = pos=(-21.35,18.635,0.35) rot=(0,0,1;0rad)
  Support = -> [XY_Plane216]
  Width = 0.23
FEATURE [PartDesign::SubtractiveBox] Box1875
  AttacherType = Attacher::AttachEngine3D
  AttachmentOffset = pos=(-20.5,18.63,0) rot=(0,0,1;0rad)
  BaseFeature = -> Box1885
  Height = 1.635
  Length = 0.5
  MapMode = 5
  Placement = pos=(-20.5,18.63,0) rot=(0,0,1;0rad)
  Support = -> [XY_Plane216]
  Width = 0.25
FEATURE [PartDesign::SubtractiveBox] Box1879
  AttacherType = Attacher::AttachEngine3D
  AttachmentOffset = pos=(-21.19,18.635,-0.12) rot=(0,-1,0;0.15708rad)
  BaseFeature = -> Box1875
  Height = 0.12
  Length = 0.725
  MapMode = 5
  Placement = pos=(-21.19,18.635,-0.12) rot=(0,-1,0;0.15708rad)
  Support = -> [XY_Plane216]
  Width = 0.25
FEATURE [PartDesign::SubtractiveBox] Box1884
  AttacherType = Attacher::AttachEngine3D
  AttachmentOffset = pos=(-21.5005,18.625,0.235) rot=(0,-1,0;0.174533rad)
  BaseFeature = -> Box1879
  Height = 0.3
  Length = 0.6605
  MapMode = 5
  Placement = pos=(-21.5005,18.625,0.235) rot=(0,-1,0;0.174533rad)
  Support = -> [XY_Plane216]
  Width = 0.25
FEATURE [PartDesign::AdditiveBox] Box1891
  AttacherType = Attacher::AttachEngine3D
  AttachmentOffset = pos=(-21.3,18.635,0) rot=(0,0,1;0rad)
  Height = 1.9
  Length = 1.3
  MapMode = 5
  Placement = pos=(-21.3,18.635,0) rot=(0,0,1;0rad)
  Support = -> [XY_Plane213]
  Width = 0.23
FEATURE [PartDesign::SubtractiveBox] Box1883
  AttacherType = Attacher::AttachEngine3D
  AttachmentOffset = pos=(-21.35,18.635,0.35) rot=(0,0,1;0rad)
  BaseFeature = -> Box1891
  Height = 1.55
  Length = 0.5
  MapMode = 5
  Placement = pos=(-21.35,18.635,0.35) rot=(0,0,1;0rad)
  Support = -> [XY_Plane213]
  Width = 0.23
FEATURE [PartDesign::SubtractiveBox] Box1871
  AttacherType = Attacher::AttachEngine3D
  AttachmentOffset = pos=(-20.5,18.63,0) rot=(0,0,1;0rad)
  BaseFeature = -> Box1883
  Height = 1.635
  Length = 0.5
  MapMode = 5
  Placement = pos=(-20.5,18.63,0) rot=(0,0,1;0rad)
  Support = -> [XY_Plane213]
  Width = 0.25
FEATURE [PartDesign::SubtractiveBox] Box1873
  AttacherType = Attacher::AttachEngine3D
  AttachmentOffset = pos=(-21.19,18.635,-0.12) rot=(0,-1,0;0.15708rad)
  BaseFeature = -> Box1871
  Height = 0.12
  Length = 0.725
  MapMode = 5
  Placement = pos=(-21.19,18.635,-0.12) rot=(0,-1,0;0.15708rad)
  Support = -> [XY_Plane213]
  Width = 0.25
FEATURE [PartDesign::AdditiveBox] Box1895
  AttacherType = Attacher::AttachEngine3D
  AttachmentOffset = pos=(-21.3,18.635,0) rot=(0,0,1;0rad)
  Height = 1.9
  Length = 1.3
  MapMode = 5
  Placement = pos=(-21.3,18.635,0) rot=(0,0,1;0rad)
  Support = -> [XY_Plane194]
  Width = 0.23
FEATURE [PartDesign::SubtractiveBox] Box1896
  AttacherType = Attacher::AttachEngine3D
  AttachmentOffset = pos=(-21.35,18.635,0.35) rot=(0,0,1;0rad)
  BaseFeature = -> Box1895
  Height = 1.55
  Length = 0.5
  MapMode = 5
  Placement = pos=(-21.35,18.635,0.35) rot=(0,0,1;0rad)
  Support = -> [XY_Plane194]
  Width = 0.23
FEATURE [PartDesign::SubtractiveBox] Box1854
  AttacherType = Attacher::AttachEngine3D
  AttachmentOffset = pos=(-20.5,18.63,0) rot=(0,0,1;0rad)
  BaseFeature = -> Box1896
  Height = 1.635
  Length = 0.5
  MapMode = 5
  Placement = pos=(-20.5,18.63,0) rot=(0,0,1;0rad)
  Support = -> [XY_Plane194]
  Width = 0.25
FEATURE [PartDesign::SubtractiveBox] Box1865
  AttacherType = Attacher::AttachEngine3D
  AttachmentOffset = pos=(-21.19,18.635,-0.12) rot=(0,-1,0;0.15708rad)
  BaseFeature = -> Box1854
  Height = 0.12
  Length = 0.725
  MapMode = 5
  Placement = pos=(-21.19,18.635,-0.12) rot=(0,-1,0;0.15708rad)
  Support = -> [XY_Plane194]
  Width = 0.25
FEATURE [PartDesign::SubtractiveBox] Box1864
  AttacherType = Attacher::AttachEngine3D
  AttachmentOffset = pos=(-21.5005,18.625,0.235) rot=(0,-1,0;0.174533rad)
  BaseFeature = -> Box1865
  Height = 0.3
  Length = 0.6605
  MapMode = 5
  Placement = pos=(-21.5005,18.625,0.235) rot=(0,-1,0;0.174533rad)
  Support = -> [XY_Plane194]
  Width = 0.25
FEATURE [PartDesign::SubtractiveBox] Box1908
  AttacherType = Attacher::AttachEngine3D
  AttachmentOffset = pos=(-20.5,18.63,0) rot=(0,0,1;0rad)
  BaseFeature = -> Box1778
  Height = 1.635
  Length = 0.5
  MapMode = 5
  Placement = pos=(-20.5,18.63,0) rot=(0,0,1;0rad)
  Support = -> [XY_Plane201]
  Width = 0.25
FEATURE [PartDesign::SubtractiveBox] Box1776
  AttacherType = Attacher::AttachEngine3D
  AttachmentOffset = pos=(-21.19,18.635,-0.12) rot=(0,-1,0;0.15708rad)
  BaseFeature = -> Box1908
  Height = 0.12
  Length = 0.725
  MapMode = 5
  Placement = pos=(-21.19,18.635,-0.12) rot=(0,-1,0;0.15708rad)
  Support = -> [XY_Plane201]
  Width = 0.25
FEATURE [PartDesign::SubtractiveBox] Box1773
  AttacherType = Attacher::AttachEngine3D
  AttachmentOffset = pos=(-21.5005,18.625,0.235) rot=(0,-1,0;0.174533rad)
  BaseFeature = -> Box1776
  Height = 0.3
  Length = 0.6605
  MapMode = 5
  Placement = pos=(-21.5005,18.625,0.235) rot=(0,-1,0;0.174533rad)
  Support = -> [XY_Plane201]
  Width = 0.25
FEATURE [PartDesign::Fillet] Fillet535
  Base = -> Box1773 [Edge2]
  BaseFeature = -> Box1773
  Placement = pos=(-21.5005,18.625,0.235) rot=(0,-1,0;0.174533rad)
  Radius = 0.05
  SupportTransform = false
FEATURE [PartDesign::Fillet] Fillet538
  Base = -> Fillet535 [Edge33]
  BaseFeature = -> Fillet535
  Placement = pos=(-21.5005,18.625,0.235) rot=(0,-1,0;0.174533rad)
  Radius = 0.5
  SupportTransform = false
FEATURE [PartDesign::SubtractiveBox] Box1910
  AttacherType = Attacher::AttachEngine3D
  AttachmentOffset = pos=(-20.5,18.63,0) rot=(0,0,1;0rad)
  BaseFeature = -> Box1769
  Height = 1.635
  Length = 0.5
  MapMode = 5
  Placement = pos=(-20.5,18.63,0) rot=(0,0,1;0rad)
  Support = -> [XY_Plane197]
  Width = 0.25
FEATURE [PartDesign::SubtractiveBox] Box1755
  AttacherType = Attacher::AttachEngine3D
  AttachmentOffset = pos=(-21.19,18.635,-0.12) rot=(0,-1,0;0.15708rad)
  BaseFeature = -> Box1910
  Height = 0.12
  Length = 0.725
  MapMode = 5
  Placement = pos=(-21.19,18.635,-0.12) rot=(0,-1,0;0.15708rad)
  Support = -> [XY_Plane197]
  Width = 0.25
FEATURE [PartDesign::SubtractiveBox] Box1775
  AttacherType = Attacher::AttachEngine3D
  AttachmentOffset = pos=(-21.5005,18.625,0.235) rot=(0,-1,0;0.174533rad)
  BaseFeature = -> Box1755
  Height = 0.3
  Length = 0.6605
  MapMode = 5
  Placement = pos=(-21.5005,18.625,0.235) rot=(0,-1,0;0.174533rad)
  Support = -> [XY_Plane197]
  Width = 0.25
FEATURE [PartDesign::Fillet] Fillet539
  Base = -> Box1775 [Edge2]
  BaseFeature = -> Box1775
  Placement = pos=(-21.5005,18.625,0.235) rot=(0,-1,0;0.174533rad)
  Radius = 0.05
  SupportTransform = false
FEATURE [PartDesign::Fillet] Fillet529
  Base = -> Fillet539 [Edge33]
  BaseFeature = -> Fillet539
  Placement = pos=(-21.5005,18.625,0.235) rot=(0,-1,0;0.174533rad)
  Radius = 0.5
  SupportTransform = false
FEATURE [PartDesign::AdditiveBox] Box1911
  AttacherType = Attacher::AttachEngine3D
  AttachmentOffset = pos=(-21.3,18.635,0) rot=(0,0,1;0rad)
  Height = 1.9
  Length = 1.3
  MapMode = 5
  Placement = pos=(-21.3,18.635,0) rot=(0,0,1;0rad)
  Support = -> [XY_Plane199]
  Width = 0.23
FEATURE [PartDesign::SubtractiveBox] Box1906
  AttacherType = Attacher::AttachEngine3D
  AttachmentOffset = pos=(-21.35,18.635,0.35) rot=(0,0,1;0rad)
  BaseFeature = -> Box1911
  Height = 1.55
  Length = 0.5
  MapMode = 5
  Placement = pos=(-21.35,18.635,0.35) rot=(0,0,1;0rad)
  Support = -> [XY_Plane199]
  Width = 0.23
FEATURE [PartDesign::SubtractiveBox] Box1834
  AttacherType = Attacher::AttachEngine3D
  AttachmentOffset = pos=(-20.5,18.63,0) rot=(0,0,1;0rad)
  BaseFeature = -> Box1906
  Height = 1.635
  Length = 0.5
  MapMode = 5
  Placement = pos=(-20.5,18.63,0) rot=(0,0,1;0rad)
  Support = -> [XY_Plane199]
  Width = 0.25
FEATURE [PartDesign::SubtractiveBox] Box1903
  AttacherType = Attacher::AttachEngine3D
  AttachmentOffset = pos=(-21.19,18.635,-0.12) rot=(0,-1,0;0.15708rad)
  BaseFeature = -> Box1834
  Height = 0.12
  Length = 0.725
  MapMode = 5
  Placement = pos=(-21.19,18.635,-0.12) rot=(0,-1,0;0.15708rad)
  Support = -> [XY_Plane199]
  Width = 0.25
FEATURE [PartDesign::SubtractiveBox] Box1902
  AttacherType = Attacher::AttachEngine3D
  AttachmentOffset = pos=(-21.5005,18.625,0.235) rot=(0,-1,0;0.174533rad)
  BaseFeature = -> Box1903
  Height = 0.3
  Length = 0.6605
  MapMode = 5
  Placement = pos=(-21.5005,18.625,0.235) rot=(0,-1,0;0.174533rad)
  Support = -> [XY_Plane199]
  Width = 0.25
FEATURE [PartDesign::Fillet] Fillet536
  Base = -> Box1902 [Edge2]
  BaseFeature = -> Box1902
  Placement = pos=(-21.5005,18.625,0.235) rot=(0,-1,0;0.174533rad)
  Radius = 0.05
  SupportTransform = false
FEATURE [PartDesign::Fillet] Fillet550
  Base = -> Fillet536 [Edge33]
  BaseFeature = -> Fillet536
  Placement = pos=(-21.5005,18.625,0.235) rot=(0,-1,0;0.174533rad)
  Radius = 0.5
  SupportTransform = false
FEATURE [PartDesign::AdditiveBox] Box1823
  AttacherType = Attacher::AttachEngine3D
  AttachmentOffset = pos=(-21.1,18.635,0.305) rot=(0,1,0;0.785398rad)
  BaseFeature = -> Fillet550
  Height = 0.375
  Length = 0.2
  MapMode = 5
  Placement = pos=(-21.1,18.635,0.305) rot=(0,1,0;0.785398rad)
  Support = -> [XY_Plane199]
  Width = 0.23
FEATURE [PartDesign::SubtractiveCylinder] Cylinder387
  Angle = 360
  AttacherType = Attacher::AttachEngine3D
  AttachmentOffset = pos=(-21.055,18.935,0.52) rot=(1,0,0;1.5708rad)
  BaseFeature = -> Box1823
  Height = 0.375
  MapMode = 5
  Placement = pos=(-21.055,18.935,0.52) rot=(1,0,0;1.5708rad)
  Radius = 0.205
  Support = -> [XY_Plane199]
FEATURE [PartDesign::SubtractiveBox] Box1900
  AttacherType = Attacher::AttachEngine3D
  AttachmentOffset = pos=(-20.95,18.635,0.53) rot=(0,0,1;0rad)
  BaseFeature = -> Cylinder387
  Height = 0.5
  Length = 0.1
  MapMode = 5
  Placement = pos=(-20.95,18.635,0.53) rot=(0,0,1;0rad)
  Support = -> [XY_Plane199]
  Width = 0.23
FEATURE [PartDesign::SubtractiveBox] Box1845
  AttacherType = Attacher::AttachEngine3D
  AttachmentOffset = pos=(-21.15,18.635,0.297) rot=(0,-1,0;0.174533rad)
  BaseFeature = -> Box1900
  Height = 0.115
  Length = 0.115
  MapMode = 5
  Placement = pos=(-21.15,18.635,0.297) rot=(0,-1,0;0.174533rad)
  Support = -> [XY_Plane199]
  Width = 0.23
FEATURE [PartDesign::Fillet] Fillet530
  Base = -> Box1845 [Edge28]
  BaseFeature = -> Box1845
  Placement = pos=(-21.15,18.635,0.297) rot=(0,-1,0;0.174533rad)
  Radius = 0.375
  SupportTransform = false
FEATURE [PartDesign::AdditiveBox] Box1844
  AttacherType = Attacher::AttachEngine3D
  AttachmentOffset = pos=(-20.7,18.635,1.55) rot=(0,1,0;0.785398rad)
  BaseFeature = -> Fillet530
  Height = 0.375
  Length = 0.23
  MapMode = 5
  Placement = pos=(-20.7,18.635,1.55) rot=(0,1,0;0.785398rad)
  Support = -> [XY_Plane199]
  Width = 0.23
FEATURE [PartDesign::SubtractiveCylinder] Cylinder386
  Angle = 360
  AttacherType = Attacher::AttachEngine3D
  AttachmentOffset = pos=(-20.271,18.635,1.4056) rot=(-1,0,0;1.5708rad)
  BaseFeature = -> Box1844
  Height = 0.23
  MapMode = 5
  Placement = pos=(-20.271,18.635,1.4056) rot=(-1,0,0;1.5708rad)
  Radius = 0.23
  Support = -> [XY_Plane199]
FEATURE [PartDesign::AdditiveBox] Box1905
  AttacherType = Attacher::AttachEngine3D
  AttachmentOffset = pos=(-20.1,18.635,1.635) rot=(0,0,1;0rad)
  BaseFeature = -> Cylinder386
  Height = 0.265
  Length = 0.23
  MapMode = 5
  Placement = pos=(-20.1,18.635,1.635) rot=(0,0,1;0rad)
  Support = -> [XY_Plane199]
  Width = 0.23
FEATURE [PartDesign::Body] Body185  label="pin185"
  Group = -> [Box1911,Box1906,Box1834,Box1903,Box1902,Fillet536,Fillet550,Box1823,Cylinder387,Box1900,Box1845,Fillet530,Box1844,Cylinder386,Box1905]
  Origin = -> Origin200
  Placement = pos=(0,-1,0) rot=(0,0,1;0rad)
  Tip = -> Box1905
FEATURE [PartDesign::AdditiveBox] Box1912
  AttacherType = Attacher::AttachEngine3D
  AttachmentOffset = pos=(-21.3,18.635,0) rot=(0,0,1;0rad)
  Height = 1.9
  Length = 1.3
  MapMode = 5
  Placement = pos=(-21.3,18.635,0) rot=(0,0,1;0rad)
  Support = -> [XY_Plane200]
  Width = 0.23
FEATURE [PartDesign::SubtractiveBox] Box1913
  AttacherType = Attacher::AttachEngine3D
  AttachmentOffset = pos=(-21.35,18.635,0.35) rot=(0,0,1;0rad)
  BaseFeature = -> Box1912
  Height = 1.55
  Length = 0.5
  MapMode = 5
  Placement = pos=(-21.35,18.635,0.35) rot=(0,0,1;0rad)
  Support = -> [XY_Plane200]
  Width = 0.23
FEATURE [PartDesign::SubtractiveBox] Box1836
  AttacherType = Attacher::AttachEngine3D
  AttachmentOffset = pos=(-20.5,18.63,0) rot=(0,0,1;0rad)
  BaseFeature = -> Box1913
  Height = 1.635
  Length = 0.5
  MapMode = 5
  Placement = pos=(-20.5,18.63,0) rot=(0,0,1;0rad)
  Support = -> [XY_Plane200]
  Width = 0.25
FEATURE [PartDesign::SubtractiveBox] Box1828
  AttacherType = Attacher::AttachEngine3D
  AttachmentOffset = pos=(-21.19,18.635,-0.12) rot=(0,-1,0;0.15708rad)
  BaseFeature = -> Box1836
  Height = 0.12
  Length = 0.725
  MapMode = 5
  Placement = pos=(-21.19,18.635,-0.12) rot=(0,-1,0;0.15708rad)
  Support = -> [XY_Plane200]
  Width = 0.25
FEATURE [PartDesign::SubtractiveBox] Box1901
  AttacherType = Attacher::AttachEngine3D
  AttachmentOffset = pos=(-21.5005,18.625,0.235) rot=(0,-1,0;0.174533rad)
  BaseFeature = -> Box1828
  Height = 0.3
  Length = 0.6605
  MapMode = 5
  Placement = pos=(-21.5005,18.625,0.235) rot=(0,-1,0;0.174533rad)
  Support = -> [XY_Plane200]
  Width = 0.25
FEATURE [PartDesign::Fillet] Fillet552
  Base = -> Box1901 [Edge2]
  BaseFeature = -> Box1901
  Placement = pos=(-21.5005,18.625,0.235) rot=(0,-1,0;0.174533rad)
  Radius = 0.05
  SupportTransform = false
FEATURE [PartDesign::Fillet] Fillet527
  Base = -> Fillet552 [Edge33]
  BaseFeature = -> Fillet552
  Placement = pos=(-21.5005,18.625,0.235) rot=(0,-1,0;0.174533rad)
  Radius = 0.5
  SupportTransform = false
FEATURE [PartDesign::AdditiveBox] Box1760
  AttacherType = Attacher::AttachEngine3D
  AttachmentOffset = pos=(-21.1,18.635,0.305) rot=(0,1,0;0.785398rad)
  BaseFeature = -> Fillet527
  Height = 0.375
  Length = 0.2
  MapMode = 5
  Placement = pos=(-21.1,18.635,0.305) rot=(0,1,0;0.785398rad)
  Support = -> [XY_Plane200]
  Width = 0.23
FEATURE [PartDesign::SubtractiveCylinder] Cylinder366
  Angle = 360
  AttacherType = Attacher::AttachEngine3D
  AttachmentOffset = pos=(-21.055,18.935,0.52) rot=(1,0,0;1.5708rad)
  BaseFeature = -> Box1760
  Height = 0.375
  MapMode = 5
  Placement = pos=(-21.055,18.935,0.52) rot=(1,0,0;1.5708rad)
  Radius = 0.205
  Support = -> [XY_Plane200]
FEATURE [PartDesign::SubtractiveBox] Box1811
  AttacherType = Attacher::AttachEngine3D
  AttachmentOffset = pos=(-20.95,18.635,0.53) rot=(0,0,1;0rad)
  BaseFeature = -> Cylinder366
  Height = 0.5
  Length = 0.1
  MapMode = 5
  Placement = pos=(-20.95,18.635,0.53) rot=(0,0,1;0rad)
  Support = -> [XY_Plane200]
  Width = 0.23
FEATURE [PartDesign::SubtractiveBox] Box1796
  AttacherType = Attacher::AttachEngine3D
  AttachmentOffset = pos=(-21.15,18.635,0.297) rot=(0,-1,0;0.174533rad)
  BaseFeature = -> Box1811
  Height = 0.115
  Length = 0.115
  MapMode = 5
  Placement = pos=(-21.15,18.635,0.297) rot=(0,-1,0;0.174533rad)
  Support = -> [XY_Plane200]
  Width = 0.23
FEATURE [PartDesign::Fillet] Fillet556
  Base = -> Box1796 [Edge28]
  BaseFeature = -> Box1796
  Placement = pos=(-21.15,18.635,0.297) rot=(0,-1,0;0.174533rad)
  Radius = 0.375
  SupportTransform = false
FEATURE [PartDesign::AdditiveBox] Box1831
  AttacherType = Attacher::AttachEngine3D
  AttachmentOffset = pos=(-20.7,18.635,1.55) rot=(0,1,0;0.785398rad)
  BaseFeature = -> Fillet556
  Height = 0.375
  Length = 0.23
  MapMode = 5
  Placement = pos=(-20.7,18.635,1.55) rot=(0,1,0;0.785398rad)
  Support = -> [XY_Plane200]
  Width = 0.23
FEATURE [PartDesign::SubtractiveCylinder] Cylinder365
  Angle = 360
  AttacherType = Attacher::AttachEngine3D
  AttachmentOffset = pos=(-20.271,18.635,1.4056) rot=(-1,0,0;1.5708rad)
  BaseFeature = -> Box1831
  Height = 0.23
  MapMode = 5
  Placement = pos=(-20.271,18.635,1.4056) rot=(-1,0,0;1.5708rad)
  Radius = 0.23
  Support = -> [XY_Plane200]
FEATURE [PartDesign::AdditiveBox] Box1841
  AttacherType = Attacher::AttachEngine3D
  AttachmentOffset = pos=(-20.1,18.635,1.635) rot=(0,0,1;0rad)
  BaseFeature = -> Cylinder365
  Height = 0.265
  Length = 0.23
  MapMode = 5
  Placement = pos=(-20.1,18.635,1.635) rot=(0,0,1;0rad)
  Support = -> [XY_Plane200]
  Width = 0.23
FEATURE [PartDesign::Body] Body179  label="pin179"
  Group = -> [Box1912,Box1913,Box1836,Box1828,Box1901,Fillet552,Fillet527,Box1760,Cylinder366,Box1811,Box1796,Fillet556,Box1831,Cylinder365,Box1841]
  Origin = -> Origin193
  Tip = -> Box1841
FEATURE [PartDesign::AdditiveBox] Box1914
  AttacherType = Attacher::AttachEngine3D
  AttachmentOffset = pos=(-21.1,18.635,0.305) rot=(0,1,0;0.785398rad)
  BaseFeature = -> Fillet529
  Height = 0.375
  Length = 0.2
  MapMode = 5
  Placement = pos=(-21.1,18.635,0.305) rot=(0,1,0;0.785398rad)
  Support = -> [XY_Plane197]
  Width = 0.23
FEATURE [PartDesign::SubtractiveCylinder] Cylinder358
  Angle = 360
  AttacherType = Attacher::AttachEngine3D
  AttachmentOffset = pos=(-21.055,18.935,0.52) rot=(1,0,0;1.5708rad)
  BaseFeature = -> Box1914
  Height = 0.375
  MapMode = 5
  Placement = pos=(-21.055,18.935,0.52) rot=(1,0,0;1.5708rad)
  Radius = 0.205
  Support = -> [XY_Plane197]
FEATURE [PartDesign::SubtractiveBox] Box1777
  AttacherType = Attacher::AttachEngine3D
  AttachmentOffset = pos=(-20.95,18.635,0.53) rot=(0,0,1;0rad)
  BaseFeature = -> Cylinder358
  Height = 0.5
  Length = 0.1
  MapMode = 5
  Placement = pos=(-20.95,18.635,0.53) rot=(0,0,1;0rad)
  Support = -> [XY_Plane197]
  Width = 0.23
FEATURE [PartDesign::SubtractiveBox] Box1781
  AttacherType = Attacher::AttachEngine3D
  AttachmentOffset = pos=(-21.15,18.635,0.297) rot=(0,-1,0;0.174533rad)
  BaseFeature = -> Box1777
  Height = 0.115
  Length = 0.115
  MapMode = 5
  Placement = pos=(-21.15,18.635,0.297) rot=(0,-1,0;0.174533rad)
  Support = -> [XY_Plane197]
  Width = 0.23
FEATURE [PartDesign::Fillet] Fillet528
  Base = -> Box1781 [Edge28]
  BaseFeature = -> Box1781
  Placement = pos=(-21.15,18.635,0.297) rot=(0,-1,0;0.174533rad)
  Radius = 0.375
  SupportTransform = false
FEATURE [PartDesign::AdditiveBox] Box1768
  AttacherType = Attacher::AttachEngine3D
  AttachmentOffset = pos=(-20.7,18.635,1.55) rot=(0,1,0;0.785398rad)
  BaseFeature = -> Fillet528
  Height = 0.375
  Length = 0.23
  MapMode = 5
  Placement = pos=(-20.7,18.635,1.55) rot=(0,1,0;0.785398rad)
  Support = -> [XY_Plane197]
  Width = 0.23
FEATURE [PartDesign::SubtractiveCylinder] Cylinder357
  Angle = 360
  AttacherType = Attacher::AttachEngine3D
  AttachmentOffset = pos=(-20.271,18.635,1.4056) rot=(-1,0,0;1.5708rad)
  BaseFeature = -> Box1768
  Height = 0.23
  MapMode = 5
  Placement = pos=(-20.271,18.635,1.4056) rot=(-1,0,0;1.5708rad)
  Radius = 0.23
  Support = -> [XY_Plane197]
FEATURE [PartDesign::AdditiveBox] Box1772
  AttacherType = Attacher::AttachEngine3D
  AttachmentOffset = pos=(-20.1,18.635,1.635) rot=(0,0,1;0rad)
  BaseFeature = -> Cylinder357
  Height = 0.265
  Length = 0.23
  MapMode = 5
  Placement = pos=(-20.1,18.635,1.635) rot=(0,0,1;0rad)
  Support = -> [XY_Plane197]
  Width = 0.23
FEATURE [PartDesign::Body] Body180  label="pin180"
  Group = -> [Box1791,Box1769,Box1910,Box1755,Box1775,Fillet539,Fillet529,Box1914,Cylinder358,Box1777,Box1781,Fillet528,Box1768,Cylinder357,Box1772]
  Origin = -> Origin203
  Placement = pos=(0,-2.5,0) rot=(0,0,1;0rad)
  Tip = -> Box1772
FEATURE [PartDesign::AdditiveBox] Box1917
  AttacherType = Attacher::AttachEngine3D
  AttachmentOffset = pos=(-21.3,18.635,0) rot=(0,0,1;0rad)
  Height = 1.9
  Length = 1.3
  MapMode = 5
  Placement = pos=(-21.3,18.635,0) rot=(0,0,1;0rad)
  Support = -> [XY_Plane215]
  Width = 0.23
FEATURE [PartDesign::SubtractiveBox] Box1918
  AttacherType = Attacher::AttachEngine3D
  AttachmentOffset = pos=(-20.5,18.63,0) rot=(0,0,1;0rad)
  BaseFeature = -> Box1783
  Height = 1.635
  Length = 0.5
  MapMode = 5
  Placement = pos=(-20.5,18.63,0) rot=(0,0,1;0rad)
  Support = -> [XY_Plane198]
  Width = 0.25
FEATURE [PartDesign::SubtractiveBox] Box1904
  AttacherType = Attacher::AttachEngine3D
  AttachmentOffset = pos=(-21.19,18.635,-0.12) rot=(0,-1,0;0.15708rad)
  BaseFeature = -> Box1918
  Height = 0.12
  Length = 0.725
  MapMode = 5
  Placement = pos=(-21.19,18.635,-0.12) rot=(0,-1,0;0.15708rad)
  Support = -> [XY_Plane198]
  Width = 0.25
FEATURE [PartDesign::SubtractiveBox] Box1782
  AttacherType = Attacher::AttachEngine3D
  AttachmentOffset = pos=(-21.5005,18.625,0.235) rot=(0,-1,0;0.174533rad)
  BaseFeature = -> Box1904
  Height = 0.3
  Length = 0.6605
  MapMode = 5
  Placement = pos=(-21.5005,18.625,0.235) rot=(0,-1,0;0.174533rad)
  Support = -> [XY_Plane198]
  Width = 0.25
FEATURE [PartDesign::Fillet] Fillet544
  Base = -> Box1782 [Edge2]
  BaseFeature = -> Box1782
  Placement = pos=(-21.5005,18.625,0.235) rot=(0,-1,0;0.174533rad)
  Radius = 0.05
  SupportTransform = false
FEATURE [PartDesign::Fillet] Fillet537
  Base = -> Fillet544 [Edge33]
  BaseFeature = -> Fillet544
  Placement = pos=(-21.5005,18.625,0.235) rot=(0,-1,0;0.174533rad)
  Radius = 0.5
  SupportTransform = false
FEATURE [PartDesign::SubtractiveBox] Box1919
  AttacherType = Attacher::AttachEngine3D
  AttachmentOffset = pos=(-21.35,18.635,0.35) rot=(0,0,1;0rad)
  BaseFeature = -> Box1917
  Height = 1.55
  Length = 0.5
  MapMode = 5
  Placement = pos=(-21.35,18.635,0.35) rot=(0,0,1;0rad)
  Support = -> [XY_Plane215]
  Width = 0.23
FEATURE [PartDesign::SubtractiveBox] Box1887
  AttacherType = Attacher::AttachEngine3D
  AttachmentOffset = pos=(-20.5,18.63,0) rot=(0,0,1;0rad)
  BaseFeature = -> Box1919
  Height = 1.635
  Length = 0.5
  MapMode = 5
  Placement = pos=(-20.5,18.63,0) rot=(0,0,1;0rad)
  Support = -> [XY_Plane215]
  Width = 0.25
FEATURE [PartDesign::AdditiveBox] Box1920
  AttacherType = Attacher::AttachEngine3D
  AttachmentOffset = pos=(-21.3,18.635,0) rot=(0,0,1;0rad)
  Height = 1.9
  Length = 1.3
  MapMode = 5
  Placement = pos=(-21.3,18.635,0) rot=(0,0,1;0rad)
  Support = -> [XY_Plane218]
  Width = 0.23
FEATURE [PartDesign::AdditiveBox] Box1923
  AttacherType = Attacher::AttachEngine3D
  AttachmentOffset = pos=(-21.1,18.635,0.305) rot=(0,1,0;0.785398rad)
  BaseFeature = -> Fillet538
  Height = 0.375
  Length = 0.2
  MapMode = 5
  Placement = pos=(-21.1,18.635,0.305) rot=(0,1,0;0.785398rad)
  Support = -> [XY_Plane201]
  Width = 0.23
FEATURE [PartDesign::SubtractiveCylinder] Cylinder388
  Angle = 360
  AttacherType = Attacher::AttachEngine3D
  AttachmentOffset = pos=(-21.055,18.935,0.52) rot=(1,0,0;1.5708rad)
  BaseFeature = -> Box1923
  Height = 0.375
  MapMode = 5
  Placement = pos=(-21.055,18.935,0.52) rot=(1,0,0;1.5708rad)
  Radius = 0.205
  Support = -> [XY_Plane201]
FEATURE [PartDesign::SubtractiveBox] Box1780
  AttacherType = Attacher::AttachEngine3D
  AttachmentOffset = pos=(-20.95,18.635,0.53) rot=(0,0,1;0rad)
  BaseFeature = -> Cylinder388
  Height = 0.5
  Length = 0.1
  MapMode = 5
  Placement = pos=(-20.95,18.635,0.53) rot=(0,0,1;0rad)
  Support = -> [XY_Plane201]
  Width = 0.23
FEATURE [PartDesign::SubtractiveBox] Box1766
  AttacherType = Attacher::AttachEngine3D
  AttachmentOffset = pos=(-21.15,18.635,0.297) rot=(0,-1,0;0.174533rad)
  BaseFeature = -> Box1780
  Height = 0.115
  Length = 0.115
  MapMode = 5
  Placement = pos=(-21.15,18.635,0.297) rot=(0,-1,0;0.174533rad)
  Support = -> [XY_Plane201]
  Width = 0.23
FEATURE [PartDesign::Fillet] Fillet532
  Base = -> Box1766 [Edge28]
  BaseFeature = -> Box1766
  Placement = pos=(-21.15,18.635,0.297) rot=(0,-1,0;0.174533rad)
  Radius = 0.375
  SupportTransform = false
FEATURE [PartDesign::AdditiveBox] Box1907
  AttacherType = Attacher::AttachEngine3D
  AttachmentOffset = pos=(-20.7,18.635,1.55) rot=(0,1,0;0.785398rad)
  BaseFeature = -> Fillet532
  Height = 0.375
  Length = 0.23
  MapMode = 5
  Placement = pos=(-20.7,18.635,1.55) rot=(0,1,0;0.785398rad)
  Support = -> [XY_Plane201]
  Width = 0.23
FEATURE [PartDesign::SubtractiveCylinder] Cylinder359
  Angle = 360
  AttacherType = Attacher::AttachEngine3D
  AttachmentOffset = pos=(-20.271,18.635,1.4056) rot=(-1,0,0;1.5708rad)
  BaseFeature = -> Box1907
  Height = 0.23
  MapMode = 5
  Placement = pos=(-20.271,18.635,1.4056) rot=(-1,0,0;1.5708rad)
  Radius = 0.23
  Support = -> [XY_Plane201]
FEATURE [PartDesign::AdditiveBox] Box1779
  AttacherType = Attacher::AttachEngine3D
  AttachmentOffset = pos=(-20.1,18.635,1.635) rot=(0,0,1;0rad)
  BaseFeature = -> Cylinder359
  Height = 0.265
  Length = 0.23
  MapMode = 5
  Placement = pos=(-20.1,18.635,1.635) rot=(0,0,1;0rad)
  Support = -> [XY_Plane201]
  Width = 0.23
FEATURE [PartDesign::Body] Body178  label="pin178"
  Group = -> [Box1767,Box1778,Box1908,Box1776,Box1773,Fillet535,Fillet538,Box1923,Cylinder388,Box1780,Box1766,Fillet532,Box1907,Cylinder359,Box1779]
  Origin = -> Origin195
  Placement = pos=(0,-2,0) rot=(0,0,1;0rad)
  Tip = -> Box1779
FEATURE [PartDesign::AdditiveBox] Box1925
  AttacherType = Attacher::AttachEngine3D
  AttachmentOffset = pos=(-21.1,18.635,0.305) rot=(0,1,0;0.785398rad)
  BaseFeature = -> Fillet537
  Height = 0.375
  Length = 0.2
  MapMode = 5
  Placement = pos=(-21.1,18.635,0.305) rot=(0,1,0;0.785398rad)
  Support = -> [XY_Plane198]
  Width = 0.23
FEATURE [PartDesign::SubtractiveCylinder] Cylinder385
  Angle = 360
  AttacherType = Attacher::AttachEngine3D
  AttachmentOffset = pos=(-21.055,18.935,0.52) rot=(1,0,0;1.5708rad)
  BaseFeature = -> Box1925
  Height = 0.375
  MapMode = 5
  Placement = pos=(-21.055,18.935,0.52) rot=(1,0,0;1.5708rad)
  Radius = 0.205
  Support = -> [XY_Plane198]
FEATURE [PartDesign::SubtractiveBox] Box1909
  AttacherType = Attacher::AttachEngine3D
  AttachmentOffset = pos=(-20.95,18.635,0.53) rot=(0,0,1;0rad)
  BaseFeature = -> Cylinder385
  Height = 0.5
  Length = 0.1
  MapMode = 5
  Placement = pos=(-20.95,18.635,0.53) rot=(0,0,1;0rad)
  Support = -> [XY_Plane198]
  Width = 0.23
FEATURE [PartDesign::SubtractiveBox] Box1915
  AttacherType = Attacher::AttachEngine3D
  AttachmentOffset = pos=(-21.15,18.635,0.297) rot=(0,-1,0;0.174533rad)
  BaseFeature = -> Box1909
  Height = 0.115
  Length = 0.115
  MapMode = 5
  Placement = pos=(-21.15,18.635,0.297) rot=(0,-1,0;0.174533rad)
  Support = -> [XY_Plane198]
  Width = 0.23
FEATURE [PartDesign::Fillet] Fillet545
  Base = -> Box1915 [Edge28]
  BaseFeature = -> Box1915
  Placement = pos=(-21.15,18.635,0.297) rot=(0,-1,0;0.174533rad)
  Radius = 0.375
  SupportTransform = false
FEATURE [PartDesign::AdditiveBox] Box1924
  AttacherType = Attacher::AttachEngine3D
  AttachmentOffset = pos=(-20.7,18.635,1.55) rot=(0,1,0;0.785398rad)
  BaseFeature = -> Fillet545
  Height = 0.375
  Length = 0.23
  MapMode = 5
  Placement = pos=(-20.7,18.635,1.55) rot=(0,1,0;0.785398rad)
  Support = -> [XY_Plane198]
  Width = 0.23
FEATURE [PartDesign::SubtractiveCylinder] Cylinder356
  Angle = 360
  AttacherType = Attacher::AttachEngine3D
  AttachmentOffset = pos=(-20.271,18.635,1.4056) rot=(-1,0,0;1.5708rad)
  BaseFeature = -> Box1924
  Height = 0.23
  MapMode = 5
  Placement = pos=(-20.271,18.635,1.4056) rot=(-1,0,0;1.5708rad)
  Radius = 0.23
  Support = -> [XY_Plane198]
FEATURE [PartDesign::AdditiveBox] Box1927
  AttacherType = Attacher::AttachEngine3D
  AttachmentOffset = pos=(-20.1,18.635,1.635) rot=(0,0,1;0rad)
  BaseFeature = -> Cylinder356
  Height = 0.265
  Length = 0.23
  MapMode = 5
  Placement = pos=(-20.1,18.635,1.635) rot=(0,0,1;0rad)
  Support = -> [XY_Plane198]
  Width = 0.23
FEATURE [PartDesign::Body] Body181  label="pin181"
  Group = -> [Box1789,Box1783,Box1918,Box1904,Box1782,Fillet544,Fillet537,Box1925,Cylinder385,Box1909,Box1915,Fillet545,Box1924,Cylinder356,Box1927]
  Origin = -> Origin198
  Placement = pos=(0,-1.5,0) rot=(0,0,1;0rad)
  Tip = -> Box1927
FEATURE [App::Part] Part014  label="Pin-set013"
  Group = -> [Body179,Body177,Body185,Body181,Body178,Body180,Body187,Body182,Body184,Body183,Body186,Body188]
  Origin = -> Origin183
  Placement = pos=(0,-12,0) rot=(0,0,1;0rad)
FEATURE [PartDesign::AdditiveBox] Box1928
  AttacherType = Attacher::AttachEngine3D
  AttachmentOffset = pos=(-21.3,18.635,0) rot=(0,0,1;0rad)
  Height = 1.9
  Length = 1.3
  MapMode = 5
  Placement = pos=(-21.3,18.635,0) rot=(0,0,1;0rad)
  Support = -> [XY_Plane217]
  Width = 0.23
FEATURE [PartDesign::SubtractiveBox] Box1932
  AttacherType = Attacher::AttachEngine3D
  AttachmentOffset = pos=(-21.19,18.635,-0.12) rot=(0,-1,0;0.15708rad)
  BaseFeature = -> Box1887
  Height = 0.12
  Length = 0.725
  MapMode = 5
  Placement = pos=(-21.19,18.635,-0.12) rot=(0,-1,0;0.15708rad)
  Support = -> [XY_Plane215]
  Width = 0.25
FEATURE [PartDesign::SubtractiveBox] Box1934
  AttacherType = Attacher::AttachEngine3D
  AttachmentOffset = pos=(-21.5005,18.625,0.235) rot=(0,-1,0;0.174533rad)
  BaseFeature = -> Box1932
  Height = 0.3
  Length = 0.6605
  MapMode = 5
  Placement = pos=(-21.5005,18.625,0.235) rot=(0,-1,0;0.174533rad)
  Support = -> [XY_Plane215]
  Width = 0.25
FEATURE [PartDesign::SubtractiveBox] Box1937
  AttacherType = Attacher::AttachEngine3D
  AttachmentOffset = pos=(-21.35,18.635,0.35) rot=(0,0,1;0rad)
  BaseFeature = -> Box1920
  Height = 1.55
  Length = 0.5
  MapMode = 5
  Placement = pos=(-21.35,18.635,0.35) rot=(0,0,1;0rad)
  Support = -> [XY_Plane218]
  Width = 0.23
FEATURE [PartDesign::AdditiveBox] Box1938
  AttacherType = Attacher::AttachEngine3D
  AttachmentOffset = pos=(-21.3,18.635,0) rot=(0,0,1;0rad)
  Height = 1.9
  Length = 1.3
  MapMode = 5
  Placement = pos=(-21.3,18.635,0) rot=(0,0,1;0rad)
  Support = -> [XY_Plane210]
  Width = 0.23
FEATURE [PartDesign::SubtractiveBox] Box1862
  AttacherType = Attacher::AttachEngine3D
  AttachmentOffset = pos=(-21.35,18.635,0.35) rot=(0,0,1;0rad)
  BaseFeature = -> Box1938
  Height = 1.55
  Length = 0.5
  MapMode = 5
  Placement = pos=(-21.35,18.635,0.35) rot=(0,0,1;0rad)
  Support = -> [XY_Plane210]
  Width = 0.23
FEATURE [PartDesign::SubtractiveBox] Box1940
  AttacherType = Attacher::AttachEngine3D
  AttachmentOffset = pos=(-21.35,18.635,0.35) rot=(0,0,1;0rad)
  BaseFeature = -> Box1928
  Height = 1.55
  Length = 0.5
  MapMode = 5
  Placement = pos=(-21.35,18.635,0.35) rot=(0,0,1;0rad)
  Support = -> [XY_Plane217]
  Width = 0.23
FEATURE [PartDesign::SubtractiveBox] Box1893
  AttacherType = Attacher::AttachEngine3D
  AttachmentOffset = pos=(-20.5,18.63,0) rot=(0,0,1;0rad)
  BaseFeature = -> Box1940
  Height = 1.635
  Length = 0.5
  MapMode = 5
  Placement = pos=(-20.5,18.63,0) rot=(0,0,1;0rad)
  Support = -> [XY_Plane217]
  Width = 0.25
FEATURE [PartDesign::Fillet] Fillet576
  Base = -> Box1864 [Edge2]
  BaseFeature = -> Box1864
  Placement = pos=(-21.5005,18.625,0.235) rot=(0,-1,0;0.174533rad)
  Radius = 0.05
  SupportTransform = false
FEATURE [PartDesign::Fillet] Fillet584
  Base = -> Box1884 [Edge2]
  BaseFeature = -> Box1884
  Placement = pos=(-21.5005,18.625,0.235) rot=(0,-1,0;0.174533rad)
  Radius = 0.05
  SupportTransform = false
FEATURE [PartDesign::Fillet] Fillet566
  Base = -> Fillet584 [Edge33]
  BaseFeature = -> Fillet584
  Placement = pos=(-21.5005,18.625,0.235) rot=(0,-1,0;0.174533rad)
  Radius = 0.5
  SupportTransform = false
FEATURE [PartDesign::AdditiveBox] Box1863
  AttacherType = Attacher::AttachEngine3D
  AttachmentOffset = pos=(-21.1,18.635,0.305) rot=(0,1,0;0.785398rad)
  BaseFeature = -> Fillet566
  Height = 0.375
  Length = 0.2
  MapMode = 5
  Placement = pos=(-21.1,18.635,0.305) rot=(0,1,0;0.785398rad)
  Support = -> [XY_Plane216]
  Width = 0.23
FEATURE [PartDesign::SubtractiveCylinder] Cylinder378
  Angle = 360
  AttacherType = Attacher::AttachEngine3D
  AttachmentOffset = pos=(-21.055,18.935,0.52) rot=(1,0,0;1.5708rad)
  BaseFeature = -> Box1863
  Height = 0.375
  MapMode = 5
  Placement = pos=(-21.055,18.935,0.52) rot=(1,0,0;1.5708rad)
  Radius = 0.205
  Support = -> [XY_Plane216]
FEATURE [PartDesign::SubtractiveBox] Box1894
  AttacherType = Attacher::AttachEngine3D
  AttachmentOffset = pos=(-20.95,18.635,0.53) rot=(0,0,1;0rad)
  BaseFeature = -> Cylinder378
  Height = 0.5
  Length = 0.1
  MapMode = 5
  Placement = pos=(-20.95,18.635,0.53) rot=(0,0,1;0rad)
  Support = -> [XY_Plane216]
  Width = 0.23
FEATURE [PartDesign::SubtractiveBox] Box1869
  AttacherType = Attacher::AttachEngine3D
  AttachmentOffset = pos=(-21.15,18.635,0.297) rot=(0,-1,0;0.174533rad)
  BaseFeature = -> Box1894
  Height = 0.115
  Length = 0.115
  MapMode = 5
  Placement = pos=(-21.15,18.635,0.297) rot=(0,-1,0;0.174533rad)
  Support = -> [XY_Plane216]
  Width = 0.23
FEATURE [PartDesign::Fillet] Fillet572
  Base = -> Box1869 [Edge28]
  BaseFeature = -> Box1869
  Placement = pos=(-21.15,18.635,0.297) rot=(0,-1,0;0.174533rad)
  Radius = 0.375
  SupportTransform = false
FEATURE [PartDesign::AdditiveBox] Box1878
  AttacherType = Attacher::AttachEngine3D
  AttachmentOffset = pos=(-20.7,18.635,1.55) rot=(0,1,0;0.785398rad)
  BaseFeature = -> Fillet572
  Height = 0.375
  Length = 0.23
  MapMode = 5
  Placement = pos=(-20.7,18.635,1.55) rot=(0,1,0;0.785398rad)
  Support = -> [XY_Plane216]
  Width = 0.23
FEATURE [PartDesign::SubtractiveCylinder] Cylinder376
  Angle = 360
  AttacherType = Attacher::AttachEngine3D
  AttachmentOffset = pos=(-20.271,18.635,1.4056) rot=(-1,0,0;1.5708rad)
  BaseFeature = -> Box1878
  Height = 0.23
  MapMode = 5
  Placement = pos=(-20.271,18.635,1.4056) rot=(-1,0,0;1.5708rad)
  Radius = 0.23
  Support = -> [XY_Plane216]
FEATURE [PartDesign::AdditiveBox] Box1888
  AttacherType = Attacher::AttachEngine3D
  AttachmentOffset = pos=(-20.1,18.635,1.635) rot=(0,0,1;0rad)
  BaseFeature = -> Cylinder376
  Height = 0.265
  Length = 0.23
  MapMode = 5
  Placement = pos=(-20.1,18.635,1.635) rot=(0,0,1;0rad)
  Support = -> [XY_Plane216]
  Width = 0.23
FEATURE [PartDesign::Fillet] Fillet586
  Base = -> Box1934 [Edge2]
  BaseFeature = -> Box1934
  Placement = pos=(-21.5005,18.625,0.235) rot=(0,-1,0;0.174533rad)
  Radius = 0.05
  SupportTransform = false
FEATURE [PartDesign::Fillet] Fillet589
  Base = -> Fillet586 [Edge33]
  BaseFeature = -> Fillet586
  Placement = pos=(-21.5005,18.625,0.235) rot=(0,-1,0;0.174533rad)
  Radius = 0.5
  SupportTransform = false
FEATURE [PartDesign::Body] Body200  label="pin200"
  Group = -> [Box1877,Box1885,Box1875,Box1879,Box1884,Fillet584,Fillet566,Box1863,Cylinder378,Box1894,Box1869,Fillet572,Box1878,Cylinder376,Box1888]
  Origin = -> Origin207
  Placement = pos=(0,-5,0) rot=(0,0,1;0rad)
  Tip = -> Box1888
FEATURE [PartDesign::Fillet] Fillet595
  Base = -> Fillet576 [Edge33]
  BaseFeature = -> Fillet576
  Placement = pos=(-21.5005,18.625,0.235) rot=(0,-1,0;0.174533rad)
  Radius = 0.5
  SupportTransform = false
FEATURE [PartDesign::AdditiveBox] Box1890
  AttacherType = Attacher::AttachEngine3D
  AttachmentOffset = pos=(-21.1,18.635,0.305) rot=(0,1,0;0.785398rad)
  BaseFeature = -> Fillet595
  Height = 0.375
  Length = 0.2
  MapMode = 5
  Placement = pos=(-21.1,18.635,0.305) rot=(0,1,0;0.785398rad)
  Support = -> [XY_Plane194]
  Width = 0.23
FEATURE [PartDesign::SubtractiveCylinder] Cylinder384
  Angle = 360
  AttacherType = Attacher::AttachEngine3D
  AttachmentOffset = pos=(-21.055,18.935,0.52) rot=(1,0,0;1.5708rad)
  BaseFeature = -> Box1890
  Height = 0.375
  MapMode = 5
  Placement = pos=(-21.055,18.935,0.52) rot=(1,0,0;1.5708rad)
  Radius = 0.205
  Support = -> [XY_Plane194]
FEATURE [PartDesign::SubtractiveBox] Box1886
  AttacherType = Attacher::AttachEngine3D
  AttachmentOffset = pos=(-20.95,18.635,0.53) rot=(0,0,1;0rad)
  BaseFeature = -> Cylinder384
  Height = 0.5
  Length = 0.1
  MapMode = 5
  Placement = pos=(-20.95,18.635,0.53) rot=(0,0,1;0rad)
  Support = -> [XY_Plane194]
  Width = 0.23
FEATURE [PartDesign::SubtractiveBox] Box1882
  AttacherType = Attacher::AttachEngine3D
  AttachmentOffset = pos=(-21.15,18.635,0.297) rot=(0,-1,0;0.174533rad)
  BaseFeature = -> Box1886
  Height = 0.115
  Length = 0.115
  MapMode = 5
  Placement = pos=(-21.15,18.635,0.297) rot=(0,-1,0;0.174533rad)
  Support = -> [XY_Plane194]
  Width = 0.23
FEATURE [PartDesign::Fillet] Fillet577
  Base = -> Box1882 [Edge28]
  BaseFeature = -> Box1882
  Placement = pos=(-21.15,18.635,0.297) rot=(0,-1,0;0.174533rad)
  Radius = 0.375
  SupportTransform = false
FEATURE [PartDesign::AdditiveBox] Box1892
  AttacherType = Attacher::AttachEngine3D
  AttachmentOffset = pos=(-20.7,18.635,1.55) rot=(0,1,0;0.785398rad)
  BaseFeature = -> Fillet577
  Height = 0.375
  Length = 0.23
  MapMode = 5
  Placement = pos=(-20.7,18.635,1.55) rot=(0,1,0;0.785398rad)
  Support = -> [XY_Plane194]
  Width = 0.23
FEATURE [PartDesign::SubtractiveCylinder] Cylinder381
  Angle = 360
  AttacherType = Attacher::AttachEngine3D
  AttachmentOffset = pos=(-20.271,18.635,1.4056) rot=(-1,0,0;1.5708rad)
  BaseFeature = -> Box1892
  Height = 0.23
  MapMode = 5
  Placement = pos=(-20.271,18.635,1.4056) rot=(-1,0,0;1.5708rad)
  Radius = 0.23
  Support = -> [XY_Plane194]
FEATURE [PartDesign::AdditiveBox] Box1889
  AttacherType = Attacher::AttachEngine3D
  AttachmentOffset = pos=(-20.1,18.635,1.635) rot=(0,0,1;0rad)
  BaseFeature = -> Cylinder381
  Height = 0.265
  Length = 0.23
  MapMode = 5
  Placement = pos=(-20.1,18.635,1.635) rot=(0,0,1;0rad)
  Support = -> [XY_Plane194]
  Width = 0.23
FEATURE [PartDesign::Body] Body199  label="pin199"
  Group = -> [Box1895,Box1896,Box1854,Box1865,Box1864,Fillet576,Fillet595,Box1890,Cylinder384,Box1886,Box1882,Fillet577,Box1892,Cylinder381,Box1889]
  Origin = -> Origin211
  Placement = pos=(0,-5.5,0) rot=(0,0,1;0rad)
  Tip = -> Box1889
FEATURE [PartDesign::SubtractiveBox] Box1943
  AttacherType = Attacher::AttachEngine3D
  AttachmentOffset = pos=(-20.5,18.63,0) rot=(0,0,1;0rad)
  BaseFeature = -> Box1660
  Height = 1.635
  Length = 0.5
  MapMode = 5
  Placement = pos=(-20.5,18.63,0) rot=(0,0,1;0rad)
  Support = -> [XY_Plane185]
  Width = 0.25
FEATURE [PartDesign::SubtractiveBox] Box1662
  AttacherType = Attacher::AttachEngine3D
  AttachmentOffset = pos=(-21.19,18.635,-0.12) rot=(0,-1,0;0.15708rad)
  BaseFeature = -> Box1943
  Height = 0.12
  Length = 0.725
  MapMode = 5
  Placement = pos=(-21.19,18.635,-0.12) rot=(0,-1,0;0.15708rad)
  Support = -> [XY_Plane185]
  Width = 0.25
FEATURE [PartDesign::SubtractiveBox] Box1663
  AttacherType = Attacher::AttachEngine3D
  AttachmentOffset = pos=(-21.5005,18.625,0.235) rot=(0,-1,0;0.174533rad)
  BaseFeature = -> Box1662
  Height = 0.3
  Length = 0.6605
  MapMode = 5
  Placement = pos=(-21.5005,18.625,0.235) rot=(0,-1,0;0.174533rad)
  Support = -> [XY_Plane185]
  Width = 0.25
FEATURE [PartDesign::Fillet] Fillet500
  Base = -> Box1663 [Edge2]
  BaseFeature = -> Box1663
  Placement = pos=(-21.5005,18.625,0.235) rot=(0,-1,0;0.174533rad)
  Radius = 0.05
  SupportTransform = false
FEATURE [PartDesign::Fillet] Fillet501
  Base = -> Fillet500 [Edge33]
  BaseFeature = -> Fillet500
  Placement = pos=(-21.5005,18.625,0.235) rot=(0,-1,0;0.174533rad)
  Radius = 0.5
  SupportTransform = false
FEATURE [PartDesign::SubtractiveBox] Box1946
  AttacherType = Attacher::AttachEngine3D
  AttachmentOffset = pos=(-20.5,18.63,0) rot=(0,0,1;0rad)
  BaseFeature = -> Box1669
  Height = 1.635
  Length = 0.5
  MapMode = 5
  Placement = pos=(-20.5,18.63,0) rot=(0,0,1;0rad)
  Support = -> [XY_Plane183]
  Width = 0.25
FEATURE [PartDesign::SubtractiveBox] Box1658
  AttacherType = Attacher::AttachEngine3D
  AttachmentOffset = pos=(-21.19,18.635,-0.12) rot=(0,-1,0;0.15708rad)
  BaseFeature = -> Box1946
  Height = 0.12
  Length = 0.725
  MapMode = 5
  Placement = pos=(-21.19,18.635,-0.12) rot=(0,-1,0;0.15708rad)
  Support = -> [XY_Plane183]
  Width = 0.25
FEATURE [PartDesign::SubtractiveBox] Box1671
  AttacherType = Attacher::AttachEngine3D
  AttachmentOffset = pos=(-21.5005,18.625,0.235) rot=(0,-1,0;0.174533rad)
  BaseFeature = -> Box1658
  Height = 0.3
  Length = 0.6605
  MapMode = 5
  Placement = pos=(-21.5005,18.625,0.235) rot=(0,-1,0;0.174533rad)
  Support = -> [XY_Plane183]
  Width = 0.25
FEATURE [PartDesign::Fillet] Fillet502
  Base = -> Box1671 [Edge2]
  BaseFeature = -> Box1671
  Placement = pos=(-21.5005,18.625,0.235) rot=(0,-1,0;0.174533rad)
  Radius = 0.05
  SupportTransform = false
FEATURE [PartDesign::Fillet] Fillet503
  Base = -> Fillet502 [Edge33]
  BaseFeature = -> Fillet502
  Placement = pos=(-21.5005,18.625,0.235) rot=(0,-1,0;0.174533rad)
  Radius = 0.5
  SupportTransform = false
FEATURE [PartDesign::AdditiveBox] Box1941
  AttacherType = Attacher::AttachEngine3D
  AttachmentOffset = pos=(-21.1,18.635,0.305) rot=(0,1,0;0.785398rad)
  BaseFeature = -> Fillet503
  Height = 0.375
  Length = 0.2
  MapMode = 5
  Placement = pos=(-21.1,18.635,0.305) rot=(0,1,0;0.785398rad)
  Support = -> [XY_Plane183]
  Width = 0.23
FEATURE [PartDesign::SubtractiveCylinder] Cylinder336
  Angle = 360
  AttacherType = Attacher::AttachEngine3D
  AttachmentOffset = pos=(-21.055,18.935,0.52) rot=(1,0,0;1.5708rad)
  BaseFeature = -> Box1941
  Height = 0.375
  MapMode = 5
  Placement = pos=(-21.055,18.935,0.52) rot=(1,0,0;1.5708rad)
  Radius = 0.205
  Support = -> [XY_Plane183]
FEATURE [PartDesign::SubtractiveBox] Box1661
  AttacherType = Attacher::AttachEngine3D
  AttachmentOffset = pos=(-20.95,18.635,0.53) rot=(0,0,1;0rad)
  BaseFeature = -> Cylinder336
  Height = 0.5
  Length = 0.1
  MapMode = 5
  Placement = pos=(-20.95,18.635,0.53) rot=(0,0,1;0rad)
  Support = -> [XY_Plane183]
  Width = 0.23
FEATURE [PartDesign::SubtractiveBox] Box1668
  AttacherType = Attacher::AttachEngine3D
  AttachmentOffset = pos=(-21.15,18.635,0.297) rot=(0,-1,0;0.174533rad)
  BaseFeature = -> Box1661
  Height = 0.115
  Length = 0.115
  MapMode = 5
  Placement = pos=(-21.15,18.635,0.297) rot=(0,-1,0;0.174533rad)
  Support = -> [XY_Plane183]
  Width = 0.23
FEATURE [PartDesign::Fillet] Fillet459
  Base = -> Box1668 [Edge28]
  BaseFeature = -> Box1668
  Placement = pos=(-21.15,18.635,0.297) rot=(0,-1,0;0.174533rad)
  Radius = 0.375
  SupportTransform = false
FEATURE [PartDesign::AdditiveBox] Box1667
  AttacherType = Attacher::AttachEngine3D
  AttachmentOffset = pos=(-20.7,18.635,1.55) rot=(0,1,0;0.785398rad)
  BaseFeature = -> Fillet459
  Height = 0.375
  Length = 0.23
  MapMode = 5
  Placement = pos=(-20.7,18.635,1.55) rot=(0,1,0;0.785398rad)
  Support = -> [XY_Plane183]
  Width = 0.23
FEATURE [PartDesign::SubtractiveCylinder] Cylinder335
  Angle = 360
  AttacherType = Attacher::AttachEngine3D
  AttachmentOffset = pos=(-20.271,18.635,1.4056) rot=(-1,0,0;1.5708rad)
  BaseFeature = -> Box1667
  Height = 0.23
  MapMode = 5
  Placement = pos=(-20.271,18.635,1.4056) rot=(-1,0,0;1.5708rad)
  Radius = 0.23
  Support = -> [XY_Plane183]
FEATURE [PartDesign::AdditiveBox] Box1659
  AttacherType = Attacher::AttachEngine3D
  AttachmentOffset = pos=(-20.1,18.635,1.635) rot=(0,0,1;0rad)
  BaseFeature = -> Cylinder335
  Height = 0.265
  Length = 0.23
  MapMode = 5
  Placement = pos=(-20.1,18.635,1.635) rot=(0,0,1;0rad)
  Support = -> [XY_Plane183]
  Width = 0.23
FEATURE [PartDesign::Body] Body169  label="pin169"
  Group = -> [Box1678,Box1669,Box1946,Box1658,Box1671,Fillet502,Fillet503,Box1941,Cylinder336,Box1661,Box1668,Fillet459,Box1667,Cylinder335,Box1659]
  Origin = -> Origin192
  Placement = pos=(0,-2.5,0) rot=(0,0,1;0rad)
  Tip = -> Box1659
FEATURE [PartDesign::AdditiveBox] Box1948
  AttacherType = Attacher::AttachEngine3D
  AttachmentOffset = pos=(-21.1,18.635,0.305) rot=(0,1,0;0.785398rad)
  BaseFeature = -> Fillet501
  Height = 0.375
  Length = 0.2
  MapMode = 5
  Placement = pos=(-21.1,18.635,0.305) rot=(0,1,0;0.785398rad)
  Support = -> [XY_Plane185]
  Width = 0.23
FEATURE [PartDesign::SubtractiveCylinder] Cylinder395
  Angle = 360
  AttacherType = Attacher::AttachEngine3D
  AttachmentOffset = pos=(-21.055,18.935,0.52) rot=(1,0,0;1.5708rad)
  BaseFeature = -> Box1948
  Height = 0.375
  MapMode = 5
  Placement = pos=(-21.055,18.935,0.52) rot=(1,0,0;1.5708rad)
  Radius = 0.205
  Support = -> [XY_Plane185]
FEATURE [PartDesign::SubtractiveBox] Box1666
  AttacherType = Attacher::AttachEngine3D
  AttachmentOffset = pos=(-20.95,18.635,0.53) rot=(0,0,1;0rad)
  BaseFeature = -> Cylinder395
  Height = 0.5
  Length = 0.1
  MapMode = 5
  Placement = pos=(-20.95,18.635,0.53) rot=(0,0,1;0rad)
  Support = -> [XY_Plane185]
  Width = 0.23
FEATURE [PartDesign::SubtractiveBox] Box1634
  AttacherType = Attacher::AttachEngine3D
  AttachmentOffset = pos=(-21.15,18.635,0.297) rot=(0,-1,0;0.174533rad)
  BaseFeature = -> Box1666
  Height = 0.115
  Length = 0.115
  MapMode = 5
  Placement = pos=(-21.15,18.635,0.297) rot=(0,-1,0;0.174533rad)
  Support = -> [XY_Plane185]
  Width = 0.23
FEATURE [PartDesign::Fillet] Fillet495
  Base = -> Box1634 [Edge28]
  BaseFeature = -> Box1634
  Placement = pos=(-21.15,18.635,0.297) rot=(0,-1,0;0.174533rad)
  Radius = 0.375
  SupportTransform = false
FEATURE [PartDesign::AdditiveBox] Box1942
  AttacherType = Attacher::AttachEngine3D
  AttachmentOffset = pos=(-20.7,18.635,1.55) rot=(0,1,0;0.785398rad)
  BaseFeature = -> Fillet495
  Height = 0.375
  Length = 0.23
  MapMode = 5
  Placement = pos=(-20.7,18.635,1.55) rot=(0,1,0;0.785398rad)
  Support = -> [XY_Plane185]
  Width = 0.23
FEATURE [PartDesign::SubtractiveCylinder] Cylinder337
  Angle = 360
  AttacherType = Attacher::AttachEngine3D
  AttachmentOffset = pos=(-20.271,18.635,1.4056) rot=(-1,0,0;1.5708rad)
  BaseFeature = -> Box1942
  Height = 0.23
  MapMode = 5
  Placement = pos=(-20.271,18.635,1.4056) rot=(-1,0,0;1.5708rad)
  Radius = 0.23
  Support = -> [XY_Plane185]
FEATURE [PartDesign::AdditiveBox] Box1665
  AttacherType = Attacher::AttachEngine3D
  AttachmentOffset = pos=(-20.1,18.635,1.635) rot=(0,0,1;0rad)
  BaseFeature = -> Cylinder337
  Height = 0.265
  Length = 0.23
  MapMode = 5
  Placement = pos=(-20.1,18.635,1.635) rot=(0,0,1;0rad)
  Support = -> [XY_Plane185]
  Width = 0.23
FEATURE [PartDesign::Body] Body165  label="pin165"
  Group = -> [Box1664,Box1660,Box1943,Box1662,Box1663,Fillet500,Fillet501,Box1948,Cylinder395,Box1666,Box1634,Fillet495,Box1942,Cylinder337,Box1665]
  Origin = -> Origin185
  Placement = pos=(0,-2,0) rot=(0,0,1;0rad)
  Tip = -> Box1665
FEATURE [PartDesign::SubtractiveBox] Box1952
  AttacherType = Attacher::AttachEngine3D
  AttachmentOffset = pos=(-20.5,18.63,0) rot=(0,0,1;0rad)
  BaseFeature = -> Box1675
  Height = 1.635
  Length = 0.5
  MapMode = 5
  Placement = pos=(-20.5,18.63,0) rot=(0,0,1;0rad)
  Support = -> [XY_Plane180]
  Width = 0.25
FEATURE [PartDesign::SubtractiveBox] Box1947
  AttacherType = Attacher::AttachEngine3D
  AttachmentOffset = pos=(-21.19,18.635,-0.12) rot=(0,-1,0;0.15708rad)
  BaseFeature = -> Box1952
  Height = 0.12
  Length = 0.725
  MapMode = 5
  Placement = pos=(-21.19,18.635,-0.12) rot=(0,-1,0;0.15708rad)
  Support = -> [XY_Plane180]
  Width = 0.25
FEATURE [PartDesign::SubtractiveBox] Box1672
  AttacherType = Attacher::AttachEngine3D
  AttachmentOffset = pos=(-21.5005,18.625,0.235) rot=(0,-1,0;0.174533rad)
  BaseFeature = -> Box1947
  Height = 0.3
  Length = 0.6605
  MapMode = 5
  Placement = pos=(-21.5005,18.625,0.235) rot=(0,-1,0;0.174533rad)
  Support = -> [XY_Plane180]
  Width = 0.25
FEATURE [PartDesign::Fillet] Fillet509
  Base = -> Box1672 [Edge2]
  BaseFeature = -> Box1672
  Placement = pos=(-21.5005,18.625,0.235) rot=(0,-1,0;0.174533rad)
  Radius = 0.05
  SupportTransform = false
FEATURE [PartDesign::Fillet] Fillet499
  Base = -> Fillet509 [Edge33]
  BaseFeature = -> Fillet509
  Placement = pos=(-21.5005,18.625,0.235) rot=(0,-1,0;0.174533rad)
  Radius = 0.5
  SupportTransform = false
FEATURE [PartDesign::AdditiveBox] Box1950
  AttacherType = Attacher::AttachEngine3D
  AttachmentOffset = pos=(-21.1,18.635,0.305) rot=(0,1,0;0.785398rad)
  BaseFeature = -> Fillet499
  Height = 0.375
  Length = 0.2
  MapMode = 5
  Placement = pos=(-21.1,18.635,0.305) rot=(0,1,0;0.785398rad)
  Support = -> [XY_Plane180]
  Width = 0.23
FEATURE [PartDesign::SubtractiveCylinder] Cylinder394
  Angle = 360
  AttacherType = Attacher::AttachEngine3D
  AttachmentOffset = pos=(-21.055,18.935,0.52) rot=(1,0,0;1.5708rad)
  BaseFeature = -> Box1950
  Height = 0.375
  MapMode = 5
  Placement = pos=(-21.055,18.935,0.52) rot=(1,0,0;1.5708rad)
  Radius = 0.205
  Support = -> [XY_Plane180]
FEATURE [PartDesign::SubtractiveBox] Box1945
  AttacherType = Attacher::AttachEngine3D
  AttachmentOffset = pos=(-20.95,18.635,0.53) rot=(0,0,1;0rad)
  BaseFeature = -> Cylinder394
  Height = 0.5
  Length = 0.1
  MapMode = 5
  Placement = pos=(-20.95,18.635,0.53) rot=(0,0,1;0rad)
  Support = -> [XY_Plane180]
  Width = 0.23
FEATURE [PartDesign::SubtractiveBox] Box1944
  AttacherType = Attacher::AttachEngine3D
  AttachmentOffset = pos=(-21.15,18.635,0.297) rot=(0,-1,0;0.174533rad)
  BaseFeature = -> Box1945
  Height = 0.115
  Length = 0.115
  MapMode = 5
  Placement = pos=(-21.15,18.635,0.297) rot=(0,-1,0;0.174533rad)
  Support = -> [XY_Plane180]
  Width = 0.23
FEATURE [PartDesign::Fillet] Fillet507
  Base = -> Box1944 [Edge28]
  BaseFeature = -> Box1944
  Placement = pos=(-21.15,18.635,0.297) rot=(0,-1,0;0.174533rad)
  Radius = 0.375
  SupportTransform = false
FEATURE [PartDesign::AdditiveBox] Box1949
  AttacherType = Attacher::AttachEngine3D
  AttachmentOffset = pos=(-20.7,18.635,1.55) rot=(0,1,0;0.785398rad)
  BaseFeature = -> Fillet507
  Height = 0.375
  Length = 0.23
  MapMode = 5
  Placement = pos=(-20.7,18.635,1.55) rot=(0,1,0;0.785398rad)
  Support = -> [XY_Plane180]
  Width = 0.23
FEATURE [PartDesign::SubtractiveCylinder] Cylinder312
  Angle = 360
  AttacherType = Attacher::AttachEngine3D
  AttachmentOffset = pos=(-20.271,18.635,1.4056) rot=(-1,0,0;1.5708rad)
  BaseFeature = -> Box1949
  Height = 0.23
  MapMode = 5
  Placement = pos=(-20.271,18.635,1.4056) rot=(-1,0,0;1.5708rad)
  Radius = 0.23
  Support = -> [XY_Plane180]
FEATURE [PartDesign::AdditiveBox] Box1951
  AttacherType = Attacher::AttachEngine3D
  AttachmentOffset = pos=(-20.1,18.635,1.635) rot=(0,0,1;0rad)
  BaseFeature = -> Cylinder312
  Height = 0.265
  Length = 0.23
  MapMode = 5
  Placement = pos=(-20.1,18.635,1.635) rot=(0,0,1;0rad)
  Support = -> [XY_Plane180]
  Width = 0.23
FEATURE [PartDesign::Body] Body167  label="pin167"
  Group = -> [Box1684,Box1675,Box1952,Box1947,Box1672,Fillet509,Fillet499,Box1950,Cylinder394,Box1945,Box1944,Fillet507,Box1949,Cylinder312,Box1951]
  Origin = -> Origin188
  Placement = pos=(0,-1.5,0) rot=(0,0,1;0rad)
  Tip = -> Box1951
FEATURE [App::Part] Part015  label="Pin-set014"
  Group = -> [Body168,Body166,Body170,Body167,Body165,Body169,Body174,Body175,Body171,Body172,Body173,Body176]
  Origin = -> Origin196
  Placement = pos=(0,-6,0) rot=(0,0,1;0rad)
FEATURE [PartDesign::SubtractiveBox] Box1953
  AttacherType = Attacher::AttachEngine3D
  AttachmentOffset = pos=(-21.35,18.635,0.35) rot=(0,0,1;0rad)
  BaseFeature = -> Box1657
  Height = 1.55
  Length = 0.5
  MapMode = 5
  Placement = pos=(-21.35,18.635,0.35) rot=(0,0,1;0rad)
  Support = -> [XY_Plane169]
  Width = 0.23
FEATURE [PartDesign::SubtractiveBox] Box1631
  AttacherType = Attacher::AttachEngine3D
  AttachmentOffset = pos=(-20.5,18.63,0) rot=(0,0,1;0rad)
  BaseFeature = -> Box1953
  Height = 1.635
  Length = 0.5
  MapMode = 5
  Placement = pos=(-20.5,18.63,0) rot=(0,0,1;0rad)
  Support = -> [XY_Plane169]
  Width = 0.25
FEATURE [PartDesign::SubtractiveBox] Box1633
  AttacherType = Attacher::AttachEngine3D
  AttachmentOffset = pos=(-21.19,18.635,-0.12) rot=(0,-1,0;0.15708rad)
  BaseFeature = -> Box1631
  Height = 0.12
  Length = 0.725
  MapMode = 5
  Placement = pos=(-21.19,18.635,-0.12) rot=(0,-1,0;0.15708rad)
  Support = -> [XY_Plane169]
  Width = 0.25
FEATURE [PartDesign::SubtractiveBox] Box1654
  AttacherType = Attacher::AttachEngine3D
  AttachmentOffset = pos=(-21.5005,18.625,0.235) rot=(0,-1,0;0.174533rad)
  BaseFeature = -> Box1633
  Height = 0.3
  Length = 0.6605
  MapMode = 5
  Placement = pos=(-21.5005,18.625,0.235) rot=(0,-1,0;0.174533rad)
  Support = -> [XY_Plane169]
  Width = 0.25
FEATURE [PartDesign::Fillet] Fillet472
  Base = -> Box1654 [Edge2]
  BaseFeature = -> Box1654
  Placement = pos=(-21.5005,18.625,0.235) rot=(0,-1,0;0.174533rad)
  Radius = 0.05
  SupportTransform = false
FEATURE [PartDesign::Fillet] Fillet456
  Base = -> Fillet472 [Edge33]
  BaseFeature = -> Fillet472
  Placement = pos=(-21.5005,18.625,0.235) rot=(0,-1,0;0.174533rad)
  Radius = 0.5
  SupportTransform = false
FEATURE [PartDesign::AdditiveBox] Box1554
  AttacherType = Attacher::AttachEngine3D
  AttachmentOffset = pos=(-21.1,18.635,0.305) rot=(0,1,0;0.785398rad)
  BaseFeature = -> Fillet456
  Height = 0.375
  Length = 0.2
  MapMode = 5
  Placement = pos=(-21.1,18.635,0.305) rot=(0,1,0;0.785398rad)
  Support = -> [XY_Plane169]
  Width = 0.23
FEATURE [PartDesign::SubtractiveCylinder] Cylinder323
  Angle = 360
  AttacherType = Attacher::AttachEngine3D
  AttachmentOffset = pos=(-21.055,18.935,0.52) rot=(1,0,0;1.5708rad)
  BaseFeature = -> Box1554
  Height = 0.375
  MapMode = 5
  Placement = pos=(-21.055,18.935,0.52) rot=(1,0,0;1.5708rad)
  Radius = 0.205
  Support = -> [XY_Plane169]
FEATURE [PartDesign::SubtractiveBox] Box1608
  AttacherType = Attacher::AttachEngine3D
  AttachmentOffset = pos=(-20.95,18.635,0.53) rot=(0,0,1;0rad)
  BaseFeature = -> Cylinder323
  Height = 0.5
  Length = 0.1
  MapMode = 5
  Placement = pos=(-20.95,18.635,0.53) rot=(0,0,1;0rad)
  Support = -> [XY_Plane169]
  Width = 0.23
FEATURE [PartDesign::SubtractiveBox] Box1607
  AttacherType = Attacher::AttachEngine3D
  AttachmentOffset = pos=(-21.15,18.635,0.297) rot=(0,-1,0;0.174533rad)
  BaseFeature = -> Box1608
  Height = 0.115
  Length = 0.115
  MapMode = 5
  Placement = pos=(-21.15,18.635,0.297) rot=(0,-1,0;0.174533rad)
  Support = -> [XY_Plane169]
  Width = 0.23
FEATURE [PartDesign::Fillet] Fillet599
  Base = -> Box1607 [Edge28]
  BaseFeature = -> Box1607
  Placement = pos=(-21.15,18.635,0.297) rot=(0,-1,0;0.174533rad)
  Radius = 0.375
  SupportTransform = false
FEATURE [PartDesign::AdditiveBox] Box1635
  AttacherType = Attacher::AttachEngine3D
  AttachmentOffset = pos=(-20.7,18.635,1.55) rot=(0,1,0;0.785398rad)
  BaseFeature = -> Fillet599
  Height = 0.375
  Length = 0.23
  MapMode = 5
  Placement = pos=(-20.7,18.635,1.55) rot=(0,1,0;0.785398rad)
  Support = -> [XY_Plane169]
  Width = 0.23
FEATURE [PartDesign::SubtractiveCylinder] Cylinder328
  Angle = 360
  AttacherType = Attacher::AttachEngine3D
  AttachmentOffset = pos=(-20.271,18.635,1.4056) rot=(-1,0,0;1.5708rad)
  BaseFeature = -> Box1635
  Height = 0.23
  MapMode = 5
  Placement = pos=(-20.271,18.635,1.4056) rot=(-1,0,0;1.5708rad)
  Radius = 0.23
  Support = -> [XY_Plane169]
FEATURE [PartDesign::AdditiveBox] Box1641
  AttacherType = Attacher::AttachEngine3D
  AttachmentOffset = pos=(-20.1,18.635,1.635) rot=(0,0,1;0rad)
  BaseFeature = -> Cylinder328
  Height = 0.265
  Length = 0.23
  MapMode = 5
  Placement = pos=(-20.1,18.635,1.635) rot=(0,0,1;0rad)
  Support = -> [XY_Plane169]
  Width = 0.23
FEATURE [PartDesign::Body] Body153  label="pin153"
  Group = -> [Box1657,Box1953,Box1631,Box1633,Box1654,Fillet472,Fillet456,Box1554,Cylinder323,Box1608,Box1607,Fillet599,Box1635,Cylinder328,Box1641]
  Origin = -> Origin168
  Tip = -> Box1641
FEATURE [App::Part] Part017  label="Pin-set015"
  Group = -> [Body153,Body154,Body155,Body156,Body157,Body158,Body159,Body160,Body161,Body162,Body163,Body164]
  Origin = -> Origin182
FEATURE [PartDesign::AdditiveBox] Box1957
  AttacherType = Attacher::AttachEngine3D
  AttachmentOffset = pos=(-21.1,18.635,0.305) rot=(0,1,0;0.785398rad)
  BaseFeature = -> Fillet589
  Height = 0.375
  Length = 0.2
  MapMode = 5
  Placement = pos=(-21.1,18.635,0.305) rot=(0,1,0;0.785398rad)
  Support = -> [XY_Plane215]
  Width = 0.23
FEATURE [PartDesign::SubtractiveCylinder] Cylinder390
  Angle = 360
  AttacherType = Attacher::AttachEngine3D
  AttachmentOffset = pos=(-21.055,18.935,0.52) rot=(1,0,0;1.5708rad)
  BaseFeature = -> Box1957
  Height = 0.375
  MapMode = 5
  Placement = pos=(-21.055,18.935,0.52) rot=(1,0,0;1.5708rad)
  Radius = 0.205
  Support = -> [XY_Plane215]
FEATURE [PartDesign::SubtractiveBox] Box1933
  AttacherType = Attacher::AttachEngine3D
  AttachmentOffset = pos=(-20.95,18.635,0.53) rot=(0,0,1;0rad)
  BaseFeature = -> Cylinder390
  Height = 0.5
  Length = 0.1
  MapMode = 5
  Placement = pos=(-20.95,18.635,0.53) rot=(0,0,1;0rad)
  Support = -> [XY_Plane215]
  Width = 0.23
FEATURE [PartDesign::SubtractiveBox] Box1922
  AttacherType = Attacher::AttachEngine3D
  AttachmentOffset = pos=(-21.15,18.635,0.297) rot=(0,-1,0;0.174533rad)
  BaseFeature = -> Box1933
  Height = 0.115
  Length = 0.115
  MapMode = 5
  Placement = pos=(-21.15,18.635,0.297) rot=(0,-1,0;0.174533rad)
  Support = -> [XY_Plane215]
  Width = 0.23
FEATURE [PartDesign::Fillet] Fillet591
  Base = -> Box1922 [Edge28]
  BaseFeature = -> Box1922
  Placement = pos=(-21.15,18.635,0.297) rot=(0,-1,0;0.174533rad)
  Radius = 0.375
  SupportTransform = false
FEATURE [PartDesign::AdditiveBox] Box1931
  AttacherType = Attacher::AttachEngine3D
  AttachmentOffset = pos=(-20.7,18.635,1.55) rot=(0,1,0;0.785398rad)
  BaseFeature = -> Fillet591
  Height = 0.375
  Length = 0.23
  MapMode = 5
  Placement = pos=(-20.7,18.635,1.55) rot=(0,1,0;0.785398rad)
  Support = -> [XY_Plane215]
  Width = 0.23
FEATURE [PartDesign::SubtractiveCylinder] Cylinder389
  Angle = 360
  AttacherType = Attacher::AttachEngine3D
  AttachmentOffset = pos=(-20.271,18.635,1.4056) rot=(-1,0,0;1.5708rad)
  BaseFeature = -> Box1931
  Height = 0.23
  MapMode = 5
  Placement = pos=(-20.271,18.635,1.4056) rot=(-1,0,0;1.5708rad)
  Radius = 0.23
  Support = -> [XY_Plane215]
FEATURE [PartDesign::AdditiveBox] Box1916
  AttacherType = Attacher::AttachEngine3D
  AttachmentOffset = pos=(-20.1,18.635,1.635) rot=(0,0,1;0rad)
  BaseFeature = -> Cylinder389
  Height = 0.265
  Length = 0.23
  MapMode = 5
  Placement = pos=(-20.1,18.635,1.635) rot=(0,0,1;0rad)
  Support = -> [XY_Plane215]
  Width = 0.23
FEATURE [PartDesign::Body] Body196  label="pin196"
  Group = -> [Box1917,Box1919,Box1887,Box1932,Box1934,Fillet586,Fillet589,Box1957,Cylinder390,Box1933,Box1922,Fillet591,Box1931,Cylinder389,Box1916]
  Origin = -> Origin227
  Placement = pos=(0,-4,0) rot=(0,0,1;0rad)
  Tip = -> Box1916
FEATURE [PartDesign::SubtractiveBox] Box1960
  AttacherType = Attacher::AttachEngine3D
  AttachmentOffset = pos=(-21.5005,18.625,0.235) rot=(0,-1,0;0.174533rad)
  BaseFeature = -> Box1873
  Height = 0.3
  Length = 0.6605
  MapMode = 5
  Placement = pos=(-21.5005,18.625,0.235) rot=(0,-1,0;0.174533rad)
  Support = -> [XY_Plane213]
  Width = 0.25
FEATURE [PartDesign::Fillet] Fillet598
  Base = -> Box1960 [Edge2]
  BaseFeature = -> Box1960
  Placement = pos=(-21.5005,18.625,0.235) rot=(0,-1,0;0.174533rad)
  Radius = 0.05
  SupportTransform = false
FEATURE [PartDesign::Fillet] Fillet580
  Base = -> Fillet598 [Edge33]
  BaseFeature = -> Fillet598
  Placement = pos=(-21.5005,18.625,0.235) rot=(0,-1,0;0.174533rad)
  Radius = 0.5
  SupportTransform = false
FEATURE [PartDesign::AdditiveBox] Box1850
  AttacherType = Attacher::AttachEngine3D
  AttachmentOffset = pos=(-21.1,18.635,0.305) rot=(0,1,0;0.785398rad)
  BaseFeature = -> Fillet580
  Height = 0.375
  Length = 0.2
  MapMode = 5
  Placement = pos=(-21.1,18.635,0.305) rot=(0,1,0;0.785398rad)
  Support = -> [XY_Plane213]
  Width = 0.23
FEATURE [PartDesign::SubtractiveCylinder] Cylinder375
  Angle = 360
  AttacherType = Attacher::AttachEngine3D
  AttachmentOffset = pos=(-21.055,18.935,0.52) rot=(1,0,0;1.5708rad)
  BaseFeature = -> Box1850
  Height = 0.375
  MapMode = 5
  Placement = pos=(-21.055,18.935,0.52) rot=(1,0,0;1.5708rad)
  Radius = 0.205
  Support = -> [XY_Plane213]
FEATURE [PartDesign::SubtractiveBox] Box1849
  AttacherType = Attacher::AttachEngine3D
  AttachmentOffset = pos=(-20.95,18.635,0.53) rot=(0,0,1;0rad)
  BaseFeature = -> Cylinder375
  Height = 0.5
  Length = 0.1
  MapMode = 5
  Placement = pos=(-20.95,18.635,0.53) rot=(0,0,1;0rad)
  Support = -> [XY_Plane213]
  Width = 0.23
FEATURE [PartDesign::SubtractiveBox] Box1867
  AttacherType = Attacher::AttachEngine3D
  AttachmentOffset = pos=(-21.15,18.635,0.297) rot=(0,-1,0;0.174533rad)
  BaseFeature = -> Box1849
  Height = 0.115
  Length = 0.115
  MapMode = 5
  Placement = pos=(-21.15,18.635,0.297) rot=(0,-1,0;0.174533rad)
  Support = -> [XY_Plane213]
  Width = 0.23
FEATURE [PartDesign::Fillet] Fillet593
  Base = -> Box1867 [Edge28]
  BaseFeature = -> Box1867
  Placement = pos=(-21.15,18.635,0.297) rot=(0,-1,0;0.174533rad)
  Radius = 0.375
  SupportTransform = false
FEATURE [PartDesign::AdditiveBox] Box1874
  AttacherType = Attacher::AttachEngine3D
  AttachmentOffset = pos=(-20.7,18.635,1.55) rot=(0,1,0;0.785398rad)
  BaseFeature = -> Fillet593
  Height = 0.375
  Length = 0.23
  MapMode = 5
  Placement = pos=(-20.7,18.635,1.55) rot=(0,1,0;0.785398rad)
  Support = -> [XY_Plane213]
  Width = 0.23
FEATURE [PartDesign::SubtractiveCylinder] Cylinder377
  Angle = 360
  AttacherType = Attacher::AttachEngine3D
  AttachmentOffset = pos=(-20.271,18.635,1.4056) rot=(-1,0,0;1.5708rad)
  BaseFeature = -> Box1874
  Height = 0.23
  MapMode = 5
  Placement = pos=(-20.271,18.635,1.4056) rot=(-1,0,0;1.5708rad)
  Radius = 0.23
  Support = -> [XY_Plane213]
FEATURE [PartDesign::AdditiveBox] Box1868
  AttacherType = Attacher::AttachEngine3D
  AttachmentOffset = pos=(-20.1,18.635,1.635) rot=(0,0,1;0rad)
  BaseFeature = -> Cylinder377
  Height = 0.265
  Length = 0.23
  MapMode = 5
  Placement = pos=(-20.1,18.635,1.635) rot=(0,0,1;0rad)
  Support = -> [XY_Plane213]
  Width = 0.23
FEATURE [PartDesign::Body] Body195  label="pin195"
  Group = -> [Box1891,Box1883,Box1871,Box1873,Box1960,Fillet598,Fillet580,Box1850,Cylinder375,Box1849,Box1867,Fillet593,Box1874,Cylinder377,Box1868]
  Origin = -> Origin210
  Placement = pos=(0,-4.5,0) rot=(0,0,1;0rad)
  Tip = -> Box1868
FEATURE [PartDesign::SubtractiveBox] Box1965
  AttacherType = Attacher::AttachEngine3D
  AttachmentOffset = pos=(-21.19,18.635,-0.12) rot=(0,-1,0;0.15708rad)
  BaseFeature = -> Box1893
  Height = 0.12
  Length = 0.725
  MapMode = 5
  Placement = pos=(-21.19,18.635,-0.12) rot=(0,-1,0;0.15708rad)
  Support = -> [XY_Plane217]
  Width = 0.25
FEATURE [PartDesign::SubtractiveBox] Box1921
  AttacherType = Attacher::AttachEngine3D
  AttachmentOffset = pos=(-21.5005,18.625,0.235) rot=(0,-1,0;0.174533rad)
  BaseFeature = -> Box1965
  Height = 0.3
  Length = 0.6605
  MapMode = 5
  Placement = pos=(-21.5005,18.625,0.235) rot=(0,-1,0;0.174533rad)
  Support = -> [XY_Plane217]
  Width = 0.25
FEATURE [PartDesign::Fillet] Fillet597
  Base = -> Box1921 [Edge2]
  BaseFeature = -> Box1921
  Placement = pos=(-21.5005,18.625,0.235) rot=(0,-1,0;0.174533rad)
  Radius = 0.05
  SupportTransform = false
FEATURE [PartDesign::Fillet] Fillet596
  Base = -> Fillet597 [Edge33]
  BaseFeature = -> Fillet597
  Placement = pos=(-21.5005,18.625,0.235) rot=(0,-1,0;0.174533rad)
  Radius = 0.5
  SupportTransform = false
FEATURE [PartDesign::AdditiveBox] Box1872
  AttacherType = Attacher::AttachEngine3D
  AttachmentOffset = pos=(-21.1,18.635,0.305) rot=(0,1,0;0.785398rad)
  BaseFeature = -> Fillet596
  Height = 0.375
  Length = 0.2
  MapMode = 5
  Placement = pos=(-21.1,18.635,0.305) rot=(0,1,0;0.785398rad)
  Support = -> [XY_Plane217]
  Width = 0.23
FEATURE [PartDesign::SubtractiveCylinder] Cylinder380
  Angle = 360
  AttacherType = Attacher::AttachEngine3D
  AttachmentOffset = pos=(-21.055,18.935,0.52) rot=(1,0,0;1.5708rad)
  BaseFeature = -> Box1872
  Height = 0.375
  MapMode = 5
  Placement = pos=(-21.055,18.935,0.52) rot=(1,0,0;1.5708rad)
  Radius = 0.205
  Support = -> [XY_Plane217]
FEATURE [PartDesign::SubtractiveBox] Box1880
  AttacherType = Attacher::AttachEngine3D
  AttachmentOffset = pos=(-20.95,18.635,0.53) rot=(0,0,1;0rad)
  BaseFeature = -> Cylinder380
  Height = 0.5
  Length = 0.1
  MapMode = 5
  Placement = pos=(-20.95,18.635,0.53) rot=(0,0,1;0rad)
  Support = -> [XY_Plane217]
  Width = 0.23
FEATURE [PartDesign::SubtractiveBox] Box1897
  AttacherType = Attacher::AttachEngine3D
  AttachmentOffset = pos=(-21.15,18.635,0.297) rot=(0,-1,0;0.174533rad)
  BaseFeature = -> Box1880
  Height = 0.115
  Length = 0.115
  MapMode = 5
  Placement = pos=(-21.15,18.635,0.297) rot=(0,-1,0;0.174533rad)
  Support = -> [XY_Plane217]
  Width = 0.23
FEATURE [PartDesign::Fillet] Fillet588
  Base = -> Box1897 [Edge28]
  BaseFeature = -> Box1897
  Placement = pos=(-21.15,18.635,0.297) rot=(0,-1,0;0.174533rad)
  Radius = 0.375
  SupportTransform = false
FEATURE [PartDesign::AdditiveBox] Box1899
  AttacherType = Attacher::AttachEngine3D
  AttachmentOffset = pos=(-20.7,18.635,1.55) rot=(0,1,0;0.785398rad)
  BaseFeature = -> Fillet588
  Height = 0.375
  Length = 0.23
  MapMode = 5
  Placement = pos=(-20.7,18.635,1.55) rot=(0,1,0;0.785398rad)
  Support = -> [XY_Plane217]
  Width = 0.23
FEATURE [PartDesign::SubtractiveCylinder] Cylinder383
  Angle = 360
  AttacherType = Attacher::AttachEngine3D
  AttachmentOffset = pos=(-20.271,18.635,1.4056) rot=(-1,0,0;1.5708rad)
  BaseFeature = -> Box1899
  Height = 0.23
  MapMode = 5
  Placement = pos=(-20.271,18.635,1.4056) rot=(-1,0,0;1.5708rad)
  Radius = 0.23
  Support = -> [XY_Plane217]
FEATURE [PartDesign::AdditiveBox] Box1956
  AttacherType = Attacher::AttachEngine3D
  AttachmentOffset = pos=(-20.1,18.635,1.635) rot=(0,0,1;0rad)
  BaseFeature = -> Cylinder383
  Height = 0.265
  Length = 0.23
  MapMode = 5
  Placement = pos=(-20.1,18.635,1.635) rot=(0,0,1;0rad)
  Support = -> [XY_Plane217]
  Width = 0.23
FEATURE [PartDesign::Body] Body197  label="pin197"
  Group = -> [Box1928,Box1940,Box1893,Box1965,Box1921,Fillet597,Fillet596,Box1872,Cylinder380,Box1880,Box1897,Fillet588,Box1899,Cylinder383,Box1956]
  Origin = -> Origin221
  Placement = pos=(0,-3,0) rot=(0,0,1;0rad)
  Tip = -> Box1956
FEATURE [PartDesign::SubtractiveBox] Box1966
  AttacherType = Attacher::AttachEngine3D
  AttachmentOffset = pos=(-20.5,18.63,0) rot=(0,0,1;0rad)
  BaseFeature = -> Box1937
  Height = 1.635
  Length = 0.5
  MapMode = 5
  Placement = pos=(-20.5,18.63,0) rot=(0,0,1;0rad)
  Support = -> [XY_Plane218]
  Width = 0.25
FEATURE [PartDesign::SubtractiveBox] Box1935
  AttacherType = Attacher::AttachEngine3D
  AttachmentOffset = pos=(-21.19,18.635,-0.12) rot=(0,-1,0;0.15708rad)
  BaseFeature = -> Box1966
  Height = 0.12
  Length = 0.725
  MapMode = 5
  Placement = pos=(-21.19,18.635,-0.12) rot=(0,-1,0;0.15708rad)
  Support = -> [XY_Plane218]
  Width = 0.25
FEATURE [PartDesign::SubtractiveBox] Box1926
  AttacherType = Attacher::AttachEngine3D
  AttachmentOffset = pos=(-21.5005,18.625,0.235) rot=(0,-1,0;0.174533rad)
  BaseFeature = -> Box1935
  Height = 0.3
  Length = 0.6605
  MapMode = 5
  Placement = pos=(-21.5005,18.625,0.235) rot=(0,-1,0;0.174533rad)
  Support = -> [XY_Plane218]
  Width = 0.25
FEATURE [PartDesign::Fillet] Fillet594
  Base = -> Box1926 [Edge2]
  BaseFeature = -> Box1926
  Placement = pos=(-21.5005,18.625,0.235) rot=(0,-1,0;0.174533rad)
  Radius = 0.05
  SupportTransform = false
FEATURE [PartDesign::Fillet] Fillet581
  Base = -> Fillet594 [Edge33]
  BaseFeature = -> Fillet594
  Placement = pos=(-21.5005,18.625,0.235) rot=(0,-1,0;0.174533rad)
  Radius = 0.5
  SupportTransform = false
FEATURE [PartDesign::AdditiveBox] Box1964
  AttacherType = Attacher::AttachEngine3D
  AttachmentOffset = pos=(-21.1,18.635,0.305) rot=(0,1,0;0.785398rad)
  BaseFeature = -> Fillet581
  Height = 0.375
  Length = 0.2
  MapMode = 5
  Placement = pos=(-21.1,18.635,0.305) rot=(0,1,0;0.785398rad)
  Support = -> [XY_Plane218]
  Width = 0.23
FEATURE [PartDesign::SubtractiveCylinder] Cylinder397
  Angle = 360
  AttacherType = Attacher::AttachEngine3D
  AttachmentOffset = pos=(-21.055,18.935,0.52) rot=(1,0,0;1.5708rad)
  BaseFeature = -> Box1964
  Height = 0.375
  MapMode = 5
  Placement = pos=(-21.055,18.935,0.52) rot=(1,0,0;1.5708rad)
  Radius = 0.205
  Support = -> [XY_Plane218]
FEATURE [PartDesign::SubtractiveBox] Box1955
  AttacherType = Attacher::AttachEngine3D
  AttachmentOffset = pos=(-20.95,18.635,0.53) rot=(0,0,1;0rad)
  BaseFeature = -> Cylinder397
  Height = 0.5
  Length = 0.1
  MapMode = 5
  Placement = pos=(-20.95,18.635,0.53) rot=(0,0,1;0rad)
  Support = -> [XY_Plane218]
  Width = 0.23
FEATURE [PartDesign::SubtractiveBox] Box1898
  AttacherType = Attacher::AttachEngine3D
  AttachmentOffset = pos=(-21.15,18.635,0.297) rot=(0,-1,0;0.174533rad)
  BaseFeature = -> Box1955
  Height = 0.115
  Length = 0.115
  MapMode = 5
  Placement = pos=(-21.15,18.635,0.297) rot=(0,-1,0;0.174533rad)
  Support = -> [XY_Plane218]
  Width = 0.23
FEATURE [PartDesign::Fillet] Fillet583
  Base = -> Box1898 [Edge28]
  BaseFeature = -> Box1898
  Placement = pos=(-21.15,18.635,0.297) rot=(0,-1,0;0.174533rad)
  Radius = 0.375
  SupportTransform = false
FEATURE [PartDesign::AdditiveBox] Box1963
  AttacherType = Attacher::AttachEngine3D
  AttachmentOffset = pos=(-20.7,18.635,1.55) rot=(0,1,0;0.785398rad)
  BaseFeature = -> Fillet583
  Height = 0.375
  Length = 0.23
  MapMode = 5
  Placement = pos=(-20.7,18.635,1.55) rot=(0,1,0;0.785398rad)
  Support = -> [XY_Plane218]
  Width = 0.23
FEATURE [PartDesign::SubtractiveCylinder] Cylinder396
  Angle = 360
  AttacherType = Attacher::AttachEngine3D
  AttachmentOffset = pos=(-20.271,18.635,1.4056) rot=(-1,0,0;1.5708rad)
  BaseFeature = -> Box1963
  Height = 0.23
  MapMode = 5
  Placement = pos=(-20.271,18.635,1.4056) rot=(-1,0,0;1.5708rad)
  Radius = 0.23
  Support = -> [XY_Plane218]
FEATURE [PartDesign::AdditiveBox] Box1929
  AttacherType = Attacher::AttachEngine3D
  AttachmentOffset = pos=(-20.1,18.635,1.635) rot=(0,0,1;0rad)
  BaseFeature = -> Cylinder396
  Height = 0.265
  Length = 0.23
  MapMode = 5
  Placement = pos=(-20.1,18.635,1.635) rot=(0,0,1;0rad)
  Support = -> [XY_Plane218]
  Width = 0.23
FEATURE [PartDesign::Body] Body194  label="pin194"
  Group = -> [Box1920,Box1937,Box1966,Box1935,Box1926,Fillet594,Fillet581,Box1964,Cylinder397,Box1955,Box1898,Fillet583,Box1963,Cylinder396,Box1929]
  Origin = -> Origin226
  Placement = pos=(0,-3.5,0) rot=(0,0,1;0rad)
  Tip = -> Box1929
FEATURE [PartDesign::AdditiveBox] Box1983
  AttacherType = Attacher::AttachEngine3D
  AttachmentOffset = pos=(-21.3,18.635,0) rot=(0,0,1;0rad)
  Height = 1.9
  Length = 1.3
  MapMode = 5
  Placement = pos=(-21.3,18.635,0) rot=(0,0,1;0rad)
  Support = -> [XY_Plane214]
  Width = 0.23
FEATURE [PartDesign::SubtractiveBox] Box1971
  AttacherType = Attacher::AttachEngine3D
  AttachmentOffset = pos=(-21.35,18.635,0.35) rot=(0,0,1;0rad)
  BaseFeature = -> Box1983
  Height = 1.55
  Length = 0.5
  MapMode = 5
  Placement = pos=(-21.35,18.635,0.35) rot=(0,0,1;0rad)
  Support = -> [XY_Plane214]
  Width = 0.23
FEATURE [PartDesign::SubtractiveBox] Box1954
  AttacherType = Attacher::AttachEngine3D
  AttachmentOffset = pos=(-20.5,18.63,0) rot=(0,0,1;0rad)
  BaseFeature = -> Box1971
  Height = 1.635
  Length = 0.5
  MapMode = 5
  Placement = pos=(-20.5,18.63,0) rot=(0,0,1;0rad)
  Support = -> [XY_Plane214]
  Width = 0.25
FEATURE [PartDesign::SubtractiveBox] Box1976
  AttacherType = Attacher::AttachEngine3D
  AttachmentOffset = pos=(-21.19,18.635,-0.12) rot=(0,-1,0;0.15708rad)
  BaseFeature = -> Box1954
  Height = 0.12
  Length = 0.725
  MapMode = 5
  Placement = pos=(-21.19,18.635,-0.12) rot=(0,-1,0;0.15708rad)
  Support = -> [XY_Plane214]
  Width = 0.25
FEATURE [PartDesign::SubtractiveBox] Box1969
  AttacherType = Attacher::AttachEngine3D
  AttachmentOffset = pos=(-21.5005,18.625,0.235) rot=(0,-1,0;0.174533rad)
  BaseFeature = -> Box1976
  Height = 0.3
  Length = 0.6605
  MapMode = 5
  Placement = pos=(-21.5005,18.625,0.235) rot=(0,-1,0;0.174533rad)
  Support = -> [XY_Plane214]
  Width = 0.25
FEATURE [PartDesign::Fillet] Fillet571
  Base = -> Box1969 [Edge2]
  BaseFeature = -> Box1969
  Placement = pos=(-21.5005,18.625,0.235) rot=(0,-1,0;0.174533rad)
  Radius = 0.05
  SupportTransform = false
FEATURE [PartDesign::Fillet] Fillet573
  Base = -> Fillet571 [Edge33]
  BaseFeature = -> Fillet571
  Placement = pos=(-21.5005,18.625,0.235) rot=(0,-1,0;0.174533rad)
  Radius = 0.5
  SupportTransform = false
FEATURE [PartDesign::AdditiveBox] Box1961
  AttacherType = Attacher::AttachEngine3D
  AttachmentOffset = pos=(-21.1,18.635,0.305) rot=(0,1,0;0.785398rad)
  BaseFeature = -> Fillet573
  Height = 0.375
  Length = 0.2
  MapMode = 5
  Placement = pos=(-21.1,18.635,0.305) rot=(0,1,0;0.785398rad)
  Support = -> [XY_Plane214]
  Width = 0.23
FEATURE [PartDesign::SubtractiveCylinder] Cylinder398
  Angle = 360
  AttacherType = Attacher::AttachEngine3D
  AttachmentOffset = pos=(-21.055,18.935,0.52) rot=(1,0,0;1.5708rad)
  BaseFeature = -> Box1961
  Height = 0.375
  MapMode = 5
  Placement = pos=(-21.055,18.935,0.52) rot=(1,0,0;1.5708rad)
  Radius = 0.205
  Support = -> [XY_Plane214]
FEATURE [PartDesign::SubtractiveBox] Box1975
  AttacherType = Attacher::AttachEngine3D
  AttachmentOffset = pos=(-20.95,18.635,0.53) rot=(0,0,1;0rad)
  BaseFeature = -> Cylinder398
  Height = 0.5
  Length = 0.1
  MapMode = 5
  Placement = pos=(-20.95,18.635,0.53) rot=(0,0,1;0rad)
  Support = -> [XY_Plane214]
  Width = 0.23
FEATURE [PartDesign::SubtractiveBox] Box1962
  AttacherType = Attacher::AttachEngine3D
  AttachmentOffset = pos=(-21.15,18.635,0.297) rot=(0,-1,0;0.174533rad)
  BaseFeature = -> Box1975
  Height = 0.115
  Length = 0.115
  MapMode = 5
  Placement = pos=(-21.15,18.635,0.297) rot=(0,-1,0;0.174533rad)
  Support = -> [XY_Plane214]
  Width = 0.23
FEATURE [PartDesign::Fillet] Fillet587
  Base = -> Box1962 [Edge28]
  BaseFeature = -> Box1962
  Placement = pos=(-21.15,18.635,0.297) rot=(0,-1,0;0.174533rad)
  Radius = 0.375
  SupportTransform = false
FEATURE [PartDesign::AdditiveBox] Box1970
  AttacherType = Attacher::AttachEngine3D
  AttachmentOffset = pos=(-20.7,18.635,1.55) rot=(0,1,0;0.785398rad)
  BaseFeature = -> Fillet587
  Height = 0.375
  Length = 0.23
  MapMode = 5
  Placement = pos=(-20.7,18.635,1.55) rot=(0,1,0;0.785398rad)
  Support = -> [XY_Plane214]
  Width = 0.23
FEATURE [PartDesign::SubtractiveCylinder] Cylinder400
  Angle = 360
  AttacherType = Attacher::AttachEngine3D
  AttachmentOffset = pos=(-20.271,18.635,1.4056) rot=(-1,0,0;1.5708rad)
  BaseFeature = -> Box1970
  Height = 0.23
  MapMode = 5
  Placement = pos=(-20.271,18.635,1.4056) rot=(-1,0,0;1.5708rad)
  Radius = 0.23
  Support = -> [XY_Plane214]
FEATURE [PartDesign::AdditiveBox] Box1979
  AttacherType = Attacher::AttachEngine3D
  AttachmentOffset = pos=(-20.1,18.635,1.635) rot=(0,0,1;0rad)
  BaseFeature = -> Cylinder400
  Height = 0.265
  Length = 0.23
  MapMode = 5
  Placement = pos=(-20.1,18.635,1.635) rot=(0,0,1;0rad)
  Support = -> [XY_Plane214]
  Width = 0.23
FEATURE [PartDesign::Body] Body189  label="pin189"
  Group = -> [Box1983,Box1971,Box1954,Box1976,Box1969,Fillet571,Fillet573,Box1961,Cylinder398,Box1975,Box1962,Fillet587,Box1970,Cylinder400,Box1979]
  Origin = -> Origin206
  Placement = pos=(0,-0.5,0) rot=(0,0,1;0rad)
  Tip = -> Box1979
FEATURE [PartDesign::SubtractiveBox] Box1987
  AttacherType = Attacher::AttachEngine3D
  AttachmentOffset = pos=(-20.5,18.63,0) rot=(0,0,1;0rad)
  BaseFeature = -> Box1851
  Height = 1.635
  Length = 0.5
  MapMode = 5
  Placement = pos=(-20.5,18.63,0) rot=(0,0,1;0rad)
  Support = -> [XY_Plane181]
  Width = 0.25
FEATURE [PartDesign::SubtractiveBox] Box1974
  AttacherType = Attacher::AttachEngine3D
  AttachmentOffset = pos=(-21.19,18.635,-0.12) rot=(0,-1,0;0.15708rad)
  BaseFeature = -> Box1987
  Height = 0.12
  Length = 0.725
  MapMode = 5
  Placement = pos=(-21.19,18.635,-0.12) rot=(0,-1,0;0.15708rad)
  Support = -> [XY_Plane181]
  Width = 0.25
FEATURE [PartDesign::SubtractiveBox] Box1856
  AttacherType = Attacher::AttachEngine3D
  AttachmentOffset = pos=(-21.5005,18.625,0.235) rot=(0,-1,0;0.174533rad)
  BaseFeature = -> Box1974
  Height = 0.3
  Length = 0.6605
  MapMode = 5
  Placement = pos=(-21.5005,18.625,0.235) rot=(0,-1,0;0.174533rad)
  Support = -> [XY_Plane181]
  Width = 0.25
FEATURE [PartDesign::Fillet] Fillet570
  Base = -> Box1856 [Edge2]
  BaseFeature = -> Box1856
  Placement = pos=(-21.5005,18.625,0.235) rot=(0,-1,0;0.174533rad)
  Radius = 0.05
  SupportTransform = false
FEATURE [PartDesign::Fillet] Fillet579
  Base = -> Fillet570 [Edge33]
  BaseFeature = -> Fillet570
  Placement = pos=(-21.5005,18.625,0.235) rot=(0,-1,0;0.174533rad)
  Radius = 0.5
  SupportTransform = false
FEATURE [PartDesign::AdditiveBox] Box1993
  AttacherType = Attacher::AttachEngine3D
  AttachmentOffset = pos=(-21.3,18.635,0) rot=(0,0,1;0rad)
  Height = 1.9
  Length = 1.3
  MapMode = 5
  Placement = pos=(-21.3,18.635,0) rot=(0,0,1;0rad)
  Support = -> [XY_Plane212]
  Width = 0.23
FEATURE [PartDesign::SubtractiveBox] Box1994
  AttacherType = Attacher::AttachEngine3D
  AttachmentOffset = pos=(-20.5,18.63,0) rot=(0,0,1;0rad)
  BaseFeature = -> Box1862
  Height = 1.635
  Length = 0.5
  MapMode = 5
  Placement = pos=(-20.5,18.63,0) rot=(0,0,1;0rad)
  Support = -> [XY_Plane210]
  Width = 0.25
FEATURE [PartDesign::SubtractiveBox] Box1847
  AttacherType = Attacher::AttachEngine3D
  AttachmentOffset = pos=(-21.19,18.635,-0.12) rot=(0,-1,0;0.15708rad)
  BaseFeature = -> Box1994
  Height = 0.12
  Length = 0.725
  MapMode = 5
  Placement = pos=(-21.19,18.635,-0.12) rot=(0,-1,0;0.15708rad)
  Support = -> [XY_Plane210]
  Width = 0.25
FEATURE [PartDesign::SubtractiveBox] Box1857
  AttacherType = Attacher::AttachEngine3D
  AttachmentOffset = pos=(-21.5005,18.625,0.235) rot=(0,-1,0;0.174533rad)
  BaseFeature = -> Box1847
  Height = 0.3
  Length = 0.6605
  MapMode = 5
  Placement = pos=(-21.5005,18.625,0.235) rot=(0,-1,0;0.174533rad)
  Support = -> [XY_Plane210]
  Width = 0.25
FEATURE [PartDesign::Fillet] Fillet575
  Base = -> Box1857 [Edge2]
  BaseFeature = -> Box1857
  Placement = pos=(-21.5005,18.625,0.235) rot=(0,-1,0;0.174533rad)
  Radius = 0.05
  SupportTransform = false
FEATURE [PartDesign::Fillet] Fillet569
  Base = -> Fillet575 [Edge33]
  BaseFeature = -> Fillet575
  Placement = pos=(-21.5005,18.625,0.235) rot=(0,-1,0;0.174533rad)
  Radius = 0.5
  SupportTransform = false
FEATURE [PartDesign::AdditiveBox] Box1995
  AttacherType = Attacher::AttachEngine3D
  AttachmentOffset = pos=(-21.3,18.635,0) rot=(0,0,1;0rad)
  Height = 1.9
  Length = 1.3
  MapMode = 5
  Placement = pos=(-21.3,18.635,0) rot=(0,0,1;0rad)
  Support = -> [XY_Plane211]
  Width = 0.23
FEATURE [PartDesign::SubtractiveBox] Box1988
  AttacherType = Attacher::AttachEngine3D
  AttachmentOffset = pos=(-21.35,18.635,0.35) rot=(0,0,1;0rad)
  BaseFeature = -> Box1995
  Height = 1.55
  Length = 0.5
  MapMode = 5
  Placement = pos=(-21.35,18.635,0.35) rot=(0,0,1;0rad)
  Support = -> [XY_Plane211]
  Width = 0.23
FEATURE [PartDesign::SubtractiveBox] Box1968
  AttacherType = Attacher::AttachEngine3D
  AttachmentOffset = pos=(-20.5,18.63,0) rot=(0,0,1;0rad)
  BaseFeature = -> Box1988
  Height = 1.635
  Length = 0.5
  MapMode = 5
  Placement = pos=(-20.5,18.63,0) rot=(0,0,1;0rad)
  Support = -> [XY_Plane211]
  Width = 0.25
FEATURE [PartDesign::SubtractiveBox] Box1967
  AttacherType = Attacher::AttachEngine3D
  AttachmentOffset = pos=(-21.19,18.635,-0.12) rot=(0,-1,0;0.15708rad)
  BaseFeature = -> Box1968
  Height = 0.12
  Length = 0.725
  MapMode = 5
  Placement = pos=(-21.19,18.635,-0.12) rot=(0,-1,0;0.15708rad)
  Support = -> [XY_Plane211]
  Width = 0.25
FEATURE [PartDesign::SubtractiveBox] Box1982
  AttacherType = Attacher::AttachEngine3D
  AttachmentOffset = pos=(-21.5005,18.625,0.235) rot=(0,-1,0;0.174533rad)
  BaseFeature = -> Box1967
  Height = 0.3
  Length = 0.6605
  MapMode = 5
  Placement = pos=(-21.5005,18.625,0.235) rot=(0,-1,0;0.174533rad)
  Support = -> [XY_Plane211]
  Width = 0.25
FEATURE [PartDesign::Fillet] Fillet585
  Base = -> Box1982 [Edge2]
  BaseFeature = -> Box1982
  Placement = pos=(-21.5005,18.625,0.235) rot=(0,-1,0;0.174533rad)
  Radius = 0.05
  SupportTransform = false
FEATURE [PartDesign::Fillet] Fillet564
  Base = -> Fillet585 [Edge33]
  BaseFeature = -> Fillet585
  Placement = pos=(-21.5005,18.625,0.235) rot=(0,-1,0;0.174533rad)
  Radius = 0.5
  SupportTransform = false
FEATURE [PartDesign::AdditiveBox] Box1939
  AttacherType = Attacher::AttachEngine3D
  AttachmentOffset = pos=(-21.1,18.635,0.305) rot=(0,1,0;0.785398rad)
  BaseFeature = -> Fillet564
  Height = 0.375
  Length = 0.2
  MapMode = 5
  Placement = pos=(-21.1,18.635,0.305) rot=(0,1,0;0.785398rad)
  Support = -> [XY_Plane211]
  Width = 0.23
FEATURE [PartDesign::SubtractiveCylinder] Cylinder382
  Angle = 360
  AttacherType = Attacher::AttachEngine3D
  AttachmentOffset = pos=(-21.055,18.935,0.52) rot=(1,0,0;1.5708rad)
  BaseFeature = -> Box1939
  Height = 0.375
  MapMode = 5
  Placement = pos=(-21.055,18.935,0.52) rot=(1,0,0;1.5708rad)
  Radius = 0.205
  Support = -> [XY_Plane211]
FEATURE [PartDesign::SubtractiveBox] Box1881
  AttacherType = Attacher::AttachEngine3D
  AttachmentOffset = pos=(-20.95,18.635,0.53) rot=(0,0,1;0rad)
  BaseFeature = -> Cylinder382
  Height = 0.5
  Length = 0.1
  MapMode = 5
  Placement = pos=(-20.95,18.635,0.53) rot=(0,0,1;0rad)
  Support = -> [XY_Plane211]
  Width = 0.23
FEATURE [PartDesign::SubtractiveBox] Box1876
  AttacherType = Attacher::AttachEngine3D
  AttachmentOffset = pos=(-21.15,18.635,0.297) rot=(0,-1,0;0.174533rad)
  BaseFeature = -> Box1881
  Height = 0.115
  Length = 0.115
  MapMode = 5
  Placement = pos=(-21.15,18.635,0.297) rot=(0,-1,0;0.174533rad)
  Support = -> [XY_Plane211]
  Width = 0.23
FEATURE [PartDesign::Fillet] Fillet590
  Base = -> Box1876 [Edge28]
  BaseFeature = -> Box1876
  Placement = pos=(-21.15,18.635,0.297) rot=(0,-1,0;0.174533rad)
  Radius = 0.375
  SupportTransform = false
FEATURE [PartDesign::AdditiveBox] Box1958
  AttacherType = Attacher::AttachEngine3D
  AttachmentOffset = pos=(-20.7,18.635,1.55) rot=(0,1,0;0.785398rad)
  BaseFeature = -> Fillet590
  Height = 0.375
  Length = 0.23
  MapMode = 5
  Placement = pos=(-20.7,18.635,1.55) rot=(0,1,0;0.785398rad)
  Support = -> [XY_Plane211]
  Width = 0.23
FEATURE [PartDesign::SubtractiveCylinder] Cylinder379
  Angle = 360
  AttacherType = Attacher::AttachEngine3D
  AttachmentOffset = pos=(-20.271,18.635,1.4056) rot=(-1,0,0;1.5708rad)
  BaseFeature = -> Box1958
  Height = 0.23
  MapMode = 5
  Placement = pos=(-20.271,18.635,1.4056) rot=(-1,0,0;1.5708rad)
  Radius = 0.23
  Support = -> [XY_Plane211]
FEATURE [PartDesign::AdditiveBox] Box1977
  AttacherType = Attacher::AttachEngine3D
  AttachmentOffset = pos=(-20.1,18.635,1.635) rot=(0,0,1;0rad)
  BaseFeature = -> Cylinder379
  Height = 0.265
  Length = 0.23
  MapMode = 5
  Placement = pos=(-20.1,18.635,1.635) rot=(0,0,1;0rad)
  Support = -> [XY_Plane211]
  Width = 0.23
FEATURE [PartDesign::Body] Body191  label="pin191"
  Group = -> [Box1995,Box1988,Box1968,Box1967,Box1982,Fillet585,Fillet564,Box1939,Cylinder382,Box1881,Box1876,Fillet590,Box1958,Cylinder379,Box1977]
  Origin = -> Origin214
  Tip = -> Box1977
FEATURE [PartDesign::SubtractiveBox] Box1998
  AttacherType = Attacher::AttachEngine3D
  AttachmentOffset = pos=(-21.35,18.635,0.35) rot=(0,0,1;0rad)
  BaseFeature = -> Box1993
  Height = 1.55
  Length = 0.5
  MapMode = 5
  Placement = pos=(-21.35,18.635,0.35) rot=(0,0,1;0rad)
  Support = -> [XY_Plane212]
  Width = 0.23
FEATURE [PartDesign::SubtractiveBox] Box1972
  AttacherType = Attacher::AttachEngine3D
  AttachmentOffset = pos=(-20.5,18.63,0) rot=(0,0,1;0rad)
  BaseFeature = -> Box1998
  Height = 1.635
  Length = 0.5
  MapMode = 5
  Placement = pos=(-20.5,18.63,0) rot=(0,0,1;0rad)
  Support = -> [XY_Plane212]
  Width = 0.25
FEATURE [PartDesign::SubtractiveBox] Box1984
  AttacherType = Attacher::AttachEngine3D
  AttachmentOffset = pos=(-21.19,18.635,-0.12) rot=(0,-1,0;0.15708rad)
  BaseFeature = -> Box1972
  Height = 0.12
  Length = 0.725
  MapMode = 5
  Placement = pos=(-21.19,18.635,-0.12) rot=(0,-1,0;0.15708rad)
  Support = -> [XY_Plane212]
  Width = 0.25
FEATURE [PartDesign::SubtractiveBox] Box1981
  AttacherType = Attacher::AttachEngine3D
  AttachmentOffset = pos=(-21.5005,18.625,0.235) rot=(0,-1,0;0.174533rad)
  BaseFeature = -> Box1984
  Height = 0.3
  Length = 0.6605
  MapMode = 5
  Placement = pos=(-21.5005,18.625,0.235) rot=(0,-1,0;0.174533rad)
  Support = -> [XY_Plane212]
  Width = 0.25
FEATURE [PartDesign::Fillet] Fillet578
  Base = -> Box1981 [Edge2]
  BaseFeature = -> Box1981
  Placement = pos=(-21.5005,18.625,0.235) rot=(0,-1,0;0.174533rad)
  Radius = 0.05
  SupportTransform = false
FEATURE [PartDesign::Fillet] Fillet592
  Base = -> Fillet578 [Edge33]
  BaseFeature = -> Fillet578
  Placement = pos=(-21.5005,18.625,0.235) rot=(0,-1,0;0.174533rad)
  Radius = 0.5
  SupportTransform = false
FEATURE [PartDesign::AdditiveBox] Box1959
  AttacherType = Attacher::AttachEngine3D
  AttachmentOffset = pos=(-21.1,18.635,0.305) rot=(0,1,0;0.785398rad)
  BaseFeature = -> Fillet592
  Height = 0.375
  Length = 0.2
  MapMode = 5
  Placement = pos=(-21.1,18.635,0.305) rot=(0,1,0;0.785398rad)
  Support = -> [XY_Plane212]
  Width = 0.23
FEATURE [PartDesign::SubtractiveCylinder] Cylinder402
  Angle = 360
  AttacherType = Attacher::AttachEngine3D
  AttachmentOffset = pos=(-21.055,18.935,0.52) rot=(1,0,0;1.5708rad)
  BaseFeature = -> Box1959
  Height = 0.375
  MapMode = 5
  Placement = pos=(-21.055,18.935,0.52) rot=(1,0,0;1.5708rad)
  Radius = 0.205
  Support = -> [XY_Plane212]
FEATURE [PartDesign::SubtractiveBox] Box1973
  AttacherType = Attacher::AttachEngine3D
  AttachmentOffset = pos=(-20.95,18.635,0.53) rot=(0,0,1;0rad)
  BaseFeature = -> Cylinder402
  Height = 0.5
  Length = 0.1
  MapMode = 5
  Placement = pos=(-20.95,18.635,0.53) rot=(0,0,1;0rad)
  Support = -> [XY_Plane212]
  Width = 0.23
FEATURE [PartDesign::SubtractiveBox] Box1980
  AttacherType = Attacher::AttachEngine3D
  AttachmentOffset = pos=(-21.15,18.635,0.297) rot=(0,-1,0;0.174533rad)
  BaseFeature = -> Box1973
  Height = 0.115
  Length = 0.115
  MapMode = 5
  Placement = pos=(-21.15,18.635,0.297) rot=(0,-1,0;0.174533rad)
  Support = -> [XY_Plane212]
  Width = 0.23
FEATURE [PartDesign::Fillet] Fillet567
  Base = -> Box1980 [Edge28]
  BaseFeature = -> Box1980
  Placement = pos=(-21.15,18.635,0.297) rot=(0,-1,0;0.174533rad)
  Radius = 0.375
  SupportTransform = false
FEATURE [PartDesign::AdditiveBox] Box1978
  AttacherType = Attacher::AttachEngine3D
  AttachmentOffset = pos=(-20.7,18.635,1.55) rot=(0,1,0;0.785398rad)
  BaseFeature = -> Fillet567
  Height = 0.375
  Length = 0.23
  MapMode = 5
  Placement = pos=(-20.7,18.635,1.55) rot=(0,1,0;0.785398rad)
  Support = -> [XY_Plane212]
  Width = 0.23
FEATURE [PartDesign::SubtractiveCylinder] Cylinder399
  Angle = 360
  AttacherType = Attacher::AttachEngine3D
  AttachmentOffset = pos=(-20.271,18.635,1.4056) rot=(-1,0,0;1.5708rad)
  BaseFeature = -> Box1978
  Height = 0.23
  MapMode = 5
  Placement = pos=(-20.271,18.635,1.4056) rot=(-1,0,0;1.5708rad)
  Radius = 0.23
  Support = -> [XY_Plane212]
FEATURE [PartDesign::AdditiveBox] Box1985
  AttacherType = Attacher::AttachEngine3D
  AttachmentOffset = pos=(-20.1,18.635,1.635) rot=(0,0,1;0rad)
  BaseFeature = -> Cylinder399
  Height = 0.265
  Length = 0.23
  MapMode = 5
  Placement = pos=(-20.1,18.635,1.635) rot=(0,0,1;0rad)
  Support = -> [XY_Plane212]
  Width = 0.23
FEATURE [PartDesign::Body] Body198  label="pin198"
  Group = -> [Box1993,Box1998,Box1972,Box1984,Box1981,Fillet578,Fillet592,Box1959,Cylinder402,Box1973,Box1980,Fillet567,Box1978,Cylinder399,Box1985]
  Origin = -> Origin209
  Placement = pos=(0,-1,0) rot=(0,0,1;0rad)
  Tip = -> Box1985
FEATURE [PartDesign::SubtractiveBox] Box1999
  AttacherType = Attacher::AttachEngine3D
  AttachmentOffset = pos=(-20.5,18.63,0) rot=(0,0,1;0rad)
  BaseFeature = -> Box1853
  Height = 1.635
  Length = 0.5
  MapMode = 5
  Placement = pos=(-20.5,18.63,0) rot=(0,0,1;0rad)
  Support = -> [XY_Plane195]
  Width = 0.25
FEATURE [PartDesign::SubtractiveBox] Box1930
  AttacherType = Attacher::AttachEngine3D
  AttachmentOffset = pos=(-21.19,18.635,-0.12) rot=(0,-1,0;0.15708rad)
  BaseFeature = -> Box1999
  Height = 0.12
  Length = 0.725
  MapMode = 5
  Placement = pos=(-21.19,18.635,-0.12) rot=(0,-1,0;0.15708rad)
  Support = -> [XY_Plane195]
  Width = 0.25
FEATURE [PartDesign::SubtractiveBox] Box1859
  AttacherType = Attacher::AttachEngine3D
  AttachmentOffset = pos=(-21.5005,18.625,0.235) rot=(0,-1,0;0.174533rad)
  BaseFeature = -> Box1930
  Height = 0.3
  Length = 0.6605
  MapMode = 5
  Placement = pos=(-21.5005,18.625,0.235) rot=(0,-1,0;0.174533rad)
  Support = -> [XY_Plane195]
  Width = 0.25
FEATURE [PartDesign::Fillet] Fillet574
  Base = -> Box1859 [Edge2]
  BaseFeature = -> Box1859
  Placement = pos=(-21.5005,18.625,0.235) rot=(0,-1,0;0.174533rad)
  Radius = 0.05
  SupportTransform = false
FEATURE [PartDesign::Fillet] Fillet565
  Base = -> Fillet574 [Edge33]
  BaseFeature = -> Fillet574
  Placement = pos=(-21.5005,18.625,0.235) rot=(0,-1,0;0.174533rad)
  Radius = 0.5
  SupportTransform = false
FEATURE [PartDesign::AdditiveBox] Box1992
  AttacherType = Attacher::AttachEngine3D
  AttachmentOffset = pos=(-21.1,18.635,0.305) rot=(0,1,0;0.785398rad)
  BaseFeature = -> Fillet565
  Height = 0.375
  Length = 0.2
  MapMode = 5
  Placement = pos=(-21.1,18.635,0.305) rot=(0,1,0;0.785398rad)
  Support = -> [XY_Plane195]
  Width = 0.23
FEATURE [PartDesign::SubtractiveCylinder] Cylinder392
  Angle = 360
  AttacherType = Attacher::AttachEngine3D
  AttachmentOffset = pos=(-21.055,18.935,0.52) rot=(1,0,0;1.5708rad)
  BaseFeature = -> Box1992
  Height = 0.375
  MapMode = 5
  Placement = pos=(-21.055,18.935,0.52) rot=(1,0,0;1.5708rad)
  Radius = 0.205
  Support = -> [XY_Plane195]
FEATURE [PartDesign::SubtractiveBox] Box1848
  AttacherType = Attacher::AttachEngine3D
  AttachmentOffset = pos=(-20.95,18.635,0.53) rot=(0,0,1;0rad)
  BaseFeature = -> Cylinder392
  Height = 0.5
  Length = 0.1
  MapMode = 5
  Placement = pos=(-20.95,18.635,0.53) rot=(0,0,1;0rad)
  Support = -> [XY_Plane195]
  Width = 0.23
FEATURE [PartDesign::SubtractiveBox] Box1855
  AttacherType = Attacher::AttachEngine3D
  AttachmentOffset = pos=(-21.15,18.635,0.297) rot=(0,-1,0;0.174533rad)
  BaseFeature = -> Box1848
  Height = 0.115
  Length = 0.115
  MapMode = 5
  Placement = pos=(-21.15,18.635,0.297) rot=(0,-1,0;0.174533rad)
  Support = -> [XY_Plane195]
  Width = 0.23
FEATURE [PartDesign::Fillet] Fillet563
  Base = -> Box1855 [Edge28]
  BaseFeature = -> Box1855
  Placement = pos=(-21.15,18.635,0.297) rot=(0,-1,0;0.174533rad)
  Radius = 0.375
  SupportTransform = false
FEATURE [PartDesign::AdditiveBox] Box1858
  AttacherType = Attacher::AttachEngine3D
  AttachmentOffset = pos=(-20.7,18.635,1.55) rot=(0,1,0;0.785398rad)
  BaseFeature = -> Fillet563
  Height = 0.375
  Length = 0.23
  MapMode = 5
  Placement = pos=(-20.7,18.635,1.55) rot=(0,1,0;0.785398rad)
  Support = -> [XY_Plane195]
  Width = 0.23
FEATURE [PartDesign::SubtractiveCylinder] Cylinder391
  Angle = 360
  AttacherType = Attacher::AttachEngine3D
  AttachmentOffset = pos=(-20.271,18.635,1.4056) rot=(-1,0,0;1.5708rad)
  BaseFeature = -> Box1858
  Height = 0.23
  MapMode = 5
  Placement = pos=(-20.271,18.635,1.4056) rot=(-1,0,0;1.5708rad)
  Radius = 0.23
  Support = -> [XY_Plane195]
FEATURE [PartDesign::AdditiveBox] Box1852
  AttacherType = Attacher::AttachEngine3D
  AttachmentOffset = pos=(-20.1,18.635,1.635) rot=(0,0,1;0rad)
  BaseFeature = -> Cylinder391
  Height = 0.265
  Length = 0.23
  MapMode = 5
  Placement = pos=(-20.1,18.635,1.635) rot=(0,0,1;0rad)
  Support = -> [XY_Plane195]
  Width = 0.23
FEATURE [PartDesign::Body] Body192  label="pin192"
  Group = -> [Box1870,Box1853,Box1999,Box1930,Box1859,Fillet574,Fillet565,Box1992,Cylinder392,Box1848,Box1855,Fillet563,Box1858,Cylinder391,Box1852]
  Origin = -> Origin213
  Placement = pos=(0,-2.5,0) rot=(0,0,1;0rad)
  Tip = -> Box1852
FEATURE [PartDesign::AdditiveBox] Box2000
  AttacherType = Attacher::AttachEngine3D
  AttachmentOffset = pos=(-21.1,18.635,0.305) rot=(0,1,0;0.785398rad)
  BaseFeature = -> Fillet569
  Height = 0.375
  Length = 0.2
  MapMode = 5
  Placement = pos=(-21.1,18.635,0.305) rot=(0,1,0;0.785398rad)
  Support = -> [XY_Plane210]
  Width = 0.23
FEATURE [PartDesign::SubtractiveCylinder] Cylinder403
  Angle = 360
  AttacherType = Attacher::AttachEngine3D
  AttachmentOffset = pos=(-21.055,18.935,0.52) rot=(1,0,0;1.5708rad)
  BaseFeature = -> Box2000
  Height = 0.375
  MapMode = 5
  Placement = pos=(-21.055,18.935,0.52) rot=(1,0,0;1.5708rad)
  Radius = 0.205
  Support = -> [XY_Plane210]
FEATURE [PartDesign::SubtractiveBox] Box1861
  AttacherType = Attacher::AttachEngine3D
  AttachmentOffset = pos=(-20.95,18.635,0.53) rot=(0,0,1;0rad)
  BaseFeature = -> Cylinder403
  Height = 0.5
  Length = 0.1
  MapMode = 5
  Placement = pos=(-20.95,18.635,0.53) rot=(0,0,1;0rad)
  Support = -> [XY_Plane210]
  Width = 0.23
FEATURE [PartDesign::SubtractiveBox] Box1936
  AttacherType = Attacher::AttachEngine3D
  AttachmentOffset = pos=(-21.15,18.635,0.297) rot=(0,-1,0;0.174533rad)
  BaseFeature = -> Box1861
  Height = 0.115
  Length = 0.115
  MapMode = 5
  Placement = pos=(-21.15,18.635,0.297) rot=(0,-1,0;0.174533rad)
  Support = -> [XY_Plane210]
  Width = 0.23
FEATURE [PartDesign::Fillet] Fillet568
  Base = -> Box1936 [Edge28]
  BaseFeature = -> Box1936
  Placement = pos=(-21.15,18.635,0.297) rot=(0,-1,0;0.174533rad)
  Radius = 0.375
  SupportTransform = false
FEATURE [PartDesign::AdditiveBox] Box1986
  AttacherType = Attacher::AttachEngine3D
  AttachmentOffset = pos=(-20.7,18.635,1.55) rot=(0,1,0;0.785398rad)
  BaseFeature = -> Fillet568
  Height = 0.375
  Length = 0.23
  MapMode = 5
  Placement = pos=(-20.7,18.635,1.55) rot=(0,1,0;0.785398rad)
  Support = -> [XY_Plane210]
  Width = 0.23
FEATURE [PartDesign::SubtractiveCylinder] Cylinder374
  Angle = 360
  AttacherType = Attacher::AttachEngine3D
  AttachmentOffset = pos=(-20.271,18.635,1.4056) rot=(-1,0,0;1.5708rad)
  BaseFeature = -> Box1986
  Height = 0.23
  MapMode = 5
  Placement = pos=(-20.271,18.635,1.4056) rot=(-1,0,0;1.5708rad)
  Radius = 0.23
  Support = -> [XY_Plane210]
FEATURE [PartDesign::AdditiveBox] Box1860
  AttacherType = Attacher::AttachEngine3D
  AttachmentOffset = pos=(-20.1,18.635,1.635) rot=(0,0,1;0rad)
  BaseFeature = -> Cylinder374
  Height = 0.265
  Length = 0.23
  MapMode = 5
  Placement = pos=(-20.1,18.635,1.635) rot=(0,0,1;0rad)
  Support = -> [XY_Plane210]
  Width = 0.23
FEATURE [PartDesign::Body] Body190  label="pin190"
  Group = -> [Box1938,Box1862,Box1994,Box1847,Box1857,Fillet575,Fillet569,Box2000,Cylinder403,Box1861,Box1936,Fillet568,Box1986,Cylinder374,Box1860]
  Origin = -> Origin222
  Placement = pos=(0,-2,0) rot=(0,0,1;0rad)
  Tip = -> Box1860
FEATURE [PartDesign::AdditiveBox] Box2001
  AttacherType = Attacher::AttachEngine3D
  AttachmentOffset = pos=(-21.1,18.635,0.305) rot=(0,1,0;0.785398rad)
  BaseFeature = -> Fillet579
  Height = 0.375
  Length = 0.2
  MapMode = 5
  Placement = pos=(-21.1,18.635,0.305) rot=(0,1,0;0.785398rad)
  Support = -> [XY_Plane181]
  Width = 0.23
FEATURE [PartDesign::SubtractiveCylinder] Cylinder401
  Angle = 360
  AttacherType = Attacher::AttachEngine3D
  AttachmentOffset = pos=(-21.055,18.935,0.52) rot=(1,0,0;1.5708rad)
  BaseFeature = -> Box2001
  Height = 0.375
  MapMode = 5
  Placement = pos=(-21.055,18.935,0.52) rot=(1,0,0;1.5708rad)
  Radius = 0.205
  Support = -> [XY_Plane181]
FEATURE [PartDesign::SubtractiveBox] Box1996
  AttacherType = Attacher::AttachEngine3D
  AttachmentOffset = pos=(-20.95,18.635,0.53) rot=(0,0,1;0rad)
  BaseFeature = -> Cylinder401
  Height = 0.5
  Length = 0.1
  MapMode = 5
  Placement = pos=(-20.95,18.635,0.53) rot=(0,0,1;0rad)
  Support = -> [XY_Plane181]
  Width = 0.23
FEATURE [PartDesign::SubtractiveBox] Box1997
  AttacherType = Attacher::AttachEngine3D
  AttachmentOffset = pos=(-21.15,18.635,0.297) rot=(0,-1,0;0.174533rad)
  BaseFeature = -> Box1996
  Height = 0.115
  Length = 0.115
  MapMode = 5
  Placement = pos=(-21.15,18.635,0.297) rot=(0,-1,0;0.174533rad)
  Support = -> [XY_Plane181]
  Width = 0.23
FEATURE [PartDesign::Fillet] Fillet582
  Base = -> Box1997 [Edge28]
  BaseFeature = -> Box1997
  Placement = pos=(-21.15,18.635,0.297) rot=(0,-1,0;0.174533rad)
  Radius = 0.375
  SupportTransform = false
FEATURE [PartDesign::AdditiveBox] Box1989
  AttacherType = Attacher::AttachEngine3D
  AttachmentOffset = pos=(-20.7,18.635,1.55) rot=(0,1,0;0.785398rad)
  BaseFeature = -> Fillet582
  Height = 0.375
  Length = 0.23
  MapMode = 5
  Placement = pos=(-20.7,18.635,1.55) rot=(0,1,0;0.785398rad)
  Support = -> [XY_Plane181]
  Width = 0.23
FEATURE [PartDesign::SubtractiveCylinder] Cylinder393
  Angle = 360
  AttacherType = Attacher::AttachEngine3D
  AttachmentOffset = pos=(-20.271,18.635,1.4056) rot=(-1,0,0;1.5708rad)
  BaseFeature = -> Box1989
  Height = 0.23
  MapMode = 5
  Placement = pos=(-20.271,18.635,1.4056) rot=(-1,0,0;1.5708rad)
  Radius = 0.23
  Support = -> [XY_Plane181]
FEATURE [PartDesign::AdditiveBox] Box1990
  AttacherType = Attacher::AttachEngine3D
  AttachmentOffset = pos=(-20.1,18.635,1.635) rot=(0,0,1;0rad)
  BaseFeature = -> Cylinder393
  Height = 0.265
  Length = 0.23
  MapMode = 5
  Placement = pos=(-20.1,18.635,1.635) rot=(0,0,1;0rad)
  Support = -> [XY_Plane181]
  Width = 0.23
FEATURE [PartDesign::Body] Body193  label="pin193"
  Group = -> [Box1866,Box1851,Box1987,Box1974,Box1856,Fillet570,Fillet579,Box2001,Cylinder401,Box1996,Box1997,Fillet582,Box1989,Cylinder393,Box1990]
  Origin = -> Origin224
  Placement = pos=(0,-1.5,0) rot=(0,0,1;0rad)
  Tip = -> Box1990
FEATURE [App::Part] Part020  label="Pin-set018"
  Group = -> [Body191,Body189,Body198,Body193,Body190,Body192,Body197,Body194,Body196,Body195,Body200,Body199]
  Origin = -> Origin225
  Placement = pos=(0,-18,0) rot=(0,0,1;0rad)
FEATURE [PartDesign::AdditiveBox] Box2022
  AttacherType = Attacher::AttachEngine3D
  AttachmentOffset = pos=(-21.3,18.635,0) rot=(0,0,1;0rad)
  Height = 1.9
  Length = 1.3
  MapMode = 5
  Placement = pos=(-21.3,18.635,0) rot=(0,0,1;0rad)
  Support = -> [XY_Plane219]
  Width = 0.23
FEATURE [PartDesign::SubtractiveBox] Box2007
  AttacherType = Attacher::AttachEngine3D
  AttachmentOffset = pos=(-21.35,18.635,0.35) rot=(0,0,1;0rad)
  BaseFeature = -> Box2022
  Height = 1.55
  Length = 0.5
  MapMode = 5
  Placement = pos=(-21.35,18.635,0.35) rot=(0,0,1;0rad)
  Support = -> [XY_Plane219]
  Width = 0.23
FEATURE [PartDesign::AdditiveBox] Box2024
  AttacherType = Attacher::AttachEngine3D
  AttachmentOffset = pos=(-21.3,18.635,0) rot=(0,0,1;0rad)
  Height = 1.9
  Length = 1.3
  MapMode = 5
  Placement = pos=(-21.3,18.635,0) rot=(0,0,1;0rad)
  Support = -> [XY_Plane223]
  Width = 0.23
FEATURE [PartDesign::SubtractiveBox] Box2006
  AttacherType = Attacher::AttachEngine3D
  AttachmentOffset = pos=(-21.35,18.635,0.35) rot=(0,0,1;0rad)
  BaseFeature = -> Box2024
  Height = 1.55
  Length = 0.5
  MapMode = 5
  Placement = pos=(-21.35,18.635,0.35) rot=(0,0,1;0rad)
  Support = -> [XY_Plane223]
  Width = 0.23
FEATURE [PartDesign::AdditiveBox] Box2035
  AttacherType = Attacher::AttachEngine3D
  AttachmentOffset = pos=(-21.3,18.635,0) rot=(0,0,1;0rad)
  Height = 1.9
  Length = 1.3
  MapMode = 5
  Placement = pos=(-21.3,18.635,0) rot=(0,0,1;0rad)
  Support = -> [XY_Plane227]
  Width = 0.23
FEATURE [PartDesign::AdditiveBox] Box2037
  AttacherType = Attacher::AttachEngine3D
  AttachmentOffset = pos=(-21.3,18.635,0) rot=(0,0,1;0rad)
  Height = 1.9
  Length = 1.3
  MapMode = 5
  Placement = pos=(-21.3,18.635,0) rot=(0,0,1;0rad)
  Support = -> [XY_Plane228]
  Width = 0.23
FEATURE [PartDesign::SubtractiveBox] Box2043
  AttacherType = Attacher::AttachEngine3D
  AttachmentOffset = pos=(-21.35,18.635,0.35) rot=(0,0,1;0rad)
  BaseFeature = -> Box2035
  Height = 1.55
  Length = 0.5
  MapMode = 5
  Placement = pos=(-21.35,18.635,0.35) rot=(0,0,1;0rad)
  Support = -> [XY_Plane227]
  Width = 0.23
FEATURE [PartDesign::SubtractiveBox] Box2027
  AttacherType = Attacher::AttachEngine3D
  AttachmentOffset = pos=(-20.5,18.63,0) rot=(0,0,1;0rad)
  BaseFeature = -> Box2043
  Height = 1.635
  Length = 0.5
  MapMode = 5
  Placement = pos=(-20.5,18.63,0) rot=(0,0,1;0rad)
  Support = -> [XY_Plane227]
  Width = 0.25
FEATURE [PartDesign::SubtractiveBox] Box2032
  AttacherType = Attacher::AttachEngine3D
  AttachmentOffset = pos=(-21.19,18.635,-0.12) rot=(0,-1,0;0.15708rad)
  BaseFeature = -> Box2027
  Height = 0.12
  Length = 0.725
  MapMode = 5
  Placement = pos=(-21.19,18.635,-0.12) rot=(0,-1,0;0.15708rad)
  Support = -> [XY_Plane227]
  Width = 0.25
FEATURE [PartDesign::SubtractiveBox] Box2038
  AttacherType = Attacher::AttachEngine3D
  AttachmentOffset = pos=(-21.5005,18.625,0.235) rot=(0,-1,0;0.174533rad)
  BaseFeature = -> Box2032
  Height = 0.3
  Length = 0.6605
  MapMode = 5
  Placement = pos=(-21.5005,18.625,0.235) rot=(0,-1,0;0.174533rad)
  Support = -> [XY_Plane227]
  Width = 0.25
FEATURE [PartDesign::SubtractiveBox] Box2045
  AttacherType = Attacher::AttachEngine3D
  AttachmentOffset = pos=(-21.35,18.635,0.35) rot=(0,0,1;0rad)
  BaseFeature = -> Box2037
  Height = 1.55
  Length = 0.5
  MapMode = 5
  Placement = pos=(-21.35,18.635,0.35) rot=(0,0,1;0rad)
  Support = -> [XY_Plane228]
  Width = 0.23
FEATURE [PartDesign::SubtractiveBox] Box2029
  AttacherType = Attacher::AttachEngine3D
  AttachmentOffset = pos=(-20.5,18.63,0) rot=(0,0,1;0rad)
  BaseFeature = -> Box2045
  Height = 1.635
  Length = 0.5
  MapMode = 5
  Placement = pos=(-20.5,18.63,0) rot=(0,0,1;0rad)
  Support = -> [XY_Plane228]
  Width = 0.25
FEATURE [PartDesign::SubtractiveBox] Box2034
  AttacherType = Attacher::AttachEngine3D
  AttachmentOffset = pos=(-21.19,18.635,-0.12) rot=(0,-1,0;0.15708rad)
  BaseFeature = -> Box2029
  Height = 0.12
  Length = 0.725
  MapMode = 5
  Placement = pos=(-21.19,18.635,-0.12) rot=(0,-1,0;0.15708rad)
  Support = -> [XY_Plane228]
  Width = 0.25
FEATURE [PartDesign::AdditiveBox] Box2049
  AttacherType = Attacher::AttachEngine3D
  AttachmentOffset = pos=(-21.3,18.635,0) rot=(0,0,1;0rad)
  Height = 1.9
  Length = 1.3
  MapMode = 5
  Placement = pos=(-21.3,18.635,0) rot=(0,0,1;0rad)
  Support = -> [XY_Plane226]
  Width = 0.23
FEATURE [PartDesign::AdditiveBox] Box2052
  AttacherType = Attacher::AttachEngine3D
  AttachmentOffset = pos=(-21.3,18.635,0) rot=(0,0,1;0rad)
  Height = 1.9
  Length = 1.3
  MapMode = 5
  Placement = pos=(-21.3,18.635,0) rot=(0,0,1;0rad)
  Support = -> [XY_Plane230]
  Width = 0.23
FEATURE [PartDesign::AdditiveBox] Box2054
  AttacherType = Attacher::AttachEngine3D
  AttachmentOffset = pos=(-21.3,18.635,0) rot=(0,0,1;0rad)
  Height = 1.9
  Length = 1.3
  MapMode = 5
  Placement = pos=(-21.3,18.635,0) rot=(0,0,1;0rad)
  Support = -> [XY_Plane222]
  Width = 0.23
FEATURE [PartDesign::SubtractiveBox] Box2060
  AttacherType = Attacher::AttachEngine3D
  AttachmentOffset = pos=(-21.35,18.635,0.35) rot=(0,0,1;0rad)
  BaseFeature = -> Box2054
  Height = 1.55
  Length = 0.5
  MapMode = 5
  Placement = pos=(-21.35,18.635,0.35) rot=(0,0,1;0rad)
  Support = -> [XY_Plane222]
  Width = 0.23
FEATURE [PartDesign::SubtractiveBox] Box2008
  AttacherType = Attacher::AttachEngine3D
  AttachmentOffset = pos=(-20.5,18.63,0) rot=(0,0,1;0rad)
  BaseFeature = -> Box2060
  Height = 1.635
  Length = 0.5
  MapMode = 5
  Placement = pos=(-20.5,18.63,0) rot=(0,0,1;0rad)
  Support = -> [XY_Plane222]
  Width = 0.25
FEATURE [PartDesign::SubtractiveBox] Box2020
  AttacherType = Attacher::AttachEngine3D
  AttachmentOffset = pos=(-21.19,18.635,-0.12) rot=(0,-1,0;0.15708rad)
  BaseFeature = -> Box2008
  Height = 0.12
  Length = 0.725
  MapMode = 5
  Placement = pos=(-21.19,18.635,-0.12) rot=(0,-1,0;0.15708rad)
  Support = -> [XY_Plane222]
  Width = 0.25
FEATURE [PartDesign::SubtractiveBox] Box2016
  AttacherType = Attacher::AttachEngine3D
  AttachmentOffset = pos=(-21.5005,18.625,0.235) rot=(0,-1,0;0.174533rad)
  BaseFeature = -> Box2020
  Height = 0.3
  Length = 0.6605
  MapMode = 5
  Placement = pos=(-21.5005,18.625,0.235) rot=(0,-1,0;0.174533rad)
  Support = -> [XY_Plane222]
  Width = 0.25
FEATURE [PartDesign::SubtractiveBox] Box2063
  AttacherType = Attacher::AttachEngine3D
  AttachmentOffset = pos=(-21.35,18.635,0.35) rot=(0,0,1;0rad)
  BaseFeature = -> Box2049
  Height = 1.55
  Length = 0.5
  MapMode = 5
  Placement = pos=(-21.35,18.635,0.35) rot=(0,0,1;0rad)
  Support = -> [XY_Plane226]
  Width = 0.23
FEATURE [PartDesign::SubtractiveBox] Box2046
  AttacherType = Attacher::AttachEngine3D
  AttachmentOffset = pos=(-20.5,18.63,0) rot=(0,0,1;0rad)
  BaseFeature = -> Box2063
  Height = 1.635
  Length = 0.5
  MapMode = 5
  Placement = pos=(-20.5,18.63,0) rot=(0,0,1;0rad)
  Support = -> [XY_Plane226]
  Width = 0.25
FEATURE [PartDesign::AdditiveBox] Box2064
  AttacherType = Attacher::AttachEngine3D
  AttachmentOffset = pos=(-21.3,18.635,0) rot=(0,0,1;0rad)
  Height = 1.9
  Length = 1.3
  MapMode = 5
  Placement = pos=(-21.3,18.635,0) rot=(0,0,1;0rad)
  Support = -> [XY_Plane231]
  Width = 0.23
FEATURE [PartDesign::SubtractiveBox] Box2068
  AttacherType = Attacher::AttachEngine3D
  AttachmentOffset = pos=(-21.19,18.635,-0.12) rot=(0,-1,0;0.15708rad)
  BaseFeature = -> Box2046
  Height = 0.12
  Length = 0.725
  MapMode = 5
  Placement = pos=(-21.19,18.635,-0.12) rot=(0,-1,0;0.15708rad)
  Support = -> [XY_Plane226]
  Width = 0.25
FEATURE [PartDesign::SubtractiveBox] Box2058
  AttacherType = Attacher::AttachEngine3D
  AttachmentOffset = pos=(-21.5005,18.625,0.235) rot=(0,-1,0;0.174533rad)
  BaseFeature = -> Box2068
  Height = 0.3
  Length = 0.6605
  MapMode = 5
  Placement = pos=(-21.5005,18.625,0.235) rot=(0,-1,0;0.174533rad)
  Support = -> [XY_Plane226]
  Width = 0.25
FEATURE [PartDesign::AdditiveBox] Box2070
  AttacherType = Attacher::AttachEngine3D
  AttachmentOffset = pos=(-21.3,18.635,0) rot=(0,0,1;0rad)
  Height = 1.9
  Length = 1.3
  MapMode = 5
  Placement = pos=(-21.3,18.635,0) rot=(0,0,1;0rad)
  Support = -> [XY_Plane224]
  Width = 0.23
FEATURE [PartDesign::SubtractiveBox] Box2018
  AttacherType = Attacher::AttachEngine3D
  AttachmentOffset = pos=(-21.35,18.635,0.35) rot=(0,0,1;0rad)
  BaseFeature = -> Box2070
  Height = 1.55
  Length = 0.5
  MapMode = 5
  Placement = pos=(-21.35,18.635,0.35) rot=(0,0,1;0rad)
  Support = -> [XY_Plane224]
  Width = 0.23
FEATURE [PartDesign::SubtractiveBox] Box2073
  AttacherType = Attacher::AttachEngine3D
  AttachmentOffset = pos=(-21.35,18.635,0.35) rot=(0,0,1;0rad)
  BaseFeature = -> Box2064
  Height = 1.55
  Length = 0.5
  MapMode = 5
  Placement = pos=(-21.35,18.635,0.35) rot=(0,0,1;0rad)
  Support = -> [XY_Plane231]
  Width = 0.23
FEATURE [PartDesign::SubtractiveBox] Box2075
  AttacherType = Attacher::AttachEngine3D
  AttachmentOffset = pos=(-21.35,18.635,0.35) rot=(0,0,1;0rad)
  BaseFeature = -> Box2052
  Height = 1.55
  Length = 0.5
  MapMode = 5
  Placement = pos=(-21.35,18.635,0.35) rot=(0,0,1;0rad)
  Support = -> [XY_Plane230]
  Width = 0.23
FEATURE [PartDesign::SubtractiveBox] Box2039
  AttacherType = Attacher::AttachEngine3D
  AttachmentOffset = pos=(-20.5,18.63,0) rot=(0,0,1;0rad)
  BaseFeature = -> Box2075
  Height = 1.635
  Length = 0.5
  MapMode = 5
  Placement = pos=(-20.5,18.63,0) rot=(0,0,1;0rad)
  Support = -> [XY_Plane230]
  Width = 0.25
FEATURE [PartDesign::SubtractiveBox] Box2083
  AttacherType = Attacher::AttachEngine3D
  AttachmentOffset = pos=(-21.5005,18.625,0.235) rot=(0,-1,0;0.174533rad)
  BaseFeature = -> Box2034
  Height = 0.3
  Length = 0.6605
  MapMode = 5
  Placement = pos=(-21.5005,18.625,0.235) rot=(0,-1,0;0.174533rad)
  Support = -> [XY_Plane228]
  Width = 0.25
FEATURE [PartDesign::SubtractiveBox] Box2086
  AttacherType = Attacher::AttachEngine3D
  AttachmentOffset = pos=(-20.5,18.63,0) rot=(0,0,1;0rad)
  BaseFeature = -> Box2073
  Height = 1.635
  Length = 0.5
  MapMode = 5
  Placement = pos=(-20.5,18.63,0) rot=(0,0,1;0rad)
  Support = -> [XY_Plane231]
  Width = 0.25
FEATURE [PartDesign::SubtractiveBox] Box2057
  AttacherType = Attacher::AttachEngine3D
  AttachmentOffset = pos=(-21.19,18.635,-0.12) rot=(0,-1,0;0.15708rad)
  BaseFeature = -> Box2086
  Height = 0.12
  Length = 0.725
  MapMode = 5
  Placement = pos=(-21.19,18.635,-0.12) rot=(0,-1,0;0.15708rad)
  Support = -> [XY_Plane231]
  Width = 0.25
FEATURE [PartDesign::SubtractiveBox] Box2056
  AttacherType = Attacher::AttachEngine3D
  AttachmentOffset = pos=(-21.5005,18.625,0.235) rot=(0,-1,0;0.174533rad)
  BaseFeature = -> Box2057
  Height = 0.3
  Length = 0.6605
  MapMode = 5
  Placement = pos=(-21.5005,18.625,0.235) rot=(0,-1,0;0.174533rad)
  Support = -> [XY_Plane231]
  Width = 0.25
FEATURE [PartDesign::SubtractiveBox] Box2091
  AttacherType = Attacher::AttachEngine3D
  AttachmentOffset = pos=(-21.19,18.635,-0.12) rot=(0,-1,0;0.15708rad)
  BaseFeature = -> Box2039
  Height = 0.12
  Length = 0.725
  MapMode = 5
  Placement = pos=(-21.19,18.635,-0.12) rot=(0,-1,0;0.15708rad)
  Support = -> [XY_Plane230]
  Width = 0.25
FEATURE [PartDesign::SubtractiveBox] Box2051
  AttacherType = Attacher::AttachEngine3D
  AttachmentOffset = pos=(-21.5005,18.625,0.235) rot=(0,-1,0;0.174533rad)
  BaseFeature = -> Box2091
  Height = 0.3
  Length = 0.6605
  MapMode = 5
  Placement = pos=(-21.5005,18.625,0.235) rot=(0,-1,0;0.174533rad)
  Support = -> [XY_Plane230]
  Width = 0.25
FEATURE [PartDesign::AdditiveBox] Box2103
  AttacherType = Attacher::AttachEngine3D
  AttachmentOffset = pos=(-21.3,18.635,0) rot=(0,0,1;0rad)
  Height = 1.9
  Length = 1.3
  MapMode = 5
  Placement = pos=(-21.3,18.635,0) rot=(0,0,1;0rad)
  Support = -> [XY_Plane220]
  Width = 0.23
FEATURE [PartDesign::SubtractiveBox] Box2105
  AttacherType = Attacher::AttachEngine3D
  AttachmentOffset = pos=(-20.5,18.63,0) rot=(0,0,1;0rad)
  BaseFeature = -> Box2007
  Height = 1.635
  Length = 0.5
  MapMode = 5
  Placement = pos=(-20.5,18.63,0) rot=(0,0,1;0rad)
  Support = -> [XY_Plane219]
  Width = 0.25
FEATURE [PartDesign::SubtractiveBox] Box2101
  AttacherType = Attacher::AttachEngine3D
  AttachmentOffset = pos=(-21.19,18.635,-0.12) rot=(0,-1,0;0.15708rad)
  BaseFeature = -> Box2105
  Height = 0.12
  Length = 0.725
  MapMode = 5
  Placement = pos=(-21.19,18.635,-0.12) rot=(0,-1,0;0.15708rad)
  Support = -> [XY_Plane219]
  Width = 0.25
FEATURE [PartDesign::SubtractiveBox] Box2017
  AttacherType = Attacher::AttachEngine3D
  AttachmentOffset = pos=(-21.5005,18.625,0.235) rot=(0,-1,0;0.174533rad)
  BaseFeature = -> Box2101
  Height = 0.3
  Length = 0.6605
  MapMode = 5
  Placement = pos=(-21.5005,18.625,0.235) rot=(0,-1,0;0.174533rad)
  Support = -> [XY_Plane219]
  Width = 0.25
FEATURE [PartDesign::Fillet] Fillet607
  Base = -> Box2017 [Edge2]
  BaseFeature = -> Box2017
  Placement = pos=(-21.5005,18.625,0.235) rot=(0,-1,0;0.174533rad)
  Radius = 0.05
  SupportTransform = false
FEATURE [PartDesign::SubtractiveBox] Box2110
  AttacherType = Attacher::AttachEngine3D
  AttachmentOffset = pos=(-21.35,18.635,0.35) rot=(0,0,1;0rad)
  BaseFeature = -> Box2103
  Height = 1.55
  Length = 0.5
  MapMode = 5
  Placement = pos=(-21.35,18.635,0.35) rot=(0,0,1;0rad)
  Support = -> [XY_Plane220]
  Width = 0.23
FEATURE [PartDesign::SubtractiveBox] Box2088
  AttacherType = Attacher::AttachEngine3D
  AttachmentOffset = pos=(-20.5,18.63,0) rot=(0,0,1;0rad)
  BaseFeature = -> Box2110
  Height = 1.635
  Length = 0.5
  MapMode = 5
  Placement = pos=(-20.5,18.63,0) rot=(0,0,1;0rad)
  Support = -> [XY_Plane220]
  Width = 0.25
FEATURE [PartDesign::SubtractiveBox] Box2087
  AttacherType = Attacher::AttachEngine3D
  AttachmentOffset = pos=(-21.19,18.635,-0.12) rot=(0,-1,0;0.15708rad)
  BaseFeature = -> Box2088
  Height = 0.12
  Length = 0.725
  MapMode = 5
  Placement = pos=(-21.19,18.635,-0.12) rot=(0,-1,0;0.15708rad)
  Support = -> [XY_Plane220]
  Width = 0.25
FEATURE [PartDesign::SubtractiveBox] Box2106
  AttacherType = Attacher::AttachEngine3D
  AttachmentOffset = pos=(-21.5005,18.625,0.235) rot=(0,-1,0;0.174533rad)
  BaseFeature = -> Box2087
  Height = 0.3
  Length = 0.6605
  MapMode = 5
  Placement = pos=(-21.5005,18.625,0.235) rot=(0,-1,0;0.174533rad)
  Support = -> [XY_Plane220]
  Width = 0.25
FEATURE [PartDesign::AdditiveBox] Box2112
  AttacherType = Attacher::AttachEngine3D
  AttachmentOffset = pos=(-21.3,18.635,0) rot=(0,0,1;0rad)
  Height = 1.9
  Length = 1.3
  MapMode = 5
  Placement = pos=(-21.3,18.635,0) rot=(0,0,1;0rad)
  Support = -> [XY_Plane229]
  Width = 0.23
FEATURE [PartDesign::SubtractiveBox] Box2080
  AttacherType = Attacher::AttachEngine3D
  AttachmentOffset = pos=(-21.35,18.635,0.35) rot=(0,0,1;0rad)
  BaseFeature = -> Box2112
  Height = 1.55
  Length = 0.5
  MapMode = 5
  Placement = pos=(-21.35,18.635,0.35) rot=(0,0,1;0rad)
  Support = -> [XY_Plane229]
  Width = 0.23
FEATURE [PartDesign::SubtractiveBox] Box2076
  AttacherType = Attacher::AttachEngine3D
  AttachmentOffset = pos=(-20.5,18.63,0) rot=(0,0,1;0rad)
  BaseFeature = -> Box2080
  Height = 1.635
  Length = 0.5
  MapMode = 5
  Placement = pos=(-20.5,18.63,0) rot=(0,0,1;0rad)
  Support = -> [XY_Plane229]
  Width = 0.25
FEATURE [PartDesign::SubtractiveBox] Box2099
  AttacherType = Attacher::AttachEngine3D
  AttachmentOffset = pos=(-21.19,18.635,-0.12) rot=(0,-1,0;0.15708rad)
  BaseFeature = -> Box2076
  Height = 0.12
  Length = 0.725
  MapMode = 5
  Placement = pos=(-21.19,18.635,-0.12) rot=(0,-1,0;0.15708rad)
  Support = -> [XY_Plane229]
  Width = 0.25
FEATURE [PartDesign::SubtractiveBox] Box2089
  AttacherType = Attacher::AttachEngine3D
  AttachmentOffset = pos=(-21.5005,18.625,0.235) rot=(0,-1,0;0.174533rad)
  BaseFeature = -> Box2099
  Height = 0.3
  Length = 0.6605
  MapMode = 5
  Placement = pos=(-21.5005,18.625,0.235) rot=(0,-1,0;0.174533rad)
  Support = -> [XY_Plane229]
  Width = 0.25
FEATURE [PartDesign::Fillet] Fillet608
  Base = -> Box2089 [Edge2]
  BaseFeature = -> Box2089
  Placement = pos=(-21.5005,18.625,0.235) rot=(0,-1,0;0.174533rad)
  Radius = 0.05
  SupportTransform = false
FEATURE [PartDesign::AdditiveBox] Box2113
  AttacherType = Attacher::AttachEngine3D
  AttachmentOffset = pos=(-21.3,18.635,0) rot=(0,0,1;0rad)
  Height = 1.9
  Length = 1.3
  MapMode = 5
  Placement = pos=(-21.3,18.635,0) rot=(0,0,1;0rad)
  Support = -> [XY_Plane225]
  Width = 0.23
FEATURE [PartDesign::SubtractiveBox] Box2114
  AttacherType = Attacher::AttachEngine3D
  AttachmentOffset = pos=(-20.5,18.63,0) rot=(0,0,1;0rad)
  BaseFeature = -> Box2018
  Height = 1.635
  Length = 0.5
  MapMode = 5
  Placement = pos=(-20.5,18.63,0) rot=(0,0,1;0rad)
  Support = -> [XY_Plane224]
  Width = 0.25
FEATURE [PartDesign::SubtractiveBox] Box2002
  AttacherType = Attacher::AttachEngine3D
  AttachmentOffset = pos=(-21.19,18.635,-0.12) rot=(0,-1,0;0.15708rad)
  BaseFeature = -> Box2114
  Height = 0.12
  Length = 0.725
  MapMode = 5
  Placement = pos=(-21.19,18.635,-0.12) rot=(0,-1,0;0.15708rad)
  Support = -> [XY_Plane224]
  Width = 0.25
FEATURE [PartDesign::SubtractiveBox] Box2011
  AttacherType = Attacher::AttachEngine3D
  AttachmentOffset = pos=(-21.5005,18.625,0.235) rot=(0,-1,0;0.174533rad)
  BaseFeature = -> Box2002
  Height = 0.3
  Length = 0.6605
  MapMode = 5
  Placement = pos=(-21.5005,18.625,0.235) rot=(0,-1,0;0.174533rad)
  Support = -> [XY_Plane224]
  Width = 0.25
FEATURE [PartDesign::SubtractiveBox] Box2120
  AttacherType = Attacher::AttachEngine3D
  AttachmentOffset = pos=(-21.35,18.635,0.35) rot=(0,0,1;0rad)
  BaseFeature = -> Box2113
  Height = 1.55
  Length = 0.5
  MapMode = 5
  Placement = pos=(-21.35,18.635,0.35) rot=(0,0,1;0rad)
  Support = -> [XY_Plane225]
  Width = 0.23
FEATURE [PartDesign::SubtractiveBox] Box2100
  AttacherType = Attacher::AttachEngine3D
  AttachmentOffset = pos=(-20.5,18.63,0) rot=(0,0,1;0rad)
  BaseFeature = -> Box2120
  Height = 1.635
  Length = 0.5
  MapMode = 5
  Placement = pos=(-20.5,18.63,0) rot=(0,0,1;0rad)
  Support = -> [XY_Plane225]
  Width = 0.25
FEATURE [PartDesign::SubtractiveBox] Box2102
  AttacherType = Attacher::AttachEngine3D
  AttachmentOffset = pos=(-21.19,18.635,-0.12) rot=(0,-1,0;0.15708rad)
  BaseFeature = -> Box2100
  Height = 0.12
  Length = 0.725
  MapMode = 5
  Placement = pos=(-21.19,18.635,-0.12) rot=(0,-1,0;0.15708rad)
  Support = -> [XY_Plane225]
  Width = 0.25
FEATURE [PartDesign::SubtractiveBox] Box2098
  AttacherType = Attacher::AttachEngine3D
  AttachmentOffset = pos=(-21.5005,18.625,0.235) rot=(0,-1,0;0.174533rad)
  BaseFeature = -> Box2102
  Height = 0.3
  Length = 0.6605
  MapMode = 5
  Placement = pos=(-21.5005,18.625,0.235) rot=(0,-1,0;0.174533rad)
  Support = -> [XY_Plane225]
  Width = 0.25
FEATURE [PartDesign::SubtractiveBox] Box2121
  AttacherType = Attacher::AttachEngine3D
  AttachmentOffset = pos=(-20.5,18.63,0) rot=(0,0,1;0rad)
  BaseFeature = -> Box2006
  Height = 1.635
  Length = 0.5
  MapMode = 5
  Placement = pos=(-20.5,18.63,0) rot=(0,0,1;0rad)
  Support = -> [XY_Plane223]
  Width = 0.25
FEATURE [PartDesign::SubtractiveBox] Box2066
  AttacherType = Attacher::AttachEngine3D
  AttachmentOffset = pos=(-21.19,18.635,-0.12) rot=(0,-1,0;0.15708rad)
  BaseFeature = -> Box2121
  Height = 0.12
  Length = 0.725
  MapMode = 5
  Placement = pos=(-21.19,18.635,-0.12) rot=(0,-1,0;0.15708rad)
  Support = -> [XY_Plane223]
  Width = 0.25
FEATURE [PartDesign::SubtractiveBox] Box2019
  AttacherType = Attacher::AttachEngine3D
  AttachmentOffset = pos=(-21.5005,18.625,0.235) rot=(0,-1,0;0.174533rad)
  BaseFeature = -> Box2066
  Height = 0.3
  Length = 0.6605
  MapMode = 5
  Placement = pos=(-21.5005,18.625,0.235) rot=(0,-1,0;0.174533rad)
  Support = -> [XY_Plane223]
  Width = 0.25
FEATURE [PartDesign::AdditiveBox] Box2141
  AttacherType = Attacher::AttachEngine3D
  AttachmentOffset = pos=(-21.3,18.635,0) rot=(0,0,1;0rad)
  Height = 1.9
  Length = 1.3
  MapMode = 5
  Placement = pos=(-21.3,18.635,0) rot=(0,0,1;0rad)
  Support = -> [XY_Plane233]
  Width = 0.23
FEATURE [PartDesign::SubtractiveBox] Box2125
  AttacherType = Attacher::AttachEngine3D
  AttachmentOffset = pos=(-21.35,18.635,0.35) rot=(0,0,1;0rad)
  BaseFeature = -> Box2141
  Height = 1.55
  Length = 0.5
  MapMode = 5
  Placement = pos=(-21.35,18.635,0.35) rot=(0,0,1;0rad)
  Support = -> [XY_Plane233]
  Width = 0.23
FEATURE [PartDesign::AdditiveBox] Box2144
  AttacherType = Attacher::AttachEngine3D
  AttachmentOffset = pos=(-21.3,18.635,0) rot=(0,0,1;0rad)
  Height = 1.9
  Length = 1.3
  MapMode = 5
  Placement = pos=(-21.3,18.635,0) rot=(0,0,1;0rad)
  Support = -> [XY_Plane234]
  Width = 0.23
FEATURE [PartDesign::SubtractiveBox] Box2124
  AttacherType = Attacher::AttachEngine3D
  AttachmentOffset = pos=(-21.35,18.635,0.35) rot=(0,0,1;0rad)
  BaseFeature = -> Box2144
  Height = 1.55
  Length = 0.5
  MapMode = 5
  Placement = pos=(-21.35,18.635,0.35) rot=(0,0,1;0rad)
  Support = -> [XY_Plane234]
  Width = 0.23
FEATURE [PartDesign::Fillet] Fillet610
  Base = -> Box2019 [Edge2]
  BaseFeature = -> Box2019
  Placement = pos=(-21.5005,18.625,0.235) rot=(0,-1,0;0.174533rad)
  Radius = 0.05
  SupportTransform = false
FEATURE [PartDesign::Fillet] Fillet601
  Base = -> Fillet610 [Edge33]
  BaseFeature = -> Fillet610
  Placement = pos=(-21.5005,18.625,0.235) rot=(0,-1,0;0.174533rad)
  Radius = 0.5
  SupportTransform = false
FEATURE [PartDesign::AdditiveBox] Box2108
  AttacherType = Attacher::AttachEngine3D
  AttachmentOffset = pos=(-21.1,18.635,0.305) rot=(0,1,0;0.785398rad)
  BaseFeature = -> Fillet601
  Height = 0.375
  Length = 0.2
  MapMode = 5
  Placement = pos=(-21.1,18.635,0.305) rot=(0,1,0;0.785398rad)
  Support = -> [XY_Plane223]
  Width = 0.23
FEATURE [PartDesign::SubtractiveCylinder] Cylinder418
  Angle = 360
  AttacherType = Attacher::AttachEngine3D
  AttachmentOffset = pos=(-21.055,18.935,0.52) rot=(1,0,0;1.5708rad)
  BaseFeature = -> Box2108
  Height = 0.375
  MapMode = 5
  Placement = pos=(-21.055,18.935,0.52) rot=(1,0,0;1.5708rad)
  Radius = 0.205
  Support = -> [XY_Plane223]
FEATURE [PartDesign::SubtractiveBox] Box1991
  AttacherType = Attacher::AttachEngine3D
  AttachmentOffset = pos=(-20.95,18.635,0.53) rot=(0,0,1;0rad)
  BaseFeature = -> Cylinder418
  Height = 0.5
  Length = 0.1
  MapMode = 5
  Placement = pos=(-20.95,18.635,0.53) rot=(0,0,1;0rad)
  Support = -> [XY_Plane223]
  Width = 0.23
FEATURE [PartDesign::SubtractiveBox] Box2009
  AttacherType = Attacher::AttachEngine3D
  AttachmentOffset = pos=(-21.15,18.635,0.297) rot=(0,-1,0;0.174533rad)
  BaseFeature = -> Box1991
  Height = 0.115
  Length = 0.115
  MapMode = 5
  Placement = pos=(-21.15,18.635,0.297) rot=(0,-1,0;0.174533rad)
  Support = -> [XY_Plane223]
  Width = 0.23
FEATURE [PartDesign::Fillet] Fillet604
  Base = -> Box2009 [Edge28]
  BaseFeature = -> Box2009
  Placement = pos=(-21.15,18.635,0.297) rot=(0,-1,0;0.174533rad)
  Radius = 0.375
  SupportTransform = false
FEATURE [PartDesign::AdditiveBox] Box2014
  AttacherType = Attacher::AttachEngine3D
  AttachmentOffset = pos=(-20.7,18.635,1.55) rot=(0,1,0;0.785398rad)
  BaseFeature = -> Fillet604
  Height = 0.375
  Length = 0.23
  MapMode = 5
  Placement = pos=(-20.7,18.635,1.55) rot=(0,1,0;0.785398rad)
  Support = -> [XY_Plane223]
  Width = 0.23
FEATURE [PartDesign::SubtractiveCylinder] Cylinder420
  Angle = 360
  AttacherType = Attacher::AttachEngine3D
  AttachmentOffset = pos=(-20.271,18.635,1.4056) rot=(-1,0,0;1.5708rad)
  BaseFeature = -> Box2014
  Height = 0.23
  MapMode = 5
  Placement = pos=(-20.271,18.635,1.4056) rot=(-1,0,0;1.5708rad)
  Radius = 0.23
  Support = -> [XY_Plane223]
FEATURE [PartDesign::AdditiveBox] Box2005
  AttacherType = Attacher::AttachEngine3D
  AttachmentOffset = pos=(-20.1,18.635,1.635) rot=(0,0,1;0rad)
  BaseFeature = -> Cylinder420
  Height = 0.265
  Length = 0.23
  MapMode = 5
  Placement = pos=(-20.1,18.635,1.635) rot=(0,0,1;0rad)
  Support = -> [XY_Plane223]
  Width = 0.23
FEATURE [PartDesign::Fillet] Fillet611
  Base = -> Fillet608 [Edge33]
  BaseFeature = -> Fillet608
  Placement = pos=(-21.5005,18.625,0.235) rot=(0,-1,0;0.174533rad)
  Radius = 0.5
  SupportTransform = false
FEATURE [PartDesign::AdditiveBox] Box2084
  AttacherType = Attacher::AttachEngine3D
  AttachmentOffset = pos=(-21.1,18.635,0.305) rot=(0,1,0;0.785398rad)
  BaseFeature = -> Fillet611
  Height = 0.375
  Length = 0.2
  MapMode = 5
  Placement = pos=(-21.1,18.635,0.305) rot=(0,1,0;0.785398rad)
  Support = -> [XY_Plane229]
  Width = 0.23
FEATURE [PartDesign::SubtractiveCylinder] Cylinder422
  Angle = 360
  AttacherType = Attacher::AttachEngine3D
  AttachmentOffset = pos=(-21.055,18.935,0.52) rot=(1,0,0;1.5708rad)
  BaseFeature = -> Box2084
  Height = 0.375
  MapMode = 5
  Placement = pos=(-21.055,18.935,0.52) rot=(1,0,0;1.5708rad)
  Radius = 0.205
  Support = -> [XY_Plane229]
FEATURE [PartDesign::SubtractiveBox] Box2092
  AttacherType = Attacher::AttachEngine3D
  AttachmentOffset = pos=(-20.95,18.635,0.53) rot=(0,0,1;0rad)
  BaseFeature = -> Cylinder422
  Height = 0.5
  Length = 0.1
  MapMode = 5
  Placement = pos=(-20.95,18.635,0.53) rot=(0,0,1;0rad)
  Support = -> [XY_Plane229]
  Width = 0.23
FEATURE [PartDesign::SubtractiveBox] Box2085
  AttacherType = Attacher::AttachEngine3D
  AttachmentOffset = pos=(-21.15,18.635,0.297) rot=(0,-1,0;0.174533rad)
  BaseFeature = -> Box2092
  Height = 0.115
  Length = 0.115
  MapMode = 5
  Placement = pos=(-21.15,18.635,0.297) rot=(0,-1,0;0.174533rad)
  Support = -> [XY_Plane229]
  Width = 0.23
FEATURE [PartDesign::Fillet] Fillet612
  Base = -> Box2011 [Edge2]
  BaseFeature = -> Box2011
  Placement = pos=(-21.5005,18.625,0.235) rot=(0,-1,0;0.174533rad)
  Radius = 0.05
  SupportTransform = false
FEATURE [PartDesign::Fillet] Fillet606
  Base = -> Fillet612 [Edge33]
  BaseFeature = -> Fillet612
  Placement = pos=(-21.5005,18.625,0.235) rot=(0,-1,0;0.174533rad)
  Radius = 0.5
  SupportTransform = false
FEATURE [PartDesign::AdditiveBox] Box2117
  AttacherType = Attacher::AttachEngine3D
  AttachmentOffset = pos=(-21.1,18.635,0.305) rot=(0,1,0;0.785398rad)
  BaseFeature = -> Fillet606
  Height = 0.375
  Length = 0.2
  MapMode = 5
  Placement = pos=(-21.1,18.635,0.305) rot=(0,1,0;0.785398rad)
  Support = -> [XY_Plane224]
  Width = 0.23
FEATURE [PartDesign::SubtractiveCylinder] Cylinder427
  Angle = 360
  AttacherType = Attacher::AttachEngine3D
  AttachmentOffset = pos=(-21.055,18.935,0.52) rot=(1,0,0;1.5708rad)
  BaseFeature = -> Box2117
  Height = 0.375
  MapMode = 5
  Placement = pos=(-21.055,18.935,0.52) rot=(1,0,0;1.5708rad)
  Radius = 0.205
  Support = -> [XY_Plane224]
FEATURE [PartDesign::SubtractiveBox] Box2021
  AttacherType = Attacher::AttachEngine3D
  AttachmentOffset = pos=(-20.95,18.635,0.53) rot=(0,0,1;0rad)
  BaseFeature = -> Cylinder427
  Height = 0.5
  Length = 0.1
  MapMode = 5
  Placement = pos=(-20.95,18.635,0.53) rot=(0,0,1;0rad)
  Support = -> [XY_Plane224]
  Width = 0.23
FEATURE [PartDesign::SubtractiveBox] Box2069
  AttacherType = Attacher::AttachEngine3D
  AttachmentOffset = pos=(-21.15,18.635,0.297) rot=(0,-1,0;0.174533rad)
  BaseFeature = -> Box2021
  Height = 0.115
  Length = 0.115
  MapMode = 5
  Placement = pos=(-21.15,18.635,0.297) rot=(0,-1,0;0.174533rad)
  Support = -> [XY_Plane224]
  Width = 0.23
FEATURE [PartDesign::Fillet] Fillet605
  Base = -> Box2069 [Edge28]
  BaseFeature = -> Box2069
  Placement = pos=(-21.15,18.635,0.297) rot=(0,-1,0;0.174533rad)
  Radius = 0.375
  SupportTransform = false
FEATURE [PartDesign::AdditiveBox] Box2107
  AttacherType = Attacher::AttachEngine3D
  AttachmentOffset = pos=(-20.7,18.635,1.55) rot=(0,1,0;0.785398rad)
  BaseFeature = -> Fillet605
  Height = 0.375
  Length = 0.23
  MapMode = 5
  Placement = pos=(-20.7,18.635,1.55) rot=(0,1,0;0.785398rad)
  Support = -> [XY_Plane224]
  Width = 0.23
FEATURE [PartDesign::SubtractiveCylinder] Cylinder405
  Angle = 360
  AttacherType = Attacher::AttachEngine3D
  AttachmentOffset = pos=(-20.271,18.635,1.4056) rot=(-1,0,0;1.5708rad)
  BaseFeature = -> Box2107
  Height = 0.23
  MapMode = 5
  Placement = pos=(-20.271,18.635,1.4056) rot=(-1,0,0;1.5708rad)
  Radius = 0.23
  Support = -> [XY_Plane224]
FEATURE [PartDesign::AdditiveBox] Box2015
  AttacherType = Attacher::AttachEngine3D
  AttachmentOffset = pos=(-20.1,18.635,1.635) rot=(0,0,1;0rad)
  BaseFeature = -> Cylinder405
  Height = 0.265
  Length = 0.23
  MapMode = 5
  Placement = pos=(-20.1,18.635,1.635) rot=(0,0,1;0rad)
  Support = -> [XY_Plane224]
  Width = 0.23
FEATURE [PartDesign::Body] Body202  label="pin202"
  Group = -> [Box2070,Box2018,Box2114,Box2002,Box2011,Fillet612,Fillet606,Box2117,Cylinder427,Box2021,Box2069,Fillet605,Box2107,Cylinder405,Box2015]
  Origin = -> Origin219
  Placement = pos=(0,-2,0) rot=(0,0,1;0rad)
  Tip = -> Box2015
FEATURE [PartDesign::Fillet] Fillet614
  Base = -> Box2106 [Edge2]
  BaseFeature = -> Box2106
  Placement = pos=(-21.5005,18.625,0.235) rot=(0,-1,0;0.174533rad)
  Radius = 0.05
  SupportTransform = false
FEATURE [PartDesign::Fillet] Fillet600
  Base = -> Fillet614 [Edge33]
  BaseFeature = -> Fillet614
  Placement = pos=(-21.5005,18.625,0.235) rot=(0,-1,0;0.174533rad)
  Radius = 0.5
  SupportTransform = false
FEATURE [PartDesign::AdditiveBox] Box2072
  AttacherType = Attacher::AttachEngine3D
  AttachmentOffset = pos=(-21.1,18.635,0.305) rot=(0,1,0;0.785398rad)
  BaseFeature = -> Fillet600
  Height = 0.375
  Length = 0.2
  MapMode = 5
  Placement = pos=(-21.1,18.635,0.305) rot=(0,1,0;0.785398rad)
  Support = -> [XY_Plane220]
  Width = 0.23
FEATURE [PartDesign::SubtractiveCylinder] Cylinder414
  Angle = 360
  AttacherType = Attacher::AttachEngine3D
  AttachmentOffset = pos=(-21.055,18.935,0.52) rot=(1,0,0;1.5708rad)
  BaseFeature = -> Box2072
  Height = 0.375
  MapMode = 5
  Placement = pos=(-21.055,18.935,0.52) rot=(1,0,0;1.5708rad)
  Radius = 0.205
  Support = -> [XY_Plane220]
FEATURE [PartDesign::SubtractiveBox] Box2033
  AttacherType = Attacher::AttachEngine3D
  AttachmentOffset = pos=(-20.95,18.635,0.53) rot=(0,0,1;0rad)
  BaseFeature = -> Cylinder414
  Height = 0.5
  Length = 0.1
  MapMode = 5
  Placement = pos=(-20.95,18.635,0.53) rot=(0,0,1;0rad)
  Support = -> [XY_Plane220]
  Width = 0.23
FEATURE [PartDesign::SubtractiveBox] Box2025
  AttacherType = Attacher::AttachEngine3D
  AttachmentOffset = pos=(-21.15,18.635,0.297) rot=(0,-1,0;0.174533rad)
  BaseFeature = -> Box2033
  Height = 0.115
  Length = 0.115
  MapMode = 5
  Placement = pos=(-21.15,18.635,0.297) rot=(0,-1,0;0.174533rad)
  Support = -> [XY_Plane220]
  Width = 0.23
FEATURE [PartDesign::Fillet] Fillet615
  Base = -> Box2038 [Edge2]
  BaseFeature = -> Box2038
  Placement = pos=(-21.5005,18.625,0.235) rot=(0,-1,0;0.174533rad)
  Radius = 0.05
  SupportTransform = false
FEATURE [PartDesign::Fillet] Fillet602
  Base = -> Fillet615 [Edge33]
  BaseFeature = -> Fillet615
  Placement = pos=(-21.5005,18.625,0.235) rot=(0,-1,0;0.174533rad)
  Radius = 0.5
  SupportTransform = false
FEATURE [PartDesign::AdditiveBox] Box2012
  AttacherType = Attacher::AttachEngine3D
  AttachmentOffset = pos=(-21.1,18.635,0.305) rot=(0,1,0;0.785398rad)
  BaseFeature = -> Fillet602
  Height = 0.375
  Length = 0.2
  MapMode = 5
  Placement = pos=(-21.1,18.635,0.305) rot=(0,1,0;0.785398rad)
  Support = -> [XY_Plane227]
  Width = 0.23
FEATURE [PartDesign::SubtractiveCylinder] Cylinder410
  Angle = 360
  AttacherType = Attacher::AttachEngine3D
  AttachmentOffset = pos=(-21.055,18.935,0.52) rot=(1,0,0;1.5708rad)
  BaseFeature = -> Box2012
  Height = 0.375
  MapMode = 5
  Placement = pos=(-21.055,18.935,0.52) rot=(1,0,0;1.5708rad)
  Radius = 0.205
  Support = -> [XY_Plane227]
FEATURE [PartDesign::SubtractiveBox] Box2040
  AttacherType = Attacher::AttachEngine3D
  AttachmentOffset = pos=(-20.95,18.635,0.53) rot=(0,0,1;0rad)
  BaseFeature = -> Cylinder410
  Height = 0.5
  Length = 0.1
  MapMode = 5
  Placement = pos=(-20.95,18.635,0.53) rot=(0,0,1;0rad)
  Support = -> [XY_Plane227]
  Width = 0.23
FEATURE [PartDesign::SubtractiveBox] Box2013
  AttacherType = Attacher::AttachEngine3D
  AttachmentOffset = pos=(-21.15,18.635,0.297) rot=(0,-1,0;0.174533rad)
  BaseFeature = -> Box2040
  Height = 0.115
  Length = 0.115
  MapMode = 5
  Placement = pos=(-21.15,18.635,0.297) rot=(0,-1,0;0.174533rad)
  Support = -> [XY_Plane227]
  Width = 0.23
FEATURE [PartDesign::Fillet] Fillet609
  Base = -> Box2013 [Edge28]
  BaseFeature = -> Box2013
  Placement = pos=(-21.15,18.635,0.297) rot=(0,-1,0;0.174533rad)
  Radius = 0.375
  SupportTransform = false
FEATURE [PartDesign::AdditiveBox] Box2031
  AttacherType = Attacher::AttachEngine3D
  AttachmentOffset = pos=(-20.7,18.635,1.55) rot=(0,1,0;0.785398rad)
  BaseFeature = -> Fillet609
  Height = 0.375
  Length = 0.23
  MapMode = 5
  Placement = pos=(-20.7,18.635,1.55) rot=(0,1,0;0.785398rad)
  Support = -> [XY_Plane227]
  Width = 0.23
FEATURE [PartDesign::SubtractiveCylinder] Cylinder406
  Angle = 360
  AttacherType = Attacher::AttachEngine3D
  AttachmentOffset = pos=(-20.271,18.635,1.4056) rot=(-1,0,0;1.5708rad)
  BaseFeature = -> Box2031
  Height = 0.23
  MapMode = 5
  Placement = pos=(-20.271,18.635,1.4056) rot=(-1,0,0;1.5708rad)
  Radius = 0.23
  Support = -> [XY_Plane227]
FEATURE [PartDesign::AdditiveBox] Box2047
  AttacherType = Attacher::AttachEngine3D
  AttachmentOffset = pos=(-20.1,18.635,1.635) rot=(0,0,1;0rad)
  BaseFeature = -> Cylinder406
  Height = 0.265
  Length = 0.23
  MapMode = 5
  Placement = pos=(-20.1,18.635,1.635) rot=(0,0,1;0rad)
  Support = -> [XY_Plane227]
  Width = 0.23
FEATURE [PartDesign::Fillet] Fillet617
  Base = -> Box2098 [Edge2]
  BaseFeature = -> Box2098
  Placement = pos=(-21.5005,18.625,0.235) rot=(0,-1,0;0.174533rad)
  Radius = 0.05
  SupportTransform = false
FEATURE [PartDesign::Body] Body205  label="pin205"
  Group = -> [Box2024,Box2006,Box2121,Box2066,Box2019,Fillet610,Fillet601,Box2108,Cylinder418,Box1991,Box2009,Fillet604,Box2014,Cylinder420,Box2005]
  Origin = -> Origin217
  Placement = pos=(0,-2.5,0) rot=(0,0,1;0rad)
  Tip = -> Box2005
FEATURE [PartDesign::Fillet] Fillet619
  Base = -> Fillet607 [Edge33]
  BaseFeature = -> Fillet607
  Placement = pos=(-21.5005,18.625,0.235) rot=(0,-1,0;0.174533rad)
  Radius = 0.5
  SupportTransform = false
FEATURE [PartDesign::AdditiveBox] Box2122
  AttacherType = Attacher::AttachEngine3D
  AttachmentOffset = pos=(-21.1,18.635,0.305) rot=(0,1,0;0.785398rad)
  BaseFeature = -> Fillet619
  Height = 0.375
  Length = 0.2
  MapMode = 5
  Placement = pos=(-21.1,18.635,0.305) rot=(0,1,0;0.785398rad)
  Support = -> [XY_Plane219]
  Width = 0.23
FEATURE [PartDesign::SubtractiveCylinder] Cylinder425
  Angle = 360
  AttacherType = Attacher::AttachEngine3D
  AttachmentOffset = pos=(-21.055,18.935,0.52) rot=(1,0,0;1.5708rad)
  BaseFeature = -> Box2122
  Height = 0.375
  MapMode = 5
  Placement = pos=(-21.055,18.935,0.52) rot=(1,0,0;1.5708rad)
  Radius = 0.205
  Support = -> [XY_Plane219]
FEATURE [PartDesign::SubtractiveBox] Box2116
  AttacherType = Attacher::AttachEngine3D
  AttachmentOffset = pos=(-20.95,18.635,0.53) rot=(0,0,1;0rad)
  BaseFeature = -> Cylinder425
  Height = 0.5
  Length = 0.1
  MapMode = 5
  Placement = pos=(-20.95,18.635,0.53) rot=(0,0,1;0rad)
  Support = -> [XY_Plane219]
  Width = 0.23
FEATURE [PartDesign::SubtractiveBox] Box2104
  AttacherType = Attacher::AttachEngine3D
  AttachmentOffset = pos=(-21.15,18.635,0.297) rot=(0,-1,0;0.174533rad)
  BaseFeature = -> Box2116
  Height = 0.115
  Length = 0.115
  MapMode = 5
  Placement = pos=(-21.15,18.635,0.297) rot=(0,-1,0;0.174533rad)
  Support = -> [XY_Plane219]
  Width = 0.23
FEATURE [PartDesign::Fillet] Fillet620
  Base = -> Box2016 [Edge2]
  BaseFeature = -> Box2016
  Placement = pos=(-21.5005,18.625,0.235) rot=(0,-1,0;0.174533rad)
  Radius = 0.05
  SupportTransform = false
FEATURE [PartDesign::Fillet] Fillet622
  Base = -> Box2104 [Edge28]
  BaseFeature = -> Box2104
  Placement = pos=(-21.15,18.635,0.297) rot=(0,-1,0;0.174533rad)
  Radius = 0.375
  SupportTransform = false
FEATURE [PartDesign::AdditiveBox] Box2115
  AttacherType = Attacher::AttachEngine3D
  AttachmentOffset = pos=(-20.7,18.635,1.55) rot=(0,1,0;0.785398rad)
  BaseFeature = -> Fillet622
  Height = 0.375
  Length = 0.23
  MapMode = 5
  Placement = pos=(-20.7,18.635,1.55) rot=(0,1,0;0.785398rad)
  Support = -> [XY_Plane219]
  Width = 0.23
FEATURE [PartDesign::SubtractiveCylinder] Cylinder417
  Angle = 360
  AttacherType = Attacher::AttachEngine3D
  AttachmentOffset = pos=(-20.271,18.635,1.4056) rot=(-1,0,0;1.5708rad)
  BaseFeature = -> Box2115
  Height = 0.23
  MapMode = 5
  Placement = pos=(-20.271,18.635,1.4056) rot=(-1,0,0;1.5708rad)
  Radius = 0.23
  Support = -> [XY_Plane219]
FEATURE [PartDesign::AdditiveBox] Box2111
  AttacherType = Attacher::AttachEngine3D
  AttachmentOffset = pos=(-20.1,18.635,1.635) rot=(0,0,1;0rad)
  BaseFeature = -> Cylinder417
  Height = 0.265
  Length = 0.23
  MapMode = 5
  Placement = pos=(-20.1,18.635,1.635) rot=(0,0,1;0rad)
  Support = -> [XY_Plane219]
  Width = 0.23
FEATURE [PartDesign::Body] Body206  label="pin206"
  Group = -> [Box2022,Box2007,Box2105,Box2101,Box2017,Fillet607,Fillet619,Box2122,Cylinder425,Box2116,Box2104,Fillet622,Box2115,Cylinder417,Box2111]
  Origin = -> Origin234
  Placement = pos=(0,-1.5,0) rot=(0,0,1;0rad)
  Tip = -> Box2111
FEATURE [PartDesign::Fillet] Fillet623
  Base = -> Box2051 [Edge2]
  BaseFeature = -> Box2051
  Placement = pos=(-21.5005,18.625,0.235) rot=(0,-1,0;0.174533rad)
  Radius = 0.05
  SupportTransform = false
FEATURE [PartDesign::Fillet] Fillet624
  Base = -> Box2085 [Edge28]
  BaseFeature = -> Box2085
  Placement = pos=(-21.15,18.635,0.297) rot=(0,-1,0;0.174533rad)
  Radius = 0.375
  SupportTransform = false
FEATURE [PartDesign::AdditiveBox] Box2090
  AttacherType = Attacher::AttachEngine3D
  AttachmentOffset = pos=(-20.7,18.635,1.55) rot=(0,1,0;0.785398rad)
  BaseFeature = -> Fillet624
  Height = 0.375
  Length = 0.23
  MapMode = 5
  Placement = pos=(-20.7,18.635,1.55) rot=(0,1,0;0.785398rad)
  Support = -> [XY_Plane229]
  Width = 0.23
FEATURE [PartDesign::SubtractiveCylinder] Cylinder423
  Angle = 360
  AttacherType = Attacher::AttachEngine3D
  AttachmentOffset = pos=(-20.271,18.635,1.4056) rot=(-1,0,0;1.5708rad)
  BaseFeature = -> Box2090
  Height = 0.23
  MapMode = 5
  Placement = pos=(-20.271,18.635,1.4056) rot=(-1,0,0;1.5708rad)
  Radius = 0.23
  Support = -> [XY_Plane229]
FEATURE [PartDesign::AdditiveBox] Box2095
  AttacherType = Attacher::AttachEngine3D
  AttachmentOffset = pos=(-20.1,18.635,1.635) rot=(0,0,1;0rad)
  BaseFeature = -> Cylinder423
  Height = 0.265
  Length = 0.23
  MapMode = 5
  Placement = pos=(-20.1,18.635,1.635) rot=(0,0,1;0rad)
  Support = -> [XY_Plane229]
  Width = 0.23
FEATURE [PartDesign::Body] Body201  label="pin201"
  Group = -> [Box2112,Box2080,Box2076,Box2099,Box2089,Fillet608,Fillet611,Box2084,Cylinder422,Box2092,Box2085,Fillet624,Box2090,Cylinder423,Box2095]
  Origin = -> Origin208
  Placement = pos=(0,-0.5,0) rot=(0,0,1;0rad)
  Tip = -> Box2095
FEATURE [PartDesign::Body] Body211  label="pin211"
  Group = -> [Box2035,Box2043,Box2027,Box2032,Box2038,Fillet615,Fillet602,Box2012,Cylinder410,Box2040,Box2013,Fillet609,Box2031,Cylinder406,Box2047]
  Origin = -> Origin212
  Placement = pos=(0,-5,0) rot=(0,0,1;0rad)
  Tip = -> Box2047
FEATURE [PartDesign::Fillet] Fillet629
  Base = -> Box2058 [Edge2]
  BaseFeature = -> Box2058
  Placement = pos=(-21.5005,18.625,0.235) rot=(0,-1,0;0.174533rad)
  Radius = 0.05
  SupportTransform = false
FEATURE [PartDesign::Fillet] Fillet627
  Base = -> Fillet629 [Edge33]
  BaseFeature = -> Fillet629
  Placement = pos=(-21.5005,18.625,0.235) rot=(0,-1,0;0.174533rad)
  Radius = 0.5
  SupportTransform = false
FEATURE [PartDesign::AdditiveBox] Box2077
  AttacherType = Attacher::AttachEngine3D
  AttachmentOffset = pos=(-21.1,18.635,0.305) rot=(0,1,0;0.785398rad)
  BaseFeature = -> Fillet627
  Height = 0.375
  Length = 0.2
  MapMode = 5
  Placement = pos=(-21.1,18.635,0.305) rot=(0,1,0;0.785398rad)
  Support = -> [XY_Plane226]
  Width = 0.23
FEATURE [PartDesign::SubtractiveCylinder] Cylinder416
  Angle = 360
  AttacherType = Attacher::AttachEngine3D
  AttachmentOffset = pos=(-21.055,18.935,0.52) rot=(1,0,0;1.5708rad)
  BaseFeature = -> Box2077
  Height = 0.375
  MapMode = 5
  Placement = pos=(-21.055,18.935,0.52) rot=(1,0,0;1.5708rad)
  Radius = 0.205
  Support = -> [XY_Plane226]
FEATURE [PartDesign::SubtractiveBox] Box2067
  AttacherType = Attacher::AttachEngine3D
  AttachmentOffset = pos=(-20.95,18.635,0.53) rot=(0,0,1;0rad)
  BaseFeature = -> Cylinder416
  Height = 0.5
  Length = 0.1
  MapMode = 5
  Placement = pos=(-20.95,18.635,0.53) rot=(0,0,1;0rad)
  Support = -> [XY_Plane226]
  Width = 0.23
FEATURE [PartDesign::SubtractiveBox] Box2059
  AttacherType = Attacher::AttachEngine3D
  AttachmentOffset = pos=(-21.15,18.635,0.297) rot=(0,-1,0;0.174533rad)
  BaseFeature = -> Box2067
  Height = 0.115
  Length = 0.115
  MapMode = 5
  Placement = pos=(-21.15,18.635,0.297) rot=(0,-1,0;0.174533rad)
  Support = -> [XY_Plane226]
  Width = 0.23
FEATURE [PartDesign::Fillet] Fillet625
  Base = -> Box2059 [Edge28]
  BaseFeature = -> Box2059
  Placement = pos=(-21.15,18.635,0.297) rot=(0,-1,0;0.174533rad)
  Radius = 0.375
  SupportTransform = false
FEATURE [PartDesign::AdditiveBox] Box2065
  AttacherType = Attacher::AttachEngine3D
  AttachmentOffset = pos=(-20.7,18.635,1.55) rot=(0,1,0;0.785398rad)
  BaseFeature = -> Fillet625
  Height = 0.375
  Length = 0.23
  MapMode = 5
  Placement = pos=(-20.7,18.635,1.55) rot=(0,1,0;0.785398rad)
  Support = -> [XY_Plane226]
  Width = 0.23
FEATURE [PartDesign::SubtractiveCylinder] Cylinder415
  Angle = 360
  AttacherType = Attacher::AttachEngine3D
  AttachmentOffset = pos=(-20.271,18.635,1.4056) rot=(-1,0,0;1.5708rad)
  BaseFeature = -> Box2065
  Height = 0.23
  MapMode = 5
  Placement = pos=(-20.271,18.635,1.4056) rot=(-1,0,0;1.5708rad)
  Radius = 0.23
  Support = -> [XY_Plane226]
FEATURE [PartDesign::AdditiveBox] Box2050
  AttacherType = Attacher::AttachEngine3D
  AttachmentOffset = pos=(-20.1,18.635,1.635) rot=(0,0,1;0rad)
  BaseFeature = -> Cylinder415
  Height = 0.265
  Length = 0.23
  MapMode = 5
  Placement = pos=(-20.1,18.635,1.635) rot=(0,0,1;0rad)
  Support = -> [XY_Plane226]
  Width = 0.23
FEATURE [PartDesign::Body] Body209  label="pin209"
  Group = -> [Box2049,Box2063,Box2046,Box2068,Box2058,Fillet629,Fillet627,Box2077,Cylinder416,Box2067,Box2059,Fillet625,Box2065,Cylinder415,Box2050]
  Origin = -> Origin246
  Placement = pos=(0,-4,0) rot=(0,0,1;0rad)
  Tip = -> Box2050
FEATURE [PartDesign::Fillet] Fillet630
  Base = -> Fillet620 [Edge33]
  BaseFeature = -> Fillet620
  Placement = pos=(-21.5005,18.625,0.235) rot=(0,-1,0;0.174533rad)
  Radius = 0.5
  SupportTransform = false
FEATURE [PartDesign::AdditiveBox] Box2044
  AttacherType = Attacher::AttachEngine3D
  AttachmentOffset = pos=(-21.1,18.635,0.305) rot=(0,1,0;0.785398rad)
  BaseFeature = -> Fillet630
  Height = 0.375
  Length = 0.2
  MapMode = 5
  Placement = pos=(-21.1,18.635,0.305) rot=(0,1,0;0.785398rad)
  Support = -> [XY_Plane222]
  Width = 0.23
FEATURE [PartDesign::SubtractiveCylinder] Cylinder412
  Angle = 360
  AttacherType = Attacher::AttachEngine3D
  AttachmentOffset = pos=(-21.055,18.935,0.52) rot=(1,0,0;1.5708rad)
  BaseFeature = -> Box2044
  Height = 0.375
  MapMode = 5
  Placement = pos=(-21.055,18.935,0.52) rot=(1,0,0;1.5708rad)
  Radius = 0.205
  Support = -> [XY_Plane222]
FEATURE [PartDesign::SubtractiveBox] Box2041
  AttacherType = Attacher::AttachEngine3D
  AttachmentOffset = pos=(-20.95,18.635,0.53) rot=(0,0,1;0rad)
  BaseFeature = -> Cylinder412
  Height = 0.5
  Length = 0.1
  MapMode = 5
  Placement = pos=(-20.95,18.635,0.53) rot=(0,0,1;0rad)
  Support = -> [XY_Plane222]
  Width = 0.23
FEATURE [PartDesign::SubtractiveBox] Box2036
  AttacherType = Attacher::AttachEngine3D
  AttachmentOffset = pos=(-21.15,18.635,0.297) rot=(0,-1,0;0.174533rad)
  BaseFeature = -> Box2041
  Height = 0.115
  Length = 0.115
  MapMode = 5
  Placement = pos=(-21.15,18.635,0.297) rot=(0,-1,0;0.174533rad)
  Support = -> [XY_Plane222]
  Width = 0.23
FEATURE [PartDesign::Fillet] Fillet618
  Base = -> Box2036 [Edge28]
  BaseFeature = -> Box2036
  Placement = pos=(-21.15,18.635,0.297) rot=(0,-1,0;0.174533rad)
  Radius = 0.375
  SupportTransform = false
FEATURE [PartDesign::AdditiveBox] Box2048
  AttacherType = Attacher::AttachEngine3D
  AttachmentOffset = pos=(-20.7,18.635,1.55) rot=(0,1,0;0.785398rad)
  BaseFeature = -> Fillet618
  Height = 0.375
  Length = 0.23
  MapMode = 5
  Placement = pos=(-20.7,18.635,1.55) rot=(0,1,0;0.785398rad)
  Support = -> [XY_Plane222]
  Width = 0.23
FEATURE [PartDesign::SubtractiveCylinder] Cylinder413
  Angle = 360
  AttacherType = Attacher::AttachEngine3D
  AttachmentOffset = pos=(-20.271,18.635,1.4056) rot=(-1,0,0;1.5708rad)
  BaseFeature = -> Box2048
  Height = 0.23
  MapMode = 5
  Placement = pos=(-20.271,18.635,1.4056) rot=(-1,0,0;1.5708rad)
  Radius = 0.23
  Support = -> [XY_Plane222]
FEATURE [PartDesign::AdditiveBox] Box2042
  AttacherType = Attacher::AttachEngine3D
  AttachmentOffset = pos=(-20.1,18.635,1.635) rot=(0,0,1;0rad)
  BaseFeature = -> Cylinder413
  Height = 0.265
  Length = 0.23
  MapMode = 5
  Placement = pos=(-20.1,18.635,1.635) rot=(0,0,1;0rad)
  Support = -> [XY_Plane222]
  Width = 0.23
FEATURE [PartDesign::Body] Body212  label="pin212"
  Group = -> [Box2054,Box2060,Box2008,Box2020,Box2016,Fillet620,Fillet630,Box2044,Cylinder412,Box2041,Box2036,Fillet618,Box2048,Cylinder413,Box2042]
  Origin = -> Origin216
  Placement = pos=(0,-5.5,0) rot=(0,0,1;0rad)
  Tip = -> Box2042
FEATURE [PartDesign::Fillet] Fillet631
  Base = -> Box2025 [Edge28]
  BaseFeature = -> Box2025
  Placement = pos=(-21.15,18.635,0.297) rot=(0,-1,0;0.174533rad)
  Radius = 0.375
  SupportTransform = false
FEATURE [PartDesign::AdditiveBox] Box2082
  AttacherType = Attacher::AttachEngine3D
  AttachmentOffset = pos=(-20.7,18.635,1.55) rot=(0,1,0;0.785398rad)
  BaseFeature = -> Fillet631
  Height = 0.375
  Length = 0.23
  MapMode = 5
  Placement = pos=(-20.7,18.635,1.55) rot=(0,1,0;0.785398rad)
  Support = -> [XY_Plane220]
  Width = 0.23
FEATURE [PartDesign::SubtractiveCylinder] Cylinder408
  Angle = 360
  AttacherType = Attacher::AttachEngine3D
  AttachmentOffset = pos=(-20.271,18.635,1.4056) rot=(-1,0,0;1.5708rad)
  BaseFeature = -> Box2082
  Height = 0.23
  MapMode = 5
  Placement = pos=(-20.271,18.635,1.4056) rot=(-1,0,0;1.5708rad)
  Radius = 0.23
  Support = -> [XY_Plane220]
FEATURE [PartDesign::AdditiveBox] Box2094
  AttacherType = Attacher::AttachEngine3D
  AttachmentOffset = pos=(-20.1,18.635,1.635) rot=(0,0,1;0rad)
  BaseFeature = -> Cylinder408
  Height = 0.265
  Length = 0.23
  MapMode = 5
  Placement = pos=(-20.1,18.635,1.635) rot=(0,0,1;0rad)
  Support = -> [XY_Plane220]
  Width = 0.23
FEATURE [PartDesign::Body] Body204  label="pin204"
  Group = -> [Box2103,Box2110,Box2088,Box2087,Box2106,Fillet614,Fillet600,Box2072,Cylinder414,Box2033,Box2025,Fillet631,Box2082,Cylinder408,Box2094]
  Origin = -> Origin220
  Tip = -> Box2094
FEATURE [PartDesign::Fillet] Fillet632
  Base = -> Fillet623 [Edge33]
  BaseFeature = -> Fillet623
  Placement = pos=(-21.5005,18.625,0.235) rot=(0,-1,0;0.174533rad)
  Radius = 0.5
  SupportTransform = false
FEATURE [PartDesign::AdditiveBox] Box2028
  AttacherType = Attacher::AttachEngine3D
  AttachmentOffset = pos=(-21.1,18.635,0.305) rot=(0,1,0;0.785398rad)
  BaseFeature = -> Fillet632
  Height = 0.375
  Length = 0.2
  MapMode = 5
  Placement = pos=(-21.1,18.635,0.305) rot=(0,1,0;0.785398rad)
  Support = -> [XY_Plane230]
  Width = 0.23
FEATURE [PartDesign::SubtractiveCylinder] Cylinder407
  Angle = 360
  AttacherType = Attacher::AttachEngine3D
  AttachmentOffset = pos=(-21.055,18.935,0.52) rot=(1,0,0;1.5708rad)
  BaseFeature = -> Box2028
  Height = 0.375
  MapMode = 5
  Placement = pos=(-21.055,18.935,0.52) rot=(1,0,0;1.5708rad)
  Radius = 0.205
  Support = -> [XY_Plane230]
FEATURE [PartDesign::SubtractiveBox] Box2026
  AttacherType = Attacher::AttachEngine3D
  AttachmentOffset = pos=(-20.95,18.635,0.53) rot=(0,0,1;0rad)
  BaseFeature = -> Cylinder407
  Height = 0.5
  Length = 0.1
  MapMode = 5
  Placement = pos=(-20.95,18.635,0.53) rot=(0,0,1;0rad)
  Support = -> [XY_Plane230]
  Width = 0.23
FEATURE [PartDesign::SubtractiveBox] Box2062
  AttacherType = Attacher::AttachEngine3D
  AttachmentOffset = pos=(-21.15,18.635,0.297) rot=(0,-1,0;0.174533rad)
  BaseFeature = -> Box2026
  Height = 0.115
  Length = 0.115
  MapMode = 5
  Placement = pos=(-21.15,18.635,0.297) rot=(0,-1,0;0.174533rad)
  Support = -> [XY_Plane230]
  Width = 0.23
FEATURE [PartDesign::Fillet] Fillet628
  Base = -> Box2062 [Edge28]
  BaseFeature = -> Box2062
  Placement = pos=(-21.15,18.635,0.297) rot=(0,-1,0;0.174533rad)
  Radius = 0.375
  SupportTransform = false
FEATURE [PartDesign::AdditiveBox] Box2055
  AttacherType = Attacher::AttachEngine3D
  AttachmentOffset = pos=(-20.7,18.635,1.55) rot=(0,1,0;0.785398rad)
  BaseFeature = -> Fillet628
  Height = 0.375
  Length = 0.23
  MapMode = 5
  Placement = pos=(-20.7,18.635,1.55) rot=(0,1,0;0.785398rad)
  Support = -> [XY_Plane230]
  Width = 0.23
FEATURE [PartDesign::SubtractiveCylinder] Cylinder411
  Angle = 360
  AttacherType = Attacher::AttachEngine3D
  AttachmentOffset = pos=(-20.271,18.635,1.4056) rot=(-1,0,0;1.5708rad)
  BaseFeature = -> Box2055
  Height = 0.23
  MapMode = 5
  Placement = pos=(-20.271,18.635,1.4056) rot=(-1,0,0;1.5708rad)
  Radius = 0.23
  Support = -> [XY_Plane230]
FEATURE [PartDesign::AdditiveBox] Box2081
  AttacherType = Attacher::AttachEngine3D
  AttachmentOffset = pos=(-20.1,18.635,1.635) rot=(0,0,1;0rad)
  BaseFeature = -> Cylinder411
  Height = 0.265
  Length = 0.23
  MapMode = 5
  Placement = pos=(-20.1,18.635,1.635) rot=(0,0,1;0rad)
  Support = -> [XY_Plane230]
  Width = 0.23
FEATURE [PartDesign::Body] Body203  label="pin203"
  Group = -> [Box2052,Box2075,Box2039,Box2091,Box2051,Fillet623,Fillet632,Box2028,Cylinder407,Box2026,Box2062,Fillet628,Box2055,Cylinder411,Box2081]
  Origin = -> Origin218
  Placement = pos=(0,-3,0) rot=(0,0,1;0rad)
  Tip = -> Box2081
FEATURE [PartDesign::Fillet] Fillet633
  Base = -> Fillet617 [Edge33]
  BaseFeature = -> Fillet617
  Placement = pos=(-21.5005,18.625,0.235) rot=(0,-1,0;0.174533rad)
  Radius = 0.5
  SupportTransform = false
FEATURE [PartDesign::AdditiveBox] Box2071
  AttacherType = Attacher::AttachEngine3D
  AttachmentOffset = pos=(-21.1,18.635,0.305) rot=(0,1,0;0.785398rad)
  BaseFeature = -> Fillet633
  Height = 0.375
  Length = 0.2
  MapMode = 5
  Placement = pos=(-21.1,18.635,0.305) rot=(0,1,0;0.785398rad)
  Support = -> [XY_Plane225]
  Width = 0.23
FEATURE [PartDesign::SubtractiveCylinder] Cylinder426
  Angle = 360
  AttacherType = Attacher::AttachEngine3D
  AttachmentOffset = pos=(-21.055,18.935,0.52) rot=(1,0,0;1.5708rad)
  BaseFeature = -> Box2071
  Height = 0.375
  MapMode = 5
  Placement = pos=(-21.055,18.935,0.52) rot=(1,0,0;1.5708rad)
  Radius = 0.205
  Support = -> [XY_Plane225]
FEATURE [PartDesign::SubtractiveBox] Box2096
  AttacherType = Attacher::AttachEngine3D
  AttachmentOffset = pos=(-20.95,18.635,0.53) rot=(0,0,1;0rad)
  BaseFeature = -> Cylinder426
  Height = 0.5
  Length = 0.1
  MapMode = 5
  Placement = pos=(-20.95,18.635,0.53) rot=(0,0,1;0rad)
  Support = -> [XY_Plane225]
  Width = 0.23
FEATURE [PartDesign::SubtractiveBox] Box2097
  AttacherType = Attacher::AttachEngine3D
  AttachmentOffset = pos=(-21.15,18.635,0.297) rot=(0,-1,0;0.174533rad)
  BaseFeature = -> Box2096
  Height = 0.115
  Length = 0.115
  MapMode = 5
  Placement = pos=(-21.15,18.635,0.297) rot=(0,-1,0;0.174533rad)
  Support = -> [XY_Plane225]
  Width = 0.23
FEATURE [PartDesign::Fillet] Fillet603
  Base = -> Box2097 [Edge28]
  BaseFeature = -> Box2097
  Placement = pos=(-21.15,18.635,0.297) rot=(0,-1,0;0.174533rad)
  Radius = 0.375
  SupportTransform = false
FEATURE [PartDesign::AdditiveBox] Box2093
  AttacherType = Attacher::AttachEngine3D
  AttachmentOffset = pos=(-20.7,18.635,1.55) rot=(0,1,0;0.785398rad)
  BaseFeature = -> Fillet603
  Height = 0.375
  Length = 0.23
  MapMode = 5
  Placement = pos=(-20.7,18.635,1.55) rot=(0,1,0;0.785398rad)
  Support = -> [XY_Plane225]
  Width = 0.23
FEATURE [PartDesign::SubtractiveCylinder] Cylinder424
  Angle = 360
  AttacherType = Attacher::AttachEngine3D
  AttachmentOffset = pos=(-20.271,18.635,1.4056) rot=(-1,0,0;1.5708rad)
  BaseFeature = -> Box2093
  Height = 0.23
  MapMode = 5
  Placement = pos=(-20.271,18.635,1.4056) rot=(-1,0,0;1.5708rad)
  Radius = 0.23
  Support = -> [XY_Plane225]
FEATURE [PartDesign::AdditiveBox] Box2109
  AttacherType = Attacher::AttachEngine3D
  AttachmentOffset = pos=(-20.1,18.635,1.635) rot=(0,0,1;0rad)
  BaseFeature = -> Cylinder424
  Height = 0.265
  Length = 0.23
  MapMode = 5
  Placement = pos=(-20.1,18.635,1.635) rot=(0,0,1;0rad)
  Support = -> [XY_Plane225]
  Width = 0.23
FEATURE [PartDesign::Body] Body210  label="pin210"
  Group = -> [Box2113,Box2120,Box2100,Box2102,Box2098,Fillet617,Fillet633,Box2071,Cylinder426,Box2096,Box2097,Fillet603,Box2093,Cylinder424,Box2109]
  Origin = -> Origin215
  Placement = pos=(0,-1,0) rot=(0,0,1;0rad)
  Tip = -> Box2109
FEATURE [PartDesign::Fillet] Fillet634
  Base = -> Box2056 [Edge2]
  BaseFeature = -> Box2056
  Placement = pos=(-21.5005,18.625,0.235) rot=(0,-1,0;0.174533rad)
  Radius = 0.05
  SupportTransform = false
FEATURE [PartDesign::Fillet] Fillet621
  Base = -> Fillet634 [Edge33]
  BaseFeature = -> Fillet634
  Placement = pos=(-21.5005,18.625,0.235) rot=(0,-1,0;0.174533rad)
  Radius = 0.5
  SupportTransform = false
FEATURE [PartDesign::AdditiveBox] Box2074
  AttacherType = Attacher::AttachEngine3D
  AttachmentOffset = pos=(-21.1,18.635,0.305) rot=(0,1,0;0.785398rad)
  BaseFeature = -> Fillet621
  Height = 0.375
  Length = 0.2
  MapMode = 5
  Placement = pos=(-21.1,18.635,0.305) rot=(0,1,0;0.785398rad)
  Support = -> [XY_Plane231]
  Width = 0.23
FEATURE [PartDesign::SubtractiveCylinder] Cylinder421
  Angle = 360
  AttacherType = Attacher::AttachEngine3D
  AttachmentOffset = pos=(-21.055,18.935,0.52) rot=(1,0,0;1.5708rad)
  BaseFeature = -> Box2074
  Height = 0.375
  MapMode = 5
  Placement = pos=(-21.055,18.935,0.52) rot=(1,0,0;1.5708rad)
  Radius = 0.205
  Support = -> [XY_Plane231]
FEATURE [PartDesign::SubtractiveBox] Box2078
  AttacherType = Attacher::AttachEngine3D
  AttachmentOffset = pos=(-20.95,18.635,0.53) rot=(0,0,1;0rad)
  BaseFeature = -> Cylinder421
  Height = 0.5
  Length = 0.1
  MapMode = 5
  Placement = pos=(-20.95,18.635,0.53) rot=(0,0,1;0rad)
  Support = -> [XY_Plane231]
  Width = 0.23
FEATURE [PartDesign::SubtractiveBox] Box2061
  AttacherType = Attacher::AttachEngine3D
  AttachmentOffset = pos=(-21.15,18.635,0.297) rot=(0,-1,0;0.174533rad)
  BaseFeature = -> Box2078
  Height = 0.115
  Length = 0.115
  MapMode = 5
  Placement = pos=(-21.15,18.635,0.297) rot=(0,-1,0;0.174533rad)
  Support = -> [XY_Plane231]
  Width = 0.23
FEATURE [PartDesign::Fillet] Fillet613
  Base = -> Box2061 [Edge28]
  BaseFeature = -> Box2061
  Placement = pos=(-21.15,18.635,0.297) rot=(0,-1,0;0.174533rad)
  Radius = 0.375
  SupportTransform = false
FEATURE [PartDesign::AdditiveBox] Box2079
  AttacherType = Attacher::AttachEngine3D
  AttachmentOffset = pos=(-20.7,18.635,1.55) rot=(0,1,0;0.785398rad)
  BaseFeature = -> Fillet613
  Height = 0.375
  Length = 0.23
  MapMode = 5
  Placement = pos=(-20.7,18.635,1.55) rot=(0,1,0;0.785398rad)
  Support = -> [XY_Plane231]
  Width = 0.23
FEATURE [PartDesign::SubtractiveCylinder] Cylinder419
  Angle = 360
  AttacherType = Attacher::AttachEngine3D
  AttachmentOffset = pos=(-20.271,18.635,1.4056) rot=(-1,0,0;1.5708rad)
  BaseFeature = -> Box2079
  Height = 0.23
  MapMode = 5
  Placement = pos=(-20.271,18.635,1.4056) rot=(-1,0,0;1.5708rad)
  Radius = 0.23
  Support = -> [XY_Plane231]
FEATURE [PartDesign::AdditiveBox] Box2053
  AttacherType = Attacher::AttachEngine3D
  AttachmentOffset = pos=(-20.1,18.635,1.635) rot=(0,0,1;0rad)
  BaseFeature = -> Cylinder419
  Height = 0.265
  Length = 0.23
  MapMode = 5
  Placement = pos=(-20.1,18.635,1.635) rot=(0,0,1;0rad)
  Support = -> [XY_Plane231]
  Width = 0.23
FEATURE [PartDesign::Body] Body208  label="pin208"
  Group = -> [Box2064,Box2073,Box2086,Box2057,Box2056,Fillet634,Fillet621,Box2074,Cylinder421,Box2078,Box2061,Fillet613,Box2079,Cylinder419,Box2053]
  Origin = -> Origin235
  Placement = pos=(0,-3.5,0) rot=(0,0,1;0rad)
  Tip = -> Box2053
FEATURE [PartDesign::Fillet] Fillet635
  Base = -> Box2083 [Edge2]
  BaseFeature = -> Box2083
  Placement = pos=(-21.5005,18.625,0.235) rot=(0,-1,0;0.174533rad)
  Radius = 0.05
  SupportTransform = false
FEATURE [PartDesign::Fillet] Fillet616
  Base = -> Fillet635 [Edge33]
  BaseFeature = -> Fillet635
  Placement = pos=(-21.5005,18.625,0.235) rot=(0,-1,0;0.174533rad)
  Radius = 0.5
  SupportTransform = false
FEATURE [PartDesign::AdditiveBox] Box2004
  AttacherType = Attacher::AttachEngine3D
  AttachmentOffset = pos=(-21.1,18.635,0.305) rot=(0,1,0;0.785398rad)
  BaseFeature = -> Fillet616
  Height = 0.375
  Length = 0.2
  MapMode = 5
  Placement = pos=(-21.1,18.635,0.305) rot=(0,1,0;0.785398rad)
  Support = -> [XY_Plane228]
  Width = 0.23
FEATURE [PartDesign::SubtractiveCylinder] Cylinder404
  Angle = 360
  AttacherType = Attacher::AttachEngine3D
  AttachmentOffset = pos=(-21.055,18.935,0.52) rot=(1,0,0;1.5708rad)
  BaseFeature = -> Box2004
  Height = 0.375
  MapMode = 5
  Placement = pos=(-21.055,18.935,0.52) rot=(1,0,0;1.5708rad)
  Radius = 0.205
  Support = -> [XY_Plane228]
FEATURE [PartDesign::SubtractiveBox] Box2003
  AttacherType = Attacher::AttachEngine3D
  AttachmentOffset = pos=(-20.95,18.635,0.53) rot=(0,0,1;0rad)
  BaseFeature = -> Cylinder404
  Height = 0.5
  Length = 0.1
  MapMode = 5
  Placement = pos=(-20.95,18.635,0.53) rot=(0,0,1;0rad)
  Support = -> [XY_Plane228]
  Width = 0.23
FEATURE [PartDesign::SubtractiveBox] Box2010
  AttacherType = Attacher::AttachEngine3D
  AttachmentOffset = pos=(-21.15,18.635,0.297) rot=(0,-1,0;0.174533rad)
  BaseFeature = -> Box2003
  Height = 0.115
  Length = 0.115
  MapMode = 5
  Placement = pos=(-21.15,18.635,0.297) rot=(0,-1,0;0.174533rad)
  Support = -> [XY_Plane228]
  Width = 0.23
FEATURE [PartDesign::Fillet] Fillet626
  Base = -> Box2010 [Edge28]
  BaseFeature = -> Box2010
  Placement = pos=(-21.15,18.635,0.297) rot=(0,-1,0;0.174533rad)
  Radius = 0.375
  SupportTransform = false
FEATURE [PartDesign::AdditiveBox] Box2030
  AttacherType = Attacher::AttachEngine3D
  AttachmentOffset = pos=(-20.7,18.635,1.55) rot=(0,1,0;0.785398rad)
  BaseFeature = -> Fillet626
  Height = 0.375
  Length = 0.23
  MapMode = 5
  Placement = pos=(-20.7,18.635,1.55) rot=(0,1,0;0.785398rad)
  Support = -> [XY_Plane228]
  Width = 0.23
FEATURE [PartDesign::SubtractiveCylinder] Cylinder409
  Angle = 360
  AttacherType = Attacher::AttachEngine3D
  AttachmentOffset = pos=(-20.271,18.635,1.4056) rot=(-1,0,0;1.5708rad)
  BaseFeature = -> Box2030
  Height = 0.23
  MapMode = 5
  Placement = pos=(-20.271,18.635,1.4056) rot=(-1,0,0;1.5708rad)
  Radius = 0.23
  Support = -> [XY_Plane228]
FEATURE [PartDesign::AdditiveBox] Box2023
  AttacherType = Attacher::AttachEngine3D
  AttachmentOffset = pos=(-20.1,18.635,1.635) rot=(0,0,1;0rad)
  BaseFeature = -> Cylinder409
  Height = 0.265
  Length = 0.23
  MapMode = 5
  Placement = pos=(-20.1,18.635,1.635) rot=(0,0,1;0rad)
  Support = -> [XY_Plane228]
  Width = 0.23
FEATURE [PartDesign::Body] Body207  label="pin207"
  Group = -> [Box2037,Box2045,Box2029,Box2034,Box2083,Fillet635,Fillet616,Box2004,Cylinder404,Box2003,Box2010,Fillet626,Box2030,Cylinder409,Box2023]
  Origin = -> Origin223
  Placement = pos=(0,-4.5,0) rot=(0,0,1;0rad)
  Tip = -> Box2023
FEATURE [App::Part] Part018  label="Pin-set016"
  Group = -> [Body204,Body201,Body210,Body206,Body202,Body205,Body203,Body208,Body209,Body207,Body211,Body212]
  Origin = -> Origin228
  Placement = pos=(0,-24,0) rot=(0,0,1;0rad)
FEATURE [PartDesign::AdditiveBox] Box2157
  AttacherType = Attacher::AttachEngine3D
  AttachmentOffset = pos=(-21.3,18.635,0) rot=(0,0,1;0rad)
  Height = 1.9
  Length = 1.3
  MapMode = 5
  Placement = pos=(-21.3,18.635,0) rot=(0,0,1;0rad)
  Support = -> [XY_Plane240]
  Width = 0.23
FEATURE [PartDesign::AdditiveBox] Box2159
  AttacherType = Attacher::AttachEngine3D
  AttachmentOffset = pos=(-21.3,18.635,0) rot=(0,0,1;0rad)
  Height = 1.9
  Length = 1.3
  MapMode = 5
  Placement = pos=(-21.3,18.635,0) rot=(0,0,1;0rad)
  Support = -> [XY_Plane241]
  Width = 0.23
FEATURE [PartDesign::AdditiveBox] Box2164
  AttacherType = Attacher::AttachEngine3D
  AttachmentOffset = pos=(-21.3,18.635,0) rot=(0,0,1;0rad)
  Height = 1.9
  Length = 1.3
  MapMode = 5
  Placement = pos=(-21.3,18.635,0) rot=(0,0,1;0rad)
  Support = -> [XY_Plane236]
  Width = 0.23
FEATURE [PartDesign::SubtractiveBox] Box2166
  AttacherType = Attacher::AttachEngine3D
  AttachmentOffset = pos=(-21.35,18.635,0.35) rot=(0,0,1;0rad)
  BaseFeature = -> Box2159
  Height = 1.55
  Length = 0.5
  MapMode = 5
  Placement = pos=(-21.35,18.635,0.35) rot=(0,0,1;0rad)
  Support = -> [XY_Plane241]
  Width = 0.23
FEATURE [PartDesign::SubtractiveBox] Box2153
  AttacherType = Attacher::AttachEngine3D
  AttachmentOffset = pos=(-20.5,18.63,0) rot=(0,0,1;0rad)
  BaseFeature = -> Box2166
  Height = 1.635
  Length = 0.5
  MapMode = 5
  Placement = pos=(-20.5,18.63,0) rot=(0,0,1;0rad)
  Support = -> [XY_Plane241]
  Width = 0.25
FEATURE [PartDesign::SubtractiveBox] Box2154
  AttacherType = Attacher::AttachEngine3D
  AttachmentOffset = pos=(-21.19,18.635,-0.12) rot=(0,-1,0;0.15708rad)
  BaseFeature = -> Box2153
  Height = 0.12
  Length = 0.725
  MapMode = 5
  Placement = pos=(-21.19,18.635,-0.12) rot=(0,-1,0;0.15708rad)
  Support = -> [XY_Plane241]
  Width = 0.25
FEATURE [PartDesign::SubtractiveBox] Box2169
  AttacherType = Attacher::AttachEngine3D
  AttachmentOffset = pos=(-21.35,18.635,0.35) rot=(0,0,1;0rad)
  BaseFeature = -> Box2157
  Height = 1.55
  Length = 0.5
  MapMode = 5
  Placement = pos=(-21.35,18.635,0.35) rot=(0,0,1;0rad)
  Support = -> [XY_Plane240]
  Width = 0.23
FEATURE [PartDesign::SubtractiveBox] Box2156
  AttacherType = Attacher::AttachEngine3D
  AttachmentOffset = pos=(-20.5,18.63,0) rot=(0,0,1;0rad)
  BaseFeature = -> Box2169
  Height = 1.635
  Length = 0.5
  MapMode = 5
  Placement = pos=(-20.5,18.63,0) rot=(0,0,1;0rad)
  Support = -> [XY_Plane240]
  Width = 0.25
FEATURE [PartDesign::SubtractiveBox] Box2151
  AttacherType = Attacher::AttachEngine3D
  AttachmentOffset = pos=(-21.19,18.635,-0.12) rot=(0,-1,0;0.15708rad)
  BaseFeature = -> Box2156
  Height = 0.12
  Length = 0.725
  MapMode = 5
  Placement = pos=(-21.19,18.635,-0.12) rot=(0,-1,0;0.15708rad)
  Support = -> [XY_Plane240]
  Width = 0.25
FEATURE [PartDesign::SubtractiveBox] Box2149
  AttacherType = Attacher::AttachEngine3D
  AttachmentOffset = pos=(-21.5005,18.625,0.235) rot=(0,-1,0;0.174533rad)
  BaseFeature = -> Box2151
  Height = 0.3
  Length = 0.6605
  MapMode = 5
  Placement = pos=(-21.5005,18.625,0.235) rot=(0,-1,0;0.174533rad)
  Support = -> [XY_Plane240]
  Width = 0.25
FEATURE [PartDesign::AdditiveBox] Box2173
  AttacherType = Attacher::AttachEngine3D
  AttachmentOffset = pos=(-21.3,18.635,0) rot=(0,0,1;0rad)
  Height = 1.9
  Length = 1.3
  MapMode = 5
  Placement = pos=(-21.3,18.635,0) rot=(0,0,1;0rad)
  Support = -> [XY_Plane242]
  Width = 0.23
FEATURE [PartDesign::AdditiveBox] Box2174
  AttacherType = Attacher::AttachEngine3D
  AttachmentOffset = pos=(-21.3,18.635,0) rot=(0,0,1;0rad)
  Height = 1.9
  Length = 1.3
  MapMode = 5
  Placement = pos=(-21.3,18.635,0) rot=(0,0,1;0rad)
  Support = -> [XY_Plane243]
  Width = 0.23
FEATURE [PartDesign::AdditiveBox] Box2177
  AttacherType = Attacher::AttachEngine3D
  AttachmentOffset = pos=(-21.3,18.635,0) rot=(0,0,1;0rad)
  Height = 1.9
  Length = 1.3
  MapMode = 5
  Placement = pos=(-21.3,18.635,0) rot=(0,0,1;0rad)
  Support = -> [XY_Plane245]
  Width = 0.23
FEATURE [PartDesign::SubtractiveBox] Box2178
  AttacherType = Attacher::AttachEngine3D
  AttachmentOffset = pos=(-21.35,18.635,0.35) rot=(0,0,1;0rad)
  BaseFeature = -> Box2164
  Height = 1.55
  Length = 0.5
  MapMode = 5
  Placement = pos=(-21.35,18.635,0.35) rot=(0,0,1;0rad)
  Support = -> [XY_Plane236]
  Width = 0.23
FEATURE [PartDesign::SubtractiveBox] Box2118
  AttacherType = Attacher::AttachEngine3D
  AttachmentOffset = pos=(-20.5,18.63,0) rot=(0,0,1;0rad)
  BaseFeature = -> Box2178
  Height = 1.635
  Length = 0.5
  MapMode = 5
  Placement = pos=(-20.5,18.63,0) rot=(0,0,1;0rad)
  Support = -> [XY_Plane236]
  Width = 0.25
FEATURE [PartDesign::SubtractiveBox] Box2137
  AttacherType = Attacher::AttachEngine3D
  AttachmentOffset = pos=(-21.19,18.635,-0.12) rot=(0,-1,0;0.15708rad)
  BaseFeature = -> Box2118
  Height = 0.12
  Length = 0.725
  MapMode = 5
  Placement = pos=(-21.19,18.635,-0.12) rot=(0,-1,0;0.15708rad)
  Support = -> [XY_Plane236]
  Width = 0.25
FEATURE [PartDesign::SubtractiveBox] Box2133
  AttacherType = Attacher::AttachEngine3D
  AttachmentOffset = pos=(-21.5005,18.625,0.235) rot=(0,-1,0;0.174533rad)
  BaseFeature = -> Box2137
  Height = 0.3
  Length = 0.6605
  MapMode = 5
  Placement = pos=(-21.5005,18.625,0.235) rot=(0,-1,0;0.174533rad)
  Support = -> [XY_Plane236]
  Width = 0.25
FEATURE [PartDesign::AdditiveBox] Box2180
  AttacherType = Attacher::AttachEngine3D
  AttachmentOffset = pos=(-21.3,18.635,0) rot=(0,0,1;0rad)
  Height = 1.9
  Length = 1.3
  MapMode = 5
  Placement = pos=(-21.3,18.635,0) rot=(0,0,1;0rad)
  Support = -> [XY_Plane237]
  Width = 0.23
FEATURE [PartDesign::SubtractiveBox] Box2132
  AttacherType = Attacher::AttachEngine3D
  AttachmentOffset = pos=(-21.35,18.635,0.35) rot=(0,0,1;0rad)
  BaseFeature = -> Box2180
  Height = 1.55
  Length = 0.5
  MapMode = 5
  Placement = pos=(-21.35,18.635,0.35) rot=(0,0,1;0rad)
  Support = -> [XY_Plane237]
  Width = 0.23
FEATURE [PartDesign::SubtractiveBox] Box2187
  AttacherType = Attacher::AttachEngine3D
  AttachmentOffset = pos=(-21.35,18.635,0.35) rot=(0,0,1;0rad)
  BaseFeature = -> Box2173
  Height = 1.55
  Length = 0.5
  MapMode = 5
  Placement = pos=(-21.35,18.635,0.35) rot=(0,0,1;0rad)
  Support = -> [XY_Plane242]
  Width = 0.23
FEATURE [PartDesign::SubtractiveBox] Box2167
  AttacherType = Attacher::AttachEngine3D
  AttachmentOffset = pos=(-20.5,18.63,0) rot=(0,0,1;0rad)
  BaseFeature = -> Box2187
  Height = 1.635
  Length = 0.5
  MapMode = 5
  Placement = pos=(-20.5,18.63,0) rot=(0,0,1;0rad)
  Support = -> [XY_Plane242]
  Width = 0.25
FEATURE [PartDesign::SubtractiveBox] Box2188
  AttacherType = Attacher::AttachEngine3D
  AttachmentOffset = pos=(-21.19,18.635,-0.12) rot=(0,-1,0;0.15708rad)
  BaseFeature = -> Box2167
  Height = 0.12
  Length = 0.725
  MapMode = 5
  Placement = pos=(-21.19,18.635,-0.12) rot=(0,-1,0;0.15708rad)
  Support = -> [XY_Plane242]
  Width = 0.25
FEATURE [PartDesign::SubtractiveBox] Box2182
  AttacherType = Attacher::AttachEngine3D
  AttachmentOffset = pos=(-21.5005,18.625,0.235) rot=(0,-1,0;0.174533rad)
  BaseFeature = -> Box2188
  Height = 0.3
  Length = 0.6605
  MapMode = 5
  Placement = pos=(-21.5005,18.625,0.235) rot=(0,-1,0;0.174533rad)
  Support = -> [XY_Plane242]
  Width = 0.25
FEATURE [PartDesign::SubtractiveBox] Box2194
  AttacherType = Attacher::AttachEngine3D
  AttachmentOffset = pos=(-21.35,18.635,0.35) rot=(0,0,1;0rad)
  BaseFeature = -> Box2174
  Height = 1.55
  Length = 0.5
  MapMode = 5
  Placement = pos=(-21.35,18.635,0.35) rot=(0,0,1;0rad)
  Support = -> [XY_Plane243]
  Width = 0.23
FEATURE [PartDesign::SubtractiveBox] Box2160
  AttacherType = Attacher::AttachEngine3D
  AttachmentOffset = pos=(-20.5,18.63,0) rot=(0,0,1;0rad)
  BaseFeature = -> Box2194
  Height = 1.635
  Length = 0.5
  MapMode = 5
  Placement = pos=(-20.5,18.63,0) rot=(0,0,1;0rad)
  Support = -> [XY_Plane243]
  Width = 0.25
FEATURE [PartDesign::SubtractiveBox] Box2196
  AttacherType = Attacher::AttachEngine3D
  AttachmentOffset = pos=(-21.35,18.635,0.35) rot=(0,0,1;0rad)
  BaseFeature = -> Box2177
  Height = 1.55
  Length = 0.5
  MapMode = 5
  Placement = pos=(-21.35,18.635,0.35) rot=(0,0,1;0rad)
  Support = -> [XY_Plane245]
  Width = 0.23
FEATURE [PartDesign::SubtractiveBox] Box2202
  AttacherType = Attacher::AttachEngine3D
  AttachmentOffset = pos=(-21.5005,18.625,0.235) rot=(0,-1,0;0.174533rad)
  BaseFeature = -> Box2154
  Height = 0.3
  Length = 0.6605
  MapMode = 5
  Placement = pos=(-21.5005,18.625,0.235) rot=(0,-1,0;0.174533rad)
  Support = -> [XY_Plane241]
  Width = 0.25
FEATURE [PartDesign::SubtractiveBox] Box2208
  AttacherType = Attacher::AttachEngine3D
  AttachmentOffset = pos=(-20.5,18.63,0) rot=(0,0,1;0rad)
  BaseFeature = -> Box2196
  Height = 1.635
  Length = 0.5
  MapMode = 5
  Placement = pos=(-20.5,18.63,0) rot=(0,0,1;0rad)
  Support = -> [XY_Plane245]
  Width = 0.25
FEATURE [PartDesign::SubtractiveBox] Box2181
  AttacherType = Attacher::AttachEngine3D
  AttachmentOffset = pos=(-21.19,18.635,-0.12) rot=(0,-1,0;0.15708rad)
  BaseFeature = -> Box2208
  Height = 0.12
  Length = 0.725
  MapMode = 5
  Placement = pos=(-21.19,18.635,-0.12) rot=(0,-1,0;0.15708rad)
  Support = -> [XY_Plane245]
  Width = 0.25
FEATURE [PartDesign::SubtractiveBox] Box2165
  AttacherType = Attacher::AttachEngine3D
  AttachmentOffset = pos=(-21.5005,18.625,0.235) rot=(0,-1,0;0.174533rad)
  BaseFeature = -> Box2181
  Height = 0.3
  Length = 0.6605
  MapMode = 5
  Placement = pos=(-21.5005,18.625,0.235) rot=(0,-1,0;0.174533rad)
  Support = -> [XY_Plane245]
  Width = 0.25
FEATURE [PartDesign::AdditiveBox] Box2213
  AttacherType = Attacher::AttachEngine3D
  AttachmentOffset = pos=(-21.3,18.635,0) rot=(0,0,1;0rad)
  Height = 1.9
  Length = 1.3
  MapMode = 5
  Placement = pos=(-21.3,18.635,0) rot=(0,0,1;0rad)
  Support = -> [XY_Plane238]
  Width = 0.23
FEATURE [PartDesign::SubtractiveBox] Box2220
  AttacherType = Attacher::AttachEngine3D
  AttachmentOffset = pos=(-21.19,18.635,-0.12) rot=(0,-1,0;0.15708rad)
  BaseFeature = -> Box2160
  Height = 0.12
  Length = 0.725
  MapMode = 5
  Placement = pos=(-21.19,18.635,-0.12) rot=(0,-1,0;0.15708rad)
  Support = -> [XY_Plane243]
  Width = 0.25
FEATURE [PartDesign::SubtractiveBox] Box2162
  AttacherType = Attacher::AttachEngine3D
  AttachmentOffset = pos=(-21.5005,18.625,0.235) rot=(0,-1,0;0.174533rad)
  BaseFeature = -> Box2220
  Height = 0.3
  Length = 0.6605
  MapMode = 5
  Placement = pos=(-21.5005,18.625,0.235) rot=(0,-1,0;0.174533rad)
  Support = -> [XY_Plane243]
  Width = 0.25
FEATURE [PartDesign::SubtractiveBox] Box2229
  AttacherType = Attacher::AttachEngine3D
  AttachmentOffset = pos=(-20.5,18.63,0) rot=(0,0,1;0rad)
  BaseFeature = -> Box2124
  Height = 1.635
  Length = 0.5
  MapMode = 5
  Placement = pos=(-20.5,18.63,0) rot=(0,0,1;0rad)
  Support = -> [XY_Plane234]
  Width = 0.25
FEATURE [PartDesign::SubtractiveBox] Box2185
  AttacherType = Attacher::AttachEngine3D
  AttachmentOffset = pos=(-21.19,18.635,-0.12) rot=(0,-1,0;0.15708rad)
  BaseFeature = -> Box2229
  Height = 0.12
  Length = 0.725
  MapMode = 5
  Placement = pos=(-21.19,18.635,-0.12) rot=(0,-1,0;0.15708rad)
  Support = -> [XY_Plane234]
  Width = 0.25
FEATURE [PartDesign::SubtractiveBox] Box2139
  AttacherType = Attacher::AttachEngine3D
  AttachmentOffset = pos=(-21.5005,18.625,0.235) rot=(0,-1,0;0.174533rad)
  BaseFeature = -> Box2185
  Height = 0.3
  Length = 0.6605
  MapMode = 5
  Placement = pos=(-21.5005,18.625,0.235) rot=(0,-1,0;0.174533rad)
  Support = -> [XY_Plane234]
  Width = 0.25
FEATURE [PartDesign::SubtractiveBox] Box2231
  AttacherType = Attacher::AttachEngine3D
  AttachmentOffset = pos=(-21.35,18.635,0.35) rot=(0,0,1;0rad)
  BaseFeature = -> Box2213
  Height = 1.55
  Length = 0.5
  MapMode = 5
  Placement = pos=(-21.35,18.635,0.35) rot=(0,0,1;0rad)
  Support = -> [XY_Plane238]
  Width = 0.23
FEATURE [PartDesign::SubtractiveBox] Box2199
  AttacherType = Attacher::AttachEngine3D
  AttachmentOffset = pos=(-20.5,18.63,0) rot=(0,0,1;0rad)
  BaseFeature = -> Box2231
  Height = 1.635
  Length = 0.5
  MapMode = 5
  Placement = pos=(-20.5,18.63,0) rot=(0,0,1;0rad)
  Support = -> [XY_Plane238]
  Width = 0.25
FEATURE [PartDesign::SubtractiveBox] Box2209
  AttacherType = Attacher::AttachEngine3D
  AttachmentOffset = pos=(-21.19,18.635,-0.12) rot=(0,-1,0;0.15708rad)
  BaseFeature = -> Box2199
  Height = 0.12
  Length = 0.725
  MapMode = 5
  Placement = pos=(-21.19,18.635,-0.12) rot=(0,-1,0;0.15708rad)
  Support = -> [XY_Plane238]
  Width = 0.25
FEATURE [PartDesign::SubtractiveBox] Box2224
  AttacherType = Attacher::AttachEngine3D
  AttachmentOffset = pos=(-21.5005,18.625,0.235) rot=(0,-1,0;0.174533rad)
  BaseFeature = -> Box2209
  Height = 0.3
  Length = 0.6605
  MapMode = 5
  Placement = pos=(-21.5005,18.625,0.235) rot=(0,-1,0;0.174533rad)
  Support = -> [XY_Plane238]
  Width = 0.25
FEATURE [PartDesign::AdditiveBox] Box2232
  AttacherType = Attacher::AttachEngine3D
  AttachmentOffset = pos=(-21.3,18.635,0) rot=(0,0,1;0rad)
  Height = 1.9
  Length = 1.3
  MapMode = 5
  Placement = pos=(-21.3,18.635,0) rot=(0,0,1;0rad)
  Support = -> [XY_Plane239]
  Width = 0.23
FEATURE [PartDesign::SubtractiveBox] Box2206
  AttacherType = Attacher::AttachEngine3D
  AttachmentOffset = pos=(-21.35,18.635,0.35) rot=(0,0,1;0rad)
  BaseFeature = -> Box2232
  Height = 1.55
  Length = 0.5
  MapMode = 5
  Placement = pos=(-21.35,18.635,0.35) rot=(0,0,1;0rad)
  Support = -> [XY_Plane239]
  Width = 0.23
FEATURE [PartDesign::SubtractiveBox] Box2195
  AttacherType = Attacher::AttachEngine3D
  AttachmentOffset = pos=(-20.5,18.63,0) rot=(0,0,1;0rad)
  BaseFeature = -> Box2206
  Height = 1.635
  Length = 0.5
  MapMode = 5
  Placement = pos=(-20.5,18.63,0) rot=(0,0,1;0rad)
  Support = -> [XY_Plane239]
  Width = 0.25
FEATURE [PartDesign::SubtractiveBox] Box2222
  AttacherType = Attacher::AttachEngine3D
  AttachmentOffset = pos=(-21.19,18.635,-0.12) rot=(0,-1,0;0.15708rad)
  BaseFeature = -> Box2195
  Height = 0.12
  Length = 0.725
  MapMode = 5
  Placement = pos=(-21.19,18.635,-0.12) rot=(0,-1,0;0.15708rad)
  Support = -> [XY_Plane239]
  Width = 0.25
FEATURE [PartDesign::SubtractiveBox] Box2210
  AttacherType = Attacher::AttachEngine3D
  AttachmentOffset = pos=(-21.5005,18.625,0.235) rot=(0,-1,0;0.174533rad)
  BaseFeature = -> Box2222
  Height = 0.3
  Length = 0.6605
  MapMode = 5
  Placement = pos=(-21.5005,18.625,0.235) rot=(0,-1,0;0.174533rad)
  Support = -> [XY_Plane239]
  Width = 0.25
FEATURE [PartDesign::SubtractiveBox] Box2233
  AttacherType = Attacher::AttachEngine3D
  AttachmentOffset = pos=(-20.5,18.63,0) rot=(0,0,1;0rad)
  BaseFeature = -> Box2125
  Height = 1.635
  Length = 0.5
  MapMode = 5
  Placement = pos=(-20.5,18.63,0) rot=(0,0,1;0rad)
  Support = -> [XY_Plane233]
  Width = 0.25
FEATURE [PartDesign::SubtractiveBox] Box2212
  AttacherType = Attacher::AttachEngine3D
  AttachmentOffset = pos=(-21.19,18.635,-0.12) rot=(0,-1,0;0.15708rad)
  BaseFeature = -> Box2233
  Height = 0.12
  Length = 0.725
  MapMode = 5
  Placement = pos=(-21.19,18.635,-0.12) rot=(0,-1,0;0.15708rad)
  Support = -> [XY_Plane233]
  Width = 0.25
FEATURE [PartDesign::SubtractiveBox] Box2136
  AttacherType = Attacher::AttachEngine3D
  AttachmentOffset = pos=(-21.5005,18.625,0.235) rot=(0,-1,0;0.174533rad)
  BaseFeature = -> Box2212
  Height = 0.3
  Length = 0.6605
  MapMode = 5
  Placement = pos=(-21.5005,18.625,0.235) rot=(0,-1,0;0.174533rad)
  Support = -> [XY_Plane233]
  Width = 0.25
FEATURE [PartDesign::AdditiveBox] Box2234
  AttacherType = Attacher::AttachEngine3D
  AttachmentOffset = pos=(-21.3,18.635,0) rot=(0,0,1;0rad)
  Height = 1.9
  Length = 1.3
  MapMode = 5
  Placement = pos=(-21.3,18.635,0) rot=(0,0,1;0rad)
  Support = -> [XY_Plane235]
  Width = 0.23
FEATURE [PartDesign::SubtractiveBox] Box2228
  AttacherType = Attacher::AttachEngine3D
  AttachmentOffset = pos=(-21.35,18.635,0.35) rot=(0,0,1;0rad)
  BaseFeature = -> Box2234
  Height = 1.55
  Length = 0.5
  MapMode = 5
  Placement = pos=(-21.35,18.635,0.35) rot=(0,0,1;0rad)
  Support = -> [XY_Plane235]
  Width = 0.23
FEATURE [PartDesign::SubtractiveBox] Box2218
  AttacherType = Attacher::AttachEngine3D
  AttachmentOffset = pos=(-20.5,18.63,0) rot=(0,0,1;0rad)
  BaseFeature = -> Box2228
  Height = 1.635
  Length = 0.5
  MapMode = 5
  Placement = pos=(-20.5,18.63,0) rot=(0,0,1;0rad)
  Support = -> [XY_Plane235]
  Width = 0.25
FEATURE [PartDesign::SubtractiveBox] Box2223
  AttacherType = Attacher::AttachEngine3D
  AttachmentOffset = pos=(-21.19,18.635,-0.12) rot=(0,-1,0;0.15708rad)
  BaseFeature = -> Box2218
  Height = 0.12
  Length = 0.725
  MapMode = 5
  Placement = pos=(-21.19,18.635,-0.12) rot=(0,-1,0;0.15708rad)
  Support = -> [XY_Plane235]
  Width = 0.25
FEATURE [PartDesign::SubtractiveBox] Box2219
  AttacherType = Attacher::AttachEngine3D
  AttachmentOffset = pos=(-21.5005,18.625,0.235) rot=(0,-1,0;0.174533rad)
  BaseFeature = -> Box2223
  Height = 0.3
  Length = 0.6605
  MapMode = 5
  Placement = pos=(-21.5005,18.625,0.235) rot=(0,-1,0;0.174533rad)
  Support = -> [XY_Plane235]
  Width = 0.25
FEATURE [PartDesign::SubtractiveBox] Box2235
  AttacherType = Attacher::AttachEngine3D
  AttachmentOffset = pos=(-20.5,18.63,0) rot=(0,0,1;0rad)
  BaseFeature = -> Box2132
  Height = 1.635
  Length = 0.5
  MapMode = 5
  Placement = pos=(-20.5,18.63,0) rot=(0,0,1;0rad)
  Support = -> [XY_Plane237]
  Width = 0.25
FEATURE [PartDesign::SubtractiveBox] Box2130
  AttacherType = Attacher::AttachEngine3D
  AttachmentOffset = pos=(-21.19,18.635,-0.12) rot=(0,-1,0;0.15708rad)
  BaseFeature = -> Box2235
  Height = 0.12
  Length = 0.725
  MapMode = 5
  Placement = pos=(-21.19,18.635,-0.12) rot=(0,-1,0;0.15708rad)
  Support = -> [XY_Plane237]
  Width = 0.25
FEATURE [PartDesign::SubtractiveBox] Box2131
  AttacherType = Attacher::AttachEngine3D
  AttachmentOffset = pos=(-21.5005,18.625,0.235) rot=(0,-1,0;0.174533rad)
  BaseFeature = -> Box2130
  Height = 0.3
  Length = 0.6605
  MapMode = 5
  Placement = pos=(-21.5005,18.625,0.235) rot=(0,-1,0;0.174533rad)
  Support = -> [XY_Plane237]
  Width = 0.25
FEATURE [PartDesign::Fillet] Fillet637
  Base = -> Box2224 [Edge2]
  BaseFeature = -> Box2224
  Placement = pos=(-21.5005,18.625,0.235) rot=(0,-1,0;0.174533rad)
  Radius = 0.05
  SupportTransform = false
FEATURE [PartDesign::Fillet] Fillet636
  Base = -> Fillet637 [Edge33]
  BaseFeature = -> Fillet637
  Placement = pos=(-21.5005,18.625,0.235) rot=(0,-1,0;0.174533rad)
  Radius = 0.5
  SupportTransform = false
FEATURE [PartDesign::AdditiveBox] Box2191
  AttacherType = Attacher::AttachEngine3D
  AttachmentOffset = pos=(-21.1,18.635,0.305) rot=(0,1,0;0.785398rad)
  BaseFeature = -> Fillet636
  Height = 0.375
  Length = 0.2
  MapMode = 5
  Placement = pos=(-21.1,18.635,0.305) rot=(0,1,0;0.785398rad)
  Support = -> [XY_Plane238]
  Width = 0.23
FEATURE [PartDesign::SubtractiveCylinder] Cylinder437
  Angle = 360
  AttacherType = Attacher::AttachEngine3D
  AttachmentOffset = pos=(-21.055,18.935,0.52) rot=(1,0,0;1.5708rad)
  BaseFeature = -> Box2191
  Height = 0.375
  MapMode = 5
  Placement = pos=(-21.055,18.935,0.52) rot=(1,0,0;1.5708rad)
  Radius = 0.205
  Support = -> [XY_Plane238]
FEATURE [PartDesign::SubtractiveBox] Box2148
  AttacherType = Attacher::AttachEngine3D
  AttachmentOffset = pos=(-20.95,18.635,0.53) rot=(0,0,1;0rad)
  BaseFeature = -> Cylinder437
  Height = 0.5
  Length = 0.1
  MapMode = 5
  Placement = pos=(-20.95,18.635,0.53) rot=(0,0,1;0rad)
  Support = -> [XY_Plane238]
  Width = 0.23
FEATURE [PartDesign::SubtractiveBox] Box2145
  AttacherType = Attacher::AttachEngine3D
  AttachmentOffset = pos=(-21.15,18.635,0.297) rot=(0,-1,0;0.174533rad)
  BaseFeature = -> Box2148
  Height = 0.115
  Length = 0.115
  MapMode = 5
  Placement = pos=(-21.15,18.635,0.297) rot=(0,-1,0;0.174533rad)
  Support = -> [XY_Plane238]
  Width = 0.23
FEATURE [PartDesign::Fillet] Fillet641
  Base = -> Box2149 [Edge2]
  BaseFeature = -> Box2149
  Placement = pos=(-21.5005,18.625,0.235) rot=(0,-1,0;0.174533rad)
  Radius = 0.05
  SupportTransform = false
FEATURE [PartDesign::Fillet] Fillet644
  Base = -> Fillet641 [Edge33]
  BaseFeature = -> Fillet641
  Placement = pos=(-21.5005,18.625,0.235) rot=(0,-1,0;0.174533rad)
  Radius = 0.5
  SupportTransform = false
FEATURE [PartDesign::AdditiveBox] Box2140
  AttacherType = Attacher::AttachEngine3D
  AttachmentOffset = pos=(-21.1,18.635,0.305) rot=(0,1,0;0.785398rad)
  BaseFeature = -> Fillet644
  Height = 0.375
  Length = 0.2
  MapMode = 5
  Placement = pos=(-21.1,18.635,0.305) rot=(0,1,0;0.785398rad)
  Support = -> [XY_Plane240]
  Width = 0.23
FEATURE [PartDesign::SubtractiveCylinder] Cylinder435
  Angle = 360
  AttacherType = Attacher::AttachEngine3D
  AttachmentOffset = pos=(-21.055,18.935,0.52) rot=(1,0,0;1.5708rad)
  BaseFeature = -> Box2140
  Height = 0.375
  MapMode = 5
  Placement = pos=(-21.055,18.935,0.52) rot=(1,0,0;1.5708rad)
  Radius = 0.205
  Support = -> [XY_Plane240]
FEATURE [PartDesign::SubtractiveBox] Box2150
  AttacherType = Attacher::AttachEngine3D
  AttachmentOffset = pos=(-20.95,18.635,0.53) rot=(0,0,1;0rad)
  BaseFeature = -> Cylinder435
  Height = 0.5
  Length = 0.1
  MapMode = 5
  Placement = pos=(-20.95,18.635,0.53) rot=(0,0,1;0rad)
  Support = -> [XY_Plane240]
  Width = 0.23
FEATURE [PartDesign::SubtractiveBox] Box2135
  AttacherType = Attacher::AttachEngine3D
  AttachmentOffset = pos=(-21.15,18.635,0.297) rot=(0,-1,0;0.174533rad)
  BaseFeature = -> Box2150
  Height = 0.115
  Length = 0.115
  MapMode = 5
  Placement = pos=(-21.15,18.635,0.297) rot=(0,-1,0;0.174533rad)
  Support = -> [XY_Plane240]
  Width = 0.23
FEATURE [PartDesign::Fillet] Fillet643
  Base = -> Box2135 [Edge28]
  BaseFeature = -> Box2135
  Placement = pos=(-21.15,18.635,0.297) rot=(0,-1,0;0.174533rad)
  Radius = 0.375
  SupportTransform = false
FEATURE [PartDesign::AdditiveBox] Box2155
  AttacherType = Attacher::AttachEngine3D
  AttachmentOffset = pos=(-20.7,18.635,1.55) rot=(0,1,0;0.785398rad)
  BaseFeature = -> Fillet643
  Height = 0.375
  Length = 0.23
  MapMode = 5
  Placement = pos=(-20.7,18.635,1.55) rot=(0,1,0;0.785398rad)
  Support = -> [XY_Plane240]
  Width = 0.23
FEATURE [PartDesign::SubtractiveCylinder] Cylinder429
  Angle = 360
  AttacherType = Attacher::AttachEngine3D
  AttachmentOffset = pos=(-20.271,18.635,1.4056) rot=(-1,0,0;1.5708rad)
  BaseFeature = -> Box2155
  Height = 0.23
  MapMode = 5
  Placement = pos=(-20.271,18.635,1.4056) rot=(-1,0,0;1.5708rad)
  Radius = 0.23
  Support = -> [XY_Plane240]
FEATURE [PartDesign::AdditiveBox] Box2170
  AttacherType = Attacher::AttachEngine3D
  AttachmentOffset = pos=(-20.1,18.635,1.635) rot=(0,0,1;0rad)
  BaseFeature = -> Cylinder429
  Height = 0.265
  Length = 0.23
  MapMode = 5
  Placement = pos=(-20.1,18.635,1.635) rot=(0,0,1;0rad)
  Support = -> [XY_Plane240]
  Width = 0.23
FEATURE [PartDesign::Fillet] Fillet647
  Base = -> Box2210 [Edge2]
  BaseFeature = -> Box2210
  Placement = pos=(-21.5005,18.625,0.235) rot=(0,-1,0;0.174533rad)
  Radius = 0.05
  SupportTransform = false
FEATURE [PartDesign::Fillet] Fillet638
  Base = -> Fillet647 [Edge33]
  BaseFeature = -> Fillet647
  Placement = pos=(-21.5005,18.625,0.235) rot=(0,-1,0;0.174533rad)
  Radius = 0.5
  SupportTransform = false
FEATURE [PartDesign::AdditiveBox] Box2198
  AttacherType = Attacher::AttachEngine3D
  AttachmentOffset = pos=(-21.1,18.635,0.305) rot=(0,1,0;0.785398rad)
  BaseFeature = -> Fillet638
  Height = 0.375
  Length = 0.2
  MapMode = 5
  Placement = pos=(-21.1,18.635,0.305) rot=(0,1,0;0.785398rad)
  Support = -> [XY_Plane239]
  Width = 0.23
FEATURE [PartDesign::SubtractiveCylinder] Cylinder446
  Angle = 360
  AttacherType = Attacher::AttachEngine3D
  AttachmentOffset = pos=(-21.055,18.935,0.52) rot=(1,0,0;1.5708rad)
  BaseFeature = -> Box2198
  Height = 0.375
  MapMode = 5
  Placement = pos=(-21.055,18.935,0.52) rot=(1,0,0;1.5708rad)
  Radius = 0.205
  Support = -> [XY_Plane239]
FEATURE [PartDesign::SubtractiveBox] Box2215
  AttacherType = Attacher::AttachEngine3D
  AttachmentOffset = pos=(-20.95,18.635,0.53) rot=(0,0,1;0rad)
  BaseFeature = -> Cylinder446
  Height = 0.5
  Length = 0.1
  MapMode = 5
  Placement = pos=(-20.95,18.635,0.53) rot=(0,0,1;0rad)
  Support = -> [XY_Plane239]
  Width = 0.23
FEATURE [PartDesign::SubtractiveBox] Box2203
  AttacherType = Attacher::AttachEngine3D
  AttachmentOffset = pos=(-21.15,18.635,0.297) rot=(0,-1,0;0.174533rad)
  BaseFeature = -> Box2215
  Height = 0.115
  Length = 0.115
  MapMode = 5
  Placement = pos=(-21.15,18.635,0.297) rot=(0,-1,0;0.174533rad)
  Support = -> [XY_Plane239]
  Width = 0.23
FEATURE [PartDesign::Fillet] Fillet649
  Base = -> Box2136 [Edge2]
  BaseFeature = -> Box2136
  Placement = pos=(-21.5005,18.625,0.235) rot=(0,-1,0;0.174533rad)
  Radius = 0.05
  SupportTransform = false
FEATURE [PartDesign::Fillet] Fillet650
  Base = -> Box2133 [Edge2]
  BaseFeature = -> Box2133
  Placement = pos=(-21.5005,18.625,0.235) rot=(0,-1,0;0.174533rad)
  Radius = 0.05
  SupportTransform = false
FEATURE [PartDesign::Fillet] Fillet651
  Base = -> Box2139 [Edge2]
  BaseFeature = -> Box2139
  Placement = pos=(-21.5005,18.625,0.235) rot=(0,-1,0;0.174533rad)
  Radius = 0.05
  SupportTransform = false
FEATURE [PartDesign::Fillet] Fillet640
  Base = -> Fillet651 [Edge33]
  BaseFeature = -> Fillet651
  Placement = pos=(-21.5005,18.625,0.235) rot=(0,-1,0;0.174533rad)
  Radius = 0.5
  SupportTransform = false
FEATURE [PartDesign::AdditiveBox] Box2237
  AttacherType = Attacher::AttachEngine3D
  AttachmentOffset = pos=(-21.1,18.635,0.305) rot=(0,1,0;0.785398rad)
  BaseFeature = -> Fillet640
  Height = 0.375
  Length = 0.2
  MapMode = 5
  Placement = pos=(-21.1,18.635,0.305) rot=(0,1,0;0.785398rad)
  Support = -> [XY_Plane234]
  Width = 0.23
FEATURE [PartDesign::SubtractiveCylinder] Cylinder442
  Angle = 360
  AttacherType = Attacher::AttachEngine3D
  AttachmentOffset = pos=(-21.055,18.935,0.52) rot=(1,0,0;1.5708rad)
  BaseFeature = -> Box2237
  Height = 0.375
  MapMode = 5
  Placement = pos=(-21.055,18.935,0.52) rot=(1,0,0;1.5708rad)
  Radius = 0.205
  Support = -> [XY_Plane234]
FEATURE [PartDesign::SubtractiveBox] Box2127
  AttacherType = Attacher::AttachEngine3D
  AttachmentOffset = pos=(-20.95,18.635,0.53) rot=(0,0,1;0rad)
  BaseFeature = -> Cylinder442
  Height = 0.5
  Length = 0.1
  MapMode = 5
  Placement = pos=(-20.95,18.635,0.53) rot=(0,0,1;0rad)
  Support = -> [XY_Plane234]
  Width = 0.23
FEATURE [PartDesign::SubtractiveBox] Box2129
  AttacherType = Attacher::AttachEngine3D
  AttachmentOffset = pos=(-21.15,18.635,0.297) rot=(0,-1,0;0.174533rad)
  BaseFeature = -> Box2127
  Height = 0.115
  Length = 0.115
  MapMode = 5
  Placement = pos=(-21.15,18.635,0.297) rot=(0,-1,0;0.174533rad)
  Support = -> [XY_Plane234]
  Width = 0.23
FEATURE [PartDesign::Fillet] Fillet648
  Base = -> Box2129 [Edge28]
  BaseFeature = -> Box2129
  Placement = pos=(-21.15,18.635,0.297) rot=(0,-1,0;0.174533rad)
  Radius = 0.375
  SupportTransform = false
FEATURE [PartDesign::AdditiveBox] Box2134
  AttacherType = Attacher::AttachEngine3D
  AttachmentOffset = pos=(-20.7,18.635,1.55) rot=(0,1,0;0.785398rad)
  BaseFeature = -> Fillet648
  Height = 0.375
  Length = 0.23
  MapMode = 5
  Placement = pos=(-20.7,18.635,1.55) rot=(0,1,0;0.785398rad)
  Support = -> [XY_Plane234]
  Width = 0.23
FEATURE [PartDesign::SubtractiveCylinder] Cylinder445
  Angle = 360
  AttacherType = Attacher::AttachEngine3D
  AttachmentOffset = pos=(-20.271,18.635,1.4056) rot=(-1,0,0;1.5708rad)
  BaseFeature = -> Box2134
  Height = 0.23
  MapMode = 5
  Placement = pos=(-20.271,18.635,1.4056) rot=(-1,0,0;1.5708rad)
  Radius = 0.23
  Support = -> [XY_Plane234]
FEATURE [PartDesign::AdditiveBox] Box2126
  AttacherType = Attacher::AttachEngine3D
  AttachmentOffset = pos=(-20.1,18.635,1.635) rot=(0,0,1;0rad)
  BaseFeature = -> Cylinder445
  Height = 0.265
  Length = 0.23
  MapMode = 5
  Placement = pos=(-20.1,18.635,1.635) rot=(0,0,1;0rad)
  Support = -> [XY_Plane234]
  Width = 0.23
FEATURE [PartDesign::Fillet] Fillet652
  Base = -> Box2131 [Edge2]
  BaseFeature = -> Box2131
  Placement = pos=(-21.5005,18.625,0.235) rot=(0,-1,0;0.174533rad)
  Radius = 0.05
  SupportTransform = false
FEATURE [PartDesign::Fillet] Fillet645
  Base = -> Fillet652 [Edge33]
  BaseFeature = -> Fillet652
  Placement = pos=(-21.5005,18.625,0.235) rot=(0,-1,0;0.174533rad)
  Radius = 0.5
  SupportTransform = false
FEATURE [PartDesign::AdditiveBox] Box2240
  AttacherType = Attacher::AttachEngine3D
  AttachmentOffset = pos=(-21.1,18.635,0.305) rot=(0,1,0;0.785398rad)
  BaseFeature = -> Fillet645
  Height = 0.375
  Length = 0.2
  MapMode = 5
  Placement = pos=(-21.1,18.635,0.305) rot=(0,1,0;0.785398rad)
  Support = -> [XY_Plane237]
  Width = 0.23
FEATURE [PartDesign::Fillet] Fillet655
  Base = -> Box2162 [Edge2]
  BaseFeature = -> Box2162
  Placement = pos=(-21.5005,18.625,0.235) rot=(0,-1,0;0.174533rad)
  Radius = 0.05
  SupportTransform = false
FEATURE [PartDesign::Body] Body218  label="pin218"
  Group = -> [Box2157,Box2169,Box2156,Box2151,Box2149,Fillet641,Fillet644,Box2140,Cylinder435,Box2150,Box2135,Fillet643,Box2155,Cylinder429,Box2170]
  Origin = -> Origin229
  Placement = pos=(0,-5,0) rot=(0,0,1;0rad)
  Tip = -> Box2170
FEATURE [PartDesign::Fillet] Fillet658
  Base = -> Box2145 [Edge28]
  BaseFeature = -> Box2145
  Placement = pos=(-21.15,18.635,0.297) rot=(0,-1,0;0.174533rad)
  Radius = 0.375
  SupportTransform = false
FEATURE [PartDesign::AdditiveBox] Box2201
  AttacherType = Attacher::AttachEngine3D
  AttachmentOffset = pos=(-20.7,18.635,1.55) rot=(0,1,0;0.785398rad)
  BaseFeature = -> Fillet658
  Height = 0.375
  Length = 0.23
  MapMode = 5
  Placement = pos=(-20.7,18.635,1.55) rot=(0,1,0;0.785398rad)
  Support = -> [XY_Plane238]
  Width = 0.23
FEATURE [PartDesign::SubtractiveCylinder] Cylinder431
  Angle = 360
  AttacherType = Attacher::AttachEngine3D
  AttachmentOffset = pos=(-20.271,18.635,1.4056) rot=(-1,0,0;1.5708rad)
  BaseFeature = -> Box2201
  Height = 0.23
  MapMode = 5
  Placement = pos=(-20.271,18.635,1.4056) rot=(-1,0,0;1.5708rad)
  Radius = 0.23
  Support = -> [XY_Plane238]
FEATURE [PartDesign::AdditiveBox] Box2217
  AttacherType = Attacher::AttachEngine3D
  AttachmentOffset = pos=(-20.1,18.635,1.635) rot=(0,0,1;0rad)
  BaseFeature = -> Cylinder431
  Height = 0.265
  Length = 0.23
  MapMode = 5
  Placement = pos=(-20.1,18.635,1.635) rot=(0,0,1;0rad)
  Support = -> [XY_Plane238]
  Width = 0.23
FEATURE [PartDesign::Body] Body216  label="pin216"
  Group = -> [Box2213,Box2231,Box2199,Box2209,Box2224,Fillet637,Fillet636,Box2191,Cylinder437,Box2148,Box2145,Fillet658,Box2201,Cylinder431,Box2217]
  Origin = -> Origin248
  Tip = -> Box2217
FEATURE [PartDesign::Fillet] Fillet661
  Base = -> Box2203 [Edge28]
  BaseFeature = -> Box2203
  Placement = pos=(-21.15,18.635,0.297) rot=(0,-1,0;0.174533rad)
  Radius = 0.375
  SupportTransform = false
FEATURE [PartDesign::AdditiveBox] Box2200
  AttacherType = Attacher::AttachEngine3D
  AttachmentOffset = pos=(-20.7,18.635,1.55) rot=(0,1,0;0.785398rad)
  BaseFeature = -> Fillet661
  Height = 0.375
  Length = 0.23
  MapMode = 5
  Placement = pos=(-20.7,18.635,1.55) rot=(0,1,0;0.785398rad)
  Support = -> [XY_Plane239]
  Width = 0.23
FEATURE [PartDesign::SubtractiveCylinder] Cylinder447
  Angle = 360
  AttacherType = Attacher::AttachEngine3D
  AttachmentOffset = pos=(-20.271,18.635,1.4056) rot=(-1,0,0;1.5708rad)
  BaseFeature = -> Box2200
  Height = 0.23
  MapMode = 5
  Placement = pos=(-20.271,18.635,1.4056) rot=(-1,0,0;1.5708rad)
  Radius = 0.23
  Support = -> [XY_Plane239]
FEATURE [PartDesign::AdditiveBox] Box2216
  AttacherType = Attacher::AttachEngine3D
  AttachmentOffset = pos=(-20.1,18.635,1.635) rot=(0,0,1;0rad)
  BaseFeature = -> Cylinder447
  Height = 0.265
  Length = 0.23
  MapMode = 5
  Placement = pos=(-20.1,18.635,1.635) rot=(0,0,1;0rad)
  Support = -> [XY_Plane239]
  Width = 0.23
FEATURE [PartDesign::Body] Body213  label="pin213"
  Group = -> [Box2232,Box2206,Box2195,Box2222,Box2210,Fillet647,Fillet638,Box2198,Cylinder446,Box2215,Box2203,Fillet661,Box2200,Cylinder447,Box2216]
  Origin = -> Origin236
  Placement = pos=(0,-0.5,0) rot=(0,0,1;0rad)
  Tip = -> Box2216
FEATURE [PartDesign::Fillet] Fillet662
  Base = -> Fillet649 [Edge33]
  BaseFeature = -> Fillet649
  Placement = pos=(-21.5005,18.625,0.235) rot=(0,-1,0;0.174533rad)
  Radius = 0.5
  SupportTransform = false
FEATURE [PartDesign::AdditiveBox] Box2230
  AttacherType = Attacher::AttachEngine3D
  AttachmentOffset = pos=(-21.1,18.635,0.305) rot=(0,1,0;0.785398rad)
  BaseFeature = -> Fillet662
  Height = 0.375
  Length = 0.2
  MapMode = 5
  Placement = pos=(-21.1,18.635,0.305) rot=(0,1,0;0.785398rad)
  Support = -> [XY_Plane233]
  Width = 0.23
FEATURE [PartDesign::SubtractiveCylinder] Cylinder448
  Angle = 360
  AttacherType = Attacher::AttachEngine3D
  AttachmentOffset = pos=(-21.055,18.935,0.52) rot=(1,0,0;1.5708rad)
  BaseFeature = -> Box2230
  Height = 0.375
  MapMode = 5
  Placement = pos=(-21.055,18.935,0.52) rot=(1,0,0;1.5708rad)
  Radius = 0.205
  Support = -> [XY_Plane233]
FEATURE [PartDesign::SubtractiveBox] Box2227
  AttacherType = Attacher::AttachEngine3D
  AttachmentOffset = pos=(-20.95,18.635,0.53) rot=(0,0,1;0rad)
  BaseFeature = -> Cylinder448
  Height = 0.5
  Length = 0.1
  MapMode = 5
  Placement = pos=(-20.95,18.635,0.53) rot=(0,0,1;0rad)
  Support = -> [XY_Plane233]
  Width = 0.23
FEATURE [PartDesign::SubtractiveBox] Box2226
  AttacherType = Attacher::AttachEngine3D
  AttachmentOffset = pos=(-21.15,18.635,0.297) rot=(0,-1,0;0.174533rad)
  BaseFeature = -> Box2227
  Height = 0.115
  Length = 0.115
  MapMode = 5
  Placement = pos=(-21.15,18.635,0.297) rot=(0,-1,0;0.174533rad)
  Support = -> [XY_Plane233]
  Width = 0.23
FEATURE [PartDesign::Fillet] Fillet654
  Base = -> Box2226 [Edge28]
  BaseFeature = -> Box2226
  Placement = pos=(-21.15,18.635,0.297) rot=(0,-1,0;0.174533rad)
  Radius = 0.375
  SupportTransform = false
FEATURE [PartDesign::AdditiveBox] Box2236
  AttacherType = Attacher::AttachEngine3D
  AttachmentOffset = pos=(-20.7,18.635,1.55) rot=(0,1,0;0.785398rad)
  BaseFeature = -> Fillet654
  Height = 0.375
  Length = 0.23
  MapMode = 5
  Placement = pos=(-20.7,18.635,1.55) rot=(0,1,0;0.785398rad)
  Support = -> [XY_Plane233]
  Width = 0.23
FEATURE [PartDesign::SubtractiveCylinder] Cylinder441
  Angle = 360
  AttacherType = Attacher::AttachEngine3D
  AttachmentOffset = pos=(-20.271,18.635,1.4056) rot=(-1,0,0;1.5708rad)
  BaseFeature = -> Box2236
  Height = 0.23
  MapMode = 5
  Placement = pos=(-20.271,18.635,1.4056) rot=(-1,0,0;1.5708rad)
  Radius = 0.23
  Support = -> [XY_Plane233]
FEATURE [PartDesign::AdditiveBox] Box2239
  AttacherType = Attacher::AttachEngine3D
  AttachmentOffset = pos=(-20.1,18.635,1.635) rot=(0,0,1;0rad)
  BaseFeature = -> Cylinder441
  Height = 0.265
  Length = 0.23
  MapMode = 5
  Placement = pos=(-20.1,18.635,1.635) rot=(0,0,1;0rad)
  Support = -> [XY_Plane233]
  Width = 0.23
FEATURE [PartDesign::Fillet] Fillet663
  Base = -> Box2219 [Edge2]
  BaseFeature = -> Box2219
  Placement = pos=(-21.5005,18.625,0.235) rot=(0,-1,0;0.174533rad)
  Radius = 0.05
  SupportTransform = false
FEATURE [PartDesign::Fillet] Fillet659
  Base = -> Fillet663 [Edge33]
  BaseFeature = -> Fillet663
  Placement = pos=(-21.5005,18.625,0.235) rot=(0,-1,0;0.174533rad)
  Radius = 0.5
  SupportTransform = false
FEATURE [PartDesign::AdditiveBox] Box2192
  AttacherType = Attacher::AttachEngine3D
  AttachmentOffset = pos=(-21.1,18.635,0.305) rot=(0,1,0;0.785398rad)
  BaseFeature = -> Fillet659
  Height = 0.375
  Length = 0.2
  MapMode = 5
  Placement = pos=(-21.1,18.635,0.305) rot=(0,1,0;0.785398rad)
  Support = -> [XY_Plane235]
  Width = 0.23
FEATURE [PartDesign::SubtractiveCylinder] Cylinder450
  Angle = 360
  AttacherType = Attacher::AttachEngine3D
  AttachmentOffset = pos=(-21.055,18.935,0.52) rot=(1,0,0;1.5708rad)
  BaseFeature = -> Box2192
  Height = 0.375
  MapMode = 5
  Placement = pos=(-21.055,18.935,0.52) rot=(1,0,0;1.5708rad)
  Radius = 0.205
  Support = -> [XY_Plane235]
FEATURE [PartDesign::SubtractiveBox] Box2221
  AttacherType = Attacher::AttachEngine3D
  AttachmentOffset = pos=(-20.95,18.635,0.53) rot=(0,0,1;0rad)
  BaseFeature = -> Cylinder450
  Height = 0.5
  Length = 0.1
  MapMode = 5
  Placement = pos=(-20.95,18.635,0.53) rot=(0,0,1;0rad)
  Support = -> [XY_Plane235]
  Width = 0.23
FEATURE [PartDesign::SubtractiveBox] Box2211
  AttacherType = Attacher::AttachEngine3D
  AttachmentOffset = pos=(-21.15,18.635,0.297) rot=(0,-1,0;0.174533rad)
  BaseFeature = -> Box2221
  Height = 0.115
  Length = 0.115
  MapMode = 5
  Placement = pos=(-21.15,18.635,0.297) rot=(0,-1,0;0.174533rad)
  Support = -> [XY_Plane235]
  Width = 0.23
FEATURE [PartDesign::Fillet] Fillet642
  Base = -> Box2211 [Edge28]
  BaseFeature = -> Box2211
  Placement = pos=(-21.15,18.635,0.297) rot=(0,-1,0;0.174533rad)
  Radius = 0.375
  SupportTransform = false
FEATURE [PartDesign::AdditiveBox] Box2214
  AttacherType = Attacher::AttachEngine3D
  AttachmentOffset = pos=(-20.7,18.635,1.55) rot=(0,1,0;0.785398rad)
  BaseFeature = -> Fillet642
  Height = 0.375
  Length = 0.23
  MapMode = 5
  Placement = pos=(-20.7,18.635,1.55) rot=(0,1,0;0.785398rad)
  Support = -> [XY_Plane235]
  Width = 0.23
FEATURE [PartDesign::SubtractiveCylinder] Cylinder449
  Angle = 360
  AttacherType = Attacher::AttachEngine3D
  AttachmentOffset = pos=(-20.271,18.635,1.4056) rot=(-1,0,0;1.5708rad)
  BaseFeature = -> Box2214
  Height = 0.23
  MapMode = 5
  Placement = pos=(-20.271,18.635,1.4056) rot=(-1,0,0;1.5708rad)
  Radius = 0.23
  Support = -> [XY_Plane235]
FEATURE [PartDesign::AdditiveBox] Box2238
  AttacherType = Attacher::AttachEngine3D
  AttachmentOffset = pos=(-20.1,18.635,1.635) rot=(0,0,1;0rad)
  BaseFeature = -> Cylinder449
  Height = 0.265
  Length = 0.23
  MapMode = 5
  Placement = pos=(-20.1,18.635,1.635) rot=(0,0,1;0rad)
  Support = -> [XY_Plane235]
  Width = 0.23
FEATURE [PartDesign::Body] Body219  label="pin219"
  Group = -> [Box2234,Box2228,Box2218,Box2223,Box2219,Fillet663,Fillet659,Box2192,Cylinder450,Box2221,Box2211,Fillet642,Box2214,Cylinder449,Box2238]
  Origin = -> Origin238
  Placement = pos=(0,-1,0) rot=(0,0,1;0rad)
  Tip = -> Box2238
FEATURE [PartDesign::Body] Body221  label="pin221"
  Group = -> [Box2144,Box2124,Box2229,Box2185,Box2139,Fillet651,Fillet640,Box2237,Cylinder442,Box2127,Box2129,Fillet648,Box2134,Cylinder445,Box2126]
  Origin = -> Origin231
  Placement = pos=(0,-2.5,0) rot=(0,0,1;0rad)
  Tip = -> Box2126
FEATURE [PartDesign::Body] Body222  label="pin222"
  Group = -> [Box2141,Box2125,Box2233,Box2212,Box2136,Fillet649,Fillet662,Box2230,Cylinder448,Box2227,Box2226,Fillet654,Box2236,Cylinder441,Box2239]
  Origin = -> Origin243
  Placement = pos=(0,-1.5,0) rot=(0,0,1;0rad)
  Tip = -> Box2239
FEATURE [PartDesign::Fillet] Fillet667
  Base = -> Box2182 [Edge2]
  BaseFeature = -> Box2182
  Placement = pos=(-21.5005,18.625,0.235) rot=(0,-1,0;0.174533rad)
  Radius = 0.05
  SupportTransform = false
FEATURE [PartDesign::Fillet] Fillet666
  Base = -> Fillet667 [Edge33]
  BaseFeature = -> Fillet667
  Placement = pos=(-21.5005,18.625,0.235) rot=(0,-1,0;0.174533rad)
  Radius = 0.5
  SupportTransform = false
FEATURE [PartDesign::AdditiveBox] Box2197
  AttacherType = Attacher::AttachEngine3D
  AttachmentOffset = pos=(-21.1,18.635,0.305) rot=(0,1,0;0.785398rad)
  BaseFeature = -> Fillet666
  Height = 0.375
  Length = 0.2
  MapMode = 5
  Placement = pos=(-21.1,18.635,0.305) rot=(0,1,0;0.785398rad)
  Support = -> [XY_Plane242]
  Width = 0.23
FEATURE [PartDesign::SubtractiveCylinder] Cylinder440
  Angle = 360
  AttacherType = Attacher::AttachEngine3D
  AttachmentOffset = pos=(-21.055,18.935,0.52) rot=(1,0,0;1.5708rad)
  BaseFeature = -> Box2197
  Height = 0.375
  MapMode = 5
  Placement = pos=(-21.055,18.935,0.52) rot=(1,0,0;1.5708rad)
  Radius = 0.205
  Support = -> [XY_Plane242]
FEATURE [PartDesign::SubtractiveBox] Box2190
  AttacherType = Attacher::AttachEngine3D
  AttachmentOffset = pos=(-20.95,18.635,0.53) rot=(0,0,1;0rad)
  BaseFeature = -> Cylinder440
  Height = 0.5
  Length = 0.1
  MapMode = 5
  Placement = pos=(-20.95,18.635,0.53) rot=(0,0,1;0rad)
  Support = -> [XY_Plane242]
  Width = 0.23
FEATURE [PartDesign::SubtractiveBox] Box2179
  AttacherType = Attacher::AttachEngine3D
  AttachmentOffset = pos=(-21.15,18.635,0.297) rot=(0,-1,0;0.174533rad)
  BaseFeature = -> Box2190
  Height = 0.115
  Length = 0.115
  MapMode = 5
  Placement = pos=(-21.15,18.635,0.297) rot=(0,-1,0;0.174533rad)
  Support = -> [XY_Plane242]
  Width = 0.23
FEATURE [PartDesign::Fillet] Fillet657
  Base = -> Box2179 [Edge28]
  BaseFeature = -> Box2179
  Placement = pos=(-21.15,18.635,0.297) rot=(0,-1,0;0.174533rad)
  Radius = 0.375
  SupportTransform = false
FEATURE [PartDesign::AdditiveBox] Box2186
  AttacherType = Attacher::AttachEngine3D
  AttachmentOffset = pos=(-20.7,18.635,1.55) rot=(0,1,0;0.785398rad)
  BaseFeature = -> Fillet657
  Height = 0.375
  Length = 0.23
  MapMode = 5
  Placement = pos=(-20.7,18.635,1.55) rot=(0,1,0;0.785398rad)
  Support = -> [XY_Plane242]
  Width = 0.23
FEATURE [PartDesign::SubtractiveCylinder] Cylinder439
  Angle = 360
  AttacherType = Attacher::AttachEngine3D
  AttachmentOffset = pos=(-20.271,18.635,1.4056) rot=(-1,0,0;1.5708rad)
  BaseFeature = -> Box2186
  Height = 0.23
  MapMode = 5
  Placement = pos=(-20.271,18.635,1.4056) rot=(-1,0,0;1.5708rad)
  Radius = 0.23
  Support = -> [XY_Plane242]
FEATURE [PartDesign::AdditiveBox] Box2163
  AttacherType = Attacher::AttachEngine3D
  AttachmentOffset = pos=(-20.1,18.635,1.635) rot=(0,0,1;0rad)
  BaseFeature = -> Cylinder439
  Height = 0.265
  Length = 0.23
  MapMode = 5
  Placement = pos=(-20.1,18.635,1.635) rot=(0,0,1;0rad)
  Support = -> [XY_Plane242]
  Width = 0.23
FEATURE [PartDesign::Body] Body223  label="pin223"
  Group = -> [Box2173,Box2187,Box2167,Box2188,Box2182,Fillet667,Fillet666,Box2197,Cylinder440,Box2190,Box2179,Fillet657,Box2186,Cylinder439,Box2163]
  Origin = -> Origin249
  Placement = pos=(0,-4,0) rot=(0,0,1;0rad)
  Tip = -> Box2163
FEATURE [PartDesign::Fillet] Fillet668
  Base = -> Fillet650 [Edge33]
  BaseFeature = -> Fillet650
  Placement = pos=(-21.5005,18.625,0.235) rot=(0,-1,0;0.174533rad)
  Radius = 0.5
  SupportTransform = false
FEATURE [PartDesign::AdditiveBox] Box2168
  AttacherType = Attacher::AttachEngine3D
  AttachmentOffset = pos=(-21.1,18.635,0.305) rot=(0,1,0;0.785398rad)
  BaseFeature = -> Fillet668
  Height = 0.375
  Length = 0.2
  MapMode = 5
  Placement = pos=(-21.1,18.635,0.305) rot=(0,1,0;0.785398rad)
  Support = -> [XY_Plane236]
  Width = 0.23
FEATURE [PartDesign::SubtractiveCylinder] Cylinder433
  Angle = 360
  AttacherType = Attacher::AttachEngine3D
  AttachmentOffset = pos=(-21.055,18.935,0.52) rot=(1,0,0;1.5708rad)
  BaseFeature = -> Box2168
  Height = 0.375
  MapMode = 5
  Placement = pos=(-21.055,18.935,0.52) rot=(1,0,0;1.5708rad)
  Radius = 0.205
  Support = -> [XY_Plane236]
FEATURE [PartDesign::SubtractiveBox] Box2161
  AttacherType = Attacher::AttachEngine3D
  AttachmentOffset = pos=(-20.95,18.635,0.53) rot=(0,0,1;0rad)
  BaseFeature = -> Cylinder433
  Height = 0.5
  Length = 0.1
  MapMode = 5
  Placement = pos=(-20.95,18.635,0.53) rot=(0,0,1;0rad)
  Support = -> [XY_Plane236]
  Width = 0.23
FEATURE [PartDesign::SubtractiveBox] Box2158
  AttacherType = Attacher::AttachEngine3D
  AttachmentOffset = pos=(-21.15,18.635,0.297) rot=(0,-1,0;0.174533rad)
  BaseFeature = -> Box2161
  Height = 0.115
  Length = 0.115
  MapMode = 5
  Placement = pos=(-21.15,18.635,0.297) rot=(0,-1,0;0.174533rad)
  Support = -> [XY_Plane236]
  Width = 0.23
FEATURE [PartDesign::Fillet] Fillet664
  Base = -> Box2158 [Edge28]
  BaseFeature = -> Box2158
  Placement = pos=(-21.15,18.635,0.297) rot=(0,-1,0;0.174533rad)
  Radius = 0.375
  SupportTransform = false
FEATURE [PartDesign::AdditiveBox] Box2171
  AttacherType = Attacher::AttachEngine3D
  AttachmentOffset = pos=(-20.7,18.635,1.55) rot=(0,1,0;0.785398rad)
  BaseFeature = -> Fillet664
  Height = 0.375
  Length = 0.23
  MapMode = 5
  Placement = pos=(-20.7,18.635,1.55) rot=(0,1,0;0.785398rad)
  Support = -> [XY_Plane236]
  Width = 0.23
FEATURE [PartDesign::SubtractiveCylinder] Cylinder438
  Angle = 360
  AttacherType = Attacher::AttachEngine3D
  AttachmentOffset = pos=(-20.271,18.635,1.4056) rot=(-1,0,0;1.5708rad)
  BaseFeature = -> Box2171
  Height = 0.23
  MapMode = 5
  Placement = pos=(-20.271,18.635,1.4056) rot=(-1,0,0;1.5708rad)
  Radius = 0.23
  Support = -> [XY_Plane236]
FEATURE [PartDesign::AdditiveBox] Box2172
  AttacherType = Attacher::AttachEngine3D
  AttachmentOffset = pos=(-20.1,18.635,1.635) rot=(0,0,1;0rad)
  BaseFeature = -> Cylinder438
  Height = 0.265
  Length = 0.23
  MapMode = 5
  Placement = pos=(-20.1,18.635,1.635) rot=(0,0,1;0rad)
  Support = -> [XY_Plane236]
  Width = 0.23
FEATURE [PartDesign::Body] Body224  label="pin224"
  Group = -> [Box2164,Box2178,Box2118,Box2137,Box2133,Fillet650,Fillet668,Box2168,Cylinder433,Box2161,Box2158,Fillet664,Box2171,Cylinder438,Box2172]
  Origin = -> Origin240
  Placement = pos=(0,-5.5,0) rot=(0,0,1;0rad)
  Tip = -> Box2172
FEATURE [PartDesign::Fillet] Fillet669
  Base = -> Fillet655 [Edge33]
  BaseFeature = -> Fillet655
  Placement = pos=(-21.5005,18.625,0.235) rot=(0,-1,0;0.174533rad)
  Radius = 0.5
  SupportTransform = false
FEATURE [PartDesign::AdditiveBox] Box2152
  AttacherType = Attacher::AttachEngine3D
  AttachmentOffset = pos=(-21.1,18.635,0.305) rot=(0,1,0;0.785398rad)
  BaseFeature = -> Fillet669
  Height = 0.375
  Length = 0.2
  MapMode = 5
  Placement = pos=(-21.1,18.635,0.305) rot=(0,1,0;0.785398rad)
  Support = -> [XY_Plane243]
  Width = 0.23
FEATURE [PartDesign::SubtractiveCylinder] Cylinder434
  Angle = 360
  AttacherType = Attacher::AttachEngine3D
  AttachmentOffset = pos=(-21.055,18.935,0.52) rot=(1,0,0;1.5708rad)
  BaseFeature = -> Box2152
  Height = 0.375
  MapMode = 5
  Placement = pos=(-21.055,18.935,0.52) rot=(1,0,0;1.5708rad)
  Radius = 0.205
  Support = -> [XY_Plane243]
FEATURE [PartDesign::SubtractiveBox] Box2146
  AttacherType = Attacher::AttachEngine3D
  AttachmentOffset = pos=(-20.95,18.635,0.53) rot=(0,0,1;0rad)
  BaseFeature = -> Cylinder434
  Height = 0.5
  Length = 0.1
  MapMode = 5
  Placement = pos=(-20.95,18.635,0.53) rot=(0,0,1;0rad)
  Support = -> [XY_Plane243]
  Width = 0.23
FEATURE [PartDesign::SubtractiveBox] Box2184
  AttacherType = Attacher::AttachEngine3D
  AttachmentOffset = pos=(-21.15,18.635,0.297) rot=(0,-1,0;0.174533rad)
  BaseFeature = -> Box2146
  Height = 0.115
  Length = 0.115
  MapMode = 5
  Placement = pos=(-21.15,18.635,0.297) rot=(0,-1,0;0.174533rad)
  Support = -> [XY_Plane243]
  Width = 0.23
FEATURE [PartDesign::Fillet] Fillet656
  Base = -> Box2184 [Edge28]
  BaseFeature = -> Box2184
  Placement = pos=(-21.15,18.635,0.297) rot=(0,-1,0;0.174533rad)
  Radius = 0.375
  SupportTransform = false
FEATURE [PartDesign::AdditiveBox] Box2176
  AttacherType = Attacher::AttachEngine3D
  AttachmentOffset = pos=(-20.7,18.635,1.55) rot=(0,1,0;0.785398rad)
  BaseFeature = -> Fillet656
  Height = 0.375
  Length = 0.23
  MapMode = 5
  Placement = pos=(-20.7,18.635,1.55) rot=(0,1,0;0.785398rad)
  Support = -> [XY_Plane243]
  Width = 0.23
FEATURE [PartDesign::SubtractiveCylinder] Cylinder436
  Angle = 360
  AttacherType = Attacher::AttachEngine3D
  AttachmentOffset = pos=(-20.271,18.635,1.4056) rot=(-1,0,0;1.5708rad)
  BaseFeature = -> Box2176
  Height = 0.23
  MapMode = 5
  Placement = pos=(-20.271,18.635,1.4056) rot=(-1,0,0;1.5708rad)
  Radius = 0.23
  Support = -> [XY_Plane243]
FEATURE [PartDesign::AdditiveBox] Box2205
  AttacherType = Attacher::AttachEngine3D
  AttachmentOffset = pos=(-20.1,18.635,1.635) rot=(0,0,1;0rad)
  BaseFeature = -> Cylinder436
  Height = 0.265
  Length = 0.23
  MapMode = 5
  Placement = pos=(-20.1,18.635,1.635) rot=(0,0,1;0rad)
  Support = -> [XY_Plane243]
  Width = 0.23
FEATURE [PartDesign::Body] Body215  label="pin215"
  Group = -> [Box2174,Box2194,Box2160,Box2220,Box2162,Fillet655,Fillet669,Box2152,Cylinder434,Box2146,Box2184,Fillet656,Box2176,Cylinder436,Box2205]
  Origin = -> Origin230
  Placement = pos=(0,-3,0) rot=(0,0,1;0rad)
  Tip = -> Box2205
FEATURE [PartDesign::Fillet] Fillet670
  Base = -> Box2165 [Edge2]
  BaseFeature = -> Box2165
  Placement = pos=(-21.5005,18.625,0.235) rot=(0,-1,0;0.174533rad)
  Radius = 0.05
  SupportTransform = false
FEATURE [PartDesign::Fillet] Fillet665
  Base = -> Fillet670 [Edge33]
  BaseFeature = -> Fillet670
  Placement = pos=(-21.5005,18.625,0.235) rot=(0,-1,0;0.174533rad)
  Radius = 0.5
  SupportTransform = false
FEATURE [PartDesign::AdditiveBox] Box2193
  AttacherType = Attacher::AttachEngine3D
  AttachmentOffset = pos=(-21.1,18.635,0.305) rot=(0,1,0;0.785398rad)
  BaseFeature = -> Fillet665
  Height = 0.375
  Length = 0.2
  MapMode = 5
  Placement = pos=(-21.1,18.635,0.305) rot=(0,1,0;0.785398rad)
  Support = -> [XY_Plane245]
  Width = 0.23
FEATURE [PartDesign::SubtractiveCylinder] Cylinder444
  Angle = 360
  AttacherType = Attacher::AttachEngine3D
  AttachmentOffset = pos=(-21.055,18.935,0.52) rot=(1,0,0;1.5708rad)
  BaseFeature = -> Box2193
  Height = 0.375
  MapMode = 5
  Placement = pos=(-21.055,18.935,0.52) rot=(1,0,0;1.5708rad)
  Radius = 0.205
  Support = -> [XY_Plane245]
FEATURE [PartDesign::SubtractiveBox] Box2207
  AttacherType = Attacher::AttachEngine3D
  AttachmentOffset = pos=(-20.95,18.635,0.53) rot=(0,0,1;0rad)
  BaseFeature = -> Cylinder444
  Height = 0.5
  Length = 0.1
  MapMode = 5
  Placement = pos=(-20.95,18.635,0.53) rot=(0,0,1;0rad)
  Support = -> [XY_Plane245]
  Width = 0.23
FEATURE [PartDesign::SubtractiveBox] Box2183
  AttacherType = Attacher::AttachEngine3D
  AttachmentOffset = pos=(-21.15,18.635,0.297) rot=(0,-1,0;0.174533rad)
  BaseFeature = -> Box2207
  Height = 0.115
  Length = 0.115
  MapMode = 5
  Placement = pos=(-21.15,18.635,0.297) rot=(0,-1,0;0.174533rad)
  Support = -> [XY_Plane245]
  Width = 0.23
FEATURE [PartDesign::Fillet] Fillet653
  Base = -> Box2183 [Edge28]
  BaseFeature = -> Box2183
  Placement = pos=(-21.15,18.635,0.297) rot=(0,-1,0;0.174533rad)
  Radius = 0.375
  SupportTransform = false
FEATURE [PartDesign::AdditiveBox] Box2204
  AttacherType = Attacher::AttachEngine3D
  AttachmentOffset = pos=(-20.7,18.635,1.55) rot=(0,1,0;0.785398rad)
  BaseFeature = -> Fillet653
  Height = 0.375
  Length = 0.23
  MapMode = 5
  Placement = pos=(-20.7,18.635,1.55) rot=(0,1,0;0.785398rad)
  Support = -> [XY_Plane245]
  Width = 0.23
FEATURE [PartDesign::SubtractiveCylinder] Cylinder443
  Angle = 360
  AttacherType = Attacher::AttachEngine3D
  AttachmentOffset = pos=(-20.271,18.635,1.4056) rot=(-1,0,0;1.5708rad)
  BaseFeature = -> Box2204
  Height = 0.23
  MapMode = 5
  Placement = pos=(-20.271,18.635,1.4056) rot=(-1,0,0;1.5708rad)
  Radius = 0.23
  Support = -> [XY_Plane245]
FEATURE [PartDesign::AdditiveBox] Box2175
  AttacherType = Attacher::AttachEngine3D
  AttachmentOffset = pos=(-20.1,18.635,1.635) rot=(0,0,1;0rad)
  BaseFeature = -> Cylinder443
  Height = 0.265
  Length = 0.23
  MapMode = 5
  Placement = pos=(-20.1,18.635,1.635) rot=(0,0,1;0rad)
  Support = -> [XY_Plane245]
  Width = 0.23
FEATURE [PartDesign::Body] Body217  label="pin217"
  Group = -> [Box2177,Box2196,Box2208,Box2181,Box2165,Fillet670,Fillet665,Box2193,Cylinder444,Box2207,Box2183,Fillet653,Box2204,Cylinder443,Box2175]
  Origin = -> Origin241
  Placement = pos=(0,-3.5,0) rot=(0,0,1;0rad)
  Tip = -> Box2175
FEATURE [PartDesign::Fillet] Fillet671
  Base = -> Box2202 [Edge2]
  BaseFeature = -> Box2202
  Placement = pos=(-21.5005,18.625,0.235) rot=(0,-1,0;0.174533rad)
  Radius = 0.05
  SupportTransform = false
FEATURE [PartDesign::Fillet] Fillet639
  Base = -> Fillet671 [Edge33]
  BaseFeature = -> Fillet671
  Placement = pos=(-21.5005,18.625,0.235) rot=(0,-1,0;0.174533rad)
  Radius = 0.5
  SupportTransform = false
FEATURE [PartDesign::AdditiveBox] Box2123
  AttacherType = Attacher::AttachEngine3D
  AttachmentOffset = pos=(-21.1,18.635,0.305) rot=(0,1,0;0.785398rad)
  BaseFeature = -> Fillet639
  Height = 0.375
  Length = 0.2
  MapMode = 5
  Placement = pos=(-21.1,18.635,0.305) rot=(0,1,0;0.785398rad)
  Support = -> [XY_Plane241]
  Width = 0.23
FEATURE [PartDesign::SubtractiveCylinder] Cylinder428
  Angle = 360
  AttacherType = Attacher::AttachEngine3D
  AttachmentOffset = pos=(-21.055,18.935,0.52) rot=(1,0,0;1.5708rad)
  BaseFeature = -> Box2123
  Height = 0.375
  MapMode = 5
  Placement = pos=(-21.055,18.935,0.52) rot=(1,0,0;1.5708rad)
  Radius = 0.205
  Support = -> [XY_Plane241]
FEATURE [PartDesign::SubtractiveBox] Box2128
  AttacherType = Attacher::AttachEngine3D
  AttachmentOffset = pos=(-20.95,18.635,0.53) rot=(0,0,1;0rad)
  BaseFeature = -> Cylinder428
  Height = 0.5
  Length = 0.1
  MapMode = 5
  Placement = pos=(-20.95,18.635,0.53) rot=(0,0,1;0rad)
  Support = -> [XY_Plane241]
  Width = 0.23
FEATURE [PartDesign::SubtractiveBox] Box2119
  AttacherType = Attacher::AttachEngine3D
  AttachmentOffset = pos=(-21.15,18.635,0.297) rot=(0,-1,0;0.174533rad)
  BaseFeature = -> Box2128
  Height = 0.115
  Length = 0.115
  MapMode = 5
  Placement = pos=(-21.15,18.635,0.297) rot=(0,-1,0;0.174533rad)
  Support = -> [XY_Plane241]
  Width = 0.23
FEATURE [PartDesign::Fillet] Fillet660
  Base = -> Box2119 [Edge28]
  BaseFeature = -> Box2119
  Placement = pos=(-21.15,18.635,0.297) rot=(0,-1,0;0.174533rad)
  Radius = 0.375
  SupportTransform = false
FEATURE [PartDesign::AdditiveBox] Box2147
  AttacherType = Attacher::AttachEngine3D
  AttachmentOffset = pos=(-20.7,18.635,1.55) rot=(0,1,0;0.785398rad)
  BaseFeature = -> Fillet660
  Height = 0.375
  Length = 0.23
  MapMode = 5
  Placement = pos=(-20.7,18.635,1.55) rot=(0,1,0;0.785398rad)
  Support = -> [XY_Plane241]
  Width = 0.23
FEATURE [PartDesign::SubtractiveCylinder] Cylinder432
  Angle = 360
  AttacherType = Attacher::AttachEngine3D
  AttachmentOffset = pos=(-20.271,18.635,1.4056) rot=(-1,0,0;1.5708rad)
  BaseFeature = -> Box2147
  Height = 0.23
  MapMode = 5
  Placement = pos=(-20.271,18.635,1.4056) rot=(-1,0,0;1.5708rad)
  Radius = 0.23
  Support = -> [XY_Plane241]
FEATURE [PartDesign::AdditiveBox] Box2143
  AttacherType = Attacher::AttachEngine3D
  AttachmentOffset = pos=(-20.1,18.635,1.635) rot=(0,0,1;0rad)
  BaseFeature = -> Cylinder432
  Height = 0.265
  Length = 0.23
  MapMode = 5
  Placement = pos=(-20.1,18.635,1.635) rot=(0,0,1;0rad)
  Support = -> [XY_Plane241]
  Width = 0.23
FEATURE [PartDesign::Body] Body220  label="pin220"
  Group = -> [Box2159,Box2166,Box2153,Box2154,Box2202,Fillet671,Fillet639,Box2123,Cylinder428,Box2128,Box2119,Fillet660,Box2147,Cylinder432,Box2143]
  Origin = -> Origin247
  Placement = pos=(0,-4.5,0) rot=(0,0,1;0rad)
  Tip = -> Box2143
FEATURE [PartDesign::SubtractiveCylinder] Cylinder451
  Angle = 360
  AttacherType = Attacher::AttachEngine3D
  AttachmentOffset = pos=(-21.055,18.935,0.52) rot=(1,0,0;1.5708rad)
  BaseFeature = -> Box2240
  Height = 0.375
  MapMode = 5
  Placement = pos=(-21.055,18.935,0.52) rot=(1,0,0;1.5708rad)
  Radius = 0.205
  Support = -> [XY_Plane237]
FEATURE [PartDesign::SubtractiveBox] Box2138
  AttacherType = Attacher::AttachEngine3D
  AttachmentOffset = pos=(-20.95,18.635,0.53) rot=(0,0,1;0rad)
  BaseFeature = -> Cylinder451
  Height = 0.5
  Length = 0.1
  MapMode = 5
  Placement = pos=(-20.95,18.635,0.53) rot=(0,0,1;0rad)
  Support = -> [XY_Plane237]
  Width = 0.23
FEATURE [PartDesign::SubtractiveBox] Box2189
  AttacherType = Attacher::AttachEngine3D
  AttachmentOffset = pos=(-21.15,18.635,0.297) rot=(0,-1,0;0.174533rad)
  BaseFeature = -> Box2138
  Height = 0.115
  Length = 0.115
  MapMode = 5
  Placement = pos=(-21.15,18.635,0.297) rot=(0,-1,0;0.174533rad)
  Support = -> [XY_Plane237]
  Width = 0.23
FEATURE [PartDesign::Fillet] Fillet646
  Base = -> Box2189 [Edge28]
  BaseFeature = -> Box2189
  Placement = pos=(-21.15,18.635,0.297) rot=(0,-1,0;0.174533rad)
  Radius = 0.375
  SupportTransform = false
FEATURE [PartDesign::AdditiveBox] Box2225
  AttacherType = Attacher::AttachEngine3D
  AttachmentOffset = pos=(-20.7,18.635,1.55) rot=(0,1,0;0.785398rad)
  BaseFeature = -> Fillet646
  Height = 0.375
  Length = 0.23
  MapMode = 5
  Placement = pos=(-20.7,18.635,1.55) rot=(0,1,0;0.785398rad)
  Support = -> [XY_Plane237]
  Width = 0.23
FEATURE [PartDesign::SubtractiveCylinder] Cylinder430
  Angle = 360
  AttacherType = Attacher::AttachEngine3D
  AttachmentOffset = pos=(-20.271,18.635,1.4056) rot=(-1,0,0;1.5708rad)
  BaseFeature = -> Box2225
  Height = 0.23
  MapMode = 5
  Placement = pos=(-20.271,18.635,1.4056) rot=(-1,0,0;1.5708rad)
  Radius = 0.23
  Support = -> [XY_Plane237]
FEATURE [PartDesign::AdditiveBox] Box2142
  AttacherType = Attacher::AttachEngine3D
  AttachmentOffset = pos=(-20.1,18.635,1.635) rot=(0,0,1;0rad)
  BaseFeature = -> Cylinder430
  Height = 0.265
  Length = 0.23
  MapMode = 5
  Placement = pos=(-20.1,18.635,1.635) rot=(0,0,1;0rad)
  Support = -> [XY_Plane237]
  Width = 0.23
FEATURE [PartDesign::Body] Body214  label="pin214"
  Group = -> [Box2180,Box2132,Box2235,Box2130,Box2131,Fillet652,Fillet645,Box2240,Cylinder451,Box2138,Box2189,Fillet646,Box2225,Cylinder430,Box2142]
  Origin = -> Origin239
  Placement = pos=(0,-2,0) rot=(0,0,1;0rad)
  Tip = -> Box2142
FEATURE [PartDesign::AdditiveBox] Box2254
  AttacherType = Attacher::AttachEngine3D
  AttachmentOffset = pos=(-21.3,18.635,0) rot=(0,0,1;0rad)
  Height = 1.9
  Length = 1.3
  MapMode = 5
  Placement = pos=(-21.3,18.635,0) rot=(0,0,1;0rad)
  Support = -> [XY_Plane246]
  Width = 0.23
FEATURE [PartDesign::AdditiveBox] Box2260
  AttacherType = Attacher::AttachEngine3D
  AttachmentOffset = pos=(-21.3,18.635,0) rot=(0,0,1;0rad)
  Height = 1.9
  Length = 1.3
  MapMode = 5
  Placement = pos=(-21.3,18.635,0) rot=(0,0,1;0rad)
  Support = -> [XY_Plane247]
  Width = 0.23
FEATURE [PartDesign::AdditiveBox] Box2261
  AttacherType = Attacher::AttachEngine3D
  AttachmentOffset = pos=(-21.3,18.635,0) rot=(0,0,1;0rad)
  Height = 1.9
  Length = 1.3
  MapMode = 5
  Placement = pos=(-21.3,18.635,0) rot=(0,0,1;0rad)
  Support = -> [XY_Plane248]
  Width = 0.23
FEATURE [PartDesign::SubtractiveBox] Box2263
  AttacherType = Attacher::AttachEngine3D
  AttachmentOffset = pos=(-21.35,18.635,0.35) rot=(0,0,1;0rad)
  BaseFeature = -> Box2260
  Height = 1.55
  Length = 0.5
  MapMode = 5
  Placement = pos=(-21.35,18.635,0.35) rot=(0,0,1;0rad)
  Support = -> [XY_Plane247]
  Width = 0.23
FEATURE [PartDesign::SubtractiveBox] Box2253
  AttacherType = Attacher::AttachEngine3D
  AttachmentOffset = pos=(-20.5,18.63,0) rot=(0,0,1;0rad)
  BaseFeature = -> Box2263
  Height = 1.635
  Length = 0.5
  MapMode = 5
  Placement = pos=(-20.5,18.63,0) rot=(0,0,1;0rad)
  Support = -> [XY_Plane247]
  Width = 0.25
FEATURE [PartDesign::SubtractiveBox] Box2257
  AttacherType = Attacher::AttachEngine3D
  AttachmentOffset = pos=(-21.19,18.635,-0.12) rot=(0,-1,0;0.15708rad)
  BaseFeature = -> Box2253
  Height = 0.12
  Length = 0.725
  MapMode = 5
  Placement = pos=(-21.19,18.635,-0.12) rot=(0,-1,0;0.15708rad)
  Support = -> [XY_Plane247]
  Width = 0.25
FEATURE [PartDesign::SubtractiveBox] Box2252
  AttacherType = Attacher::AttachEngine3D
  AttachmentOffset = pos=(-21.5005,18.625,0.235) rot=(0,-1,0;0.174533rad)
  BaseFeature = -> Box2257
  Height = 0.3
  Length = 0.6605
  MapMode = 5
  Placement = pos=(-21.5005,18.625,0.235) rot=(0,-1,0;0.174533rad)
  Support = -> [XY_Plane247]
  Width = 0.25
FEATURE [PartDesign::SubtractiveBox] Box2267
  AttacherType = Attacher::AttachEngine3D
  AttachmentOffset = pos=(-21.35,18.635,0.35) rot=(0,0,1;0rad)
  BaseFeature = -> Box2261
  Height = 1.55
  Length = 0.5
  MapMode = 5
  Placement = pos=(-21.35,18.635,0.35) rot=(0,0,1;0rad)
  Support = -> [XY_Plane248]
  Width = 0.23
FEATURE [PartDesign::SubtractiveBox] Box2258
  AttacherType = Attacher::AttachEngine3D
  AttachmentOffset = pos=(-20.5,18.63,0) rot=(0,0,1;0rad)
  BaseFeature = -> Box2267
  Height = 1.635
  Length = 0.5
  MapMode = 5
  Placement = pos=(-20.5,18.63,0) rot=(0,0,1;0rad)
  Support = -> [XY_Plane248]
  Width = 0.25
FEATURE [PartDesign::SubtractiveBox] Box2259
  AttacherType = Attacher::AttachEngine3D
  AttachmentOffset = pos=(-21.19,18.635,-0.12) rot=(0,-1,0;0.15708rad)
  BaseFeature = -> Box2258
  Height = 0.12
  Length = 0.725
  MapMode = 5
  Placement = pos=(-21.19,18.635,-0.12) rot=(0,-1,0;0.15708rad)
  Support = -> [XY_Plane248]
  Width = 0.25
FEATURE [PartDesign::AdditiveBox] Box2275
  AttacherType = Attacher::AttachEngine3D
  AttachmentOffset = pos=(-21.3,18.635,0) rot=(0,0,1;0rad)
  Height = 1.9
  Length = 1.3
  MapMode = 5
  Placement = pos=(-21.3,18.635,0) rot=(0,0,1;0rad)
  Support = -> [XY_Plane249]
  Width = 0.23
FEATURE [PartDesign::SubtractiveBox] Box2276
  AttacherType = Attacher::AttachEngine3D
  AttachmentOffset = pos=(-21.35,18.635,0.35) rot=(0,0,1;0rad)
  BaseFeature = -> Box2254
  Height = 1.55
  Length = 0.5
  MapMode = 5
  Placement = pos=(-21.35,18.635,0.35) rot=(0,0,1;0rad)
  Support = -> [XY_Plane246]
  Width = 0.23
FEATURE [PartDesign::SubtractiveBox] Box2243
  AttacherType = Attacher::AttachEngine3D
  AttachmentOffset = pos=(-20.5,18.63,0) rot=(0,0,1;0rad)
  BaseFeature = -> Box2276
  Height = 1.635
  Length = 0.5
  MapMode = 5
  Placement = pos=(-20.5,18.63,0) rot=(0,0,1;0rad)
  Support = -> [XY_Plane246]
  Width = 0.25
FEATURE [PartDesign::SubtractiveBox] Box2248
  AttacherType = Attacher::AttachEngine3D
  AttachmentOffset = pos=(-21.19,18.635,-0.12) rot=(0,-1,0;0.15708rad)
  BaseFeature = -> Box2243
  Height = 0.12
  Length = 0.725
  MapMode = 5
  Placement = pos=(-21.19,18.635,-0.12) rot=(0,-1,0;0.15708rad)
  Support = -> [XY_Plane246]
  Width = 0.25
FEATURE [PartDesign::SubtractiveBox] Box2246
  AttacherType = Attacher::AttachEngine3D
  AttachmentOffset = pos=(-21.5005,18.625,0.235) rot=(0,-1,0;0.174533rad)
  BaseFeature = -> Box2248
  Height = 0.3
  Length = 0.6605
  MapMode = 5
  Placement = pos=(-21.5005,18.625,0.235) rot=(0,-1,0;0.174533rad)
  Support = -> [XY_Plane246]
  Width = 0.25
FEATURE [PartDesign::SubtractiveBox] Box2277
  AttacherType = Attacher::AttachEngine3D
  AttachmentOffset = pos=(-21.5005,18.625,0.235) rot=(0,-1,0;0.174533rad)
  BaseFeature = -> Box2259
  Height = 0.3
  Length = 0.6605
  MapMode = 5
  Placement = pos=(-21.5005,18.625,0.235) rot=(0,-1,0;0.174533rad)
  Support = -> [XY_Plane248]
  Width = 0.25
FEATURE [PartDesign::SubtractiveBox] Box2278
  AttacherType = Attacher::AttachEngine3D
  AttachmentOffset = pos=(-21.35,18.635,0.35) rot=(0,0,1;0rad)
  BaseFeature = -> Box2275
  Height = 1.55
  Length = 0.5
  MapMode = 5
  Placement = pos=(-21.35,18.635,0.35) rot=(0,0,1;0rad)
  Support = -> [XY_Plane249]
  Width = 0.23
FEATURE [PartDesign::SubtractiveBox] Box2274
  AttacherType = Attacher::AttachEngine3D
  AttachmentOffset = pos=(-20.5,18.63,0) rot=(0,0,1;0rad)
  BaseFeature = -> Box2278
  Height = 1.635
  Length = 0.5
  MapMode = 5
  Placement = pos=(-20.5,18.63,0) rot=(0,0,1;0rad)
  Support = -> [XY_Plane249]
  Width = 0.25
FEATURE [PartDesign::SubtractiveBox] Box2279
  AttacherType = Attacher::AttachEngine3D
  AttachmentOffset = pos=(-21.19,18.635,-0.12) rot=(0,-1,0;0.15708rad)
  BaseFeature = -> Box2274
  Height = 0.12
  Length = 0.725
  MapMode = 5
  Placement = pos=(-21.19,18.635,-0.12) rot=(0,-1,0;0.15708rad)
  Support = -> [XY_Plane249]
  Width = 0.25
FEATURE [PartDesign::SubtractiveBox] Box2265
  AttacherType = Attacher::AttachEngine3D
  AttachmentOffset = pos=(-21.5005,18.625,0.235) rot=(0,-1,0;0.174533rad)
  BaseFeature = -> Box2279
  Height = 0.3
  Length = 0.6605
  MapMode = 5
  Placement = pos=(-21.5005,18.625,0.235) rot=(0,-1,0;0.174533rad)
  Support = -> [XY_Plane249]
  Width = 0.25
FEATURE [PartDesign::Fillet] Fillet675
  Base = -> Box2246 [Edge2]
  BaseFeature = -> Box2246
  Placement = pos=(-21.5005,18.625,0.235) rot=(0,-1,0;0.174533rad)
  Radius = 0.05
  SupportTransform = false
FEATURE [PartDesign::Fillet] Fillet679
  Base = -> Box2252 [Edge2]
  BaseFeature = -> Box2252
  Placement = pos=(-21.5005,18.625,0.235) rot=(0,-1,0;0.174533rad)
  Radius = 0.05
  SupportTransform = false
FEATURE [PartDesign::Fillet] Fillet674
  Base = -> Fillet679 [Edge33]
  BaseFeature = -> Fillet679
  Placement = pos=(-21.5005,18.625,0.235) rot=(0,-1,0;0.174533rad)
  Radius = 0.5
  SupportTransform = false
FEATURE [PartDesign::AdditiveBox] Box2242
  AttacherType = Attacher::AttachEngine3D
  AttachmentOffset = pos=(-21.1,18.635,0.305) rot=(0,1,0;0.785398rad)
  BaseFeature = -> Fillet674
  Height = 0.375
  Length = 0.2
  MapMode = 5
  Placement = pos=(-21.1,18.635,0.305) rot=(0,1,0;0.785398rad)
  Support = -> [XY_Plane247]
  Width = 0.23
FEATURE [PartDesign::SubtractiveCylinder] Cylinder454
  Angle = 360
  AttacherType = Attacher::AttachEngine3D
  AttachmentOffset = pos=(-21.055,18.935,0.52) rot=(1,0,0;1.5708rad)
  BaseFeature = -> Box2242
  Height = 0.375
  MapMode = 5
  Placement = pos=(-21.055,18.935,0.52) rot=(1,0,0;1.5708rad)
  Radius = 0.205
  Support = -> [XY_Plane247]
FEATURE [PartDesign::SubtractiveBox] Box2256
  AttacherType = Attacher::AttachEngine3D
  AttachmentOffset = pos=(-20.95,18.635,0.53) rot=(0,0,1;0rad)
  BaseFeature = -> Cylinder454
  Height = 0.5
  Length = 0.1
  MapMode = 5
  Placement = pos=(-20.95,18.635,0.53) rot=(0,0,1;0rad)
  Support = -> [XY_Plane247]
  Width = 0.23
FEATURE [PartDesign::SubtractiveBox] Box2247
  AttacherType = Attacher::AttachEngine3D
  AttachmentOffset = pos=(-21.15,18.635,0.297) rot=(0,-1,0;0.174533rad)
  BaseFeature = -> Box2256
  Height = 0.115
  Length = 0.115
  MapMode = 5
  Placement = pos=(-21.15,18.635,0.297) rot=(0,-1,0;0.174533rad)
  Support = -> [XY_Plane247]
  Width = 0.23
FEATURE [PartDesign::Fillet] Fillet678
  Base = -> Box2247 [Edge28]
  BaseFeature = -> Box2247
  Placement = pos=(-21.15,18.635,0.297) rot=(0,-1,0;0.174533rad)
  Radius = 0.375
  SupportTransform = false
FEATURE [PartDesign::AdditiveBox] Box2250
  AttacherType = Attacher::AttachEngine3D
  AttachmentOffset = pos=(-20.7,18.635,1.55) rot=(0,1,0;0.785398rad)
  BaseFeature = -> Fillet678
  Height = 0.375
  Length = 0.23
  MapMode = 5
  Placement = pos=(-20.7,18.635,1.55) rot=(0,1,0;0.785398rad)
  Support = -> [XY_Plane247]
  Width = 0.23
FEATURE [PartDesign::SubtractiveCylinder] Cylinder453
  Angle = 360
  AttacherType = Attacher::AttachEngine3D
  AttachmentOffset = pos=(-20.271,18.635,1.4056) rot=(-1,0,0;1.5708rad)
  BaseFeature = -> Box2250
  Height = 0.23
  MapMode = 5
  Placement = pos=(-20.271,18.635,1.4056) rot=(-1,0,0;1.5708rad)
  Radius = 0.23
  Support = -> [XY_Plane247]
FEATURE [PartDesign::AdditiveBox] Box2268
  AttacherType = Attacher::AttachEngine3D
  AttachmentOffset = pos=(-20.1,18.635,1.635) rot=(0,0,1;0rad)
  BaseFeature = -> Cylinder453
  Height = 0.265
  Length = 0.23
  MapMode = 5
  Placement = pos=(-20.1,18.635,1.635) rot=(0,0,1;0rad)
  Support = -> [XY_Plane247]
  Width = 0.23
FEATURE [PartDesign::Body] Body225  label="pin225"
  Group = -> [Box2260,Box2263,Box2253,Box2257,Box2252,Fillet679,Fillet674,Box2242,Cylinder454,Box2256,Box2247,Fillet678,Box2250,Cylinder453,Box2268]
  Origin = -> Origin232
  Placement = pos=(0,-6,0) rot=(0,0,1;0rad)
  Tip = -> Box2268
FEATURE [PartDesign::Fillet] Fillet681
  Base = -> Box2265 [Edge2]
  BaseFeature = -> Box2265
  Placement = pos=(-21.5005,18.625,0.235) rot=(0,-1,0;0.174533rad)
  Radius = 0.05
  SupportTransform = false
FEATURE [PartDesign::Fillet] Fillet672
  Base = -> Fillet681 [Edge33]
  BaseFeature = -> Fillet681
  Placement = pos=(-21.5005,18.625,0.235) rot=(0,-1,0;0.174533rad)
  Radius = 0.5
  SupportTransform = false
FEATURE [PartDesign::AdditiveBox] Box2273
  AttacherType = Attacher::AttachEngine3D
  AttachmentOffset = pos=(-21.1,18.635,0.305) rot=(0,1,0;0.785398rad)
  BaseFeature = -> Fillet672
  Height = 0.375
  Length = 0.2
  MapMode = 5
  Placement = pos=(-21.1,18.635,0.305) rot=(0,1,0;0.785398rad)
  Support = -> [XY_Plane249]
  Width = 0.23
FEATURE [PartDesign::SubtractiveCylinder] Cylinder459
  Angle = 360
  AttacherType = Attacher::AttachEngine3D
  AttachmentOffset = pos=(-21.055,18.935,0.52) rot=(1,0,0;1.5708rad)
  BaseFeature = -> Box2273
  Height = 0.375
  MapMode = 5
  Placement = pos=(-21.055,18.935,0.52) rot=(1,0,0;1.5708rad)
  Radius = 0.205
  Support = -> [XY_Plane249]
FEATURE [PartDesign::SubtractiveBox] Box2280
  AttacherType = Attacher::AttachEngine3D
  AttachmentOffset = pos=(-20.95,18.635,0.53) rot=(0,0,1;0rad)
  BaseFeature = -> Cylinder459
  Height = 0.5
  Length = 0.1
  MapMode = 5
  Placement = pos=(-20.95,18.635,0.53) rot=(0,0,1;0rad)
  Support = -> [XY_Plane249]
  Width = 0.23
FEATURE [PartDesign::SubtractiveBox] Box2272
  AttacherType = Attacher::AttachEngine3D
  AttachmentOffset = pos=(-21.15,18.635,0.297) rot=(0,-1,0;0.174533rad)
  BaseFeature = -> Box2280
  Height = 0.115
  Length = 0.115
  MapMode = 5
  Placement = pos=(-21.15,18.635,0.297) rot=(0,-1,0;0.174533rad)
  Support = -> [XY_Plane249]
  Width = 0.23
FEATURE [PartDesign::Fillet] Fillet676
  Base = -> Box2272 [Edge28]
  BaseFeature = -> Box2272
  Placement = pos=(-21.15,18.635,0.297) rot=(0,-1,0;0.174533rad)
  Radius = 0.375
  SupportTransform = false
FEATURE [PartDesign::AdditiveBox] Box2266
  AttacherType = Attacher::AttachEngine3D
  AttachmentOffset = pos=(-20.7,18.635,1.55) rot=(0,1,0;0.785398rad)
  BaseFeature = -> Fillet676
  Height = 0.375
  Length = 0.23
  MapMode = 5
  Placement = pos=(-20.7,18.635,1.55) rot=(0,1,0;0.785398rad)
  Support = -> [XY_Plane249]
  Width = 0.23
FEATURE [PartDesign::SubtractiveCylinder] Cylinder458
  Angle = 360
  AttacherType = Attacher::AttachEngine3D
  AttachmentOffset = pos=(-20.271,18.635,1.4056) rot=(-1,0,0;1.5708rad)
  BaseFeature = -> Box2266
  Height = 0.23
  MapMode = 5
  Placement = pos=(-20.271,18.635,1.4056) rot=(-1,0,0;1.5708rad)
  Radius = 0.23
  Support = -> [XY_Plane249]
FEATURE [PartDesign::AdditiveBox] Box2262
  AttacherType = Attacher::AttachEngine3D
  AttachmentOffset = pos=(-20.1,18.635,1.635) rot=(0,0,1;0rad)
  BaseFeature = -> Cylinder458
  Height = 0.265
  Length = 0.23
  MapMode = 5
  Placement = pos=(-20.1,18.635,1.635) rot=(0,0,1;0rad)
  Support = -> [XY_Plane249]
  Width = 0.23
FEATURE [PartDesign::Body] Body227  label="pin227"
  Group = -> [Box2275,Box2278,Box2274,Box2279,Box2265,Fillet681,Fillet672,Box2273,Cylinder459,Box2280,Box2272,Fillet676,Box2266,Cylinder458,Box2262]
  Origin = -> Origin233
  Placement = pos=(0,-7,0) rot=(0,0,1;0rad)
  Tip = -> Box2262
FEATURE [PartDesign::Fillet] Fillet682
  Base = -> Box2277 [Edge2]
  BaseFeature = -> Box2277
  Placement = pos=(-21.5005,18.625,0.235) rot=(0,-1,0;0.174533rad)
  Radius = 0.05
  SupportTransform = false
FEATURE [PartDesign::Fillet] Fillet673
  Base = -> Fillet682 [Edge33]
  BaseFeature = -> Fillet682
  Placement = pos=(-21.5005,18.625,0.235) rot=(0,-1,0;0.174533rad)
  Radius = 0.5
  SupportTransform = false
FEATURE [PartDesign::AdditiveBox] Box2241
  AttacherType = Attacher::AttachEngine3D
  AttachmentOffset = pos=(-21.1,18.635,0.305) rot=(0,1,0;0.785398rad)
  BaseFeature = -> Fillet673
  Height = 0.375
  Length = 0.2
  MapMode = 5
  Placement = pos=(-21.1,18.635,0.305) rot=(0,1,0;0.785398rad)
  Support = -> [XY_Plane248]
  Width = 0.23
FEATURE [PartDesign::SubtractiveCylinder] Cylinder452
  Angle = 360
  AttacherType = Attacher::AttachEngine3D
  AttachmentOffset = pos=(-21.055,18.935,0.52) rot=(1,0,0;1.5708rad)
  BaseFeature = -> Box2241
  Height = 0.375
  MapMode = 5
  Placement = pos=(-21.055,18.935,0.52) rot=(1,0,0;1.5708rad)
  Radius = 0.205
  Support = -> [XY_Plane248]
FEATURE [PartDesign::SubtractiveBox] Box2244
  AttacherType = Attacher::AttachEngine3D
  AttachmentOffset = pos=(-20.95,18.635,0.53) rot=(0,0,1;0rad)
  BaseFeature = -> Cylinder452
  Height = 0.5
  Length = 0.1
  MapMode = 5
  Placement = pos=(-20.95,18.635,0.53) rot=(0,0,1;0rad)
  Support = -> [XY_Plane248]
  Width = 0.23
FEATURE [PartDesign::SubtractiveBox] Box2245
  AttacherType = Attacher::AttachEngine3D
  AttachmentOffset = pos=(-21.15,18.635,0.297) rot=(0,-1,0;0.174533rad)
  BaseFeature = -> Box2244
  Height = 0.115
  Length = 0.115
  MapMode = 5
  Placement = pos=(-21.15,18.635,0.297) rot=(0,-1,0;0.174533rad)
  Support = -> [XY_Plane248]
  Width = 0.23
FEATURE [PartDesign::Fillet] Fillet677
  Base = -> Box2245 [Edge28]
  BaseFeature = -> Box2245
  Placement = pos=(-21.15,18.635,0.297) rot=(0,-1,0;0.174533rad)
  Radius = 0.375
  SupportTransform = false
FEATURE [PartDesign::AdditiveBox] Box2255
  AttacherType = Attacher::AttachEngine3D
  AttachmentOffset = pos=(-20.7,18.635,1.55) rot=(0,1,0;0.785398rad)
  BaseFeature = -> Fillet677
  Height = 0.375
  Length = 0.23
  MapMode = 5
  Placement = pos=(-20.7,18.635,1.55) rot=(0,1,0;0.785398rad)
  Support = -> [XY_Plane248]
  Width = 0.23
FEATURE [PartDesign::SubtractiveCylinder] Cylinder456
  Angle = 360
  AttacherType = Attacher::AttachEngine3D
  AttachmentOffset = pos=(-20.271,18.635,1.4056) rot=(-1,0,0;1.5708rad)
  BaseFeature = -> Box2255
  Height = 0.23
  MapMode = 5
  Placement = pos=(-20.271,18.635,1.4056) rot=(-1,0,0;1.5708rad)
  Radius = 0.23
  Support = -> [XY_Plane248]
FEATURE [PartDesign::AdditiveBox] Box2249
  AttacherType = Attacher::AttachEngine3D
  AttachmentOffset = pos=(-20.1,18.635,1.635) rot=(0,0,1;0rad)
  BaseFeature = -> Cylinder456
  Height = 0.265
  Length = 0.23
  MapMode = 5
  Placement = pos=(-20.1,18.635,1.635) rot=(0,0,1;0rad)
  Support = -> [XY_Plane248]
  Width = 0.23
FEATURE [PartDesign::Body] Body226  label="pin226"
  Group = -> [Box2261,Box2267,Box2258,Box2259,Box2277,Fillet682,Fillet673,Box2241,Cylinder452,Box2244,Box2245,Fillet677,Box2255,Cylinder456,Box2249]
  Origin = -> Origin244
  Placement = pos=(0,-6.5,0) rot=(0,0,1;0rad)
  Tip = -> Box2249
FEATURE [PartDesign::Fillet] Fillet683
  Base = -> Fillet675 [Edge33]
  BaseFeature = -> Fillet675
  Placement = pos=(-21.5005,18.625,0.235) rot=(0,-1,0;0.174533rad)
  Radius = 0.5
  SupportTransform = false
FEATURE [PartDesign::AdditiveBox] Box2270
  AttacherType = Attacher::AttachEngine3D
  AttachmentOffset = pos=(-21.1,18.635,0.305) rot=(0,1,0;0.785398rad)
  BaseFeature = -> Fillet683
  Height = 0.375
  Length = 0.2
  MapMode = 5
  Placement = pos=(-21.1,18.635,0.305) rot=(0,1,0;0.785398rad)
  Support = -> [XY_Plane246]
  Width = 0.23
FEATURE [PartDesign::SubtractiveCylinder] Cylinder457
  Angle = 360
  AttacherType = Attacher::AttachEngine3D
  AttachmentOffset = pos=(-21.055,18.935,0.52) rot=(1,0,0;1.5708rad)
  BaseFeature = -> Box2270
  Height = 0.375
  MapMode = 5
  Placement = pos=(-21.055,18.935,0.52) rot=(1,0,0;1.5708rad)
  Radius = 0.205
  Support = -> [XY_Plane246]
FEATURE [PartDesign::SubtractiveBox] Box2264
  AttacherType = Attacher::AttachEngine3D
  AttachmentOffset = pos=(-20.95,18.635,0.53) rot=(0,0,1;0rad)
  BaseFeature = -> Cylinder457
  Height = 0.5
  Length = 0.1
  MapMode = 5
  Placement = pos=(-20.95,18.635,0.53) rot=(0,0,1;0rad)
  Support = -> [XY_Plane246]
  Width = 0.23
FEATURE [PartDesign::SubtractiveBox] Box2251
  AttacherType = Attacher::AttachEngine3D
  AttachmentOffset = pos=(-21.15,18.635,0.297) rot=(0,-1,0;0.174533rad)
  BaseFeature = -> Box2264
  Height = 0.115
  Length = 0.115
  MapMode = 5
  Placement = pos=(-21.15,18.635,0.297) rot=(0,-1,0;0.174533rad)
  Support = -> [XY_Plane246]
  Width = 0.23
FEATURE [PartDesign::Fillet] Fillet680
  Base = -> Box2251 [Edge28]
  BaseFeature = -> Box2251
  Placement = pos=(-21.15,18.635,0.297) rot=(0,-1,0;0.174533rad)
  Radius = 0.375
  SupportTransform = false
FEATURE [PartDesign::AdditiveBox] Box2271
  AttacherType = Attacher::AttachEngine3D
  AttachmentOffset = pos=(-20.7,18.635,1.55) rot=(0,1,0;0.785398rad)
  BaseFeature = -> Fillet680
  Height = 0.375
  Length = 0.23
  MapMode = 5
  Placement = pos=(-20.7,18.635,1.55) rot=(0,1,0;0.785398rad)
  Support = -> [XY_Plane246]
  Width = 0.23
FEATURE [PartDesign::SubtractiveCylinder] Cylinder455
  Angle = 360
  AttacherType = Attacher::AttachEngine3D
  AttachmentOffset = pos=(-20.271,18.635,1.4056) rot=(-1,0,0;1.5708rad)
  BaseFeature = -> Box2271
  Height = 0.23
  MapMode = 5
  Placement = pos=(-20.271,18.635,1.4056) rot=(-1,0,0;1.5708rad)
  Radius = 0.23
  Support = -> [XY_Plane246]
FEATURE [PartDesign::AdditiveBox] Box2269
  AttacherType = Attacher::AttachEngine3D
  AttachmentOffset = pos=(-20.1,18.635,1.635) rot=(0,0,1;0rad)
  BaseFeature = -> Cylinder455
  Height = 0.265
  Length = 0.23
  MapMode = 5
  Placement = pos=(-20.1,18.635,1.635) rot=(0,0,1;0rad)
  Support = -> [XY_Plane246]
  Width = 0.23
FEATURE [PartDesign::Body] Body228  label="pin228"
  Group = -> [Box2254,Box2276,Box2243,Box2248,Box2246,Fillet675,Fillet683,Box2270,Cylinder457,Box2264,Box2251,Fillet680,Box2271,Cylinder455,Box2269]
  Origin = -> Origin242
  Placement = pos=(0,-7.5,0) rot=(0,0,1;0rad)
  Tip = -> Box2269
FEATURE [App::Part] Part019  label="Pin-set017"
  Group = -> [Body216,Body213,Body219,Body222,Body214,Body221,Body215,Body217,Body223,Body220,Body218,Body224,Body225,Body226,Body227,Body228]
  Origin = -> Origin237
  Placement = pos=(0,-30,0) rot=(0,0,1;0rad)
FEATURE [App::Part] Part016  label="Pin-collection003"
  Group = -> [Part017,Part015,Part014,Part020,Part018,Part019]
  Origin = -> Origin245
  Placement = pos=(0,0,0) rot=(0,0,1;-1.5708rad)
FEATURE [PartDesign::AdditiveBox] Box2283
  AttacherType = Attacher::AttachEngine3D
  AttachmentOffset = pos=(-21.3,18.635,0) rot=(0,0,1;0rad)
  Height = 1.9
  Length = 1.3
  MapMode = 5
  Placement = pos=(-21.3,18.635,0) rot=(0,0,1;0rad)
  Support = -> [XY_Plane269]
  Width = 0.23
FEATURE [PartDesign::SubtractiveBox] Box2286
  AttacherType = Attacher::AttachEngine3D
  AttachmentOffset = pos=(-21.35,18.635,0.35) rot=(0,0,1;0rad)
  BaseFeature = -> Box2283
  Height = 1.55
  Length = 0.5
  MapMode = 5
  Placement = pos=(-21.35,18.635,0.35) rot=(0,0,1;0rad)
  Support = -> [XY_Plane269]
  Width = 0.23
FEATURE [PartDesign::AdditiveBox] Box2292
  AttacherType = Attacher::AttachEngine3D
  AttachmentOffset = pos=(-21.3,18.635,0) rot=(0,0,1;0rad)
  Height = 1.9
  Length = 1.3
  MapMode = 5
  Placement = pos=(-21.3,18.635,0) rot=(0,0,1;0rad)
  Support = -> [XY_Plane275]
  Width = 0.23
FEATURE [PartDesign::SubtractiveBox] Box2290
  AttacherType = Attacher::AttachEngine3D
  AttachmentOffset = pos=(-21.35,18.635,0.35) rot=(0,0,1;0rad)
  BaseFeature = -> Box2292
  Height = 1.55
  Length = 0.5
  MapMode = 5
  Placement = pos=(-21.35,18.635,0.35) rot=(0,0,1;0rad)
  Support = -> [XY_Plane275]
  Width = 0.23
FEATURE [PartDesign::AdditiveBox] Box2297
  AttacherType = Attacher::AttachEngine3D
  AttachmentOffset = pos=(-21.3,18.635,0) rot=(0,0,1;0rad)
  Height = 1.9
  Length = 1.3
  MapMode = 5
  Placement = pos=(-21.3,18.635,0) rot=(0,0,1;0rad)
  Support = -> [XY_Plane270]
  Width = 0.23
FEATURE [PartDesign::SubtractiveBox] Box2285
  AttacherType = Attacher::AttachEngine3D
  AttachmentOffset = pos=(-21.35,18.635,0.35) rot=(0,0,1;0rad)
  BaseFeature = -> Box2297
  Height = 1.55
  Length = 0.5
  MapMode = 5
  Placement = pos=(-21.35,18.635,0.35) rot=(0,0,1;0rad)
  Support = -> [XY_Plane270]
  Width = 0.23
FEATURE [PartDesign::AdditiveBox] Box2300
  AttacherType = Attacher::AttachEngine3D
  AttachmentOffset = pos=(-21.3,18.635,0) rot=(0,0,1;0rad)
  Height = 1.9
  Length = 1.3
  MapMode = 5
  Placement = pos=(-21.3,18.635,0) rot=(0,0,1;0rad)
  Support = -> [XY_Plane279]
  Width = 0.23
FEATURE [PartDesign::AdditiveBox] Box2301
  AttacherType = Attacher::AttachEngine3D
  AttachmentOffset = pos=(-21.3,18.635,0) rot=(0,0,1;0rad)
  Height = 1.9
  Length = 1.3
  MapMode = 5
  Placement = pos=(-21.3,18.635,0) rot=(0,0,1;0rad)
  Support = -> [XY_Plane283]
  Width = 0.23
FEATURE [PartDesign::AdditiveBox] Box2316
  AttacherType = Attacher::AttachEngine3D
  AttachmentOffset = pos=(-21.3,18.635,0) rot=(0,0,1;0rad)
  Height = 1.9
  Length = 1.3
  MapMode = 5
  Placement = pos=(-21.3,18.635,0) rot=(0,0,1;0rad)
  Support = -> [XY_Plane250]
  Width = 0.23
FEATURE [PartDesign::AdditiveBox] Box2318
  AttacherType = Attacher::AttachEngine3D
  AttachmentOffset = pos=(-21.3,18.635,0) rot=(0,0,1;0rad)
  Height = 1.9
  Length = 1.3
  MapMode = 5
  Placement = pos=(-21.3,18.635,0) rot=(0,0,1;0rad)
  Support = -> [XY_Plane271]
  Width = 0.23
FEATURE [PartDesign::SubtractiveBox] Box2313
  AttacherType = Attacher::AttachEngine3D
  AttachmentOffset = pos=(-21.35,18.635,0.35) rot=(0,0,1;0rad)
  BaseFeature = -> Box2318
  Height = 1.55
  Length = 0.5
  MapMode = 5
  Placement = pos=(-21.35,18.635,0.35) rot=(0,0,1;0rad)
  Support = -> [XY_Plane271]
  Width = 0.23
FEATURE [PartDesign::SubtractiveBox] Box2333
  AttacherType = Attacher::AttachEngine3D
  AttachmentOffset = pos=(-20.5,18.63,0) rot=(0,0,1;0rad)
  BaseFeature = -> Box2286
  Height = 1.635
  Length = 0.5
  MapMode = 5
  Placement = pos=(-20.5,18.63,0) rot=(0,0,1;0rad)
  Support = -> [XY_Plane269]
  Width = 0.25
FEATURE [PartDesign::SubtractiveBox] Box2288
  AttacherType = Attacher::AttachEngine3D
  AttachmentOffset = pos=(-21.19,18.635,-0.12) rot=(0,-1,0;0.15708rad)
  BaseFeature = -> Box2333
  Height = 0.12
  Length = 0.725
  MapMode = 5
  Placement = pos=(-21.19,18.635,-0.12) rot=(0,-1,0;0.15708rad)
  Support = -> [XY_Plane269]
  Width = 0.25
FEATURE [PartDesign::SubtractiveBox] Box2284
  AttacherType = Attacher::AttachEngine3D
  AttachmentOffset = pos=(-21.5005,18.625,0.235) rot=(0,-1,0;0.174533rad)
  BaseFeature = -> Box2288
  Height = 0.3
  Length = 0.6605
  MapMode = 5
  Placement = pos=(-21.5005,18.625,0.235) rot=(0,-1,0;0.174533rad)
  Support = -> [XY_Plane269]
  Width = 0.25
FEATURE [PartDesign::Fillet] Fillet747
  Base = -> Box2284 [Edge2]
  BaseFeature = -> Box2284
  Placement = pos=(-21.5005,18.625,0.235) rot=(0,-1,0;0.174533rad)
  Radius = 0.05
  SupportTransform = false
FEATURE [PartDesign::Fillet] Fillet760
  Base = -> Fillet747 [Edge33]
  BaseFeature = -> Fillet747
  Placement = pos=(-21.5005,18.625,0.235) rot=(0,-1,0;0.174533rad)
  Radius = 0.5
  SupportTransform = false
FEATURE [PartDesign::AdditiveBox] Box2335
  AttacherType = Attacher::AttachEngine3D
  AttachmentOffset = pos=(-21.3,18.635,0) rot=(0,0,1;0rad)
  Height = 1.9
  Length = 1.3
  MapMode = 5
  Placement = pos=(-21.3,18.635,0) rot=(0,0,1;0rad)
  Support = -> [XY_Plane268]
  Width = 0.23
FEATURE [PartDesign::SubtractiveBox] Box2328
  AttacherType = Attacher::AttachEngine3D
  AttachmentOffset = pos=(-21.35,18.635,0.35) rot=(0,0,1;0rad)
  BaseFeature = -> Box2335
  Height = 1.55
  Length = 0.5
  MapMode = 5
  Placement = pos=(-21.35,18.635,0.35) rot=(0,0,1;0rad)
  Support = -> [XY_Plane268]
  Width = 0.23
FEATURE [PartDesign::SubtractiveBox] Box2308
  AttacherType = Attacher::AttachEngine3D
  AttachmentOffset = pos=(-20.5,18.63,0) rot=(0,0,1;0rad)
  BaseFeature = -> Box2328
  Height = 1.635
  Length = 0.5
  MapMode = 5
  Placement = pos=(-20.5,18.63,0) rot=(0,0,1;0rad)
  Support = -> [XY_Plane268]
  Width = 0.25
FEATURE [PartDesign::SubtractiveBox] Box2317
  AttacherType = Attacher::AttachEngine3D
  AttachmentOffset = pos=(-21.19,18.635,-0.12) rot=(0,-1,0;0.15708rad)
  BaseFeature = -> Box2308
  Height = 0.12
  Length = 0.725
  MapMode = 5
  Placement = pos=(-21.19,18.635,-0.12) rot=(0,-1,0;0.15708rad)
  Support = -> [XY_Plane268]
  Width = 0.25
FEATURE [PartDesign::SubtractiveBox] Box2329
  AttacherType = Attacher::AttachEngine3D
  AttachmentOffset = pos=(-21.5005,18.625,0.235) rot=(0,-1,0;0.174533rad)
  BaseFeature = -> Box2317
  Height = 0.3
  Length = 0.6605
  MapMode = 5
  Placement = pos=(-21.5005,18.625,0.235) rot=(0,-1,0;0.174533rad)
  Support = -> [XY_Plane268]
  Width = 0.25
FEATURE [PartDesign::Fillet] Fillet768
  Base = -> Box2329 [Edge2]
  BaseFeature = -> Box2329
  Placement = pos=(-21.5005,18.625,0.235) rot=(0,-1,0;0.174533rad)
  Radius = 0.05
  SupportTransform = false
FEATURE [PartDesign::Fillet] Fillet749
  Base = -> Fillet768 [Edge33]
  BaseFeature = -> Fillet768
  Placement = pos=(-21.5005,18.625,0.235) rot=(0,-1,0;0.174533rad)
  Radius = 0.5
  SupportTransform = false
FEATURE [PartDesign::AdditiveBox] Box2305
  AttacherType = Attacher::AttachEngine3D
  AttachmentOffset = pos=(-21.1,18.635,0.305) rot=(0,1,0;0.785398rad)
  BaseFeature = -> Fillet749
  Height = 0.375
  Length = 0.2
  MapMode = 5
  Placement = pos=(-21.1,18.635,0.305) rot=(0,1,0;0.785398rad)
  Support = -> [XY_Plane268]
  Width = 0.23
FEATURE [PartDesign::SubtractiveCylinder] Cylinder465
  Angle = 360
  AttacherType = Attacher::AttachEngine3D
  AttachmentOffset = pos=(-21.055,18.935,0.52) rot=(1,0,0;1.5708rad)
  BaseFeature = -> Box2305
  Height = 0.375
  MapMode = 5
  Placement = pos=(-21.055,18.935,0.52) rot=(1,0,0;1.5708rad)
  Radius = 0.205
  Support = -> [XY_Plane268]
FEATURE [PartDesign::SubtractiveBox] Box2315
  AttacherType = Attacher::AttachEngine3D
  AttachmentOffset = pos=(-20.95,18.635,0.53) rot=(0,0,1;0rad)
  BaseFeature = -> Cylinder465
  Height = 0.5
  Length = 0.1
  MapMode = 5
  Placement = pos=(-20.95,18.635,0.53) rot=(0,0,1;0rad)
  Support = -> [XY_Plane268]
  Width = 0.23
FEATURE [PartDesign::SubtractiveBox] Box2306
  AttacherType = Attacher::AttachEngine3D
  AttachmentOffset = pos=(-21.15,18.635,0.297) rot=(0,-1,0;0.174533rad)
  BaseFeature = -> Box2315
  Height = 0.115
  Length = 0.115
  MapMode = 5
  Placement = pos=(-21.15,18.635,0.297) rot=(0,-1,0;0.174533rad)
  Support = -> [XY_Plane268]
  Width = 0.23
FEATURE [PartDesign::Fillet] Fillet769
  Base = -> Box2306 [Edge28]
  BaseFeature = -> Box2306
  Placement = pos=(-21.15,18.635,0.297) rot=(0,-1,0;0.174533rad)
  Radius = 0.375
  SupportTransform = false
FEATURE [PartDesign::AdditiveBox] Box2309
  AttacherType = Attacher::AttachEngine3D
  AttachmentOffset = pos=(-20.7,18.635,1.55) rot=(0,1,0;0.785398rad)
  BaseFeature = -> Fillet769
  Height = 0.375
  Length = 0.23
  MapMode = 5
  Placement = pos=(-20.7,18.635,1.55) rot=(0,1,0;0.785398rad)
  Support = -> [XY_Plane268]
  Width = 0.23
FEATURE [PartDesign::SubtractiveCylinder] Cylinder464
  Angle = 360
  AttacherType = Attacher::AttachEngine3D
  AttachmentOffset = pos=(-20.271,18.635,1.4056) rot=(-1,0,0;1.5708rad)
  BaseFeature = -> Box2309
  Height = 0.23
  MapMode = 5
  Placement = pos=(-20.271,18.635,1.4056) rot=(-1,0,0;1.5708rad)
  Radius = 0.23
  Support = -> [XY_Plane268]
FEATURE [PartDesign::SubtractiveBox] Box2338
  AttacherType = Attacher::AttachEngine3D
  AttachmentOffset = pos=(-20.5,18.63,0) rot=(0,0,1;0rad)
  BaseFeature = -> Box2285
  Height = 1.635
  Length = 0.5
  MapMode = 5
  Placement = pos=(-20.5,18.63,0) rot=(0,0,1;0rad)
  Support = -> [XY_Plane270]
  Width = 0.25
FEATURE [PartDesign::AdditiveBox] Box2339
  AttacherType = Attacher::AttachEngine3D
  AttachmentOffset = pos=(-21.3,18.635,0) rot=(0,0,1;0rad)
  Height = 1.9
  Length = 1.3
  MapMode = 5
  Placement = pos=(-21.3,18.635,0) rot=(0,0,1;0rad)
  Support = -> [XY_Plane267]
  Width = 0.23
FEATURE [PartDesign::SubtractiveBox] Box2325
  AttacherType = Attacher::AttachEngine3D
  AttachmentOffset = pos=(-21.35,18.635,0.35) rot=(0,0,1;0rad)
  BaseFeature = -> Box2339
  Height = 1.55
  Length = 0.5
  MapMode = 5
  Placement = pos=(-21.35,18.635,0.35) rot=(0,0,1;0rad)
  Support = -> [XY_Plane267]
  Width = 0.23
FEATURE [PartDesign::SubtractiveBox] Box2340
  AttacherType = Attacher::AttachEngine3D
  AttachmentOffset = pos=(-21.19,18.635,-0.12) rot=(0,-1,0;0.15708rad)
  BaseFeature = -> Box2338
  Height = 0.12
  Length = 0.725
  MapMode = 5
  Placement = pos=(-21.19,18.635,-0.12) rot=(0,-1,0;0.15708rad)
  Support = -> [XY_Plane270]
  Width = 0.25
FEATURE [PartDesign::SubtractiveBox] Box2294
  AttacherType = Attacher::AttachEngine3D
  AttachmentOffset = pos=(-21.5005,18.625,0.235) rot=(0,-1,0;0.174533rad)
  BaseFeature = -> Box2340
  Height = 0.3
  Length = 0.6605
  MapMode = 5
  Placement = pos=(-21.5005,18.625,0.235) rot=(0,-1,0;0.174533rad)
  Support = -> [XY_Plane270]
  Width = 0.25
FEATURE [PartDesign::Fillet] Fillet762
  Base = -> Box2294 [Edge2]
  BaseFeature = -> Box2294
  Placement = pos=(-21.5005,18.625,0.235) rot=(0,-1,0;0.174533rad)
  Radius = 0.05
  SupportTransform = false
FEATURE [PartDesign::Fillet] Fillet753
  Base = -> Fillet762 [Edge33]
  BaseFeature = -> Fillet762
  Placement = pos=(-21.5005,18.625,0.235) rot=(0,-1,0;0.174533rad)
  Radius = 0.5
  SupportTransform = false
FEATURE [PartDesign::AdditiveBox] Box2310
  AttacherType = Attacher::AttachEngine3D
  AttachmentOffset = pos=(-21.1,18.635,0.305) rot=(0,1,0;0.785398rad)
  BaseFeature = -> Fillet753
  Height = 0.375
  Length = 0.2
  MapMode = 5
  Placement = pos=(-21.1,18.635,0.305) rot=(0,1,0;0.785398rad)
  Support = -> [XY_Plane270]
  Width = 0.23
FEATURE [PartDesign::SubtractiveCylinder] Cylinder470
  Angle = 360
  AttacherType = Attacher::AttachEngine3D
  AttachmentOffset = pos=(-21.055,18.935,0.52) rot=(1,0,0;1.5708rad)
  BaseFeature = -> Box2310
  Height = 0.375
  MapMode = 5
  Placement = pos=(-21.055,18.935,0.52) rot=(1,0,0;1.5708rad)
  Radius = 0.205
  Support = -> [XY_Plane270]
FEATURE [PartDesign::SubtractiveBox] Box2337
  AttacherType = Attacher::AttachEngine3D
  AttachmentOffset = pos=(-20.95,18.635,0.53) rot=(0,0,1;0rad)
  BaseFeature = -> Cylinder470
  Height = 0.5
  Length = 0.1
  MapMode = 5
  Placement = pos=(-20.95,18.635,0.53) rot=(0,0,1;0rad)
  Support = -> [XY_Plane270]
  Width = 0.23
FEATURE [PartDesign::SubtractiveBox] Box2336
  AttacherType = Attacher::AttachEngine3D
  AttachmentOffset = pos=(-21.15,18.635,0.297) rot=(0,-1,0;0.174533rad)
  BaseFeature = -> Box2337
  Height = 0.115
  Length = 0.115
  MapMode = 5
  Placement = pos=(-21.15,18.635,0.297) rot=(0,-1,0;0.174533rad)
  Support = -> [XY_Plane270]
  Width = 0.23
FEATURE [PartDesign::Fillet] Fillet764
  Base = -> Box2336 [Edge28]
  BaseFeature = -> Box2336
  Placement = pos=(-21.15,18.635,0.297) rot=(0,-1,0;0.174533rad)
  Radius = 0.375
  SupportTransform = false
FEATURE [PartDesign::AdditiveBox] Box2344
  AttacherType = Attacher::AttachEngine3D
  AttachmentOffset = pos=(-20.7,18.635,1.55) rot=(0,1,0;0.785398rad)
  BaseFeature = -> Fillet764
  Height = 0.375
  Length = 0.23
  MapMode = 5
  Placement = pos=(-20.7,18.635,1.55) rot=(0,1,0;0.785398rad)
  Support = -> [XY_Plane270]
  Width = 0.23
FEATURE [PartDesign::SubtractiveCylinder] Cylinder471
  Angle = 360
  AttacherType = Attacher::AttachEngine3D
  AttachmentOffset = pos=(-20.271,18.635,1.4056) rot=(-1,0,0;1.5708rad)
  BaseFeature = -> Box2344
  Height = 0.23
  MapMode = 5
  Placement = pos=(-20.271,18.635,1.4056) rot=(-1,0,0;1.5708rad)
  Radius = 0.23
  Support = -> [XY_Plane270]
FEATURE [PartDesign::AdditiveBox] Box2341
  AttacherType = Attacher::AttachEngine3D
  AttachmentOffset = pos=(-20.1,18.635,1.635) rot=(0,0,1;0rad)
  BaseFeature = -> Cylinder471
  Height = 0.265
  Length = 0.23
  MapMode = 5
  Placement = pos=(-20.1,18.635,1.635) rot=(0,0,1;0rad)
  Support = -> [XY_Plane270]
  Width = 0.23
FEATURE [PartDesign::Body] Body252  label="pin252"
  Group = -> [Box2297,Box2285,Box2338,Box2340,Box2294,Fillet762,Fillet753,Box2310,Cylinder470,Box2337,Box2336,Fillet764,Box2344,Cylinder471,Box2341]
  Origin = -> Origin253
  Placement = pos=(0,-3,0) rot=(0,0,1;0rad)
  Tip = -> Box2341
FEATURE [PartDesign::SubtractiveBox] Box2350
  AttacherType = Attacher::AttachEngine3D
  AttachmentOffset = pos=(-20.5,18.63,0) rot=(0,0,1;0rad)
  BaseFeature = -> Box2290
  Height = 1.635
  Length = 0.5
  MapMode = 5
  Placement = pos=(-20.5,18.63,0) rot=(0,0,1;0rad)
  Support = -> [XY_Plane275]
  Width = 0.25
FEATURE [PartDesign::SubtractiveBox] Box2287
  AttacherType = Attacher::AttachEngine3D
  AttachmentOffset = pos=(-21.19,18.635,-0.12) rot=(0,-1,0;0.15708rad)
  BaseFeature = -> Box2350
  Height = 0.12
  Length = 0.725
  MapMode = 5
  Placement = pos=(-21.19,18.635,-0.12) rot=(0,-1,0;0.15708rad)
  Support = -> [XY_Plane275]
  Width = 0.25
FEATURE [PartDesign::SubtractiveBox] Box2281
  AttacherType = Attacher::AttachEngine3D
  AttachmentOffset = pos=(-21.5005,18.625,0.235) rot=(0,-1,0;0.174533rad)
  BaseFeature = -> Box2287
  Height = 0.3
  Length = 0.6605
  MapMode = 5
  Placement = pos=(-21.5005,18.625,0.235) rot=(0,-1,0;0.174533rad)
  Support = -> [XY_Plane275]
  Width = 0.25
FEATURE [PartDesign::Fillet] Fillet752
  Base = -> Box2281 [Edge2]
  BaseFeature = -> Box2281
  Placement = pos=(-21.5005,18.625,0.235) rot=(0,-1,0;0.174533rad)
  Radius = 0.05
  SupportTransform = false
FEATURE [PartDesign::Fillet] Fillet756
  Base = -> Fillet752 [Edge33]
  BaseFeature = -> Fillet752
  Placement = pos=(-21.5005,18.625,0.235) rot=(0,-1,0;0.174533rad)
  Radius = 0.5
  SupportTransform = false
FEATURE [PartDesign::AdditiveBox] Box2349
  AttacherType = Attacher::AttachEngine3D
  AttachmentOffset = pos=(-21.1,18.635,0.305) rot=(0,1,0;0.785398rad)
  BaseFeature = -> Fillet756
  Height = 0.375
  Length = 0.2
  MapMode = 5
  Placement = pos=(-21.1,18.635,0.305) rot=(0,1,0;0.785398rad)
  Support = -> [XY_Plane275]
  Width = 0.23
FEATURE [PartDesign::AdditiveBox] Box2351
  AttacherType = Attacher::AttachEngine3D
  AttachmentOffset = pos=(-21.1,18.635,0.305) rot=(0,1,0;0.785398rad)
  BaseFeature = -> Fillet760
  Height = 0.375
  Length = 0.2
  MapMode = 5
  Placement = pos=(-21.1,18.635,0.305) rot=(0,1,0;0.785398rad)
  Support = -> [XY_Plane269]
  Width = 0.23
FEATURE [PartDesign::SubtractiveCylinder] Cylinder461
  Angle = 360
  AttacherType = Attacher::AttachEngine3D
  AttachmentOffset = pos=(-21.055,18.935,0.52) rot=(1,0,0;1.5708rad)
  BaseFeature = -> Box2351
  Height = 0.375
  MapMode = 5
  Placement = pos=(-21.055,18.935,0.52) rot=(1,0,0;1.5708rad)
  Radius = 0.205
  Support = -> [XY_Plane269]
FEATURE [PartDesign::SubtractiveBox] Box2296
  AttacherType = Attacher::AttachEngine3D
  AttachmentOffset = pos=(-20.95,18.635,0.53) rot=(0,0,1;0rad)
  BaseFeature = -> Cylinder461
  Height = 0.5
  Length = 0.1
  MapMode = 5
  Placement = pos=(-20.95,18.635,0.53) rot=(0,0,1;0rad)
  Support = -> [XY_Plane269]
  Width = 0.23
FEATURE [PartDesign::SubtractiveBox] Box2293
  AttacherType = Attacher::AttachEngine3D
  AttachmentOffset = pos=(-21.15,18.635,0.297) rot=(0,-1,0;0.174533rad)
  BaseFeature = -> Box2296
  Height = 0.115
  Length = 0.115
  MapMode = 5
  Placement = pos=(-21.15,18.635,0.297) rot=(0,-1,0;0.174533rad)
  Support = -> [XY_Plane269]
  Width = 0.23
FEATURE [PartDesign::Fillet] Fillet767
  Base = -> Box2293 [Edge28]
  BaseFeature = -> Box2293
  Placement = pos=(-21.15,18.635,0.297) rot=(0,-1,0;0.174533rad)
  Radius = 0.375
  SupportTransform = false
FEATURE [PartDesign::AdditiveBox] Box2282
  AttacherType = Attacher::AttachEngine3D
  AttachmentOffset = pos=(-20.7,18.635,1.55) rot=(0,1,0;0.785398rad)
  BaseFeature = -> Fillet767
  Height = 0.375
  Length = 0.23
  MapMode = 5
  Placement = pos=(-20.7,18.635,1.55) rot=(0,1,0;0.785398rad)
  Support = -> [XY_Plane269]
  Width = 0.23
FEATURE [PartDesign::SubtractiveCylinder] Cylinder460
  Angle = 360
  AttacherType = Attacher::AttachEngine3D
  AttachmentOffset = pos=(-20.271,18.635,1.4056) rot=(-1,0,0;1.5708rad)
  BaseFeature = -> Box2282
  Height = 0.23
  MapMode = 5
  Placement = pos=(-20.271,18.635,1.4056) rot=(-1,0,0;1.5708rad)
  Radius = 0.23
  Support = -> [XY_Plane269]
FEATURE [PartDesign::AdditiveBox] Box2289
  AttacherType = Attacher::AttachEngine3D
  AttachmentOffset = pos=(-20.1,18.635,1.635) rot=(0,0,1;0rad)
  BaseFeature = -> Cylinder460
  Height = 0.265
  Length = 0.23
  MapMode = 5
  Placement = pos=(-20.1,18.635,1.635) rot=(0,0,1;0rad)
  Support = -> [XY_Plane269]
  Width = 0.23
FEATURE [PartDesign::Body] Body255  label="pin255"
  Group = -> [Box2283,Box2286,Box2333,Box2288,Box2284,Fillet747,Fillet760,Box2351,Cylinder461,Box2296,Box2293,Fillet767,Box2282,Cylinder460,Box2289]
  Origin = -> Origin266
  Placement = pos=(0,-4,0) rot=(0,0,1;0rad)
  Tip = -> Box2289
FEATURE [PartDesign::SubtractiveCylinder] Cylinder474
  Angle = 360
  AttacherType = Attacher::AttachEngine3D
  AttachmentOffset = pos=(-21.055,18.935,0.52) rot=(1,0,0;1.5708rad)
  BaseFeature = -> Box2349
  Height = 0.375
  MapMode = 5
  Placement = pos=(-21.055,18.935,0.52) rot=(1,0,0;1.5708rad)
  Radius = 0.205
  Support = -> [XY_Plane275]
FEATURE [PartDesign::SubtractiveBox] Box2352
  AttacherType = Attacher::AttachEngine3D
  AttachmentOffset = pos=(-20.95,18.635,0.53) rot=(0,0,1;0rad)
  BaseFeature = -> Cylinder474
  Height = 0.5
  Length = 0.1
  MapMode = 5
  Placement = pos=(-20.95,18.635,0.53) rot=(0,0,1;0rad)
  Support = -> [XY_Plane275]
  Width = 0.23
FEATURE [PartDesign::SubtractiveBox] Box2345
  AttacherType = Attacher::AttachEngine3D
  AttachmentOffset = pos=(-21.15,18.635,0.297) rot=(0,-1,0;0.174533rad)
  BaseFeature = -> Box2352
  Height = 0.115
  Length = 0.115
  MapMode = 5
  Placement = pos=(-21.15,18.635,0.297) rot=(0,-1,0;0.174533rad)
  Support = -> [XY_Plane275]
  Width = 0.23
FEATURE [PartDesign::Fillet] Fillet761
  Base = -> Box2345 [Edge28]
  BaseFeature = -> Box2345
  Placement = pos=(-21.15,18.635,0.297) rot=(0,-1,0;0.174533rad)
  Radius = 0.375
  SupportTransform = false
FEATURE [PartDesign::AdditiveBox] Box2346
  AttacherType = Attacher::AttachEngine3D
  AttachmentOffset = pos=(-20.7,18.635,1.55) rot=(0,1,0;0.785398rad)
  BaseFeature = -> Fillet761
  Height = 0.375
  Length = 0.23
  MapMode = 5
  Placement = pos=(-20.7,18.635,1.55) rot=(0,1,0;0.785398rad)
  Support = -> [XY_Plane275]
  Width = 0.23
FEATURE [PartDesign::SubtractiveCylinder] Cylinder472
  Angle = 360
  AttacherType = Attacher::AttachEngine3D
  AttachmentOffset = pos=(-20.271,18.635,1.4056) rot=(-1,0,0;1.5708rad)
  BaseFeature = -> Box2346
  Height = 0.23
  MapMode = 5
  Placement = pos=(-20.271,18.635,1.4056) rot=(-1,0,0;1.5708rad)
  Radius = 0.23
  Support = -> [XY_Plane275]
FEATURE [PartDesign::AdditiveBox] Box2291
  AttacherType = Attacher::AttachEngine3D
  AttachmentOffset = pos=(-20.1,18.635,1.635) rot=(0,0,1;0rad)
  BaseFeature = -> Cylinder472
  Height = 0.265
  Length = 0.23
  MapMode = 5
  Placement = pos=(-20.1,18.635,1.635) rot=(0,0,1;0rad)
  Support = -> [XY_Plane275]
  Width = 0.23
FEATURE [PartDesign::Body] Body253  label="pin253"
  Group = -> [Box2292,Box2290,Box2350,Box2287,Box2281,Fillet752,Fillet756,Box2349,Cylinder474,Box2352,Box2345,Fillet761,Box2346,Cylinder472,Box2291]
  Origin = -> Origin259
  Placement = pos=(0,-3.5,0) rot=(0,0,1;0rad)
  Tip = -> Box2291
FEATURE [PartDesign::AdditiveBox] Box2356
  AttacherType = Attacher::AttachEngine3D
  AttachmentOffset = pos=(-21.3,18.635,0) rot=(0,0,1;0rad)
  Height = 1.9
  Length = 1.3
  MapMode = 5
  Placement = pos=(-21.3,18.635,0) rot=(0,0,1;0rad)
  Support = -> [XY_Plane285]
  Width = 0.23
FEATURE [PartDesign::SubtractiveBox] Box2361
  AttacherType = Attacher::AttachEngine3D
  AttachmentOffset = pos=(-21.35,18.635,0.35) rot=(0,0,1;0rad)
  BaseFeature = -> Box2356
  Height = 1.55
  Length = 0.5
  MapMode = 5
  Placement = pos=(-21.35,18.635,0.35) rot=(0,0,1;0rad)
  Support = -> [XY_Plane285]
  Width = 0.23
FEATURE [PartDesign::SubtractiveBox] Box2362
  AttacherType = Attacher::AttachEngine3D
  AttachmentOffset = pos=(-21.35,18.635,0.35) rot=(0,0,1;0rad)
  BaseFeature = -> Box2300
  Height = 1.55
  Length = 0.5
  MapMode = 5
  Placement = pos=(-21.35,18.635,0.35) rot=(0,0,1;0rad)
  Support = -> [XY_Plane279]
  Width = 0.23
FEATURE [PartDesign::SubtractiveBox] Box2364
  AttacherType = Attacher::AttachEngine3D
  AttachmentOffset = pos=(-21.35,18.635,0.35) rot=(0,0,1;0rad)
  BaseFeature = -> Box2301
  Height = 1.55
  Length = 0.5
  MapMode = 5
  Placement = pos=(-21.35,18.635,0.35) rot=(0,0,1;0rad)
  Support = -> [XY_Plane283]
  Width = 0.23
FEATURE [PartDesign::AdditiveBox] Box2377
  AttacherType = Attacher::AttachEngine3D
  AttachmentOffset = pos=(-21.3,18.635,0) rot=(0,0,1;0rad)
  Height = 1.9
  Length = 1.3
  MapMode = 5
  Placement = pos=(-21.3,18.635,0) rot=(0,0,1;0rad)
  Support = -> [XY_Plane254]
  Width = 0.23
FEATURE [PartDesign::SubtractiveBox] Box2384
  AttacherType = Attacher::AttachEngine3D
  AttachmentOffset = pos=(-21.35,18.635,0.35) rot=(0,0,1;0rad)
  BaseFeature = -> Box2377
  Height = 1.55
  Length = 0.5
  MapMode = 5
  Placement = pos=(-21.35,18.635,0.35) rot=(0,0,1;0rad)
  Support = -> [XY_Plane254]
  Width = 0.23
FEATURE [PartDesign::SubtractiveBox] Box2372
  AttacherType = Attacher::AttachEngine3D
  AttachmentOffset = pos=(-20.5,18.63,0) rot=(0,0,1;0rad)
  BaseFeature = -> Box2384
  Height = 1.635
  Length = 0.5
  MapMode = 5
  Placement = pos=(-20.5,18.63,0) rot=(0,0,1;0rad)
  Support = -> [XY_Plane254]
  Width = 0.25
FEATURE [PartDesign::SubtractiveBox] Box2390
  AttacherType = Attacher::AttachEngine3D
  AttachmentOffset = pos=(-21.19,18.635,-0.12) rot=(0,-1,0;0.15708rad)
  BaseFeature = -> Box2372
  Height = 0.12
  Length = 0.725
  MapMode = 5
  Placement = pos=(-21.19,18.635,-0.12) rot=(0,-1,0;0.15708rad)
  Support = -> [XY_Plane254]
  Width = 0.25
FEATURE [PartDesign::SubtractiveBox] Box2388
  AttacherType = Attacher::AttachEngine3D
  AttachmentOffset = pos=(-21.5005,18.625,0.235) rot=(0,-1,0;0.174533rad)
  BaseFeature = -> Box2390
  Height = 0.3
  Length = 0.6605
  MapMode = 5
  Placement = pos=(-21.5005,18.625,0.235) rot=(0,-1,0;0.174533rad)
  Support = -> [XY_Plane254]
  Width = 0.25
FEATURE [PartDesign::Fillet] Fillet742
  Base = -> Box2388 [Edge2]
  BaseFeature = -> Box2388
  Placement = pos=(-21.5005,18.625,0.235) rot=(0,-1,0;0.174533rad)
  Radius = 0.05
  SupportTransform = false
FEATURE [PartDesign::Fillet] Fillet744
  Base = -> Fillet742 [Edge33]
  BaseFeature = -> Fillet742
  Placement = pos=(-21.5005,18.625,0.235) rot=(0,-1,0;0.174533rad)
  Radius = 0.5
  SupportTransform = false
FEATURE [PartDesign::AdditiveBox] Box2373
  AttacherType = Attacher::AttachEngine3D
  AttachmentOffset = pos=(-21.1,18.635,0.305) rot=(0,1,0;0.785398rad)
  BaseFeature = -> Fillet744
  Height = 0.375
  Length = 0.2
  MapMode = 5
  Placement = pos=(-21.1,18.635,0.305) rot=(0,1,0;0.785398rad)
  Support = -> [XY_Plane254]
  Width = 0.23
FEATURE [PartDesign::SubtractiveCylinder] Cylinder478
  Angle = 360
  AttacherType = Attacher::AttachEngine3D
  AttachmentOffset = pos=(-21.055,18.935,0.52) rot=(1,0,0;1.5708rad)
  BaseFeature = -> Box2373
  Height = 0.375
  MapMode = 5
  Placement = pos=(-21.055,18.935,0.52) rot=(1,0,0;1.5708rad)
  Radius = 0.205
  Support = -> [XY_Plane254]
FEATURE [PartDesign::SubtractiveBox] Box2385
  AttacherType = Attacher::AttachEngine3D
  AttachmentOffset = pos=(-20.95,18.635,0.53) rot=(0,0,1;0rad)
  BaseFeature = -> Cylinder478
  Height = 0.5
  Length = 0.1
  MapMode = 5
  Placement = pos=(-20.95,18.635,0.53) rot=(0,0,1;0rad)
  Support = -> [XY_Plane254]
  Width = 0.23
FEATURE [PartDesign::SubtractiveBox] Box2381
  AttacherType = Attacher::AttachEngine3D
  AttachmentOffset = pos=(-21.15,18.635,0.297) rot=(0,-1,0;0.174533rad)
  BaseFeature = -> Box2385
  Height = 0.115
  Length = 0.115
  MapMode = 5
  Placement = pos=(-21.15,18.635,0.297) rot=(0,-1,0;0.174533rad)
  Support = -> [XY_Plane254]
  Width = 0.23
FEATURE [PartDesign::Fillet] Fillet731
  Base = -> Box2381 [Edge28]
  BaseFeature = -> Box2381
  Placement = pos=(-21.15,18.635,0.297) rot=(0,-1,0;0.174533rad)
  Radius = 0.375
  SupportTransform = false
FEATURE [PartDesign::AdditiveBox] Box2382
  AttacherType = Attacher::AttachEngine3D
  AttachmentOffset = pos=(-20.7,18.635,1.55) rot=(0,1,0;0.785398rad)
  BaseFeature = -> Fillet731
  Height = 0.375
  Length = 0.23
  MapMode = 5
  Placement = pos=(-20.7,18.635,1.55) rot=(0,1,0;0.785398rad)
  Support = -> [XY_Plane254]
  Width = 0.23
FEATURE [PartDesign::SubtractiveCylinder] Cylinder480
  Angle = 360
  AttacherType = Attacher::AttachEngine3D
  AttachmentOffset = pos=(-20.271,18.635,1.4056) rot=(-1,0,0;1.5708rad)
  BaseFeature = -> Box2382
  Height = 0.23
  MapMode = 5
  Placement = pos=(-20.271,18.635,1.4056) rot=(-1,0,0;1.5708rad)
  Radius = 0.23
  Support = -> [XY_Plane254]
FEATURE [PartDesign::AdditiveBox] Box2391
  AttacherType = Attacher::AttachEngine3D
  AttachmentOffset = pos=(-20.1,18.635,1.635) rot=(0,0,1;0rad)
  BaseFeature = -> Cylinder480
  Height = 0.265
  Length = 0.23
  MapMode = 5
  Placement = pos=(-20.1,18.635,1.635) rot=(0,0,1;0rad)
  Support = -> [XY_Plane254]
  Width = 0.23
FEATURE [PartDesign::Body] Body246  label="pin246"
  Group = -> [Box2377,Box2384,Box2372,Box2390,Box2388,Fillet742,Fillet744,Box2373,Cylinder478,Box2385,Box2381,Fillet731,Box2382,Cylinder480,Box2391]
  Origin = -> Origin263
  Placement = pos=(0,-2,0) rot=(0,0,1;0rad)
  Tip = -> Box2391
FEATURE [PartDesign::SubtractiveBox] Box2392
  AttacherType = Attacher::AttachEngine3D
  AttachmentOffset = pos=(-21.35,18.635,0.35) rot=(0,0,1;0rad)
  BaseFeature = -> Box2316
  Height = 1.55
  Length = 0.5
  MapMode = 5
  Placement = pos=(-21.35,18.635,0.35) rot=(0,0,1;0rad)
  Support = -> [XY_Plane250]
  Width = 0.23
FEATURE [PartDesign::SubtractiveBox] Box2369
  AttacherType = Attacher::AttachEngine3D
  AttachmentOffset = pos=(-20.5,18.63,0) rot=(0,0,1;0rad)
  BaseFeature = -> Box2392
  Height = 1.635
  Length = 0.5
  MapMode = 5
  Placement = pos=(-20.5,18.63,0) rot=(0,0,1;0rad)
  Support = -> [XY_Plane250]
  Width = 0.25
FEATURE [PartDesign::SubtractiveBox] Box2370
  AttacherType = Attacher::AttachEngine3D
  AttachmentOffset = pos=(-21.19,18.635,-0.12) rot=(0,-1,0;0.15708rad)
  BaseFeature = -> Box2369
  Height = 0.12
  Length = 0.725
  MapMode = 5
  Placement = pos=(-21.19,18.635,-0.12) rot=(0,-1,0;0.15708rad)
  Support = -> [XY_Plane250]
  Width = 0.25
FEATURE [PartDesign::SubtractiveBox] Box2387
  AttacherType = Attacher::AttachEngine3D
  AttachmentOffset = pos=(-21.5005,18.625,0.235) rot=(0,-1,0;0.174533rad)
  BaseFeature = -> Box2370
  Height = 0.3
  Length = 0.6605
  MapMode = 5
  Placement = pos=(-21.5005,18.625,0.235) rot=(0,-1,0;0.174533rad)
  Support = -> [XY_Plane250]
  Width = 0.25
FEATURE [PartDesign::Fillet] Fillet750
  Base = -> Box2387 [Edge2]
  BaseFeature = -> Box2387
  Placement = pos=(-21.5005,18.625,0.235) rot=(0,-1,0;0.174533rad)
  Radius = 0.05
  SupportTransform = false
FEATURE [PartDesign::Fillet] Fillet733
  Base = -> Fillet750 [Edge33]
  BaseFeature = -> Fillet750
  Placement = pos=(-21.5005,18.625,0.235) rot=(0,-1,0;0.174533rad)
  Radius = 0.5
  SupportTransform = false
FEATURE [PartDesign::AdditiveBox] Box2368
  AttacherType = Attacher::AttachEngine3D
  AttachmentOffset = pos=(-21.1,18.635,0.305) rot=(0,1,0;0.785398rad)
  BaseFeature = -> Fillet733
  Height = 0.375
  Length = 0.2
  MapMode = 5
  Placement = pos=(-21.1,18.635,0.305) rot=(0,1,0;0.785398rad)
  Support = -> [XY_Plane250]
  Width = 0.23
FEATURE [PartDesign::SubtractiveCylinder] Cylinder477
  Angle = 360
  AttacherType = Attacher::AttachEngine3D
  AttachmentOffset = pos=(-21.055,18.935,0.52) rot=(1,0,0;1.5708rad)
  BaseFeature = -> Box2368
  Height = 0.375
  MapMode = 5
  Placement = pos=(-21.055,18.935,0.52) rot=(1,0,0;1.5708rad)
  Radius = 0.205
  Support = -> [XY_Plane250]
FEATURE [PartDesign::SubtractiveBox] Box2378
  AttacherType = Attacher::AttachEngine3D
  AttachmentOffset = pos=(-20.95,18.635,0.53) rot=(0,0,1;0rad)
  BaseFeature = -> Cylinder477
  Height = 0.5
  Length = 0.1
  MapMode = 5
  Placement = pos=(-20.95,18.635,0.53) rot=(0,0,1;0rad)
  Support = -> [XY_Plane250]
  Width = 0.23
FEATURE [PartDesign::SubtractiveBox] Box2376
  AttacherType = Attacher::AttachEngine3D
  AttachmentOffset = pos=(-21.15,18.635,0.297) rot=(0,-1,0;0.174533rad)
  BaseFeature = -> Box2378
  Height = 0.115
  Length = 0.115
  MapMode = 5
  Placement = pos=(-21.15,18.635,0.297) rot=(0,-1,0;0.174533rad)
  Support = -> [XY_Plane250]
  Width = 0.23
FEATURE [PartDesign::Fillet] Fillet755
  Base = -> Box2376 [Edge28]
  BaseFeature = -> Box2376
  Placement = pos=(-21.15,18.635,0.297) rot=(0,-1,0;0.174533rad)
  Radius = 0.375
  SupportTransform = false
FEATURE [PartDesign::AdditiveBox] Box2375
  AttacherType = Attacher::AttachEngine3D
  AttachmentOffset = pos=(-20.7,18.635,1.55) rot=(0,1,0;0.785398rad)
  BaseFeature = -> Fillet755
  Height = 0.375
  Length = 0.23
  MapMode = 5
  Placement = pos=(-20.7,18.635,1.55) rot=(0,1,0;0.785398rad)
  Support = -> [XY_Plane250]
  Width = 0.23
FEATURE [PartDesign::SubtractiveCylinder] Cylinder479
  Angle = 360
  AttacherType = Attacher::AttachEngine3D
  AttachmentOffset = pos=(-20.271,18.635,1.4056) rot=(-1,0,0;1.5708rad)
  BaseFeature = -> Box2375
  Height = 0.23
  MapMode = 5
  Placement = pos=(-20.271,18.635,1.4056) rot=(-1,0,0;1.5708rad)
  Radius = 0.23
  Support = -> [XY_Plane250]
FEATURE [PartDesign::AdditiveBox] Box2374
  AttacherType = Attacher::AttachEngine3D
  AttachmentOffset = pos=(-20.1,18.635,1.635) rot=(0,0,1;0rad)
  BaseFeature = -> Cylinder479
  Height = 0.265
  Length = 0.23
  MapMode = 5
  Placement = pos=(-20.1,18.635,1.635) rot=(0,0,1;0rad)
  Support = -> [XY_Plane250]
  Width = 0.23
FEATURE [PartDesign::Body] Body250  label="pin250"
  Group = -> [Box2316,Box2392,Box2369,Box2370,Box2387,Fillet750,Fillet733,Box2368,Cylinder477,Box2378,Box2376,Fillet755,Box2375,Cylinder479,Box2374]
  Origin = -> Origin254
  Placement = pos=(0,-1.5,0) rot=(0,0,1;0rad)
  Tip = -> Box2374
FEATURE [PartDesign::AdditiveBox] Box2394
  AttacherType = Attacher::AttachEngine3D
  AttachmentOffset = pos=(-20.1,18.635,1.635) rot=(0,0,1;0rad)
  BaseFeature = -> Cylinder464
  Height = 0.265
  Length = 0.23
  MapMode = 5
  Placement = pos=(-20.1,18.635,1.635) rot=(0,0,1;0rad)
  Support = -> [XY_Plane268]
  Width = 0.23
FEATURE [PartDesign::Body] Body257  label="pin257"
  Group = -> [Box2335,Box2328,Box2308,Box2317,Box2329,Fillet768,Fillet749,Box2305,Cylinder465,Box2315,Box2306,Fillet769,Box2309,Cylinder464,Box2394]
  Origin = -> Origin262
  Placement = pos=(0,-4.5,0) rot=(0,0,1;0rad)
  Tip = -> Box2394
FEATURE [PartDesign::SubtractiveBox] Box2395
  AttacherType = Attacher::AttachEngine3D
  AttachmentOffset = pos=(-20.5,18.63,0) rot=(0,0,1;0rad)
  BaseFeature = -> Box2325
  Height = 1.635
  Length = 0.5
  MapMode = 5
  Placement = pos=(-20.5,18.63,0) rot=(0,0,1;0rad)
  Support = -> [XY_Plane267]
  Width = 0.25
FEATURE [PartDesign::SubtractiveBox] Box2311
  AttacherType = Attacher::AttachEngine3D
  AttachmentOffset = pos=(-21.19,18.635,-0.12) rot=(0,-1,0;0.15708rad)
  BaseFeature = -> Box2395
  Height = 0.12
  Length = 0.725
  MapMode = 5
  Placement = pos=(-21.19,18.635,-0.12) rot=(0,-1,0;0.15708rad)
  Support = -> [XY_Plane267]
  Width = 0.25
FEATURE [PartDesign::SubtractiveBox] Box2322
  AttacherType = Attacher::AttachEngine3D
  AttachmentOffset = pos=(-21.5005,18.625,0.235) rot=(0,-1,0;0.174533rad)
  BaseFeature = -> Box2311
  Height = 0.3
  Length = 0.6605
  MapMode = 5
  Placement = pos=(-21.5005,18.625,0.235) rot=(0,-1,0;0.174533rad)
  Support = -> [XY_Plane267]
  Width = 0.25
FEATURE [PartDesign::Fillet] Fillet751
  Base = -> Box2322 [Edge2]
  BaseFeature = -> Box2322
  Placement = pos=(-21.5005,18.625,0.235) rot=(0,-1,0;0.174533rad)
  Radius = 0.05
  SupportTransform = false
FEATURE [PartDesign::Fillet] Fillet766
  Base = -> Fillet751 [Edge33]
  BaseFeature = -> Fillet751
  Placement = pos=(-21.5005,18.625,0.235) rot=(0,-1,0;0.174533rad)
  Radius = 0.5
  SupportTransform = false
FEATURE [PartDesign::AdditiveBox] Box2324
  AttacherType = Attacher::AttachEngine3D
  AttachmentOffset = pos=(-21.1,18.635,0.305) rot=(0,1,0;0.785398rad)
  BaseFeature = -> Fillet766
  Height = 0.375
  Length = 0.2
  MapMode = 5
  Placement = pos=(-21.1,18.635,0.305) rot=(0,1,0;0.785398rad)
  Support = -> [XY_Plane267]
  Width = 0.23
FEATURE [PartDesign::SubtractiveCylinder] Cylinder468
  Angle = 360
  AttacherType = Attacher::AttachEngine3D
  AttachmentOffset = pos=(-21.055,18.935,0.52) rot=(1,0,0;1.5708rad)
  BaseFeature = -> Box2324
  Height = 0.375
  MapMode = 5
  Placement = pos=(-21.055,18.935,0.52) rot=(1,0,0;1.5708rad)
  Radius = 0.205
  Support = -> [XY_Plane267]
FEATURE [PartDesign::SubtractiveBox] Box2330
  AttacherType = Attacher::AttachEngine3D
  AttachmentOffset = pos=(-20.95,18.635,0.53) rot=(0,0,1;0rad)
  BaseFeature = -> Cylinder468
  Height = 0.5
  Length = 0.1
  MapMode = 5
  Placement = pos=(-20.95,18.635,0.53) rot=(0,0,1;0rad)
  Support = -> [XY_Plane267]
  Width = 0.23
FEATURE [PartDesign::SubtractiveBox] Box2332
  AttacherType = Attacher::AttachEngine3D
  AttachmentOffset = pos=(-21.15,18.635,0.297) rot=(0,-1,0;0.174533rad)
  BaseFeature = -> Box2330
  Height = 0.115
  Length = 0.115
  MapMode = 5
  Placement = pos=(-21.15,18.635,0.297) rot=(0,-1,0;0.174533rad)
  Support = -> [XY_Plane267]
  Width = 0.23
FEATURE [PartDesign::Fillet] Fillet748
  Base = -> Box2332 [Edge28]
  BaseFeature = -> Box2332
  Placement = pos=(-21.15,18.635,0.297) rot=(0,-1,0;0.174533rad)
  Radius = 0.375
  SupportTransform = false
FEATURE [PartDesign::AdditiveBox] Box2331
  AttacherType = Attacher::AttachEngine3D
  AttachmentOffset = pos=(-20.7,18.635,1.55) rot=(0,1,0;0.785398rad)
  BaseFeature = -> Fillet748
  Height = 0.375
  Length = 0.23
  MapMode = 5
  Placement = pos=(-20.7,18.635,1.55) rot=(0,1,0;0.785398rad)
  Support = -> [XY_Plane267]
  Width = 0.23
FEATURE [PartDesign::SubtractiveCylinder] Cylinder467
  Angle = 360
  AttacherType = Attacher::AttachEngine3D
  AttachmentOffset = pos=(-20.271,18.635,1.4056) rot=(-1,0,0;1.5708rad)
  BaseFeature = -> Box2331
  Height = 0.23
  MapMode = 5
  Placement = pos=(-20.271,18.635,1.4056) rot=(-1,0,0;1.5708rad)
  Radius = 0.23
  Support = -> [XY_Plane267]
FEATURE [PartDesign::AdditiveBox] Box2307
  AttacherType = Attacher::AttachEngine3D
  AttachmentOffset = pos=(-20.1,18.635,1.635) rot=(0,0,1;0rad)
  BaseFeature = -> Cylinder467
  Height = 0.265
  Length = 0.23
  MapMode = 5
  Placement = pos=(-20.1,18.635,1.635) rot=(0,0,1;0rad)
  Support = -> [XY_Plane267]
  Width = 0.23
FEATURE [PartDesign::Body] Body254  label="pin254"
  Group = -> [Box2339,Box2325,Box2395,Box2311,Box2322,Fillet751,Fillet766,Box2324,Cylinder468,Box2330,Box2332,Fillet748,Box2331,Cylinder467,Box2307]
  Origin = -> Origin264
  Placement = pos=(0,-5.5,0) rot=(0,0,1;0rad)
  Tip = -> Box2307
FEATURE [PartDesign::SubtractiveBox] Box2396
  AttacherType = Attacher::AttachEngine3D
  AttachmentOffset = pos=(-20.5,18.63,0) rot=(0,0,1;0rad)
  BaseFeature = -> Box2313
  Height = 1.635
  Length = 0.5
  MapMode = 5
  Placement = pos=(-20.5,18.63,0) rot=(0,0,1;0rad)
  Support = -> [XY_Plane271]
  Width = 0.25
FEATURE [PartDesign::SubtractiveBox] Box2327
  AttacherType = Attacher::AttachEngine3D
  AttachmentOffset = pos=(-21.19,18.635,-0.12) rot=(0,-1,0;0.15708rad)
  BaseFeature = -> Box2396
  Height = 0.12
  Length = 0.725
  MapMode = 5
  Placement = pos=(-21.19,18.635,-0.12) rot=(0,-1,0;0.15708rad)
  Support = -> [XY_Plane271]
  Width = 0.25
FEATURE [PartDesign::SubtractiveBox] Box2323
  AttacherType = Attacher::AttachEngine3D
  AttachmentOffset = pos=(-21.5005,18.625,0.235) rot=(0,-1,0;0.174533rad)
  BaseFeature = -> Box2327
  Height = 0.3
  Length = 0.6605
  MapMode = 5
  Placement = pos=(-21.5005,18.625,0.235) rot=(0,-1,0;0.174533rad)
  Support = -> [XY_Plane271]
  Width = 0.25
FEATURE [PartDesign::Fillet] Fillet757
  Base = -> Box2323 [Edge2]
  BaseFeature = -> Box2323
  Placement = pos=(-21.5005,18.625,0.235) rot=(0,-1,0;0.174533rad)
  Radius = 0.05
  SupportTransform = false
FEATURE [PartDesign::Fillet] Fillet763
  Base = -> Fillet757 [Edge33]
  BaseFeature = -> Fillet757
  Placement = pos=(-21.5005,18.625,0.235) rot=(0,-1,0;0.174533rad)
  Radius = 0.5
  SupportTransform = false
FEATURE [PartDesign::AdditiveBox] Box2314
  AttacherType = Attacher::AttachEngine3D
  AttachmentOffset = pos=(-21.1,18.635,0.305) rot=(0,1,0;0.785398rad)
  BaseFeature = -> Fillet763
  Height = 0.375
  Length = 0.2
  MapMode = 5
  Placement = pos=(-21.1,18.635,0.305) rot=(0,1,0;0.785398rad)
  Support = -> [XY_Plane271]
  Width = 0.23
FEATURE [PartDesign::SubtractiveCylinder] Cylinder463
  Angle = 360
  AttacherType = Attacher::AttachEngine3D
  AttachmentOffset = pos=(-21.055,18.935,0.52) rot=(1,0,0;1.5708rad)
  BaseFeature = -> Box2314
  Height = 0.375
  MapMode = 5
  Placement = pos=(-21.055,18.935,0.52) rot=(1,0,0;1.5708rad)
  Radius = 0.205
  Support = -> [XY_Plane271]
FEATURE [PartDesign::SubtractiveBox] Box2312
  AttacherType = Attacher::AttachEngine3D
  AttachmentOffset = pos=(-20.95,18.635,0.53) rot=(0,0,1;0rad)
  BaseFeature = -> Cylinder463
  Height = 0.5
  Length = 0.1
  MapMode = 5
  Placement = pos=(-20.95,18.635,0.53) rot=(0,0,1;0rad)
  Support = -> [XY_Plane271]
  Width = 0.23
FEATURE [PartDesign::SubtractiveBox] Box2320
  AttacherType = Attacher::AttachEngine3D
  AttachmentOffset = pos=(-21.15,18.635,0.297) rot=(0,-1,0;0.174533rad)
  BaseFeature = -> Box2312
  Height = 0.115
  Length = 0.115
  MapMode = 5
  Placement = pos=(-21.15,18.635,0.297) rot=(0,-1,0;0.174533rad)
  Support = -> [XY_Plane271]
  Width = 0.23
FEATURE [PartDesign::Fillet] Fillet765
  Base = -> Box2320 [Edge28]
  BaseFeature = -> Box2320
  Placement = pos=(-21.15,18.635,0.297) rot=(0,-1,0;0.174533rad)
  Radius = 0.375
  SupportTransform = false
FEATURE [PartDesign::AdditiveBox] Box2319
  AttacherType = Attacher::AttachEngine3D
  AttachmentOffset = pos=(-20.7,18.635,1.55) rot=(0,1,0;0.785398rad)
  BaseFeature = -> Fillet765
  Height = 0.375
  Length = 0.23
  MapMode = 5
  Placement = pos=(-20.7,18.635,1.55) rot=(0,1,0;0.785398rad)
  Support = -> [XY_Plane271]
  Width = 0.23
FEATURE [PartDesign::SubtractiveCylinder] Cylinder469
  Angle = 360
  AttacherType = Attacher::AttachEngine3D
  AttachmentOffset = pos=(-20.271,18.635,1.4056) rot=(-1,0,0;1.5708rad)
  BaseFeature = -> Box2319
  Height = 0.23
  MapMode = 5
  Placement = pos=(-20.271,18.635,1.4056) rot=(-1,0,0;1.5708rad)
  Radius = 0.23
  Support = -> [XY_Plane271]
FEATURE [PartDesign::AdditiveBox] Box2321
  AttacherType = Attacher::AttachEngine3D
  AttachmentOffset = pos=(-20.1,18.635,1.635) rot=(0,0,1;0rad)
  BaseFeature = -> Cylinder469
  Height = 0.265
  Length = 0.23
  MapMode = 5
  Placement = pos=(-20.1,18.635,1.635) rot=(0,0,1;0rad)
  Support = -> [XY_Plane271]
  Width = 0.23
FEATURE [PartDesign::Body] Body256  label="pin256"
  Group = -> [Box2318,Box2313,Box2396,Box2327,Box2323,Fillet757,Fillet763,Box2314,Cylinder463,Box2312,Box2320,Fillet765,Box2319,Cylinder469,Box2321]
  Origin = -> Origin265
  Placement = pos=(0,-5,0) rot=(0,0,1;0rad)
  Tip = -> Box2321
FEATURE [PartDesign::AdditiveBox] Box2397
  AttacherType = Attacher::AttachEngine3D
  AttachmentOffset = pos=(-21.3,18.635,0) rot=(0,0,1;0rad)
  Height = 1.9
  Length = 1.3
  MapMode = 5
  Placement = pos=(-21.3,18.635,0) rot=(0,0,1;0rad)
  Support = -> [XY_Plane252]
  Width = 0.23
FEATURE [PartDesign::SubtractiveBox] Box2304
  AttacherType = Attacher::AttachEngine3D
  AttachmentOffset = pos=(-21.35,18.635,0.35) rot=(0,0,1;0rad)
  BaseFeature = -> Box2397
  Height = 1.55
  Length = 0.5
  MapMode = 5
  Placement = pos=(-21.35,18.635,0.35) rot=(0,0,1;0rad)
  Support = -> [XY_Plane252]
  Width = 0.23
FEATURE [PartDesign::SubtractiveBox] Box2367
  AttacherType = Attacher::AttachEngine3D
  AttachmentOffset = pos=(-20.5,18.63,0) rot=(0,0,1;0rad)
  BaseFeature = -> Box2304
  Height = 1.635
  Length = 0.5
  MapMode = 5
  Placement = pos=(-20.5,18.63,0) rot=(0,0,1;0rad)
  Support = -> [XY_Plane252]
  Width = 0.25
FEATURE [PartDesign::SubtractiveBox] Box2371
  AttacherType = Attacher::AttachEngine3D
  AttachmentOffset = pos=(-21.19,18.635,-0.12) rot=(0,-1,0;0.15708rad)
  BaseFeature = -> Box2367
  Height = 0.12
  Length = 0.725
  MapMode = 5
  Placement = pos=(-21.19,18.635,-0.12) rot=(0,-1,0;0.15708rad)
  Support = -> [XY_Plane252]
  Width = 0.25
FEATURE [PartDesign::SubtractiveBox] Box2393
  AttacherType = Attacher::AttachEngine3D
  AttachmentOffset = pos=(-21.5005,18.625,0.235) rot=(0,-1,0;0.174533rad)
  BaseFeature = -> Box2371
  Height = 0.3
  Length = 0.6605
  MapMode = 5
  Placement = pos=(-21.5005,18.625,0.235) rot=(0,-1,0;0.174533rad)
  Support = -> [XY_Plane252]
  Width = 0.25
FEATURE [PartDesign::Fillet] Fillet732
  Base = -> Box2393 [Edge2]
  BaseFeature = -> Box2393
  Placement = pos=(-21.5005,18.625,0.235) rot=(0,-1,0;0.174533rad)
  Radius = 0.05
  SupportTransform = false
FEATURE [PartDesign::Fillet] Fillet745
  Base = -> Fillet732 [Edge33]
  BaseFeature = -> Fillet732
  Placement = pos=(-21.5005,18.625,0.235) rot=(0,-1,0;0.174533rad)
  Radius = 0.5
  SupportTransform = false
FEATURE [PartDesign::AdditiveBox] Box2383
  AttacherType = Attacher::AttachEngine3D
  AttachmentOffset = pos=(-21.1,18.635,0.305) rot=(0,1,0;0.785398rad)
  BaseFeature = -> Fillet745
  Height = 0.375
  Length = 0.2
  MapMode = 5
  Placement = pos=(-21.1,18.635,0.305) rot=(0,1,0;0.785398rad)
  Support = -> [XY_Plane252]
  Width = 0.23
FEATURE [PartDesign::SubtractiveCylinder] Cylinder481
  Angle = 360
  AttacherType = Attacher::AttachEngine3D
  AttachmentOffset = pos=(-21.055,18.935,0.52) rot=(1,0,0;1.5708rad)
  BaseFeature = -> Box2383
  Height = 0.375
  MapMode = 5
  Placement = pos=(-21.055,18.935,0.52) rot=(1,0,0;1.5708rad)
  Radius = 0.205
  Support = -> [XY_Plane252]
FEATURE [PartDesign::SubtractiveBox] Box2389
  AttacherType = Attacher::AttachEngine3D
  AttachmentOffset = pos=(-20.95,18.635,0.53) rot=(0,0,1;0rad)
  BaseFeature = -> Cylinder481
  Height = 0.5
  Length = 0.1
  MapMode = 5
  Placement = pos=(-20.95,18.635,0.53) rot=(0,0,1;0rad)
  Support = -> [XY_Plane252]
  Width = 0.23
FEATURE [PartDesign::SubtractiveBox] Box2380
  AttacherType = Attacher::AttachEngine3D
  AttachmentOffset = pos=(-21.15,18.635,0.297) rot=(0,-1,0;0.174533rad)
  BaseFeature = -> Box2389
  Height = 0.115
  Length = 0.115
  MapMode = 5
  Placement = pos=(-21.15,18.635,0.297) rot=(0,-1,0;0.174533rad)
  Support = -> [XY_Plane252]
  Width = 0.23
FEATURE [PartDesign::Fillet] Fillet739
  Base = -> Box2380 [Edge28]
  BaseFeature = -> Box2380
  Placement = pos=(-21.15,18.635,0.297) rot=(0,-1,0;0.174533rad)
  Radius = 0.375
  SupportTransform = false
FEATURE [PartDesign::AdditiveBox] Box2386
  AttacherType = Attacher::AttachEngine3D
  AttachmentOffset = pos=(-20.7,18.635,1.55) rot=(0,1,0;0.785398rad)
  BaseFeature = -> Fillet739
  Height = 0.375
  Length = 0.23
  MapMode = 5
  Placement = pos=(-20.7,18.635,1.55) rot=(0,1,0;0.785398rad)
  Support = -> [XY_Plane252]
  Width = 0.23
FEATURE [PartDesign::SubtractiveCylinder] Cylinder482
  Angle = 360
  AttacherType = Attacher::AttachEngine3D
  AttachmentOffset = pos=(-20.271,18.635,1.4056) rot=(-1,0,0;1.5708rad)
  BaseFeature = -> Box2386
  Height = 0.23
  MapMode = 5
  Placement = pos=(-20.271,18.635,1.4056) rot=(-1,0,0;1.5708rad)
  Radius = 0.23
  Support = -> [XY_Plane252]
FEATURE [PartDesign::AdditiveBox] Box2379
  AttacherType = Attacher::AttachEngine3D
  AttachmentOffset = pos=(-20.1,18.635,1.635) rot=(0,0,1;0rad)
  BaseFeature = -> Cylinder482
  Height = 0.265
  Length = 0.23
  MapMode = 5
  Placement = pos=(-20.1,18.635,1.635) rot=(0,0,1;0rad)
  Support = -> [XY_Plane252]
  Width = 0.23
FEATURE [PartDesign::Body] Body251  label="pin251"
  Group = -> [Box2397,Box2304,Box2367,Box2371,Box2393,Fillet732,Fillet745,Box2383,Cylinder481,Box2389,Box2380,Fillet739,Box2386,Cylinder482,Box2379]
  Origin = -> Origin258
  Placement = pos=(0,-2.5,0) rot=(0,0,1;0rad)
  Tip = -> Box2379
FEATURE [PartDesign::AdditiveBox] Box2404
  AttacherType = Attacher::AttachEngine3D
  AttachmentOffset = pos=(-21.3,18.635,0) rot=(0,0,1;0rad)
  Height = 1.9
  Length = 1.3
  MapMode = 5
  Placement = pos=(-21.3,18.635,0) rot=(0,0,1;0rad)
  Support = -> [XY_Plane272]
  Width = 0.23
FEATURE [PartDesign::SubtractiveBox] Box2405
  AttacherType = Attacher::AttachEngine3D
  AttachmentOffset = pos=(-21.35,18.635,0.35) rot=(0,0,1;0rad)
  BaseFeature = -> Box2404
  Height = 1.55
  Length = 0.5
  MapMode = 5
  Placement = pos=(-21.35,18.635,0.35) rot=(0,0,1;0rad)
  Support = -> [XY_Plane272]
  Width = 0.23
FEATURE [PartDesign::SubtractiveBox] Box2343
  AttacherType = Attacher::AttachEngine3D
  AttachmentOffset = pos=(-20.5,18.63,0) rot=(0,0,1;0rad)
  BaseFeature = -> Box2405
  Height = 1.635
  Length = 0.5
  MapMode = 5
  Placement = pos=(-20.5,18.63,0) rot=(0,0,1;0rad)
  Support = -> [XY_Plane272]
  Width = 0.25
FEATURE [PartDesign::SubtractiveBox] Box2409
  AttacherType = Attacher::AttachEngine3D
  AttachmentOffset = pos=(-21.19,18.635,-0.12) rot=(0,-1,0;0.15708rad)
  BaseFeature = -> Box2343
  Height = 0.12
  Length = 0.725
  MapMode = 5
  Placement = pos=(-21.19,18.635,-0.12) rot=(0,-1,0;0.15708rad)
  Support = -> [XY_Plane272]
  Width = 0.25
FEATURE [PartDesign::SubtractiveBox] Box2402
  AttacherType = Attacher::AttachEngine3D
  AttachmentOffset = pos=(-21.5005,18.625,0.235) rot=(0,-1,0;0.174533rad)
  BaseFeature = -> Box2409
  Height = 0.3
  Length = 0.6605
  MapMode = 5
  Placement = pos=(-21.5005,18.625,0.235) rot=(0,-1,0;0.174533rad)
  Support = -> [XY_Plane272]
  Width = 0.25
FEATURE [PartDesign::Fillet] Fillet741
  Base = -> Box2402 [Edge2]
  BaseFeature = -> Box2402
  Placement = pos=(-21.5005,18.625,0.235) rot=(0,-1,0;0.174533rad)
  Radius = 0.05
  SupportTransform = false
FEATURE [PartDesign::Fillet] Fillet743
  Base = -> Fillet741 [Edge33]
  BaseFeature = -> Fillet741
  Placement = pos=(-21.5005,18.625,0.235) rot=(0,-1,0;0.174533rad)
  Radius = 0.5
  SupportTransform = false
FEATURE [PartDesign::AdditiveBox] Box2398
  AttacherType = Attacher::AttachEngine3D
  AttachmentOffset = pos=(-21.1,18.635,0.305) rot=(0,1,0;0.785398rad)
  BaseFeature = -> Fillet743
  Height = 0.375
  Length = 0.2
  MapMode = 5
  Placement = pos=(-21.1,18.635,0.305) rot=(0,1,0;0.785398rad)
  Support = -> [XY_Plane272]
  Width = 0.23
FEATURE [PartDesign::SubtractiveCylinder] Cylinder483
  Angle = 360
  AttacherType = Attacher::AttachEngine3D
  AttachmentOffset = pos=(-21.055,18.935,0.52) rot=(1,0,0;1.5708rad)
  BaseFeature = -> Box2398
  Height = 0.375
  MapMode = 5
  Placement = pos=(-21.055,18.935,0.52) rot=(1,0,0;1.5708rad)
  Radius = 0.205
  Support = -> [XY_Plane272]
FEATURE [PartDesign::SubtractiveBox] Box2401
  AttacherType = Attacher::AttachEngine3D
  AttachmentOffset = pos=(-20.95,18.635,0.53) rot=(0,0,1;0rad)
  BaseFeature = -> Cylinder483
  Height = 0.5
  Length = 0.1
  MapMode = 5
  Placement = pos=(-20.95,18.635,0.53) rot=(0,0,1;0rad)
  Support = -> [XY_Plane272]
  Width = 0.23
FEATURE [PartDesign::SubtractiveBox] Box2407
  AttacherType = Attacher::AttachEngine3D
  AttachmentOffset = pos=(-21.15,18.635,0.297) rot=(0,-1,0;0.174533rad)
  BaseFeature = -> Box2401
  Height = 0.115
  Length = 0.115
  MapMode = 5
  Placement = pos=(-21.15,18.635,0.297) rot=(0,-1,0;0.174533rad)
  Support = -> [XY_Plane272]
  Width = 0.23
FEATURE [PartDesign::Fillet] Fillet740
  Base = -> Box2407 [Edge28]
  BaseFeature = -> Box2407
  Placement = pos=(-21.15,18.635,0.297) rot=(0,-1,0;0.174533rad)
  Radius = 0.375
  SupportTransform = false
FEATURE [PartDesign::AdditiveBox] Box2348
  AttacherType = Attacher::AttachEngine3D
  AttachmentOffset = pos=(-20.7,18.635,1.55) rot=(0,1,0;0.785398rad)
  BaseFeature = -> Fillet740
  Height = 0.375
  Length = 0.23
  MapMode = 5
  Placement = pos=(-20.7,18.635,1.55) rot=(0,1,0;0.785398rad)
  Support = -> [XY_Plane272]
  Width = 0.23
FEATURE [PartDesign::SubtractiveCylinder] Cylinder484
  Angle = 360
  AttacherType = Attacher::AttachEngine3D
  AttachmentOffset = pos=(-20.271,18.635,1.4056) rot=(-1,0,0;1.5708rad)
  BaseFeature = -> Box2348
  Height = 0.23
  MapMode = 5
  Placement = pos=(-20.271,18.635,1.4056) rot=(-1,0,0;1.5708rad)
  Radius = 0.23
  Support = -> [XY_Plane272]
FEATURE [PartDesign::AdditiveBox] Box2400
  AttacherType = Attacher::AttachEngine3D
  AttachmentOffset = pos=(-20.1,18.635,1.635) rot=(0,0,1;0rad)
  BaseFeature = -> Cylinder484
  Height = 0.265
  Length = 0.23
  MapMode = 5
  Placement = pos=(-20.1,18.635,1.635) rot=(0,0,1;0rad)
  Support = -> [XY_Plane272]
  Width = 0.23
FEATURE [PartDesign::Body] Body248  label="pin248"
  Group = -> [Box2404,Box2405,Box2343,Box2409,Box2402,Fillet741,Fillet743,Box2398,Cylinder483,Box2401,Box2407,Fillet740,Box2348,Cylinder484,Box2400]
  Origin = -> Origin252
  Placement = pos=(0,-0.5,0) rot=(0,0,1;0rad)
  Tip = -> Box2400
FEATURE [PartDesign::AdditiveBox] Box2415
  AttacherType = Attacher::AttachEngine3D
  AttachmentOffset = pos=(-21.3,18.635,0) rot=(0,0,1;0rad)
  Height = 1.9
  Length = 1.3
  MapMode = 5
  Placement = pos=(-21.3,18.635,0) rot=(0,0,1;0rad)
  Support = -> [XY_Plane251]
  Width = 0.23
FEATURE [PartDesign::SubtractiveBox] Box2417
  AttacherType = Attacher::AttachEngine3D
  AttachmentOffset = pos=(-21.35,18.635,0.35) rot=(0,0,1;0rad)
  BaseFeature = -> Box2415
  Height = 1.55
  Length = 0.5
  MapMode = 5
  Placement = pos=(-21.35,18.635,0.35) rot=(0,0,1;0rad)
  Support = -> [XY_Plane251]
  Width = 0.23
FEATURE [PartDesign::SubtractiveBox] Box2353
  AttacherType = Attacher::AttachEngine3D
  AttachmentOffset = pos=(-20.5,18.63,0) rot=(0,0,1;0rad)
  BaseFeature = -> Box2417
  Height = 1.635
  Length = 0.5
  MapMode = 5
  Placement = pos=(-20.5,18.63,0) rot=(0,0,1;0rad)
  Support = -> [XY_Plane251]
  Width = 0.25
FEATURE [PartDesign::AdditiveBox] Box2420
  AttacherType = Attacher::AttachEngine3D
  AttachmentOffset = pos=(-21.3,18.635,0) rot=(0,0,1;0rad)
  Height = 1.9
  Length = 1.3
  MapMode = 5
  Placement = pos=(-21.3,18.635,0) rot=(0,0,1;0rad)
  Support = -> [XY_Plane253]
  Width = 0.23
FEATURE [PartDesign::SubtractiveBox] Box2421
  AttacherType = Attacher::AttachEngine3D
  AttachmentOffset = pos=(-21.19,18.635,-0.12) rot=(0,-1,0;0.15708rad)
  BaseFeature = -> Box2353
  Height = 0.12
  Length = 0.725
  MapMode = 5
  Placement = pos=(-21.19,18.635,-0.12) rot=(0,-1,0;0.15708rad)
  Support = -> [XY_Plane251]
  Width = 0.25
FEATURE [PartDesign::SubtractiveBox] Box2414
  AttacherType = Attacher::AttachEngine3D
  AttachmentOffset = pos=(-21.5005,18.625,0.235) rot=(0,-1,0;0.174533rad)
  BaseFeature = -> Box2421
  Height = 0.3
  Length = 0.6605
  MapMode = 5
  Placement = pos=(-21.5005,18.625,0.235) rot=(0,-1,0;0.174533rad)
  Support = -> [XY_Plane251]
  Width = 0.25
FEATURE [PartDesign::Fillet] Fillet738
  Base = -> Box2414 [Edge2]
  BaseFeature = -> Box2414
  Placement = pos=(-21.5005,18.625,0.235) rot=(0,-1,0;0.174533rad)
  Radius = 0.05
  SupportTransform = false
FEATURE [PartDesign::Fillet] Fillet746
  Base = -> Fillet738 [Edge33]
  BaseFeature = -> Fillet738
  Placement = pos=(-21.5005,18.625,0.235) rot=(0,-1,0;0.174533rad)
  Radius = 0.5
  SupportTransform = false
FEATURE [PartDesign::AdditiveBox] Box2403
  AttacherType = Attacher::AttachEngine3D
  AttachmentOffset = pos=(-21.1,18.635,0.305) rot=(0,1,0;0.785398rad)
  BaseFeature = -> Fillet746
  Height = 0.375
  Length = 0.2
  MapMode = 5
  Placement = pos=(-21.1,18.635,0.305) rot=(0,1,0;0.785398rad)
  Support = -> [XY_Plane251]
  Width = 0.23
FEATURE [PartDesign::SubtractiveCylinder] Cylinder486
  Angle = 360
  AttacherType = Attacher::AttachEngine3D
  AttachmentOffset = pos=(-21.055,18.935,0.52) rot=(1,0,0;1.5708rad)
  BaseFeature = -> Box2403
  Height = 0.375
  MapMode = 5
  Placement = pos=(-21.055,18.935,0.52) rot=(1,0,0;1.5708rad)
  Radius = 0.205
  Support = -> [XY_Plane251]
FEATURE [PartDesign::SubtractiveBox] Box2416
  AttacherType = Attacher::AttachEngine3D
  AttachmentOffset = pos=(-20.95,18.635,0.53) rot=(0,0,1;0rad)
  BaseFeature = -> Cylinder486
  Height = 0.5
  Length = 0.1
  MapMode = 5
  Placement = pos=(-20.95,18.635,0.53) rot=(0,0,1;0rad)
  Support = -> [XY_Plane251]
  Width = 0.23
FEATURE [PartDesign::SubtractiveBox] Box2399
  AttacherType = Attacher::AttachEngine3D
  AttachmentOffset = pos=(-21.15,18.635,0.297) rot=(0,-1,0;0.174533rad)
  BaseFeature = -> Box2416
  Height = 0.115
  Length = 0.115
  MapMode = 5
  Placement = pos=(-21.15,18.635,0.297) rot=(0,-1,0;0.174533rad)
  Support = -> [XY_Plane251]
  Width = 0.23
FEATURE [PartDesign::Fillet] Fillet734
  Base = -> Box2399 [Edge28]
  BaseFeature = -> Box2399
  Placement = pos=(-21.15,18.635,0.297) rot=(0,-1,0;0.174533rad)
  Radius = 0.375
  SupportTransform = false
FEATURE [PartDesign::AdditiveBox] Box2406
  AttacherType = Attacher::AttachEngine3D
  AttachmentOffset = pos=(-20.7,18.635,1.55) rot=(0,1,0;0.785398rad)
  BaseFeature = -> Fillet734
  Height = 0.375
  Length = 0.23
  MapMode = 5
  Placement = pos=(-20.7,18.635,1.55) rot=(0,1,0;0.785398rad)
  Support = -> [XY_Plane251]
  Width = 0.23
FEATURE [PartDesign::SubtractiveCylinder] Cylinder485
  Angle = 360
  AttacherType = Attacher::AttachEngine3D
  AttachmentOffset = pos=(-20.271,18.635,1.4056) rot=(-1,0,0;1.5708rad)
  BaseFeature = -> Box2406
  Height = 0.23
  MapMode = 5
  Placement = pos=(-20.271,18.635,1.4056) rot=(-1,0,0;1.5708rad)
  Radius = 0.23
  Support = -> [XY_Plane251]
FEATURE [PartDesign::AdditiveBox] Box2419
  AttacherType = Attacher::AttachEngine3D
  AttachmentOffset = pos=(-20.1,18.635,1.635) rot=(0,0,1;0rad)
  BaseFeature = -> Cylinder485
  Height = 0.265
  Length = 0.23
  MapMode = 5
  Placement = pos=(-20.1,18.635,1.635) rot=(0,0,1;0rad)
  Support = -> [XY_Plane251]
  Width = 0.23
FEATURE [PartDesign::Body] Body249  label="pin249"
  Group = -> [Box2415,Box2417,Box2353,Box2421,Box2414,Fillet738,Fillet746,Box2403,Cylinder486,Box2416,Box2399,Fillet734,Box2406,Cylinder485,Box2419]
  Origin = -> Origin250
  Placement = pos=(0,-1,0) rot=(0,0,1;0rad)
  Tip = -> Box2419
FEATURE [PartDesign::AdditiveBox] Box2428
  AttacherType = Attacher::AttachEngine3D
  AttachmentOffset = pos=(-21.3,18.635,0) rot=(0,0,1;0rad)
  Height = 1.9
  Length = 1.3
  MapMode = 5
  Placement = pos=(-21.3,18.635,0) rot=(0,0,1;0rad)
  Support = -> [XY_Plane278]
  Width = 0.23
FEATURE [PartDesign::SubtractiveBox] Box2422
  AttacherType = Attacher::AttachEngine3D
  AttachmentOffset = pos=(-21.35,18.635,0.35) rot=(0,0,1;0rad)
  BaseFeature = -> Box2428
  Height = 1.55
  Length = 0.5
  MapMode = 5
  Placement = pos=(-21.35,18.635,0.35) rot=(0,0,1;0rad)
  Support = -> [XY_Plane278]
  Width = 0.23
FEATURE [PartDesign::AdditiveBox] Box2440
  AttacherType = Attacher::AttachEngine3D
  AttachmentOffset = pos=(-21.3,18.635,0) rot=(0,0,1;0rad)
  Height = 1.9
  Length = 1.3
  MapMode = 5
  Placement = pos=(-21.3,18.635,0) rot=(0,0,1;0rad)
  Support = -> [XY_Plane274]
  Width = 0.23
FEATURE [PartDesign::SubtractiveBox] Box2435
  AttacherType = Attacher::AttachEngine3D
  AttachmentOffset = pos=(-21.35,18.635,0.35) rot=(0,0,1;0rad)
  BaseFeature = -> Box2440
  Height = 1.55
  Length = 0.5
  MapMode = 5
  Placement = pos=(-21.35,18.635,0.35) rot=(0,0,1;0rad)
  Support = -> [XY_Plane274]
  Width = 0.23
FEATURE [PartDesign::AdditiveBox] Box2444
  AttacherType = Attacher::AttachEngine3D
  AttachmentOffset = pos=(-21.3,18.635,0) rot=(0,0,1;0rad)
  Height = 1.9
  Length = 1.3
  MapMode = 5
  Placement = pos=(-21.3,18.635,0) rot=(0,0,1;0rad)
  Support = -> [XY_Plane280]
  Width = 0.23
FEATURE [PartDesign::SubtractiveBox] Box2429
  AttacherType = Attacher::AttachEngine3D
  AttachmentOffset = pos=(-21.35,18.635,0.35) rot=(0,0,1;0rad)
  BaseFeature = -> Box2444
  Height = 1.55
  Length = 0.5
  MapMode = 5
  Placement = pos=(-21.35,18.635,0.35) rot=(0,0,1;0rad)
  Support = -> [XY_Plane280]
  Width = 0.23
FEATURE [PartDesign::SubtractiveBox] Box2459
  AttacherType = Attacher::AttachEngine3D
  AttachmentOffset = pos=(-20.5,18.63,0) rot=(0,0,1;0rad)
  BaseFeature = -> Box2362
  Height = 1.635
  Length = 0.5
  MapMode = 5
  Placement = pos=(-20.5,18.63,0) rot=(0,0,1;0rad)
  Support = -> [XY_Plane279]
  Width = 0.25
FEATURE [PartDesign::SubtractiveBox] Box2302
  AttacherType = Attacher::AttachEngine3D
  AttachmentOffset = pos=(-21.19,18.635,-0.12) rot=(0,-1,0;0.15708rad)
  BaseFeature = -> Box2459
  Height = 0.12
  Length = 0.725
  MapMode = 5
  Placement = pos=(-21.19,18.635,-0.12) rot=(0,-1,0;0.15708rad)
  Support = -> [XY_Plane279]
  Width = 0.25
FEATURE [PartDesign::SubtractiveBox] Box2298
  AttacherType = Attacher::AttachEngine3D
  AttachmentOffset = pos=(-21.5005,18.625,0.235) rot=(0,-1,0;0.174533rad)
  BaseFeature = -> Box2302
  Height = 0.3
  Length = 0.6605
  MapMode = 5
  Placement = pos=(-21.5005,18.625,0.235) rot=(0,-1,0;0.174533rad)
  Support = -> [XY_Plane279]
  Width = 0.25
FEATURE [PartDesign::Fillet] Fillet699
  Base = -> Box2298 [Edge2]
  BaseFeature = -> Box2298
  Placement = pos=(-21.5005,18.625,0.235) rot=(0,-1,0;0.174533rad)
  Radius = 0.05
  SupportTransform = false
FEATURE [PartDesign::Fillet] Fillet706
  Base = -> Fillet699 [Edge33]
  BaseFeature = -> Fillet699
  Placement = pos=(-21.5005,18.625,0.235) rot=(0,-1,0;0.174533rad)
  Radius = 0.5
  SupportTransform = false
FEATURE [PartDesign::AdditiveBox] Box2461
  AttacherType = Attacher::AttachEngine3D
  AttachmentOffset = pos=(-21.3,18.635,0) rot=(0,0,1;0rad)
  Height = 1.9
  Length = 1.3
  MapMode = 5
  Placement = pos=(-21.3,18.635,0) rot=(0,0,1;0rad)
  Support = -> [XY_Plane284]
  Width = 0.23
FEATURE [PartDesign::SubtractiveBox] Box2450
  AttacherType = Attacher::AttachEngine3D
  AttachmentOffset = pos=(-21.35,18.635,0.35) rot=(0,0,1;0rad)
  BaseFeature = -> Box2461
  Height = 1.55
  Length = 0.5
  MapMode = 5
  Placement = pos=(-21.35,18.635,0.35) rot=(0,0,1;0rad)
  Support = -> [XY_Plane284]
  Width = 0.23
FEATURE [PartDesign::SubtractiveBox] Box2447
  AttacherType = Attacher::AttachEngine3D
  AttachmentOffset = pos=(-20.5,18.63,0) rot=(0,0,1;0rad)
  BaseFeature = -> Box2450
  Height = 1.635
  Length = 0.5
  MapMode = 5
  Placement = pos=(-20.5,18.63,0) rot=(0,0,1;0rad)
  Support = -> [XY_Plane284]
  Width = 0.25
FEATURE [PartDesign::SubtractiveBox] Box2452
  AttacherType = Attacher::AttachEngine3D
  AttachmentOffset = pos=(-21.19,18.635,-0.12) rot=(0,-1,0;0.15708rad)
  BaseFeature = -> Box2447
  Height = 0.12
  Length = 0.725
  MapMode = 5
  Placement = pos=(-21.19,18.635,-0.12) rot=(0,-1,0;0.15708rad)
  Support = -> [XY_Plane284]
  Width = 0.25
FEATURE [PartDesign::SubtractiveBox] Box2463
  AttacherType = Attacher::AttachEngine3D
  AttachmentOffset = pos=(-21.5005,18.625,0.235) rot=(0,-1,0;0.174533rad)
  BaseFeature = -> Box2452
  Height = 0.3
  Length = 0.6605
  MapMode = 5
  Placement = pos=(-21.5005,18.625,0.235) rot=(0,-1,0;0.174533rad)
  Support = -> [XY_Plane284]
  Width = 0.25
FEATURE [PartDesign::Fillet] Fillet697
  Base = -> Box2463 [Edge2]
  BaseFeature = -> Box2463
  Placement = pos=(-21.5005,18.625,0.235) rot=(0,-1,0;0.174533rad)
  Radius = 0.05
  SupportTransform = false
FEATURE [PartDesign::Fillet] Fillet684
  Base = -> Fillet697 [Edge33]
  BaseFeature = -> Fillet697
  Placement = pos=(-21.5005,18.625,0.235) rot=(0,-1,0;0.174533rad)
  Radius = 0.5
  SupportTransform = false
FEATURE [PartDesign::AdditiveBox] Box2437
  AttacherType = Attacher::AttachEngine3D
  AttachmentOffset = pos=(-21.1,18.635,0.305) rot=(0,1,0;0.785398rad)
  BaseFeature = -> Fillet684
  Height = 0.375
  Length = 0.2
  MapMode = 5
  Placement = pos=(-21.1,18.635,0.305) rot=(0,1,0;0.785398rad)
  Support = -> [XY_Plane284]
  Width = 0.23
FEATURE [PartDesign::SubtractiveCylinder] Cylinder492
  Angle = 360
  AttacherType = Attacher::AttachEngine3D
  AttachmentOffset = pos=(-21.055,18.935,0.52) rot=(1,0,0;1.5708rad)
  BaseFeature = -> Box2437
  Height = 0.375
  MapMode = 5
  Placement = pos=(-21.055,18.935,0.52) rot=(1,0,0;1.5708rad)
  Radius = 0.205
  Support = -> [XY_Plane284]
FEATURE [PartDesign::SubtractiveBox] Box2454
  AttacherType = Attacher::AttachEngine3D
  AttachmentOffset = pos=(-20.95,18.635,0.53) rot=(0,0,1;0rad)
  BaseFeature = -> Cylinder492
  Height = 0.5
  Length = 0.1
  MapMode = 5
  Placement = pos=(-20.95,18.635,0.53) rot=(0,0,1;0rad)
  Support = -> [XY_Plane284]
  Width = 0.23
FEATURE [PartDesign::SubtractiveBox] Box2443
  AttacherType = Attacher::AttachEngine3D
  AttachmentOffset = pos=(-21.15,18.635,0.297) rot=(0,-1,0;0.174533rad)
  BaseFeature = -> Box2454
  Height = 0.115
  Length = 0.115
  MapMode = 5
  Placement = pos=(-21.15,18.635,0.297) rot=(0,-1,0;0.174533rad)
  Support = -> [XY_Plane284]
  Width = 0.23
FEATURE [PartDesign::Fillet] Fillet696
  Base = -> Box2443 [Edge28]
  BaseFeature = -> Box2443
  Placement = pos=(-21.15,18.635,0.297) rot=(0,-1,0;0.174533rad)
  Radius = 0.375
  SupportTransform = false
FEATURE [PartDesign::AdditiveBox] Box2451
  AttacherType = Attacher::AttachEngine3D
  AttachmentOffset = pos=(-20.7,18.635,1.55) rot=(0,1,0;0.785398rad)
  BaseFeature = -> Fillet696
  Height = 0.375
  Length = 0.23
  MapMode = 5
  Placement = pos=(-20.7,18.635,1.55) rot=(0,1,0;0.785398rad)
  Support = -> [XY_Plane284]
  Width = 0.23
FEATURE [PartDesign::SubtractiveCylinder] Cylinder496
  Angle = 360
  AttacherType = Attacher::AttachEngine3D
  AttachmentOffset = pos=(-20.271,18.635,1.4056) rot=(-1,0,0;1.5708rad)
  BaseFeature = -> Box2451
  Height = 0.23
  MapMode = 5
  Placement = pos=(-20.271,18.635,1.4056) rot=(-1,0,0;1.5708rad)
  Radius = 0.23
  Support = -> [XY_Plane284]
FEATURE [PartDesign::AdditiveBox] Box2453
  AttacherType = Attacher::AttachEngine3D
  AttachmentOffset = pos=(-20.1,18.635,1.635) rot=(0,0,1;0rad)
  BaseFeature = -> Cylinder496
  Height = 0.265
  Length = 0.23
  MapMode = 5
  Placement = pos=(-20.1,18.635,1.635) rot=(0,0,1;0rad)
  Support = -> [XY_Plane284]
  Width = 0.23
FEATURE [PartDesign::Body] Body236  label="pin236"
  Group = -> [Box2461,Box2450,Box2447,Box2452,Box2463,Fillet697,Fillet684,Box2437,Cylinder492,Box2454,Box2443,Fillet696,Box2451,Cylinder496,Box2453]
  Origin = -> Origin284
  Placement = pos=(0,-5,0) rot=(0,0,1;0rad)
  Tip = -> Box2453
FEATURE [PartDesign::AdditiveBox] Box2468
  AttacherType = Attacher::AttachEngine3D
  AttachmentOffset = pos=(-21.3,18.635,0) rot=(0,0,1;0rad)
  Height = 1.9
  Length = 1.3
  MapMode = 5
  Placement = pos=(-21.3,18.635,0) rot=(0,0,1;0rad)
  Support = -> [XY_Plane286]
  Width = 0.23
FEATURE [PartDesign::SubtractiveBox] Box2455
  AttacherType = Attacher::AttachEngine3D
  AttachmentOffset = pos=(-21.35,18.635,0.35) rot=(0,0,1;0rad)
  BaseFeature = -> Box2468
  Height = 1.55
  Length = 0.5
  MapMode = 5
  Placement = pos=(-21.35,18.635,0.35) rot=(0,0,1;0rad)
  Support = -> [XY_Plane286]
  Width = 0.23
FEATURE [PartDesign::SubtractiveBox] Box2442
  AttacherType = Attacher::AttachEngine3D
  AttachmentOffset = pos=(-20.5,18.63,0) rot=(0,0,1;0rad)
  BaseFeature = -> Box2455
  Height = 1.635
  Length = 0.5
  MapMode = 5
  Placement = pos=(-20.5,18.63,0) rot=(0,0,1;0rad)
  Support = -> [XY_Plane286]
  Width = 0.25
FEATURE [PartDesign::SubtractiveBox] Box2424
  AttacherType = Attacher::AttachEngine3D
  AttachmentOffset = pos=(-21.19,18.635,-0.12) rot=(0,-1,0;0.15708rad)
  BaseFeature = -> Box2442
  Height = 0.12
  Length = 0.725
  MapMode = 5
  Placement = pos=(-21.19,18.635,-0.12) rot=(0,-1,0;0.15708rad)
  Support = -> [XY_Plane286]
  Width = 0.25
FEATURE [PartDesign::AdditiveBox] Box2472
  AttacherType = Attacher::AttachEngine3D
  AttachmentOffset = pos=(-21.3,18.635,0) rot=(0,0,1;0rad)
  Height = 1.9
  Length = 1.3
  MapMode = 5
  Placement = pos=(-21.3,18.635,0) rot=(0,0,1;0rad)
  Support = -> [XY_Plane266]
  Width = 0.23
FEATURE [PartDesign::SubtractiveBox] Box2467
  AttacherType = Attacher::AttachEngine3D
  AttachmentOffset = pos=(-21.35,18.635,0.35) rot=(0,0,1;0rad)
  BaseFeature = -> Box2472
  Height = 1.55
  Length = 0.5
  MapMode = 5
  Placement = pos=(-21.35,18.635,0.35) rot=(0,0,1;0rad)
  Support = -> [XY_Plane266]
  Width = 0.23
FEATURE [PartDesign::SubtractiveBox] Box2439
  AttacherType = Attacher::AttachEngine3D
  AttachmentOffset = pos=(-20.5,18.63,0) rot=(0,0,1;0rad)
  BaseFeature = -> Box2467
  Height = 1.635
  Length = 0.5
  MapMode = 5
  Placement = pos=(-20.5,18.63,0) rot=(0,0,1;0rad)
  Support = -> [XY_Plane266]
  Width = 0.25
FEATURE [PartDesign::SubtractiveBox] Box2445
  AttacherType = Attacher::AttachEngine3D
  AttachmentOffset = pos=(-21.19,18.635,-0.12) rot=(0,-1,0;0.15708rad)
  BaseFeature = -> Box2439
  Height = 0.12
  Length = 0.725
  MapMode = 5
  Placement = pos=(-21.19,18.635,-0.12) rot=(0,-1,0;0.15708rad)
  Support = -> [XY_Plane266]
  Width = 0.25
FEATURE [PartDesign::SubtractiveBox] Box2446
  AttacherType = Attacher::AttachEngine3D
  AttachmentOffset = pos=(-21.5005,18.625,0.235) rot=(0,-1,0;0.174533rad)
  BaseFeature = -> Box2445
  Height = 0.3
  Length = 0.6605
  MapMode = 5
  Placement = pos=(-21.5005,18.625,0.235) rot=(0,-1,0;0.174533rad)
  Support = -> [XY_Plane266]
  Width = 0.25
FEATURE [PartDesign::Fillet] Fillet708
  Base = -> Box2446 [Edge2]
  BaseFeature = -> Box2446
  Placement = pos=(-21.5005,18.625,0.235) rot=(0,-1,0;0.174533rad)
  Radius = 0.05
  SupportTransform = false
FEATURE [PartDesign::Fillet] Fillet701
  Base = -> Fillet708 [Edge33]
  BaseFeature = -> Fillet708
  Placement = pos=(-21.5005,18.625,0.235) rot=(0,-1,0;0.174533rad)
  Radius = 0.5
  SupportTransform = false
FEATURE [PartDesign::AdditiveBox] Box2456
  AttacherType = Attacher::AttachEngine3D
  AttachmentOffset = pos=(-21.1,18.635,0.305) rot=(0,1,0;0.785398rad)
  BaseFeature = -> Fillet701
  Height = 0.375
  Length = 0.2
  MapMode = 5
  Placement = pos=(-21.1,18.635,0.305) rot=(0,1,0;0.785398rad)
  Support = -> [XY_Plane266]
  Width = 0.23
FEATURE [PartDesign::SubtractiveCylinder] Cylinder493
  Angle = 360
  AttacherType = Attacher::AttachEngine3D
  AttachmentOffset = pos=(-21.055,18.935,0.52) rot=(1,0,0;1.5708rad)
  BaseFeature = -> Box2456
  Height = 0.375
  MapMode = 5
  Placement = pos=(-21.055,18.935,0.52) rot=(1,0,0;1.5708rad)
  Radius = 0.205
  Support = -> [XY_Plane266]
FEATURE [PartDesign::SubtractiveBox] Box2464
  AttacherType = Attacher::AttachEngine3D
  AttachmentOffset = pos=(-20.95,18.635,0.53) rot=(0,0,1;0rad)
  BaseFeature = -> Cylinder493
  Height = 0.5
  Length = 0.1
  MapMode = 5
  Placement = pos=(-20.95,18.635,0.53) rot=(0,0,1;0rad)
  Support = -> [XY_Plane266]
  Width = 0.23
FEATURE [PartDesign::SubtractiveBox] Box2466
  AttacherType = Attacher::AttachEngine3D
  AttachmentOffset = pos=(-21.15,18.635,0.297) rot=(0,-1,0;0.174533rad)
  BaseFeature = -> Box2464
  Height = 0.115
  Length = 0.115
  MapMode = 5
  Placement = pos=(-21.15,18.635,0.297) rot=(0,-1,0;0.174533rad)
  Support = -> [XY_Plane266]
  Width = 0.23
FEATURE [PartDesign::Fillet] Fillet771
  Base = -> Box2466 [Edge28]
  BaseFeature = -> Box2466
  Placement = pos=(-21.15,18.635,0.297) rot=(0,-1,0;0.174533rad)
  Radius = 0.375
  SupportTransform = false
FEATURE [PartDesign::AdditiveBox] Box2457
  AttacherType = Attacher::AttachEngine3D
  AttachmentOffset = pos=(-20.7,18.635,1.55) rot=(0,1,0;0.785398rad)
  BaseFeature = -> Fillet771
  Height = 0.375
  Length = 0.23
  MapMode = 5
  Placement = pos=(-20.7,18.635,1.55) rot=(0,1,0;0.785398rad)
  Support = -> [XY_Plane266]
  Width = 0.23
FEATURE [PartDesign::SubtractiveCylinder] Cylinder495
  Angle = 360
  AttacherType = Attacher::AttachEngine3D
  AttachmentOffset = pos=(-20.271,18.635,1.4056) rot=(-1,0,0;1.5708rad)
  BaseFeature = -> Box2457
  Height = 0.23
  MapMode = 5
  Placement = pos=(-20.271,18.635,1.4056) rot=(-1,0,0;1.5708rad)
  Radius = 0.23
  Support = -> [XY_Plane266]
FEATURE [PartDesign::AdditiveBox] Box2462
  AttacherType = Attacher::AttachEngine3D
  AttachmentOffset = pos=(-20.1,18.635,1.635) rot=(0,0,1;0rad)
  BaseFeature = -> Cylinder495
  Height = 0.265
  Length = 0.23
  MapMode = 5
  Placement = pos=(-20.1,18.635,1.635) rot=(0,0,1;0rad)
  Support = -> [XY_Plane266]
  Width = 0.23
FEATURE [PartDesign::Body] Body238  label="pin238"
  Group = -> [Box2472,Box2467,Box2439,Box2445,Box2446,Fillet708,Fillet701,Box2456,Cylinder493,Box2464,Box2466,Fillet771,Box2457,Cylinder495,Box2462]
  Origin = -> Origin272
  Placement = pos=(0,-5.5,0) rot=(0,0,1;0rad)
  Tip = -> Box2462
FEATURE [PartDesign::AdditiveBox] Box2473
  AttacherType = Attacher::AttachEngine3D
  AttachmentOffset = pos=(-21.1,18.635,0.305) rot=(0,1,0;0.785398rad)
  BaseFeature = -> Fillet706
  Height = 0.375
  Length = 0.2
  MapMode = 5
  Placement = pos=(-21.1,18.635,0.305) rot=(0,1,0;0.785398rad)
  Support = -> [XY_Plane279]
  Width = 0.23
FEATURE [PartDesign::SubtractiveCylinder] Cylinder462
  Angle = 360
  AttacherType = Attacher::AttachEngine3D
  AttachmentOffset = pos=(-21.055,18.935,0.52) rot=(1,0,0;1.5708rad)
  BaseFeature = -> Box2473
  Height = 0.375
  MapMode = 5
  Placement = pos=(-21.055,18.935,0.52) rot=(1,0,0;1.5708rad)
  Radius = 0.205
  Support = -> [XY_Plane279]
FEATURE [PartDesign::SubtractiveBox] Box2363
  AttacherType = Attacher::AttachEngine3D
  AttachmentOffset = pos=(-20.95,18.635,0.53) rot=(0,0,1;0rad)
  BaseFeature = -> Cylinder462
  Height = 0.5
  Length = 0.1
  MapMode = 5
  Placement = pos=(-20.95,18.635,0.53) rot=(0,0,1;0rad)
  Support = -> [XY_Plane279]
  Width = 0.23
FEATURE [PartDesign::SubtractiveBox] Box2366
  AttacherType = Attacher::AttachEngine3D
  AttachmentOffset = pos=(-21.15,18.635,0.297) rot=(0,-1,0;0.174533rad)
  BaseFeature = -> Box2363
  Height = 0.115
  Length = 0.115
  MapMode = 5
  Placement = pos=(-21.15,18.635,0.297) rot=(0,-1,0;0.174533rad)
  Support = -> [XY_Plane279]
  Width = 0.23
FEATURE [PartDesign::Fillet] Fillet707
  Base = -> Box2366 [Edge28]
  BaseFeature = -> Box2366
  Placement = pos=(-21.15,18.635,0.297) rot=(0,-1,0;0.174533rad)
  Radius = 0.375
  SupportTransform = false
FEATURE [PartDesign::AdditiveBox] Box2360
  AttacherType = Attacher::AttachEngine3D
  AttachmentOffset = pos=(-20.7,18.635,1.55) rot=(0,1,0;0.785398rad)
  BaseFeature = -> Fillet707
  Height = 0.375
  Length = 0.23
  MapMode = 5
  Placement = pos=(-20.7,18.635,1.55) rot=(0,1,0;0.785398rad)
  Support = -> [XY_Plane279]
  Width = 0.23
FEATURE [PartDesign::SubtractiveCylinder] Cylinder476
  Angle = 360
  AttacherType = Attacher::AttachEngine3D
  AttachmentOffset = pos=(-20.271,18.635,1.4056) rot=(-1,0,0;1.5708rad)
  BaseFeature = -> Box2360
  Height = 0.23
  MapMode = 5
  Placement = pos=(-20.271,18.635,1.4056) rot=(-1,0,0;1.5708rad)
  Radius = 0.23
  Support = -> [XY_Plane279]
FEATURE [PartDesign::AdditiveBox] Box2295
  AttacherType = Attacher::AttachEngine3D
  AttachmentOffset = pos=(-20.1,18.635,1.635) rot=(0,0,1;0rad)
  BaseFeature = -> Cylinder476
  Height = 0.265
  Length = 0.23
  MapMode = 5
  Placement = pos=(-20.1,18.635,1.635) rot=(0,0,1;0rad)
  Support = -> [XY_Plane279]
  Width = 0.23
FEATURE [PartDesign::Body] Body230  label="pin230"
  Group = -> [Box2300,Box2362,Box2459,Box2302,Box2298,Fillet699,Fillet706,Box2473,Cylinder462,Box2363,Box2366,Fillet707,Box2360,Cylinder476,Box2295]
  Origin = -> Origin269
  Placement = pos=(0,-4,0) rot=(0,0,1;0rad)
  Tip = -> Box2295
FEATURE [PartDesign::SubtractiveBox] Box2476
  AttacherType = Attacher::AttachEngine3D
  AttachmentOffset = pos=(-20.5,18.63,0) rot=(0,0,1;0rad)
  BaseFeature = -> Box2364
  Height = 1.635
  Length = 0.5
  MapMode = 5
  Placement = pos=(-20.5,18.63,0) rot=(0,0,1;0rad)
  Support = -> [XY_Plane283]
  Width = 0.25
FEATURE [PartDesign::SubtractiveBox] Box2471
  AttacherType = Attacher::AttachEngine3D
  AttachmentOffset = pos=(-21.19,18.635,-0.12) rot=(0,-1,0;0.15708rad)
  BaseFeature = -> Box2476
  Height = 0.12
  Length = 0.725
  MapMode = 5
  Placement = pos=(-21.19,18.635,-0.12) rot=(0,-1,0;0.15708rad)
  Support = -> [XY_Plane283]
  Width = 0.25
FEATURE [PartDesign::SubtractiveBox] Box2359
  AttacherType = Attacher::AttachEngine3D
  AttachmentOffset = pos=(-21.5005,18.625,0.235) rot=(0,-1,0;0.174533rad)
  BaseFeature = -> Box2471
  Height = 0.3
  Length = 0.6605
  MapMode = 5
  Placement = pos=(-21.5005,18.625,0.235) rot=(0,-1,0;0.174533rad)
  Support = -> [XY_Plane283]
  Width = 0.25
FEATURE [PartDesign::Fillet] Fillet705
  Base = -> Box2359 [Edge2]
  BaseFeature = -> Box2359
  Placement = pos=(-21.5005,18.625,0.235) rot=(0,-1,0;0.174533rad)
  Radius = 0.05
  SupportTransform = false
FEATURE [PartDesign::Fillet] Fillet704
  Base = -> Fillet705 [Edge33]
  BaseFeature = -> Fillet705
  Placement = pos=(-21.5005,18.625,0.235) rot=(0,-1,0;0.174533rad)
  Radius = 0.5
  SupportTransform = false
FEATURE [PartDesign::AdditiveBox] Box2449
  AttacherType = Attacher::AttachEngine3D
  AttachmentOffset = pos=(-21.1,18.635,0.305) rot=(0,1,0;0.785398rad)
  BaseFeature = -> Fillet704
  Height = 0.375
  Length = 0.2
  MapMode = 5
  Placement = pos=(-21.1,18.635,0.305) rot=(0,1,0;0.785398rad)
  Support = -> [XY_Plane283]
  Width = 0.23
FEATURE [PartDesign::SubtractiveCylinder] Cylinder494
  Angle = 360
  AttacherType = Attacher::AttachEngine3D
  AttachmentOffset = pos=(-21.055,18.935,0.52) rot=(1,0,0;1.5708rad)
  BaseFeature = -> Box2449
  Height = 0.375
  MapMode = 5
  Placement = pos=(-21.055,18.935,0.52) rot=(1,0,0;1.5708rad)
  Radius = 0.205
  Support = -> [XY_Plane283]
FEATURE [PartDesign::SubtractiveBox] Box2458
  AttacherType = Attacher::AttachEngine3D
  AttachmentOffset = pos=(-20.95,18.635,0.53) rot=(0,0,1;0rad)
  BaseFeature = -> Cylinder494
  Height = 0.5
  Length = 0.1
  MapMode = 5
  Placement = pos=(-20.95,18.635,0.53) rot=(0,0,1;0rad)
  Support = -> [XY_Plane283]
  Width = 0.23
FEATURE [PartDesign::SubtractiveBox] Box2460
  AttacherType = Attacher::AttachEngine3D
  AttachmentOffset = pos=(-21.15,18.635,0.297) rot=(0,-1,0;0.174533rad)
  BaseFeature = -> Box2458
  Height = 0.115
  Length = 0.115
  MapMode = 5
  Placement = pos=(-21.15,18.635,0.297) rot=(0,-1,0;0.174533rad)
  Support = -> [XY_Plane283]
  Width = 0.23
FEATURE [PartDesign::Fillet] Fillet700
  Base = -> Box2460 [Edge28]
  BaseFeature = -> Box2460
  Placement = pos=(-21.15,18.635,0.297) rot=(0,-1,0;0.174533rad)
  Radius = 0.375
  SupportTransform = false
FEATURE [PartDesign::SubtractiveBox] Box2477
  AttacherType = Attacher::AttachEngine3D
  AttachmentOffset = pos=(-21.5005,18.625,0.235) rot=(0,-1,0;0.174533rad)
  BaseFeature = -> Box2424
  Height = 0.3
  Length = 0.6605
  MapMode = 5
  Placement = pos=(-21.5005,18.625,0.235) rot=(0,-1,0;0.174533rad)
  Support = -> [XY_Plane286]
  Width = 0.25
FEATURE [PartDesign::Fillet] Fillet711
  Base = -> Box2477 [Edge2]
  BaseFeature = -> Box2477
  Placement = pos=(-21.5005,18.625,0.235) rot=(0,-1,0;0.174533rad)
  Radius = 0.05
  SupportTransform = false
FEATURE [PartDesign::Fillet] Fillet703
  Base = -> Fillet711 [Edge33]
  BaseFeature = -> Fillet711
  Placement = pos=(-21.5005,18.625,0.235) rot=(0,-1,0;0.174533rad)
  Radius = 0.5
  SupportTransform = false
FEATURE [PartDesign::AdditiveBox] Box2434
  AttacherType = Attacher::AttachEngine3D
  AttachmentOffset = pos=(-21.1,18.635,0.305) rot=(0,1,0;0.785398rad)
  BaseFeature = -> Fillet703
  Height = 0.375
  Length = 0.2
  MapMode = 5
  Placement = pos=(-21.1,18.635,0.305) rot=(0,1,0;0.785398rad)
  Support = -> [XY_Plane286]
  Width = 0.23
FEATURE [PartDesign::SubtractiveCylinder] Cylinder491
  Angle = 360
  AttacherType = Attacher::AttachEngine3D
  AttachmentOffset = pos=(-21.055,18.935,0.52) rot=(1,0,0;1.5708rad)
  BaseFeature = -> Box2434
  Height = 0.375
  MapMode = 5
  Placement = pos=(-21.055,18.935,0.52) rot=(1,0,0;1.5708rad)
  Radius = 0.205
  Support = -> [XY_Plane286]
FEATURE [PartDesign::SubtractiveBox] Box2432
  AttacherType = Attacher::AttachEngine3D
  AttachmentOffset = pos=(-20.95,18.635,0.53) rot=(0,0,1;0rad)
  BaseFeature = -> Cylinder491
  Height = 0.5
  Length = 0.1
  MapMode = 5
  Placement = pos=(-20.95,18.635,0.53) rot=(0,0,1;0rad)
  Support = -> [XY_Plane286]
  Width = 0.23
FEATURE [PartDesign::SubtractiveBox] Box2441
  AttacherType = Attacher::AttachEngine3D
  AttachmentOffset = pos=(-21.15,18.635,0.297) rot=(0,-1,0;0.174533rad)
  BaseFeature = -> Box2432
  Height = 0.115
  Length = 0.115
  MapMode = 5
  Placement = pos=(-21.15,18.635,0.297) rot=(0,-1,0;0.174533rad)
  Support = -> [XY_Plane286]
  Width = 0.23
FEATURE [PartDesign::Fillet] Fillet698
  Base = -> Box2441 [Edge28]
  BaseFeature = -> Box2441
  Placement = pos=(-21.15,18.635,0.297) rot=(0,-1,0;0.174533rad)
  Radius = 0.375
  SupportTransform = false
FEATURE [PartDesign::AdditiveBox] Box2436
  AttacherType = Attacher::AttachEngine3D
  AttachmentOffset = pos=(-20.7,18.635,1.55) rot=(0,1,0;0.785398rad)
  BaseFeature = -> Fillet698
  Height = 0.375
  Length = 0.23
  MapMode = 5
  Placement = pos=(-20.7,18.635,1.55) rot=(0,1,0;0.785398rad)
  Support = -> [XY_Plane286]
  Width = 0.23
FEATURE [PartDesign::SubtractiveCylinder] Cylinder489
  Angle = 360
  AttacherType = Attacher::AttachEngine3D
  AttachmentOffset = pos=(-20.271,18.635,1.4056) rot=(-1,0,0;1.5708rad)
  BaseFeature = -> Box2436
  Height = 0.23
  MapMode = 5
  Placement = pos=(-20.271,18.635,1.4056) rot=(-1,0,0;1.5708rad)
  Radius = 0.23
  Support = -> [XY_Plane286]
FEATURE [PartDesign::AdditiveBox] Box2448
  AttacherType = Attacher::AttachEngine3D
  AttachmentOffset = pos=(-20.1,18.635,1.635) rot=(0,0,1;0rad)
  BaseFeature = -> Cylinder489
  Height = 0.265
  Length = 0.23
  MapMode = 5
  Placement = pos=(-20.1,18.635,1.635) rot=(0,0,1;0rad)
  Support = -> [XY_Plane286]
  Width = 0.23
FEATURE [PartDesign::Body] Body233  label="pin233"
  Group = -> [Box2468,Box2455,Box2442,Box2424,Box2477,Fillet711,Fillet703,Box2434,Cylinder491,Box2432,Box2441,Fillet698,Box2436,Cylinder489,Box2448]
  Origin = -> Origin256
  Placement = pos=(0,-4.5,0) rot=(0,0,1;0rad)
  Tip = -> Box2448
FEATURE [PartDesign::SubtractiveBox] Box2478
  AttacherType = Attacher::AttachEngine3D
  AttachmentOffset = pos=(-20.5,18.63,0) rot=(0,0,1;0rad)
  BaseFeature = -> Box2361
  Height = 1.635
  Length = 0.5
  MapMode = 5
  Placement = pos=(-20.5,18.63,0) rot=(0,0,1;0rad)
  Support = -> [XY_Plane285]
  Width = 0.25
FEATURE [PartDesign::SubtractiveBox] Box2358
  AttacherType = Attacher::AttachEngine3D
  AttachmentOffset = pos=(-21.19,18.635,-0.12) rot=(0,-1,0;0.15708rad)
  BaseFeature = -> Box2478
  Height = 0.12
  Length = 0.725
  MapMode = 5
  Placement = pos=(-21.19,18.635,-0.12) rot=(0,-1,0;0.15708rad)
  Support = -> [XY_Plane285]
  Width = 0.25
FEATURE [PartDesign::SubtractiveBox] Box2299
  AttacherType = Attacher::AttachEngine3D
  AttachmentOffset = pos=(-21.5005,18.625,0.235) rot=(0,-1,0;0.174533rad)
  BaseFeature = -> Box2358
  Height = 0.3
  Length = 0.6605
  MapMode = 5
  Placement = pos=(-21.5005,18.625,0.235) rot=(0,-1,0;0.174533rad)
  Support = -> [XY_Plane285]
  Width = 0.25
FEATURE [PartDesign::Fillet] Fillet709
  Base = -> Box2299 [Edge2]
  BaseFeature = -> Box2299
  Placement = pos=(-21.5005,18.625,0.235) rot=(0,-1,0;0.174533rad)
  Radius = 0.05
  SupportTransform = false
FEATURE [PartDesign::Fillet] Fillet710
  Base = -> Fillet709 [Edge33]
  BaseFeature = -> Fillet709
  Placement = pos=(-21.5005,18.625,0.235) rot=(0,-1,0;0.174533rad)
  Radius = 0.5
  SupportTransform = false
FEATURE [PartDesign::AdditiveBox] Box2475
  AttacherType = Attacher::AttachEngine3D
  AttachmentOffset = pos=(-21.1,18.635,0.305) rot=(0,1,0;0.785398rad)
  BaseFeature = -> Fillet710
  Height = 0.375
  Length = 0.2
  MapMode = 5
  Placement = pos=(-21.1,18.635,0.305) rot=(0,1,0;0.785398rad)
  Support = -> [XY_Plane285]
  Width = 0.23
FEATURE [PartDesign::AdditiveBox] Box2479
  AttacherType = Attacher::AttachEngine3D
  AttachmentOffset = pos=(-20.7,18.635,1.55) rot=(0,1,0;0.785398rad)
  BaseFeature = -> Fillet700
  Height = 0.375
  Length = 0.23
  MapMode = 5
  Placement = pos=(-20.7,18.635,1.55) rot=(0,1,0;0.785398rad)
  Support = -> [XY_Plane283]
  Width = 0.23
FEATURE [PartDesign::SubtractiveCylinder] Cylinder499
  Angle = 360
  AttacherType = Attacher::AttachEngine3D
  AttachmentOffset = pos=(-20.271,18.635,1.4056) rot=(-1,0,0;1.5708rad)
  BaseFeature = -> Box2479
  Height = 0.23
  MapMode = 5
  Placement = pos=(-20.271,18.635,1.4056) rot=(-1,0,0;1.5708rad)
  Radius = 0.23
  Support = -> [XY_Plane283]
FEATURE [PartDesign::SubtractiveCylinder] Cylinder502
  Angle = 360
  AttacherType = Attacher::AttachEngine3D
  AttachmentOffset = pos=(-21.055,18.935,0.52) rot=(1,0,0;1.5708rad)
  BaseFeature = -> Box2475
  Height = 0.375
  MapMode = 5
  Placement = pos=(-21.055,18.935,0.52) rot=(1,0,0;1.5708rad)
  Radius = 0.205
  Support = -> [XY_Plane285]
FEATURE [PartDesign::SubtractiveBox] Box2474
  AttacherType = Attacher::AttachEngine3D
  AttachmentOffset = pos=(-20.95,18.635,0.53) rot=(0,0,1;0rad)
  BaseFeature = -> Cylinder502
  Height = 0.5
  Length = 0.1
  MapMode = 5
  Placement = pos=(-20.95,18.635,0.53) rot=(0,0,1;0rad)
  Support = -> [XY_Plane285]
  Width = 0.23
FEATURE [PartDesign::SubtractiveBox] Box2469
  AttacherType = Attacher::AttachEngine3D
  AttachmentOffset = pos=(-21.15,18.635,0.297) rot=(0,-1,0;0.174533rad)
  BaseFeature = -> Box2474
  Height = 0.115
  Length = 0.115
  MapMode = 5
  Placement = pos=(-21.15,18.635,0.297) rot=(0,-1,0;0.174533rad)
  Support = -> [XY_Plane285]
  Width = 0.23
FEATURE [PartDesign::Fillet] Fillet693
  Base = -> Box2469 [Edge28]
  BaseFeature = -> Box2469
  Placement = pos=(-21.15,18.635,0.297) rot=(0,-1,0;0.174533rad)
  Radius = 0.375
  SupportTransform = false
FEATURE [PartDesign::AdditiveBox] Box2470
  AttacherType = Attacher::AttachEngine3D
  AttachmentOffset = pos=(-20.7,18.635,1.55) rot=(0,1,0;0.785398rad)
  BaseFeature = -> Fillet693
  Height = 0.375
  Length = 0.23
  MapMode = 5
  Placement = pos=(-20.7,18.635,1.55) rot=(0,1,0;0.785398rad)
  Support = -> [XY_Plane285]
  Width = 0.23
FEATURE [PartDesign::SubtractiveCylinder] Cylinder500
  Angle = 360
  AttacherType = Attacher::AttachEngine3D
  AttachmentOffset = pos=(-20.271,18.635,1.4056) rot=(-1,0,0;1.5708rad)
  BaseFeature = -> Box2470
  Height = 0.23
  MapMode = 5
  Placement = pos=(-20.271,18.635,1.4056) rot=(-1,0,0;1.5708rad)
  Radius = 0.23
  Support = -> [XY_Plane285]
FEATURE [PartDesign::AdditiveBox] Box2303
  AttacherType = Attacher::AttachEngine3D
  AttachmentOffset = pos=(-20.1,18.635,1.635) rot=(0,0,1;0rad)
  BaseFeature = -> Cylinder500
  Height = 0.265
  Length = 0.23
  MapMode = 5
  Placement = pos=(-20.1,18.635,1.635) rot=(0,0,1;0rad)
  Support = -> [XY_Plane285]
  Width = 0.23
FEATURE [PartDesign::Body] Body235  label="pin235"
  Group = -> [Box2356,Box2361,Box2478,Box2358,Box2299,Fillet709,Fillet710,Box2475,Cylinder502,Box2474,Box2469,Fillet693,Box2470,Cylinder500,Box2303]
  Origin = -> Origin280
  Placement = pos=(0,-3.5,0) rot=(0,0,1;0rad)
  Tip = -> Box2303
FEATURE [PartDesign::AdditiveBox] Box2485
  AttacherType = Attacher::AttachEngine3D
  AttachmentOffset = pos=(-20.1,18.635,1.635) rot=(0,0,1;0rad)
  BaseFeature = -> Cylinder499
  Height = 0.265
  Length = 0.23
  MapMode = 5
  Placement = pos=(-20.1,18.635,1.635) rot=(0,0,1;0rad)
  Support = -> [XY_Plane283]
  Width = 0.23
FEATURE [PartDesign::Body] Body237  label="pin237"
  Group = -> [Box2301,Box2364,Box2476,Box2471,Box2359,Fillet705,Fillet704,Box2449,Cylinder494,Box2458,Box2460,Fillet700,Box2479,Cylinder499,Box2485]
  Origin = -> Origin268
  Placement = pos=(0,-3,0) rot=(0,0,1;0rad)
  Tip = -> Box2485
FEATURE [PartDesign::AdditiveBox] Box2492
  AttacherType = Attacher::AttachEngine3D
  AttachmentOffset = pos=(-21.3,18.635,0) rot=(0,0,1;0rad)
  Height = 1.9
  Length = 1.3
  MapMode = 5
  Placement = pos=(-21.3,18.635,0) rot=(0,0,1;0rad)
  Support = -> [XY_Plane261]
  Width = 0.23
FEATURE [PartDesign::AdditiveBox] Box2496
  AttacherType = Attacher::AttachEngine3D
  AttachmentOffset = pos=(-21.3,18.635,0) rot=(0,0,1;0rad)
  Height = 1.9
  Length = 1.3
  MapMode = 5
  Placement = pos=(-21.3,18.635,0) rot=(0,0,1;0rad)
  Support = -> [XY_Plane282]
  Width = 0.23
FEATURE [PartDesign::SubtractiveBox] Box2482
  AttacherType = Attacher::AttachEngine3D
  AttachmentOffset = pos=(-21.35,18.635,0.35) rot=(0,0,1;0rad)
  BaseFeature = -> Box2496
  Height = 1.55
  Length = 0.5
  MapMode = 5
  Placement = pos=(-21.35,18.635,0.35) rot=(0,0,1;0rad)
  Support = -> [XY_Plane282]
  Width = 0.23
FEATURE [PartDesign::SubtractiveBox] Box2486
  AttacherType = Attacher::AttachEngine3D
  AttachmentOffset = pos=(-20.5,18.63,0) rot=(0,0,1;0rad)
  BaseFeature = -> Box2482
  Height = 1.635
  Length = 0.5
  MapMode = 5
  Placement = pos=(-20.5,18.63,0) rot=(0,0,1;0rad)
  Support = -> [XY_Plane282]
  Width = 0.25
FEATURE [PartDesign::SubtractiveBox] Box2500
  AttacherType = Attacher::AttachEngine3D
  AttachmentOffset = pos=(-21.19,18.635,-0.12) rot=(0,-1,0;0.15708rad)
  BaseFeature = -> Box2486
  Height = 0.12
  Length = 0.725
  MapMode = 5
  Placement = pos=(-21.19,18.635,-0.12) rot=(0,-1,0;0.15708rad)
  Support = -> [XY_Plane282]
  Width = 0.25
FEATURE [PartDesign::SubtractiveBox] Box2498
  AttacherType = Attacher::AttachEngine3D
  AttachmentOffset = pos=(-21.5005,18.625,0.235) rot=(0,-1,0;0.174533rad)
  BaseFeature = -> Box2500
  Height = 0.3
  Length = 0.6605
  MapMode = 5
  Placement = pos=(-21.5005,18.625,0.235) rot=(0,-1,0;0.174533rad)
  Support = -> [XY_Plane282]
  Width = 0.25
FEATURE [PartDesign::Fillet] Fillet772
  Base = -> Box2498 [Edge2]
  BaseFeature = -> Box2498
  Placement = pos=(-21.5005,18.625,0.235) rot=(0,-1,0;0.174533rad)
  Radius = 0.05
  SupportTransform = false
FEATURE [PartDesign::Fillet] Fillet759
  Base = -> Fillet772 [Edge33]
  BaseFeature = -> Fillet772
  Placement = pos=(-21.5005,18.625,0.235) rot=(0,-1,0;0.174533rad)
  Radius = 0.5
  SupportTransform = false
FEATURE [PartDesign::AdditiveBox] Box2481
  AttacherType = Attacher::AttachEngine3D
  AttachmentOffset = pos=(-21.1,18.635,0.305) rot=(0,1,0;0.785398rad)
  BaseFeature = -> Fillet759
  Height = 0.375
  Length = 0.2
  MapMode = 5
  Placement = pos=(-21.1,18.635,0.305) rot=(0,1,0;0.785398rad)
  Support = -> [XY_Plane282]
  Width = 0.23
FEATURE [PartDesign::SubtractiveCylinder] Cylinder501
  Angle = 360
  AttacherType = Attacher::AttachEngine3D
  AttachmentOffset = pos=(-21.055,18.935,0.52) rot=(1,0,0;1.5708rad)
  BaseFeature = -> Box2481
  Height = 0.375
  MapMode = 5
  Placement = pos=(-21.055,18.935,0.52) rot=(1,0,0;1.5708rad)
  Radius = 0.205
  Support = -> [XY_Plane282]
FEATURE [PartDesign::SubtractiveBox] Box2495
  AttacherType = Attacher::AttachEngine3D
  AttachmentOffset = pos=(-20.95,18.635,0.53) rot=(0,0,1;0rad)
  BaseFeature = -> Cylinder501
  Height = 0.5
  Length = 0.1
  MapMode = 5
  Placement = pos=(-20.95,18.635,0.53) rot=(0,0,1;0rad)
  Support = -> [XY_Plane282]
  Width = 0.23
FEATURE [PartDesign::SubtractiveBox] Box2489
  AttacherType = Attacher::AttachEngine3D
  AttachmentOffset = pos=(-21.15,18.635,0.297) rot=(0,-1,0;0.174533rad)
  BaseFeature = -> Box2495
  Height = 0.115
  Length = 0.115
  MapMode = 5
  Placement = pos=(-21.15,18.635,0.297) rot=(0,-1,0;0.174533rad)
  Support = -> [XY_Plane282]
  Width = 0.23
FEATURE [PartDesign::Fillet] Fillet688
  Base = -> Box2489 [Edge28]
  BaseFeature = -> Box2489
  Placement = pos=(-21.15,18.635,0.297) rot=(0,-1,0;0.174533rad)
  Radius = 0.375
  SupportTransform = false
FEATURE [PartDesign::AdditiveBox] Box2487
  AttacherType = Attacher::AttachEngine3D
  AttachmentOffset = pos=(-20.7,18.635,1.55) rot=(0,1,0;0.785398rad)
  BaseFeature = -> Fillet688
  Height = 0.375
  Length = 0.23
  MapMode = 5
  Placement = pos=(-20.7,18.635,1.55) rot=(0,1,0;0.785398rad)
  Support = -> [XY_Plane282]
  Width = 0.23
FEATURE [PartDesign::SubtractiveCylinder] Cylinder503
  Angle = 360
  AttacherType = Attacher::AttachEngine3D
  AttachmentOffset = pos=(-20.271,18.635,1.4056) rot=(-1,0,0;1.5708rad)
  BaseFeature = -> Box2487
  Height = 0.23
  MapMode = 5
  Placement = pos=(-20.271,18.635,1.4056) rot=(-1,0,0;1.5708rad)
  Radius = 0.23
  Support = -> [XY_Plane282]
FEATURE [PartDesign::AdditiveBox] Box2499
  AttacherType = Attacher::AttachEngine3D
  AttachmentOffset = pos=(-20.1,18.635,1.635) rot=(0,0,1;0rad)
  BaseFeature = -> Cylinder503
  Height = 0.265
  Length = 0.23
  MapMode = 5
  Placement = pos=(-20.1,18.635,1.635) rot=(0,0,1;0rad)
  Support = -> [XY_Plane282]
  Width = 0.23
FEATURE [PartDesign::Body] Body259  label="pin259"
  Group = -> [Box2496,Box2482,Box2486,Box2500,Box2498,Fillet772,Fillet759,Box2481,Cylinder501,Box2495,Box2489,Fillet688,Box2487,Cylinder503,Box2499]
  Origin = -> Origin257
  Placement = pos=(0,-0.5,0) rot=(0,0,1;0rad)
  Tip = -> Box2499
FEATURE [PartDesign::AdditiveBox] Box2505
  AttacherType = Attacher::AttachEngine3D
  AttachmentOffset = pos=(-21.3,18.635,0) rot=(0,0,1;0rad)
  Height = 1.9
  Length = 1.3
  MapMode = 5
  Placement = pos=(-21.3,18.635,0) rot=(0,0,1;0rad)
  Support = -> [XY_Plane277]
  Width = 0.23
FEATURE [PartDesign::SubtractiveBox] Box2503
  AttacherType = Attacher::AttachEngine3D
  AttachmentOffset = pos=(-21.35,18.635,0.35) rot=(0,0,1;0rad)
  BaseFeature = -> Box2505
  Height = 1.55
  Length = 0.5
  MapMode = 5
  Placement = pos=(-21.35,18.635,0.35) rot=(0,0,1;0rad)
  Support = -> [XY_Plane277]
  Width = 0.23
FEATURE [PartDesign::SubtractiveBox] Box2488
  AttacherType = Attacher::AttachEngine3D
  AttachmentOffset = pos=(-20.5,18.63,0) rot=(0,0,1;0rad)
  BaseFeature = -> Box2503
  Height = 1.635
  Length = 0.5
  MapMode = 5
  Placement = pos=(-20.5,18.63,0) rot=(0,0,1;0rad)
  Support = -> [XY_Plane277]
  Width = 0.25
FEATURE [PartDesign::SubtractiveBox] Box2508
  AttacherType = Attacher::AttachEngine3D
  AttachmentOffset = pos=(-21.35,18.635,0.35) rot=(0,0,1;0rad)
  BaseFeature = -> Box2492
  Height = 1.55
  Length = 0.5
  MapMode = 5
  Placement = pos=(-21.35,18.635,0.35) rot=(0,0,1;0rad)
  Support = -> [XY_Plane261]
  Width = 0.23
FEATURE [PartDesign::AdditiveBox] Box2509
  AttacherType = Attacher::AttachEngine3D
  AttachmentOffset = pos=(-21.3,18.635,0) rot=(0,0,1;0rad)
  Height = 1.9
  Length = 1.3
  MapMode = 5
  Placement = pos=(-21.3,18.635,0) rot=(0,0,1;0rad)
  Support = -> [XY_Plane281]
  Width = 0.23
FEATURE [PartDesign::SubtractiveBox] Box2510
  AttacherType = Attacher::AttachEngine3D
  AttachmentOffset = pos=(-21.35,18.635,0.35) rot=(0,0,1;0rad)
  BaseFeature = -> Box2509
  Height = 1.55
  Length = 0.5
  MapMode = 5
  Placement = pos=(-21.35,18.635,0.35) rot=(0,0,1;0rad)
  Support = -> [XY_Plane281]
  Width = 0.23
FEATURE [PartDesign::SubtractiveBox] Box2484
  AttacherType = Attacher::AttachEngine3D
  AttachmentOffset = pos=(-20.5,18.63,0) rot=(0,0,1;0rad)
  BaseFeature = -> Box2510
  Height = 1.635
  Length = 0.5
  MapMode = 5
  Placement = pos=(-20.5,18.63,0) rot=(0,0,1;0rad)
  Support = -> [XY_Plane281]
  Width = 0.25
FEATURE [PartDesign::SubtractiveBox] Box2483
  AttacherType = Attacher::AttachEngine3D
  AttachmentOffset = pos=(-21.19,18.635,-0.12) rot=(0,-1,0;0.15708rad)
  BaseFeature = -> Box2484
  Height = 0.12
  Length = 0.725
  MapMode = 5
  Placement = pos=(-21.19,18.635,-0.12) rot=(0,-1,0;0.15708rad)
  Support = -> [XY_Plane281]
  Width = 0.25
FEATURE [PartDesign::SubtractiveBox] Box2494
  AttacherType = Attacher::AttachEngine3D
  AttachmentOffset = pos=(-21.5005,18.625,0.235) rot=(0,-1,0;0.174533rad)
  BaseFeature = -> Box2483
  Height = 0.3
  Length = 0.6605
  MapMode = 5
  Placement = pos=(-21.5005,18.625,0.235) rot=(0,-1,0;0.174533rad)
  Support = -> [XY_Plane281]
  Width = 0.25
FEATURE [PartDesign::Fillet] Fillet692
  Base = -> Box2494 [Edge2]
  BaseFeature = -> Box2494
  Placement = pos=(-21.5005,18.625,0.235) rot=(0,-1,0;0.174533rad)
  Radius = 0.05
  SupportTransform = false
FEATURE [PartDesign::Fillet] Fillet735
  Base = -> Fillet692 [Edge33]
  BaseFeature = -> Fillet692
  Placement = pos=(-21.5005,18.625,0.235) rot=(0,-1,0;0.174533rad)
  Radius = 0.5
  SupportTransform = false
FEATURE [PartDesign::AdditiveBox] Box2365
  AttacherType = Attacher::AttachEngine3D
  AttachmentOffset = pos=(-21.1,18.635,0.305) rot=(0,1,0;0.785398rad)
  BaseFeature = -> Fillet735
  Height = 0.375
  Length = 0.2
  MapMode = 5
  Placement = pos=(-21.1,18.635,0.305) rot=(0,1,0;0.785398rad)
  Support = -> [XY_Plane281]
  Width = 0.23
FEATURE [PartDesign::SubtractiveCylinder] Cylinder497
  Angle = 360
  AttacherType = Attacher::AttachEngine3D
  AttachmentOffset = pos=(-21.055,18.935,0.52) rot=(1,0,0;1.5708rad)
  BaseFeature = -> Box2365
  Height = 0.375
  MapMode = 5
  Placement = pos=(-21.055,18.935,0.52) rot=(1,0,0;1.5708rad)
  Radius = 0.205
  Support = -> [XY_Plane281]
FEATURE [PartDesign::SubtractiveBox] Box2465
  AttacherType = Attacher::AttachEngine3D
  AttachmentOffset = pos=(-20.95,18.635,0.53) rot=(0,0,1;0rad)
  BaseFeature = -> Cylinder497
  Height = 0.5
  Length = 0.1
  MapMode = 5
  Placement = pos=(-20.95,18.635,0.53) rot=(0,0,1;0rad)
  Support = -> [XY_Plane281]
  Width = 0.23
FEATURE [PartDesign::SubtractiveBox] Box2438
  AttacherType = Attacher::AttachEngine3D
  AttachmentOffset = pos=(-21.15,18.635,0.297) rot=(0,-1,0;0.174533rad)
  BaseFeature = -> Box2465
  Height = 0.115
  Length = 0.115
  MapMode = 5
  Placement = pos=(-21.15,18.635,0.297) rot=(0,-1,0;0.174533rad)
  Support = -> [XY_Plane281]
  Width = 0.23
FEATURE [PartDesign::Fillet] Fillet712
  Base = -> Box2438 [Edge28]
  BaseFeature = -> Box2438
  Placement = pos=(-21.15,18.635,0.297) rot=(0,-1,0;0.174533rad)
  Radius = 0.375
  SupportTransform = false
FEATURE [PartDesign::AdditiveBox] Box2480
  AttacherType = Attacher::AttachEngine3D
  AttachmentOffset = pos=(-20.7,18.635,1.55) rot=(0,1,0;0.785398rad)
  BaseFeature = -> Fillet712
  Height = 0.375
  Length = 0.23
  MapMode = 5
  Placement = pos=(-20.7,18.635,1.55) rot=(0,1,0;0.785398rad)
  Support = -> [XY_Plane281]
  Width = 0.23
FEATURE [PartDesign::SubtractiveCylinder] Cylinder498
  Angle = 360
  AttacherType = Attacher::AttachEngine3D
  AttachmentOffset = pos=(-20.271,18.635,1.4056) rot=(-1,0,0;1.5708rad)
  BaseFeature = -> Box2480
  Height = 0.23
  MapMode = 5
  Placement = pos=(-20.271,18.635,1.4056) rot=(-1,0,0;1.5708rad)
  Radius = 0.23
  Support = -> [XY_Plane281]
FEATURE [PartDesign::AdditiveBox] Box2491
  AttacherType = Attacher::AttachEngine3D
  AttachmentOffset = pos=(-20.1,18.635,1.635) rot=(0,0,1;0rad)
  BaseFeature = -> Cylinder498
  Height = 0.265
  Length = 0.23
  MapMode = 5
  Placement = pos=(-20.1,18.635,1.635) rot=(0,0,1;0rad)
  Support = -> [XY_Plane281]
  Width = 0.23
FEATURE [PartDesign::Body] Body232  label="pin232"
  Group = -> [Box2509,Box2510,Box2484,Box2483,Box2494,Fillet692,Fillet735,Box2365,Cylinder497,Box2465,Box2438,Fillet712,Box2480,Cylinder498,Box2491]
  Origin = -> Origin255
  Tip = -> Box2491
FEATURE [PartDesign::AdditiveBox] Box2511
  AttacherType = Attacher::AttachEngine3D
  AttachmentOffset = pos=(-21.3,18.635,0) rot=(0,0,1;0rad)
  Height = 1.9
  Length = 1.3
  MapMode = 5
  Placement = pos=(-21.3,18.635,0) rot=(0,0,1;0rad)
  Support = -> [XY_Plane256]
  Width = 0.23
FEATURE [PartDesign::SubtractiveBox] Box2513
  AttacherType = Attacher::AttachEngine3D
  AttachmentOffset = pos=(-21.35,18.635,0.35) rot=(0,0,1;0rad)
  BaseFeature = -> Box2511
  Height = 1.55
  Length = 0.5
  MapMode = 5
  Placement = pos=(-21.35,18.635,0.35) rot=(0,0,1;0rad)
  Support = -> [XY_Plane256]
  Width = 0.23
FEATURE [PartDesign::SubtractiveBox] Box2515
  AttacherType = Attacher::AttachEngine3D
  AttachmentOffset = pos=(-21.19,18.635,-0.12) rot=(0,-1,0;0.15708rad)
  BaseFeature = -> Box2488
  Height = 0.12
  Length = 0.725
  MapMode = 5
  Placement = pos=(-21.19,18.635,-0.12) rot=(0,-1,0;0.15708rad)
  Support = -> [XY_Plane277]
  Width = 0.25
FEATURE [PartDesign::SubtractiveBox] Box2514
  AttacherType = Attacher::AttachEngine3D
  AttachmentOffset = pos=(-21.5005,18.625,0.235) rot=(0,-1,0;0.174533rad)
  BaseFeature = -> Box2515
  Height = 0.3
  Length = 0.6605
  MapMode = 5
  Placement = pos=(-21.5005,18.625,0.235) rot=(0,-1,0;0.174533rad)
  Support = -> [XY_Plane277]
  Width = 0.25
FEATURE [PartDesign::Fillet] Fillet773
  Base = -> Box2514 [Edge2]
  BaseFeature = -> Box2514
  Placement = pos=(-21.5005,18.625,0.235) rot=(0,-1,0;0.174533rad)
  Radius = 0.05
  SupportTransform = false
FEATURE [PartDesign::Fillet] Fillet691
  Base = -> Fillet773 [Edge33]
  BaseFeature = -> Fillet773
  Placement = pos=(-21.5005,18.625,0.235) rot=(0,-1,0;0.174533rad)
  Radius = 0.5
  SupportTransform = false
FEATURE [PartDesign::AdditiveBox] Box2490
  AttacherType = Attacher::AttachEngine3D
  AttachmentOffset = pos=(-21.1,18.635,0.305) rot=(0,1,0;0.785398rad)
  BaseFeature = -> Fillet691
  Height = 0.375
  Length = 0.2
  MapMode = 5
  Placement = pos=(-21.1,18.635,0.305) rot=(0,1,0;0.785398rad)
  Support = -> [XY_Plane277]
  Width = 0.23
FEATURE [PartDesign::SubtractiveCylinder] Cylinder504
  Angle = 360
  AttacherType = Attacher::AttachEngine3D
  AttachmentOffset = pos=(-21.055,18.935,0.52) rot=(1,0,0;1.5708rad)
  BaseFeature = -> Box2490
  Height = 0.375
  MapMode = 5
  Placement = pos=(-21.055,18.935,0.52) rot=(1,0,0;1.5708rad)
  Radius = 0.205
  Support = -> [XY_Plane277]
FEATURE [PartDesign::SubtractiveBox] Box2493
  AttacherType = Attacher::AttachEngine3D
  AttachmentOffset = pos=(-20.95,18.635,0.53) rot=(0,0,1;0rad)
  BaseFeature = -> Cylinder504
  Height = 0.5
  Length = 0.1
  MapMode = 5
  Placement = pos=(-20.95,18.635,0.53) rot=(0,0,1;0rad)
  Support = -> [XY_Plane277]
  Width = 0.23
FEATURE [PartDesign::SubtractiveBox] Box2502
  AttacherType = Attacher::AttachEngine3D
  AttachmentOffset = pos=(-21.15,18.635,0.297) rot=(0,-1,0;0.174533rad)
  BaseFeature = -> Box2493
  Height = 0.115
  Length = 0.115
  MapMode = 5
  Placement = pos=(-21.15,18.635,0.297) rot=(0,-1,0;0.174533rad)
  Support = -> [XY_Plane277]
  Width = 0.23
FEATURE [PartDesign::Fillet] Fillet770
  Base = -> Box2502 [Edge28]
  BaseFeature = -> Box2502
  Placement = pos=(-21.15,18.635,0.297) rot=(0,-1,0;0.174533rad)
  Radius = 0.375
  SupportTransform = false
FEATURE [PartDesign::AdditiveBox] Box2501
  AttacherType = Attacher::AttachEngine3D
  AttachmentOffset = pos=(-20.7,18.635,1.55) rot=(0,1,0;0.785398rad)
  BaseFeature = -> Fillet770
  Height = 0.375
  Length = 0.23
  MapMode = 5
  Placement = pos=(-20.7,18.635,1.55) rot=(0,1,0;0.785398rad)
  Support = -> [XY_Plane277]
  Width = 0.23
FEATURE [PartDesign::SubtractiveCylinder] Cylinder506
  Angle = 360
  AttacherType = Attacher::AttachEngine3D
  AttachmentOffset = pos=(-20.271,18.635,1.4056) rot=(-1,0,0;1.5708rad)
  BaseFeature = -> Box2501
  Height = 0.23
  MapMode = 5
  Placement = pos=(-20.271,18.635,1.4056) rot=(-1,0,0;1.5708rad)
  Radius = 0.23
  Support = -> [XY_Plane277]
FEATURE [PartDesign::AdditiveBox] Box2504
  AttacherType = Attacher::AttachEngine3D
  AttachmentOffset = pos=(-20.1,18.635,1.635) rot=(0,0,1;0rad)
  BaseFeature = -> Cylinder506
  Height = 0.265
  Length = 0.23
  MapMode = 5
  Placement = pos=(-20.1,18.635,1.635) rot=(0,0,1;0rad)
  Support = -> [XY_Plane277]
  Width = 0.23
FEATURE [PartDesign::Body] Body229  label="pin229"
  Group = -> [Box2505,Box2503,Box2488,Box2515,Box2514,Fillet773,Fillet691,Box2490,Cylinder504,Box2493,Box2502,Fillet770,Box2501,Cylinder506,Box2504]
  Origin = -> Origin285
  Placement = pos=(0,-1,0) rot=(0,0,1;0rad)
  Tip = -> Box2504
FEATURE [PartDesign::AdditiveBox] Box2518
  AttacherType = Attacher::AttachEngine3D
  AttachmentOffset = pos=(-21.3,18.635,0) rot=(0,0,1;0rad)
  Height = 1.9
  Length = 1.3
  MapMode = 5
  Placement = pos=(-21.3,18.635,0) rot=(0,0,1;0rad)
  Support = -> [XY_Plane262]
  Width = 0.23
FEATURE [PartDesign::SubtractiveBox] Box2527
  AttacherType = Attacher::AttachEngine3D
  AttachmentOffset = pos=(-21.35,18.635,0.35) rot=(0,0,1;0rad)
  BaseFeature = -> Box2518
  Height = 1.55
  Length = 0.5
  MapMode = 5
  Placement = pos=(-21.35,18.635,0.35) rot=(0,0,1;0rad)
  Support = -> [XY_Plane262]
  Width = 0.23
FEATURE [PartDesign::AdditiveBox] Box2531
  AttacherType = Attacher::AttachEngine3D
  AttachmentOffset = pos=(-21.3,18.635,0) rot=(0,0,1;0rad)
  Height = 1.9
  Length = 1.3
  MapMode = 5
  Placement = pos=(-21.3,18.635,0) rot=(0,0,1;0rad)
  Support = -> [XY_Plane255]
  Width = 0.23
FEATURE [PartDesign::SubtractiveBox] Box2543
  AttacherType = Attacher::AttachEngine3D
  AttachmentOffset = pos=(-21.35,18.635,0.35) rot=(0,0,1;0rad)
  BaseFeature = -> Box2531
  Height = 1.55
  Length = 0.5
  MapMode = 5
  Placement = pos=(-21.35,18.635,0.35) rot=(0,0,1;0rad)
  Support = -> [XY_Plane255]
  Width = 0.23
FEATURE [PartDesign::AdditiveBox] Box2547
  AttacherType = Attacher::AttachEngine3D
  AttachmentOffset = pos=(-21.3,18.635,0) rot=(0,0,1;0rad)
  Height = 1.9
  Length = 1.3
  MapMode = 5
  Placement = pos=(-21.3,18.635,0) rot=(0,0,1;0rad)
  Support = -> [XY_Plane258]
  Width = 0.23
FEATURE [PartDesign::AdditiveBox] Box2551
  AttacherType = Attacher::AttachEngine3D
  AttachmentOffset = pos=(-21.3,18.635,0) rot=(0,0,1;0rad)
  Height = 1.9
  Length = 1.3
  MapMode = 5
  Placement = pos=(-21.3,18.635,0) rot=(0,0,1;0rad)
  Support = -> [XY_Plane293]
  Width = 0.23
FEATURE [PartDesign::SubtractiveBox] Box2532
  AttacherType = Attacher::AttachEngine3D
  AttachmentOffset = pos=(-21.35,18.635,0.35) rot=(0,0,1;0rad)
  BaseFeature = -> Box2551
  Height = 1.55
  Length = 0.5
  MapMode = 5
  Placement = pos=(-21.35,18.635,0.35) rot=(0,0,1;0rad)
  Support = -> [XY_Plane293]
  Width = 0.23
FEATURE [PartDesign::AdditiveBox] Box2556
  AttacherType = Attacher::AttachEngine3D
  AttachmentOffset = pos=(-21.3,18.635,0) rot=(0,0,1;0rad)
  Height = 1.9
  Length = 1.3
  MapMode = 5
  Placement = pos=(-21.3,18.635,0) rot=(0,0,1;0rad)
  Support = -> [XY_Plane291]
  Width = 0.23
FEATURE [PartDesign::SubtractiveBox] Box2539
  AttacherType = Attacher::AttachEngine3D
  AttachmentOffset = pos=(-21.35,18.635,0.35) rot=(0,0,1;0rad)
  BaseFeature = -> Box2556
  Height = 1.55
  Length = 0.5
  MapMode = 5
  Placement = pos=(-21.35,18.635,0.35) rot=(0,0,1;0rad)
  Support = -> [XY_Plane291]
  Width = 0.23
FEATURE [PartDesign::SubtractiveBox] Box2565
  AttacherType = Attacher::AttachEngine3D
  AttachmentOffset = pos=(-20.5,18.63,0) rot=(0,0,1;0rad)
  BaseFeature = -> Box2513
  Height = 1.635
  Length = 0.5
  MapMode = 5
  Placement = pos=(-20.5,18.63,0) rot=(0,0,1;0rad)
  Support = -> [XY_Plane256]
  Width = 0.25
FEATURE [PartDesign::SubtractiveBox] Box2529
  AttacherType = Attacher::AttachEngine3D
  AttachmentOffset = pos=(-21.19,18.635,-0.12) rot=(0,-1,0;0.15708rad)
  BaseFeature = -> Box2565
  Height = 0.12
  Length = 0.725
  MapMode = 5
  Placement = pos=(-21.19,18.635,-0.12) rot=(0,-1,0;0.15708rad)
  Support = -> [XY_Plane256]
  Width = 0.25
FEATURE [PartDesign::SubtractiveBox] Box2530
  AttacherType = Attacher::AttachEngine3D
  AttachmentOffset = pos=(-21.5005,18.625,0.235) rot=(0,-1,0;0.174533rad)
  BaseFeature = -> Box2529
  Height = 0.3
  Length = 0.6605
  MapMode = 5
  Placement = pos=(-21.5005,18.625,0.235) rot=(0,-1,0;0.174533rad)
  Support = -> [XY_Plane256]
  Width = 0.25
FEATURE [PartDesign::SubtractiveBox] Box2566
  AttacherType = Attacher::AttachEngine3D
  AttachmentOffset = pos=(-21.35,18.635,0.35) rot=(0,0,1;0rad)
  BaseFeature = -> Box2547
  Height = 1.55
  Length = 0.5
  MapMode = 5
  Placement = pos=(-21.35,18.635,0.35) rot=(0,0,1;0rad)
  Support = -> [XY_Plane258]
  Width = 0.23
FEATURE [PartDesign::SubtractiveBox] Box2546
  AttacherType = Attacher::AttachEngine3D
  AttachmentOffset = pos=(-20.5,18.63,0) rot=(0,0,1;0rad)
  BaseFeature = -> Box2566
  Height = 1.635
  Length = 0.5
  MapMode = 5
  Placement = pos=(-20.5,18.63,0) rot=(0,0,1;0rad)
  Support = -> [XY_Plane258]
  Width = 0.25
FEATURE [PartDesign::SubtractiveBox] Box2549
  AttacherType = Attacher::AttachEngine3D
  AttachmentOffset = pos=(-21.19,18.635,-0.12) rot=(0,-1,0;0.15708rad)
  BaseFeature = -> Box2546
  Height = 0.12
  Length = 0.725
  MapMode = 5
  Placement = pos=(-21.19,18.635,-0.12) rot=(0,-1,0;0.15708rad)
  Support = -> [XY_Plane258]
  Width = 0.25
FEATURE [PartDesign::AdditiveBox] Box2571
  AttacherType = Attacher::AttachEngine3D
  AttachmentOffset = pos=(-21.3,18.635,0) rot=(0,0,1;0rad)
  Height = 1.9
  Length = 1.3
  MapMode = 5
  Placement = pos=(-21.3,18.635,0) rot=(0,0,1;0rad)
  Support = -> [XY_Plane259]
  Width = 0.23
FEATURE [PartDesign::SubtractiveBox] Box2563
  AttacherType = Attacher::AttachEngine3D
  AttachmentOffset = pos=(-21.35,18.635,0.35) rot=(0,0,1;0rad)
  BaseFeature = -> Box2571
  Height = 1.55
  Length = 0.5
  MapMode = 5
  Placement = pos=(-21.35,18.635,0.35) rot=(0,0,1;0rad)
  Support = -> [XY_Plane259]
  Width = 0.23
FEATURE [PartDesign::SubtractiveBox] Box2557
  AttacherType = Attacher::AttachEngine3D
  AttachmentOffset = pos=(-20.5,18.63,0) rot=(0,0,1;0rad)
  BaseFeature = -> Box2563
  Height = 1.635
  Length = 0.5
  MapMode = 5
  Placement = pos=(-20.5,18.63,0) rot=(0,0,1;0rad)
  Support = -> [XY_Plane259]
  Width = 0.25
FEATURE [PartDesign::SubtractiveBox] Box2541
  AttacherType = Attacher::AttachEngine3D
  AttachmentOffset = pos=(-21.19,18.635,-0.12) rot=(0,-1,0;0.15708rad)
  BaseFeature = -> Box2557
  Height = 0.12
  Length = 0.725
  MapMode = 5
  Placement = pos=(-21.19,18.635,-0.12) rot=(0,-1,0;0.15708rad)
  Support = -> [XY_Plane259]
  Width = 0.25
FEATURE [PartDesign::SubtractiveBox] Box2573
  AttacherType = Attacher::AttachEngine3D
  AttachmentOffset = pos=(-20.5,18.63,0) rot=(0,0,1;0rad)
  BaseFeature = -> Box2508
  Height = 1.635
  Length = 0.5
  MapMode = 5
  Placement = pos=(-20.5,18.63,0) rot=(0,0,1;0rad)
  Support = -> [XY_Plane261]
  Width = 0.25
FEATURE [PartDesign::AdditiveBox] Box2581
  AttacherType = Attacher::AttachEngine3D
  AttachmentOffset = pos=(-21.3,18.635,0) rot=(0,0,1;0rad)
  Height = 1.9
  Length = 1.3
  MapMode = 5
  Placement = pos=(-21.3,18.635,0) rot=(0,0,1;0rad)
  Support = -> [XY_Plane290]
  Width = 0.23
FEATURE [PartDesign::SubtractiveBox] Box2575
  AttacherType = Attacher::AttachEngine3D
  AttachmentOffset = pos=(-21.35,18.635,0.35) rot=(0,0,1;0rad)
  BaseFeature = -> Box2581
  Height = 1.55
  Length = 0.5
  MapMode = 5
  Placement = pos=(-21.35,18.635,0.35) rot=(0,0,1;0rad)
  Support = -> [XY_Plane290]
  Width = 0.23
FEATURE [PartDesign::SubtractiveBox] Box2525
  AttacherType = Attacher::AttachEngine3D
  AttachmentOffset = pos=(-20.5,18.63,0) rot=(0,0,1;0rad)
  BaseFeature = -> Box2575
  Height = 1.635
  Length = 0.5
  MapMode = 5
  Placement = pos=(-20.5,18.63,0) rot=(0,0,1;0rad)
  Support = -> [XY_Plane290]
  Width = 0.25
FEATURE [PartDesign::SubtractiveBox] Box2558
  AttacherType = Attacher::AttachEngine3D
  AttachmentOffset = pos=(-21.19,18.635,-0.12) rot=(0,-1,0;0.15708rad)
  BaseFeature = -> Box2525
  Height = 0.12
  Length = 0.725
  MapMode = 5
  Placement = pos=(-21.19,18.635,-0.12) rot=(0,-1,0;0.15708rad)
  Support = -> [XY_Plane290]
  Width = 0.25
FEATURE [PartDesign::SubtractiveBox] Box2553
  AttacherType = Attacher::AttachEngine3D
  AttachmentOffset = pos=(-21.5005,18.625,0.235) rot=(0,-1,0;0.174533rad)
  BaseFeature = -> Box2558
  Height = 0.3
  Length = 0.6605
  MapMode = 5
  Placement = pos=(-21.5005,18.625,0.235) rot=(0,-1,0;0.174533rad)
  Support = -> [XY_Plane290]
  Width = 0.25
FEATURE [PartDesign::Fillet] Fillet729
  Base = -> Box2553 [Edge2]
  BaseFeature = -> Box2553
  Placement = pos=(-21.5005,18.625,0.235) rot=(0,-1,0;0.174533rad)
  Radius = 0.05
  SupportTransform = false
FEATURE [PartDesign::SubtractiveBox] Box2582
  AttacherType = Attacher::AttachEngine3D
  AttachmentOffset = pos=(-21.19,18.635,-0.12) rot=(0,-1,0;0.15708rad)
  BaseFeature = -> Box2573
  Height = 0.12
  Length = 0.725
  MapMode = 5
  Placement = pos=(-21.19,18.635,-0.12) rot=(0,-1,0;0.15708rad)
  Support = -> [XY_Plane261]
  Width = 0.25
FEATURE [PartDesign::SubtractiveBox] Box2519
  AttacherType = Attacher::AttachEngine3D
  AttachmentOffset = pos=(-21.5005,18.625,0.235) rot=(0,-1,0;0.174533rad)
  BaseFeature = -> Box2582
  Height = 0.3
  Length = 0.6605
  MapMode = 5
  Placement = pos=(-21.5005,18.625,0.235) rot=(0,-1,0;0.174533rad)
  Support = -> [XY_Plane261]
  Width = 0.25
FEATURE [PartDesign::SubtractiveBox] Box2584
  AttacherType = Attacher::AttachEngine3D
  AttachmentOffset = pos=(-21.5005,18.625,0.235) rot=(0,-1,0;0.174533rad)
  BaseFeature = -> Box2549
  Height = 0.3
  Length = 0.6605
  MapMode = 5
  Placement = pos=(-21.5005,18.625,0.235) rot=(0,-1,0;0.174533rad)
  Support = -> [XY_Plane258]
  Width = 0.25
FEATURE [PartDesign::Fillet] Fillet775
  Base = -> Box2530 [Edge2]
  BaseFeature = -> Box2530
  Placement = pos=(-21.5005,18.625,0.235) rot=(0,-1,0;0.174533rad)
  Radius = 0.05
  SupportTransform = false
FEATURE [PartDesign::Fillet] Fillet776
  Base = -> Box2519 [Edge2]
  BaseFeature = -> Box2519
  Placement = pos=(-21.5005,18.625,0.235) rot=(0,-1,0;0.174533rad)
  Radius = 0.05
  SupportTransform = false
FEATURE [PartDesign::Fillet] Fillet778
  Base = -> Box2584 [Edge2]
  BaseFeature = -> Box2584
  Placement = pos=(-21.5005,18.625,0.235) rot=(0,-1,0;0.174533rad)
  Radius = 0.05
  SupportTransform = false
FEATURE [PartDesign::Fillet] Fillet716
  Base = -> Fillet778 [Edge33]
  BaseFeature = -> Fillet778
  Placement = pos=(-21.5005,18.625,0.235) rot=(0,-1,0;0.174533rad)
  Radius = 0.5
  SupportTransform = false
FEATURE [PartDesign::AdditiveBox] Box2548
  AttacherType = Attacher::AttachEngine3D
  AttachmentOffset = pos=(-21.1,18.635,0.305) rot=(0,1,0;0.785398rad)
  BaseFeature = -> Fillet716
  Height = 0.375
  Length = 0.2
  MapMode = 5
  Placement = pos=(-21.1,18.635,0.305) rot=(0,1,0;0.785398rad)
  Support = -> [XY_Plane258]
  Width = 0.23
FEATURE [PartDesign::SubtractiveCylinder] Cylinder513
  Angle = 360
  AttacherType = Attacher::AttachEngine3D
  AttachmentOffset = pos=(-21.055,18.935,0.52) rot=(1,0,0;1.5708rad)
  BaseFeature = -> Box2548
  Height = 0.375
  MapMode = 5
  Placement = pos=(-21.055,18.935,0.52) rot=(1,0,0;1.5708rad)
  Radius = 0.205
  Support = -> [XY_Plane258]
FEATURE [PartDesign::SubtractiveBox] Box2579
  AttacherType = Attacher::AttachEngine3D
  AttachmentOffset = pos=(-20.95,18.635,0.53) rot=(0,0,1;0rad)
  BaseFeature = -> Cylinder513
  Height = 0.5
  Length = 0.1
  MapMode = 5
  Placement = pos=(-20.95,18.635,0.53) rot=(0,0,1;0rad)
  Support = -> [XY_Plane258]
  Width = 0.23
FEATURE [PartDesign::SubtractiveBox] Box2550
  AttacherType = Attacher::AttachEngine3D
  AttachmentOffset = pos=(-21.15,18.635,0.297) rot=(0,-1,0;0.174533rad)
  BaseFeature = -> Box2579
  Height = 0.115
  Length = 0.115
  MapMode = 5
  Placement = pos=(-21.15,18.635,0.297) rot=(0,-1,0;0.174533rad)
  Support = -> [XY_Plane258]
  Width = 0.23
FEATURE [PartDesign::Fillet] Fillet780
  Base = -> Box2550 [Edge28]
  BaseFeature = -> Box2550
  Placement = pos=(-21.15,18.635,0.297) rot=(0,-1,0;0.174533rad)
  Radius = 0.375
  SupportTransform = false
FEATURE [PartDesign::AdditiveBox] Box2560
  AttacherType = Attacher::AttachEngine3D
  AttachmentOffset = pos=(-20.7,18.635,1.55) rot=(0,1,0;0.785398rad)
  BaseFeature = -> Fillet780
  Height = 0.375
  Length = 0.23
  MapMode = 5
  Placement = pos=(-20.7,18.635,1.55) rot=(0,1,0;0.785398rad)
  Support = -> [XY_Plane258]
  Width = 0.23
FEATURE [PartDesign::SubtractiveCylinder] Cylinder516
  Angle = 360
  AttacherType = Attacher::AttachEngine3D
  AttachmentOffset = pos=(-20.271,18.635,1.4056) rot=(-1,0,0;1.5708rad)
  BaseFeature = -> Box2560
  Height = 0.23
  MapMode = 5
  Placement = pos=(-20.271,18.635,1.4056) rot=(-1,0,0;1.5708rad)
  Radius = 0.23
  Support = -> [XY_Plane258]
FEATURE [PartDesign::AdditiveBox] Box2570
  AttacherType = Attacher::AttachEngine3D
  AttachmentOffset = pos=(-20.1,18.635,1.635) rot=(0,0,1;0rad)
  BaseFeature = -> Cylinder516
  Height = 0.265
  Length = 0.23
  MapMode = 5
  Placement = pos=(-20.1,18.635,1.635) rot=(0,0,1;0rad)
  Support = -> [XY_Plane258]
  Width = 0.23
FEATURE [PartDesign::Body] Body263  label="pin263"
  Group = -> [Box2547,Box2566,Box2546,Box2549,Box2584,Fillet778,Fillet716,Box2548,Cylinder513,Box2579,Box2550,Fillet780,Box2560,Cylinder516,Box2570]
  Origin = -> Origin282
  Placement = pos=(0,-5,0) rot=(0,0,1;0rad)
  Tip = -> Box2570
FEATURE [PartDesign::Fillet] Fillet784
  Base = -> Fillet729 [Edge33]
  BaseFeature = -> Fillet729
  Placement = pos=(-21.5005,18.625,0.235) rot=(0,-1,0;0.174533rad)
  Radius = 0.5
  SupportTransform = false
FEATURE [PartDesign::AdditiveBox] Box2564
  AttacherType = Attacher::AttachEngine3D
  AttachmentOffset = pos=(-21.1,18.635,0.305) rot=(0,1,0;0.785398rad)
  BaseFeature = -> Fillet784
  Height = 0.375
  Length = 0.2
  MapMode = 5
  Placement = pos=(-21.1,18.635,0.305) rot=(0,1,0;0.785398rad)
  Support = -> [XY_Plane290]
  Width = 0.23
FEATURE [PartDesign::SubtractiveCylinder] Cylinder521
  Angle = 360
  AttacherType = Attacher::AttachEngine3D
  AttachmentOffset = pos=(-21.055,18.935,0.52) rot=(1,0,0;1.5708rad)
  BaseFeature = -> Box2564
  Height = 0.375
  MapMode = 5
  Placement = pos=(-21.055,18.935,0.52) rot=(1,0,0;1.5708rad)
  Radius = 0.205
  Support = -> [XY_Plane290]
FEATURE [PartDesign::SubtractiveBox] Box2569
  AttacherType = Attacher::AttachEngine3D
  AttachmentOffset = pos=(-20.95,18.635,0.53) rot=(0,0,1;0rad)
  BaseFeature = -> Cylinder521
  Height = 0.5
  Length = 0.1
  MapMode = 5
  Placement = pos=(-20.95,18.635,0.53) rot=(0,0,1;0rad)
  Support = -> [XY_Plane290]
  Width = 0.23
FEATURE [PartDesign::SubtractiveBox] Box2561
  AttacherType = Attacher::AttachEngine3D
  AttachmentOffset = pos=(-21.15,18.635,0.297) rot=(0,-1,0;0.174533rad)
  BaseFeature = -> Box2569
  Height = 0.115
  Length = 0.115
  MapMode = 5
  Placement = pos=(-21.15,18.635,0.297) rot=(0,-1,0;0.174533rad)
  Support = -> [XY_Plane290]
  Width = 0.23
FEATURE [PartDesign::Fillet] Fillet719
  Base = -> Box2561 [Edge28]
  BaseFeature = -> Box2561
  Placement = pos=(-21.15,18.635,0.297) rot=(0,-1,0;0.174533rad)
  Radius = 0.375
  SupportTransform = false
FEATURE [PartDesign::AdditiveBox] Box2562
  AttacherType = Attacher::AttachEngine3D
  AttachmentOffset = pos=(-20.7,18.635,1.55) rot=(0,1,0;0.785398rad)
  BaseFeature = -> Fillet719
  Height = 0.375
  Length = 0.23
  MapMode = 5
  Placement = pos=(-20.7,18.635,1.55) rot=(0,1,0;0.785398rad)
  Support = -> [XY_Plane290]
  Width = 0.23
FEATURE [PartDesign::SubtractiveCylinder] Cylinder518
  Angle = 360
  AttacherType = Attacher::AttachEngine3D
  AttachmentOffset = pos=(-20.271,18.635,1.4056) rot=(-1,0,0;1.5708rad)
  BaseFeature = -> Box2562
  Height = 0.23
  MapMode = 5
  Placement = pos=(-20.271,18.635,1.4056) rot=(-1,0,0;1.5708rad)
  Radius = 0.23
  Support = -> [XY_Plane290]
FEATURE [PartDesign::AdditiveBox] Box2568
  AttacherType = Attacher::AttachEngine3D
  AttachmentOffset = pos=(-20.1,18.635,1.635) rot=(0,0,1;0rad)
  BaseFeature = -> Cylinder518
  Height = 0.265
  Length = 0.23
  MapMode = 5
  Placement = pos=(-20.1,18.635,1.635) rot=(0,0,1;0rad)
  Support = -> [XY_Plane290]
  Width = 0.23
FEATURE [PartDesign::Body] Body260  label="pin260"
  Group = -> [Box2581,Box2575,Box2525,Box2558,Box2553,Fillet729,Fillet784,Box2564,Cylinder521,Box2569,Box2561,Fillet719,Box2562,Cylinder518,Box2568]
  Origin = -> Origin279
  Placement = pos=(0,-5.5,0) rot=(0,0,1;0rad)
  Tip = -> Box2568
FEATURE [PartDesign::Fillet] Fillet785
  Base = -> Fillet775 [Edge33]
  BaseFeature = -> Fillet775
  Placement = pos=(-21.5005,18.625,0.235) rot=(0,-1,0;0.174533rad)
  Radius = 0.5
  SupportTransform = false
FEATURE [PartDesign::Fillet] Fillet786
  Base = -> Fillet776 [Edge33]
  BaseFeature = -> Fillet776
  Placement = pos=(-21.5005,18.625,0.235) rot=(0,-1,0;0.174533rad)
  Radius = 0.5
  SupportTransform = false
FEATURE [PartDesign::AdditiveBox] Box2552
  AttacherType = Attacher::AttachEngine3D
  AttachmentOffset = pos=(-21.1,18.635,0.305) rot=(0,1,0;0.785398rad)
  BaseFeature = -> Fillet786
  Height = 0.375
  Length = 0.2
  MapMode = 5
  Placement = pos=(-21.1,18.635,0.305) rot=(0,1,0;0.785398rad)
  Support = -> [XY_Plane261]
  Width = 0.23
FEATURE [PartDesign::SubtractiveCylinder] Cylinder520
  Angle = 360
  AttacherType = Attacher::AttachEngine3D
  AttachmentOffset = pos=(-21.055,18.935,0.52) rot=(1,0,0;1.5708rad)
  BaseFeature = -> Box2552
  Height = 0.375
  MapMode = 5
  Placement = pos=(-21.055,18.935,0.52) rot=(1,0,0;1.5708rad)
  Radius = 0.205
  Support = -> [XY_Plane261]
FEATURE [PartDesign::SubtractiveBox] Box2567
  AttacherType = Attacher::AttachEngine3D
  AttachmentOffset = pos=(-20.95,18.635,0.53) rot=(0,0,1;0rad)
  BaseFeature = -> Cylinder520
  Height = 0.5
  Length = 0.1
  MapMode = 5
  Placement = pos=(-20.95,18.635,0.53) rot=(0,0,1;0rad)
  Support = -> [XY_Plane261]
  Width = 0.23
FEATURE [PartDesign::SubtractiveBox] Box2585
  AttacherType = Attacher::AttachEngine3D
  AttachmentOffset = pos=(-21.15,18.635,0.297) rot=(0,-1,0;0.174533rad)
  BaseFeature = -> Box2567
  Height = 0.115
  Length = 0.115
  MapMode = 5
  Placement = pos=(-21.15,18.635,0.297) rot=(0,-1,0;0.174533rad)
  Support = -> [XY_Plane261]
  Width = 0.23
FEATURE [PartDesign::Fillet] Fillet783
  Base = -> Box2585 [Edge28]
  BaseFeature = -> Box2585
  Placement = pos=(-21.15,18.635,0.297) rot=(0,-1,0;0.174533rad)
  Radius = 0.375
  SupportTransform = false
FEATURE [PartDesign::AdditiveBox] Box2580
  AttacherType = Attacher::AttachEngine3D
  AttachmentOffset = pos=(-20.7,18.635,1.55) rot=(0,1,0;0.785398rad)
  BaseFeature = -> Fillet783
  Height = 0.375
  Length = 0.23
  MapMode = 5
  Placement = pos=(-20.7,18.635,1.55) rot=(0,1,0;0.785398rad)
  Support = -> [XY_Plane261]
  Width = 0.23
FEATURE [PartDesign::SubtractiveCylinder] Cylinder519
  Angle = 360
  AttacherType = Attacher::AttachEngine3D
  AttachmentOffset = pos=(-20.271,18.635,1.4056) rot=(-1,0,0;1.5708rad)
  BaseFeature = -> Box2580
  Height = 0.23
  MapMode = 5
  Placement = pos=(-20.271,18.635,1.4056) rot=(-1,0,0;1.5708rad)
  Radius = 0.23
  Support = -> [XY_Plane261]
FEATURE [PartDesign::AdditiveBox] Box2577
  AttacherType = Attacher::AttachEngine3D
  AttachmentOffset = pos=(-20.1,18.635,1.635) rot=(0,0,1;0rad)
  BaseFeature = -> Cylinder519
  Height = 0.265
  Length = 0.23
  MapMode = 5
  Placement = pos=(-20.1,18.635,1.635) rot=(0,0,1;0rad)
  Support = -> [XY_Plane261]
  Width = 0.23
FEATURE [PartDesign::Body] Body264  label="pin264"
  Group = -> [Box2492,Box2508,Box2573,Box2582,Box2519,Fillet776,Fillet786,Box2552,Cylinder520,Box2567,Box2585,Fillet783,Box2580,Cylinder519,Box2577]
  Origin = -> Origin274
  Placement = pos=(0,-3,0) rot=(0,0,1;0rad)
  Tip = -> Box2577
FEATURE [PartDesign::SubtractiveBox] Box2586
  AttacherType = Attacher::AttachEngine3D
  AttachmentOffset = pos=(-21.5005,18.625,0.235) rot=(0,-1,0;0.174533rad)
  BaseFeature = -> Box2541
  Height = 0.3
  Length = 0.6605
  MapMode = 5
  Placement = pos=(-21.5005,18.625,0.235) rot=(0,-1,0;0.174533rad)
  Support = -> [XY_Plane259]
  Width = 0.25
FEATURE [PartDesign::Fillet] Fillet796
  Base = -> Box2586 [Edge2]
  BaseFeature = -> Box2586
  Placement = pos=(-21.5005,18.625,0.235) rot=(0,-1,0;0.174533rad)
  Radius = 0.05
  SupportTransform = false
FEATURE [PartDesign::Fillet] Fillet728
  Base = -> Fillet796 [Edge33]
  BaseFeature = -> Fillet796
  Placement = pos=(-21.5005,18.625,0.235) rot=(0,-1,0;0.174533rad)
  Radius = 0.5
  SupportTransform = false
FEATURE [PartDesign::AdditiveBox] Box2523
  AttacherType = Attacher::AttachEngine3D
  AttachmentOffset = pos=(-21.1,18.635,0.305) rot=(0,1,0;0.785398rad)
  BaseFeature = -> Fillet728
  Height = 0.375
  Length = 0.2
  MapMode = 5
  Placement = pos=(-21.1,18.635,0.305) rot=(0,1,0;0.785398rad)
  Support = -> [XY_Plane259]
  Width = 0.23
FEATURE [PartDesign::SubtractiveCylinder] Cylinder512
  Angle = 360
  AttacherType = Attacher::AttachEngine3D
  AttachmentOffset = pos=(-21.055,18.935,0.52) rot=(1,0,0;1.5708rad)
  BaseFeature = -> Box2523
  Height = 0.375
  MapMode = 5
  Placement = pos=(-21.055,18.935,0.52) rot=(1,0,0;1.5708rad)
  Radius = 0.205
  Support = -> [XY_Plane259]
FEATURE [PartDesign::SubtractiveBox] Box2533
  AttacherType = Attacher::AttachEngine3D
  AttachmentOffset = pos=(-20.95,18.635,0.53) rot=(0,0,1;0rad)
  BaseFeature = -> Cylinder512
  Height = 0.5
  Length = 0.1
  MapMode = 5
  Placement = pos=(-20.95,18.635,0.53) rot=(0,0,1;0rad)
  Support = -> [XY_Plane259]
  Width = 0.23
FEATURE [PartDesign::SubtractiveBox] Box2559
  AttacherType = Attacher::AttachEngine3D
  AttachmentOffset = pos=(-21.15,18.635,0.297) rot=(0,-1,0;0.174533rad)
  BaseFeature = -> Box2533
  Height = 0.115
  Length = 0.115
  MapMode = 5
  Placement = pos=(-21.15,18.635,0.297) rot=(0,-1,0;0.174533rad)
  Support = -> [XY_Plane259]
  Width = 0.23
FEATURE [PartDesign::Fillet] Fillet789
  Base = -> Box2559 [Edge28]
  BaseFeature = -> Box2559
  Placement = pos=(-21.15,18.635,0.297) rot=(0,-1,0;0.174533rad)
  Radius = 0.375
  SupportTransform = false
FEATURE [PartDesign::AdditiveBox] Box2542
  AttacherType = Attacher::AttachEngine3D
  AttachmentOffset = pos=(-20.7,18.635,1.55) rot=(0,1,0;0.785398rad)
  BaseFeature = -> Fillet789
  Height = 0.375
  Length = 0.23
  MapMode = 5
  Placement = pos=(-20.7,18.635,1.55) rot=(0,1,0;0.785398rad)
  Support = -> [XY_Plane259]
  Width = 0.23
FEATURE [PartDesign::SubtractiveCylinder] Cylinder514
  Angle = 360
  AttacherType = Attacher::AttachEngine3D
  AttachmentOffset = pos=(-20.271,18.635,1.4056) rot=(-1,0,0;1.5708rad)
  BaseFeature = -> Box2542
  Height = 0.23
  MapMode = 5
  Placement = pos=(-20.271,18.635,1.4056) rot=(-1,0,0;1.5708rad)
  Radius = 0.23
  Support = -> [XY_Plane259]
FEATURE [PartDesign::AdditiveBox] Box2554
  AttacherType = Attacher::AttachEngine3D
  AttachmentOffset = pos=(-20.1,18.635,1.635) rot=(0,0,1;0rad)
  BaseFeature = -> Cylinder514
  Height = 0.265
  Length = 0.23
  MapMode = 5
  Placement = pos=(-20.1,18.635,1.635) rot=(0,0,1;0rad)
  Support = -> [XY_Plane259]
  Width = 0.23
FEATURE [PartDesign::Body] Body242  label="pin242"
  Group = -> [Box2571,Box2563,Box2557,Box2541,Box2586,Fillet796,Fillet728,Box2523,Cylinder512,Box2533,Box2559,Fillet789,Box2542,Cylinder514,Box2554]
  Origin = -> Origin267
  Placement = pos=(0,-4.5,0) rot=(0,0,1;0rad)
  Tip = -> Box2554
FEATURE [PartDesign::AdditiveBox] Box2591
  AttacherType = Attacher::AttachEngine3D
  AttachmentOffset = pos=(-21.1,18.635,0.305) rot=(0,1,0;0.785398rad)
  BaseFeature = -> Fillet785
  Height = 0.375
  Length = 0.2
  MapMode = 5
  Placement = pos=(-21.1,18.635,0.305) rot=(0,1,0;0.785398rad)
  Support = -> [XY_Plane256]
  Width = 0.23
FEATURE [PartDesign::SubtractiveCylinder] Cylinder505
  Angle = 360
  AttacherType = Attacher::AttachEngine3D
  AttachmentOffset = pos=(-21.055,18.935,0.52) rot=(1,0,0;1.5708rad)
  BaseFeature = -> Box2591
  Height = 0.375
  MapMode = 5
  Placement = pos=(-21.055,18.935,0.52) rot=(1,0,0;1.5708rad)
  Radius = 0.205
  Support = -> [XY_Plane256]
FEATURE [PartDesign::SubtractiveBox] Box2526
  AttacherType = Attacher::AttachEngine3D
  AttachmentOffset = pos=(-20.95,18.635,0.53) rot=(0,0,1;0rad)
  BaseFeature = -> Cylinder505
  Height = 0.5
  Length = 0.1
  MapMode = 5
  Placement = pos=(-20.95,18.635,0.53) rot=(0,0,1;0rad)
  Support = -> [XY_Plane256]
  Width = 0.23
FEATURE [PartDesign::SubtractiveBox] Box2516
  AttacherType = Attacher::AttachEngine3D
  AttachmentOffset = pos=(-21.15,18.635,0.297) rot=(0,-1,0;0.174533rad)
  BaseFeature = -> Box2526
  Height = 0.115
  Length = 0.115
  MapMode = 5
  Placement = pos=(-21.15,18.635,0.297) rot=(0,-1,0;0.174533rad)
  Support = -> [XY_Plane256]
  Width = 0.23
FEATURE [PartDesign::Fillet] Fillet788
  Base = -> Box2516 [Edge28]
  BaseFeature = -> Box2516
  Placement = pos=(-21.15,18.635,0.297) rot=(0,-1,0;0.174533rad)
  Radius = 0.375
  SupportTransform = false
FEATURE [PartDesign::AdditiveBox] Box2507
  AttacherType = Attacher::AttachEngine3D
  AttachmentOffset = pos=(-20.7,18.635,1.55) rot=(0,1,0;0.785398rad)
  BaseFeature = -> Fillet788
  Height = 0.375
  Length = 0.23
  MapMode = 5
  Placement = pos=(-20.7,18.635,1.55) rot=(0,1,0;0.785398rad)
  Support = -> [XY_Plane256]
  Width = 0.23
FEATURE [PartDesign::SubtractiveCylinder] Cylinder507
  Angle = 360
  AttacherType = Attacher::AttachEngine3D
  AttachmentOffset = pos=(-20.271,18.635,1.4056) rot=(-1,0,0;1.5708rad)
  BaseFeature = -> Box2507
  Height = 0.23
  MapMode = 5
  Placement = pos=(-20.271,18.635,1.4056) rot=(-1,0,0;1.5708rad)
  Radius = 0.23
  Support = -> [XY_Plane256]
FEATURE [PartDesign::AdditiveBox] Box2497
  AttacherType = Attacher::AttachEngine3D
  AttachmentOffset = pos=(-20.1,18.635,1.635) rot=(0,0,1;0rad)
  BaseFeature = -> Cylinder507
  Height = 0.265
  Length = 0.23
  MapMode = 5
  Placement = pos=(-20.1,18.635,1.635) rot=(0,0,1;0rad)
  Support = -> [XY_Plane256]
  Width = 0.23
FEATURE [PartDesign::Body] Body261  label="pin261"
  Group = -> [Box2511,Box2513,Box2565,Box2529,Box2530,Fillet775,Fillet785,Box2591,Cylinder505,Box2526,Box2516,Fillet788,Box2507,Cylinder507,Box2497]
  Origin = -> Origin283
  Placement = pos=(0,-4,0) rot=(0,0,1;0rad)
  Tip = -> Box2497
FEATURE [PartDesign::SubtractiveBox] Box2592
  AttacherType = Attacher::AttachEngine3D
  AttachmentOffset = pos=(-20.5,18.63,0) rot=(0,0,1;0rad)
  BaseFeature = -> Box2527
  Height = 1.635
  Length = 0.5
  MapMode = 5
  Placement = pos=(-20.5,18.63,0) rot=(0,0,1;0rad)
  Support = -> [XY_Plane262]
  Width = 0.25
FEATURE [PartDesign::SubtractiveBox] Box2521
  AttacherType = Attacher::AttachEngine3D
  AttachmentOffset = pos=(-21.19,18.635,-0.12) rot=(0,-1,0;0.15708rad)
  BaseFeature = -> Box2592
  Height = 0.12
  Length = 0.725
  MapMode = 5
  Placement = pos=(-21.19,18.635,-0.12) rot=(0,-1,0;0.15708rad)
  Support = -> [XY_Plane262]
  Width = 0.25
FEATURE [PartDesign::SubtractiveBox] Box2512
  AttacherType = Attacher::AttachEngine3D
  AttachmentOffset = pos=(-21.5005,18.625,0.235) rot=(0,-1,0;0.174533rad)
  BaseFeature = -> Box2521
  Height = 0.3
  Length = 0.6605
  MapMode = 5
  Placement = pos=(-21.5005,18.625,0.235) rot=(0,-1,0;0.174533rad)
  Support = -> [XY_Plane262]
  Width = 0.25
FEATURE [PartDesign::Fillet] Fillet781
  Base = -> Box2512 [Edge2]
  BaseFeature = -> Box2512
  Placement = pos=(-21.5005,18.625,0.235) rot=(0,-1,0;0.174533rad)
  Radius = 0.05
  SupportTransform = false
FEATURE [PartDesign::Fillet] Fillet718
  Base = -> Fillet781 [Edge33]
  BaseFeature = -> Fillet781
  Placement = pos=(-21.5005,18.625,0.235) rot=(0,-1,0;0.174533rad)
  Radius = 0.5
  SupportTransform = false
FEATURE [PartDesign::AdditiveBox] Box2590
  AttacherType = Attacher::AttachEngine3D
  AttachmentOffset = pos=(-21.1,18.635,0.305) rot=(0,1,0;0.785398rad)
  BaseFeature = -> Fillet718
  Height = 0.375
  Length = 0.2
  MapMode = 5
  Placement = pos=(-21.1,18.635,0.305) rot=(0,1,0;0.785398rad)
  Support = -> [XY_Plane262]
  Width = 0.23
FEATURE [PartDesign::SubtractiveCylinder] Cylinder522
  Angle = 360
  AttacherType = Attacher::AttachEngine3D
  AttachmentOffset = pos=(-21.055,18.935,0.52) rot=(1,0,0;1.5708rad)
  BaseFeature = -> Box2590
  Height = 0.375
  MapMode = 5
  Placement = pos=(-21.055,18.935,0.52) rot=(1,0,0;1.5708rad)
  Radius = 0.205
  Support = -> [XY_Plane262]
FEATURE [PartDesign::SubtractiveBox] Box2594
  AttacherType = Attacher::AttachEngine3D
  AttachmentOffset = pos=(-20.95,18.635,0.53) rot=(0,0,1;0rad)
  BaseFeature = -> Cylinder522
  Height = 0.5
  Length = 0.1
  MapMode = 5
  Placement = pos=(-20.95,18.635,0.53) rot=(0,0,1;0rad)
  Support = -> [XY_Plane262]
  Width = 0.23
FEATURE [PartDesign::SubtractiveBox] Box2578
  AttacherType = Attacher::AttachEngine3D
  AttachmentOffset = pos=(-21.15,18.635,0.297) rot=(0,-1,0;0.174533rad)
  BaseFeature = -> Box2594
  Height = 0.115
  Length = 0.115
  MapMode = 5
  Placement = pos=(-21.15,18.635,0.297) rot=(0,-1,0;0.174533rad)
  Support = -> [XY_Plane262]
  Width = 0.23
FEATURE [PartDesign::Fillet] Fillet777
  Base = -> Box2578 [Edge28]
  BaseFeature = -> Box2578
  Placement = pos=(-21.15,18.635,0.297) rot=(0,-1,0;0.174533rad)
  Radius = 0.375
  SupportTransform = false
FEATURE [PartDesign::AdditiveBox] Box2589
  AttacherType = Attacher::AttachEngine3D
  AttachmentOffset = pos=(-20.7,18.635,1.55) rot=(0,1,0;0.785398rad)
  BaseFeature = -> Fillet777
  Height = 0.375
  Length = 0.23
  MapMode = 5
  Placement = pos=(-20.7,18.635,1.55) rot=(0,1,0;0.785398rad)
  Support = -> [XY_Plane262]
  Width = 0.23
FEATURE [PartDesign::SubtractiveCylinder] Cylinder525
  Angle = 360
  AttacherType = Attacher::AttachEngine3D
  AttachmentOffset = pos=(-20.271,18.635,1.4056) rot=(-1,0,0;1.5708rad)
  BaseFeature = -> Box2589
  Height = 0.23
  MapMode = 5
  Placement = pos=(-20.271,18.635,1.4056) rot=(-1,0,0;1.5708rad)
  Radius = 0.23
  Support = -> [XY_Plane262]
FEATURE [PartDesign::AdditiveBox] Box2506
  AttacherType = Attacher::AttachEngine3D
  AttachmentOffset = pos=(-20.1,18.635,1.635) rot=(0,0,1;0rad)
  BaseFeature = -> Cylinder525
  Height = 0.265
  Length = 0.23
  MapMode = 5
  Placement = pos=(-20.1,18.635,1.635) rot=(0,0,1;0rad)
  Support = -> [XY_Plane262]
  Width = 0.23
FEATURE [PartDesign::Body] Body241  label="pin241"
  Group = -> [Box2518,Box2527,Box2592,Box2521,Box2512,Fillet781,Fillet718,Box2590,Cylinder522,Box2594,Box2578,Fillet777,Box2589,Cylinder525,Box2506]
  Origin = -> Origin271
  Placement = pos=(0,-3.5,0) rot=(0,0,1;0rad)
  Tip = -> Box2506
FEATURE [PartDesign::AdditiveBox] Box2604
  AttacherType = Attacher::AttachEngine3D
  AttachmentOffset = pos=(-21.3,18.635,0) rot=(0,0,1;0rad)
  Height = 1.9
  Length = 1.3
  MapMode = 5
  Placement = pos=(-21.3,18.635,0) rot=(0,0,1;0rad)
  Support = -> [XY_Plane257]
  Width = 0.23
FEATURE [PartDesign::SubtractiveBox] Box2596
  AttacherType = Attacher::AttachEngine3D
  AttachmentOffset = pos=(-21.35,18.635,0.35) rot=(0,0,1;0rad)
  BaseFeature = -> Box2604
  Height = 1.55
  Length = 0.5
  MapMode = 5
  Placement = pos=(-21.35,18.635,0.35) rot=(0,0,1;0rad)
  Support = -> [XY_Plane257]
  Width = 0.23
FEATURE [PartDesign::SubtractiveBox] Box2576
  AttacherType = Attacher::AttachEngine3D
  AttachmentOffset = pos=(-20.5,18.63,0) rot=(0,0,1;0rad)
  BaseFeature = -> Box2596
  Height = 1.635
  Length = 0.5
  MapMode = 5
  Placement = pos=(-20.5,18.63,0) rot=(0,0,1;0rad)
  Support = -> [XY_Plane257]
  Width = 0.25
FEATURE [PartDesign::SubtractiveBox] Box2599
  AttacherType = Attacher::AttachEngine3D
  AttachmentOffset = pos=(-21.19,18.635,-0.12) rot=(0,-1,0;0.15708rad)
  BaseFeature = -> Box2576
  Height = 0.12
  Length = 0.725
  MapMode = 5
  Placement = pos=(-21.19,18.635,-0.12) rot=(0,-1,0;0.15708rad)
  Support = -> [XY_Plane257]
  Width = 0.25
FEATURE [PartDesign::SubtractiveBox] Box2607
  AttacherType = Attacher::AttachEngine3D
  AttachmentOffset = pos=(-21.5005,18.625,0.235) rot=(0,-1,0;0.174533rad)
  BaseFeature = -> Box2599
  Height = 0.3
  Length = 0.6605
  MapMode = 5
  Placement = pos=(-21.5005,18.625,0.235) rot=(0,-1,0;0.174533rad)
  Support = -> [XY_Plane257]
  Width = 0.25
FEATURE [PartDesign::Fillet] Fillet721
  Base = -> Box2607 [Edge2]
  BaseFeature = -> Box2607
  Placement = pos=(-21.5005,18.625,0.235) rot=(0,-1,0;0.174533rad)
  Radius = 0.05
  SupportTransform = false
FEATURE [PartDesign::Fillet] Fillet724
  Base = -> Fillet721 [Edge33]
  BaseFeature = -> Fillet721
  Placement = pos=(-21.5005,18.625,0.235) rot=(0,-1,0;0.174533rad)
  Radius = 0.5
  SupportTransform = false
FEATURE [PartDesign::AdditiveBox] Box2574
  AttacherType = Attacher::AttachEngine3D
  AttachmentOffset = pos=(-21.1,18.635,0.305) rot=(0,1,0;0.785398rad)
  BaseFeature = -> Fillet724
  Height = 0.375
  Length = 0.2
  MapMode = 5
  Placement = pos=(-21.1,18.635,0.305) rot=(0,1,0;0.785398rad)
  Support = -> [XY_Plane257]
  Width = 0.23
FEATURE [PartDesign::SubtractiveCylinder] Cylinder524
  Angle = 360
  AttacherType = Attacher::AttachEngine3D
  AttachmentOffset = pos=(-21.055,18.935,0.52) rot=(1,0,0;1.5708rad)
  BaseFeature = -> Box2574
  Height = 0.375
  MapMode = 5
  Placement = pos=(-21.055,18.935,0.52) rot=(1,0,0;1.5708rad)
  Radius = 0.205
  Support = -> [XY_Plane257]
FEATURE [PartDesign::SubtractiveBox] Box2605
  AttacherType = Attacher::AttachEngine3D
  AttachmentOffset = pos=(-20.95,18.635,0.53) rot=(0,0,1;0rad)
  BaseFeature = -> Cylinder524
  Height = 0.5
  Length = 0.1
  MapMode = 5
  Placement = pos=(-20.95,18.635,0.53) rot=(0,0,1;0rad)
  Support = -> [XY_Plane257]
  Width = 0.23
FEATURE [PartDesign::SubtractiveBox] Box2598
  AttacherType = Attacher::AttachEngine3D
  AttachmentOffset = pos=(-21.15,18.635,0.297) rot=(0,-1,0;0.174533rad)
  BaseFeature = -> Box2605
  Height = 0.115
  Length = 0.115
  MapMode = 5
  Placement = pos=(-21.15,18.635,0.297) rot=(0,-1,0;0.174533rad)
  Support = -> [XY_Plane257]
  Width = 0.23
FEATURE [PartDesign::Fillet] Fillet774
  Base = -> Box2598 [Edge28]
  BaseFeature = -> Box2598
  Placement = pos=(-21.15,18.635,0.297) rot=(0,-1,0;0.174533rad)
  Radius = 0.375
  SupportTransform = false
FEATURE [PartDesign::AdditiveBox] Box2587
  AttacherType = Attacher::AttachEngine3D
  AttachmentOffset = pos=(-20.7,18.635,1.55) rot=(0,1,0;0.785398rad)
  BaseFeature = -> Fillet774
  Height = 0.375
  Length = 0.23
  MapMode = 5
  Placement = pos=(-20.7,18.635,1.55) rot=(0,1,0;0.785398rad)
  Support = -> [XY_Plane257]
  Width = 0.23
FEATURE [PartDesign::SubtractiveCylinder] Cylinder523
  Angle = 360
  AttacherType = Attacher::AttachEngine3D
  AttachmentOffset = pos=(-20.271,18.635,1.4056) rot=(-1,0,0;1.5708rad)
  BaseFeature = -> Box2587
  Height = 0.23
  MapMode = 5
  Placement = pos=(-20.271,18.635,1.4056) rot=(-1,0,0;1.5708rad)
  Radius = 0.23
  Support = -> [XY_Plane257]
FEATURE [PartDesign::AdditiveBox] Box2606
  AttacherType = Attacher::AttachEngine3D
  AttachmentOffset = pos=(-20.1,18.635,1.635) rot=(0,0,1;0rad)
  BaseFeature = -> Cylinder523
  Height = 0.265
  Length = 0.23
  MapMode = 5
  Placement = pos=(-20.1,18.635,1.635) rot=(0,0,1;0rad)
  Support = -> [XY_Plane257]
  Width = 0.23
FEATURE [PartDesign::Body] Body239  label="pin239"
  Group = -> [Box2604,Box2596,Box2576,Box2599,Box2607,Fillet721,Fillet724,Box2574,Cylinder524,Box2605,Box2598,Fillet774,Box2587,Cylinder523,Box2606]
  Origin = -> Origin276
  Placement = pos=(0,-0.5,0) rot=(0,0,1;0rad)
  Tip = -> Box2606
FEATURE [PartDesign::AdditiveBox] Box2628
  AttacherType = Attacher::AttachEngine3D
  AttachmentOffset = pos=(-21.3,18.635,0) rot=(0,0,1;0rad)
  Height = 1.9
  Length = 1.3
  MapMode = 5
  Placement = pos=(-21.3,18.635,0) rot=(0,0,1;0rad)
  Support = -> [XY_Plane292]
  Width = 0.23
FEATURE [PartDesign::SubtractiveBox] Box2600
  AttacherType = Attacher::AttachEngine3D
  AttachmentOffset = pos=(-21.35,18.635,0.35) rot=(0,0,1;0rad)
  BaseFeature = -> Box2628
  Height = 1.55
  Length = 0.5
  MapMode = 5
  Placement = pos=(-21.35,18.635,0.35) rot=(0,0,1;0rad)
  Support = -> [XY_Plane292]
  Width = 0.23
FEATURE [PartDesign::AdditiveBox] Box2629
  AttacherType = Attacher::AttachEngine3D
  AttachmentOffset = pos=(-21.3,18.635,0) rot=(0,0,1;0rad)
  Height = 1.9
  Length = 1.3
  MapMode = 5
  Placement = pos=(-21.3,18.635,0) rot=(0,0,1;0rad)
  Support = -> [XY_Plane307]
  Width = 0.23
FEATURE [PartDesign::AdditiveBox] Box2634
  AttacherType = Attacher::AttachEngine3D
  AttachmentOffset = pos=(-21.3,18.635,0) rot=(0,0,1;0rad)
  Height = 1.9
  Length = 1.3
  MapMode = 5
  Placement = pos=(-21.3,18.635,0) rot=(0,0,1;0rad)
  Support = -> [XY_Plane276]
  Width = 0.23
FEATURE [PartDesign::SubtractiveBox] Box2612
  AttacherType = Attacher::AttachEngine3D
  AttachmentOffset = pos=(-21.35,18.635,0.35) rot=(0,0,1;0rad)
  BaseFeature = -> Box2634
  Height = 1.55
  Length = 0.5
  MapMode = 5
  Placement = pos=(-21.35,18.635,0.35) rot=(0,0,1;0rad)
  Support = -> [XY_Plane276]
  Width = 0.23
FEATURE [PartDesign::AdditiveBox] Box2641
  AttacherType = Attacher::AttachEngine3D
  AttachmentOffset = pos=(-21.3,18.635,0) rot=(0,0,1;0rad)
  Height = 1.9
  Length = 1.3
  MapMode = 5
  Placement = pos=(-21.3,18.635,0) rot=(0,0,1;0rad)
  Support = -> [XY_Plane305]
  Width = 0.23
FEATURE [PartDesign::AdditiveBox] Box2647
  AttacherType = Attacher::AttachEngine3D
  AttachmentOffset = pos=(-21.3,18.635,0) rot=(0,0,1;0rad)
  Height = 1.9
  Length = 1.3
  MapMode = 5
  Placement = pos=(-21.3,18.635,0) rot=(0,0,1;0rad)
  Support = -> [XY_Plane289]
  Width = 0.23
FEATURE [PartDesign::SubtractiveBox] Box2650
  AttacherType = Attacher::AttachEngine3D
  AttachmentOffset = pos=(-21.35,18.635,0.35) rot=(0,0,1;0rad)
  BaseFeature = -> Box2641
  Height = 1.55
  Length = 0.5
  MapMode = 5
  Placement = pos=(-21.35,18.635,0.35) rot=(0,0,1;0rad)
  Support = -> [XY_Plane305]
  Width = 0.23
FEATURE [PartDesign::SubtractiveBox] Box2636
  AttacherType = Attacher::AttachEngine3D
  AttachmentOffset = pos=(-20.5,18.63,0) rot=(0,0,1;0rad)
  BaseFeature = -> Box2650
  Height = 1.635
  Length = 0.5
  MapMode = 5
  Placement = pos=(-20.5,18.63,0) rot=(0,0,1;0rad)
  Support = -> [XY_Plane305]
  Width = 0.25
FEATURE [PartDesign::SubtractiveBox] Box2635
  AttacherType = Attacher::AttachEngine3D
  AttachmentOffset = pos=(-21.19,18.635,-0.12) rot=(0,-1,0;0.15708rad)
  BaseFeature = -> Box2636
  Height = 0.12
  Length = 0.725
  MapMode = 5
  Placement = pos=(-21.19,18.635,-0.12) rot=(0,-1,0;0.15708rad)
  Support = -> [XY_Plane305]
  Width = 0.25
FEATURE [PartDesign::SubtractiveBox] Box2651
  AttacherType = Attacher::AttachEngine3D
  AttachmentOffset = pos=(-21.35,18.635,0.35) rot=(0,0,1;0rad)
  BaseFeature = -> Box2629
  Height = 1.55
  Length = 0.5
  MapMode = 5
  Placement = pos=(-21.35,18.635,0.35) rot=(0,0,1;0rad)
  Support = -> [XY_Plane307]
  Width = 0.23
FEATURE [PartDesign::SubtractiveBox] Box2638
  AttacherType = Attacher::AttachEngine3D
  AttachmentOffset = pos=(-20.5,18.63,0) rot=(0,0,1;0rad)
  BaseFeature = -> Box2651
  Height = 1.635
  Length = 0.5
  MapMode = 5
  Placement = pos=(-20.5,18.63,0) rot=(0,0,1;0rad)
  Support = -> [XY_Plane307]
  Width = 0.25
FEATURE [PartDesign::SubtractiveBox] Box2633
  AttacherType = Attacher::AttachEngine3D
  AttachmentOffset = pos=(-21.19,18.635,-0.12) rot=(0,-1,0;0.15708rad)
  BaseFeature = -> Box2638
  Height = 0.12
  Length = 0.725
  MapMode = 5
  Placement = pos=(-21.19,18.635,-0.12) rot=(0,-1,0;0.15708rad)
  Support = -> [XY_Plane307]
  Width = 0.25
FEATURE [PartDesign::SubtractiveBox] Box2644
  AttacherType = Attacher::AttachEngine3D
  AttachmentOffset = pos=(-21.5005,18.625,0.235) rot=(0,-1,0;0.174533rad)
  BaseFeature = -> Box2633
  Height = 0.3
  Length = 0.6605
  MapMode = 5
  Placement = pos=(-21.5005,18.625,0.235) rot=(0,-1,0;0.174533rad)
  Support = -> [XY_Plane307]
  Width = 0.25
FEATURE [PartDesign::Fillet] Fillet818
  Base = -> Box2644 [Edge2]
  BaseFeature = -> Box2644
  Placement = pos=(-21.5005,18.625,0.235) rot=(0,-1,0;0.174533rad)
  Radius = 0.05
  SupportTransform = false
FEATURE [PartDesign::Fillet] Fillet802
  Base = -> Fillet818 [Edge33]
  BaseFeature = -> Fillet818
  Placement = pos=(-21.5005,18.625,0.235) rot=(0,-1,0;0.174533rad)
  Radius = 0.5
  SupportTransform = false
FEATURE [PartDesign::AdditiveBox] Box2614
  AttacherType = Attacher::AttachEngine3D
  AttachmentOffset = pos=(-21.1,18.635,0.305) rot=(0,1,0;0.785398rad)
  BaseFeature = -> Fillet802
  Height = 0.375
  Length = 0.2
  MapMode = 5
  Placement = pos=(-21.1,18.635,0.305) rot=(0,1,0;0.785398rad)
  Support = -> [XY_Plane307]
  Width = 0.23
FEATURE [PartDesign::SubtractiveCylinder] Cylinder530
  Angle = 360
  AttacherType = Attacher::AttachEngine3D
  AttachmentOffset = pos=(-21.055,18.935,0.52) rot=(1,0,0;1.5708rad)
  BaseFeature = -> Box2614
  Height = 0.375
  MapMode = 5
  Placement = pos=(-21.055,18.935,0.52) rot=(1,0,0;1.5708rad)
  Radius = 0.205
  Support = -> [XY_Plane307]
FEATURE [PartDesign::SubtractiveBox] Box2655
  AttacherType = Attacher::AttachEngine3D
  AttachmentOffset = pos=(-20.95,18.635,0.53) rot=(0,0,1;0rad)
  BaseFeature = -> Cylinder530
  Height = 0.5
  Length = 0.1
  MapMode = 5
  Placement = pos=(-20.95,18.635,0.53) rot=(0,0,1;0rad)
  Support = -> [XY_Plane307]
  Width = 0.23
FEATURE [PartDesign::SubtractiveBox] Box2626
  AttacherType = Attacher::AttachEngine3D
  AttachmentOffset = pos=(-21.15,18.635,0.297) rot=(0,-1,0;0.174533rad)
  BaseFeature = -> Box2655
  Height = 0.115
  Length = 0.115
  MapMode = 5
  Placement = pos=(-21.15,18.635,0.297) rot=(0,-1,0;0.174533rad)
  Support = -> [XY_Plane307]
  Width = 0.23
FEATURE [PartDesign::Fillet] Fillet797
  Base = -> Box2626 [Edge28]
  BaseFeature = -> Box2626
  Placement = pos=(-21.15,18.635,0.297) rot=(0,-1,0;0.174533rad)
  Radius = 0.375
  SupportTransform = false
FEATURE [PartDesign::AdditiveBox] Box2640
  AttacherType = Attacher::AttachEngine3D
  AttachmentOffset = pos=(-20.7,18.635,1.55) rot=(0,1,0;0.785398rad)
  BaseFeature = -> Fillet797
  Height = 0.375
  Length = 0.23
  MapMode = 5
  Placement = pos=(-20.7,18.635,1.55) rot=(0,1,0;0.785398rad)
  Support = -> [XY_Plane307]
  Width = 0.23
FEATURE [PartDesign::SubtractiveCylinder] Cylinder529
  Angle = 360
  AttacherType = Attacher::AttachEngine3D
  AttachmentOffset = pos=(-20.271,18.635,1.4056) rot=(-1,0,0;1.5708rad)
  BaseFeature = -> Box2640
  Height = 0.23
  MapMode = 5
  Placement = pos=(-20.271,18.635,1.4056) rot=(-1,0,0;1.5708rad)
  Radius = 0.23
  Support = -> [XY_Plane307]
FEATURE [PartDesign::AdditiveBox] Box2648
  AttacherType = Attacher::AttachEngine3D
  AttachmentOffset = pos=(-20.1,18.635,1.635) rot=(0,0,1;0rad)
  BaseFeature = -> Cylinder529
  Height = 0.265
  Length = 0.23
  MapMode = 5
  Placement = pos=(-20.1,18.635,1.635) rot=(0,0,1;0rad)
  Support = -> [XY_Plane307]
  Width = 0.23
FEATURE [PartDesign::Body] Body272  label="pin272"
  Group = -> [Box2629,Box2651,Box2638,Box2633,Box2644,Fillet818,Fillet802,Box2614,Cylinder530,Box2655,Box2626,Fillet797,Box2640,Cylinder529,Box2648]
  Origin = -> Origin291
  Placement = pos=(0,-5,0) rot=(0,0,1;0rad)
  Tip = -> Box2648
FEATURE [PartDesign::SubtractiveBox] Box2656
  AttacherType = Attacher::AttachEngine3D
  AttachmentOffset = pos=(-21.35,18.635,0.35) rot=(0,0,1;0rad)
  BaseFeature = -> Box2647
  Height = 1.55
  Length = 0.5
  MapMode = 5
  Placement = pos=(-21.35,18.635,0.35) rot=(0,0,1;0rad)
  Support = -> [XY_Plane289]
  Width = 0.23
FEATURE [PartDesign::SubtractiveBox] Box2623
  AttacherType = Attacher::AttachEngine3D
  AttachmentOffset = pos=(-20.5,18.63,0) rot=(0,0,1;0rad)
  BaseFeature = -> Box2656
  Height = 1.635
  Length = 0.5
  MapMode = 5
  Placement = pos=(-20.5,18.63,0) rot=(0,0,1;0rad)
  Support = -> [XY_Plane289]
  Width = 0.25
FEATURE [PartDesign::SubtractiveBox] Box2624
  AttacherType = Attacher::AttachEngine3D
  AttachmentOffset = pos=(-21.19,18.635,-0.12) rot=(0,-1,0;0.15708rad)
  BaseFeature = -> Box2623
  Height = 0.12
  Length = 0.725
  MapMode = 5
  Placement = pos=(-21.19,18.635,-0.12) rot=(0,-1,0;0.15708rad)
  Support = -> [XY_Plane289]
  Width = 0.25
FEATURE [PartDesign::SubtractiveBox] Box2615
  AttacherType = Attacher::AttachEngine3D
  AttachmentOffset = pos=(-21.5005,18.625,0.235) rot=(0,-1,0;0.174533rad)
  BaseFeature = -> Box2624
  Height = 0.3
  Length = 0.6605
  MapMode = 5
  Placement = pos=(-21.5005,18.625,0.235) rot=(0,-1,0;0.174533rad)
  Support = -> [XY_Plane289]
  Width = 0.25
FEATURE [PartDesign::Fillet] Fillet805
  Base = -> Box2615 [Edge2]
  BaseFeature = -> Box2615
  Placement = pos=(-21.5005,18.625,0.235) rot=(0,-1,0;0.174533rad)
  Radius = 0.05
  SupportTransform = false
FEATURE [PartDesign::Fillet] Fillet825
  Base = -> Fillet805 [Edge33]
  BaseFeature = -> Fillet805
  Placement = pos=(-21.5005,18.625,0.235) rot=(0,-1,0;0.174533rad)
  Radius = 0.5
  SupportTransform = false
FEATURE [PartDesign::AdditiveBox] Box2645
  AttacherType = Attacher::AttachEngine3D
  AttachmentOffset = pos=(-21.1,18.635,0.305) rot=(0,1,0;0.785398rad)
  BaseFeature = -> Fillet825
  Height = 0.375
  Length = 0.2
  MapMode = 5
  Placement = pos=(-21.1,18.635,0.305) rot=(0,1,0;0.785398rad)
  Support = -> [XY_Plane289]
  Width = 0.23
FEATURE [PartDesign::SubtractiveCylinder] Cylinder536
  Angle = 360
  AttacherType = Attacher::AttachEngine3D
  AttachmentOffset = pos=(-21.055,18.935,0.52) rot=(1,0,0;1.5708rad)
  BaseFeature = -> Box2645
  Height = 0.375
  MapMode = 5
  Placement = pos=(-21.055,18.935,0.52) rot=(1,0,0;1.5708rad)
  Radius = 0.205
  Support = -> [XY_Plane289]
FEATURE [PartDesign::SubtractiveBox] Box2652
  AttacherType = Attacher::AttachEngine3D
  AttachmentOffset = pos=(-20.95,18.635,0.53) rot=(0,0,1;0rad)
  BaseFeature = -> Cylinder536
  Height = 0.5
  Length = 0.1
  MapMode = 5
  Placement = pos=(-20.95,18.635,0.53) rot=(0,0,1;0rad)
  Support = -> [XY_Plane289]
  Width = 0.23
FEATURE [PartDesign::SubtractiveBox] Box2646
  AttacherType = Attacher::AttachEngine3D
  AttachmentOffset = pos=(-21.15,18.635,0.297) rot=(0,-1,0;0.174533rad)
  BaseFeature = -> Box2652
  Height = 0.115
  Length = 0.115
  MapMode = 5
  Placement = pos=(-21.15,18.635,0.297) rot=(0,-1,0;0.174533rad)
  Support = -> [XY_Plane289]
  Width = 0.23
FEATURE [PartDesign::Fillet] Fillet806
  Base = -> Box2646 [Edge28]
  BaseFeature = -> Box2646
  Placement = pos=(-21.15,18.635,0.297) rot=(0,-1,0;0.174533rad)
  Radius = 0.375
  SupportTransform = false
FEATURE [PartDesign::AdditiveBox] Box2653
  AttacherType = Attacher::AttachEngine3D
  AttachmentOffset = pos=(-20.7,18.635,1.55) rot=(0,1,0;0.785398rad)
  BaseFeature = -> Fillet806
  Height = 0.375
  Length = 0.23
  MapMode = 5
  Placement = pos=(-20.7,18.635,1.55) rot=(0,1,0;0.785398rad)
  Support = -> [XY_Plane289]
  Width = 0.23
FEATURE [PartDesign::SubtractiveCylinder] Cylinder533
  Angle = 360
  AttacherType = Attacher::AttachEngine3D
  AttachmentOffset = pos=(-20.271,18.635,1.4056) rot=(-1,0,0;1.5708rad)
  BaseFeature = -> Box2653
  Height = 0.23
  MapMode = 5
  Placement = pos=(-20.271,18.635,1.4056) rot=(-1,0,0;1.5708rad)
  Radius = 0.23
  Support = -> [XY_Plane289]
FEATURE [PartDesign::AdditiveBox] Box2643
  AttacherType = Attacher::AttachEngine3D
  AttachmentOffset = pos=(-20.1,18.635,1.635) rot=(0,0,1;0rad)
  BaseFeature = -> Cylinder533
  Height = 0.265
  Length = 0.23
  MapMode = 5
  Placement = pos=(-20.1,18.635,1.635) rot=(0,0,1;0rad)
  Support = -> [XY_Plane289]
  Width = 0.23
FEATURE [PartDesign::Body] Body274  label="pin274"
  Group = -> [Box2647,Box2656,Box2623,Box2624,Box2615,Fillet805,Fillet825,Box2645,Cylinder536,Box2652,Box2646,Fillet806,Box2653,Cylinder533,Box2643]
  Origin = -> Origin300
  Placement = pos=(0,-5.5,0) rot=(0,0,1;0rad)
  Tip = -> Box2643
FEATURE [PartDesign::SubtractiveBox] Box2660
  AttacherType = Attacher::AttachEngine3D
  AttachmentOffset = pos=(-20.5,18.63,0) rot=(0,0,1;0rad)
  BaseFeature = -> Box2543
  Height = 1.635
  Length = 0.5
  MapMode = 5
  Placement = pos=(-20.5,18.63,0) rot=(0,0,1;0rad)
  Support = -> [XY_Plane255]
  Width = 0.25
FEATURE [PartDesign::SubtractiveBox] Box2540
  AttacherType = Attacher::AttachEngine3D
  AttachmentOffset = pos=(-21.19,18.635,-0.12) rot=(0,-1,0;0.15708rad)
  BaseFeature = -> Box2660
  Height = 0.12
  Length = 0.725
  MapMode = 5
  Placement = pos=(-21.19,18.635,-0.12) rot=(0,-1,0;0.15708rad)
  Support = -> [XY_Plane255]
  Width = 0.25
FEATURE [PartDesign::SubtractiveBox] Box2524
  AttacherType = Attacher::AttachEngine3D
  AttachmentOffset = pos=(-21.5005,18.625,0.235) rot=(0,-1,0;0.174533rad)
  BaseFeature = -> Box2540
  Height = 0.3
  Length = 0.6605
  MapMode = 5
  Placement = pos=(-21.5005,18.625,0.235) rot=(0,-1,0;0.174533rad)
  Support = -> [XY_Plane255]
  Width = 0.25
FEATURE [PartDesign::Fillet] Fillet725
  Base = -> Box2524 [Edge2]
  BaseFeature = -> Box2524
  Placement = pos=(-21.5005,18.625,0.235) rot=(0,-1,0;0.174533rad)
  Radius = 0.05
  SupportTransform = false
FEATURE [PartDesign::Fillet] Fillet720
  Base = -> Fillet725 [Edge33]
  BaseFeature = -> Fillet725
  Placement = pos=(-21.5005,18.625,0.235) rot=(0,-1,0;0.174533rad)
  Radius = 0.5
  SupportTransform = false
FEATURE [PartDesign::SubtractiveBox] Box2663
  AttacherType = Attacher::AttachEngine3D
  AttachmentOffset = pos=(-20.5,18.63,0) rot=(0,0,1;0rad)
  BaseFeature = -> Box2532
  Height = 1.635
  Length = 0.5
  MapMode = 5
  Placement = pos=(-20.5,18.63,0) rot=(0,0,1;0rad)
  Support = -> [XY_Plane293]
  Width = 0.25
FEATURE [PartDesign::SubtractiveBox] Box2517
  AttacherType = Attacher::AttachEngine3D
  AttachmentOffset = pos=(-21.19,18.635,-0.12) rot=(0,-1,0;0.15708rad)
  BaseFeature = -> Box2663
  Height = 0.12
  Length = 0.725
  MapMode = 5
  Placement = pos=(-21.19,18.635,-0.12) rot=(0,-1,0;0.15708rad)
  Support = -> [XY_Plane293]
  Width = 0.25
FEATURE [PartDesign::SubtractiveBox] Box2544
  AttacherType = Attacher::AttachEngine3D
  AttachmentOffset = pos=(-21.5005,18.625,0.235) rot=(0,-1,0;0.174533rad)
  BaseFeature = -> Box2517
  Height = 0.3
  Length = 0.6605
  MapMode = 5
  Placement = pos=(-21.5005,18.625,0.235) rot=(0,-1,0;0.174533rad)
  Support = -> [XY_Plane293]
  Width = 0.25
FEATURE [PartDesign::Fillet] Fillet722
  Base = -> Box2544 [Edge2]
  BaseFeature = -> Box2544
  Placement = pos=(-21.5005,18.625,0.235) rot=(0,-1,0;0.174533rad)
  Radius = 0.05
  SupportTransform = false
FEATURE [PartDesign::Fillet] Fillet715
  Base = -> Fillet722 [Edge33]
  BaseFeature = -> Fillet722
  Placement = pos=(-21.5005,18.625,0.235) rot=(0,-1,0;0.174533rad)
  Radius = 0.5
  SupportTransform = false
FEATURE [PartDesign::AdditiveBox] Box2671
  AttacherType = Attacher::AttachEngine3D
  AttachmentOffset = pos=(-21.3,18.635,0) rot=(0,0,1;0rad)
  Height = 1.9
  Length = 1.3
  MapMode = 5
  Placement = pos=(-21.3,18.635,0) rot=(0,0,1;0rad)
  Support = -> [XY_Plane260]
  Width = 0.23
FEATURE [PartDesign::SubtractiveBox] Box2661
  AttacherType = Attacher::AttachEngine3D
  AttachmentOffset = pos=(-21.35,18.635,0.35) rot=(0,0,1;0rad)
  BaseFeature = -> Box2671
  Height = 1.55
  Length = 0.5
  MapMode = 5
  Placement = pos=(-21.35,18.635,0.35) rot=(0,0,1;0rad)
  Support = -> [XY_Plane260]
  Width = 0.23
FEATURE [PartDesign::SubtractiveBox] Box2597
  AttacherType = Attacher::AttachEngine3D
  AttachmentOffset = pos=(-20.5,18.63,0) rot=(0,0,1;0rad)
  BaseFeature = -> Box2661
  Height = 1.635
  Length = 0.5
  MapMode = 5
  Placement = pos=(-20.5,18.63,0) rot=(0,0,1;0rad)
  Support = -> [XY_Plane260]
  Width = 0.25
FEATURE [PartDesign::SubtractiveBox] Box2593
  AttacherType = Attacher::AttachEngine3D
  AttachmentOffset = pos=(-21.19,18.635,-0.12) rot=(0,-1,0;0.15708rad)
  BaseFeature = -> Box2597
  Height = 0.12
  Length = 0.725
  MapMode = 5
  Placement = pos=(-21.19,18.635,-0.12) rot=(0,-1,0;0.15708rad)
  Support = -> [XY_Plane260]
  Width = 0.25
FEATURE [PartDesign::SubtractiveBox] Box2662
  AttacherType = Attacher::AttachEngine3D
  AttachmentOffset = pos=(-21.5005,18.625,0.235) rot=(0,-1,0;0.174533rad)
  BaseFeature = -> Box2593
  Height = 0.3
  Length = 0.6605
  MapMode = 5
  Placement = pos=(-21.5005,18.625,0.235) rot=(0,-1,0;0.174533rad)
  Support = -> [XY_Plane260]
  Width = 0.25
FEATURE [PartDesign::Fillet] Fillet782
  Base = -> Box2662 [Edge2]
  BaseFeature = -> Box2662
  Placement = pos=(-21.5005,18.625,0.235) rot=(0,-1,0;0.174533rad)
  Radius = 0.05
  SupportTransform = false
FEATURE [PartDesign::Fillet] Fillet713
  Base = -> Fillet782 [Edge33]
  BaseFeature = -> Fillet782
  Placement = pos=(-21.5005,18.625,0.235) rot=(0,-1,0;0.174533rad)
  Radius = 0.5
  SupportTransform = false
FEATURE [PartDesign::AdditiveBox] Box2528
  AttacherType = Attacher::AttachEngine3D
  AttachmentOffset = pos=(-21.1,18.635,0.305) rot=(0,1,0;0.785398rad)
  BaseFeature = -> Fillet713
  Height = 0.375
  Length = 0.2
  MapMode = 5
  Placement = pos=(-21.1,18.635,0.305) rot=(0,1,0;0.785398rad)
  Support = -> [XY_Plane260]
  Width = 0.23
FEATURE [PartDesign::SubtractiveCylinder] Cylinder515
  Angle = 360
  AttacherType = Attacher::AttachEngine3D
  AttachmentOffset = pos=(-21.055,18.935,0.52) rot=(1,0,0;1.5708rad)
  BaseFeature = -> Box2528
  Height = 0.375
  MapMode = 5
  Placement = pos=(-21.055,18.935,0.52) rot=(1,0,0;1.5708rad)
  Radius = 0.205
  Support = -> [XY_Plane260]
FEATURE [PartDesign::SubtractiveBox] Box2572
  AttacherType = Attacher::AttachEngine3D
  AttachmentOffset = pos=(-20.95,18.635,0.53) rot=(0,0,1;0rad)
  BaseFeature = -> Cylinder515
  Height = 0.5
  Length = 0.1
  MapMode = 5
  Placement = pos=(-20.95,18.635,0.53) rot=(0,0,1;0rad)
  Support = -> [XY_Plane260]
  Width = 0.23
FEATURE [PartDesign::SubtractiveBox] Box2555
  AttacherType = Attacher::AttachEngine3D
  AttachmentOffset = pos=(-21.15,18.635,0.297) rot=(0,-1,0;0.174533rad)
  BaseFeature = -> Box2572
  Height = 0.115
  Length = 0.115
  MapMode = 5
  Placement = pos=(-21.15,18.635,0.297) rot=(0,-1,0;0.174533rad)
  Support = -> [XY_Plane260]
  Width = 0.23
FEATURE [PartDesign::Fillet] Fillet787
  Base = -> Box2555 [Edge28]
  BaseFeature = -> Box2555
  Placement = pos=(-21.15,18.635,0.297) rot=(0,-1,0;0.174533rad)
  Radius = 0.375
  SupportTransform = false
FEATURE [PartDesign::AdditiveBox] Box2595
  AttacherType = Attacher::AttachEngine3D
  AttachmentOffset = pos=(-20.7,18.635,1.55) rot=(0,1,0;0.785398rad)
  BaseFeature = -> Fillet787
  Height = 0.375
  Length = 0.23
  MapMode = 5
  Placement = pos=(-20.7,18.635,1.55) rot=(0,1,0;0.785398rad)
  Support = -> [XY_Plane260]
  Width = 0.23
FEATURE [PartDesign::SubtractiveCylinder] Cylinder517
  Angle = 360
  AttacherType = Attacher::AttachEngine3D
  AttachmentOffset = pos=(-20.271,18.635,1.4056) rot=(-1,0,0;1.5708rad)
  BaseFeature = -> Box2595
  Height = 0.23
  MapMode = 5
  Placement = pos=(-20.271,18.635,1.4056) rot=(-1,0,0;1.5708rad)
  Radius = 0.23
  Support = -> [XY_Plane260]
FEATURE [PartDesign::AdditiveBox] Box2603
  AttacherType = Attacher::AttachEngine3D
  AttachmentOffset = pos=(-20.1,18.635,1.635) rot=(0,0,1;0rad)
  BaseFeature = -> Cylinder517
  Height = 0.265
  Length = 0.23
  MapMode = 5
  Placement = pos=(-20.1,18.635,1.635) rot=(0,0,1;0rad)
  Support = -> [XY_Plane260]
  Width = 0.23
FEATURE [PartDesign::Body] Body245  label="pin245"
  Group = -> [Box2671,Box2661,Box2597,Box2593,Box2662,Fillet782,Fillet713,Box2528,Cylinder515,Box2572,Box2555,Fillet787,Box2595,Cylinder517,Box2603]
  Origin = -> Origin278
  Tip = -> Box2603
FEATURE [PartDesign::AdditiveBox] Box2673
  AttacherType = Attacher::AttachEngine3D
  AttachmentOffset = pos=(-21.3,18.635,0) rot=(0,0,1;0rad)
  Height = 1.9
  Length = 1.3
  MapMode = 5
  Placement = pos=(-21.3,18.635,0) rot=(0,0,1;0rad)
  Support = -> [XY_Plane288]
  Width = 0.23
FEATURE [PartDesign::SubtractiveBox] Box2669
  AttacherType = Attacher::AttachEngine3D
  AttachmentOffset = pos=(-21.35,18.635,0.35) rot=(0,0,1;0rad)
  BaseFeature = -> Box2673
  Height = 1.55
  Length = 0.5
  MapMode = 5
  Placement = pos=(-21.35,18.635,0.35) rot=(0,0,1;0rad)
  Support = -> [XY_Plane288]
  Width = 0.23
FEATURE [PartDesign::SubtractiveBox] Box2588
  AttacherType = Attacher::AttachEngine3D
  AttachmentOffset = pos=(-20.5,18.63,0) rot=(0,0,1;0rad)
  BaseFeature = -> Box2669
  Height = 1.635
  Length = 0.5
  MapMode = 5
  Placement = pos=(-20.5,18.63,0) rot=(0,0,1;0rad)
  Support = -> [XY_Plane288]
  Width = 0.25
FEATURE [PartDesign::SubtractiveBox] Box2668
  AttacherType = Attacher::AttachEngine3D
  AttachmentOffset = pos=(-21.19,18.635,-0.12) rot=(0,-1,0;0.15708rad)
  BaseFeature = -> Box2588
  Height = 0.12
  Length = 0.725
  MapMode = 5
  Placement = pos=(-21.19,18.635,-0.12) rot=(0,-1,0;0.15708rad)
  Support = -> [XY_Plane288]
  Width = 0.25
FEATURE [PartDesign::SubtractiveBox] Box2665
  AttacherType = Attacher::AttachEngine3D
  AttachmentOffset = pos=(-21.5005,18.625,0.235) rot=(0,-1,0;0.174533rad)
  BaseFeature = -> Box2668
  Height = 0.3
  Length = 0.6605
  MapMode = 5
  Placement = pos=(-21.5005,18.625,0.235) rot=(0,-1,0;0.174533rad)
  Support = -> [XY_Plane288]
  Width = 0.25
FEATURE [PartDesign::Fillet] Fillet726
  Base = -> Box2665 [Edge2]
  BaseFeature = -> Box2665
  Placement = pos=(-21.5005,18.625,0.235) rot=(0,-1,0;0.174533rad)
  Radius = 0.05
  SupportTransform = false
FEATURE [PartDesign::Fillet] Fillet779
  Base = -> Fillet726 [Edge33]
  BaseFeature = -> Fillet726
  Placement = pos=(-21.5005,18.625,0.235) rot=(0,-1,0;0.174533rad)
  Radius = 0.5
  SupportTransform = false
FEATURE [PartDesign::AdditiveBox] Box2583
  AttacherType = Attacher::AttachEngine3D
  AttachmentOffset = pos=(-21.1,18.635,0.305) rot=(0,1,0;0.785398rad)
  BaseFeature = -> Fillet779
  Height = 0.375
  Length = 0.2
  MapMode = 5
  Placement = pos=(-21.1,18.635,0.305) rot=(0,1,0;0.785398rad)
  Support = -> [XY_Plane288]
  Width = 0.23
FEATURE [PartDesign::SubtractiveCylinder] Cylinder537
  Angle = 360
  AttacherType = Attacher::AttachEngine3D
  AttachmentOffset = pos=(-21.055,18.935,0.52) rot=(1,0,0;1.5708rad)
  BaseFeature = -> Box2583
  Height = 0.375
  MapMode = 5
  Placement = pos=(-21.055,18.935,0.52) rot=(1,0,0;1.5708rad)
  Radius = 0.205
  Support = -> [XY_Plane288]
FEATURE [PartDesign::SubtractiveBox] Box2667
  AttacherType = Attacher::AttachEngine3D
  AttachmentOffset = pos=(-20.95,18.635,0.53) rot=(0,0,1;0rad)
  BaseFeature = -> Cylinder537
  Height = 0.5
  Length = 0.1
  MapMode = 5
  Placement = pos=(-20.95,18.635,0.53) rot=(0,0,1;0rad)
  Support = -> [XY_Plane288]
  Width = 0.23
FEATURE [PartDesign::SubtractiveBox] Box2610
  AttacherType = Attacher::AttachEngine3D
  AttachmentOffset = pos=(-21.15,18.635,0.297) rot=(0,-1,0;0.174533rad)
  BaseFeature = -> Box2667
  Height = 0.115
  Length = 0.115
  MapMode = 5
  Placement = pos=(-21.15,18.635,0.297) rot=(0,-1,0;0.174533rad)
  Support = -> [XY_Plane288]
  Width = 0.23
FEATURE [PartDesign::Fillet] Fillet702
  Base = -> Box2610 [Edge28]
  BaseFeature = -> Box2610
  Placement = pos=(-21.15,18.635,0.297) rot=(0,-1,0;0.174533rad)
  Radius = 0.375
  SupportTransform = false
FEATURE [PartDesign::AdditiveBox] Box2608
  AttacherType = Attacher::AttachEngine3D
  AttachmentOffset = pos=(-20.7,18.635,1.55) rot=(0,1,0;0.785398rad)
  BaseFeature = -> Fillet702
  Height = 0.375
  Length = 0.23
  MapMode = 5
  Placement = pos=(-20.7,18.635,1.55) rot=(0,1,0;0.785398rad)
  Support = -> [XY_Plane288]
  Width = 0.23
FEATURE [PartDesign::SubtractiveCylinder] Cylinder538
  Angle = 360
  AttacherType = Attacher::AttachEngine3D
  AttachmentOffset = pos=(-20.271,18.635,1.4056) rot=(-1,0,0;1.5708rad)
  BaseFeature = -> Box2608
  Height = 0.23
  MapMode = 5
  Placement = pos=(-20.271,18.635,1.4056) rot=(-1,0,0;1.5708rad)
  Radius = 0.23
  Support = -> [XY_Plane288]
FEATURE [PartDesign::AdditiveBox] Box2664
  AttacherType = Attacher::AttachEngine3D
  AttachmentOffset = pos=(-20.1,18.635,1.635) rot=(0,0,1;0rad)
  BaseFeature = -> Cylinder538
  Height = 0.265
  Length = 0.23
  MapMode = 5
  Placement = pos=(-20.1,18.635,1.635) rot=(0,0,1;0rad)
  Support = -> [XY_Plane288]
  Width = 0.23
FEATURE [PartDesign::Body] Body262  label="pin262"
  Group = -> [Box2673,Box2669,Box2588,Box2668,Box2665,Fillet726,Fillet779,Box2583,Cylinder537,Box2667,Box2610,Fillet702,Box2608,Cylinder538,Box2664]
  Origin = -> Origin288
  Placement = pos=(0,-1,0) rot=(0,0,1;0rad)
  Tip = -> Box2664
FEATURE [PartDesign::AdditiveBox] Box2674
  AttacherType = Attacher::AttachEngine3D
  AttachmentOffset = pos=(-21.1,18.635,0.305) rot=(0,1,0;0.785398rad)
  BaseFeature = -> Fillet715
  Height = 0.375
  Length = 0.2
  MapMode = 5
  Placement = pos=(-21.1,18.635,0.305) rot=(0,1,0;0.785398rad)
  Support = -> [XY_Plane293]
  Width = 0.23
FEATURE [PartDesign::SubtractiveCylinder] Cylinder509
  Angle = 360
  AttacherType = Attacher::AttachEngine3D
  AttachmentOffset = pos=(-21.055,18.935,0.52) rot=(1,0,0;1.5708rad)
  BaseFeature = -> Box2674
  Height = 0.375
  MapMode = 5
  Placement = pos=(-21.055,18.935,0.52) rot=(1,0,0;1.5708rad)
  Radius = 0.205
  Support = -> [XY_Plane293]
FEATURE [PartDesign::SubtractiveBox] Box2535
  AttacherType = Attacher::AttachEngine3D
  AttachmentOffset = pos=(-20.95,18.635,0.53) rot=(0,0,1;0rad)
  BaseFeature = -> Cylinder509
  Height = 0.5
  Length = 0.1
  MapMode = 5
  Placement = pos=(-20.95,18.635,0.53) rot=(0,0,1;0rad)
  Support = -> [XY_Plane293]
  Width = 0.23
FEATURE [PartDesign::SubtractiveBox] Box2537
  AttacherType = Attacher::AttachEngine3D
  AttachmentOffset = pos=(-21.15,18.635,0.297) rot=(0,-1,0;0.174533rad)
  BaseFeature = -> Box2535
  Height = 0.115
  Length = 0.115
  MapMode = 5
  Placement = pos=(-21.15,18.635,0.297) rot=(0,-1,0;0.174533rad)
  Support = -> [XY_Plane293]
  Width = 0.23
FEATURE [PartDesign::Fillet] Fillet714
  Base = -> Box2537 [Edge28]
  BaseFeature = -> Box2537
  Placement = pos=(-21.15,18.635,0.297) rot=(0,-1,0;0.174533rad)
  Radius = 0.375
  SupportTransform = false
FEATURE [PartDesign::AdditiveBox] Box2522
  AttacherType = Attacher::AttachEngine3D
  AttachmentOffset = pos=(-20.7,18.635,1.55) rot=(0,1,0;0.785398rad)
  BaseFeature = -> Fillet714
  Height = 0.375
  Length = 0.23
  MapMode = 5
  Placement = pos=(-20.7,18.635,1.55) rot=(0,1,0;0.785398rad)
  Support = -> [XY_Plane293]
  Width = 0.23
FEATURE [PartDesign::SubtractiveCylinder] Cylinder508
  Angle = 360
  AttacherType = Attacher::AttachEngine3D
  AttachmentOffset = pos=(-20.271,18.635,1.4056) rot=(-1,0,0;1.5708rad)
  BaseFeature = -> Box2522
  Height = 0.23
  MapMode = 5
  Placement = pos=(-20.271,18.635,1.4056) rot=(-1,0,0;1.5708rad)
  Radius = 0.23
  Support = -> [XY_Plane293]
FEATURE [PartDesign::AdditiveBox] Box2534
  AttacherType = Attacher::AttachEngine3D
  AttachmentOffset = pos=(-20.1,18.635,1.635) rot=(0,0,1;0rad)
  BaseFeature = -> Cylinder508
  Height = 0.265
  Length = 0.23
  MapMode = 5
  Placement = pos=(-20.1,18.635,1.635) rot=(0,0,1;0rad)
  Support = -> [XY_Plane293]
  Width = 0.23
FEATURE [PartDesign::Body] Body244  label="pin244"
  Group = -> [Box2551,Box2532,Box2663,Box2517,Box2544,Fillet722,Fillet715,Box2674,Cylinder509,Box2535,Box2537,Fillet714,Box2522,Cylinder508,Box2534]
  Origin = -> Origin289
  Placement = pos=(0,-2.5,0) rot=(0,0,1;0rad)
  Tip = -> Box2534
FEATURE [PartDesign::AdditiveBox] Box2677
  AttacherType = Attacher::AttachEngine3D
  AttachmentOffset = pos=(-21.3,18.635,0) rot=(0,0,1;0rad)
  Height = 1.9
  Length = 1.3
  MapMode = 5
  Placement = pos=(-21.3,18.635,0) rot=(0,0,1;0rad)
  Support = -> [XY_Plane306]
  Width = 0.23
FEATURE [PartDesign::SubtractiveBox] Box2678
  AttacherType = Attacher::AttachEngine3D
  AttachmentOffset = pos=(-21.35,18.635,0.35) rot=(0,0,1;0rad)
  BaseFeature = -> Box2677
  Height = 1.55
  Length = 0.5
  MapMode = 5
  Placement = pos=(-21.35,18.635,0.35) rot=(0,0,1;0rad)
  Support = -> [XY_Plane306]
  Width = 0.23
FEATURE [PartDesign::SubtractiveBox] Box2642
  AttacherType = Attacher::AttachEngine3D
  AttachmentOffset = pos=(-20.5,18.63,0) rot=(0,0,1;0rad)
  BaseFeature = -> Box2678
  Height = 1.635
  Length = 0.5
  MapMode = 5
  Placement = pos=(-20.5,18.63,0) rot=(0,0,1;0rad)
  Support = -> [XY_Plane306]
  Width = 0.25
FEATURE [PartDesign::SubtractiveBox] Box2679
  AttacherType = Attacher::AttachEngine3D
  AttachmentOffset = pos=(-20.5,18.63,0) rot=(0,0,1;0rad)
  BaseFeature = -> Box2539
  Height = 1.635
  Length = 0.5
  MapMode = 5
  Placement = pos=(-20.5,18.63,0) rot=(0,0,1;0rad)
  Support = -> [XY_Plane291]
  Width = 0.25
FEATURE [PartDesign::SubtractiveBox] Box2659
  AttacherType = Attacher::AttachEngine3D
  AttachmentOffset = pos=(-21.19,18.635,-0.12) rot=(0,-1,0;0.15708rad)
  BaseFeature = -> Box2679
  Height = 0.12
  Length = 0.725
  MapMode = 5
  Placement = pos=(-21.19,18.635,-0.12) rot=(0,-1,0;0.15708rad)
  Support = -> [XY_Plane291]
  Width = 0.25
FEATURE [PartDesign::SubtractiveBox] Box2538
  AttacherType = Attacher::AttachEngine3D
  AttachmentOffset = pos=(-21.5005,18.625,0.235) rot=(0,-1,0;0.174533rad)
  BaseFeature = -> Box2659
  Height = 0.3
  Length = 0.6605
  MapMode = 5
  Placement = pos=(-21.5005,18.625,0.235) rot=(0,-1,0;0.174533rad)
  Support = -> [XY_Plane291]
  Width = 0.25
FEATURE [PartDesign::Fillet] Fillet730
  Base = -> Box2538 [Edge2]
  BaseFeature = -> Box2538
  Placement = pos=(-21.5005,18.625,0.235) rot=(0,-1,0;0.174533rad)
  Radius = 0.05
  SupportTransform = false
FEATURE [PartDesign::Fillet] Fillet727
  Base = -> Fillet730 [Edge33]
  BaseFeature = -> Fillet730
  Placement = pos=(-21.5005,18.625,0.235) rot=(0,-1,0;0.174533rad)
  Radius = 0.5
  SupportTransform = false
FEATURE [PartDesign::AdditiveBox] Box2680
  AttacherType = Attacher::AttachEngine3D
  AttachmentOffset = pos=(-21.3,18.635,0) rot=(0,0,1;0rad)
  Height = 1.9
  Length = 1.3
  MapMode = 5
  Placement = pos=(-21.3,18.635,0) rot=(0,0,1;0rad)
  Support = -> [XY_Plane310]
  Width = 0.23
FEATURE [PartDesign::AdditiveBox] Box2687
  AttacherType = Attacher::AttachEngine3D
  AttachmentOffset = pos=(-21.1,18.635,0.305) rot=(0,1,0;0.785398rad)
  BaseFeature = -> Fillet720
  Height = 0.375
  Length = 0.2
  MapMode = 5
  Placement = pos=(-21.1,18.635,0.305) rot=(0,1,0;0.785398rad)
  Support = -> [XY_Plane255]
  Width = 0.23
FEATURE [PartDesign::AdditiveBox] Box2688
  AttacherType = Attacher::AttachEngine3D
  AttachmentOffset = pos=(-21.3,18.635,0) rot=(0,0,1;0rad)
  Height = 1.9
  Length = 1.3
  MapMode = 5
  Placement = pos=(-21.3,18.635,0) rot=(0,0,1;0rad)
  Support = -> [XY_Plane308]
  Width = 0.23
FEATURE [PartDesign::AdditiveBox] Box2691
  AttacherType = Attacher::AttachEngine3D
  AttachmentOffset = pos=(-21.1,18.635,0.305) rot=(0,1,0;0.785398rad)
  BaseFeature = -> Fillet727
  Height = 0.375
  Length = 0.2
  MapMode = 5
  Placement = pos=(-21.1,18.635,0.305) rot=(0,1,0;0.785398rad)
  Support = -> [XY_Plane291]
  Width = 0.23
FEATURE [PartDesign::SubtractiveCylinder] Cylinder539
  Angle = 360
  AttacherType = Attacher::AttachEngine3D
  AttachmentOffset = pos=(-21.055,18.935,0.52) rot=(1,0,0;1.5708rad)
  BaseFeature = -> Box2691
  Height = 0.375
  MapMode = 5
  Placement = pos=(-21.055,18.935,0.52) rot=(1,0,0;1.5708rad)
  Radius = 0.205
  Support = -> [XY_Plane291]
FEATURE [PartDesign::SubtractiveBox] Box2672
  AttacherType = Attacher::AttachEngine3D
  AttachmentOffset = pos=(-20.95,18.635,0.53) rot=(0,0,1;0rad)
  BaseFeature = -> Cylinder539
  Height = 0.5
  Length = 0.1
  MapMode = 5
  Placement = pos=(-20.95,18.635,0.53) rot=(0,0,1;0rad)
  Support = -> [XY_Plane291]
  Width = 0.23
FEATURE [PartDesign::SubtractiveBox] Box2675
  AttacherType = Attacher::AttachEngine3D
  AttachmentOffset = pos=(-21.15,18.635,0.297) rot=(0,-1,0;0.174533rad)
  BaseFeature = -> Box2672
  Height = 0.115
  Length = 0.115
  MapMode = 5
  Placement = pos=(-21.15,18.635,0.297) rot=(0,-1,0;0.174533rad)
  Support = -> [XY_Plane291]
  Width = 0.23
FEATURE [PartDesign::Fillet] Fillet717
  Base = -> Box2675 [Edge28]
  BaseFeature = -> Box2675
  Placement = pos=(-21.15,18.635,0.297) rot=(0,-1,0;0.174533rad)
  Radius = 0.375
  SupportTransform = false
FEATURE [PartDesign::AdditiveBox] Box2686
  AttacherType = Attacher::AttachEngine3D
  AttachmentOffset = pos=(-20.7,18.635,1.55) rot=(0,1,0;0.785398rad)
  BaseFeature = -> Fillet717
  Height = 0.375
  Length = 0.23
  MapMode = 5
  Placement = pos=(-20.7,18.635,1.55) rot=(0,1,0;0.785398rad)
  Support = -> [XY_Plane291]
  Width = 0.23
FEATURE [PartDesign::SubtractiveCylinder] Cylinder510
  Angle = 360
  AttacherType = Attacher::AttachEngine3D
  AttachmentOffset = pos=(-20.271,18.635,1.4056) rot=(-1,0,0;1.5708rad)
  BaseFeature = -> Box2686
  Height = 0.23
  MapMode = 5
  Placement = pos=(-20.271,18.635,1.4056) rot=(-1,0,0;1.5708rad)
  Radius = 0.23
  Support = -> [XY_Plane291]
FEATURE [PartDesign::AdditiveBox] Box2684
  AttacherType = Attacher::AttachEngine3D
  AttachmentOffset = pos=(-20.1,18.635,1.635) rot=(0,0,1;0rad)
  BaseFeature = -> Cylinder510
  Height = 0.265
  Length = 0.23
  MapMode = 5
  Placement = pos=(-20.1,18.635,1.635) rot=(0,0,1;0rad)
  Support = -> [XY_Plane291]
  Width = 0.23
FEATURE [PartDesign::Body] Body243  label="pin243"
  Group = -> [Box2556,Box2539,Box2679,Box2659,Box2538,Fillet730,Fillet727,Box2691,Cylinder539,Box2672,Box2675,Fillet717,Box2686,Cylinder510,Box2684]
  Origin = -> Origin273
  Placement = pos=(0,-1.5,0) rot=(0,0,1;0rad)
  Tip = -> Box2684
FEATURE [PartDesign::SubtractiveCylinder] Cylinder541
  Angle = 360
  AttacherType = Attacher::AttachEngine3D
  AttachmentOffset = pos=(-21.055,18.935,0.52) rot=(1,0,0;1.5708rad)
  BaseFeature = -> Box2687
  Height = 0.375
  MapMode = 5
  Placement = pos=(-21.055,18.935,0.52) rot=(1,0,0;1.5708rad)
  Radius = 0.205
  Support = -> [XY_Plane255]
FEATURE [PartDesign::SubtractiveBox] Box2545
  AttacherType = Attacher::AttachEngine3D
  AttachmentOffset = pos=(-20.95,18.635,0.53) rot=(0,0,1;0rad)
  BaseFeature = -> Cylinder541
  Height = 0.5
  Length = 0.1
  MapMode = 5
  Placement = pos=(-20.95,18.635,0.53) rot=(0,0,1;0rad)
  Support = -> [XY_Plane255]
  Width = 0.23
FEATURE [PartDesign::SubtractiveBox] Box2520
  AttacherType = Attacher::AttachEngine3D
  AttachmentOffset = pos=(-21.15,18.635,0.297) rot=(0,-1,0;0.174533rad)
  BaseFeature = -> Box2545
  Height = 0.115
  Length = 0.115
  MapMode = 5
  Placement = pos=(-21.15,18.635,0.297) rot=(0,-1,0;0.174533rad)
  Support = -> [XY_Plane255]
  Width = 0.23
FEATURE [PartDesign::Fillet] Fillet723
  Base = -> Box2520 [Edge28]
  BaseFeature = -> Box2520
  Placement = pos=(-21.15,18.635,0.297) rot=(0,-1,0;0.174533rad)
  Radius = 0.375
  SupportTransform = false
FEATURE [PartDesign::AdditiveBox] Box2670
  AttacherType = Attacher::AttachEngine3D
  AttachmentOffset = pos=(-20.7,18.635,1.55) rot=(0,1,0;0.785398rad)
  BaseFeature = -> Fillet723
  Height = 0.375
  Length = 0.23
  MapMode = 5
  Placement = pos=(-20.7,18.635,1.55) rot=(0,1,0;0.785398rad)
  Support = -> [XY_Plane255]
  Width = 0.23
FEATURE [PartDesign::SubtractiveCylinder] Cylinder511
  Angle = 360
  AttacherType = Attacher::AttachEngine3D
  AttachmentOffset = pos=(-20.271,18.635,1.4056) rot=(-1,0,0;1.5708rad)
  BaseFeature = -> Box2670
  Height = 0.23
  MapMode = 5
  Placement = pos=(-20.271,18.635,1.4056) rot=(-1,0,0;1.5708rad)
  Radius = 0.23
  Support = -> [XY_Plane255]
FEATURE [PartDesign::AdditiveBox] Box2536
  AttacherType = Attacher::AttachEngine3D
  AttachmentOffset = pos=(-20.1,18.635,1.635) rot=(0,0,1;0rad)
  BaseFeature = -> Cylinder511
  Height = 0.265
  Length = 0.23
  MapMode = 5
  Placement = pos=(-20.1,18.635,1.635) rot=(0,0,1;0rad)
  Support = -> [XY_Plane255]
  Width = 0.23
FEATURE [PartDesign::Body] Body240  label="pin240"
  Group = -> [Box2531,Box2543,Box2660,Box2540,Box2524,Fillet725,Fillet720,Box2687,Cylinder541,Box2545,Box2520,Fillet723,Box2670,Cylinder511,Box2536]
  Origin = -> Origin287
  Placement = pos=(0,-2,0) rot=(0,0,1;0rad)
  Tip = -> Box2536
FEATURE [App::Part] Part024  label="Pin-set022"
  Group = -> [Body245,Body239,Body262,Body243,Body240,Body244,Body264,Body241,Body261,Body242,Body263,Body260]
  Origin = -> Origin261
  Placement = pos=(0,-12,0) rot=(0,0,1;0rad)
FEATURE [PartDesign::SubtractiveBox] Box2694
  AttacherType = Attacher::AttachEngine3D
  AttachmentOffset = pos=(-21.19,18.635,-0.12) rot=(0,-1,0;0.15708rad)
  BaseFeature = -> Box2642
  Height = 0.12
  Length = 0.725
  MapMode = 5
  Placement = pos=(-21.19,18.635,-0.12) rot=(0,-1,0;0.15708rad)
  Support = -> [XY_Plane306]
  Width = 0.25
FEATURE [PartDesign::SubtractiveBox] Box2695
  AttacherType = Attacher::AttachEngine3D
  AttachmentOffset = pos=(-21.5005,18.625,0.235) rot=(0,-1,0;0.174533rad)
  BaseFeature = -> Box2694
  Height = 0.3
  Length = 0.6605
  MapMode = 5
  Placement = pos=(-21.5005,18.625,0.235) rot=(0,-1,0;0.174533rad)
  Support = -> [XY_Plane306]
  Width = 0.25
FEATURE [PartDesign::Fillet] Fillet812
  Base = -> Box2695 [Edge2]
  BaseFeature = -> Box2695
  Placement = pos=(-21.5005,18.625,0.235) rot=(0,-1,0;0.174533rad)
  Radius = 0.05
  SupportTransform = false
FEATURE [PartDesign::Fillet] Fillet816
  Base = -> Fillet812 [Edge33]
  BaseFeature = -> Fillet812
  Placement = pos=(-21.5005,18.625,0.235) rot=(0,-1,0;0.174533rad)
  Radius = 0.5
  SupportTransform = false
FEATURE [PartDesign::SubtractiveBox] Box2696
  AttacherType = Attacher::AttachEngine3D
  AttachmentOffset = pos=(-21.35,18.635,0.35) rot=(0,0,1;0rad)
  BaseFeature = -> Box2680
  Height = 1.55
  Length = 0.5
  MapMode = 5
  Placement = pos=(-21.35,18.635,0.35) rot=(0,0,1;0rad)
  Support = -> [XY_Plane310]
  Width = 0.23
FEATURE [PartDesign::SubtractiveBox] Box2698
  AttacherType = Attacher::AttachEngine3D
  AttachmentOffset = pos=(-21.35,18.635,0.35) rot=(0,0,1;0rad)
  BaseFeature = -> Box2688
  Height = 1.55
  Length = 0.5
  MapMode = 5
  Placement = pos=(-21.35,18.635,0.35) rot=(0,0,1;0rad)
  Support = -> [XY_Plane308]
  Width = 0.23
FEATURE [PartDesign::SubtractiveBox] Box2654
  AttacherType = Attacher::AttachEngine3D
  AttachmentOffset = pos=(-20.5,18.63,0) rot=(0,0,1;0rad)
  BaseFeature = -> Box2698
  Height = 1.635
  Length = 0.5
  MapMode = 5
  Placement = pos=(-20.5,18.63,0) rot=(0,0,1;0rad)
  Support = -> [XY_Plane308]
  Width = 0.25
FEATURE [PartDesign::SubtractiveBox] Box2701
  AttacherType = Attacher::AttachEngine3D
  AttachmentOffset = pos=(-20.5,18.63,0) rot=(0,0,1;0rad)
  BaseFeature = -> Box2422
  Height = 1.635
  Length = 0.5
  MapMode = 5
  Placement = pos=(-20.5,18.63,0) rot=(0,0,1;0rad)
  Support = -> [XY_Plane278]
  Width = 0.25
FEATURE [PartDesign::SubtractiveBox] Box2413
  AttacherType = Attacher::AttachEngine3D
  AttachmentOffset = pos=(-21.19,18.635,-0.12) rot=(0,-1,0;0.15708rad)
  BaseFeature = -> Box2701
  Height = 0.12
  Length = 0.725
  MapMode = 5
  Placement = pos=(-21.19,18.635,-0.12) rot=(0,-1,0;0.15708rad)
  Support = -> [XY_Plane278]
  Width = 0.25
FEATURE [PartDesign::SubtractiveBox] Box2423
  AttacherType = Attacher::AttachEngine3D
  AttachmentOffset = pos=(-21.5005,18.625,0.235) rot=(0,-1,0;0.174533rad)
  BaseFeature = -> Box2413
  Height = 0.3
  Length = 0.6605
  MapMode = 5
  Placement = pos=(-21.5005,18.625,0.235) rot=(0,-1,0;0.174533rad)
  Support = -> [XY_Plane278]
  Width = 0.25
FEATURE [PartDesign::Fillet] Fillet687
  Base = -> Box2423 [Edge2]
  BaseFeature = -> Box2423
  Placement = pos=(-21.5005,18.625,0.235) rot=(0,-1,0;0.174533rad)
  Radius = 0.05
  SupportTransform = false
FEATURE [PartDesign::Fillet] Fillet689
  Base = -> Fillet687 [Edge33]
  BaseFeature = -> Fillet687
  Placement = pos=(-21.5005,18.625,0.235) rot=(0,-1,0;0.174533rad)
  Radius = 0.5
  SupportTransform = false
FEATURE [PartDesign::SubtractiveBox] Box2702
  AttacherType = Attacher::AttachEngine3D
  AttachmentOffset = pos=(-20.5,18.63,0) rot=(0,0,1;0rad)
  BaseFeature = -> Box2435
  Height = 1.635
  Length = 0.5
  MapMode = 5
  Placement = pos=(-20.5,18.63,0) rot=(0,0,1;0rad)
  Support = -> [XY_Plane274]
  Width = 0.25
FEATURE [PartDesign::SubtractiveBox] Box2703
  AttacherType = Attacher::AttachEngine3D
  AttachmentOffset = pos=(-20.5,18.63,0) rot=(0,0,1;0rad)
  BaseFeature = -> Box2429
  Height = 1.635
  Length = 0.5
  MapMode = 5
  Placement = pos=(-20.5,18.63,0) rot=(0,0,1;0rad)
  Support = -> [XY_Plane280]
  Width = 0.25
FEATURE [PartDesign::SubtractiveBox] Box2412
  AttacherType = Attacher::AttachEngine3D
  AttachmentOffset = pos=(-21.19,18.635,-0.12) rot=(0,-1,0;0.15708rad)
  BaseFeature = -> Box2703
  Height = 0.12
  Length = 0.725
  MapMode = 5
  Placement = pos=(-21.19,18.635,-0.12) rot=(0,-1,0;0.15708rad)
  Support = -> [XY_Plane280]
  Width = 0.25
FEATURE [PartDesign::SubtractiveBox] Box2427
  AttacherType = Attacher::AttachEngine3D
  AttachmentOffset = pos=(-21.5005,18.625,0.235) rot=(0,-1,0;0.174533rad)
  BaseFeature = -> Box2412
  Height = 0.3
  Length = 0.6605
  MapMode = 5
  Placement = pos=(-21.5005,18.625,0.235) rot=(0,-1,0;0.174533rad)
  Support = -> [XY_Plane280]
  Width = 0.25
FEATURE [PartDesign::Fillet] Fillet690
  Base = -> Box2427 [Edge2]
  BaseFeature = -> Box2427
  Placement = pos=(-21.5005,18.625,0.235) rot=(0,-1,0;0.174533rad)
  Radius = 0.05
  SupportTransform = false
FEATURE [PartDesign::Fillet] Fillet685
  Base = -> Fillet690 [Edge33]
  BaseFeature = -> Fillet690
  Placement = pos=(-21.5005,18.625,0.235) rot=(0,-1,0;0.174533rad)
  Radius = 0.5
  SupportTransform = false
FEATURE [PartDesign::AdditiveBox] Box2705
  AttacherType = Attacher::AttachEngine3D
  AttachmentOffset = pos=(-21.3,18.635,0) rot=(0,0,1;0rad)
  Height = 1.9
  Length = 1.3
  MapMode = 5
  Placement = pos=(-21.3,18.635,0) rot=(0,0,1;0rad)
  Support = -> [XY_Plane264]
  Width = 0.23
FEATURE [PartDesign::SubtractiveBox] Box2619
  AttacherType = Attacher::AttachEngine3D
  AttachmentOffset = pos=(-21.35,18.635,0.35) rot=(0,0,1;0rad)
  BaseFeature = -> Box2705
  Height = 1.55
  Length = 0.5
  MapMode = 5
  Placement = pos=(-21.35,18.635,0.35) rot=(0,0,1;0rad)
  Support = -> [XY_Plane264]
  Width = 0.23
FEATURE [PartDesign::AdditiveBox] Box2707
  AttacherType = Attacher::AttachEngine3D
  AttachmentOffset = pos=(-21.1,18.635,0.305) rot=(0,1,0;0.785398rad)
  BaseFeature = -> Fillet689
  Height = 0.375
  Length = 0.2
  MapMode = 5
  Placement = pos=(-21.1,18.635,0.305) rot=(0,1,0;0.785398rad)
  Support = -> [XY_Plane278]
  Width = 0.23
FEATURE [PartDesign::AdditiveBox] Box2709
  AttacherType = Attacher::AttachEngine3D
  AttachmentOffset = pos=(-21.1,18.635,0.305) rot=(0,1,0;0.785398rad)
  BaseFeature = -> Fillet685
  Height = 0.375
  Length = 0.2
  MapMode = 5
  Placement = pos=(-21.1,18.635,0.305) rot=(0,1,0;0.785398rad)
  Support = -> [XY_Plane280]
  Width = 0.23
FEATURE [PartDesign::SubtractiveCylinder] Cylinder487
  Angle = 360
  AttacherType = Attacher::AttachEngine3D
  AttachmentOffset = pos=(-21.055,18.935,0.52) rot=(1,0,0;1.5708rad)
  BaseFeature = -> Box2709
  Height = 0.375
  MapMode = 5
  Placement = pos=(-21.055,18.935,0.52) rot=(1,0,0;1.5708rad)
  Radius = 0.205
  Support = -> [XY_Plane280]
FEATURE [PartDesign::SubtractiveBox] Box2411
  AttacherType = Attacher::AttachEngine3D
  AttachmentOffset = pos=(-20.95,18.635,0.53) rot=(0,0,1;0rad)
  BaseFeature = -> Cylinder487
  Height = 0.5
  Length = 0.1
  MapMode = 5
  Placement = pos=(-20.95,18.635,0.53) rot=(0,0,1;0rad)
  Support = -> [XY_Plane280]
  Width = 0.23
FEATURE [PartDesign::SubtractiveBox] Box2425
  AttacherType = Attacher::AttachEngine3D
  AttachmentOffset = pos=(-21.15,18.635,0.297) rot=(0,-1,0;0.174533rad)
  BaseFeature = -> Box2411
  Height = 0.115
  Length = 0.115
  MapMode = 5
  Placement = pos=(-21.15,18.635,0.297) rot=(0,-1,0;0.174533rad)
  Support = -> [XY_Plane280]
  Width = 0.23
FEATURE [PartDesign::Fillet] Fillet736
  Base = -> Box2425 [Edge28]
  BaseFeature = -> Box2425
  Placement = pos=(-21.15,18.635,0.297) rot=(0,-1,0;0.174533rad)
  Radius = 0.375
  SupportTransform = false
FEATURE [PartDesign::AdditiveBox] Box2430
  AttacherType = Attacher::AttachEngine3D
  AttachmentOffset = pos=(-20.7,18.635,1.55) rot=(0,1,0;0.785398rad)
  BaseFeature = -> Fillet736
  Height = 0.375
  Length = 0.23
  MapMode = 5
  Placement = pos=(-20.7,18.635,1.55) rot=(0,1,0;0.785398rad)
  Support = -> [XY_Plane280]
  Width = 0.23
FEATURE [PartDesign::SubtractiveCylinder] Cylinder488
  Angle = 360
  AttacherType = Attacher::AttachEngine3D
  AttachmentOffset = pos=(-20.271,18.635,1.4056) rot=(-1,0,0;1.5708rad)
  BaseFeature = -> Box2430
  Height = 0.23
  MapMode = 5
  Placement = pos=(-20.271,18.635,1.4056) rot=(-1,0,0;1.5708rad)
  Radius = 0.23
  Support = -> [XY_Plane280]
FEATURE [PartDesign::AdditiveBox] Box2410
  AttacherType = Attacher::AttachEngine3D
  AttachmentOffset = pos=(-20.1,18.635,1.635) rot=(0,0,1;0rad)
  BaseFeature = -> Cylinder488
  Height = 0.265
  Length = 0.23
  MapMode = 5
  Placement = pos=(-20.1,18.635,1.635) rot=(0,0,1;0rad)
  Support = -> [XY_Plane280]
  Width = 0.23
FEATURE [PartDesign::Body] Body234  label="pin234"
  Group = -> [Box2444,Box2429,Box2703,Box2412,Box2427,Fillet690,Fillet685,Box2709,Cylinder487,Box2411,Box2425,Fillet736,Box2430,Cylinder488,Box2410]
  Origin = -> Origin286
  Placement = pos=(0,-2.5,0) rot=(0,0,1;0rad)
  Tip = -> Box2410
FEATURE [PartDesign::SubtractiveBox] Box2710
  AttacherType = Attacher::AttachEngine3D
  AttachmentOffset = pos=(-21.19,18.635,-0.12) rot=(0,-1,0;0.15708rad)
  BaseFeature = -> Box2702
  Height = 0.12
  Length = 0.725
  MapMode = 5
  Placement = pos=(-21.19,18.635,-0.12) rot=(0,-1,0;0.15708rad)
  Support = -> [XY_Plane274]
  Width = 0.25
FEATURE [PartDesign::SubtractiveBox] Box2433
  AttacherType = Attacher::AttachEngine3D
  AttachmentOffset = pos=(-21.5005,18.625,0.235) rot=(0,-1,0;0.174533rad)
  BaseFeature = -> Box2710
  Height = 0.3
  Length = 0.6605
  MapMode = 5
  Placement = pos=(-21.5005,18.625,0.235) rot=(0,-1,0;0.174533rad)
  Support = -> [XY_Plane274]
  Width = 0.25
FEATURE [PartDesign::Fillet] Fillet695
  Base = -> Box2433 [Edge2]
  BaseFeature = -> Box2433
  Placement = pos=(-21.5005,18.625,0.235) rot=(0,-1,0;0.174533rad)
  Radius = 0.05
  SupportTransform = false
FEATURE [PartDesign::Fillet] Fillet694
  Base = -> Fillet695 [Edge33]
  BaseFeature = -> Fillet695
  Placement = pos=(-21.5005,18.625,0.235) rot=(0,-1,0;0.174533rad)
  Radius = 0.5
  SupportTransform = false
FEATURE [PartDesign::SubtractiveCylinder] Cylinder547
  Angle = 360
  AttacherType = Attacher::AttachEngine3D
  AttachmentOffset = pos=(-21.055,18.935,0.52) rot=(1,0,0;1.5708rad)
  BaseFeature = -> Box2707
  Height = 0.375
  MapMode = 5
  Placement = pos=(-21.055,18.935,0.52) rot=(1,0,0;1.5708rad)
  Radius = 0.205
  Support = -> [XY_Plane278]
FEATURE [PartDesign::SubtractiveBox] Box2426
  AttacherType = Attacher::AttachEngine3D
  AttachmentOffset = pos=(-20.95,18.635,0.53) rot=(0,0,1;0rad)
  BaseFeature = -> Cylinder547
  Height = 0.5
  Length = 0.1
  MapMode = 5
  Placement = pos=(-20.95,18.635,0.53) rot=(0,0,1;0rad)
  Support = -> [XY_Plane278]
  Width = 0.23
FEATURE [PartDesign::SubtractiveBox] Box2354
  AttacherType = Attacher::AttachEngine3D
  AttachmentOffset = pos=(-21.15,18.635,0.297) rot=(0,-1,0;0.174533rad)
  BaseFeature = -> Box2426
  Height = 0.115
  Length = 0.115
  MapMode = 5
  Placement = pos=(-21.15,18.635,0.297) rot=(0,-1,0;0.174533rad)
  Support = -> [XY_Plane278]
  Width = 0.23
FEATURE [PartDesign::Fillet] Fillet758
  Base = -> Box2354 [Edge28]
  BaseFeature = -> Box2354
  Placement = pos=(-21.15,18.635,0.297) rot=(0,-1,0;0.174533rad)
  Radius = 0.375
  SupportTransform = false
FEATURE [PartDesign::AdditiveBox] Box2700
  AttacherType = Attacher::AttachEngine3D
  AttachmentOffset = pos=(-20.7,18.635,1.55) rot=(0,1,0;0.785398rad)
  BaseFeature = -> Fillet758
  Height = 0.375
  Length = 0.23
  MapMode = 5
  Placement = pos=(-20.7,18.635,1.55) rot=(0,1,0;0.785398rad)
  Support = -> [XY_Plane278]
  Width = 0.23
FEATURE [PartDesign::SubtractiveCylinder] Cylinder490
  Angle = 360
  AttacherType = Attacher::AttachEngine3D
  AttachmentOffset = pos=(-20.271,18.635,1.4056) rot=(-1,0,0;1.5708rad)
  BaseFeature = -> Box2700
  Height = 0.23
  MapMode = 5
  Placement = pos=(-20.271,18.635,1.4056) rot=(-1,0,0;1.5708rad)
  Radius = 0.23
  Support = -> [XY_Plane278]
FEATURE [PartDesign::AdditiveBox] Box2431
  AttacherType = Attacher::AttachEngine3D
  AttachmentOffset = pos=(-20.1,18.635,1.635) rot=(0,0,1;0rad)
  BaseFeature = -> Cylinder490
  Height = 0.265
  Length = 0.23
  MapMode = 5
  Placement = pos=(-20.1,18.635,1.635) rot=(0,0,1;0rad)
  Support = -> [XY_Plane278]
  Width = 0.23
FEATURE [PartDesign::Body] Body258  label="pin258"
  Group = -> [Box2428,Box2422,Box2701,Box2413,Box2423,Fillet687,Fillet689,Box2707,Cylinder547,Box2426,Box2354,Fillet758,Box2700,Cylinder490,Box2431]
  Origin = -> Origin281
  Placement = pos=(0,-2,0) rot=(0,0,1;0rad)
  Tip = -> Box2431
FEATURE [PartDesign::AdditiveBox] Box2713
  AttacherType = Attacher::AttachEngine3D
  AttachmentOffset = pos=(-21.1,18.635,0.305) rot=(0,1,0;0.785398rad)
  BaseFeature = -> Fillet694
  Height = 0.375
  Length = 0.2
  MapMode = 5
  Placement = pos=(-21.1,18.635,0.305) rot=(0,1,0;0.785398rad)
  Support = -> [XY_Plane274]
  Width = 0.23
FEATURE [PartDesign::SubtractiveCylinder] Cylinder545
  Angle = 360
  AttacherType = Attacher::AttachEngine3D
  AttachmentOffset = pos=(-21.055,18.935,0.52) rot=(1,0,0;1.5708rad)
  BaseFeature = -> Box2713
  Height = 0.375
  MapMode = 5
  Placement = pos=(-21.055,18.935,0.52) rot=(1,0,0;1.5708rad)
  Radius = 0.205
  Support = -> [XY_Plane274]
FEATURE [PartDesign::SubtractiveBox] Box2699
  AttacherType = Attacher::AttachEngine3D
  AttachmentOffset = pos=(-20.95,18.635,0.53) rot=(0,0,1;0rad)
  BaseFeature = -> Cylinder545
  Height = 0.5
  Length = 0.1
  MapMode = 5
  Placement = pos=(-20.95,18.635,0.53) rot=(0,0,1;0rad)
  Support = -> [XY_Plane274]
  Width = 0.23
FEATURE [PartDesign::SubtractiveBox] Box2704
  AttacherType = Attacher::AttachEngine3D
  AttachmentOffset = pos=(-21.15,18.635,0.297) rot=(0,-1,0;0.174533rad)
  BaseFeature = -> Box2699
  Height = 0.115
  Length = 0.115
  MapMode = 5
  Placement = pos=(-21.15,18.635,0.297) rot=(0,-1,0;0.174533rad)
  Support = -> [XY_Plane274]
  Width = 0.23
FEATURE [PartDesign::Fillet] Fillet686
  Base = -> Box2704 [Edge28]
  BaseFeature = -> Box2704
  Placement = pos=(-21.15,18.635,0.297) rot=(0,-1,0;0.174533rad)
  Radius = 0.375
  SupportTransform = false
FEATURE [PartDesign::AdditiveBox] Box2711
  AttacherType = Attacher::AttachEngine3D
  AttachmentOffset = pos=(-20.7,18.635,1.55) rot=(0,1,0;0.785398rad)
  BaseFeature = -> Fillet686
  Height = 0.375
  Length = 0.23
  MapMode = 5
  Placement = pos=(-20.7,18.635,1.55) rot=(0,1,0;0.785398rad)
  Support = -> [XY_Plane274]
  Width = 0.23
FEATURE [PartDesign::SubtractiveCylinder] Cylinder475
  Angle = 360
  AttacherType = Attacher::AttachEngine3D
  AttachmentOffset = pos=(-20.271,18.635,1.4056) rot=(-1,0,0;1.5708rad)
  BaseFeature = -> Box2711
  Height = 0.23
  MapMode = 5
  Placement = pos=(-20.271,18.635,1.4056) rot=(-1,0,0;1.5708rad)
  Radius = 0.23
  Support = -> [XY_Plane274]
FEATURE [PartDesign::AdditiveBox] Box2712
  AttacherType = Attacher::AttachEngine3D
  AttachmentOffset = pos=(-20.1,18.635,1.635) rot=(0,0,1;0rad)
  BaseFeature = -> Cylinder475
  Height = 0.265
  Length = 0.23
  MapMode = 5
  Placement = pos=(-20.1,18.635,1.635) rot=(0,0,1;0rad)
  Support = -> [XY_Plane274]
  Width = 0.23
FEATURE [PartDesign::Body] Body231  label="pin231"
  Group = -> [Box2440,Box2435,Box2702,Box2710,Box2433,Fillet695,Fillet694,Box2713,Cylinder545,Box2699,Box2704,Fillet686,Box2711,Cylinder475,Box2712]
  Origin = -> Origin275
  Placement = pos=(0,-1.5,0) rot=(0,0,1;0rad)
  Tip = -> Box2712
FEATURE [App::Part] Part025  label="Pin-set023"
  Group = -> [Body232,Body259,Body229,Body231,Body258,Body234,Body237,Body235,Body230,Body233,Body236,Body238]
  Origin = -> Origin277
  Placement = pos=(0,-6,0) rot=(0,0,1;0rad)
FEATURE [PartDesign::SubtractiveBox] Box2714
  AttacherType = Attacher::AttachEngine3D
  AttachmentOffset = pos=(-21.35,18.635,0.35) rot=(0,0,1;0rad)
  BaseFeature = -> Box2420
  Height = 1.55
  Length = 0.5
  MapMode = 5
  Placement = pos=(-21.35,18.635,0.35) rot=(0,0,1;0rad)
  Support = -> [XY_Plane253]
  Width = 0.23
FEATURE [PartDesign::SubtractiveBox] Box2347
  AttacherType = Attacher::AttachEngine3D
  AttachmentOffset = pos=(-20.5,18.63,0) rot=(0,0,1;0rad)
  BaseFeature = -> Box2714
  Height = 1.635
  Length = 0.5
  MapMode = 5
  Placement = pos=(-20.5,18.63,0) rot=(0,0,1;0rad)
  Support = -> [XY_Plane253]
  Width = 0.25
FEATURE [PartDesign::SubtractiveBox] Box2342
  AttacherType = Attacher::AttachEngine3D
  AttachmentOffset = pos=(-21.19,18.635,-0.12) rot=(0,-1,0;0.15708rad)
  BaseFeature = -> Box2347
  Height = 0.12
  Length = 0.725
  MapMode = 5
  Placement = pos=(-21.19,18.635,-0.12) rot=(0,-1,0;0.15708rad)
  Support = -> [XY_Plane253]
  Width = 0.25
FEATURE [PartDesign::SubtractiveBox] Box2418
  AttacherType = Attacher::AttachEngine3D
  AttachmentOffset = pos=(-21.5005,18.625,0.235) rot=(0,-1,0;0.174533rad)
  BaseFeature = -> Box2342
  Height = 0.3
  Length = 0.6605
  MapMode = 5
  Placement = pos=(-21.5005,18.625,0.235) rot=(0,-1,0;0.174533rad)
  Support = -> [XY_Plane253]
  Width = 0.25
FEATURE [PartDesign::Fillet] Fillet754
  Base = -> Box2418 [Edge2]
  BaseFeature = -> Box2418
  Placement = pos=(-21.5005,18.625,0.235) rot=(0,-1,0;0.174533rad)
  Radius = 0.05
  SupportTransform = false
FEATURE [PartDesign::Fillet] Fillet737
  Base = -> Fillet754 [Edge33]
  BaseFeature = -> Fillet754
  Placement = pos=(-21.5005,18.625,0.235) rot=(0,-1,0;0.174533rad)
  Radius = 0.5
  SupportTransform = false
FEATURE [PartDesign::AdditiveBox] Box2357
  AttacherType = Attacher::AttachEngine3D
  AttachmentOffset = pos=(-21.1,18.635,0.305) rot=(0,1,0;0.785398rad)
  BaseFeature = -> Fillet737
  Height = 0.375
  Length = 0.2
  MapMode = 5
  Placement = pos=(-21.1,18.635,0.305) rot=(0,1,0;0.785398rad)
  Support = -> [XY_Plane253]
  Width = 0.23
FEATURE [PartDesign::SubtractiveCylinder] Cylinder466
  Angle = 360
  AttacherType = Attacher::AttachEngine3D
  AttachmentOffset = pos=(-21.055,18.935,0.52) rot=(1,0,0;1.5708rad)
  BaseFeature = -> Box2357
  Height = 0.375
  MapMode = 5
  Placement = pos=(-21.055,18.935,0.52) rot=(1,0,0;1.5708rad)
  Radius = 0.205
  Support = -> [XY_Plane253]
FEATURE [PartDesign::SubtractiveBox] Box2334
  AttacherType = Attacher::AttachEngine3D
  AttachmentOffset = pos=(-20.95,18.635,0.53) rot=(0,0,1;0rad)
  BaseFeature = -> Cylinder466
  Height = 0.5
  Length = 0.1
  MapMode = 5
  Placement = pos=(-20.95,18.635,0.53) rot=(0,0,1;0rad)
  Support = -> [XY_Plane253]
  Width = 0.23
FEATURE [PartDesign::SubtractiveBox] Box2326
  AttacherType = Attacher::AttachEngine3D
  AttachmentOffset = pos=(-21.15,18.635,0.297) rot=(0,-1,0;0.174533rad)
  BaseFeature = -> Box2334
  Height = 0.115
  Length = 0.115
  MapMode = 5
  Placement = pos=(-21.15,18.635,0.297) rot=(0,-1,0;0.174533rad)
  Support = -> [XY_Plane253]
  Width = 0.23
FEATURE [PartDesign::Fillet] Fillet828
  Base = -> Box2326 [Edge28]
  BaseFeature = -> Box2326
  Placement = pos=(-21.15,18.635,0.297) rot=(0,-1,0;0.174533rad)
  Radius = 0.375
  SupportTransform = false
FEATURE [PartDesign::AdditiveBox] Box2355
  AttacherType = Attacher::AttachEngine3D
  AttachmentOffset = pos=(-20.7,18.635,1.55) rot=(0,1,0;0.785398rad)
  BaseFeature = -> Fillet828
  Height = 0.375
  Length = 0.23
  MapMode = 5
  Placement = pos=(-20.7,18.635,1.55) rot=(0,1,0;0.785398rad)
  Support = -> [XY_Plane253]
  Width = 0.23
FEATURE [PartDesign::SubtractiveCylinder] Cylinder473
  Angle = 360
  AttacherType = Attacher::AttachEngine3D
  AttachmentOffset = pos=(-20.271,18.635,1.4056) rot=(-1,0,0;1.5708rad)
  BaseFeature = -> Box2355
  Height = 0.23
  MapMode = 5
  Placement = pos=(-20.271,18.635,1.4056) rot=(-1,0,0;1.5708rad)
  Radius = 0.23
  Support = -> [XY_Plane253]
FEATURE [PartDesign::AdditiveBox] Box2408
  AttacherType = Attacher::AttachEngine3D
  AttachmentOffset = pos=(-20.1,18.635,1.635) rot=(0,0,1;0rad)
  BaseFeature = -> Cylinder473
  Height = 0.265
  Length = 0.23
  MapMode = 5
  Placement = pos=(-20.1,18.635,1.635) rot=(0,0,1;0rad)
  Support = -> [XY_Plane253]
  Width = 0.23
FEATURE [PartDesign::Body] Body247  label="pin247"
  Group = -> [Box2420,Box2714,Box2347,Box2342,Box2418,Fillet754,Fillet737,Box2357,Cylinder466,Box2334,Box2326,Fillet828,Box2355,Cylinder473,Box2408]
  Origin = -> Origin251
  Tip = -> Box2408
FEATURE [App::Part] Part021  label="Pin-set019"
  Group = -> [Body247,Body248,Body249,Body250,Body246,Body251,Body252,Body253,Body255,Body257,Body256,Body254]
  Origin = -> Origin260
FEATURE [PartDesign::AdditiveBox] Box2718
  AttacherType = Attacher::AttachEngine3D
  AttachmentOffset = pos=(-21.1,18.635,0.305) rot=(0,1,0;0.785398rad)
  BaseFeature = -> Fillet816
  Height = 0.375
  Length = 0.2
  MapMode = 5
  Placement = pos=(-21.1,18.635,0.305) rot=(0,1,0;0.785398rad)
  Support = -> [XY_Plane306]
  Width = 0.23
FEATURE [PartDesign::SubtractiveCylinder] Cylinder540
  Angle = 360
  AttacherType = Attacher::AttachEngine3D
  AttachmentOffset = pos=(-21.055,18.935,0.52) rot=(1,0,0;1.5708rad)
  BaseFeature = -> Box2718
  Height = 0.375
  MapMode = 5
  Placement = pos=(-21.055,18.935,0.52) rot=(1,0,0;1.5708rad)
  Radius = 0.205
  Support = -> [XY_Plane306]
FEATURE [PartDesign::SubtractiveBox] Box2692
  AttacherType = Attacher::AttachEngine3D
  AttachmentOffset = pos=(-20.95,18.635,0.53) rot=(0,0,1;0rad)
  BaseFeature = -> Cylinder540
  Height = 0.5
  Length = 0.1
  MapMode = 5
  Placement = pos=(-20.95,18.635,0.53) rot=(0,0,1;0rad)
  Support = -> [XY_Plane306]
  Width = 0.23
FEATURE [PartDesign::SubtractiveBox] Box2682
  AttacherType = Attacher::AttachEngine3D
  AttachmentOffset = pos=(-21.15,18.635,0.297) rot=(0,-1,0;0.174533rad)
  BaseFeature = -> Box2692
  Height = 0.115
  Length = 0.115
  MapMode = 5
  Placement = pos=(-21.15,18.635,0.297) rot=(0,-1,0;0.174533rad)
  Support = -> [XY_Plane306]
  Width = 0.23
FEATURE [PartDesign::Fillet] Fillet817
  Base = -> Box2682 [Edge28]
  BaseFeature = -> Box2682
  Placement = pos=(-21.15,18.635,0.297) rot=(0,-1,0;0.174533rad)
  Radius = 0.375
  SupportTransform = false
FEATURE [PartDesign::AdditiveBox] Box2683
  AttacherType = Attacher::AttachEngine3D
  AttachmentOffset = pos=(-20.7,18.635,1.55) rot=(0,1,0;0.785398rad)
  BaseFeature = -> Fillet817
  Height = 0.375
  Length = 0.23
  MapMode = 5
  Placement = pos=(-20.7,18.635,1.55) rot=(0,1,0;0.785398rad)
  Support = -> [XY_Plane306]
  Width = 0.23
FEATURE [PartDesign::SubtractiveCylinder] Cylinder542
  Angle = 360
  AttacherType = Attacher::AttachEngine3D
  AttachmentOffset = pos=(-20.271,18.635,1.4056) rot=(-1,0,0;1.5708rad)
  BaseFeature = -> Box2683
  Height = 0.23
  MapMode = 5
  Placement = pos=(-20.271,18.635,1.4056) rot=(-1,0,0;1.5708rad)
  Radius = 0.23
  Support = -> [XY_Plane306]
FEATURE [PartDesign::AdditiveBox] Box2676
  AttacherType = Attacher::AttachEngine3D
  AttachmentOffset = pos=(-20.1,18.635,1.635) rot=(0,0,1;0rad)
  BaseFeature = -> Cylinder542
  Height = 0.265
  Length = 0.23
  MapMode = 5
  Placement = pos=(-20.1,18.635,1.635) rot=(0,0,1;0rad)
  Support = -> [XY_Plane306]
  Width = 0.23
FEATURE [PartDesign::Body] Body276  label="pin276"
  Group = -> [Box2677,Box2678,Box2642,Box2694,Box2695,Fillet812,Fillet816,Box2718,Cylinder540,Box2692,Box2682,Fillet817,Box2683,Cylinder542,Box2676]
  Origin = -> Origin308
  Placement = pos=(0,-4,0) rot=(0,0,1;0rad)
  Tip = -> Box2676
FEATURE [PartDesign::SubtractiveBox] Box2721
  AttacherType = Attacher::AttachEngine3D
  AttachmentOffset = pos=(-21.19,18.635,-0.12) rot=(0,-1,0;0.15708rad)
  BaseFeature = -> Box2654
  Height = 0.12
  Length = 0.725
  MapMode = 5
  Placement = pos=(-21.19,18.635,-0.12) rot=(0,-1,0;0.15708rad)
  Support = -> [XY_Plane308]
  Width = 0.25
FEATURE [PartDesign::SubtractiveBox] Box2681
  AttacherType = Attacher::AttachEngine3D
  AttachmentOffset = pos=(-21.5005,18.625,0.235) rot=(0,-1,0;0.174533rad)
  BaseFeature = -> Box2721
  Height = 0.3
  Length = 0.6605
  MapMode = 5
  Placement = pos=(-21.5005,18.625,0.235) rot=(0,-1,0;0.174533rad)
  Support = -> [XY_Plane308]
  Width = 0.25
FEATURE [PartDesign::Fillet] Fillet826
  Base = -> Box2681 [Edge2]
  BaseFeature = -> Box2681
  Placement = pos=(-21.5005,18.625,0.235) rot=(0,-1,0;0.174533rad)
  Radius = 0.05
  SupportTransform = false
FEATURE [PartDesign::Fillet] Fillet822
  Base = -> Fillet826 [Edge33]
  BaseFeature = -> Fillet826
  Placement = pos=(-21.5005,18.625,0.235) rot=(0,-1,0;0.174533rad)
  Radius = 0.5
  SupportTransform = false
FEATURE [PartDesign::AdditiveBox] Box2627
  AttacherType = Attacher::AttachEngine3D
  AttachmentOffset = pos=(-21.1,18.635,0.305) rot=(0,1,0;0.785398rad)
  BaseFeature = -> Fillet822
  Height = 0.375
  Length = 0.2
  MapMode = 5
  Placement = pos=(-21.1,18.635,0.305) rot=(0,1,0;0.785398rad)
  Support = -> [XY_Plane308]
  Width = 0.23
FEATURE [PartDesign::SubtractiveCylinder] Cylinder532
  Angle = 360
  AttacherType = Attacher::AttachEngine3D
  AttachmentOffset = pos=(-21.055,18.935,0.52) rot=(1,0,0;1.5708rad)
  BaseFeature = -> Box2627
  Height = 0.375
  MapMode = 5
  Placement = pos=(-21.055,18.935,0.52) rot=(1,0,0;1.5708rad)
  Radius = 0.205
  Support = -> [XY_Plane308]
FEATURE [PartDesign::SubtractiveBox] Box2630
  AttacherType = Attacher::AttachEngine3D
  AttachmentOffset = pos=(-20.95,18.635,0.53) rot=(0,0,1;0rad)
  BaseFeature = -> Cylinder532
  Height = 0.5
  Length = 0.1
  MapMode = 5
  Placement = pos=(-20.95,18.635,0.53) rot=(0,0,1;0rad)
  Support = -> [XY_Plane308]
  Width = 0.23
FEATURE [PartDesign::SubtractiveBox] Box2657
  AttacherType = Attacher::AttachEngine3D
  AttachmentOffset = pos=(-21.15,18.635,0.297) rot=(0,-1,0;0.174533rad)
  BaseFeature = -> Box2630
  Height = 0.115
  Length = 0.115
  MapMode = 5
  Placement = pos=(-21.15,18.635,0.297) rot=(0,-1,0;0.174533rad)
  Support = -> [XY_Plane308]
  Width = 0.23
FEATURE [PartDesign::Fillet] Fillet819
  Base = -> Box2657 [Edge28]
  BaseFeature = -> Box2657
  Placement = pos=(-21.15,18.635,0.297) rot=(0,-1,0;0.174533rad)
  Radius = 0.375
  SupportTransform = false
FEATURE [PartDesign::AdditiveBox] Box2658
  AttacherType = Attacher::AttachEngine3D
  AttachmentOffset = pos=(-20.7,18.635,1.55) rot=(0,1,0;0.785398rad)
  BaseFeature = -> Fillet819
  Height = 0.375
  Length = 0.23
  MapMode = 5
  Placement = pos=(-20.7,18.635,1.55) rot=(0,1,0;0.785398rad)
  Support = -> [XY_Plane308]
  Width = 0.23
FEATURE [PartDesign::SubtractiveCylinder] Cylinder535
  Angle = 360
  AttacherType = Attacher::AttachEngine3D
  AttachmentOffset = pos=(-20.271,18.635,1.4056) rot=(-1,0,0;1.5708rad)
  BaseFeature = -> Box2658
  Height = 0.23
  MapMode = 5
  Placement = pos=(-20.271,18.635,1.4056) rot=(-1,0,0;1.5708rad)
  Radius = 0.23
  Support = -> [XY_Plane308]
FEATURE [PartDesign::AdditiveBox] Box2717
  AttacherType = Attacher::AttachEngine3D
  AttachmentOffset = pos=(-20.1,18.635,1.635) rot=(0,0,1;0rad)
  BaseFeature = -> Cylinder535
  Height = 0.265
  Length = 0.23
  MapMode = 5
  Placement = pos=(-20.1,18.635,1.635) rot=(0,0,1;0rad)
  Support = -> [XY_Plane308]
  Width = 0.23
FEATURE [PartDesign::Body] Body275  label="pin275"
  Group = -> [Box2688,Box2698,Box2654,Box2721,Box2681,Fillet826,Fillet822,Box2627,Cylinder532,Box2630,Box2657,Fillet819,Box2658,Cylinder535,Box2717]
  Origin = -> Origin296
  Placement = pos=(0,-3,0) rot=(0,0,1;0rad)
  Tip = -> Box2717
FEATURE [PartDesign::SubtractiveBox] Box2729
  AttacherType = Attacher::AttachEngine3D
  AttachmentOffset = pos=(-21.5005,18.625,0.235) rot=(0,-1,0;0.174533rad)
  BaseFeature = -> Box2635
  Height = 0.3
  Length = 0.6605
  MapMode = 5
  Placement = pos=(-21.5005,18.625,0.235) rot=(0,-1,0;0.174533rad)
  Support = -> [XY_Plane305]
  Width = 0.25
FEATURE [PartDesign::Fillet] Fillet823
  Base = -> Box2729 [Edge2]
  BaseFeature = -> Box2729
  Placement = pos=(-21.5005,18.625,0.235) rot=(0,-1,0;0.174533rad)
  Radius = 0.05
  SupportTransform = false
FEATURE [PartDesign::Fillet] Fillet815
  Base = -> Fillet823 [Edge33]
  BaseFeature = -> Fillet823
  Placement = pos=(-21.5005,18.625,0.235) rot=(0,-1,0;0.174533rad)
  Radius = 0.5
  SupportTransform = false
FEATURE [PartDesign::AdditiveBox] Box2613
  AttacherType = Attacher::AttachEngine3D
  AttachmentOffset = pos=(-21.1,18.635,0.305) rot=(0,1,0;0.785398rad)
  BaseFeature = -> Fillet815
  Height = 0.375
  Length = 0.2
  MapMode = 5
  Placement = pos=(-21.1,18.635,0.305) rot=(0,1,0;0.785398rad)
  Support = -> [XY_Plane305]
  Width = 0.23
FEATURE [PartDesign::SubtractiveCylinder] Cylinder527
  Angle = 360
  AttacherType = Attacher::AttachEngine3D
  AttachmentOffset = pos=(-21.055,18.935,0.52) rot=(1,0,0;1.5708rad)
  BaseFeature = -> Box2613
  Height = 0.375
  MapMode = 5
  Placement = pos=(-21.055,18.935,0.52) rot=(1,0,0;1.5708rad)
  Radius = 0.205
  Support = -> [XY_Plane305]
FEATURE [PartDesign::SubtractiveBox] Box2611
  AttacherType = Attacher::AttachEngine3D
  AttachmentOffset = pos=(-20.95,18.635,0.53) rot=(0,0,1;0rad)
  BaseFeature = -> Cylinder527
  Height = 0.5
  Length = 0.1
  MapMode = 5
  Placement = pos=(-20.95,18.635,0.53) rot=(0,0,1;0rad)
  Support = -> [XY_Plane305]
  Width = 0.23
FEATURE [PartDesign::SubtractiveBox] Box2632
  AttacherType = Attacher::AttachEngine3D
  AttachmentOffset = pos=(-21.15,18.635,0.297) rot=(0,-1,0;0.174533rad)
  BaseFeature = -> Box2611
  Height = 0.115
  Length = 0.115
  MapMode = 5
  Placement = pos=(-21.15,18.635,0.297) rot=(0,-1,0;0.174533rad)
  Support = -> [XY_Plane305]
  Width = 0.23
FEATURE [PartDesign::Fillet] Fillet827
  Base = -> Box2632 [Edge28]
  BaseFeature = -> Box2632
  Placement = pos=(-21.15,18.635,0.297) rot=(0,-1,0;0.174533rad)
  Radius = 0.375
  SupportTransform = false
FEATURE [PartDesign::AdditiveBox] Box2637
  AttacherType = Attacher::AttachEngine3D
  AttachmentOffset = pos=(-20.7,18.635,1.55) rot=(0,1,0;0.785398rad)
  BaseFeature = -> Fillet827
  Height = 0.375
  Length = 0.23
  MapMode = 5
  Placement = pos=(-20.7,18.635,1.55) rot=(0,1,0;0.785398rad)
  Support = -> [XY_Plane305]
  Width = 0.23
FEATURE [PartDesign::SubtractiveCylinder] Cylinder528
  Angle = 360
  AttacherType = Attacher::AttachEngine3D
  AttachmentOffset = pos=(-20.271,18.635,1.4056) rot=(-1,0,0;1.5708rad)
  BaseFeature = -> Box2637
  Height = 0.23
  MapMode = 5
  Placement = pos=(-20.271,18.635,1.4056) rot=(-1,0,0;1.5708rad)
  Radius = 0.23
  Support = -> [XY_Plane305]
FEATURE [PartDesign::AdditiveBox] Box2631
  AttacherType = Attacher::AttachEngine3D
  AttachmentOffset = pos=(-20.1,18.635,1.635) rot=(0,0,1;0rad)
  BaseFeature = -> Cylinder528
  Height = 0.265
  Length = 0.23
  MapMode = 5
  Placement = pos=(-20.1,18.635,1.635) rot=(0,0,1;0rad)
  Support = -> [XY_Plane305]
  Width = 0.23
FEATURE [PartDesign::Body] Body271  label="pin271"
  Group = -> [Box2641,Box2650,Box2636,Box2635,Box2729,Fillet823,Fillet815,Box2613,Cylinder527,Box2611,Box2632,Fillet827,Box2637,Cylinder528,Box2631]
  Origin = -> Origin305
  Placement = pos=(0,-4.5,0) rot=(0,0,1;0rad)
  Tip = -> Box2631
FEATURE [PartDesign::SubtractiveBox] Box2731
  AttacherType = Attacher::AttachEngine3D
  AttachmentOffset = pos=(-20.5,18.63,0) rot=(0,0,1;0rad)
  BaseFeature = -> Box2696
  Height = 1.635
  Length = 0.5
  MapMode = 5
  Placement = pos=(-20.5,18.63,0) rot=(0,0,1;0rad)
  Support = -> [XY_Plane310]
  Width = 0.25
FEATURE [PartDesign::SubtractiveBox] Box2697
  AttacherType = Attacher::AttachEngine3D
  AttachmentOffset = pos=(-21.19,18.635,-0.12) rot=(0,-1,0;0.15708rad)
  BaseFeature = -> Box2731
  Height = 0.12
  Length = 0.725
  MapMode = 5
  Placement = pos=(-21.19,18.635,-0.12) rot=(0,-1,0;0.15708rad)
  Support = -> [XY_Plane310]
  Width = 0.25
FEATURE [PartDesign::SubtractiveBox] Box2689
  AttacherType = Attacher::AttachEngine3D
  AttachmentOffset = pos=(-21.5005,18.625,0.235) rot=(0,-1,0;0.174533rad)
  BaseFeature = -> Box2697
  Height = 0.3
  Length = 0.6605
  MapMode = 5
  Placement = pos=(-21.5005,18.625,0.235) rot=(0,-1,0;0.174533rad)
  Support = -> [XY_Plane310]
  Width = 0.25
FEATURE [PartDesign::Fillet] Fillet837
  Base = -> Box2689 [Edge2]
  BaseFeature = -> Box2689
  Placement = pos=(-21.5005,18.625,0.235) rot=(0,-1,0;0.174533rad)
  Radius = 0.05
  SupportTransform = false
FEATURE [PartDesign::Fillet] Fillet813
  Base = -> Fillet837 [Edge33]
  BaseFeature = -> Fillet837
  Placement = pos=(-21.5005,18.625,0.235) rot=(0,-1,0;0.174533rad)
  Radius = 0.5
  SupportTransform = false
FEATURE [PartDesign::AdditiveBox] Box2719
  AttacherType = Attacher::AttachEngine3D
  AttachmentOffset = pos=(-21.1,18.635,0.305) rot=(0,1,0;0.785398rad)
  BaseFeature = -> Fillet813
  Height = 0.375
  Length = 0.2
  MapMode = 5
  Placement = pos=(-21.1,18.635,0.305) rot=(0,1,0;0.785398rad)
  Support = -> [XY_Plane310]
  Width = 0.23
FEATURE [PartDesign::SubtractiveCylinder] Cylinder549
  Angle = 360
  AttacherType = Attacher::AttachEngine3D
  AttachmentOffset = pos=(-21.055,18.935,0.52) rot=(1,0,0;1.5708rad)
  BaseFeature = -> Box2719
  Height = 0.375
  MapMode = 5
  Placement = pos=(-21.055,18.935,0.52) rot=(1,0,0;1.5708rad)
  Radius = 0.205
  Support = -> [XY_Plane310]
FEATURE [PartDesign::SubtractiveBox] Box2716
  AttacherType = Attacher::AttachEngine3D
  AttachmentOffset = pos=(-20.95,18.635,0.53) rot=(0,0,1;0rad)
  BaseFeature = -> Cylinder549
  Height = 0.5
  Length = 0.1
  MapMode = 5
  Placement = pos=(-20.95,18.635,0.53) rot=(0,0,1;0rad)
  Support = -> [XY_Plane310]
  Width = 0.23
FEATURE [PartDesign::SubtractiveBox] Box2666
  AttacherType = Attacher::AttachEngine3D
  AttachmentOffset = pos=(-21.15,18.635,0.297) rot=(0,-1,0;0.174533rad)
  BaseFeature = -> Box2716
  Height = 0.115
  Length = 0.115
  MapMode = 5
  Placement = pos=(-21.15,18.635,0.297) rot=(0,-1,0;0.174533rad)
  Support = -> [XY_Plane310]
  Width = 0.23
FEATURE [PartDesign::Fillet] Fillet807
  Base = -> Box2666 [Edge28]
  BaseFeature = -> Box2666
  Placement = pos=(-21.15,18.635,0.297) rot=(0,-1,0;0.174533rad)
  Radius = 0.375
  SupportTransform = false
FEATURE [PartDesign::AdditiveBox] Box2730
  AttacherType = Attacher::AttachEngine3D
  AttachmentOffset = pos=(-20.7,18.635,1.55) rot=(0,1,0;0.785398rad)
  BaseFeature = -> Fillet807
  Height = 0.375
  Length = 0.23
  MapMode = 5
  Placement = pos=(-20.7,18.635,1.55) rot=(0,1,0;0.785398rad)
  Support = -> [XY_Plane310]
  Width = 0.23
FEATURE [PartDesign::SubtractiveCylinder] Cylinder548
  Angle = 360
  AttacherType = Attacher::AttachEngine3D
  AttachmentOffset = pos=(-20.271,18.635,1.4056) rot=(-1,0,0;1.5708rad)
  BaseFeature = -> Box2730
  Height = 0.23
  MapMode = 5
  Placement = pos=(-20.271,18.635,1.4056) rot=(-1,0,0;1.5708rad)
  Radius = 0.23
  Support = -> [XY_Plane310]
FEATURE [PartDesign::AdditiveBox] Box2685
  AttacherType = Attacher::AttachEngine3D
  AttachmentOffset = pos=(-20.1,18.635,1.635) rot=(0,0,1;0rad)
  BaseFeature = -> Cylinder548
  Height = 0.265
  Length = 0.23
  MapMode = 5
  Placement = pos=(-20.1,18.635,1.635) rot=(0,0,1;0rad)
  Support = -> [XY_Plane310]
  Width = 0.23
FEATURE [PartDesign::Body] Body270  label="pin270"
  Group = -> [Box2680,Box2696,Box2731,Box2697,Box2689,Fillet837,Fillet813,Box2719,Cylinder549,Box2716,Box2666,Fillet807,Box2730,Cylinder548,Box2685]
  Origin = -> Origin307
  Placement = pos=(0,-3.5,0) rot=(0,0,1;0rad)
  Tip = -> Box2685
FEATURE [PartDesign::AdditiveBox] Box2735
  AttacherType = Attacher::AttachEngine3D
  AttachmentOffset = pos=(-21.3,18.635,0) rot=(0,0,1;0rad)
  Height = 1.9
  Length = 1.3
  MapMode = 5
  Placement = pos=(-21.3,18.635,0) rot=(0,0,1;0rad)
  Support = -> [XY_Plane303]
  Width = 0.23
FEATURE [PartDesign::SubtractiveBox] Box2734
  AttacherType = Attacher::AttachEngine3D
  AttachmentOffset = pos=(-21.35,18.635,0.35) rot=(0,0,1;0rad)
  BaseFeature = -> Box2735
  Height = 1.55
  Length = 0.5
  MapMode = 5
  Placement = pos=(-21.35,18.635,0.35) rot=(0,0,1;0rad)
  Support = -> [XY_Plane303]
  Width = 0.23
FEATURE [PartDesign::SubtractiveBox] Box2715
  AttacherType = Attacher::AttachEngine3D
  AttachmentOffset = pos=(-20.5,18.63,0) rot=(0,0,1;0rad)
  BaseFeature = -> Box2734
  Height = 1.635
  Length = 0.5
  MapMode = 5
  Placement = pos=(-20.5,18.63,0) rot=(0,0,1;0rad)
  Support = -> [XY_Plane303]
  Width = 0.25
FEATURE [PartDesign::SubtractiveBox] Box2746
  AttacherType = Attacher::AttachEngine3D
  AttachmentOffset = pos=(-21.19,18.635,-0.12) rot=(0,-1,0;0.15708rad)
  BaseFeature = -> Box2715
  Height = 0.12
  Length = 0.725
  MapMode = 5
  Placement = pos=(-21.19,18.635,-0.12) rot=(0,-1,0;0.15708rad)
  Support = -> [XY_Plane303]
  Width = 0.25
FEATURE [PartDesign::SubtractiveBox] Box2733
  AttacherType = Attacher::AttachEngine3D
  AttachmentOffset = pos=(-21.5005,18.625,0.235) rot=(0,-1,0;0.174533rad)
  BaseFeature = -> Box2746
  Height = 0.3
  Length = 0.6605
  MapMode = 5
  Placement = pos=(-21.5005,18.625,0.235) rot=(0,-1,0;0.174533rad)
  Support = -> [XY_Plane303]
  Width = 0.25
FEATURE [PartDesign::Fillet] Fillet795
  Base = -> Box2733 [Edge2]
  BaseFeature = -> Box2733
  Placement = pos=(-21.5005,18.625,0.235) rot=(0,-1,0;0.174533rad)
  Radius = 0.05
  SupportTransform = false
FEATURE [PartDesign::Fillet] Fillet799
  Base = -> Fillet795 [Edge33]
  BaseFeature = -> Fillet795
  Placement = pos=(-21.5005,18.625,0.235) rot=(0,-1,0;0.174533rad)
  Radius = 0.5
  SupportTransform = false
FEATURE [PartDesign::AdditiveBox] Box2722
  AttacherType = Attacher::AttachEngine3D
  AttachmentOffset = pos=(-21.1,18.635,0.305) rot=(0,1,0;0.785398rad)
  BaseFeature = -> Fillet799
  Height = 0.375
  Length = 0.2
  MapMode = 5
  Placement = pos=(-21.1,18.635,0.305) rot=(0,1,0;0.785398rad)
  Support = -> [XY_Plane303]
  Width = 0.23
FEATURE [PartDesign::SubtractiveCylinder] Cylinder551
  Angle = 360
  AttacherType = Attacher::AttachEngine3D
  AttachmentOffset = pos=(-21.055,18.935,0.52) rot=(1,0,0;1.5708rad)
  BaseFeature = -> Box2722
  Height = 0.375
  MapMode = 5
  Placement = pos=(-21.055,18.935,0.52) rot=(1,0,0;1.5708rad)
  Radius = 0.205
  Support = -> [XY_Plane303]
FEATURE [PartDesign::SubtractiveBox] Box2744
  AttacherType = Attacher::AttachEngine3D
  AttachmentOffset = pos=(-20.95,18.635,0.53) rot=(0,0,1;0rad)
  BaseFeature = -> Cylinder551
  Height = 0.5
  Length = 0.1
  MapMode = 5
  Placement = pos=(-20.95,18.635,0.53) rot=(0,0,1;0rad)
  Support = -> [XY_Plane303]
  Width = 0.23
FEATURE [PartDesign::SubtractiveBox] Box2726
  AttacherType = Attacher::AttachEngine3D
  AttachmentOffset = pos=(-21.15,18.635,0.297) rot=(0,-1,0;0.174533rad)
  BaseFeature = -> Box2744
  Height = 0.115
  Length = 0.115
  MapMode = 5
  Placement = pos=(-21.15,18.635,0.297) rot=(0,-1,0;0.174533rad)
  Support = -> [XY_Plane303]
  Width = 0.23
FEATURE [PartDesign::Fillet] Fillet814
  Base = -> Box2726 [Edge28]
  BaseFeature = -> Box2726
  Placement = pos=(-21.15,18.635,0.297) rot=(0,-1,0;0.174533rad)
  Radius = 0.375
  SupportTransform = false
FEATURE [PartDesign::AdditiveBox] Box2723
  AttacherType = Attacher::AttachEngine3D
  AttachmentOffset = pos=(-20.7,18.635,1.55) rot=(0,1,0;0.785398rad)
  BaseFeature = -> Fillet814
  Height = 0.375
  Length = 0.23
  MapMode = 5
  Placement = pos=(-20.7,18.635,1.55) rot=(0,1,0;0.785398rad)
  Support = -> [XY_Plane303]
  Width = 0.23
FEATURE [PartDesign::SubtractiveCylinder] Cylinder553
  Angle = 360
  AttacherType = Attacher::AttachEngine3D
  AttachmentOffset = pos=(-20.271,18.635,1.4056) rot=(-1,0,0;1.5708rad)
  BaseFeature = -> Box2723
  Height = 0.23
  MapMode = 5
  Placement = pos=(-20.271,18.635,1.4056) rot=(-1,0,0;1.5708rad)
  Radius = 0.23
  Support = -> [XY_Plane303]
FEATURE [PartDesign::AdditiveBox] Box2745
  AttacherType = Attacher::AttachEngine3D
  AttachmentOffset = pos=(-20.1,18.635,1.635) rot=(0,0,1;0rad)
  BaseFeature = -> Cylinder553
  Height = 0.265
  Length = 0.23
  MapMode = 5
  Placement = pos=(-20.1,18.635,1.635) rot=(0,0,1;0rad)
  Support = -> [XY_Plane303]
  Width = 0.23
FEATURE [PartDesign::Body] Body266  label="pin266"
  Group = -> [Box2735,Box2734,Box2715,Box2746,Box2733,Fillet795,Fillet799,Box2722,Cylinder551,Box2744,Box2726,Fillet814,Box2723,Cylinder553,Box2745]
  Origin = -> Origin290
  Placement = pos=(0,-0.5,0) rot=(0,0,1;0rad)
  Tip = -> Box2745
FEATURE [PartDesign::SubtractiveBox] Box2748
  AttacherType = Attacher::AttachEngine3D
  AttachmentOffset = pos=(-20.5,18.63,0) rot=(0,0,1;0rad)
  BaseFeature = -> Box2612
  Height = 1.635
  Length = 0.5
  MapMode = 5
  Placement = pos=(-20.5,18.63,0) rot=(0,0,1;0rad)
  Support = -> [XY_Plane276]
  Width = 0.25
FEATURE [PartDesign::SubtractiveBox] Box2728
  AttacherType = Attacher::AttachEngine3D
  AttachmentOffset = pos=(-21.19,18.635,-0.12) rot=(0,-1,0;0.15708rad)
  BaseFeature = -> Box2748
  Height = 0.12
  Length = 0.725
  MapMode = 5
  Placement = pos=(-21.19,18.635,-0.12) rot=(0,-1,0;0.15708rad)
  Support = -> [XY_Plane276]
  Width = 0.25
FEATURE [PartDesign::SubtractiveBox] Box2620
  AttacherType = Attacher::AttachEngine3D
  AttachmentOffset = pos=(-21.5005,18.625,0.235) rot=(0,-1,0;0.174533rad)
  BaseFeature = -> Box2728
  Height = 0.3
  Length = 0.6605
  MapMode = 5
  Placement = pos=(-21.5005,18.625,0.235) rot=(0,-1,0;0.174533rad)
  Support = -> [XY_Plane276]
  Width = 0.25
FEATURE [PartDesign::Fillet] Fillet791
  Base = -> Box2620 [Edge2]
  BaseFeature = -> Box2620
  Placement = pos=(-21.5005,18.625,0.235) rot=(0,-1,0;0.174533rad)
  Radius = 0.05
  SupportTransform = false
FEATURE [PartDesign::Fillet] Fillet811
  Base = -> Fillet791 [Edge33]
  BaseFeature = -> Fillet791
  Placement = pos=(-21.5005,18.625,0.235) rot=(0,-1,0;0.174533rad)
  Radius = 0.5
  SupportTransform = false
FEATURE [PartDesign::AdditiveBox] Box2749
  AttacherType = Attacher::AttachEngine3D
  AttachmentOffset = pos=(-21.3,18.635,0) rot=(0,0,1;0rad)
  Height = 1.9
  Length = 1.3
  MapMode = 5
  Placement = pos=(-21.3,18.635,0) rot=(0,0,1;0rad)
  Support = -> [XY_Plane302]
  Width = 0.23
FEATURE [PartDesign::AdditiveBox] Box2750
  AttacherType = Attacher::AttachEngine3D
  AttachmentOffset = pos=(-21.3,18.635,0) rot=(0,0,1;0rad)
  Height = 1.9
  Length = 1.3
  MapMode = 5
  Placement = pos=(-21.3,18.635,0) rot=(0,0,1;0rad)
  Support = -> [XY_Plane304]
  Width = 0.23
FEATURE [PartDesign::SubtractiveBox] Box2737
  AttacherType = Attacher::AttachEngine3D
  AttachmentOffset = pos=(-21.35,18.635,0.35) rot=(0,0,1;0rad)
  BaseFeature = -> Box2750
  Height = 1.55
  Length = 0.5
  MapMode = 5
  Placement = pos=(-21.35,18.635,0.35) rot=(0,0,1;0rad)
  Support = -> [XY_Plane304]
  Width = 0.23
FEATURE [PartDesign::SubtractiveBox] Box2732
  AttacherType = Attacher::AttachEngine3D
  AttachmentOffset = pos=(-20.5,18.63,0) rot=(0,0,1;0rad)
  BaseFeature = -> Box2737
  Height = 1.635
  Length = 0.5
  MapMode = 5
  Placement = pos=(-20.5,18.63,0) rot=(0,0,1;0rad)
  Support = -> [XY_Plane304]
  Width = 0.25
FEATURE [PartDesign::SubtractiveBox] Box2720
  AttacherType = Attacher::AttachEngine3D
  AttachmentOffset = pos=(-21.19,18.635,-0.12) rot=(0,-1,0;0.15708rad)
  BaseFeature = -> Box2732
  Height = 0.12
  Length = 0.725
  MapMode = 5
  Placement = pos=(-21.19,18.635,-0.12) rot=(0,-1,0;0.15708rad)
  Support = -> [XY_Plane304]
  Width = 0.25
FEATURE [PartDesign::SubtractiveBox] Box2741
  AttacherType = Attacher::AttachEngine3D
  AttachmentOffset = pos=(-21.5005,18.625,0.235) rot=(0,-1,0;0.174533rad)
  BaseFeature = -> Box2720
  Height = 0.3
  Length = 0.6605
  MapMode = 5
  Placement = pos=(-21.5005,18.625,0.235) rot=(0,-1,0;0.174533rad)
  Support = -> [XY_Plane304]
  Width = 0.25
FEATURE [PartDesign::Fillet] Fillet808
  Base = -> Box2741 [Edge2]
  BaseFeature = -> Box2741
  Placement = pos=(-21.5005,18.625,0.235) rot=(0,-1,0;0.174533rad)
  Radius = 0.05
  SupportTransform = false
FEATURE [PartDesign::Fillet] Fillet803
  Base = -> Fillet808 [Edge33]
  BaseFeature = -> Fillet808
  Placement = pos=(-21.5005,18.625,0.235) rot=(0,-1,0;0.174533rad)
  Radius = 0.5
  SupportTransform = false
FEATURE [PartDesign::AdditiveBox] Box2706
  AttacherType = Attacher::AttachEngine3D
  AttachmentOffset = pos=(-21.1,18.635,0.305) rot=(0,1,0;0.785398rad)
  BaseFeature = -> Fillet803
  Height = 0.375
  Length = 0.2
  MapMode = 5
  Placement = pos=(-21.1,18.635,0.305) rot=(0,1,0;0.785398rad)
  Support = -> [XY_Plane304]
  Width = 0.23
FEATURE [PartDesign::SubtractiveCylinder] Cylinder534
  Angle = 360
  AttacherType = Attacher::AttachEngine3D
  AttachmentOffset = pos=(-21.055,18.935,0.52) rot=(1,0,0;1.5708rad)
  BaseFeature = -> Box2706
  Height = 0.375
  MapMode = 5
  Placement = pos=(-21.055,18.935,0.52) rot=(1,0,0;1.5708rad)
  Radius = 0.205
  Support = -> [XY_Plane304]
FEATURE [PartDesign::SubtractiveBox] Box2649
  AttacherType = Attacher::AttachEngine3D
  AttachmentOffset = pos=(-20.95,18.635,0.53) rot=(0,0,1;0rad)
  BaseFeature = -> Cylinder534
  Height = 0.5
  Length = 0.1
  MapMode = 5
  Placement = pos=(-20.95,18.635,0.53) rot=(0,0,1;0rad)
  Support = -> [XY_Plane304]
  Width = 0.23
FEATURE [PartDesign::SubtractiveBox] Box2639
  AttacherType = Attacher::AttachEngine3D
  AttachmentOffset = pos=(-21.15,18.635,0.297) rot=(0,-1,0;0.174533rad)
  BaseFeature = -> Box2649
  Height = 0.115
  Length = 0.115
  MapMode = 5
  Placement = pos=(-21.15,18.635,0.297) rot=(0,-1,0;0.174533rad)
  Support = -> [XY_Plane304]
  Width = 0.23
FEATURE [PartDesign::Fillet] Fillet810
  Base = -> Box2639 [Edge28]
  BaseFeature = -> Box2639
  Placement = pos=(-21.15,18.635,0.297) rot=(0,-1,0;0.174533rad)
  Radius = 0.375
  SupportTransform = false
FEATURE [PartDesign::AdditiveBox] Box2708
  AttacherType = Attacher::AttachEngine3D
  AttachmentOffset = pos=(-20.7,18.635,1.55) rot=(0,1,0;0.785398rad)
  BaseFeature = -> Fillet810
  Height = 0.375
  Length = 0.23
  MapMode = 5
  Placement = pos=(-20.7,18.635,1.55) rot=(0,1,0;0.785398rad)
  Support = -> [XY_Plane304]
  Width = 0.23
FEATURE [PartDesign::SubtractiveCylinder] Cylinder531
  Angle = 360
  AttacherType = Attacher::AttachEngine3D
  AttachmentOffset = pos=(-20.271,18.635,1.4056) rot=(-1,0,0;1.5708rad)
  BaseFeature = -> Box2708
  Height = 0.23
  MapMode = 5
  Placement = pos=(-20.271,18.635,1.4056) rot=(-1,0,0;1.5708rad)
  Radius = 0.23
  Support = -> [XY_Plane304]
FEATURE [PartDesign::AdditiveBox] Box2739
  AttacherType = Attacher::AttachEngine3D
  AttachmentOffset = pos=(-20.1,18.635,1.635) rot=(0,0,1;0rad)
  BaseFeature = -> Cylinder531
  Height = 0.265
  Length = 0.23
  MapMode = 5
  Placement = pos=(-20.1,18.635,1.635) rot=(0,0,1;0rad)
  Support = -> [XY_Plane304]
  Width = 0.23
FEATURE [PartDesign::Body] Body268  label="pin268"
  Group = -> [Box2750,Box2737,Box2732,Box2720,Box2741,Fillet808,Fillet803,Box2706,Cylinder534,Box2649,Box2639,Fillet810,Box2708,Cylinder531,Box2739]
  Origin = -> Origin301
  Tip = -> Box2739
FEATURE [PartDesign::SubtractiveBox] Box2754
  AttacherType = Attacher::AttachEngine3D
  AttachmentOffset = pos=(-21.35,18.635,0.35) rot=(0,0,1;0rad)
  BaseFeature = -> Box2749
  Height = 1.55
  Length = 0.5
  MapMode = 5
  Placement = pos=(-21.35,18.635,0.35) rot=(0,0,1;0rad)
  Support = -> [XY_Plane302]
  Width = 0.23
FEATURE [PartDesign::SubtractiveBox] Box2727
  AttacherType = Attacher::AttachEngine3D
  AttachmentOffset = pos=(-20.5,18.63,0) rot=(0,0,1;0rad)
  BaseFeature = -> Box2754
  Height = 1.635
  Length = 0.5
  MapMode = 5
  Placement = pos=(-20.5,18.63,0) rot=(0,0,1;0rad)
  Support = -> [XY_Plane302]
  Width = 0.25
FEATURE [PartDesign::SubtractiveBox] Box2747
  AttacherType = Attacher::AttachEngine3D
  AttachmentOffset = pos=(-21.19,18.635,-0.12) rot=(0,-1,0;0.15708rad)
  BaseFeature = -> Box2727
  Height = 0.12
  Length = 0.725
  MapMode = 5
  Placement = pos=(-21.19,18.635,-0.12) rot=(0,-1,0;0.15708rad)
  Support = -> [XY_Plane302]
  Width = 0.25
FEATURE [PartDesign::SubtractiveBox] Box2738
  AttacherType = Attacher::AttachEngine3D
  AttachmentOffset = pos=(-21.5005,18.625,0.235) rot=(0,-1,0;0.174533rad)
  BaseFeature = -> Box2747
  Height = 0.3
  Length = 0.6605
  MapMode = 5
  Placement = pos=(-21.5005,18.625,0.235) rot=(0,-1,0;0.174533rad)
  Support = -> [XY_Plane302]
  Width = 0.25
FEATURE [PartDesign::Fillet] Fillet794
  Base = -> Box2738 [Edge2]
  BaseFeature = -> Box2738
  Placement = pos=(-21.5005,18.625,0.235) rot=(0,-1,0;0.174533rad)
  Radius = 0.05
  SupportTransform = false
FEATURE [PartDesign::Fillet] Fillet820
  Base = -> Fillet794 [Edge33]
  BaseFeature = -> Fillet794
  Placement = pos=(-21.5005,18.625,0.235) rot=(0,-1,0;0.174533rad)
  Radius = 0.5
  SupportTransform = false
FEATURE [PartDesign::AdditiveBox] Box2725
  AttacherType = Attacher::AttachEngine3D
  AttachmentOffset = pos=(-21.1,18.635,0.305) rot=(0,1,0;0.785398rad)
  BaseFeature = -> Fillet820
  Height = 0.375
  Length = 0.2
  MapMode = 5
  Placement = pos=(-21.1,18.635,0.305) rot=(0,1,0;0.785398rad)
  Support = -> [XY_Plane302]
  Width = 0.23
FEATURE [PartDesign::SubtractiveCylinder] Cylinder554
  Angle = 360
  AttacherType = Attacher::AttachEngine3D
  AttachmentOffset = pos=(-21.055,18.935,0.52) rot=(1,0,0;1.5708rad)
  BaseFeature = -> Box2725
  Height = 0.375
  MapMode = 5
  Placement = pos=(-21.055,18.935,0.52) rot=(1,0,0;1.5708rad)
  Radius = 0.205
  Support = -> [XY_Plane302]
FEATURE [PartDesign::SubtractiveBox] Box2724
  AttacherType = Attacher::AttachEngine3D
  AttachmentOffset = pos=(-20.95,18.635,0.53) rot=(0,0,1;0rad)
  BaseFeature = -> Cylinder554
  Height = 0.5
  Length = 0.1
  MapMode = 5
  Placement = pos=(-20.95,18.635,0.53) rot=(0,0,1;0rad)
  Support = -> [XY_Plane302]
  Width = 0.23
FEATURE [PartDesign::SubtractiveBox] Box2743
  AttacherType = Attacher::AttachEngine3D
  AttachmentOffset = pos=(-21.15,18.635,0.297) rot=(0,-1,0;0.174533rad)
  BaseFeature = -> Box2724
  Height = 0.115
  Length = 0.115
  MapMode = 5
  Placement = pos=(-21.15,18.635,0.297) rot=(0,-1,0;0.174533rad)
  Support = -> [XY_Plane302]
  Width = 0.23
FEATURE [PartDesign::Fillet] Fillet801
  Base = -> Box2743 [Edge28]
  BaseFeature = -> Box2743
  Placement = pos=(-21.15,18.635,0.297) rot=(0,-1,0;0.174533rad)
  Radius = 0.375
  SupportTransform = false
FEATURE [PartDesign::AdditiveBox] Box2742
  AttacherType = Attacher::AttachEngine3D
  AttachmentOffset = pos=(-20.7,18.635,1.55) rot=(0,1,0;0.785398rad)
  BaseFeature = -> Fillet801
  Height = 0.375
  Length = 0.23
  MapMode = 5
  Placement = pos=(-20.7,18.635,1.55) rot=(0,1,0;0.785398rad)
  Support = -> [XY_Plane302]
  Width = 0.23
FEATURE [PartDesign::SubtractiveCylinder] Cylinder550
  Angle = 360
  AttacherType = Attacher::AttachEngine3D
  AttachmentOffset = pos=(-20.271,18.635,1.4056) rot=(-1,0,0;1.5708rad)
  BaseFeature = -> Box2742
  Height = 0.23
  MapMode = 5
  Placement = pos=(-20.271,18.635,1.4056) rot=(-1,0,0;1.5708rad)
  Radius = 0.23
  Support = -> [XY_Plane302]
FEATURE [PartDesign::AdditiveBox] Box2736
  AttacherType = Attacher::AttachEngine3D
  AttachmentOffset = pos=(-20.1,18.635,1.635) rot=(0,0,1;0rad)
  BaseFeature = -> Cylinder550
  Height = 0.265
  Length = 0.23
  MapMode = 5
  Placement = pos=(-20.1,18.635,1.635) rot=(0,0,1;0rad)
  Support = -> [XY_Plane302]
  Width = 0.23
FEATURE [PartDesign::Body] Body273  label="pin273"
  Group = -> [Box2749,Box2754,Box2727,Box2747,Box2738,Fillet794,Fillet820,Box2725,Cylinder554,Box2724,Box2743,Fillet801,Box2742,Cylinder550,Box2736]
  Origin = -> Origin304
  Placement = pos=(0,-1,0) rot=(0,0,1;0rad)
  Tip = -> Box2736
FEATURE [PartDesign::SubtractiveBox] Box2761
  AttacherType = Attacher::AttachEngine3D
  AttachmentOffset = pos=(-20.5,18.63,0) rot=(0,0,1;0rad)
  BaseFeature = -> Box2619
  Height = 1.635
  Length = 0.5
  MapMode = 5
  Placement = pos=(-20.5,18.63,0) rot=(0,0,1;0rad)
  Support = -> [XY_Plane264]
  Width = 0.25
FEATURE [PartDesign::SubtractiveBox] Box2609
  AttacherType = Attacher::AttachEngine3D
  AttachmentOffset = pos=(-21.19,18.635,-0.12) rot=(0,-1,0;0.15708rad)
  BaseFeature = -> Box2761
  Height = 0.12
  Length = 0.725
  MapMode = 5
  Placement = pos=(-21.19,18.635,-0.12) rot=(0,-1,0;0.15708rad)
  Support = -> [XY_Plane264]
  Width = 0.25
FEATURE [PartDesign::SubtractiveBox] Box2621
  AttacherType = Attacher::AttachEngine3D
  AttachmentOffset = pos=(-21.5005,18.625,0.235) rot=(0,-1,0;0.174533rad)
  BaseFeature = -> Box2609
  Height = 0.3
  Length = 0.6605
  MapMode = 5
  Placement = pos=(-21.5005,18.625,0.235) rot=(0,-1,0;0.174533rad)
  Support = -> [XY_Plane264]
  Width = 0.25
FEATURE [PartDesign::Fillet] Fillet800
  Base = -> Box2621 [Edge2]
  BaseFeature = -> Box2621
  Placement = pos=(-21.5005,18.625,0.235) rot=(0,-1,0;0.174533rad)
  Radius = 0.05
  SupportTransform = false
FEATURE [PartDesign::Fillet] Fillet790
  Base = -> Fillet800 [Edge33]
  BaseFeature = -> Fillet800
  Placement = pos=(-21.5005,18.625,0.235) rot=(0,-1,0;0.174533rad)
  Radius = 0.5
  SupportTransform = false
FEATURE [PartDesign::AdditiveBox] Box2751
  AttacherType = Attacher::AttachEngine3D
  AttachmentOffset = pos=(-21.1,18.635,0.305) rot=(0,1,0;0.785398rad)
  BaseFeature = -> Fillet790
  Height = 0.375
  Length = 0.2
  MapMode = 5
  Placement = pos=(-21.1,18.635,0.305) rot=(0,1,0;0.785398rad)
  Support = -> [XY_Plane264]
  Width = 0.23
FEATURE [PartDesign::SubtractiveCylinder] Cylinder555
  Angle = 360
  AttacherType = Attacher::AttachEngine3D
  AttachmentOffset = pos=(-21.055,18.935,0.52) rot=(1,0,0;1.5708rad)
  BaseFeature = -> Box2751
  Height = 0.375
  MapMode = 5
  Placement = pos=(-21.055,18.935,0.52) rot=(1,0,0;1.5708rad)
  Radius = 0.205
  Support = -> [XY_Plane264]
FEATURE [PartDesign::SubtractiveBox] Box2618
  AttacherType = Attacher::AttachEngine3D
  AttachmentOffset = pos=(-20.95,18.635,0.53) rot=(0,0,1;0rad)
  BaseFeature = -> Cylinder555
  Height = 0.5
  Length = 0.1
  MapMode = 5
  Placement = pos=(-20.95,18.635,0.53) rot=(0,0,1;0rad)
  Support = -> [XY_Plane264]
  Width = 0.23
FEATURE [PartDesign::SubtractiveBox] Box2690
  AttacherType = Attacher::AttachEngine3D
  AttachmentOffset = pos=(-21.15,18.635,0.297) rot=(0,-1,0;0.174533rad)
  BaseFeature = -> Box2618
  Height = 0.115
  Length = 0.115
  MapMode = 5
  Placement = pos=(-21.15,18.635,0.297) rot=(0,-1,0;0.174533rad)
  Support = -> [XY_Plane264]
  Width = 0.23
FEATURE [PartDesign::Fillet] Fillet793
  Base = -> Box2690 [Edge28]
  BaseFeature = -> Box2690
  Placement = pos=(-21.15,18.635,0.297) rot=(0,-1,0;0.174533rad)
  Radius = 0.375
  SupportTransform = false
FEATURE [PartDesign::AdditiveBox] Box2740
  AttacherType = Attacher::AttachEngine3D
  AttachmentOffset = pos=(-20.7,18.635,1.55) rot=(0,1,0;0.785398rad)
  BaseFeature = -> Fillet793
  Height = 0.375
  Length = 0.23
  MapMode = 5
  Placement = pos=(-20.7,18.635,1.55) rot=(0,1,0;0.785398rad)
  Support = -> [XY_Plane264]
  Width = 0.23
FEATURE [PartDesign::SubtractiveCylinder] Cylinder526
  Angle = 360
  AttacherType = Attacher::AttachEngine3D
  AttachmentOffset = pos=(-20.271,18.635,1.4056) rot=(-1,0,0;1.5708rad)
  BaseFeature = -> Box2740
  Height = 0.23
  MapMode = 5
  Placement = pos=(-20.271,18.635,1.4056) rot=(-1,0,0;1.5708rad)
  Radius = 0.23
  Support = -> [XY_Plane264]
FEATURE [PartDesign::AdditiveBox] Box2617
  AttacherType = Attacher::AttachEngine3D
  AttachmentOffset = pos=(-20.1,18.635,1.635) rot=(0,0,1;0rad)
  BaseFeature = -> Cylinder526
  Height = 0.265
  Length = 0.23
  MapMode = 5
  Placement = pos=(-20.1,18.635,1.635) rot=(0,0,1;0rad)
  Support = -> [XY_Plane264]
  Width = 0.23
FEATURE [PartDesign::Body] Body265  label="pin265"
  Group = -> [Box2705,Box2619,Box2761,Box2609,Box2621,Fillet800,Fillet790,Box2751,Cylinder555,Box2618,Box2690,Fillet793,Box2740,Cylinder526,Box2617]
  Origin = -> Origin310
  Placement = pos=(0,-2,0) rot=(0,0,1;0rad)
  Tip = -> Box2617
FEATURE [PartDesign::SubtractiveBox] Box2762
  AttacherType = Attacher::AttachEngine3D
  AttachmentOffset = pos=(-20.5,18.63,0) rot=(0,0,1;0rad)
  BaseFeature = -> Box2600
  Height = 1.635
  Length = 0.5
  MapMode = 5
  Placement = pos=(-20.5,18.63,0) rot=(0,0,1;0rad)
  Support = -> [XY_Plane292]
  Width = 0.25
FEATURE [PartDesign::SubtractiveBox] Box2693
  AttacherType = Attacher::AttachEngine3D
  AttachmentOffset = pos=(-21.19,18.635,-0.12) rot=(0,-1,0;0.15708rad)
  BaseFeature = -> Box2762
  Height = 0.12
  Length = 0.725
  MapMode = 5
  Placement = pos=(-21.19,18.635,-0.12) rot=(0,-1,0;0.15708rad)
  Support = -> [XY_Plane292]
  Width = 0.25
FEATURE [PartDesign::SubtractiveBox] Box2622
  AttacherType = Attacher::AttachEngine3D
  AttachmentOffset = pos=(-21.5005,18.625,0.235) rot=(0,-1,0;0.174533rad)
  BaseFeature = -> Box2693
  Height = 0.3
  Length = 0.6605
  MapMode = 5
  Placement = pos=(-21.5005,18.625,0.235) rot=(0,-1,0;0.174533rad)
  Support = -> [XY_Plane292]
  Width = 0.25
FEATURE [PartDesign::Fillet] Fillet792
  Base = -> Box2622 [Edge2]
  BaseFeature = -> Box2622
  Placement = pos=(-21.5005,18.625,0.235) rot=(0,-1,0;0.174533rad)
  Radius = 0.05
  SupportTransform = false
FEATURE [PartDesign::Fillet] Fillet804
  Base = -> Fillet792 [Edge33]
  BaseFeature = -> Fillet792
  Placement = pos=(-21.5005,18.625,0.235) rot=(0,-1,0;0.174533rad)
  Radius = 0.5
  SupportTransform = false
FEATURE [PartDesign::AdditiveBox] Box2757
  AttacherType = Attacher::AttachEngine3D
  AttachmentOffset = pos=(-21.1,18.635,0.305) rot=(0,1,0;0.785398rad)
  BaseFeature = -> Fillet804
  Height = 0.375
  Length = 0.2
  MapMode = 5
  Placement = pos=(-21.1,18.635,0.305) rot=(0,1,0;0.785398rad)
  Support = -> [XY_Plane292]
  Width = 0.23
FEATURE [PartDesign::SubtractiveCylinder] Cylinder543
  Angle = 360
  AttacherType = Attacher::AttachEngine3D
  AttachmentOffset = pos=(-21.055,18.935,0.52) rot=(1,0,0;1.5708rad)
  BaseFeature = -> Box2757
  Height = 0.375
  MapMode = 5
  Placement = pos=(-21.055,18.935,0.52) rot=(1,0,0;1.5708rad)
  Radius = 0.205
  Support = -> [XY_Plane292]
FEATURE [PartDesign::SubtractiveBox] Box2601
  AttacherType = Attacher::AttachEngine3D
  AttachmentOffset = pos=(-20.95,18.635,0.53) rot=(0,0,1;0rad)
  BaseFeature = -> Cylinder543
  Height = 0.5
  Length = 0.1
  MapMode = 5
  Placement = pos=(-20.95,18.635,0.53) rot=(0,0,1;0rad)
  Support = -> [XY_Plane292]
  Width = 0.23
FEATURE [PartDesign::SubtractiveBox] Box2625
  AttacherType = Attacher::AttachEngine3D
  AttachmentOffset = pos=(-21.15,18.635,0.297) rot=(0,-1,0;0.174533rad)
  BaseFeature = -> Box2601
  Height = 0.115
  Length = 0.115
  MapMode = 5
  Placement = pos=(-21.15,18.635,0.297) rot=(0,-1,0;0.174533rad)
  Support = -> [XY_Plane292]
  Width = 0.23
FEATURE [PartDesign::Fillet] Fillet798
  Base = -> Box2625 [Edge28]
  BaseFeature = -> Box2625
  Placement = pos=(-21.15,18.635,0.297) rot=(0,-1,0;0.174533rad)
  Radius = 0.375
  SupportTransform = false
FEATURE [PartDesign::AdditiveBox] Box2616
  AttacherType = Attacher::AttachEngine3D
  AttachmentOffset = pos=(-20.7,18.635,1.55) rot=(0,1,0;0.785398rad)
  BaseFeature = -> Fillet798
  Height = 0.375
  Length = 0.23
  MapMode = 5
  Placement = pos=(-20.7,18.635,1.55) rot=(0,1,0;0.785398rad)
  Support = -> [XY_Plane292]
  Width = 0.23
FEATURE [PartDesign::SubtractiveCylinder] Cylinder544
  Angle = 360
  AttacherType = Attacher::AttachEngine3D
  AttachmentOffset = pos=(-20.271,18.635,1.4056) rot=(-1,0,0;1.5708rad)
  BaseFeature = -> Box2616
  Height = 0.23
  MapMode = 5
  Placement = pos=(-20.271,18.635,1.4056) rot=(-1,0,0;1.5708rad)
  Radius = 0.23
  Support = -> [XY_Plane292]
FEATURE [PartDesign::AdditiveBox] Box2602
  AttacherType = Attacher::AttachEngine3D
  AttachmentOffset = pos=(-20.1,18.635,1.635) rot=(0,0,1;0rad)
  BaseFeature = -> Cylinder544
  Height = 0.265
  Length = 0.23
  MapMode = 5
  Placement = pos=(-20.1,18.635,1.635) rot=(0,0,1;0rad)
  Support = -> [XY_Plane292]
  Width = 0.23
FEATURE [PartDesign::Body] Body269  label="pin269"
  Group = -> [Box2628,Box2600,Box2762,Box2693,Box2622,Fillet792,Fillet804,Box2757,Cylinder543,Box2601,Box2625,Fillet798,Box2616,Cylinder544,Box2602]
  Origin = -> Origin303
  Placement = pos=(0,-2.5,0) rot=(0,0,1;0rad)
  Tip = -> Box2602
FEATURE [PartDesign::AdditiveBox] Box2763
  AttacherType = Attacher::AttachEngine3D
  AttachmentOffset = pos=(-21.1,18.635,0.305) rot=(0,1,0;0.785398rad)
  BaseFeature = -> Fillet811
  Height = 0.375
  Length = 0.2
  MapMode = 5
  Placement = pos=(-21.1,18.635,0.305) rot=(0,1,0;0.785398rad)
  Support = -> [XY_Plane276]
  Width = 0.23
FEATURE [PartDesign::SubtractiveCylinder] Cylinder552
  Angle = 360
  AttacherType = Attacher::AttachEngine3D
  AttachmentOffset = pos=(-21.055,18.935,0.52) rot=(1,0,0;1.5708rad)
  BaseFeature = -> Box2763
  Height = 0.375
  MapMode = 5
  Placement = pos=(-21.055,18.935,0.52) rot=(1,0,0;1.5708rad)
  Radius = 0.205
  Support = -> [XY_Plane276]
FEATURE [PartDesign::SubtractiveBox] Box2758
  AttacherType = Attacher::AttachEngine3D
  AttachmentOffset = pos=(-20.95,18.635,0.53) rot=(0,0,1;0rad)
  BaseFeature = -> Cylinder552
  Height = 0.5
  Length = 0.1
  MapMode = 5
  Placement = pos=(-20.95,18.635,0.53) rot=(0,0,1;0rad)
  Support = -> [XY_Plane276]
  Width = 0.23
FEATURE [PartDesign::SubtractiveBox] Box2753
  AttacherType = Attacher::AttachEngine3D
  AttachmentOffset = pos=(-21.15,18.635,0.297) rot=(0,-1,0;0.174533rad)
  BaseFeature = -> Box2758
  Height = 0.115
  Length = 0.115
  MapMode = 5
  Placement = pos=(-21.15,18.635,0.297) rot=(0,-1,0;0.174533rad)
  Support = -> [XY_Plane276]
  Width = 0.23
FEATURE [PartDesign::Fillet] Fillet809
  Base = -> Box2753 [Edge28]
  BaseFeature = -> Box2753
  Placement = pos=(-21.15,18.635,0.297) rot=(0,-1,0;0.174533rad)
  Radius = 0.375
  SupportTransform = false
FEATURE [PartDesign::AdditiveBox] Box2756
  AttacherType = Attacher::AttachEngine3D
  AttachmentOffset = pos=(-20.7,18.635,1.55) rot=(0,1,0;0.785398rad)
  BaseFeature = -> Fillet809
  Height = 0.375
  Length = 0.23
  MapMode = 5
  Placement = pos=(-20.7,18.635,1.55) rot=(0,1,0;0.785398rad)
  Support = -> [XY_Plane276]
  Width = 0.23
FEATURE [PartDesign::SubtractiveCylinder] Cylinder546
  Angle = 360
  AttacherType = Attacher::AttachEngine3D
  AttachmentOffset = pos=(-20.271,18.635,1.4056) rot=(-1,0,0;1.5708rad)
  BaseFeature = -> Box2756
  Height = 0.23
  MapMode = 5
  Placement = pos=(-20.271,18.635,1.4056) rot=(-1,0,0;1.5708rad)
  Radius = 0.23
  Support = -> [XY_Plane276]
FEATURE [PartDesign::AdditiveBox] Box2752
  AttacherType = Attacher::AttachEngine3D
  AttachmentOffset = pos=(-20.1,18.635,1.635) rot=(0,0,1;0rad)
  BaseFeature = -> Cylinder546
  Height = 0.265
  Length = 0.23
  MapMode = 5
  Placement = pos=(-20.1,18.635,1.635) rot=(0,0,1;0rad)
  Support = -> [XY_Plane276]
  Width = 0.23
FEATURE [PartDesign::Body] Body267  label="pin267"
  Group = -> [Box2634,Box2612,Box2748,Box2728,Box2620,Fillet791,Fillet811,Box2763,Cylinder552,Box2758,Box2753,Fillet809,Box2756,Cylinder546,Box2752]
  Origin = -> Origin298
  Placement = pos=(0,-1.5,0) rot=(0,0,1;0rad)
  Tip = -> Box2752
FEATURE [App::Part] Part027  label="Pin-set024"
  Group = -> [Body268,Body266,Body273,Body267,Body265,Body269,Body275,Body270,Body276,Body271,Body272,Body274]
  Origin = -> Origin309
  Placement = pos=(0,-18,0) rot=(0,0,1;0rad)
FEATURE [PartDesign::AdditiveBox] Box2779
  AttacherType = Attacher::AttachEngine3D
  AttachmentOffset = pos=(-21.3,18.635,0) rot=(0,0,1;0rad)
  Height = 1.9
  Length = 1.3
  MapMode = 5
  Placement = pos=(-21.3,18.635,0) rot=(0,0,1;0rad)
  Support = -> [XY_Plane314]
  Width = 0.23
FEATURE [PartDesign::SubtractiveBox] Box2768
  AttacherType = Attacher::AttachEngine3D
  AttachmentOffset = pos=(-21.35,18.635,0.35) rot=(0,0,1;0rad)
  BaseFeature = -> Box2779
  Height = 1.55
  Length = 0.5
  MapMode = 5
  Placement = pos=(-21.35,18.635,0.35) rot=(0,0,1;0rad)
  Support = -> [XY_Plane314]
  Width = 0.23
FEATURE [PartDesign::AdditiveBox] Box2784
  AttacherType = Attacher::AttachEngine3D
  AttachmentOffset = pos=(-21.3,18.635,0) rot=(0,0,1;0rad)
  Height = 1.9
  Length = 1.3
  MapMode = 5
  Placement = pos=(-21.3,18.635,0) rot=(0,0,1;0rad)
  Support = -> [XY_Plane318]
  Width = 0.23
FEATURE [PartDesign::AdditiveBox] Box2785
  AttacherType = Attacher::AttachEngine3D
  AttachmentOffset = pos=(-21.3,18.635,0) rot=(0,0,1;0rad)
  Height = 1.9
  Length = 1.3
  MapMode = 5
  Placement = pos=(-21.3,18.635,0) rot=(0,0,1;0rad)
  Support = -> [XY_Plane309]
  Width = 0.23
FEATURE [PartDesign::SubtractiveBox] Box2774
  AttacherType = Attacher::AttachEngine3D
  AttachmentOffset = pos=(-21.35,18.635,0.35) rot=(0,0,1;0rad)
  BaseFeature = -> Box2785
  Height = 1.55
  Length = 0.5
  MapMode = 5
  Placement = pos=(-21.35,18.635,0.35) rot=(0,0,1;0rad)
  Support = -> [XY_Plane309]
  Width = 0.23
FEATURE [PartDesign::SubtractiveBox] Box2799
  AttacherType = Attacher::AttachEngine3D
  AttachmentOffset = pos=(-21.35,18.635,0.35) rot=(0,0,1;0rad)
  BaseFeature = -> Box2784
  Height = 1.55
  Length = 0.5
  MapMode = 5
  Placement = pos=(-21.35,18.635,0.35) rot=(0,0,1;0rad)
  Support = -> [XY_Plane318]
  Width = 0.23
FEATURE [PartDesign::SubtractiveBox] Box2780
  AttacherType = Attacher::AttachEngine3D
  AttachmentOffset = pos=(-20.5,18.63,0) rot=(0,0,1;0rad)
  BaseFeature = -> Box2799
  Height = 1.635
  Length = 0.5
  MapMode = 5
  Placement = pos=(-20.5,18.63,0) rot=(0,0,1;0rad)
  Support = -> [XY_Plane318]
  Width = 0.25
FEATURE [PartDesign::SubtractiveBox] Box2783
  AttacherType = Attacher::AttachEngine3D
  AttachmentOffset = pos=(-21.19,18.635,-0.12) rot=(0,-1,0;0.15708rad)
  BaseFeature = -> Box2780
  Height = 0.12
  Length = 0.725
  MapMode = 5
  Placement = pos=(-21.19,18.635,-0.12) rot=(0,-1,0;0.15708rad)
  Support = -> [XY_Plane318]
  Width = 0.25
FEATURE [PartDesign::AdditiveBox] Box2801
  AttacherType = Attacher::AttachEngine3D
  AttachmentOffset = pos=(-21.3,18.635,0) rot=(0,0,1;0rad)
  Height = 1.9
  Length = 1.3
  MapMode = 5
  Placement = pos=(-21.3,18.635,0) rot=(0,0,1;0rad)
  Support = -> [XY_Plane317]
  Width = 0.23
FEATURE [PartDesign::SubtractiveBox] Box2803
  AttacherType = Attacher::AttachEngine3D
  AttachmentOffset = pos=(-21.5005,18.625,0.235) rot=(0,-1,0;0.174533rad)
  BaseFeature = -> Box2783
  Height = 0.3
  Length = 0.6605
  MapMode = 5
  Placement = pos=(-21.5005,18.625,0.235) rot=(0,-1,0;0.174533rad)
  Support = -> [XY_Plane318]
  Width = 0.25
FEATURE [PartDesign::Fillet] Fillet845
  Base = -> Box2803 [Edge2]
  BaseFeature = -> Box2803
  Placement = pos=(-21.5005,18.625,0.235) rot=(0,-1,0;0.174533rad)
  Radius = 0.05
  SupportTransform = false
FEATURE [PartDesign::Fillet] Fillet831
  Base = -> Fillet845 [Edge33]
  BaseFeature = -> Fillet845
  Placement = pos=(-21.5005,18.625,0.235) rot=(0,-1,0;0.174533rad)
  Radius = 0.5
  SupportTransform = false
FEATURE [PartDesign::AdditiveBox] Box2773
  AttacherType = Attacher::AttachEngine3D
  AttachmentOffset = pos=(-21.1,18.635,0.305) rot=(0,1,0;0.785398rad)
  BaseFeature = -> Fillet831
  Height = 0.375
  Length = 0.2
  MapMode = 5
  Placement = pos=(-21.1,18.635,0.305) rot=(0,1,0;0.785398rad)
  Support = -> [XY_Plane318]
  Width = 0.23
FEATURE [PartDesign::SubtractiveCylinder] Cylinder559
  Angle = 360
  AttacherType = Attacher::AttachEngine3D
  AttachmentOffset = pos=(-21.055,18.935,0.52) rot=(1,0,0;1.5708rad)
  BaseFeature = -> Box2773
  Height = 0.375
  MapMode = 5
  Placement = pos=(-21.055,18.935,0.52) rot=(1,0,0;1.5708rad)
  Radius = 0.205
  Support = -> [XY_Plane318]
FEATURE [PartDesign::SubtractiveBox] Box2798
  AttacherType = Attacher::AttachEngine3D
  AttachmentOffset = pos=(-20.95,18.635,0.53) rot=(0,0,1;0rad)
  BaseFeature = -> Cylinder559
  Height = 0.5
  Length = 0.1
  MapMode = 5
  Placement = pos=(-20.95,18.635,0.53) rot=(0,0,1;0rad)
  Support = -> [XY_Plane318]
  Width = 0.23
FEATURE [PartDesign::SubtractiveBox] Box2778
  AttacherType = Attacher::AttachEngine3D
  AttachmentOffset = pos=(-21.15,18.635,0.297) rot=(0,-1,0;0.174533rad)
  BaseFeature = -> Box2798
  Height = 0.115
  Length = 0.115
  MapMode = 5
  Placement = pos=(-21.15,18.635,0.297) rot=(0,-1,0;0.174533rad)
  Support = -> [XY_Plane318]
  Width = 0.23
FEATURE [PartDesign::Fillet] Fillet838
  Base = -> Box2778 [Edge28]
  BaseFeature = -> Box2778
  Placement = pos=(-21.15,18.635,0.297) rot=(0,-1,0;0.174533rad)
  Radius = 0.375
  SupportTransform = false
FEATURE [PartDesign::AdditiveBox] Box2793
  AttacherType = Attacher::AttachEngine3D
  AttachmentOffset = pos=(-20.7,18.635,1.55) rot=(0,1,0;0.785398rad)
  BaseFeature = -> Fillet838
  Height = 0.375
  Length = 0.23
  MapMode = 5
  Placement = pos=(-20.7,18.635,1.55) rot=(0,1,0;0.785398rad)
  Support = -> [XY_Plane318]
  Width = 0.23
FEATURE [PartDesign::SubtractiveCylinder] Cylinder558
  Angle = 360
  AttacherType = Attacher::AttachEngine3D
  AttachmentOffset = pos=(-20.271,18.635,1.4056) rot=(-1,0,0;1.5708rad)
  BaseFeature = -> Box2793
  Height = 0.23
  MapMode = 5
  Placement = pos=(-20.271,18.635,1.4056) rot=(-1,0,0;1.5708rad)
  Radius = 0.23
  Support = -> [XY_Plane318]
FEATURE [PartDesign::AdditiveBox] Box2805
  AttacherType = Attacher::AttachEngine3D
  AttachmentOffset = pos=(-21.3,18.635,0) rot=(0,0,1;0rad)
  Height = 1.9
  Length = 1.3
  MapMode = 5
  Placement = pos=(-21.3,18.635,0) rot=(0,0,1;0rad)
  Support = -> [XY_Plane321]
  Width = 0.23
FEATURE [PartDesign::SubtractiveBox] Box2797
  AttacherType = Attacher::AttachEngine3D
  AttachmentOffset = pos=(-21.35,18.635,0.35) rot=(0,0,1;0rad)
  BaseFeature = -> Box2805
  Height = 1.55
  Length = 0.5
  MapMode = 5
  Placement = pos=(-21.35,18.635,0.35) rot=(0,0,1;0rad)
  Support = -> [XY_Plane321]
  Width = 0.23
FEATURE [PartDesign::SubtractiveBox] Box2782
  AttacherType = Attacher::AttachEngine3D
  AttachmentOffset = pos=(-20.5,18.63,0) rot=(0,0,1;0rad)
  BaseFeature = -> Box2797
  Height = 1.635
  Length = 0.5
  MapMode = 5
  Placement = pos=(-20.5,18.63,0) rot=(0,0,1;0rad)
  Support = -> [XY_Plane321]
  Width = 0.25
FEATURE [PartDesign::SubtractiveBox] Box2795
  AttacherType = Attacher::AttachEngine3D
  AttachmentOffset = pos=(-21.19,18.635,-0.12) rot=(0,-1,0;0.15708rad)
  BaseFeature = -> Box2782
  Height = 0.12
  Length = 0.725
  MapMode = 5
  Placement = pos=(-21.19,18.635,-0.12) rot=(0,-1,0;0.15708rad)
  Support = -> [XY_Plane321]
  Width = 0.25
FEATURE [PartDesign::AdditiveBox] Box2810
  AttacherType = Attacher::AttachEngine3D
  AttachmentOffset = pos=(-20.1,18.635,1.635) rot=(0,0,1;0rad)
  BaseFeature = -> Cylinder558
  Height = 0.265
  Length = 0.23
  MapMode = 5
  Placement = pos=(-20.1,18.635,1.635) rot=(0,0,1;0rad)
  Support = -> [XY_Plane318]
  Width = 0.23
FEATURE [PartDesign::Body] Body281  label="pin281"
  Group = -> [Box2784,Box2799,Box2780,Box2783,Box2803,Fillet845,Fillet831,Box2773,Cylinder559,Box2798,Box2778,Fillet838,Box2793,Cylinder558,Box2810]
  Origin = -> Origin292
  Placement = pos=(0,-5,0) rot=(0,0,1;0rad)
  Tip = -> Box2810
FEATURE [PartDesign::AdditiveBox] Box2813
  AttacherType = Attacher::AttachEngine3D
  AttachmentOffset = pos=(-21.3,18.635,0) rot=(0,0,1;0rad)
  Height = 1.9
  Length = 1.3
  MapMode = 5
  Placement = pos=(-21.3,18.635,0) rot=(0,0,1;0rad)
  Support = -> [XY_Plane320]
  Width = 0.23
FEATURE [PartDesign::AdditiveBox] Box2814
  AttacherType = Attacher::AttachEngine3D
  AttachmentOffset = pos=(-21.3,18.635,0) rot=(0,0,1;0rad)
  Height = 1.9
  Length = 1.3
  MapMode = 5
  Placement = pos=(-21.3,18.635,0) rot=(0,0,1;0rad)
  Support = -> [XY_Plane313]
  Width = 0.23
FEATURE [PartDesign::SubtractiveBox] Box2816
  AttacherType = Attacher::AttachEngine3D
  AttachmentOffset = pos=(-21.35,18.635,0.35) rot=(0,0,1;0rad)
  BaseFeature = -> Box2814
  Height = 1.55
  Length = 0.5
  MapMode = 5
  Placement = pos=(-21.35,18.635,0.35) rot=(0,0,1;0rad)
  Support = -> [XY_Plane313]
  Width = 0.23
FEATURE [PartDesign::SubtractiveBox] Box2771
  AttacherType = Attacher::AttachEngine3D
  AttachmentOffset = pos=(-20.5,18.63,0) rot=(0,0,1;0rad)
  BaseFeature = -> Box2816
  Height = 1.635
  Length = 0.5
  MapMode = 5
  Placement = pos=(-20.5,18.63,0) rot=(0,0,1;0rad)
  Support = -> [XY_Plane313]
  Width = 0.25
FEATURE [PartDesign::SubtractiveBox] Box2787
  AttacherType = Attacher::AttachEngine3D
  AttachmentOffset = pos=(-21.19,18.635,-0.12) rot=(0,-1,0;0.15708rad)
  BaseFeature = -> Box2771
  Height = 0.12
  Length = 0.725
  MapMode = 5
  Placement = pos=(-21.19,18.635,-0.12) rot=(0,-1,0;0.15708rad)
  Support = -> [XY_Plane313]
  Width = 0.25
FEATURE [PartDesign::SubtractiveBox] Box2776
  AttacherType = Attacher::AttachEngine3D
  AttachmentOffset = pos=(-21.5005,18.625,0.235) rot=(0,-1,0;0.174533rad)
  BaseFeature = -> Box2787
  Height = 0.3
  Length = 0.6605
  MapMode = 5
  Placement = pos=(-21.5005,18.625,0.235) rot=(0,-1,0;0.174533rad)
  Support = -> [XY_Plane313]
  Width = 0.25
FEATURE [PartDesign::Fillet] Fillet850
  Base = -> Box2776 [Edge2]
  BaseFeature = -> Box2776
  Placement = pos=(-21.5005,18.625,0.235) rot=(0,-1,0;0.174533rad)
  Radius = 0.05
  SupportTransform = false
FEATURE [PartDesign::Fillet] Fillet861
  Base = -> Fillet850 [Edge33]
  BaseFeature = -> Fillet850
  Placement = pos=(-21.5005,18.625,0.235) rot=(0,-1,0;0.174533rad)
  Radius = 0.5
  SupportTransform = false
FEATURE [PartDesign::AdditiveBox] Box2800
  AttacherType = Attacher::AttachEngine3D
  AttachmentOffset = pos=(-21.1,18.635,0.305) rot=(0,1,0;0.785398rad)
  BaseFeature = -> Fillet861
  Height = 0.375
  Length = 0.2
  MapMode = 5
  Placement = pos=(-21.1,18.635,0.305) rot=(0,1,0;0.785398rad)
  Support = -> [XY_Plane313]
  Width = 0.23
FEATURE [PartDesign::SubtractiveCylinder] Cylinder564
  Angle = 360
  AttacherType = Attacher::AttachEngine3D
  AttachmentOffset = pos=(-21.055,18.935,0.52) rot=(1,0,0;1.5708rad)
  BaseFeature = -> Box2800
  Height = 0.375
  MapMode = 5
  Placement = pos=(-21.055,18.935,0.52) rot=(1,0,0;1.5708rad)
  Radius = 0.205
  Support = -> [XY_Plane313]
FEATURE [PartDesign::SubtractiveBox] Box2806
  AttacherType = Attacher::AttachEngine3D
  AttachmentOffset = pos=(-20.95,18.635,0.53) rot=(0,0,1;0rad)
  BaseFeature = -> Cylinder564
  Height = 0.5
  Length = 0.1
  MapMode = 5
  Placement = pos=(-20.95,18.635,0.53) rot=(0,0,1;0rad)
  Support = -> [XY_Plane313]
  Width = 0.23
FEATURE [PartDesign::SubtractiveBox] Box2796
  AttacherType = Attacher::AttachEngine3D
  AttachmentOffset = pos=(-21.15,18.635,0.297) rot=(0,-1,0;0.174533rad)
  BaseFeature = -> Box2806
  Height = 0.115
  Length = 0.115
  MapMode = 5
  Placement = pos=(-21.15,18.635,0.297) rot=(0,-1,0;0.174533rad)
  Support = -> [XY_Plane313]
  Width = 0.23
FEATURE [PartDesign::Fillet] Fillet848
  Base = -> Box2796 [Edge28]
  BaseFeature = -> Box2796
  Placement = pos=(-21.15,18.635,0.297) rot=(0,-1,0;0.174533rad)
  Radius = 0.375
  SupportTransform = false
FEATURE [PartDesign::AdditiveBox] Box2809
  AttacherType = Attacher::AttachEngine3D
  AttachmentOffset = pos=(-20.7,18.635,1.55) rot=(0,1,0;0.785398rad)
  BaseFeature = -> Fillet848
  Height = 0.375
  Length = 0.23
  MapMode = 5
  Placement = pos=(-20.7,18.635,1.55) rot=(0,1,0;0.785398rad)
  Support = -> [XY_Plane313]
  Width = 0.23
FEATURE [PartDesign::SubtractiveCylinder] Cylinder565
  Angle = 360
  AttacherType = Attacher::AttachEngine3D
  AttachmentOffset = pos=(-20.271,18.635,1.4056) rot=(-1,0,0;1.5708rad)
  BaseFeature = -> Box2809
  Height = 0.23
  MapMode = 5
  Placement = pos=(-20.271,18.635,1.4056) rot=(-1,0,0;1.5708rad)
  Radius = 0.23
  Support = -> [XY_Plane313]
FEATURE [PartDesign::AdditiveBox] Box2807
  AttacherType = Attacher::AttachEngine3D
  AttachmentOffset = pos=(-20.1,18.635,1.635) rot=(0,0,1;0rad)
  BaseFeature = -> Cylinder565
  Height = 0.265
  Length = 0.23
  MapMode = 5
  Placement = pos=(-20.1,18.635,1.635) rot=(0,0,1;0rad)
  Support = -> [XY_Plane313]
  Width = 0.23
FEATURE [PartDesign::Body] Body288  label="pin288"
  Group = -> [Box2814,Box2816,Box2771,Box2787,Box2776,Fillet850,Fillet861,Box2800,Cylinder564,Box2806,Box2796,Fillet848,Box2809,Cylinder565,Box2807]
  Origin = -> Origin293
  Placement = pos=(0,-5.5,0) rot=(0,0,1;0rad)
  Tip = -> Box2807
FEATURE [PartDesign::AdditiveBox] Box2817
  AttacherType = Attacher::AttachEngine3D
  AttachmentOffset = pos=(-21.3,18.635,0) rot=(0,0,1;0rad)
  Height = 1.9
  Length = 1.3
  MapMode = 5
  Placement = pos=(-21.3,18.635,0) rot=(0,0,1;0rad)
  Support = -> [XY_Plane324]
  Width = 0.23
FEATURE [PartDesign::SubtractiveBox] Box2825
  AttacherType = Attacher::AttachEngine3D
  AttachmentOffset = pos=(-21.35,18.635,0.35) rot=(0,0,1;0rad)
  BaseFeature = -> Box2801
  Height = 1.55
  Length = 0.5
  MapMode = 5
  Placement = pos=(-21.35,18.635,0.35) rot=(0,0,1;0rad)
  Support = -> [XY_Plane317]
  Width = 0.23
FEATURE [PartDesign::SubtractiveBox] Box2808
  AttacherType = Attacher::AttachEngine3D
  AttachmentOffset = pos=(-20.5,18.63,0) rot=(0,0,1;0rad)
  BaseFeature = -> Box2825
  Height = 1.635
  Length = 0.5
  MapMode = 5
  Placement = pos=(-20.5,18.63,0) rot=(0,0,1;0rad)
  Support = -> [XY_Plane317]
  Width = 0.25
FEATURE [PartDesign::SubtractiveBox] Box2820
  AttacherType = Attacher::AttachEngine3D
  AttachmentOffset = pos=(-21.19,18.635,-0.12) rot=(0,-1,0;0.15708rad)
  BaseFeature = -> Box2808
  Height = 0.12
  Length = 0.725
  MapMode = 5
  Placement = pos=(-21.19,18.635,-0.12) rot=(0,-1,0;0.15708rad)
  Support = -> [XY_Plane317]
  Width = 0.25
FEATURE [PartDesign::SubtractiveBox] Box2815
  AttacherType = Attacher::AttachEngine3D
  AttachmentOffset = pos=(-21.5005,18.625,0.235) rot=(0,-1,0;0.174533rad)
  BaseFeature = -> Box2820
  Height = 0.3
  Length = 0.6605
  MapMode = 5
  Placement = pos=(-21.5005,18.625,0.235) rot=(0,-1,0;0.174533rad)
  Support = -> [XY_Plane317]
  Width = 0.25
FEATURE [PartDesign::Fillet] Fillet854
  Base = -> Box2815 [Edge2]
  BaseFeature = -> Box2815
  Placement = pos=(-21.5005,18.625,0.235) rot=(0,-1,0;0.174533rad)
  Radius = 0.05
  SupportTransform = false
FEATURE [PartDesign::Fillet] Fillet863
  Base = -> Fillet854 [Edge33]
  BaseFeature = -> Fillet854
  Placement = pos=(-21.5005,18.625,0.235) rot=(0,-1,0;0.174533rad)
  Radius = 0.5
  SupportTransform = false
FEATURE [PartDesign::AdditiveBox] Box2831
  AttacherType = Attacher::AttachEngine3D
  AttachmentOffset = pos=(-21.3,18.635,0) rot=(0,0,1;0rad)
  Height = 1.9
  Length = 1.3
  MapMode = 5
  Placement = pos=(-21.3,18.635,0) rot=(0,0,1;0rad)
  Support = -> [XY_Plane315]
  Width = 0.23
FEATURE [PartDesign::SubtractiveBox] Box2767
  AttacherType = Attacher::AttachEngine3D
  AttachmentOffset = pos=(-21.35,18.635,0.35) rot=(0,0,1;0rad)
  BaseFeature = -> Box2831
  Height = 1.55
  Length = 0.5
  MapMode = 5
  Placement = pos=(-21.35,18.635,0.35) rot=(0,0,1;0rad)
  Support = -> [XY_Plane315]
  Width = 0.23
FEATURE [PartDesign::AdditiveBox] Box2834
  AttacherType = Attacher::AttachEngine3D
  AttachmentOffset = pos=(-21.1,18.635,0.305) rot=(0,1,0;0.785398rad)
  BaseFeature = -> Fillet863
  Height = 0.375
  Length = 0.2
  MapMode = 5
  Placement = pos=(-21.1,18.635,0.305) rot=(0,1,0;0.785398rad)
  Support = -> [XY_Plane317]
  Width = 0.23
FEATURE [PartDesign::SubtractiveCylinder] Cylinder569
  Angle = 360
  AttacherType = Attacher::AttachEngine3D
  AttachmentOffset = pos=(-21.055,18.935,0.52) rot=(1,0,0;1.5708rad)
  BaseFeature = -> Box2834
  Height = 0.375
  MapMode = 5
  Placement = pos=(-21.055,18.935,0.52) rot=(1,0,0;1.5708rad)
  Radius = 0.205
  Support = -> [XY_Plane317]
FEATURE [PartDesign::SubtractiveBox] Box2818
  AttacherType = Attacher::AttachEngine3D
  AttachmentOffset = pos=(-20.95,18.635,0.53) rot=(0,0,1;0rad)
  BaseFeature = -> Cylinder569
  Height = 0.5
  Length = 0.1
  MapMode = 5
  Placement = pos=(-20.95,18.635,0.53) rot=(0,0,1;0rad)
  Support = -> [XY_Plane317]
  Width = 0.23
FEATURE [PartDesign::SubtractiveBox] Box2826
  AttacherType = Attacher::AttachEngine3D
  AttachmentOffset = pos=(-21.15,18.635,0.297) rot=(0,-1,0;0.174533rad)
  BaseFeature = -> Box2818
  Height = 0.115
  Length = 0.115
  MapMode = 5
  Placement = pos=(-21.15,18.635,0.297) rot=(0,-1,0;0.174533rad)
  Support = -> [XY_Plane317]
  Width = 0.23
FEATURE [PartDesign::Fillet] Fillet853
  Base = -> Box2826 [Edge28]
  BaseFeature = -> Box2826
  Placement = pos=(-21.15,18.635,0.297) rot=(0,-1,0;0.174533rad)
  Radius = 0.375
  SupportTransform = false
FEATURE [PartDesign::AdditiveBox] Box2821
  AttacherType = Attacher::AttachEngine3D
  AttachmentOffset = pos=(-20.7,18.635,1.55) rot=(0,1,0;0.785398rad)
  BaseFeature = -> Fillet853
  Height = 0.375
  Length = 0.23
  MapMode = 5
  Placement = pos=(-20.7,18.635,1.55) rot=(0,1,0;0.785398rad)
  Support = -> [XY_Plane317]
  Width = 0.23
FEATURE [PartDesign::SubtractiveCylinder] Cylinder568
  Angle = 360
  AttacherType = Attacher::AttachEngine3D
  AttachmentOffset = pos=(-20.271,18.635,1.4056) rot=(-1,0,0;1.5708rad)
  BaseFeature = -> Box2821
  Height = 0.23
  MapMode = 5
  Placement = pos=(-20.271,18.635,1.4056) rot=(-1,0,0;1.5708rad)
  Radius = 0.23
  Support = -> [XY_Plane317]
FEATURE [PartDesign::AdditiveBox] Box2811
  AttacherType = Attacher::AttachEngine3D
  AttachmentOffset = pos=(-20.1,18.635,1.635) rot=(0,0,1;0rad)
  BaseFeature = -> Cylinder568
  Height = 0.265
  Length = 0.23
  MapMode = 5
  Placement = pos=(-20.1,18.635,1.635) rot=(0,0,1;0rad)
  Support = -> [XY_Plane317]
  Width = 0.23
FEATURE [PartDesign::Body] Body280  label="pin280"
  Group = -> [Box2801,Box2825,Box2808,Box2820,Box2815,Fillet854,Fillet863,Box2834,Cylinder569,Box2818,Box2826,Fillet853,Box2821,Cylinder568,Box2811]
  Origin = -> Origin326
  Placement = pos=(0,-4,0) rot=(0,0,1;0rad)
  Tip = -> Box2811
FEATURE [PartDesign::SubtractiveBox] Box2840
  AttacherType = Attacher::AttachEngine3D
  AttachmentOffset = pos=(-21.35,18.635,0.35) rot=(0,0,1;0rad)
  BaseFeature = -> Box2817
  Height = 1.55
  Length = 0.5
  MapMode = 5
  Placement = pos=(-21.35,18.635,0.35) rot=(0,0,1;0rad)
  Support = -> [XY_Plane324]
  Width = 0.23
FEATURE [PartDesign::SubtractiveBox] Box2841
  AttacherType = Attacher::AttachEngine3D
  AttachmentOffset = pos=(-21.35,18.635,0.35) rot=(0,0,1;0rad)
  BaseFeature = -> Box2813
  Height = 1.55
  Length = 0.5
  MapMode = 5
  Placement = pos=(-21.35,18.635,0.35) rot=(0,0,1;0rad)
  Support = -> [XY_Plane320]
  Width = 0.23
FEATURE [PartDesign::SubtractiveBox] Box2804
  AttacherType = Attacher::AttachEngine3D
  AttachmentOffset = pos=(-20.5,18.63,0) rot=(0,0,1;0rad)
  BaseFeature = -> Box2841
  Height = 1.635
  Length = 0.5
  MapMode = 5
  Placement = pos=(-20.5,18.63,0) rot=(0,0,1;0rad)
  Support = -> [XY_Plane320]
  Width = 0.25
FEATURE [PartDesign::SubtractiveBox] Box2848
  AttacherType = Attacher::AttachEngine3D
  AttachmentOffset = pos=(-21.5005,18.625,0.235) rot=(0,-1,0;0.174533rad)
  BaseFeature = -> Box2795
  Height = 0.3
  Length = 0.6605
  MapMode = 5
  Placement = pos=(-21.5005,18.625,0.235) rot=(0,-1,0;0.174533rad)
  Support = -> [XY_Plane321]
  Width = 0.25
FEATURE [PartDesign::Fillet] Fillet860
  Base = -> Box2848 [Edge2]
  BaseFeature = -> Box2848
  Placement = pos=(-21.5005,18.625,0.235) rot=(0,-1,0;0.174533rad)
  Radius = 0.05
  SupportTransform = false
FEATURE [PartDesign::Fillet] Fillet846
  Base = -> Fillet860 [Edge33]
  BaseFeature = -> Fillet860
  Placement = pos=(-21.5005,18.625,0.235) rot=(0,-1,0;0.174533rad)
  Radius = 0.5
  SupportTransform = false
FEATURE [PartDesign::AdditiveBox] Box2755
  AttacherType = Attacher::AttachEngine3D
  AttachmentOffset = pos=(-21.1,18.635,0.305) rot=(0,1,0;0.785398rad)
  BaseFeature = -> Fillet846
  Height = 0.375
  Length = 0.2
  MapMode = 5
  Placement = pos=(-21.1,18.635,0.305) rot=(0,1,0;0.785398rad)
  Support = -> [XY_Plane321]
  Width = 0.23
FEATURE [PartDesign::SubtractiveCylinder] Cylinder556
  Angle = 360
  AttacherType = Attacher::AttachEngine3D
  AttachmentOffset = pos=(-21.055,18.935,0.52) rot=(1,0,0;1.5708rad)
  BaseFeature = -> Box2755
  Height = 0.375
  MapMode = 5
  Placement = pos=(-21.055,18.935,0.52) rot=(1,0,0;1.5708rad)
  Radius = 0.205
  Support = -> [XY_Plane321]
FEATURE [PartDesign::SubtractiveBox] Box2765
  AttacherType = Attacher::AttachEngine3D
  AttachmentOffset = pos=(-20.95,18.635,0.53) rot=(0,0,1;0rad)
  BaseFeature = -> Cylinder556
  Height = 0.5
  Length = 0.1
  MapMode = 5
  Placement = pos=(-20.95,18.635,0.53) rot=(0,0,1;0rad)
  Support = -> [XY_Plane321]
  Width = 0.23
FEATURE [PartDesign::SubtractiveBox] Box2770
  AttacherType = Attacher::AttachEngine3D
  AttachmentOffset = pos=(-21.15,18.635,0.297) rot=(0,-1,0;0.174533rad)
  BaseFeature = -> Box2765
  Height = 0.115
  Length = 0.115
  MapMode = 5
  Placement = pos=(-21.15,18.635,0.297) rot=(0,-1,0;0.174533rad)
  Support = -> [XY_Plane321]
  Width = 0.23
FEATURE [PartDesign::Fillet] Fillet855
  Base = -> Box2770 [Edge28]
  BaseFeature = -> Box2770
  Placement = pos=(-21.15,18.635,0.297) rot=(0,-1,0;0.174533rad)
  Radius = 0.375
  SupportTransform = false
FEATURE [PartDesign::AdditiveBox] Box2792
  AttacherType = Attacher::AttachEngine3D
  AttachmentOffset = pos=(-20.7,18.635,1.55) rot=(0,1,0;0.785398rad)
  BaseFeature = -> Fillet855
  Height = 0.375
  Length = 0.23
  MapMode = 5
  Placement = pos=(-20.7,18.635,1.55) rot=(0,1,0;0.785398rad)
  Support = -> [XY_Plane321]
  Width = 0.23
FEATURE [PartDesign::SubtractiveCylinder] Cylinder560
  Angle = 360
  AttacherType = Attacher::AttachEngine3D
  AttachmentOffset = pos=(-20.271,18.635,1.4056) rot=(-1,0,0;1.5708rad)
  BaseFeature = -> Box2792
  Height = 0.23
  MapMode = 5
  Placement = pos=(-20.271,18.635,1.4056) rot=(-1,0,0;1.5708rad)
  Radius = 0.23
  Support = -> [XY_Plane321]
FEATURE [PartDesign::AdditiveBox] Box2789
  AttacherType = Attacher::AttachEngine3D
  AttachmentOffset = pos=(-20.1,18.635,1.635) rot=(0,0,1;0rad)
  BaseFeature = -> Cylinder560
  Height = 0.265
  Length = 0.23
  MapMode = 5
  Placement = pos=(-20.1,18.635,1.635) rot=(0,0,1;0rad)
  Support = -> [XY_Plane321]
  Width = 0.23
FEATURE [PartDesign::Body] Body283  label="pin283"
  Group = -> [Box2805,Box2797,Box2782,Box2795,Box2848,Fillet860,Fillet846,Box2755,Cylinder556,Box2765,Box2770,Fillet855,Box2792,Cylinder560,Box2789]
  Origin = -> Origin297
  Placement = pos=(0,-4.5,0) rot=(0,0,1;0rad)
  Tip = -> Box2789
FEATURE [PartDesign::SubtractiveBox] Box2851
  AttacherType = Attacher::AttachEngine3D
  AttachmentOffset = pos=(-20.5,18.63,0) rot=(0,0,1;0rad)
  BaseFeature = -> Box2840
  Height = 1.635
  Length = 0.5
  MapMode = 5
  Placement = pos=(-20.5,18.63,0) rot=(0,0,1;0rad)
  Support = -> [XY_Plane324]
  Width = 0.25
FEATURE [PartDesign::SubtractiveBox] Box2824
  AttacherType = Attacher::AttachEngine3D
  AttachmentOffset = pos=(-21.19,18.635,-0.12) rot=(0,-1,0;0.15708rad)
  BaseFeature = -> Box2851
  Height = 0.12
  Length = 0.725
  MapMode = 5
  Placement = pos=(-21.19,18.635,-0.12) rot=(0,-1,0;0.15708rad)
  Support = -> [XY_Plane324]
  Width = 0.25
FEATURE [PartDesign::SubtractiveBox] Box2819
  AttacherType = Attacher::AttachEngine3D
  AttachmentOffset = pos=(-21.5005,18.625,0.235) rot=(0,-1,0;0.174533rad)
  BaseFeature = -> Box2824
  Height = 0.3
  Length = 0.6605
  MapMode = 5
  Placement = pos=(-21.5005,18.625,0.235) rot=(0,-1,0;0.174533rad)
  Support = -> [XY_Plane324]
  Width = 0.25
FEATURE [PartDesign::Fillet] Fillet857
  Base = -> Box2819 [Edge2]
  BaseFeature = -> Box2819
  Placement = pos=(-21.5005,18.625,0.235) rot=(0,-1,0;0.174533rad)
  Radius = 0.05
  SupportTransform = false
FEATURE [PartDesign::Fillet] Fillet841
  Base = -> Fillet857 [Edge33]
  BaseFeature = -> Fillet857
  Placement = pos=(-21.5005,18.625,0.235) rot=(0,-1,0;0.174533rad)
  Radius = 0.5
  SupportTransform = false
FEATURE [PartDesign::AdditiveBox] Box2836
  AttacherType = Attacher::AttachEngine3D
  AttachmentOffset = pos=(-21.1,18.635,0.305) rot=(0,1,0;0.785398rad)
  BaseFeature = -> Fillet841
  Height = 0.375
  Length = 0.2
  MapMode = 5
  Placement = pos=(-21.1,18.635,0.305) rot=(0,1,0;0.785398rad)
  Support = -> [XY_Plane324]
  Width = 0.23
FEATURE [PartDesign::SubtractiveCylinder] Cylinder574
  Angle = 360
  AttacherType = Attacher::AttachEngine3D
  AttachmentOffset = pos=(-21.055,18.935,0.52) rot=(1,0,0;1.5708rad)
  BaseFeature = -> Box2836
  Height = 0.375
  MapMode = 5
  Placement = pos=(-21.055,18.935,0.52) rot=(1,0,0;1.5708rad)
  Radius = 0.205
  Support = -> [XY_Plane324]
FEATURE [PartDesign::SubtractiveBox] Box2837
  AttacherType = Attacher::AttachEngine3D
  AttachmentOffset = pos=(-20.95,18.635,0.53) rot=(0,0,1;0rad)
  BaseFeature = -> Cylinder574
  Height = 0.5
  Length = 0.1
  MapMode = 5
  Placement = pos=(-20.95,18.635,0.53) rot=(0,0,1;0rad)
  Support = -> [XY_Plane324]
  Width = 0.23
FEATURE [PartDesign::SubtractiveBox] Box2823
  AttacherType = Attacher::AttachEngine3D
  AttachmentOffset = pos=(-21.15,18.635,0.297) rot=(0,-1,0;0.174533rad)
  BaseFeature = -> Box2837
  Height = 0.115
  Length = 0.115
  MapMode = 5
  Placement = pos=(-21.15,18.635,0.297) rot=(0,-1,0;0.174533rad)
  Support = -> [XY_Plane324]
  Width = 0.23
FEATURE [PartDesign::Fillet] Fillet843
  Base = -> Box2823 [Edge28]
  BaseFeature = -> Box2823
  Placement = pos=(-21.15,18.635,0.297) rot=(0,-1,0;0.174533rad)
  Radius = 0.375
  SupportTransform = false
FEATURE [PartDesign::AdditiveBox] Box2842
  AttacherType = Attacher::AttachEngine3D
  AttachmentOffset = pos=(-20.7,18.635,1.55) rot=(0,1,0;0.785398rad)
  BaseFeature = -> Fillet843
  Height = 0.375
  Length = 0.23
  MapMode = 5
  Placement = pos=(-20.7,18.635,1.55) rot=(0,1,0;0.785398rad)
  Support = -> [XY_Plane324]
  Width = 0.23
FEATURE [PartDesign::SubtractiveCylinder] Cylinder571
  Angle = 360
  AttacherType = Attacher::AttachEngine3D
  AttachmentOffset = pos=(-20.271,18.635,1.4056) rot=(-1,0,0;1.5708rad)
  BaseFeature = -> Box2842
  Height = 0.23
  MapMode = 5
  Placement = pos=(-20.271,18.635,1.4056) rot=(-1,0,0;1.5708rad)
  Radius = 0.23
  Support = -> [XY_Plane324]
FEATURE [PartDesign::AdditiveBox] Box2802
  AttacherType = Attacher::AttachEngine3D
  AttachmentOffset = pos=(-20.1,18.635,1.635) rot=(0,0,1;0rad)
  BaseFeature = -> Cylinder571
  Height = 0.265
  Length = 0.23
  MapMode = 5
  Placement = pos=(-20.1,18.635,1.635) rot=(0,0,1;0rad)
  Support = -> [XY_Plane324]
  Width = 0.23
FEATURE [PartDesign::Body] Body282  label="pin282"
  Group = -> [Box2817,Box2840,Box2851,Box2824,Box2819,Fillet857,Fillet841,Box2836,Cylinder574,Box2837,Box2823,Fillet843,Box2842,Cylinder571,Box2802]
  Origin = -> Origin322
  Placement = pos=(0,-3.5,0) rot=(0,0,1;0rad)
  Tip = -> Box2802
FEATURE [PartDesign::SubtractiveBox] Box2855
  AttacherType = Attacher::AttachEngine3D
  AttachmentOffset = pos=(-21.19,18.635,-0.12) rot=(0,-1,0;0.15708rad)
  BaseFeature = -> Box2804
  Height = 0.12
  Length = 0.725
  MapMode = 5
  Placement = pos=(-21.19,18.635,-0.12) rot=(0,-1,0;0.15708rad)
  Support = -> [XY_Plane320]
  Width = 0.25
FEATURE [PartDesign::SubtractiveBox] Box2812
  AttacherType = Attacher::AttachEngine3D
  AttachmentOffset = pos=(-21.5005,18.625,0.235) rot=(0,-1,0;0.174533rad)
  BaseFeature = -> Box2855
  Height = 0.3
  Length = 0.6605
  MapMode = 5
  Placement = pos=(-21.5005,18.625,0.235) rot=(0,-1,0;0.174533rad)
  Support = -> [XY_Plane320]
  Width = 0.25
FEATURE [PartDesign::Fillet] Fillet852
  Base = -> Box2812 [Edge2]
  BaseFeature = -> Box2812
  Placement = pos=(-21.5005,18.625,0.235) rot=(0,-1,0;0.174533rad)
  Radius = 0.05
  SupportTransform = false
FEATURE [PartDesign::Fillet] Fillet865
  Base = -> Fillet852 [Edge33]
  BaseFeature = -> Fillet852
  Placement = pos=(-21.5005,18.625,0.235) rot=(0,-1,0;0.174533rad)
  Radius = 0.5
  SupportTransform = false
FEATURE [PartDesign::AdditiveBox] Box2791
  AttacherType = Attacher::AttachEngine3D
  AttachmentOffset = pos=(-21.1,18.635,0.305) rot=(0,1,0;0.785398rad)
  BaseFeature = -> Fillet865
  Height = 0.375
  Length = 0.2
  MapMode = 5
  Placement = pos=(-21.1,18.635,0.305) rot=(0,1,0;0.785398rad)
  Support = -> [XY_Plane320]
  Width = 0.23
FEATURE [PartDesign::SubtractiveCylinder] Cylinder561
  Angle = 360
  AttacherType = Attacher::AttachEngine3D
  AttachmentOffset = pos=(-21.055,18.935,0.52) rot=(1,0,0;1.5708rad)
  BaseFeature = -> Box2791
  Height = 0.375
  MapMode = 5
  Placement = pos=(-21.055,18.935,0.52) rot=(1,0,0;1.5708rad)
  Radius = 0.205
  Support = -> [XY_Plane320]
FEATURE [PartDesign::SubtractiveBox] Box2781
  AttacherType = Attacher::AttachEngine3D
  AttachmentOffset = pos=(-20.95,18.635,0.53) rot=(0,0,1;0rad)
  BaseFeature = -> Cylinder561
  Height = 0.5
  Length = 0.1
  MapMode = 5
  Placement = pos=(-20.95,18.635,0.53) rot=(0,0,1;0rad)
  Support = -> [XY_Plane320]
  Width = 0.23
FEATURE [PartDesign::SubtractiveBox] Box2827
  AttacherType = Attacher::AttachEngine3D
  AttachmentOffset = pos=(-21.15,18.635,0.297) rot=(0,-1,0;0.174533rad)
  BaseFeature = -> Box2781
  Height = 0.115
  Length = 0.115
  MapMode = 5
  Placement = pos=(-21.15,18.635,0.297) rot=(0,-1,0;0.174533rad)
  Support = -> [XY_Plane320]
  Width = 0.23
FEATURE [PartDesign::Fillet] Fillet856
  Base = -> Box2827 [Edge28]
  BaseFeature = -> Box2827
  Placement = pos=(-21.15,18.635,0.297) rot=(0,-1,0;0.174533rad)
  Radius = 0.375
  SupportTransform = false
FEATURE [PartDesign::AdditiveBox] Box2822
  AttacherType = Attacher::AttachEngine3D
  AttachmentOffset = pos=(-20.7,18.635,1.55) rot=(0,1,0;0.785398rad)
  BaseFeature = -> Fillet856
  Height = 0.375
  Length = 0.23
  MapMode = 5
  Placement = pos=(-20.7,18.635,1.55) rot=(0,1,0;0.785398rad)
  Support = -> [XY_Plane320]
  Width = 0.23
FEATURE [PartDesign::SubtractiveCylinder] Cylinder563
  Angle = 360
  AttacherType = Attacher::AttachEngine3D
  AttachmentOffset = pos=(-20.271,18.635,1.4056) rot=(-1,0,0;1.5708rad)
  BaseFeature = -> Box2822
  Height = 0.23
  MapMode = 5
  Placement = pos=(-20.271,18.635,1.4056) rot=(-1,0,0;1.5708rad)
  Radius = 0.23
  Support = -> [XY_Plane320]
FEATURE [PartDesign::AdditiveBox] Box2833
  AttacherType = Attacher::AttachEngine3D
  AttachmentOffset = pos=(-20.1,18.635,1.635) rot=(0,0,1;0rad)
  BaseFeature = -> Cylinder563
  Height = 0.265
  Length = 0.23
  MapMode = 5
  Placement = pos=(-20.1,18.635,1.635) rot=(0,0,1;0rad)
  Support = -> [XY_Plane320]
  Width = 0.23
FEATURE [PartDesign::Body] Body285  label="pin285"
  Group = -> [Box2813,Box2841,Box2804,Box2855,Box2812,Fillet852,Fillet865,Box2791,Cylinder561,Box2781,Box2827,Fillet856,Box2822,Cylinder563,Box2833]
  Origin = -> Origin295
  Placement = pos=(0,-3,0) rot=(0,0,1;0rad)
  Tip = -> Box2833
FEATURE [PartDesign::AdditiveBox] Box2861
  AttacherType = Attacher::AttachEngine3D
  AttachmentOffset = pos=(-21.3,18.635,0) rot=(0,0,1;0rad)
  Height = 1.9
  Length = 1.3
  MapMode = 5
  Placement = pos=(-21.3,18.635,0) rot=(0,0,1;0rad)
  Support = -> [XY_Plane312]
  Width = 0.23
FEATURE [PartDesign::SubtractiveBox] Box2863
  AttacherType = Attacher::AttachEngine3D
  AttachmentOffset = pos=(-21.35,18.635,0.35) rot=(0,0,1;0rad)
  BaseFeature = -> Box2861
  Height = 1.55
  Length = 0.5
  MapMode = 5
  Placement = pos=(-21.35,18.635,0.35) rot=(0,0,1;0rad)
  Support = -> [XY_Plane312]
  Width = 0.23
FEATURE [PartDesign::SubtractiveBox] Box2844
  AttacherType = Attacher::AttachEngine3D
  AttachmentOffset = pos=(-20.5,18.63,0) rot=(0,0,1;0rad)
  BaseFeature = -> Box2863
  Height = 1.635
  Length = 0.5
  MapMode = 5
  Placement = pos=(-20.5,18.63,0) rot=(0,0,1;0rad)
  Support = -> [XY_Plane312]
  Width = 0.25
FEATURE [PartDesign::SubtractiveBox] Box2853
  AttacherType = Attacher::AttachEngine3D
  AttachmentOffset = pos=(-21.19,18.635,-0.12) rot=(0,-1,0;0.15708rad)
  BaseFeature = -> Box2844
  Height = 0.12
  Length = 0.725
  MapMode = 5
  Placement = pos=(-21.19,18.635,-0.12) rot=(0,-1,0;0.15708rad)
  Support = -> [XY_Plane312]
  Width = 0.25
FEATURE [PartDesign::SubtractiveBox] Box2870
  AttacherType = Attacher::AttachEngine3D
  AttachmentOffset = pos=(-21.5005,18.625,0.235) rot=(0,-1,0;0.174533rad)
  BaseFeature = -> Box2853
  Height = 0.3
  Length = 0.6605
  MapMode = 5
  Placement = pos=(-21.5005,18.625,0.235) rot=(0,-1,0;0.174533rad)
  Support = -> [XY_Plane312]
  Width = 0.25
FEATURE [PartDesign::Fillet] Fillet844
  Base = -> Box2870 [Edge2]
  BaseFeature = -> Box2870
  Placement = pos=(-21.5005,18.625,0.235) rot=(0,-1,0;0.174533rad)
  Radius = 0.05
  SupportTransform = false
FEATURE [PartDesign::Fillet] Fillet830
  Base = -> Fillet844 [Edge33]
  BaseFeature = -> Fillet844
  Placement = pos=(-21.5005,18.625,0.235) rot=(0,-1,0;0.174533rad)
  Radius = 0.5
  SupportTransform = false
FEATURE [PartDesign::AdditiveBox] Box2839
  AttacherType = Attacher::AttachEngine3D
  AttachmentOffset = pos=(-21.1,18.635,0.305) rot=(0,1,0;0.785398rad)
  BaseFeature = -> Fillet830
  Height = 0.375
  Length = 0.2
  MapMode = 5
  Placement = pos=(-21.1,18.635,0.305) rot=(0,1,0;0.785398rad)
  Support = -> [XY_Plane312]
  Width = 0.23
FEATURE [PartDesign::SubtractiveCylinder] Cylinder566
  Angle = 360
  AttacherType = Attacher::AttachEngine3D
  AttachmentOffset = pos=(-21.055,18.935,0.52) rot=(1,0,0;1.5708rad)
  BaseFeature = -> Box2839
  Height = 0.375
  MapMode = 5
  Placement = pos=(-21.055,18.935,0.52) rot=(1,0,0;1.5708rad)
  Radius = 0.205
  Support = -> [XY_Plane312]
FEATURE [PartDesign::SubtractiveBox] Box2794
  AttacherType = Attacher::AttachEngine3D
  AttachmentOffset = pos=(-20.95,18.635,0.53) rot=(0,0,1;0rad)
  BaseFeature = -> Cylinder566
  Height = 0.5
  Length = 0.1
  MapMode = 5
  Placement = pos=(-20.95,18.635,0.53) rot=(0,0,1;0rad)
  Support = -> [XY_Plane312]
  Width = 0.23
FEATURE [PartDesign::SubtractiveBox] Box2790
  AttacherType = Attacher::AttachEngine3D
  AttachmentOffset = pos=(-21.15,18.635,0.297) rot=(0,-1,0;0.174533rad)
  BaseFeature = -> Box2794
  Height = 0.115
  Length = 0.115
  MapMode = 5
  Placement = pos=(-21.15,18.635,0.297) rot=(0,-1,0;0.174533rad)
  Support = -> [XY_Plane312]
  Width = 0.23
FEATURE [PartDesign::Fillet] Fillet862
  Base = -> Box2790 [Edge28]
  BaseFeature = -> Box2790
  Placement = pos=(-21.15,18.635,0.297) rot=(0,-1,0;0.174533rad)
  Radius = 0.375
  SupportTransform = false
FEATURE [PartDesign::AdditiveBox] Box2835
  AttacherType = Attacher::AttachEngine3D
  AttachmentOffset = pos=(-20.7,18.635,1.55) rot=(0,1,0;0.785398rad)
  BaseFeature = -> Fillet862
  Height = 0.375
  Length = 0.23
  MapMode = 5
  Placement = pos=(-20.7,18.635,1.55) rot=(0,1,0;0.785398rad)
  Support = -> [XY_Plane312]
  Width = 0.23
FEATURE [PartDesign::SubtractiveCylinder] Cylinder562
  Angle = 360
  AttacherType = Attacher::AttachEngine3D
  AttachmentOffset = pos=(-20.271,18.635,1.4056) rot=(-1,0,0;1.5708rad)
  BaseFeature = -> Box2835
  Height = 0.23
  MapMode = 5
  Placement = pos=(-20.271,18.635,1.4056) rot=(-1,0,0;1.5708rad)
  Radius = 0.23
  Support = -> [XY_Plane312]
FEATURE [PartDesign::AdditiveBox] Box2856
  AttacherType = Attacher::AttachEngine3D
  AttachmentOffset = pos=(-20.1,18.635,1.635) rot=(0,0,1;0rad)
  BaseFeature = -> Cylinder562
  Height = 0.265
  Length = 0.23
  MapMode = 5
  Placement = pos=(-20.1,18.635,1.635) rot=(0,0,1;0rad)
  Support = -> [XY_Plane312]
  Width = 0.23
FEATURE [PartDesign::Body] Body278  label="pin278"
  Group = -> [Box2861,Box2863,Box2844,Box2853,Box2870,Fillet844,Fillet830,Box2839,Cylinder566,Box2794,Box2790,Fillet862,Box2835,Cylinder562,Box2856]
  Origin = -> Origin306
  Tip = -> Box2856
FEATURE [PartDesign::SubtractiveBox] Box2871
  AttacherType = Attacher::AttachEngine3D
  AttachmentOffset = pos=(-20.5,18.63,0) rot=(0,0,1;0rad)
  BaseFeature = -> Box2774
  Height = 1.635
  Length = 0.5
  MapMode = 5
  Placement = pos=(-20.5,18.63,0) rot=(0,0,1;0rad)
  Support = -> [XY_Plane309]
  Width = 0.25
FEATURE [PartDesign::SubtractiveBox] Box2859
  AttacherType = Attacher::AttachEngine3D
  AttachmentOffset = pos=(-21.19,18.635,-0.12) rot=(0,-1,0;0.15708rad)
  BaseFeature = -> Box2871
  Height = 0.12
  Length = 0.725
  MapMode = 5
  Placement = pos=(-21.19,18.635,-0.12) rot=(0,-1,0;0.15708rad)
  Support = -> [XY_Plane309]
  Width = 0.25
FEATURE [PartDesign::SubtractiveBox] Box2769
  AttacherType = Attacher::AttachEngine3D
  AttachmentOffset = pos=(-21.5005,18.625,0.235) rot=(0,-1,0;0.174533rad)
  BaseFeature = -> Box2859
  Height = 0.3
  Length = 0.6605
  MapMode = 5
  Placement = pos=(-21.5005,18.625,0.235) rot=(0,-1,0;0.174533rad)
  Support = -> [XY_Plane309]
  Width = 0.25
FEATURE [PartDesign::Fillet] Fillet834
  Base = -> Box2769 [Edge2]
  BaseFeature = -> Box2769
  Placement = pos=(-21.5005,18.625,0.235) rot=(0,-1,0;0.174533rad)
  Radius = 0.05
  SupportTransform = false
FEATURE [PartDesign::Fillet] Fillet849
  Base = -> Fillet834 [Edge33]
  BaseFeature = -> Fillet834
  Placement = pos=(-21.5005,18.625,0.235) rot=(0,-1,0;0.174533rad)
  Radius = 0.5
  SupportTransform = false
FEATURE [PartDesign::AdditiveBox] Box2877
  AttacherType = Attacher::AttachEngine3D
  AttachmentOffset = pos=(-21.3,18.635,0) rot=(0,0,1;0rad)
  Height = 1.9
  Length = 1.3
  MapMode = 5
  Placement = pos=(-21.3,18.635,0) rot=(0,0,1;0rad)
  Support = -> [XY_Plane319]
  Width = 0.23
FEATURE [PartDesign::SubtractiveBox] Box2830
  AttacherType = Attacher::AttachEngine3D
  AttachmentOffset = pos=(-21.35,18.635,0.35) rot=(0,0,1;0rad)
  BaseFeature = -> Box2877
  Height = 1.55
  Length = 0.5
  MapMode = 5
  Placement = pos=(-21.35,18.635,0.35) rot=(0,0,1;0rad)
  Support = -> [XY_Plane319]
  Width = 0.23
FEATURE [PartDesign::SubtractiveBox] Box2832
  AttacherType = Attacher::AttachEngine3D
  AttachmentOffset = pos=(-20.5,18.63,0) rot=(0,0,1;0rad)
  BaseFeature = -> Box2830
  Height = 1.635
  Length = 0.5
  MapMode = 5
  Placement = pos=(-20.5,18.63,0) rot=(0,0,1;0rad)
  Support = -> [XY_Plane319]
  Width = 0.25
FEATURE [PartDesign::SubtractiveBox] Box2868
  AttacherType = Attacher::AttachEngine3D
  AttachmentOffset = pos=(-21.19,18.635,-0.12) rot=(0,-1,0;0.15708rad)
  BaseFeature = -> Box2832
  Height = 0.12
  Length = 0.725
  MapMode = 5
  Placement = pos=(-21.19,18.635,-0.12) rot=(0,-1,0;0.15708rad)
  Support = -> [XY_Plane319]
  Width = 0.25
FEATURE [PartDesign::SubtractiveBox] Box2843
  AttacherType = Attacher::AttachEngine3D
  AttachmentOffset = pos=(-21.5005,18.625,0.235) rot=(0,-1,0;0.174533rad)
  BaseFeature = -> Box2868
  Height = 0.3
  Length = 0.6605
  MapMode = 5
  Placement = pos=(-21.5005,18.625,0.235) rot=(0,-1,0;0.174533rad)
  Support = -> [XY_Plane319]
  Width = 0.25
FEATURE [PartDesign::Fillet] Fillet821
  Base = -> Box2843 [Edge2]
  BaseFeature = -> Box2843
  Placement = pos=(-21.5005,18.625,0.235) rot=(0,-1,0;0.174533rad)
  Radius = 0.05
  SupportTransform = false
FEATURE [PartDesign::Fillet] Fillet840
  Base = -> Fillet821 [Edge33]
  BaseFeature = -> Fillet821
  Placement = pos=(-21.5005,18.625,0.235) rot=(0,-1,0;0.174533rad)
  Radius = 0.5
  SupportTransform = false
FEATURE [PartDesign::AdditiveBox] Box2852
  AttacherType = Attacher::AttachEngine3D
  AttachmentOffset = pos=(-21.1,18.635,0.305) rot=(0,1,0;0.785398rad)
  BaseFeature = -> Fillet840
  Height = 0.375
  Length = 0.2
  MapMode = 5
  Placement = pos=(-21.1,18.635,0.305) rot=(0,1,0;0.785398rad)
  Support = -> [XY_Plane319]
  Width = 0.23
FEATURE [PartDesign::SubtractiveCylinder] Cylinder575
  Angle = 360
  AttacherType = Attacher::AttachEngine3D
  AttachmentOffset = pos=(-21.055,18.935,0.52) rot=(1,0,0;1.5708rad)
  BaseFeature = -> Box2852
  Height = 0.375
  MapMode = 5
  Placement = pos=(-21.055,18.935,0.52) rot=(1,0,0;1.5708rad)
  Radius = 0.205
  Support = -> [XY_Plane319]
FEATURE [PartDesign::SubtractiveBox] Box2845
  AttacherType = Attacher::AttachEngine3D
  AttachmentOffset = pos=(-20.95,18.635,0.53) rot=(0,0,1;0rad)
  BaseFeature = -> Cylinder575
  Height = 0.5
  Length = 0.1
  MapMode = 5
  Placement = pos=(-20.95,18.635,0.53) rot=(0,0,1;0rad)
  Support = -> [XY_Plane319]
  Width = 0.23
FEATURE [PartDesign::SubtractiveBox] Box2850
  AttacherType = Attacher::AttachEngine3D
  AttachmentOffset = pos=(-21.15,18.635,0.297) rot=(0,-1,0;0.174533rad)
  BaseFeature = -> Box2845
  Height = 0.115
  Length = 0.115
  MapMode = 5
  Placement = pos=(-21.15,18.635,0.297) rot=(0,-1,0;0.174533rad)
  Support = -> [XY_Plane319]
  Width = 0.23
FEATURE [PartDesign::Fillet] Fillet842
  Base = -> Box2850 [Edge28]
  BaseFeature = -> Box2850
  Placement = pos=(-21.15,18.635,0.297) rot=(0,-1,0;0.174533rad)
  Radius = 0.375
  SupportTransform = false
FEATURE [PartDesign::AdditiveBox] Box2854
  AttacherType = Attacher::AttachEngine3D
  AttachmentOffset = pos=(-20.7,18.635,1.55) rot=(0,1,0;0.785398rad)
  BaseFeature = -> Fillet842
  Height = 0.375
  Length = 0.23
  MapMode = 5
  Placement = pos=(-20.7,18.635,1.55) rot=(0,1,0;0.785398rad)
  Support = -> [XY_Plane319]
  Width = 0.23
FEATURE [PartDesign::SubtractiveCylinder] Cylinder576
  Angle = 360
  AttacherType = Attacher::AttachEngine3D
  AttachmentOffset = pos=(-20.271,18.635,1.4056) rot=(-1,0,0;1.5708rad)
  BaseFeature = -> Box2854
  Height = 0.23
  MapMode = 5
  Placement = pos=(-20.271,18.635,1.4056) rot=(-1,0,0;1.5708rad)
  Radius = 0.23
  Support = -> [XY_Plane319]
FEATURE [PartDesign::AdditiveBox] Box2847
  AttacherType = Attacher::AttachEngine3D
  AttachmentOffset = pos=(-20.1,18.635,1.635) rot=(0,0,1;0rad)
  BaseFeature = -> Cylinder576
  Height = 0.265
  Length = 0.23
  MapMode = 5
  Placement = pos=(-20.1,18.635,1.635) rot=(0,0,1;0rad)
  Support = -> [XY_Plane319]
  Width = 0.23
FEATURE [PartDesign::Body] Body277  label="pin277"
  Group = -> [Box2877,Box2830,Box2832,Box2868,Box2843,Fillet821,Fillet840,Box2852,Cylinder575,Box2845,Box2850,Fillet842,Box2854,Cylinder576,Box2847]
  Origin = -> Origin270
  Placement = pos=(0,-0.5,0) rot=(0,0,1;0rad)
  Tip = -> Box2847
FEATURE [PartDesign::SubtractiveBox] Box2878
  AttacherType = Attacher::AttachEngine3D
  AttachmentOffset = pos=(-20.5,18.63,0) rot=(0,0,1;0rad)
  BaseFeature = -> Box2767
  Height = 1.635
  Length = 0.5
  MapMode = 5
  Placement = pos=(-20.5,18.63,0) rot=(0,0,1;0rad)
  Support = -> [XY_Plane315]
  Width = 0.25
FEATURE [PartDesign::SubtractiveBox] Box2764
  AttacherType = Attacher::AttachEngine3D
  AttachmentOffset = pos=(-21.19,18.635,-0.12) rot=(0,-1,0;0.15708rad)
  BaseFeature = -> Box2878
  Height = 0.12
  Length = 0.725
  MapMode = 5
  Placement = pos=(-21.19,18.635,-0.12) rot=(0,-1,0;0.15708rad)
  Support = -> [XY_Plane315]
  Width = 0.25
FEATURE [PartDesign::SubtractiveBox] Box2777
  AttacherType = Attacher::AttachEngine3D
  AttachmentOffset = pos=(-21.5005,18.625,0.235) rot=(0,-1,0;0.174533rad)
  BaseFeature = -> Box2764
  Height = 0.3
  Length = 0.6605
  MapMode = 5
  Placement = pos=(-21.5005,18.625,0.235) rot=(0,-1,0;0.174533rad)
  Support = -> [XY_Plane315]
  Width = 0.25
FEATURE [PartDesign::Fillet] Fillet824
  Base = -> Box2777 [Edge2]
  BaseFeature = -> Box2777
  Placement = pos=(-21.5005,18.625,0.235) rot=(0,-1,0;0.174533rad)
  Radius = 0.05
  SupportTransform = false
FEATURE [PartDesign::Fillet] Fillet836
  Base = -> Fillet824 [Edge33]
  BaseFeature = -> Fillet824
  Placement = pos=(-21.5005,18.625,0.235) rot=(0,-1,0;0.174533rad)
  Radius = 0.5
  SupportTransform = false
FEATURE [PartDesign::AdditiveBox] Box2882
  AttacherType = Attacher::AttachEngine3D
  AttachmentOffset = pos=(-21.1,18.635,0.305) rot=(0,1,0;0.785398rad)
  BaseFeature = -> Fillet836
  Height = 0.375
  Length = 0.2
  MapMode = 5
  Placement = pos=(-21.1,18.635,0.305) rot=(0,1,0;0.785398rad)
  Support = -> [XY_Plane315]
  Width = 0.23
FEATURE [PartDesign::AdditiveBox] Box2883
  AttacherType = Attacher::AttachEngine3D
  AttachmentOffset = pos=(-21.3,18.635,0) rot=(0,0,1;0rad)
  Height = 1.9
  Length = 1.3
  MapMode = 5
  Placement = pos=(-21.3,18.635,0) rot=(0,0,1;0rad)
  Support = -> [XY_Plane311]
  Width = 0.23
FEATURE [PartDesign::SubtractiveBox] Box2879
  AttacherType = Attacher::AttachEngine3D
  AttachmentOffset = pos=(-21.35,18.635,0.35) rot=(0,0,1;0rad)
  BaseFeature = -> Box2883
  Height = 1.55
  Length = 0.5
  MapMode = 5
  Placement = pos=(-21.35,18.635,0.35) rot=(0,0,1;0rad)
  Support = -> [XY_Plane311]
  Width = 0.23
FEATURE [PartDesign::SubtractiveBox] Box2860
  AttacherType = Attacher::AttachEngine3D
  AttachmentOffset = pos=(-20.5,18.63,0) rot=(0,0,1;0rad)
  BaseFeature = -> Box2879
  Height = 1.635
  Length = 0.5
  MapMode = 5
  Placement = pos=(-20.5,18.63,0) rot=(0,0,1;0rad)
  Support = -> [XY_Plane311]
  Width = 0.25
FEATURE [PartDesign::SubtractiveBox] Box2865
  AttacherType = Attacher::AttachEngine3D
  AttachmentOffset = pos=(-21.19,18.635,-0.12) rot=(0,-1,0;0.15708rad)
  BaseFeature = -> Box2860
  Height = 0.12
  Length = 0.725
  MapMode = 5
  Placement = pos=(-21.19,18.635,-0.12) rot=(0,-1,0;0.15708rad)
  Support = -> [XY_Plane311]
  Width = 0.25
FEATURE [PartDesign::SubtractiveBox] Box2849
  AttacherType = Attacher::AttachEngine3D
  AttachmentOffset = pos=(-21.5005,18.625,0.235) rot=(0,-1,0;0.174533rad)
  BaseFeature = -> Box2865
  Height = 0.3
  Length = 0.6605
  MapMode = 5
  Placement = pos=(-21.5005,18.625,0.235) rot=(0,-1,0;0.174533rad)
  Support = -> [XY_Plane311]
  Width = 0.25
FEATURE [PartDesign::Fillet] Fillet847
  Base = -> Box2849 [Edge2]
  BaseFeature = -> Box2849
  Placement = pos=(-21.5005,18.625,0.235) rot=(0,-1,0;0.174533rad)
  Radius = 0.05
  SupportTransform = false
FEATURE [PartDesign::Fillet] Fillet859
  Base = -> Fillet847 [Edge33]
  BaseFeature = -> Fillet847
  Placement = pos=(-21.5005,18.625,0.235) rot=(0,-1,0;0.174533rad)
  Radius = 0.5
  SupportTransform = false
FEATURE [PartDesign::AdditiveBox] Box2838
  AttacherType = Attacher::AttachEngine3D
  AttachmentOffset = pos=(-21.1,18.635,0.305) rot=(0,1,0;0.785398rad)
  BaseFeature = -> Fillet859
  Height = 0.375
  Length = 0.2
  MapMode = 5
  Placement = pos=(-21.1,18.635,0.305) rot=(0,1,0;0.785398rad)
  Support = -> [XY_Plane311]
  Width = 0.23
FEATURE [PartDesign::SubtractiveCylinder] Cylinder578
  Angle = 360
  AttacherType = Attacher::AttachEngine3D
  AttachmentOffset = pos=(-21.055,18.935,0.52) rot=(1,0,0;1.5708rad)
  BaseFeature = -> Box2838
  Height = 0.375
  MapMode = 5
  Placement = pos=(-21.055,18.935,0.52) rot=(1,0,0;1.5708rad)
  Radius = 0.205
  Support = -> [XY_Plane311]
FEATURE [PartDesign::SubtractiveBox] Box2857
  AttacherType = Attacher::AttachEngine3D
  AttachmentOffset = pos=(-20.95,18.635,0.53) rot=(0,0,1;0rad)
  BaseFeature = -> Cylinder578
  Height = 0.5
  Length = 0.1
  MapMode = 5
  Placement = pos=(-20.95,18.635,0.53) rot=(0,0,1;0rad)
  Support = -> [XY_Plane311]
  Width = 0.23
FEATURE [PartDesign::SubtractiveBox] Box2858
  AttacherType = Attacher::AttachEngine3D
  AttachmentOffset = pos=(-21.15,18.635,0.297) rot=(0,-1,0;0.174533rad)
  BaseFeature = -> Box2857
  Height = 0.115
  Length = 0.115
  MapMode = 5
  Placement = pos=(-21.15,18.635,0.297) rot=(0,-1,0;0.174533rad)
  Support = -> [XY_Plane311]
  Width = 0.23
FEATURE [PartDesign::Fillet] Fillet833
  Base = -> Box2858 [Edge28]
  BaseFeature = -> Box2858
  Placement = pos=(-21.15,18.635,0.297) rot=(0,-1,0;0.174533rad)
  Radius = 0.375
  SupportTransform = false
FEATURE [PartDesign::AdditiveBox] Box2846
  AttacherType = Attacher::AttachEngine3D
  AttachmentOffset = pos=(-20.7,18.635,1.55) rot=(0,1,0;0.785398rad)
  BaseFeature = -> Fillet833
  Height = 0.375
  Length = 0.23
  MapMode = 5
  Placement = pos=(-20.7,18.635,1.55) rot=(0,1,0;0.785398rad)
  Support = -> [XY_Plane311]
  Width = 0.23
FEATURE [PartDesign::SubtractiveCylinder] Cylinder573
  Angle = 360
  AttacherType = Attacher::AttachEngine3D
  AttachmentOffset = pos=(-20.271,18.635,1.4056) rot=(-1,0,0;1.5708rad)
  BaseFeature = -> Box2846
  Height = 0.23
  MapMode = 5
  Placement = pos=(-20.271,18.635,1.4056) rot=(-1,0,0;1.5708rad)
  Radius = 0.23
  Support = -> [XY_Plane311]
FEATURE [PartDesign::AdditiveBox] Box2864
  AttacherType = Attacher::AttachEngine3D
  AttachmentOffset = pos=(-20.1,18.635,1.635) rot=(0,0,1;0rad)
  BaseFeature = -> Cylinder573
  Height = 0.265
  Length = 0.23
  MapMode = 5
  Placement = pos=(-20.1,18.635,1.635) rot=(0,0,1;0rad)
  Support = -> [XY_Plane311]
  Width = 0.23
FEATURE [PartDesign::Body] Body284  label="pin284"
  Group = -> [Box2883,Box2879,Box2860,Box2865,Box2849,Fillet847,Fillet859,Box2838,Cylinder578,Box2857,Box2858,Fillet833,Box2846,Cylinder573,Box2864]
  Origin = -> Origin299
  Placement = pos=(0,-1,0) rot=(0,0,1;0rad)
  Tip = -> Box2864
FEATURE [PartDesign::SubtractiveBox] Box2884
  AttacherType = Attacher::AttachEngine3D
  AttachmentOffset = pos=(-20.5,18.63,0) rot=(0,0,1;0rad)
  BaseFeature = -> Box2768
  Height = 1.635
  Length = 0.5
  MapMode = 5
  Placement = pos=(-20.5,18.63,0) rot=(0,0,1;0rad)
  Support = -> [XY_Plane314]
  Width = 0.25
FEATURE [PartDesign::SubtractiveBox] Box2828
  AttacherType = Attacher::AttachEngine3D
  AttachmentOffset = pos=(-21.19,18.635,-0.12) rot=(0,-1,0;0.15708rad)
  BaseFeature = -> Box2884
  Height = 0.12
  Length = 0.725
  MapMode = 5
  Placement = pos=(-21.19,18.635,-0.12) rot=(0,-1,0;0.15708rad)
  Support = -> [XY_Plane314]
  Width = 0.25
FEATURE [PartDesign::SubtractiveBox] Box2786
  AttacherType = Attacher::AttachEngine3D
  AttachmentOffset = pos=(-21.5005,18.625,0.235) rot=(0,-1,0;0.174533rad)
  BaseFeature = -> Box2828
  Height = 0.3
  Length = 0.6605
  MapMode = 5
  Placement = pos=(-21.5005,18.625,0.235) rot=(0,-1,0;0.174533rad)
  Support = -> [XY_Plane314]
  Width = 0.25
FEATURE [PartDesign::Fillet] Fillet839
  Base = -> Box2786 [Edge2]
  BaseFeature = -> Box2786
  Placement = pos=(-21.5005,18.625,0.235) rot=(0,-1,0;0.174533rad)
  Radius = 0.05
  SupportTransform = false
FEATURE [PartDesign::Fillet] Fillet829
  Base = -> Fillet839 [Edge33]
  BaseFeature = -> Fillet839
  Placement = pos=(-21.5005,18.625,0.235) rot=(0,-1,0;0.174533rad)
  Radius = 0.5
  SupportTransform = false
FEATURE [PartDesign::AdditiveBox] Box2862
  AttacherType = Attacher::AttachEngine3D
  AttachmentOffset = pos=(-21.1,18.635,0.305) rot=(0,1,0;0.785398rad)
  BaseFeature = -> Fillet829
  Height = 0.375
  Length = 0.2
  MapMode = 5
  Placement = pos=(-21.1,18.635,0.305) rot=(0,1,0;0.785398rad)
  Support = -> [XY_Plane314]
  Width = 0.23
FEATURE [PartDesign::SubtractiveCylinder] Cylinder567
  Angle = 360
  AttacherType = Attacher::AttachEngine3D
  AttachmentOffset = pos=(-21.055,18.935,0.52) rot=(1,0,0;1.5708rad)
  BaseFeature = -> Box2862
  Height = 0.375
  MapMode = 5
  Placement = pos=(-21.055,18.935,0.52) rot=(1,0,0;1.5708rad)
  Radius = 0.205
  Support = -> [XY_Plane314]
FEATURE [PartDesign::SubtractiveBox] Box2760
  AttacherType = Attacher::AttachEngine3D
  AttachmentOffset = pos=(-20.95,18.635,0.53) rot=(0,0,1;0rad)
  BaseFeature = -> Cylinder567
  Height = 0.5
  Length = 0.1
  MapMode = 5
  Placement = pos=(-20.95,18.635,0.53) rot=(0,0,1;0rad)
  Support = -> [XY_Plane314]
  Width = 0.23
FEATURE [PartDesign::SubtractiveBox] Box2766
  AttacherType = Attacher::AttachEngine3D
  AttachmentOffset = pos=(-21.15,18.635,0.297) rot=(0,-1,0;0.174533rad)
  BaseFeature = -> Box2760
  Height = 0.115
  Length = 0.115
  MapMode = 5
  Placement = pos=(-21.15,18.635,0.297) rot=(0,-1,0;0.174533rad)
  Support = -> [XY_Plane314]
  Width = 0.23
FEATURE [PartDesign::Fillet] Fillet832
  Base = -> Box2766 [Edge28]
  BaseFeature = -> Box2766
  Placement = pos=(-21.15,18.635,0.297) rot=(0,-1,0;0.174533rad)
  Radius = 0.375
  SupportTransform = false
FEATURE [PartDesign::AdditiveBox] Box2772
  AttacherType = Attacher::AttachEngine3D
  AttachmentOffset = pos=(-20.7,18.635,1.55) rot=(0,1,0;0.785398rad)
  BaseFeature = -> Fillet832
  Height = 0.375
  Length = 0.23
  MapMode = 5
  Placement = pos=(-20.7,18.635,1.55) rot=(0,1,0;0.785398rad)
  Support = -> [XY_Plane314]
  Width = 0.23
FEATURE [PartDesign::SubtractiveCylinder] Cylinder572
  Angle = 360
  AttacherType = Attacher::AttachEngine3D
  AttachmentOffset = pos=(-20.271,18.635,1.4056) rot=(-1,0,0;1.5708rad)
  BaseFeature = -> Box2772
  Height = 0.23
  MapMode = 5
  Placement = pos=(-20.271,18.635,1.4056) rot=(-1,0,0;1.5708rad)
  Radius = 0.23
  Support = -> [XY_Plane314]
FEATURE [PartDesign::AdditiveBox] Box2759
  AttacherType = Attacher::AttachEngine3D
  AttachmentOffset = pos=(-20.1,18.635,1.635) rot=(0,0,1;0rad)
  BaseFeature = -> Cylinder572
  Height = 0.265
  Length = 0.23
  MapMode = 5
  Placement = pos=(-20.1,18.635,1.635) rot=(0,0,1;0rad)
  Support = -> [XY_Plane314]
  Width = 0.23
FEATURE [PartDesign::Body] Body279  label="pin279"
  Group = -> [Box2779,Box2768,Box2884,Box2828,Box2786,Fillet839,Fillet829,Box2862,Cylinder567,Box2760,Box2766,Fillet832,Box2772,Cylinder572,Box2759]
  Origin = -> Origin294
  Placement = pos=(0,-2.5,0) rot=(0,0,1;0rad)
  Tip = -> Box2759
FEATURE [PartDesign::AdditiveBox] Box2885
  AttacherType = Attacher::AttachEngine3D
  AttachmentOffset = pos=(-21.1,18.635,0.305) rot=(0,1,0;0.785398rad)
  BaseFeature = -> Fillet849
  Height = 0.375
  Length = 0.2
  MapMode = 5
  Placement = pos=(-21.1,18.635,0.305) rot=(0,1,0;0.785398rad)
  Support = -> [XY_Plane309]
  Width = 0.23
FEATURE [PartDesign::SubtractiveCylinder] Cylinder577
  Angle = 360
  AttacherType = Attacher::AttachEngine3D
  AttachmentOffset = pos=(-21.055,18.935,0.52) rot=(1,0,0;1.5708rad)
  BaseFeature = -> Box2885
  Height = 0.375
  MapMode = 5
  Placement = pos=(-21.055,18.935,0.52) rot=(1,0,0;1.5708rad)
  Radius = 0.205
  Support = -> [XY_Plane309]
FEATURE [PartDesign::SubtractiveBox] Box2881
  AttacherType = Attacher::AttachEngine3D
  AttachmentOffset = pos=(-20.95,18.635,0.53) rot=(0,0,1;0rad)
  BaseFeature = -> Cylinder577
  Height = 0.5
  Length = 0.1
  MapMode = 5
  Placement = pos=(-20.95,18.635,0.53) rot=(0,0,1;0rad)
  Support = -> [XY_Plane309]
  Width = 0.23
FEATURE [PartDesign::SubtractiveBox] Box2869
  AttacherType = Attacher::AttachEngine3D
  AttachmentOffset = pos=(-21.15,18.635,0.297) rot=(0,-1,0;0.174533rad)
  BaseFeature = -> Box2881
  Height = 0.115
  Length = 0.115
  MapMode = 5
  Placement = pos=(-21.15,18.635,0.297) rot=(0,-1,0;0.174533rad)
  Support = -> [XY_Plane309]
  Width = 0.23
FEATURE [PartDesign::Fillet] Fillet851
  Base = -> Box2869 [Edge28]
  BaseFeature = -> Box2869
  Placement = pos=(-21.15,18.635,0.297) rot=(0,-1,0;0.174533rad)
  Radius = 0.375
  SupportTransform = false
FEATURE [PartDesign::AdditiveBox] Box2876
  AttacherType = Attacher::AttachEngine3D
  AttachmentOffset = pos=(-20.7,18.635,1.55) rot=(0,1,0;0.785398rad)
  BaseFeature = -> Fillet851
  Height = 0.375
  Length = 0.23
  MapMode = 5
  Placement = pos=(-20.7,18.635,1.55) rot=(0,1,0;0.785398rad)
  Support = -> [XY_Plane309]
  Width = 0.23
FEATURE [PartDesign::SubtractiveCylinder] Cylinder570
  Angle = 360
  AttacherType = Attacher::AttachEngine3D
  AttachmentOffset = pos=(-20.271,18.635,1.4056) rot=(-1,0,0;1.5708rad)
  BaseFeature = -> Box2876
  Height = 0.23
  MapMode = 5
  Placement = pos=(-20.271,18.635,1.4056) rot=(-1,0,0;1.5708rad)
  Radius = 0.23
  Support = -> [XY_Plane309]
FEATURE [PartDesign::AdditiveBox] Box2866
  AttacherType = Attacher::AttachEngine3D
  AttachmentOffset = pos=(-20.1,18.635,1.635) rot=(0,0,1;0rad)
  BaseFeature = -> Cylinder570
  Height = 0.265
  Length = 0.23
  MapMode = 5
  Placement = pos=(-20.1,18.635,1.635) rot=(0,0,1;0rad)
  Support = -> [XY_Plane309]
  Width = 0.23
FEATURE [PartDesign::Body] Body287  label="pin287"
  Group = -> [Box2785,Box2774,Box2871,Box2859,Box2769,Fillet834,Fillet849,Box2885,Cylinder577,Box2881,Box2869,Fillet851,Box2876,Cylinder570,Box2866]
  Origin = -> Origin316
  Placement = pos=(0,-1.5,0) rot=(0,0,1;0rad)
  Tip = -> Box2866
FEATURE [PartDesign::AdditiveBox] Box2892
  AttacherType = Attacher::AttachEngine3D
  AttachmentOffset = pos=(-21.3,18.635,0) rot=(0,0,1;0rad)
  Height = 1.9
  Length = 1.3
  MapMode = 5
  Placement = pos=(-21.3,18.635,0) rot=(0,0,1;0rad)
  Support = -> [XY_Plane325]
  Width = 0.23
FEATURE [PartDesign::SubtractiveBox] Box2875
  AttacherType = Attacher::AttachEngine3D
  AttachmentOffset = pos=(-21.35,18.635,0.35) rot=(0,0,1;0rad)
  BaseFeature = -> Box2892
  Height = 1.55
  Length = 0.5
  MapMode = 5
  Placement = pos=(-21.35,18.635,0.35) rot=(0,0,1;0rad)
  Support = -> [XY_Plane325]
  Width = 0.23
FEATURE [PartDesign::SubtractiveCylinder] Cylinder579
  Angle = 360
  AttacherType = Attacher::AttachEngine3D
  AttachmentOffset = pos=(-21.055,18.935,0.52) rot=(1,0,0;1.5708rad)
  BaseFeature = -> Box2882
  Height = 0.375
  MapMode = 5
  Placement = pos=(-21.055,18.935,0.52) rot=(1,0,0;1.5708rad)
  Radius = 0.205
  Support = -> [XY_Plane315]
FEATURE [PartDesign::SubtractiveBox] Box2788
  AttacherType = Attacher::AttachEngine3D
  AttachmentOffset = pos=(-20.95,18.635,0.53) rot=(0,0,1;0rad)
  BaseFeature = -> Cylinder579
  Height = 0.5
  Length = 0.1
  MapMode = 5
  Placement = pos=(-20.95,18.635,0.53) rot=(0,0,1;0rad)
  Support = -> [XY_Plane315]
  Width = 0.23
FEATURE [PartDesign::SubtractiveBox] Box2829
  AttacherType = Attacher::AttachEngine3D
  AttachmentOffset = pos=(-21.15,18.635,0.297) rot=(0,-1,0;0.174533rad)
  BaseFeature = -> Box2788
  Height = 0.115
  Length = 0.115
  MapMode = 5
  Placement = pos=(-21.15,18.635,0.297) rot=(0,-1,0;0.174533rad)
  Support = -> [XY_Plane315]
  Width = 0.23
FEATURE [PartDesign::Fillet] Fillet835
  Base = -> Box2829 [Edge28]
  BaseFeature = -> Box2829
  Placement = pos=(-21.15,18.635,0.297) rot=(0,-1,0;0.174533rad)
  Radius = 0.375
  SupportTransform = false
FEATURE [PartDesign::AdditiveBox] Box2867
  AttacherType = Attacher::AttachEngine3D
  AttachmentOffset = pos=(-20.7,18.635,1.55) rot=(0,1,0;0.785398rad)
  BaseFeature = -> Fillet835
  Height = 0.375
  Length = 0.23
  MapMode = 5
  Placement = pos=(-20.7,18.635,1.55) rot=(0,1,0;0.785398rad)
  Support = -> [XY_Plane315]
  Width = 0.23
FEATURE [PartDesign::SubtractiveCylinder] Cylinder557
  Angle = 360
  AttacherType = Attacher::AttachEngine3D
  AttachmentOffset = pos=(-20.271,18.635,1.4056) rot=(-1,0,0;1.5708rad)
  BaseFeature = -> Box2867
  Height = 0.23
  MapMode = 5
  Placement = pos=(-20.271,18.635,1.4056) rot=(-1,0,0;1.5708rad)
  Radius = 0.23
  Support = -> [XY_Plane315]
FEATURE [PartDesign::AdditiveBox] Box2775
  AttacherType = Attacher::AttachEngine3D
  AttachmentOffset = pos=(-20.1,18.635,1.635) rot=(0,0,1;0rad)
  BaseFeature = -> Cylinder557
  Height = 0.265
  Length = 0.23
  MapMode = 5
  Placement = pos=(-20.1,18.635,1.635) rot=(0,0,1;0rad)
  Support = -> [XY_Plane315]
  Width = 0.23
FEATURE [PartDesign::Body] Body286  label="pin286"
  Group = -> [Box2831,Box2767,Box2878,Box2764,Box2777,Fillet824,Fillet836,Box2882,Cylinder579,Box2788,Box2829,Fillet835,Box2867,Cylinder557,Box2775]
  Origin = -> Origin302
  Placement = pos=(0,-2,0) rot=(0,0,1;0rad)
  Tip = -> Box2775
FEATURE [App::Part] Part023  label="Pin-set021"
  Group = -> [Body278,Body277,Body284,Body287,Body286,Body279,Body285,Body282,Body280,Body283,Body281,Body288]
  Origin = -> Origin311
  Placement = pos=(0,-24,0) rot=(0,0,1;0rad)
FEATURE [PartDesign::AdditiveBox] Box2909
  AttacherType = Attacher::AttachEngine3D
  AttachmentOffset = pos=(-21.3,18.635,0) rot=(0,0,1;0rad)
  Height = 1.9
  Length = 1.3
  MapMode = 5
  Placement = pos=(-21.3,18.635,0) rot=(0,0,1;0rad)
  Support = -> [XY_Plane326]
  Width = 0.23
FEATURE [PartDesign::SubtractiveBox] Box2873
  AttacherType = Attacher::AttachEngine3D
  AttachmentOffset = pos=(-21.35,18.635,0.35) rot=(0,0,1;0rad)
  BaseFeature = -> Box2909
  Height = 1.55
  Length = 0.5
  MapMode = 5
  Placement = pos=(-21.35,18.635,0.35) rot=(0,0,1;0rad)
  Support = -> [XY_Plane326]
  Width = 0.23
FEATURE [PartDesign::AdditiveBox] Box2915
  AttacherType = Attacher::AttachEngine3D
  AttachmentOffset = pos=(-21.3,18.635,0) rot=(0,0,1;0rad)
  Height = 1.9
  Length = 1.3
  MapMode = 5
  Placement = pos=(-21.3,18.635,0) rot=(0,0,1;0rad)
  Support = -> [XY_Plane294]
  Width = 0.23
FEATURE [PartDesign::AdditiveBox] Box2917
  AttacherType = Attacher::AttachEngine3D
  AttachmentOffset = pos=(-21.3,18.635,0) rot=(0,0,1;0rad)
  Height = 1.9
  Length = 1.3
  MapMode = 5
  Placement = pos=(-21.3,18.635,0) rot=(0,0,1;0rad)
  Support = -> [XY_Plane328]
  Width = 0.23
FEATURE [PartDesign::AdditiveBox] Box2923
  AttacherType = Attacher::AttachEngine3D
  AttachmentOffset = pos=(-21.3,18.635,0) rot=(0,0,1;0rad)
  Height = 1.9
  Length = 1.3
  MapMode = 5
  Placement = pos=(-21.3,18.635,0) rot=(0,0,1;0rad)
  Support = -> [XY_Plane297]
  Width = 0.23
FEATURE [PartDesign::AdditiveBox] Box2927
  AttacherType = Attacher::AttachEngine3D
  AttachmentOffset = pos=(-21.3,18.635,0) rot=(0,0,1;0rad)
  Height = 1.9
  Length = 1.3
  MapMode = 5
  Placement = pos=(-21.3,18.635,0) rot=(0,0,1;0rad)
  Support = -> [XY_Plane298]
  Width = 0.23
FEATURE [PartDesign::SubtractiveBox] Box2928
  AttacherType = Attacher::AttachEngine3D
  AttachmentOffset = pos=(-21.35,18.635,0.35) rot=(0,0,1;0rad)
  BaseFeature = -> Box2917
  Height = 1.55
  Length = 0.5
  MapMode = 5
  Placement = pos=(-21.35,18.635,0.35) rot=(0,0,1;0rad)
  Support = -> [XY_Plane328]
  Width = 0.23
FEATURE [PartDesign::SubtractiveBox] Box2880
  AttacherType = Attacher::AttachEngine3D
  AttachmentOffset = pos=(-20.5,18.63,0) rot=(0,0,1;0rad)
  BaseFeature = -> Box2928
  Height = 1.635
  Length = 0.5
  MapMode = 5
  Placement = pos=(-20.5,18.63,0) rot=(0,0,1;0rad)
  Support = -> [XY_Plane328]
  Width = 0.25
FEATURE [PartDesign::SubtractiveBox] Box2899
  AttacherType = Attacher::AttachEngine3D
  AttachmentOffset = pos=(-21.19,18.635,-0.12) rot=(0,-1,0;0.15708rad)
  BaseFeature = -> Box2880
  Height = 0.12
  Length = 0.725
  MapMode = 5
  Placement = pos=(-21.19,18.635,-0.12) rot=(0,-1,0;0.15708rad)
  Support = -> [XY_Plane328]
  Width = 0.25
FEATURE [PartDesign::SubtractiveBox] Box2897
  AttacherType = Attacher::AttachEngine3D
  AttachmentOffset = pos=(-21.5005,18.625,0.235) rot=(0,-1,0;0.174533rad)
  BaseFeature = -> Box2899
  Height = 0.3
  Length = 0.6605
  MapMode = 5
  Placement = pos=(-21.5005,18.625,0.235) rot=(0,-1,0;0.174533rad)
  Support = -> [XY_Plane328]
  Width = 0.25
FEATURE [PartDesign::Fillet] Fillet879
  Base = -> Box2897 [Edge2]
  BaseFeature = -> Box2897
  Placement = pos=(-21.5005,18.625,0.235) rot=(0,-1,0;0.174533rad)
  Radius = 0.05
  SupportTransform = false
FEATURE [PartDesign::AdditiveBox] Box2932
  AttacherType = Attacher::AttachEngine3D
  AttachmentOffset = pos=(-21.3,18.635,0) rot=(0,0,1;0rad)
  Height = 1.9
  Length = 1.3
  MapMode = 5
  Placement = pos=(-21.3,18.635,0) rot=(0,0,1;0rad)
  Support = -> [XY_Plane299]
  Width = 0.23
FEATURE [PartDesign::SubtractiveBox] Box2935
  AttacherType = Attacher::AttachEngine3D
  AttachmentOffset = pos=(-21.35,18.635,0.35) rot=(0,0,1;0rad)
  BaseFeature = -> Box2915
  Height = 1.55
  Length = 0.5
  MapMode = 5
  Placement = pos=(-21.35,18.635,0.35) rot=(0,0,1;0rad)
  Support = -> [XY_Plane294]
  Width = 0.23
FEATURE [PartDesign::SubtractiveBox] Box2903
  AttacherType = Attacher::AttachEngine3D
  AttachmentOffset = pos=(-20.5,18.63,0) rot=(0,0,1;0rad)
  BaseFeature = -> Box2935
  Height = 1.635
  Length = 0.5
  MapMode = 5
  Placement = pos=(-20.5,18.63,0) rot=(0,0,1;0rad)
  Support = -> [XY_Plane294]
  Width = 0.25
FEATURE [PartDesign::SubtractiveBox] Box2922
  AttacherType = Attacher::AttachEngine3D
  AttachmentOffset = pos=(-21.19,18.635,-0.12) rot=(0,-1,0;0.15708rad)
  BaseFeature = -> Box2903
  Height = 0.12
  Length = 0.725
  MapMode = 5
  Placement = pos=(-21.19,18.635,-0.12) rot=(0,-1,0;0.15708rad)
  Support = -> [XY_Plane294]
  Width = 0.25
FEATURE [PartDesign::AdditiveBox] Box2936
  AttacherType = Attacher::AttachEngine3D
  AttachmentOffset = pos=(-21.3,18.635,0) rot=(0,0,1;0rad)
  Height = 1.9
  Length = 1.3
  MapMode = 5
  Placement = pos=(-21.3,18.635,0) rot=(0,0,1;0rad)
  Support = -> [XY_Plane300]
  Width = 0.23
FEATURE [PartDesign::SubtractiveBox] Box2937
  AttacherType = Attacher::AttachEngine3D
  AttachmentOffset = pos=(-21.35,18.635,0.35) rot=(0,0,1;0rad)
  BaseFeature = -> Box2923
  Height = 1.55
  Length = 0.5
  MapMode = 5
  Placement = pos=(-21.35,18.635,0.35) rot=(0,0,1;0rad)
  Support = -> [XY_Plane297]
  Width = 0.23
FEATURE [PartDesign::SubtractiveBox] Box2921
  AttacherType = Attacher::AttachEngine3D
  AttachmentOffset = pos=(-20.5,18.63,0) rot=(0,0,1;0rad)
  BaseFeature = -> Box2937
  Height = 1.635
  Length = 0.5
  MapMode = 5
  Placement = pos=(-20.5,18.63,0) rot=(0,0,1;0rad)
  Support = -> [XY_Plane297]
  Width = 0.25
FEATURE [PartDesign::SubtractiveBox] Box2913
  AttacherType = Attacher::AttachEngine3D
  AttachmentOffset = pos=(-21.19,18.635,-0.12) rot=(0,-1,0;0.15708rad)
  BaseFeature = -> Box2921
  Height = 0.12
  Length = 0.725
  MapMode = 5
  Placement = pos=(-21.19,18.635,-0.12) rot=(0,-1,0;0.15708rad)
  Support = -> [XY_Plane297]
  Width = 0.25
FEATURE [PartDesign::SubtractiveBox] Box2904
  AttacherType = Attacher::AttachEngine3D
  AttachmentOffset = pos=(-21.5005,18.625,0.235) rot=(0,-1,0;0.174533rad)
  BaseFeature = -> Box2913
  Height = 0.3
  Length = 0.6605
  MapMode = 5
  Placement = pos=(-21.5005,18.625,0.235) rot=(0,-1,0;0.174533rad)
  Support = -> [XY_Plane297]
  Width = 0.25
FEATURE [PartDesign::Fillet] Fillet869
  Base = -> Box2904 [Edge2]
  BaseFeature = -> Box2904
  Placement = pos=(-21.5005,18.625,0.235) rot=(0,-1,0;0.174533rad)
  Radius = 0.05
  SupportTransform = false
FEATURE [PartDesign::Fillet] Fillet877
  Base = -> Fillet869 [Edge33]
  BaseFeature = -> Fillet869
  Placement = pos=(-21.5005,18.625,0.235) rot=(0,-1,0;0.174533rad)
  Radius = 0.5
  SupportTransform = false
FEATURE [PartDesign::AdditiveBox] Box2901
  AttacherType = Attacher::AttachEngine3D
  AttachmentOffset = pos=(-21.1,18.635,0.305) rot=(0,1,0;0.785398rad)
  BaseFeature = -> Fillet877
  Height = 0.375
  Length = 0.2
  MapMode = 5
  Placement = pos=(-21.1,18.635,0.305) rot=(0,1,0;0.785398rad)
  Support = -> [XY_Plane297]
  Width = 0.23
FEATURE [PartDesign::SubtractiveCylinder] Cylinder587
  Angle = 360
  AttacherType = Attacher::AttachEngine3D
  AttachmentOffset = pos=(-21.055,18.935,0.52) rot=(1,0,0;1.5708rad)
  BaseFeature = -> Box2901
  Height = 0.375
  MapMode = 5
  Placement = pos=(-21.055,18.935,0.52) rot=(1,0,0;1.5708rad)
  Radius = 0.205
  Support = -> [XY_Plane297]
FEATURE [PartDesign::SubtractiveBox] Box2902
  AttacherType = Attacher::AttachEngine3D
  AttachmentOffset = pos=(-20.95,18.635,0.53) rot=(0,0,1;0rad)
  BaseFeature = -> Cylinder587
  Height = 0.5
  Length = 0.1
  MapMode = 5
  Placement = pos=(-20.95,18.635,0.53) rot=(0,0,1;0rad)
  Support = -> [XY_Plane297]
  Width = 0.23
FEATURE [PartDesign::SubtractiveBox] Box2890
  AttacherType = Attacher::AttachEngine3D
  AttachmentOffset = pos=(-21.15,18.635,0.297) rot=(0,-1,0;0.174533rad)
  BaseFeature = -> Box2902
  Height = 0.115
  Length = 0.115
  MapMode = 5
  Placement = pos=(-21.15,18.635,0.297) rot=(0,-1,0;0.174533rad)
  Support = -> [XY_Plane297]
  Width = 0.23
FEATURE [PartDesign::Fillet] Fillet871
  Base = -> Box2890 [Edge28]
  BaseFeature = -> Box2890
  Placement = pos=(-21.15,18.635,0.297) rot=(0,-1,0;0.174533rad)
  Radius = 0.375
  SupportTransform = false
FEATURE [PartDesign::AdditiveBox] Box2920
  AttacherType = Attacher::AttachEngine3D
  AttachmentOffset = pos=(-20.7,18.635,1.55) rot=(0,1,0;0.785398rad)
  BaseFeature = -> Fillet871
  Height = 0.375
  Length = 0.23
  MapMode = 5
  Placement = pos=(-20.7,18.635,1.55) rot=(0,1,0;0.785398rad)
  Support = -> [XY_Plane297]
  Width = 0.23
FEATURE [PartDesign::SubtractiveCylinder] Cylinder582
  Angle = 360
  AttacherType = Attacher::AttachEngine3D
  AttachmentOffset = pos=(-20.271,18.635,1.4056) rot=(-1,0,0;1.5708rad)
  BaseFeature = -> Box2920
  Height = 0.23
  MapMode = 5
  Placement = pos=(-20.271,18.635,1.4056) rot=(-1,0,0;1.5708rad)
  Radius = 0.23
  Support = -> [XY_Plane297]
FEATURE [PartDesign::AdditiveBox] Box2930
  AttacherType = Attacher::AttachEngine3D
  AttachmentOffset = pos=(-20.1,18.635,1.635) rot=(0,0,1;0rad)
  BaseFeature = -> Cylinder582
  Height = 0.265
  Length = 0.23
  MapMode = 5
  Placement = pos=(-20.1,18.635,1.635) rot=(0,0,1;0rad)
  Support = -> [XY_Plane297]
  Width = 0.23
FEATURE [PartDesign::Body] Body291  label="pin291"
  Group = -> [Box2923,Box2937,Box2921,Box2913,Box2904,Fillet869,Fillet877,Box2901,Cylinder587,Box2902,Box2890,Fillet871,Box2920,Cylinder582,Box2930]
  Origin = -> Origin328
  Placement = pos=(0,-5,0) rot=(0,0,1;0rad)
  Tip = -> Box2930
FEATURE [PartDesign::AdditiveBox] Box2942
  AttacherType = Attacher::AttachEngine3D
  AttachmentOffset = pos=(-21.3,18.635,0) rot=(0,0,1;0rad)
  Height = 1.9
  Length = 1.3
  MapMode = 5
  Placement = pos=(-21.3,18.635,0) rot=(0,0,1;0rad)
  Support = -> [XY_Plane323]
  Width = 0.23
FEATURE [PartDesign::SubtractiveBox] Box2896
  AttacherType = Attacher::AttachEngine3D
  AttachmentOffset = pos=(-21.35,18.635,0.35) rot=(0,0,1;0rad)
  BaseFeature = -> Box2942
  Height = 1.55
  Length = 0.5
  MapMode = 5
  Placement = pos=(-21.35,18.635,0.35) rot=(0,0,1;0rad)
  Support = -> [XY_Plane323]
  Width = 0.23
FEATURE [PartDesign::SubtractiveBox] Box2947
  AttacherType = Attacher::AttachEngine3D
  AttachmentOffset = pos=(-21.35,18.635,0.35) rot=(0,0,1;0rad)
  BaseFeature = -> Box2927
  Height = 1.55
  Length = 0.5
  MapMode = 5
  Placement = pos=(-21.35,18.635,0.35) rot=(0,0,1;0rad)
  Support = -> [XY_Plane298]
  Width = 0.23
FEATURE [PartDesign::SubtractiveBox] Box2929
  AttacherType = Attacher::AttachEngine3D
  AttachmentOffset = pos=(-20.5,18.63,0) rot=(0,0,1;0rad)
  BaseFeature = -> Box2947
  Height = 1.635
  Length = 0.5
  MapMode = 5
  Placement = pos=(-20.5,18.63,0) rot=(0,0,1;0rad)
  Support = -> [XY_Plane298]
  Width = 0.25
FEATURE [PartDesign::SubtractiveBox] Box2948
  AttacherType = Attacher::AttachEngine3D
  AttachmentOffset = pos=(-21.19,18.635,-0.12) rot=(0,-1,0;0.15708rad)
  BaseFeature = -> Box2929
  Height = 0.12
  Length = 0.725
  MapMode = 5
  Placement = pos=(-21.19,18.635,-0.12) rot=(0,-1,0;0.15708rad)
  Support = -> [XY_Plane298]
  Width = 0.25
FEATURE [PartDesign::SubtractiveBox] Box2950
  AttacherType = Attacher::AttachEngine3D
  AttachmentOffset = pos=(-21.5005,18.625,0.235) rot=(0,-1,0;0.174533rad)
  BaseFeature = -> Box2948
  Height = 0.3
  Length = 0.6605
  MapMode = 5
  Placement = pos=(-21.5005,18.625,0.235) rot=(0,-1,0;0.174533rad)
  Support = -> [XY_Plane298]
  Width = 0.25
FEATURE [PartDesign::SubtractiveBox] Box2952
  AttacherType = Attacher::AttachEngine3D
  AttachmentOffset = pos=(-21.5005,18.625,0.235) rot=(0,-1,0;0.174533rad)
  BaseFeature = -> Box2922
  Height = 0.3
  Length = 0.6605
  MapMode = 5
  Placement = pos=(-21.5005,18.625,0.235) rot=(0,-1,0;0.174533rad)
  Support = -> [XY_Plane294]
  Width = 0.25
FEATURE [PartDesign::SubtractiveBox] Box2955
  AttacherType = Attacher::AttachEngine3D
  AttachmentOffset = pos=(-21.35,18.635,0.35) rot=(0,0,1;0rad)
  BaseFeature = -> Box2932
  Height = 1.55
  Length = 0.5
  MapMode = 5
  Placement = pos=(-21.35,18.635,0.35) rot=(0,0,1;0rad)
  Support = -> [XY_Plane299]
  Width = 0.23
FEATURE [PartDesign::SubtractiveBox] Box2916
  AttacherType = Attacher::AttachEngine3D
  AttachmentOffset = pos=(-20.5,18.63,0) rot=(0,0,1;0rad)
  BaseFeature = -> Box2955
  Height = 1.635
  Length = 0.5
  MapMode = 5
  Placement = pos=(-20.5,18.63,0) rot=(0,0,1;0rad)
  Support = -> [XY_Plane299]
  Width = 0.25
FEATURE [PartDesign::SubtractiveBox] Box2963
  AttacherType = Attacher::AttachEngine3D
  AttachmentOffset = pos=(-21.35,18.635,0.35) rot=(0,0,1;0rad)
  BaseFeature = -> Box2936
  Height = 1.55
  Length = 0.5
  MapMode = 5
  Placement = pos=(-21.35,18.635,0.35) rot=(0,0,1;0rad)
  Support = -> [XY_Plane300]
  Width = 0.23
FEATURE [PartDesign::AdditiveBox] Box2970
  AttacherType = Attacher::AttachEngine3D
  AttachmentOffset = pos=(-21.3,18.635,0) rot=(0,0,1;0rad)
  Height = 1.9
  Length = 1.3
  MapMode = 5
  Placement = pos=(-21.3,18.635,0) rot=(0,0,1;0rad)
  Support = -> [XY_Plane332]
  Width = 0.23
FEATURE [PartDesign::AdditiveBox] Box2973
  AttacherType = Attacher::AttachEngine3D
  AttachmentOffset = pos=(-21.3,18.635,0) rot=(0,0,1;0rad)
  Height = 1.9
  Length = 1.3
  MapMode = 5
  Placement = pos=(-21.3,18.635,0) rot=(0,0,1;0rad)
  Support = -> [XY_Plane331]
  Width = 0.23
FEATURE [PartDesign::AdditiveBox] Box2979
  AttacherType = Attacher::AttachEngine3D
  AttachmentOffset = pos=(-21.3,18.635,0) rot=(0,0,1;0rad)
  Height = 1.9
  Length = 1.3
  MapMode = 5
  Placement = pos=(-21.3,18.635,0) rot=(0,0,1;0rad)
  Support = -> [XY_Plane330]
  Width = 0.23
FEATURE [PartDesign::SubtractiveBox] Box2980
  AttacherType = Attacher::AttachEngine3D
  AttachmentOffset = pos=(-21.35,18.635,0.35) rot=(0,0,1;0rad)
  BaseFeature = -> Box2979
  Height = 1.55
  Length = 0.5
  MapMode = 5
  Placement = pos=(-21.35,18.635,0.35) rot=(0,0,1;0rad)
  Support = -> [XY_Plane330]
  Width = 0.23
FEATURE [PartDesign::SubtractiveBox] Box2969
  AttacherType = Attacher::AttachEngine3D
  AttachmentOffset = pos=(-20.5,18.63,0) rot=(0,0,1;0rad)
  BaseFeature = -> Box2980
  Height = 1.635
  Length = 0.5
  MapMode = 5
  Placement = pos=(-20.5,18.63,0) rot=(0,0,1;0rad)
  Support = -> [XY_Plane330]
  Width = 0.25
FEATURE [PartDesign::SubtractiveBox] Box2976
  AttacherType = Attacher::AttachEngine3D
  AttachmentOffset = pos=(-21.19,18.635,-0.12) rot=(0,-1,0;0.15708rad)
  BaseFeature = -> Box2969
  Height = 0.12
  Length = 0.725
  MapMode = 5
  Placement = pos=(-21.19,18.635,-0.12) rot=(0,-1,0;0.15708rad)
  Support = -> [XY_Plane330]
  Width = 0.25
FEATURE [PartDesign::SubtractiveBox] Box2972
  AttacherType = Attacher::AttachEngine3D
  AttachmentOffset = pos=(-21.5005,18.625,0.235) rot=(0,-1,0;0.174533rad)
  BaseFeature = -> Box2976
  Height = 0.3
  Length = 0.6605
  MapMode = 5
  Placement = pos=(-21.5005,18.625,0.235) rot=(0,-1,0;0.174533rad)
  Support = -> [XY_Plane330]
  Width = 0.25
FEATURE [PartDesign::AdditiveBox] Box2985
  AttacherType = Attacher::AttachEngine3D
  AttachmentOffset = pos=(-21.3,18.635,0) rot=(0,0,1;0rad)
  Height = 1.9
  Length = 1.3
  MapMode = 5
  Placement = pos=(-21.3,18.635,0) rot=(0,0,1;0rad)
  Support = -> [XY_Plane329]
  Width = 0.23
FEATURE [PartDesign::SubtractiveBox] Box2990
  AttacherType = Attacher::AttachEngine3D
  AttachmentOffset = pos=(-21.35,18.635,0.35) rot=(0,0,1;0rad)
  BaseFeature = -> Box2970
  Height = 1.55
  Length = 0.5
  MapMode = 5
  Placement = pos=(-21.35,18.635,0.35) rot=(0,0,1;0rad)
  Support = -> [XY_Plane332]
  Width = 0.23
FEATURE [PartDesign::SubtractiveBox] Box2968
  AttacherType = Attacher::AttachEngine3D
  AttachmentOffset = pos=(-20.5,18.63,0) rot=(0,0,1;0rad)
  BaseFeature = -> Box2990
  Height = 1.635
  Length = 0.5
  MapMode = 5
  Placement = pos=(-20.5,18.63,0) rot=(0,0,1;0rad)
  Support = -> [XY_Plane332]
  Width = 0.25
FEATURE [PartDesign::SubtractiveBox] Box2978
  AttacherType = Attacher::AttachEngine3D
  AttachmentOffset = pos=(-21.19,18.635,-0.12) rot=(0,-1,0;0.15708rad)
  BaseFeature = -> Box2968
  Height = 0.12
  Length = 0.725
  MapMode = 5
  Placement = pos=(-21.19,18.635,-0.12) rot=(0,-1,0;0.15708rad)
  Support = -> [XY_Plane332]
  Width = 0.25
FEATURE [PartDesign::SubtractiveBox] Box2984
  AttacherType = Attacher::AttachEngine3D
  AttachmentOffset = pos=(-21.5005,18.625,0.235) rot=(0,-1,0;0.174533rad)
  BaseFeature = -> Box2978
  Height = 0.3
  Length = 0.6605
  MapMode = 5
  Placement = pos=(-21.5005,18.625,0.235) rot=(0,-1,0;0.174533rad)
  Support = -> [XY_Plane332]
  Width = 0.25
FEATURE [PartDesign::SubtractiveBox] Box2992
  AttacherType = Attacher::AttachEngine3D
  AttachmentOffset = pos=(-21.35,18.635,0.35) rot=(0,0,1;0rad)
  BaseFeature = -> Box2973
  Height = 1.55
  Length = 0.5
  MapMode = 5
  Placement = pos=(-21.35,18.635,0.35) rot=(0,0,1;0rad)
  Support = -> [XY_Plane331]
  Width = 0.23
FEATURE [PartDesign::SubtractiveBox] Box2997
  AttacherType = Attacher::AttachEngine3D
  AttachmentOffset = pos=(-21.35,18.635,0.35) rot=(0,0,1;0rad)
  BaseFeature = -> Box2985
  Height = 1.55
  Length = 0.5
  MapMode = 5
  Placement = pos=(-21.35,18.635,0.35) rot=(0,0,1;0rad)
  Support = -> [XY_Plane329]
  Width = 0.23
FEATURE [PartDesign::SubtractiveBox] Box2995
  AttacherType = Attacher::AttachEngine3D
  AttachmentOffset = pos=(-20.5,18.63,0) rot=(0,0,1;0rad)
  BaseFeature = -> Box2997
  Height = 1.635
  Length = 0.5
  MapMode = 5
  Placement = pos=(-20.5,18.63,0) rot=(0,0,1;0rad)
  Support = -> [XY_Plane329]
  Width = 0.25
FEATURE [PartDesign::SubtractiveBox] Box2996
  AttacherType = Attacher::AttachEngine3D
  AttachmentOffset = pos=(-21.19,18.635,-0.12) rot=(0,-1,0;0.15708rad)
  BaseFeature = -> Box2995
  Height = 0.12
  Length = 0.725
  MapMode = 5
  Placement = pos=(-21.19,18.635,-0.12) rot=(0,-1,0;0.15708rad)
  Support = -> [XY_Plane329]
  Width = 0.25
FEATURE [PartDesign::SubtractiveBox] Box2988
  AttacherType = Attacher::AttachEngine3D
  AttachmentOffset = pos=(-21.5005,18.625,0.235) rot=(0,-1,0;0.174533rad)
  BaseFeature = -> Box2996
  Height = 0.3
  Length = 0.6605
  MapMode = 5
  Placement = pos=(-21.5005,18.625,0.235) rot=(0,-1,0;0.174533rad)
  Support = -> [XY_Plane329]
  Width = 0.25
FEATURE [PartDesign::SubtractiveBox] Box3002
  AttacherType = Attacher::AttachEngine3D
  AttachmentOffset = pos=(-20.5,18.63,0) rot=(0,0,1;0rad)
  BaseFeature = -> Box2963
  Height = 1.635
  Length = 0.5
  MapMode = 5
  Placement = pos=(-20.5,18.63,0) rot=(0,0,1;0rad)
  Support = -> [XY_Plane300]
  Width = 0.25
FEATURE [PartDesign::SubtractiveBox] Box2943
  AttacherType = Attacher::AttachEngine3D
  AttachmentOffset = pos=(-21.19,18.635,-0.12) rot=(0,-1,0;0.15708rad)
  BaseFeature = -> Box3002
  Height = 0.12
  Length = 0.725
  MapMode = 5
  Placement = pos=(-21.19,18.635,-0.12) rot=(0,-1,0;0.15708rad)
  Support = -> [XY_Plane300]
  Width = 0.25
FEATURE [PartDesign::SubtractiveBox] Box2925
  AttacherType = Attacher::AttachEngine3D
  AttachmentOffset = pos=(-21.5005,18.625,0.235) rot=(0,-1,0;0.174533rad)
  BaseFeature = -> Box2943
  Height = 0.3
  Length = 0.6605
  MapMode = 5
  Placement = pos=(-21.5005,18.625,0.235) rot=(0,-1,0;0.174533rad)
  Support = -> [XY_Plane300]
  Width = 0.25
FEATURE [PartDesign::AdditiveBox] Box3007
  AttacherType = Attacher::AttachEngine3D
  AttachmentOffset = pos=(-21.3,18.635,0) rot=(0,0,1;0rad)
  Height = 1.9
  Length = 1.3
  MapMode = 5
  Placement = pos=(-21.3,18.635,0) rot=(0,0,1;0rad)
  Support = -> [XY_Plane296]
  Width = 0.23
FEATURE [PartDesign::SubtractiveBox] Box3011
  AttacherType = Attacher::AttachEngine3D
  AttachmentOffset = pos=(-21.19,18.635,-0.12) rot=(0,-1,0;0.15708rad)
  BaseFeature = -> Box2916
  Height = 0.12
  Length = 0.725
  MapMode = 5
  Placement = pos=(-21.19,18.635,-0.12) rot=(0,-1,0;0.15708rad)
  Support = -> [XY_Plane299]
  Width = 0.25
FEATURE [PartDesign::SubtractiveBox] Box2914
  AttacherType = Attacher::AttachEngine3D
  AttachmentOffset = pos=(-21.5005,18.625,0.235) rot=(0,-1,0;0.174533rad)
  BaseFeature = -> Box3011
  Height = 0.3
  Length = 0.6605
  MapMode = 5
  Placement = pos=(-21.5005,18.625,0.235) rot=(0,-1,0;0.174533rad)
  Support = -> [XY_Plane299]
  Width = 0.25
FEATURE [PartDesign::Fillet] Fillet881
  Base = -> Box2914 [Edge2]
  BaseFeature = -> Box2914
  Placement = pos=(-21.5005,18.625,0.235) rot=(0,-1,0;0.174533rad)
  Radius = 0.05
  SupportTransform = false
FEATURE [PartDesign::SubtractiveBox] Box3019
  AttacherType = Attacher::AttachEngine3D
  AttachmentOffset = pos=(-20.5,18.63,0) rot=(0,0,1;0rad)
  BaseFeature = -> Box2873
  Height = 1.635
  Length = 0.5
  MapMode = 5
  Placement = pos=(-20.5,18.63,0) rot=(0,0,1;0rad)
  Support = -> [XY_Plane326]
  Width = 0.25
FEATURE [PartDesign::SubtractiveBox] Box2945
  AttacherType = Attacher::AttachEngine3D
  AttachmentOffset = pos=(-21.19,18.635,-0.12) rot=(0,-1,0;0.15708rad)
  BaseFeature = -> Box3019
  Height = 0.12
  Length = 0.725
  MapMode = 5
  Placement = pos=(-21.19,18.635,-0.12) rot=(0,-1,0;0.15708rad)
  Support = -> [XY_Plane326]
  Width = 0.25
FEATURE [PartDesign::SubtractiveBox] Box2891
  AttacherType = Attacher::AttachEngine3D
  AttachmentOffset = pos=(-21.5005,18.625,0.235) rot=(0,-1,0;0.174533rad)
  BaseFeature = -> Box2945
  Height = 0.3
  Length = 0.6605
  MapMode = 5
  Placement = pos=(-21.5005,18.625,0.235) rot=(0,-1,0;0.174533rad)
  Support = -> [XY_Plane326]
  Width = 0.25
FEATURE [PartDesign::Fillet] Fillet880
  Base = -> Box2891 [Edge2]
  BaseFeature = -> Box2891
  Placement = pos=(-21.5005,18.625,0.235) rot=(0,-1,0;0.174533rad)
  Radius = 0.05
  SupportTransform = false
FEATURE [PartDesign::Fillet] Fillet868
  Base = -> Fillet880 [Edge33]
  BaseFeature = -> Fillet880
  Placement = pos=(-21.5005,18.625,0.235) rot=(0,-1,0;0.174533rad)
  Radius = 0.5
  SupportTransform = false
FEATURE [PartDesign::AdditiveBox] Box3022
  AttacherType = Attacher::AttachEngine3D
  AttachmentOffset = pos=(-21.3,18.635,0) rot=(0,0,1;0rad)
  Height = 1.9
  Length = 1.3
  MapMode = 5
  Placement = pos=(-21.3,18.635,0) rot=(0,0,1;0rad)
  Support = -> [XY_Plane295]
  Width = 0.23
FEATURE [PartDesign::SubtractiveBox] Box2966
  AttacherType = Attacher::AttachEngine3D
  AttachmentOffset = pos=(-21.35,18.635,0.35) rot=(0,0,1;0rad)
  BaseFeature = -> Box3022
  Height = 1.55
  Length = 0.5
  MapMode = 5
  Placement = pos=(-21.35,18.635,0.35) rot=(0,0,1;0rad)
  Support = -> [XY_Plane295]
  Width = 0.23
FEATURE [PartDesign::SubtractiveBox] Box2959
  AttacherType = Attacher::AttachEngine3D
  AttachmentOffset = pos=(-20.5,18.63,0) rot=(0,0,1;0rad)
  BaseFeature = -> Box2966
  Height = 1.635
  Length = 0.5
  MapMode = 5
  Placement = pos=(-20.5,18.63,0) rot=(0,0,1;0rad)
  Support = -> [XY_Plane295]
  Width = 0.25
FEATURE [PartDesign::SubtractiveBox] Box3012
  AttacherType = Attacher::AttachEngine3D
  AttachmentOffset = pos=(-21.19,18.635,-0.12) rot=(0,-1,0;0.15708rad)
  BaseFeature = -> Box2959
  Height = 0.12
  Length = 0.725
  MapMode = 5
  Placement = pos=(-21.19,18.635,-0.12) rot=(0,-1,0;0.15708rad)
  Support = -> [XY_Plane295]
  Width = 0.25
FEATURE [PartDesign::SubtractiveBox] Box3000
  AttacherType = Attacher::AttachEngine3D
  AttachmentOffset = pos=(-21.5005,18.625,0.235) rot=(0,-1,0;0.174533rad)
  BaseFeature = -> Box3012
  Height = 0.3
  Length = 0.6605
  MapMode = 5
  Placement = pos=(-21.5005,18.625,0.235) rot=(0,-1,0;0.174533rad)
  Support = -> [XY_Plane295]
  Width = 0.25
FEATURE [PartDesign::Fillet] Fillet875
  Base = -> Box3000 [Edge2]
  BaseFeature = -> Box3000
  Placement = pos=(-21.5005,18.625,0.235) rot=(0,-1,0;0.174533rad)
  Radius = 0.05
  SupportTransform = false
FEATURE [PartDesign::Fillet] Fillet866
  Base = -> Fillet875 [Edge33]
  BaseFeature = -> Fillet875
  Placement = pos=(-21.5005,18.625,0.235) rot=(0,-1,0;0.174533rad)
  Radius = 0.5
  SupportTransform = false
FEATURE [PartDesign::AdditiveBox] Box2957
  AttacherType = Attacher::AttachEngine3D
  AttachmentOffset = pos=(-21.1,18.635,0.305) rot=(0,1,0;0.785398rad)
  BaseFeature = -> Fillet866
  Height = 0.375
  Length = 0.2
  MapMode = 5
  Placement = pos=(-21.1,18.635,0.305) rot=(0,1,0;0.785398rad)
  Support = -> [XY_Plane295]
  Width = 0.23
FEATURE [PartDesign::SubtractiveCylinder] Cylinder607
  Angle = 360
  AttacherType = Attacher::AttachEngine3D
  AttachmentOffset = pos=(-21.055,18.935,0.52) rot=(1,0,0;1.5708rad)
  BaseFeature = -> Box2957
  Height = 0.375
  MapMode = 5
  Placement = pos=(-21.055,18.935,0.52) rot=(1,0,0;1.5708rad)
  Radius = 0.205
  Support = -> [XY_Plane295]
FEATURE [PartDesign::SubtractiveBox] Box3003
  AttacherType = Attacher::AttachEngine3D
  AttachmentOffset = pos=(-20.95,18.635,0.53) rot=(0,0,1;0rad)
  BaseFeature = -> Cylinder607
  Height = 0.5
  Length = 0.1
  MapMode = 5
  Placement = pos=(-20.95,18.635,0.53) rot=(0,0,1;0rad)
  Support = -> [XY_Plane295]
  Width = 0.23
FEATURE [PartDesign::SubtractiveBox] Box2964
  AttacherType = Attacher::AttachEngine3D
  AttachmentOffset = pos=(-21.15,18.635,0.297) rot=(0,-1,0;0.174533rad)
  BaseFeature = -> Box3003
  Height = 0.115
  Length = 0.115
  MapMode = 5
  Placement = pos=(-21.15,18.635,0.297) rot=(0,-1,0;0.174533rad)
  Support = -> [XY_Plane295]
  Width = 0.23
FEATURE [PartDesign::Fillet] Fillet889
  Base = -> Box2964 [Edge28]
  BaseFeature = -> Box2964
  Placement = pos=(-21.15,18.635,0.297) rot=(0,-1,0;0.174533rad)
  Radius = 0.375
  SupportTransform = false
FEATURE [PartDesign::AdditiveBox] Box2962
  AttacherType = Attacher::AttachEngine3D
  AttachmentOffset = pos=(-20.7,18.635,1.55) rot=(0,1,0;0.785398rad)
  BaseFeature = -> Fillet889
  Height = 0.375
  Length = 0.23
  MapMode = 5
  Placement = pos=(-20.7,18.635,1.55) rot=(0,1,0;0.785398rad)
  Support = -> [XY_Plane295]
  Width = 0.23
FEATURE [PartDesign::SubtractiveCylinder] Cylinder605
  Angle = 360
  AttacherType = Attacher::AttachEngine3D
  AttachmentOffset = pos=(-20.271,18.635,1.4056) rot=(-1,0,0;1.5708rad)
  BaseFeature = -> Box2962
  Height = 0.23
  MapMode = 5
  Placement = pos=(-20.271,18.635,1.4056) rot=(-1,0,0;1.5708rad)
  Radius = 0.23
  Support = -> [XY_Plane295]
FEATURE [PartDesign::AdditiveBox] Box3015
  AttacherType = Attacher::AttachEngine3D
  AttachmentOffset = pos=(-20.1,18.635,1.635) rot=(0,0,1;0rad)
  BaseFeature = -> Cylinder605
  Height = 0.265
  Length = 0.23
  MapMode = 5
  Placement = pos=(-20.1,18.635,1.635) rot=(0,0,1;0rad)
  Support = -> [XY_Plane295]
  Width = 0.23
FEATURE [PartDesign::Body] Body289  label="pin289"
  Group = -> [Box3022,Box2966,Box2959,Box3012,Box3000,Fillet875,Fillet866,Box2957,Cylinder607,Box3003,Box2964,Fillet889,Box2962,Cylinder605,Box3015]
  Origin = -> Origin312
  Placement = pos=(0,-0.5,0) rot=(0,0,1;0rad)
  Tip = -> Box3015
FEATURE [PartDesign::SubtractiveBox] Box3026
  AttacherType = Attacher::AttachEngine3D
  AttachmentOffset = pos=(-21.35,18.635,0.35) rot=(0,0,1;0rad)
  BaseFeature = -> Box3007
  Height = 1.55
  Length = 0.5
  MapMode = 5
  Placement = pos=(-21.35,18.635,0.35) rot=(0,0,1;0rad)
  Support = -> [XY_Plane296]
  Width = 0.23
FEATURE [PartDesign::SubtractiveBox] Box2961
  AttacherType = Attacher::AttachEngine3D
  AttachmentOffset = pos=(-20.5,18.63,0) rot=(0,0,1;0rad)
  BaseFeature = -> Box3026
  Height = 1.635
  Length = 0.5
  MapMode = 5
  Placement = pos=(-20.5,18.63,0) rot=(0,0,1;0rad)
  Support = -> [XY_Plane296]
  Width = 0.25
FEATURE [PartDesign::SubtractiveBox] Box2999
  AttacherType = Attacher::AttachEngine3D
  AttachmentOffset = pos=(-21.19,18.635,-0.12) rot=(0,-1,0;0.15708rad)
  BaseFeature = -> Box2961
  Height = 0.12
  Length = 0.725
  MapMode = 5
  Placement = pos=(-21.19,18.635,-0.12) rot=(0,-1,0;0.15708rad)
  Support = -> [XY_Plane296]
  Width = 0.25
FEATURE [PartDesign::SubtractiveBox] Box3004
  AttacherType = Attacher::AttachEngine3D
  AttachmentOffset = pos=(-21.5005,18.625,0.235) rot=(0,-1,0;0.174533rad)
  BaseFeature = -> Box2999
  Height = 0.3
  Length = 0.6605
  MapMode = 5
  Placement = pos=(-21.5005,18.625,0.235) rot=(0,-1,0;0.174533rad)
  Support = -> [XY_Plane296]
  Width = 0.25
FEATURE [PartDesign::Fillet] Fillet864
  Base = -> Box3004 [Edge2]
  BaseFeature = -> Box3004
  Placement = pos=(-21.5005,18.625,0.235) rot=(0,-1,0;0.174533rad)
  Radius = 0.05
  SupportTransform = false
FEATURE [PartDesign::Fillet] Fillet858
  Base = -> Fillet864 [Edge33]
  BaseFeature = -> Fillet864
  Placement = pos=(-21.5005,18.625,0.235) rot=(0,-1,0;0.174533rad)
  Radius = 0.5
  SupportTransform = false
FEATURE [PartDesign::AdditiveBox] Box2940
  AttacherType = Attacher::AttachEngine3D
  AttachmentOffset = pos=(-21.1,18.635,0.305) rot=(0,1,0;0.785398rad)
  BaseFeature = -> Fillet858
  Height = 0.375
  Length = 0.2
  MapMode = 5
  Placement = pos=(-21.1,18.635,0.305) rot=(0,1,0;0.785398rad)
  Support = -> [XY_Plane296]
  Width = 0.23
FEATURE [PartDesign::SubtractiveCylinder] Cylinder591
  Angle = 360
  AttacherType = Attacher::AttachEngine3D
  AttachmentOffset = pos=(-21.055,18.935,0.52) rot=(1,0,0;1.5708rad)
  BaseFeature = -> Box2940
  Height = 0.375
  MapMode = 5
  Placement = pos=(-21.055,18.935,0.52) rot=(1,0,0;1.5708rad)
  Radius = 0.205
  Support = -> [XY_Plane296]
FEATURE [PartDesign::SubtractiveBox] Box2911
  AttacherType = Attacher::AttachEngine3D
  AttachmentOffset = pos=(-20.95,18.635,0.53) rot=(0,0,1;0rad)
  BaseFeature = -> Cylinder591
  Height = 0.5
  Length = 0.1
  MapMode = 5
  Placement = pos=(-20.95,18.635,0.53) rot=(0,0,1;0rad)
  Support = -> [XY_Plane296]
  Width = 0.23
FEATURE [PartDesign::SubtractiveBox] Box2912
  AttacherType = Attacher::AttachEngine3D
  AttachmentOffset = pos=(-21.15,18.635,0.297) rot=(0,-1,0;0.174533rad)
  BaseFeature = -> Box2911
  Height = 0.115
  Length = 0.115
  MapMode = 5
  Placement = pos=(-21.15,18.635,0.297) rot=(0,-1,0;0.174533rad)
  Support = -> [XY_Plane296]
  Width = 0.23
FEATURE [PartDesign::Fillet] Fillet887
  Base = -> Box2912 [Edge28]
  BaseFeature = -> Box2912
  Placement = pos=(-21.15,18.635,0.297) rot=(0,-1,0;0.174533rad)
  Radius = 0.375
  SupportTransform = false
FEATURE [PartDesign::AdditiveBox] Box2954
  AttacherType = Attacher::AttachEngine3D
  AttachmentOffset = pos=(-20.7,18.635,1.55) rot=(0,1,0;0.785398rad)
  BaseFeature = -> Fillet887
  Height = 0.375
  Length = 0.23
  MapMode = 5
  Placement = pos=(-20.7,18.635,1.55) rot=(0,1,0;0.785398rad)
  Support = -> [XY_Plane296]
  Width = 0.23
FEATURE [PartDesign::SubtractiveCylinder] Cylinder585
  Angle = 360
  AttacherType = Attacher::AttachEngine3D
  AttachmentOffset = pos=(-20.271,18.635,1.4056) rot=(-1,0,0;1.5708rad)
  BaseFeature = -> Box2954
  Height = 0.23
  MapMode = 5
  Placement = pos=(-20.271,18.635,1.4056) rot=(-1,0,0;1.5708rad)
  Radius = 0.23
  Support = -> [XY_Plane296]
FEATURE [PartDesign::AdditiveBox] Box3013
  AttacherType = Attacher::AttachEngine3D
  AttachmentOffset = pos=(-20.1,18.635,1.635) rot=(0,0,1;0rad)
  BaseFeature = -> Cylinder585
  Height = 0.265
  Length = 0.23
  MapMode = 5
  Placement = pos=(-20.1,18.635,1.635) rot=(0,0,1;0rad)
  Support = -> [XY_Plane296]
  Width = 0.23
FEATURE [PartDesign::Body] Body293  label="pin293"
  Group = -> [Box3007,Box3026,Box2961,Box2999,Box3004,Fillet864,Fillet858,Box2940,Cylinder591,Box2911,Box2912,Fillet887,Box2954,Cylinder585,Box3013]
  Origin = -> Origin331
  Tip = -> Box3013
FEATURE [PartDesign::SubtractiveBox] Box3028
  AttacherType = Attacher::AttachEngine3D
  AttachmentOffset = pos=(-20.5,18.63,0) rot=(0,0,1;0rad)
  BaseFeature = -> Box2896
  Height = 1.635
  Length = 0.5
  MapMode = 5
  Placement = pos=(-20.5,18.63,0) rot=(0,0,1;0rad)
  Support = -> [XY_Plane323]
  Width = 0.25
FEATURE [PartDesign::SubtractiveBox] Box2888
  AttacherType = Attacher::AttachEngine3D
  AttachmentOffset = pos=(-21.19,18.635,-0.12) rot=(0,-1,0;0.15708rad)
  BaseFeature = -> Box3028
  Height = 0.12
  Length = 0.725
  MapMode = 5
  Placement = pos=(-21.19,18.635,-0.12) rot=(0,-1,0;0.15708rad)
  Support = -> [XY_Plane323]
  Width = 0.25
FEATURE [PartDesign::SubtractiveBox] Box2895
  AttacherType = Attacher::AttachEngine3D
  AttachmentOffset = pos=(-21.5005,18.625,0.235) rot=(0,-1,0;0.174533rad)
  BaseFeature = -> Box2888
  Height = 0.3
  Length = 0.6605
  MapMode = 5
  Placement = pos=(-21.5005,18.625,0.235) rot=(0,-1,0;0.174533rad)
  Support = -> [XY_Plane323]
  Width = 0.25
FEATURE [PartDesign::Fillet] Fillet882
  Base = -> Box2895 [Edge2]
  BaseFeature = -> Box2895
  Placement = pos=(-21.5005,18.625,0.235) rot=(0,-1,0;0.174533rad)
  Radius = 0.05
  SupportTransform = false
FEATURE [PartDesign::Fillet] Fillet884
  Base = -> Fillet882 [Edge33]
  BaseFeature = -> Fillet882
  Placement = pos=(-21.5005,18.625,0.235) rot=(0,-1,0;0.174533rad)
  Radius = 0.5
  SupportTransform = false
FEATURE [PartDesign::AdditiveBox] Box3021
  AttacherType = Attacher::AttachEngine3D
  AttachmentOffset = pos=(-21.1,18.635,0.305) rot=(0,1,0;0.785398rad)
  BaseFeature = -> Fillet884
  Height = 0.375
  Length = 0.2
  MapMode = 5
  Placement = pos=(-21.1,18.635,0.305) rot=(0,1,0;0.785398rad)
  Support = -> [XY_Plane323]
  Width = 0.23
FEATURE [PartDesign::AdditiveBox] Box3030
  AttacherType = Attacher::AttachEngine3D
  AttachmentOffset = pos=(-21.1,18.635,0.305) rot=(0,1,0;0.785398rad)
  BaseFeature = -> Fillet868
  Height = 0.375
  Length = 0.2
  MapMode = 5
  Placement = pos=(-21.1,18.635,0.305) rot=(0,1,0;0.785398rad)
  Support = -> [XY_Plane326]
  Width = 0.23
FEATURE [PartDesign::SubtractiveCylinder] Cylinder592
  Angle = 360
  AttacherType = Attacher::AttachEngine3D
  AttachmentOffset = pos=(-21.055,18.935,0.52) rot=(1,0,0;1.5708rad)
  BaseFeature = -> Box3030
  Height = 0.375
  MapMode = 5
  Placement = pos=(-21.055,18.935,0.52) rot=(1,0,0;1.5708rad)
  Radius = 0.205
  Support = -> [XY_Plane326]
FEATURE [PartDesign::SubtractiveBox] Box2874
  AttacherType = Attacher::AttachEngine3D
  AttachmentOffset = pos=(-20.95,18.635,0.53) rot=(0,0,1;0rad)
  BaseFeature = -> Cylinder592
  Height = 0.5
  Length = 0.1
  MapMode = 5
  Placement = pos=(-20.95,18.635,0.53) rot=(0,0,1;0rad)
  Support = -> [XY_Plane326]
  Width = 0.23
FEATURE [PartDesign::SubtractiveBox] Box2889
  AttacherType = Attacher::AttachEngine3D
  AttachmentOffset = pos=(-21.15,18.635,0.297) rot=(0,-1,0;0.174533rad)
  BaseFeature = -> Box2874
  Height = 0.115
  Length = 0.115
  MapMode = 5
  Placement = pos=(-21.15,18.635,0.297) rot=(0,-1,0;0.174533rad)
  Support = -> [XY_Plane326]
  Width = 0.23
FEATURE [PartDesign::Fillet] Fillet876
  Base = -> Box2889 [Edge28]
  BaseFeature = -> Box2889
  Placement = pos=(-21.15,18.635,0.297) rot=(0,-1,0;0.174533rad)
  Radius = 0.375
  SupportTransform = false
FEATURE [PartDesign::AdditiveBox] Box2894
  AttacherType = Attacher::AttachEngine3D
  AttachmentOffset = pos=(-20.7,18.635,1.55) rot=(0,1,0;0.785398rad)
  BaseFeature = -> Fillet876
  Height = 0.375
  Length = 0.23
  MapMode = 5
  Placement = pos=(-20.7,18.635,1.55) rot=(0,1,0;0.785398rad)
  Support = -> [XY_Plane326]
  Width = 0.23
FEATURE [PartDesign::SubtractiveCylinder] Cylinder597
  Angle = 360
  AttacherType = Attacher::AttachEngine3D
  AttachmentOffset = pos=(-20.271,18.635,1.4056) rot=(-1,0,0;1.5708rad)
  BaseFeature = -> Box2894
  Height = 0.23
  MapMode = 5
  Placement = pos=(-20.271,18.635,1.4056) rot=(-1,0,0;1.5708rad)
  Radius = 0.23
  Support = -> [XY_Plane326]
FEATURE [PartDesign::AdditiveBox] Box2887
  AttacherType = Attacher::AttachEngine3D
  AttachmentOffset = pos=(-20.1,18.635,1.635) rot=(0,0,1;0rad)
  BaseFeature = -> Cylinder597
  Height = 0.265
  Length = 0.23
  MapMode = 5
  Placement = pos=(-20.1,18.635,1.635) rot=(0,0,1;0rad)
  Support = -> [XY_Plane326]
  Width = 0.23
FEATURE [PartDesign::AdditiveBox] Box3031
  AttacherType = Attacher::AttachEngine3D
  AttachmentOffset = pos=(-21.3,18.635,0) rot=(0,0,1;0rad)
  Height = 1.9
  Length = 1.3
  MapMode = 5
  Placement = pos=(-21.3,18.635,0) rot=(0,0,1;0rad)
  Support = -> [XY_Plane327]
  Width = 0.23
FEATURE [PartDesign::SubtractiveBox] Box3024
  AttacherType = Attacher::AttachEngine3D
  AttachmentOffset = pos=(-21.35,18.635,0.35) rot=(0,0,1;0rad)
  BaseFeature = -> Box3031
  Height = 1.55
  Length = 0.5
  MapMode = 5
  Placement = pos=(-21.35,18.635,0.35) rot=(0,0,1;0rad)
  Support = -> [XY_Plane327]
  Width = 0.23
FEATURE [PartDesign::SubtractiveBox] Box3010
  AttacherType = Attacher::AttachEngine3D
  AttachmentOffset = pos=(-20.5,18.63,0) rot=(0,0,1;0rad)
  BaseFeature = -> Box3024
  Height = 1.635
  Length = 0.5
  MapMode = 5
  Placement = pos=(-20.5,18.63,0) rot=(0,0,1;0rad)
  Support = -> [XY_Plane327]
  Width = 0.25
FEATURE [PartDesign::SubtractiveBox] Box3014
  AttacherType = Attacher::AttachEngine3D
  AttachmentOffset = pos=(-21.19,18.635,-0.12) rot=(0,-1,0;0.15708rad)
  BaseFeature = -> Box3010
  Height = 0.12
  Length = 0.725
  MapMode = 5
  Placement = pos=(-21.19,18.635,-0.12) rot=(0,-1,0;0.15708rad)
  Support = -> [XY_Plane327]
  Width = 0.25
FEATURE [PartDesign::SubtractiveBox] Box3009
  AttacherType = Attacher::AttachEngine3D
  AttachmentOffset = pos=(-21.5005,18.625,0.235) rot=(0,-1,0;0.174533rad)
  BaseFeature = -> Box3014
  Height = 0.3
  Length = 0.6605
  MapMode = 5
  Placement = pos=(-21.5005,18.625,0.235) rot=(0,-1,0;0.174533rad)
  Support = -> [XY_Plane327]
  Width = 0.25
FEATURE [PartDesign::SubtractiveBox] Box3032
  AttacherType = Attacher::AttachEngine3D
  AttachmentOffset = pos=(-20.5,18.63,0) rot=(0,0,1;0rad)
  BaseFeature = -> Box2875
  Height = 1.635
  Length = 0.5
  MapMode = 5
  Placement = pos=(-20.5,18.63,0) rot=(0,0,1;0rad)
  Support = -> [XY_Plane325]
  Width = 0.25
FEATURE [PartDesign::SubtractiveBox] Box3006
  AttacherType = Attacher::AttachEngine3D
  AttachmentOffset = pos=(-21.19,18.635,-0.12) rot=(0,-1,0;0.15708rad)
  BaseFeature = -> Box3032
  Height = 0.12
  Length = 0.725
  MapMode = 5
  Placement = pos=(-21.19,18.635,-0.12) rot=(0,-1,0;0.15708rad)
  Support = -> [XY_Plane325]
  Width = 0.25
FEATURE [PartDesign::SubtractiveBox] Box2900
  AttacherType = Attacher::AttachEngine3D
  AttachmentOffset = pos=(-21.5005,18.625,0.235) rot=(0,-1,0;0.174533rad)
  BaseFeature = -> Box3006
  Height = 0.3
  Length = 0.6605
  MapMode = 5
  Placement = pos=(-21.5005,18.625,0.235) rot=(0,-1,0;0.174533rad)
  Support = -> [XY_Plane325]
  Width = 0.25
FEATURE [PartDesign::Fillet] Fillet873
  Base = -> Box2900 [Edge2]
  BaseFeature = -> Box2900
  Placement = pos=(-21.5005,18.625,0.235) rot=(0,-1,0;0.174533rad)
  Radius = 0.05
  SupportTransform = false
FEATURE [PartDesign::SubtractiveCylinder] Cylinder609
  Angle = 360
  AttacherType = Attacher::AttachEngine3D
  AttachmentOffset = pos=(-21.055,18.935,0.52) rot=(1,0,0;1.5708rad)
  BaseFeature = -> Box3021
  Height = 0.375
  MapMode = 5
  Placement = pos=(-21.055,18.935,0.52) rot=(1,0,0;1.5708rad)
  Radius = 0.205
  Support = -> [XY_Plane323]
FEATURE [PartDesign::SubtractiveBox] Box2898
  AttacherType = Attacher::AttachEngine3D
  AttachmentOffset = pos=(-20.95,18.635,0.53) rot=(0,0,1;0rad)
  BaseFeature = -> Cylinder609
  Height = 0.5
  Length = 0.1
  MapMode = 5
  Placement = pos=(-20.95,18.635,0.53) rot=(0,0,1;0rad)
  Support = -> [XY_Plane323]
  Width = 0.23
FEATURE [PartDesign::SubtractiveBox] Box2949
  AttacherType = Attacher::AttachEngine3D
  AttachmentOffset = pos=(-21.15,18.635,0.297) rot=(0,-1,0;0.174533rad)
  BaseFeature = -> Box2898
  Height = 0.115
  Length = 0.115
  MapMode = 5
  Placement = pos=(-21.15,18.635,0.297) rot=(0,-1,0;0.174533rad)
  Support = -> [XY_Plane323]
  Width = 0.23
FEATURE [PartDesign::Fillet] Fillet878
  Base = -> Box2949 [Edge28]
  BaseFeature = -> Box2949
  Placement = pos=(-21.15,18.635,0.297) rot=(0,-1,0;0.174533rad)
  Radius = 0.375
  SupportTransform = false
FEATURE [PartDesign::AdditiveBox] Box3017
  AttacherType = Attacher::AttachEngine3D
  AttachmentOffset = pos=(-20.7,18.635,1.55) rot=(0,1,0;0.785398rad)
  BaseFeature = -> Fillet878
  Height = 0.375
  Length = 0.23
  MapMode = 5
  Placement = pos=(-20.7,18.635,1.55) rot=(0,1,0;0.785398rad)
  Support = -> [XY_Plane323]
  Width = 0.23
FEATURE [PartDesign::SubtractiveCylinder] Cylinder581
  Angle = 360
  AttacherType = Attacher::AttachEngine3D
  AttachmentOffset = pos=(-20.271,18.635,1.4056) rot=(-1,0,0;1.5708rad)
  BaseFeature = -> Box3017
  Height = 0.23
  MapMode = 5
  Placement = pos=(-20.271,18.635,1.4056) rot=(-1,0,0;1.5708rad)
  Radius = 0.23
  Support = -> [XY_Plane323]
FEATURE [PartDesign::AdditiveBox] Box2906
  AttacherType = Attacher::AttachEngine3D
  AttachmentOffset = pos=(-20.1,18.635,1.635) rot=(0,0,1;0rad)
  BaseFeature = -> Cylinder581
  Height = 0.265
  Length = 0.23
  MapMode = 5
  Placement = pos=(-20.1,18.635,1.635) rot=(0,0,1;0rad)
  Support = -> [XY_Plane323]
  Width = 0.23
FEATURE [PartDesign::Body] Body294  label="pin294"
  Group = -> [Box2942,Box2896,Box3028,Box2888,Box2895,Fillet882,Fillet884,Box3021,Cylinder609,Box2898,Box2949,Fillet878,Box3017,Cylinder581,Box2906]
  Origin = -> Origin320
  Placement = pos=(0,-2,0) rot=(0,0,1;0rad)
  Tip = -> Box2906
FEATURE [PartDesign::SubtractiveBox] Box3035
  AttacherType = Attacher::AttachEngine3D
  AttachmentOffset = pos=(-20.5,18.63,0) rot=(0,0,1;0rad)
  BaseFeature = -> Box2992
  Height = 1.635
  Length = 0.5
  MapMode = 5
  Placement = pos=(-20.5,18.63,0) rot=(0,0,1;0rad)
  Support = -> [XY_Plane331]
  Width = 0.25
FEATURE [PartDesign::SubtractiveBox] Box3039
  AttacherType = Attacher::AttachEngine3D
  AttachmentOffset = pos=(-21.19,18.635,-0.12) rot=(0,-1,0;0.15708rad)
  BaseFeature = -> Box3035
  Height = 0.12
  Length = 0.725
  MapMode = 5
  Placement = pos=(-21.19,18.635,-0.12) rot=(0,-1,0;0.15708rad)
  Support = -> [XY_Plane331]
  Width = 0.25
FEATURE [PartDesign::SubtractiveBox] Box3037
  AttacherType = Attacher::AttachEngine3D
  AttachmentOffset = pos=(-21.5005,18.625,0.235) rot=(0,-1,0;0.174533rad)
  BaseFeature = -> Box3039
  Height = 0.3
  Length = 0.6605
  MapMode = 5
  Placement = pos=(-21.5005,18.625,0.235) rot=(0,-1,0;0.174533rad)
  Support = -> [XY_Plane331]
  Width = 0.25
FEATURE [PartDesign::Fillet] Fillet890
  Base = -> Box2952 [Edge2]
  BaseFeature = -> Box2952
  Placement = pos=(-21.5005,18.625,0.235) rot=(0,-1,0;0.174533rad)
  Radius = 0.05
  SupportTransform = false
FEATURE [PartDesign::Fillet] Fillet867
  Base = -> Fillet890 [Edge33]
  BaseFeature = -> Fillet890
  Placement = pos=(-21.5005,18.625,0.235) rot=(0,-1,0;0.174533rad)
  Radius = 0.5
  SupportTransform = false
FEATURE [PartDesign::AdditiveBox] Box2886
  AttacherType = Attacher::AttachEngine3D
  AttachmentOffset = pos=(-21.1,18.635,0.305) rot=(0,1,0;0.785398rad)
  BaseFeature = -> Fillet867
  Height = 0.375
  Length = 0.2
  MapMode = 5
  Placement = pos=(-21.1,18.635,0.305) rot=(0,1,0;0.785398rad)
  Support = -> [XY_Plane294]
  Width = 0.23
FEATURE [PartDesign::SubtractiveCylinder] Cylinder580
  Angle = 360
  AttacherType = Attacher::AttachEngine3D
  AttachmentOffset = pos=(-21.055,18.935,0.52) rot=(1,0,0;1.5708rad)
  BaseFeature = -> Box2886
  Height = 0.375
  MapMode = 5
  Placement = pos=(-21.055,18.935,0.52) rot=(1,0,0;1.5708rad)
  Radius = 0.205
  Support = -> [XY_Plane294]
FEATURE [PartDesign::SubtractiveBox] Box2893
  AttacherType = Attacher::AttachEngine3D
  AttachmentOffset = pos=(-20.95,18.635,0.53) rot=(0,0,1;0rad)
  BaseFeature = -> Cylinder580
  Height = 0.5
  Length = 0.1
  MapMode = 5
  Placement = pos=(-20.95,18.635,0.53) rot=(0,0,1;0rad)
  Support = -> [XY_Plane294]
  Width = 0.23
FEATURE [PartDesign::SubtractiveBox] Box2872
  AttacherType = Attacher::AttachEngine3D
  AttachmentOffset = pos=(-21.15,18.635,0.297) rot=(0,-1,0;0.174533rad)
  BaseFeature = -> Box2893
  Height = 0.115
  Length = 0.115
  MapMode = 5
  Placement = pos=(-21.15,18.635,0.297) rot=(0,-1,0;0.174533rad)
  Support = -> [XY_Plane294]
  Width = 0.23
FEATURE [PartDesign::Fillet] Fillet874
  Base = -> Box2872 [Edge28]
  BaseFeature = -> Box2872
  Placement = pos=(-21.15,18.635,0.297) rot=(0,-1,0;0.174533rad)
  Radius = 0.375
  SupportTransform = false
FEATURE [PartDesign::AdditiveBox] Box2907
  AttacherType = Attacher::AttachEngine3D
  AttachmentOffset = pos=(-20.7,18.635,1.55) rot=(0,1,0;0.785398rad)
  BaseFeature = -> Fillet874
  Height = 0.375
  Length = 0.23
  MapMode = 5
  Placement = pos=(-20.7,18.635,1.55) rot=(0,1,0;0.785398rad)
  Support = -> [XY_Plane294]
  Width = 0.23
FEATURE [PartDesign::SubtractiveCylinder] Cylinder583
  Angle = 360
  AttacherType = Attacher::AttachEngine3D
  AttachmentOffset = pos=(-20.271,18.635,1.4056) rot=(-1,0,0;1.5708rad)
  BaseFeature = -> Box2907
  Height = 0.23
  MapMode = 5
  Placement = pos=(-20.271,18.635,1.4056) rot=(-1,0,0;1.5708rad)
  Radius = 0.23
  Support = -> [XY_Plane294]
FEATURE [PartDesign::AdditiveBox] Box2908
  AttacherType = Attacher::AttachEngine3D
  AttachmentOffset = pos=(-20.1,18.635,1.635) rot=(0,0,1;0rad)
  BaseFeature = -> Cylinder583
  Height = 0.265
  Length = 0.23
  MapMode = 5
  Placement = pos=(-20.1,18.635,1.635) rot=(0,0,1;0rad)
  Support = -> [XY_Plane294]
  Width = 0.23
FEATURE [PartDesign::Fillet] Fillet892
  Base = -> Box3009 [Edge2]
  BaseFeature = -> Box3009
  Placement = pos=(-21.5005,18.625,0.235) rot=(0,-1,0;0.174533rad)
  Radius = 0.05
  SupportTransform = false
FEATURE [PartDesign::Fillet] Fillet888
  Base = -> Fillet892 [Edge33]
  BaseFeature = -> Fillet892
  Placement = pos=(-21.5005,18.625,0.235) rot=(0,-1,0;0.174533rad)
  Radius = 0.5
  SupportTransform = false
FEATURE [PartDesign::AdditiveBox] Box2960
  AttacherType = Attacher::AttachEngine3D
  AttachmentOffset = pos=(-21.1,18.635,0.305) rot=(0,1,0;0.785398rad)
  BaseFeature = -> Fillet888
  Height = 0.375
  Length = 0.2
  MapMode = 5
  Placement = pos=(-21.1,18.635,0.305) rot=(0,1,0;0.785398rad)
  Support = -> [XY_Plane327]
  Width = 0.23
FEATURE [PartDesign::SubtractiveCylinder] Cylinder608
  Angle = 360
  AttacherType = Attacher::AttachEngine3D
  AttachmentOffset = pos=(-21.055,18.935,0.52) rot=(1,0,0;1.5708rad)
  BaseFeature = -> Box2960
  Height = 0.375
  MapMode = 5
  Placement = pos=(-21.055,18.935,0.52) rot=(1,0,0;1.5708rad)
  Radius = 0.205
  Support = -> [XY_Plane327]
FEATURE [PartDesign::SubtractiveBox] Box3016
  AttacherType = Attacher::AttachEngine3D
  AttachmentOffset = pos=(-20.95,18.635,0.53) rot=(0,0,1;0rad)
  BaseFeature = -> Cylinder608
  Height = 0.5
  Length = 0.1
  MapMode = 5
  Placement = pos=(-20.95,18.635,0.53) rot=(0,0,1;0rad)
  Support = -> [XY_Plane327]
  Width = 0.23
FEATURE [PartDesign::SubtractiveBox] Box3001
  AttacherType = Attacher::AttachEngine3D
  AttachmentOffset = pos=(-21.15,18.635,0.297) rot=(0,-1,0;0.174533rad)
  BaseFeature = -> Box3016
  Height = 0.115
  Length = 0.115
  MapMode = 5
  Placement = pos=(-21.15,18.635,0.297) rot=(0,-1,0;0.174533rad)
  Support = -> [XY_Plane327]
  Width = 0.23
FEATURE [PartDesign::Fillet] Fillet870
  Base = -> Box3001 [Edge28]
  BaseFeature = -> Box3001
  Placement = pos=(-21.15,18.635,0.297) rot=(0,-1,0;0.174533rad)
  Radius = 0.375
  SupportTransform = false
FEATURE [PartDesign::AdditiveBox] Box3008
  AttacherType = Attacher::AttachEngine3D
  AttachmentOffset = pos=(-20.7,18.635,1.55) rot=(0,1,0;0.785398rad)
  BaseFeature = -> Fillet870
  Height = 0.375
  Length = 0.23
  MapMode = 5
  Placement = pos=(-20.7,18.635,1.55) rot=(0,1,0;0.785398rad)
  Support = -> [XY_Plane327]
  Width = 0.23
FEATURE [PartDesign::SubtractiveCylinder] Cylinder604
  Angle = 360
  AttacherType = Attacher::AttachEngine3D
  AttachmentOffset = pos=(-20.271,18.635,1.4056) rot=(-1,0,0;1.5708rad)
  BaseFeature = -> Box3008
  Height = 0.23
  MapMode = 5
  Placement = pos=(-20.271,18.635,1.4056) rot=(-1,0,0;1.5708rad)
  Radius = 0.23
  Support = -> [XY_Plane327]
FEATURE [PartDesign::AdditiveBox] Box3020
  AttacherType = Attacher::AttachEngine3D
  AttachmentOffset = pos=(-20.1,18.635,1.635) rot=(0,0,1;0rad)
  BaseFeature = -> Cylinder604
  Height = 0.265
  Length = 0.23
  MapMode = 5
  Placement = pos=(-20.1,18.635,1.635) rot=(0,0,1;0rad)
  Support = -> [XY_Plane327]
  Width = 0.23
FEATURE [PartDesign::Body] Body295  label="pin295"
  Group = -> [Box3031,Box3024,Box3010,Box3014,Box3009,Fillet892,Fillet888,Box2960,Cylinder608,Box3016,Box3001,Fillet870,Box3008,Cylinder604,Box3020]
  Origin = -> Origin313
  Placement = pos=(0,-1,0) rot=(0,0,1;0rad)
  Tip = -> Box3020
FEATURE [PartDesign::Body] Body296  label="pin296"
  Group = -> [Box2909,Box2873,Box3019,Box2945,Box2891,Fillet880,Fillet868,Box3030,Cylinder592,Box2874,Box2889,Fillet876,Box2894,Cylinder597,Box2887]
  Origin = -> Origin329
  Placement = pos=(0,-2.5,0) rot=(0,0,1;0rad)
  Tip = -> Box2887
FEATURE [PartDesign::Fillet] Fillet895
  Base = -> Fillet873 [Edge33]
  BaseFeature = -> Fillet873
  Placement = pos=(-21.5005,18.625,0.235) rot=(0,-1,0;0.174533rad)
  Radius = 0.5
  SupportTransform = false
FEATURE [PartDesign::AdditiveBox] Box3018
  AttacherType = Attacher::AttachEngine3D
  AttachmentOffset = pos=(-21.1,18.635,0.305) rot=(0,1,0;0.785398rad)
  BaseFeature = -> Fillet895
  Height = 0.375
  Length = 0.2
  MapMode = 5
  Placement = pos=(-21.1,18.635,0.305) rot=(0,1,0;0.785398rad)
  Support = -> [XY_Plane325]
  Width = 0.23
FEATURE [PartDesign::SubtractiveCylinder] Cylinder606
  Angle = 360
  AttacherType = Attacher::AttachEngine3D
  AttachmentOffset = pos=(-21.055,18.935,0.52) rot=(1,0,0;1.5708rad)
  BaseFeature = -> Box3018
  Height = 0.375
  MapMode = 5
  Placement = pos=(-21.055,18.935,0.52) rot=(1,0,0;1.5708rad)
  Radius = 0.205
  Support = -> [XY_Plane325]
FEATURE [PartDesign::SubtractiveBox] Box3027
  AttacherType = Attacher::AttachEngine3D
  AttachmentOffset = pos=(-20.95,18.635,0.53) rot=(0,0,1;0rad)
  BaseFeature = -> Cylinder606
  Height = 0.5
  Length = 0.1
  MapMode = 5
  Placement = pos=(-20.95,18.635,0.53) rot=(0,0,1;0rad)
  Support = -> [XY_Plane325]
  Width = 0.23
FEATURE [PartDesign::SubtractiveBox] Box3025
  AttacherType = Attacher::AttachEngine3D
  AttachmentOffset = pos=(-21.15,18.635,0.297) rot=(0,-1,0;0.174533rad)
  BaseFeature = -> Box3027
  Height = 0.115
  Length = 0.115
  MapMode = 5
  Placement = pos=(-21.15,18.635,0.297) rot=(0,-1,0;0.174533rad)
  Support = -> [XY_Plane325]
  Width = 0.23
FEATURE [PartDesign::Fillet] Fillet885
  Base = -> Box3025 [Edge28]
  BaseFeature = -> Box3025
  Placement = pos=(-21.15,18.635,0.297) rot=(0,-1,0;0.174533rad)
  Radius = 0.375
  SupportTransform = false
FEATURE [PartDesign::AdditiveBox] Box3029
  AttacherType = Attacher::AttachEngine3D
  AttachmentOffset = pos=(-20.7,18.635,1.55) rot=(0,1,0;0.785398rad)
  BaseFeature = -> Fillet885
  Height = 0.375
  Length = 0.23
  MapMode = 5
  Placement = pos=(-20.7,18.635,1.55) rot=(0,1,0;0.785398rad)
  Support = -> [XY_Plane325]
  Width = 0.23
FEATURE [PartDesign::SubtractiveCylinder] Cylinder594
  Angle = 360
  AttacherType = Attacher::AttachEngine3D
  AttachmentOffset = pos=(-20.271,18.635,1.4056) rot=(-1,0,0;1.5708rad)
  BaseFeature = -> Box3029
  Height = 0.23
  MapMode = 5
  Placement = pos=(-20.271,18.635,1.4056) rot=(-1,0,0;1.5708rad)
  Radius = 0.23
  Support = -> [XY_Plane325]
FEATURE [PartDesign::AdditiveBox] Box3033
  AttacherType = Attacher::AttachEngine3D
  AttachmentOffset = pos=(-20.1,18.635,1.635) rot=(0,0,1;0rad)
  BaseFeature = -> Cylinder594
  Height = 0.265
  Length = 0.23
  MapMode = 5
  Placement = pos=(-20.1,18.635,1.635) rot=(0,0,1;0rad)
  Support = -> [XY_Plane325]
  Width = 0.23
FEATURE [PartDesign::Body] Body298  label="pin298"
  Group = -> [Box2892,Box2875,Box3032,Box3006,Box2900,Fillet873,Fillet895,Box3018,Cylinder606,Box3027,Box3025,Fillet885,Box3029,Cylinder594,Box3033]
  Origin = -> Origin323
  Placement = pos=(0,-1.5,0) rot=(0,0,1;0rad)
  Tip = -> Box3033
FEATURE [PartDesign::Body] Body299  label="pin299"
  Group = -> [Box2915,Box2935,Box2903,Box2922,Box2952,Fillet890,Fillet867,Box2886,Cylinder580,Box2893,Box2872,Fillet874,Box2907,Cylinder583,Box2908]
  Origin = -> Origin314
  Placement = pos=(0,-4.5,0) rot=(0,0,1;0rad)
  Tip = -> Box2908
FEATURE [PartDesign::Fillet] Fillet896
  Base = -> Fillet879 [Edge33]
  BaseFeature = -> Fillet879
  Placement = pos=(-21.5005,18.625,0.235) rot=(0,-1,0;0.174533rad)
  Radius = 0.5
  SupportTransform = false
FEATURE [PartDesign::AdditiveBox] Box2926
  AttacherType = Attacher::AttachEngine3D
  AttachmentOffset = pos=(-21.1,18.635,0.305) rot=(0,1,0;0.785398rad)
  BaseFeature = -> Fillet896
  Height = 0.375
  Length = 0.2
  MapMode = 5
  Placement = pos=(-21.1,18.635,0.305) rot=(0,1,0;0.785398rad)
  Support = -> [XY_Plane328]
  Width = 0.23
FEATURE [PartDesign::SubtractiveCylinder] Cylinder584
  Angle = 360
  AttacherType = Attacher::AttachEngine3D
  AttachmentOffset = pos=(-21.055,18.935,0.52) rot=(1,0,0;1.5708rad)
  BaseFeature = -> Box2926
  Height = 0.375
  MapMode = 5
  Placement = pos=(-21.055,18.935,0.52) rot=(1,0,0;1.5708rad)
  Radius = 0.205
  Support = -> [XY_Plane328]
FEATURE [PartDesign::SubtractiveBox] Box2918
  AttacherType = Attacher::AttachEngine3D
  AttachmentOffset = pos=(-20.95,18.635,0.53) rot=(0,0,1;0rad)
  BaseFeature = -> Cylinder584
  Height = 0.5
  Length = 0.1
  MapMode = 5
  Placement = pos=(-20.95,18.635,0.53) rot=(0,0,1;0rad)
  Support = -> [XY_Plane328]
  Width = 0.23
FEATURE [PartDesign::SubtractiveBox] Box2924
  AttacherType = Attacher::AttachEngine3D
  AttachmentOffset = pos=(-21.15,18.635,0.297) rot=(0,-1,0;0.174533rad)
  BaseFeature = -> Box2918
  Height = 0.115
  Length = 0.115
  MapMode = 5
  Placement = pos=(-21.15,18.635,0.297) rot=(0,-1,0;0.174533rad)
  Support = -> [XY_Plane328]
  Width = 0.23
FEATURE [PartDesign::Fillet] Fillet897
  Base = -> Box2924 [Edge28]
  BaseFeature = -> Box2924
  Placement = pos=(-21.15,18.635,0.297) rot=(0,-1,0;0.174533rad)
  Radius = 0.375
  SupportTransform = false
FEATURE [PartDesign::AdditiveBox] Box2931
  AttacherType = Attacher::AttachEngine3D
  AttachmentOffset = pos=(-20.7,18.635,1.55) rot=(0,1,0;0.785398rad)
  BaseFeature = -> Fillet897
  Height = 0.375
  Length = 0.23
  MapMode = 5
  Placement = pos=(-20.7,18.635,1.55) rot=(0,1,0;0.785398rad)
  Support = -> [XY_Plane328]
  Width = 0.23
FEATURE [PartDesign::SubtractiveCylinder] Cylinder589
  Angle = 360
  AttacherType = Attacher::AttachEngine3D
  AttachmentOffset = pos=(-20.271,18.635,1.4056) rot=(-1,0,0;1.5708rad)
  BaseFeature = -> Box2931
  Height = 0.23
  MapMode = 5
  Placement = pos=(-20.271,18.635,1.4056) rot=(-1,0,0;1.5708rad)
  Radius = 0.23
  Support = -> [XY_Plane328]
FEATURE [PartDesign::AdditiveBox] Box2934
  AttacherType = Attacher::AttachEngine3D
  AttachmentOffset = pos=(-20.1,18.635,1.635) rot=(0,0,1;0rad)
  BaseFeature = -> Cylinder589
  Height = 0.265
  Length = 0.23
  MapMode = 5
  Placement = pos=(-20.1,18.635,1.635) rot=(0,0,1;0rad)
  Support = -> [XY_Plane328]
  Width = 0.23
FEATURE [PartDesign::Fillet] Fillet898
  Base = -> Box2925 [Edge2]
  BaseFeature = -> Box2925
  Placement = pos=(-21.5005,18.625,0.235) rot=(0,-1,0;0.174533rad)
  Radius = 0.05
  SupportTransform = false
FEATURE [PartDesign::Fillet] Fillet899
  Base = -> Box2950 [Edge2]
  BaseFeature = -> Box2950
  Placement = pos=(-21.5005,18.625,0.235) rot=(0,-1,0;0.174533rad)
  Radius = 0.05
  SupportTransform = false
FEATURE [PartDesign::Fillet] Fillet894
  Base = -> Fillet899 [Edge33]
  BaseFeature = -> Fillet899
  Placement = pos=(-21.5005,18.625,0.235) rot=(0,-1,0;0.174533rad)
  Radius = 0.5
  SupportTransform = false
FEATURE [PartDesign::AdditiveBox] Box2958
  AttacherType = Attacher::AttachEngine3D
  AttachmentOffset = pos=(-21.1,18.635,0.305) rot=(0,1,0;0.785398rad)
  BaseFeature = -> Fillet894
  Height = 0.375
  Length = 0.2
  MapMode = 5
  Placement = pos=(-21.1,18.635,0.305) rot=(0,1,0;0.785398rad)
  Support = -> [XY_Plane298]
  Width = 0.23
FEATURE [PartDesign::SubtractiveCylinder] Cylinder593
  Angle = 360
  AttacherType = Attacher::AttachEngine3D
  AttachmentOffset = pos=(-21.055,18.935,0.52) rot=(1,0,0;1.5708rad)
  BaseFeature = -> Box2958
  Height = 0.375
  MapMode = 5
  Placement = pos=(-21.055,18.935,0.52) rot=(1,0,0;1.5708rad)
  Radius = 0.205
  Support = -> [XY_Plane298]
FEATURE [PartDesign::SubtractiveBox] Box2951
  AttacherType = Attacher::AttachEngine3D
  AttachmentOffset = pos=(-20.95,18.635,0.53) rot=(0,0,1;0rad)
  BaseFeature = -> Cylinder593
  Height = 0.5
  Length = 0.1
  MapMode = 5
  Placement = pos=(-20.95,18.635,0.53) rot=(0,0,1;0rad)
  Support = -> [XY_Plane298]
  Width = 0.23
FEATURE [PartDesign::SubtractiveBox] Box2939
  AttacherType = Attacher::AttachEngine3D
  AttachmentOffset = pos=(-21.15,18.635,0.297) rot=(0,-1,0;0.174533rad)
  BaseFeature = -> Box2951
  Height = 0.115
  Length = 0.115
  MapMode = 5
  Placement = pos=(-21.15,18.635,0.297) rot=(0,-1,0;0.174533rad)
  Support = -> [XY_Plane298]
  Width = 0.23
FEATURE [PartDesign::Fillet] Fillet886
  Base = -> Box2939 [Edge28]
  BaseFeature = -> Box2939
  Placement = pos=(-21.15,18.635,0.297) rot=(0,-1,0;0.174533rad)
  Radius = 0.375
  SupportTransform = false
FEATURE [PartDesign::AdditiveBox] Box2946
  AttacherType = Attacher::AttachEngine3D
  AttachmentOffset = pos=(-20.7,18.635,1.55) rot=(0,1,0;0.785398rad)
  BaseFeature = -> Fillet886
  Height = 0.375
  Length = 0.23
  MapMode = 5
  Placement = pos=(-20.7,18.635,1.55) rot=(0,1,0;0.785398rad)
  Support = -> [XY_Plane298]
  Width = 0.23
FEATURE [PartDesign::SubtractiveCylinder] Cylinder590
  Angle = 360
  AttacherType = Attacher::AttachEngine3D
  AttachmentOffset = pos=(-20.271,18.635,1.4056) rot=(-1,0,0;1.5708rad)
  BaseFeature = -> Box2946
  Height = 0.23
  MapMode = 5
  Placement = pos=(-20.271,18.635,1.4056) rot=(-1,0,0;1.5708rad)
  Radius = 0.23
  Support = -> [XY_Plane298]
FEATURE [PartDesign::AdditiveBox] Box2919
  AttacherType = Attacher::AttachEngine3D
  AttachmentOffset = pos=(-20.1,18.635,1.635) rot=(0,0,1;0rad)
  BaseFeature = -> Cylinder590
  Height = 0.265
  Length = 0.23
  MapMode = 5
  Placement = pos=(-20.1,18.635,1.635) rot=(0,0,1;0rad)
  Support = -> [XY_Plane298]
  Width = 0.23
FEATURE [PartDesign::Body] Body300  label="pin300"
  Group = -> [Box2927,Box2947,Box2929,Box2948,Box2950,Fillet899,Fillet894,Box2958,Cylinder593,Box2951,Box2939,Fillet886,Box2946,Cylinder590,Box2919]
  Origin = -> Origin332
  Placement = pos=(0,-4,0) rot=(0,0,1;0rad)
  Tip = -> Box2919
FEATURE [PartDesign::Fillet] Fillet900
  Base = -> Fillet881 [Edge33]
  BaseFeature = -> Fillet881
  Placement = pos=(-21.5005,18.625,0.235) rot=(0,-1,0;0.174533rad)
  Radius = 0.5
  SupportTransform = false
FEATURE [PartDesign::AdditiveBox] Box2905
  AttacherType = Attacher::AttachEngine3D
  AttachmentOffset = pos=(-21.1,18.635,0.305) rot=(0,1,0;0.785398rad)
  BaseFeature = -> Fillet900
  Height = 0.375
  Length = 0.2
  MapMode = 5
  Placement = pos=(-21.1,18.635,0.305) rot=(0,1,0;0.785398rad)
  Support = -> [XY_Plane299]
  Width = 0.23
FEATURE [PartDesign::SubtractiveCylinder] Cylinder586
  Angle = 360
  AttacherType = Attacher::AttachEngine3D
  AttachmentOffset = pos=(-21.055,18.935,0.52) rot=(1,0,0;1.5708rad)
  BaseFeature = -> Box2905
  Height = 0.375
  MapMode = 5
  Placement = pos=(-21.055,18.935,0.52) rot=(1,0,0;1.5708rad)
  Radius = 0.205
  Support = -> [XY_Plane299]
FEATURE [PartDesign::SubtractiveBox] Box2910
  AttacherType = Attacher::AttachEngine3D
  AttachmentOffset = pos=(-20.95,18.635,0.53) rot=(0,0,1;0rad)
  BaseFeature = -> Cylinder586
  Height = 0.5
  Length = 0.1
  MapMode = 5
  Placement = pos=(-20.95,18.635,0.53) rot=(0,0,1;0rad)
  Support = -> [XY_Plane299]
  Width = 0.23
FEATURE [PartDesign::SubtractiveBox] Box2944
  AttacherType = Attacher::AttachEngine3D
  AttachmentOffset = pos=(-21.15,18.635,0.297) rot=(0,-1,0;0.174533rad)
  BaseFeature = -> Box2910
  Height = 0.115
  Length = 0.115
  MapMode = 5
  Placement = pos=(-21.15,18.635,0.297) rot=(0,-1,0;0.174533rad)
  Support = -> [XY_Plane299]
  Width = 0.23
FEATURE [PartDesign::Fillet] Fillet872
  Base = -> Box2944 [Edge28]
  BaseFeature = -> Box2944
  Placement = pos=(-21.15,18.635,0.297) rot=(0,-1,0;0.174533rad)
  Radius = 0.375
  SupportTransform = false
FEATURE [PartDesign::AdditiveBox] Box2938
  AttacherType = Attacher::AttachEngine3D
  AttachmentOffset = pos=(-20.7,18.635,1.55) rot=(0,1,0;0.785398rad)
  BaseFeature = -> Fillet872
  Height = 0.375
  Length = 0.23
  MapMode = 5
  Placement = pos=(-20.7,18.635,1.55) rot=(0,1,0;0.785398rad)
  Support = -> [XY_Plane299]
  Width = 0.23
FEATURE [PartDesign::SubtractiveCylinder] Cylinder588
  Angle = 360
  AttacherType = Attacher::AttachEngine3D
  AttachmentOffset = pos=(-20.271,18.635,1.4056) rot=(-1,0,0;1.5708rad)
  BaseFeature = -> Box2938
  Height = 0.23
  MapMode = 5
  Placement = pos=(-20.271,18.635,1.4056) rot=(-1,0,0;1.5708rad)
  Radius = 0.23
  Support = -> [XY_Plane299]
FEATURE [PartDesign::AdditiveBox] Box2965
  AttacherType = Attacher::AttachEngine3D
  AttachmentOffset = pos=(-20.1,18.635,1.635) rot=(0,0,1;0rad)
  BaseFeature = -> Cylinder588
  Height = 0.265
  Length = 0.23
  MapMode = 5
  Placement = pos=(-20.1,18.635,1.635) rot=(0,0,1;0rad)
  Support = -> [XY_Plane299]
  Width = 0.23
FEATURE [PartDesign::Body] Body292  label="pin292"
  Group = -> [Box2932,Box2955,Box2916,Box3011,Box2914,Fillet881,Fillet900,Box2905,Cylinder586,Box2910,Box2944,Fillet872,Box2938,Cylinder588,Box2965]
  Origin = -> Origin327
  Placement = pos=(0,-3,0) rot=(0,0,1;0rad)
  Tip = -> Box2965
FEATURE [PartDesign::Body] Body301  label="pin301"
  Group = -> [Box2917,Box2928,Box2880,Box2899,Box2897,Fillet879,Fillet896,Box2926,Cylinder584,Box2918,Box2924,Fillet897,Box2931,Cylinder589,Box2934]
  Origin = -> Origin319
  Placement = pos=(0,-5.5,0) rot=(0,0,1;0rad)
  Tip = -> Box2934
FEATURE [PartDesign::Fillet] Fillet901
  Base = -> Fillet898 [Edge33]
  BaseFeature = -> Fillet898
  Placement = pos=(-21.5005,18.625,0.235) rot=(0,-1,0;0.174533rad)
  Radius = 0.5
  SupportTransform = false
FEATURE [PartDesign::AdditiveBox] Box2956
  AttacherType = Attacher::AttachEngine3D
  AttachmentOffset = pos=(-21.1,18.635,0.305) rot=(0,1,0;0.785398rad)
  BaseFeature = -> Fillet901
  Height = 0.375
  Length = 0.2
  MapMode = 5
  Placement = pos=(-21.1,18.635,0.305) rot=(0,1,0;0.785398rad)
  Support = -> [XY_Plane300]
  Width = 0.23
FEATURE [PartDesign::SubtractiveCylinder] Cylinder596
  Angle = 360
  AttacherType = Attacher::AttachEngine3D
  AttachmentOffset = pos=(-21.055,18.935,0.52) rot=(1,0,0;1.5708rad)
  BaseFeature = -> Box2956
  Height = 0.375
  MapMode = 5
  Placement = pos=(-21.055,18.935,0.52) rot=(1,0,0;1.5708rad)
  Radius = 0.205
  Support = -> [XY_Plane300]
FEATURE [PartDesign::SubtractiveBox] Box3005
  AttacherType = Attacher::AttachEngine3D
  AttachmentOffset = pos=(-20.95,18.635,0.53) rot=(0,0,1;0rad)
  BaseFeature = -> Cylinder596
  Height = 0.5
  Length = 0.1
  MapMode = 5
  Placement = pos=(-20.95,18.635,0.53) rot=(0,0,1;0rad)
  Support = -> [XY_Plane300]
  Width = 0.23
FEATURE [PartDesign::SubtractiveBox] Box2941
  AttacherType = Attacher::AttachEngine3D
  AttachmentOffset = pos=(-21.15,18.635,0.297) rot=(0,-1,0;0.174533rad)
  BaseFeature = -> Box3005
  Height = 0.115
  Length = 0.115
  MapMode = 5
  Placement = pos=(-21.15,18.635,0.297) rot=(0,-1,0;0.174533rad)
  Support = -> [XY_Plane300]
  Width = 0.23
FEATURE [PartDesign::Fillet] Fillet883
  Base = -> Box2941 [Edge28]
  BaseFeature = -> Box2941
  Placement = pos=(-21.15,18.635,0.297) rot=(0,-1,0;0.174533rad)
  Radius = 0.375
  SupportTransform = false
FEATURE [PartDesign::AdditiveBox] Box2953
  AttacherType = Attacher::AttachEngine3D
  AttachmentOffset = pos=(-20.7,18.635,1.55) rot=(0,1,0;0.785398rad)
  BaseFeature = -> Fillet883
  Height = 0.375
  Length = 0.23
  MapMode = 5
  Placement = pos=(-20.7,18.635,1.55) rot=(0,1,0;0.785398rad)
  Support = -> [XY_Plane300]
  Width = 0.23
FEATURE [PartDesign::SubtractiveCylinder] Cylinder595
  Angle = 360
  AttacherType = Attacher::AttachEngine3D
  AttachmentOffset = pos=(-20.271,18.635,1.4056) rot=(-1,0,0;1.5708rad)
  BaseFeature = -> Box2953
  Height = 0.23
  MapMode = 5
  Placement = pos=(-20.271,18.635,1.4056) rot=(-1,0,0;1.5708rad)
  Radius = 0.23
  Support = -> [XY_Plane300]
FEATURE [PartDesign::AdditiveBox] Box2933
  AttacherType = Attacher::AttachEngine3D
  AttachmentOffset = pos=(-20.1,18.635,1.635) rot=(0,0,1;0rad)
  BaseFeature = -> Cylinder595
  Height = 0.265
  Length = 0.23
  MapMode = 5
  Placement = pos=(-20.1,18.635,1.635) rot=(0,0,1;0rad)
  Support = -> [XY_Plane300]
  Width = 0.23
FEATURE [PartDesign::Body] Body290  label="pin290"
  Group = -> [Box2936,Box2963,Box3002,Box2943,Box2925,Fillet898,Fillet901,Box2956,Cylinder596,Box3005,Box2941,Fillet883,Box2953,Cylinder595,Box2933]
  Origin = -> Origin315
  Placement = pos=(0,-3.5,0) rot=(0,0,1;0rad)
  Tip = -> Box2933
FEATURE [PartDesign::Fillet] Fillet904
  Base = -> Box3037 [Edge2]
  BaseFeature = -> Box3037
  Placement = pos=(-21.5005,18.625,0.235) rot=(0,-1,0;0.174533rad)
  Radius = 0.05
  SupportTransform = false
FEATURE [PartDesign::Fillet] Fillet907
  Base = -> Box2984 [Edge2]
  BaseFeature = -> Box2984
  Placement = pos=(-21.5005,18.625,0.235) rot=(0,-1,0;0.174533rad)
  Radius = 0.05
  SupportTransform = false
FEATURE [PartDesign::Fillet] Fillet902
  Base = -> Fillet907 [Edge33]
  BaseFeature = -> Fillet907
  Placement = pos=(-21.5005,18.625,0.235) rot=(0,-1,0;0.174533rad)
  Radius = 0.5
  SupportTransform = false
FEATURE [PartDesign::AdditiveBox] Box3034
  AttacherType = Attacher::AttachEngine3D
  AttachmentOffset = pos=(-21.1,18.635,0.305) rot=(0,1,0;0.785398rad)
  BaseFeature = -> Fillet902
  Height = 0.375
  Length = 0.2
  MapMode = 5
  Placement = pos=(-21.1,18.635,0.305) rot=(0,1,0;0.785398rad)
  Support = -> [XY_Plane332]
  Width = 0.23
FEATURE [PartDesign::SubtractiveCylinder] Cylinder610
  Angle = 360
  AttacherType = Attacher::AttachEngine3D
  AttachmentOffset = pos=(-21.055,18.935,0.52) rot=(1,0,0;1.5708rad)
  BaseFeature = -> Box3034
  Height = 0.375
  MapMode = 5
  Placement = pos=(-21.055,18.935,0.52) rot=(1,0,0;1.5708rad)
  Radius = 0.205
  Support = -> [XY_Plane332]
FEATURE [PartDesign::SubtractiveBox] Box3040
  AttacherType = Attacher::AttachEngine3D
  AttachmentOffset = pos=(-20.95,18.635,0.53) rot=(0,0,1;0rad)
  BaseFeature = -> Cylinder610
  Height = 0.5
  Length = 0.1
  MapMode = 5
  Placement = pos=(-20.95,18.635,0.53) rot=(0,0,1;0rad)
  Support = -> [XY_Plane332]
  Width = 0.23
FEATURE [PartDesign::SubtractiveBox] Box3036
  AttacherType = Attacher::AttachEngine3D
  AttachmentOffset = pos=(-21.15,18.635,0.297) rot=(0,-1,0;0.174533rad)
  BaseFeature = -> Box3040
  Height = 0.115
  Length = 0.115
  MapMode = 5
  Placement = pos=(-21.15,18.635,0.297) rot=(0,-1,0;0.174533rad)
  Support = -> [XY_Plane332]
  Width = 0.23
FEATURE [PartDesign::Fillet] Fillet905
  Base = -> Box3036 [Edge28]
  BaseFeature = -> Box3036
  Placement = pos=(-21.15,18.635,0.297) rot=(0,-1,0;0.174533rad)
  Radius = 0.375
  SupportTransform = false
FEATURE [PartDesign::AdditiveBox] Box2977
  AttacherType = Attacher::AttachEngine3D
  AttachmentOffset = pos=(-20.7,18.635,1.55) rot=(0,1,0;0.785398rad)
  BaseFeature = -> Fillet905
  Height = 0.375
  Length = 0.23
  MapMode = 5
  Placement = pos=(-20.7,18.635,1.55) rot=(0,1,0;0.785398rad)
  Support = -> [XY_Plane332]
  Width = 0.23
FEATURE [PartDesign::SubtractiveCylinder] Cylinder601
  Angle = 360
  AttacherType = Attacher::AttachEngine3D
  AttachmentOffset = pos=(-20.271,18.635,1.4056) rot=(-1,0,0;1.5708rad)
  BaseFeature = -> Box2977
  Height = 0.23
  MapMode = 5
  Placement = pos=(-20.271,18.635,1.4056) rot=(-1,0,0;1.5708rad)
  Radius = 0.23
  Support = -> [XY_Plane332]
FEATURE [PartDesign::AdditiveBox] Box2974
  AttacherType = Attacher::AttachEngine3D
  AttachmentOffset = pos=(-20.1,18.635,1.635) rot=(0,0,1;0rad)
  BaseFeature = -> Cylinder601
  Height = 0.265
  Length = 0.23
  MapMode = 5
  Placement = pos=(-20.1,18.635,1.635) rot=(0,0,1;0rad)
  Support = -> [XY_Plane332]
  Width = 0.23
FEATURE [PartDesign::Body] Body297  label="pin297"
  Group = -> [Box2970,Box2990,Box2968,Box2978,Box2984,Fillet907,Fillet902,Box3034,Cylinder610,Box3040,Box3036,Fillet905,Box2977,Cylinder601,Box2974]
  Origin = -> Origin324
  Placement = pos=(0,-6.5,0) rot=(0,0,1;0rad)
  Tip = -> Box2974
FEATURE [PartDesign::Fillet] Fillet909
  Base = -> Fillet904 [Edge33]
  BaseFeature = -> Fillet904
  Placement = pos=(-21.5005,18.625,0.235) rot=(0,-1,0;0.174533rad)
  Radius = 0.5
  SupportTransform = false
FEATURE [PartDesign::AdditiveBox] Box2991
  AttacherType = Attacher::AttachEngine3D
  AttachmentOffset = pos=(-21.1,18.635,0.305) rot=(0,1,0;0.785398rad)
  BaseFeature = -> Fillet909
  Height = 0.375
  Length = 0.2
  MapMode = 5
  Placement = pos=(-21.1,18.635,0.305) rot=(0,1,0;0.785398rad)
  Support = -> [XY_Plane331]
  Width = 0.23
FEATURE [PartDesign::SubtractiveCylinder] Cylinder600
  Angle = 360
  AttacherType = Attacher::AttachEngine3D
  AttachmentOffset = pos=(-21.055,18.935,0.52) rot=(1,0,0;1.5708rad)
  BaseFeature = -> Box2991
  Height = 0.375
  MapMode = 5
  Placement = pos=(-21.055,18.935,0.52) rot=(1,0,0;1.5708rad)
  Radius = 0.205
  Support = -> [XY_Plane331]
FEATURE [PartDesign::SubtractiveBox] Box2986
  AttacherType = Attacher::AttachEngine3D
  AttachmentOffset = pos=(-20.95,18.635,0.53) rot=(0,0,1;0rad)
  BaseFeature = -> Cylinder600
  Height = 0.5
  Length = 0.1
  MapMode = 5
  Placement = pos=(-20.95,18.635,0.53) rot=(0,0,1;0rad)
  Support = -> [XY_Plane331]
  Width = 0.23
FEATURE [PartDesign::SubtractiveBox] Box2967
  AttacherType = Attacher::AttachEngine3D
  AttachmentOffset = pos=(-21.15,18.635,0.297) rot=(0,-1,0;0.174533rad)
  BaseFeature = -> Box2986
  Height = 0.115
  Length = 0.115
  MapMode = 5
  Placement = pos=(-21.15,18.635,0.297) rot=(0,-1,0;0.174533rad)
  Support = -> [XY_Plane331]
  Width = 0.23
FEATURE [PartDesign::Fillet] Fillet908
  Base = -> Box2967 [Edge28]
  BaseFeature = -> Box2967
  Placement = pos=(-21.15,18.635,0.297) rot=(0,-1,0;0.174533rad)
  Radius = 0.375
  SupportTransform = false
FEATURE [PartDesign::AdditiveBox] Box2993
  AttacherType = Attacher::AttachEngine3D
  AttachmentOffset = pos=(-20.7,18.635,1.55) rot=(0,1,0;0.785398rad)
  BaseFeature = -> Fillet908
  Height = 0.375
  Length = 0.23
  MapMode = 5
  Placement = pos=(-20.7,18.635,1.55) rot=(0,1,0;0.785398rad)
  Support = -> [XY_Plane331]
  Width = 0.23
FEATURE [PartDesign::SubtractiveCylinder] Cylinder599
  Angle = 360
  AttacherType = Attacher::AttachEngine3D
  AttachmentOffset = pos=(-20.271,18.635,1.4056) rot=(-1,0,0;1.5708rad)
  BaseFeature = -> Box2993
  Height = 0.23
  MapMode = 5
  Placement = pos=(-20.271,18.635,1.4056) rot=(-1,0,0;1.5708rad)
  Radius = 0.23
  Support = -> [XY_Plane331]
FEATURE [PartDesign::AdditiveBox] Box2983
  AttacherType = Attacher::AttachEngine3D
  AttachmentOffset = pos=(-20.1,18.635,1.635) rot=(0,0,1;0rad)
  BaseFeature = -> Cylinder599
  Height = 0.265
  Length = 0.23
  MapMode = 5
  Placement = pos=(-20.1,18.635,1.635) rot=(0,0,1;0rad)
  Support = -> [XY_Plane331]
  Width = 0.23
FEATURE [PartDesign::Body] Body303  label="pin303"
  Group = -> [Box2973,Box2992,Box3035,Box3039,Box3037,Fillet904,Fillet909,Box2991,Cylinder600,Box2986,Box2967,Fillet908,Box2993,Cylinder599,Box2983]
  Origin = -> Origin321
  Placement = pos=(0,-7.5,0) rot=(0,0,1;0rad)
  Tip = -> Box2983
FEATURE [PartDesign::Fillet] Fillet910
  Base = -> Box2972 [Edge2]
  BaseFeature = -> Box2972
  Placement = pos=(-21.5005,18.625,0.235) rot=(0,-1,0;0.174533rad)
  Radius = 0.05
  SupportTransform = false
FEATURE [PartDesign::Fillet] Fillet903
  Base = -> Fillet910 [Edge33]
  BaseFeature = -> Fillet910
  Placement = pos=(-21.5005,18.625,0.235) rot=(0,-1,0;0.174533rad)
  Radius = 0.5
  SupportTransform = false
FEATURE [PartDesign::AdditiveBox] Box3023
  AttacherType = Attacher::AttachEngine3D
  AttachmentOffset = pos=(-21.1,18.635,0.305) rot=(0,1,0;0.785398rad)
  BaseFeature = -> Fillet903
  Height = 0.375
  Length = 0.2
  MapMode = 5
  Placement = pos=(-21.1,18.635,0.305) rot=(0,1,0;0.785398rad)
  Support = -> [XY_Plane330]
  Width = 0.23
FEATURE [PartDesign::SubtractiveCylinder] Cylinder598
  Angle = 360
  AttacherType = Attacher::AttachEngine3D
  AttachmentOffset = pos=(-21.055,18.935,0.52) rot=(1,0,0;1.5708rad)
  BaseFeature = -> Box3023
  Height = 0.375
  MapMode = 5
  Placement = pos=(-21.055,18.935,0.52) rot=(1,0,0;1.5708rad)
  Radius = 0.205
  Support = -> [XY_Plane330]
FEATURE [PartDesign::SubtractiveBox] Box2971
  AttacherType = Attacher::AttachEngine3D
  AttachmentOffset = pos=(-20.95,18.635,0.53) rot=(0,0,1;0rad)
  BaseFeature = -> Cylinder598
  Height = 0.5
  Length = 0.1
  MapMode = 5
  Placement = pos=(-20.95,18.635,0.53) rot=(0,0,1;0rad)
  Support = -> [XY_Plane330]
  Width = 0.23
FEATURE [PartDesign::SubtractiveBox] Box3038
  AttacherType = Attacher::AttachEngine3D
  AttachmentOffset = pos=(-21.15,18.635,0.297) rot=(0,-1,0;0.174533rad)
  BaseFeature = -> Box2971
  Height = 0.115
  Length = 0.115
  MapMode = 5
  Placement = pos=(-21.15,18.635,0.297) rot=(0,-1,0;0.174533rad)
  Support = -> [XY_Plane330]
  Width = 0.23
FEATURE [PartDesign::Fillet] Fillet906
  Base = -> Box3038 [Edge28]
  BaseFeature = -> Box3038
  Placement = pos=(-21.15,18.635,0.297) rot=(0,-1,0;0.174533rad)
  Radius = 0.375
  SupportTransform = false
FEATURE [PartDesign::AdditiveBox] Box2975
  AttacherType = Attacher::AttachEngine3D
  AttachmentOffset = pos=(-20.7,18.635,1.55) rot=(0,1,0;0.785398rad)
  BaseFeature = -> Fillet906
  Height = 0.375
  Length = 0.23
  MapMode = 5
  Placement = pos=(-20.7,18.635,1.55) rot=(0,1,0;0.785398rad)
  Support = -> [XY_Plane330]
  Width = 0.23
FEATURE [PartDesign::SubtractiveCylinder] Cylinder611
  Angle = 360
  AttacherType = Attacher::AttachEngine3D
  AttachmentOffset = pos=(-20.271,18.635,1.4056) rot=(-1,0,0;1.5708rad)
  BaseFeature = -> Box2975
  Height = 0.23
  MapMode = 5
  Placement = pos=(-20.271,18.635,1.4056) rot=(-1,0,0;1.5708rad)
  Radius = 0.23
  Support = -> [XY_Plane330]
FEATURE [PartDesign::AdditiveBox] Box2989
  AttacherType = Attacher::AttachEngine3D
  AttachmentOffset = pos=(-20.1,18.635,1.635) rot=(0,0,1;0rad)
  BaseFeature = -> Cylinder611
  Height = 0.265
  Length = 0.23
  MapMode = 5
  Placement = pos=(-20.1,18.635,1.635) rot=(0,0,1;0rad)
  Support = -> [XY_Plane330]
  Width = 0.23
FEATURE [PartDesign::Body] Body302  label="pin302"
  Group = -> [Box2979,Box2980,Box2969,Box2976,Box2972,Fillet910,Fillet903,Box3023,Cylinder598,Box2971,Box3038,Fillet906,Box2975,Cylinder611,Box2989]
  Origin = -> Origin317
  Placement = pos=(0,-6,0) rot=(0,0,1;0rad)
  Tip = -> Box2989
FEATURE [PartDesign::Fillet] Fillet911
  Base = -> Box2988 [Edge2]
  BaseFeature = -> Box2988
  Placement = pos=(-21.5005,18.625,0.235) rot=(0,-1,0;0.174533rad)
  Radius = 0.05
  SupportTransform = false
FEATURE [PartDesign::Fillet] Fillet891
  Base = -> Fillet911 [Edge33]
  BaseFeature = -> Fillet911
  Placement = pos=(-21.5005,18.625,0.235) rot=(0,-1,0;0.174533rad)
  Radius = 0.5
  SupportTransform = false
FEATURE [PartDesign::AdditiveBox] Box2994
  AttacherType = Attacher::AttachEngine3D
  AttachmentOffset = pos=(-21.1,18.635,0.305) rot=(0,1,0;0.785398rad)
  BaseFeature = -> Fillet891
  Height = 0.375
  Length = 0.2
  MapMode = 5
  Placement = pos=(-21.1,18.635,0.305) rot=(0,1,0;0.785398rad)
  Support = -> [XY_Plane329]
  Width = 0.23
FEATURE [PartDesign::SubtractiveCylinder] Cylinder603
  Angle = 360
  AttacherType = Attacher::AttachEngine3D
  AttachmentOffset = pos=(-21.055,18.935,0.52) rot=(1,0,0;1.5708rad)
  BaseFeature = -> Box2994
  Height = 0.375
  MapMode = 5
  Placement = pos=(-21.055,18.935,0.52) rot=(1,0,0;1.5708rad)
  Radius = 0.205
  Support = -> [XY_Plane329]
FEATURE [PartDesign::SubtractiveBox] Box2998
  AttacherType = Attacher::AttachEngine3D
  AttachmentOffset = pos=(-20.95,18.635,0.53) rot=(0,0,1;0rad)
  BaseFeature = -> Cylinder603
  Height = 0.5
  Length = 0.1
  MapMode = 5
  Placement = pos=(-20.95,18.635,0.53) rot=(0,0,1;0rad)
  Support = -> [XY_Plane329]
  Width = 0.23
FEATURE [PartDesign::SubtractiveBox] Box2982
  AttacherType = Attacher::AttachEngine3D
  AttachmentOffset = pos=(-21.15,18.635,0.297) rot=(0,-1,0;0.174533rad)
  BaseFeature = -> Box2998
  Height = 0.115
  Length = 0.115
  MapMode = 5
  Placement = pos=(-21.15,18.635,0.297) rot=(0,-1,0;0.174533rad)
  Support = -> [XY_Plane329]
  Width = 0.23
FEATURE [PartDesign::Fillet] Fillet893
  Base = -> Box2982 [Edge28]
  BaseFeature = -> Box2982
  Placement = pos=(-21.15,18.635,0.297) rot=(0,-1,0;0.174533rad)
  Radius = 0.375
  SupportTransform = false
FEATURE [PartDesign::AdditiveBox] Box2987
  AttacherType = Attacher::AttachEngine3D
  AttachmentOffset = pos=(-20.7,18.635,1.55) rot=(0,1,0;0.785398rad)
  BaseFeature = -> Fillet893
  Height = 0.375
  Length = 0.23
  MapMode = 5
  Placement = pos=(-20.7,18.635,1.55) rot=(0,1,0;0.785398rad)
  Support = -> [XY_Plane329]
  Width = 0.23
FEATURE [PartDesign::SubtractiveCylinder] Cylinder602
  Angle = 360
  AttacherType = Attacher::AttachEngine3D
  AttachmentOffset = pos=(-20.271,18.635,1.4056) rot=(-1,0,0;1.5708rad)
  BaseFeature = -> Box2987
  Height = 0.23
  MapMode = 5
  Placement = pos=(-20.271,18.635,1.4056) rot=(-1,0,0;1.5708rad)
  Radius = 0.23
  Support = -> [XY_Plane329]
FEATURE [PartDesign::AdditiveBox] Box2981
  AttacherType = Attacher::AttachEngine3D
  AttachmentOffset = pos=(-20.1,18.635,1.635) rot=(0,0,1;0rad)
  BaseFeature = -> Cylinder602
  Height = 0.265
  Length = 0.23
  MapMode = 5
  Placement = pos=(-20.1,18.635,1.635) rot=(0,0,1;0rad)
  Support = -> [XY_Plane329]
  Width = 0.23
FEATURE [PartDesign::Body] Body304  label="pin304"
  Group = -> [Box2985,Box2997,Box2995,Box2996,Box2988,Fillet911,Fillet891,Box2994,Cylinder603,Box2998,Box2982,Fillet893,Box2987,Cylinder602,Box2981]
  Origin = -> Origin318
  Placement = pos=(0,-7,0) rot=(0,0,1;0rad)
  Tip = -> Box2981
FEATURE [App::Part] Part022  label="Pin-set020"
  Group = -> [Body293,Body289,Body295,Body298,Body294,Body296,Body292,Body290,Body300,Body299,Body291,Body301,Body302,Body297,Body304,Body303]
  Origin = -> Origin330
  Placement = pos=(0,-30,0) rot=(0,0,1;0rad)
FEATURE [App::Part] Part026  label="Pin-collection004"
  Group = -> [Part021,Part025,Part024,Part027,Part023,Part022]
  Origin = -> Origin325
  Placement = pos=(0,0,0) rot=(0,0,-1;3.14159rad)
FEATURE [Part::FeaturePython] FCrtYd_lines  label="FCrtYd"  # a2plus imported part (geometry in sourceFile) (typed FeaturePython)
  fixedPosition = true
FEATURE [Part::FeaturePython] FFab_lines  label="FFab"  # a2plus imported part (geometry in sourceFile) (typed FeaturePython)
  fixedPosition = true
FEATURE [Part::FeaturePython] FSilk_lines  label="FrontSilk"  # a2plus imported part (geometry in sourceFile) (typed FeaturePython)
  fixedPosition = true
FEATURE [Part::FeaturePython] TopPads  # a2plus imported part (geometry in sourceFile) (typed FeaturePython)
  fixedPosition = true
FEATURE [Part::FeaturePython] newPCB  label="Pcb"  # a2plus imported part (geometry in sourceFile) (typed FeaturePython)
  fixedPosition = true
FEATURE [App::DocumentObjectGroup] PQFP_304_40x40mm_P0_5mm_fp
  Group = -> [FCrtYd_lines,FFab_lines,FSilk_lines,TopPads,newPCB]
